FCSTD DOCUMENT  (FreeCAD 1.0R39285 (Git))
Label: pranaV2
License: All rights reserved
LicenseURL: https://en.wikipedia.org/wiki/All_rights_reserved
objects: Sketcher::SketchObject×195, Part::Extrusion×187, Part::Feature×26, Part::MultiFuse×14, Part::Cut×8, Part::Fillet×5, Part::Cylinder×4, Part::Loft×4, Part::MultiCommon×4, App::Part×3, Part::Compound×2, Part::Box×1
note: 645 computed .brp shape members not serialized (recipe doc carries the construction recipe); baked Part::Feature solids carry a one-line shape summary decoded from their .brp

FEATURE [Part::Feature] Part__Feature023  label="COZIR"
  Placement = pos=(5.41029,2.97838,5.56111) rot=(0,0,1;0rad)
  shape: bbox 51.61 x 17 x 50.23 mm, 43 faces (baked)
FEATURE [Part::Feature] Part__Feature024  label="COMPOUND"
  shape: bbox 3.14 x 5 x 10.76 mm, 60 faces, 10 solids (baked)
FEATURE [App::Part] COZIR_Sensor_v2  label="COZIR Sensor v2"
  Group = -> [Part__Feature023,Part__Feature024]
  Origin = -> Origin002
  Placement = pos=(18.5,-15,8.25) rot=(0,-1,0;5.75959rad)
FEATURE [Part::Feature] Part__Feature334  label="CAPC-0805-T0.95-BN v012"
  Placement = pos=(-5.48627,2.66154,1.6) rot=(0,0,-1;1.5708rad)
  shape: bbox 1.35 x 2.1 x 0.95 mm, 42 faces (baked)
FEATURE [Part::Feature] Part__Feature335  label="CAPC-0805-T0.95-BN v013"
  Placement = pos=(-3.43627,2.66154,1.6) rot=(0,0,-1;1.5708rad)
  shape: bbox 1.35 x 2.1 x 0.95 mm, 42 faces (baked)
FEATURE [Part::Feature] Part__Feature336  label="CAPC-0603-T0.9-BN v009"
  Placement = pos=(-1.69987,-3.28475,1.6) rot=(0,0,1;0rad)
  shape: bbox 1.7 x 0.9 x 0.9 mm, 42 faces (baked)
FEATURE [Part::Feature] Part__Feature337  label="BODY_MF06A003"
  Placement = pos=(0,0,0.762) rot=(0.57735,-0.57735,-0.57735;2.0944rad)
  shape: bbox 1.601 x 2.921 x 1.016 mm, 42 faces (baked)
FEATURE [Part::Feature] Part__Feature338  label="LEAD_MF06A018"
  Placement = pos=(-0.9652,-0.9525,0.1016) rot=(0.57735,-0.57735,-0.57735;2.0944rad)
  shape: bbox 0.6223 x 0.3749 x 0.8636 mm, 14 faces (baked)
FEATURE [Part::Feature] Part__Feature339  label="LEAD_MF06A019"
  Placement = pos=(-0.9652,0,0.1016) rot=(0.57735,-0.57735,-0.57735;2.0944rad)
  shape: bbox 0.6223 x 0.3749 x 0.8636 mm, 14 faces (baked)
FEATURE [Part::Feature] Part__Feature340  label="LEAD_MF06A020"
  Placement = pos=(-0.9652,0.9525,0.1016) rot=(0.57735,-0.57735,-0.57735;2.0944rad)
  shape: bbox 0.6223 x 0.3749 x 0.8636 mm, 14 faces (baked)
FEATURE [Part::Feature] Part__Feature341  label="LEAD_MF06A021"
  Placement = pos=(0.9652,-0.9525,0.1016) rot=(0.57735,0.57735,0.57735;2.0944rad)
  shape: bbox 0.6223 x 0.3749 x 0.8636 mm, 14 faces (baked)
FEATURE [Part::Feature] Part__Feature342  label="LEAD_MF06A022"
  Placement = pos=(0.9652,0,0.1016) rot=(0.57735,0.57735,0.57735;2.0944rad)
  shape: bbox 0.6223 x 0.3749 x 0.8636 mm, 14 faces (baked)
FEATURE [Part::Feature] Part__Feature343  label="LEAD_MF06A023"
  Placement = pos=(0.9652,0.9525,0.1016) rot=(0.57735,0.57735,0.57735;2.0944rad)
  shape: bbox 0.6223 x 0.3749 x 0.8636 mm, 14 faces (baked)
FEATURE [Part::Feature] Part__Feature344  label="SOT363 v005"
  Placement = pos=(4.97054,-0.645171,1.675) rot=(0,0,1;3.14159rad)
  shape: bbox 2.1 x 2 x 1.1 mm, 94 faces, 7 solids (baked)
FEATURE [Part::Feature] Part__Feature345  label="LED 0603 single color v005"
  Placement = pos=(-9.18406,3.72778,1.60762) rot=(0,0,1;1.5708rad)
  shape: bbox 1.961 x 0.7932 x 0.7145 mm, 63 faces, 5 solids (baked)
FEATURE [Part::Feature] Part__Feature346  label="RESC-0603 v007"
  Placement = pos=(4.83432,-3.67461,1.6) rot=(0,0,1;0rad)
  shape: bbox 1.7 x 0.9 x 0.55 mm, 52 faces, 3 solids (baked)
FEATURE [Part::Feature] Part__Feature347  label="RESC-0603 v008"
  Placement = pos=(-7.14949,3.61248,1.6) rot=(0,0,-1;1.5708rad)
  shape: bbox 0.9 x 1.7 x 0.55 mm, 52 faces, 3 solids (baked)
FEATURE [Part::Feature] Part__Feature348  label="Printed Circuit Board004"
  shape: bbox 25.4 x 17.78 x 1.6 mm, 42 faces (baked)
FEATURE [Part::Feature] Part__Feature349  label="EAHC2835WD009"
  shape: bbox 3.513 x 2.813 x 0.7485 mm, 108 faces, 4 solids (baked)
FEATURE [Part::Feature] Part__Feature350  label="AS7341 v005"
  Placement = pos=(0,-0.339822,1.6) rot=(0,0,1;0rad)
  shape: bbox 2 x 3.1 x 1.1 mm, 267 faces, 26 solids (baked)
FEATURE [Part::Feature] Part__Feature351  label="CAPC-0805-T0.95-BN v014"
  Placement = pos=(-5.01759,-3.15294,1.6) rot=(0,0,1;0rad)
  shape: bbox 2.1 x 1.35 x 0.95 mm, 42 faces (baked)
FEATURE [Part::Feature] Part__Feature352  label="YC164_RESPACK v007"
  Placement = pos=(2.99591,1.52916,1.6) rot=(0,0,1;0rad)
  shape: bbox 3.2 x 1.6 x 0.61 mm, 172 faces (baked)
FEATURE [Part::Feature] Part__Feature353  label="qwicc v009"
  Placement = pos=(-10.8364,0.0607456,1.65) rot=(0,0,-1;1.5708rad)
  shape: bbox 4.95 x 6 x 2.96 mm, 229 faces, 7 solids (baked)
FEATURE [Part::Feature] Part__Feature354  label="qwicc v010"
  Placement = pos=(10.8256,0.00556102,1.65) rot=(0,0,1;1.5708rad)
  shape: bbox 4.95 x 6 x 2.96 mm, 229 faces, 7 solids (baked)
FEATURE [Part::Feature] Part__Feature356  label="RaspberryPiZeroW002"
  Placement = pos=(0,8,25) rot=(-1,0,0;3.14159rad)
  shape: bbox 65.9 x 4.8 x 31.25 mm, 368 faces, 2 solids (baked)
FEATURE [App::Part] sot_23_6_v005  label="sot-23-6 v005"
  Group = -> [Part__Feature337,Part__Feature338,Part__Feature339,Part__Feature340,Part__Feature341,Part__Feature342,Part__Feature343]
  Origin = -> Origin019
  Placement = pos=(-4.47945,-0.603742,1.69152) rot=(0,0,1;0rad)
FEATURE [App::Part] Adafruit_AS7341_STEMMA_QT_v005  label="bme280"
  Group = -> [Part__Feature348,Part__Feature349,Part__Feature350,Part__Feature351,Part__Feature334,Part__Feature335,Part__Feature336,sot_23_6_v005,Part__Feature344,Part__Feature345,Part__Feature346,Part__Feature347,Part__Feature352,Part__Feature353,Part__Feature354]
  Origin = -> Origin020
  Placement = pos=(-40,-15,75) rot=(0.935113,-0.250563,0.250563;1.62036rad)
FEATURE [Part::Cylinder] Cylinder004  label="heatSetHolderCut001"
  Angle = 360
  AttacherType = Attacher::AttachEngine3D
  FirstAngle = 0
  Height = 4
  Placement = pos=(-8,5,1.1e-15) rot=(0,-1,0;4.71239rad)
  Radius = 1.65
  SecondAngle = 0
FEATURE [Part::Cylinder] Cylinder005  label="m2Cut002"
  Angle = 360
  AttacherType = Attacher::AttachEngine3D
  FirstAngle = 0
  Height = 16
  Placement = pos=(-8,0,1.1e-15) rot=(0,-1,0;4.71239rad)
  Radius = 1.2
  SecondAngle = 0
FEATURE [Part::MultiFuse] Fusion568  label="meshCut001"
  Refine = true
  Shapes = -> [Cylinder005,Cylinder004]
FEATURE [Sketcher::SketchObject] Sketch575
  ArcFitTolerance = 1e-06
  FullyConstrained = true
  MakeInternals = false
  Placement = pos=(0,0,0) rot=(1,0,0;1.5708rad)
  sketch-geometry (49):
    g0: LineSegment StartX=1e-16 StartY=3.5 StartZ=0 EndX=-3.03109 EndY=1.75 EndZ=0
    g1: LineSegment StartX=-3.03109 StartY=1.75 StartZ=0 EndX=-3.03109 EndY=-1.75 EndZ=0
    g2: LineSegment StartX=-3.03109 StartY=-1.75 StartZ=0 EndX=-1e-16 EndY=-3.5 EndZ=0
    g3: LineSegment StartX=-1e-16 StartY=-3.5 StartZ=0 EndX=3.03109 EndY=-1.75 EndZ=0
    g4: LineSegment StartX=3.03109 StartY=-1.75 StartZ=0 EndX=3.03109 EndY=1.75 EndZ=0
    g5: LineSegment StartX=3.03109 StartY=1.75 StartZ=0 EndX=1e-16 EndY=3.5 EndZ=0
    g6: Circle [constr] CenterX=0 CenterY=0 CenterZ=0 NormalX=0 NormalY=0 NormalZ=1 AngleXU=0 Radius=3.5
    g7: LineSegment StartX=4.96892 StartY=-1.75002 StartZ=0 EndX=8.00002 EndY=-3.5 EndZ=0
    g8: LineSegment StartX=8.00002 StartY=-3.5 StartZ=0 EndX=11.0311 EndY=-1.74998 EndZ=0
    g9: LineSegment StartX=11.0311 StartY=-1.74998 StartZ=0 EndX=11.0311 EndY=1.75002 EndZ=0
    g10: LineSegment StartX=11.0311 StartY=1.75002 StartZ=0 EndX=7.99998 EndY=3.5 EndZ=0
    g11: LineSegment StartX=7.99998 StartY=3.5 StartZ=0 EndX=4.9689 EndY=1.74998 EndZ=0
    g12: LineSegment StartX=4.9689 StartY=1.74998 StartZ=0 EndX=4.96892 EndY=-1.75002 EndZ=0
    g13: Circle [constr] CenterX=8 CenterY=0 CenterZ=0 NormalX=0 NormalY=0 NormalZ=1 AngleXU=0 Radius=3.5
    g14: LineSegment StartX=4.03109 StartY=3.5 StartZ=0 EndX=7.06218 EndY=5.25 EndZ=0
    g15: LineSegment StartX=7.06218 StartY=5.25 StartZ=0 EndX=7.06218 EndY=8.75 EndZ=0
    g16: LineSegment StartX=7.06218 StartY=8.75 StartZ=0 EndX=4.03109 EndY=10.5 EndZ=0
    g17: LineSegment StartX=4.03109 StartY=10.5 StartZ=0 EndX=1 EndY=8.75 EndZ=0
    g18: LineSegment StartX=1 StartY=8.75 StartZ=0 EndX=1 EndY=5.25 EndZ=0
    g19: LineSegment StartX=1 StartY=5.25 StartZ=0 EndX=4.03109 EndY=3.5 EndZ=0
    g20: Circle [constr] CenterX=4.03109 CenterY=7 CenterZ=0 NormalX=0 NormalY=0 NormalZ=1 AngleXU=0 Radius=3.5
    g21: LineSegment StartX=-1 StartY=5.25 StartZ=0 EndX=-1 EndY=8.75 EndZ=0
    g22: LineSegment StartX=-1 StartY=8.75 StartZ=0 EndX=-4.03109 EndY=10.5 EndZ=0
    g23: LineSegment StartX=-4.03109 StartY=10.5 StartZ=0 EndX=-7.06218 EndY=8.75 EndZ=0
    g24: LineSegment StartX=-7.06218 StartY=8.75 StartZ=0 EndX=-7.06218 EndY=5.25 EndZ=0
    g25: LineSegment StartX=-7.06218 StartY=5.25 StartZ=0 EndX=-4.03109 EndY=3.5 EndZ=0
    g26: LineSegment StartX=-4.03109 StartY=3.5 StartZ=0 EndX=-1 EndY=5.25 EndZ=0
    g27: Circle [constr] CenterX=-4.03109 CenterY=7 CenterZ=0 NormalX=0 NormalY=0 NormalZ=1 AngleXU=0 Radius=3.5
    g28: LineSegment StartX=-4.96891 StartY=-1.75 StartZ=0 EndX=-4.96891 EndY=1.75 EndZ=0
    g29: LineSegment StartX=-4.96891 StartY=1.75 StartZ=0 EndX=-8 EndY=3.5 EndZ=0
    g30: LineSegment StartX=-8 StartY=3.5 StartZ=0 EndX=-11.0311 EndY=1.75 EndZ=0
    g31: LineSegment StartX=-11.0311 StartY=1.75 StartZ=0 EndX=-11.0311 EndY=-1.75 EndZ=0
    g32: LineSegment StartX=-11.0311 StartY=-1.75 StartZ=0 EndX=-8 EndY=-3.5 EndZ=0
    g33: LineSegment StartX=-8 StartY=-3.5 StartZ=0 EndX=-4.96891 EndY=-1.75 EndZ=0
    g34: Circle [constr] CenterX=-8 CenterY=0 CenterZ=0 NormalX=0 NormalY=0 NormalZ=1 AngleXU=0 Radius=3.5
    g35: LineSegment StartX=-4.03109 StartY=-3.5 StartZ=0 EndX=-7.06218 EndY=-5.25 EndZ=0
    g36: LineSegment StartX=-7.06218 StartY=-5.25 StartZ=0 EndX=-7.06218 EndY=-8.75 EndZ=0
    g37: LineSegment StartX=-7.06218 StartY=-8.75 StartZ=0 EndX=-4.03109 EndY=-10.5 EndZ=0
    g38: LineSegment StartX=-4.03109 StartY=-10.5 StartZ=0 EndX=-1 EndY=-8.75 EndZ=0
    g39: LineSegment StartX=-1 StartY=-8.75 StartZ=0 EndX=-1 EndY=-5.25 EndZ=0
    g40: LineSegment StartX=-1 StartY=-5.25 StartZ=0 EndX=-4.03109 EndY=-3.5 EndZ=0
    g41: Circle [constr] CenterX=-4.03109 CenterY=-7 CenterZ=0 NormalX=0 NormalY=0 NormalZ=1 AngleXU=0 Radius=3.5
    g42: LineSegment StartX=4.03109 StartY=-3.5 StartZ=0 EndX=1 EndY=-5.25 EndZ=0
    g43: LineSegment StartX=1 StartY=-5.25 StartZ=0 EndX=1 EndY=-8.75 EndZ=0
    g44: LineSegment StartX=1 StartY=-8.75 StartZ=0 EndX=4.03109 EndY=-10.5 EndZ=0
    g45: LineSegment StartX=4.03109 StartY=-10.5 StartZ=0 EndX=7.06218 EndY=-8.75 EndZ=0
    g46: LineSegment StartX=7.06218 StartY=-8.75 StartZ=0 EndX=7.06218 EndY=-5.25 EndZ=0
    g47: LineSegment StartX=7.06218 StartY=-5.25 StartZ=0 EndX=4.03109 EndY=-3.5 EndZ=0
    g48: Circle [constr] CenterX=4.03109 CenterY=-7 CenterZ=0 NormalX=0 NormalY=0 NormalZ=1 AngleXU=0 Radius=3.5
  constraints (117):
    c: Coincident(g0,g1)
    c: Coincident(g1,g2)
    c: Coincident(g2,g3)
    c: Coincident(g3,g4)
    c: Coincident(g4,g5)
    c: Coincident(g5,g0)
    c: Equal(g0, g1-g5) x5
    c: PointOnObject(g0,g6)
    c: PointOnObject(g1,g6)
    c: PointOnObject(g2,g6)
    c: PointOnObject(g3,g6)
    c: PointOnObject(g4,g6)
    c: PointOnObject(g5,g6)
    c: Coincident(g6,g-1)
    c: Diameter(g6) = 7
    c: PointOnObject(g0,g-2)
    c: Coincident(g7,g8)
    c: Coincident(g8,g9)
    c: Coincident(g9,g10)
    c: Coincident(g10,g11)
    c: Coincident(g11,g12)
    c: Coincident(g12,g7)
    c: Equal(g7, g8-g12) x5
    c: PointOnObject(g7,g13)
    c: PointOnObject(g8,g13)
    c: PointOnObject(g9,g13)
    c: PointOnObject(g10,g13)
    c: PointOnObject(g11,g13)
    c: PointOnObject(g12,g13)
    c: PointOnObject(g13,g-1)
    c: Diameter(g13) = 7
    c: Distance(g6,g13) = 8
    c: Horizontal(g0,g10)
    c: Coincident(g14,g15)
    c: Coincident(g15,g16)
    c: Coincident(g16,g17)
    c: Coincident(g17,g18)
    c: Coincident(g18,g19)
    c: Coincident(g19,g14)
    c: Equal(g14, g15-g19) x5
    c: PointOnObject(g14,g20)
    c: PointOnObject(g15,g20)
    c: PointOnObject(g16,g20)
    c: PointOnObject(g17,g20)
    c: PointOnObject(g18,g20)
    c: PointOnObject(g19,g20)
    c: Diameter(g20) = 7
    c: DistanceY(g-1,g20) = 7
    c: Vertical(g18)
    c: Distance(g17,g-2) = 1
    c: Coincident(g21,g22)
    c: Coincident(g22,g23)
    c: Coincident(g23,g24)
    c: Coincident(g24,g25)
    c: Coincident(g25,g26)
    c: Coincident(g26,g21)
    c: Equal(g21, g22-g26) x5
    c: PointOnObject(g21,g27)
    c: PointOnObject(g22,g27)
    c: PointOnObject(g23,g27)
    c: PointOnObject(g24,g27)
    c: PointOnObject(g25,g27)
    c: PointOnObject(g26,g27)
    c: Diameter(g27) = 7
    c: DistanceY(g-1,g27) = 7
    c: DistanceX(g21,g-1) = 1
    c: Vertical(g21)
    c: Coincident(g28,g29)
    c: Coincident(g29,g30)
    c: Coincident(g30,g31)
    c: Coincident(g31,g32)
    c: Coincident(g32,g33)
    c: Coincident(g33,g28)
    c: Equal(g28, g29-g33) x5
    c: PointOnObject(g28,g34)
    c: PointOnObject(g29,g34)
    c: PointOnObject(g30,g34)
    c: PointOnObject(g31,g34)
    c: PointOnObject(g32,g34)
    c: PointOnObject(g33,g34)
    c: PointOnObject(g34,g-1)
    c: Diameter(g34) = 7
    c: Vertical(g31)
    c: DistanceX(g34,g-1) = 8
    c: Coincident(g35,g36)
    c: Coincident(g36,g37)
    c: Coincident(g37,g38)
    c: Coincident(g38,g39)
    c: Coincident(g39,g40)
    c: Coincident(g40,g35)
    c: Equal(g35, g36-g40) x5
    c: PointOnObject(g35,g41)
    c: PointOnObject(g36,g41)
    c: PointOnObject(g37,g41)
    c: PointOnObject(g38,g41)
    c: PointOnObject(g39,g41)
    c: PointOnObject(g40,g41)
    c: Coincident(g42,g43)
    c: Coincident(g43,g44)
    c: Coincident(g44,g45)
    c: Coincident(g45,g46)
    c: Coincident(g46,g47)
    c: Coincident(g47,g42)
    c: Equal(g42, g43-g47) x5
    c: PointOnObject(g42,g48)
    c: PointOnObject(g43,g48)
    c: PointOnObject(g44,g48)
    c: PointOnObject(g45,g48)
    c: PointOnObject(g46,g48)
    c: PointOnObject(g47,g48)
    c: Equal(g41,g48)
    c: Diameter(g41) = 7
    c: Vertical(g39)
    c: Vertical(g43)
    c: Distance(g-2,g39) = 1
    c: Symmetric(g38,g43,g-2)
    c: Distance(g41,g-1) = 7
FEATURE [Part::Extrusion] Extrude566  label="hex168"
  Base = -> Sketch575
  Dir = (0,-1,2e-16)
  DirMode = 2
  FaceMakerClass = Part::FaceMakerBullseye
  FaceMakerMode = 3
  LengthFwd = 10
  LengthRev = 0
  Solid = true
  Symmetric = false
FEATURE [Sketcher::SketchObject] Sketch576
  ArcFitTolerance = 1e-06
  FullyConstrained = true
  MakeInternals = false
  Placement = pos=(0,0,0) rot=(1,0,0;1.5708rad)
  sketch-geometry (49):
    g0: LineSegment StartX=1e-16 StartY=3.5 StartZ=0 EndX=-3.03109 EndY=1.75 EndZ=0
    g1: LineSegment StartX=-3.03109 StartY=1.75 StartZ=0 EndX=-3.03109 EndY=-1.75 EndZ=0
    g2: LineSegment StartX=-3.03109 StartY=-1.75 StartZ=0 EndX=-1e-16 EndY=-3.5 EndZ=0
    g3: LineSegment StartX=-1e-16 StartY=-3.5 StartZ=0 EndX=3.03109 EndY=-1.75 EndZ=0
    g4: LineSegment StartX=3.03109 StartY=-1.75 StartZ=0 EndX=3.03109 EndY=1.75 EndZ=0
    g5: LineSegment StartX=3.03109 StartY=1.75 StartZ=0 EndX=1e-16 EndY=3.5 EndZ=0
    g6: Circle [constr] CenterX=0 CenterY=0 CenterZ=0 NormalX=0 NormalY=0 NormalZ=1 AngleXU=0 Radius=3.5
    g7: LineSegment StartX=4.96892 StartY=-1.75002 StartZ=0 EndX=8.00002 EndY=-3.5 EndZ=0
    g8: LineSegment StartX=8.00002 StartY=-3.5 StartZ=0 EndX=11.0311 EndY=-1.74998 EndZ=0
    g9: LineSegment StartX=11.0311 StartY=-1.74998 StartZ=0 EndX=11.0311 EndY=1.75002 EndZ=0
    g10: LineSegment StartX=11.0311 StartY=1.75002 StartZ=0 EndX=7.99998 EndY=3.5 EndZ=0
    g11: LineSegment StartX=7.99998 StartY=3.5 StartZ=0 EndX=4.9689 EndY=1.74998 EndZ=0
    g12: LineSegment StartX=4.9689 StartY=1.74998 StartZ=0 EndX=4.96892 EndY=-1.75002 EndZ=0
    g13: Circle [constr] CenterX=8 CenterY=0 CenterZ=0 NormalX=0 NormalY=0 NormalZ=1 AngleXU=0 Radius=3.5
    g14: LineSegment StartX=4.03109 StartY=3.5 StartZ=0 EndX=7.06218 EndY=5.25 EndZ=0
    g15: LineSegment StartX=7.06218 StartY=5.25 StartZ=0 EndX=7.06218 EndY=8.75 EndZ=0
    g16: LineSegment StartX=7.06218 StartY=8.75 StartZ=0 EndX=4.03109 EndY=10.5 EndZ=0
    g17: LineSegment StartX=4.03109 StartY=10.5 StartZ=0 EndX=1 EndY=8.75 EndZ=0
    g18: LineSegment StartX=1 StartY=8.75 StartZ=0 EndX=1 EndY=5.25 EndZ=0
    g19: LineSegment StartX=1 StartY=5.25 StartZ=0 EndX=4.03109 EndY=3.5 EndZ=0
    g20: Circle [constr] CenterX=4.03109 CenterY=7 CenterZ=0 NormalX=0 NormalY=0 NormalZ=1 AngleXU=0 Radius=3.5
    g21: LineSegment StartX=-1 StartY=5.25 StartZ=0 EndX=-1 EndY=8.75 EndZ=0
    g22: LineSegment StartX=-1 StartY=8.75 StartZ=0 EndX=-4.03109 EndY=10.5 EndZ=0
    g23: LineSegment StartX=-4.03109 StartY=10.5 StartZ=0 EndX=-7.06218 EndY=8.75 EndZ=0
    g24: LineSegment StartX=-7.06218 StartY=8.75 StartZ=0 EndX=-7.06218 EndY=5.25 EndZ=0
    g25: LineSegment StartX=-7.06218 StartY=5.25 StartZ=0 EndX=-4.03109 EndY=3.5 EndZ=0
    g26: LineSegment StartX=-4.03109 StartY=3.5 StartZ=0 EndX=-1 EndY=5.25 EndZ=0
    g27: Circle [constr] CenterX=-4.03109 CenterY=7 CenterZ=0 NormalX=0 NormalY=0 NormalZ=1 AngleXU=0 Radius=3.5
    g28: LineSegment StartX=-4.96891 StartY=-1.75 StartZ=0 EndX=-4.96891 EndY=1.75 EndZ=0
    g29: LineSegment StartX=-4.96891 StartY=1.75 StartZ=0 EndX=-8 EndY=3.5 EndZ=0
    g30: LineSegment StartX=-8 StartY=3.5 StartZ=0 EndX=-11.0311 EndY=1.75 EndZ=0
    g31: LineSegment StartX=-11.0311 StartY=1.75 StartZ=0 EndX=-11.0311 EndY=-1.75 EndZ=0
    g32: LineSegment StartX=-11.0311 StartY=-1.75 StartZ=0 EndX=-8 EndY=-3.5 EndZ=0
    g33: LineSegment StartX=-8 StartY=-3.5 StartZ=0 EndX=-4.96891 EndY=-1.75 EndZ=0
    g34: Circle [constr] CenterX=-8 CenterY=0 CenterZ=0 NormalX=0 NormalY=0 NormalZ=1 AngleXU=0 Radius=3.5
    g35: LineSegment StartX=-4.03109 StartY=-3.5 StartZ=0 EndX=-7.06218 EndY=-5.25 EndZ=0
    g36: LineSegment StartX=-7.06218 StartY=-5.25 StartZ=0 EndX=-7.06218 EndY=-8.75 EndZ=0
    g37: LineSegment StartX=-7.06218 StartY=-8.75 StartZ=0 EndX=-4.03109 EndY=-10.5 EndZ=0
    g38: LineSegment StartX=-4.03109 StartY=-10.5 StartZ=0 EndX=-1 EndY=-8.75 EndZ=0
    g39: LineSegment StartX=-1 StartY=-8.75 StartZ=0 EndX=-1 EndY=-5.25 EndZ=0
    g40: LineSegment StartX=-1 StartY=-5.25 StartZ=0 EndX=-4.03109 EndY=-3.5 EndZ=0
    g41: Circle [constr] CenterX=-4.03109 CenterY=-7 CenterZ=0 NormalX=0 NormalY=0 NormalZ=1 AngleXU=0 Radius=3.5
    g42: LineSegment StartX=4.03109 StartY=-3.5 StartZ=0 EndX=1 EndY=-5.25 EndZ=0
    g43: LineSegment StartX=1 StartY=-5.25 StartZ=0 EndX=1 EndY=-8.75 EndZ=0
    g44: LineSegment StartX=1 StartY=-8.75 StartZ=0 EndX=4.03109 EndY=-10.5 EndZ=0
    g45: LineSegment StartX=4.03109 StartY=-10.5 StartZ=0 EndX=7.06218 EndY=-8.75 EndZ=0
    g46: LineSegment StartX=7.06218 StartY=-8.75 StartZ=0 EndX=7.06218 EndY=-5.25 EndZ=0
    g47: LineSegment StartX=7.06218 StartY=-5.25 StartZ=0 EndX=4.03109 EndY=-3.5 EndZ=0
    g48: Circle [constr] CenterX=4.03109 CenterY=-7 CenterZ=0 NormalX=0 NormalY=0 NormalZ=1 AngleXU=0 Radius=3.5
  constraints (117):
    c: Coincident(g0,g1)
    c: Coincident(g1,g2)
    c: Coincident(g2,g3)
    c: Coincident(g3,g4)
    c: Coincident(g4,g5)
    c: Coincident(g5,g0)
    c: Equal(g0, g1-g5) x5
    c: PointOnObject(g0,g6)
    c: PointOnObject(g1,g6)
    c: PointOnObject(g2,g6)
    c: PointOnObject(g3,g6)
    c: PointOnObject(g4,g6)
    c: PointOnObject(g5,g6)
    c: Coincident(g6,g-1)
    c: Diameter(g6) = 7
    c: PointOnObject(g0,g-2)
    c: Coincident(g7,g8)
    c: Coincident(g8,g9)
    c: Coincident(g9,g10)
    c: Coincident(g10,g11)
    c: Coincident(g11,g12)
    c: Coincident(g12,g7)
    c: Equal(g7, g8-g12) x5
    c: PointOnObject(g7,g13)
    c: PointOnObject(g8,g13)
    c: PointOnObject(g9,g13)
    c: PointOnObject(g10,g13)
    c: PointOnObject(g11,g13)
    c: PointOnObject(g12,g13)
    c: PointOnObject(g13,g-1)
    c: Diameter(g13) = 7
    c: Distance(g6,g13) = 8
    c: Horizontal(g0,g10)
    c: Coincident(g14,g15)
    c: Coincident(g15,g16)
    c: Coincident(g16,g17)
    c: Coincident(g17,g18)
    c: Coincident(g18,g19)
    c: Coincident(g19,g14)
    c: Equal(g14, g15-g19) x5
    c: PointOnObject(g14,g20)
    c: PointOnObject(g15,g20)
    c: PointOnObject(g16,g20)
    c: PointOnObject(g17,g20)
    c: PointOnObject(g18,g20)
    c: PointOnObject(g19,g20)
    c: Diameter(g20) = 7
    c: DistanceY(g-1,g20) = 7
    c: Vertical(g18)
    c: Distance(g17,g-2) = 1
    c: Coincident(g21,g22)
    c: Coincident(g22,g23)
    c: Coincident(g23,g24)
    c: Coincident(g24,g25)
    c: Coincident(g25,g26)
    c: Coincident(g26,g21)
    c: Equal(g21, g22-g26) x5
    c: PointOnObject(g21,g27)
    c: PointOnObject(g22,g27)
    c: PointOnObject(g23,g27)
    c: PointOnObject(g24,g27)
    c: PointOnObject(g25,g27)
    c: PointOnObject(g26,g27)
    c: Diameter(g27) = 7
    c: DistanceY(g-1,g27) = 7
    c: DistanceX(g21,g-1) = 1
    c: Vertical(g21)
    c: Coincident(g28,g29)
    c: Coincident(g29,g30)
    c: Coincident(g30,g31)
    c: Coincident(g31,g32)
    c: Coincident(g32,g33)
    c: Coincident(g33,g28)
    c: Equal(g28, g29-g33) x5
    c: PointOnObject(g28,g34)
    c: PointOnObject(g29,g34)
    c: PointOnObject(g30,g34)
    c: PointOnObject(g31,g34)
    c: PointOnObject(g32,g34)
    c: PointOnObject(g33,g34)
    c: PointOnObject(g34,g-1)
    c: Diameter(g34) = 7
    c: Vertical(g31)
    c: DistanceX(g34,g-1) = 8
    c: Coincident(g35,g36)
    c: Coincident(g36,g37)
    c: Coincident(g37,g38)
    c: Coincident(g38,g39)
    c: Coincident(g39,g40)
    c: Coincident(g40,g35)
    c: Equal(g35, g36-g40) x5
    c: PointOnObject(g35,g41)
    c: PointOnObject(g36,g41)
    c: PointOnObject(g37,g41)
    c: PointOnObject(g38,g41)
    c: PointOnObject(g39,g41)
    c: PointOnObject(g40,g41)
    c: Coincident(g42,g43)
    c: Coincident(g43,g44)
    c: Coincident(g44,g45)
    c: Coincident(g45,g46)
    c: Coincident(g46,g47)
    c: Coincident(g47,g42)
    c: Equal(g42, g43-g47) x5
    c: PointOnObject(g42,g48)
    c: PointOnObject(g43,g48)
    c: PointOnObject(g44,g48)
    c: PointOnObject(g45,g48)
    c: PointOnObject(g46,g48)
    c: PointOnObject(g47,g48)
    c: Equal(g41,g48)
    c: Diameter(g41) = 7
    c: Vertical(g39)
    c: Vertical(g43)
    c: Distance(g-2,g39) = 1
    c: Symmetric(g38,g43,g-2)
    c: Distance(g41,g-1) = 7
FEATURE [Part::Extrusion] Extrude567  label="hex169"
  Base = -> Sketch576
  Dir = (0,-1,2e-16)
  DirMode = 2
  FaceMakerClass = Part::FaceMakerBullseye
  FaceMakerMode = 3
  LengthFwd = 10
  LengthRev = 0
  Placement = pos=(20,0,-7) rot=(0,0,1;0rad)
  Solid = true
  Symmetric = false
FEATURE [Sketcher::SketchObject] Sketch577
  ArcFitTolerance = 1e-06
  FullyConstrained = true
  MakeInternals = false
  Placement = pos=(0,0,0) rot=(1,0,0;1.5708rad)
  sketch-geometry (49):
    g0: LineSegment StartX=1e-16 StartY=3.5 StartZ=0 EndX=-3.03109 EndY=1.75 EndZ=0
    g1: LineSegment StartX=-3.03109 StartY=1.75 StartZ=0 EndX=-3.03109 EndY=-1.75 EndZ=0
    g2: LineSegment StartX=-3.03109 StartY=-1.75 StartZ=0 EndX=-1e-16 EndY=-3.5 EndZ=0
    g3: LineSegment StartX=-1e-16 StartY=-3.5 StartZ=0 EndX=3.03109 EndY=-1.75 EndZ=0
    g4: LineSegment StartX=3.03109 StartY=-1.75 StartZ=0 EndX=3.03109 EndY=1.75 EndZ=0
    g5: LineSegment StartX=3.03109 StartY=1.75 StartZ=0 EndX=1e-16 EndY=3.5 EndZ=0
    g6: Circle [constr] CenterX=0 CenterY=0 CenterZ=0 NormalX=0 NormalY=0 NormalZ=1 AngleXU=0 Radius=3.5
    g7: LineSegment StartX=4.96892 StartY=-1.75002 StartZ=0 EndX=8.00002 EndY=-3.5 EndZ=0
    g8: LineSegment StartX=8.00002 StartY=-3.5 StartZ=0 EndX=11.0311 EndY=-1.74998 EndZ=0
    g9: LineSegment StartX=11.0311 StartY=-1.74998 StartZ=0 EndX=11.0311 EndY=1.75002 EndZ=0
    g10: LineSegment StartX=11.0311 StartY=1.75002 StartZ=0 EndX=7.99998 EndY=3.5 EndZ=0
    g11: LineSegment StartX=7.99998 StartY=3.5 StartZ=0 EndX=4.9689 EndY=1.74998 EndZ=0
    g12: LineSegment StartX=4.9689 StartY=1.74998 StartZ=0 EndX=4.96892 EndY=-1.75002 EndZ=0
    g13: Circle [constr] CenterX=8 CenterY=0 CenterZ=0 NormalX=0 NormalY=0 NormalZ=1 AngleXU=0 Radius=3.5
    g14: LineSegment StartX=4.03109 StartY=3.5 StartZ=0 EndX=7.06218 EndY=5.25 EndZ=0
    g15: LineSegment StartX=7.06218 StartY=5.25 StartZ=0 EndX=7.06218 EndY=8.75 EndZ=0
    g16: LineSegment StartX=7.06218 StartY=8.75 StartZ=0 EndX=4.03109 EndY=10.5 EndZ=0
    g17: LineSegment StartX=4.03109 StartY=10.5 StartZ=0 EndX=1 EndY=8.75 EndZ=0
    g18: LineSegment StartX=1 StartY=8.75 StartZ=0 EndX=1 EndY=5.25 EndZ=0
    g19: LineSegment StartX=1 StartY=5.25 StartZ=0 EndX=4.03109 EndY=3.5 EndZ=0
    g20: Circle [constr] CenterX=4.03109 CenterY=7 CenterZ=0 NormalX=0 NormalY=0 NormalZ=1 AngleXU=0 Radius=3.5
    g21: LineSegment StartX=-1 StartY=5.25 StartZ=0 EndX=-1 EndY=8.75 EndZ=0
    g22: LineSegment StartX=-1 StartY=8.75 StartZ=0 EndX=-4.03109 EndY=10.5 EndZ=0
    g23: LineSegment StartX=-4.03109 StartY=10.5 StartZ=0 EndX=-7.06218 EndY=8.75 EndZ=0
    g24: LineSegment StartX=-7.06218 StartY=8.75 StartZ=0 EndX=-7.06218 EndY=5.25 EndZ=0
    g25: LineSegment StartX=-7.06218 StartY=5.25 StartZ=0 EndX=-4.03109 EndY=3.5 EndZ=0
    g26: LineSegment StartX=-4.03109 StartY=3.5 StartZ=0 EndX=-1 EndY=5.25 EndZ=0
    g27: Circle [constr] CenterX=-4.03109 CenterY=7 CenterZ=0 NormalX=0 NormalY=0 NormalZ=1 AngleXU=0 Radius=3.5
    g28: LineSegment StartX=-4.96891 StartY=-1.75 StartZ=0 EndX=-4.96891 EndY=1.75 EndZ=0
    g29: LineSegment StartX=-4.96891 StartY=1.75 StartZ=0 EndX=-8 EndY=3.5 EndZ=0
    g30: LineSegment StartX=-8 StartY=3.5 StartZ=0 EndX=-11.0311 EndY=1.75 EndZ=0
    g31: LineSegment StartX=-11.0311 StartY=1.75 StartZ=0 EndX=-11.0311 EndY=-1.75 EndZ=0
    g32: LineSegment StartX=-11.0311 StartY=-1.75 StartZ=0 EndX=-8 EndY=-3.5 EndZ=0
    g33: LineSegment StartX=-8 StartY=-3.5 StartZ=0 EndX=-4.96891 EndY=-1.75 EndZ=0
    g34: Circle [constr] CenterX=-8 CenterY=0 CenterZ=0 NormalX=0 NormalY=0 NormalZ=1 AngleXU=0 Radius=3.5
    g35: LineSegment StartX=-4.03109 StartY=-3.5 StartZ=0 EndX=-7.06218 EndY=-5.25 EndZ=0
    g36: LineSegment StartX=-7.06218 StartY=-5.25 StartZ=0 EndX=-7.06218 EndY=-8.75 EndZ=0
    g37: LineSegment StartX=-7.06218 StartY=-8.75 StartZ=0 EndX=-4.03109 EndY=-10.5 EndZ=0
    g38: LineSegment StartX=-4.03109 StartY=-10.5 StartZ=0 EndX=-1 EndY=-8.75 EndZ=0
    g39: LineSegment StartX=-1 StartY=-8.75 StartZ=0 EndX=-1 EndY=-5.25 EndZ=0
    g40: LineSegment StartX=-1 StartY=-5.25 StartZ=0 EndX=-4.03109 EndY=-3.5 EndZ=0
    g41: Circle [constr] CenterX=-4.03109 CenterY=-7 CenterZ=0 NormalX=0 NormalY=0 NormalZ=1 AngleXU=0 Radius=3.5
    g42: LineSegment StartX=4.03109 StartY=-3.5 StartZ=0 EndX=1 EndY=-5.25 EndZ=0
    g43: LineSegment StartX=1 StartY=-5.25 StartZ=0 EndX=1 EndY=-8.75 EndZ=0
    g44: LineSegment StartX=1 StartY=-8.75 StartZ=0 EndX=4.03109 EndY=-10.5 EndZ=0
    g45: LineSegment StartX=4.03109 StartY=-10.5 StartZ=0 EndX=7.06218 EndY=-8.75 EndZ=0
    g46: LineSegment StartX=7.06218 StartY=-8.75 StartZ=0 EndX=7.06218 EndY=-5.25 EndZ=0
    g47: LineSegment StartX=7.06218 StartY=-5.25 StartZ=0 EndX=4.03109 EndY=-3.5 EndZ=0
    g48: Circle [constr] CenterX=4.03109 CenterY=-7 CenterZ=0 NormalX=0 NormalY=0 NormalZ=1 AngleXU=0 Radius=3.5
  constraints (117):
    c: Coincident(g0,g1)
    c: Coincident(g1,g2)
    c: Coincident(g2,g3)
    c: Coincident(g3,g4)
    c: Coincident(g4,g5)
    c: Coincident(g5,g0)
    c: Equal(g0, g1-g5) x5
    c: PointOnObject(g0,g6)
    c: PointOnObject(g1,g6)
    c: PointOnObject(g2,g6)
    c: PointOnObject(g3,g6)
    c: PointOnObject(g4,g6)
    c: PointOnObject(g5,g6)
    c: Coincident(g6,g-1)
    c: Diameter(g6) = 7
    c: PointOnObject(g0,g-2)
    c: Coincident(g7,g8)
    c: Coincident(g8,g9)
    c: Coincident(g9,g10)
    c: Coincident(g10,g11)
    c: Coincident(g11,g12)
    c: Coincident(g12,g7)
    c: Equal(g7, g8-g12) x5
    c: PointOnObject(g7,g13)
    c: PointOnObject(g8,g13)
    c: PointOnObject(g9,g13)
    c: PointOnObject(g10,g13)
    c: PointOnObject(g11,g13)
    c: PointOnObject(g12,g13)
    c: PointOnObject(g13,g-1)
    c: Diameter(g13) = 7
    c: Distance(g6,g13) = 8
    c: Horizontal(g0,g10)
    c: Coincident(g14,g15)
    c: Coincident(g15,g16)
    c: Coincident(g16,g17)
    c: Coincident(g17,g18)
    c: Coincident(g18,g19)
    c: Coincident(g19,g14)
    c: Equal(g14, g15-g19) x5
    c: PointOnObject(g14,g20)
    c: PointOnObject(g15,g20)
    c: PointOnObject(g16,g20)
    c: PointOnObject(g17,g20)
    c: PointOnObject(g18,g20)
    c: PointOnObject(g19,g20)
    c: Diameter(g20) = 7
    c: DistanceY(g-1,g20) = 7
    c: Vertical(g18)
    c: Distance(g17,g-2) = 1
    c: Coincident(g21,g22)
    c: Coincident(g22,g23)
    c: Coincident(g23,g24)
    c: Coincident(g24,g25)
    c: Coincident(g25,g26)
    c: Coincident(g26,g21)
    c: Equal(g21, g22-g26) x5
    c: PointOnObject(g21,g27)
    c: PointOnObject(g22,g27)
    c: PointOnObject(g23,g27)
    c: PointOnObject(g24,g27)
    c: PointOnObject(g25,g27)
    c: PointOnObject(g26,g27)
    c: Diameter(g27) = 7
    c: DistanceY(g-1,g27) = 7
    c: DistanceX(g21,g-1) = 1
    c: Vertical(g21)
    c: Coincident(g28,g29)
    c: Coincident(g29,g30)
    c: Coincident(g30,g31)
    c: Coincident(g31,g32)
    c: Coincident(g32,g33)
    c: Coincident(g33,g28)
    c: Equal(g28, g29-g33) x5
    c: PointOnObject(g28,g34)
    c: PointOnObject(g29,g34)
    c: PointOnObject(g30,g34)
    c: PointOnObject(g31,g34)
    c: PointOnObject(g32,g34)
    c: PointOnObject(g33,g34)
    c: PointOnObject(g34,g-1)
    c: Diameter(g34) = 7
    c: Vertical(g31)
    c: DistanceX(g34,g-1) = 8
    c: Coincident(g35,g36)
    c: Coincident(g36,g37)
    c: Coincident(g37,g38)
    c: Coincident(g38,g39)
    c: Coincident(g39,g40)
    c: Coincident(g40,g35)
    c: Equal(g35, g36-g40) x5
    c: PointOnObject(g35,g41)
    c: PointOnObject(g36,g41)
    c: PointOnObject(g37,g41)
    c: PointOnObject(g38,g41)
    c: PointOnObject(g39,g41)
    c: PointOnObject(g40,g41)
    c: Coincident(g42,g43)
    c: Coincident(g43,g44)
    c: Coincident(g44,g45)
    c: Coincident(g45,g46)
    c: Coincident(g46,g47)
    c: Coincident(g47,g42)
    c: Equal(g42, g43-g47) x5
    c: PointOnObject(g42,g48)
    c: PointOnObject(g43,g48)
    c: PointOnObject(g44,g48)
    c: PointOnObject(g45,g48)
    c: PointOnObject(g46,g48)
    c: PointOnObject(g47,g48)
    c: Equal(g41,g48)
    c: Diameter(g41) = 7
    c: Vertical(g39)
    c: Vertical(g43)
    c: Distance(g-2,g39) = 1
    c: Symmetric(g38,g43,g-2)
    c: Distance(g41,g-1) = 7
FEATURE [Part::Extrusion] Extrude568  label="hex170"
  Base = -> Sketch577
  Dir = (0,-1,2e-16)
  DirMode = 2
  FaceMakerClass = Part::FaceMakerBullseye
  FaceMakerMode = 3
  LengthFwd = 10
  LengthRev = 0
  Placement = pos=(16,0,14) rot=(0,0,1;0rad)
  Solid = true
  Symmetric = false
FEATURE [Sketcher::SketchObject] Sketch578
  ArcFitTolerance = 1e-06
  FullyConstrained = true
  MakeInternals = false
  Placement = pos=(0,0,0) rot=(1,0,0;1.5708rad)
  sketch-geometry (49):
    g0: LineSegment StartX=1e-16 StartY=3.5 StartZ=0 EndX=-3.03109 EndY=1.75 EndZ=0
    g1: LineSegment StartX=-3.03109 StartY=1.75 StartZ=0 EndX=-3.03109 EndY=-1.75 EndZ=0
    g2: LineSegment StartX=-3.03109 StartY=-1.75 StartZ=0 EndX=-1e-16 EndY=-3.5 EndZ=0
    g3: LineSegment StartX=-1e-16 StartY=-3.5 StartZ=0 EndX=3.03109 EndY=-1.75 EndZ=0
    g4: LineSegment StartX=3.03109 StartY=-1.75 StartZ=0 EndX=3.03109 EndY=1.75 EndZ=0
    g5: LineSegment StartX=3.03109 StartY=1.75 StartZ=0 EndX=1e-16 EndY=3.5 EndZ=0
    g6: Circle [constr] CenterX=0 CenterY=0 CenterZ=0 NormalX=0 NormalY=0 NormalZ=1 AngleXU=0 Radius=3.5
    g7: LineSegment StartX=4.96892 StartY=-1.75002 StartZ=0 EndX=8.00002 EndY=-3.5 EndZ=0
    g8: LineSegment StartX=8.00002 StartY=-3.5 StartZ=0 EndX=11.0311 EndY=-1.74998 EndZ=0
    g9: LineSegment StartX=11.0311 StartY=-1.74998 StartZ=0 EndX=11.0311 EndY=1.75002 EndZ=0
    g10: LineSegment StartX=11.0311 StartY=1.75002 StartZ=0 EndX=7.99998 EndY=3.5 EndZ=0
    g11: LineSegment StartX=7.99998 StartY=3.5 StartZ=0 EndX=4.9689 EndY=1.74998 EndZ=0
    g12: LineSegment StartX=4.9689 StartY=1.74998 StartZ=0 EndX=4.96892 EndY=-1.75002 EndZ=0
    g13: Circle [constr] CenterX=8 CenterY=0 CenterZ=0 NormalX=0 NormalY=0 NormalZ=1 AngleXU=0 Radius=3.5
    g14: LineSegment StartX=4.03109 StartY=3.5 StartZ=0 EndX=7.06218 EndY=5.25 EndZ=0
    g15: LineSegment StartX=7.06218 StartY=5.25 StartZ=0 EndX=7.06218 EndY=8.75 EndZ=0
    g16: LineSegment StartX=7.06218 StartY=8.75 StartZ=0 EndX=4.03109 EndY=10.5 EndZ=0
    g17: LineSegment StartX=4.03109 StartY=10.5 StartZ=0 EndX=1 EndY=8.75 EndZ=0
    g18: LineSegment StartX=1 StartY=8.75 StartZ=0 EndX=1 EndY=5.25 EndZ=0
    g19: LineSegment StartX=1 StartY=5.25 StartZ=0 EndX=4.03109 EndY=3.5 EndZ=0
    g20: Circle [constr] CenterX=4.03109 CenterY=7 CenterZ=0 NormalX=0 NormalY=0 NormalZ=1 AngleXU=0 Radius=3.5
    g21: LineSegment StartX=-1 StartY=5.25 StartZ=0 EndX=-1 EndY=8.75 EndZ=0
    g22: LineSegment StartX=-1 StartY=8.75 StartZ=0 EndX=-4.03109 EndY=10.5 EndZ=0
    g23: LineSegment StartX=-4.03109 StartY=10.5 StartZ=0 EndX=-7.06218 EndY=8.75 EndZ=0
    g24: LineSegment StartX=-7.06218 StartY=8.75 StartZ=0 EndX=-7.06218 EndY=5.25 EndZ=0
    g25: LineSegment StartX=-7.06218 StartY=5.25 StartZ=0 EndX=-4.03109 EndY=3.5 EndZ=0
    g26: LineSegment StartX=-4.03109 StartY=3.5 StartZ=0 EndX=-1 EndY=5.25 EndZ=0
    g27: Circle [constr] CenterX=-4.03109 CenterY=7 CenterZ=0 NormalX=0 NormalY=0 NormalZ=1 AngleXU=0 Radius=3.5
    g28: LineSegment StartX=-4.96891 StartY=-1.75 StartZ=0 EndX=-4.96891 EndY=1.75 EndZ=0
    g29: LineSegment StartX=-4.96891 StartY=1.75 StartZ=0 EndX=-8 EndY=3.5 EndZ=0
    g30: LineSegment StartX=-8 StartY=3.5 StartZ=0 EndX=-11.0311 EndY=1.75 EndZ=0
    g31: LineSegment StartX=-11.0311 StartY=1.75 StartZ=0 EndX=-11.0311 EndY=-1.75 EndZ=0
    g32: LineSegment StartX=-11.0311 StartY=-1.75 StartZ=0 EndX=-8 EndY=-3.5 EndZ=0
    g33: LineSegment StartX=-8 StartY=-3.5 StartZ=0 EndX=-4.96891 EndY=-1.75 EndZ=0
    g34: Circle [constr] CenterX=-8 CenterY=0 CenterZ=0 NormalX=0 NormalY=0 NormalZ=1 AngleXU=0 Radius=3.5
    g35: LineSegment StartX=-4.03109 StartY=-3.5 StartZ=0 EndX=-7.06218 EndY=-5.25 EndZ=0
    g36: LineSegment StartX=-7.06218 StartY=-5.25 StartZ=0 EndX=-7.06218 EndY=-8.75 EndZ=0
    g37: LineSegment StartX=-7.06218 StartY=-8.75 StartZ=0 EndX=-4.03109 EndY=-10.5 EndZ=0
    g38: LineSegment StartX=-4.03109 StartY=-10.5 StartZ=0 EndX=-1 EndY=-8.75 EndZ=0
    g39: LineSegment StartX=-1 StartY=-8.75 StartZ=0 EndX=-1 EndY=-5.25 EndZ=0
    g40: LineSegment StartX=-1 StartY=-5.25 StartZ=0 EndX=-4.03109 EndY=-3.5 EndZ=0
    g41: Circle [constr] CenterX=-4.03109 CenterY=-7 CenterZ=0 NormalX=0 NormalY=0 NormalZ=1 AngleXU=0 Radius=3.5
    g42: LineSegment StartX=4.03109 StartY=-3.5 StartZ=0 EndX=1 EndY=-5.25 EndZ=0
    g43: LineSegment StartX=1 StartY=-5.25 StartZ=0 EndX=1 EndY=-8.75 EndZ=0
    g44: LineSegment StartX=1 StartY=-8.75 StartZ=0 EndX=4.03109 EndY=-10.5 EndZ=0
    g45: LineSegment StartX=4.03109 StartY=-10.5 StartZ=0 EndX=7.06218 EndY=-8.75 EndZ=0
    g46: LineSegment StartX=7.06218 StartY=-8.75 StartZ=0 EndX=7.06218 EndY=-5.25 EndZ=0
    g47: LineSegment StartX=7.06218 StartY=-5.25 StartZ=0 EndX=4.03109 EndY=-3.5 EndZ=0
    g48: Circle [constr] CenterX=4.03109 CenterY=-7 CenterZ=0 NormalX=0 NormalY=0 NormalZ=1 AngleXU=0 Radius=3.5
  constraints (117):
    c: Coincident(g0,g1)
    c: Coincident(g1,g2)
    c: Coincident(g2,g3)
    c: Coincident(g3,g4)
    c: Coincident(g4,g5)
    c: Coincident(g5,g0)
    c: Equal(g0, g1-g5) x5
    c: PointOnObject(g0,g6)
    c: PointOnObject(g1,g6)
    c: PointOnObject(g2,g6)
    c: PointOnObject(g3,g6)
    c: PointOnObject(g4,g6)
    c: PointOnObject(g5,g6)
    c: Coincident(g6,g-1)
    c: Diameter(g6) = 7
    c: PointOnObject(g0,g-2)
    c: Coincident(g7,g8)
    c: Coincident(g8,g9)
    c: Coincident(g9,g10)
    c: Coincident(g10,g11)
    c: Coincident(g11,g12)
    c: Coincident(g12,g7)
    c: Equal(g7, g8-g12) x5
    c: PointOnObject(g7,g13)
    c: PointOnObject(g8,g13)
    c: PointOnObject(g9,g13)
    c: PointOnObject(g10,g13)
    c: PointOnObject(g11,g13)
    c: PointOnObject(g12,g13)
    c: PointOnObject(g13,g-1)
    c: Diameter(g13) = 7
    c: Distance(g6,g13) = 8
    c: Horizontal(g0,g10)
    c: Coincident(g14,g15)
    c: Coincident(g15,g16)
    c: Coincident(g16,g17)
    c: Coincident(g17,g18)
    c: Coincident(g18,g19)
    c: Coincident(g19,g14)
    c: Equal(g14, g15-g19) x5
    c: PointOnObject(g14,g20)
    c: PointOnObject(g15,g20)
    c: PointOnObject(g16,g20)
    c: PointOnObject(g17,g20)
    c: PointOnObject(g18,g20)
    c: PointOnObject(g19,g20)
    c: Diameter(g20) = 7
    c: DistanceY(g-1,g20) = 7
    c: Vertical(g18)
    c: Distance(g17,g-2) = 1
    c: Coincident(g21,g22)
    c: Coincident(g22,g23)
    c: Coincident(g23,g24)
    c: Coincident(g24,g25)
    c: Coincident(g25,g26)
    c: Coincident(g26,g21)
    c: Equal(g21, g22-g26) x5
    c: PointOnObject(g21,g27)
    c: PointOnObject(g22,g27)
    c: PointOnObject(g23,g27)
    c: PointOnObject(g24,g27)
    c: PointOnObject(g25,g27)
    c: PointOnObject(g26,g27)
    c: Diameter(g27) = 7
    c: DistanceY(g-1,g27) = 7
    c: DistanceX(g21,g-1) = 1
    c: Vertical(g21)
    c: Coincident(g28,g29)
    c: Coincident(g29,g30)
    c: Coincident(g30,g31)
    c: Coincident(g31,g32)
    c: Coincident(g32,g33)
    c: Coincident(g33,g28)
    c: Equal(g28, g29-g33) x5
    c: PointOnObject(g28,g34)
    c: PointOnObject(g29,g34)
    c: PointOnObject(g30,g34)
    c: PointOnObject(g31,g34)
    c: PointOnObject(g32,g34)
    c: PointOnObject(g33,g34)
    c: PointOnObject(g34,g-1)
    c: Diameter(g34) = 7
    c: Vertical(g31)
    c: DistanceX(g34,g-1) = 8
    c: Coincident(g35,g36)
    c: Coincident(g36,g37)
    c: Coincident(g37,g38)
    c: Coincident(g38,g39)
    c: Coincident(g39,g40)
    c: Coincident(g40,g35)
    c: Equal(g35, g36-g40) x5
    c: PointOnObject(g35,g41)
    c: PointOnObject(g36,g41)
    c: PointOnObject(g37,g41)
    c: PointOnObject(g38,g41)
    c: PointOnObject(g39,g41)
    c: PointOnObject(g40,g41)
    c: Coincident(g42,g43)
    c: Coincident(g43,g44)
    c: Coincident(g44,g45)
    c: Coincident(g45,g46)
    c: Coincident(g46,g47)
    c: Coincident(g47,g42)
    c: Equal(g42, g43-g47) x5
    c: PointOnObject(g42,g48)
    c: PointOnObject(g43,g48)
    c: PointOnObject(g44,g48)
    c: PointOnObject(g45,g48)
    c: PointOnObject(g46,g48)
    c: PointOnObject(g47,g48)
    c: Equal(g41,g48)
    c: Diameter(g41) = 7
    c: Vertical(g39)
    c: Vertical(g43)
    c: Distance(g-2,g39) = 1
    c: Symmetric(g38,g43,g-2)
    c: Distance(g41,g-1) = 7
FEATURE [Part::Extrusion] Extrude569  label="hex171"
  Base = -> Sketch578
  Dir = (0,-1,2e-16)
  DirMode = 2
  FaceMakerClass = Part::FaceMakerBullseye
  FaceMakerMode = 3
  LengthFwd = 10
  LengthRev = 0
  Placement = pos=(-20,0,-7) rot=(0,0,1;0rad)
  Solid = true
  Symmetric = false
FEATURE [Sketcher::SketchObject] Sketch579
  ArcFitTolerance = 1e-06
  FullyConstrained = true
  MakeInternals = false
  Placement = pos=(0,0,0) rot=(1,0,0;1.5708rad)
  sketch-geometry (49):
    g0: LineSegment StartX=1e-16 StartY=3.5 StartZ=0 EndX=-3.03109 EndY=1.75 EndZ=0
    g1: LineSegment StartX=-3.03109 StartY=1.75 StartZ=0 EndX=-3.03109 EndY=-1.75 EndZ=0
    g2: LineSegment StartX=-3.03109 StartY=-1.75 StartZ=0 EndX=-1e-16 EndY=-3.5 EndZ=0
    g3: LineSegment StartX=-1e-16 StartY=-3.5 StartZ=0 EndX=3.03109 EndY=-1.75 EndZ=0
    g4: LineSegment StartX=3.03109 StartY=-1.75 StartZ=0 EndX=3.03109 EndY=1.75 EndZ=0
    g5: LineSegment StartX=3.03109 StartY=1.75 StartZ=0 EndX=1e-16 EndY=3.5 EndZ=0
    g6: Circle [constr] CenterX=0 CenterY=0 CenterZ=0 NormalX=0 NormalY=0 NormalZ=1 AngleXU=0 Radius=3.5
    g7: LineSegment StartX=4.96892 StartY=-1.75002 StartZ=0 EndX=8.00002 EndY=-3.5 EndZ=0
    g8: LineSegment StartX=8.00002 StartY=-3.5 StartZ=0 EndX=11.0311 EndY=-1.74998 EndZ=0
    g9: LineSegment StartX=11.0311 StartY=-1.74998 StartZ=0 EndX=11.0311 EndY=1.75002 EndZ=0
    g10: LineSegment StartX=11.0311 StartY=1.75002 StartZ=0 EndX=7.99998 EndY=3.5 EndZ=0
    g11: LineSegment StartX=7.99998 StartY=3.5 StartZ=0 EndX=4.9689 EndY=1.74998 EndZ=0
    g12: LineSegment StartX=4.9689 StartY=1.74998 StartZ=0 EndX=4.96892 EndY=-1.75002 EndZ=0
    g13: Circle [constr] CenterX=8 CenterY=0 CenterZ=0 NormalX=0 NormalY=0 NormalZ=1 AngleXU=0 Radius=3.5
    g14: LineSegment StartX=4.03109 StartY=3.5 StartZ=0 EndX=7.06218 EndY=5.25 EndZ=0
    g15: LineSegment StartX=7.06218 StartY=5.25 StartZ=0 EndX=7.06218 EndY=8.75 EndZ=0
    g16: LineSegment StartX=7.06218 StartY=8.75 StartZ=0 EndX=4.03109 EndY=10.5 EndZ=0
    g17: LineSegment StartX=4.03109 StartY=10.5 StartZ=0 EndX=1 EndY=8.75 EndZ=0
    g18: LineSegment StartX=1 StartY=8.75 StartZ=0 EndX=1 EndY=5.25 EndZ=0
    g19: LineSegment StartX=1 StartY=5.25 StartZ=0 EndX=4.03109 EndY=3.5 EndZ=0
    g20: Circle [constr] CenterX=4.03109 CenterY=7 CenterZ=0 NormalX=0 NormalY=0 NormalZ=1 AngleXU=0 Radius=3.5
    g21: LineSegment StartX=-1 StartY=5.25 StartZ=0 EndX=-1 EndY=8.75 EndZ=0
    g22: LineSegment StartX=-1 StartY=8.75 StartZ=0 EndX=-4.03109 EndY=10.5 EndZ=0
    g23: LineSegment StartX=-4.03109 StartY=10.5 StartZ=0 EndX=-7.06218 EndY=8.75 EndZ=0
    g24: LineSegment StartX=-7.06218 StartY=8.75 StartZ=0 EndX=-7.06218 EndY=5.25 EndZ=0
    g25: LineSegment StartX=-7.06218 StartY=5.25 StartZ=0 EndX=-4.03109 EndY=3.5 EndZ=0
    g26: LineSegment StartX=-4.03109 StartY=3.5 StartZ=0 EndX=-1 EndY=5.25 EndZ=0
    g27: Circle [constr] CenterX=-4.03109 CenterY=7 CenterZ=0 NormalX=0 NormalY=0 NormalZ=1 AngleXU=0 Radius=3.5
    g28: LineSegment StartX=-4.96891 StartY=-1.75 StartZ=0 EndX=-4.96891 EndY=1.75 EndZ=0
    g29: LineSegment StartX=-4.96891 StartY=1.75 StartZ=0 EndX=-8 EndY=3.5 EndZ=0
    g30: LineSegment StartX=-8 StartY=3.5 StartZ=0 EndX=-11.0311 EndY=1.75 EndZ=0
    g31: LineSegment StartX=-11.0311 StartY=1.75 StartZ=0 EndX=-11.0311 EndY=-1.75 EndZ=0
    g32: LineSegment StartX=-11.0311 StartY=-1.75 StartZ=0 EndX=-8 EndY=-3.5 EndZ=0
    g33: LineSegment StartX=-8 StartY=-3.5 StartZ=0 EndX=-4.96891 EndY=-1.75 EndZ=0
    g34: Circle [constr] CenterX=-8 CenterY=0 CenterZ=0 NormalX=0 NormalY=0 NormalZ=1 AngleXU=0 Radius=3.5
    g35: LineSegment StartX=-4.03109 StartY=-3.5 StartZ=0 EndX=-7.06218 EndY=-5.25 EndZ=0
    g36: LineSegment StartX=-7.06218 StartY=-5.25 StartZ=0 EndX=-7.06218 EndY=-8.75 EndZ=0
    g37: LineSegment StartX=-7.06218 StartY=-8.75 StartZ=0 EndX=-4.03109 EndY=-10.5 EndZ=0
    g38: LineSegment StartX=-4.03109 StartY=-10.5 StartZ=0 EndX=-1 EndY=-8.75 EndZ=0
    g39: LineSegment StartX=-1 StartY=-8.75 StartZ=0 EndX=-1 EndY=-5.25 EndZ=0
    g40: LineSegment StartX=-1 StartY=-5.25 StartZ=0 EndX=-4.03109 EndY=-3.5 EndZ=0
    g41: Circle [constr] CenterX=-4.03109 CenterY=-7 CenterZ=0 NormalX=0 NormalY=0 NormalZ=1 AngleXU=0 Radius=3.5
    g42: LineSegment StartX=4.03109 StartY=-3.5 StartZ=0 EndX=1 EndY=-5.25 EndZ=0
    g43: LineSegment StartX=1 StartY=-5.25 StartZ=0 EndX=1 EndY=-8.75 EndZ=0
    g44: LineSegment StartX=1 StartY=-8.75 StartZ=0 EndX=4.03109 EndY=-10.5 EndZ=0
    g45: LineSegment StartX=4.03109 StartY=-10.5 StartZ=0 EndX=7.06218 EndY=-8.75 EndZ=0
    g46: LineSegment StartX=7.06218 StartY=-8.75 StartZ=0 EndX=7.06218 EndY=-5.25 EndZ=0
    g47: LineSegment StartX=7.06218 StartY=-5.25 StartZ=0 EndX=4.03109 EndY=-3.5 EndZ=0
    g48: Circle [constr] CenterX=4.03109 CenterY=-7 CenterZ=0 NormalX=0 NormalY=0 NormalZ=1 AngleXU=0 Radius=3.5
  constraints (117):
    c: Coincident(g0,g1)
    c: Coincident(g1,g2)
    c: Coincident(g2,g3)
    c: Coincident(g3,g4)
    c: Coincident(g4,g5)
    c: Coincident(g5,g0)
    c: Equal(g0, g1-g5) x5
    c: PointOnObject(g0,g6)
    c: PointOnObject(g1,g6)
    c: PointOnObject(g2,g6)
    c: PointOnObject(g3,g6)
    c: PointOnObject(g4,g6)
    c: PointOnObject(g5,g6)
    c: Coincident(g6,g-1)
    c: Diameter(g6) = 7
    c: PointOnObject(g0,g-2)
    c: Coincident(g7,g8)
    c: Coincident(g8,g9)
    c: Coincident(g9,g10)
    c: Coincident(g10,g11)
    c: Coincident(g11,g12)
    c: Coincident(g12,g7)
    c: Equal(g7, g8-g12) x5
    c: PointOnObject(g7,g13)
    c: PointOnObject(g8,g13)
    c: PointOnObject(g9,g13)
    c: PointOnObject(g10,g13)
    c: PointOnObject(g11,g13)
    c: PointOnObject(g12,g13)
    c: PointOnObject(g13,g-1)
    c: Diameter(g13) = 7
    c: Distance(g6,g13) = 8
    c: Horizontal(g0,g10)
    c: Coincident(g14,g15)
    c: Coincident(g15,g16)
    c: Coincident(g16,g17)
    c: Coincident(g17,g18)
    c: Coincident(g18,g19)
    c: Coincident(g19,g14)
    c: Equal(g14, g15-g19) x5
    c: PointOnObject(g14,g20)
    c: PointOnObject(g15,g20)
    c: PointOnObject(g16,g20)
    c: PointOnObject(g17,g20)
    c: PointOnObject(g18,g20)
    c: PointOnObject(g19,g20)
    c: Diameter(g20) = 7
    c: DistanceY(g-1,g20) = 7
    c: Vertical(g18)
    c: Distance(g17,g-2) = 1
    c: Coincident(g21,g22)
    c: Coincident(g22,g23)
    c: Coincident(g23,g24)
    c: Coincident(g24,g25)
    c: Coincident(g25,g26)
    c: Coincident(g26,g21)
    c: Equal(g21, g22-g26) x5
    c: PointOnObject(g21,g27)
    c: PointOnObject(g22,g27)
    c: PointOnObject(g23,g27)
    c: PointOnObject(g24,g27)
    c: PointOnObject(g25,g27)
    c: PointOnObject(g26,g27)
    c: Diameter(g27) = 7
    c: DistanceY(g-1,g27) = 7
    c: DistanceX(g21,g-1) = 1
    c: Vertical(g21)
    c: Coincident(g28,g29)
    c: Coincident(g29,g30)
    c: Coincident(g30,g31)
    c: Coincident(g31,g32)
    c: Coincident(g32,g33)
    c: Coincident(g33,g28)
    c: Equal(g28, g29-g33) x5
    c: PointOnObject(g28,g34)
    c: PointOnObject(g29,g34)
    c: PointOnObject(g30,g34)
    c: PointOnObject(g31,g34)
    c: PointOnObject(g32,g34)
    c: PointOnObject(g33,g34)
    c: PointOnObject(g34,g-1)
    c: Diameter(g34) = 7
    c: Vertical(g31)
    c: DistanceX(g34,g-1) = 8
    c: Coincident(g35,g36)
    c: Coincident(g36,g37)
    c: Coincident(g37,g38)
    c: Coincident(g38,g39)
    c: Coincident(g39,g40)
    c: Coincident(g40,g35)
    c: Equal(g35, g36-g40) x5
    c: PointOnObject(g35,g41)
    c: PointOnObject(g36,g41)
    c: PointOnObject(g37,g41)
    c: PointOnObject(g38,g41)
    c: PointOnObject(g39,g41)
    c: PointOnObject(g40,g41)
    c: Coincident(g42,g43)
    c: Coincident(g43,g44)
    c: Coincident(g44,g45)
    c: Coincident(g45,g46)
    c: Coincident(g46,g47)
    c: Coincident(g47,g42)
    c: Equal(g42, g43-g47) x5
    c: PointOnObject(g42,g48)
    c: PointOnObject(g43,g48)
    c: PointOnObject(g44,g48)
    c: PointOnObject(g45,g48)
    c: PointOnObject(g46,g48)
    c: PointOnObject(g47,g48)
    c: Equal(g41,g48)
    c: Diameter(g41) = 7
    c: Vertical(g39)
    c: Vertical(g43)
    c: Distance(g-2,g39) = 1
    c: Symmetric(g38,g43,g-2)
    c: Distance(g41,g-1) = 7
FEATURE [Part::Extrusion] Extrude570  label="hex172"
  Base = -> Sketch579
  Dir = (0,-1,2e-16)
  DirMode = 2
  FaceMakerClass = Part::FaceMakerBullseye
  FaceMakerMode = 3
  LengthFwd = 10
  LengthRev = 0
  Placement = pos=(-16,0,14) rot=(0,0,1;0rad)
  Solid = true
  Symmetric = false
FEATURE [Sketcher::SketchObject] Sketch580
  ArcFitTolerance = 1e-06
  FullyConstrained = true
  MakeInternals = false
  Placement = pos=(0,0,0) rot=(1,0,0;1.5708rad)
  sketch-geometry (49):
    g0: LineSegment StartX=1e-16 StartY=3.5 StartZ=0 EndX=-3.03109 EndY=1.75 EndZ=0
    g1: LineSegment StartX=-3.03109 StartY=1.75 StartZ=0 EndX=-3.03109 EndY=-1.75 EndZ=0
    g2: LineSegment StartX=-3.03109 StartY=-1.75 StartZ=0 EndX=-1e-16 EndY=-3.5 EndZ=0
    g3: LineSegment StartX=-1e-16 StartY=-3.5 StartZ=0 EndX=3.03109 EndY=-1.75 EndZ=0
    g4: LineSegment StartX=3.03109 StartY=-1.75 StartZ=0 EndX=3.03109 EndY=1.75 EndZ=0
    g5: LineSegment StartX=3.03109 StartY=1.75 StartZ=0 EndX=1e-16 EndY=3.5 EndZ=0
    g6: Circle [constr] CenterX=0 CenterY=0 CenterZ=0 NormalX=0 NormalY=0 NormalZ=1 AngleXU=0 Radius=3.5
    g7: LineSegment StartX=4.96892 StartY=-1.75002 StartZ=0 EndX=8.00002 EndY=-3.5 EndZ=0
    g8: LineSegment StartX=8.00002 StartY=-3.5 StartZ=0 EndX=11.0311 EndY=-1.74998 EndZ=0
    g9: LineSegment StartX=11.0311 StartY=-1.74998 StartZ=0 EndX=11.0311 EndY=1.75002 EndZ=0
    g10: LineSegment StartX=11.0311 StartY=1.75002 StartZ=0 EndX=7.99998 EndY=3.5 EndZ=0
    g11: LineSegment StartX=7.99998 StartY=3.5 StartZ=0 EndX=4.9689 EndY=1.74998 EndZ=0
    g12: LineSegment StartX=4.9689 StartY=1.74998 StartZ=0 EndX=4.96892 EndY=-1.75002 EndZ=0
    g13: Circle [constr] CenterX=8 CenterY=0 CenterZ=0 NormalX=0 NormalY=0 NormalZ=1 AngleXU=0 Radius=3.5
    g14: LineSegment StartX=4.03109 StartY=3.5 StartZ=0 EndX=7.06218 EndY=5.25 EndZ=0
    g15: LineSegment StartX=7.06218 StartY=5.25 StartZ=0 EndX=7.06218 EndY=8.75 EndZ=0
    g16: LineSegment StartX=7.06218 StartY=8.75 StartZ=0 EndX=4.03109 EndY=10.5 EndZ=0
    g17: LineSegment StartX=4.03109 StartY=10.5 StartZ=0 EndX=1 EndY=8.75 EndZ=0
    g18: LineSegment StartX=1 StartY=8.75 StartZ=0 EndX=1 EndY=5.25 EndZ=0
    g19: LineSegment StartX=1 StartY=5.25 StartZ=0 EndX=4.03109 EndY=3.5 EndZ=0
    g20: Circle [constr] CenterX=4.03109 CenterY=7 CenterZ=0 NormalX=0 NormalY=0 NormalZ=1 AngleXU=0 Radius=3.5
    g21: LineSegment StartX=-1 StartY=5.25 StartZ=0 EndX=-1 EndY=8.75 EndZ=0
    g22: LineSegment StartX=-1 StartY=8.75 StartZ=0 EndX=-4.03109 EndY=10.5 EndZ=0
    g23: LineSegment StartX=-4.03109 StartY=10.5 StartZ=0 EndX=-7.06218 EndY=8.75 EndZ=0
    g24: LineSegment StartX=-7.06218 StartY=8.75 StartZ=0 EndX=-7.06218 EndY=5.25 EndZ=0
    g25: LineSegment StartX=-7.06218 StartY=5.25 StartZ=0 EndX=-4.03109 EndY=3.5 EndZ=0
    g26: LineSegment StartX=-4.03109 StartY=3.5 StartZ=0 EndX=-1 EndY=5.25 EndZ=0
    g27: Circle [constr] CenterX=-4.03109 CenterY=7 CenterZ=0 NormalX=0 NormalY=0 NormalZ=1 AngleXU=0 Radius=3.5
    g28: LineSegment StartX=-4.96891 StartY=-1.75 StartZ=0 EndX=-4.96891 EndY=1.75 EndZ=0
    g29: LineSegment StartX=-4.96891 StartY=1.75 StartZ=0 EndX=-8 EndY=3.5 EndZ=0
    g30: LineSegment StartX=-8 StartY=3.5 StartZ=0 EndX=-11.0311 EndY=1.75 EndZ=0
    g31: LineSegment StartX=-11.0311 StartY=1.75 StartZ=0 EndX=-11.0311 EndY=-1.75 EndZ=0
    g32: LineSegment StartX=-11.0311 StartY=-1.75 StartZ=0 EndX=-8 EndY=-3.5 EndZ=0
    g33: LineSegment StartX=-8 StartY=-3.5 StartZ=0 EndX=-4.96891 EndY=-1.75 EndZ=0
    g34: Circle [constr] CenterX=-8 CenterY=0 CenterZ=0 NormalX=0 NormalY=0 NormalZ=1 AngleXU=0 Radius=3.5
    g35: LineSegment StartX=-4.03109 StartY=-3.5 StartZ=0 EndX=-7.06218 EndY=-5.25 EndZ=0
    g36: LineSegment StartX=-7.06218 StartY=-5.25 StartZ=0 EndX=-7.06218 EndY=-8.75 EndZ=0
    g37: LineSegment StartX=-7.06218 StartY=-8.75 StartZ=0 EndX=-4.03109 EndY=-10.5 EndZ=0
    g38: LineSegment StartX=-4.03109 StartY=-10.5 StartZ=0 EndX=-1 EndY=-8.75 EndZ=0
    g39: LineSegment StartX=-1 StartY=-8.75 StartZ=0 EndX=-1 EndY=-5.25 EndZ=0
    g40: LineSegment StartX=-1 StartY=-5.25 StartZ=0 EndX=-4.03109 EndY=-3.5 EndZ=0
    g41: Circle [constr] CenterX=-4.03109 CenterY=-7 CenterZ=0 NormalX=0 NormalY=0 NormalZ=1 AngleXU=0 Radius=3.5
    g42: LineSegment StartX=4.03109 StartY=-3.5 StartZ=0 EndX=1 EndY=-5.25 EndZ=0
    g43: LineSegment StartX=1 StartY=-5.25 StartZ=0 EndX=1 EndY=-8.75 EndZ=0
    g44: LineSegment StartX=1 StartY=-8.75 StartZ=0 EndX=4.03109 EndY=-10.5 EndZ=0
    g45: LineSegment StartX=4.03109 StartY=-10.5 StartZ=0 EndX=7.06218 EndY=-8.75 EndZ=0
    g46: LineSegment StartX=7.06218 StartY=-8.75 StartZ=0 EndX=7.06218 EndY=-5.25 EndZ=0
    g47: LineSegment StartX=7.06218 StartY=-5.25 StartZ=0 EndX=4.03109 EndY=-3.5 EndZ=0
    g48: Circle [constr] CenterX=4.03109 CenterY=-7 CenterZ=0 NormalX=0 NormalY=0 NormalZ=1 AngleXU=0 Radius=3.5
  constraints (117):
    c: Coincident(g0,g1)
    c: Coincident(g1,g2)
    c: Coincident(g2,g3)
    c: Coincident(g3,g4)
    c: Coincident(g4,g5)
    c: Coincident(g5,g0)
    c: Equal(g0, g1-g5) x5
    c: PointOnObject(g0,g6)
    c: PointOnObject(g1,g6)
    c: PointOnObject(g2,g6)
    c: PointOnObject(g3,g6)
    c: PointOnObject(g4,g6)
    c: PointOnObject(g5,g6)
    c: Coincident(g6,g-1)
    c: Diameter(g6) = 7
    c: PointOnObject(g0,g-2)
    c: Coincident(g7,g8)
    c: Coincident(g8,g9)
    c: Coincident(g9,g10)
    c: Coincident(g10,g11)
    c: Coincident(g11,g12)
    c: Coincident(g12,g7)
    c: Equal(g7, g8-g12) x5
    c: PointOnObject(g7,g13)
    c: PointOnObject(g8,g13)
    c: PointOnObject(g9,g13)
    c: PointOnObject(g10,g13)
    c: PointOnObject(g11,g13)
    c: PointOnObject(g12,g13)
    c: PointOnObject(g13,g-1)
    c: Diameter(g13) = 7
    c: Distance(g6,g13) = 8
    c: Horizontal(g0,g10)
    c: Coincident(g14,g15)
    c: Coincident(g15,g16)
    c: Coincident(g16,g17)
    c: Coincident(g17,g18)
    c: Coincident(g18,g19)
    c: Coincident(g19,g14)
    c: Equal(g14, g15-g19) x5
    c: PointOnObject(g14,g20)
    c: PointOnObject(g15,g20)
    c: PointOnObject(g16,g20)
    c: PointOnObject(g17,g20)
    c: PointOnObject(g18,g20)
    c: PointOnObject(g19,g20)
    c: Diameter(g20) = 7
    c: DistanceY(g-1,g20) = 7
    c: Vertical(g18)
    c: Distance(g17,g-2) = 1
    c: Coincident(g21,g22)
    c: Coincident(g22,g23)
    c: Coincident(g23,g24)
    c: Coincident(g24,g25)
    c: Coincident(g25,g26)
    c: Coincident(g26,g21)
    c: Equal(g21, g22-g26) x5
    c: PointOnObject(g21,g27)
    c: PointOnObject(g22,g27)
    c: PointOnObject(g23,g27)
    c: PointOnObject(g24,g27)
    c: PointOnObject(g25,g27)
    c: PointOnObject(g26,g27)
    c: Diameter(g27) = 7
    c: DistanceY(g-1,g27) = 7
    c: DistanceX(g21,g-1) = 1
    c: Vertical(g21)
    c: Coincident(g28,g29)
    c: Coincident(g29,g30)
    c: Coincident(g30,g31)
    c: Coincident(g31,g32)
    c: Coincident(g32,g33)
    c: Coincident(g33,g28)
    c: Equal(g28, g29-g33) x5
    c: PointOnObject(g28,g34)
    c: PointOnObject(g29,g34)
    c: PointOnObject(g30,g34)
    c: PointOnObject(g31,g34)
    c: PointOnObject(g32,g34)
    c: PointOnObject(g33,g34)
    c: PointOnObject(g34,g-1)
    c: Diameter(g34) = 7
    c: Vertical(g31)
    c: DistanceX(g34,g-1) = 8
    c: Coincident(g35,g36)
    c: Coincident(g36,g37)
    c: Coincident(g37,g38)
    c: Coincident(g38,g39)
    c: Coincident(g39,g40)
    c: Coincident(g40,g35)
    c: Equal(g35, g36-g40) x5
    c: PointOnObject(g35,g41)
    c: PointOnObject(g36,g41)
    c: PointOnObject(g37,g41)
    c: PointOnObject(g38,g41)
    c: PointOnObject(g39,g41)
    c: PointOnObject(g40,g41)
    c: Coincident(g42,g43)
    c: Coincident(g43,g44)
    c: Coincident(g44,g45)
    c: Coincident(g45,g46)
    c: Coincident(g46,g47)
    c: Coincident(g47,g42)
    c: Equal(g42, g43-g47) x5
    c: PointOnObject(g42,g48)
    c: PointOnObject(g43,g48)
    c: PointOnObject(g44,g48)
    c: PointOnObject(g45,g48)
    c: PointOnObject(g46,g48)
    c: PointOnObject(g47,g48)
    c: Equal(g41,g48)
    c: Diameter(g41) = 7
    c: Vertical(g39)
    c: Vertical(g43)
    c: Distance(g-2,g39) = 1
    c: Symmetric(g38,g43,g-2)
    c: Distance(g41,g-1) = 7
FEATURE [Part::Extrusion] Extrude571  label="hex173"
  Base = -> Sketch580
  Dir = (0,-1,2e-16)
  DirMode = 2
  FaceMakerClass = Part::FaceMakerBullseye
  FaceMakerMode = 3
  LengthFwd = 10
  LengthRev = 0
  Placement = pos=(-4,0,-21) rot=(0,0,1;0rad)
  Solid = true
  Symmetric = false
FEATURE [Sketcher::SketchObject] Sketch581
  ArcFitTolerance = 1e-06
  FullyConstrained = true
  MakeInternals = false
  Placement = pos=(0,0,0) rot=(1,0,0;1.5708rad)
  sketch-geometry (49):
    g0: LineSegment StartX=1e-16 StartY=3.5 StartZ=0 EndX=-3.03109 EndY=1.75 EndZ=0
    g1: LineSegment StartX=-3.03109 StartY=1.75 StartZ=0 EndX=-3.03109 EndY=-1.75 EndZ=0
    g2: LineSegment StartX=-3.03109 StartY=-1.75 StartZ=0 EndX=-1e-16 EndY=-3.5 EndZ=0
    g3: LineSegment StartX=-1e-16 StartY=-3.5 StartZ=0 EndX=3.03109 EndY=-1.75 EndZ=0
    g4: LineSegment StartX=3.03109 StartY=-1.75 StartZ=0 EndX=3.03109 EndY=1.75 EndZ=0
    g5: LineSegment StartX=3.03109 StartY=1.75 StartZ=0 EndX=1e-16 EndY=3.5 EndZ=0
    g6: Circle [constr] CenterX=0 CenterY=0 CenterZ=0 NormalX=0 NormalY=0 NormalZ=1 AngleXU=0 Radius=3.5
    g7: LineSegment StartX=4.96892 StartY=-1.75002 StartZ=0 EndX=8.00002 EndY=-3.5 EndZ=0
    g8: LineSegment StartX=8.00002 StartY=-3.5 StartZ=0 EndX=11.0311 EndY=-1.74998 EndZ=0
    g9: LineSegment StartX=11.0311 StartY=-1.74998 StartZ=0 EndX=11.0311 EndY=1.75002 EndZ=0
    g10: LineSegment StartX=11.0311 StartY=1.75002 StartZ=0 EndX=7.99998 EndY=3.5 EndZ=0
    g11: LineSegment StartX=7.99998 StartY=3.5 StartZ=0 EndX=4.9689 EndY=1.74998 EndZ=0
    g12: LineSegment StartX=4.9689 StartY=1.74998 StartZ=0 EndX=4.96892 EndY=-1.75002 EndZ=0
    g13: Circle [constr] CenterX=8 CenterY=0 CenterZ=0 NormalX=0 NormalY=0 NormalZ=1 AngleXU=0 Radius=3.5
    g14: LineSegment StartX=4.03109 StartY=3.5 StartZ=0 EndX=7.06218 EndY=5.25 EndZ=0
    g15: LineSegment StartX=7.06218 StartY=5.25 StartZ=0 EndX=7.06218 EndY=8.75 EndZ=0
    g16: LineSegment StartX=7.06218 StartY=8.75 StartZ=0 EndX=4.03109 EndY=10.5 EndZ=0
    g17: LineSegment StartX=4.03109 StartY=10.5 StartZ=0 EndX=1 EndY=8.75 EndZ=0
    g18: LineSegment StartX=1 StartY=8.75 StartZ=0 EndX=1 EndY=5.25 EndZ=0
    g19: LineSegment StartX=1 StartY=5.25 StartZ=0 EndX=4.03109 EndY=3.5 EndZ=0
    g20: Circle [constr] CenterX=4.03109 CenterY=7 CenterZ=0 NormalX=0 NormalY=0 NormalZ=1 AngleXU=0 Radius=3.5
    g21: LineSegment StartX=-1 StartY=5.25 StartZ=0 EndX=-1 EndY=8.75 EndZ=0
    g22: LineSegment StartX=-1 StartY=8.75 StartZ=0 EndX=-4.03109 EndY=10.5 EndZ=0
    g23: LineSegment StartX=-4.03109 StartY=10.5 StartZ=0 EndX=-7.06218 EndY=8.75 EndZ=0
    g24: LineSegment StartX=-7.06218 StartY=8.75 StartZ=0 EndX=-7.06218 EndY=5.25 EndZ=0
    g25: LineSegment StartX=-7.06218 StartY=5.25 StartZ=0 EndX=-4.03109 EndY=3.5 EndZ=0
    g26: LineSegment StartX=-4.03109 StartY=3.5 StartZ=0 EndX=-1 EndY=5.25 EndZ=0
    g27: Circle [constr] CenterX=-4.03109 CenterY=7 CenterZ=0 NormalX=0 NormalY=0 NormalZ=1 AngleXU=0 Radius=3.5
    g28: LineSegment StartX=-4.96891 StartY=-1.75 StartZ=0 EndX=-4.96891 EndY=1.75 EndZ=0
    g29: LineSegment StartX=-4.96891 StartY=1.75 StartZ=0 EndX=-8 EndY=3.5 EndZ=0
    g30: LineSegment StartX=-8 StartY=3.5 StartZ=0 EndX=-11.0311 EndY=1.75 EndZ=0
    g31: LineSegment StartX=-11.0311 StartY=1.75 StartZ=0 EndX=-11.0311 EndY=-1.75 EndZ=0
    g32: LineSegment StartX=-11.0311 StartY=-1.75 StartZ=0 EndX=-8 EndY=-3.5 EndZ=0
    g33: LineSegment StartX=-8 StartY=-3.5 StartZ=0 EndX=-4.96891 EndY=-1.75 EndZ=0
    g34: Circle [constr] CenterX=-8 CenterY=0 CenterZ=0 NormalX=0 NormalY=0 NormalZ=1 AngleXU=0 Radius=3.5
    g35: LineSegment StartX=-4.03109 StartY=-3.5 StartZ=0 EndX=-7.06218 EndY=-5.25 EndZ=0
    g36: LineSegment StartX=-7.06218 StartY=-5.25 StartZ=0 EndX=-7.06218 EndY=-8.75 EndZ=0
    g37: LineSegment StartX=-7.06218 StartY=-8.75 StartZ=0 EndX=-4.03109 EndY=-10.5 EndZ=0
    g38: LineSegment StartX=-4.03109 StartY=-10.5 StartZ=0 EndX=-1 EndY=-8.75 EndZ=0
    g39: LineSegment StartX=-1 StartY=-8.75 StartZ=0 EndX=-1 EndY=-5.25 EndZ=0
    g40: LineSegment StartX=-1 StartY=-5.25 StartZ=0 EndX=-4.03109 EndY=-3.5 EndZ=0
    g41: Circle [constr] CenterX=-4.03109 CenterY=-7 CenterZ=0 NormalX=0 NormalY=0 NormalZ=1 AngleXU=0 Radius=3.5
    g42: LineSegment StartX=4.03109 StartY=-3.5 StartZ=0 EndX=1 EndY=-5.25 EndZ=0
    g43: LineSegment StartX=1 StartY=-5.25 StartZ=0 EndX=1 EndY=-8.75 EndZ=0
    g44: LineSegment StartX=1 StartY=-8.75 StartZ=0 EndX=4.03109 EndY=-10.5 EndZ=0
    g45: LineSegment StartX=4.03109 StartY=-10.5 StartZ=0 EndX=7.06218 EndY=-8.75 EndZ=0
    g46: LineSegment StartX=7.06218 StartY=-8.75 StartZ=0 EndX=7.06218 EndY=-5.25 EndZ=0
    g47: LineSegment StartX=7.06218 StartY=-5.25 StartZ=0 EndX=4.03109 EndY=-3.5 EndZ=0
    g48: Circle [constr] CenterX=4.03109 CenterY=-7 CenterZ=0 NormalX=0 NormalY=0 NormalZ=1 AngleXU=0 Radius=3.5
  constraints (117):
    c: Coincident(g0,g1)
    c: Coincident(g1,g2)
    c: Coincident(g2,g3)
    c: Coincident(g3,g4)
    c: Coincident(g4,g5)
    c: Coincident(g5,g0)
    c: Equal(g0, g1-g5) x5
    c: PointOnObject(g0,g6)
    c: PointOnObject(g1,g6)
    c: PointOnObject(g2,g6)
    c: PointOnObject(g3,g6)
    c: PointOnObject(g4,g6)
    c: PointOnObject(g5,g6)
    c: Coincident(g6,g-1)
    c: Diameter(g6) = 7
    c: PointOnObject(g0,g-2)
    c: Coincident(g7,g8)
    c: Coincident(g8,g9)
    c: Coincident(g9,g10)
    c: Coincident(g10,g11)
    c: Coincident(g11,g12)
    c: Coincident(g12,g7)
    c: Equal(g7, g8-g12) x5
    c: PointOnObject(g7,g13)
    c: PointOnObject(g8,g13)
    c: PointOnObject(g9,g13)
    c: PointOnObject(g10,g13)
    c: PointOnObject(g11,g13)
    c: PointOnObject(g12,g13)
    c: PointOnObject(g13,g-1)
    c: Diameter(g13) = 7
    c: Distance(g6,g13) = 8
    c: Horizontal(g0,g10)
    c: Coincident(g14,g15)
    c: Coincident(g15,g16)
    c: Coincident(g16,g17)
    c: Coincident(g17,g18)
    c: Coincident(g18,g19)
    c: Coincident(g19,g14)
    c: Equal(g14, g15-g19) x5
    c: PointOnObject(g14,g20)
    c: PointOnObject(g15,g20)
    c: PointOnObject(g16,g20)
    c: PointOnObject(g17,g20)
    c: PointOnObject(g18,g20)
    c: PointOnObject(g19,g20)
    c: Diameter(g20) = 7
    c: DistanceY(g-1,g20) = 7
    c: Vertical(g18)
    c: Distance(g17,g-2) = 1
    c: Coincident(g21,g22)
    c: Coincident(g22,g23)
    c: Coincident(g23,g24)
    c: Coincident(g24,g25)
    c: Coincident(g25,g26)
    c: Coincident(g26,g21)
    c: Equal(g21, g22-g26) x5
    c: PointOnObject(g21,g27)
    c: PointOnObject(g22,g27)
    c: PointOnObject(g23,g27)
    c: PointOnObject(g24,g27)
    c: PointOnObject(g25,g27)
    c: PointOnObject(g26,g27)
    c: Diameter(g27) = 7
    c: DistanceY(g-1,g27) = 7
    c: DistanceX(g21,g-1) = 1
    c: Vertical(g21)
    c: Coincident(g28,g29)
    c: Coincident(g29,g30)
    c: Coincident(g30,g31)
    c: Coincident(g31,g32)
    c: Coincident(g32,g33)
    c: Coincident(g33,g28)
    c: Equal(g28, g29-g33) x5
    c: PointOnObject(g28,g34)
    c: PointOnObject(g29,g34)
    c: PointOnObject(g30,g34)
    c: PointOnObject(g31,g34)
    c: PointOnObject(g32,g34)
    c: PointOnObject(g33,g34)
    c: PointOnObject(g34,g-1)
    c: Diameter(g34) = 7
    c: Vertical(g31)
    c: DistanceX(g34,g-1) = 8
    c: Coincident(g35,g36)
    c: Coincident(g36,g37)
    c: Coincident(g37,g38)
    c: Coincident(g38,g39)
    c: Coincident(g39,g40)
    c: Coincident(g40,g35)
    c: Equal(g35, g36-g40) x5
    c: PointOnObject(g35,g41)
    c: PointOnObject(g36,g41)
    c: PointOnObject(g37,g41)
    c: PointOnObject(g38,g41)
    c: PointOnObject(g39,g41)
    c: PointOnObject(g40,g41)
    c: Coincident(g42,g43)
    c: Coincident(g43,g44)
    c: Coincident(g44,g45)
    c: Coincident(g45,g46)
    c: Coincident(g46,g47)
    c: Coincident(g47,g42)
    c: Equal(g42, g43-g47) x5
    c: PointOnObject(g42,g48)
    c: PointOnObject(g43,g48)
    c: PointOnObject(g44,g48)
    c: PointOnObject(g45,g48)
    c: PointOnObject(g46,g48)
    c: PointOnObject(g47,g48)
    c: Equal(g41,g48)
    c: Diameter(g41) = 7
    c: Vertical(g39)
    c: Vertical(g43)
    c: Distance(g-2,g39) = 1
    c: Symmetric(g38,g43,g-2)
    c: Distance(g41,g-1) = 7
FEATURE [Part::Extrusion] Extrude572  label="hex174"
  Base = -> Sketch581
  Dir = (0,-1,2e-16)
  DirMode = 2
  FaceMakerClass = Part::FaceMakerBullseye
  FaceMakerMode = 3
  LengthFwd = 10
  LengthRev = 0
  Placement = pos=(16,0,-14) rot=(0,0,1;0rad)
  Solid = true
  Symmetric = false
FEATURE [Sketcher::SketchObject] Sketch582
  ArcFitTolerance = 1e-06
  FullyConstrained = true
  MakeInternals = false
  Placement = pos=(0,0,0) rot=(1,0,0;1.5708rad)
  sketch-geometry (49):
    g0: LineSegment StartX=1e-16 StartY=3.5 StartZ=0 EndX=-3.03109 EndY=1.75 EndZ=0
    g1: LineSegment StartX=-3.03109 StartY=1.75 StartZ=0 EndX=-3.03109 EndY=-1.75 EndZ=0
    g2: LineSegment StartX=-3.03109 StartY=-1.75 StartZ=0 EndX=-1e-16 EndY=-3.5 EndZ=0
    g3: LineSegment StartX=-1e-16 StartY=-3.5 StartZ=0 EndX=3.03109 EndY=-1.75 EndZ=0
    g4: LineSegment StartX=3.03109 StartY=-1.75 StartZ=0 EndX=3.03109 EndY=1.75 EndZ=0
    g5: LineSegment StartX=3.03109 StartY=1.75 StartZ=0 EndX=1e-16 EndY=3.5 EndZ=0
    g6: Circle [constr] CenterX=0 CenterY=0 CenterZ=0 NormalX=0 NormalY=0 NormalZ=1 AngleXU=0 Radius=3.5
    g7: LineSegment StartX=4.96892 StartY=-1.75002 StartZ=0 EndX=8.00002 EndY=-3.5 EndZ=0
    g8: LineSegment StartX=8.00002 StartY=-3.5 StartZ=0 EndX=11.0311 EndY=-1.74998 EndZ=0
    g9: LineSegment StartX=11.0311 StartY=-1.74998 StartZ=0 EndX=11.0311 EndY=1.75002 EndZ=0
    g10: LineSegment StartX=11.0311 StartY=1.75002 StartZ=0 EndX=7.99998 EndY=3.5 EndZ=0
    g11: LineSegment StartX=7.99998 StartY=3.5 StartZ=0 EndX=4.9689 EndY=1.74998 EndZ=0
    g12: LineSegment StartX=4.9689 StartY=1.74998 StartZ=0 EndX=4.96892 EndY=-1.75002 EndZ=0
    g13: Circle [constr] CenterX=8 CenterY=0 CenterZ=0 NormalX=0 NormalY=0 NormalZ=1 AngleXU=0 Radius=3.5
    g14: LineSegment StartX=4.03109 StartY=3.5 StartZ=0 EndX=7.06218 EndY=5.25 EndZ=0
    g15: LineSegment StartX=7.06218 StartY=5.25 StartZ=0 EndX=7.06218 EndY=8.75 EndZ=0
    g16: LineSegment StartX=7.06218 StartY=8.75 StartZ=0 EndX=4.03109 EndY=10.5 EndZ=0
    g17: LineSegment StartX=4.03109 StartY=10.5 StartZ=0 EndX=1 EndY=8.75 EndZ=0
    g18: LineSegment StartX=1 StartY=8.75 StartZ=0 EndX=1 EndY=5.25 EndZ=0
    g19: LineSegment StartX=1 StartY=5.25 StartZ=0 EndX=4.03109 EndY=3.5 EndZ=0
    g20: Circle [constr] CenterX=4.03109 CenterY=7 CenterZ=0 NormalX=0 NormalY=0 NormalZ=1 AngleXU=0 Radius=3.5
    g21: LineSegment StartX=-1 StartY=5.25 StartZ=0 EndX=-1 EndY=8.75 EndZ=0
    g22: LineSegment StartX=-1 StartY=8.75 StartZ=0 EndX=-4.03109 EndY=10.5 EndZ=0
    g23: LineSegment StartX=-4.03109 StartY=10.5 StartZ=0 EndX=-7.06218 EndY=8.75 EndZ=0
    g24: LineSegment StartX=-7.06218 StartY=8.75 StartZ=0 EndX=-7.06218 EndY=5.25 EndZ=0
    g25: LineSegment StartX=-7.06218 StartY=5.25 StartZ=0 EndX=-4.03109 EndY=3.5 EndZ=0
    g26: LineSegment StartX=-4.03109 StartY=3.5 StartZ=0 EndX=-1 EndY=5.25 EndZ=0
    g27: Circle [constr] CenterX=-4.03109 CenterY=7 CenterZ=0 NormalX=0 NormalY=0 NormalZ=1 AngleXU=0 Radius=3.5
    g28: LineSegment StartX=-4.96891 StartY=-1.75 StartZ=0 EndX=-4.96891 EndY=1.75 EndZ=0
    g29: LineSegment StartX=-4.96891 StartY=1.75 StartZ=0 EndX=-8 EndY=3.5 EndZ=0
    g30: LineSegment StartX=-8 StartY=3.5 StartZ=0 EndX=-11.0311 EndY=1.75 EndZ=0
    g31: LineSegment StartX=-11.0311 StartY=1.75 StartZ=0 EndX=-11.0311 EndY=-1.75 EndZ=0
    g32: LineSegment StartX=-11.0311 StartY=-1.75 StartZ=0 EndX=-8 EndY=-3.5 EndZ=0
    g33: LineSegment StartX=-8 StartY=-3.5 StartZ=0 EndX=-4.96891 EndY=-1.75 EndZ=0
    g34: Circle [constr] CenterX=-8 CenterY=0 CenterZ=0 NormalX=0 NormalY=0 NormalZ=1 AngleXU=0 Radius=3.5
    g35: LineSegment StartX=-4.03109 StartY=-3.5 StartZ=0 EndX=-7.06218 EndY=-5.25 EndZ=0
    g36: LineSegment StartX=-7.06218 StartY=-5.25 StartZ=0 EndX=-7.06218 EndY=-8.75 EndZ=0
    g37: LineSegment StartX=-7.06218 StartY=-8.75 StartZ=0 EndX=-4.03109 EndY=-10.5 EndZ=0
    g38: LineSegment StartX=-4.03109 StartY=-10.5 StartZ=0 EndX=-1 EndY=-8.75 EndZ=0
    g39: LineSegment StartX=-1 StartY=-8.75 StartZ=0 EndX=-1 EndY=-5.25 EndZ=0
    g40: LineSegment StartX=-1 StartY=-5.25 StartZ=0 EndX=-4.03109 EndY=-3.5 EndZ=0
    g41: Circle [constr] CenterX=-4.03109 CenterY=-7 CenterZ=0 NormalX=0 NormalY=0 NormalZ=1 AngleXU=0 Radius=3.5
    g42: LineSegment StartX=4.03109 StartY=-3.5 StartZ=0 EndX=1 EndY=-5.25 EndZ=0
    g43: LineSegment StartX=1 StartY=-5.25 StartZ=0 EndX=1 EndY=-8.75 EndZ=0
    g44: LineSegment StartX=1 StartY=-8.75 StartZ=0 EndX=4.03109 EndY=-10.5 EndZ=0
    g45: LineSegment StartX=4.03109 StartY=-10.5 StartZ=0 EndX=7.06218 EndY=-8.75 EndZ=0
    g46: LineSegment StartX=7.06218 StartY=-8.75 StartZ=0 EndX=7.06218 EndY=-5.25 EndZ=0
    g47: LineSegment StartX=7.06218 StartY=-5.25 StartZ=0 EndX=4.03109 EndY=-3.5 EndZ=0
    g48: Circle [constr] CenterX=4.03109 CenterY=-7 CenterZ=0 NormalX=0 NormalY=0 NormalZ=1 AngleXU=0 Radius=3.5
  constraints (117):
    c: Coincident(g0,g1)
    c: Coincident(g1,g2)
    c: Coincident(g2,g3)
    c: Coincident(g3,g4)
    c: Coincident(g4,g5)
    c: Coincident(g5,g0)
    c: Equal(g0, g1-g5) x5
    c: PointOnObject(g0,g6)
    c: PointOnObject(g1,g6)
    c: PointOnObject(g2,g6)
    c: PointOnObject(g3,g6)
    c: PointOnObject(g4,g6)
    c: PointOnObject(g5,g6)
    c: Coincident(g6,g-1)
    c: Diameter(g6) = 7
    c: PointOnObject(g0,g-2)
    c: Coincident(g7,g8)
    c: Coincident(g8,g9)
    c: Coincident(g9,g10)
    c: Coincident(g10,g11)
    c: Coincident(g11,g12)
    c: Coincident(g12,g7)
    c: Equal(g7, g8-g12) x5
    c: PointOnObject(g7,g13)
    c: PointOnObject(g8,g13)
    c: PointOnObject(g9,g13)
    c: PointOnObject(g10,g13)
    c: PointOnObject(g11,g13)
    c: PointOnObject(g12,g13)
    c: PointOnObject(g13,g-1)
    c: Diameter(g13) = 7
    c: Distance(g6,g13) = 8
    c: Horizontal(g0,g10)
    c: Coincident(g14,g15)
    c: Coincident(g15,g16)
    c: Coincident(g16,g17)
    c: Coincident(g17,g18)
    c: Coincident(g18,g19)
    c: Coincident(g19,g14)
    c: Equal(g14, g15-g19) x5
    c: PointOnObject(g14,g20)
    c: PointOnObject(g15,g20)
    c: PointOnObject(g16,g20)
    c: PointOnObject(g17,g20)
    c: PointOnObject(g18,g20)
    c: PointOnObject(g19,g20)
    c: Diameter(g20) = 7
    c: DistanceY(g-1,g20) = 7
    c: Vertical(g18)
    c: Distance(g17,g-2) = 1
    c: Coincident(g21,g22)
    c: Coincident(g22,g23)
    c: Coincident(g23,g24)
    c: Coincident(g24,g25)
    c: Coincident(g25,g26)
    c: Coincident(g26,g21)
    c: Equal(g21, g22-g26) x5
    c: PointOnObject(g21,g27)
    c: PointOnObject(g22,g27)
    c: PointOnObject(g23,g27)
    c: PointOnObject(g24,g27)
    c: PointOnObject(g25,g27)
    c: PointOnObject(g26,g27)
    c: Diameter(g27) = 7
    c: DistanceY(g-1,g27) = 7
    c: DistanceX(g21,g-1) = 1
    c: Vertical(g21)
    c: Coincident(g28,g29)
    c: Coincident(g29,g30)
    c: Coincident(g30,g31)
    c: Coincident(g31,g32)
    c: Coincident(g32,g33)
    c: Coincident(g33,g28)
    c: Equal(g28, g29-g33) x5
    c: PointOnObject(g28,g34)
    c: PointOnObject(g29,g34)
    c: PointOnObject(g30,g34)
    c: PointOnObject(g31,g34)
    c: PointOnObject(g32,g34)
    c: PointOnObject(g33,g34)
    c: PointOnObject(g34,g-1)
    c: Diameter(g34) = 7
    c: Vertical(g31)
    c: DistanceX(g34,g-1) = 8
    c: Coincident(g35,g36)
    c: Coincident(g36,g37)
    c: Coincident(g37,g38)
    c: Coincident(g38,g39)
    c: Coincident(g39,g40)
    c: Coincident(g40,g35)
    c: Equal(g35, g36-g40) x5
    c: PointOnObject(g35,g41)
    c: PointOnObject(g36,g41)
    c: PointOnObject(g37,g41)
    c: PointOnObject(g38,g41)
    c: PointOnObject(g39,g41)
    c: PointOnObject(g40,g41)
    c: Coincident(g42,g43)
    c: Coincident(g43,g44)
    c: Coincident(g44,g45)
    c: Coincident(g45,g46)
    c: Coincident(g46,g47)
    c: Coincident(g47,g42)
    c: Equal(g42, g43-g47) x5
    c: PointOnObject(g42,g48)
    c: PointOnObject(g43,g48)
    c: PointOnObject(g44,g48)
    c: PointOnObject(g45,g48)
    c: PointOnObject(g46,g48)
    c: PointOnObject(g47,g48)
    c: Equal(g41,g48)
    c: Diameter(g41) = 7
    c: Vertical(g39)
    c: Vertical(g43)
    c: Distance(g-2,g39) = 1
    c: Symmetric(g38,g43,g-2)
    c: Distance(g41,g-1) = 7
FEATURE [Part::Extrusion] Extrude573  label="hex175"
  Base = -> Sketch582
  Dir = (0,-1,2e-16)
  DirMode = 2
  FaceMakerClass = Part::FaceMakerBullseye
  FaceMakerMode = 3
  LengthFwd = 10
  LengthRev = 0
  Placement = pos=(-4,0,21) rot=(0,0,1;0rad)
  Solid = true
  Symmetric = false
FEATURE [Sketcher::SketchObject] Sketch583
  ArcFitTolerance = 1e-06
  FullyConstrained = true
  MakeInternals = false
  Placement = pos=(0,0,0) rot=(1,0,0;1.5708rad)
  sketch-geometry (49):
    g0: LineSegment StartX=1e-16 StartY=3.5 StartZ=0 EndX=-3.03109 EndY=1.75 EndZ=0
    g1: LineSegment StartX=-3.03109 StartY=1.75 StartZ=0 EndX=-3.03109 EndY=-1.75 EndZ=0
    g2: LineSegment StartX=-3.03109 StartY=-1.75 StartZ=0 EndX=-1e-16 EndY=-3.5 EndZ=0
    g3: LineSegment StartX=-1e-16 StartY=-3.5 StartZ=0 EndX=3.03109 EndY=-1.75 EndZ=0
    g4: LineSegment StartX=3.03109 StartY=-1.75 StartZ=0 EndX=3.03109 EndY=1.75 EndZ=0
    g5: LineSegment StartX=3.03109 StartY=1.75 StartZ=0 EndX=1e-16 EndY=3.5 EndZ=0
    g6: Circle [constr] CenterX=0 CenterY=0 CenterZ=0 NormalX=0 NormalY=0 NormalZ=1 AngleXU=0 Radius=3.5
    g7: LineSegment StartX=4.96892 StartY=-1.75002 StartZ=0 EndX=8.00002 EndY=-3.5 EndZ=0
    g8: LineSegment StartX=8.00002 StartY=-3.5 StartZ=0 EndX=11.0311 EndY=-1.74998 EndZ=0
    g9: LineSegment StartX=11.0311 StartY=-1.74998 StartZ=0 EndX=11.0311 EndY=1.75002 EndZ=0
    g10: LineSegment StartX=11.0311 StartY=1.75002 StartZ=0 EndX=7.99998 EndY=3.5 EndZ=0
    g11: LineSegment StartX=7.99998 StartY=3.5 StartZ=0 EndX=4.9689 EndY=1.74998 EndZ=0
    g12: LineSegment StartX=4.9689 StartY=1.74998 StartZ=0 EndX=4.96892 EndY=-1.75002 EndZ=0
    g13: Circle [constr] CenterX=8 CenterY=0 CenterZ=0 NormalX=0 NormalY=0 NormalZ=1 AngleXU=0 Radius=3.5
    g14: LineSegment StartX=4.03109 StartY=3.5 StartZ=0 EndX=7.06218 EndY=5.25 EndZ=0
    g15: LineSegment StartX=7.06218 StartY=5.25 StartZ=0 EndX=7.06218 EndY=8.75 EndZ=0
    g16: LineSegment StartX=7.06218 StartY=8.75 StartZ=0 EndX=4.03109 EndY=10.5 EndZ=0
    g17: LineSegment StartX=4.03109 StartY=10.5 StartZ=0 EndX=1 EndY=8.75 EndZ=0
    g18: LineSegment StartX=1 StartY=8.75 StartZ=0 EndX=1 EndY=5.25 EndZ=0
    g19: LineSegment StartX=1 StartY=5.25 StartZ=0 EndX=4.03109 EndY=3.5 EndZ=0
    g20: Circle [constr] CenterX=4.03109 CenterY=7 CenterZ=0 NormalX=0 NormalY=0 NormalZ=1 AngleXU=0 Radius=3.5
    g21: LineSegment StartX=-1 StartY=5.25 StartZ=0 EndX=-1 EndY=8.75 EndZ=0
    g22: LineSegment StartX=-1 StartY=8.75 StartZ=0 EndX=-4.03109 EndY=10.5 EndZ=0
    g23: LineSegment StartX=-4.03109 StartY=10.5 StartZ=0 EndX=-7.06218 EndY=8.75 EndZ=0
    g24: LineSegment StartX=-7.06218 StartY=8.75 StartZ=0 EndX=-7.06218 EndY=5.25 EndZ=0
    g25: LineSegment StartX=-7.06218 StartY=5.25 StartZ=0 EndX=-4.03109 EndY=3.5 EndZ=0
    g26: LineSegment StartX=-4.03109 StartY=3.5 StartZ=0 EndX=-1 EndY=5.25 EndZ=0
    g27: Circle [constr] CenterX=-4.03109 CenterY=7 CenterZ=0 NormalX=0 NormalY=0 NormalZ=1 AngleXU=0 Radius=3.5
    g28: LineSegment StartX=-4.96891 StartY=-1.75 StartZ=0 EndX=-4.96891 EndY=1.75 EndZ=0
    g29: LineSegment StartX=-4.96891 StartY=1.75 StartZ=0 EndX=-8 EndY=3.5 EndZ=0
    g30: LineSegment StartX=-8 StartY=3.5 StartZ=0 EndX=-11.0311 EndY=1.75 EndZ=0
    g31: LineSegment StartX=-11.0311 StartY=1.75 StartZ=0 EndX=-11.0311 EndY=-1.75 EndZ=0
    g32: LineSegment StartX=-11.0311 StartY=-1.75 StartZ=0 EndX=-8 EndY=-3.5 EndZ=0
    g33: LineSegment StartX=-8 StartY=-3.5 StartZ=0 EndX=-4.96891 EndY=-1.75 EndZ=0
    g34: Circle [constr] CenterX=-8 CenterY=0 CenterZ=0 NormalX=0 NormalY=0 NormalZ=1 AngleXU=0 Radius=3.5
    g35: LineSegment StartX=-4.03109 StartY=-3.5 StartZ=0 EndX=-7.06218 EndY=-5.25 EndZ=0
    g36: LineSegment StartX=-7.06218 StartY=-5.25 StartZ=0 EndX=-7.06218 EndY=-8.75 EndZ=0
    g37: LineSegment StartX=-7.06218 StartY=-8.75 StartZ=0 EndX=-4.03109 EndY=-10.5 EndZ=0
    g38: LineSegment StartX=-4.03109 StartY=-10.5 StartZ=0 EndX=-1 EndY=-8.75 EndZ=0
    g39: LineSegment StartX=-1 StartY=-8.75 StartZ=0 EndX=-1 EndY=-5.25 EndZ=0
    g40: LineSegment StartX=-1 StartY=-5.25 StartZ=0 EndX=-4.03109 EndY=-3.5 EndZ=0
    g41: Circle [constr] CenterX=-4.03109 CenterY=-7 CenterZ=0 NormalX=0 NormalY=0 NormalZ=1 AngleXU=0 Radius=3.5
    g42: LineSegment StartX=4.03109 StartY=-3.5 StartZ=0 EndX=1 EndY=-5.25 EndZ=0
    g43: LineSegment StartX=1 StartY=-5.25 StartZ=0 EndX=1 EndY=-8.75 EndZ=0
    g44: LineSegment StartX=1 StartY=-8.75 StartZ=0 EndX=4.03109 EndY=-10.5 EndZ=0
    g45: LineSegment StartX=4.03109 StartY=-10.5 StartZ=0 EndX=7.06218 EndY=-8.75 EndZ=0
    g46: LineSegment StartX=7.06218 StartY=-8.75 StartZ=0 EndX=7.06218 EndY=-5.25 EndZ=0
    g47: LineSegment StartX=7.06218 StartY=-5.25 StartZ=0 EndX=4.03109 EndY=-3.5 EndZ=0
    g48: Circle [constr] CenterX=4.03109 CenterY=-7 CenterZ=0 NormalX=0 NormalY=0 NormalZ=1 AngleXU=0 Radius=3.5
  constraints (117):
    c: Coincident(g0,g1)
    c: Coincident(g1,g2)
    c: Coincident(g2,g3)
    c: Coincident(g3,g4)
    c: Coincident(g4,g5)
    c: Coincident(g5,g0)
    c: Equal(g0, g1-g5) x5
    c: PointOnObject(g0,g6)
    c: PointOnObject(g1,g6)
    c: PointOnObject(g2,g6)
    c: PointOnObject(g3,g6)
    c: PointOnObject(g4,g6)
    c: PointOnObject(g5,g6)
    c: Coincident(g6,g-1)
    c: Diameter(g6) = 7
    c: PointOnObject(g0,g-2)
    c: Coincident(g7,g8)
    c: Coincident(g8,g9)
    c: Coincident(g9,g10)
    c: Coincident(g10,g11)
    c: Coincident(g11,g12)
    c: Coincident(g12,g7)
    c: Equal(g7, g8-g12) x5
    c: PointOnObject(g7,g13)
    c: PointOnObject(g8,g13)
    c: PointOnObject(g9,g13)
    c: PointOnObject(g10,g13)
    c: PointOnObject(g11,g13)
    c: PointOnObject(g12,g13)
    c: PointOnObject(g13,g-1)
    c: Diameter(g13) = 7
    c: Distance(g6,g13) = 8
    c: Horizontal(g0,g10)
    c: Coincident(g14,g15)
    c: Coincident(g15,g16)
    c: Coincident(g16,g17)
    c: Coincident(g17,g18)
    c: Coincident(g18,g19)
    c: Coincident(g19,g14)
    c: Equal(g14, g15-g19) x5
    c: PointOnObject(g14,g20)
    c: PointOnObject(g15,g20)
    c: PointOnObject(g16,g20)
    c: PointOnObject(g17,g20)
    c: PointOnObject(g18,g20)
    c: PointOnObject(g19,g20)
    c: Diameter(g20) = 7
    c: DistanceY(g-1,g20) = 7
    c: Vertical(g18)
    c: Distance(g17,g-2) = 1
    c: Coincident(g21,g22)
    c: Coincident(g22,g23)
    c: Coincident(g23,g24)
    c: Coincident(g24,g25)
    c: Coincident(g25,g26)
    c: Coincident(g26,g21)
    c: Equal(g21, g22-g26) x5
    c: PointOnObject(g21,g27)
    c: PointOnObject(g22,g27)
    c: PointOnObject(g23,g27)
    c: PointOnObject(g24,g27)
    c: PointOnObject(g25,g27)
    c: PointOnObject(g26,g27)
    c: Diameter(g27) = 7
    c: DistanceY(g-1,g27) = 7
    c: DistanceX(g21,g-1) = 1
    c: Vertical(g21)
    c: Coincident(g28,g29)
    c: Coincident(g29,g30)
    c: Coincident(g30,g31)
    c: Coincident(g31,g32)
    c: Coincident(g32,g33)
    c: Coincident(g33,g28)
    c: Equal(g28, g29-g33) x5
    c: PointOnObject(g28,g34)
    c: PointOnObject(g29,g34)
    c: PointOnObject(g30,g34)
    c: PointOnObject(g31,g34)
    c: PointOnObject(g32,g34)
    c: PointOnObject(g33,g34)
    c: PointOnObject(g34,g-1)
    c: Diameter(g34) = 7
    c: Vertical(g31)
    c: DistanceX(g34,g-1) = 8
    c: Coincident(g35,g36)
    c: Coincident(g36,g37)
    c: Coincident(g37,g38)
    c: Coincident(g38,g39)
    c: Coincident(g39,g40)
    c: Coincident(g40,g35)
    c: Equal(g35, g36-g40) x5
    c: PointOnObject(g35,g41)
    c: PointOnObject(g36,g41)
    c: PointOnObject(g37,g41)
    c: PointOnObject(g38,g41)
    c: PointOnObject(g39,g41)
    c: PointOnObject(g40,g41)
    c: Coincident(g42,g43)
    c: Coincident(g43,g44)
    c: Coincident(g44,g45)
    c: Coincident(g45,g46)
    c: Coincident(g46,g47)
    c: Coincident(g47,g42)
    c: Equal(g42, g43-g47) x5
    c: PointOnObject(g42,g48)
    c: PointOnObject(g43,g48)
    c: PointOnObject(g44,g48)
    c: PointOnObject(g45,g48)
    c: PointOnObject(g46,g48)
    c: PointOnObject(g47,g48)
    c: Equal(g41,g48)
    c: Diameter(g41) = 7
    c: Vertical(g39)
    c: Vertical(g43)
    c: Distance(g-2,g39) = 1
    c: Symmetric(g38,g43,g-2)
    c: Distance(g41,g-1) = 7
FEATURE [Part::Extrusion] Extrude574  label="hex176"
  Base = -> Sketch583
  Dir = (0,-1,2e-16)
  DirMode = 2
  FaceMakerClass = Part::FaceMakerBullseye
  FaceMakerMode = 3
  LengthFwd = 10
  LengthRev = 0
  Placement = pos=(12,0,-35) rot=(0,0,1;0rad)
  Solid = true
  Symmetric = false
FEATURE [Sketcher::SketchObject] Sketch584
  ArcFitTolerance = 1e-06
  FullyConstrained = true
  MakeInternals = false
  Placement = pos=(0,0,0) rot=(1,0,0;1.5708rad)
  sketch-geometry (49):
    g0: LineSegment StartX=1e-16 StartY=3.5 StartZ=0 EndX=-3.03109 EndY=1.75 EndZ=0
    g1: LineSegment StartX=-3.03109 StartY=1.75 StartZ=0 EndX=-3.03109 EndY=-1.75 EndZ=0
    g2: LineSegment StartX=-3.03109 StartY=-1.75 StartZ=0 EndX=-1e-16 EndY=-3.5 EndZ=0
    g3: LineSegment StartX=-1e-16 StartY=-3.5 StartZ=0 EndX=3.03109 EndY=-1.75 EndZ=0
    g4: LineSegment StartX=3.03109 StartY=-1.75 StartZ=0 EndX=3.03109 EndY=1.75 EndZ=0
    g5: LineSegment StartX=3.03109 StartY=1.75 StartZ=0 EndX=1e-16 EndY=3.5 EndZ=0
    g6: Circle [constr] CenterX=0 CenterY=0 CenterZ=0 NormalX=0 NormalY=0 NormalZ=1 AngleXU=0 Radius=3.5
    g7: LineSegment StartX=4.96892 StartY=-1.75002 StartZ=0 EndX=8.00002 EndY=-3.5 EndZ=0
    g8: LineSegment StartX=8.00002 StartY=-3.5 StartZ=0 EndX=11.0311 EndY=-1.74998 EndZ=0
    g9: LineSegment StartX=11.0311 StartY=-1.74998 StartZ=0 EndX=11.0311 EndY=1.75002 EndZ=0
    g10: LineSegment StartX=11.0311 StartY=1.75002 StartZ=0 EndX=7.99998 EndY=3.5 EndZ=0
    g11: LineSegment StartX=7.99998 StartY=3.5 StartZ=0 EndX=4.9689 EndY=1.74998 EndZ=0
    g12: LineSegment StartX=4.9689 StartY=1.74998 StartZ=0 EndX=4.96892 EndY=-1.75002 EndZ=0
    g13: Circle [constr] CenterX=8 CenterY=0 CenterZ=0 NormalX=0 NormalY=0 NormalZ=1 AngleXU=0 Radius=3.5
    g14: LineSegment StartX=4.03109 StartY=3.5 StartZ=0 EndX=7.06218 EndY=5.25 EndZ=0
    g15: LineSegment StartX=7.06218 StartY=5.25 StartZ=0 EndX=7.06218 EndY=8.75 EndZ=0
    g16: LineSegment StartX=7.06218 StartY=8.75 StartZ=0 EndX=4.03109 EndY=10.5 EndZ=0
    g17: LineSegment StartX=4.03109 StartY=10.5 StartZ=0 EndX=1 EndY=8.75 EndZ=0
    g18: LineSegment StartX=1 StartY=8.75 StartZ=0 EndX=1 EndY=5.25 EndZ=0
    g19: LineSegment StartX=1 StartY=5.25 StartZ=0 EndX=4.03109 EndY=3.5 EndZ=0
    g20: Circle [constr] CenterX=4.03109 CenterY=7 CenterZ=0 NormalX=0 NormalY=0 NormalZ=1 AngleXU=0 Radius=3.5
    g21: LineSegment StartX=-1 StartY=5.25 StartZ=0 EndX=-1 EndY=8.75 EndZ=0
    g22: LineSegment StartX=-1 StartY=8.75 StartZ=0 EndX=-4.03109 EndY=10.5 EndZ=0
    g23: LineSegment StartX=-4.03109 StartY=10.5 StartZ=0 EndX=-7.06218 EndY=8.75 EndZ=0
    g24: LineSegment StartX=-7.06218 StartY=8.75 StartZ=0 EndX=-7.06218 EndY=5.25 EndZ=0
    g25: LineSegment StartX=-7.06218 StartY=5.25 StartZ=0 EndX=-4.03109 EndY=3.5 EndZ=0
    g26: LineSegment StartX=-4.03109 StartY=3.5 StartZ=0 EndX=-1 EndY=5.25 EndZ=0
    g27: Circle [constr] CenterX=-4.03109 CenterY=7 CenterZ=0 NormalX=0 NormalY=0 NormalZ=1 AngleXU=0 Radius=3.5
    g28: LineSegment StartX=-4.96891 StartY=-1.75 StartZ=0 EndX=-4.96891 EndY=1.75 EndZ=0
    g29: LineSegment StartX=-4.96891 StartY=1.75 StartZ=0 EndX=-8 EndY=3.5 EndZ=0
    g30: LineSegment StartX=-8 StartY=3.5 StartZ=0 EndX=-11.0311 EndY=1.75 EndZ=0
    g31: LineSegment StartX=-11.0311 StartY=1.75 StartZ=0 EndX=-11.0311 EndY=-1.75 EndZ=0
    g32: LineSegment StartX=-11.0311 StartY=-1.75 StartZ=0 EndX=-8 EndY=-3.5 EndZ=0
    g33: LineSegment StartX=-8 StartY=-3.5 StartZ=0 EndX=-4.96891 EndY=-1.75 EndZ=0
    g34: Circle [constr] CenterX=-8 CenterY=0 CenterZ=0 NormalX=0 NormalY=0 NormalZ=1 AngleXU=0 Radius=3.5
    g35: LineSegment StartX=-4.03109 StartY=-3.5 StartZ=0 EndX=-7.06218 EndY=-5.25 EndZ=0
    g36: LineSegment StartX=-7.06218 StartY=-5.25 StartZ=0 EndX=-7.06218 EndY=-8.75 EndZ=0
    g37: LineSegment StartX=-7.06218 StartY=-8.75 StartZ=0 EndX=-4.03109 EndY=-10.5 EndZ=0
    g38: LineSegment StartX=-4.03109 StartY=-10.5 StartZ=0 EndX=-1 EndY=-8.75 EndZ=0
    g39: LineSegment StartX=-1 StartY=-8.75 StartZ=0 EndX=-1 EndY=-5.25 EndZ=0
    g40: LineSegment StartX=-1 StartY=-5.25 StartZ=0 EndX=-4.03109 EndY=-3.5 EndZ=0
    g41: Circle [constr] CenterX=-4.03109 CenterY=-7 CenterZ=0 NormalX=0 NormalY=0 NormalZ=1 AngleXU=0 Radius=3.5
    g42: LineSegment StartX=4.03109 StartY=-3.5 StartZ=0 EndX=1 EndY=-5.25 EndZ=0
    g43: LineSegment StartX=1 StartY=-5.25 StartZ=0 EndX=1 EndY=-8.75 EndZ=0
    g44: LineSegment StartX=1 StartY=-8.75 StartZ=0 EndX=4.03109 EndY=-10.5 EndZ=0
    g45: LineSegment StartX=4.03109 StartY=-10.5 StartZ=0 EndX=7.06218 EndY=-8.75 EndZ=0
    g46: LineSegment StartX=7.06218 StartY=-8.75 StartZ=0 EndX=7.06218 EndY=-5.25 EndZ=0
    g47: LineSegment StartX=7.06218 StartY=-5.25 StartZ=0 EndX=4.03109 EndY=-3.5 EndZ=0
    g48: Circle [constr] CenterX=4.03109 CenterY=-7 CenterZ=0 NormalX=0 NormalY=0 NormalZ=1 AngleXU=0 Radius=3.5
  constraints (117):
    c: Coincident(g0,g1)
    c: Coincident(g1,g2)
    c: Coincident(g2,g3)
    c: Coincident(g3,g4)
    c: Coincident(g4,g5)
    c: Coincident(g5,g0)
    c: Equal(g0, g1-g5) x5
    c: PointOnObject(g0,g6)
    c: PointOnObject(g1,g6)
    c: PointOnObject(g2,g6)
    c: PointOnObject(g3,g6)
    c: PointOnObject(g4,g6)
    c: PointOnObject(g5,g6)
    c: Coincident(g6,g-1)
    c: Diameter(g6) = 7
    c: PointOnObject(g0,g-2)
    c: Coincident(g7,g8)
    c: Coincident(g8,g9)
    c: Coincident(g9,g10)
    c: Coincident(g10,g11)
    c: Coincident(g11,g12)
    c: Coincident(g12,g7)
    c: Equal(g7, g8-g12) x5
    c: PointOnObject(g7,g13)
    c: PointOnObject(g8,g13)
    c: PointOnObject(g9,g13)
    c: PointOnObject(g10,g13)
    c: PointOnObject(g11,g13)
    c: PointOnObject(g12,g13)
    c: PointOnObject(g13,g-1)
    c: Diameter(g13) = 7
    c: Distance(g6,g13) = 8
    c: Horizontal(g0,g10)
    c: Coincident(g14,g15)
    c: Coincident(g15,g16)
    c: Coincident(g16,g17)
    c: Coincident(g17,g18)
    c: Coincident(g18,g19)
    c: Coincident(g19,g14)
    c: Equal(g14, g15-g19) x5
    c: PointOnObject(g14,g20)
    c: PointOnObject(g15,g20)
    c: PointOnObject(g16,g20)
    c: PointOnObject(g17,g20)
    c: PointOnObject(g18,g20)
    c: PointOnObject(g19,g20)
    c: Diameter(g20) = 7
    c: DistanceY(g-1,g20) = 7
    c: Vertical(g18)
    c: Distance(g17,g-2) = 1
    c: Coincident(g21,g22)
    c: Coincident(g22,g23)
    c: Coincident(g23,g24)
    c: Coincident(g24,g25)
    c: Coincident(g25,g26)
    c: Coincident(g26,g21)
    c: Equal(g21, g22-g26) x5
    c: PointOnObject(g21,g27)
    c: PointOnObject(g22,g27)
    c: PointOnObject(g23,g27)
    c: PointOnObject(g24,g27)
    c: PointOnObject(g25,g27)
    c: PointOnObject(g26,g27)
    c: Diameter(g27) = 7
    c: DistanceY(g-1,g27) = 7
    c: DistanceX(g21,g-1) = 1
    c: Vertical(g21)
    c: Coincident(g28,g29)
    c: Coincident(g29,g30)
    c: Coincident(g30,g31)
    c: Coincident(g31,g32)
    c: Coincident(g32,g33)
    c: Coincident(g33,g28)
    c: Equal(g28, g29-g33) x5
    c: PointOnObject(g28,g34)
    c: PointOnObject(g29,g34)
    c: PointOnObject(g30,g34)
    c: PointOnObject(g31,g34)
    c: PointOnObject(g32,g34)
    c: PointOnObject(g33,g34)
    c: PointOnObject(g34,g-1)
    c: Diameter(g34) = 7
    c: Vertical(g31)
    c: DistanceX(g34,g-1) = 8
    c: Coincident(g35,g36)
    c: Coincident(g36,g37)
    c: Coincident(g37,g38)
    c: Coincident(g38,g39)
    c: Coincident(g39,g40)
    c: Coincident(g40,g35)
    c: Equal(g35, g36-g40) x5
    c: PointOnObject(g35,g41)
    c: PointOnObject(g36,g41)
    c: PointOnObject(g37,g41)
    c: PointOnObject(g38,g41)
    c: PointOnObject(g39,g41)
    c: PointOnObject(g40,g41)
    c: Coincident(g42,g43)
    c: Coincident(g43,g44)
    c: Coincident(g44,g45)
    c: Coincident(g45,g46)
    c: Coincident(g46,g47)
    c: Coincident(g47,g42)
    c: Equal(g42, g43-g47) x5
    c: PointOnObject(g42,g48)
    c: PointOnObject(g43,g48)
    c: PointOnObject(g44,g48)
    c: PointOnObject(g45,g48)
    c: PointOnObject(g46,g48)
    c: PointOnObject(g47,g48)
    c: Equal(g41,g48)
    c: Diameter(g41) = 7
    c: Vertical(g39)
    c: Vertical(g43)
    c: Distance(g-2,g39) = 1
    c: Symmetric(g38,g43,g-2)
    c: Distance(g41,g-1) = 7
FEATURE [Part::Extrusion] Extrude575  label="hex177"
  Base = -> Sketch584
  Dir = (0,-1,2e-16)
  DirMode = 2
  FaceMakerClass = Part::FaceMakerBullseye
  FaceMakerMode = 3
  LengthFwd = 10
  LengthRev = 0
  Placement = pos=(12,0,35) rot=(0,0,1;0rad)
  Solid = true
  Symmetric = false
FEATURE [Sketcher::SketchObject] Sketch585
  ArcFitTolerance = 1e-06
  FullyConstrained = true
  MakeInternals = false
  Placement = pos=(0,0,0) rot=(1,0,0;1.5708rad)
  sketch-geometry (49):
    g0: LineSegment StartX=1e-16 StartY=3.5 StartZ=0 EndX=-3.03109 EndY=1.75 EndZ=0
    g1: LineSegment StartX=-3.03109 StartY=1.75 StartZ=0 EndX=-3.03109 EndY=-1.75 EndZ=0
    g2: LineSegment StartX=-3.03109 StartY=-1.75 StartZ=0 EndX=-1e-16 EndY=-3.5 EndZ=0
    g3: LineSegment StartX=-1e-16 StartY=-3.5 StartZ=0 EndX=3.03109 EndY=-1.75 EndZ=0
    g4: LineSegment StartX=3.03109 StartY=-1.75 StartZ=0 EndX=3.03109 EndY=1.75 EndZ=0
    g5: LineSegment StartX=3.03109 StartY=1.75 StartZ=0 EndX=1e-16 EndY=3.5 EndZ=0
    g6: Circle [constr] CenterX=0 CenterY=0 CenterZ=0 NormalX=0 NormalY=0 NormalZ=1 AngleXU=0 Radius=3.5
    g7: LineSegment StartX=4.96892 StartY=-1.75002 StartZ=0 EndX=8.00002 EndY=-3.5 EndZ=0
    g8: LineSegment StartX=8.00002 StartY=-3.5 StartZ=0 EndX=11.0311 EndY=-1.74998 EndZ=0
    g9: LineSegment StartX=11.0311 StartY=-1.74998 StartZ=0 EndX=11.0311 EndY=1.75002 EndZ=0
    g10: LineSegment StartX=11.0311 StartY=1.75002 StartZ=0 EndX=7.99998 EndY=3.5 EndZ=0
    g11: LineSegment StartX=7.99998 StartY=3.5 StartZ=0 EndX=4.9689 EndY=1.74998 EndZ=0
    g12: LineSegment StartX=4.9689 StartY=1.74998 StartZ=0 EndX=4.96892 EndY=-1.75002 EndZ=0
    g13: Circle [constr] CenterX=8 CenterY=0 CenterZ=0 NormalX=0 NormalY=0 NormalZ=1 AngleXU=0 Radius=3.5
    g14: LineSegment StartX=4.03109 StartY=3.5 StartZ=0 EndX=7.06218 EndY=5.25 EndZ=0
    g15: LineSegment StartX=7.06218 StartY=5.25 StartZ=0 EndX=7.06218 EndY=8.75 EndZ=0
    g16: LineSegment StartX=7.06218 StartY=8.75 StartZ=0 EndX=4.03109 EndY=10.5 EndZ=0
    g17: LineSegment StartX=4.03109 StartY=10.5 StartZ=0 EndX=1 EndY=8.75 EndZ=0
    g18: LineSegment StartX=1 StartY=8.75 StartZ=0 EndX=1 EndY=5.25 EndZ=0
    g19: LineSegment StartX=1 StartY=5.25 StartZ=0 EndX=4.03109 EndY=3.5 EndZ=0
    g20: Circle [constr] CenterX=4.03109 CenterY=7 CenterZ=0 NormalX=0 NormalY=0 NormalZ=1 AngleXU=0 Radius=3.5
    g21: LineSegment StartX=-1 StartY=5.25 StartZ=0 EndX=-1 EndY=8.75 EndZ=0
    g22: LineSegment StartX=-1 StartY=8.75 StartZ=0 EndX=-4.03109 EndY=10.5 EndZ=0
    g23: LineSegment StartX=-4.03109 StartY=10.5 StartZ=0 EndX=-7.06218 EndY=8.75 EndZ=0
    g24: LineSegment StartX=-7.06218 StartY=8.75 StartZ=0 EndX=-7.06218 EndY=5.25 EndZ=0
    g25: LineSegment StartX=-7.06218 StartY=5.25 StartZ=0 EndX=-4.03109 EndY=3.5 EndZ=0
    g26: LineSegment StartX=-4.03109 StartY=3.5 StartZ=0 EndX=-1 EndY=5.25 EndZ=0
    g27: Circle [constr] CenterX=-4.03109 CenterY=7 CenterZ=0 NormalX=0 NormalY=0 NormalZ=1 AngleXU=0 Radius=3.5
    g28: LineSegment StartX=-4.96891 StartY=-1.75 StartZ=0 EndX=-4.96891 EndY=1.75 EndZ=0
    g29: LineSegment StartX=-4.96891 StartY=1.75 StartZ=0 EndX=-8 EndY=3.5 EndZ=0
    g30: LineSegment StartX=-8 StartY=3.5 StartZ=0 EndX=-11.0311 EndY=1.75 EndZ=0
    g31: LineSegment StartX=-11.0311 StartY=1.75 StartZ=0 EndX=-11.0311 EndY=-1.75 EndZ=0
    g32: LineSegment StartX=-11.0311 StartY=-1.75 StartZ=0 EndX=-8 EndY=-3.5 EndZ=0
    g33: LineSegment StartX=-8 StartY=-3.5 StartZ=0 EndX=-4.96891 EndY=-1.75 EndZ=0
    g34: Circle [constr] CenterX=-8 CenterY=0 CenterZ=0 NormalX=0 NormalY=0 NormalZ=1 AngleXU=0 Radius=3.5
    g35: LineSegment StartX=-4.03109 StartY=-3.5 StartZ=0 EndX=-7.06218 EndY=-5.25 EndZ=0
    g36: LineSegment StartX=-7.06218 StartY=-5.25 StartZ=0 EndX=-7.06218 EndY=-8.75 EndZ=0
    g37: LineSegment StartX=-7.06218 StartY=-8.75 StartZ=0 EndX=-4.03109 EndY=-10.5 EndZ=0
    g38: LineSegment StartX=-4.03109 StartY=-10.5 StartZ=0 EndX=-1 EndY=-8.75 EndZ=0
    g39: LineSegment StartX=-1 StartY=-8.75 StartZ=0 EndX=-1 EndY=-5.25 EndZ=0
    g40: LineSegment StartX=-1 StartY=-5.25 StartZ=0 EndX=-4.03109 EndY=-3.5 EndZ=0
    g41: Circle [constr] CenterX=-4.03109 CenterY=-7 CenterZ=0 NormalX=0 NormalY=0 NormalZ=1 AngleXU=0 Radius=3.5
    g42: LineSegment StartX=4.03109 StartY=-3.5 StartZ=0 EndX=1 EndY=-5.25 EndZ=0
    g43: LineSegment StartX=1 StartY=-5.25 StartZ=0 EndX=1 EndY=-8.75 EndZ=0
    g44: LineSegment StartX=1 StartY=-8.75 StartZ=0 EndX=4.03109 EndY=-10.5 EndZ=0
    g45: LineSegment StartX=4.03109 StartY=-10.5 StartZ=0 EndX=7.06218 EndY=-8.75 EndZ=0
    g46: LineSegment StartX=7.06218 StartY=-8.75 StartZ=0 EndX=7.06218 EndY=-5.25 EndZ=0
    g47: LineSegment StartX=7.06218 StartY=-5.25 StartZ=0 EndX=4.03109 EndY=-3.5 EndZ=0
    g48: Circle [constr] CenterX=4.03109 CenterY=-7 CenterZ=0 NormalX=0 NormalY=0 NormalZ=1 AngleXU=0 Radius=3.5
  constraints (117):
    c: Coincident(g0,g1)
    c: Coincident(g1,g2)
    c: Coincident(g2,g3)
    c: Coincident(g3,g4)
    c: Coincident(g4,g5)
    c: Coincident(g5,g0)
    c: Equal(g0, g1-g5) x5
    c: PointOnObject(g0,g6)
    c: PointOnObject(g1,g6)
    c: PointOnObject(g2,g6)
    c: PointOnObject(g3,g6)
    c: PointOnObject(g4,g6)
    c: PointOnObject(g5,g6)
    c: Coincident(g6,g-1)
    c: Diameter(g6) = 7
    c: PointOnObject(g0,g-2)
    c: Coincident(g7,g8)
    c: Coincident(g8,g9)
    c: Coincident(g9,g10)
    c: Coincident(g10,g11)
    c: Coincident(g11,g12)
    c: Coincident(g12,g7)
    c: Equal(g7, g8-g12) x5
    c: PointOnObject(g7,g13)
    c: PointOnObject(g8,g13)
    c: PointOnObject(g9,g13)
    c: PointOnObject(g10,g13)
    c: PointOnObject(g11,g13)
    c: PointOnObject(g12,g13)
    c: PointOnObject(g13,g-1)
    c: Diameter(g13) = 7
    c: Distance(g6,g13) = 8
    c: Horizontal(g0,g10)
    c: Coincident(g14,g15)
    c: Coincident(g15,g16)
    c: Coincident(g16,g17)
    c: Coincident(g17,g18)
    c: Coincident(g18,g19)
    c: Coincident(g19,g14)
    c: Equal(g14, g15-g19) x5
    c: PointOnObject(g14,g20)
    c: PointOnObject(g15,g20)
    c: PointOnObject(g16,g20)
    c: PointOnObject(g17,g20)
    c: PointOnObject(g18,g20)
    c: PointOnObject(g19,g20)
    c: Diameter(g20) = 7
    c: DistanceY(g-1,g20) = 7
    c: Vertical(g18)
    c: Distance(g17,g-2) = 1
    c: Coincident(g21,g22)
    c: Coincident(g22,g23)
    c: Coincident(g23,g24)
    c: Coincident(g24,g25)
    c: Coincident(g25,g26)
    c: Coincident(g26,g21)
    c: Equal(g21, g22-g26) x5
    c: PointOnObject(g21,g27)
    c: PointOnObject(g22,g27)
    c: PointOnObject(g23,g27)
    c: PointOnObject(g24,g27)
    c: PointOnObject(g25,g27)
    c: PointOnObject(g26,g27)
    c: Diameter(g27) = 7
    c: DistanceY(g-1,g27) = 7
    c: DistanceX(g21,g-1) = 1
    c: Vertical(g21)
    c: Coincident(g28,g29)
    c: Coincident(g29,g30)
    c: Coincident(g30,g31)
    c: Coincident(g31,g32)
    c: Coincident(g32,g33)
    c: Coincident(g33,g28)
    c: Equal(g28, g29-g33) x5
    c: PointOnObject(g28,g34)
    c: PointOnObject(g29,g34)
    c: PointOnObject(g30,g34)
    c: PointOnObject(g31,g34)
    c: PointOnObject(g32,g34)
    c: PointOnObject(g33,g34)
    c: PointOnObject(g34,g-1)
    c: Diameter(g34) = 7
    c: Vertical(g31)
    c: DistanceX(g34,g-1) = 8
    c: Coincident(g35,g36)
    c: Coincident(g36,g37)
    c: Coincident(g37,g38)
    c: Coincident(g38,g39)
    c: Coincident(g39,g40)
    c: Coincident(g40,g35)
    c: Equal(g35, g36-g40) x5
    c: PointOnObject(g35,g41)
    c: PointOnObject(g36,g41)
    c: PointOnObject(g37,g41)
    c: PointOnObject(g38,g41)
    c: PointOnObject(g39,g41)
    c: PointOnObject(g40,g41)
    c: Coincident(g42,g43)
    c: Coincident(g43,g44)
    c: Coincident(g44,g45)
    c: Coincident(g45,g46)
    c: Coincident(g46,g47)
    c: Coincident(g47,g42)
    c: Equal(g42, g43-g47) x5
    c: PointOnObject(g42,g48)
    c: PointOnObject(g43,g48)
    c: PointOnObject(g44,g48)
    c: PointOnObject(g45,g48)
    c: PointOnObject(g46,g48)
    c: PointOnObject(g47,g48)
    c: Equal(g41,g48)
    c: Diameter(g41) = 7
    c: Vertical(g39)
    c: Vertical(g43)
    c: Distance(g-2,g39) = 1
    c: Symmetric(g38,g43,g-2)
    c: Distance(g41,g-1) = 7
FEATURE [Part::Extrusion] Extrude576  label="hex178"
  Base = -> Sketch585
  Dir = (0,-1,2e-16)
  DirMode = 2
  FaceMakerClass = Part::FaceMakerBullseye
  FaceMakerMode = 3
  LengthFwd = 10
  LengthRev = 0
  Placement = pos=(-36,0,7) rot=(0,0,1;0rad)
  Solid = true
  Symmetric = false
FEATURE [Sketcher::SketchObject] Sketch586
  ArcFitTolerance = 1e-06
  FullyConstrained = true
  MakeInternals = false
  Placement = pos=(0,0,0) rot=(1,0,0;1.5708rad)
  sketch-geometry (49):
    g0: LineSegment StartX=1e-16 StartY=3.5 StartZ=0 EndX=-3.03109 EndY=1.75 EndZ=0
    g1: LineSegment StartX=-3.03109 StartY=1.75 StartZ=0 EndX=-3.03109 EndY=-1.75 EndZ=0
    g2: LineSegment StartX=-3.03109 StartY=-1.75 StartZ=0 EndX=-1e-16 EndY=-3.5 EndZ=0
    g3: LineSegment StartX=-1e-16 StartY=-3.5 StartZ=0 EndX=3.03109 EndY=-1.75 EndZ=0
    g4: LineSegment StartX=3.03109 StartY=-1.75 StartZ=0 EndX=3.03109 EndY=1.75 EndZ=0
    g5: LineSegment StartX=3.03109 StartY=1.75 StartZ=0 EndX=1e-16 EndY=3.5 EndZ=0
    g6: Circle [constr] CenterX=0 CenterY=0 CenterZ=0 NormalX=0 NormalY=0 NormalZ=1 AngleXU=0 Radius=3.5
    g7: LineSegment StartX=4.96892 StartY=-1.75002 StartZ=0 EndX=8.00002 EndY=-3.5 EndZ=0
    g8: LineSegment StartX=8.00002 StartY=-3.5 StartZ=0 EndX=11.0311 EndY=-1.74998 EndZ=0
    g9: LineSegment StartX=11.0311 StartY=-1.74998 StartZ=0 EndX=11.0311 EndY=1.75002 EndZ=0
    g10: LineSegment StartX=11.0311 StartY=1.75002 StartZ=0 EndX=7.99998 EndY=3.5 EndZ=0
    g11: LineSegment StartX=7.99998 StartY=3.5 StartZ=0 EndX=4.9689 EndY=1.74998 EndZ=0
    g12: LineSegment StartX=4.9689 StartY=1.74998 StartZ=0 EndX=4.96892 EndY=-1.75002 EndZ=0
    g13: Circle [constr] CenterX=8 CenterY=0 CenterZ=0 NormalX=0 NormalY=0 NormalZ=1 AngleXU=0 Radius=3.5
    g14: LineSegment StartX=4.03109 StartY=3.5 StartZ=0 EndX=7.06218 EndY=5.25 EndZ=0
    g15: LineSegment StartX=7.06218 StartY=5.25 StartZ=0 EndX=7.06218 EndY=8.75 EndZ=0
    g16: LineSegment StartX=7.06218 StartY=8.75 StartZ=0 EndX=4.03109 EndY=10.5 EndZ=0
    g17: LineSegment StartX=4.03109 StartY=10.5 StartZ=0 EndX=1 EndY=8.75 EndZ=0
    g18: LineSegment StartX=1 StartY=8.75 StartZ=0 EndX=1 EndY=5.25 EndZ=0
    g19: LineSegment StartX=1 StartY=5.25 StartZ=0 EndX=4.03109 EndY=3.5 EndZ=0
    g20: Circle [constr] CenterX=4.03109 CenterY=7 CenterZ=0 NormalX=0 NormalY=0 NormalZ=1 AngleXU=0 Radius=3.5
    g21: LineSegment StartX=-1 StartY=5.25 StartZ=0 EndX=-1 EndY=8.75 EndZ=0
    g22: LineSegment StartX=-1 StartY=8.75 StartZ=0 EndX=-4.03109 EndY=10.5 EndZ=0
    g23: LineSegment StartX=-4.03109 StartY=10.5 StartZ=0 EndX=-7.06218 EndY=8.75 EndZ=0
    g24: LineSegment StartX=-7.06218 StartY=8.75 StartZ=0 EndX=-7.06218 EndY=5.25 EndZ=0
    g25: LineSegment StartX=-7.06218 StartY=5.25 StartZ=0 EndX=-4.03109 EndY=3.5 EndZ=0
    g26: LineSegment StartX=-4.03109 StartY=3.5 StartZ=0 EndX=-1 EndY=5.25 EndZ=0
    g27: Circle [constr] CenterX=-4.03109 CenterY=7 CenterZ=0 NormalX=0 NormalY=0 NormalZ=1 AngleXU=0 Radius=3.5
    g28: LineSegment StartX=-4.96891 StartY=-1.75 StartZ=0 EndX=-4.96891 EndY=1.75 EndZ=0
    g29: LineSegment StartX=-4.96891 StartY=1.75 StartZ=0 EndX=-8 EndY=3.5 EndZ=0
    g30: LineSegment StartX=-8 StartY=3.5 StartZ=0 EndX=-11.0311 EndY=1.75 EndZ=0
    g31: LineSegment StartX=-11.0311 StartY=1.75 StartZ=0 EndX=-11.0311 EndY=-1.75 EndZ=0
    g32: LineSegment StartX=-11.0311 StartY=-1.75 StartZ=0 EndX=-8 EndY=-3.5 EndZ=0
    g33: LineSegment StartX=-8 StartY=-3.5 StartZ=0 EndX=-4.96891 EndY=-1.75 EndZ=0
    g34: Circle [constr] CenterX=-8 CenterY=0 CenterZ=0 NormalX=0 NormalY=0 NormalZ=1 AngleXU=0 Radius=3.5
    g35: LineSegment StartX=-4.03109 StartY=-3.5 StartZ=0 EndX=-7.06218 EndY=-5.25 EndZ=0
    g36: LineSegment StartX=-7.06218 StartY=-5.25 StartZ=0 EndX=-7.06218 EndY=-8.75 EndZ=0
    g37: LineSegment StartX=-7.06218 StartY=-8.75 StartZ=0 EndX=-4.03109 EndY=-10.5 EndZ=0
    g38: LineSegment StartX=-4.03109 StartY=-10.5 StartZ=0 EndX=-1 EndY=-8.75 EndZ=0
    g39: LineSegment StartX=-1 StartY=-8.75 StartZ=0 EndX=-1 EndY=-5.25 EndZ=0
    g40: LineSegment StartX=-1 StartY=-5.25 StartZ=0 EndX=-4.03109 EndY=-3.5 EndZ=0
    g41: Circle [constr] CenterX=-4.03109 CenterY=-7 CenterZ=0 NormalX=0 NormalY=0 NormalZ=1 AngleXU=0 Radius=3.5
    g42: LineSegment StartX=4.03109 StartY=-3.5 StartZ=0 EndX=1 EndY=-5.25 EndZ=0
    g43: LineSegment StartX=1 StartY=-5.25 StartZ=0 EndX=1 EndY=-8.75 EndZ=0
    g44: LineSegment StartX=1 StartY=-8.75 StartZ=0 EndX=4.03109 EndY=-10.5 EndZ=0
    g45: LineSegment StartX=4.03109 StartY=-10.5 StartZ=0 EndX=7.06218 EndY=-8.75 EndZ=0
    g46: LineSegment StartX=7.06218 StartY=-8.75 StartZ=0 EndX=7.06218 EndY=-5.25 EndZ=0
    g47: LineSegment StartX=7.06218 StartY=-5.25 StartZ=0 EndX=4.03109 EndY=-3.5 EndZ=0
    g48: Circle [constr] CenterX=4.03109 CenterY=-7 CenterZ=0 NormalX=0 NormalY=0 NormalZ=1 AngleXU=0 Radius=3.5
  constraints (117):
    c: Coincident(g0,g1)
    c: Coincident(g1,g2)
    c: Coincident(g2,g3)
    c: Coincident(g3,g4)
    c: Coincident(g4,g5)
    c: Coincident(g5,g0)
    c: Equal(g0, g1-g5) x5
    c: PointOnObject(g0,g6)
    c: PointOnObject(g1,g6)
    c: PointOnObject(g2,g6)
    c: PointOnObject(g3,g6)
    c: PointOnObject(g4,g6)
    c: PointOnObject(g5,g6)
    c: Coincident(g6,g-1)
    c: Diameter(g6) = 7
    c: PointOnObject(g0,g-2)
    c: Coincident(g7,g8)
    c: Coincident(g8,g9)
    c: Coincident(g9,g10)
    c: Coincident(g10,g11)
    c: Coincident(g11,g12)
    c: Coincident(g12,g7)
    c: Equal(g7, g8-g12) x5
    c: PointOnObject(g7,g13)
    c: PointOnObject(g8,g13)
    c: PointOnObject(g9,g13)
    c: PointOnObject(g10,g13)
    c: PointOnObject(g11,g13)
    c: PointOnObject(g12,g13)
    c: PointOnObject(g13,g-1)
    c: Diameter(g13) = 7
    c: Distance(g6,g13) = 8
    c: Horizontal(g0,g10)
    c: Coincident(g14,g15)
    c: Coincident(g15,g16)
    c: Coincident(g16,g17)
    c: Coincident(g17,g18)
    c: Coincident(g18,g19)
    c: Coincident(g19,g14)
    c: Equal(g14, g15-g19) x5
    c: PointOnObject(g14,g20)
    c: PointOnObject(g15,g20)
    c: PointOnObject(g16,g20)
    c: PointOnObject(g17,g20)
    c: PointOnObject(g18,g20)
    c: PointOnObject(g19,g20)
    c: Diameter(g20) = 7
    c: DistanceY(g-1,g20) = 7
    c: Vertical(g18)
    c: Distance(g17,g-2) = 1
    c: Coincident(g21,g22)
    c: Coincident(g22,g23)
    c: Coincident(g23,g24)
    c: Coincident(g24,g25)
    c: Coincident(g25,g26)
    c: Coincident(g26,g21)
    c: Equal(g21, g22-g26) x5
    c: PointOnObject(g21,g27)
    c: PointOnObject(g22,g27)
    c: PointOnObject(g23,g27)
    c: PointOnObject(g24,g27)
    c: PointOnObject(g25,g27)
    c: PointOnObject(g26,g27)
    c: Diameter(g27) = 7
    c: DistanceY(g-1,g27) = 7
    c: DistanceX(g21,g-1) = 1
    c: Vertical(g21)
    c: Coincident(g28,g29)
    c: Coincident(g29,g30)
    c: Coincident(g30,g31)
    c: Coincident(g31,g32)
    c: Coincident(g32,g33)
    c: Coincident(g33,g28)
    c: Equal(g28, g29-g33) x5
    c: PointOnObject(g28,g34)
    c: PointOnObject(g29,g34)
    c: PointOnObject(g30,g34)
    c: PointOnObject(g31,g34)
    c: PointOnObject(g32,g34)
    c: PointOnObject(g33,g34)
    c: PointOnObject(g34,g-1)
    c: Diameter(g34) = 7
    c: Vertical(g31)
    c: DistanceX(g34,g-1) = 8
    c: Coincident(g35,g36)
    c: Coincident(g36,g37)
    c: Coincident(g37,g38)
    c: Coincident(g38,g39)
    c: Coincident(g39,g40)
    c: Coincident(g40,g35)
    c: Equal(g35, g36-g40) x5
    c: PointOnObject(g35,g41)
    c: PointOnObject(g36,g41)
    c: PointOnObject(g37,g41)
    c: PointOnObject(g38,g41)
    c: PointOnObject(g39,g41)
    c: PointOnObject(g40,g41)
    c: Coincident(g42,g43)
    c: Coincident(g43,g44)
    c: Coincident(g44,g45)
    c: Coincident(g45,g46)
    c: Coincident(g46,g47)
    c: Coincident(g47,g42)
    c: Equal(g42, g43-g47) x5
    c: PointOnObject(g42,g48)
    c: PointOnObject(g43,g48)
    c: PointOnObject(g44,g48)
    c: PointOnObject(g45,g48)
    c: PointOnObject(g46,g48)
    c: PointOnObject(g47,g48)
    c: Equal(g41,g48)
    c: Diameter(g41) = 7
    c: Vertical(g39)
    c: Vertical(g43)
    c: Distance(g-2,g39) = 1
    c: Symmetric(g38,g43,g-2)
    c: Distance(g41,g-1) = 7
FEATURE [Part::Extrusion] Extrude577  label="hex179"
  Base = -> Sketch586
  Dir = (0,-1,2e-16)
  DirMode = 2
  FaceMakerClass = Part::FaceMakerBullseye
  FaceMakerMode = 3
  LengthFwd = 10
  LengthRev = 0
  Placement = pos=(36,0,7) rot=(0,0,1;0rad)
  Solid = true
  Symmetric = false
FEATURE [Sketcher::SketchObject] Sketch587
  ArcFitTolerance = 1e-06
  FullyConstrained = true
  MakeInternals = false
  Placement = pos=(0,0,0) rot=(1,0,0;1.5708rad)
  sketch-geometry (49):
    g0: LineSegment StartX=1e-16 StartY=3.5 StartZ=0 EndX=-3.03109 EndY=1.75 EndZ=0
    g1: LineSegment StartX=-3.03109 StartY=1.75 StartZ=0 EndX=-3.03109 EndY=-1.75 EndZ=0
    g2: LineSegment StartX=-3.03109 StartY=-1.75 StartZ=0 EndX=-1e-16 EndY=-3.5 EndZ=0
    g3: LineSegment StartX=-1e-16 StartY=-3.5 StartZ=0 EndX=3.03109 EndY=-1.75 EndZ=0
    g4: LineSegment StartX=3.03109 StartY=-1.75 StartZ=0 EndX=3.03109 EndY=1.75 EndZ=0
    g5: LineSegment StartX=3.03109 StartY=1.75 StartZ=0 EndX=1e-16 EndY=3.5 EndZ=0
    g6: Circle [constr] CenterX=0 CenterY=0 CenterZ=0 NormalX=0 NormalY=0 NormalZ=1 AngleXU=0 Radius=3.5
    g7: LineSegment StartX=4.96892 StartY=-1.75002 StartZ=0 EndX=8.00002 EndY=-3.5 EndZ=0
    g8: LineSegment StartX=8.00002 StartY=-3.5 StartZ=0 EndX=11.0311 EndY=-1.74998 EndZ=0
    g9: LineSegment StartX=11.0311 StartY=-1.74998 StartZ=0 EndX=11.0311 EndY=1.75002 EndZ=0
    g10: LineSegment StartX=11.0311 StartY=1.75002 StartZ=0 EndX=7.99998 EndY=3.5 EndZ=0
    g11: LineSegment StartX=7.99998 StartY=3.5 StartZ=0 EndX=4.9689 EndY=1.74998 EndZ=0
    g12: LineSegment StartX=4.9689 StartY=1.74998 StartZ=0 EndX=4.96892 EndY=-1.75002 EndZ=0
    g13: Circle [constr] CenterX=8 CenterY=0 CenterZ=0 NormalX=0 NormalY=0 NormalZ=1 AngleXU=0 Radius=3.5
    g14: LineSegment StartX=4.03109 StartY=3.5 StartZ=0 EndX=7.06218 EndY=5.25 EndZ=0
    g15: LineSegment StartX=7.06218 StartY=5.25 StartZ=0 EndX=7.06218 EndY=8.75 EndZ=0
    g16: LineSegment StartX=7.06218 StartY=8.75 StartZ=0 EndX=4.03109 EndY=10.5 EndZ=0
    g17: LineSegment StartX=4.03109 StartY=10.5 StartZ=0 EndX=1 EndY=8.75 EndZ=0
    g18: LineSegment StartX=1 StartY=8.75 StartZ=0 EndX=1 EndY=5.25 EndZ=0
    g19: LineSegment StartX=1 StartY=5.25 StartZ=0 EndX=4.03109 EndY=3.5 EndZ=0
    g20: Circle [constr] CenterX=4.03109 CenterY=7 CenterZ=0 NormalX=0 NormalY=0 NormalZ=1 AngleXU=0 Radius=3.5
    g21: LineSegment StartX=-1 StartY=5.25 StartZ=0 EndX=-1 EndY=8.75 EndZ=0
    g22: LineSegment StartX=-1 StartY=8.75 StartZ=0 EndX=-4.03109 EndY=10.5 EndZ=0
    g23: LineSegment StartX=-4.03109 StartY=10.5 StartZ=0 EndX=-7.06218 EndY=8.75 EndZ=0
    g24: LineSegment StartX=-7.06218 StartY=8.75 StartZ=0 EndX=-7.06218 EndY=5.25 EndZ=0
    g25: LineSegment StartX=-7.06218 StartY=5.25 StartZ=0 EndX=-4.03109 EndY=3.5 EndZ=0
    g26: LineSegment StartX=-4.03109 StartY=3.5 StartZ=0 EndX=-1 EndY=5.25 EndZ=0
    g27: Circle [constr] CenterX=-4.03109 CenterY=7 CenterZ=0 NormalX=0 NormalY=0 NormalZ=1 AngleXU=0 Radius=3.5
    g28: LineSegment StartX=-4.96891 StartY=-1.75 StartZ=0 EndX=-4.96891 EndY=1.75 EndZ=0
    g29: LineSegment StartX=-4.96891 StartY=1.75 StartZ=0 EndX=-8 EndY=3.5 EndZ=0
    g30: LineSegment StartX=-8 StartY=3.5 StartZ=0 EndX=-11.0311 EndY=1.75 EndZ=0
    g31: LineSegment StartX=-11.0311 StartY=1.75 StartZ=0 EndX=-11.0311 EndY=-1.75 EndZ=0
    g32: LineSegment StartX=-11.0311 StartY=-1.75 StartZ=0 EndX=-8 EndY=-3.5 EndZ=0
    g33: LineSegment StartX=-8 StartY=-3.5 StartZ=0 EndX=-4.96891 EndY=-1.75 EndZ=0
    g34: Circle [constr] CenterX=-8 CenterY=0 CenterZ=0 NormalX=0 NormalY=0 NormalZ=1 AngleXU=0 Radius=3.5
    g35: LineSegment StartX=-4.03109 StartY=-3.5 StartZ=0 EndX=-7.06218 EndY=-5.25 EndZ=0
    g36: LineSegment StartX=-7.06218 StartY=-5.25 StartZ=0 EndX=-7.06218 EndY=-8.75 EndZ=0
    g37: LineSegment StartX=-7.06218 StartY=-8.75 StartZ=0 EndX=-4.03109 EndY=-10.5 EndZ=0
    g38: LineSegment StartX=-4.03109 StartY=-10.5 StartZ=0 EndX=-1 EndY=-8.75 EndZ=0
    g39: LineSegment StartX=-1 StartY=-8.75 StartZ=0 EndX=-1 EndY=-5.25 EndZ=0
    g40: LineSegment StartX=-1 StartY=-5.25 StartZ=0 EndX=-4.03109 EndY=-3.5 EndZ=0
    g41: Circle [constr] CenterX=-4.03109 CenterY=-7 CenterZ=0 NormalX=0 NormalY=0 NormalZ=1 AngleXU=0 Radius=3.5
    g42: LineSegment StartX=4.03109 StartY=-3.5 StartZ=0 EndX=1 EndY=-5.25 EndZ=0
    g43: LineSegment StartX=1 StartY=-5.25 StartZ=0 EndX=1 EndY=-8.75 EndZ=0
    g44: LineSegment StartX=1 StartY=-8.75 StartZ=0 EndX=4.03109 EndY=-10.5 EndZ=0
    g45: LineSegment StartX=4.03109 StartY=-10.5 StartZ=0 EndX=7.06218 EndY=-8.75 EndZ=0
    g46: LineSegment StartX=7.06218 StartY=-8.75 StartZ=0 EndX=7.06218 EndY=-5.25 EndZ=0
    g47: LineSegment StartX=7.06218 StartY=-5.25 StartZ=0 EndX=4.03109 EndY=-3.5 EndZ=0
    g48: Circle [constr] CenterX=4.03109 CenterY=-7 CenterZ=0 NormalX=0 NormalY=0 NormalZ=1 AngleXU=0 Radius=3.5
  constraints (117):
    c: Coincident(g0,g1)
    c: Coincident(g1,g2)
    c: Coincident(g2,g3)
    c: Coincident(g3,g4)
    c: Coincident(g4,g5)
    c: Coincident(g5,g0)
    c: Equal(g0, g1-g5) x5
    c: PointOnObject(g0,g6)
    c: PointOnObject(g1,g6)
    c: PointOnObject(g2,g6)
    c: PointOnObject(g3,g6)
    c: PointOnObject(g4,g6)
    c: PointOnObject(g5,g6)
    c: Coincident(g6,g-1)
    c: Diameter(g6) = 7
    c: PointOnObject(g0,g-2)
    c: Coincident(g7,g8)
    c: Coincident(g8,g9)
    c: Coincident(g9,g10)
    c: Coincident(g10,g11)
    c: Coincident(g11,g12)
    c: Coincident(g12,g7)
    c: Equal(g7, g8-g12) x5
    c: PointOnObject(g7,g13)
    c: PointOnObject(g8,g13)
    c: PointOnObject(g9,g13)
    c: PointOnObject(g10,g13)
    c: PointOnObject(g11,g13)
    c: PointOnObject(g12,g13)
    c: PointOnObject(g13,g-1)
    c: Diameter(g13) = 7
    c: Distance(g6,g13) = 8
    c: Horizontal(g0,g10)
    c: Coincident(g14,g15)
    c: Coincident(g15,g16)
    c: Coincident(g16,g17)
    c: Coincident(g17,g18)
    c: Coincident(g18,g19)
    c: Coincident(g19,g14)
    c: Equal(g14, g15-g19) x5
    c: PointOnObject(g14,g20)
    c: PointOnObject(g15,g20)
    c: PointOnObject(g16,g20)
    c: PointOnObject(g17,g20)
    c: PointOnObject(g18,g20)
    c: PointOnObject(g19,g20)
    c: Diameter(g20) = 7
    c: DistanceY(g-1,g20) = 7
    c: Vertical(g18)
    c: Distance(g17,g-2) = 1
    c: Coincident(g21,g22)
    c: Coincident(g22,g23)
    c: Coincident(g23,g24)
    c: Coincident(g24,g25)
    c: Coincident(g25,g26)
    c: Coincident(g26,g21)
    c: Equal(g21, g22-g26) x5
    c: PointOnObject(g21,g27)
    c: PointOnObject(g22,g27)
    c: PointOnObject(g23,g27)
    c: PointOnObject(g24,g27)
    c: PointOnObject(g25,g27)
    c: PointOnObject(g26,g27)
    c: Diameter(g27) = 7
    c: DistanceY(g-1,g27) = 7
    c: DistanceX(g21,g-1) = 1
    c: Vertical(g21)
    c: Coincident(g28,g29)
    c: Coincident(g29,g30)
    c: Coincident(g30,g31)
    c: Coincident(g31,g32)
    c: Coincident(g32,g33)
    c: Coincident(g33,g28)
    c: Equal(g28, g29-g33) x5
    c: PointOnObject(g28,g34)
    c: PointOnObject(g29,g34)
    c: PointOnObject(g30,g34)
    c: PointOnObject(g31,g34)
    c: PointOnObject(g32,g34)
    c: PointOnObject(g33,g34)
    c: PointOnObject(g34,g-1)
    c: Diameter(g34) = 7
    c: Vertical(g31)
    c: DistanceX(g34,g-1) = 8
    c: Coincident(g35,g36)
    c: Coincident(g36,g37)
    c: Coincident(g37,g38)
    c: Coincident(g38,g39)
    c: Coincident(g39,g40)
    c: Coincident(g40,g35)
    c: Equal(g35, g36-g40) x5
    c: PointOnObject(g35,g41)
    c: PointOnObject(g36,g41)
    c: PointOnObject(g37,g41)
    c: PointOnObject(g38,g41)
    c: PointOnObject(g39,g41)
    c: PointOnObject(g40,g41)
    c: Coincident(g42,g43)
    c: Coincident(g43,g44)
    c: Coincident(g44,g45)
    c: Coincident(g45,g46)
    c: Coincident(g46,g47)
    c: Coincident(g47,g42)
    c: Equal(g42, g43-g47) x5
    c: PointOnObject(g42,g48)
    c: PointOnObject(g43,g48)
    c: PointOnObject(g44,g48)
    c: PointOnObject(g45,g48)
    c: PointOnObject(g46,g48)
    c: PointOnObject(g47,g48)
    c: Equal(g41,g48)
    c: Diameter(g41) = 7
    c: Vertical(g39)
    c: Vertical(g43)
    c: Distance(g-2,g39) = 1
    c: Symmetric(g38,g43,g-2)
    c: Distance(g41,g-1) = 7
FEATURE [Part::Extrusion] Extrude578  label="hex180"
  Base = -> Sketch587
  Dir = (0,-1,2e-16)
  DirMode = 2
  FaceMakerClass = Part::FaceMakerBullseye
  FaceMakerMode = 3
  LengthFwd = 10
  LengthRev = 0
  Placement = pos=(32,0,28) rot=(0,0,1;0rad)
  Solid = true
  Symmetric = false
FEATURE [Sketcher::SketchObject] Sketch588
  ArcFitTolerance = 1e-06
  FullyConstrained = true
  MakeInternals = false
  Placement = pos=(0,0,0) rot=(1,0,0;1.5708rad)
  sketch-geometry (49):
    g0: LineSegment StartX=1e-16 StartY=3.5 StartZ=0 EndX=-3.03109 EndY=1.75 EndZ=0
    g1: LineSegment StartX=-3.03109 StartY=1.75 StartZ=0 EndX=-3.03109 EndY=-1.75 EndZ=0
    g2: LineSegment StartX=-3.03109 StartY=-1.75 StartZ=0 EndX=-1e-16 EndY=-3.5 EndZ=0
    g3: LineSegment StartX=-1e-16 StartY=-3.5 StartZ=0 EndX=3.03109 EndY=-1.75 EndZ=0
    g4: LineSegment StartX=3.03109 StartY=-1.75 StartZ=0 EndX=3.03109 EndY=1.75 EndZ=0
    g5: LineSegment StartX=3.03109 StartY=1.75 StartZ=0 EndX=1e-16 EndY=3.5 EndZ=0
    g6: Circle [constr] CenterX=0 CenterY=0 CenterZ=0 NormalX=0 NormalY=0 NormalZ=1 AngleXU=0 Radius=3.5
    g7: LineSegment StartX=4.96892 StartY=-1.75002 StartZ=0 EndX=8.00002 EndY=-3.5 EndZ=0
    g8: LineSegment StartX=8.00002 StartY=-3.5 StartZ=0 EndX=11.0311 EndY=-1.74998 EndZ=0
    g9: LineSegment StartX=11.0311 StartY=-1.74998 StartZ=0 EndX=11.0311 EndY=1.75002 EndZ=0
    g10: LineSegment StartX=11.0311 StartY=1.75002 StartZ=0 EndX=7.99998 EndY=3.5 EndZ=0
    g11: LineSegment StartX=7.99998 StartY=3.5 StartZ=0 EndX=4.9689 EndY=1.74998 EndZ=0
    g12: LineSegment StartX=4.9689 StartY=1.74998 StartZ=0 EndX=4.96892 EndY=-1.75002 EndZ=0
    g13: Circle [constr] CenterX=8 CenterY=0 CenterZ=0 NormalX=0 NormalY=0 NormalZ=1 AngleXU=0 Radius=3.5
    g14: LineSegment StartX=4.03109 StartY=3.5 StartZ=0 EndX=7.06218 EndY=5.25 EndZ=0
    g15: LineSegment StartX=7.06218 StartY=5.25 StartZ=0 EndX=7.06218 EndY=8.75 EndZ=0
    g16: LineSegment StartX=7.06218 StartY=8.75 StartZ=0 EndX=4.03109 EndY=10.5 EndZ=0
    g17: LineSegment StartX=4.03109 StartY=10.5 StartZ=0 EndX=1 EndY=8.75 EndZ=0
    g18: LineSegment StartX=1 StartY=8.75 StartZ=0 EndX=1 EndY=5.25 EndZ=0
    g19: LineSegment StartX=1 StartY=5.25 StartZ=0 EndX=4.03109 EndY=3.5 EndZ=0
    g20: Circle [constr] CenterX=4.03109 CenterY=7 CenterZ=0 NormalX=0 NormalY=0 NormalZ=1 AngleXU=0 Radius=3.5
    g21: LineSegment StartX=-1 StartY=5.25 StartZ=0 EndX=-1 EndY=8.75 EndZ=0
    g22: LineSegment StartX=-1 StartY=8.75 StartZ=0 EndX=-4.03109 EndY=10.5 EndZ=0
    g23: LineSegment StartX=-4.03109 StartY=10.5 StartZ=0 EndX=-7.06218 EndY=8.75 EndZ=0
    g24: LineSegment StartX=-7.06218 StartY=8.75 StartZ=0 EndX=-7.06218 EndY=5.25 EndZ=0
    g25: LineSegment StartX=-7.06218 StartY=5.25 StartZ=0 EndX=-4.03109 EndY=3.5 EndZ=0
    g26: LineSegment StartX=-4.03109 StartY=3.5 StartZ=0 EndX=-1 EndY=5.25 EndZ=0
    g27: Circle [constr] CenterX=-4.03109 CenterY=7 CenterZ=0 NormalX=0 NormalY=0 NormalZ=1 AngleXU=0 Radius=3.5
    g28: LineSegment StartX=-4.96891 StartY=-1.75 StartZ=0 EndX=-4.96891 EndY=1.75 EndZ=0
    g29: LineSegment StartX=-4.96891 StartY=1.75 StartZ=0 EndX=-8 EndY=3.5 EndZ=0
    g30: LineSegment StartX=-8 StartY=3.5 StartZ=0 EndX=-11.0311 EndY=1.75 EndZ=0
    g31: LineSegment StartX=-11.0311 StartY=1.75 StartZ=0 EndX=-11.0311 EndY=-1.75 EndZ=0
    g32: LineSegment StartX=-11.0311 StartY=-1.75 StartZ=0 EndX=-8 EndY=-3.5 EndZ=0
    g33: LineSegment StartX=-8 StartY=-3.5 StartZ=0 EndX=-4.96891 EndY=-1.75 EndZ=0
    g34: Circle [constr] CenterX=-8 CenterY=0 CenterZ=0 NormalX=0 NormalY=0 NormalZ=1 AngleXU=0 Radius=3.5
    g35: LineSegment StartX=-4.03109 StartY=-3.5 StartZ=0 EndX=-7.06218 EndY=-5.25 EndZ=0
    g36: LineSegment StartX=-7.06218 StartY=-5.25 StartZ=0 EndX=-7.06218 EndY=-8.75 EndZ=0
    g37: LineSegment StartX=-7.06218 StartY=-8.75 StartZ=0 EndX=-4.03109 EndY=-10.5 EndZ=0
    g38: LineSegment StartX=-4.03109 StartY=-10.5 StartZ=0 EndX=-1 EndY=-8.75 EndZ=0
    g39: LineSegment StartX=-1 StartY=-8.75 StartZ=0 EndX=-1 EndY=-5.25 EndZ=0
    g40: LineSegment StartX=-1 StartY=-5.25 StartZ=0 EndX=-4.03109 EndY=-3.5 EndZ=0
    g41: Circle [constr] CenterX=-4.03109 CenterY=-7 CenterZ=0 NormalX=0 NormalY=0 NormalZ=1 AngleXU=0 Radius=3.5
    g42: LineSegment StartX=4.03109 StartY=-3.5 StartZ=0 EndX=1 EndY=-5.25 EndZ=0
    g43: LineSegment StartX=1 StartY=-5.25 StartZ=0 EndX=1 EndY=-8.75 EndZ=0
    g44: LineSegment StartX=1 StartY=-8.75 StartZ=0 EndX=4.03109 EndY=-10.5 EndZ=0
    g45: LineSegment StartX=4.03109 StartY=-10.5 StartZ=0 EndX=7.06218 EndY=-8.75 EndZ=0
    g46: LineSegment StartX=7.06218 StartY=-8.75 StartZ=0 EndX=7.06218 EndY=-5.25 EndZ=0
    g47: LineSegment StartX=7.06218 StartY=-5.25 StartZ=0 EndX=4.03109 EndY=-3.5 EndZ=0
    g48: Circle [constr] CenterX=4.03109 CenterY=-7 CenterZ=0 NormalX=0 NormalY=0 NormalZ=1 AngleXU=0 Radius=3.5
  constraints (117):
    c: Coincident(g0,g1)
    c: Coincident(g1,g2)
    c: Coincident(g2,g3)
    c: Coincident(g3,g4)
    c: Coincident(g4,g5)
    c: Coincident(g5,g0)
    c: Equal(g0, g1-g5) x5
    c: PointOnObject(g0,g6)
    c: PointOnObject(g1,g6)
    c: PointOnObject(g2,g6)
    c: PointOnObject(g3,g6)
    c: PointOnObject(g4,g6)
    c: PointOnObject(g5,g6)
    c: Coincident(g6,g-1)
    c: Diameter(g6) = 7
    c: PointOnObject(g0,g-2)
    c: Coincident(g7,g8)
    c: Coincident(g8,g9)
    c: Coincident(g9,g10)
    c: Coincident(g10,g11)
    c: Coincident(g11,g12)
    c: Coincident(g12,g7)
    c: Equal(g7, g8-g12) x5
    c: PointOnObject(g7,g13)
    c: PointOnObject(g8,g13)
    c: PointOnObject(g9,g13)
    c: PointOnObject(g10,g13)
    c: PointOnObject(g11,g13)
    c: PointOnObject(g12,g13)
    c: PointOnObject(g13,g-1)
    c: Diameter(g13) = 7
    c: Distance(g6,g13) = 8
    c: Horizontal(g0,g10)
    c: Coincident(g14,g15)
    c: Coincident(g15,g16)
    c: Coincident(g16,g17)
    c: Coincident(g17,g18)
    c: Coincident(g18,g19)
    c: Coincident(g19,g14)
    c: Equal(g14, g15-g19) x5
    c: PointOnObject(g14,g20)
    c: PointOnObject(g15,g20)
    c: PointOnObject(g16,g20)
    c: PointOnObject(g17,g20)
    c: PointOnObject(g18,g20)
    c: PointOnObject(g19,g20)
    c: Diameter(g20) = 7
    c: DistanceY(g-1,g20) = 7
    c: Vertical(g18)
    c: Distance(g17,g-2) = 1
    c: Coincident(g21,g22)
    c: Coincident(g22,g23)
    c: Coincident(g23,g24)
    c: Coincident(g24,g25)
    c: Coincident(g25,g26)
    c: Coincident(g26,g21)
    c: Equal(g21, g22-g26) x5
    c: PointOnObject(g21,g27)
    c: PointOnObject(g22,g27)
    c: PointOnObject(g23,g27)
    c: PointOnObject(g24,g27)
    c: PointOnObject(g25,g27)
    c: PointOnObject(g26,g27)
    c: Diameter(g27) = 7
    c: DistanceY(g-1,g27) = 7
    c: DistanceX(g21,g-1) = 1
    c: Vertical(g21)
    c: Coincident(g28,g29)
    c: Coincident(g29,g30)
    c: Coincident(g30,g31)
    c: Coincident(g31,g32)
    c: Coincident(g32,g33)
    c: Coincident(g33,g28)
    c: Equal(g28, g29-g33) x5
    c: PointOnObject(g28,g34)
    c: PointOnObject(g29,g34)
    c: PointOnObject(g30,g34)
    c: PointOnObject(g31,g34)
    c: PointOnObject(g32,g34)
    c: PointOnObject(g33,g34)
    c: PointOnObject(g34,g-1)
    c: Diameter(g34) = 7
    c: Vertical(g31)
    c: DistanceX(g34,g-1) = 8
    c: Coincident(g35,g36)
    c: Coincident(g36,g37)
    c: Coincident(g37,g38)
    c: Coincident(g38,g39)
    c: Coincident(g39,g40)
    c: Coincident(g40,g35)
    c: Equal(g35, g36-g40) x5
    c: PointOnObject(g35,g41)
    c: PointOnObject(g36,g41)
    c: PointOnObject(g37,g41)
    c: PointOnObject(g38,g41)
    c: PointOnObject(g39,g41)
    c: PointOnObject(g40,g41)
    c: Coincident(g42,g43)
    c: Coincident(g43,g44)
    c: Coincident(g44,g45)
    c: Coincident(g45,g46)
    c: Coincident(g46,g47)
    c: Coincident(g47,g42)
    c: Equal(g42, g43-g47) x5
    c: PointOnObject(g42,g48)
    c: PointOnObject(g43,g48)
    c: PointOnObject(g44,g48)
    c: PointOnObject(g45,g48)
    c: PointOnObject(g46,g48)
    c: PointOnObject(g47,g48)
    c: Equal(g41,g48)
    c: Diameter(g41) = 7
    c: Vertical(g39)
    c: Vertical(g43)
    c: Distance(g-2,g39) = 1
    c: Symmetric(g38,g43,g-2)
    c: Distance(g41,g-1) = 7
FEATURE [Part::Extrusion] Extrude579  label="hex181"
  Base = -> Sketch588
  Dir = (0,-1,2e-16)
  DirMode = 2
  FaceMakerClass = Part::FaceMakerBullseye
  FaceMakerMode = 3
  LengthFwd = 10
  LengthRev = 0
  Placement = pos=(-40,0,-14) rot=(0,0,1;0rad)
  Solid = true
  Symmetric = false
FEATURE [Sketcher::SketchObject] Sketch589
  ArcFitTolerance = 1e-06
  FullyConstrained = true
  MakeInternals = false
  Placement = pos=(0,0,0) rot=(1,0,0;1.5708rad)
  sketch-geometry (49):
    g0: LineSegment StartX=1e-16 StartY=3.5 StartZ=0 EndX=-3.03109 EndY=1.75 EndZ=0
    g1: LineSegment StartX=-3.03109 StartY=1.75 StartZ=0 EndX=-3.03109 EndY=-1.75 EndZ=0
    g2: LineSegment StartX=-3.03109 StartY=-1.75 StartZ=0 EndX=-1e-16 EndY=-3.5 EndZ=0
    g3: LineSegment StartX=-1e-16 StartY=-3.5 StartZ=0 EndX=3.03109 EndY=-1.75 EndZ=0
    g4: LineSegment StartX=3.03109 StartY=-1.75 StartZ=0 EndX=3.03109 EndY=1.75 EndZ=0
    g5: LineSegment StartX=3.03109 StartY=1.75 StartZ=0 EndX=1e-16 EndY=3.5 EndZ=0
    g6: Circle [constr] CenterX=0 CenterY=0 CenterZ=0 NormalX=0 NormalY=0 NormalZ=1 AngleXU=0 Radius=3.5
    g7: LineSegment StartX=4.96892 StartY=-1.75002 StartZ=0 EndX=8.00002 EndY=-3.5 EndZ=0
    g8: LineSegment StartX=8.00002 StartY=-3.5 StartZ=0 EndX=11.0311 EndY=-1.74998 EndZ=0
    g9: LineSegment StartX=11.0311 StartY=-1.74998 StartZ=0 EndX=11.0311 EndY=1.75002 EndZ=0
    g10: LineSegment StartX=11.0311 StartY=1.75002 StartZ=0 EndX=7.99998 EndY=3.5 EndZ=0
    g11: LineSegment StartX=7.99998 StartY=3.5 StartZ=0 EndX=4.9689 EndY=1.74998 EndZ=0
    g12: LineSegment StartX=4.9689 StartY=1.74998 StartZ=0 EndX=4.96892 EndY=-1.75002 EndZ=0
    g13: Circle [constr] CenterX=8 CenterY=0 CenterZ=0 NormalX=0 NormalY=0 NormalZ=1 AngleXU=0 Radius=3.5
    g14: LineSegment StartX=4.03109 StartY=3.5 StartZ=0 EndX=7.06218 EndY=5.25 EndZ=0
    g15: LineSegment StartX=7.06218 StartY=5.25 StartZ=0 EndX=7.06218 EndY=8.75 EndZ=0
    g16: LineSegment StartX=7.06218 StartY=8.75 StartZ=0 EndX=4.03109 EndY=10.5 EndZ=0
    g17: LineSegment StartX=4.03109 StartY=10.5 StartZ=0 EndX=1 EndY=8.75 EndZ=0
    g18: LineSegment StartX=1 StartY=8.75 StartZ=0 EndX=1 EndY=5.25 EndZ=0
    g19: LineSegment StartX=1 StartY=5.25 StartZ=0 EndX=4.03109 EndY=3.5 EndZ=0
    g20: Circle [constr] CenterX=4.03109 CenterY=7 CenterZ=0 NormalX=0 NormalY=0 NormalZ=1 AngleXU=0 Radius=3.5
    g21: LineSegment StartX=-1 StartY=5.25 StartZ=0 EndX=-1 EndY=8.75 EndZ=0
    g22: LineSegment StartX=-1 StartY=8.75 StartZ=0 EndX=-4.03109 EndY=10.5 EndZ=0
    g23: LineSegment StartX=-4.03109 StartY=10.5 StartZ=0 EndX=-7.06218 EndY=8.75 EndZ=0
    g24: LineSegment StartX=-7.06218 StartY=8.75 StartZ=0 EndX=-7.06218 EndY=5.25 EndZ=0
    g25: LineSegment StartX=-7.06218 StartY=5.25 StartZ=0 EndX=-4.03109 EndY=3.5 EndZ=0
    g26: LineSegment StartX=-4.03109 StartY=3.5 StartZ=0 EndX=-1 EndY=5.25 EndZ=0
    g27: Circle [constr] CenterX=-4.03109 CenterY=7 CenterZ=0 NormalX=0 NormalY=0 NormalZ=1 AngleXU=0 Radius=3.5
    g28: LineSegment StartX=-4.96891 StartY=-1.75 StartZ=0 EndX=-4.96891 EndY=1.75 EndZ=0
    g29: LineSegment StartX=-4.96891 StartY=1.75 StartZ=0 EndX=-8 EndY=3.5 EndZ=0
    g30: LineSegment StartX=-8 StartY=3.5 StartZ=0 EndX=-11.0311 EndY=1.75 EndZ=0
    g31: LineSegment StartX=-11.0311 StartY=1.75 StartZ=0 EndX=-11.0311 EndY=-1.75 EndZ=0
    g32: LineSegment StartX=-11.0311 StartY=-1.75 StartZ=0 EndX=-8 EndY=-3.5 EndZ=0
    g33: LineSegment StartX=-8 StartY=-3.5 StartZ=0 EndX=-4.96891 EndY=-1.75 EndZ=0
    g34: Circle [constr] CenterX=-8 CenterY=0 CenterZ=0 NormalX=0 NormalY=0 NormalZ=1 AngleXU=0 Radius=3.5
    g35: LineSegment StartX=-4.03109 StartY=-3.5 StartZ=0 EndX=-7.06218 EndY=-5.25 EndZ=0
    g36: LineSegment StartX=-7.06218 StartY=-5.25 StartZ=0 EndX=-7.06218 EndY=-8.75 EndZ=0
    g37: LineSegment StartX=-7.06218 StartY=-8.75 StartZ=0 EndX=-4.03109 EndY=-10.5 EndZ=0
    g38: LineSegment StartX=-4.03109 StartY=-10.5 StartZ=0 EndX=-1 EndY=-8.75 EndZ=0
    g39: LineSegment StartX=-1 StartY=-8.75 StartZ=0 EndX=-1 EndY=-5.25 EndZ=0
    g40: LineSegment StartX=-1 StartY=-5.25 StartZ=0 EndX=-4.03109 EndY=-3.5 EndZ=0
    g41: Circle [constr] CenterX=-4.03109 CenterY=-7 CenterZ=0 NormalX=0 NormalY=0 NormalZ=1 AngleXU=0 Radius=3.5
    g42: LineSegment StartX=4.03109 StartY=-3.5 StartZ=0 EndX=1 EndY=-5.25 EndZ=0
    g43: LineSegment StartX=1 StartY=-5.25 StartZ=0 EndX=1 EndY=-8.75 EndZ=0
    g44: LineSegment StartX=1 StartY=-8.75 StartZ=0 EndX=4.03109 EndY=-10.5 EndZ=0
    g45: LineSegment StartX=4.03109 StartY=-10.5 StartZ=0 EndX=7.06218 EndY=-8.75 EndZ=0
    g46: LineSegment StartX=7.06218 StartY=-8.75 StartZ=0 EndX=7.06218 EndY=-5.25 EndZ=0
    g47: LineSegment StartX=7.06218 StartY=-5.25 StartZ=0 EndX=4.03109 EndY=-3.5 EndZ=0
    g48: Circle [constr] CenterX=4.03109 CenterY=-7 CenterZ=0 NormalX=0 NormalY=0 NormalZ=1 AngleXU=0 Radius=3.5
  constraints (117):
    c: Coincident(g0,g1)
    c: Coincident(g1,g2)
    c: Coincident(g2,g3)
    c: Coincident(g3,g4)
    c: Coincident(g4,g5)
    c: Coincident(g5,g0)
    c: Equal(g0, g1-g5) x5
    c: PointOnObject(g0,g6)
    c: PointOnObject(g1,g6)
    c: PointOnObject(g2,g6)
    c: PointOnObject(g3,g6)
    c: PointOnObject(g4,g6)
    c: PointOnObject(g5,g6)
    c: Coincident(g6,g-1)
    c: Diameter(g6) = 7
    c: PointOnObject(g0,g-2)
    c: Coincident(g7,g8)
    c: Coincident(g8,g9)
    c: Coincident(g9,g10)
    c: Coincident(g10,g11)
    c: Coincident(g11,g12)
    c: Coincident(g12,g7)
    c: Equal(g7, g8-g12) x5
    c: PointOnObject(g7,g13)
    c: PointOnObject(g8,g13)
    c: PointOnObject(g9,g13)
    c: PointOnObject(g10,g13)
    c: PointOnObject(g11,g13)
    c: PointOnObject(g12,g13)
    c: PointOnObject(g13,g-1)
    c: Diameter(g13) = 7
    c: Distance(g6,g13) = 8
    c: Horizontal(g0,g10)
    c: Coincident(g14,g15)
    c: Coincident(g15,g16)
    c: Coincident(g16,g17)
    c: Coincident(g17,g18)
    c: Coincident(g18,g19)
    c: Coincident(g19,g14)
    c: Equal(g14, g15-g19) x5
    c: PointOnObject(g14,g20)
    c: PointOnObject(g15,g20)
    c: PointOnObject(g16,g20)
    c: PointOnObject(g17,g20)
    c: PointOnObject(g18,g20)
    c: PointOnObject(g19,g20)
    c: Diameter(g20) = 7
    c: DistanceY(g-1,g20) = 7
    c: Vertical(g18)
    c: Distance(g17,g-2) = 1
    c: Coincident(g21,g22)
    c: Coincident(g22,g23)
    c: Coincident(g23,g24)
    c: Coincident(g24,g25)
    c: Coincident(g25,g26)
    c: Coincident(g26,g21)
    c: Equal(g21, g22-g26) x5
    c: PointOnObject(g21,g27)
    c: PointOnObject(g22,g27)
    c: PointOnObject(g23,g27)
    c: PointOnObject(g24,g27)
    c: PointOnObject(g25,g27)
    c: PointOnObject(g26,g27)
    c: Diameter(g27) = 7
    c: DistanceY(g-1,g27) = 7
    c: DistanceX(g21,g-1) = 1
    c: Vertical(g21)
    c: Coincident(g28,g29)
    c: Coincident(g29,g30)
    c: Coincident(g30,g31)
    c: Coincident(g31,g32)
    c: Coincident(g32,g33)
    c: Coincident(g33,g28)
    c: Equal(g28, g29-g33) x5
    c: PointOnObject(g28,g34)
    c: PointOnObject(g29,g34)
    c: PointOnObject(g30,g34)
    c: PointOnObject(g31,g34)
    c: PointOnObject(g32,g34)
    c: PointOnObject(g33,g34)
    c: PointOnObject(g34,g-1)
    c: Diameter(g34) = 7
    c: Vertical(g31)
    c: DistanceX(g34,g-1) = 8
    c: Coincident(g35,g36)
    c: Coincident(g36,g37)
    c: Coincident(g37,g38)
    c: Coincident(g38,g39)
    c: Coincident(g39,g40)
    c: Coincident(g40,g35)
    c: Equal(g35, g36-g40) x5
    c: PointOnObject(g35,g41)
    c: PointOnObject(g36,g41)
    c: PointOnObject(g37,g41)
    c: PointOnObject(g38,g41)
    c: PointOnObject(g39,g41)
    c: PointOnObject(g40,g41)
    c: Coincident(g42,g43)
    c: Coincident(g43,g44)
    c: Coincident(g44,g45)
    c: Coincident(g45,g46)
    c: Coincident(g46,g47)
    c: Coincident(g47,g42)
    c: Equal(g42, g43-g47) x5
    c: PointOnObject(g42,g48)
    c: PointOnObject(g43,g48)
    c: PointOnObject(g44,g48)
    c: PointOnObject(g45,g48)
    c: PointOnObject(g46,g48)
    c: PointOnObject(g47,g48)
    c: Equal(g41,g48)
    c: Diameter(g41) = 7
    c: Vertical(g39)
    c: Vertical(g43)
    c: Distance(g-2,g39) = 1
    c: Symmetric(g38,g43,g-2)
    c: Distance(g41,g-1) = 7
FEATURE [Part::Extrusion] Extrude580  label="hex182"
  Base = -> Sketch589
  Dir = (0,-1,2e-16)
  DirMode = 2
  FaceMakerClass = Part::FaceMakerBullseye
  FaceMakerMode = 3
  LengthFwd = 10
  LengthRev = 0
  Placement = pos=(-24,0,-28) rot=(0,0,1;0rad)
  Solid = true
  Symmetric = false
FEATURE [Sketcher::SketchObject] Sketch590
  ArcFitTolerance = 1e-06
  FullyConstrained = true
  MakeInternals = false
  Placement = pos=(0,0,0) rot=(1,0,0;1.5708rad)
  sketch-geometry (49):
    g0: LineSegment StartX=1e-16 StartY=3.5 StartZ=0 EndX=-3.03109 EndY=1.75 EndZ=0
    g1: LineSegment StartX=-3.03109 StartY=1.75 StartZ=0 EndX=-3.03109 EndY=-1.75 EndZ=0
    g2: LineSegment StartX=-3.03109 StartY=-1.75 StartZ=0 EndX=-1e-16 EndY=-3.5 EndZ=0
    g3: LineSegment StartX=-1e-16 StartY=-3.5 StartZ=0 EndX=3.03109 EndY=-1.75 EndZ=0
    g4: LineSegment StartX=3.03109 StartY=-1.75 StartZ=0 EndX=3.03109 EndY=1.75 EndZ=0
    g5: LineSegment StartX=3.03109 StartY=1.75 StartZ=0 EndX=1e-16 EndY=3.5 EndZ=0
    g6: Circle [constr] CenterX=0 CenterY=0 CenterZ=0 NormalX=0 NormalY=0 NormalZ=1 AngleXU=0 Radius=3.5
    g7: LineSegment StartX=4.96892 StartY=-1.75002 StartZ=0 EndX=8.00002 EndY=-3.5 EndZ=0
    g8: LineSegment StartX=8.00002 StartY=-3.5 StartZ=0 EndX=11.0311 EndY=-1.74998 EndZ=0
    g9: LineSegment StartX=11.0311 StartY=-1.74998 StartZ=0 EndX=11.0311 EndY=1.75002 EndZ=0
    g10: LineSegment StartX=11.0311 StartY=1.75002 StartZ=0 EndX=7.99998 EndY=3.5 EndZ=0
    g11: LineSegment StartX=7.99998 StartY=3.5 StartZ=0 EndX=4.9689 EndY=1.74998 EndZ=0
    g12: LineSegment StartX=4.9689 StartY=1.74998 StartZ=0 EndX=4.96892 EndY=-1.75002 EndZ=0
    g13: Circle [constr] CenterX=8 CenterY=0 CenterZ=0 NormalX=0 NormalY=0 NormalZ=1 AngleXU=0 Radius=3.5
    g14: LineSegment StartX=4.03109 StartY=3.5 StartZ=0 EndX=7.06218 EndY=5.25 EndZ=0
    g15: LineSegment StartX=7.06218 StartY=5.25 StartZ=0 EndX=7.06218 EndY=8.75 EndZ=0
    g16: LineSegment StartX=7.06218 StartY=8.75 StartZ=0 EndX=4.03109 EndY=10.5 EndZ=0
    g17: LineSegment StartX=4.03109 StartY=10.5 StartZ=0 EndX=1 EndY=8.75 EndZ=0
    g18: LineSegment StartX=1 StartY=8.75 StartZ=0 EndX=1 EndY=5.25 EndZ=0
    g19: LineSegment StartX=1 StartY=5.25 StartZ=0 EndX=4.03109 EndY=3.5 EndZ=0
    g20: Circle [constr] CenterX=4.03109 CenterY=7 CenterZ=0 NormalX=0 NormalY=0 NormalZ=1 AngleXU=0 Radius=3.5
    g21: LineSegment StartX=-1 StartY=5.25 StartZ=0 EndX=-1 EndY=8.75 EndZ=0
    g22: LineSegment StartX=-1 StartY=8.75 StartZ=0 EndX=-4.03109 EndY=10.5 EndZ=0
    g23: LineSegment StartX=-4.03109 StartY=10.5 StartZ=0 EndX=-7.06218 EndY=8.75 EndZ=0
    g24: LineSegment StartX=-7.06218 StartY=8.75 StartZ=0 EndX=-7.06218 EndY=5.25 EndZ=0
    g25: LineSegment StartX=-7.06218 StartY=5.25 StartZ=0 EndX=-4.03109 EndY=3.5 EndZ=0
    g26: LineSegment StartX=-4.03109 StartY=3.5 StartZ=0 EndX=-1 EndY=5.25 EndZ=0
    g27: Circle [constr] CenterX=-4.03109 CenterY=7 CenterZ=0 NormalX=0 NormalY=0 NormalZ=1 AngleXU=0 Radius=3.5
    g28: LineSegment StartX=-4.96891 StartY=-1.75 StartZ=0 EndX=-4.96891 EndY=1.75 EndZ=0
    g29: LineSegment StartX=-4.96891 StartY=1.75 StartZ=0 EndX=-8 EndY=3.5 EndZ=0
    g30: LineSegment StartX=-8 StartY=3.5 StartZ=0 EndX=-11.0311 EndY=1.75 EndZ=0
    g31: LineSegment StartX=-11.0311 StartY=1.75 StartZ=0 EndX=-11.0311 EndY=-1.75 EndZ=0
    g32: LineSegment StartX=-11.0311 StartY=-1.75 StartZ=0 EndX=-8 EndY=-3.5 EndZ=0
    g33: LineSegment StartX=-8 StartY=-3.5 StartZ=0 EndX=-4.96891 EndY=-1.75 EndZ=0
    g34: Circle [constr] CenterX=-8 CenterY=0 CenterZ=0 NormalX=0 NormalY=0 NormalZ=1 AngleXU=0 Radius=3.5
    g35: LineSegment StartX=-4.03109 StartY=-3.5 StartZ=0 EndX=-7.06218 EndY=-5.25 EndZ=0
    g36: LineSegment StartX=-7.06218 StartY=-5.25 StartZ=0 EndX=-7.06218 EndY=-8.75 EndZ=0
    g37: LineSegment StartX=-7.06218 StartY=-8.75 StartZ=0 EndX=-4.03109 EndY=-10.5 EndZ=0
    g38: LineSegment StartX=-4.03109 StartY=-10.5 StartZ=0 EndX=-1 EndY=-8.75 EndZ=0
    g39: LineSegment StartX=-1 StartY=-8.75 StartZ=0 EndX=-1 EndY=-5.25 EndZ=0
    g40: LineSegment StartX=-1 StartY=-5.25 StartZ=0 EndX=-4.03109 EndY=-3.5 EndZ=0
    g41: Circle [constr] CenterX=-4.03109 CenterY=-7 CenterZ=0 NormalX=0 NormalY=0 NormalZ=1 AngleXU=0 Radius=3.5
    g42: LineSegment StartX=4.03109 StartY=-3.5 StartZ=0 EndX=1 EndY=-5.25 EndZ=0
    g43: LineSegment StartX=1 StartY=-5.25 StartZ=0 EndX=1 EndY=-8.75 EndZ=0
    g44: LineSegment StartX=1 StartY=-8.75 StartZ=0 EndX=4.03109 EndY=-10.5 EndZ=0
    g45: LineSegment StartX=4.03109 StartY=-10.5 StartZ=0 EndX=7.06218 EndY=-8.75 EndZ=0
    g46: LineSegment StartX=7.06218 StartY=-8.75 StartZ=0 EndX=7.06218 EndY=-5.25 EndZ=0
    g47: LineSegment StartX=7.06218 StartY=-5.25 StartZ=0 EndX=4.03109 EndY=-3.5 EndZ=0
    g48: Circle [constr] CenterX=4.03109 CenterY=-7 CenterZ=0 NormalX=0 NormalY=0 NormalZ=1 AngleXU=0 Radius=3.5
  constraints (117):
    c: Coincident(g0,g1)
    c: Coincident(g1,g2)
    c: Coincident(g2,g3)
    c: Coincident(g3,g4)
    c: Coincident(g4,g5)
    c: Coincident(g5,g0)
    c: Equal(g0, g1-g5) x5
    c: PointOnObject(g0,g6)
    c: PointOnObject(g1,g6)
    c: PointOnObject(g2,g6)
    c: PointOnObject(g3,g6)
    c: PointOnObject(g4,g6)
    c: PointOnObject(g5,g6)
    c: Coincident(g6,g-1)
    c: Diameter(g6) = 7
    c: PointOnObject(g0,g-2)
    c: Coincident(g7,g8)
    c: Coincident(g8,g9)
    c: Coincident(g9,g10)
    c: Coincident(g10,g11)
    c: Coincident(g11,g12)
    c: Coincident(g12,g7)
    c: Equal(g7, g8-g12) x5
    c: PointOnObject(g7,g13)
    c: PointOnObject(g8,g13)
    c: PointOnObject(g9,g13)
    c: PointOnObject(g10,g13)
    c: PointOnObject(g11,g13)
    c: PointOnObject(g12,g13)
    c: PointOnObject(g13,g-1)
    c: Diameter(g13) = 7
    c: Distance(g6,g13) = 8
    c: Horizontal(g0,g10)
    c: Coincident(g14,g15)
    c: Coincident(g15,g16)
    c: Coincident(g16,g17)
    c: Coincident(g17,g18)
    c: Coincident(g18,g19)
    c: Coincident(g19,g14)
    c: Equal(g14, g15-g19) x5
    c: PointOnObject(g14,g20)
    c: PointOnObject(g15,g20)
    c: PointOnObject(g16,g20)
    c: PointOnObject(g17,g20)
    c: PointOnObject(g18,g20)
    c: PointOnObject(g19,g20)
    c: Diameter(g20) = 7
    c: DistanceY(g-1,g20) = 7
    c: Vertical(g18)
    c: Distance(g17,g-2) = 1
    c: Coincident(g21,g22)
    c: Coincident(g22,g23)
    c: Coincident(g23,g24)
    c: Coincident(g24,g25)
    c: Coincident(g25,g26)
    c: Coincident(g26,g21)
    c: Equal(g21, g22-g26) x5
    c: PointOnObject(g21,g27)
    c: PointOnObject(g22,g27)
    c: PointOnObject(g23,g27)
    c: PointOnObject(g24,g27)
    c: PointOnObject(g25,g27)
    c: PointOnObject(g26,g27)
    c: Diameter(g27) = 7
    c: DistanceY(g-1,g27) = 7
    c: DistanceX(g21,g-1) = 1
    c: Vertical(g21)
    c: Coincident(g28,g29)
    c: Coincident(g29,g30)
    c: Coincident(g30,g31)
    c: Coincident(g31,g32)
    c: Coincident(g32,g33)
    c: Coincident(g33,g28)
    c: Equal(g28, g29-g33) x5
    c: PointOnObject(g28,g34)
    c: PointOnObject(g29,g34)
    c: PointOnObject(g30,g34)
    c: PointOnObject(g31,g34)
    c: PointOnObject(g32,g34)
    c: PointOnObject(g33,g34)
    c: PointOnObject(g34,g-1)
    c: Diameter(g34) = 7
    c: Vertical(g31)
    c: DistanceX(g34,g-1) = 8
    c: Coincident(g35,g36)
    c: Coincident(g36,g37)
    c: Coincident(g37,g38)
    c: Coincident(g38,g39)
    c: Coincident(g39,g40)
    c: Coincident(g40,g35)
    c: Equal(g35, g36-g40) x5
    c: PointOnObject(g35,g41)
    c: PointOnObject(g36,g41)
    c: PointOnObject(g37,g41)
    c: PointOnObject(g38,g41)
    c: PointOnObject(g39,g41)
    c: PointOnObject(g40,g41)
    c: Coincident(g42,g43)
    c: Coincident(g43,g44)
    c: Coincident(g44,g45)
    c: Coincident(g45,g46)
    c: Coincident(g46,g47)
    c: Coincident(g47,g42)
    c: Equal(g42, g43-g47) x5
    c: PointOnObject(g42,g48)
    c: PointOnObject(g43,g48)
    c: PointOnObject(g44,g48)
    c: PointOnObject(g45,g48)
    c: PointOnObject(g46,g48)
    c: PointOnObject(g47,g48)
    c: Equal(g41,g48)
    c: Diameter(g41) = 7
    c: Vertical(g39)
    c: Vertical(g43)
    c: Distance(g-2,g39) = 1
    c: Symmetric(g38,g43,g-2)
    c: Distance(g41,g-1) = 7
FEATURE [Part::Extrusion] Extrude581  label="hex183"
  Base = -> Sketch590
  Dir = (0,-1,2e-16)
  DirMode = 2
  FaceMakerClass = Part::FaceMakerBullseye
  FaceMakerMode = 3
  LengthFwd = 10
  LengthRev = 0
  Placement = pos=(-8,0,-42) rot=(0,0,1;0rad)
  Solid = true
  Symmetric = false
FEATURE [Sketcher::SketchObject] Sketch591
  ArcFitTolerance = 1e-06
  FullyConstrained = true
  MakeInternals = false
  Placement = pos=(0,0,0) rot=(1,0,0;1.5708rad)
  sketch-geometry (49):
    g0: LineSegment StartX=1e-16 StartY=3.5 StartZ=0 EndX=-3.03109 EndY=1.75 EndZ=0
    g1: LineSegment StartX=-3.03109 StartY=1.75 StartZ=0 EndX=-3.03109 EndY=-1.75 EndZ=0
    g2: LineSegment StartX=-3.03109 StartY=-1.75 StartZ=0 EndX=-1e-16 EndY=-3.5 EndZ=0
    g3: LineSegment StartX=-1e-16 StartY=-3.5 StartZ=0 EndX=3.03109 EndY=-1.75 EndZ=0
    g4: LineSegment StartX=3.03109 StartY=-1.75 StartZ=0 EndX=3.03109 EndY=1.75 EndZ=0
    g5: LineSegment StartX=3.03109 StartY=1.75 StartZ=0 EndX=1e-16 EndY=3.5 EndZ=0
    g6: Circle [constr] CenterX=0 CenterY=0 CenterZ=0 NormalX=0 NormalY=0 NormalZ=1 AngleXU=0 Radius=3.5
    g7: LineSegment StartX=4.96892 StartY=-1.75002 StartZ=0 EndX=8.00002 EndY=-3.5 EndZ=0
    g8: LineSegment StartX=8.00002 StartY=-3.5 StartZ=0 EndX=11.0311 EndY=-1.74998 EndZ=0
    g9: LineSegment StartX=11.0311 StartY=-1.74998 StartZ=0 EndX=11.0311 EndY=1.75002 EndZ=0
    g10: LineSegment StartX=11.0311 StartY=1.75002 StartZ=0 EndX=7.99998 EndY=3.5 EndZ=0
    g11: LineSegment StartX=7.99998 StartY=3.5 StartZ=0 EndX=4.9689 EndY=1.74998 EndZ=0
    g12: LineSegment StartX=4.9689 StartY=1.74998 StartZ=0 EndX=4.96892 EndY=-1.75002 EndZ=0
    g13: Circle [constr] CenterX=8 CenterY=0 CenterZ=0 NormalX=0 NormalY=0 NormalZ=1 AngleXU=0 Radius=3.5
    g14: LineSegment StartX=4.03109 StartY=3.5 StartZ=0 EndX=7.06218 EndY=5.25 EndZ=0
    g15: LineSegment StartX=7.06218 StartY=5.25 StartZ=0 EndX=7.06218 EndY=8.75 EndZ=0
    g16: LineSegment StartX=7.06218 StartY=8.75 StartZ=0 EndX=4.03109 EndY=10.5 EndZ=0
    g17: LineSegment StartX=4.03109 StartY=10.5 StartZ=0 EndX=1 EndY=8.75 EndZ=0
    g18: LineSegment StartX=1 StartY=8.75 StartZ=0 EndX=1 EndY=5.25 EndZ=0
    g19: LineSegment StartX=1 StartY=5.25 StartZ=0 EndX=4.03109 EndY=3.5 EndZ=0
    g20: Circle [constr] CenterX=4.03109 CenterY=7 CenterZ=0 NormalX=0 NormalY=0 NormalZ=1 AngleXU=0 Radius=3.5
    g21: LineSegment StartX=-1 StartY=5.25 StartZ=0 EndX=-1 EndY=8.75 EndZ=0
    g22: LineSegment StartX=-1 StartY=8.75 StartZ=0 EndX=-4.03109 EndY=10.5 EndZ=0
    g23: LineSegment StartX=-4.03109 StartY=10.5 StartZ=0 EndX=-7.06218 EndY=8.75 EndZ=0
    g24: LineSegment StartX=-7.06218 StartY=8.75 StartZ=0 EndX=-7.06218 EndY=5.25 EndZ=0
    g25: LineSegment StartX=-7.06218 StartY=5.25 StartZ=0 EndX=-4.03109 EndY=3.5 EndZ=0
    g26: LineSegment StartX=-4.03109 StartY=3.5 StartZ=0 EndX=-1 EndY=5.25 EndZ=0
    g27: Circle [constr] CenterX=-4.03109 CenterY=7 CenterZ=0 NormalX=0 NormalY=0 NormalZ=1 AngleXU=0 Radius=3.5
    g28: LineSegment StartX=-4.96891 StartY=-1.75 StartZ=0 EndX=-4.96891 EndY=1.75 EndZ=0
    g29: LineSegment StartX=-4.96891 StartY=1.75 StartZ=0 EndX=-8 EndY=3.5 EndZ=0
    g30: LineSegment StartX=-8 StartY=3.5 StartZ=0 EndX=-11.0311 EndY=1.75 EndZ=0
    g31: LineSegment StartX=-11.0311 StartY=1.75 StartZ=0 EndX=-11.0311 EndY=-1.75 EndZ=0
    g32: LineSegment StartX=-11.0311 StartY=-1.75 StartZ=0 EndX=-8 EndY=-3.5 EndZ=0
    g33: LineSegment StartX=-8 StartY=-3.5 StartZ=0 EndX=-4.96891 EndY=-1.75 EndZ=0
    g34: Circle [constr] CenterX=-8 CenterY=0 CenterZ=0 NormalX=0 NormalY=0 NormalZ=1 AngleXU=0 Radius=3.5
    g35: LineSegment StartX=-4.03109 StartY=-3.5 StartZ=0 EndX=-7.06218 EndY=-5.25 EndZ=0
    g36: LineSegment StartX=-7.06218 StartY=-5.25 StartZ=0 EndX=-7.06218 EndY=-8.75 EndZ=0
    g37: LineSegment StartX=-7.06218 StartY=-8.75 StartZ=0 EndX=-4.03109 EndY=-10.5 EndZ=0
    g38: LineSegment StartX=-4.03109 StartY=-10.5 StartZ=0 EndX=-1 EndY=-8.75 EndZ=0
    g39: LineSegment StartX=-1 StartY=-8.75 StartZ=0 EndX=-1 EndY=-5.25 EndZ=0
    g40: LineSegment StartX=-1 StartY=-5.25 StartZ=0 EndX=-4.03109 EndY=-3.5 EndZ=0
    g41: Circle [constr] CenterX=-4.03109 CenterY=-7 CenterZ=0 NormalX=0 NormalY=0 NormalZ=1 AngleXU=0 Radius=3.5
    g42: LineSegment StartX=4.03109 StartY=-3.5 StartZ=0 EndX=1 EndY=-5.25 EndZ=0
    g43: LineSegment StartX=1 StartY=-5.25 StartZ=0 EndX=1 EndY=-8.75 EndZ=0
    g44: LineSegment StartX=1 StartY=-8.75 StartZ=0 EndX=4.03109 EndY=-10.5 EndZ=0
    g45: LineSegment StartX=4.03109 StartY=-10.5 StartZ=0 EndX=7.06218 EndY=-8.75 EndZ=0
    g46: LineSegment StartX=7.06218 StartY=-8.75 StartZ=0 EndX=7.06218 EndY=-5.25 EndZ=0
    g47: LineSegment StartX=7.06218 StartY=-5.25 StartZ=0 EndX=4.03109 EndY=-3.5 EndZ=0
    g48: Circle [constr] CenterX=4.03109 CenterY=-7 CenterZ=0 NormalX=0 NormalY=0 NormalZ=1 AngleXU=0 Radius=3.5
  constraints (117):
    c: Coincident(g0,g1)
    c: Coincident(g1,g2)
    c: Coincident(g2,g3)
    c: Coincident(g3,g4)
    c: Coincident(g4,g5)
    c: Coincident(g5,g0)
    c: Equal(g0, g1-g5) x5
    c: PointOnObject(g0,g6)
    c: PointOnObject(g1,g6)
    c: PointOnObject(g2,g6)
    c: PointOnObject(g3,g6)
    c: PointOnObject(g4,g6)
    c: PointOnObject(g5,g6)
    c: Coincident(g6,g-1)
    c: Diameter(g6) = 7
    c: PointOnObject(g0,g-2)
    c: Coincident(g7,g8)
    c: Coincident(g8,g9)
    c: Coincident(g9,g10)
    c: Coincident(g10,g11)
    c: Coincident(g11,g12)
    c: Coincident(g12,g7)
    c: Equal(g7, g8-g12) x5
    c: PointOnObject(g7,g13)
    c: PointOnObject(g8,g13)
    c: PointOnObject(g9,g13)
    c: PointOnObject(g10,g13)
    c: PointOnObject(g11,g13)
    c: PointOnObject(g12,g13)
    c: PointOnObject(g13,g-1)
    c: Diameter(g13) = 7
    c: Distance(g6,g13) = 8
    c: Horizontal(g0,g10)
    c: Coincident(g14,g15)
    c: Coincident(g15,g16)
    c: Coincident(g16,g17)
    c: Coincident(g17,g18)
    c: Coincident(g18,g19)
    c: Coincident(g19,g14)
    c: Equal(g14, g15-g19) x5
    c: PointOnObject(g14,g20)
    c: PointOnObject(g15,g20)
    c: PointOnObject(g16,g20)
    c: PointOnObject(g17,g20)
    c: PointOnObject(g18,g20)
    c: PointOnObject(g19,g20)
    c: Diameter(g20) = 7
    c: DistanceY(g-1,g20) = 7
    c: Vertical(g18)
    c: Distance(g17,g-2) = 1
    c: Coincident(g21,g22)
    c: Coincident(g22,g23)
    c: Coincident(g23,g24)
    c: Coincident(g24,g25)
    c: Coincident(g25,g26)
    c: Coincident(g26,g21)
    c: Equal(g21, g22-g26) x5
    c: PointOnObject(g21,g27)
    c: PointOnObject(g22,g27)
    c: PointOnObject(g23,g27)
    c: PointOnObject(g24,g27)
    c: PointOnObject(g25,g27)
    c: PointOnObject(g26,g27)
    c: Diameter(g27) = 7
    c: DistanceY(g-1,g27) = 7
    c: DistanceX(g21,g-1) = 1
    c: Vertical(g21)
    c: Coincident(g28,g29)
    c: Coincident(g29,g30)
    c: Coincident(g30,g31)
    c: Coincident(g31,g32)
    c: Coincident(g32,g33)
    c: Coincident(g33,g28)
    c: Equal(g28, g29-g33) x5
    c: PointOnObject(g28,g34)
    c: PointOnObject(g29,g34)
    c: PointOnObject(g30,g34)
    c: PointOnObject(g31,g34)
    c: PointOnObject(g32,g34)
    c: PointOnObject(g33,g34)
    c: PointOnObject(g34,g-1)
    c: Diameter(g34) = 7
    c: Vertical(g31)
    c: DistanceX(g34,g-1) = 8
    c: Coincident(g35,g36)
    c: Coincident(g36,g37)
    c: Coincident(g37,g38)
    c: Coincident(g38,g39)
    c: Coincident(g39,g40)
    c: Coincident(g40,g35)
    c: Equal(g35, g36-g40) x5
    c: PointOnObject(g35,g41)
    c: PointOnObject(g36,g41)
    c: PointOnObject(g37,g41)
    c: PointOnObject(g38,g41)
    c: PointOnObject(g39,g41)
    c: PointOnObject(g40,g41)
    c: Coincident(g42,g43)
    c: Coincident(g43,g44)
    c: Coincident(g44,g45)
    c: Coincident(g45,g46)
    c: Coincident(g46,g47)
    c: Coincident(g47,g42)
    c: Equal(g42, g43-g47) x5
    c: PointOnObject(g42,g48)
    c: PointOnObject(g43,g48)
    c: PointOnObject(g44,g48)
    c: PointOnObject(g45,g48)
    c: PointOnObject(g46,g48)
    c: PointOnObject(g47,g48)
    c: Equal(g41,g48)
    c: Diameter(g41) = 7
    c: Vertical(g39)
    c: Vertical(g43)
    c: Distance(g-2,g39) = 1
    c: Symmetric(g38,g43,g-2)
    c: Distance(g41,g-1) = 7
FEATURE [Part::Extrusion] Extrude582  label="hex184"
  Base = -> Sketch591
  Dir = (0,-1,2e-16)
  DirMode = 2
  FaceMakerClass = Part::FaceMakerBullseye
  FaceMakerMode = 3
  LengthFwd = 10
  LengthRev = 0
  Placement = pos=(32,0,-28) rot=(0,0,1;0rad)
  Solid = true
  Symmetric = false
FEATURE [Sketcher::SketchObject] Sketch592
  ArcFitTolerance = 1e-06
  FullyConstrained = true
  MakeInternals = false
  Placement = pos=(0,0,0) rot=(1,0,0;1.5708rad)
  sketch-geometry (49):
    g0: LineSegment StartX=1e-16 StartY=3.5 StartZ=0 EndX=-3.03109 EndY=1.75 EndZ=0
    g1: LineSegment StartX=-3.03109 StartY=1.75 StartZ=0 EndX=-3.03109 EndY=-1.75 EndZ=0
    g2: LineSegment StartX=-3.03109 StartY=-1.75 StartZ=0 EndX=-1e-16 EndY=-3.5 EndZ=0
    g3: LineSegment StartX=-1e-16 StartY=-3.5 StartZ=0 EndX=3.03109 EndY=-1.75 EndZ=0
    g4: LineSegment StartX=3.03109 StartY=-1.75 StartZ=0 EndX=3.03109 EndY=1.75 EndZ=0
    g5: LineSegment StartX=3.03109 StartY=1.75 StartZ=0 EndX=1e-16 EndY=3.5 EndZ=0
    g6: Circle [constr] CenterX=0 CenterY=0 CenterZ=0 NormalX=0 NormalY=0 NormalZ=1 AngleXU=0 Radius=3.5
    g7: LineSegment StartX=4.96892 StartY=-1.75002 StartZ=0 EndX=8.00002 EndY=-3.5 EndZ=0
    g8: LineSegment StartX=8.00002 StartY=-3.5 StartZ=0 EndX=11.0311 EndY=-1.74998 EndZ=0
    g9: LineSegment StartX=11.0311 StartY=-1.74998 StartZ=0 EndX=11.0311 EndY=1.75002 EndZ=0
    g10: LineSegment StartX=11.0311 StartY=1.75002 StartZ=0 EndX=7.99998 EndY=3.5 EndZ=0
    g11: LineSegment StartX=7.99998 StartY=3.5 StartZ=0 EndX=4.9689 EndY=1.74998 EndZ=0
    g12: LineSegment StartX=4.9689 StartY=1.74998 StartZ=0 EndX=4.96892 EndY=-1.75002 EndZ=0
    g13: Circle [constr] CenterX=8 CenterY=0 CenterZ=0 NormalX=0 NormalY=0 NormalZ=1 AngleXU=0 Radius=3.5
    g14: LineSegment StartX=4.03109 StartY=3.5 StartZ=0 EndX=7.06218 EndY=5.25 EndZ=0
    g15: LineSegment StartX=7.06218 StartY=5.25 StartZ=0 EndX=7.06218 EndY=8.75 EndZ=0
    g16: LineSegment StartX=7.06218 StartY=8.75 StartZ=0 EndX=4.03109 EndY=10.5 EndZ=0
    g17: LineSegment StartX=4.03109 StartY=10.5 StartZ=0 EndX=1 EndY=8.75 EndZ=0
    g18: LineSegment StartX=1 StartY=8.75 StartZ=0 EndX=1 EndY=5.25 EndZ=0
    g19: LineSegment StartX=1 StartY=5.25 StartZ=0 EndX=4.03109 EndY=3.5 EndZ=0
    g20: Circle [constr] CenterX=4.03109 CenterY=7 CenterZ=0 NormalX=0 NormalY=0 NormalZ=1 AngleXU=0 Radius=3.5
    g21: LineSegment StartX=-1 StartY=5.25 StartZ=0 EndX=-1 EndY=8.75 EndZ=0
    g22: LineSegment StartX=-1 StartY=8.75 StartZ=0 EndX=-4.03109 EndY=10.5 EndZ=0
    g23: LineSegment StartX=-4.03109 StartY=10.5 StartZ=0 EndX=-7.06218 EndY=8.75 EndZ=0
    g24: LineSegment StartX=-7.06218 StartY=8.75 StartZ=0 EndX=-7.06218 EndY=5.25 EndZ=0
    g25: LineSegment StartX=-7.06218 StartY=5.25 StartZ=0 EndX=-4.03109 EndY=3.5 EndZ=0
    g26: LineSegment StartX=-4.03109 StartY=3.5 StartZ=0 EndX=-1 EndY=5.25 EndZ=0
    g27: Circle [constr] CenterX=-4.03109 CenterY=7 CenterZ=0 NormalX=0 NormalY=0 NormalZ=1 AngleXU=0 Radius=3.5
    g28: LineSegment StartX=-4.96891 StartY=-1.75 StartZ=0 EndX=-4.96891 EndY=1.75 EndZ=0
    g29: LineSegment StartX=-4.96891 StartY=1.75 StartZ=0 EndX=-8 EndY=3.5 EndZ=0
    g30: LineSegment StartX=-8 StartY=3.5 StartZ=0 EndX=-11.0311 EndY=1.75 EndZ=0
    g31: LineSegment StartX=-11.0311 StartY=1.75 StartZ=0 EndX=-11.0311 EndY=-1.75 EndZ=0
    g32: LineSegment StartX=-11.0311 StartY=-1.75 StartZ=0 EndX=-8 EndY=-3.5 EndZ=0
    g33: LineSegment StartX=-8 StartY=-3.5 StartZ=0 EndX=-4.96891 EndY=-1.75 EndZ=0
    g34: Circle [constr] CenterX=-8 CenterY=0 CenterZ=0 NormalX=0 NormalY=0 NormalZ=1 AngleXU=0 Radius=3.5
    g35: LineSegment StartX=-4.03109 StartY=-3.5 StartZ=0 EndX=-7.06218 EndY=-5.25 EndZ=0
    g36: LineSegment StartX=-7.06218 StartY=-5.25 StartZ=0 EndX=-7.06218 EndY=-8.75 EndZ=0
    g37: LineSegment StartX=-7.06218 StartY=-8.75 StartZ=0 EndX=-4.03109 EndY=-10.5 EndZ=0
    g38: LineSegment StartX=-4.03109 StartY=-10.5 StartZ=0 EndX=-1 EndY=-8.75 EndZ=0
    g39: LineSegment StartX=-1 StartY=-8.75 StartZ=0 EndX=-1 EndY=-5.25 EndZ=0
    g40: LineSegment StartX=-1 StartY=-5.25 StartZ=0 EndX=-4.03109 EndY=-3.5 EndZ=0
    g41: Circle [constr] CenterX=-4.03109 CenterY=-7 CenterZ=0 NormalX=0 NormalY=0 NormalZ=1 AngleXU=0 Radius=3.5
    g42: LineSegment StartX=4.03109 StartY=-3.5 StartZ=0 EndX=1 EndY=-5.25 EndZ=0
    g43: LineSegment StartX=1 StartY=-5.25 StartZ=0 EndX=1 EndY=-8.75 EndZ=0
    g44: LineSegment StartX=1 StartY=-8.75 StartZ=0 EndX=4.03109 EndY=-10.5 EndZ=0
    g45: LineSegment StartX=4.03109 StartY=-10.5 StartZ=0 EndX=7.06218 EndY=-8.75 EndZ=0
    g46: LineSegment StartX=7.06218 StartY=-8.75 StartZ=0 EndX=7.06218 EndY=-5.25 EndZ=0
    g47: LineSegment StartX=7.06218 StartY=-5.25 StartZ=0 EndX=4.03109 EndY=-3.5 EndZ=0
    g48: Circle [constr] CenterX=4.03109 CenterY=-7 CenterZ=0 NormalX=0 NormalY=0 NormalZ=1 AngleXU=0 Radius=3.5
  constraints (117):
    c: Coincident(g0,g1)
    c: Coincident(g1,g2)
    c: Coincident(g2,g3)
    c: Coincident(g3,g4)
    c: Coincident(g4,g5)
    c: Coincident(g5,g0)
    c: Equal(g0, g1-g5) x5
    c: PointOnObject(g0,g6)
    c: PointOnObject(g1,g6)
    c: PointOnObject(g2,g6)
    c: PointOnObject(g3,g6)
    c: PointOnObject(g4,g6)
    c: PointOnObject(g5,g6)
    c: Coincident(g6,g-1)
    c: Diameter(g6) = 7
    c: PointOnObject(g0,g-2)
    c: Coincident(g7,g8)
    c: Coincident(g8,g9)
    c: Coincident(g9,g10)
    c: Coincident(g10,g11)
    c: Coincident(g11,g12)
    c: Coincident(g12,g7)
    c: Equal(g7, g8-g12) x5
    c: PointOnObject(g7,g13)
    c: PointOnObject(g8,g13)
    c: PointOnObject(g9,g13)
    c: PointOnObject(g10,g13)
    c: PointOnObject(g11,g13)
    c: PointOnObject(g12,g13)
    c: PointOnObject(g13,g-1)
    c: Diameter(g13) = 7
    c: Distance(g6,g13) = 8
    c: Horizontal(g0,g10)
    c: Coincident(g14,g15)
    c: Coincident(g15,g16)
    c: Coincident(g16,g17)
    c: Coincident(g17,g18)
    c: Coincident(g18,g19)
    c: Coincident(g19,g14)
    c: Equal(g14, g15-g19) x5
    c: PointOnObject(g14,g20)
    c: PointOnObject(g15,g20)
    c: PointOnObject(g16,g20)
    c: PointOnObject(g17,g20)
    c: PointOnObject(g18,g20)
    c: PointOnObject(g19,g20)
    c: Diameter(g20) = 7
    c: DistanceY(g-1,g20) = 7
    c: Vertical(g18)
    c: Distance(g17,g-2) = 1
    c: Coincident(g21,g22)
    c: Coincident(g22,g23)
    c: Coincident(g23,g24)
    c: Coincident(g24,g25)
    c: Coincident(g25,g26)
    c: Coincident(g26,g21)
    c: Equal(g21, g22-g26) x5
    c: PointOnObject(g21,g27)
    c: PointOnObject(g22,g27)
    c: PointOnObject(g23,g27)
    c: PointOnObject(g24,g27)
    c: PointOnObject(g25,g27)
    c: PointOnObject(g26,g27)
    c: Diameter(g27) = 7
    c: DistanceY(g-1,g27) = 7
    c: DistanceX(g21,g-1) = 1
    c: Vertical(g21)
    c: Coincident(g28,g29)
    c: Coincident(g29,g30)
    c: Coincident(g30,g31)
    c: Coincident(g31,g32)
    c: Coincident(g32,g33)
    c: Coincident(g33,g28)
    c: Equal(g28, g29-g33) x5
    c: PointOnObject(g28,g34)
    c: PointOnObject(g29,g34)
    c: PointOnObject(g30,g34)
    c: PointOnObject(g31,g34)
    c: PointOnObject(g32,g34)
    c: PointOnObject(g33,g34)
    c: PointOnObject(g34,g-1)
    c: Diameter(g34) = 7
    c: Vertical(g31)
    c: DistanceX(g34,g-1) = 8
    c: Coincident(g35,g36)
    c: Coincident(g36,g37)
    c: Coincident(g37,g38)
    c: Coincident(g38,g39)
    c: Coincident(g39,g40)
    c: Coincident(g40,g35)
    c: Equal(g35, g36-g40) x5
    c: PointOnObject(g35,g41)
    c: PointOnObject(g36,g41)
    c: PointOnObject(g37,g41)
    c: PointOnObject(g38,g41)
    c: PointOnObject(g39,g41)
    c: PointOnObject(g40,g41)
    c: Coincident(g42,g43)
    c: Coincident(g43,g44)
    c: Coincident(g44,g45)
    c: Coincident(g45,g46)
    c: Coincident(g46,g47)
    c: Coincident(g47,g42)
    c: Equal(g42, g43-g47) x5
    c: PointOnObject(g42,g48)
    c: PointOnObject(g43,g48)
    c: PointOnObject(g44,g48)
    c: PointOnObject(g45,g48)
    c: PointOnObject(g46,g48)
    c: PointOnObject(g47,g48)
    c: Equal(g41,g48)
    c: Diameter(g41) = 7
    c: Vertical(g39)
    c: Vertical(g43)
    c: Distance(g-2,g39) = 1
    c: Symmetric(g38,g43,g-2)
    c: Distance(g41,g-1) = 7
FEATURE [Part::Extrusion] Extrude583  label="hex185"
  Base = -> Sketch592
  Dir = (0,-1,2e-16)
  DirMode = 2
  FaceMakerClass = Part::FaceMakerBullseye
  FaceMakerMode = 3
  LengthFwd = 10
  LengthRev = 0
  Placement = pos=(36,0,-7) rot=(0,0,1;0rad)
  Solid = true
  Symmetric = false
FEATURE [Sketcher::SketchObject] Sketch593
  ArcFitTolerance = 1e-06
  FullyConstrained = true
  MakeInternals = false
  Placement = pos=(0,0,0) rot=(1,0,0;1.5708rad)
  sketch-geometry (49):
    g0: LineSegment StartX=1e-16 StartY=3.5 StartZ=0 EndX=-3.03109 EndY=1.75 EndZ=0
    g1: LineSegment StartX=-3.03109 StartY=1.75 StartZ=0 EndX=-3.03109 EndY=-1.75 EndZ=0
    g2: LineSegment StartX=-3.03109 StartY=-1.75 StartZ=0 EndX=-1e-16 EndY=-3.5 EndZ=0
    g3: LineSegment StartX=-1e-16 StartY=-3.5 StartZ=0 EndX=3.03109 EndY=-1.75 EndZ=0
    g4: LineSegment StartX=3.03109 StartY=-1.75 StartZ=0 EndX=3.03109 EndY=1.75 EndZ=0
    g5: LineSegment StartX=3.03109 StartY=1.75 StartZ=0 EndX=1e-16 EndY=3.5 EndZ=0
    g6: Circle [constr] CenterX=0 CenterY=0 CenterZ=0 NormalX=0 NormalY=0 NormalZ=1 AngleXU=0 Radius=3.5
    g7: LineSegment StartX=4.96892 StartY=-1.75002 StartZ=0 EndX=8.00002 EndY=-3.5 EndZ=0
    g8: LineSegment StartX=8.00002 StartY=-3.5 StartZ=0 EndX=11.0311 EndY=-1.74998 EndZ=0
    g9: LineSegment StartX=11.0311 StartY=-1.74998 StartZ=0 EndX=11.0311 EndY=1.75002 EndZ=0
    g10: LineSegment StartX=11.0311 StartY=1.75002 StartZ=0 EndX=7.99998 EndY=3.5 EndZ=0
    g11: LineSegment StartX=7.99998 StartY=3.5 StartZ=0 EndX=4.9689 EndY=1.74998 EndZ=0
    g12: LineSegment StartX=4.9689 StartY=1.74998 StartZ=0 EndX=4.96892 EndY=-1.75002 EndZ=0
    g13: Circle [constr] CenterX=8 CenterY=0 CenterZ=0 NormalX=0 NormalY=0 NormalZ=1 AngleXU=0 Radius=3.5
    g14: LineSegment StartX=4.03109 StartY=3.5 StartZ=0 EndX=7.06218 EndY=5.25 EndZ=0
    g15: LineSegment StartX=7.06218 StartY=5.25 StartZ=0 EndX=7.06218 EndY=8.75 EndZ=0
    g16: LineSegment StartX=7.06218 StartY=8.75 StartZ=0 EndX=4.03109 EndY=10.5 EndZ=0
    g17: LineSegment StartX=4.03109 StartY=10.5 StartZ=0 EndX=1 EndY=8.75 EndZ=0
    g18: LineSegment StartX=1 StartY=8.75 StartZ=0 EndX=1 EndY=5.25 EndZ=0
    g19: LineSegment StartX=1 StartY=5.25 StartZ=0 EndX=4.03109 EndY=3.5 EndZ=0
    g20: Circle [constr] CenterX=4.03109 CenterY=7 CenterZ=0 NormalX=0 NormalY=0 NormalZ=1 AngleXU=0 Radius=3.5
    g21: LineSegment StartX=-1 StartY=5.25 StartZ=0 EndX=-1 EndY=8.75 EndZ=0
    g22: LineSegment StartX=-1 StartY=8.75 StartZ=0 EndX=-4.03109 EndY=10.5 EndZ=0
    g23: LineSegment StartX=-4.03109 StartY=10.5 StartZ=0 EndX=-7.06218 EndY=8.75 EndZ=0
    g24: LineSegment StartX=-7.06218 StartY=8.75 StartZ=0 EndX=-7.06218 EndY=5.25 EndZ=0
    g25: LineSegment StartX=-7.06218 StartY=5.25 StartZ=0 EndX=-4.03109 EndY=3.5 EndZ=0
    g26: LineSegment StartX=-4.03109 StartY=3.5 StartZ=0 EndX=-1 EndY=5.25 EndZ=0
    g27: Circle [constr] CenterX=-4.03109 CenterY=7 CenterZ=0 NormalX=0 NormalY=0 NormalZ=1 AngleXU=0 Radius=3.5
    g28: LineSegment StartX=-4.96891 StartY=-1.75 StartZ=0 EndX=-4.96891 EndY=1.75 EndZ=0
    g29: LineSegment StartX=-4.96891 StartY=1.75 StartZ=0 EndX=-8 EndY=3.5 EndZ=0
    g30: LineSegment StartX=-8 StartY=3.5 StartZ=0 EndX=-11.0311 EndY=1.75 EndZ=0
    g31: LineSegment StartX=-11.0311 StartY=1.75 StartZ=0 EndX=-11.0311 EndY=-1.75 EndZ=0
    g32: LineSegment StartX=-11.0311 StartY=-1.75 StartZ=0 EndX=-8 EndY=-3.5 EndZ=0
    g33: LineSegment StartX=-8 StartY=-3.5 StartZ=0 EndX=-4.96891 EndY=-1.75 EndZ=0
    g34: Circle [constr] CenterX=-8 CenterY=0 CenterZ=0 NormalX=0 NormalY=0 NormalZ=1 AngleXU=0 Radius=3.5
    g35: LineSegment StartX=-4.03109 StartY=-3.5 StartZ=0 EndX=-7.06218 EndY=-5.25 EndZ=0
    g36: LineSegment StartX=-7.06218 StartY=-5.25 StartZ=0 EndX=-7.06218 EndY=-8.75 EndZ=0
    g37: LineSegment StartX=-7.06218 StartY=-8.75 StartZ=0 EndX=-4.03109 EndY=-10.5 EndZ=0
    g38: LineSegment StartX=-4.03109 StartY=-10.5 StartZ=0 EndX=-1 EndY=-8.75 EndZ=0
    g39: LineSegment StartX=-1 StartY=-8.75 StartZ=0 EndX=-1 EndY=-5.25 EndZ=0
    g40: LineSegment StartX=-1 StartY=-5.25 StartZ=0 EndX=-4.03109 EndY=-3.5 EndZ=0
    g41: Circle [constr] CenterX=-4.03109 CenterY=-7 CenterZ=0 NormalX=0 NormalY=0 NormalZ=1 AngleXU=0 Radius=3.5
    g42: LineSegment StartX=4.03109 StartY=-3.5 StartZ=0 EndX=1 EndY=-5.25 EndZ=0
    g43: LineSegment StartX=1 StartY=-5.25 StartZ=0 EndX=1 EndY=-8.75 EndZ=0
    g44: LineSegment StartX=1 StartY=-8.75 StartZ=0 EndX=4.03109 EndY=-10.5 EndZ=0
    g45: LineSegment StartX=4.03109 StartY=-10.5 StartZ=0 EndX=7.06218 EndY=-8.75 EndZ=0
    g46: LineSegment StartX=7.06218 StartY=-8.75 StartZ=0 EndX=7.06218 EndY=-5.25 EndZ=0
    g47: LineSegment StartX=7.06218 StartY=-5.25 StartZ=0 EndX=4.03109 EndY=-3.5 EndZ=0
    g48: Circle [constr] CenterX=4.03109 CenterY=-7 CenterZ=0 NormalX=0 NormalY=0 NormalZ=1 AngleXU=0 Radius=3.5
  constraints (117):
    c: Coincident(g0,g1)
    c: Coincident(g1,g2)
    c: Coincident(g2,g3)
    c: Coincident(g3,g4)
    c: Coincident(g4,g5)
    c: Coincident(g5,g0)
    c: Equal(g0, g1-g5) x5
    c: PointOnObject(g0,g6)
    c: PointOnObject(g1,g6)
    c: PointOnObject(g2,g6)
    c: PointOnObject(g3,g6)
    c: PointOnObject(g4,g6)
    c: PointOnObject(g5,g6)
    c: Coincident(g6,g-1)
    c: Diameter(g6) = 7
    c: PointOnObject(g0,g-2)
    c: Coincident(g7,g8)
    c: Coincident(g8,g9)
    c: Coincident(g9,g10)
    c: Coincident(g10,g11)
    c: Coincident(g11,g12)
    c: Coincident(g12,g7)
    c: Equal(g7, g8-g12) x5
    c: PointOnObject(g7,g13)
    c: PointOnObject(g8,g13)
    c: PointOnObject(g9,g13)
    c: PointOnObject(g10,g13)
    c: PointOnObject(g11,g13)
    c: PointOnObject(g12,g13)
    c: PointOnObject(g13,g-1)
    c: Diameter(g13) = 7
    c: Distance(g6,g13) = 8
    c: Horizontal(g0,g10)
    c: Coincident(g14,g15)
    c: Coincident(g15,g16)
    c: Coincident(g16,g17)
    c: Coincident(g17,g18)
    c: Coincident(g18,g19)
    c: Coincident(g19,g14)
    c: Equal(g14, g15-g19) x5
    c: PointOnObject(g14,g20)
    c: PointOnObject(g15,g20)
    c: PointOnObject(g16,g20)
    c: PointOnObject(g17,g20)
    c: PointOnObject(g18,g20)
    c: PointOnObject(g19,g20)
    c: Diameter(g20) = 7
    c: DistanceY(g-1,g20) = 7
    c: Vertical(g18)
    c: Distance(g17,g-2) = 1
    c: Coincident(g21,g22)
    c: Coincident(g22,g23)
    c: Coincident(g23,g24)
    c: Coincident(g24,g25)
    c: Coincident(g25,g26)
    c: Coincident(g26,g21)
    c: Equal(g21, g22-g26) x5
    c: PointOnObject(g21,g27)
    c: PointOnObject(g22,g27)
    c: PointOnObject(g23,g27)
    c: PointOnObject(g24,g27)
    c: PointOnObject(g25,g27)
    c: PointOnObject(g26,g27)
    c: Diameter(g27) = 7
    c: DistanceY(g-1,g27) = 7
    c: DistanceX(g21,g-1) = 1
    c: Vertical(g21)
    c: Coincident(g28,g29)
    c: Coincident(g29,g30)
    c: Coincident(g30,g31)
    c: Coincident(g31,g32)
    c: Coincident(g32,g33)
    c: Coincident(g33,g28)
    c: Equal(g28, g29-g33) x5
    c: PointOnObject(g28,g34)
    c: PointOnObject(g29,g34)
    c: PointOnObject(g30,g34)
    c: PointOnObject(g31,g34)
    c: PointOnObject(g32,g34)
    c: PointOnObject(g33,g34)
    c: PointOnObject(g34,g-1)
    c: Diameter(g34) = 7
    c: Vertical(g31)
    c: DistanceX(g34,g-1) = 8
    c: Coincident(g35,g36)
    c: Coincident(g36,g37)
    c: Coincident(g37,g38)
    c: Coincident(g38,g39)
    c: Coincident(g39,g40)
    c: Coincident(g40,g35)
    c: Equal(g35, g36-g40) x5
    c: PointOnObject(g35,g41)
    c: PointOnObject(g36,g41)
    c: PointOnObject(g37,g41)
    c: PointOnObject(g38,g41)
    c: PointOnObject(g39,g41)
    c: PointOnObject(g40,g41)
    c: Coincident(g42,g43)
    c: Coincident(g43,g44)
    c: Coincident(g44,g45)
    c: Coincident(g45,g46)
    c: Coincident(g46,g47)
    c: Coincident(g47,g42)
    c: Equal(g42, g43-g47) x5
    c: PointOnObject(g42,g48)
    c: PointOnObject(g43,g48)
    c: PointOnObject(g44,g48)
    c: PointOnObject(g45,g48)
    c: PointOnObject(g46,g48)
    c: PointOnObject(g47,g48)
    c: Equal(g41,g48)
    c: Diameter(g41) = 7
    c: Vertical(g39)
    c: Vertical(g43)
    c: Distance(g-2,g39) = 1
    c: Symmetric(g38,g43,g-2)
    c: Distance(g41,g-1) = 7
FEATURE [Part::Extrusion] Extrude584  label="hex186"
  Base = -> Sketch593
  Dir = (0,-1,2e-16)
  DirMode = 2
  FaceMakerClass = Part::FaceMakerBullseye
  FaceMakerMode = 3
  LengthFwd = 10
  LengthRev = 0
  Placement = pos=(56,0,0) rot=(0,0,1;0rad)
  Solid = true
  Symmetric = false
FEATURE [Sketcher::SketchObject] Sketch594
  ArcFitTolerance = 1e-06
  FullyConstrained = true
  MakeInternals = false
  Placement = pos=(0,0,0) rot=(1,0,0;1.5708rad)
  sketch-geometry (49):
    g0: LineSegment StartX=1e-16 StartY=3.5 StartZ=0 EndX=-3.03109 EndY=1.75 EndZ=0
    g1: LineSegment StartX=-3.03109 StartY=1.75 StartZ=0 EndX=-3.03109 EndY=-1.75 EndZ=0
    g2: LineSegment StartX=-3.03109 StartY=-1.75 StartZ=0 EndX=-1e-16 EndY=-3.5 EndZ=0
    g3: LineSegment StartX=-1e-16 StartY=-3.5 StartZ=0 EndX=3.03109 EndY=-1.75 EndZ=0
    g4: LineSegment StartX=3.03109 StartY=-1.75 StartZ=0 EndX=3.03109 EndY=1.75 EndZ=0
    g5: LineSegment StartX=3.03109 StartY=1.75 StartZ=0 EndX=1e-16 EndY=3.5 EndZ=0
    g6: Circle [constr] CenterX=0 CenterY=0 CenterZ=0 NormalX=0 NormalY=0 NormalZ=1 AngleXU=0 Radius=3.5
    g7: LineSegment StartX=4.96892 StartY=-1.75002 StartZ=0 EndX=8.00002 EndY=-3.5 EndZ=0
    g8: LineSegment StartX=8.00002 StartY=-3.5 StartZ=0 EndX=11.0311 EndY=-1.74998 EndZ=0
    g9: LineSegment StartX=11.0311 StartY=-1.74998 StartZ=0 EndX=11.0311 EndY=1.75002 EndZ=0
    g10: LineSegment StartX=11.0311 StartY=1.75002 StartZ=0 EndX=7.99998 EndY=3.5 EndZ=0
    g11: LineSegment StartX=7.99998 StartY=3.5 StartZ=0 EndX=4.9689 EndY=1.74998 EndZ=0
    g12: LineSegment StartX=4.9689 StartY=1.74998 StartZ=0 EndX=4.96892 EndY=-1.75002 EndZ=0
    g13: Circle [constr] CenterX=8 CenterY=0 CenterZ=0 NormalX=0 NormalY=0 NormalZ=1 AngleXU=0 Radius=3.5
    g14: LineSegment StartX=4.03109 StartY=3.5 StartZ=0 EndX=7.06218 EndY=5.25 EndZ=0
    g15: LineSegment StartX=7.06218 StartY=5.25 StartZ=0 EndX=7.06218 EndY=8.75 EndZ=0
    g16: LineSegment StartX=7.06218 StartY=8.75 StartZ=0 EndX=4.03109 EndY=10.5 EndZ=0
    g17: LineSegment StartX=4.03109 StartY=10.5 StartZ=0 EndX=1 EndY=8.75 EndZ=0
    g18: LineSegment StartX=1 StartY=8.75 StartZ=0 EndX=1 EndY=5.25 EndZ=0
    g19: LineSegment StartX=1 StartY=5.25 StartZ=0 EndX=4.03109 EndY=3.5 EndZ=0
    g20: Circle [constr] CenterX=4.03109 CenterY=7 CenterZ=0 NormalX=0 NormalY=0 NormalZ=1 AngleXU=0 Radius=3.5
    g21: LineSegment StartX=-1 StartY=5.25 StartZ=0 EndX=-1 EndY=8.75 EndZ=0
    g22: LineSegment StartX=-1 StartY=8.75 StartZ=0 EndX=-4.03109 EndY=10.5 EndZ=0
    g23: LineSegment StartX=-4.03109 StartY=10.5 StartZ=0 EndX=-7.06218 EndY=8.75 EndZ=0
    g24: LineSegment StartX=-7.06218 StartY=8.75 StartZ=0 EndX=-7.06218 EndY=5.25 EndZ=0
    g25: LineSegment StartX=-7.06218 StartY=5.25 StartZ=0 EndX=-4.03109 EndY=3.5 EndZ=0
    g26: LineSegment StartX=-4.03109 StartY=3.5 StartZ=0 EndX=-1 EndY=5.25 EndZ=0
    g27: Circle [constr] CenterX=-4.03109 CenterY=7 CenterZ=0 NormalX=0 NormalY=0 NormalZ=1 AngleXU=0 Radius=3.5
    g28: LineSegment StartX=-4.96891 StartY=-1.75 StartZ=0 EndX=-4.96891 EndY=1.75 EndZ=0
    g29: LineSegment StartX=-4.96891 StartY=1.75 StartZ=0 EndX=-8 EndY=3.5 EndZ=0
    g30: LineSegment StartX=-8 StartY=3.5 StartZ=0 EndX=-11.0311 EndY=1.75 EndZ=0
    g31: LineSegment StartX=-11.0311 StartY=1.75 StartZ=0 EndX=-11.0311 EndY=-1.75 EndZ=0
    g32: LineSegment StartX=-11.0311 StartY=-1.75 StartZ=0 EndX=-8 EndY=-3.5 EndZ=0
    g33: LineSegment StartX=-8 StartY=-3.5 StartZ=0 EndX=-4.96891 EndY=-1.75 EndZ=0
    g34: Circle [constr] CenterX=-8 CenterY=0 CenterZ=0 NormalX=0 NormalY=0 NormalZ=1 AngleXU=0 Radius=3.5
    g35: LineSegment StartX=-4.03109 StartY=-3.5 StartZ=0 EndX=-7.06218 EndY=-5.25 EndZ=0
    g36: LineSegment StartX=-7.06218 StartY=-5.25 StartZ=0 EndX=-7.06218 EndY=-8.75 EndZ=0
    g37: LineSegment StartX=-7.06218 StartY=-8.75 StartZ=0 EndX=-4.03109 EndY=-10.5 EndZ=0
    g38: LineSegment StartX=-4.03109 StartY=-10.5 StartZ=0 EndX=-1 EndY=-8.75 EndZ=0
    g39: LineSegment StartX=-1 StartY=-8.75 StartZ=0 EndX=-1 EndY=-5.25 EndZ=0
    g40: LineSegment StartX=-1 StartY=-5.25 StartZ=0 EndX=-4.03109 EndY=-3.5 EndZ=0
    g41: Circle [constr] CenterX=-4.03109 CenterY=-7 CenterZ=0 NormalX=0 NormalY=0 NormalZ=1 AngleXU=0 Radius=3.5
    g42: LineSegment StartX=4.03109 StartY=-3.5 StartZ=0 EndX=1 EndY=-5.25 EndZ=0
    g43: LineSegment StartX=1 StartY=-5.25 StartZ=0 EndX=1 EndY=-8.75 EndZ=0
    g44: LineSegment StartX=1 StartY=-8.75 StartZ=0 EndX=4.03109 EndY=-10.5 EndZ=0
    g45: LineSegment StartX=4.03109 StartY=-10.5 StartZ=0 EndX=7.06218 EndY=-8.75 EndZ=0
    g46: LineSegment StartX=7.06218 StartY=-8.75 StartZ=0 EndX=7.06218 EndY=-5.25 EndZ=0
    g47: LineSegment StartX=7.06218 StartY=-5.25 StartZ=0 EndX=4.03109 EndY=-3.5 EndZ=0
    g48: Circle [constr] CenterX=4.03109 CenterY=-7 CenterZ=0 NormalX=0 NormalY=0 NormalZ=1 AngleXU=0 Radius=3.5
  constraints (117):
    c: Coincident(g0,g1)
    c: Coincident(g1,g2)
    c: Coincident(g2,g3)
    c: Coincident(g3,g4)
    c: Coincident(g4,g5)
    c: Coincident(g5,g0)
    c: Equal(g0, g1-g5) x5
    c: PointOnObject(g0,g6)
    c: PointOnObject(g1,g6)
    c: PointOnObject(g2,g6)
    c: PointOnObject(g3,g6)
    c: PointOnObject(g4,g6)
    c: PointOnObject(g5,g6)
    c: Coincident(g6,g-1)
    c: Diameter(g6) = 7
    c: PointOnObject(g0,g-2)
    c: Coincident(g7,g8)
    c: Coincident(g8,g9)
    c: Coincident(g9,g10)
    c: Coincident(g10,g11)
    c: Coincident(g11,g12)
    c: Coincident(g12,g7)
    c: Equal(g7, g8-g12) x5
    c: PointOnObject(g7,g13)
    c: PointOnObject(g8,g13)
    c: PointOnObject(g9,g13)
    c: PointOnObject(g10,g13)
    c: PointOnObject(g11,g13)
    c: PointOnObject(g12,g13)
    c: PointOnObject(g13,g-1)
    c: Diameter(g13) = 7
    c: Distance(g6,g13) = 8
    c: Horizontal(g0,g10)
    c: Coincident(g14,g15)
    c: Coincident(g15,g16)
    c: Coincident(g16,g17)
    c: Coincident(g17,g18)
    c: Coincident(g18,g19)
    c: Coincident(g19,g14)
    c: Equal(g14, g15-g19) x5
    c: PointOnObject(g14,g20)
    c: PointOnObject(g15,g20)
    c: PointOnObject(g16,g20)
    c: PointOnObject(g17,g20)
    c: PointOnObject(g18,g20)
    c: PointOnObject(g19,g20)
    c: Diameter(g20) = 7
    c: DistanceY(g-1,g20) = 7
    c: Vertical(g18)
    c: Distance(g17,g-2) = 1
    c: Coincident(g21,g22)
    c: Coincident(g22,g23)
    c: Coincident(g23,g24)
    c: Coincident(g24,g25)
    c: Coincident(g25,g26)
    c: Coincident(g26,g21)
    c: Equal(g21, g22-g26) x5
    c: PointOnObject(g21,g27)
    c: PointOnObject(g22,g27)
    c: PointOnObject(g23,g27)
    c: PointOnObject(g24,g27)
    c: PointOnObject(g25,g27)
    c: PointOnObject(g26,g27)
    c: Diameter(g27) = 7
    c: DistanceY(g-1,g27) = 7
    c: DistanceX(g21,g-1) = 1
    c: Vertical(g21)
    c: Coincident(g28,g29)
    c: Coincident(g29,g30)
    c: Coincident(g30,g31)
    c: Coincident(g31,g32)
    c: Coincident(g32,g33)
    c: Coincident(g33,g28)
    c: Equal(g28, g29-g33) x5
    c: PointOnObject(g28,g34)
    c: PointOnObject(g29,g34)
    c: PointOnObject(g30,g34)
    c: PointOnObject(g31,g34)
    c: PointOnObject(g32,g34)
    c: PointOnObject(g33,g34)
    c: PointOnObject(g34,g-1)
    c: Diameter(g34) = 7
    c: Vertical(g31)
    c: DistanceX(g34,g-1) = 8
    c: Coincident(g35,g36)
    c: Coincident(g36,g37)
    c: Coincident(g37,g38)
    c: Coincident(g38,g39)
    c: Coincident(g39,g40)
    c: Coincident(g40,g35)
    c: Equal(g35, g36-g40) x5
    c: PointOnObject(g35,g41)
    c: PointOnObject(g36,g41)
    c: PointOnObject(g37,g41)
    c: PointOnObject(g38,g41)
    c: PointOnObject(g39,g41)
    c: PointOnObject(g40,g41)
    c: Coincident(g42,g43)
    c: Coincident(g43,g44)
    c: Coincident(g44,g45)
    c: Coincident(g45,g46)
    c: Coincident(g46,g47)
    c: Coincident(g47,g42)
    c: Equal(g42, g43-g47) x5
    c: PointOnObject(g42,g48)
    c: PointOnObject(g43,g48)
    c: PointOnObject(g44,g48)
    c: PointOnObject(g45,g48)
    c: PointOnObject(g46,g48)
    c: PointOnObject(g47,g48)
    c: Equal(g41,g48)
    c: Diameter(g41) = 7
    c: Vertical(g39)
    c: Vertical(g43)
    c: Distance(g-2,g39) = 1
    c: Symmetric(g38,g43,g-2)
    c: Distance(g41,g-1) = 7
FEATURE [Part::Extrusion] Extrude585  label="hex187"
  Base = -> Sketch594
  Dir = (0,-1,2e-16)
  DirMode = 2
  FaceMakerClass = Part::FaceMakerBullseye
  FaceMakerMode = 3
  LengthFwd = 10
  LengthRev = 0
  Placement = pos=(52,0,-21) rot=(0,0,1;0rad)
  Solid = true
  Symmetric = false
FEATURE [Sketcher::SketchObject] Sketch595
  ArcFitTolerance = 1e-06
  FullyConstrained = true
  MakeInternals = false
  Placement = pos=(0,0,0) rot=(1,0,0;1.5708rad)
  sketch-geometry (49):
    g0: LineSegment StartX=1e-16 StartY=3.5 StartZ=0 EndX=-3.03109 EndY=1.75 EndZ=0
    g1: LineSegment StartX=-3.03109 StartY=1.75 StartZ=0 EndX=-3.03109 EndY=-1.75 EndZ=0
    g2: LineSegment StartX=-3.03109 StartY=-1.75 StartZ=0 EndX=-1e-16 EndY=-3.5 EndZ=0
    g3: LineSegment StartX=-1e-16 StartY=-3.5 StartZ=0 EndX=3.03109 EndY=-1.75 EndZ=0
    g4: LineSegment StartX=3.03109 StartY=-1.75 StartZ=0 EndX=3.03109 EndY=1.75 EndZ=0
    g5: LineSegment StartX=3.03109 StartY=1.75 StartZ=0 EndX=1e-16 EndY=3.5 EndZ=0
    g6: Circle [constr] CenterX=0 CenterY=0 CenterZ=0 NormalX=0 NormalY=0 NormalZ=1 AngleXU=0 Radius=3.5
    g7: LineSegment StartX=4.96892 StartY=-1.75002 StartZ=0 EndX=8.00002 EndY=-3.5 EndZ=0
    g8: LineSegment StartX=8.00002 StartY=-3.5 StartZ=0 EndX=11.0311 EndY=-1.74998 EndZ=0
    g9: LineSegment StartX=11.0311 StartY=-1.74998 StartZ=0 EndX=11.0311 EndY=1.75002 EndZ=0
    g10: LineSegment StartX=11.0311 StartY=1.75002 StartZ=0 EndX=7.99998 EndY=3.5 EndZ=0
    g11: LineSegment StartX=7.99998 StartY=3.5 StartZ=0 EndX=4.9689 EndY=1.74998 EndZ=0
    g12: LineSegment StartX=4.9689 StartY=1.74998 StartZ=0 EndX=4.96892 EndY=-1.75002 EndZ=0
    g13: Circle [constr] CenterX=8 CenterY=0 CenterZ=0 NormalX=0 NormalY=0 NormalZ=1 AngleXU=0 Radius=3.5
    g14: LineSegment StartX=4.03109 StartY=3.5 StartZ=0 EndX=7.06218 EndY=5.25 EndZ=0
    g15: LineSegment StartX=7.06218 StartY=5.25 StartZ=0 EndX=7.06218 EndY=8.75 EndZ=0
    g16: LineSegment StartX=7.06218 StartY=8.75 StartZ=0 EndX=4.03109 EndY=10.5 EndZ=0
    g17: LineSegment StartX=4.03109 StartY=10.5 StartZ=0 EndX=1 EndY=8.75 EndZ=0
    g18: LineSegment StartX=1 StartY=8.75 StartZ=0 EndX=1 EndY=5.25 EndZ=0
    g19: LineSegment StartX=1 StartY=5.25 StartZ=0 EndX=4.03109 EndY=3.5 EndZ=0
    g20: Circle [constr] CenterX=4.03109 CenterY=7 CenterZ=0 NormalX=0 NormalY=0 NormalZ=1 AngleXU=0 Radius=3.5
    g21: LineSegment StartX=-1 StartY=5.25 StartZ=0 EndX=-1 EndY=8.75 EndZ=0
    g22: LineSegment StartX=-1 StartY=8.75 StartZ=0 EndX=-4.03109 EndY=10.5 EndZ=0
    g23: LineSegment StartX=-4.03109 StartY=10.5 StartZ=0 EndX=-7.06218 EndY=8.75 EndZ=0
    g24: LineSegment StartX=-7.06218 StartY=8.75 StartZ=0 EndX=-7.06218 EndY=5.25 EndZ=0
    g25: LineSegment StartX=-7.06218 StartY=5.25 StartZ=0 EndX=-4.03109 EndY=3.5 EndZ=0
    g26: LineSegment StartX=-4.03109 StartY=3.5 StartZ=0 EndX=-1 EndY=5.25 EndZ=0
    g27: Circle [constr] CenterX=-4.03109 CenterY=7 CenterZ=0 NormalX=0 NormalY=0 NormalZ=1 AngleXU=0 Radius=3.5
    g28: LineSegment StartX=-4.96891 StartY=-1.75 StartZ=0 EndX=-4.96891 EndY=1.75 EndZ=0
    g29: LineSegment StartX=-4.96891 StartY=1.75 StartZ=0 EndX=-8 EndY=3.5 EndZ=0
    g30: LineSegment StartX=-8 StartY=3.5 StartZ=0 EndX=-11.0311 EndY=1.75 EndZ=0
    g31: LineSegment StartX=-11.0311 StartY=1.75 StartZ=0 EndX=-11.0311 EndY=-1.75 EndZ=0
    g32: LineSegment StartX=-11.0311 StartY=-1.75 StartZ=0 EndX=-8 EndY=-3.5 EndZ=0
    g33: LineSegment StartX=-8 StartY=-3.5 StartZ=0 EndX=-4.96891 EndY=-1.75 EndZ=0
    g34: Circle [constr] CenterX=-8 CenterY=0 CenterZ=0 NormalX=0 NormalY=0 NormalZ=1 AngleXU=0 Radius=3.5
    g35: LineSegment StartX=-4.03109 StartY=-3.5 StartZ=0 EndX=-7.06218 EndY=-5.25 EndZ=0
    g36: LineSegment StartX=-7.06218 StartY=-5.25 StartZ=0 EndX=-7.06218 EndY=-8.75 EndZ=0
    g37: LineSegment StartX=-7.06218 StartY=-8.75 StartZ=0 EndX=-4.03109 EndY=-10.5 EndZ=0
    g38: LineSegment StartX=-4.03109 StartY=-10.5 StartZ=0 EndX=-1 EndY=-8.75 EndZ=0
    g39: LineSegment StartX=-1 StartY=-8.75 StartZ=0 EndX=-1 EndY=-5.25 EndZ=0
    g40: LineSegment StartX=-1 StartY=-5.25 StartZ=0 EndX=-4.03109 EndY=-3.5 EndZ=0
    g41: Circle [constr] CenterX=-4.03109 CenterY=-7 CenterZ=0 NormalX=0 NormalY=0 NormalZ=1 AngleXU=0 Radius=3.5
    g42: LineSegment StartX=4.03109 StartY=-3.5 StartZ=0 EndX=1 EndY=-5.25 EndZ=0
    g43: LineSegment StartX=1 StartY=-5.25 StartZ=0 EndX=1 EndY=-8.75 EndZ=0
    g44: LineSegment StartX=1 StartY=-8.75 StartZ=0 EndX=4.03109 EndY=-10.5 EndZ=0
    g45: LineSegment StartX=4.03109 StartY=-10.5 StartZ=0 EndX=7.06218 EndY=-8.75 EndZ=0
    g46: LineSegment StartX=7.06218 StartY=-8.75 StartZ=0 EndX=7.06218 EndY=-5.25 EndZ=0
    g47: LineSegment StartX=7.06218 StartY=-5.25 StartZ=0 EndX=4.03109 EndY=-3.5 EndZ=0
    g48: Circle [constr] CenterX=4.03109 CenterY=-7 CenterZ=0 NormalX=0 NormalY=0 NormalZ=1 AngleXU=0 Radius=3.5
  constraints (117):
    c: Coincident(g0,g1)
    c: Coincident(g1,g2)
    c: Coincident(g2,g3)
    c: Coincident(g3,g4)
    c: Coincident(g4,g5)
    c: Coincident(g5,g0)
    c: Equal(g0, g1-g5) x5
    c: PointOnObject(g0,g6)
    c: PointOnObject(g1,g6)
    c: PointOnObject(g2,g6)
    c: PointOnObject(g3,g6)
    c: PointOnObject(g4,g6)
    c: PointOnObject(g5,g6)
    c: Coincident(g6,g-1)
    c: Diameter(g6) = 7
    c: PointOnObject(g0,g-2)
    c: Coincident(g7,g8)
    c: Coincident(g8,g9)
    c: Coincident(g9,g10)
    c: Coincident(g10,g11)
    c: Coincident(g11,g12)
    c: Coincident(g12,g7)
    c: Equal(g7, g8-g12) x5
    c: PointOnObject(g7,g13)
    c: PointOnObject(g8,g13)
    c: PointOnObject(g9,g13)
    c: PointOnObject(g10,g13)
    c: PointOnObject(g11,g13)
    c: PointOnObject(g12,g13)
    c: PointOnObject(g13,g-1)
    c: Diameter(g13) = 7
    c: Distance(g6,g13) = 8
    c: Horizontal(g0,g10)
    c: Coincident(g14,g15)
    c: Coincident(g15,g16)
    c: Coincident(g16,g17)
    c: Coincident(g17,g18)
    c: Coincident(g18,g19)
    c: Coincident(g19,g14)
    c: Equal(g14, g15-g19) x5
    c: PointOnObject(g14,g20)
    c: PointOnObject(g15,g20)
    c: PointOnObject(g16,g20)
    c: PointOnObject(g17,g20)
    c: PointOnObject(g18,g20)
    c: PointOnObject(g19,g20)
    c: Diameter(g20) = 7
    c: DistanceY(g-1,g20) = 7
    c: Vertical(g18)
    c: Distance(g17,g-2) = 1
    c: Coincident(g21,g22)
    c: Coincident(g22,g23)
    c: Coincident(g23,g24)
    c: Coincident(g24,g25)
    c: Coincident(g25,g26)
    c: Coincident(g26,g21)
    c: Equal(g21, g22-g26) x5
    c: PointOnObject(g21,g27)
    c: PointOnObject(g22,g27)
    c: PointOnObject(g23,g27)
    c: PointOnObject(g24,g27)
    c: PointOnObject(g25,g27)
    c: PointOnObject(g26,g27)
    c: Diameter(g27) = 7
    c: DistanceY(g-1,g27) = 7
    c: DistanceX(g21,g-1) = 1
    c: Vertical(g21)
    c: Coincident(g28,g29)
    c: Coincident(g29,g30)
    c: Coincident(g30,g31)
    c: Coincident(g31,g32)
    c: Coincident(g32,g33)
    c: Coincident(g33,g28)
    c: Equal(g28, g29-g33) x5
    c: PointOnObject(g28,g34)
    c: PointOnObject(g29,g34)
    c: PointOnObject(g30,g34)
    c: PointOnObject(g31,g34)
    c: PointOnObject(g32,g34)
    c: PointOnObject(g33,g34)
    c: PointOnObject(g34,g-1)
    c: Diameter(g34) = 7
    c: Vertical(g31)
    c: DistanceX(g34,g-1) = 8
    c: Coincident(g35,g36)
    c: Coincident(g36,g37)
    c: Coincident(g37,g38)
    c: Coincident(g38,g39)
    c: Coincident(g39,g40)
    c: Coincident(g40,g35)
    c: Equal(g35, g36-g40) x5
    c: PointOnObject(g35,g41)
    c: PointOnObject(g36,g41)
    c: PointOnObject(g37,g41)
    c: PointOnObject(g38,g41)
    c: PointOnObject(g39,g41)
    c: PointOnObject(g40,g41)
    c: Coincident(g42,g43)
    c: Coincident(g43,g44)
    c: Coincident(g44,g45)
    c: Coincident(g45,g46)
    c: Coincident(g46,g47)
    c: Coincident(g47,g42)
    c: Equal(g42, g43-g47) x5
    c: PointOnObject(g42,g48)
    c: PointOnObject(g43,g48)
    c: PointOnObject(g44,g48)
    c: PointOnObject(g45,g48)
    c: PointOnObject(g46,g48)
    c: PointOnObject(g47,g48)
    c: Equal(g41,g48)
    c: Diameter(g41) = 7
    c: Vertical(g39)
    c: Vertical(g43)
    c: Distance(g-2,g39) = 1
    c: Symmetric(g38,g43,g-2)
    c: Distance(g41,g-1) = 7
FEATURE [Part::Extrusion] Extrude586  label="hex188"
  Base = -> Sketch595
  Dir = (0,-1,2e-16)
  DirMode = 2
  FaceMakerClass = Part::FaceMakerBullseye
  FaceMakerMode = 3
  LengthFwd = 10
  LengthRev = 0
  Placement = pos=(-56,0,0) rot=(0,0,1;0rad)
  Solid = true
  Symmetric = false
FEATURE [Sketcher::SketchObject] Sketch596
  ArcFitTolerance = 1e-06
  FullyConstrained = true
  MakeInternals = false
  Placement = pos=(0,0,0) rot=(1,0,0;1.5708rad)
  sketch-geometry (49):
    g0: LineSegment StartX=1e-16 StartY=3.5 StartZ=0 EndX=-3.03109 EndY=1.75 EndZ=0
    g1: LineSegment StartX=-3.03109 StartY=1.75 StartZ=0 EndX=-3.03109 EndY=-1.75 EndZ=0
    g2: LineSegment StartX=-3.03109 StartY=-1.75 StartZ=0 EndX=-1e-16 EndY=-3.5 EndZ=0
    g3: LineSegment StartX=-1e-16 StartY=-3.5 StartZ=0 EndX=3.03109 EndY=-1.75 EndZ=0
    g4: LineSegment StartX=3.03109 StartY=-1.75 StartZ=0 EndX=3.03109 EndY=1.75 EndZ=0
    g5: LineSegment StartX=3.03109 StartY=1.75 StartZ=0 EndX=1e-16 EndY=3.5 EndZ=0
    g6: Circle [constr] CenterX=0 CenterY=0 CenterZ=0 NormalX=0 NormalY=0 NormalZ=1 AngleXU=0 Radius=3.5
    g7: LineSegment StartX=4.96892 StartY=-1.75002 StartZ=0 EndX=8.00002 EndY=-3.5 EndZ=0
    g8: LineSegment StartX=8.00002 StartY=-3.5 StartZ=0 EndX=11.0311 EndY=-1.74998 EndZ=0
    g9: LineSegment StartX=11.0311 StartY=-1.74998 StartZ=0 EndX=11.0311 EndY=1.75002 EndZ=0
    g10: LineSegment StartX=11.0311 StartY=1.75002 StartZ=0 EndX=7.99998 EndY=3.5 EndZ=0
    g11: LineSegment StartX=7.99998 StartY=3.5 StartZ=0 EndX=4.9689 EndY=1.74998 EndZ=0
    g12: LineSegment StartX=4.9689 StartY=1.74998 StartZ=0 EndX=4.96892 EndY=-1.75002 EndZ=0
    g13: Circle [constr] CenterX=8 CenterY=0 CenterZ=0 NormalX=0 NormalY=0 NormalZ=1 AngleXU=0 Radius=3.5
    g14: LineSegment StartX=4.03109 StartY=3.5 StartZ=0 EndX=7.06218 EndY=5.25 EndZ=0
    g15: LineSegment StartX=7.06218 StartY=5.25 StartZ=0 EndX=7.06218 EndY=8.75 EndZ=0
    g16: LineSegment StartX=7.06218 StartY=8.75 StartZ=0 EndX=4.03109 EndY=10.5 EndZ=0
    g17: LineSegment StartX=4.03109 StartY=10.5 StartZ=0 EndX=1 EndY=8.75 EndZ=0
    g18: LineSegment StartX=1 StartY=8.75 StartZ=0 EndX=1 EndY=5.25 EndZ=0
    g19: LineSegment StartX=1 StartY=5.25 StartZ=0 EndX=4.03109 EndY=3.5 EndZ=0
    g20: Circle [constr] CenterX=4.03109 CenterY=7 CenterZ=0 NormalX=0 NormalY=0 NormalZ=1 AngleXU=0 Radius=3.5
    g21: LineSegment StartX=-1 StartY=5.25 StartZ=0 EndX=-1 EndY=8.75 EndZ=0
    g22: LineSegment StartX=-1 StartY=8.75 StartZ=0 EndX=-4.03109 EndY=10.5 EndZ=0
    g23: LineSegment StartX=-4.03109 StartY=10.5 StartZ=0 EndX=-7.06218 EndY=8.75 EndZ=0
    g24: LineSegment StartX=-7.06218 StartY=8.75 StartZ=0 EndX=-7.06218 EndY=5.25 EndZ=0
    g25: LineSegment StartX=-7.06218 StartY=5.25 StartZ=0 EndX=-4.03109 EndY=3.5 EndZ=0
    g26: LineSegment StartX=-4.03109 StartY=3.5 StartZ=0 EndX=-1 EndY=5.25 EndZ=0
    g27: Circle [constr] CenterX=-4.03109 CenterY=7 CenterZ=0 NormalX=0 NormalY=0 NormalZ=1 AngleXU=0 Radius=3.5
    g28: LineSegment StartX=-4.96891 StartY=-1.75 StartZ=0 EndX=-4.96891 EndY=1.75 EndZ=0
    g29: LineSegment StartX=-4.96891 StartY=1.75 StartZ=0 EndX=-8 EndY=3.5 EndZ=0
    g30: LineSegment StartX=-8 StartY=3.5 StartZ=0 EndX=-11.0311 EndY=1.75 EndZ=0
    g31: LineSegment StartX=-11.0311 StartY=1.75 StartZ=0 EndX=-11.0311 EndY=-1.75 EndZ=0
    g32: LineSegment StartX=-11.0311 StartY=-1.75 StartZ=0 EndX=-8 EndY=-3.5 EndZ=0
    g33: LineSegment StartX=-8 StartY=-3.5 StartZ=0 EndX=-4.96891 EndY=-1.75 EndZ=0
    g34: Circle [constr] CenterX=-8 CenterY=0 CenterZ=0 NormalX=0 NormalY=0 NormalZ=1 AngleXU=0 Radius=3.5
    g35: LineSegment StartX=-4.03109 StartY=-3.5 StartZ=0 EndX=-7.06218 EndY=-5.25 EndZ=0
    g36: LineSegment StartX=-7.06218 StartY=-5.25 StartZ=0 EndX=-7.06218 EndY=-8.75 EndZ=0
    g37: LineSegment StartX=-7.06218 StartY=-8.75 StartZ=0 EndX=-4.03109 EndY=-10.5 EndZ=0
    g38: LineSegment StartX=-4.03109 StartY=-10.5 StartZ=0 EndX=-1 EndY=-8.75 EndZ=0
    g39: LineSegment StartX=-1 StartY=-8.75 StartZ=0 EndX=-1 EndY=-5.25 EndZ=0
    g40: LineSegment StartX=-1 StartY=-5.25 StartZ=0 EndX=-4.03109 EndY=-3.5 EndZ=0
    g41: Circle [constr] CenterX=-4.03109 CenterY=-7 CenterZ=0 NormalX=0 NormalY=0 NormalZ=1 AngleXU=0 Radius=3.5
    g42: LineSegment StartX=4.03109 StartY=-3.5 StartZ=0 EndX=1 EndY=-5.25 EndZ=0
    g43: LineSegment StartX=1 StartY=-5.25 StartZ=0 EndX=1 EndY=-8.75 EndZ=0
    g44: LineSegment StartX=1 StartY=-8.75 StartZ=0 EndX=4.03109 EndY=-10.5 EndZ=0
    g45: LineSegment StartX=4.03109 StartY=-10.5 StartZ=0 EndX=7.06218 EndY=-8.75 EndZ=0
    g46: LineSegment StartX=7.06218 StartY=-8.75 StartZ=0 EndX=7.06218 EndY=-5.25 EndZ=0
    g47: LineSegment StartX=7.06218 StartY=-5.25 StartZ=0 EndX=4.03109 EndY=-3.5 EndZ=0
    g48: Circle [constr] CenterX=4.03109 CenterY=-7 CenterZ=0 NormalX=0 NormalY=0 NormalZ=1 AngleXU=0 Radius=3.5
  constraints (117):
    c: Coincident(g0,g1)
    c: Coincident(g1,g2)
    c: Coincident(g2,g3)
    c: Coincident(g3,g4)
    c: Coincident(g4,g5)
    c: Coincident(g5,g0)
    c: Equal(g0, g1-g5) x5
    c: PointOnObject(g0,g6)
    c: PointOnObject(g1,g6)
    c: PointOnObject(g2,g6)
    c: PointOnObject(g3,g6)
    c: PointOnObject(g4,g6)
    c: PointOnObject(g5,g6)
    c: Coincident(g6,g-1)
    c: Diameter(g6) = 7
    c: PointOnObject(g0,g-2)
    c: Coincident(g7,g8)
    c: Coincident(g8,g9)
    c: Coincident(g9,g10)
    c: Coincident(g10,g11)
    c: Coincident(g11,g12)
    c: Coincident(g12,g7)
    c: Equal(g7, g8-g12) x5
    c: PointOnObject(g7,g13)
    c: PointOnObject(g8,g13)
    c: PointOnObject(g9,g13)
    c: PointOnObject(g10,g13)
    c: PointOnObject(g11,g13)
    c: PointOnObject(g12,g13)
    c: PointOnObject(g13,g-1)
    c: Diameter(g13) = 7
    c: Distance(g6,g13) = 8
    c: Horizontal(g0,g10)
    c: Coincident(g14,g15)
    c: Coincident(g15,g16)
    c: Coincident(g16,g17)
    c: Coincident(g17,g18)
    c: Coincident(g18,g19)
    c: Coincident(g19,g14)
    c: Equal(g14, g15-g19) x5
    c: PointOnObject(g14,g20)
    c: PointOnObject(g15,g20)
    c: PointOnObject(g16,g20)
    c: PointOnObject(g17,g20)
    c: PointOnObject(g18,g20)
    c: PointOnObject(g19,g20)
    c: Diameter(g20) = 7
    c: DistanceY(g-1,g20) = 7
    c: Vertical(g18)
    c: Distance(g17,g-2) = 1
    c: Coincident(g21,g22)
    c: Coincident(g22,g23)
    c: Coincident(g23,g24)
    c: Coincident(g24,g25)
    c: Coincident(g25,g26)
    c: Coincident(g26,g21)
    c: Equal(g21, g22-g26) x5
    c: PointOnObject(g21,g27)
    c: PointOnObject(g22,g27)
    c: PointOnObject(g23,g27)
    c: PointOnObject(g24,g27)
    c: PointOnObject(g25,g27)
    c: PointOnObject(g26,g27)
    c: Diameter(g27) = 7
    c: DistanceY(g-1,g27) = 7
    c: DistanceX(g21,g-1) = 1
    c: Vertical(g21)
    c: Coincident(g28,g29)
    c: Coincident(g29,g30)
    c: Coincident(g30,g31)
    c: Coincident(g31,g32)
    c: Coincident(g32,g33)
    c: Coincident(g33,g28)
    c: Equal(g28, g29-g33) x5
    c: PointOnObject(g28,g34)
    c: PointOnObject(g29,g34)
    c: PointOnObject(g30,g34)
    c: PointOnObject(g31,g34)
    c: PointOnObject(g32,g34)
    c: PointOnObject(g33,g34)
    c: PointOnObject(g34,g-1)
    c: Diameter(g34) = 7
    c: Vertical(g31)
    c: DistanceX(g34,g-1) = 8
    c: Coincident(g35,g36)
    c: Coincident(g36,g37)
    c: Coincident(g37,g38)
    c: Coincident(g38,g39)
    c: Coincident(g39,g40)
    c: Coincident(g40,g35)
    c: Equal(g35, g36-g40) x5
    c: PointOnObject(g35,g41)
    c: PointOnObject(g36,g41)
    c: PointOnObject(g37,g41)
    c: PointOnObject(g38,g41)
    c: PointOnObject(g39,g41)
    c: PointOnObject(g40,g41)
    c: Coincident(g42,g43)
    c: Coincident(g43,g44)
    c: Coincident(g44,g45)
    c: Coincident(g45,g46)
    c: Coincident(g46,g47)
    c: Coincident(g47,g42)
    c: Equal(g42, g43-g47) x5
    c: PointOnObject(g42,g48)
    c: PointOnObject(g43,g48)
    c: PointOnObject(g44,g48)
    c: PointOnObject(g45,g48)
    c: PointOnObject(g46,g48)
    c: PointOnObject(g47,g48)
    c: Equal(g41,g48)
    c: Diameter(g41) = 7
    c: Vertical(g39)
    c: Vertical(g43)
    c: Distance(g-2,g39) = 1
    c: Symmetric(g38,g43,g-2)
    c: Distance(g41,g-1) = 7
FEATURE [Part::Extrusion] Extrude587  label="hex189"
  Base = -> Sketch596
  Dir = (0,-1,2e-16)
  DirMode = 2
  FaceMakerClass = Part::FaceMakerBullseye
  FaceMakerMode = 3
  LengthFwd = 10
  LengthRev = 0
  Placement = pos=(-52,0,21) rot=(0,0,1;0rad)
  Solid = true
  Symmetric = false
FEATURE [Sketcher::SketchObject] Sketch597
  ArcFitTolerance = 1e-06
  FullyConstrained = true
  MakeInternals = false
  Placement = pos=(0,0,0) rot=(1,0,0;1.5708rad)
  sketch-geometry (49):
    g0: LineSegment StartX=1e-16 StartY=3.5 StartZ=0 EndX=-3.03109 EndY=1.75 EndZ=0
    g1: LineSegment StartX=-3.03109 StartY=1.75 StartZ=0 EndX=-3.03109 EndY=-1.75 EndZ=0
    g2: LineSegment StartX=-3.03109 StartY=-1.75 StartZ=0 EndX=-1e-16 EndY=-3.5 EndZ=0
    g3: LineSegment StartX=-1e-16 StartY=-3.5 StartZ=0 EndX=3.03109 EndY=-1.75 EndZ=0
    g4: LineSegment StartX=3.03109 StartY=-1.75 StartZ=0 EndX=3.03109 EndY=1.75 EndZ=0
    g5: LineSegment StartX=3.03109 StartY=1.75 StartZ=0 EndX=1e-16 EndY=3.5 EndZ=0
    g6: Circle [constr] CenterX=0 CenterY=0 CenterZ=0 NormalX=0 NormalY=0 NormalZ=1 AngleXU=0 Radius=3.5
    g7: LineSegment StartX=4.96892 StartY=-1.75002 StartZ=0 EndX=8.00002 EndY=-3.5 EndZ=0
    g8: LineSegment StartX=8.00002 StartY=-3.5 StartZ=0 EndX=11.0311 EndY=-1.74998 EndZ=0
    g9: LineSegment StartX=11.0311 StartY=-1.74998 StartZ=0 EndX=11.0311 EndY=1.75002 EndZ=0
    g10: LineSegment StartX=11.0311 StartY=1.75002 StartZ=0 EndX=7.99998 EndY=3.5 EndZ=0
    g11: LineSegment StartX=7.99998 StartY=3.5 StartZ=0 EndX=4.9689 EndY=1.74998 EndZ=0
    g12: LineSegment StartX=4.9689 StartY=1.74998 StartZ=0 EndX=4.96892 EndY=-1.75002 EndZ=0
    g13: Circle [constr] CenterX=8 CenterY=0 CenterZ=0 NormalX=0 NormalY=0 NormalZ=1 AngleXU=0 Radius=3.5
    g14: LineSegment StartX=4.03109 StartY=3.5 StartZ=0 EndX=7.06218 EndY=5.25 EndZ=0
    g15: LineSegment StartX=7.06218 StartY=5.25 StartZ=0 EndX=7.06218 EndY=8.75 EndZ=0
    g16: LineSegment StartX=7.06218 StartY=8.75 StartZ=0 EndX=4.03109 EndY=10.5 EndZ=0
    g17: LineSegment StartX=4.03109 StartY=10.5 StartZ=0 EndX=1 EndY=8.75 EndZ=0
    g18: LineSegment StartX=1 StartY=8.75 StartZ=0 EndX=1 EndY=5.25 EndZ=0
    g19: LineSegment StartX=1 StartY=5.25 StartZ=0 EndX=4.03109 EndY=3.5 EndZ=0
    g20: Circle [constr] CenterX=4.03109 CenterY=7 CenterZ=0 NormalX=0 NormalY=0 NormalZ=1 AngleXU=0 Radius=3.5
    g21: LineSegment StartX=-1 StartY=5.25 StartZ=0 EndX=-1 EndY=8.75 EndZ=0
    g22: LineSegment StartX=-1 StartY=8.75 StartZ=0 EndX=-4.03109 EndY=10.5 EndZ=0
    g23: LineSegment StartX=-4.03109 StartY=10.5 StartZ=0 EndX=-7.06218 EndY=8.75 EndZ=0
    g24: LineSegment StartX=-7.06218 StartY=8.75 StartZ=0 EndX=-7.06218 EndY=5.25 EndZ=0
    g25: LineSegment StartX=-7.06218 StartY=5.25 StartZ=0 EndX=-4.03109 EndY=3.5 EndZ=0
    g26: LineSegment StartX=-4.03109 StartY=3.5 StartZ=0 EndX=-1 EndY=5.25 EndZ=0
    g27: Circle [constr] CenterX=-4.03109 CenterY=7 CenterZ=0 NormalX=0 NormalY=0 NormalZ=1 AngleXU=0 Radius=3.5
    g28: LineSegment StartX=-4.96891 StartY=-1.75 StartZ=0 EndX=-4.96891 EndY=1.75 EndZ=0
    g29: LineSegment StartX=-4.96891 StartY=1.75 StartZ=0 EndX=-8 EndY=3.5 EndZ=0
    g30: LineSegment StartX=-8 StartY=3.5 StartZ=0 EndX=-11.0311 EndY=1.75 EndZ=0
    g31: LineSegment StartX=-11.0311 StartY=1.75 StartZ=0 EndX=-11.0311 EndY=-1.75 EndZ=0
    g32: LineSegment StartX=-11.0311 StartY=-1.75 StartZ=0 EndX=-8 EndY=-3.5 EndZ=0
    g33: LineSegment StartX=-8 StartY=-3.5 StartZ=0 EndX=-4.96891 EndY=-1.75 EndZ=0
    g34: Circle [constr] CenterX=-8 CenterY=0 CenterZ=0 NormalX=0 NormalY=0 NormalZ=1 AngleXU=0 Radius=3.5
    g35: LineSegment StartX=-4.03109 StartY=-3.5 StartZ=0 EndX=-7.06218 EndY=-5.25 EndZ=0
    g36: LineSegment StartX=-7.06218 StartY=-5.25 StartZ=0 EndX=-7.06218 EndY=-8.75 EndZ=0
    g37: LineSegment StartX=-7.06218 StartY=-8.75 StartZ=0 EndX=-4.03109 EndY=-10.5 EndZ=0
    g38: LineSegment StartX=-4.03109 StartY=-10.5 StartZ=0 EndX=-1 EndY=-8.75 EndZ=0
    g39: LineSegment StartX=-1 StartY=-8.75 StartZ=0 EndX=-1 EndY=-5.25 EndZ=0
    g40: LineSegment StartX=-1 StartY=-5.25 StartZ=0 EndX=-4.03109 EndY=-3.5 EndZ=0
    g41: Circle [constr] CenterX=-4.03109 CenterY=-7 CenterZ=0 NormalX=0 NormalY=0 NormalZ=1 AngleXU=0 Radius=3.5
    g42: LineSegment StartX=4.03109 StartY=-3.5 StartZ=0 EndX=1 EndY=-5.25 EndZ=0
    g43: LineSegment StartX=1 StartY=-5.25 StartZ=0 EndX=1 EndY=-8.75 EndZ=0
    g44: LineSegment StartX=1 StartY=-8.75 StartZ=0 EndX=4.03109 EndY=-10.5 EndZ=0
    g45: LineSegment StartX=4.03109 StartY=-10.5 StartZ=0 EndX=7.06218 EndY=-8.75 EndZ=0
    g46: LineSegment StartX=7.06218 StartY=-8.75 StartZ=0 EndX=7.06218 EndY=-5.25 EndZ=0
    g47: LineSegment StartX=7.06218 StartY=-5.25 StartZ=0 EndX=4.03109 EndY=-3.5 EndZ=0
    g48: Circle [constr] CenterX=4.03109 CenterY=-7 CenterZ=0 NormalX=0 NormalY=0 NormalZ=1 AngleXU=0 Radius=3.5
  constraints (117):
    c: Coincident(g0,g1)
    c: Coincident(g1,g2)
    c: Coincident(g2,g3)
    c: Coincident(g3,g4)
    c: Coincident(g4,g5)
    c: Coincident(g5,g0)
    c: Equal(g0, g1-g5) x5
    c: PointOnObject(g0,g6)
    c: PointOnObject(g1,g6)
    c: PointOnObject(g2,g6)
    c: PointOnObject(g3,g6)
    c: PointOnObject(g4,g6)
    c: PointOnObject(g5,g6)
    c: Coincident(g6,g-1)
    c: Diameter(g6) = 7
    c: PointOnObject(g0,g-2)
    c: Coincident(g7,g8)
    c: Coincident(g8,g9)
    c: Coincident(g9,g10)
    c: Coincident(g10,g11)
    c: Coincident(g11,g12)
    c: Coincident(g12,g7)
    c: Equal(g7, g8-g12) x5
    c: PointOnObject(g7,g13)
    c: PointOnObject(g8,g13)
    c: PointOnObject(g9,g13)
    c: PointOnObject(g10,g13)
    c: PointOnObject(g11,g13)
    c: PointOnObject(g12,g13)
    c: PointOnObject(g13,g-1)
    c: Diameter(g13) = 7
    c: Distance(g6,g13) = 8
    c: Horizontal(g0,g10)
    c: Coincident(g14,g15)
    c: Coincident(g15,g16)
    c: Coincident(g16,g17)
    c: Coincident(g17,g18)
    c: Coincident(g18,g19)
    c: Coincident(g19,g14)
    c: Equal(g14, g15-g19) x5
    c: PointOnObject(g14,g20)
    c: PointOnObject(g15,g20)
    c: PointOnObject(g16,g20)
    c: PointOnObject(g17,g20)
    c: PointOnObject(g18,g20)
    c: PointOnObject(g19,g20)
    c: Diameter(g20) = 7
    c: DistanceY(g-1,g20) = 7
    c: Vertical(g18)
    c: Distance(g17,g-2) = 1
    c: Coincident(g21,g22)
    c: Coincident(g22,g23)
    c: Coincident(g23,g24)
    c: Coincident(g24,g25)
    c: Coincident(g25,g26)
    c: Coincident(g26,g21)
    c: Equal(g21, g22-g26) x5
    c: PointOnObject(g21,g27)
    c: PointOnObject(g22,g27)
    c: PointOnObject(g23,g27)
    c: PointOnObject(g24,g27)
    c: PointOnObject(g25,g27)
    c: PointOnObject(g26,g27)
    c: Diameter(g27) = 7
    c: DistanceY(g-1,g27) = 7
    c: DistanceX(g21,g-1) = 1
    c: Vertical(g21)
    c: Coincident(g28,g29)
    c: Coincident(g29,g30)
    c: Coincident(g30,g31)
    c: Coincident(g31,g32)
    c: Coincident(g32,g33)
    c: Coincident(g33,g28)
    c: Equal(g28, g29-g33) x5
    c: PointOnObject(g28,g34)
    c: PointOnObject(g29,g34)
    c: PointOnObject(g30,g34)
    c: PointOnObject(g31,g34)
    c: PointOnObject(g32,g34)
    c: PointOnObject(g33,g34)
    c: PointOnObject(g34,g-1)
    c: Diameter(g34) = 7
    c: Vertical(g31)
    c: DistanceX(g34,g-1) = 8
    c: Coincident(g35,g36)
    c: Coincident(g36,g37)
    c: Coincident(g37,g38)
    c: Coincident(g38,g39)
    c: Coincident(g39,g40)
    c: Coincident(g40,g35)
    c: Equal(g35, g36-g40) x5
    c: PointOnObject(g35,g41)
    c: PointOnObject(g36,g41)
    c: PointOnObject(g37,g41)
    c: PointOnObject(g38,g41)
    c: PointOnObject(g39,g41)
    c: PointOnObject(g40,g41)
    c: Coincident(g42,g43)
    c: Coincident(g43,g44)
    c: Coincident(g44,g45)
    c: Coincident(g45,g46)
    c: Coincident(g46,g47)
    c: Coincident(g47,g42)
    c: Equal(g42, g43-g47) x5
    c: PointOnObject(g42,g48)
    c: PointOnObject(g43,g48)
    c: PointOnObject(g44,g48)
    c: PointOnObject(g45,g48)
    c: PointOnObject(g46,g48)
    c: PointOnObject(g47,g48)
    c: Equal(g41,g48)
    c: Diameter(g41) = 7
    c: Vertical(g39)
    c: Vertical(g43)
    c: Distance(g-2,g39) = 1
    c: Symmetric(g38,g43,g-2)
    c: Distance(g41,g-1) = 7
FEATURE [Part::Extrusion] Extrude588  label="hex190"
  Base = -> Sketch597
  Dir = (0,-1,2e-16)
  DirMode = 2
  FaceMakerClass = Part::FaceMakerBullseye
  FaceMakerMode = 3
  LengthFwd = 10
  LengthRev = 0
  Placement = pos=(52,0,21) rot=(0,0,1;0rad)
  Solid = true
  Symmetric = false
FEATURE [Sketcher::SketchObject] Sketch598
  ArcFitTolerance = 1e-06
  FullyConstrained = true
  MakeInternals = false
  Placement = pos=(0,0,0) rot=(1,0,0;1.5708rad)
  sketch-geometry (49):
    g0: LineSegment StartX=1e-16 StartY=3.5 StartZ=0 EndX=-3.03109 EndY=1.75 EndZ=0
    g1: LineSegment StartX=-3.03109 StartY=1.75 StartZ=0 EndX=-3.03109 EndY=-1.75 EndZ=0
    g2: LineSegment StartX=-3.03109 StartY=-1.75 StartZ=0 EndX=-1e-16 EndY=-3.5 EndZ=0
    g3: LineSegment StartX=-1e-16 StartY=-3.5 StartZ=0 EndX=3.03109 EndY=-1.75 EndZ=0
    g4: LineSegment StartX=3.03109 StartY=-1.75 StartZ=0 EndX=3.03109 EndY=1.75 EndZ=0
    g5: LineSegment StartX=3.03109 StartY=1.75 StartZ=0 EndX=1e-16 EndY=3.5 EndZ=0
    g6: Circle [constr] CenterX=0 CenterY=0 CenterZ=0 NormalX=0 NormalY=0 NormalZ=1 AngleXU=0 Radius=3.5
    g7: LineSegment StartX=4.96892 StartY=-1.75002 StartZ=0 EndX=8.00002 EndY=-3.5 EndZ=0
    g8: LineSegment StartX=8.00002 StartY=-3.5 StartZ=0 EndX=11.0311 EndY=-1.74998 EndZ=0
    g9: LineSegment StartX=11.0311 StartY=-1.74998 StartZ=0 EndX=11.0311 EndY=1.75002 EndZ=0
    g10: LineSegment StartX=11.0311 StartY=1.75002 StartZ=0 EndX=7.99998 EndY=3.5 EndZ=0
    g11: LineSegment StartX=7.99998 StartY=3.5 StartZ=0 EndX=4.9689 EndY=1.74998 EndZ=0
    g12: LineSegment StartX=4.9689 StartY=1.74998 StartZ=0 EndX=4.96892 EndY=-1.75002 EndZ=0
    g13: Circle [constr] CenterX=8 CenterY=0 CenterZ=0 NormalX=0 NormalY=0 NormalZ=1 AngleXU=0 Radius=3.5
    g14: LineSegment StartX=4.03109 StartY=3.5 StartZ=0 EndX=7.06218 EndY=5.25 EndZ=0
    g15: LineSegment StartX=7.06218 StartY=5.25 StartZ=0 EndX=7.06218 EndY=8.75 EndZ=0
    g16: LineSegment StartX=7.06218 StartY=8.75 StartZ=0 EndX=4.03109 EndY=10.5 EndZ=0
    g17: LineSegment StartX=4.03109 StartY=10.5 StartZ=0 EndX=1 EndY=8.75 EndZ=0
    g18: LineSegment StartX=1 StartY=8.75 StartZ=0 EndX=1 EndY=5.25 EndZ=0
    g19: LineSegment StartX=1 StartY=5.25 StartZ=0 EndX=4.03109 EndY=3.5 EndZ=0
    g20: Circle [constr] CenterX=4.03109 CenterY=7 CenterZ=0 NormalX=0 NormalY=0 NormalZ=1 AngleXU=0 Radius=3.5
    g21: LineSegment StartX=-1 StartY=5.25 StartZ=0 EndX=-1 EndY=8.75 EndZ=0
    g22: LineSegment StartX=-1 StartY=8.75 StartZ=0 EndX=-4.03109 EndY=10.5 EndZ=0
    g23: LineSegment StartX=-4.03109 StartY=10.5 StartZ=0 EndX=-7.06218 EndY=8.75 EndZ=0
    g24: LineSegment StartX=-7.06218 StartY=8.75 StartZ=0 EndX=-7.06218 EndY=5.25 EndZ=0
    g25: LineSegment StartX=-7.06218 StartY=5.25 StartZ=0 EndX=-4.03109 EndY=3.5 EndZ=0
    g26: LineSegment StartX=-4.03109 StartY=3.5 StartZ=0 EndX=-1 EndY=5.25 EndZ=0
    g27: Circle [constr] CenterX=-4.03109 CenterY=7 CenterZ=0 NormalX=0 NormalY=0 NormalZ=1 AngleXU=0 Radius=3.5
    g28: LineSegment StartX=-4.96891 StartY=-1.75 StartZ=0 EndX=-4.96891 EndY=1.75 EndZ=0
    g29: LineSegment StartX=-4.96891 StartY=1.75 StartZ=0 EndX=-8 EndY=3.5 EndZ=0
    g30: LineSegment StartX=-8 StartY=3.5 StartZ=0 EndX=-11.0311 EndY=1.75 EndZ=0
    g31: LineSegment StartX=-11.0311 StartY=1.75 StartZ=0 EndX=-11.0311 EndY=-1.75 EndZ=0
    g32: LineSegment StartX=-11.0311 StartY=-1.75 StartZ=0 EndX=-8 EndY=-3.5 EndZ=0
    g33: LineSegment StartX=-8 StartY=-3.5 StartZ=0 EndX=-4.96891 EndY=-1.75 EndZ=0
    g34: Circle [constr] CenterX=-8 CenterY=0 CenterZ=0 NormalX=0 NormalY=0 NormalZ=1 AngleXU=0 Radius=3.5
    g35: LineSegment StartX=-4.03109 StartY=-3.5 StartZ=0 EndX=-7.06218 EndY=-5.25 EndZ=0
    g36: LineSegment StartX=-7.06218 StartY=-5.25 StartZ=0 EndX=-7.06218 EndY=-8.75 EndZ=0
    g37: LineSegment StartX=-7.06218 StartY=-8.75 StartZ=0 EndX=-4.03109 EndY=-10.5 EndZ=0
    g38: LineSegment StartX=-4.03109 StartY=-10.5 StartZ=0 EndX=-1 EndY=-8.75 EndZ=0
    g39: LineSegment StartX=-1 StartY=-8.75 StartZ=0 EndX=-1 EndY=-5.25 EndZ=0
    g40: LineSegment StartX=-1 StartY=-5.25 StartZ=0 EndX=-4.03109 EndY=-3.5 EndZ=0
    g41: Circle [constr] CenterX=-4.03109 CenterY=-7 CenterZ=0 NormalX=0 NormalY=0 NormalZ=1 AngleXU=0 Radius=3.5
    g42: LineSegment StartX=4.03109 StartY=-3.5 StartZ=0 EndX=1 EndY=-5.25 EndZ=0
    g43: LineSegment StartX=1 StartY=-5.25 StartZ=0 EndX=1 EndY=-8.75 EndZ=0
    g44: LineSegment StartX=1 StartY=-8.75 StartZ=0 EndX=4.03109 EndY=-10.5 EndZ=0
    g45: LineSegment StartX=4.03109 StartY=-10.5 StartZ=0 EndX=7.06218 EndY=-8.75 EndZ=0
    g46: LineSegment StartX=7.06218 StartY=-8.75 StartZ=0 EndX=7.06218 EndY=-5.25 EndZ=0
    g47: LineSegment StartX=7.06218 StartY=-5.25 StartZ=0 EndX=4.03109 EndY=-3.5 EndZ=0
    g48: Circle [constr] CenterX=4.03109 CenterY=-7 CenterZ=0 NormalX=0 NormalY=0 NormalZ=1 AngleXU=0 Radius=3.5
  constraints (117):
    c: Coincident(g0,g1)
    c: Coincident(g1,g2)
    c: Coincident(g2,g3)
    c: Coincident(g3,g4)
    c: Coincident(g4,g5)
    c: Coincident(g5,g0)
    c: Equal(g0, g1-g5) x5
    c: PointOnObject(g0,g6)
    c: PointOnObject(g1,g6)
    c: PointOnObject(g2,g6)
    c: PointOnObject(g3,g6)
    c: PointOnObject(g4,g6)
    c: PointOnObject(g5,g6)
    c: Coincident(g6,g-1)
    c: Diameter(g6) = 7
    c: PointOnObject(g0,g-2)
    c: Coincident(g7,g8)
    c: Coincident(g8,g9)
    c: Coincident(g9,g10)
    c: Coincident(g10,g11)
    c: Coincident(g11,g12)
    c: Coincident(g12,g7)
    c: Equal(g7, g8-g12) x5
    c: PointOnObject(g7,g13)
    c: PointOnObject(g8,g13)
    c: PointOnObject(g9,g13)
    c: PointOnObject(g10,g13)
    c: PointOnObject(g11,g13)
    c: PointOnObject(g12,g13)
    c: PointOnObject(g13,g-1)
    c: Diameter(g13) = 7
    c: Distance(g6,g13) = 8
    c: Horizontal(g0,g10)
    c: Coincident(g14,g15)
    c: Coincident(g15,g16)
    c: Coincident(g16,g17)
    c: Coincident(g17,g18)
    c: Coincident(g18,g19)
    c: Coincident(g19,g14)
    c: Equal(g14, g15-g19) x5
    c: PointOnObject(g14,g20)
    c: PointOnObject(g15,g20)
    c: PointOnObject(g16,g20)
    c: PointOnObject(g17,g20)
    c: PointOnObject(g18,g20)
    c: PointOnObject(g19,g20)
    c: Diameter(g20) = 7
    c: DistanceY(g-1,g20) = 7
    c: Vertical(g18)
    c: Distance(g17,g-2) = 1
    c: Coincident(g21,g22)
    c: Coincident(g22,g23)
    c: Coincident(g23,g24)
    c: Coincident(g24,g25)
    c: Coincident(g25,g26)
    c: Coincident(g26,g21)
    c: Equal(g21, g22-g26) x5
    c: PointOnObject(g21,g27)
    c: PointOnObject(g22,g27)
    c: PointOnObject(g23,g27)
    c: PointOnObject(g24,g27)
    c: PointOnObject(g25,g27)
    c: PointOnObject(g26,g27)
    c: Diameter(g27) = 7
    c: DistanceY(g-1,g27) = 7
    c: DistanceX(g21,g-1) = 1
    c: Vertical(g21)
    c: Coincident(g28,g29)
    c: Coincident(g29,g30)
    c: Coincident(g30,g31)
    c: Coincident(g31,g32)
    c: Coincident(g32,g33)
    c: Coincident(g33,g28)
    c: Equal(g28, g29-g33) x5
    c: PointOnObject(g28,g34)
    c: PointOnObject(g29,g34)
    c: PointOnObject(g30,g34)
    c: PointOnObject(g31,g34)
    c: PointOnObject(g32,g34)
    c: PointOnObject(g33,g34)
    c: PointOnObject(g34,g-1)
    c: Diameter(g34) = 7
    c: Vertical(g31)
    c: DistanceX(g34,g-1) = 8
    c: Coincident(g35,g36)
    c: Coincident(g36,g37)
    c: Coincident(g37,g38)
    c: Coincident(g38,g39)
    c: Coincident(g39,g40)
    c: Coincident(g40,g35)
    c: Equal(g35, g36-g40) x5
    c: PointOnObject(g35,g41)
    c: PointOnObject(g36,g41)
    c: PointOnObject(g37,g41)
    c: PointOnObject(g38,g41)
    c: PointOnObject(g39,g41)
    c: PointOnObject(g40,g41)
    c: Coincident(g42,g43)
    c: Coincident(g43,g44)
    c: Coincident(g44,g45)
    c: Coincident(g45,g46)
    c: Coincident(g46,g47)
    c: Coincident(g47,g42)
    c: Equal(g42, g43-g47) x5
    c: PointOnObject(g42,g48)
    c: PointOnObject(g43,g48)
    c: PointOnObject(g44,g48)
    c: PointOnObject(g45,g48)
    c: PointOnObject(g46,g48)
    c: PointOnObject(g47,g48)
    c: Equal(g41,g48)
    c: Diameter(g41) = 7
    c: Vertical(g39)
    c: Vertical(g43)
    c: Distance(g-2,g39) = 1
    c: Symmetric(g38,g43,g-2)
    c: Distance(g41,g-1) = 7
FEATURE [Part::Extrusion] Extrude589  label="hex191"
  Base = -> Sketch598
  Dir = (0,-1,2e-16)
  DirMode = 2
  FaceMakerClass = Part::FaceMakerBullseye
  FaceMakerMode = 3
  LengthFwd = 10
  LengthRev = 0
  Placement = pos=(-32,0,28) rot=(0,0,1;0rad)
  Solid = true
  Symmetric = false
FEATURE [Sketcher::SketchObject] Sketch599
  ArcFitTolerance = 1e-06
  FullyConstrained = true
  MakeInternals = false
  Placement = pos=(0,0,0) rot=(1,0,0;1.5708rad)
  sketch-geometry (49):
    g0: LineSegment StartX=1e-16 StartY=3.5 StartZ=0 EndX=-3.03109 EndY=1.75 EndZ=0
    g1: LineSegment StartX=-3.03109 StartY=1.75 StartZ=0 EndX=-3.03109 EndY=-1.75 EndZ=0
    g2: LineSegment StartX=-3.03109 StartY=-1.75 StartZ=0 EndX=-1e-16 EndY=-3.5 EndZ=0
    g3: LineSegment StartX=-1e-16 StartY=-3.5 StartZ=0 EndX=3.03109 EndY=-1.75 EndZ=0
    g4: LineSegment StartX=3.03109 StartY=-1.75 StartZ=0 EndX=3.03109 EndY=1.75 EndZ=0
    g5: LineSegment StartX=3.03109 StartY=1.75 StartZ=0 EndX=1e-16 EndY=3.5 EndZ=0
    g6: Circle [constr] CenterX=0 CenterY=0 CenterZ=0 NormalX=0 NormalY=0 NormalZ=1 AngleXU=0 Radius=3.5
    g7: LineSegment StartX=4.96892 StartY=-1.75002 StartZ=0 EndX=8.00002 EndY=-3.5 EndZ=0
    g8: LineSegment StartX=8.00002 StartY=-3.5 StartZ=0 EndX=11.0311 EndY=-1.74998 EndZ=0
    g9: LineSegment StartX=11.0311 StartY=-1.74998 StartZ=0 EndX=11.0311 EndY=1.75002 EndZ=0
    g10: LineSegment StartX=11.0311 StartY=1.75002 StartZ=0 EndX=7.99998 EndY=3.5 EndZ=0
    g11: LineSegment StartX=7.99998 StartY=3.5 StartZ=0 EndX=4.9689 EndY=1.74998 EndZ=0
    g12: LineSegment StartX=4.9689 StartY=1.74998 StartZ=0 EndX=4.96892 EndY=-1.75002 EndZ=0
    g13: Circle [constr] CenterX=8 CenterY=0 CenterZ=0 NormalX=0 NormalY=0 NormalZ=1 AngleXU=0 Radius=3.5
    g14: LineSegment StartX=4.03109 StartY=3.5 StartZ=0 EndX=7.06218 EndY=5.25 EndZ=0
    g15: LineSegment StartX=7.06218 StartY=5.25 StartZ=0 EndX=7.06218 EndY=8.75 EndZ=0
    g16: LineSegment StartX=7.06218 StartY=8.75 StartZ=0 EndX=4.03109 EndY=10.5 EndZ=0
    g17: LineSegment StartX=4.03109 StartY=10.5 StartZ=0 EndX=1 EndY=8.75 EndZ=0
    g18: LineSegment StartX=1 StartY=8.75 StartZ=0 EndX=1 EndY=5.25 EndZ=0
    g19: LineSegment StartX=1 StartY=5.25 StartZ=0 EndX=4.03109 EndY=3.5 EndZ=0
    g20: Circle [constr] CenterX=4.03109 CenterY=7 CenterZ=0 NormalX=0 NormalY=0 NormalZ=1 AngleXU=0 Radius=3.5
    g21: LineSegment StartX=-1 StartY=5.25 StartZ=0 EndX=-1 EndY=8.75 EndZ=0
    g22: LineSegment StartX=-1 StartY=8.75 StartZ=0 EndX=-4.03109 EndY=10.5 EndZ=0
    g23: LineSegment StartX=-4.03109 StartY=10.5 StartZ=0 EndX=-7.06218 EndY=8.75 EndZ=0
    g24: LineSegment StartX=-7.06218 StartY=8.75 StartZ=0 EndX=-7.06218 EndY=5.25 EndZ=0
    g25: LineSegment StartX=-7.06218 StartY=5.25 StartZ=0 EndX=-4.03109 EndY=3.5 EndZ=0
    g26: LineSegment StartX=-4.03109 StartY=3.5 StartZ=0 EndX=-1 EndY=5.25 EndZ=0
    g27: Circle [constr] CenterX=-4.03109 CenterY=7 CenterZ=0 NormalX=0 NormalY=0 NormalZ=1 AngleXU=0 Radius=3.5
    g28: LineSegment StartX=-4.96891 StartY=-1.75 StartZ=0 EndX=-4.96891 EndY=1.75 EndZ=0
    g29: LineSegment StartX=-4.96891 StartY=1.75 StartZ=0 EndX=-8 EndY=3.5 EndZ=0
    g30: LineSegment StartX=-8 StartY=3.5 StartZ=0 EndX=-11.0311 EndY=1.75 EndZ=0
    g31: LineSegment StartX=-11.0311 StartY=1.75 StartZ=0 EndX=-11.0311 EndY=-1.75 EndZ=0
    g32: LineSegment StartX=-11.0311 StartY=-1.75 StartZ=0 EndX=-8 EndY=-3.5 EndZ=0
    g33: LineSegment StartX=-8 StartY=-3.5 StartZ=0 EndX=-4.96891 EndY=-1.75 EndZ=0
    g34: Circle [constr] CenterX=-8 CenterY=0 CenterZ=0 NormalX=0 NormalY=0 NormalZ=1 AngleXU=0 Radius=3.5
    g35: LineSegment StartX=-4.03109 StartY=-3.5 StartZ=0 EndX=-7.06218 EndY=-5.25 EndZ=0
    g36: LineSegment StartX=-7.06218 StartY=-5.25 StartZ=0 EndX=-7.06218 EndY=-8.75 EndZ=0
    g37: LineSegment StartX=-7.06218 StartY=-8.75 StartZ=0 EndX=-4.03109 EndY=-10.5 EndZ=0
    g38: LineSegment StartX=-4.03109 StartY=-10.5 StartZ=0 EndX=-1 EndY=-8.75 EndZ=0
    g39: LineSegment StartX=-1 StartY=-8.75 StartZ=0 EndX=-1 EndY=-5.25 EndZ=0
    g40: LineSegment StartX=-1 StartY=-5.25 StartZ=0 EndX=-4.03109 EndY=-3.5 EndZ=0
    g41: Circle [constr] CenterX=-4.03109 CenterY=-7 CenterZ=0 NormalX=0 NormalY=0 NormalZ=1 AngleXU=0 Radius=3.5
    g42: LineSegment StartX=4.03109 StartY=-3.5 StartZ=0 EndX=1 EndY=-5.25 EndZ=0
    g43: LineSegment StartX=1 StartY=-5.25 StartZ=0 EndX=1 EndY=-8.75 EndZ=0
    g44: LineSegment StartX=1 StartY=-8.75 StartZ=0 EndX=4.03109 EndY=-10.5 EndZ=0
    g45: LineSegment StartX=4.03109 StartY=-10.5 StartZ=0 EndX=7.06218 EndY=-8.75 EndZ=0
    g46: LineSegment StartX=7.06218 StartY=-8.75 StartZ=0 EndX=7.06218 EndY=-5.25 EndZ=0
    g47: LineSegment StartX=7.06218 StartY=-5.25 StartZ=0 EndX=4.03109 EndY=-3.5 EndZ=0
    g48: Circle [constr] CenterX=4.03109 CenterY=-7 CenterZ=0 NormalX=0 NormalY=0 NormalZ=1 AngleXU=0 Radius=3.5
  constraints (117):
    c: Coincident(g0,g1)
    c: Coincident(g1,g2)
    c: Coincident(g2,g3)
    c: Coincident(g3,g4)
    c: Coincident(g4,g5)
    c: Coincident(g5,g0)
    c: Equal(g0, g1-g5) x5
    c: PointOnObject(g0,g6)
    c: PointOnObject(g1,g6)
    c: PointOnObject(g2,g6)
    c: PointOnObject(g3,g6)
    c: PointOnObject(g4,g6)
    c: PointOnObject(g5,g6)
    c: Coincident(g6,g-1)
    c: Diameter(g6) = 7
    c: PointOnObject(g0,g-2)
    c: Coincident(g7,g8)
    c: Coincident(g8,g9)
    c: Coincident(g9,g10)
    c: Coincident(g10,g11)
    c: Coincident(g11,g12)
    c: Coincident(g12,g7)
    c: Equal(g7, g8-g12) x5
    c: PointOnObject(g7,g13)
    c: PointOnObject(g8,g13)
    c: PointOnObject(g9,g13)
    c: PointOnObject(g10,g13)
    c: PointOnObject(g11,g13)
    c: PointOnObject(g12,g13)
    c: PointOnObject(g13,g-1)
    c: Diameter(g13) = 7
    c: Distance(g6,g13) = 8
    c: Horizontal(g0,g10)
    c: Coincident(g14,g15)
    c: Coincident(g15,g16)
    c: Coincident(g16,g17)
    c: Coincident(g17,g18)
    c: Coincident(g18,g19)
    c: Coincident(g19,g14)
    c: Equal(g14, g15-g19) x5
    c: PointOnObject(g14,g20)
    c: PointOnObject(g15,g20)
    c: PointOnObject(g16,g20)
    c: PointOnObject(g17,g20)
    c: PointOnObject(g18,g20)
    c: PointOnObject(g19,g20)
    c: Diameter(g20) = 7
    c: DistanceY(g-1,g20) = 7
    c: Vertical(g18)
    c: Distance(g17,g-2) = 1
    c: Coincident(g21,g22)
    c: Coincident(g22,g23)
    c: Coincident(g23,g24)
    c: Coincident(g24,g25)
    c: Coincident(g25,g26)
    c: Coincident(g26,g21)
    c: Equal(g21, g22-g26) x5
    c: PointOnObject(g21,g27)
    c: PointOnObject(g22,g27)
    c: PointOnObject(g23,g27)
    c: PointOnObject(g24,g27)
    c: PointOnObject(g25,g27)
    c: PointOnObject(g26,g27)
    c: Diameter(g27) = 7
    c: DistanceY(g-1,g27) = 7
    c: DistanceX(g21,g-1) = 1
    c: Vertical(g21)
    c: Coincident(g28,g29)
    c: Coincident(g29,g30)
    c: Coincident(g30,g31)
    c: Coincident(g31,g32)
    c: Coincident(g32,g33)
    c: Coincident(g33,g28)
    c: Equal(g28, g29-g33) x5
    c: PointOnObject(g28,g34)
    c: PointOnObject(g29,g34)
    c: PointOnObject(g30,g34)
    c: PointOnObject(g31,g34)
    c: PointOnObject(g32,g34)
    c: PointOnObject(g33,g34)
    c: PointOnObject(g34,g-1)
    c: Diameter(g34) = 7
    c: Vertical(g31)
    c: DistanceX(g34,g-1) = 8
    c: Coincident(g35,g36)
    c: Coincident(g36,g37)
    c: Coincident(g37,g38)
    c: Coincident(g38,g39)
    c: Coincident(g39,g40)
    c: Coincident(g40,g35)
    c: Equal(g35, g36-g40) x5
    c: PointOnObject(g35,g41)
    c: PointOnObject(g36,g41)
    c: PointOnObject(g37,g41)
    c: PointOnObject(g38,g41)
    c: PointOnObject(g39,g41)
    c: PointOnObject(g40,g41)
    c: Coincident(g42,g43)
    c: Coincident(g43,g44)
    c: Coincident(g44,g45)
    c: Coincident(g45,g46)
    c: Coincident(g46,g47)
    c: Coincident(g47,g42)
    c: Equal(g42, g43-g47) x5
    c: PointOnObject(g42,g48)
    c: PointOnObject(g43,g48)
    c: PointOnObject(g44,g48)
    c: PointOnObject(g45,g48)
    c: PointOnObject(g46,g48)
    c: PointOnObject(g47,g48)
    c: Equal(g41,g48)
    c: Diameter(g41) = 7
    c: Vertical(g39)
    c: Vertical(g43)
    c: Distance(g-2,g39) = 1
    c: Symmetric(g38,g43,g-2)
    c: Distance(g41,g-1) = 7
FEATURE [Part::Extrusion] Extrude590  label="hex192"
  Base = -> Sketch599
  Dir = (0,-1,2e-16)
  DirMode = 2
  FaceMakerClass = Part::FaceMakerBullseye
  FaceMakerMode = 3
  LengthFwd = 10
  LengthRev = 0
  Placement = pos=(-12,0,35) rot=(0,0,1;0rad)
  Solid = true
  Symmetric = false
FEATURE [Sketcher::SketchObject] Sketch600
  ArcFitTolerance = 1e-06
  FullyConstrained = true
  MakeInternals = false
  Placement = pos=(0,0,0) rot=(1,0,0;1.5708rad)
  sketch-geometry (49):
    g0: LineSegment StartX=1e-16 StartY=3.5 StartZ=0 EndX=-3.03109 EndY=1.75 EndZ=0
    g1: LineSegment StartX=-3.03109 StartY=1.75 StartZ=0 EndX=-3.03109 EndY=-1.75 EndZ=0
    g2: LineSegment StartX=-3.03109 StartY=-1.75 StartZ=0 EndX=-1e-16 EndY=-3.5 EndZ=0
    g3: LineSegment StartX=-1e-16 StartY=-3.5 StartZ=0 EndX=3.03109 EndY=-1.75 EndZ=0
    g4: LineSegment StartX=3.03109 StartY=-1.75 StartZ=0 EndX=3.03109 EndY=1.75 EndZ=0
    g5: LineSegment StartX=3.03109 StartY=1.75 StartZ=0 EndX=1e-16 EndY=3.5 EndZ=0
    g6: Circle [constr] CenterX=0 CenterY=0 CenterZ=0 NormalX=0 NormalY=0 NormalZ=1 AngleXU=0 Radius=3.5
    g7: LineSegment StartX=4.96892 StartY=-1.75002 StartZ=0 EndX=8.00002 EndY=-3.5 EndZ=0
    g8: LineSegment StartX=8.00002 StartY=-3.5 StartZ=0 EndX=11.0311 EndY=-1.74998 EndZ=0
    g9: LineSegment StartX=11.0311 StartY=-1.74998 StartZ=0 EndX=11.0311 EndY=1.75002 EndZ=0
    g10: LineSegment StartX=11.0311 StartY=1.75002 StartZ=0 EndX=7.99998 EndY=3.5 EndZ=0
    g11: LineSegment StartX=7.99998 StartY=3.5 StartZ=0 EndX=4.9689 EndY=1.74998 EndZ=0
    g12: LineSegment StartX=4.9689 StartY=1.74998 StartZ=0 EndX=4.96892 EndY=-1.75002 EndZ=0
    g13: Circle [constr] CenterX=8 CenterY=0 CenterZ=0 NormalX=0 NormalY=0 NormalZ=1 AngleXU=0 Radius=3.5
    g14: LineSegment StartX=4.03109 StartY=3.5 StartZ=0 EndX=7.06218 EndY=5.25 EndZ=0
    g15: LineSegment StartX=7.06218 StartY=5.25 StartZ=0 EndX=7.06218 EndY=8.75 EndZ=0
    g16: LineSegment StartX=7.06218 StartY=8.75 StartZ=0 EndX=4.03109 EndY=10.5 EndZ=0
    g17: LineSegment StartX=4.03109 StartY=10.5 StartZ=0 EndX=1 EndY=8.75 EndZ=0
    g18: LineSegment StartX=1 StartY=8.75 StartZ=0 EndX=1 EndY=5.25 EndZ=0
    g19: LineSegment StartX=1 StartY=5.25 StartZ=0 EndX=4.03109 EndY=3.5 EndZ=0
    g20: Circle [constr] CenterX=4.03109 CenterY=7 CenterZ=0 NormalX=0 NormalY=0 NormalZ=1 AngleXU=0 Radius=3.5
    g21: LineSegment StartX=-1 StartY=5.25 StartZ=0 EndX=-1 EndY=8.75 EndZ=0
    g22: LineSegment StartX=-1 StartY=8.75 StartZ=0 EndX=-4.03109 EndY=10.5 EndZ=0
    g23: LineSegment StartX=-4.03109 StartY=10.5 StartZ=0 EndX=-7.06218 EndY=8.75 EndZ=0
    g24: LineSegment StartX=-7.06218 StartY=8.75 StartZ=0 EndX=-7.06218 EndY=5.25 EndZ=0
    g25: LineSegment StartX=-7.06218 StartY=5.25 StartZ=0 EndX=-4.03109 EndY=3.5 EndZ=0
    g26: LineSegment StartX=-4.03109 StartY=3.5 StartZ=0 EndX=-1 EndY=5.25 EndZ=0
    g27: Circle [constr] CenterX=-4.03109 CenterY=7 CenterZ=0 NormalX=0 NormalY=0 NormalZ=1 AngleXU=0 Radius=3.5
    g28: LineSegment StartX=-4.96891 StartY=-1.75 StartZ=0 EndX=-4.96891 EndY=1.75 EndZ=0
    g29: LineSegment StartX=-4.96891 StartY=1.75 StartZ=0 EndX=-8 EndY=3.5 EndZ=0
    g30: LineSegment StartX=-8 StartY=3.5 StartZ=0 EndX=-11.0311 EndY=1.75 EndZ=0
    g31: LineSegment StartX=-11.0311 StartY=1.75 StartZ=0 EndX=-11.0311 EndY=-1.75 EndZ=0
    g32: LineSegment StartX=-11.0311 StartY=-1.75 StartZ=0 EndX=-8 EndY=-3.5 EndZ=0
    g33: LineSegment StartX=-8 StartY=-3.5 StartZ=0 EndX=-4.96891 EndY=-1.75 EndZ=0
    g34: Circle [constr] CenterX=-8 CenterY=0 CenterZ=0 NormalX=0 NormalY=0 NormalZ=1 AngleXU=0 Radius=3.5
    g35: LineSegment StartX=-4.03109 StartY=-3.5 StartZ=0 EndX=-7.06218 EndY=-5.25 EndZ=0
    g36: LineSegment StartX=-7.06218 StartY=-5.25 StartZ=0 EndX=-7.06218 EndY=-8.75 EndZ=0
    g37: LineSegment StartX=-7.06218 StartY=-8.75 StartZ=0 EndX=-4.03109 EndY=-10.5 EndZ=0
    g38: LineSegment StartX=-4.03109 StartY=-10.5 StartZ=0 EndX=-1 EndY=-8.75 EndZ=0
    g39: LineSegment StartX=-1 StartY=-8.75 StartZ=0 EndX=-1 EndY=-5.25 EndZ=0
    g40: LineSegment StartX=-1 StartY=-5.25 StartZ=0 EndX=-4.03109 EndY=-3.5 EndZ=0
    g41: Circle [constr] CenterX=-4.03109 CenterY=-7 CenterZ=0 NormalX=0 NormalY=0 NormalZ=1 AngleXU=0 Radius=3.5
    g42: LineSegment StartX=4.03109 StartY=-3.5 StartZ=0 EndX=1 EndY=-5.25 EndZ=0
    g43: LineSegment StartX=1 StartY=-5.25 StartZ=0 EndX=1 EndY=-8.75 EndZ=0
    g44: LineSegment StartX=1 StartY=-8.75 StartZ=0 EndX=4.03109 EndY=-10.5 EndZ=0
    g45: LineSegment StartX=4.03109 StartY=-10.5 StartZ=0 EndX=7.06218 EndY=-8.75 EndZ=0
    g46: LineSegment StartX=7.06218 StartY=-8.75 StartZ=0 EndX=7.06218 EndY=-5.25 EndZ=0
    g47: LineSegment StartX=7.06218 StartY=-5.25 StartZ=0 EndX=4.03109 EndY=-3.5 EndZ=0
    g48: Circle [constr] CenterX=4.03109 CenterY=-7 CenterZ=0 NormalX=0 NormalY=0 NormalZ=1 AngleXU=0 Radius=3.5
  constraints (117):
    c: Coincident(g0,g1)
    c: Coincident(g1,g2)
    c: Coincident(g2,g3)
    c: Coincident(g3,g4)
    c: Coincident(g4,g5)
    c: Coincident(g5,g0)
    c: Equal(g0, g1-g5) x5
    c: PointOnObject(g0,g6)
    c: PointOnObject(g1,g6)
    c: PointOnObject(g2,g6)
    c: PointOnObject(g3,g6)
    c: PointOnObject(g4,g6)
    c: PointOnObject(g5,g6)
    c: Coincident(g6,g-1)
    c: Diameter(g6) = 7
    c: PointOnObject(g0,g-2)
    c: Coincident(g7,g8)
    c: Coincident(g8,g9)
    c: Coincident(g9,g10)
    c: Coincident(g10,g11)
    c: Coincident(g11,g12)
    c: Coincident(g12,g7)
    c: Equal(g7, g8-g12) x5
    c: PointOnObject(g7,g13)
    c: PointOnObject(g8,g13)
    c: PointOnObject(g9,g13)
    c: PointOnObject(g10,g13)
    c: PointOnObject(g11,g13)
    c: PointOnObject(g12,g13)
    c: PointOnObject(g13,g-1)
    c: Diameter(g13) = 7
    c: Distance(g6,g13) = 8
    c: Horizontal(g0,g10)
    c: Coincident(g14,g15)
    c: Coincident(g15,g16)
    c: Coincident(g16,g17)
    c: Coincident(g17,g18)
    c: Coincident(g18,g19)
    c: Coincident(g19,g14)
    c: Equal(g14, g15-g19) x5
    c: PointOnObject(g14,g20)
    c: PointOnObject(g15,g20)
    c: PointOnObject(g16,g20)
    c: PointOnObject(g17,g20)
    c: PointOnObject(g18,g20)
    c: PointOnObject(g19,g20)
    c: Diameter(g20) = 7
    c: DistanceY(g-1,g20) = 7
    c: Vertical(g18)
    c: Distance(g17,g-2) = 1
    c: Coincident(g21,g22)
    c: Coincident(g22,g23)
    c: Coincident(g23,g24)
    c: Coincident(g24,g25)
    c: Coincident(g25,g26)
    c: Coincident(g26,g21)
    c: Equal(g21, g22-g26) x5
    c: PointOnObject(g21,g27)
    c: PointOnObject(g22,g27)
    c: PointOnObject(g23,g27)
    c: PointOnObject(g24,g27)
    c: PointOnObject(g25,g27)
    c: PointOnObject(g26,g27)
    c: Diameter(g27) = 7
    c: DistanceY(g-1,g27) = 7
    c: DistanceX(g21,g-1) = 1
    c: Vertical(g21)
    c: Coincident(g28,g29)
    c: Coincident(g29,g30)
    c: Coincident(g30,g31)
    c: Coincident(g31,g32)
    c: Coincident(g32,g33)
    c: Coincident(g33,g28)
    c: Equal(g28, g29-g33) x5
    c: PointOnObject(g28,g34)
    c: PointOnObject(g29,g34)
    c: PointOnObject(g30,g34)
    c: PointOnObject(g31,g34)
    c: PointOnObject(g32,g34)
    c: PointOnObject(g33,g34)
    c: PointOnObject(g34,g-1)
    c: Diameter(g34) = 7
    c: Vertical(g31)
    c: DistanceX(g34,g-1) = 8
    c: Coincident(g35,g36)
    c: Coincident(g36,g37)
    c: Coincident(g37,g38)
    c: Coincident(g38,g39)
    c: Coincident(g39,g40)
    c: Coincident(g40,g35)
    c: Equal(g35, g36-g40) x5
    c: PointOnObject(g35,g41)
    c: PointOnObject(g36,g41)
    c: PointOnObject(g37,g41)
    c: PointOnObject(g38,g41)
    c: PointOnObject(g39,g41)
    c: PointOnObject(g40,g41)
    c: Coincident(g42,g43)
    c: Coincident(g43,g44)
    c: Coincident(g44,g45)
    c: Coincident(g45,g46)
    c: Coincident(g46,g47)
    c: Coincident(g47,g42)
    c: Equal(g42, g43-g47) x5
    c: PointOnObject(g42,g48)
    c: PointOnObject(g43,g48)
    c: PointOnObject(g44,g48)
    c: PointOnObject(g45,g48)
    c: PointOnObject(g46,g48)
    c: PointOnObject(g47,g48)
    c: Equal(g41,g48)
    c: Diameter(g41) = 7
    c: Vertical(g39)
    c: Vertical(g43)
    c: Distance(g-2,g39) = 1
    c: Symmetric(g38,g43,g-2)
    c: Distance(g41,g-1) = 7
FEATURE [Part::Extrusion] Extrude591  label="hex193"
  Base = -> Sketch600
  Dir = (0,-1,2e-16)
  DirMode = 2
  FaceMakerClass = Part::FaceMakerBullseye
  FaceMakerMode = 3
  LengthFwd = 10
  LengthRev = 0
  Placement = pos=(-80,0,0) rot=(0,0,1;0rad)
  Solid = true
  Symmetric = false
FEATURE [Sketcher::SketchObject] Sketch601
  ArcFitTolerance = 1e-06
  FullyConstrained = true
  MakeInternals = false
  Placement = pos=(0,0,0) rot=(1,0,0;1.5708rad)
  sketch-geometry (49):
    g0: LineSegment StartX=1e-16 StartY=3.5 StartZ=0 EndX=-3.03109 EndY=1.75 EndZ=0
    g1: LineSegment StartX=-3.03109 StartY=1.75 StartZ=0 EndX=-3.03109 EndY=-1.75 EndZ=0
    g2: LineSegment StartX=-3.03109 StartY=-1.75 StartZ=0 EndX=-1e-16 EndY=-3.5 EndZ=0
    g3: LineSegment StartX=-1e-16 StartY=-3.5 StartZ=0 EndX=3.03109 EndY=-1.75 EndZ=0
    g4: LineSegment StartX=3.03109 StartY=-1.75 StartZ=0 EndX=3.03109 EndY=1.75 EndZ=0
    g5: LineSegment StartX=3.03109 StartY=1.75 StartZ=0 EndX=1e-16 EndY=3.5 EndZ=0
    g6: Circle [constr] CenterX=0 CenterY=0 CenterZ=0 NormalX=0 NormalY=0 NormalZ=1 AngleXU=0 Radius=3.5
    g7: LineSegment StartX=4.96892 StartY=-1.75002 StartZ=0 EndX=8.00002 EndY=-3.5 EndZ=0
    g8: LineSegment StartX=8.00002 StartY=-3.5 StartZ=0 EndX=11.0311 EndY=-1.74998 EndZ=0
    g9: LineSegment StartX=11.0311 StartY=-1.74998 StartZ=0 EndX=11.0311 EndY=1.75002 EndZ=0
    g10: LineSegment StartX=11.0311 StartY=1.75002 StartZ=0 EndX=7.99998 EndY=3.5 EndZ=0
    g11: LineSegment StartX=7.99998 StartY=3.5 StartZ=0 EndX=4.9689 EndY=1.74998 EndZ=0
    g12: LineSegment StartX=4.9689 StartY=1.74998 StartZ=0 EndX=4.96892 EndY=-1.75002 EndZ=0
    g13: Circle [constr] CenterX=8 CenterY=0 CenterZ=0 NormalX=0 NormalY=0 NormalZ=1 AngleXU=0 Radius=3.5
    g14: LineSegment StartX=4.03109 StartY=3.5 StartZ=0 EndX=7.06218 EndY=5.25 EndZ=0
    g15: LineSegment StartX=7.06218 StartY=5.25 StartZ=0 EndX=7.06218 EndY=8.75 EndZ=0
    g16: LineSegment StartX=7.06218 StartY=8.75 StartZ=0 EndX=4.03109 EndY=10.5 EndZ=0
    g17: LineSegment StartX=4.03109 StartY=10.5 StartZ=0 EndX=1 EndY=8.75 EndZ=0
    g18: LineSegment StartX=1 StartY=8.75 StartZ=0 EndX=1 EndY=5.25 EndZ=0
    g19: LineSegment StartX=1 StartY=5.25 StartZ=0 EndX=4.03109 EndY=3.5 EndZ=0
    g20: Circle [constr] CenterX=4.03109 CenterY=7 CenterZ=0 NormalX=0 NormalY=0 NormalZ=1 AngleXU=0 Radius=3.5
    g21: LineSegment StartX=-1 StartY=5.25 StartZ=0 EndX=-1 EndY=8.75 EndZ=0
    g22: LineSegment StartX=-1 StartY=8.75 StartZ=0 EndX=-4.03109 EndY=10.5 EndZ=0
    g23: LineSegment StartX=-4.03109 StartY=10.5 StartZ=0 EndX=-7.06218 EndY=8.75 EndZ=0
    g24: LineSegment StartX=-7.06218 StartY=8.75 StartZ=0 EndX=-7.06218 EndY=5.25 EndZ=0
    g25: LineSegment StartX=-7.06218 StartY=5.25 StartZ=0 EndX=-4.03109 EndY=3.5 EndZ=0
    g26: LineSegment StartX=-4.03109 StartY=3.5 StartZ=0 EndX=-1 EndY=5.25 EndZ=0
    g27: Circle [constr] CenterX=-4.03109 CenterY=7 CenterZ=0 NormalX=0 NormalY=0 NormalZ=1 AngleXU=0 Radius=3.5
    g28: LineSegment StartX=-4.96891 StartY=-1.75 StartZ=0 EndX=-4.96891 EndY=1.75 EndZ=0
    g29: LineSegment StartX=-4.96891 StartY=1.75 StartZ=0 EndX=-8 EndY=3.5 EndZ=0
    g30: LineSegment StartX=-8 StartY=3.5 StartZ=0 EndX=-11.0311 EndY=1.75 EndZ=0
    g31: LineSegment StartX=-11.0311 StartY=1.75 StartZ=0 EndX=-11.0311 EndY=-1.75 EndZ=0
    g32: LineSegment StartX=-11.0311 StartY=-1.75 StartZ=0 EndX=-8 EndY=-3.5 EndZ=0
    g33: LineSegment StartX=-8 StartY=-3.5 StartZ=0 EndX=-4.96891 EndY=-1.75 EndZ=0
    g34: Circle [constr] CenterX=-8 CenterY=0 CenterZ=0 NormalX=0 NormalY=0 NormalZ=1 AngleXU=0 Radius=3.5
    g35: LineSegment StartX=-4.03109 StartY=-3.5 StartZ=0 EndX=-7.06218 EndY=-5.25 EndZ=0
    g36: LineSegment StartX=-7.06218 StartY=-5.25 StartZ=0 EndX=-7.06218 EndY=-8.75 EndZ=0
    g37: LineSegment StartX=-7.06218 StartY=-8.75 StartZ=0 EndX=-4.03109 EndY=-10.5 EndZ=0
    g38: LineSegment StartX=-4.03109 StartY=-10.5 StartZ=0 EndX=-1 EndY=-8.75 EndZ=0
    g39: LineSegment StartX=-1 StartY=-8.75 StartZ=0 EndX=-1 EndY=-5.25 EndZ=0
    g40: LineSegment StartX=-1 StartY=-5.25 StartZ=0 EndX=-4.03109 EndY=-3.5 EndZ=0
    g41: Circle [constr] CenterX=-4.03109 CenterY=-7 CenterZ=0 NormalX=0 NormalY=0 NormalZ=1 AngleXU=0 Radius=3.5
    g42: LineSegment StartX=4.03109 StartY=-3.5 StartZ=0 EndX=1 EndY=-5.25 EndZ=0
    g43: LineSegment StartX=1 StartY=-5.25 StartZ=0 EndX=1 EndY=-8.75 EndZ=0
    g44: LineSegment StartX=1 StartY=-8.75 StartZ=0 EndX=4.03109 EndY=-10.5 EndZ=0
    g45: LineSegment StartX=4.03109 StartY=-10.5 StartZ=0 EndX=7.06218 EndY=-8.75 EndZ=0
    g46: LineSegment StartX=7.06218 StartY=-8.75 StartZ=0 EndX=7.06218 EndY=-5.25 EndZ=0
    g47: LineSegment StartX=7.06218 StartY=-5.25 StartZ=0 EndX=4.03109 EndY=-3.5 EndZ=0
    g48: Circle [constr] CenterX=4.03109 CenterY=-7 CenterZ=0 NormalX=0 NormalY=0 NormalZ=1 AngleXU=0 Radius=3.5
  constraints (117):
    c: Coincident(g0,g1)
    c: Coincident(g1,g2)
    c: Coincident(g2,g3)
    c: Coincident(g3,g4)
    c: Coincident(g4,g5)
    c: Coincident(g5,g0)
    c: Equal(g0, g1-g5) x5
    c: PointOnObject(g0,g6)
    c: PointOnObject(g1,g6)
    c: PointOnObject(g2,g6)
    c: PointOnObject(g3,g6)
    c: PointOnObject(g4,g6)
    c: PointOnObject(g5,g6)
    c: Coincident(g6,g-1)
    c: Diameter(g6) = 7
    c: PointOnObject(g0,g-2)
    c: Coincident(g7,g8)
    c: Coincident(g8,g9)
    c: Coincident(g9,g10)
    c: Coincident(g10,g11)
    c: Coincident(g11,g12)
    c: Coincident(g12,g7)
    c: Equal(g7, g8-g12) x5
    c: PointOnObject(g7,g13)
    c: PointOnObject(g8,g13)
    c: PointOnObject(g9,g13)
    c: PointOnObject(g10,g13)
    c: PointOnObject(g11,g13)
    c: PointOnObject(g12,g13)
    c: PointOnObject(g13,g-1)
    c: Diameter(g13) = 7
    c: Distance(g6,g13) = 8
    c: Horizontal(g0,g10)
    c: Coincident(g14,g15)
    c: Coincident(g15,g16)
    c: Coincident(g16,g17)
    c: Coincident(g17,g18)
    c: Coincident(g18,g19)
    c: Coincident(g19,g14)
    c: Equal(g14, g15-g19) x5
    c: PointOnObject(g14,g20)
    c: PointOnObject(g15,g20)
    c: PointOnObject(g16,g20)
    c: PointOnObject(g17,g20)
    c: PointOnObject(g18,g20)
    c: PointOnObject(g19,g20)
    c: Diameter(g20) = 7
    c: DistanceY(g-1,g20) = 7
    c: Vertical(g18)
    c: Distance(g17,g-2) = 1
    c: Coincident(g21,g22)
    c: Coincident(g22,g23)
    c: Coincident(g23,g24)
    c: Coincident(g24,g25)
    c: Coincident(g25,g26)
    c: Coincident(g26,g21)
    c: Equal(g21, g22-g26) x5
    c: PointOnObject(g21,g27)
    c: PointOnObject(g22,g27)
    c: PointOnObject(g23,g27)
    c: PointOnObject(g24,g27)
    c: PointOnObject(g25,g27)
    c: PointOnObject(g26,g27)
    c: Diameter(g27) = 7
    c: DistanceY(g-1,g27) = 7
    c: DistanceX(g21,g-1) = 1
    c: Vertical(g21)
    c: Coincident(g28,g29)
    c: Coincident(g29,g30)
    c: Coincident(g30,g31)
    c: Coincident(g31,g32)
    c: Coincident(g32,g33)
    c: Coincident(g33,g28)
    c: Equal(g28, g29-g33) x5
    c: PointOnObject(g28,g34)
    c: PointOnObject(g29,g34)
    c: PointOnObject(g30,g34)
    c: PointOnObject(g31,g34)
    c: PointOnObject(g32,g34)
    c: PointOnObject(g33,g34)
    c: PointOnObject(g34,g-1)
    c: Diameter(g34) = 7
    c: Vertical(g31)
    c: DistanceX(g34,g-1) = 8
    c: Coincident(g35,g36)
    c: Coincident(g36,g37)
    c: Coincident(g37,g38)
    c: Coincident(g38,g39)
    c: Coincident(g39,g40)
    c: Coincident(g40,g35)
    c: Equal(g35, g36-g40) x5
    c: PointOnObject(g35,g41)
    c: PointOnObject(g36,g41)
    c: PointOnObject(g37,g41)
    c: PointOnObject(g38,g41)
    c: PointOnObject(g39,g41)
    c: PointOnObject(g40,g41)
    c: Coincident(g42,g43)
    c: Coincident(g43,g44)
    c: Coincident(g44,g45)
    c: Coincident(g45,g46)
    c: Coincident(g46,g47)
    c: Coincident(g47,g42)
    c: Equal(g42, g43-g47) x5
    c: PointOnObject(g42,g48)
    c: PointOnObject(g43,g48)
    c: PointOnObject(g44,g48)
    c: PointOnObject(g45,g48)
    c: PointOnObject(g46,g48)
    c: PointOnObject(g47,g48)
    c: Equal(g41,g48)
    c: Diameter(g41) = 7
    c: Vertical(g39)
    c: Vertical(g43)
    c: Distance(g-2,g39) = 1
    c: Symmetric(g38,g43,g-2)
    c: Distance(g41,g-1) = 7
FEATURE [Part::Extrusion] Extrude592  label="hex194"
  Base = -> Sketch601
  Dir = (0,-1,2e-16)
  DirMode = 2
  FaceMakerClass = Part::FaceMakerBullseye
  FaceMakerMode = 3
  LengthFwd = 10
  LengthRev = 0
  Placement = pos=(-104,0,0) rot=(0,0,1;0rad)
  Solid = true
  Symmetric = false
FEATURE [Sketcher::SketchObject] Sketch602
  ArcFitTolerance = 1e-06
  FullyConstrained = true
  MakeInternals = false
  Placement = pos=(0,0,0) rot=(1,0,0;1.5708rad)
  sketch-geometry (49):
    g0: LineSegment StartX=1e-16 StartY=3.5 StartZ=0 EndX=-3.03109 EndY=1.75 EndZ=0
    g1: LineSegment StartX=-3.03109 StartY=1.75 StartZ=0 EndX=-3.03109 EndY=-1.75 EndZ=0
    g2: LineSegment StartX=-3.03109 StartY=-1.75 StartZ=0 EndX=-1e-16 EndY=-3.5 EndZ=0
    g3: LineSegment StartX=-1e-16 StartY=-3.5 StartZ=0 EndX=3.03109 EndY=-1.75 EndZ=0
    g4: LineSegment StartX=3.03109 StartY=-1.75 StartZ=0 EndX=3.03109 EndY=1.75 EndZ=0
    g5: LineSegment StartX=3.03109 StartY=1.75 StartZ=0 EndX=1e-16 EndY=3.5 EndZ=0
    g6: Circle [constr] CenterX=0 CenterY=0 CenterZ=0 NormalX=0 NormalY=0 NormalZ=1 AngleXU=0 Radius=3.5
    g7: LineSegment StartX=4.96892 StartY=-1.75002 StartZ=0 EndX=8.00002 EndY=-3.5 EndZ=0
    g8: LineSegment StartX=8.00002 StartY=-3.5 StartZ=0 EndX=11.0311 EndY=-1.74998 EndZ=0
    g9: LineSegment StartX=11.0311 StartY=-1.74998 StartZ=0 EndX=11.0311 EndY=1.75002 EndZ=0
    g10: LineSegment StartX=11.0311 StartY=1.75002 StartZ=0 EndX=7.99998 EndY=3.5 EndZ=0
    g11: LineSegment StartX=7.99998 StartY=3.5 StartZ=0 EndX=4.9689 EndY=1.74998 EndZ=0
    g12: LineSegment StartX=4.9689 StartY=1.74998 StartZ=0 EndX=4.96892 EndY=-1.75002 EndZ=0
    g13: Circle [constr] CenterX=8 CenterY=0 CenterZ=0 NormalX=0 NormalY=0 NormalZ=1 AngleXU=0 Radius=3.5
    g14: LineSegment StartX=4.03109 StartY=3.5 StartZ=0 EndX=7.06218 EndY=5.25 EndZ=0
    g15: LineSegment StartX=7.06218 StartY=5.25 StartZ=0 EndX=7.06218 EndY=8.75 EndZ=0
    g16: LineSegment StartX=7.06218 StartY=8.75 StartZ=0 EndX=4.03109 EndY=10.5 EndZ=0
    g17: LineSegment StartX=4.03109 StartY=10.5 StartZ=0 EndX=1 EndY=8.75 EndZ=0
    g18: LineSegment StartX=1 StartY=8.75 StartZ=0 EndX=1 EndY=5.25 EndZ=0
    g19: LineSegment StartX=1 StartY=5.25 StartZ=0 EndX=4.03109 EndY=3.5 EndZ=0
    g20: Circle [constr] CenterX=4.03109 CenterY=7 CenterZ=0 NormalX=0 NormalY=0 NormalZ=1 AngleXU=0 Radius=3.5
    g21: LineSegment StartX=-1 StartY=5.25 StartZ=0 EndX=-1 EndY=8.75 EndZ=0
    g22: LineSegment StartX=-1 StartY=8.75 StartZ=0 EndX=-4.03109 EndY=10.5 EndZ=0
    g23: LineSegment StartX=-4.03109 StartY=10.5 StartZ=0 EndX=-7.06218 EndY=8.75 EndZ=0
    g24: LineSegment StartX=-7.06218 StartY=8.75 StartZ=0 EndX=-7.06218 EndY=5.25 EndZ=0
    g25: LineSegment StartX=-7.06218 StartY=5.25 StartZ=0 EndX=-4.03109 EndY=3.5 EndZ=0
    g26: LineSegment StartX=-4.03109 StartY=3.5 StartZ=0 EndX=-1 EndY=5.25 EndZ=0
    g27: Circle [constr] CenterX=-4.03109 CenterY=7 CenterZ=0 NormalX=0 NormalY=0 NormalZ=1 AngleXU=0 Radius=3.5
    g28: LineSegment StartX=-4.96891 StartY=-1.75 StartZ=0 EndX=-4.96891 EndY=1.75 EndZ=0
    g29: LineSegment StartX=-4.96891 StartY=1.75 StartZ=0 EndX=-8 EndY=3.5 EndZ=0
    g30: LineSegment StartX=-8 StartY=3.5 StartZ=0 EndX=-11.0311 EndY=1.75 EndZ=0
    g31: LineSegment StartX=-11.0311 StartY=1.75 StartZ=0 EndX=-11.0311 EndY=-1.75 EndZ=0
    g32: LineSegment StartX=-11.0311 StartY=-1.75 StartZ=0 EndX=-8 EndY=-3.5 EndZ=0
    g33: LineSegment StartX=-8 StartY=-3.5 StartZ=0 EndX=-4.96891 EndY=-1.75 EndZ=0
    g34: Circle [constr] CenterX=-8 CenterY=0 CenterZ=0 NormalX=0 NormalY=0 NormalZ=1 AngleXU=0 Radius=3.5
    g35: LineSegment StartX=-4.03109 StartY=-3.5 StartZ=0 EndX=-7.06218 EndY=-5.25 EndZ=0
    g36: LineSegment StartX=-7.06218 StartY=-5.25 StartZ=0 EndX=-7.06218 EndY=-8.75 EndZ=0
    g37: LineSegment StartX=-7.06218 StartY=-8.75 StartZ=0 EndX=-4.03109 EndY=-10.5 EndZ=0
    g38: LineSegment StartX=-4.03109 StartY=-10.5 StartZ=0 EndX=-1 EndY=-8.75 EndZ=0
    g39: LineSegment StartX=-1 StartY=-8.75 StartZ=0 EndX=-1 EndY=-5.25 EndZ=0
    g40: LineSegment StartX=-1 StartY=-5.25 StartZ=0 EndX=-4.03109 EndY=-3.5 EndZ=0
    g41: Circle [constr] CenterX=-4.03109 CenterY=-7 CenterZ=0 NormalX=0 NormalY=0 NormalZ=1 AngleXU=0 Radius=3.5
    g42: LineSegment StartX=4.03109 StartY=-3.5 StartZ=0 EndX=1 EndY=-5.25 EndZ=0
    g43: LineSegment StartX=1 StartY=-5.25 StartZ=0 EndX=1 EndY=-8.75 EndZ=0
    g44: LineSegment StartX=1 StartY=-8.75 StartZ=0 EndX=4.03109 EndY=-10.5 EndZ=0
    g45: LineSegment StartX=4.03109 StartY=-10.5 StartZ=0 EndX=7.06218 EndY=-8.75 EndZ=0
    g46: LineSegment StartX=7.06218 StartY=-8.75 StartZ=0 EndX=7.06218 EndY=-5.25 EndZ=0
    g47: LineSegment StartX=7.06218 StartY=-5.25 StartZ=0 EndX=4.03109 EndY=-3.5 EndZ=0
    g48: Circle [constr] CenterX=4.03109 CenterY=-7 CenterZ=0 NormalX=0 NormalY=0 NormalZ=1 AngleXU=0 Radius=3.5
  constraints (117):
    c: Coincident(g0,g1)
    c: Coincident(g1,g2)
    c: Coincident(g2,g3)
    c: Coincident(g3,g4)
    c: Coincident(g4,g5)
    c: Coincident(g5,g0)
    c: Equal(g0, g1-g5) x5
    c: PointOnObject(g0,g6)
    c: PointOnObject(g1,g6)
    c: PointOnObject(g2,g6)
    c: PointOnObject(g3,g6)
    c: PointOnObject(g4,g6)
    c: PointOnObject(g5,g6)
    c: Coincident(g6,g-1)
    c: Diameter(g6) = 7
    c: PointOnObject(g0,g-2)
    c: Coincident(g7,g8)
    c: Coincident(g8,g9)
    c: Coincident(g9,g10)
    c: Coincident(g10,g11)
    c: Coincident(g11,g12)
    c: Coincident(g12,g7)
    c: Equal(g7, g8-g12) x5
    c: PointOnObject(g7,g13)
    c: PointOnObject(g8,g13)
    c: PointOnObject(g9,g13)
    c: PointOnObject(g10,g13)
    c: PointOnObject(g11,g13)
    c: PointOnObject(g12,g13)
    c: PointOnObject(g13,g-1)
    c: Diameter(g13) = 7
    c: Distance(g6,g13) = 8
    c: Horizontal(g0,g10)
    c: Coincident(g14,g15)
    c: Coincident(g15,g16)
    c: Coincident(g16,g17)
    c: Coincident(g17,g18)
    c: Coincident(g18,g19)
    c: Coincident(g19,g14)
    c: Equal(g14, g15-g19) x5
    c: PointOnObject(g14,g20)
    c: PointOnObject(g15,g20)
    c: PointOnObject(g16,g20)
    c: PointOnObject(g17,g20)
    c: PointOnObject(g18,g20)
    c: PointOnObject(g19,g20)
    c: Diameter(g20) = 7
    c: DistanceY(g-1,g20) = 7
    c: Vertical(g18)
    c: Distance(g17,g-2) = 1
    c: Coincident(g21,g22)
    c: Coincident(g22,g23)
    c: Coincident(g23,g24)
    c: Coincident(g24,g25)
    c: Coincident(g25,g26)
    c: Coincident(g26,g21)
    c: Equal(g21, g22-g26) x5
    c: PointOnObject(g21,g27)
    c: PointOnObject(g22,g27)
    c: PointOnObject(g23,g27)
    c: PointOnObject(g24,g27)
    c: PointOnObject(g25,g27)
    c: PointOnObject(g26,g27)
    c: Diameter(g27) = 7
    c: DistanceY(g-1,g27) = 7
    c: DistanceX(g21,g-1) = 1
    c: Vertical(g21)
    c: Coincident(g28,g29)
    c: Coincident(g29,g30)
    c: Coincident(g30,g31)
    c: Coincident(g31,g32)
    c: Coincident(g32,g33)
    c: Coincident(g33,g28)
    c: Equal(g28, g29-g33) x5
    c: PointOnObject(g28,g34)
    c: PointOnObject(g29,g34)
    c: PointOnObject(g30,g34)
    c: PointOnObject(g31,g34)
    c: PointOnObject(g32,g34)
    c: PointOnObject(g33,g34)
    c: PointOnObject(g34,g-1)
    c: Diameter(g34) = 7
    c: Vertical(g31)
    c: DistanceX(g34,g-1) = 8
    c: Coincident(g35,g36)
    c: Coincident(g36,g37)
    c: Coincident(g37,g38)
    c: Coincident(g38,g39)
    c: Coincident(g39,g40)
    c: Coincident(g40,g35)
    c: Equal(g35, g36-g40) x5
    c: PointOnObject(g35,g41)
    c: PointOnObject(g36,g41)
    c: PointOnObject(g37,g41)
    c: PointOnObject(g38,g41)
    c: PointOnObject(g39,g41)
    c: PointOnObject(g40,g41)
    c: Coincident(g42,g43)
    c: Coincident(g43,g44)
    c: Coincident(g44,g45)
    c: Coincident(g45,g46)
    c: Coincident(g46,g47)
    c: Coincident(g47,g42)
    c: Equal(g42, g43-g47) x5
    c: PointOnObject(g42,g48)
    c: PointOnObject(g43,g48)
    c: PointOnObject(g44,g48)
    c: PointOnObject(g45,g48)
    c: PointOnObject(g46,g48)
    c: PointOnObject(g47,g48)
    c: Equal(g41,g48)
    c: Diameter(g41) = 7
    c: Vertical(g39)
    c: Vertical(g43)
    c: Distance(g-2,g39) = 1
    c: Symmetric(g38,g43,g-2)
    c: Distance(g41,g-1) = 7
FEATURE [Part::Extrusion] Extrude593  label="hex195"
  Base = -> Sketch602
  Dir = (0,-1,2e-16)
  DirMode = 2
  FaceMakerClass = Part::FaceMakerBullseye
  FaceMakerMode = 3
  LengthFwd = 10
  LengthRev = 0
  Placement = pos=(-64,0,14) rot=(0,0,1;0rad)
  Solid = true
  Symmetric = false
FEATURE [Sketcher::SketchObject] Sketch603
  ArcFitTolerance = 1e-06
  FullyConstrained = true
  MakeInternals = false
  Placement = pos=(0,0,0) rot=(1,0,0;1.5708rad)
  sketch-geometry (49):
    g0: LineSegment StartX=1e-16 StartY=3.5 StartZ=0 EndX=-3.03109 EndY=1.75 EndZ=0
    g1: LineSegment StartX=-3.03109 StartY=1.75 StartZ=0 EndX=-3.03109 EndY=-1.75 EndZ=0
    g2: LineSegment StartX=-3.03109 StartY=-1.75 StartZ=0 EndX=-1e-16 EndY=-3.5 EndZ=0
    g3: LineSegment StartX=-1e-16 StartY=-3.5 StartZ=0 EndX=3.03109 EndY=-1.75 EndZ=0
    g4: LineSegment StartX=3.03109 StartY=-1.75 StartZ=0 EndX=3.03109 EndY=1.75 EndZ=0
    g5: LineSegment StartX=3.03109 StartY=1.75 StartZ=0 EndX=1e-16 EndY=3.5 EndZ=0
    g6: Circle [constr] CenterX=0 CenterY=0 CenterZ=0 NormalX=0 NormalY=0 NormalZ=1 AngleXU=0 Radius=3.5
    g7: LineSegment StartX=4.96892 StartY=-1.75002 StartZ=0 EndX=8.00002 EndY=-3.5 EndZ=0
    g8: LineSegment StartX=8.00002 StartY=-3.5 StartZ=0 EndX=11.0311 EndY=-1.74998 EndZ=0
    g9: LineSegment StartX=11.0311 StartY=-1.74998 StartZ=0 EndX=11.0311 EndY=1.75002 EndZ=0
    g10: LineSegment StartX=11.0311 StartY=1.75002 StartZ=0 EndX=7.99998 EndY=3.5 EndZ=0
    g11: LineSegment StartX=7.99998 StartY=3.5 StartZ=0 EndX=4.9689 EndY=1.74998 EndZ=0
    g12: LineSegment StartX=4.9689 StartY=1.74998 StartZ=0 EndX=4.96892 EndY=-1.75002 EndZ=0
    g13: Circle [constr] CenterX=8 CenterY=0 CenterZ=0 NormalX=0 NormalY=0 NormalZ=1 AngleXU=0 Radius=3.5
    g14: LineSegment StartX=4.03109 StartY=3.5 StartZ=0 EndX=7.06218 EndY=5.25 EndZ=0
    g15: LineSegment StartX=7.06218 StartY=5.25 StartZ=0 EndX=7.06218 EndY=8.75 EndZ=0
    g16: LineSegment StartX=7.06218 StartY=8.75 StartZ=0 EndX=4.03109 EndY=10.5 EndZ=0
    g17: LineSegment StartX=4.03109 StartY=10.5 StartZ=0 EndX=1 EndY=8.75 EndZ=0
    g18: LineSegment StartX=1 StartY=8.75 StartZ=0 EndX=1 EndY=5.25 EndZ=0
    g19: LineSegment StartX=1 StartY=5.25 StartZ=0 EndX=4.03109 EndY=3.5 EndZ=0
    g20: Circle [constr] CenterX=4.03109 CenterY=7 CenterZ=0 NormalX=0 NormalY=0 NormalZ=1 AngleXU=0 Radius=3.5
    g21: LineSegment StartX=-1 StartY=5.25 StartZ=0 EndX=-1 EndY=8.75 EndZ=0
    g22: LineSegment StartX=-1 StartY=8.75 StartZ=0 EndX=-4.03109 EndY=10.5 EndZ=0
    g23: LineSegment StartX=-4.03109 StartY=10.5 StartZ=0 EndX=-7.06218 EndY=8.75 EndZ=0
    g24: LineSegment StartX=-7.06218 StartY=8.75 StartZ=0 EndX=-7.06218 EndY=5.25 EndZ=0
    g25: LineSegment StartX=-7.06218 StartY=5.25 StartZ=0 EndX=-4.03109 EndY=3.5 EndZ=0
    g26: LineSegment StartX=-4.03109 StartY=3.5 StartZ=0 EndX=-1 EndY=5.25 EndZ=0
    g27: Circle [constr] CenterX=-4.03109 CenterY=7 CenterZ=0 NormalX=0 NormalY=0 NormalZ=1 AngleXU=0 Radius=3.5
    g28: LineSegment StartX=-4.96891 StartY=-1.75 StartZ=0 EndX=-4.96891 EndY=1.75 EndZ=0
    g29: LineSegment StartX=-4.96891 StartY=1.75 StartZ=0 EndX=-8 EndY=3.5 EndZ=0
    g30: LineSegment StartX=-8 StartY=3.5 StartZ=0 EndX=-11.0311 EndY=1.75 EndZ=0
    g31: LineSegment StartX=-11.0311 StartY=1.75 StartZ=0 EndX=-11.0311 EndY=-1.75 EndZ=0
    g32: LineSegment StartX=-11.0311 StartY=-1.75 StartZ=0 EndX=-8 EndY=-3.5 EndZ=0
    g33: LineSegment StartX=-8 StartY=-3.5 StartZ=0 EndX=-4.96891 EndY=-1.75 EndZ=0
    g34: Circle [constr] CenterX=-8 CenterY=0 CenterZ=0 NormalX=0 NormalY=0 NormalZ=1 AngleXU=0 Radius=3.5
    g35: LineSegment StartX=-4.03109 StartY=-3.5 StartZ=0 EndX=-7.06218 EndY=-5.25 EndZ=0
    g36: LineSegment StartX=-7.06218 StartY=-5.25 StartZ=0 EndX=-7.06218 EndY=-8.75 EndZ=0
    g37: LineSegment StartX=-7.06218 StartY=-8.75 StartZ=0 EndX=-4.03109 EndY=-10.5 EndZ=0
    g38: LineSegment StartX=-4.03109 StartY=-10.5 StartZ=0 EndX=-1 EndY=-8.75 EndZ=0
    g39: LineSegment StartX=-1 StartY=-8.75 StartZ=0 EndX=-1 EndY=-5.25 EndZ=0
    g40: LineSegment StartX=-1 StartY=-5.25 StartZ=0 EndX=-4.03109 EndY=-3.5 EndZ=0
    g41: Circle [constr] CenterX=-4.03109 CenterY=-7 CenterZ=0 NormalX=0 NormalY=0 NormalZ=1 AngleXU=0 Radius=3.5
    g42: LineSegment StartX=4.03109 StartY=-3.5 StartZ=0 EndX=1 EndY=-5.25 EndZ=0
    g43: LineSegment StartX=1 StartY=-5.25 StartZ=0 EndX=1 EndY=-8.75 EndZ=0
    g44: LineSegment StartX=1 StartY=-8.75 StartZ=0 EndX=4.03109 EndY=-10.5 EndZ=0
    g45: LineSegment StartX=4.03109 StartY=-10.5 StartZ=0 EndX=7.06218 EndY=-8.75 EndZ=0
    g46: LineSegment StartX=7.06218 StartY=-8.75 StartZ=0 EndX=7.06218 EndY=-5.25 EndZ=0
    g47: LineSegment StartX=7.06218 StartY=-5.25 StartZ=0 EndX=4.03109 EndY=-3.5 EndZ=0
    g48: Circle [constr] CenterX=4.03109 CenterY=-7 CenterZ=0 NormalX=0 NormalY=0 NormalZ=1 AngleXU=0 Radius=3.5
  constraints (117):
    c: Coincident(g0,g1)
    c: Coincident(g1,g2)
    c: Coincident(g2,g3)
    c: Coincident(g3,g4)
    c: Coincident(g4,g5)
    c: Coincident(g5,g0)
    c: Equal(g0, g1-g5) x5
    c: PointOnObject(g0,g6)
    c: PointOnObject(g1,g6)
    c: PointOnObject(g2,g6)
    c: PointOnObject(g3,g6)
    c: PointOnObject(g4,g6)
    c: PointOnObject(g5,g6)
    c: Coincident(g6,g-1)
    c: Diameter(g6) = 7
    c: PointOnObject(g0,g-2)
    c: Coincident(g7,g8)
    c: Coincident(g8,g9)
    c: Coincident(g9,g10)
    c: Coincident(g10,g11)
    c: Coincident(g11,g12)
    c: Coincident(g12,g7)
    c: Equal(g7, g8-g12) x5
    c: PointOnObject(g7,g13)
    c: PointOnObject(g8,g13)
    c: PointOnObject(g9,g13)
    c: PointOnObject(g10,g13)
    c: PointOnObject(g11,g13)
    c: PointOnObject(g12,g13)
    c: PointOnObject(g13,g-1)
    c: Diameter(g13) = 7
    c: Distance(g6,g13) = 8
    c: Horizontal(g0,g10)
    c: Coincident(g14,g15)
    c: Coincident(g15,g16)
    c: Coincident(g16,g17)
    c: Coincident(g17,g18)
    c: Coincident(g18,g19)
    c: Coincident(g19,g14)
    c: Equal(g14, g15-g19) x5
    c: PointOnObject(g14,g20)
    c: PointOnObject(g15,g20)
    c: PointOnObject(g16,g20)
    c: PointOnObject(g17,g20)
    c: PointOnObject(g18,g20)
    c: PointOnObject(g19,g20)
    c: Diameter(g20) = 7
    c: DistanceY(g-1,g20) = 7
    c: Vertical(g18)
    c: Distance(g17,g-2) = 1
    c: Coincident(g21,g22)
    c: Coincident(g22,g23)
    c: Coincident(g23,g24)
    c: Coincident(g24,g25)
    c: Coincident(g25,g26)
    c: Coincident(g26,g21)
    c: Equal(g21, g22-g26) x5
    c: PointOnObject(g21,g27)
    c: PointOnObject(g22,g27)
    c: PointOnObject(g23,g27)
    c: PointOnObject(g24,g27)
    c: PointOnObject(g25,g27)
    c: PointOnObject(g26,g27)
    c: Diameter(g27) = 7
    c: DistanceY(g-1,g27) = 7
    c: DistanceX(g21,g-1) = 1
    c: Vertical(g21)
    c: Coincident(g28,g29)
    c: Coincident(g29,g30)
    c: Coincident(g30,g31)
    c: Coincident(g31,g32)
    c: Coincident(g32,g33)
    c: Coincident(g33,g28)
    c: Equal(g28, g29-g33) x5
    c: PointOnObject(g28,g34)
    c: PointOnObject(g29,g34)
    c: PointOnObject(g30,g34)
    c: PointOnObject(g31,g34)
    c: PointOnObject(g32,g34)
    c: PointOnObject(g33,g34)
    c: PointOnObject(g34,g-1)
    c: Diameter(g34) = 7
    c: Vertical(g31)
    c: DistanceX(g34,g-1) = 8
    c: Coincident(g35,g36)
    c: Coincident(g36,g37)
    c: Coincident(g37,g38)
    c: Coincident(g38,g39)
    c: Coincident(g39,g40)
    c: Coincident(g40,g35)
    c: Equal(g35, g36-g40) x5
    c: PointOnObject(g35,g41)
    c: PointOnObject(g36,g41)
    c: PointOnObject(g37,g41)
    c: PointOnObject(g38,g41)
    c: PointOnObject(g39,g41)
    c: PointOnObject(g40,g41)
    c: Coincident(g42,g43)
    c: Coincident(g43,g44)
    c: Coincident(g44,g45)
    c: Coincident(g45,g46)
    c: Coincident(g46,g47)
    c: Coincident(g47,g42)
    c: Equal(g42, g43-g47) x5
    c: PointOnObject(g42,g48)
    c: PointOnObject(g43,g48)
    c: PointOnObject(g44,g48)
    c: PointOnObject(g45,g48)
    c: PointOnObject(g46,g48)
    c: PointOnObject(g47,g48)
    c: Equal(g41,g48)
    c: Diameter(g41) = 7
    c: Vertical(g39)
    c: Vertical(g43)
    c: Distance(g-2,g39) = 1
    c: Symmetric(g38,g43,g-2)
    c: Distance(g41,g-1) = 7
FEATURE [Part::Extrusion] Extrude594  label="hex196"
  Base = -> Sketch603
  Dir = (0,-1,2e-16)
  DirMode = 2
  FaceMakerClass = Part::FaceMakerBullseye
  FaceMakerMode = 3
  LengthFwd = 10
  LengthRev = 0
  Placement = pos=(-64,0,-14) rot=(0,0,1;0rad)
  Solid = true
  Symmetric = false
FEATURE [Sketcher::SketchObject] Sketch604
  ArcFitTolerance = 1e-06
  FullyConstrained = true
  MakeInternals = false
  Placement = pos=(0,0,0) rot=(1,0,0;1.5708rad)
  sketch-geometry (49):
    g0: LineSegment StartX=1e-16 StartY=3.5 StartZ=0 EndX=-3.03109 EndY=1.75 EndZ=0
    g1: LineSegment StartX=-3.03109 StartY=1.75 StartZ=0 EndX=-3.03109 EndY=-1.75 EndZ=0
    g2: LineSegment StartX=-3.03109 StartY=-1.75 StartZ=0 EndX=-1e-16 EndY=-3.5 EndZ=0
    g3: LineSegment StartX=-1e-16 StartY=-3.5 StartZ=0 EndX=3.03109 EndY=-1.75 EndZ=0
    g4: LineSegment StartX=3.03109 StartY=-1.75 StartZ=0 EndX=3.03109 EndY=1.75 EndZ=0
    g5: LineSegment StartX=3.03109 StartY=1.75 StartZ=0 EndX=1e-16 EndY=3.5 EndZ=0
    g6: Circle [constr] CenterX=0 CenterY=0 CenterZ=0 NormalX=0 NormalY=0 NormalZ=1 AngleXU=0 Radius=3.5
    g7: LineSegment StartX=4.96892 StartY=-1.75002 StartZ=0 EndX=8.00002 EndY=-3.5 EndZ=0
    g8: LineSegment StartX=8.00002 StartY=-3.5 StartZ=0 EndX=11.0311 EndY=-1.74998 EndZ=0
    g9: LineSegment StartX=11.0311 StartY=-1.74998 StartZ=0 EndX=11.0311 EndY=1.75002 EndZ=0
    g10: LineSegment StartX=11.0311 StartY=1.75002 StartZ=0 EndX=7.99998 EndY=3.5 EndZ=0
    g11: LineSegment StartX=7.99998 StartY=3.5 StartZ=0 EndX=4.9689 EndY=1.74998 EndZ=0
    g12: LineSegment StartX=4.9689 StartY=1.74998 StartZ=0 EndX=4.96892 EndY=-1.75002 EndZ=0
    g13: Circle [constr] CenterX=8 CenterY=0 CenterZ=0 NormalX=0 NormalY=0 NormalZ=1 AngleXU=0 Radius=3.5
    g14: LineSegment StartX=4.03109 StartY=3.5 StartZ=0 EndX=7.06218 EndY=5.25 EndZ=0
    g15: LineSegment StartX=7.06218 StartY=5.25 StartZ=0 EndX=7.06218 EndY=8.75 EndZ=0
    g16: LineSegment StartX=7.06218 StartY=8.75 StartZ=0 EndX=4.03109 EndY=10.5 EndZ=0
    g17: LineSegment StartX=4.03109 StartY=10.5 StartZ=0 EndX=1 EndY=8.75 EndZ=0
    g18: LineSegment StartX=1 StartY=8.75 StartZ=0 EndX=1 EndY=5.25 EndZ=0
    g19: LineSegment StartX=1 StartY=5.25 StartZ=0 EndX=4.03109 EndY=3.5 EndZ=0
    g20: Circle [constr] CenterX=4.03109 CenterY=7 CenterZ=0 NormalX=0 NormalY=0 NormalZ=1 AngleXU=0 Radius=3.5
    g21: LineSegment StartX=-1 StartY=5.25 StartZ=0 EndX=-1 EndY=8.75 EndZ=0
    g22: LineSegment StartX=-1 StartY=8.75 StartZ=0 EndX=-4.03109 EndY=10.5 EndZ=0
    g23: LineSegment StartX=-4.03109 StartY=10.5 StartZ=0 EndX=-7.06218 EndY=8.75 EndZ=0
    g24: LineSegment StartX=-7.06218 StartY=8.75 StartZ=0 EndX=-7.06218 EndY=5.25 EndZ=0
    g25: LineSegment StartX=-7.06218 StartY=5.25 StartZ=0 EndX=-4.03109 EndY=3.5 EndZ=0
    g26: LineSegment StartX=-4.03109 StartY=3.5 StartZ=0 EndX=-1 EndY=5.25 EndZ=0
    g27: Circle [constr] CenterX=-4.03109 CenterY=7 CenterZ=0 NormalX=0 NormalY=0 NormalZ=1 AngleXU=0 Radius=3.5
    g28: LineSegment StartX=-4.96891 StartY=-1.75 StartZ=0 EndX=-4.96891 EndY=1.75 EndZ=0
    g29: LineSegment StartX=-4.96891 StartY=1.75 StartZ=0 EndX=-8 EndY=3.5 EndZ=0
    g30: LineSegment StartX=-8 StartY=3.5 StartZ=0 EndX=-11.0311 EndY=1.75 EndZ=0
    g31: LineSegment StartX=-11.0311 StartY=1.75 StartZ=0 EndX=-11.0311 EndY=-1.75 EndZ=0
    g32: LineSegment StartX=-11.0311 StartY=-1.75 StartZ=0 EndX=-8 EndY=-3.5 EndZ=0
    g33: LineSegment StartX=-8 StartY=-3.5 StartZ=0 EndX=-4.96891 EndY=-1.75 EndZ=0
    g34: Circle [constr] CenterX=-8 CenterY=0 CenterZ=0 NormalX=0 NormalY=0 NormalZ=1 AngleXU=0 Radius=3.5
    g35: LineSegment StartX=-4.03109 StartY=-3.5 StartZ=0 EndX=-7.06218 EndY=-5.25 EndZ=0
    g36: LineSegment StartX=-7.06218 StartY=-5.25 StartZ=0 EndX=-7.06218 EndY=-8.75 EndZ=0
    g37: LineSegment StartX=-7.06218 StartY=-8.75 StartZ=0 EndX=-4.03109 EndY=-10.5 EndZ=0
    g38: LineSegment StartX=-4.03109 StartY=-10.5 StartZ=0 EndX=-1 EndY=-8.75 EndZ=0
    g39: LineSegment StartX=-1 StartY=-8.75 StartZ=0 EndX=-1 EndY=-5.25 EndZ=0
    g40: LineSegment StartX=-1 StartY=-5.25 StartZ=0 EndX=-4.03109 EndY=-3.5 EndZ=0
    g41: Circle [constr] CenterX=-4.03109 CenterY=-7 CenterZ=0 NormalX=0 NormalY=0 NormalZ=1 AngleXU=0 Radius=3.5
    g42: LineSegment StartX=4.03109 StartY=-3.5 StartZ=0 EndX=1 EndY=-5.25 EndZ=0
    g43: LineSegment StartX=1 StartY=-5.25 StartZ=0 EndX=1 EndY=-8.75 EndZ=0
    g44: LineSegment StartX=1 StartY=-8.75 StartZ=0 EndX=4.03109 EndY=-10.5 EndZ=0
    g45: LineSegment StartX=4.03109 StartY=-10.5 StartZ=0 EndX=7.06218 EndY=-8.75 EndZ=0
    g46: LineSegment StartX=7.06218 StartY=-8.75 StartZ=0 EndX=7.06218 EndY=-5.25 EndZ=0
    g47: LineSegment StartX=7.06218 StartY=-5.25 StartZ=0 EndX=4.03109 EndY=-3.5 EndZ=0
    g48: Circle [constr] CenterX=4.03109 CenterY=-7 CenterZ=0 NormalX=0 NormalY=0 NormalZ=1 AngleXU=0 Radius=3.5
  constraints (117):
    c: Coincident(g0,g1)
    c: Coincident(g1,g2)
    c: Coincident(g2,g3)
    c: Coincident(g3,g4)
    c: Coincident(g4,g5)
    c: Coincident(g5,g0)
    c: Equal(g0, g1-g5) x5
    c: PointOnObject(g0,g6)
    c: PointOnObject(g1,g6)
    c: PointOnObject(g2,g6)
    c: PointOnObject(g3,g6)
    c: PointOnObject(g4,g6)
    c: PointOnObject(g5,g6)
    c: Coincident(g6,g-1)
    c: Diameter(g6) = 7
    c: PointOnObject(g0,g-2)
    c: Coincident(g7,g8)
    c: Coincident(g8,g9)
    c: Coincident(g9,g10)
    c: Coincident(g10,g11)
    c: Coincident(g11,g12)
    c: Coincident(g12,g7)
    c: Equal(g7, g8-g12) x5
    c: PointOnObject(g7,g13)
    c: PointOnObject(g8,g13)
    c: PointOnObject(g9,g13)
    c: PointOnObject(g10,g13)
    c: PointOnObject(g11,g13)
    c: PointOnObject(g12,g13)
    c: PointOnObject(g13,g-1)
    c: Diameter(g13) = 7
    c: Distance(g6,g13) = 8
    c: Horizontal(g0,g10)
    c: Coincident(g14,g15)
    c: Coincident(g15,g16)
    c: Coincident(g16,g17)
    c: Coincident(g17,g18)
    c: Coincident(g18,g19)
    c: Coincident(g19,g14)
    c: Equal(g14, g15-g19) x5
    c: PointOnObject(g14,g20)
    c: PointOnObject(g15,g20)
    c: PointOnObject(g16,g20)
    c: PointOnObject(g17,g20)
    c: PointOnObject(g18,g20)
    c: PointOnObject(g19,g20)
    c: Diameter(g20) = 7
    c: DistanceY(g-1,g20) = 7
    c: Vertical(g18)
    c: Distance(g17,g-2) = 1
    c: Coincident(g21,g22)
    c: Coincident(g22,g23)
    c: Coincident(g23,g24)
    c: Coincident(g24,g25)
    c: Coincident(g25,g26)
    c: Coincident(g26,g21)
    c: Equal(g21, g22-g26) x5
    c: PointOnObject(g21,g27)
    c: PointOnObject(g22,g27)
    c: PointOnObject(g23,g27)
    c: PointOnObject(g24,g27)
    c: PointOnObject(g25,g27)
    c: PointOnObject(g26,g27)
    c: Diameter(g27) = 7
    c: DistanceY(g-1,g27) = 7
    c: DistanceX(g21,g-1) = 1
    c: Vertical(g21)
    c: Coincident(g28,g29)
    c: Coincident(g29,g30)
    c: Coincident(g30,g31)
    c: Coincident(g31,g32)
    c: Coincident(g32,g33)
    c: Coincident(g33,g28)
    c: Equal(g28, g29-g33) x5
    c: PointOnObject(g28,g34)
    c: PointOnObject(g29,g34)
    c: PointOnObject(g30,g34)
    c: PointOnObject(g31,g34)
    c: PointOnObject(g32,g34)
    c: PointOnObject(g33,g34)
    c: PointOnObject(g34,g-1)
    c: Diameter(g34) = 7
    c: Vertical(g31)
    c: DistanceX(g34,g-1) = 8
    c: Coincident(g35,g36)
    c: Coincident(g36,g37)
    c: Coincident(g37,g38)
    c: Coincident(g38,g39)
    c: Coincident(g39,g40)
    c: Coincident(g40,g35)
    c: Equal(g35, g36-g40) x5
    c: PointOnObject(g35,g41)
    c: PointOnObject(g36,g41)
    c: PointOnObject(g37,g41)
    c: PointOnObject(g38,g41)
    c: PointOnObject(g39,g41)
    c: PointOnObject(g40,g41)
    c: Coincident(g42,g43)
    c: Coincident(g43,g44)
    c: Coincident(g44,g45)
    c: Coincident(g45,g46)
    c: Coincident(g46,g47)
    c: Coincident(g47,g42)
    c: Equal(g42, g43-g47) x5
    c: PointOnObject(g42,g48)
    c: PointOnObject(g43,g48)
    c: PointOnObject(g44,g48)
    c: PointOnObject(g45,g48)
    c: PointOnObject(g46,g48)
    c: PointOnObject(g47,g48)
    c: Equal(g41,g48)
    c: Diameter(g41) = 7
    c: Vertical(g39)
    c: Vertical(g43)
    c: Distance(g-2,g39) = 1
    c: Symmetric(g38,g43,g-2)
    c: Distance(g41,g-1) = 7
FEATURE [Part::Extrusion] Extrude595  label="hex197"
  Base = -> Sketch604
  Dir = (0,-1,2e-16)
  DirMode = 2
  FaceMakerClass = Part::FaceMakerBullseye
  FaceMakerMode = 3
  LengthFwd = 10
  LengthRev = 0
  Placement = pos=(-48,0,-28) rot=(0,0,1;0rad)
  Solid = true
  Symmetric = false
FEATURE [Sketcher::SketchObject] Sketch605
  ArcFitTolerance = 1e-06
  FullyConstrained = true
  MakeInternals = false
  Placement = pos=(0,0,0) rot=(1,0,0;1.5708rad)
  sketch-geometry (49):
    g0: LineSegment StartX=1e-16 StartY=3.5 StartZ=0 EndX=-3.03109 EndY=1.75 EndZ=0
    g1: LineSegment StartX=-3.03109 StartY=1.75 StartZ=0 EndX=-3.03109 EndY=-1.75 EndZ=0
    g2: LineSegment StartX=-3.03109 StartY=-1.75 StartZ=0 EndX=-1e-16 EndY=-3.5 EndZ=0
    g3: LineSegment StartX=-1e-16 StartY=-3.5 StartZ=0 EndX=3.03109 EndY=-1.75 EndZ=0
    g4: LineSegment StartX=3.03109 StartY=-1.75 StartZ=0 EndX=3.03109 EndY=1.75 EndZ=0
    g5: LineSegment StartX=3.03109 StartY=1.75 StartZ=0 EndX=1e-16 EndY=3.5 EndZ=0
    g6: Circle [constr] CenterX=0 CenterY=0 CenterZ=0 NormalX=0 NormalY=0 NormalZ=1 AngleXU=0 Radius=3.5
    g7: LineSegment StartX=4.96892 StartY=-1.75002 StartZ=0 EndX=8.00002 EndY=-3.5 EndZ=0
    g8: LineSegment StartX=8.00002 StartY=-3.5 StartZ=0 EndX=11.0311 EndY=-1.74998 EndZ=0
    g9: LineSegment StartX=11.0311 StartY=-1.74998 StartZ=0 EndX=11.0311 EndY=1.75002 EndZ=0
    g10: LineSegment StartX=11.0311 StartY=1.75002 StartZ=0 EndX=7.99998 EndY=3.5 EndZ=0
    g11: LineSegment StartX=7.99998 StartY=3.5 StartZ=0 EndX=4.9689 EndY=1.74998 EndZ=0
    g12: LineSegment StartX=4.9689 StartY=1.74998 StartZ=0 EndX=4.96892 EndY=-1.75002 EndZ=0
    g13: Circle [constr] CenterX=8 CenterY=0 CenterZ=0 NormalX=0 NormalY=0 NormalZ=1 AngleXU=0 Radius=3.5
    g14: LineSegment StartX=4.03109 StartY=3.5 StartZ=0 EndX=7.06218 EndY=5.25 EndZ=0
    g15: LineSegment StartX=7.06218 StartY=5.25 StartZ=0 EndX=7.06218 EndY=8.75 EndZ=0
    g16: LineSegment StartX=7.06218 StartY=8.75 StartZ=0 EndX=4.03109 EndY=10.5 EndZ=0
    g17: LineSegment StartX=4.03109 StartY=10.5 StartZ=0 EndX=1 EndY=8.75 EndZ=0
    g18: LineSegment StartX=1 StartY=8.75 StartZ=0 EndX=1 EndY=5.25 EndZ=0
    g19: LineSegment StartX=1 StartY=5.25 StartZ=0 EndX=4.03109 EndY=3.5 EndZ=0
    g20: Circle [constr] CenterX=4.03109 CenterY=7 CenterZ=0 NormalX=0 NormalY=0 NormalZ=1 AngleXU=0 Radius=3.5
    g21: LineSegment StartX=-1 StartY=5.25 StartZ=0 EndX=-1 EndY=8.75 EndZ=0
    g22: LineSegment StartX=-1 StartY=8.75 StartZ=0 EndX=-4.03109 EndY=10.5 EndZ=0
    g23: LineSegment StartX=-4.03109 StartY=10.5 StartZ=0 EndX=-7.06218 EndY=8.75 EndZ=0
    g24: LineSegment StartX=-7.06218 StartY=8.75 StartZ=0 EndX=-7.06218 EndY=5.25 EndZ=0
    g25: LineSegment StartX=-7.06218 StartY=5.25 StartZ=0 EndX=-4.03109 EndY=3.5 EndZ=0
    g26: LineSegment StartX=-4.03109 StartY=3.5 StartZ=0 EndX=-1 EndY=5.25 EndZ=0
    g27: Circle [constr] CenterX=-4.03109 CenterY=7 CenterZ=0 NormalX=0 NormalY=0 NormalZ=1 AngleXU=0 Radius=3.5
    g28: LineSegment StartX=-4.96891 StartY=-1.75 StartZ=0 EndX=-4.96891 EndY=1.75 EndZ=0
    g29: LineSegment StartX=-4.96891 StartY=1.75 StartZ=0 EndX=-8 EndY=3.5 EndZ=0
    g30: LineSegment StartX=-8 StartY=3.5 StartZ=0 EndX=-11.0311 EndY=1.75 EndZ=0
    g31: LineSegment StartX=-11.0311 StartY=1.75 StartZ=0 EndX=-11.0311 EndY=-1.75 EndZ=0
    g32: LineSegment StartX=-11.0311 StartY=-1.75 StartZ=0 EndX=-8 EndY=-3.5 EndZ=0
    g33: LineSegment StartX=-8 StartY=-3.5 StartZ=0 EndX=-4.96891 EndY=-1.75 EndZ=0
    g34: Circle [constr] CenterX=-8 CenterY=0 CenterZ=0 NormalX=0 NormalY=0 NormalZ=1 AngleXU=0 Radius=3.5
    g35: LineSegment StartX=-4.03109 StartY=-3.5 StartZ=0 EndX=-7.06218 EndY=-5.25 EndZ=0
    g36: LineSegment StartX=-7.06218 StartY=-5.25 StartZ=0 EndX=-7.06218 EndY=-8.75 EndZ=0
    g37: LineSegment StartX=-7.06218 StartY=-8.75 StartZ=0 EndX=-4.03109 EndY=-10.5 EndZ=0
    g38: LineSegment StartX=-4.03109 StartY=-10.5 StartZ=0 EndX=-1 EndY=-8.75 EndZ=0
    g39: LineSegment StartX=-1 StartY=-8.75 StartZ=0 EndX=-1 EndY=-5.25 EndZ=0
    g40: LineSegment StartX=-1 StartY=-5.25 StartZ=0 EndX=-4.03109 EndY=-3.5 EndZ=0
    g41: Circle [constr] CenterX=-4.03109 CenterY=-7 CenterZ=0 NormalX=0 NormalY=0 NormalZ=1 AngleXU=0 Radius=3.5
    g42: LineSegment StartX=4.03109 StartY=-3.5 StartZ=0 EndX=1 EndY=-5.25 EndZ=0
    g43: LineSegment StartX=1 StartY=-5.25 StartZ=0 EndX=1 EndY=-8.75 EndZ=0
    g44: LineSegment StartX=1 StartY=-8.75 StartZ=0 EndX=4.03109 EndY=-10.5 EndZ=0
    g45: LineSegment StartX=4.03109 StartY=-10.5 StartZ=0 EndX=7.06218 EndY=-8.75 EndZ=0
    g46: LineSegment StartX=7.06218 StartY=-8.75 StartZ=0 EndX=7.06218 EndY=-5.25 EndZ=0
    g47: LineSegment StartX=7.06218 StartY=-5.25 StartZ=0 EndX=4.03109 EndY=-3.5 EndZ=0
    g48: Circle [constr] CenterX=4.03109 CenterY=-7 CenterZ=0 NormalX=0 NormalY=0 NormalZ=1 AngleXU=0 Radius=3.5
  constraints (117):
    c: Coincident(g0,g1)
    c: Coincident(g1,g2)
    c: Coincident(g2,g3)
    c: Coincident(g3,g4)
    c: Coincident(g4,g5)
    c: Coincident(g5,g0)
    c: Equal(g0, g1-g5) x5
    c: PointOnObject(g0,g6)
    c: PointOnObject(g1,g6)
    c: PointOnObject(g2,g6)
    c: PointOnObject(g3,g6)
    c: PointOnObject(g4,g6)
    c: PointOnObject(g5,g6)
    c: Coincident(g6,g-1)
    c: Diameter(g6) = 7
    c: PointOnObject(g0,g-2)
    c: Coincident(g7,g8)
    c: Coincident(g8,g9)
    c: Coincident(g9,g10)
    c: Coincident(g10,g11)
    c: Coincident(g11,g12)
    c: Coincident(g12,g7)
    c: Equal(g7, g8-g12) x5
    c: PointOnObject(g7,g13)
    c: PointOnObject(g8,g13)
    c: PointOnObject(g9,g13)
    c: PointOnObject(g10,g13)
    c: PointOnObject(g11,g13)
    c: PointOnObject(g12,g13)
    c: PointOnObject(g13,g-1)
    c: Diameter(g13) = 7
    c: Distance(g6,g13) = 8
    c: Horizontal(g0,g10)
    c: Coincident(g14,g15)
    c: Coincident(g15,g16)
    c: Coincident(g16,g17)
    c: Coincident(g17,g18)
    c: Coincident(g18,g19)
    c: Coincident(g19,g14)
    c: Equal(g14, g15-g19) x5
    c: PointOnObject(g14,g20)
    c: PointOnObject(g15,g20)
    c: PointOnObject(g16,g20)
    c: PointOnObject(g17,g20)
    c: PointOnObject(g18,g20)
    c: PointOnObject(g19,g20)
    c: Diameter(g20) = 7
    c: DistanceY(g-1,g20) = 7
    c: Vertical(g18)
    c: Distance(g17,g-2) = 1
    c: Coincident(g21,g22)
    c: Coincident(g22,g23)
    c: Coincident(g23,g24)
    c: Coincident(g24,g25)
    c: Coincident(g25,g26)
    c: Coincident(g26,g21)
    c: Equal(g21, g22-g26) x5
    c: PointOnObject(g21,g27)
    c: PointOnObject(g22,g27)
    c: PointOnObject(g23,g27)
    c: PointOnObject(g24,g27)
    c: PointOnObject(g25,g27)
    c: PointOnObject(g26,g27)
    c: Diameter(g27) = 7
    c: DistanceY(g-1,g27) = 7
    c: DistanceX(g21,g-1) = 1
    c: Vertical(g21)
    c: Coincident(g28,g29)
    c: Coincident(g29,g30)
    c: Coincident(g30,g31)
    c: Coincident(g31,g32)
    c: Coincident(g32,g33)
    c: Coincident(g33,g28)
    c: Equal(g28, g29-g33) x5
    c: PointOnObject(g28,g34)
    c: PointOnObject(g29,g34)
    c: PointOnObject(g30,g34)
    c: PointOnObject(g31,g34)
    c: PointOnObject(g32,g34)
    c: PointOnObject(g33,g34)
    c: PointOnObject(g34,g-1)
    c: Diameter(g34) = 7
    c: Vertical(g31)
    c: DistanceX(g34,g-1) = 8
    c: Coincident(g35,g36)
    c: Coincident(g36,g37)
    c: Coincident(g37,g38)
    c: Coincident(g38,g39)
    c: Coincident(g39,g40)
    c: Coincident(g40,g35)
    c: Equal(g35, g36-g40) x5
    c: PointOnObject(g35,g41)
    c: PointOnObject(g36,g41)
    c: PointOnObject(g37,g41)
    c: PointOnObject(g38,g41)
    c: PointOnObject(g39,g41)
    c: PointOnObject(g40,g41)
    c: Coincident(g42,g43)
    c: Coincident(g43,g44)
    c: Coincident(g44,g45)
    c: Coincident(g45,g46)
    c: Coincident(g46,g47)
    c: Coincident(g47,g42)
    c: Equal(g42, g43-g47) x5
    c: PointOnObject(g42,g48)
    c: PointOnObject(g43,g48)
    c: PointOnObject(g44,g48)
    c: PointOnObject(g45,g48)
    c: PointOnObject(g46,g48)
    c: PointOnObject(g47,g48)
    c: Equal(g41,g48)
    c: Diameter(g41) = 7
    c: Vertical(g39)
    c: Vertical(g43)
    c: Distance(g-2,g39) = 1
    c: Symmetric(g38,g43,g-2)
    c: Distance(g41,g-1) = 7
FEATURE [Part::Extrusion] Extrude596  label="hex198"
  Base = -> Sketch605
  Dir = (0,-1,2e-16)
  DirMode = 2
  FaceMakerClass = Part::FaceMakerBullseye
  FaceMakerMode = 3
  LengthFwd = 10
  LengthRev = 0
  Placement = pos=(-32,0,-42) rot=(0,0,1;0rad)
  Solid = true
  Symmetric = false
FEATURE [Sketcher::SketchObject] Sketch606
  ArcFitTolerance = 1e-06
  FullyConstrained = true
  MakeInternals = false
  Placement = pos=(0,0,0) rot=(1,0,0;1.5708rad)
  sketch-geometry (49):
    g0: LineSegment StartX=1e-16 StartY=3.5 StartZ=0 EndX=-3.03109 EndY=1.75 EndZ=0
    g1: LineSegment StartX=-3.03109 StartY=1.75 StartZ=0 EndX=-3.03109 EndY=-1.75 EndZ=0
    g2: LineSegment StartX=-3.03109 StartY=-1.75 StartZ=0 EndX=-1e-16 EndY=-3.5 EndZ=0
    g3: LineSegment StartX=-1e-16 StartY=-3.5 StartZ=0 EndX=3.03109 EndY=-1.75 EndZ=0
    g4: LineSegment StartX=3.03109 StartY=-1.75 StartZ=0 EndX=3.03109 EndY=1.75 EndZ=0
    g5: LineSegment StartX=3.03109 StartY=1.75 StartZ=0 EndX=1e-16 EndY=3.5 EndZ=0
    g6: Circle [constr] CenterX=0 CenterY=0 CenterZ=0 NormalX=0 NormalY=0 NormalZ=1 AngleXU=0 Radius=3.5
    g7: LineSegment StartX=4.96892 StartY=-1.75002 StartZ=0 EndX=8.00002 EndY=-3.5 EndZ=0
    g8: LineSegment StartX=8.00002 StartY=-3.5 StartZ=0 EndX=11.0311 EndY=-1.74998 EndZ=0
    g9: LineSegment StartX=11.0311 StartY=-1.74998 StartZ=0 EndX=11.0311 EndY=1.75002 EndZ=0
    g10: LineSegment StartX=11.0311 StartY=1.75002 StartZ=0 EndX=7.99998 EndY=3.5 EndZ=0
    g11: LineSegment StartX=7.99998 StartY=3.5 StartZ=0 EndX=4.9689 EndY=1.74998 EndZ=0
    g12: LineSegment StartX=4.9689 StartY=1.74998 StartZ=0 EndX=4.96892 EndY=-1.75002 EndZ=0
    g13: Circle [constr] CenterX=8 CenterY=0 CenterZ=0 NormalX=0 NormalY=0 NormalZ=1 AngleXU=0 Radius=3.5
    g14: LineSegment StartX=4.03109 StartY=3.5 StartZ=0 EndX=7.06218 EndY=5.25 EndZ=0
    g15: LineSegment StartX=7.06218 StartY=5.25 StartZ=0 EndX=7.06218 EndY=8.75 EndZ=0
    g16: LineSegment StartX=7.06218 StartY=8.75 StartZ=0 EndX=4.03109 EndY=10.5 EndZ=0
    g17: LineSegment StartX=4.03109 StartY=10.5 StartZ=0 EndX=1 EndY=8.75 EndZ=0
    g18: LineSegment StartX=1 StartY=8.75 StartZ=0 EndX=1 EndY=5.25 EndZ=0
    g19: LineSegment StartX=1 StartY=5.25 StartZ=0 EndX=4.03109 EndY=3.5 EndZ=0
    g20: Circle [constr] CenterX=4.03109 CenterY=7 CenterZ=0 NormalX=0 NormalY=0 NormalZ=1 AngleXU=0 Radius=3.5
    g21: LineSegment StartX=-1 StartY=5.25 StartZ=0 EndX=-1 EndY=8.75 EndZ=0
    g22: LineSegment StartX=-1 StartY=8.75 StartZ=0 EndX=-4.03109 EndY=10.5 EndZ=0
    g23: LineSegment StartX=-4.03109 StartY=10.5 StartZ=0 EndX=-7.06218 EndY=8.75 EndZ=0
    g24: LineSegment StartX=-7.06218 StartY=8.75 StartZ=0 EndX=-7.06218 EndY=5.25 EndZ=0
    g25: LineSegment StartX=-7.06218 StartY=5.25 StartZ=0 EndX=-4.03109 EndY=3.5 EndZ=0
    g26: LineSegment StartX=-4.03109 StartY=3.5 StartZ=0 EndX=-1 EndY=5.25 EndZ=0
    g27: Circle [constr] CenterX=-4.03109 CenterY=7 CenterZ=0 NormalX=0 NormalY=0 NormalZ=1 AngleXU=0 Radius=3.5
    g28: LineSegment StartX=-4.96891 StartY=-1.75 StartZ=0 EndX=-4.96891 EndY=1.75 EndZ=0
    g29: LineSegment StartX=-4.96891 StartY=1.75 StartZ=0 EndX=-8 EndY=3.5 EndZ=0
    g30: LineSegment StartX=-8 StartY=3.5 StartZ=0 EndX=-11.0311 EndY=1.75 EndZ=0
    g31: LineSegment StartX=-11.0311 StartY=1.75 StartZ=0 EndX=-11.0311 EndY=-1.75 EndZ=0
    g32: LineSegment StartX=-11.0311 StartY=-1.75 StartZ=0 EndX=-8 EndY=-3.5 EndZ=0
    g33: LineSegment StartX=-8 StartY=-3.5 StartZ=0 EndX=-4.96891 EndY=-1.75 EndZ=0
    g34: Circle [constr] CenterX=-8 CenterY=0 CenterZ=0 NormalX=0 NormalY=0 NormalZ=1 AngleXU=0 Radius=3.5
    g35: LineSegment StartX=-4.03109 StartY=-3.5 StartZ=0 EndX=-7.06218 EndY=-5.25 EndZ=0
    g36: LineSegment StartX=-7.06218 StartY=-5.25 StartZ=0 EndX=-7.06218 EndY=-8.75 EndZ=0
    g37: LineSegment StartX=-7.06218 StartY=-8.75 StartZ=0 EndX=-4.03109 EndY=-10.5 EndZ=0
    g38: LineSegment StartX=-4.03109 StartY=-10.5 StartZ=0 EndX=-1 EndY=-8.75 EndZ=0
    g39: LineSegment StartX=-1 StartY=-8.75 StartZ=0 EndX=-1 EndY=-5.25 EndZ=0
    g40: LineSegment StartX=-1 StartY=-5.25 StartZ=0 EndX=-4.03109 EndY=-3.5 EndZ=0
    g41: Circle [constr] CenterX=-4.03109 CenterY=-7 CenterZ=0 NormalX=0 NormalY=0 NormalZ=1 AngleXU=0 Radius=3.5
    g42: LineSegment StartX=4.03109 StartY=-3.5 StartZ=0 EndX=1 EndY=-5.25 EndZ=0
    g43: LineSegment StartX=1 StartY=-5.25 StartZ=0 EndX=1 EndY=-8.75 EndZ=0
    g44: LineSegment StartX=1 StartY=-8.75 StartZ=0 EndX=4.03109 EndY=-10.5 EndZ=0
    g45: LineSegment StartX=4.03109 StartY=-10.5 StartZ=0 EndX=7.06218 EndY=-8.75 EndZ=0
    g46: LineSegment StartX=7.06218 StartY=-8.75 StartZ=0 EndX=7.06218 EndY=-5.25 EndZ=0
    g47: LineSegment StartX=7.06218 StartY=-5.25 StartZ=0 EndX=4.03109 EndY=-3.5 EndZ=0
    g48: Circle [constr] CenterX=4.03109 CenterY=-7 CenterZ=0 NormalX=0 NormalY=0 NormalZ=1 AngleXU=0 Radius=3.5
  constraints (117):
    c: Coincident(g0,g1)
    c: Coincident(g1,g2)
    c: Coincident(g2,g3)
    c: Coincident(g3,g4)
    c: Coincident(g4,g5)
    c: Coincident(g5,g0)
    c: Equal(g0, g1-g5) x5
    c: PointOnObject(g0,g6)
    c: PointOnObject(g1,g6)
    c: PointOnObject(g2,g6)
    c: PointOnObject(g3,g6)
    c: PointOnObject(g4,g6)
    c: PointOnObject(g5,g6)
    c: Coincident(g6,g-1)
    c: Diameter(g6) = 7
    c: PointOnObject(g0,g-2)
    c: Coincident(g7,g8)
    c: Coincident(g8,g9)
    c: Coincident(g9,g10)
    c: Coincident(g10,g11)
    c: Coincident(g11,g12)
    c: Coincident(g12,g7)
    c: Equal(g7, g8-g12) x5
    c: PointOnObject(g7,g13)
    c: PointOnObject(g8,g13)
    c: PointOnObject(g9,g13)
    c: PointOnObject(g10,g13)
    c: PointOnObject(g11,g13)
    c: PointOnObject(g12,g13)
    c: PointOnObject(g13,g-1)
    c: Diameter(g13) = 7
    c: Distance(g6,g13) = 8
    c: Horizontal(g0,g10)
    c: Coincident(g14,g15)
    c: Coincident(g15,g16)
    c: Coincident(g16,g17)
    c: Coincident(g17,g18)
    c: Coincident(g18,g19)
    c: Coincident(g19,g14)
    c: Equal(g14, g15-g19) x5
    c: PointOnObject(g14,g20)
    c: PointOnObject(g15,g20)
    c: PointOnObject(g16,g20)
    c: PointOnObject(g17,g20)
    c: PointOnObject(g18,g20)
    c: PointOnObject(g19,g20)
    c: Diameter(g20) = 7
    c: DistanceY(g-1,g20) = 7
    c: Vertical(g18)
    c: Distance(g17,g-2) = 1
    c: Coincident(g21,g22)
    c: Coincident(g22,g23)
    c: Coincident(g23,g24)
    c: Coincident(g24,g25)
    c: Coincident(g25,g26)
    c: Coincident(g26,g21)
    c: Equal(g21, g22-g26) x5
    c: PointOnObject(g21,g27)
    c: PointOnObject(g22,g27)
    c: PointOnObject(g23,g27)
    c: PointOnObject(g24,g27)
    c: PointOnObject(g25,g27)
    c: PointOnObject(g26,g27)
    c: Diameter(g27) = 7
    c: DistanceY(g-1,g27) = 7
    c: DistanceX(g21,g-1) = 1
    c: Vertical(g21)
    c: Coincident(g28,g29)
    c: Coincident(g29,g30)
    c: Coincident(g30,g31)
    c: Coincident(g31,g32)
    c: Coincident(g32,g33)
    c: Coincident(g33,g28)
    c: Equal(g28, g29-g33) x5
    c: PointOnObject(g28,g34)
    c: PointOnObject(g29,g34)
    c: PointOnObject(g30,g34)
    c: PointOnObject(g31,g34)
    c: PointOnObject(g32,g34)
    c: PointOnObject(g33,g34)
    c: PointOnObject(g34,g-1)
    c: Diameter(g34) = 7
    c: Vertical(g31)
    c: DistanceX(g34,g-1) = 8
    c: Coincident(g35,g36)
    c: Coincident(g36,g37)
    c: Coincident(g37,g38)
    c: Coincident(g38,g39)
    c: Coincident(g39,g40)
    c: Coincident(g40,g35)
    c: Equal(g35, g36-g40) x5
    c: PointOnObject(g35,g41)
    c: PointOnObject(g36,g41)
    c: PointOnObject(g37,g41)
    c: PointOnObject(g38,g41)
    c: PointOnObject(g39,g41)
    c: PointOnObject(g40,g41)
    c: Coincident(g42,g43)
    c: Coincident(g43,g44)
    c: Coincident(g44,g45)
    c: Coincident(g45,g46)
    c: Coincident(g46,g47)
    c: Coincident(g47,g42)
    c: Equal(g42, g43-g47) x5
    c: PointOnObject(g42,g48)
    c: PointOnObject(g43,g48)
    c: PointOnObject(g44,g48)
    c: PointOnObject(g45,g48)
    c: PointOnObject(g46,g48)
    c: PointOnObject(g47,g48)
    c: Equal(g41,g48)
    c: Diameter(g41) = 7
    c: Vertical(g39)
    c: Vertical(g43)
    c: Distance(g-2,g39) = 1
    c: Symmetric(g38,g43,g-2)
    c: Distance(g41,g-1) = 7
FEATURE [Part::Extrusion] Extrude597  label="hex199"
  Base = -> Sketch606
  Dir = (0,-1,2e-16)
  DirMode = 2
  FaceMakerClass = Part::FaceMakerBullseye
  FaceMakerMode = 3
  LengthFwd = 10
  LengthRev = 0
  Placement = pos=(-56,0,-42) rot=(0,0,1;0rad)
  Solid = true
  Symmetric = false
FEATURE [Sketcher::SketchObject] Sketch607
  ArcFitTolerance = 1e-06
  FullyConstrained = true
  MakeInternals = false
  Placement = pos=(0,0,0) rot=(1,0,0;1.5708rad)
  sketch-geometry (49):
    g0: LineSegment StartX=1e-16 StartY=3.5 StartZ=0 EndX=-3.03109 EndY=1.75 EndZ=0
    g1: LineSegment StartX=-3.03109 StartY=1.75 StartZ=0 EndX=-3.03109 EndY=-1.75 EndZ=0
    g2: LineSegment StartX=-3.03109 StartY=-1.75 StartZ=0 EndX=-1e-16 EndY=-3.5 EndZ=0
    g3: LineSegment StartX=-1e-16 StartY=-3.5 StartZ=0 EndX=3.03109 EndY=-1.75 EndZ=0
    g4: LineSegment StartX=3.03109 StartY=-1.75 StartZ=0 EndX=3.03109 EndY=1.75 EndZ=0
    g5: LineSegment StartX=3.03109 StartY=1.75 StartZ=0 EndX=1e-16 EndY=3.5 EndZ=0
    g6: Circle [constr] CenterX=0 CenterY=0 CenterZ=0 NormalX=0 NormalY=0 NormalZ=1 AngleXU=0 Radius=3.5
    g7: LineSegment StartX=4.96892 StartY=-1.75002 StartZ=0 EndX=8.00002 EndY=-3.5 EndZ=0
    g8: LineSegment StartX=8.00002 StartY=-3.5 StartZ=0 EndX=11.0311 EndY=-1.74998 EndZ=0
    g9: LineSegment StartX=11.0311 StartY=-1.74998 StartZ=0 EndX=11.0311 EndY=1.75002 EndZ=0
    g10: LineSegment StartX=11.0311 StartY=1.75002 StartZ=0 EndX=7.99998 EndY=3.5 EndZ=0
    g11: LineSegment StartX=7.99998 StartY=3.5 StartZ=0 EndX=4.9689 EndY=1.74998 EndZ=0
    g12: LineSegment StartX=4.9689 StartY=1.74998 StartZ=0 EndX=4.96892 EndY=-1.75002 EndZ=0
    g13: Circle [constr] CenterX=8 CenterY=0 CenterZ=0 NormalX=0 NormalY=0 NormalZ=1 AngleXU=0 Radius=3.5
    g14: LineSegment StartX=4.03109 StartY=3.5 StartZ=0 EndX=7.06218 EndY=5.25 EndZ=0
    g15: LineSegment StartX=7.06218 StartY=5.25 StartZ=0 EndX=7.06218 EndY=8.75 EndZ=0
    g16: LineSegment StartX=7.06218 StartY=8.75 StartZ=0 EndX=4.03109 EndY=10.5 EndZ=0
    g17: LineSegment StartX=4.03109 StartY=10.5 StartZ=0 EndX=1 EndY=8.75 EndZ=0
    g18: LineSegment StartX=1 StartY=8.75 StartZ=0 EndX=1 EndY=5.25 EndZ=0
    g19: LineSegment StartX=1 StartY=5.25 StartZ=0 EndX=4.03109 EndY=3.5 EndZ=0
    g20: Circle [constr] CenterX=4.03109 CenterY=7 CenterZ=0 NormalX=0 NormalY=0 NormalZ=1 AngleXU=0 Radius=3.5
    g21: LineSegment StartX=-1 StartY=5.25 StartZ=0 EndX=-1 EndY=8.75 EndZ=0
    g22: LineSegment StartX=-1 StartY=8.75 StartZ=0 EndX=-4.03109 EndY=10.5 EndZ=0
    g23: LineSegment StartX=-4.03109 StartY=10.5 StartZ=0 EndX=-7.06218 EndY=8.75 EndZ=0
    g24: LineSegment StartX=-7.06218 StartY=8.75 StartZ=0 EndX=-7.06218 EndY=5.25 EndZ=0
    g25: LineSegment StartX=-7.06218 StartY=5.25 StartZ=0 EndX=-4.03109 EndY=3.5 EndZ=0
    g26: LineSegment StartX=-4.03109 StartY=3.5 StartZ=0 EndX=-1 EndY=5.25 EndZ=0
    g27: Circle [constr] CenterX=-4.03109 CenterY=7 CenterZ=0 NormalX=0 NormalY=0 NormalZ=1 AngleXU=0 Radius=3.5
    g28: LineSegment StartX=-4.96891 StartY=-1.75 StartZ=0 EndX=-4.96891 EndY=1.75 EndZ=0
    g29: LineSegment StartX=-4.96891 StartY=1.75 StartZ=0 EndX=-8 EndY=3.5 EndZ=0
    g30: LineSegment StartX=-8 StartY=3.5 StartZ=0 EndX=-11.0311 EndY=1.75 EndZ=0
    g31: LineSegment StartX=-11.0311 StartY=1.75 StartZ=0 EndX=-11.0311 EndY=-1.75 EndZ=0
    g32: LineSegment StartX=-11.0311 StartY=-1.75 StartZ=0 EndX=-8 EndY=-3.5 EndZ=0
    g33: LineSegment StartX=-8 StartY=-3.5 StartZ=0 EndX=-4.96891 EndY=-1.75 EndZ=0
    g34: Circle [constr] CenterX=-8 CenterY=0 CenterZ=0 NormalX=0 NormalY=0 NormalZ=1 AngleXU=0 Radius=3.5
    g35: LineSegment StartX=-4.03109 StartY=-3.5 StartZ=0 EndX=-7.06218 EndY=-5.25 EndZ=0
    g36: LineSegment StartX=-7.06218 StartY=-5.25 StartZ=0 EndX=-7.06218 EndY=-8.75 EndZ=0
    g37: LineSegment StartX=-7.06218 StartY=-8.75 StartZ=0 EndX=-4.03109 EndY=-10.5 EndZ=0
    g38: LineSegment StartX=-4.03109 StartY=-10.5 StartZ=0 EndX=-1 EndY=-8.75 EndZ=0
    g39: LineSegment StartX=-1 StartY=-8.75 StartZ=0 EndX=-1 EndY=-5.25 EndZ=0
    g40: LineSegment StartX=-1 StartY=-5.25 StartZ=0 EndX=-4.03109 EndY=-3.5 EndZ=0
    g41: Circle [constr] CenterX=-4.03109 CenterY=-7 CenterZ=0 NormalX=0 NormalY=0 NormalZ=1 AngleXU=0 Radius=3.5
    g42: LineSegment StartX=4.03109 StartY=-3.5 StartZ=0 EndX=1 EndY=-5.25 EndZ=0
    g43: LineSegment StartX=1 StartY=-5.25 StartZ=0 EndX=1 EndY=-8.75 EndZ=0
    g44: LineSegment StartX=1 StartY=-8.75 StartZ=0 EndX=4.03109 EndY=-10.5 EndZ=0
    g45: LineSegment StartX=4.03109 StartY=-10.5 StartZ=0 EndX=7.06218 EndY=-8.75 EndZ=0
    g46: LineSegment StartX=7.06218 StartY=-8.75 StartZ=0 EndX=7.06218 EndY=-5.25 EndZ=0
    g47: LineSegment StartX=7.06218 StartY=-5.25 StartZ=0 EndX=4.03109 EndY=-3.5 EndZ=0
    g48: Circle [constr] CenterX=4.03109 CenterY=-7 CenterZ=0 NormalX=0 NormalY=0 NormalZ=1 AngleXU=0 Radius=3.5
  constraints (117):
    c: Coincident(g0,g1)
    c: Coincident(g1,g2)
    c: Coincident(g2,g3)
    c: Coincident(g3,g4)
    c: Coincident(g4,g5)
    c: Coincident(g5,g0)
    c: Equal(g0, g1-g5) x5
    c: PointOnObject(g0,g6)
    c: PointOnObject(g1,g6)
    c: PointOnObject(g2,g6)
    c: PointOnObject(g3,g6)
    c: PointOnObject(g4,g6)
    c: PointOnObject(g5,g6)
    c: Coincident(g6,g-1)
    c: Diameter(g6) = 7
    c: PointOnObject(g0,g-2)
    c: Coincident(g7,g8)
    c: Coincident(g8,g9)
    c: Coincident(g9,g10)
    c: Coincident(g10,g11)
    c: Coincident(g11,g12)
    c: Coincident(g12,g7)
    c: Equal(g7, g8-g12) x5
    c: PointOnObject(g7,g13)
    c: PointOnObject(g8,g13)
    c: PointOnObject(g9,g13)
    c: PointOnObject(g10,g13)
    c: PointOnObject(g11,g13)
    c: PointOnObject(g12,g13)
    c: PointOnObject(g13,g-1)
    c: Diameter(g13) = 7
    c: Distance(g6,g13) = 8
    c: Horizontal(g0,g10)
    c: Coincident(g14,g15)
    c: Coincident(g15,g16)
    c: Coincident(g16,g17)
    c: Coincident(g17,g18)
    c: Coincident(g18,g19)
    c: Coincident(g19,g14)
    c: Equal(g14, g15-g19) x5
    c: PointOnObject(g14,g20)
    c: PointOnObject(g15,g20)
    c: PointOnObject(g16,g20)
    c: PointOnObject(g17,g20)
    c: PointOnObject(g18,g20)
    c: PointOnObject(g19,g20)
    c: Diameter(g20) = 7
    c: DistanceY(g-1,g20) = 7
    c: Vertical(g18)
    c: Distance(g17,g-2) = 1
    c: Coincident(g21,g22)
    c: Coincident(g22,g23)
    c: Coincident(g23,g24)
    c: Coincident(g24,g25)
    c: Coincident(g25,g26)
    c: Coincident(g26,g21)
    c: Equal(g21, g22-g26) x5
    c: PointOnObject(g21,g27)
    c: PointOnObject(g22,g27)
    c: PointOnObject(g23,g27)
    c: PointOnObject(g24,g27)
    c: PointOnObject(g25,g27)
    c: PointOnObject(g26,g27)
    c: Diameter(g27) = 7
    c: DistanceY(g-1,g27) = 7
    c: DistanceX(g21,g-1) = 1
    c: Vertical(g21)
    c: Coincident(g28,g29)
    c: Coincident(g29,g30)
    c: Coincident(g30,g31)
    c: Coincident(g31,g32)
    c: Coincident(g32,g33)
    c: Coincident(g33,g28)
    c: Equal(g28, g29-g33) x5
    c: PointOnObject(g28,g34)
    c: PointOnObject(g29,g34)
    c: PointOnObject(g30,g34)
    c: PointOnObject(g31,g34)
    c: PointOnObject(g32,g34)
    c: PointOnObject(g33,g34)
    c: PointOnObject(g34,g-1)
    c: Diameter(g34) = 7
    c: Vertical(g31)
    c: DistanceX(g34,g-1) = 8
    c: Coincident(g35,g36)
    c: Coincident(g36,g37)
    c: Coincident(g37,g38)
    c: Coincident(g38,g39)
    c: Coincident(g39,g40)
    c: Coincident(g40,g35)
    c: Equal(g35, g36-g40) x5
    c: PointOnObject(g35,g41)
    c: PointOnObject(g36,g41)
    c: PointOnObject(g37,g41)
    c: PointOnObject(g38,g41)
    c: PointOnObject(g39,g41)
    c: PointOnObject(g40,g41)
    c: Coincident(g42,g43)
    c: Coincident(g43,g44)
    c: Coincident(g44,g45)
    c: Coincident(g45,g46)
    c: Coincident(g46,g47)
    c: Coincident(g47,g42)
    c: Equal(g42, g43-g47) x5
    c: PointOnObject(g42,g48)
    c: PointOnObject(g43,g48)
    c: PointOnObject(g44,g48)
    c: PointOnObject(g45,g48)
    c: PointOnObject(g46,g48)
    c: PointOnObject(g47,g48)
    c: Equal(g41,g48)
    c: Diameter(g41) = 7
    c: Vertical(g39)
    c: Vertical(g43)
    c: Distance(g-2,g39) = 1
    c: Symmetric(g38,g43,g-2)
    c: Distance(g41,g-1) = 7
FEATURE [Part::Extrusion] Extrude598  label="hex200"
  Base = -> Sketch607
  Dir = (0,-1,2e-16)
  DirMode = 2
  FaceMakerClass = Part::FaceMakerBullseye
  FaceMakerMode = 3
  LengthFwd = 10
  LengthRev = 0
  Placement = pos=(-40,0,-56) rot=(0,0,1;0rad)
  Solid = true
  Symmetric = false
FEATURE [Sketcher::SketchObject] Sketch608
  ArcFitTolerance = 1e-06
  FullyConstrained = true
  MakeInternals = false
  Placement = pos=(0,0,0) rot=(1,0,0;1.5708rad)
  sketch-geometry (49):
    g0: LineSegment StartX=1e-16 StartY=3.5 StartZ=0 EndX=-3.03109 EndY=1.75 EndZ=0
    g1: LineSegment StartX=-3.03109 StartY=1.75 StartZ=0 EndX=-3.03109 EndY=-1.75 EndZ=0
    g2: LineSegment StartX=-3.03109 StartY=-1.75 StartZ=0 EndX=-1e-16 EndY=-3.5 EndZ=0
    g3: LineSegment StartX=-1e-16 StartY=-3.5 StartZ=0 EndX=3.03109 EndY=-1.75 EndZ=0
    g4: LineSegment StartX=3.03109 StartY=-1.75 StartZ=0 EndX=3.03109 EndY=1.75 EndZ=0
    g5: LineSegment StartX=3.03109 StartY=1.75 StartZ=0 EndX=1e-16 EndY=3.5 EndZ=0
    g6: Circle [constr] CenterX=0 CenterY=0 CenterZ=0 NormalX=0 NormalY=0 NormalZ=1 AngleXU=0 Radius=3.5
    g7: LineSegment StartX=4.96892 StartY=-1.75002 StartZ=0 EndX=8.00002 EndY=-3.5 EndZ=0
    g8: LineSegment StartX=8.00002 StartY=-3.5 StartZ=0 EndX=11.0311 EndY=-1.74998 EndZ=0
    g9: LineSegment StartX=11.0311 StartY=-1.74998 StartZ=0 EndX=11.0311 EndY=1.75002 EndZ=0
    g10: LineSegment StartX=11.0311 StartY=1.75002 StartZ=0 EndX=7.99998 EndY=3.5 EndZ=0
    g11: LineSegment StartX=7.99998 StartY=3.5 StartZ=0 EndX=4.9689 EndY=1.74998 EndZ=0
    g12: LineSegment StartX=4.9689 StartY=1.74998 StartZ=0 EndX=4.96892 EndY=-1.75002 EndZ=0
    g13: Circle [constr] CenterX=8 CenterY=0 CenterZ=0 NormalX=0 NormalY=0 NormalZ=1 AngleXU=0 Radius=3.5
    g14: LineSegment StartX=4.03109 StartY=3.5 StartZ=0 EndX=7.06218 EndY=5.25 EndZ=0
    g15: LineSegment StartX=7.06218 StartY=5.25 StartZ=0 EndX=7.06218 EndY=8.75 EndZ=0
    g16: LineSegment StartX=7.06218 StartY=8.75 StartZ=0 EndX=4.03109 EndY=10.5 EndZ=0
    g17: LineSegment StartX=4.03109 StartY=10.5 StartZ=0 EndX=1 EndY=8.75 EndZ=0
    g18: LineSegment StartX=1 StartY=8.75 StartZ=0 EndX=1 EndY=5.25 EndZ=0
    g19: LineSegment StartX=1 StartY=5.25 StartZ=0 EndX=4.03109 EndY=3.5 EndZ=0
    g20: Circle [constr] CenterX=4.03109 CenterY=7 CenterZ=0 NormalX=0 NormalY=0 NormalZ=1 AngleXU=0 Radius=3.5
    g21: LineSegment StartX=-1 StartY=5.25 StartZ=0 EndX=-1 EndY=8.75 EndZ=0
    g22: LineSegment StartX=-1 StartY=8.75 StartZ=0 EndX=-4.03109 EndY=10.5 EndZ=0
    g23: LineSegment StartX=-4.03109 StartY=10.5 StartZ=0 EndX=-7.06218 EndY=8.75 EndZ=0
    g24: LineSegment StartX=-7.06218 StartY=8.75 StartZ=0 EndX=-7.06218 EndY=5.25 EndZ=0
    g25: LineSegment StartX=-7.06218 StartY=5.25 StartZ=0 EndX=-4.03109 EndY=3.5 EndZ=0
    g26: LineSegment StartX=-4.03109 StartY=3.5 StartZ=0 EndX=-1 EndY=5.25 EndZ=0
    g27: Circle [constr] CenterX=-4.03109 CenterY=7 CenterZ=0 NormalX=0 NormalY=0 NormalZ=1 AngleXU=0 Radius=3.5
    g28: LineSegment StartX=-4.96891 StartY=-1.75 StartZ=0 EndX=-4.96891 EndY=1.75 EndZ=0
    g29: LineSegment StartX=-4.96891 StartY=1.75 StartZ=0 EndX=-8 EndY=3.5 EndZ=0
    g30: LineSegment StartX=-8 StartY=3.5 StartZ=0 EndX=-11.0311 EndY=1.75 EndZ=0
    g31: LineSegment StartX=-11.0311 StartY=1.75 StartZ=0 EndX=-11.0311 EndY=-1.75 EndZ=0
    g32: LineSegment StartX=-11.0311 StartY=-1.75 StartZ=0 EndX=-8 EndY=-3.5 EndZ=0
    g33: LineSegment StartX=-8 StartY=-3.5 StartZ=0 EndX=-4.96891 EndY=-1.75 EndZ=0
    g34: Circle [constr] CenterX=-8 CenterY=0 CenterZ=0 NormalX=0 NormalY=0 NormalZ=1 AngleXU=0 Radius=3.5
    g35: LineSegment StartX=-4.03109 StartY=-3.5 StartZ=0 EndX=-7.06218 EndY=-5.25 EndZ=0
    g36: LineSegment StartX=-7.06218 StartY=-5.25 StartZ=0 EndX=-7.06218 EndY=-8.75 EndZ=0
    g37: LineSegment StartX=-7.06218 StartY=-8.75 StartZ=0 EndX=-4.03109 EndY=-10.5 EndZ=0
    g38: LineSegment StartX=-4.03109 StartY=-10.5 StartZ=0 EndX=-1 EndY=-8.75 EndZ=0
    g39: LineSegment StartX=-1 StartY=-8.75 StartZ=0 EndX=-1 EndY=-5.25 EndZ=0
    g40: LineSegment StartX=-1 StartY=-5.25 StartZ=0 EndX=-4.03109 EndY=-3.5 EndZ=0
    g41: Circle [constr] CenterX=-4.03109 CenterY=-7 CenterZ=0 NormalX=0 NormalY=0 NormalZ=1 AngleXU=0 Radius=3.5
    g42: LineSegment StartX=4.03109 StartY=-3.5 StartZ=0 EndX=1 EndY=-5.25 EndZ=0
    g43: LineSegment StartX=1 StartY=-5.25 StartZ=0 EndX=1 EndY=-8.75 EndZ=0
    g44: LineSegment StartX=1 StartY=-8.75 StartZ=0 EndX=4.03109 EndY=-10.5 EndZ=0
    g45: LineSegment StartX=4.03109 StartY=-10.5 StartZ=0 EndX=7.06218 EndY=-8.75 EndZ=0
    g46: LineSegment StartX=7.06218 StartY=-8.75 StartZ=0 EndX=7.06218 EndY=-5.25 EndZ=0
    g47: LineSegment StartX=7.06218 StartY=-5.25 StartZ=0 EndX=4.03109 EndY=-3.5 EndZ=0
    g48: Circle [constr] CenterX=4.03109 CenterY=-7 CenterZ=0 NormalX=0 NormalY=0 NormalZ=1 AngleXU=0 Radius=3.5
  constraints (117):
    c: Coincident(g0,g1)
    c: Coincident(g1,g2)
    c: Coincident(g2,g3)
    c: Coincident(g3,g4)
    c: Coincident(g4,g5)
    c: Coincident(g5,g0)
    c: Equal(g0, g1-g5) x5
    c: PointOnObject(g0,g6)
    c: PointOnObject(g1,g6)
    c: PointOnObject(g2,g6)
    c: PointOnObject(g3,g6)
    c: PointOnObject(g4,g6)
    c: PointOnObject(g5,g6)
    c: Coincident(g6,g-1)
    c: Diameter(g6) = 7
    c: PointOnObject(g0,g-2)
    c: Coincident(g7,g8)
    c: Coincident(g8,g9)
    c: Coincident(g9,g10)
    c: Coincident(g10,g11)
    c: Coincident(g11,g12)
    c: Coincident(g12,g7)
    c: Equal(g7, g8-g12) x5
    c: PointOnObject(g7,g13)
    c: PointOnObject(g8,g13)
    c: PointOnObject(g9,g13)
    c: PointOnObject(g10,g13)
    c: PointOnObject(g11,g13)
    c: PointOnObject(g12,g13)
    c: PointOnObject(g13,g-1)
    c: Diameter(g13) = 7
    c: Distance(g6,g13) = 8
    c: Horizontal(g0,g10)
    c: Coincident(g14,g15)
    c: Coincident(g15,g16)
    c: Coincident(g16,g17)
    c: Coincident(g17,g18)
    c: Coincident(g18,g19)
    c: Coincident(g19,g14)
    c: Equal(g14, g15-g19) x5
    c: PointOnObject(g14,g20)
    c: PointOnObject(g15,g20)
    c: PointOnObject(g16,g20)
    c: PointOnObject(g17,g20)
    c: PointOnObject(g18,g20)
    c: PointOnObject(g19,g20)
    c: Diameter(g20) = 7
    c: DistanceY(g-1,g20) = 7
    c: Vertical(g18)
    c: Distance(g17,g-2) = 1
    c: Coincident(g21,g22)
    c: Coincident(g22,g23)
    c: Coincident(g23,g24)
    c: Coincident(g24,g25)
    c: Coincident(g25,g26)
    c: Coincident(g26,g21)
    c: Equal(g21, g22-g26) x5
    c: PointOnObject(g21,g27)
    c: PointOnObject(g22,g27)
    c: PointOnObject(g23,g27)
    c: PointOnObject(g24,g27)
    c: PointOnObject(g25,g27)
    c: PointOnObject(g26,g27)
    c: Diameter(g27) = 7
    c: DistanceY(g-1,g27) = 7
    c: DistanceX(g21,g-1) = 1
    c: Vertical(g21)
    c: Coincident(g28,g29)
    c: Coincident(g29,g30)
    c: Coincident(g30,g31)
    c: Coincident(g31,g32)
    c: Coincident(g32,g33)
    c: Coincident(g33,g28)
    c: Equal(g28, g29-g33) x5
    c: PointOnObject(g28,g34)
    c: PointOnObject(g29,g34)
    c: PointOnObject(g30,g34)
    c: PointOnObject(g31,g34)
    c: PointOnObject(g32,g34)
    c: PointOnObject(g33,g34)
    c: PointOnObject(g34,g-1)
    c: Diameter(g34) = 7
    c: Vertical(g31)
    c: DistanceX(g34,g-1) = 8
    c: Coincident(g35,g36)
    c: Coincident(g36,g37)
    c: Coincident(g37,g38)
    c: Coincident(g38,g39)
    c: Coincident(g39,g40)
    c: Coincident(g40,g35)
    c: Equal(g35, g36-g40) x5
    c: PointOnObject(g35,g41)
    c: PointOnObject(g36,g41)
    c: PointOnObject(g37,g41)
    c: PointOnObject(g38,g41)
    c: PointOnObject(g39,g41)
    c: PointOnObject(g40,g41)
    c: Coincident(g42,g43)
    c: Coincident(g43,g44)
    c: Coincident(g44,g45)
    c: Coincident(g45,g46)
    c: Coincident(g46,g47)
    c: Coincident(g47,g42)
    c: Equal(g42, g43-g47) x5
    c: PointOnObject(g42,g48)
    c: PointOnObject(g43,g48)
    c: PointOnObject(g44,g48)
    c: PointOnObject(g45,g48)
    c: PointOnObject(g46,g48)
    c: PointOnObject(g47,g48)
    c: Equal(g41,g48)
    c: Diameter(g41) = 7
    c: Vertical(g39)
    c: Vertical(g43)
    c: Distance(g-2,g39) = 1
    c: Symmetric(g38,g43,g-2)
    c: Distance(g41,g-1) = 7
FEATURE [Part::Extrusion] Extrude599  label="hex201"
  Base = -> Sketch608
  Dir = (0,-1,2e-16)
  DirMode = 2
  FaceMakerClass = Part::FaceMakerBullseye
  FaceMakerMode = 3
  LengthFwd = 10
  LengthRev = 0
  Placement = pos=(-16,0,-56) rot=(0,0,1;0rad)
  Solid = true
  Symmetric = false
FEATURE [Sketcher::SketchObject] Sketch609
  ArcFitTolerance = 1e-06
  FullyConstrained = true
  MakeInternals = false
  Placement = pos=(0,0,0) rot=(1,0,0;1.5708rad)
  sketch-geometry (49):
    g0: LineSegment StartX=1e-16 StartY=3.5 StartZ=0 EndX=-3.03109 EndY=1.75 EndZ=0
    g1: LineSegment StartX=-3.03109 StartY=1.75 StartZ=0 EndX=-3.03109 EndY=-1.75 EndZ=0
    g2: LineSegment StartX=-3.03109 StartY=-1.75 StartZ=0 EndX=-1e-16 EndY=-3.5 EndZ=0
    g3: LineSegment StartX=-1e-16 StartY=-3.5 StartZ=0 EndX=3.03109 EndY=-1.75 EndZ=0
    g4: LineSegment StartX=3.03109 StartY=-1.75 StartZ=0 EndX=3.03109 EndY=1.75 EndZ=0
    g5: LineSegment StartX=3.03109 StartY=1.75 StartZ=0 EndX=1e-16 EndY=3.5 EndZ=0
    g6: Circle [constr] CenterX=0 CenterY=0 CenterZ=0 NormalX=0 NormalY=0 NormalZ=1 AngleXU=0 Radius=3.5
    g7: LineSegment StartX=4.96892 StartY=-1.75002 StartZ=0 EndX=8.00002 EndY=-3.5 EndZ=0
    g8: LineSegment StartX=8.00002 StartY=-3.5 StartZ=0 EndX=11.0311 EndY=-1.74998 EndZ=0
    g9: LineSegment StartX=11.0311 StartY=-1.74998 StartZ=0 EndX=11.0311 EndY=1.75002 EndZ=0
    g10: LineSegment StartX=11.0311 StartY=1.75002 StartZ=0 EndX=7.99998 EndY=3.5 EndZ=0
    g11: LineSegment StartX=7.99998 StartY=3.5 StartZ=0 EndX=4.9689 EndY=1.74998 EndZ=0
    g12: LineSegment StartX=4.9689 StartY=1.74998 StartZ=0 EndX=4.96892 EndY=-1.75002 EndZ=0
    g13: Circle [constr] CenterX=8 CenterY=0 CenterZ=0 NormalX=0 NormalY=0 NormalZ=1 AngleXU=0 Radius=3.5
    g14: LineSegment StartX=4.03109 StartY=3.5 StartZ=0 EndX=7.06218 EndY=5.25 EndZ=0
    g15: LineSegment StartX=7.06218 StartY=5.25 StartZ=0 EndX=7.06218 EndY=8.75 EndZ=0
    g16: LineSegment StartX=7.06218 StartY=8.75 StartZ=0 EndX=4.03109 EndY=10.5 EndZ=0
    g17: LineSegment StartX=4.03109 StartY=10.5 StartZ=0 EndX=1 EndY=8.75 EndZ=0
    g18: LineSegment StartX=1 StartY=8.75 StartZ=0 EndX=1 EndY=5.25 EndZ=0
    g19: LineSegment StartX=1 StartY=5.25 StartZ=0 EndX=4.03109 EndY=3.5 EndZ=0
    g20: Circle [constr] CenterX=4.03109 CenterY=7 CenterZ=0 NormalX=0 NormalY=0 NormalZ=1 AngleXU=0 Radius=3.5
    g21: LineSegment StartX=-1 StartY=5.25 StartZ=0 EndX=-1 EndY=8.75 EndZ=0
    g22: LineSegment StartX=-1 StartY=8.75 StartZ=0 EndX=-4.03109 EndY=10.5 EndZ=0
    g23: LineSegment StartX=-4.03109 StartY=10.5 StartZ=0 EndX=-7.06218 EndY=8.75 EndZ=0
    g24: LineSegment StartX=-7.06218 StartY=8.75 StartZ=0 EndX=-7.06218 EndY=5.25 EndZ=0
    g25: LineSegment StartX=-7.06218 StartY=5.25 StartZ=0 EndX=-4.03109 EndY=3.5 EndZ=0
    g26: LineSegment StartX=-4.03109 StartY=3.5 StartZ=0 EndX=-1 EndY=5.25 EndZ=0
    g27: Circle [constr] CenterX=-4.03109 CenterY=7 CenterZ=0 NormalX=0 NormalY=0 NormalZ=1 AngleXU=0 Radius=3.5
    g28: LineSegment StartX=-4.96891 StartY=-1.75 StartZ=0 EndX=-4.96891 EndY=1.75 EndZ=0
    g29: LineSegment StartX=-4.96891 StartY=1.75 StartZ=0 EndX=-8 EndY=3.5 EndZ=0
    g30: LineSegment StartX=-8 StartY=3.5 StartZ=0 EndX=-11.0311 EndY=1.75 EndZ=0
    g31: LineSegment StartX=-11.0311 StartY=1.75 StartZ=0 EndX=-11.0311 EndY=-1.75 EndZ=0
    g32: LineSegment StartX=-11.0311 StartY=-1.75 StartZ=0 EndX=-8 EndY=-3.5 EndZ=0
    g33: LineSegment StartX=-8 StartY=-3.5 StartZ=0 EndX=-4.96891 EndY=-1.75 EndZ=0
    g34: Circle [constr] CenterX=-8 CenterY=0 CenterZ=0 NormalX=0 NormalY=0 NormalZ=1 AngleXU=0 Radius=3.5
    g35: LineSegment StartX=-4.03109 StartY=-3.5 StartZ=0 EndX=-7.06218 EndY=-5.25 EndZ=0
    g36: LineSegment StartX=-7.06218 StartY=-5.25 StartZ=0 EndX=-7.06218 EndY=-8.75 EndZ=0
    g37: LineSegment StartX=-7.06218 StartY=-8.75 StartZ=0 EndX=-4.03109 EndY=-10.5 EndZ=0
    g38: LineSegment StartX=-4.03109 StartY=-10.5 StartZ=0 EndX=-1 EndY=-8.75 EndZ=0
    g39: LineSegment StartX=-1 StartY=-8.75 StartZ=0 EndX=-1 EndY=-5.25 EndZ=0
    g40: LineSegment StartX=-1 StartY=-5.25 StartZ=0 EndX=-4.03109 EndY=-3.5 EndZ=0
    g41: Circle [constr] CenterX=-4.03109 CenterY=-7 CenterZ=0 NormalX=0 NormalY=0 NormalZ=1 AngleXU=0 Radius=3.5
    g42: LineSegment StartX=4.03109 StartY=-3.5 StartZ=0 EndX=1 EndY=-5.25 EndZ=0
    g43: LineSegment StartX=1 StartY=-5.25 StartZ=0 EndX=1 EndY=-8.75 EndZ=0
    g44: LineSegment StartX=1 StartY=-8.75 StartZ=0 EndX=4.03109 EndY=-10.5 EndZ=0
    g45: LineSegment StartX=4.03109 StartY=-10.5 StartZ=0 EndX=7.06218 EndY=-8.75 EndZ=0
    g46: LineSegment StartX=7.06218 StartY=-8.75 StartZ=0 EndX=7.06218 EndY=-5.25 EndZ=0
    g47: LineSegment StartX=7.06218 StartY=-5.25 StartZ=0 EndX=4.03109 EndY=-3.5 EndZ=0
    g48: Circle [constr] CenterX=4.03109 CenterY=-7 CenterZ=0 NormalX=0 NormalY=0 NormalZ=1 AngleXU=0 Radius=3.5
  constraints (117):
    c: Coincident(g0,g1)
    c: Coincident(g1,g2)
    c: Coincident(g2,g3)
    c: Coincident(g3,g4)
    c: Coincident(g4,g5)
    c: Coincident(g5,g0)
    c: Equal(g0, g1-g5) x5
    c: PointOnObject(g0,g6)
    c: PointOnObject(g1,g6)
    c: PointOnObject(g2,g6)
    c: PointOnObject(g3,g6)
    c: PointOnObject(g4,g6)
    c: PointOnObject(g5,g6)
    c: Coincident(g6,g-1)
    c: Diameter(g6) = 7
    c: PointOnObject(g0,g-2)
    c: Coincident(g7,g8)
    c: Coincident(g8,g9)
    c: Coincident(g9,g10)
    c: Coincident(g10,g11)
    c: Coincident(g11,g12)
    c: Coincident(g12,g7)
    c: Equal(g7, g8-g12) x5
    c: PointOnObject(g7,g13)
    c: PointOnObject(g8,g13)
    c: PointOnObject(g9,g13)
    c: PointOnObject(g10,g13)
    c: PointOnObject(g11,g13)
    c: PointOnObject(g12,g13)
    c: PointOnObject(g13,g-1)
    c: Diameter(g13) = 7
    c: Distance(g6,g13) = 8
    c: Horizontal(g0,g10)
    c: Coincident(g14,g15)
    c: Coincident(g15,g16)
    c: Coincident(g16,g17)
    c: Coincident(g17,g18)
    c: Coincident(g18,g19)
    c: Coincident(g19,g14)
    c: Equal(g14, g15-g19) x5
    c: PointOnObject(g14,g20)
    c: PointOnObject(g15,g20)
    c: PointOnObject(g16,g20)
    c: PointOnObject(g17,g20)
    c: PointOnObject(g18,g20)
    c: PointOnObject(g19,g20)
    c: Diameter(g20) = 7
    c: DistanceY(g-1,g20) = 7
    c: Vertical(g18)
    c: Distance(g17,g-2) = 1
    c: Coincident(g21,g22)
    c: Coincident(g22,g23)
    c: Coincident(g23,g24)
    c: Coincident(g24,g25)
    c: Coincident(g25,g26)
    c: Coincident(g26,g21)
    c: Equal(g21, g22-g26) x5
    c: PointOnObject(g21,g27)
    c: PointOnObject(g22,g27)
    c: PointOnObject(g23,g27)
    c: PointOnObject(g24,g27)
    c: PointOnObject(g25,g27)
    c: PointOnObject(g26,g27)
    c: Diameter(g27) = 7
    c: DistanceY(g-1,g27) = 7
    c: DistanceX(g21,g-1) = 1
    c: Vertical(g21)
    c: Coincident(g28,g29)
    c: Coincident(g29,g30)
    c: Coincident(g30,g31)
    c: Coincident(g31,g32)
    c: Coincident(g32,g33)
    c: Coincident(g33,g28)
    c: Equal(g28, g29-g33) x5
    c: PointOnObject(g28,g34)
    c: PointOnObject(g29,g34)
    c: PointOnObject(g30,g34)
    c: PointOnObject(g31,g34)
    c: PointOnObject(g32,g34)
    c: PointOnObject(g33,g34)
    c: PointOnObject(g34,g-1)
    c: Diameter(g34) = 7
    c: Vertical(g31)
    c: DistanceX(g34,g-1) = 8
    c: Coincident(g35,g36)
    c: Coincident(g36,g37)
    c: Coincident(g37,g38)
    c: Coincident(g38,g39)
    c: Coincident(g39,g40)
    c: Coincident(g40,g35)
    c: Equal(g35, g36-g40) x5
    c: PointOnObject(g35,g41)
    c: PointOnObject(g36,g41)
    c: PointOnObject(g37,g41)
    c: PointOnObject(g38,g41)
    c: PointOnObject(g39,g41)
    c: PointOnObject(g40,g41)
    c: Coincident(g42,g43)
    c: Coincident(g43,g44)
    c: Coincident(g44,g45)
    c: Coincident(g45,g46)
    c: Coincident(g46,g47)
    c: Coincident(g47,g42)
    c: Equal(g42, g43-g47) x5
    c: PointOnObject(g42,g48)
    c: PointOnObject(g43,g48)
    c: PointOnObject(g44,g48)
    c: PointOnObject(g45,g48)
    c: PointOnObject(g46,g48)
    c: PointOnObject(g47,g48)
    c: Equal(g41,g48)
    c: Diameter(g41) = 7
    c: Vertical(g39)
    c: Vertical(g43)
    c: Distance(g-2,g39) = 1
    c: Symmetric(g38,g43,g-2)
    c: Distance(g41,g-1) = 7
FEATURE [Part::Extrusion] Extrude600  label="hex202"
  Base = -> Sketch609
  Dir = (0,-1,2e-16)
  DirMode = 2
  FaceMakerClass = Part::FaceMakerBullseye
  FaceMakerMode = 3
  LengthFwd = 10
  LengthRev = 0
  Placement = pos=(8,0,-56) rot=(0,0,1;0rad)
  Solid = true
  Symmetric = false
FEATURE [Sketcher::SketchObject] Sketch610
  ArcFitTolerance = 1e-06
  FullyConstrained = true
  MakeInternals = false
  Placement = pos=(0,0,0) rot=(1,0,0;1.5708rad)
  sketch-geometry (49):
    g0: LineSegment StartX=1e-16 StartY=3.5 StartZ=0 EndX=-3.03109 EndY=1.75 EndZ=0
    g1: LineSegment StartX=-3.03109 StartY=1.75 StartZ=0 EndX=-3.03109 EndY=-1.75 EndZ=0
    g2: LineSegment StartX=-3.03109 StartY=-1.75 StartZ=0 EndX=-1e-16 EndY=-3.5 EndZ=0
    g3: LineSegment StartX=-1e-16 StartY=-3.5 StartZ=0 EndX=3.03109 EndY=-1.75 EndZ=0
    g4: LineSegment StartX=3.03109 StartY=-1.75 StartZ=0 EndX=3.03109 EndY=1.75 EndZ=0
    g5: LineSegment StartX=3.03109 StartY=1.75 StartZ=0 EndX=1e-16 EndY=3.5 EndZ=0
    g6: Circle [constr] CenterX=0 CenterY=0 CenterZ=0 NormalX=0 NormalY=0 NormalZ=1 AngleXU=0 Radius=3.5
    g7: LineSegment StartX=4.96892 StartY=-1.75002 StartZ=0 EndX=8.00002 EndY=-3.5 EndZ=0
    g8: LineSegment StartX=8.00002 StartY=-3.5 StartZ=0 EndX=11.0311 EndY=-1.74998 EndZ=0
    g9: LineSegment StartX=11.0311 StartY=-1.74998 StartZ=0 EndX=11.0311 EndY=1.75002 EndZ=0
    g10: LineSegment StartX=11.0311 StartY=1.75002 StartZ=0 EndX=7.99998 EndY=3.5 EndZ=0
    g11: LineSegment StartX=7.99998 StartY=3.5 StartZ=0 EndX=4.9689 EndY=1.74998 EndZ=0
    g12: LineSegment StartX=4.9689 StartY=1.74998 StartZ=0 EndX=4.96892 EndY=-1.75002 EndZ=0
    g13: Circle [constr] CenterX=8 CenterY=0 CenterZ=0 NormalX=0 NormalY=0 NormalZ=1 AngleXU=0 Radius=3.5
    g14: LineSegment StartX=4.03109 StartY=3.5 StartZ=0 EndX=7.06218 EndY=5.25 EndZ=0
    g15: LineSegment StartX=7.06218 StartY=5.25 StartZ=0 EndX=7.06218 EndY=8.75 EndZ=0
    g16: LineSegment StartX=7.06218 StartY=8.75 StartZ=0 EndX=4.03109 EndY=10.5 EndZ=0
    g17: LineSegment StartX=4.03109 StartY=10.5 StartZ=0 EndX=1 EndY=8.75 EndZ=0
    g18: LineSegment StartX=1 StartY=8.75 StartZ=0 EndX=1 EndY=5.25 EndZ=0
    g19: LineSegment StartX=1 StartY=5.25 StartZ=0 EndX=4.03109 EndY=3.5 EndZ=0
    g20: Circle [constr] CenterX=4.03109 CenterY=7 CenterZ=0 NormalX=0 NormalY=0 NormalZ=1 AngleXU=0 Radius=3.5
    g21: LineSegment StartX=-1 StartY=5.25 StartZ=0 EndX=-1 EndY=8.75 EndZ=0
    g22: LineSegment StartX=-1 StartY=8.75 StartZ=0 EndX=-4.03109 EndY=10.5 EndZ=0
    g23: LineSegment StartX=-4.03109 StartY=10.5 StartZ=0 EndX=-7.06218 EndY=8.75 EndZ=0
    g24: LineSegment StartX=-7.06218 StartY=8.75 StartZ=0 EndX=-7.06218 EndY=5.25 EndZ=0
    g25: LineSegment StartX=-7.06218 StartY=5.25 StartZ=0 EndX=-4.03109 EndY=3.5 EndZ=0
    g26: LineSegment StartX=-4.03109 StartY=3.5 StartZ=0 EndX=-1 EndY=5.25 EndZ=0
    g27: Circle [constr] CenterX=-4.03109 CenterY=7 CenterZ=0 NormalX=0 NormalY=0 NormalZ=1 AngleXU=0 Radius=3.5
    g28: LineSegment StartX=-4.96891 StartY=-1.75 StartZ=0 EndX=-4.96891 EndY=1.75 EndZ=0
    g29: LineSegment StartX=-4.96891 StartY=1.75 StartZ=0 EndX=-8 EndY=3.5 EndZ=0
    g30: LineSegment StartX=-8 StartY=3.5 StartZ=0 EndX=-11.0311 EndY=1.75 EndZ=0
    g31: LineSegment StartX=-11.0311 StartY=1.75 StartZ=0 EndX=-11.0311 EndY=-1.75 EndZ=0
    g32: LineSegment StartX=-11.0311 StartY=-1.75 StartZ=0 EndX=-8 EndY=-3.5 EndZ=0
    g33: LineSegment StartX=-8 StartY=-3.5 StartZ=0 EndX=-4.96891 EndY=-1.75 EndZ=0
    g34: Circle [constr] CenterX=-8 CenterY=0 CenterZ=0 NormalX=0 NormalY=0 NormalZ=1 AngleXU=0 Radius=3.5
    g35: LineSegment StartX=-4.03109 StartY=-3.5 StartZ=0 EndX=-7.06218 EndY=-5.25 EndZ=0
    g36: LineSegment StartX=-7.06218 StartY=-5.25 StartZ=0 EndX=-7.06218 EndY=-8.75 EndZ=0
    g37: LineSegment StartX=-7.06218 StartY=-8.75 StartZ=0 EndX=-4.03109 EndY=-10.5 EndZ=0
    g38: LineSegment StartX=-4.03109 StartY=-10.5 StartZ=0 EndX=-1 EndY=-8.75 EndZ=0
    g39: LineSegment StartX=-1 StartY=-8.75 StartZ=0 EndX=-1 EndY=-5.25 EndZ=0
    g40: LineSegment StartX=-1 StartY=-5.25 StartZ=0 EndX=-4.03109 EndY=-3.5 EndZ=0
    g41: Circle [constr] CenterX=-4.03109 CenterY=-7 CenterZ=0 NormalX=0 NormalY=0 NormalZ=1 AngleXU=0 Radius=3.5
    g42: LineSegment StartX=4.03109 StartY=-3.5 StartZ=0 EndX=1 EndY=-5.25 EndZ=0
    g43: LineSegment StartX=1 StartY=-5.25 StartZ=0 EndX=1 EndY=-8.75 EndZ=0
    g44: LineSegment StartX=1 StartY=-8.75 StartZ=0 EndX=4.03109 EndY=-10.5 EndZ=0
    g45: LineSegment StartX=4.03109 StartY=-10.5 StartZ=0 EndX=7.06218 EndY=-8.75 EndZ=0
    g46: LineSegment StartX=7.06218 StartY=-8.75 StartZ=0 EndX=7.06218 EndY=-5.25 EndZ=0
    g47: LineSegment StartX=7.06218 StartY=-5.25 StartZ=0 EndX=4.03109 EndY=-3.5 EndZ=0
    g48: Circle [constr] CenterX=4.03109 CenterY=-7 CenterZ=0 NormalX=0 NormalY=0 NormalZ=1 AngleXU=0 Radius=3.5
  constraints (117):
    c: Coincident(g0,g1)
    c: Coincident(g1,g2)
    c: Coincident(g2,g3)
    c: Coincident(g3,g4)
    c: Coincident(g4,g5)
    c: Coincident(g5,g0)
    c: Equal(g0, g1-g5) x5
    c: PointOnObject(g0,g6)
    c: PointOnObject(g1,g6)
    c: PointOnObject(g2,g6)
    c: PointOnObject(g3,g6)
    c: PointOnObject(g4,g6)
    c: PointOnObject(g5,g6)
    c: Coincident(g6,g-1)
    c: Diameter(g6) = 7
    c: PointOnObject(g0,g-2)
    c: Coincident(g7,g8)
    c: Coincident(g8,g9)
    c: Coincident(g9,g10)
    c: Coincident(g10,g11)
    c: Coincident(g11,g12)
    c: Coincident(g12,g7)
    c: Equal(g7, g8-g12) x5
    c: PointOnObject(g7,g13)
    c: PointOnObject(g8,g13)
    c: PointOnObject(g9,g13)
    c: PointOnObject(g10,g13)
    c: PointOnObject(g11,g13)
    c: PointOnObject(g12,g13)
    c: PointOnObject(g13,g-1)
    c: Diameter(g13) = 7
    c: Distance(g6,g13) = 8
    c: Horizontal(g0,g10)
    c: Coincident(g14,g15)
    c: Coincident(g15,g16)
    c: Coincident(g16,g17)
    c: Coincident(g17,g18)
    c: Coincident(g18,g19)
    c: Coincident(g19,g14)
    c: Equal(g14, g15-g19) x5
    c: PointOnObject(g14,g20)
    c: PointOnObject(g15,g20)
    c: PointOnObject(g16,g20)
    c: PointOnObject(g17,g20)
    c: PointOnObject(g18,g20)
    c: PointOnObject(g19,g20)
    c: Diameter(g20) = 7
    c: DistanceY(g-1,g20) = 7
    c: Vertical(g18)
    c: Distance(g17,g-2) = 1
    c: Coincident(g21,g22)
    c: Coincident(g22,g23)
    c: Coincident(g23,g24)
    c: Coincident(g24,g25)
    c: Coincident(g25,g26)
    c: Coincident(g26,g21)
    c: Equal(g21, g22-g26) x5
    c: PointOnObject(g21,g27)
    c: PointOnObject(g22,g27)
    c: PointOnObject(g23,g27)
    c: PointOnObject(g24,g27)
    c: PointOnObject(g25,g27)
    c: PointOnObject(g26,g27)
    c: Diameter(g27) = 7
    c: DistanceY(g-1,g27) = 7
    c: DistanceX(g21,g-1) = 1
    c: Vertical(g21)
    c: Coincident(g28,g29)
    c: Coincident(g29,g30)
    c: Coincident(g30,g31)
    c: Coincident(g31,g32)
    c: Coincident(g32,g33)
    c: Coincident(g33,g28)
    c: Equal(g28, g29-g33) x5
    c: PointOnObject(g28,g34)
    c: PointOnObject(g29,g34)
    c: PointOnObject(g30,g34)
    c: PointOnObject(g31,g34)
    c: PointOnObject(g32,g34)
    c: PointOnObject(g33,g34)
    c: PointOnObject(g34,g-1)
    c: Diameter(g34) = 7
    c: Vertical(g31)
    c: DistanceX(g34,g-1) = 8
    c: Coincident(g35,g36)
    c: Coincident(g36,g37)
    c: Coincident(g37,g38)
    c: Coincident(g38,g39)
    c: Coincident(g39,g40)
    c: Coincident(g40,g35)
    c: Equal(g35, g36-g40) x5
    c: PointOnObject(g35,g41)
    c: PointOnObject(g36,g41)
    c: PointOnObject(g37,g41)
    c: PointOnObject(g38,g41)
    c: PointOnObject(g39,g41)
    c: PointOnObject(g40,g41)
    c: Coincident(g42,g43)
    c: Coincident(g43,g44)
    c: Coincident(g44,g45)
    c: Coincident(g45,g46)
    c: Coincident(g46,g47)
    c: Coincident(g47,g42)
    c: Equal(g42, g43-g47) x5
    c: PointOnObject(g42,g48)
    c: PointOnObject(g43,g48)
    c: PointOnObject(g44,g48)
    c: PointOnObject(g45,g48)
    c: PointOnObject(g46,g48)
    c: PointOnObject(g47,g48)
    c: Equal(g41,g48)
    c: Diameter(g41) = 7
    c: Vertical(g39)
    c: Vertical(g43)
    c: Distance(g-2,g39) = 1
    c: Symmetric(g38,g43,g-2)
    c: Distance(g41,g-1) = 7
FEATURE [Part::Extrusion] Extrude601  label="hex203"
  Base = -> Sketch610
  Dir = (0,-1,2e-16)
  DirMode = 2
  FaceMakerClass = Part::FaceMakerBullseye
  FaceMakerMode = 3
  LengthFwd = 10
  LengthRev = 0
  Placement = pos=(28,0,-49) rot=(0,0,1;0rad)
  Solid = true
  Symmetric = false
FEATURE [Sketcher::SketchObject] Sketch611
  ArcFitTolerance = 1e-06
  FullyConstrained = true
  MakeInternals = false
  Placement = pos=(0,0,0) rot=(1,0,0;1.5708rad)
  sketch-geometry (49):
    g0: LineSegment StartX=1e-16 StartY=3.5 StartZ=0 EndX=-3.03109 EndY=1.75 EndZ=0
    g1: LineSegment StartX=-3.03109 StartY=1.75 StartZ=0 EndX=-3.03109 EndY=-1.75 EndZ=0
    g2: LineSegment StartX=-3.03109 StartY=-1.75 StartZ=0 EndX=-1e-16 EndY=-3.5 EndZ=0
    g3: LineSegment StartX=-1e-16 StartY=-3.5 StartZ=0 EndX=3.03109 EndY=-1.75 EndZ=0
    g4: LineSegment StartX=3.03109 StartY=-1.75 StartZ=0 EndX=3.03109 EndY=1.75 EndZ=0
    g5: LineSegment StartX=3.03109 StartY=1.75 StartZ=0 EndX=1e-16 EndY=3.5 EndZ=0
    g6: Circle [constr] CenterX=0 CenterY=0 CenterZ=0 NormalX=0 NormalY=0 NormalZ=1 AngleXU=0 Radius=3.5
    g7: LineSegment StartX=4.96892 StartY=-1.75002 StartZ=0 EndX=8.00002 EndY=-3.5 EndZ=0
    g8: LineSegment StartX=8.00002 StartY=-3.5 StartZ=0 EndX=11.0311 EndY=-1.74998 EndZ=0
    g9: LineSegment StartX=11.0311 StartY=-1.74998 StartZ=0 EndX=11.0311 EndY=1.75002 EndZ=0
    g10: LineSegment StartX=11.0311 StartY=1.75002 StartZ=0 EndX=7.99998 EndY=3.5 EndZ=0
    g11: LineSegment StartX=7.99998 StartY=3.5 StartZ=0 EndX=4.9689 EndY=1.74998 EndZ=0
    g12: LineSegment StartX=4.9689 StartY=1.74998 StartZ=0 EndX=4.96892 EndY=-1.75002 EndZ=0
    g13: Circle [constr] CenterX=8 CenterY=0 CenterZ=0 NormalX=0 NormalY=0 NormalZ=1 AngleXU=0 Radius=3.5
    g14: LineSegment StartX=4.03109 StartY=3.5 StartZ=0 EndX=7.06218 EndY=5.25 EndZ=0
    g15: LineSegment StartX=7.06218 StartY=5.25 StartZ=0 EndX=7.06218 EndY=8.75 EndZ=0
    g16: LineSegment StartX=7.06218 StartY=8.75 StartZ=0 EndX=4.03109 EndY=10.5 EndZ=0
    g17: LineSegment StartX=4.03109 StartY=10.5 StartZ=0 EndX=1 EndY=8.75 EndZ=0
    g18: LineSegment StartX=1 StartY=8.75 StartZ=0 EndX=1 EndY=5.25 EndZ=0
    g19: LineSegment StartX=1 StartY=5.25 StartZ=0 EndX=4.03109 EndY=3.5 EndZ=0
    g20: Circle [constr] CenterX=4.03109 CenterY=7 CenterZ=0 NormalX=0 NormalY=0 NormalZ=1 AngleXU=0 Radius=3.5
    g21: LineSegment StartX=-1 StartY=5.25 StartZ=0 EndX=-1 EndY=8.75 EndZ=0
    g22: LineSegment StartX=-1 StartY=8.75 StartZ=0 EndX=-4.03109 EndY=10.5 EndZ=0
    g23: LineSegment StartX=-4.03109 StartY=10.5 StartZ=0 EndX=-7.06218 EndY=8.75 EndZ=0
    g24: LineSegment StartX=-7.06218 StartY=8.75 StartZ=0 EndX=-7.06218 EndY=5.25 EndZ=0
    g25: LineSegment StartX=-7.06218 StartY=5.25 StartZ=0 EndX=-4.03109 EndY=3.5 EndZ=0
    g26: LineSegment StartX=-4.03109 StartY=3.5 StartZ=0 EndX=-1 EndY=5.25 EndZ=0
    g27: Circle [constr] CenterX=-4.03109 CenterY=7 CenterZ=0 NormalX=0 NormalY=0 NormalZ=1 AngleXU=0 Radius=3.5
    g28: LineSegment StartX=-4.96891 StartY=-1.75 StartZ=0 EndX=-4.96891 EndY=1.75 EndZ=0
    g29: LineSegment StartX=-4.96891 StartY=1.75 StartZ=0 EndX=-8 EndY=3.5 EndZ=0
    g30: LineSegment StartX=-8 StartY=3.5 StartZ=0 EndX=-11.0311 EndY=1.75 EndZ=0
    g31: LineSegment StartX=-11.0311 StartY=1.75 StartZ=0 EndX=-11.0311 EndY=-1.75 EndZ=0
    g32: LineSegment StartX=-11.0311 StartY=-1.75 StartZ=0 EndX=-8 EndY=-3.5 EndZ=0
    g33: LineSegment StartX=-8 StartY=-3.5 StartZ=0 EndX=-4.96891 EndY=-1.75 EndZ=0
    g34: Circle [constr] CenterX=-8 CenterY=0 CenterZ=0 NormalX=0 NormalY=0 NormalZ=1 AngleXU=0 Radius=3.5
    g35: LineSegment StartX=-4.03109 StartY=-3.5 StartZ=0 EndX=-7.06218 EndY=-5.25 EndZ=0
    g36: LineSegment StartX=-7.06218 StartY=-5.25 StartZ=0 EndX=-7.06218 EndY=-8.75 EndZ=0
    g37: LineSegment StartX=-7.06218 StartY=-8.75 StartZ=0 EndX=-4.03109 EndY=-10.5 EndZ=0
    g38: LineSegment StartX=-4.03109 StartY=-10.5 StartZ=0 EndX=-1 EndY=-8.75 EndZ=0
    g39: LineSegment StartX=-1 StartY=-8.75 StartZ=0 EndX=-1 EndY=-5.25 EndZ=0
    g40: LineSegment StartX=-1 StartY=-5.25 StartZ=0 EndX=-4.03109 EndY=-3.5 EndZ=0
    g41: Circle [constr] CenterX=-4.03109 CenterY=-7 CenterZ=0 NormalX=0 NormalY=0 NormalZ=1 AngleXU=0 Radius=3.5
    g42: LineSegment StartX=4.03109 StartY=-3.5 StartZ=0 EndX=1 EndY=-5.25 EndZ=0
    g43: LineSegment StartX=1 StartY=-5.25 StartZ=0 EndX=1 EndY=-8.75 EndZ=0
    g44: LineSegment StartX=1 StartY=-8.75 StartZ=0 EndX=4.03109 EndY=-10.5 EndZ=0
    g45: LineSegment StartX=4.03109 StartY=-10.5 StartZ=0 EndX=7.06218 EndY=-8.75 EndZ=0
    g46: LineSegment StartX=7.06218 StartY=-8.75 StartZ=0 EndX=7.06218 EndY=-5.25 EndZ=0
    g47: LineSegment StartX=7.06218 StartY=-5.25 StartZ=0 EndX=4.03109 EndY=-3.5 EndZ=0
    g48: Circle [constr] CenterX=4.03109 CenterY=-7 CenterZ=0 NormalX=0 NormalY=0 NormalZ=1 AngleXU=0 Radius=3.5
  constraints (117):
    c: Coincident(g0,g1)
    c: Coincident(g1,g2)
    c: Coincident(g2,g3)
    c: Coincident(g3,g4)
    c: Coincident(g4,g5)
    c: Coincident(g5,g0)
    c: Equal(g0, g1-g5) x5
    c: PointOnObject(g0,g6)
    c: PointOnObject(g1,g6)
    c: PointOnObject(g2,g6)
    c: PointOnObject(g3,g6)
    c: PointOnObject(g4,g6)
    c: PointOnObject(g5,g6)
    c: Coincident(g6,g-1)
    c: Diameter(g6) = 7
    c: PointOnObject(g0,g-2)
    c: Coincident(g7,g8)
    c: Coincident(g8,g9)
    c: Coincident(g9,g10)
    c: Coincident(g10,g11)
    c: Coincident(g11,g12)
    c: Coincident(g12,g7)
    c: Equal(g7, g8-g12) x5
    c: PointOnObject(g7,g13)
    c: PointOnObject(g8,g13)
    c: PointOnObject(g9,g13)
    c: PointOnObject(g10,g13)
    c: PointOnObject(g11,g13)
    c: PointOnObject(g12,g13)
    c: PointOnObject(g13,g-1)
    c: Diameter(g13) = 7
    c: Distance(g6,g13) = 8
    c: Horizontal(g0,g10)
    c: Coincident(g14,g15)
    c: Coincident(g15,g16)
    c: Coincident(g16,g17)
    c: Coincident(g17,g18)
    c: Coincident(g18,g19)
    c: Coincident(g19,g14)
    c: Equal(g14, g15-g19) x5
    c: PointOnObject(g14,g20)
    c: PointOnObject(g15,g20)
    c: PointOnObject(g16,g20)
    c: PointOnObject(g17,g20)
    c: PointOnObject(g18,g20)
    c: PointOnObject(g19,g20)
    c: Diameter(g20) = 7
    c: DistanceY(g-1,g20) = 7
    c: Vertical(g18)
    c: Distance(g17,g-2) = 1
    c: Coincident(g21,g22)
    c: Coincident(g22,g23)
    c: Coincident(g23,g24)
    c: Coincident(g24,g25)
    c: Coincident(g25,g26)
    c: Coincident(g26,g21)
    c: Equal(g21, g22-g26) x5
    c: PointOnObject(g21,g27)
    c: PointOnObject(g22,g27)
    c: PointOnObject(g23,g27)
    c: PointOnObject(g24,g27)
    c: PointOnObject(g25,g27)
    c: PointOnObject(g26,g27)
    c: Diameter(g27) = 7
    c: DistanceY(g-1,g27) = 7
    c: DistanceX(g21,g-1) = 1
    c: Vertical(g21)
    c: Coincident(g28,g29)
    c: Coincident(g29,g30)
    c: Coincident(g30,g31)
    c: Coincident(g31,g32)
    c: Coincident(g32,g33)
    c: Coincident(g33,g28)
    c: Equal(g28, g29-g33) x5
    c: PointOnObject(g28,g34)
    c: PointOnObject(g29,g34)
    c: PointOnObject(g30,g34)
    c: PointOnObject(g31,g34)
    c: PointOnObject(g32,g34)
    c: PointOnObject(g33,g34)
    c: PointOnObject(g34,g-1)
    c: Diameter(g34) = 7
    c: Vertical(g31)
    c: DistanceX(g34,g-1) = 8
    c: Coincident(g35,g36)
    c: Coincident(g36,g37)
    c: Coincident(g37,g38)
    c: Coincident(g38,g39)
    c: Coincident(g39,g40)
    c: Coincident(g40,g35)
    c: Equal(g35, g36-g40) x5
    c: PointOnObject(g35,g41)
    c: PointOnObject(g36,g41)
    c: PointOnObject(g37,g41)
    c: PointOnObject(g38,g41)
    c: PointOnObject(g39,g41)
    c: PointOnObject(g40,g41)
    c: Coincident(g42,g43)
    c: Coincident(g43,g44)
    c: Coincident(g44,g45)
    c: Coincident(g45,g46)
    c: Coincident(g46,g47)
    c: Coincident(g47,g42)
    c: Equal(g42, g43-g47) x5
    c: PointOnObject(g42,g48)
    c: PointOnObject(g43,g48)
    c: PointOnObject(g44,g48)
    c: PointOnObject(g45,g48)
    c: PointOnObject(g46,g48)
    c: PointOnObject(g47,g48)
    c: Equal(g41,g48)
    c: Diameter(g41) = 7
    c: Vertical(g39)
    c: Vertical(g43)
    c: Distance(g-2,g39) = 1
    c: Symmetric(g38,g43,g-2)
    c: Distance(g41,g-1) = 7
FEATURE [Part::Extrusion] Extrude602  label="hex204"
  Base = -> Sketch611
  Dir = (0,-1,2e-16)
  DirMode = 2
  FaceMakerClass = Part::FaceMakerBullseye
  FaceMakerMode = 3
  LengthFwd = 10
  LengthRev = 0
  Placement = pos=(48,0,-42) rot=(0,0,1;0rad)
  Solid = true
  Symmetric = false
FEATURE [Sketcher::SketchObject] Sketch612
  ArcFitTolerance = 1e-06
  FullyConstrained = true
  MakeInternals = false
  Placement = pos=(0,0,0) rot=(1,0,0;1.5708rad)
  sketch-geometry (49):
    g0: LineSegment StartX=1e-16 StartY=3.5 StartZ=0 EndX=-3.03109 EndY=1.75 EndZ=0
    g1: LineSegment StartX=-3.03109 StartY=1.75 StartZ=0 EndX=-3.03109 EndY=-1.75 EndZ=0
    g2: LineSegment StartX=-3.03109 StartY=-1.75 StartZ=0 EndX=-1e-16 EndY=-3.5 EndZ=0
    g3: LineSegment StartX=-1e-16 StartY=-3.5 StartZ=0 EndX=3.03109 EndY=-1.75 EndZ=0
    g4: LineSegment StartX=3.03109 StartY=-1.75 StartZ=0 EndX=3.03109 EndY=1.75 EndZ=0
    g5: LineSegment StartX=3.03109 StartY=1.75 StartZ=0 EndX=1e-16 EndY=3.5 EndZ=0
    g6: Circle [constr] CenterX=0 CenterY=0 CenterZ=0 NormalX=0 NormalY=0 NormalZ=1 AngleXU=0 Radius=3.5
    g7: LineSegment StartX=4.96892 StartY=-1.75002 StartZ=0 EndX=8.00002 EndY=-3.5 EndZ=0
    g8: LineSegment StartX=8.00002 StartY=-3.5 StartZ=0 EndX=11.0311 EndY=-1.74998 EndZ=0
    g9: LineSegment StartX=11.0311 StartY=-1.74998 StartZ=0 EndX=11.0311 EndY=1.75002 EndZ=0
    g10: LineSegment StartX=11.0311 StartY=1.75002 StartZ=0 EndX=7.99998 EndY=3.5 EndZ=0
    g11: LineSegment StartX=7.99998 StartY=3.5 StartZ=0 EndX=4.9689 EndY=1.74998 EndZ=0
    g12: LineSegment StartX=4.9689 StartY=1.74998 StartZ=0 EndX=4.96892 EndY=-1.75002 EndZ=0
    g13: Circle [constr] CenterX=8 CenterY=0 CenterZ=0 NormalX=0 NormalY=0 NormalZ=1 AngleXU=0 Radius=3.5
    g14: LineSegment StartX=4.03109 StartY=3.5 StartZ=0 EndX=7.06218 EndY=5.25 EndZ=0
    g15: LineSegment StartX=7.06218 StartY=5.25 StartZ=0 EndX=7.06218 EndY=8.75 EndZ=0
    g16: LineSegment StartX=7.06218 StartY=8.75 StartZ=0 EndX=4.03109 EndY=10.5 EndZ=0
    g17: LineSegment StartX=4.03109 StartY=10.5 StartZ=0 EndX=1 EndY=8.75 EndZ=0
    g18: LineSegment StartX=1 StartY=8.75 StartZ=0 EndX=1 EndY=5.25 EndZ=0
    g19: LineSegment StartX=1 StartY=5.25 StartZ=0 EndX=4.03109 EndY=3.5 EndZ=0
    g20: Circle [constr] CenterX=4.03109 CenterY=7 CenterZ=0 NormalX=0 NormalY=0 NormalZ=1 AngleXU=0 Radius=3.5
    g21: LineSegment StartX=-1 StartY=5.25 StartZ=0 EndX=-1 EndY=8.75 EndZ=0
    g22: LineSegment StartX=-1 StartY=8.75 StartZ=0 EndX=-4.03109 EndY=10.5 EndZ=0
    g23: LineSegment StartX=-4.03109 StartY=10.5 StartZ=0 EndX=-7.06218 EndY=8.75 EndZ=0
    g24: LineSegment StartX=-7.06218 StartY=8.75 StartZ=0 EndX=-7.06218 EndY=5.25 EndZ=0
    g25: LineSegment StartX=-7.06218 StartY=5.25 StartZ=0 EndX=-4.03109 EndY=3.5 EndZ=0
    g26: LineSegment StartX=-4.03109 StartY=3.5 StartZ=0 EndX=-1 EndY=5.25 EndZ=0
    g27: Circle [constr] CenterX=-4.03109 CenterY=7 CenterZ=0 NormalX=0 NormalY=0 NormalZ=1 AngleXU=0 Radius=3.5
    g28: LineSegment StartX=-4.96891 StartY=-1.75 StartZ=0 EndX=-4.96891 EndY=1.75 EndZ=0
    g29: LineSegment StartX=-4.96891 StartY=1.75 StartZ=0 EndX=-8 EndY=3.5 EndZ=0
    g30: LineSegment StartX=-8 StartY=3.5 StartZ=0 EndX=-11.0311 EndY=1.75 EndZ=0
    g31: LineSegment StartX=-11.0311 StartY=1.75 StartZ=0 EndX=-11.0311 EndY=-1.75 EndZ=0
    g32: LineSegment StartX=-11.0311 StartY=-1.75 StartZ=0 EndX=-8 EndY=-3.5 EndZ=0
    g33: LineSegment StartX=-8 StartY=-3.5 StartZ=0 EndX=-4.96891 EndY=-1.75 EndZ=0
    g34: Circle [constr] CenterX=-8 CenterY=0 CenterZ=0 NormalX=0 NormalY=0 NormalZ=1 AngleXU=0 Radius=3.5
    g35: LineSegment StartX=-4.03109 StartY=-3.5 StartZ=0 EndX=-7.06218 EndY=-5.25 EndZ=0
    g36: LineSegment StartX=-7.06218 StartY=-5.25 StartZ=0 EndX=-7.06218 EndY=-8.75 EndZ=0
    g37: LineSegment StartX=-7.06218 StartY=-8.75 StartZ=0 EndX=-4.03109 EndY=-10.5 EndZ=0
    g38: LineSegment StartX=-4.03109 StartY=-10.5 StartZ=0 EndX=-1 EndY=-8.75 EndZ=0
    g39: LineSegment StartX=-1 StartY=-8.75 StartZ=0 EndX=-1 EndY=-5.25 EndZ=0
    g40: LineSegment StartX=-1 StartY=-5.25 StartZ=0 EndX=-4.03109 EndY=-3.5 EndZ=0
    g41: Circle [constr] CenterX=-4.03109 CenterY=-7 CenterZ=0 NormalX=0 NormalY=0 NormalZ=1 AngleXU=0 Radius=3.5
    g42: LineSegment StartX=4.03109 StartY=-3.5 StartZ=0 EndX=1 EndY=-5.25 EndZ=0
    g43: LineSegment StartX=1 StartY=-5.25 StartZ=0 EndX=1 EndY=-8.75 EndZ=0
    g44: LineSegment StartX=1 StartY=-8.75 StartZ=0 EndX=4.03109 EndY=-10.5 EndZ=0
    g45: LineSegment StartX=4.03109 StartY=-10.5 StartZ=0 EndX=7.06218 EndY=-8.75 EndZ=0
    g46: LineSegment StartX=7.06218 StartY=-8.75 StartZ=0 EndX=7.06218 EndY=-5.25 EndZ=0
    g47: LineSegment StartX=7.06218 StartY=-5.25 StartZ=0 EndX=4.03109 EndY=-3.5 EndZ=0
    g48: Circle [constr] CenterX=4.03109 CenterY=-7 CenterZ=0 NormalX=0 NormalY=0 NormalZ=1 AngleXU=0 Radius=3.5
  constraints (117):
    c: Coincident(g0,g1)
    c: Coincident(g1,g2)
    c: Coincident(g2,g3)
    c: Coincident(g3,g4)
    c: Coincident(g4,g5)
    c: Coincident(g5,g0)
    c: Equal(g0, g1-g5) x5
    c: PointOnObject(g0,g6)
    c: PointOnObject(g1,g6)
    c: PointOnObject(g2,g6)
    c: PointOnObject(g3,g6)
    c: PointOnObject(g4,g6)
    c: PointOnObject(g5,g6)
    c: Coincident(g6,g-1)
    c: Diameter(g6) = 7
    c: PointOnObject(g0,g-2)
    c: Coincident(g7,g8)
    c: Coincident(g8,g9)
    c: Coincident(g9,g10)
    c: Coincident(g10,g11)
    c: Coincident(g11,g12)
    c: Coincident(g12,g7)
    c: Equal(g7, g8-g12) x5
    c: PointOnObject(g7,g13)
    c: PointOnObject(g8,g13)
    c: PointOnObject(g9,g13)
    c: PointOnObject(g10,g13)
    c: PointOnObject(g11,g13)
    c: PointOnObject(g12,g13)
    c: PointOnObject(g13,g-1)
    c: Diameter(g13) = 7
    c: Distance(g6,g13) = 8
    c: Horizontal(g0,g10)
    c: Coincident(g14,g15)
    c: Coincident(g15,g16)
    c: Coincident(g16,g17)
    c: Coincident(g17,g18)
    c: Coincident(g18,g19)
    c: Coincident(g19,g14)
    c: Equal(g14, g15-g19) x5
    c: PointOnObject(g14,g20)
    c: PointOnObject(g15,g20)
    c: PointOnObject(g16,g20)
    c: PointOnObject(g17,g20)
    c: PointOnObject(g18,g20)
    c: PointOnObject(g19,g20)
    c: Diameter(g20) = 7
    c: DistanceY(g-1,g20) = 7
    c: Vertical(g18)
    c: Distance(g17,g-2) = 1
    c: Coincident(g21,g22)
    c: Coincident(g22,g23)
    c: Coincident(g23,g24)
    c: Coincident(g24,g25)
    c: Coincident(g25,g26)
    c: Coincident(g26,g21)
    c: Equal(g21, g22-g26) x5
    c: PointOnObject(g21,g27)
    c: PointOnObject(g22,g27)
    c: PointOnObject(g23,g27)
    c: PointOnObject(g24,g27)
    c: PointOnObject(g25,g27)
    c: PointOnObject(g26,g27)
    c: Diameter(g27) = 7
    c: DistanceY(g-1,g27) = 7
    c: DistanceX(g21,g-1) = 1
    c: Vertical(g21)
    c: Coincident(g28,g29)
    c: Coincident(g29,g30)
    c: Coincident(g30,g31)
    c: Coincident(g31,g32)
    c: Coincident(g32,g33)
    c: Coincident(g33,g28)
    c: Equal(g28, g29-g33) x5
    c: PointOnObject(g28,g34)
    c: PointOnObject(g29,g34)
    c: PointOnObject(g30,g34)
    c: PointOnObject(g31,g34)
    c: PointOnObject(g32,g34)
    c: PointOnObject(g33,g34)
    c: PointOnObject(g34,g-1)
    c: Diameter(g34) = 7
    c: Vertical(g31)
    c: DistanceX(g34,g-1) = 8
    c: Coincident(g35,g36)
    c: Coincident(g36,g37)
    c: Coincident(g37,g38)
    c: Coincident(g38,g39)
    c: Coincident(g39,g40)
    c: Coincident(g40,g35)
    c: Equal(g35, g36-g40) x5
    c: PointOnObject(g35,g41)
    c: PointOnObject(g36,g41)
    c: PointOnObject(g37,g41)
    c: PointOnObject(g38,g41)
    c: PointOnObject(g39,g41)
    c: PointOnObject(g40,g41)
    c: Coincident(g42,g43)
    c: Coincident(g43,g44)
    c: Coincident(g44,g45)
    c: Coincident(g45,g46)
    c: Coincident(g46,g47)
    c: Coincident(g47,g42)
    c: Equal(g42, g43-g47) x5
    c: PointOnObject(g42,g48)
    c: PointOnObject(g43,g48)
    c: PointOnObject(g44,g48)
    c: PointOnObject(g45,g48)
    c: PointOnObject(g46,g48)
    c: PointOnObject(g47,g48)
    c: Equal(g41,g48)
    c: Diameter(g41) = 7
    c: Vertical(g39)
    c: Vertical(g43)
    c: Distance(g-2,g39) = 1
    c: Symmetric(g38,g43,g-2)
    c: Distance(g41,g-1) = 7
FEATURE [Part::Extrusion] Extrude603  label="hex205"
  Base = -> Sketch612
  Dir = (0,-1,2e-16)
  DirMode = 2
  FaceMakerClass = Part::FaceMakerBullseye
  FaceMakerMode = 3
  LengthFwd = 10
  LengthRev = 0
  Placement = pos=(68,0,-35) rot=(0,0,1;0rad)
  Solid = true
  Symmetric = false
FEATURE [Sketcher::SketchObject] Sketch613
  ArcFitTolerance = 1e-06
  FullyConstrained = true
  MakeInternals = false
  Placement = pos=(0,0,0) rot=(1,0,0;1.5708rad)
  sketch-geometry (49):
    g0: LineSegment StartX=1e-16 StartY=3.5 StartZ=0 EndX=-3.03109 EndY=1.75 EndZ=0
    g1: LineSegment StartX=-3.03109 StartY=1.75 StartZ=0 EndX=-3.03109 EndY=-1.75 EndZ=0
    g2: LineSegment StartX=-3.03109 StartY=-1.75 StartZ=0 EndX=-1e-16 EndY=-3.5 EndZ=0
    g3: LineSegment StartX=-1e-16 StartY=-3.5 StartZ=0 EndX=3.03109 EndY=-1.75 EndZ=0
    g4: LineSegment StartX=3.03109 StartY=-1.75 StartZ=0 EndX=3.03109 EndY=1.75 EndZ=0
    g5: LineSegment StartX=3.03109 StartY=1.75 StartZ=0 EndX=1e-16 EndY=3.5 EndZ=0
    g6: Circle [constr] CenterX=0 CenterY=0 CenterZ=0 NormalX=0 NormalY=0 NormalZ=1 AngleXU=0 Radius=3.5
    g7: LineSegment StartX=4.96892 StartY=-1.75002 StartZ=0 EndX=8.00002 EndY=-3.5 EndZ=0
    g8: LineSegment StartX=8.00002 StartY=-3.5 StartZ=0 EndX=11.0311 EndY=-1.74998 EndZ=0
    g9: LineSegment StartX=11.0311 StartY=-1.74998 StartZ=0 EndX=11.0311 EndY=1.75002 EndZ=0
    g10: LineSegment StartX=11.0311 StartY=1.75002 StartZ=0 EndX=7.99998 EndY=3.5 EndZ=0
    g11: LineSegment StartX=7.99998 StartY=3.5 StartZ=0 EndX=4.9689 EndY=1.74998 EndZ=0
    g12: LineSegment StartX=4.9689 StartY=1.74998 StartZ=0 EndX=4.96892 EndY=-1.75002 EndZ=0
    g13: Circle [constr] CenterX=8 CenterY=0 CenterZ=0 NormalX=0 NormalY=0 NormalZ=1 AngleXU=0 Radius=3.5
    g14: LineSegment StartX=4.03109 StartY=3.5 StartZ=0 EndX=7.06218 EndY=5.25 EndZ=0
    g15: LineSegment StartX=7.06218 StartY=5.25 StartZ=0 EndX=7.06218 EndY=8.75 EndZ=0
    g16: LineSegment StartX=7.06218 StartY=8.75 StartZ=0 EndX=4.03109 EndY=10.5 EndZ=0
    g17: LineSegment StartX=4.03109 StartY=10.5 StartZ=0 EndX=1 EndY=8.75 EndZ=0
    g18: LineSegment StartX=1 StartY=8.75 StartZ=0 EndX=1 EndY=5.25 EndZ=0
    g19: LineSegment StartX=1 StartY=5.25 StartZ=0 EndX=4.03109 EndY=3.5 EndZ=0
    g20: Circle [constr] CenterX=4.03109 CenterY=7 CenterZ=0 NormalX=0 NormalY=0 NormalZ=1 AngleXU=0 Radius=3.5
    g21: LineSegment StartX=-1 StartY=5.25 StartZ=0 EndX=-1 EndY=8.75 EndZ=0
    g22: LineSegment StartX=-1 StartY=8.75 StartZ=0 EndX=-4.03109 EndY=10.5 EndZ=0
    g23: LineSegment StartX=-4.03109 StartY=10.5 StartZ=0 EndX=-7.06218 EndY=8.75 EndZ=0
    g24: LineSegment StartX=-7.06218 StartY=8.75 StartZ=0 EndX=-7.06218 EndY=5.25 EndZ=0
    g25: LineSegment StartX=-7.06218 StartY=5.25 StartZ=0 EndX=-4.03109 EndY=3.5 EndZ=0
    g26: LineSegment StartX=-4.03109 StartY=3.5 StartZ=0 EndX=-1 EndY=5.25 EndZ=0
    g27: Circle [constr] CenterX=-4.03109 CenterY=7 CenterZ=0 NormalX=0 NormalY=0 NormalZ=1 AngleXU=0 Radius=3.5
    g28: LineSegment StartX=-4.96891 StartY=-1.75 StartZ=0 EndX=-4.96891 EndY=1.75 EndZ=0
    g29: LineSegment StartX=-4.96891 StartY=1.75 StartZ=0 EndX=-8 EndY=3.5 EndZ=0
    g30: LineSegment StartX=-8 StartY=3.5 StartZ=0 EndX=-11.0311 EndY=1.75 EndZ=0
    g31: LineSegment StartX=-11.0311 StartY=1.75 StartZ=0 EndX=-11.0311 EndY=-1.75 EndZ=0
    g32: LineSegment StartX=-11.0311 StartY=-1.75 StartZ=0 EndX=-8 EndY=-3.5 EndZ=0
    g33: LineSegment StartX=-8 StartY=-3.5 StartZ=0 EndX=-4.96891 EndY=-1.75 EndZ=0
    g34: Circle [constr] CenterX=-8 CenterY=0 CenterZ=0 NormalX=0 NormalY=0 NormalZ=1 AngleXU=0 Radius=3.5
    g35: LineSegment StartX=-4.03109 StartY=-3.5 StartZ=0 EndX=-7.06218 EndY=-5.25 EndZ=0
    g36: LineSegment StartX=-7.06218 StartY=-5.25 StartZ=0 EndX=-7.06218 EndY=-8.75 EndZ=0
    g37: LineSegment StartX=-7.06218 StartY=-8.75 StartZ=0 EndX=-4.03109 EndY=-10.5 EndZ=0
    g38: LineSegment StartX=-4.03109 StartY=-10.5 StartZ=0 EndX=-1 EndY=-8.75 EndZ=0
    g39: LineSegment StartX=-1 StartY=-8.75 StartZ=0 EndX=-1 EndY=-5.25 EndZ=0
    g40: LineSegment StartX=-1 StartY=-5.25 StartZ=0 EndX=-4.03109 EndY=-3.5 EndZ=0
    g41: Circle [constr] CenterX=-4.03109 CenterY=-7 CenterZ=0 NormalX=0 NormalY=0 NormalZ=1 AngleXU=0 Radius=3.5
    g42: LineSegment StartX=4.03109 StartY=-3.5 StartZ=0 EndX=1 EndY=-5.25 EndZ=0
    g43: LineSegment StartX=1 StartY=-5.25 StartZ=0 EndX=1 EndY=-8.75 EndZ=0
    g44: LineSegment StartX=1 StartY=-8.75 StartZ=0 EndX=4.03109 EndY=-10.5 EndZ=0
    g45: LineSegment StartX=4.03109 StartY=-10.5 StartZ=0 EndX=7.06218 EndY=-8.75 EndZ=0
    g46: LineSegment StartX=7.06218 StartY=-8.75 StartZ=0 EndX=7.06218 EndY=-5.25 EndZ=0
    g47: LineSegment StartX=7.06218 StartY=-5.25 StartZ=0 EndX=4.03109 EndY=-3.5 EndZ=0
    g48: Circle [constr] CenterX=4.03109 CenterY=-7 CenterZ=0 NormalX=0 NormalY=0 NormalZ=1 AngleXU=0 Radius=3.5
  constraints (117):
    c: Coincident(g0,g1)
    c: Coincident(g1,g2)
    c: Coincident(g2,g3)
    c: Coincident(g3,g4)
    c: Coincident(g4,g5)
    c: Coincident(g5,g0)
    c: Equal(g0, g1-g5) x5
    c: PointOnObject(g0,g6)
    c: PointOnObject(g1,g6)
    c: PointOnObject(g2,g6)
    c: PointOnObject(g3,g6)
    c: PointOnObject(g4,g6)
    c: PointOnObject(g5,g6)
    c: Coincident(g6,g-1)
    c: Diameter(g6) = 7
    c: PointOnObject(g0,g-2)
    c: Coincident(g7,g8)
    c: Coincident(g8,g9)
    c: Coincident(g9,g10)
    c: Coincident(g10,g11)
    c: Coincident(g11,g12)
    c: Coincident(g12,g7)
    c: Equal(g7, g8-g12) x5
    c: PointOnObject(g7,g13)
    c: PointOnObject(g8,g13)
    c: PointOnObject(g9,g13)
    c: PointOnObject(g10,g13)
    c: PointOnObject(g11,g13)
    c: PointOnObject(g12,g13)
    c: PointOnObject(g13,g-1)
    c: Diameter(g13) = 7
    c: Distance(g6,g13) = 8
    c: Horizontal(g0,g10)
    c: Coincident(g14,g15)
    c: Coincident(g15,g16)
    c: Coincident(g16,g17)
    c: Coincident(g17,g18)
    c: Coincident(g18,g19)
    c: Coincident(g19,g14)
    c: Equal(g14, g15-g19) x5
    c: PointOnObject(g14,g20)
    c: PointOnObject(g15,g20)
    c: PointOnObject(g16,g20)
    c: PointOnObject(g17,g20)
    c: PointOnObject(g18,g20)
    c: PointOnObject(g19,g20)
    c: Diameter(g20) = 7
    c: DistanceY(g-1,g20) = 7
    c: Vertical(g18)
    c: Distance(g17,g-2) = 1
    c: Coincident(g21,g22)
    c: Coincident(g22,g23)
    c: Coincident(g23,g24)
    c: Coincident(g24,g25)
    c: Coincident(g25,g26)
    c: Coincident(g26,g21)
    c: Equal(g21, g22-g26) x5
    c: PointOnObject(g21,g27)
    c: PointOnObject(g22,g27)
    c: PointOnObject(g23,g27)
    c: PointOnObject(g24,g27)
    c: PointOnObject(g25,g27)
    c: PointOnObject(g26,g27)
    c: Diameter(g27) = 7
    c: DistanceY(g-1,g27) = 7
    c: DistanceX(g21,g-1) = 1
    c: Vertical(g21)
    c: Coincident(g28,g29)
    c: Coincident(g29,g30)
    c: Coincident(g30,g31)
    c: Coincident(g31,g32)
    c: Coincident(g32,g33)
    c: Coincident(g33,g28)
    c: Equal(g28, g29-g33) x5
    c: PointOnObject(g28,g34)
    c: PointOnObject(g29,g34)
    c: PointOnObject(g30,g34)
    c: PointOnObject(g31,g34)
    c: PointOnObject(g32,g34)
    c: PointOnObject(g33,g34)
    c: PointOnObject(g34,g-1)
    c: Diameter(g34) = 7
    c: Vertical(g31)
    c: DistanceX(g34,g-1) = 8
    c: Coincident(g35,g36)
    c: Coincident(g36,g37)
    c: Coincident(g37,g38)
    c: Coincident(g38,g39)
    c: Coincident(g39,g40)
    c: Coincident(g40,g35)
    c: Equal(g35, g36-g40) x5
    c: PointOnObject(g35,g41)
    c: PointOnObject(g36,g41)
    c: PointOnObject(g37,g41)
    c: PointOnObject(g38,g41)
    c: PointOnObject(g39,g41)
    c: PointOnObject(g40,g41)
    c: Coincident(g42,g43)
    c: Coincident(g43,g44)
    c: Coincident(g44,g45)
    c: Coincident(g45,g46)
    c: Coincident(g46,g47)
    c: Coincident(g47,g42)
    c: Equal(g42, g43-g47) x5
    c: PointOnObject(g42,g48)
    c: PointOnObject(g43,g48)
    c: PointOnObject(g44,g48)
    c: PointOnObject(g45,g48)
    c: PointOnObject(g46,g48)
    c: PointOnObject(g47,g48)
    c: Equal(g41,g48)
    c: Diameter(g41) = 7
    c: Vertical(g39)
    c: Vertical(g43)
    c: Distance(g-2,g39) = 1
    c: Symmetric(g38,g43,g-2)
    c: Distance(g41,g-1) = 7
FEATURE [Part::Extrusion] Extrude604  label="hex206"
  Base = -> Sketch613
  Dir = (0,-1,2e-16)
  DirMode = 2
  FaceMakerClass = Part::FaceMakerBullseye
  FaceMakerMode = 3
  LengthFwd = 10
  LengthRev = 0
  Placement = pos=(72,0,-14) rot=(0,0,1;0rad)
  Solid = true
  Symmetric = false
FEATURE [Sketcher::SketchObject] Sketch614
  ArcFitTolerance = 1e-06
  FullyConstrained = true
  MakeInternals = false
  Placement = pos=(0,0,0) rot=(1,0,0;1.5708rad)
  sketch-geometry (49):
    g0: LineSegment StartX=1e-16 StartY=3.5 StartZ=0 EndX=-3.03109 EndY=1.75 EndZ=0
    g1: LineSegment StartX=-3.03109 StartY=1.75 StartZ=0 EndX=-3.03109 EndY=-1.75 EndZ=0
    g2: LineSegment StartX=-3.03109 StartY=-1.75 StartZ=0 EndX=-1e-16 EndY=-3.5 EndZ=0
    g3: LineSegment StartX=-1e-16 StartY=-3.5 StartZ=0 EndX=3.03109 EndY=-1.75 EndZ=0
    g4: LineSegment StartX=3.03109 StartY=-1.75 StartZ=0 EndX=3.03109 EndY=1.75 EndZ=0
    g5: LineSegment StartX=3.03109 StartY=1.75 StartZ=0 EndX=1e-16 EndY=3.5 EndZ=0
    g6: Circle [constr] CenterX=0 CenterY=0 CenterZ=0 NormalX=0 NormalY=0 NormalZ=1 AngleXU=0 Radius=3.5
    g7: LineSegment StartX=4.96892 StartY=-1.75002 StartZ=0 EndX=8.00002 EndY=-3.5 EndZ=0
    g8: LineSegment StartX=8.00002 StartY=-3.5 StartZ=0 EndX=11.0311 EndY=-1.74998 EndZ=0
    g9: LineSegment StartX=11.0311 StartY=-1.74998 StartZ=0 EndX=11.0311 EndY=1.75002 EndZ=0
    g10: LineSegment StartX=11.0311 StartY=1.75002 StartZ=0 EndX=7.99998 EndY=3.5 EndZ=0
    g11: LineSegment StartX=7.99998 StartY=3.5 StartZ=0 EndX=4.9689 EndY=1.74998 EndZ=0
    g12: LineSegment StartX=4.9689 StartY=1.74998 StartZ=0 EndX=4.96892 EndY=-1.75002 EndZ=0
    g13: Circle [constr] CenterX=8 CenterY=0 CenterZ=0 NormalX=0 NormalY=0 NormalZ=1 AngleXU=0 Radius=3.5
    g14: LineSegment StartX=4.03109 StartY=3.5 StartZ=0 EndX=7.06218 EndY=5.25 EndZ=0
    g15: LineSegment StartX=7.06218 StartY=5.25 StartZ=0 EndX=7.06218 EndY=8.75 EndZ=0
    g16: LineSegment StartX=7.06218 StartY=8.75 StartZ=0 EndX=4.03109 EndY=10.5 EndZ=0
    g17: LineSegment StartX=4.03109 StartY=10.5 StartZ=0 EndX=1 EndY=8.75 EndZ=0
    g18: LineSegment StartX=1 StartY=8.75 StartZ=0 EndX=1 EndY=5.25 EndZ=0
    g19: LineSegment StartX=1 StartY=5.25 StartZ=0 EndX=4.03109 EndY=3.5 EndZ=0
    g20: Circle [constr] CenterX=4.03109 CenterY=7 CenterZ=0 NormalX=0 NormalY=0 NormalZ=1 AngleXU=0 Radius=3.5
    g21: LineSegment StartX=-1 StartY=5.25 StartZ=0 EndX=-1 EndY=8.75 EndZ=0
    g22: LineSegment StartX=-1 StartY=8.75 StartZ=0 EndX=-4.03109 EndY=10.5 EndZ=0
    g23: LineSegment StartX=-4.03109 StartY=10.5 StartZ=0 EndX=-7.06218 EndY=8.75 EndZ=0
    g24: LineSegment StartX=-7.06218 StartY=8.75 StartZ=0 EndX=-7.06218 EndY=5.25 EndZ=0
    g25: LineSegment StartX=-7.06218 StartY=5.25 StartZ=0 EndX=-4.03109 EndY=3.5 EndZ=0
    g26: LineSegment StartX=-4.03109 StartY=3.5 StartZ=0 EndX=-1 EndY=5.25 EndZ=0
    g27: Circle [constr] CenterX=-4.03109 CenterY=7 CenterZ=0 NormalX=0 NormalY=0 NormalZ=1 AngleXU=0 Radius=3.5
    g28: LineSegment StartX=-4.96891 StartY=-1.75 StartZ=0 EndX=-4.96891 EndY=1.75 EndZ=0
    g29: LineSegment StartX=-4.96891 StartY=1.75 StartZ=0 EndX=-8 EndY=3.5 EndZ=0
    g30: LineSegment StartX=-8 StartY=3.5 StartZ=0 EndX=-11.0311 EndY=1.75 EndZ=0
    g31: LineSegment StartX=-11.0311 StartY=1.75 StartZ=0 EndX=-11.0311 EndY=-1.75 EndZ=0
    g32: LineSegment StartX=-11.0311 StartY=-1.75 StartZ=0 EndX=-8 EndY=-3.5 EndZ=0
    g33: LineSegment StartX=-8 StartY=-3.5 StartZ=0 EndX=-4.96891 EndY=-1.75 EndZ=0
    g34: Circle [constr] CenterX=-8 CenterY=0 CenterZ=0 NormalX=0 NormalY=0 NormalZ=1 AngleXU=0 Radius=3.5
    g35: LineSegment StartX=-4.03109 StartY=-3.5 StartZ=0 EndX=-7.06218 EndY=-5.25 EndZ=0
    g36: LineSegment StartX=-7.06218 StartY=-5.25 StartZ=0 EndX=-7.06218 EndY=-8.75 EndZ=0
    g37: LineSegment StartX=-7.06218 StartY=-8.75 StartZ=0 EndX=-4.03109 EndY=-10.5 EndZ=0
    g38: LineSegment StartX=-4.03109 StartY=-10.5 StartZ=0 EndX=-1 EndY=-8.75 EndZ=0
    g39: LineSegment StartX=-1 StartY=-8.75 StartZ=0 EndX=-1 EndY=-5.25 EndZ=0
    g40: LineSegment StartX=-1 StartY=-5.25 StartZ=0 EndX=-4.03109 EndY=-3.5 EndZ=0
    g41: Circle [constr] CenterX=-4.03109 CenterY=-7 CenterZ=0 NormalX=0 NormalY=0 NormalZ=1 AngleXU=0 Radius=3.5
    g42: LineSegment StartX=4.03109 StartY=-3.5 StartZ=0 EndX=1 EndY=-5.25 EndZ=0
    g43: LineSegment StartX=1 StartY=-5.25 StartZ=0 EndX=1 EndY=-8.75 EndZ=0
    g44: LineSegment StartX=1 StartY=-8.75 StartZ=0 EndX=4.03109 EndY=-10.5 EndZ=0
    g45: LineSegment StartX=4.03109 StartY=-10.5 StartZ=0 EndX=7.06218 EndY=-8.75 EndZ=0
    g46: LineSegment StartX=7.06218 StartY=-8.75 StartZ=0 EndX=7.06218 EndY=-5.25 EndZ=0
    g47: LineSegment StartX=7.06218 StartY=-5.25 StartZ=0 EndX=4.03109 EndY=-3.5 EndZ=0
    g48: Circle [constr] CenterX=4.03109 CenterY=-7 CenterZ=0 NormalX=0 NormalY=0 NormalZ=1 AngleXU=0 Radius=3.5
  constraints (117):
    c: Coincident(g0,g1)
    c: Coincident(g1,g2)
    c: Coincident(g2,g3)
    c: Coincident(g3,g4)
    c: Coincident(g4,g5)
    c: Coincident(g5,g0)
    c: Equal(g0, g1-g5) x5
    c: PointOnObject(g0,g6)
    c: PointOnObject(g1,g6)
    c: PointOnObject(g2,g6)
    c: PointOnObject(g3,g6)
    c: PointOnObject(g4,g6)
    c: PointOnObject(g5,g6)
    c: Coincident(g6,g-1)
    c: Diameter(g6) = 7
    c: PointOnObject(g0,g-2)
    c: Coincident(g7,g8)
    c: Coincident(g8,g9)
    c: Coincident(g9,g10)
    c: Coincident(g10,g11)
    c: Coincident(g11,g12)
    c: Coincident(g12,g7)
    c: Equal(g7, g8-g12) x5
    c: PointOnObject(g7,g13)
    c: PointOnObject(g8,g13)
    c: PointOnObject(g9,g13)
    c: PointOnObject(g10,g13)
    c: PointOnObject(g11,g13)
    c: PointOnObject(g12,g13)
    c: PointOnObject(g13,g-1)
    c: Diameter(g13) = 7
    c: Distance(g6,g13) = 8
    c: Horizontal(g0,g10)
    c: Coincident(g14,g15)
    c: Coincident(g15,g16)
    c: Coincident(g16,g17)
    c: Coincident(g17,g18)
    c: Coincident(g18,g19)
    c: Coincident(g19,g14)
    c: Equal(g14, g15-g19) x5
    c: PointOnObject(g14,g20)
    c: PointOnObject(g15,g20)
    c: PointOnObject(g16,g20)
    c: PointOnObject(g17,g20)
    c: PointOnObject(g18,g20)
    c: PointOnObject(g19,g20)
    c: Diameter(g20) = 7
    c: DistanceY(g-1,g20) = 7
    c: Vertical(g18)
    c: Distance(g17,g-2) = 1
    c: Coincident(g21,g22)
    c: Coincident(g22,g23)
    c: Coincident(g23,g24)
    c: Coincident(g24,g25)
    c: Coincident(g25,g26)
    c: Coincident(g26,g21)
    c: Equal(g21, g22-g26) x5
    c: PointOnObject(g21,g27)
    c: PointOnObject(g22,g27)
    c: PointOnObject(g23,g27)
    c: PointOnObject(g24,g27)
    c: PointOnObject(g25,g27)
    c: PointOnObject(g26,g27)
    c: Diameter(g27) = 7
    c: DistanceY(g-1,g27) = 7
    c: DistanceX(g21,g-1) = 1
    c: Vertical(g21)
    c: Coincident(g28,g29)
    c: Coincident(g29,g30)
    c: Coincident(g30,g31)
    c: Coincident(g31,g32)
    c: Coincident(g32,g33)
    c: Coincident(g33,g28)
    c: Equal(g28, g29-g33) x5
    c: PointOnObject(g28,g34)
    c: PointOnObject(g29,g34)
    c: PointOnObject(g30,g34)
    c: PointOnObject(g31,g34)
    c: PointOnObject(g32,g34)
    c: PointOnObject(g33,g34)
    c: PointOnObject(g34,g-1)
    c: Diameter(g34) = 7
    c: Vertical(g31)
    c: DistanceX(g34,g-1) = 8
    c: Coincident(g35,g36)
    c: Coincident(g36,g37)
    c: Coincident(g37,g38)
    c: Coincident(g38,g39)
    c: Coincident(g39,g40)
    c: Coincident(g40,g35)
    c: Equal(g35, g36-g40) x5
    c: PointOnObject(g35,g41)
    c: PointOnObject(g36,g41)
    c: PointOnObject(g37,g41)
    c: PointOnObject(g38,g41)
    c: PointOnObject(g39,g41)
    c: PointOnObject(g40,g41)
    c: Coincident(g42,g43)
    c: Coincident(g43,g44)
    c: Coincident(g44,g45)
    c: Coincident(g45,g46)
    c: Coincident(g46,g47)
    c: Coincident(g47,g42)
    c: Equal(g42, g43-g47) x5
    c: PointOnObject(g42,g48)
    c: PointOnObject(g43,g48)
    c: PointOnObject(g44,g48)
    c: PointOnObject(g45,g48)
    c: PointOnObject(g46,g48)
    c: PointOnObject(g47,g48)
    c: Equal(g41,g48)
    c: Diameter(g41) = 7
    c: Vertical(g39)
    c: Vertical(g43)
    c: Distance(g-2,g39) = 1
    c: Symmetric(g38,g43,g-2)
    c: Distance(g41,g-1) = 7
FEATURE [Part::Extrusion] Extrude605  label="hex207"
  Base = -> Sketch614
  Dir = (0,-1,2e-16)
  DirMode = 2
  FaceMakerClass = Part::FaceMakerBullseye
  FaceMakerMode = 3
  LengthFwd = 10
  LengthRev = 0
  Placement = pos=(72,0,14) rot=(0,0,1;0rad)
  Solid = true
  Symmetric = false
FEATURE [Sketcher::SketchObject] Sketch615
  ArcFitTolerance = 1e-06
  FullyConstrained = true
  MakeInternals = false
  Placement = pos=(0,0,0) rot=(1,0,0;1.5708rad)
  sketch-geometry (49):
    g0: LineSegment StartX=1e-16 StartY=3.5 StartZ=0 EndX=-3.03109 EndY=1.75 EndZ=0
    g1: LineSegment StartX=-3.03109 StartY=1.75 StartZ=0 EndX=-3.03109 EndY=-1.75 EndZ=0
    g2: LineSegment StartX=-3.03109 StartY=-1.75 StartZ=0 EndX=-1e-16 EndY=-3.5 EndZ=0
    g3: LineSegment StartX=-1e-16 StartY=-3.5 StartZ=0 EndX=3.03109 EndY=-1.75 EndZ=0
    g4: LineSegment StartX=3.03109 StartY=-1.75 StartZ=0 EndX=3.03109 EndY=1.75 EndZ=0
    g5: LineSegment StartX=3.03109 StartY=1.75 StartZ=0 EndX=1e-16 EndY=3.5 EndZ=0
    g6: Circle [constr] CenterX=0 CenterY=0 CenterZ=0 NormalX=0 NormalY=0 NormalZ=1 AngleXU=0 Radius=3.5
    g7: LineSegment StartX=4.96892 StartY=-1.75002 StartZ=0 EndX=8.00002 EndY=-3.5 EndZ=0
    g8: LineSegment StartX=8.00002 StartY=-3.5 StartZ=0 EndX=11.0311 EndY=-1.74998 EndZ=0
    g9: LineSegment StartX=11.0311 StartY=-1.74998 StartZ=0 EndX=11.0311 EndY=1.75002 EndZ=0
    g10: LineSegment StartX=11.0311 StartY=1.75002 StartZ=0 EndX=7.99998 EndY=3.5 EndZ=0
    g11: LineSegment StartX=7.99998 StartY=3.5 StartZ=0 EndX=4.9689 EndY=1.74998 EndZ=0
    g12: LineSegment StartX=4.9689 StartY=1.74998 StartZ=0 EndX=4.96892 EndY=-1.75002 EndZ=0
    g13: Circle [constr] CenterX=8 CenterY=0 CenterZ=0 NormalX=0 NormalY=0 NormalZ=1 AngleXU=0 Radius=3.5
    g14: LineSegment StartX=4.03109 StartY=3.5 StartZ=0 EndX=7.06218 EndY=5.25 EndZ=0
    g15: LineSegment StartX=7.06218 StartY=5.25 StartZ=0 EndX=7.06218 EndY=8.75 EndZ=0
    g16: LineSegment StartX=7.06218 StartY=8.75 StartZ=0 EndX=4.03109 EndY=10.5 EndZ=0
    g17: LineSegment StartX=4.03109 StartY=10.5 StartZ=0 EndX=1 EndY=8.75 EndZ=0
    g18: LineSegment StartX=1 StartY=8.75 StartZ=0 EndX=1 EndY=5.25 EndZ=0
    g19: LineSegment StartX=1 StartY=5.25 StartZ=0 EndX=4.03109 EndY=3.5 EndZ=0
    g20: Circle [constr] CenterX=4.03109 CenterY=7 CenterZ=0 NormalX=0 NormalY=0 NormalZ=1 AngleXU=0 Radius=3.5
    g21: LineSegment StartX=-1 StartY=5.25 StartZ=0 EndX=-1 EndY=8.75 EndZ=0
    g22: LineSegment StartX=-1 StartY=8.75 StartZ=0 EndX=-4.03109 EndY=10.5 EndZ=0
    g23: LineSegment StartX=-4.03109 StartY=10.5 StartZ=0 EndX=-7.06218 EndY=8.75 EndZ=0
    g24: LineSegment StartX=-7.06218 StartY=8.75 StartZ=0 EndX=-7.06218 EndY=5.25 EndZ=0
    g25: LineSegment StartX=-7.06218 StartY=5.25 StartZ=0 EndX=-4.03109 EndY=3.5 EndZ=0
    g26: LineSegment StartX=-4.03109 StartY=3.5 StartZ=0 EndX=-1 EndY=5.25 EndZ=0
    g27: Circle [constr] CenterX=-4.03109 CenterY=7 CenterZ=0 NormalX=0 NormalY=0 NormalZ=1 AngleXU=0 Radius=3.5
    g28: LineSegment StartX=-4.96891 StartY=-1.75 StartZ=0 EndX=-4.96891 EndY=1.75 EndZ=0
    g29: LineSegment StartX=-4.96891 StartY=1.75 StartZ=0 EndX=-8 EndY=3.5 EndZ=0
    g30: LineSegment StartX=-8 StartY=3.5 StartZ=0 EndX=-11.0311 EndY=1.75 EndZ=0
    g31: LineSegment StartX=-11.0311 StartY=1.75 StartZ=0 EndX=-11.0311 EndY=-1.75 EndZ=0
    g32: LineSegment StartX=-11.0311 StartY=-1.75 StartZ=0 EndX=-8 EndY=-3.5 EndZ=0
    g33: LineSegment StartX=-8 StartY=-3.5 StartZ=0 EndX=-4.96891 EndY=-1.75 EndZ=0
    g34: Circle [constr] CenterX=-8 CenterY=0 CenterZ=0 NormalX=0 NormalY=0 NormalZ=1 AngleXU=0 Radius=3.5
    g35: LineSegment StartX=-4.03109 StartY=-3.5 StartZ=0 EndX=-7.06218 EndY=-5.25 EndZ=0
    g36: LineSegment StartX=-7.06218 StartY=-5.25 StartZ=0 EndX=-7.06218 EndY=-8.75 EndZ=0
    g37: LineSegment StartX=-7.06218 StartY=-8.75 StartZ=0 EndX=-4.03109 EndY=-10.5 EndZ=0
    g38: LineSegment StartX=-4.03109 StartY=-10.5 StartZ=0 EndX=-1 EndY=-8.75 EndZ=0
    g39: LineSegment StartX=-1 StartY=-8.75 StartZ=0 EndX=-1 EndY=-5.25 EndZ=0
    g40: LineSegment StartX=-1 StartY=-5.25 StartZ=0 EndX=-4.03109 EndY=-3.5 EndZ=0
    g41: Circle [constr] CenterX=-4.03109 CenterY=-7 CenterZ=0 NormalX=0 NormalY=0 NormalZ=1 AngleXU=0 Radius=3.5
    g42: LineSegment StartX=4.03109 StartY=-3.5 StartZ=0 EndX=1 EndY=-5.25 EndZ=0
    g43: LineSegment StartX=1 StartY=-5.25 StartZ=0 EndX=1 EndY=-8.75 EndZ=0
    g44: LineSegment StartX=1 StartY=-8.75 StartZ=0 EndX=4.03109 EndY=-10.5 EndZ=0
    g45: LineSegment StartX=4.03109 StartY=-10.5 StartZ=0 EndX=7.06218 EndY=-8.75 EndZ=0
    g46: LineSegment StartX=7.06218 StartY=-8.75 StartZ=0 EndX=7.06218 EndY=-5.25 EndZ=0
    g47: LineSegment StartX=7.06218 StartY=-5.25 StartZ=0 EndX=4.03109 EndY=-3.5 EndZ=0
    g48: Circle [constr] CenterX=4.03109 CenterY=-7 CenterZ=0 NormalX=0 NormalY=0 NormalZ=1 AngleXU=0 Radius=3.5
  constraints (117):
    c: Coincident(g0,g1)
    c: Coincident(g1,g2)
    c: Coincident(g2,g3)
    c: Coincident(g3,g4)
    c: Coincident(g4,g5)
    c: Coincident(g5,g0)
    c: Equal(g0, g1-g5) x5
    c: PointOnObject(g0,g6)
    c: PointOnObject(g1,g6)
    c: PointOnObject(g2,g6)
    c: PointOnObject(g3,g6)
    c: PointOnObject(g4,g6)
    c: PointOnObject(g5,g6)
    c: Coincident(g6,g-1)
    c: Diameter(g6) = 7
    c: PointOnObject(g0,g-2)
    c: Coincident(g7,g8)
    c: Coincident(g8,g9)
    c: Coincident(g9,g10)
    c: Coincident(g10,g11)
    c: Coincident(g11,g12)
    c: Coincident(g12,g7)
    c: Equal(g7, g8-g12) x5
    c: PointOnObject(g7,g13)
    c: PointOnObject(g8,g13)
    c: PointOnObject(g9,g13)
    c: PointOnObject(g10,g13)
    c: PointOnObject(g11,g13)
    c: PointOnObject(g12,g13)
    c: PointOnObject(g13,g-1)
    c: Diameter(g13) = 7
    c: Distance(g6,g13) = 8
    c: Horizontal(g0,g10)
    c: Coincident(g14,g15)
    c: Coincident(g15,g16)
    c: Coincident(g16,g17)
    c: Coincident(g17,g18)
    c: Coincident(g18,g19)
    c: Coincident(g19,g14)
    c: Equal(g14, g15-g19) x5
    c: PointOnObject(g14,g20)
    c: PointOnObject(g15,g20)
    c: PointOnObject(g16,g20)
    c: PointOnObject(g17,g20)
    c: PointOnObject(g18,g20)
    c: PointOnObject(g19,g20)
    c: Diameter(g20) = 7
    c: DistanceY(g-1,g20) = 7
    c: Vertical(g18)
    c: Distance(g17,g-2) = 1
    c: Coincident(g21,g22)
    c: Coincident(g22,g23)
    c: Coincident(g23,g24)
    c: Coincident(g24,g25)
    c: Coincident(g25,g26)
    c: Coincident(g26,g21)
    c: Equal(g21, g22-g26) x5
    c: PointOnObject(g21,g27)
    c: PointOnObject(g22,g27)
    c: PointOnObject(g23,g27)
    c: PointOnObject(g24,g27)
    c: PointOnObject(g25,g27)
    c: PointOnObject(g26,g27)
    c: Diameter(g27) = 7
    c: DistanceY(g-1,g27) = 7
    c: DistanceX(g21,g-1) = 1
    c: Vertical(g21)
    c: Coincident(g28,g29)
    c: Coincident(g29,g30)
    c: Coincident(g30,g31)
    c: Coincident(g31,g32)
    c: Coincident(g32,g33)
    c: Coincident(g33,g28)
    c: Equal(g28, g29-g33) x5
    c: PointOnObject(g28,g34)
    c: PointOnObject(g29,g34)
    c: PointOnObject(g30,g34)
    c: PointOnObject(g31,g34)
    c: PointOnObject(g32,g34)
    c: PointOnObject(g33,g34)
    c: PointOnObject(g34,g-1)
    c: Diameter(g34) = 7
    c: Vertical(g31)
    c: DistanceX(g34,g-1) = 8
    c: Coincident(g35,g36)
    c: Coincident(g36,g37)
    c: Coincident(g37,g38)
    c: Coincident(g38,g39)
    c: Coincident(g39,g40)
    c: Coincident(g40,g35)
    c: Equal(g35, g36-g40) x5
    c: PointOnObject(g35,g41)
    c: PointOnObject(g36,g41)
    c: PointOnObject(g37,g41)
    c: PointOnObject(g38,g41)
    c: PointOnObject(g39,g41)
    c: PointOnObject(g40,g41)
    c: Coincident(g42,g43)
    c: Coincident(g43,g44)
    c: Coincident(g44,g45)
    c: Coincident(g45,g46)
    c: Coincident(g46,g47)
    c: Coincident(g47,g42)
    c: Equal(g42, g43-g47) x5
    c: PointOnObject(g42,g48)
    c: PointOnObject(g43,g48)
    c: PointOnObject(g44,g48)
    c: PointOnObject(g45,g48)
    c: PointOnObject(g46,g48)
    c: PointOnObject(g47,g48)
    c: Equal(g41,g48)
    c: Diameter(g41) = 7
    c: Vertical(g39)
    c: Vertical(g43)
    c: Distance(g-2,g39) = 1
    c: Symmetric(g38,g43,g-2)
    c: Distance(g41,g-1) = 7
FEATURE [Part::Extrusion] Extrude606  label="hex208"
  Base = -> Sketch615
  Dir = (0,-1,2e-16)
  DirMode = 2
  FaceMakerClass = Part::FaceMakerBullseye
  FaceMakerMode = 3
  LengthFwd = 10
  LengthRev = 0
  Placement = pos=(80,0,0) rot=(0,0,1;0rad)
  Solid = true
  Symmetric = false
FEATURE [Sketcher::SketchObject] Sketch616
  ArcFitTolerance = 1e-06
  FullyConstrained = true
  MakeInternals = false
  Placement = pos=(0,0,0) rot=(1,0,0;1.5708rad)
  sketch-geometry (49):
    g0: LineSegment StartX=1e-16 StartY=3.5 StartZ=0 EndX=-3.03109 EndY=1.75 EndZ=0
    g1: LineSegment StartX=-3.03109 StartY=1.75 StartZ=0 EndX=-3.03109 EndY=-1.75 EndZ=0
    g2: LineSegment StartX=-3.03109 StartY=-1.75 StartZ=0 EndX=-1e-16 EndY=-3.5 EndZ=0
    g3: LineSegment StartX=-1e-16 StartY=-3.5 StartZ=0 EndX=3.03109 EndY=-1.75 EndZ=0
    g4: LineSegment StartX=3.03109 StartY=-1.75 StartZ=0 EndX=3.03109 EndY=1.75 EndZ=0
    g5: LineSegment StartX=3.03109 StartY=1.75 StartZ=0 EndX=1e-16 EndY=3.5 EndZ=0
    g6: Circle [constr] CenterX=0 CenterY=0 CenterZ=0 NormalX=0 NormalY=0 NormalZ=1 AngleXU=0 Radius=3.5
    g7: LineSegment StartX=4.96892 StartY=-1.75002 StartZ=0 EndX=8.00002 EndY=-3.5 EndZ=0
    g8: LineSegment StartX=8.00002 StartY=-3.5 StartZ=0 EndX=11.0311 EndY=-1.74998 EndZ=0
    g9: LineSegment StartX=11.0311 StartY=-1.74998 StartZ=0 EndX=11.0311 EndY=1.75002 EndZ=0
    g10: LineSegment StartX=11.0311 StartY=1.75002 StartZ=0 EndX=7.99998 EndY=3.5 EndZ=0
    g11: LineSegment StartX=7.99998 StartY=3.5 StartZ=0 EndX=4.9689 EndY=1.74998 EndZ=0
    g12: LineSegment StartX=4.9689 StartY=1.74998 StartZ=0 EndX=4.96892 EndY=-1.75002 EndZ=0
    g13: Circle [constr] CenterX=8 CenterY=0 CenterZ=0 NormalX=0 NormalY=0 NormalZ=1 AngleXU=0 Radius=3.5
    g14: LineSegment StartX=4.03109 StartY=3.5 StartZ=0 EndX=7.06218 EndY=5.25 EndZ=0
    g15: LineSegment StartX=7.06218 StartY=5.25 StartZ=0 EndX=7.06218 EndY=8.75 EndZ=0
    g16: LineSegment StartX=7.06218 StartY=8.75 StartZ=0 EndX=4.03109 EndY=10.5 EndZ=0
    g17: LineSegment StartX=4.03109 StartY=10.5 StartZ=0 EndX=1 EndY=8.75 EndZ=0
    g18: LineSegment StartX=1 StartY=8.75 StartZ=0 EndX=1 EndY=5.25 EndZ=0
    g19: LineSegment StartX=1 StartY=5.25 StartZ=0 EndX=4.03109 EndY=3.5 EndZ=0
    g20: Circle [constr] CenterX=4.03109 CenterY=7 CenterZ=0 NormalX=0 NormalY=0 NormalZ=1 AngleXU=0 Radius=3.5
    g21: LineSegment StartX=-1 StartY=5.25 StartZ=0 EndX=-1 EndY=8.75 EndZ=0
    g22: LineSegment StartX=-1 StartY=8.75 StartZ=0 EndX=-4.03109 EndY=10.5 EndZ=0
    g23: LineSegment StartX=-4.03109 StartY=10.5 StartZ=0 EndX=-7.06218 EndY=8.75 EndZ=0
    g24: LineSegment StartX=-7.06218 StartY=8.75 StartZ=0 EndX=-7.06218 EndY=5.25 EndZ=0
    g25: LineSegment StartX=-7.06218 StartY=5.25 StartZ=0 EndX=-4.03109 EndY=3.5 EndZ=0
    g26: LineSegment StartX=-4.03109 StartY=3.5 StartZ=0 EndX=-1 EndY=5.25 EndZ=0
    g27: Circle [constr] CenterX=-4.03109 CenterY=7 CenterZ=0 NormalX=0 NormalY=0 NormalZ=1 AngleXU=0 Radius=3.5
    g28: LineSegment StartX=-4.96891 StartY=-1.75 StartZ=0 EndX=-4.96891 EndY=1.75 EndZ=0
    g29: LineSegment StartX=-4.96891 StartY=1.75 StartZ=0 EndX=-8 EndY=3.5 EndZ=0
    g30: LineSegment StartX=-8 StartY=3.5 StartZ=0 EndX=-11.0311 EndY=1.75 EndZ=0
    g31: LineSegment StartX=-11.0311 StartY=1.75 StartZ=0 EndX=-11.0311 EndY=-1.75 EndZ=0
    g32: LineSegment StartX=-11.0311 StartY=-1.75 StartZ=0 EndX=-8 EndY=-3.5 EndZ=0
    g33: LineSegment StartX=-8 StartY=-3.5 StartZ=0 EndX=-4.96891 EndY=-1.75 EndZ=0
    g34: Circle [constr] CenterX=-8 CenterY=0 CenterZ=0 NormalX=0 NormalY=0 NormalZ=1 AngleXU=0 Radius=3.5
    g35: LineSegment StartX=-4.03109 StartY=-3.5 StartZ=0 EndX=-7.06218 EndY=-5.25 EndZ=0
    g36: LineSegment StartX=-7.06218 StartY=-5.25 StartZ=0 EndX=-7.06218 EndY=-8.75 EndZ=0
    g37: LineSegment StartX=-7.06218 StartY=-8.75 StartZ=0 EndX=-4.03109 EndY=-10.5 EndZ=0
    g38: LineSegment StartX=-4.03109 StartY=-10.5 StartZ=0 EndX=-1 EndY=-8.75 EndZ=0
    g39: LineSegment StartX=-1 StartY=-8.75 StartZ=0 EndX=-1 EndY=-5.25 EndZ=0
    g40: LineSegment StartX=-1 StartY=-5.25 StartZ=0 EndX=-4.03109 EndY=-3.5 EndZ=0
    g41: Circle [constr] CenterX=-4.03109 CenterY=-7 CenterZ=0 NormalX=0 NormalY=0 NormalZ=1 AngleXU=0 Radius=3.5
    g42: LineSegment StartX=4.03109 StartY=-3.5 StartZ=0 EndX=1 EndY=-5.25 EndZ=0
    g43: LineSegment StartX=1 StartY=-5.25 StartZ=0 EndX=1 EndY=-8.75 EndZ=0
    g44: LineSegment StartX=1 StartY=-8.75 StartZ=0 EndX=4.03109 EndY=-10.5 EndZ=0
    g45: LineSegment StartX=4.03109 StartY=-10.5 StartZ=0 EndX=7.06218 EndY=-8.75 EndZ=0
    g46: LineSegment StartX=7.06218 StartY=-8.75 StartZ=0 EndX=7.06218 EndY=-5.25 EndZ=0
    g47: LineSegment StartX=7.06218 StartY=-5.25 StartZ=0 EndX=4.03109 EndY=-3.5 EndZ=0
    g48: Circle [constr] CenterX=4.03109 CenterY=-7 CenterZ=0 NormalX=0 NormalY=0 NormalZ=1 AngleXU=0 Radius=3.5
  constraints (117):
    c: Coincident(g0,g1)
    c: Coincident(g1,g2)
    c: Coincident(g2,g3)
    c: Coincident(g3,g4)
    c: Coincident(g4,g5)
    c: Coincident(g5,g0)
    c: Equal(g0, g1-g5) x5
    c: PointOnObject(g0,g6)
    c: PointOnObject(g1,g6)
    c: PointOnObject(g2,g6)
    c: PointOnObject(g3,g6)
    c: PointOnObject(g4,g6)
    c: PointOnObject(g5,g6)
    c: Coincident(g6,g-1)
    c: Diameter(g6) = 7
    c: PointOnObject(g0,g-2)
    c: Coincident(g7,g8)
    c: Coincident(g8,g9)
    c: Coincident(g9,g10)
    c: Coincident(g10,g11)
    c: Coincident(g11,g12)
    c: Coincident(g12,g7)
    c: Equal(g7, g8-g12) x5
    c: PointOnObject(g7,g13)
    c: PointOnObject(g8,g13)
    c: PointOnObject(g9,g13)
    c: PointOnObject(g10,g13)
    c: PointOnObject(g11,g13)
    c: PointOnObject(g12,g13)
    c: PointOnObject(g13,g-1)
    c: Diameter(g13) = 7
    c: Distance(g6,g13) = 8
    c: Horizontal(g0,g10)
    c: Coincident(g14,g15)
    c: Coincident(g15,g16)
    c: Coincident(g16,g17)
    c: Coincident(g17,g18)
    c: Coincident(g18,g19)
    c: Coincident(g19,g14)
    c: Equal(g14, g15-g19) x5
    c: PointOnObject(g14,g20)
    c: PointOnObject(g15,g20)
    c: PointOnObject(g16,g20)
    c: PointOnObject(g17,g20)
    c: PointOnObject(g18,g20)
    c: PointOnObject(g19,g20)
    c: Diameter(g20) = 7
    c: DistanceY(g-1,g20) = 7
    c: Vertical(g18)
    c: Distance(g17,g-2) = 1
    c: Coincident(g21,g22)
    c: Coincident(g22,g23)
    c: Coincident(g23,g24)
    c: Coincident(g24,g25)
    c: Coincident(g25,g26)
    c: Coincident(g26,g21)
    c: Equal(g21, g22-g26) x5
    c: PointOnObject(g21,g27)
    c: PointOnObject(g22,g27)
    c: PointOnObject(g23,g27)
    c: PointOnObject(g24,g27)
    c: PointOnObject(g25,g27)
    c: PointOnObject(g26,g27)
    c: Diameter(g27) = 7
    c: DistanceY(g-1,g27) = 7
    c: DistanceX(g21,g-1) = 1
    c: Vertical(g21)
    c: Coincident(g28,g29)
    c: Coincident(g29,g30)
    c: Coincident(g30,g31)
    c: Coincident(g31,g32)
    c: Coincident(g32,g33)
    c: Coincident(g33,g28)
    c: Equal(g28, g29-g33) x5
    c: PointOnObject(g28,g34)
    c: PointOnObject(g29,g34)
    c: PointOnObject(g30,g34)
    c: PointOnObject(g31,g34)
    c: PointOnObject(g32,g34)
    c: PointOnObject(g33,g34)
    c: PointOnObject(g34,g-1)
    c: Diameter(g34) = 7
    c: Vertical(g31)
    c: DistanceX(g34,g-1) = 8
    c: Coincident(g35,g36)
    c: Coincident(g36,g37)
    c: Coincident(g37,g38)
    c: Coincident(g38,g39)
    c: Coincident(g39,g40)
    c: Coincident(g40,g35)
    c: Equal(g35, g36-g40) x5
    c: PointOnObject(g35,g41)
    c: PointOnObject(g36,g41)
    c: PointOnObject(g37,g41)
    c: PointOnObject(g38,g41)
    c: PointOnObject(g39,g41)
    c: PointOnObject(g40,g41)
    c: Coincident(g42,g43)
    c: Coincident(g43,g44)
    c: Coincident(g44,g45)
    c: Coincident(g45,g46)
    c: Coincident(g46,g47)
    c: Coincident(g47,g42)
    c: Equal(g42, g43-g47) x5
    c: PointOnObject(g42,g48)
    c: PointOnObject(g43,g48)
    c: PointOnObject(g44,g48)
    c: PointOnObject(g45,g48)
    c: PointOnObject(g46,g48)
    c: PointOnObject(g47,g48)
    c: Equal(g41,g48)
    c: Diameter(g41) = 7
    c: Vertical(g39)
    c: Vertical(g43)
    c: Distance(g-2,g39) = 1
    c: Symmetric(g38,g43,g-2)
    c: Distance(g41,g-1) = 7
FEATURE [Part::Extrusion] Extrude607  label="hex209"
  Base = -> Sketch616
  Dir = (0,-1,2e-16)
  DirMode = 2
  FaceMakerClass = Part::FaceMakerBullseye
  FaceMakerMode = 3
  LengthFwd = 10
  LengthRev = 0
  Placement = pos=(104,0,0) rot=(0,0,1;0rad)
  Solid = true
  Symmetric = false
FEATURE [Sketcher::SketchObject] Sketch617
  ArcFitTolerance = 1e-06
  FullyConstrained = true
  MakeInternals = false
  Placement = pos=(0,0,0) rot=(1,0,0;1.5708rad)
  sketch-geometry (49):
    g0: LineSegment StartX=1e-16 StartY=3.5 StartZ=0 EndX=-3.03109 EndY=1.75 EndZ=0
    g1: LineSegment StartX=-3.03109 StartY=1.75 StartZ=0 EndX=-3.03109 EndY=-1.75 EndZ=0
    g2: LineSegment StartX=-3.03109 StartY=-1.75 StartZ=0 EndX=-1e-16 EndY=-3.5 EndZ=0
    g3: LineSegment StartX=-1e-16 StartY=-3.5 StartZ=0 EndX=3.03109 EndY=-1.75 EndZ=0
    g4: LineSegment StartX=3.03109 StartY=-1.75 StartZ=0 EndX=3.03109 EndY=1.75 EndZ=0
    g5: LineSegment StartX=3.03109 StartY=1.75 StartZ=0 EndX=1e-16 EndY=3.5 EndZ=0
    g6: Circle [constr] CenterX=0 CenterY=0 CenterZ=0 NormalX=0 NormalY=0 NormalZ=1 AngleXU=0 Radius=3.5
    g7: LineSegment StartX=4.96892 StartY=-1.75002 StartZ=0 EndX=8.00002 EndY=-3.5 EndZ=0
    g8: LineSegment StartX=8.00002 StartY=-3.5 StartZ=0 EndX=11.0311 EndY=-1.74998 EndZ=0
    g9: LineSegment StartX=11.0311 StartY=-1.74998 StartZ=0 EndX=11.0311 EndY=1.75002 EndZ=0
    g10: LineSegment StartX=11.0311 StartY=1.75002 StartZ=0 EndX=7.99998 EndY=3.5 EndZ=0
    g11: LineSegment StartX=7.99998 StartY=3.5 StartZ=0 EndX=4.9689 EndY=1.74998 EndZ=0
    g12: LineSegment StartX=4.9689 StartY=1.74998 StartZ=0 EndX=4.96892 EndY=-1.75002 EndZ=0
    g13: Circle [constr] CenterX=8 CenterY=0 CenterZ=0 NormalX=0 NormalY=0 NormalZ=1 AngleXU=0 Radius=3.5
    g14: LineSegment StartX=4.03109 StartY=3.5 StartZ=0 EndX=7.06218 EndY=5.25 EndZ=0
    g15: LineSegment StartX=7.06218 StartY=5.25 StartZ=0 EndX=7.06218 EndY=8.75 EndZ=0
    g16: LineSegment StartX=7.06218 StartY=8.75 StartZ=0 EndX=4.03109 EndY=10.5 EndZ=0
    g17: LineSegment StartX=4.03109 StartY=10.5 StartZ=0 EndX=1 EndY=8.75 EndZ=0
    g18: LineSegment StartX=1 StartY=8.75 StartZ=0 EndX=1 EndY=5.25 EndZ=0
    g19: LineSegment StartX=1 StartY=5.25 StartZ=0 EndX=4.03109 EndY=3.5 EndZ=0
    g20: Circle [constr] CenterX=4.03109 CenterY=7 CenterZ=0 NormalX=0 NormalY=0 NormalZ=1 AngleXU=0 Radius=3.5
    g21: LineSegment StartX=-1 StartY=5.25 StartZ=0 EndX=-1 EndY=8.75 EndZ=0
    g22: LineSegment StartX=-1 StartY=8.75 StartZ=0 EndX=-4.03109 EndY=10.5 EndZ=0
    g23: LineSegment StartX=-4.03109 StartY=10.5 StartZ=0 EndX=-7.06218 EndY=8.75 EndZ=0
    g24: LineSegment StartX=-7.06218 StartY=8.75 StartZ=0 EndX=-7.06218 EndY=5.25 EndZ=0
    g25: LineSegment StartX=-7.06218 StartY=5.25 StartZ=0 EndX=-4.03109 EndY=3.5 EndZ=0
    g26: LineSegment StartX=-4.03109 StartY=3.5 StartZ=0 EndX=-1 EndY=5.25 EndZ=0
    g27: Circle [constr] CenterX=-4.03109 CenterY=7 CenterZ=0 NormalX=0 NormalY=0 NormalZ=1 AngleXU=0 Radius=3.5
    g28: LineSegment StartX=-4.96891 StartY=-1.75 StartZ=0 EndX=-4.96891 EndY=1.75 EndZ=0
    g29: LineSegment StartX=-4.96891 StartY=1.75 StartZ=0 EndX=-8 EndY=3.5 EndZ=0
    g30: LineSegment StartX=-8 StartY=3.5 StartZ=0 EndX=-11.0311 EndY=1.75 EndZ=0
    g31: LineSegment StartX=-11.0311 StartY=1.75 StartZ=0 EndX=-11.0311 EndY=-1.75 EndZ=0
    g32: LineSegment StartX=-11.0311 StartY=-1.75 StartZ=0 EndX=-8 EndY=-3.5 EndZ=0
    g33: LineSegment StartX=-8 StartY=-3.5 StartZ=0 EndX=-4.96891 EndY=-1.75 EndZ=0
    g34: Circle [constr] CenterX=-8 CenterY=0 CenterZ=0 NormalX=0 NormalY=0 NormalZ=1 AngleXU=0 Radius=3.5
    g35: LineSegment StartX=-4.03109 StartY=-3.5 StartZ=0 EndX=-7.06218 EndY=-5.25 EndZ=0
    g36: LineSegment StartX=-7.06218 StartY=-5.25 StartZ=0 EndX=-7.06218 EndY=-8.75 EndZ=0
    g37: LineSegment StartX=-7.06218 StartY=-8.75 StartZ=0 EndX=-4.03109 EndY=-10.5 EndZ=0
    g38: LineSegment StartX=-4.03109 StartY=-10.5 StartZ=0 EndX=-1 EndY=-8.75 EndZ=0
    g39: LineSegment StartX=-1 StartY=-8.75 StartZ=0 EndX=-1 EndY=-5.25 EndZ=0
    g40: LineSegment StartX=-1 StartY=-5.25 StartZ=0 EndX=-4.03109 EndY=-3.5 EndZ=0
    g41: Circle [constr] CenterX=-4.03109 CenterY=-7 CenterZ=0 NormalX=0 NormalY=0 NormalZ=1 AngleXU=0 Radius=3.5
    g42: LineSegment StartX=4.03109 StartY=-3.5 StartZ=0 EndX=1 EndY=-5.25 EndZ=0
    g43: LineSegment StartX=1 StartY=-5.25 StartZ=0 EndX=1 EndY=-8.75 EndZ=0
    g44: LineSegment StartX=1 StartY=-8.75 StartZ=0 EndX=4.03109 EndY=-10.5 EndZ=0
    g45: LineSegment StartX=4.03109 StartY=-10.5 StartZ=0 EndX=7.06218 EndY=-8.75 EndZ=0
    g46: LineSegment StartX=7.06218 StartY=-8.75 StartZ=0 EndX=7.06218 EndY=-5.25 EndZ=0
    g47: LineSegment StartX=7.06218 StartY=-5.25 StartZ=0 EndX=4.03109 EndY=-3.5 EndZ=0
    g48: Circle [constr] CenterX=4.03109 CenterY=-7 CenterZ=0 NormalX=0 NormalY=0 NormalZ=1 AngleXU=0 Radius=3.5
  constraints (117):
    c: Coincident(g0,g1)
    c: Coincident(g1,g2)
    c: Coincident(g2,g3)
    c: Coincident(g3,g4)
    c: Coincident(g4,g5)
    c: Coincident(g5,g0)
    c: Equal(g0, g1-g5) x5
    c: PointOnObject(g0,g6)
    c: PointOnObject(g1,g6)
    c: PointOnObject(g2,g6)
    c: PointOnObject(g3,g6)
    c: PointOnObject(g4,g6)
    c: PointOnObject(g5,g6)
    c: Coincident(g6,g-1)
    c: Diameter(g6) = 7
    c: PointOnObject(g0,g-2)
    c: Coincident(g7,g8)
    c: Coincident(g8,g9)
    c: Coincident(g9,g10)
    c: Coincident(g10,g11)
    c: Coincident(g11,g12)
    c: Coincident(g12,g7)
    c: Equal(g7, g8-g12) x5
    c: PointOnObject(g7,g13)
    c: PointOnObject(g8,g13)
    c: PointOnObject(g9,g13)
    c: PointOnObject(g10,g13)
    c: PointOnObject(g11,g13)
    c: PointOnObject(g12,g13)
    c: PointOnObject(g13,g-1)
    c: Diameter(g13) = 7
    c: Distance(g6,g13) = 8
    c: Horizontal(g0,g10)
    c: Coincident(g14,g15)
    c: Coincident(g15,g16)
    c: Coincident(g16,g17)
    c: Coincident(g17,g18)
    c: Coincident(g18,g19)
    c: Coincident(g19,g14)
    c: Equal(g14, g15-g19) x5
    c: PointOnObject(g14,g20)
    c: PointOnObject(g15,g20)
    c: PointOnObject(g16,g20)
    c: PointOnObject(g17,g20)
    c: PointOnObject(g18,g20)
    c: PointOnObject(g19,g20)
    c: Diameter(g20) = 7
    c: DistanceY(g-1,g20) = 7
    c: Vertical(g18)
    c: Distance(g17,g-2) = 1
    c: Coincident(g21,g22)
    c: Coincident(g22,g23)
    c: Coincident(g23,g24)
    c: Coincident(g24,g25)
    c: Coincident(g25,g26)
    c: Coincident(g26,g21)
    c: Equal(g21, g22-g26) x5
    c: PointOnObject(g21,g27)
    c: PointOnObject(g22,g27)
    c: PointOnObject(g23,g27)
    c: PointOnObject(g24,g27)
    c: PointOnObject(g25,g27)
    c: PointOnObject(g26,g27)
    c: Diameter(g27) = 7
    c: DistanceY(g-1,g27) = 7
    c: DistanceX(g21,g-1) = 1
    c: Vertical(g21)
    c: Coincident(g28,g29)
    c: Coincident(g29,g30)
    c: Coincident(g30,g31)
    c: Coincident(g31,g32)
    c: Coincident(g32,g33)
    c: Coincident(g33,g28)
    c: Equal(g28, g29-g33) x5
    c: PointOnObject(g28,g34)
    c: PointOnObject(g29,g34)
    c: PointOnObject(g30,g34)
    c: PointOnObject(g31,g34)
    c: PointOnObject(g32,g34)
    c: PointOnObject(g33,g34)
    c: PointOnObject(g34,g-1)
    c: Diameter(g34) = 7
    c: Vertical(g31)
    c: DistanceX(g34,g-1) = 8
    c: Coincident(g35,g36)
    c: Coincident(g36,g37)
    c: Coincident(g37,g38)
    c: Coincident(g38,g39)
    c: Coincident(g39,g40)
    c: Coincident(g40,g35)
    c: Equal(g35, g36-g40) x5
    c: PointOnObject(g35,g41)
    c: PointOnObject(g36,g41)
    c: PointOnObject(g37,g41)
    c: PointOnObject(g38,g41)
    c: PointOnObject(g39,g41)
    c: PointOnObject(g40,g41)
    c: Coincident(g42,g43)
    c: Coincident(g43,g44)
    c: Coincident(g44,g45)
    c: Coincident(g45,g46)
    c: Coincident(g46,g47)
    c: Coincident(g47,g42)
    c: Equal(g42, g43-g47) x5
    c: PointOnObject(g42,g48)
    c: PointOnObject(g43,g48)
    c: PointOnObject(g44,g48)
    c: PointOnObject(g45,g48)
    c: PointOnObject(g46,g48)
    c: PointOnObject(g47,g48)
    c: Equal(g41,g48)
    c: Diameter(g41) = 7
    c: Vertical(g39)
    c: Vertical(g43)
    c: Distance(g-2,g39) = 1
    c: Symmetric(g38,g43,g-2)
    c: Distance(g41,g-1) = 7
FEATURE [Part::Extrusion] Extrude608  label="hex210"
  Base = -> Sketch617
  Dir = (0,-1,2e-16)
  DirMode = 2
  FaceMakerClass = Part::FaceMakerBullseye
  FaceMakerMode = 3
  LengthFwd = 10
  LengthRev = 0
  Placement = pos=(96,0,-14) rot=(0,0,1;0rad)
  Solid = true
  Symmetric = false
FEATURE [Sketcher::SketchObject] Sketch618
  ArcFitTolerance = 1e-06
  FullyConstrained = true
  MakeInternals = false
  Placement = pos=(0,0,0) rot=(1,0,0;1.5708rad)
  sketch-geometry (49):
    g0: LineSegment StartX=1e-16 StartY=3.5 StartZ=0 EndX=-3.03109 EndY=1.75 EndZ=0
    g1: LineSegment StartX=-3.03109 StartY=1.75 StartZ=0 EndX=-3.03109 EndY=-1.75 EndZ=0
    g2: LineSegment StartX=-3.03109 StartY=-1.75 StartZ=0 EndX=-1e-16 EndY=-3.5 EndZ=0
    g3: LineSegment StartX=-1e-16 StartY=-3.5 StartZ=0 EndX=3.03109 EndY=-1.75 EndZ=0
    g4: LineSegment StartX=3.03109 StartY=-1.75 StartZ=0 EndX=3.03109 EndY=1.75 EndZ=0
    g5: LineSegment StartX=3.03109 StartY=1.75 StartZ=0 EndX=1e-16 EndY=3.5 EndZ=0
    g6: Circle [constr] CenterX=0 CenterY=0 CenterZ=0 NormalX=0 NormalY=0 NormalZ=1 AngleXU=0 Radius=3.5
    g7: LineSegment StartX=4.96892 StartY=-1.75002 StartZ=0 EndX=8.00002 EndY=-3.5 EndZ=0
    g8: LineSegment StartX=8.00002 StartY=-3.5 StartZ=0 EndX=11.0311 EndY=-1.74998 EndZ=0
    g9: LineSegment StartX=11.0311 StartY=-1.74998 StartZ=0 EndX=11.0311 EndY=1.75002 EndZ=0
    g10: LineSegment StartX=11.0311 StartY=1.75002 StartZ=0 EndX=7.99998 EndY=3.5 EndZ=0
    g11: LineSegment StartX=7.99998 StartY=3.5 StartZ=0 EndX=4.9689 EndY=1.74998 EndZ=0
    g12: LineSegment StartX=4.9689 StartY=1.74998 StartZ=0 EndX=4.96892 EndY=-1.75002 EndZ=0
    g13: Circle [constr] CenterX=8 CenterY=0 CenterZ=0 NormalX=0 NormalY=0 NormalZ=1 AngleXU=0 Radius=3.5
    g14: LineSegment StartX=4.03109 StartY=3.5 StartZ=0 EndX=7.06218 EndY=5.25 EndZ=0
    g15: LineSegment StartX=7.06218 StartY=5.25 StartZ=0 EndX=7.06218 EndY=8.75 EndZ=0
    g16: LineSegment StartX=7.06218 StartY=8.75 StartZ=0 EndX=4.03109 EndY=10.5 EndZ=0
    g17: LineSegment StartX=4.03109 StartY=10.5 StartZ=0 EndX=1 EndY=8.75 EndZ=0
    g18: LineSegment StartX=1 StartY=8.75 StartZ=0 EndX=1 EndY=5.25 EndZ=0
    g19: LineSegment StartX=1 StartY=5.25 StartZ=0 EndX=4.03109 EndY=3.5 EndZ=0
    g20: Circle [constr] CenterX=4.03109 CenterY=7 CenterZ=0 NormalX=0 NormalY=0 NormalZ=1 AngleXU=0 Radius=3.5
    g21: LineSegment StartX=-1 StartY=5.25 StartZ=0 EndX=-1 EndY=8.75 EndZ=0
    g22: LineSegment StartX=-1 StartY=8.75 StartZ=0 EndX=-4.03109 EndY=10.5 EndZ=0
    g23: LineSegment StartX=-4.03109 StartY=10.5 StartZ=0 EndX=-7.06218 EndY=8.75 EndZ=0
    g24: LineSegment StartX=-7.06218 StartY=8.75 StartZ=0 EndX=-7.06218 EndY=5.25 EndZ=0
    g25: LineSegment StartX=-7.06218 StartY=5.25 StartZ=0 EndX=-4.03109 EndY=3.5 EndZ=0
    g26: LineSegment StartX=-4.03109 StartY=3.5 StartZ=0 EndX=-1 EndY=5.25 EndZ=0
    g27: Circle [constr] CenterX=-4.03109 CenterY=7 CenterZ=0 NormalX=0 NormalY=0 NormalZ=1 AngleXU=0 Radius=3.5
    g28: LineSegment StartX=-4.96891 StartY=-1.75 StartZ=0 EndX=-4.96891 EndY=1.75 EndZ=0
    g29: LineSegment StartX=-4.96891 StartY=1.75 StartZ=0 EndX=-8 EndY=3.5 EndZ=0
    g30: LineSegment StartX=-8 StartY=3.5 StartZ=0 EndX=-11.0311 EndY=1.75 EndZ=0
    g31: LineSegment StartX=-11.0311 StartY=1.75 StartZ=0 EndX=-11.0311 EndY=-1.75 EndZ=0
    g32: LineSegment StartX=-11.0311 StartY=-1.75 StartZ=0 EndX=-8 EndY=-3.5 EndZ=0
    g33: LineSegment StartX=-8 StartY=-3.5 StartZ=0 EndX=-4.96891 EndY=-1.75 EndZ=0
    g34: Circle [constr] CenterX=-8 CenterY=0 CenterZ=0 NormalX=0 NormalY=0 NormalZ=1 AngleXU=0 Radius=3.5
    g35: LineSegment StartX=-4.03109 StartY=-3.5 StartZ=0 EndX=-7.06218 EndY=-5.25 EndZ=0
    g36: LineSegment StartX=-7.06218 StartY=-5.25 StartZ=0 EndX=-7.06218 EndY=-8.75 EndZ=0
    g37: LineSegment StartX=-7.06218 StartY=-8.75 StartZ=0 EndX=-4.03109 EndY=-10.5 EndZ=0
    g38: LineSegment StartX=-4.03109 StartY=-10.5 StartZ=0 EndX=-1 EndY=-8.75 EndZ=0
    g39: LineSegment StartX=-1 StartY=-8.75 StartZ=0 EndX=-1 EndY=-5.25 EndZ=0
    g40: LineSegment StartX=-1 StartY=-5.25 StartZ=0 EndX=-4.03109 EndY=-3.5 EndZ=0
    g41: Circle [constr] CenterX=-4.03109 CenterY=-7 CenterZ=0 NormalX=0 NormalY=0 NormalZ=1 AngleXU=0 Radius=3.5
    g42: LineSegment StartX=4.03109 StartY=-3.5 StartZ=0 EndX=1 EndY=-5.25 EndZ=0
    g43: LineSegment StartX=1 StartY=-5.25 StartZ=0 EndX=1 EndY=-8.75 EndZ=0
    g44: LineSegment StartX=1 StartY=-8.75 StartZ=0 EndX=4.03109 EndY=-10.5 EndZ=0
    g45: LineSegment StartX=4.03109 StartY=-10.5 StartZ=0 EndX=7.06218 EndY=-8.75 EndZ=0
    g46: LineSegment StartX=7.06218 StartY=-8.75 StartZ=0 EndX=7.06218 EndY=-5.25 EndZ=0
    g47: LineSegment StartX=7.06218 StartY=-5.25 StartZ=0 EndX=4.03109 EndY=-3.5 EndZ=0
    g48: Circle [constr] CenterX=4.03109 CenterY=-7 CenterZ=0 NormalX=0 NormalY=0 NormalZ=1 AngleXU=0 Radius=3.5
  constraints (117):
    c: Coincident(g0,g1)
    c: Coincident(g1,g2)
    c: Coincident(g2,g3)
    c: Coincident(g3,g4)
    c: Coincident(g4,g5)
    c: Coincident(g5,g0)
    c: Equal(g0, g1-g5) x5
    c: PointOnObject(g0,g6)
    c: PointOnObject(g1,g6)
    c: PointOnObject(g2,g6)
    c: PointOnObject(g3,g6)
    c: PointOnObject(g4,g6)
    c: PointOnObject(g5,g6)
    c: Coincident(g6,g-1)
    c: Diameter(g6) = 7
    c: PointOnObject(g0,g-2)
    c: Coincident(g7,g8)
    c: Coincident(g8,g9)
    c: Coincident(g9,g10)
    c: Coincident(g10,g11)
    c: Coincident(g11,g12)
    c: Coincident(g12,g7)
    c: Equal(g7, g8-g12) x5
    c: PointOnObject(g7,g13)
    c: PointOnObject(g8,g13)
    c: PointOnObject(g9,g13)
    c: PointOnObject(g10,g13)
    c: PointOnObject(g11,g13)
    c: PointOnObject(g12,g13)
    c: PointOnObject(g13,g-1)
    c: Diameter(g13) = 7
    c: Distance(g6,g13) = 8
    c: Horizontal(g0,g10)
    c: Coincident(g14,g15)
    c: Coincident(g15,g16)
    c: Coincident(g16,g17)
    c: Coincident(g17,g18)
    c: Coincident(g18,g19)
    c: Coincident(g19,g14)
    c: Equal(g14, g15-g19) x5
    c: PointOnObject(g14,g20)
    c: PointOnObject(g15,g20)
    c: PointOnObject(g16,g20)
    c: PointOnObject(g17,g20)
    c: PointOnObject(g18,g20)
    c: PointOnObject(g19,g20)
    c: Diameter(g20) = 7
    c: DistanceY(g-1,g20) = 7
    c: Vertical(g18)
    c: Distance(g17,g-2) = 1
    c: Coincident(g21,g22)
    c: Coincident(g22,g23)
    c: Coincident(g23,g24)
    c: Coincident(g24,g25)
    c: Coincident(g25,g26)
    c: Coincident(g26,g21)
    c: Equal(g21, g22-g26) x5
    c: PointOnObject(g21,g27)
    c: PointOnObject(g22,g27)
    c: PointOnObject(g23,g27)
    c: PointOnObject(g24,g27)
    c: PointOnObject(g25,g27)
    c: PointOnObject(g26,g27)
    c: Diameter(g27) = 7
    c: DistanceY(g-1,g27) = 7
    c: DistanceX(g21,g-1) = 1
    c: Vertical(g21)
    c: Coincident(g28,g29)
    c: Coincident(g29,g30)
    c: Coincident(g30,g31)
    c: Coincident(g31,g32)
    c: Coincident(g32,g33)
    c: Coincident(g33,g28)
    c: Equal(g28, g29-g33) x5
    c: PointOnObject(g28,g34)
    c: PointOnObject(g29,g34)
    c: PointOnObject(g30,g34)
    c: PointOnObject(g31,g34)
    c: PointOnObject(g32,g34)
    c: PointOnObject(g33,g34)
    c: PointOnObject(g34,g-1)
    c: Diameter(g34) = 7
    c: Vertical(g31)
    c: DistanceX(g34,g-1) = 8
    c: Coincident(g35,g36)
    c: Coincident(g36,g37)
    c: Coincident(g37,g38)
    c: Coincident(g38,g39)
    c: Coincident(g39,g40)
    c: Coincident(g40,g35)
    c: Equal(g35, g36-g40) x5
    c: PointOnObject(g35,g41)
    c: PointOnObject(g36,g41)
    c: PointOnObject(g37,g41)
    c: PointOnObject(g38,g41)
    c: PointOnObject(g39,g41)
    c: PointOnObject(g40,g41)
    c: Coincident(g42,g43)
    c: Coincident(g43,g44)
    c: Coincident(g44,g45)
    c: Coincident(g45,g46)
    c: Coincident(g46,g47)
    c: Coincident(g47,g42)
    c: Equal(g42, g43-g47) x5
    c: PointOnObject(g42,g48)
    c: PointOnObject(g43,g48)
    c: PointOnObject(g44,g48)
    c: PointOnObject(g45,g48)
    c: PointOnObject(g46,g48)
    c: PointOnObject(g47,g48)
    c: Equal(g41,g48)
    c: Diameter(g41) = 7
    c: Vertical(g39)
    c: Vertical(g43)
    c: Distance(g-2,g39) = 1
    c: Symmetric(g38,g43,g-2)
    c: Distance(g41,g-1) = 7
FEATURE [Part::Extrusion] Extrude609  label="hex211"
  Base = -> Sketch618
  Dir = (0,-1,2e-16)
  DirMode = 2
  FaceMakerClass = Part::FaceMakerBullseye
  FaceMakerMode = 3
  LengthFwd = 10
  LengthRev = 0
  Placement = pos=(88,0,-28) rot=(0,0,1;0rad)
  Solid = true
  Symmetric = false
FEATURE [Sketcher::SketchObject] Sketch619
  ArcFitTolerance = 1e-06
  FullyConstrained = true
  MakeInternals = false
  Placement = pos=(0,0,0) rot=(1,0,0;1.5708rad)
  sketch-geometry (49):
    g0: LineSegment StartX=1e-16 StartY=3.5 StartZ=0 EndX=-3.03109 EndY=1.75 EndZ=0
    g1: LineSegment StartX=-3.03109 StartY=1.75 StartZ=0 EndX=-3.03109 EndY=-1.75 EndZ=0
    g2: LineSegment StartX=-3.03109 StartY=-1.75 StartZ=0 EndX=-1e-16 EndY=-3.5 EndZ=0
    g3: LineSegment StartX=-1e-16 StartY=-3.5 StartZ=0 EndX=3.03109 EndY=-1.75 EndZ=0
    g4: LineSegment StartX=3.03109 StartY=-1.75 StartZ=0 EndX=3.03109 EndY=1.75 EndZ=0
    g5: LineSegment StartX=3.03109 StartY=1.75 StartZ=0 EndX=1e-16 EndY=3.5 EndZ=0
    g6: Circle [constr] CenterX=0 CenterY=0 CenterZ=0 NormalX=0 NormalY=0 NormalZ=1 AngleXU=0 Radius=3.5
    g7: LineSegment StartX=4.96892 StartY=-1.75002 StartZ=0 EndX=8.00002 EndY=-3.5 EndZ=0
    g8: LineSegment StartX=8.00002 StartY=-3.5 StartZ=0 EndX=11.0311 EndY=-1.74998 EndZ=0
    g9: LineSegment StartX=11.0311 StartY=-1.74998 StartZ=0 EndX=11.0311 EndY=1.75002 EndZ=0
    g10: LineSegment StartX=11.0311 StartY=1.75002 StartZ=0 EndX=7.99998 EndY=3.5 EndZ=0
    g11: LineSegment StartX=7.99998 StartY=3.5 StartZ=0 EndX=4.9689 EndY=1.74998 EndZ=0
    g12: LineSegment StartX=4.9689 StartY=1.74998 StartZ=0 EndX=4.96892 EndY=-1.75002 EndZ=0
    g13: Circle [constr] CenterX=8 CenterY=0 CenterZ=0 NormalX=0 NormalY=0 NormalZ=1 AngleXU=0 Radius=3.5
    g14: LineSegment StartX=4.03109 StartY=3.5 StartZ=0 EndX=7.06218 EndY=5.25 EndZ=0
    g15: LineSegment StartX=7.06218 StartY=5.25 StartZ=0 EndX=7.06218 EndY=8.75 EndZ=0
    g16: LineSegment StartX=7.06218 StartY=8.75 StartZ=0 EndX=4.03109 EndY=10.5 EndZ=0
    g17: LineSegment StartX=4.03109 StartY=10.5 StartZ=0 EndX=1 EndY=8.75 EndZ=0
    g18: LineSegment StartX=1 StartY=8.75 StartZ=0 EndX=1 EndY=5.25 EndZ=0
    g19: LineSegment StartX=1 StartY=5.25 StartZ=0 EndX=4.03109 EndY=3.5 EndZ=0
    g20: Circle [constr] CenterX=4.03109 CenterY=7 CenterZ=0 NormalX=0 NormalY=0 NormalZ=1 AngleXU=0 Radius=3.5
    g21: LineSegment StartX=-1 StartY=5.25 StartZ=0 EndX=-1 EndY=8.75 EndZ=0
    g22: LineSegment StartX=-1 StartY=8.75 StartZ=0 EndX=-4.03109 EndY=10.5 EndZ=0
    g23: LineSegment StartX=-4.03109 StartY=10.5 StartZ=0 EndX=-7.06218 EndY=8.75 EndZ=0
    g24: LineSegment StartX=-7.06218 StartY=8.75 StartZ=0 EndX=-7.06218 EndY=5.25 EndZ=0
    g25: LineSegment StartX=-7.06218 StartY=5.25 StartZ=0 EndX=-4.03109 EndY=3.5 EndZ=0
    g26: LineSegment StartX=-4.03109 StartY=3.5 StartZ=0 EndX=-1 EndY=5.25 EndZ=0
    g27: Circle [constr] CenterX=-4.03109 CenterY=7 CenterZ=0 NormalX=0 NormalY=0 NormalZ=1 AngleXU=0 Radius=3.5
    g28: LineSegment StartX=-4.96891 StartY=-1.75 StartZ=0 EndX=-4.96891 EndY=1.75 EndZ=0
    g29: LineSegment StartX=-4.96891 StartY=1.75 StartZ=0 EndX=-8 EndY=3.5 EndZ=0
    g30: LineSegment StartX=-8 StartY=3.5 StartZ=0 EndX=-11.0311 EndY=1.75 EndZ=0
    g31: LineSegment StartX=-11.0311 StartY=1.75 StartZ=0 EndX=-11.0311 EndY=-1.75 EndZ=0
    g32: LineSegment StartX=-11.0311 StartY=-1.75 StartZ=0 EndX=-8 EndY=-3.5 EndZ=0
    g33: LineSegment StartX=-8 StartY=-3.5 StartZ=0 EndX=-4.96891 EndY=-1.75 EndZ=0
    g34: Circle [constr] CenterX=-8 CenterY=0 CenterZ=0 NormalX=0 NormalY=0 NormalZ=1 AngleXU=0 Radius=3.5
    g35: LineSegment StartX=-4.03109 StartY=-3.5 StartZ=0 EndX=-7.06218 EndY=-5.25 EndZ=0
    g36: LineSegment StartX=-7.06218 StartY=-5.25 StartZ=0 EndX=-7.06218 EndY=-8.75 EndZ=0
    g37: LineSegment StartX=-7.06218 StartY=-8.75 StartZ=0 EndX=-4.03109 EndY=-10.5 EndZ=0
    g38: LineSegment StartX=-4.03109 StartY=-10.5 StartZ=0 EndX=-1 EndY=-8.75 EndZ=0
    g39: LineSegment StartX=-1 StartY=-8.75 StartZ=0 EndX=-1 EndY=-5.25 EndZ=0
    g40: LineSegment StartX=-1 StartY=-5.25 StartZ=0 EndX=-4.03109 EndY=-3.5 EndZ=0
    g41: Circle [constr] CenterX=-4.03109 CenterY=-7 CenterZ=0 NormalX=0 NormalY=0 NormalZ=1 AngleXU=0 Radius=3.5
    g42: LineSegment StartX=4.03109 StartY=-3.5 StartZ=0 EndX=1 EndY=-5.25 EndZ=0
    g43: LineSegment StartX=1 StartY=-5.25 StartZ=0 EndX=1 EndY=-8.75 EndZ=0
    g44: LineSegment StartX=1 StartY=-8.75 StartZ=0 EndX=4.03109 EndY=-10.5 EndZ=0
    g45: LineSegment StartX=4.03109 StartY=-10.5 StartZ=0 EndX=7.06218 EndY=-8.75 EndZ=0
    g46: LineSegment StartX=7.06218 StartY=-8.75 StartZ=0 EndX=7.06218 EndY=-5.25 EndZ=0
    g47: LineSegment StartX=7.06218 StartY=-5.25 StartZ=0 EndX=4.03109 EndY=-3.5 EndZ=0
    g48: Circle [constr] CenterX=4.03109 CenterY=-7 CenterZ=0 NormalX=0 NormalY=0 NormalZ=1 AngleXU=0 Radius=3.5
  constraints (117):
    c: Coincident(g0,g1)
    c: Coincident(g1,g2)
    c: Coincident(g2,g3)
    c: Coincident(g3,g4)
    c: Coincident(g4,g5)
    c: Coincident(g5,g0)
    c: Equal(g0, g1-g5) x5
    c: PointOnObject(g0,g6)
    c: PointOnObject(g1,g6)
    c: PointOnObject(g2,g6)
    c: PointOnObject(g3,g6)
    c: PointOnObject(g4,g6)
    c: PointOnObject(g5,g6)
    c: Coincident(g6,g-1)
    c: Diameter(g6) = 7
    c: PointOnObject(g0,g-2)
    c: Coincident(g7,g8)
    c: Coincident(g8,g9)
    c: Coincident(g9,g10)
    c: Coincident(g10,g11)
    c: Coincident(g11,g12)
    c: Coincident(g12,g7)
    c: Equal(g7, g8-g12) x5
    c: PointOnObject(g7,g13)
    c: PointOnObject(g8,g13)
    c: PointOnObject(g9,g13)
    c: PointOnObject(g10,g13)
    c: PointOnObject(g11,g13)
    c: PointOnObject(g12,g13)
    c: PointOnObject(g13,g-1)
    c: Diameter(g13) = 7
    c: Distance(g6,g13) = 8
    c: Horizontal(g0,g10)
    c: Coincident(g14,g15)
    c: Coincident(g15,g16)
    c: Coincident(g16,g17)
    c: Coincident(g17,g18)
    c: Coincident(g18,g19)
    c: Coincident(g19,g14)
    c: Equal(g14, g15-g19) x5
    c: PointOnObject(g14,g20)
    c: PointOnObject(g15,g20)
    c: PointOnObject(g16,g20)
    c: PointOnObject(g17,g20)
    c: PointOnObject(g18,g20)
    c: PointOnObject(g19,g20)
    c: Diameter(g20) = 7
    c: DistanceY(g-1,g20) = 7
    c: Vertical(g18)
    c: Distance(g17,g-2) = 1
    c: Coincident(g21,g22)
    c: Coincident(g22,g23)
    c: Coincident(g23,g24)
    c: Coincident(g24,g25)
    c: Coincident(g25,g26)
    c: Coincident(g26,g21)
    c: Equal(g21, g22-g26) x5
    c: PointOnObject(g21,g27)
    c: PointOnObject(g22,g27)
    c: PointOnObject(g23,g27)
    c: PointOnObject(g24,g27)
    c: PointOnObject(g25,g27)
    c: PointOnObject(g26,g27)
    c: Diameter(g27) = 7
    c: DistanceY(g-1,g27) = 7
    c: DistanceX(g21,g-1) = 1
    c: Vertical(g21)
    c: Coincident(g28,g29)
    c: Coincident(g29,g30)
    c: Coincident(g30,g31)
    c: Coincident(g31,g32)
    c: Coincident(g32,g33)
    c: Coincident(g33,g28)
    c: Equal(g28, g29-g33) x5
    c: PointOnObject(g28,g34)
    c: PointOnObject(g29,g34)
    c: PointOnObject(g30,g34)
    c: PointOnObject(g31,g34)
    c: PointOnObject(g32,g34)
    c: PointOnObject(g33,g34)
    c: PointOnObject(g34,g-1)
    c: Diameter(g34) = 7
    c: Vertical(g31)
    c: DistanceX(g34,g-1) = 8
    c: Coincident(g35,g36)
    c: Coincident(g36,g37)
    c: Coincident(g37,g38)
    c: Coincident(g38,g39)
    c: Coincident(g39,g40)
    c: Coincident(g40,g35)
    c: Equal(g35, g36-g40) x5
    c: PointOnObject(g35,g41)
    c: PointOnObject(g36,g41)
    c: PointOnObject(g37,g41)
    c: PointOnObject(g38,g41)
    c: PointOnObject(g39,g41)
    c: PointOnObject(g40,g41)
    c: Coincident(g42,g43)
    c: Coincident(g43,g44)
    c: Coincident(g44,g45)
    c: Coincident(g45,g46)
    c: Coincident(g46,g47)
    c: Coincident(g47,g42)
    c: Equal(g42, g43-g47) x5
    c: PointOnObject(g42,g48)
    c: PointOnObject(g43,g48)
    c: PointOnObject(g44,g48)
    c: PointOnObject(g45,g48)
    c: PointOnObject(g46,g48)
    c: PointOnObject(g47,g48)
    c: Equal(g41,g48)
    c: Diameter(g41) = 7
    c: Vertical(g39)
    c: Vertical(g43)
    c: Distance(g-2,g39) = 1
    c: Symmetric(g38,g43,g-2)
    c: Distance(g41,g-1) = 7
FEATURE [Part::Extrusion] Extrude610  label="hex212"
  Base = -> Sketch619
  Dir = (0,-1,2e-16)
  DirMode = 2
  FaceMakerClass = Part::FaceMakerBullseye
  FaceMakerMode = 3
  LengthFwd = 10
  LengthRev = 0
  Placement = pos=(104,0,-28) rot=(0,0,1;0rad)
  Solid = true
  Symmetric = false
FEATURE [Sketcher::SketchObject] Sketch620
  ArcFitTolerance = 1e-06
  FullyConstrained = true
  MakeInternals = false
  Placement = pos=(0,0,0) rot=(1,0,0;1.5708rad)
  sketch-geometry (49):
    g0: LineSegment StartX=1e-16 StartY=3.5 StartZ=0 EndX=-3.03109 EndY=1.75 EndZ=0
    g1: LineSegment StartX=-3.03109 StartY=1.75 StartZ=0 EndX=-3.03109 EndY=-1.75 EndZ=0
    g2: LineSegment StartX=-3.03109 StartY=-1.75 StartZ=0 EndX=-1e-16 EndY=-3.5 EndZ=0
    g3: LineSegment StartX=-1e-16 StartY=-3.5 StartZ=0 EndX=3.03109 EndY=-1.75 EndZ=0
    g4: LineSegment StartX=3.03109 StartY=-1.75 StartZ=0 EndX=3.03109 EndY=1.75 EndZ=0
    g5: LineSegment StartX=3.03109 StartY=1.75 StartZ=0 EndX=1e-16 EndY=3.5 EndZ=0
    g6: Circle [constr] CenterX=0 CenterY=0 CenterZ=0 NormalX=0 NormalY=0 NormalZ=1 AngleXU=0 Radius=3.5
    g7: LineSegment StartX=4.96892 StartY=-1.75002 StartZ=0 EndX=8.00002 EndY=-3.5 EndZ=0
    g8: LineSegment StartX=8.00002 StartY=-3.5 StartZ=0 EndX=11.0311 EndY=-1.74998 EndZ=0
    g9: LineSegment StartX=11.0311 StartY=-1.74998 StartZ=0 EndX=11.0311 EndY=1.75002 EndZ=0
    g10: LineSegment StartX=11.0311 StartY=1.75002 StartZ=0 EndX=7.99998 EndY=3.5 EndZ=0
    g11: LineSegment StartX=7.99998 StartY=3.5 StartZ=0 EndX=4.9689 EndY=1.74998 EndZ=0
    g12: LineSegment StartX=4.9689 StartY=1.74998 StartZ=0 EndX=4.96892 EndY=-1.75002 EndZ=0
    g13: Circle [constr] CenterX=8 CenterY=0 CenterZ=0 NormalX=0 NormalY=0 NormalZ=1 AngleXU=0 Radius=3.5
    g14: LineSegment StartX=4.03109 StartY=3.5 StartZ=0 EndX=7.06218 EndY=5.25 EndZ=0
    g15: LineSegment StartX=7.06218 StartY=5.25 StartZ=0 EndX=7.06218 EndY=8.75 EndZ=0
    g16: LineSegment StartX=7.06218 StartY=8.75 StartZ=0 EndX=4.03109 EndY=10.5 EndZ=0
    g17: LineSegment StartX=4.03109 StartY=10.5 StartZ=0 EndX=1 EndY=8.75 EndZ=0
    g18: LineSegment StartX=1 StartY=8.75 StartZ=0 EndX=1 EndY=5.25 EndZ=0
    g19: LineSegment StartX=1 StartY=5.25 StartZ=0 EndX=4.03109 EndY=3.5 EndZ=0
    g20: Circle [constr] CenterX=4.03109 CenterY=7 CenterZ=0 NormalX=0 NormalY=0 NormalZ=1 AngleXU=0 Radius=3.5
    g21: LineSegment StartX=-1 StartY=5.25 StartZ=0 EndX=-1 EndY=8.75 EndZ=0
    g22: LineSegment StartX=-1 StartY=8.75 StartZ=0 EndX=-4.03109 EndY=10.5 EndZ=0
    g23: LineSegment StartX=-4.03109 StartY=10.5 StartZ=0 EndX=-7.06218 EndY=8.75 EndZ=0
    g24: LineSegment StartX=-7.06218 StartY=8.75 StartZ=0 EndX=-7.06218 EndY=5.25 EndZ=0
    g25: LineSegment StartX=-7.06218 StartY=5.25 StartZ=0 EndX=-4.03109 EndY=3.5 EndZ=0
    g26: LineSegment StartX=-4.03109 StartY=3.5 StartZ=0 EndX=-1 EndY=5.25 EndZ=0
    g27: Circle [constr] CenterX=-4.03109 CenterY=7 CenterZ=0 NormalX=0 NormalY=0 NormalZ=1 AngleXU=0 Radius=3.5
    g28: LineSegment StartX=-4.96891 StartY=-1.75 StartZ=0 EndX=-4.96891 EndY=1.75 EndZ=0
    g29: LineSegment StartX=-4.96891 StartY=1.75 StartZ=0 EndX=-8 EndY=3.5 EndZ=0
    g30: LineSegment StartX=-8 StartY=3.5 StartZ=0 EndX=-11.0311 EndY=1.75 EndZ=0
    g31: LineSegment StartX=-11.0311 StartY=1.75 StartZ=0 EndX=-11.0311 EndY=-1.75 EndZ=0
    g32: LineSegment StartX=-11.0311 StartY=-1.75 StartZ=0 EndX=-8 EndY=-3.5 EndZ=0
    g33: LineSegment StartX=-8 StartY=-3.5 StartZ=0 EndX=-4.96891 EndY=-1.75 EndZ=0
    g34: Circle [constr] CenterX=-8 CenterY=0 CenterZ=0 NormalX=0 NormalY=0 NormalZ=1 AngleXU=0 Radius=3.5
    g35: LineSegment StartX=-4.03109 StartY=-3.5 StartZ=0 EndX=-7.06218 EndY=-5.25 EndZ=0
    g36: LineSegment StartX=-7.06218 StartY=-5.25 StartZ=0 EndX=-7.06218 EndY=-8.75 EndZ=0
    g37: LineSegment StartX=-7.06218 StartY=-8.75 StartZ=0 EndX=-4.03109 EndY=-10.5 EndZ=0
    g38: LineSegment StartX=-4.03109 StartY=-10.5 StartZ=0 EndX=-1 EndY=-8.75 EndZ=0
    g39: LineSegment StartX=-1 StartY=-8.75 StartZ=0 EndX=-1 EndY=-5.25 EndZ=0
    g40: LineSegment StartX=-1 StartY=-5.25 StartZ=0 EndX=-4.03109 EndY=-3.5 EndZ=0
    g41: Circle [constr] CenterX=-4.03109 CenterY=-7 CenterZ=0 NormalX=0 NormalY=0 NormalZ=1 AngleXU=0 Radius=3.5
    g42: LineSegment StartX=4.03109 StartY=-3.5 StartZ=0 EndX=1 EndY=-5.25 EndZ=0
    g43: LineSegment StartX=1 StartY=-5.25 StartZ=0 EndX=1 EndY=-8.75 EndZ=0
    g44: LineSegment StartX=1 StartY=-8.75 StartZ=0 EndX=4.03109 EndY=-10.5 EndZ=0
    g45: LineSegment StartX=4.03109 StartY=-10.5 StartZ=0 EndX=7.06218 EndY=-8.75 EndZ=0
    g46: LineSegment StartX=7.06218 StartY=-8.75 StartZ=0 EndX=7.06218 EndY=-5.25 EndZ=0
    g47: LineSegment StartX=7.06218 StartY=-5.25 StartZ=0 EndX=4.03109 EndY=-3.5 EndZ=0
    g48: Circle [constr] CenterX=4.03109 CenterY=-7 CenterZ=0 NormalX=0 NormalY=0 NormalZ=1 AngleXU=0 Radius=3.5
  constraints (117):
    c: Coincident(g0,g1)
    c: Coincident(g1,g2)
    c: Coincident(g2,g3)
    c: Coincident(g3,g4)
    c: Coincident(g4,g5)
    c: Coincident(g5,g0)
    c: Equal(g0, g1-g5) x5
    c: PointOnObject(g0,g6)
    c: PointOnObject(g1,g6)
    c: PointOnObject(g2,g6)
    c: PointOnObject(g3,g6)
    c: PointOnObject(g4,g6)
    c: PointOnObject(g5,g6)
    c: Coincident(g6,g-1)
    c: Diameter(g6) = 7
    c: PointOnObject(g0,g-2)
    c: Coincident(g7,g8)
    c: Coincident(g8,g9)
    c: Coincident(g9,g10)
    c: Coincident(g10,g11)
    c: Coincident(g11,g12)
    c: Coincident(g12,g7)
    c: Equal(g7, g8-g12) x5
    c: PointOnObject(g7,g13)
    c: PointOnObject(g8,g13)
    c: PointOnObject(g9,g13)
    c: PointOnObject(g10,g13)
    c: PointOnObject(g11,g13)
    c: PointOnObject(g12,g13)
    c: PointOnObject(g13,g-1)
    c: Diameter(g13) = 7
    c: Distance(g6,g13) = 8
    c: Horizontal(g0,g10)
    c: Coincident(g14,g15)
    c: Coincident(g15,g16)
    c: Coincident(g16,g17)
    c: Coincident(g17,g18)
    c: Coincident(g18,g19)
    c: Coincident(g19,g14)
    c: Equal(g14, g15-g19) x5
    c: PointOnObject(g14,g20)
    c: PointOnObject(g15,g20)
    c: PointOnObject(g16,g20)
    c: PointOnObject(g17,g20)
    c: PointOnObject(g18,g20)
    c: PointOnObject(g19,g20)
    c: Diameter(g20) = 7
    c: DistanceY(g-1,g20) = 7
    c: Vertical(g18)
    c: Distance(g17,g-2) = 1
    c: Coincident(g21,g22)
    c: Coincident(g22,g23)
    c: Coincident(g23,g24)
    c: Coincident(g24,g25)
    c: Coincident(g25,g26)
    c: Coincident(g26,g21)
    c: Equal(g21, g22-g26) x5
    c: PointOnObject(g21,g27)
    c: PointOnObject(g22,g27)
    c: PointOnObject(g23,g27)
    c: PointOnObject(g24,g27)
    c: PointOnObject(g25,g27)
    c: PointOnObject(g26,g27)
    c: Diameter(g27) = 7
    c: DistanceY(g-1,g27) = 7
    c: DistanceX(g21,g-1) = 1
    c: Vertical(g21)
    c: Coincident(g28,g29)
    c: Coincident(g29,g30)
    c: Coincident(g30,g31)
    c: Coincident(g31,g32)
    c: Coincident(g32,g33)
    c: Coincident(g33,g28)
    c: Equal(g28, g29-g33) x5
    c: PointOnObject(g28,g34)
    c: PointOnObject(g29,g34)
    c: PointOnObject(g30,g34)
    c: PointOnObject(g31,g34)
    c: PointOnObject(g32,g34)
    c: PointOnObject(g33,g34)
    c: PointOnObject(g34,g-1)
    c: Diameter(g34) = 7
    c: Vertical(g31)
    c: DistanceX(g34,g-1) = 8
    c: Coincident(g35,g36)
    c: Coincident(g36,g37)
    c: Coincident(g37,g38)
    c: Coincident(g38,g39)
    c: Coincident(g39,g40)
    c: Coincident(g40,g35)
    c: Equal(g35, g36-g40) x5
    c: PointOnObject(g35,g41)
    c: PointOnObject(g36,g41)
    c: PointOnObject(g37,g41)
    c: PointOnObject(g38,g41)
    c: PointOnObject(g39,g41)
    c: PointOnObject(g40,g41)
    c: Coincident(g42,g43)
    c: Coincident(g43,g44)
    c: Coincident(g44,g45)
    c: Coincident(g45,g46)
    c: Coincident(g46,g47)
    c: Coincident(g47,g42)
    c: Equal(g42, g43-g47) x5
    c: PointOnObject(g42,g48)
    c: PointOnObject(g43,g48)
    c: PointOnObject(g44,g48)
    c: PointOnObject(g45,g48)
    c: PointOnObject(g46,g48)
    c: PointOnObject(g47,g48)
    c: Equal(g41,g48)
    c: Diameter(g41) = 7
    c: Vertical(g39)
    c: Vertical(g43)
    c: Distance(g-2,g39) = 1
    c: Symmetric(g38,g43,g-2)
    c: Distance(g41,g-1) = 7
FEATURE [Part::Extrusion] Extrude611  label="hex213"
  Base = -> Sketch620
  Dir = (0,-1,2e-16)
  DirMode = 2
  FaceMakerClass = Part::FaceMakerBullseye
  FaceMakerMode = 3
  LengthFwd = 10
  LengthRev = 0
  Placement = pos=(-96,0,-14) rot=(0,0,1;0rad)
  Solid = true
  Symmetric = false
FEATURE [Sketcher::SketchObject] Sketch621
  ArcFitTolerance = 1e-06
  FullyConstrained = true
  MakeInternals = false
  Placement = pos=(0,0,0) rot=(1,0,0;1.5708rad)
  sketch-geometry (49):
    g0: LineSegment StartX=1e-16 StartY=3.5 StartZ=0 EndX=-3.03109 EndY=1.75 EndZ=0
    g1: LineSegment StartX=-3.03109 StartY=1.75 StartZ=0 EndX=-3.03109 EndY=-1.75 EndZ=0
    g2: LineSegment StartX=-3.03109 StartY=-1.75 StartZ=0 EndX=-1e-16 EndY=-3.5 EndZ=0
    g3: LineSegment StartX=-1e-16 StartY=-3.5 StartZ=0 EndX=3.03109 EndY=-1.75 EndZ=0
    g4: LineSegment StartX=3.03109 StartY=-1.75 StartZ=0 EndX=3.03109 EndY=1.75 EndZ=0
    g5: LineSegment StartX=3.03109 StartY=1.75 StartZ=0 EndX=1e-16 EndY=3.5 EndZ=0
    g6: Circle [constr] CenterX=0 CenterY=0 CenterZ=0 NormalX=0 NormalY=0 NormalZ=1 AngleXU=0 Radius=3.5
    g7: LineSegment StartX=4.96892 StartY=-1.75002 StartZ=0 EndX=8.00002 EndY=-3.5 EndZ=0
    g8: LineSegment StartX=8.00002 StartY=-3.5 StartZ=0 EndX=11.0311 EndY=-1.74998 EndZ=0
    g9: LineSegment StartX=11.0311 StartY=-1.74998 StartZ=0 EndX=11.0311 EndY=1.75002 EndZ=0
    g10: LineSegment StartX=11.0311 StartY=1.75002 StartZ=0 EndX=7.99998 EndY=3.5 EndZ=0
    g11: LineSegment StartX=7.99998 StartY=3.5 StartZ=0 EndX=4.9689 EndY=1.74998 EndZ=0
    g12: LineSegment StartX=4.9689 StartY=1.74998 StartZ=0 EndX=4.96892 EndY=-1.75002 EndZ=0
    g13: Circle [constr] CenterX=8 CenterY=0 CenterZ=0 NormalX=0 NormalY=0 NormalZ=1 AngleXU=0 Radius=3.5
    g14: LineSegment StartX=4.03109 StartY=3.5 StartZ=0 EndX=7.06218 EndY=5.25 EndZ=0
    g15: LineSegment StartX=7.06218 StartY=5.25 StartZ=0 EndX=7.06218 EndY=8.75 EndZ=0
    g16: LineSegment StartX=7.06218 StartY=8.75 StartZ=0 EndX=4.03109 EndY=10.5 EndZ=0
    g17: LineSegment StartX=4.03109 StartY=10.5 StartZ=0 EndX=1 EndY=8.75 EndZ=0
    g18: LineSegment StartX=1 StartY=8.75 StartZ=0 EndX=1 EndY=5.25 EndZ=0
    g19: LineSegment StartX=1 StartY=5.25 StartZ=0 EndX=4.03109 EndY=3.5 EndZ=0
    g20: Circle [constr] CenterX=4.03109 CenterY=7 CenterZ=0 NormalX=0 NormalY=0 NormalZ=1 AngleXU=0 Radius=3.5
    g21: LineSegment StartX=-1 StartY=5.25 StartZ=0 EndX=-1 EndY=8.75 EndZ=0
    g22: LineSegment StartX=-1 StartY=8.75 StartZ=0 EndX=-4.03109 EndY=10.5 EndZ=0
    g23: LineSegment StartX=-4.03109 StartY=10.5 StartZ=0 EndX=-7.06218 EndY=8.75 EndZ=0
    g24: LineSegment StartX=-7.06218 StartY=8.75 StartZ=0 EndX=-7.06218 EndY=5.25 EndZ=0
    g25: LineSegment StartX=-7.06218 StartY=5.25 StartZ=0 EndX=-4.03109 EndY=3.5 EndZ=0
    g26: LineSegment StartX=-4.03109 StartY=3.5 StartZ=0 EndX=-1 EndY=5.25 EndZ=0
    g27: Circle [constr] CenterX=-4.03109 CenterY=7 CenterZ=0 NormalX=0 NormalY=0 NormalZ=1 AngleXU=0 Radius=3.5
    g28: LineSegment StartX=-4.96891 StartY=-1.75 StartZ=0 EndX=-4.96891 EndY=1.75 EndZ=0
    g29: LineSegment StartX=-4.96891 StartY=1.75 StartZ=0 EndX=-8 EndY=3.5 EndZ=0
    g30: LineSegment StartX=-8 StartY=3.5 StartZ=0 EndX=-11.0311 EndY=1.75 EndZ=0
    g31: LineSegment StartX=-11.0311 StartY=1.75 StartZ=0 EndX=-11.0311 EndY=-1.75 EndZ=0
    g32: LineSegment StartX=-11.0311 StartY=-1.75 StartZ=0 EndX=-8 EndY=-3.5 EndZ=0
    g33: LineSegment StartX=-8 StartY=-3.5 StartZ=0 EndX=-4.96891 EndY=-1.75 EndZ=0
    g34: Circle [constr] CenterX=-8 CenterY=0 CenterZ=0 NormalX=0 NormalY=0 NormalZ=1 AngleXU=0 Radius=3.5
    g35: LineSegment StartX=-4.03109 StartY=-3.5 StartZ=0 EndX=-7.06218 EndY=-5.25 EndZ=0
    g36: LineSegment StartX=-7.06218 StartY=-5.25 StartZ=0 EndX=-7.06218 EndY=-8.75 EndZ=0
    g37: LineSegment StartX=-7.06218 StartY=-8.75 StartZ=0 EndX=-4.03109 EndY=-10.5 EndZ=0
    g38: LineSegment StartX=-4.03109 StartY=-10.5 StartZ=0 EndX=-1 EndY=-8.75 EndZ=0
    g39: LineSegment StartX=-1 StartY=-8.75 StartZ=0 EndX=-1 EndY=-5.25 EndZ=0
    g40: LineSegment StartX=-1 StartY=-5.25 StartZ=0 EndX=-4.03109 EndY=-3.5 EndZ=0
    g41: Circle [constr] CenterX=-4.03109 CenterY=-7 CenterZ=0 NormalX=0 NormalY=0 NormalZ=1 AngleXU=0 Radius=3.5
    g42: LineSegment StartX=4.03109 StartY=-3.5 StartZ=0 EndX=1 EndY=-5.25 EndZ=0
    g43: LineSegment StartX=1 StartY=-5.25 StartZ=0 EndX=1 EndY=-8.75 EndZ=0
    g44: LineSegment StartX=1 StartY=-8.75 StartZ=0 EndX=4.03109 EndY=-10.5 EndZ=0
    g45: LineSegment StartX=4.03109 StartY=-10.5 StartZ=0 EndX=7.06218 EndY=-8.75 EndZ=0
    g46: LineSegment StartX=7.06218 StartY=-8.75 StartZ=0 EndX=7.06218 EndY=-5.25 EndZ=0
    g47: LineSegment StartX=7.06218 StartY=-5.25 StartZ=0 EndX=4.03109 EndY=-3.5 EndZ=0
    g48: Circle [constr] CenterX=4.03109 CenterY=-7 CenterZ=0 NormalX=0 NormalY=0 NormalZ=1 AngleXU=0 Radius=3.5
  constraints (117):
    c: Coincident(g0,g1)
    c: Coincident(g1,g2)
    c: Coincident(g2,g3)
    c: Coincident(g3,g4)
    c: Coincident(g4,g5)
    c: Coincident(g5,g0)
    c: Equal(g0, g1-g5) x5
    c: PointOnObject(g0,g6)
    c: PointOnObject(g1,g6)
    c: PointOnObject(g2,g6)
    c: PointOnObject(g3,g6)
    c: PointOnObject(g4,g6)
    c: PointOnObject(g5,g6)
    c: Coincident(g6,g-1)
    c: Diameter(g6) = 7
    c: PointOnObject(g0,g-2)
    c: Coincident(g7,g8)
    c: Coincident(g8,g9)
    c: Coincident(g9,g10)
    c: Coincident(g10,g11)
    c: Coincident(g11,g12)
    c: Coincident(g12,g7)
    c: Equal(g7, g8-g12) x5
    c: PointOnObject(g7,g13)
    c: PointOnObject(g8,g13)
    c: PointOnObject(g9,g13)
    c: PointOnObject(g10,g13)
    c: PointOnObject(g11,g13)
    c: PointOnObject(g12,g13)
    c: PointOnObject(g13,g-1)
    c: Diameter(g13) = 7
    c: Distance(g6,g13) = 8
    c: Horizontal(g0,g10)
    c: Coincident(g14,g15)
    c: Coincident(g15,g16)
    c: Coincident(g16,g17)
    c: Coincident(g17,g18)
    c: Coincident(g18,g19)
    c: Coincident(g19,g14)
    c: Equal(g14, g15-g19) x5
    c: PointOnObject(g14,g20)
    c: PointOnObject(g15,g20)
    c: PointOnObject(g16,g20)
    c: PointOnObject(g17,g20)
    c: PointOnObject(g18,g20)
    c: PointOnObject(g19,g20)
    c: Diameter(g20) = 7
    c: DistanceY(g-1,g20) = 7
    c: Vertical(g18)
    c: Distance(g17,g-2) = 1
    c: Coincident(g21,g22)
    c: Coincident(g22,g23)
    c: Coincident(g23,g24)
    c: Coincident(g24,g25)
    c: Coincident(g25,g26)
    c: Coincident(g26,g21)
    c: Equal(g21, g22-g26) x5
    c: PointOnObject(g21,g27)
    c: PointOnObject(g22,g27)
    c: PointOnObject(g23,g27)
    c: PointOnObject(g24,g27)
    c: PointOnObject(g25,g27)
    c: PointOnObject(g26,g27)
    c: Diameter(g27) = 7
    c: DistanceY(g-1,g27) = 7
    c: DistanceX(g21,g-1) = 1
    c: Vertical(g21)
    c: Coincident(g28,g29)
    c: Coincident(g29,g30)
    c: Coincident(g30,g31)
    c: Coincident(g31,g32)
    c: Coincident(g32,g33)
    c: Coincident(g33,g28)
    c: Equal(g28, g29-g33) x5
    c: PointOnObject(g28,g34)
    c: PointOnObject(g29,g34)
    c: PointOnObject(g30,g34)
    c: PointOnObject(g31,g34)
    c: PointOnObject(g32,g34)
    c: PointOnObject(g33,g34)
    c: PointOnObject(g34,g-1)
    c: Diameter(g34) = 7
    c: Vertical(g31)
    c: DistanceX(g34,g-1) = 8
    c: Coincident(g35,g36)
    c: Coincident(g36,g37)
    c: Coincident(g37,g38)
    c: Coincident(g38,g39)
    c: Coincident(g39,g40)
    c: Coincident(g40,g35)
    c: Equal(g35, g36-g40) x5
    c: PointOnObject(g35,g41)
    c: PointOnObject(g36,g41)
    c: PointOnObject(g37,g41)
    c: PointOnObject(g38,g41)
    c: PointOnObject(g39,g41)
    c: PointOnObject(g40,g41)
    c: Coincident(g42,g43)
    c: Coincident(g43,g44)
    c: Coincident(g44,g45)
    c: Coincident(g45,g46)
    c: Coincident(g46,g47)
    c: Coincident(g47,g42)
    c: Equal(g42, g43-g47) x5
    c: PointOnObject(g42,g48)
    c: PointOnObject(g43,g48)
    c: PointOnObject(g44,g48)
    c: PointOnObject(g45,g48)
    c: PointOnObject(g46,g48)
    c: PointOnObject(g47,g48)
    c: Equal(g41,g48)
    c: Diameter(g41) = 7
    c: Vertical(g39)
    c: Vertical(g43)
    c: Distance(g-2,g39) = 1
    c: Symmetric(g38,g43,g-2)
    c: Distance(g41,g-1) = 7
FEATURE [Part::Extrusion] Extrude612  label="hex214"
  Base = -> Sketch621
  Dir = (0,-1,2e-16)
  DirMode = 2
  FaceMakerClass = Part::FaceMakerBullseye
  FaceMakerMode = 3
  LengthFwd = 10
  LengthRev = 0
  Placement = pos=(-68,0,-35) rot=(0,0,1;0rad)
  Solid = true
  Symmetric = false
FEATURE [Sketcher::SketchObject] Sketch622
  ArcFitTolerance = 1e-06
  FullyConstrained = true
  MakeInternals = false
  Placement = pos=(0,0,0) rot=(1,0,0;1.5708rad)
  sketch-geometry (49):
    g0: LineSegment StartX=1e-16 StartY=3.5 StartZ=0 EndX=-3.03109 EndY=1.75 EndZ=0
    g1: LineSegment StartX=-3.03109 StartY=1.75 StartZ=0 EndX=-3.03109 EndY=-1.75 EndZ=0
    g2: LineSegment StartX=-3.03109 StartY=-1.75 StartZ=0 EndX=-1e-16 EndY=-3.5 EndZ=0
    g3: LineSegment StartX=-1e-16 StartY=-3.5 StartZ=0 EndX=3.03109 EndY=-1.75 EndZ=0
    g4: LineSegment StartX=3.03109 StartY=-1.75 StartZ=0 EndX=3.03109 EndY=1.75 EndZ=0
    g5: LineSegment StartX=3.03109 StartY=1.75 StartZ=0 EndX=1e-16 EndY=3.5 EndZ=0
    g6: Circle [constr] CenterX=0 CenterY=0 CenterZ=0 NormalX=0 NormalY=0 NormalZ=1 AngleXU=0 Radius=3.5
    g7: LineSegment StartX=4.96892 StartY=-1.75002 StartZ=0 EndX=8.00002 EndY=-3.5 EndZ=0
    g8: LineSegment StartX=8.00002 StartY=-3.5 StartZ=0 EndX=11.0311 EndY=-1.74998 EndZ=0
    g9: LineSegment StartX=11.0311 StartY=-1.74998 StartZ=0 EndX=11.0311 EndY=1.75002 EndZ=0
    g10: LineSegment StartX=11.0311 StartY=1.75002 StartZ=0 EndX=7.99998 EndY=3.5 EndZ=0
    g11: LineSegment StartX=7.99998 StartY=3.5 StartZ=0 EndX=4.9689 EndY=1.74998 EndZ=0
    g12: LineSegment StartX=4.9689 StartY=1.74998 StartZ=0 EndX=4.96892 EndY=-1.75002 EndZ=0
    g13: Circle [constr] CenterX=8 CenterY=0 CenterZ=0 NormalX=0 NormalY=0 NormalZ=1 AngleXU=0 Radius=3.5
    g14: LineSegment StartX=4.03109 StartY=3.5 StartZ=0 EndX=7.06218 EndY=5.25 EndZ=0
    g15: LineSegment StartX=7.06218 StartY=5.25 StartZ=0 EndX=7.06218 EndY=8.75 EndZ=0
    g16: LineSegment StartX=7.06218 StartY=8.75 StartZ=0 EndX=4.03109 EndY=10.5 EndZ=0
    g17: LineSegment StartX=4.03109 StartY=10.5 StartZ=0 EndX=1 EndY=8.75 EndZ=0
    g18: LineSegment StartX=1 StartY=8.75 StartZ=0 EndX=1 EndY=5.25 EndZ=0
    g19: LineSegment StartX=1 StartY=5.25 StartZ=0 EndX=4.03109 EndY=3.5 EndZ=0
    g20: Circle [constr] CenterX=4.03109 CenterY=7 CenterZ=0 NormalX=0 NormalY=0 NormalZ=1 AngleXU=0 Radius=3.5
    g21: LineSegment StartX=-1 StartY=5.25 StartZ=0 EndX=-1 EndY=8.75 EndZ=0
    g22: LineSegment StartX=-1 StartY=8.75 StartZ=0 EndX=-4.03109 EndY=10.5 EndZ=0
    g23: LineSegment StartX=-4.03109 StartY=10.5 StartZ=0 EndX=-7.06218 EndY=8.75 EndZ=0
    g24: LineSegment StartX=-7.06218 StartY=8.75 StartZ=0 EndX=-7.06218 EndY=5.25 EndZ=0
    g25: LineSegment StartX=-7.06218 StartY=5.25 StartZ=0 EndX=-4.03109 EndY=3.5 EndZ=0
    g26: LineSegment StartX=-4.03109 StartY=3.5 StartZ=0 EndX=-1 EndY=5.25 EndZ=0
    g27: Circle [constr] CenterX=-4.03109 CenterY=7 CenterZ=0 NormalX=0 NormalY=0 NormalZ=1 AngleXU=0 Radius=3.5
    g28: LineSegment StartX=-4.96891 StartY=-1.75 StartZ=0 EndX=-4.96891 EndY=1.75 EndZ=0
    g29: LineSegment StartX=-4.96891 StartY=1.75 StartZ=0 EndX=-8 EndY=3.5 EndZ=0
    g30: LineSegment StartX=-8 StartY=3.5 StartZ=0 EndX=-11.0311 EndY=1.75 EndZ=0
    g31: LineSegment StartX=-11.0311 StartY=1.75 StartZ=0 EndX=-11.0311 EndY=-1.75 EndZ=0
    g32: LineSegment StartX=-11.0311 StartY=-1.75 StartZ=0 EndX=-8 EndY=-3.5 EndZ=0
    g33: LineSegment StartX=-8 StartY=-3.5 StartZ=0 EndX=-4.96891 EndY=-1.75 EndZ=0
    g34: Circle [constr] CenterX=-8 CenterY=0 CenterZ=0 NormalX=0 NormalY=0 NormalZ=1 AngleXU=0 Radius=3.5
    g35: LineSegment StartX=-4.03109 StartY=-3.5 StartZ=0 EndX=-7.06218 EndY=-5.25 EndZ=0
    g36: LineSegment StartX=-7.06218 StartY=-5.25 StartZ=0 EndX=-7.06218 EndY=-8.75 EndZ=0
    g37: LineSegment StartX=-7.06218 StartY=-8.75 StartZ=0 EndX=-4.03109 EndY=-10.5 EndZ=0
    g38: LineSegment StartX=-4.03109 StartY=-10.5 StartZ=0 EndX=-1 EndY=-8.75 EndZ=0
    g39: LineSegment StartX=-1 StartY=-8.75 StartZ=0 EndX=-1 EndY=-5.25 EndZ=0
    g40: LineSegment StartX=-1 StartY=-5.25 StartZ=0 EndX=-4.03109 EndY=-3.5 EndZ=0
    g41: Circle [constr] CenterX=-4.03109 CenterY=-7 CenterZ=0 NormalX=0 NormalY=0 NormalZ=1 AngleXU=0 Radius=3.5
    g42: LineSegment StartX=4.03109 StartY=-3.5 StartZ=0 EndX=1 EndY=-5.25 EndZ=0
    g43: LineSegment StartX=1 StartY=-5.25 StartZ=0 EndX=1 EndY=-8.75 EndZ=0
    g44: LineSegment StartX=1 StartY=-8.75 StartZ=0 EndX=4.03109 EndY=-10.5 EndZ=0
    g45: LineSegment StartX=4.03109 StartY=-10.5 StartZ=0 EndX=7.06218 EndY=-8.75 EndZ=0
    g46: LineSegment StartX=7.06218 StartY=-8.75 StartZ=0 EndX=7.06218 EndY=-5.25 EndZ=0
    g47: LineSegment StartX=7.06218 StartY=-5.25 StartZ=0 EndX=4.03109 EndY=-3.5 EndZ=0
    g48: Circle [constr] CenterX=4.03109 CenterY=-7 CenterZ=0 NormalX=0 NormalY=0 NormalZ=1 AngleXU=0 Radius=3.5
  constraints (117):
    c: Coincident(g0,g1)
    c: Coincident(g1,g2)
    c: Coincident(g2,g3)
    c: Coincident(g3,g4)
    c: Coincident(g4,g5)
    c: Coincident(g5,g0)
    c: Equal(g0, g1-g5) x5
    c: PointOnObject(g0,g6)
    c: PointOnObject(g1,g6)
    c: PointOnObject(g2,g6)
    c: PointOnObject(g3,g6)
    c: PointOnObject(g4,g6)
    c: PointOnObject(g5,g6)
    c: Coincident(g6,g-1)
    c: Diameter(g6) = 7
    c: PointOnObject(g0,g-2)
    c: Coincident(g7,g8)
    c: Coincident(g8,g9)
    c: Coincident(g9,g10)
    c: Coincident(g10,g11)
    c: Coincident(g11,g12)
    c: Coincident(g12,g7)
    c: Equal(g7, g8-g12) x5
    c: PointOnObject(g7,g13)
    c: PointOnObject(g8,g13)
    c: PointOnObject(g9,g13)
    c: PointOnObject(g10,g13)
    c: PointOnObject(g11,g13)
    c: PointOnObject(g12,g13)
    c: PointOnObject(g13,g-1)
    c: Diameter(g13) = 7
    c: Distance(g6,g13) = 8
    c: Horizontal(g0,g10)
    c: Coincident(g14,g15)
    c: Coincident(g15,g16)
    c: Coincident(g16,g17)
    c: Coincident(g17,g18)
    c: Coincident(g18,g19)
    c: Coincident(g19,g14)
    c: Equal(g14, g15-g19) x5
    c: PointOnObject(g14,g20)
    c: PointOnObject(g15,g20)
    c: PointOnObject(g16,g20)
    c: PointOnObject(g17,g20)
    c: PointOnObject(g18,g20)
    c: PointOnObject(g19,g20)
    c: Diameter(g20) = 7
    c: DistanceY(g-1,g20) = 7
    c: Vertical(g18)
    c: Distance(g17,g-2) = 1
    c: Coincident(g21,g22)
    c: Coincident(g22,g23)
    c: Coincident(g23,g24)
    c: Coincident(g24,g25)
    c: Coincident(g25,g26)
    c: Coincident(g26,g21)
    c: Equal(g21, g22-g26) x5
    c: PointOnObject(g21,g27)
    c: PointOnObject(g22,g27)
    c: PointOnObject(g23,g27)
    c: PointOnObject(g24,g27)
    c: PointOnObject(g25,g27)
    c: PointOnObject(g26,g27)
    c: Diameter(g27) = 7
    c: DistanceY(g-1,g27) = 7
    c: DistanceX(g21,g-1) = 1
    c: Vertical(g21)
    c: Coincident(g28,g29)
    c: Coincident(g29,g30)
    c: Coincident(g30,g31)
    c: Coincident(g31,g32)
    c: Coincident(g32,g33)
    c: Coincident(g33,g28)
    c: Equal(g28, g29-g33) x5
    c: PointOnObject(g28,g34)
    c: PointOnObject(g29,g34)
    c: PointOnObject(g30,g34)
    c: PointOnObject(g31,g34)
    c: PointOnObject(g32,g34)
    c: PointOnObject(g33,g34)
    c: PointOnObject(g34,g-1)
    c: Diameter(g34) = 7
    c: Vertical(g31)
    c: DistanceX(g34,g-1) = 8
    c: Coincident(g35,g36)
    c: Coincident(g36,g37)
    c: Coincident(g37,g38)
    c: Coincident(g38,g39)
    c: Coincident(g39,g40)
    c: Coincident(g40,g35)
    c: Equal(g35, g36-g40) x5
    c: PointOnObject(g35,g41)
    c: PointOnObject(g36,g41)
    c: PointOnObject(g37,g41)
    c: PointOnObject(g38,g41)
    c: PointOnObject(g39,g41)
    c: PointOnObject(g40,g41)
    c: Coincident(g42,g43)
    c: Coincident(g43,g44)
    c: Coincident(g44,g45)
    c: Coincident(g45,g46)
    c: Coincident(g46,g47)
    c: Coincident(g47,g42)
    c: Equal(g42, g43-g47) x5
    c: PointOnObject(g42,g48)
    c: PointOnObject(g43,g48)
    c: PointOnObject(g44,g48)
    c: PointOnObject(g45,g48)
    c: PointOnObject(g46,g48)
    c: PointOnObject(g47,g48)
    c: Equal(g41,g48)
    c: Diameter(g41) = 7
    c: Vertical(g39)
    c: Vertical(g43)
    c: Distance(g-2,g39) = 1
    c: Symmetric(g38,g43,g-2)
    c: Distance(g41,g-1) = 7
FEATURE [Part::Extrusion] Extrude613  label="hex215"
  Base = -> Sketch622
  Dir = (0,-1,2e-16)
  DirMode = 2
  FaceMakerClass = Part::FaceMakerBullseye
  FaceMakerMode = 3
  LengthFwd = 10
  LengthRev = 0
  Placement = pos=(-84,0,-21) rot=(0,0,1;0rad)
  Solid = true
  Symmetric = false
FEATURE [Sketcher::SketchObject] Sketch623
  ArcFitTolerance = 1e-06
  FullyConstrained = true
  MakeInternals = false
  Placement = pos=(0,0,0) rot=(1,0,0;1.5708rad)
  sketch-geometry (49):
    g0: LineSegment StartX=1e-16 StartY=3.5 StartZ=0 EndX=-3.03109 EndY=1.75 EndZ=0
    g1: LineSegment StartX=-3.03109 StartY=1.75 StartZ=0 EndX=-3.03109 EndY=-1.75 EndZ=0
    g2: LineSegment StartX=-3.03109 StartY=-1.75 StartZ=0 EndX=-1e-16 EndY=-3.5 EndZ=0
    g3: LineSegment StartX=-1e-16 StartY=-3.5 StartZ=0 EndX=3.03109 EndY=-1.75 EndZ=0
    g4: LineSegment StartX=3.03109 StartY=-1.75 StartZ=0 EndX=3.03109 EndY=1.75 EndZ=0
    g5: LineSegment StartX=3.03109 StartY=1.75 StartZ=0 EndX=1e-16 EndY=3.5 EndZ=0
    g6: Circle [constr] CenterX=0 CenterY=0 CenterZ=0 NormalX=0 NormalY=0 NormalZ=1 AngleXU=0 Radius=3.5
    g7: LineSegment StartX=4.96892 StartY=-1.75002 StartZ=0 EndX=8.00002 EndY=-3.5 EndZ=0
    g8: LineSegment StartX=8.00002 StartY=-3.5 StartZ=0 EndX=11.0311 EndY=-1.74998 EndZ=0
    g9: LineSegment StartX=11.0311 StartY=-1.74998 StartZ=0 EndX=11.0311 EndY=1.75002 EndZ=0
    g10: LineSegment StartX=11.0311 StartY=1.75002 StartZ=0 EndX=7.99998 EndY=3.5 EndZ=0
    g11: LineSegment StartX=7.99998 StartY=3.5 StartZ=0 EndX=4.9689 EndY=1.74998 EndZ=0
    g12: LineSegment StartX=4.9689 StartY=1.74998 StartZ=0 EndX=4.96892 EndY=-1.75002 EndZ=0
    g13: Circle [constr] CenterX=8 CenterY=0 CenterZ=0 NormalX=0 NormalY=0 NormalZ=1 AngleXU=0 Radius=3.5
    g14: LineSegment StartX=4.03109 StartY=3.5 StartZ=0 EndX=7.06218 EndY=5.25 EndZ=0
    g15: LineSegment StartX=7.06218 StartY=5.25 StartZ=0 EndX=7.06218 EndY=8.75 EndZ=0
    g16: LineSegment StartX=7.06218 StartY=8.75 StartZ=0 EndX=4.03109 EndY=10.5 EndZ=0
    g17: LineSegment StartX=4.03109 StartY=10.5 StartZ=0 EndX=1 EndY=8.75 EndZ=0
    g18: LineSegment StartX=1 StartY=8.75 StartZ=0 EndX=1 EndY=5.25 EndZ=0
    g19: LineSegment StartX=1 StartY=5.25 StartZ=0 EndX=4.03109 EndY=3.5 EndZ=0
    g20: Circle [constr] CenterX=4.03109 CenterY=7 CenterZ=0 NormalX=0 NormalY=0 NormalZ=1 AngleXU=0 Radius=3.5
    g21: LineSegment StartX=-1 StartY=5.25 StartZ=0 EndX=-1 EndY=8.75 EndZ=0
    g22: LineSegment StartX=-1 StartY=8.75 StartZ=0 EndX=-4.03109 EndY=10.5 EndZ=0
    g23: LineSegment StartX=-4.03109 StartY=10.5 StartZ=0 EndX=-7.06218 EndY=8.75 EndZ=0
    g24: LineSegment StartX=-7.06218 StartY=8.75 StartZ=0 EndX=-7.06218 EndY=5.25 EndZ=0
    g25: LineSegment StartX=-7.06218 StartY=5.25 StartZ=0 EndX=-4.03109 EndY=3.5 EndZ=0
    g26: LineSegment StartX=-4.03109 StartY=3.5 StartZ=0 EndX=-1 EndY=5.25 EndZ=0
    g27: Circle [constr] CenterX=-4.03109 CenterY=7 CenterZ=0 NormalX=0 NormalY=0 NormalZ=1 AngleXU=0 Radius=3.5
    g28: LineSegment StartX=-4.96891 StartY=-1.75 StartZ=0 EndX=-4.96891 EndY=1.75 EndZ=0
    g29: LineSegment StartX=-4.96891 StartY=1.75 StartZ=0 EndX=-8 EndY=3.5 EndZ=0
    g30: LineSegment StartX=-8 StartY=3.5 StartZ=0 EndX=-11.0311 EndY=1.75 EndZ=0
    g31: LineSegment StartX=-11.0311 StartY=1.75 StartZ=0 EndX=-11.0311 EndY=-1.75 EndZ=0
    g32: LineSegment StartX=-11.0311 StartY=-1.75 StartZ=0 EndX=-8 EndY=-3.5 EndZ=0
    g33: LineSegment StartX=-8 StartY=-3.5 StartZ=0 EndX=-4.96891 EndY=-1.75 EndZ=0
    g34: Circle [constr] CenterX=-8 CenterY=0 CenterZ=0 NormalX=0 NormalY=0 NormalZ=1 AngleXU=0 Radius=3.5
    g35: LineSegment StartX=-4.03109 StartY=-3.5 StartZ=0 EndX=-7.06218 EndY=-5.25 EndZ=0
    g36: LineSegment StartX=-7.06218 StartY=-5.25 StartZ=0 EndX=-7.06218 EndY=-8.75 EndZ=0
    g37: LineSegment StartX=-7.06218 StartY=-8.75 StartZ=0 EndX=-4.03109 EndY=-10.5 EndZ=0
    g38: LineSegment StartX=-4.03109 StartY=-10.5 StartZ=0 EndX=-1 EndY=-8.75 EndZ=0
    g39: LineSegment StartX=-1 StartY=-8.75 StartZ=0 EndX=-1 EndY=-5.25 EndZ=0
    g40: LineSegment StartX=-1 StartY=-5.25 StartZ=0 EndX=-4.03109 EndY=-3.5 EndZ=0
    g41: Circle [constr] CenterX=-4.03109 CenterY=-7 CenterZ=0 NormalX=0 NormalY=0 NormalZ=1 AngleXU=0 Radius=3.5
    g42: LineSegment StartX=4.03109 StartY=-3.5 StartZ=0 EndX=1 EndY=-5.25 EndZ=0
    g43: LineSegment StartX=1 StartY=-5.25 StartZ=0 EndX=1 EndY=-8.75 EndZ=0
    g44: LineSegment StartX=1 StartY=-8.75 StartZ=0 EndX=4.03109 EndY=-10.5 EndZ=0
    g45: LineSegment StartX=4.03109 StartY=-10.5 StartZ=0 EndX=7.06218 EndY=-8.75 EndZ=0
    g46: LineSegment StartX=7.06218 StartY=-8.75 StartZ=0 EndX=7.06218 EndY=-5.25 EndZ=0
    g47: LineSegment StartX=7.06218 StartY=-5.25 StartZ=0 EndX=4.03109 EndY=-3.5 EndZ=0
    g48: Circle [constr] CenterX=4.03109 CenterY=-7 CenterZ=0 NormalX=0 NormalY=0 NormalZ=1 AngleXU=0 Radius=3.5
  constraints (117):
    c: Coincident(g0,g1)
    c: Coincident(g1,g2)
    c: Coincident(g2,g3)
    c: Coincident(g3,g4)
    c: Coincident(g4,g5)
    c: Coincident(g5,g0)
    c: Equal(g0, g1-g5) x5
    c: PointOnObject(g0,g6)
    c: PointOnObject(g1,g6)
    c: PointOnObject(g2,g6)
    c: PointOnObject(g3,g6)
    c: PointOnObject(g4,g6)
    c: PointOnObject(g5,g6)
    c: Coincident(g6,g-1)
    c: Diameter(g6) = 7
    c: PointOnObject(g0,g-2)
    c: Coincident(g7,g8)
    c: Coincident(g8,g9)
    c: Coincident(g9,g10)
    c: Coincident(g10,g11)
    c: Coincident(g11,g12)
    c: Coincident(g12,g7)
    c: Equal(g7, g8-g12) x5
    c: PointOnObject(g7,g13)
    c: PointOnObject(g8,g13)
    c: PointOnObject(g9,g13)
    c: PointOnObject(g10,g13)
    c: PointOnObject(g11,g13)
    c: PointOnObject(g12,g13)
    c: PointOnObject(g13,g-1)
    c: Diameter(g13) = 7
    c: Distance(g6,g13) = 8
    c: Horizontal(g0,g10)
    c: Coincident(g14,g15)
    c: Coincident(g15,g16)
    c: Coincident(g16,g17)
    c: Coincident(g17,g18)
    c: Coincident(g18,g19)
    c: Coincident(g19,g14)
    c: Equal(g14, g15-g19) x5
    c: PointOnObject(g14,g20)
    c: PointOnObject(g15,g20)
    c: PointOnObject(g16,g20)
    c: PointOnObject(g17,g20)
    c: PointOnObject(g18,g20)
    c: PointOnObject(g19,g20)
    c: Diameter(g20) = 7
    c: DistanceY(g-1,g20) = 7
    c: Vertical(g18)
    c: Distance(g17,g-2) = 1
    c: Coincident(g21,g22)
    c: Coincident(g22,g23)
    c: Coincident(g23,g24)
    c: Coincident(g24,g25)
    c: Coincident(g25,g26)
    c: Coincident(g26,g21)
    c: Equal(g21, g22-g26) x5
    c: PointOnObject(g21,g27)
    c: PointOnObject(g22,g27)
    c: PointOnObject(g23,g27)
    c: PointOnObject(g24,g27)
    c: PointOnObject(g25,g27)
    c: PointOnObject(g26,g27)
    c: Diameter(g27) = 7
    c: DistanceY(g-1,g27) = 7
    c: DistanceX(g21,g-1) = 1
    c: Vertical(g21)
    c: Coincident(g28,g29)
    c: Coincident(g29,g30)
    c: Coincident(g30,g31)
    c: Coincident(g31,g32)
    c: Coincident(g32,g33)
    c: Coincident(g33,g28)
    c: Equal(g28, g29-g33) x5
    c: PointOnObject(g28,g34)
    c: PointOnObject(g29,g34)
    c: PointOnObject(g30,g34)
    c: PointOnObject(g31,g34)
    c: PointOnObject(g32,g34)
    c: PointOnObject(g33,g34)
    c: PointOnObject(g34,g-1)
    c: Diameter(g34) = 7
    c: Vertical(g31)
    c: DistanceX(g34,g-1) = 8
    c: Coincident(g35,g36)
    c: Coincident(g36,g37)
    c: Coincident(g37,g38)
    c: Coincident(g38,g39)
    c: Coincident(g39,g40)
    c: Coincident(g40,g35)
    c: Equal(g35, g36-g40) x5
    c: PointOnObject(g35,g41)
    c: PointOnObject(g36,g41)
    c: PointOnObject(g37,g41)
    c: PointOnObject(g38,g41)
    c: PointOnObject(g39,g41)
    c: PointOnObject(g40,g41)
    c: Coincident(g42,g43)
    c: Coincident(g43,g44)
    c: Coincident(g44,g45)
    c: Coincident(g45,g46)
    c: Coincident(g46,g47)
    c: Coincident(g47,g42)
    c: Equal(g42, g43-g47) x5
    c: PointOnObject(g42,g48)
    c: PointOnObject(g43,g48)
    c: PointOnObject(g44,g48)
    c: PointOnObject(g45,g48)
    c: PointOnObject(g46,g48)
    c: PointOnObject(g47,g48)
    c: Equal(g41,g48)
    c: Diameter(g41) = 7
    c: Vertical(g39)
    c: Vertical(g43)
    c: Distance(g-2,g39) = 1
    c: Symmetric(g38,g43,g-2)
    c: Distance(g41,g-1) = 7
FEATURE [Part::Extrusion] Extrude614  label="hex216"
  Base = -> Sketch623
  Dir = (0,-1,2e-16)
  DirMode = 2
  FaceMakerClass = Part::FaceMakerBullseye
  FaceMakerMode = 3
  LengthFwd = 10
  LengthRev = 0
  Placement = pos=(-88,0,14) rot=(0,0,1;0rad)
  Solid = true
  Symmetric = false
FEATURE [Sketcher::SketchObject] Sketch624
  ArcFitTolerance = 1e-06
  FullyConstrained = true
  MakeInternals = false
  Placement = pos=(0,0,0) rot=(1,0,0;1.5708rad)
  sketch-geometry (49):
    g0: LineSegment StartX=1e-16 StartY=3.5 StartZ=0 EndX=-3.03109 EndY=1.75 EndZ=0
    g1: LineSegment StartX=-3.03109 StartY=1.75 StartZ=0 EndX=-3.03109 EndY=-1.75 EndZ=0
    g2: LineSegment StartX=-3.03109 StartY=-1.75 StartZ=0 EndX=-1e-16 EndY=-3.5 EndZ=0
    g3: LineSegment StartX=-1e-16 StartY=-3.5 StartZ=0 EndX=3.03109 EndY=-1.75 EndZ=0
    g4: LineSegment StartX=3.03109 StartY=-1.75 StartZ=0 EndX=3.03109 EndY=1.75 EndZ=0
    g5: LineSegment StartX=3.03109 StartY=1.75 StartZ=0 EndX=1e-16 EndY=3.5 EndZ=0
    g6: Circle [constr] CenterX=0 CenterY=0 CenterZ=0 NormalX=0 NormalY=0 NormalZ=1 AngleXU=0 Radius=3.5
    g7: LineSegment StartX=4.96892 StartY=-1.75002 StartZ=0 EndX=8.00002 EndY=-3.5 EndZ=0
    g8: LineSegment StartX=8.00002 StartY=-3.5 StartZ=0 EndX=11.0311 EndY=-1.74998 EndZ=0
    g9: LineSegment StartX=11.0311 StartY=-1.74998 StartZ=0 EndX=11.0311 EndY=1.75002 EndZ=0
    g10: LineSegment StartX=11.0311 StartY=1.75002 StartZ=0 EndX=7.99998 EndY=3.5 EndZ=0
    g11: LineSegment StartX=7.99998 StartY=3.5 StartZ=0 EndX=4.9689 EndY=1.74998 EndZ=0
    g12: LineSegment StartX=4.9689 StartY=1.74998 StartZ=0 EndX=4.96892 EndY=-1.75002 EndZ=0
    g13: Circle [constr] CenterX=8 CenterY=0 CenterZ=0 NormalX=0 NormalY=0 NormalZ=1 AngleXU=0 Radius=3.5
    g14: LineSegment StartX=4.03109 StartY=3.5 StartZ=0 EndX=7.06218 EndY=5.25 EndZ=0
    g15: LineSegment StartX=7.06218 StartY=5.25 StartZ=0 EndX=7.06218 EndY=8.75 EndZ=0
    g16: LineSegment StartX=7.06218 StartY=8.75 StartZ=0 EndX=4.03109 EndY=10.5 EndZ=0
    g17: LineSegment StartX=4.03109 StartY=10.5 StartZ=0 EndX=1 EndY=8.75 EndZ=0
    g18: LineSegment StartX=1 StartY=8.75 StartZ=0 EndX=1 EndY=5.25 EndZ=0
    g19: LineSegment StartX=1 StartY=5.25 StartZ=0 EndX=4.03109 EndY=3.5 EndZ=0
    g20: Circle [constr] CenterX=4.03109 CenterY=7 CenterZ=0 NormalX=0 NormalY=0 NormalZ=1 AngleXU=0 Radius=3.5
    g21: LineSegment StartX=-1 StartY=5.25 StartZ=0 EndX=-1 EndY=8.75 EndZ=0
    g22: LineSegment StartX=-1 StartY=8.75 StartZ=0 EndX=-4.03109 EndY=10.5 EndZ=0
    g23: LineSegment StartX=-4.03109 StartY=10.5 StartZ=0 EndX=-7.06218 EndY=8.75 EndZ=0
    g24: LineSegment StartX=-7.06218 StartY=8.75 StartZ=0 EndX=-7.06218 EndY=5.25 EndZ=0
    g25: LineSegment StartX=-7.06218 StartY=5.25 StartZ=0 EndX=-4.03109 EndY=3.5 EndZ=0
    g26: LineSegment StartX=-4.03109 StartY=3.5 StartZ=0 EndX=-1 EndY=5.25 EndZ=0
    g27: Circle [constr] CenterX=-4.03109 CenterY=7 CenterZ=0 NormalX=0 NormalY=0 NormalZ=1 AngleXU=0 Radius=3.5
    g28: LineSegment StartX=-4.96891 StartY=-1.75 StartZ=0 EndX=-4.96891 EndY=1.75 EndZ=0
    g29: LineSegment StartX=-4.96891 StartY=1.75 StartZ=0 EndX=-8 EndY=3.5 EndZ=0
    g30: LineSegment StartX=-8 StartY=3.5 StartZ=0 EndX=-11.0311 EndY=1.75 EndZ=0
    g31: LineSegment StartX=-11.0311 StartY=1.75 StartZ=0 EndX=-11.0311 EndY=-1.75 EndZ=0
    g32: LineSegment StartX=-11.0311 StartY=-1.75 StartZ=0 EndX=-8 EndY=-3.5 EndZ=0
    g33: LineSegment StartX=-8 StartY=-3.5 StartZ=0 EndX=-4.96891 EndY=-1.75 EndZ=0
    g34: Circle [constr] CenterX=-8 CenterY=0 CenterZ=0 NormalX=0 NormalY=0 NormalZ=1 AngleXU=0 Radius=3.5
    g35: LineSegment StartX=-4.03109 StartY=-3.5 StartZ=0 EndX=-7.06218 EndY=-5.25 EndZ=0
    g36: LineSegment StartX=-7.06218 StartY=-5.25 StartZ=0 EndX=-7.06218 EndY=-8.75 EndZ=0
    g37: LineSegment StartX=-7.06218 StartY=-8.75 StartZ=0 EndX=-4.03109 EndY=-10.5 EndZ=0
    g38: LineSegment StartX=-4.03109 StartY=-10.5 StartZ=0 EndX=-1 EndY=-8.75 EndZ=0
    g39: LineSegment StartX=-1 StartY=-8.75 StartZ=0 EndX=-1 EndY=-5.25 EndZ=0
    g40: LineSegment StartX=-1 StartY=-5.25 StartZ=0 EndX=-4.03109 EndY=-3.5 EndZ=0
    g41: Circle [constr] CenterX=-4.03109 CenterY=-7 CenterZ=0 NormalX=0 NormalY=0 NormalZ=1 AngleXU=0 Radius=3.5
    g42: LineSegment StartX=4.03109 StartY=-3.5 StartZ=0 EndX=1 EndY=-5.25 EndZ=0
    g43: LineSegment StartX=1 StartY=-5.25 StartZ=0 EndX=1 EndY=-8.75 EndZ=0
    g44: LineSegment StartX=1 StartY=-8.75 StartZ=0 EndX=4.03109 EndY=-10.5 EndZ=0
    g45: LineSegment StartX=4.03109 StartY=-10.5 StartZ=0 EndX=7.06218 EndY=-8.75 EndZ=0
    g46: LineSegment StartX=7.06218 StartY=-8.75 StartZ=0 EndX=7.06218 EndY=-5.25 EndZ=0
    g47: LineSegment StartX=7.06218 StartY=-5.25 StartZ=0 EndX=4.03109 EndY=-3.5 EndZ=0
    g48: Circle [constr] CenterX=4.03109 CenterY=-7 CenterZ=0 NormalX=0 NormalY=0 NormalZ=1 AngleXU=0 Radius=3.5
  constraints (117):
    c: Coincident(g0,g1)
    c: Coincident(g1,g2)
    c: Coincident(g2,g3)
    c: Coincident(g3,g4)
    c: Coincident(g4,g5)
    c: Coincident(g5,g0)
    c: Equal(g0, g1-g5) x5
    c: PointOnObject(g0,g6)
    c: PointOnObject(g1,g6)
    c: PointOnObject(g2,g6)
    c: PointOnObject(g3,g6)
    c: PointOnObject(g4,g6)
    c: PointOnObject(g5,g6)
    c: Coincident(g6,g-1)
    c: Diameter(g6) = 7
    c: PointOnObject(g0,g-2)
    c: Coincident(g7,g8)
    c: Coincident(g8,g9)
    c: Coincident(g9,g10)
    c: Coincident(g10,g11)
    c: Coincident(g11,g12)
    c: Coincident(g12,g7)
    c: Equal(g7, g8-g12) x5
    c: PointOnObject(g7,g13)
    c: PointOnObject(g8,g13)
    c: PointOnObject(g9,g13)
    c: PointOnObject(g10,g13)
    c: PointOnObject(g11,g13)
    c: PointOnObject(g12,g13)
    c: PointOnObject(g13,g-1)
    c: Diameter(g13) = 7
    c: Distance(g6,g13) = 8
    c: Horizontal(g0,g10)
    c: Coincident(g14,g15)
    c: Coincident(g15,g16)
    c: Coincident(g16,g17)
    c: Coincident(g17,g18)
    c: Coincident(g18,g19)
    c: Coincident(g19,g14)
    c: Equal(g14, g15-g19) x5
    c: PointOnObject(g14,g20)
    c: PointOnObject(g15,g20)
    c: PointOnObject(g16,g20)
    c: PointOnObject(g17,g20)
    c: PointOnObject(g18,g20)
    c: PointOnObject(g19,g20)
    c: Diameter(g20) = 7
    c: DistanceY(g-1,g20) = 7
    c: Vertical(g18)
    c: Distance(g17,g-2) = 1
    c: Coincident(g21,g22)
    c: Coincident(g22,g23)
    c: Coincident(g23,g24)
    c: Coincident(g24,g25)
    c: Coincident(g25,g26)
    c: Coincident(g26,g21)
    c: Equal(g21, g22-g26) x5
    c: PointOnObject(g21,g27)
    c: PointOnObject(g22,g27)
    c: PointOnObject(g23,g27)
    c: PointOnObject(g24,g27)
    c: PointOnObject(g25,g27)
    c: PointOnObject(g26,g27)
    c: Diameter(g27) = 7
    c: DistanceY(g-1,g27) = 7
    c: DistanceX(g21,g-1) = 1
    c: Vertical(g21)
    c: Coincident(g28,g29)
    c: Coincident(g29,g30)
    c: Coincident(g30,g31)
    c: Coincident(g31,g32)
    c: Coincident(g32,g33)
    c: Coincident(g33,g28)
    c: Equal(g28, g29-g33) x5
    c: PointOnObject(g28,g34)
    c: PointOnObject(g29,g34)
    c: PointOnObject(g30,g34)
    c: PointOnObject(g31,g34)
    c: PointOnObject(g32,g34)
    c: PointOnObject(g33,g34)
    c: PointOnObject(g34,g-1)
    c: Diameter(g34) = 7
    c: Vertical(g31)
    c: DistanceX(g34,g-1) = 8
    c: Coincident(g35,g36)
    c: Coincident(g36,g37)
    c: Coincident(g37,g38)
    c: Coincident(g38,g39)
    c: Coincident(g39,g40)
    c: Coincident(g40,g35)
    c: Equal(g35, g36-g40) x5
    c: PointOnObject(g35,g41)
    c: PointOnObject(g36,g41)
    c: PointOnObject(g37,g41)
    c: PointOnObject(g38,g41)
    c: PointOnObject(g39,g41)
    c: PointOnObject(g40,g41)
    c: Coincident(g42,g43)
    c: Coincident(g43,g44)
    c: Coincident(g44,g45)
    c: Coincident(g45,g46)
    c: Coincident(g46,g47)
    c: Coincident(g47,g42)
    c: Equal(g42, g43-g47) x5
    c: PointOnObject(g42,g48)
    c: PointOnObject(g43,g48)
    c: PointOnObject(g44,g48)
    c: PointOnObject(g45,g48)
    c: PointOnObject(g46,g48)
    c: PointOnObject(g47,g48)
    c: Equal(g41,g48)
    c: Diameter(g41) = 7
    c: Vertical(g39)
    c: Vertical(g43)
    c: Distance(g-2,g39) = 1
    c: Symmetric(g38,g43,g-2)
    c: Distance(g41,g-1) = 7
FEATURE [Part::Extrusion] Extrude615  label="hex217"
  Base = -> Sketch624
  Dir = (0,-1,2e-16)
  DirMode = 2
  FaceMakerClass = Part::FaceMakerBullseye
  FaceMakerMode = 3
  LengthFwd = 10
  LengthRev = 0
  Placement = pos=(96,0,14) rot=(0,0,1;0rad)
  Solid = true
  Symmetric = false
FEATURE [Part::MultiFuse] Fusion563
  Refine = true
  Shapes = -> [Extrude566,Extrude567,Extrude568,Extrude569,Extrude570,Extrude571,Extrude572,Extrude573,Extrude574,Extrude575,Extrude576,Extrude577,Extrude578,Extrude579,Extrude580,Extrude581,Extrude582,Extrude583,Extrude584,Extrude585,Extrude586,Extrude587,Extrude588,Extrude589,Extrude590,Extrude591,Extrude592,Extrude593,Extrude594,Extrude595,Extrude596,Extrude597,Extrude598,Extrude599,Extrude600,Extrude601,+14 more]
FEATURE [Sketcher::SketchObject] Sketch625
  ArcFitTolerance = 1e-06
  FullyConstrained = true
  MakeInternals = false
  Placement = pos=(0,0,0) rot=(1,0,0;1.5708rad)
  sketch-geometry (49):
    g0: LineSegment StartX=1e-16 StartY=3.5 StartZ=0 EndX=-3.03109 EndY=1.75 EndZ=0
    g1: LineSegment StartX=-3.03109 StartY=1.75 StartZ=0 EndX=-3.03109 EndY=-1.75 EndZ=0
    g2: LineSegment StartX=-3.03109 StartY=-1.75 StartZ=0 EndX=-1e-16 EndY=-3.5 EndZ=0
    g3: LineSegment StartX=-1e-16 StartY=-3.5 StartZ=0 EndX=3.03109 EndY=-1.75 EndZ=0
    g4: LineSegment StartX=3.03109 StartY=-1.75 StartZ=0 EndX=3.03109 EndY=1.75 EndZ=0
    g5: LineSegment StartX=3.03109 StartY=1.75 StartZ=0 EndX=1e-16 EndY=3.5 EndZ=0
    g6: Circle [constr] CenterX=0 CenterY=0 CenterZ=0 NormalX=0 NormalY=0 NormalZ=1 AngleXU=0 Radius=3.5
    g7: LineSegment StartX=4.96892 StartY=-1.75002 StartZ=0 EndX=8.00002 EndY=-3.5 EndZ=0
    g8: LineSegment StartX=8.00002 StartY=-3.5 StartZ=0 EndX=11.0311 EndY=-1.74998 EndZ=0
    g9: LineSegment StartX=11.0311 StartY=-1.74998 StartZ=0 EndX=11.0311 EndY=1.75002 EndZ=0
    g10: LineSegment StartX=11.0311 StartY=1.75002 StartZ=0 EndX=7.99998 EndY=3.5 EndZ=0
    g11: LineSegment StartX=7.99998 StartY=3.5 StartZ=0 EndX=4.9689 EndY=1.74998 EndZ=0
    g12: LineSegment StartX=4.9689 StartY=1.74998 StartZ=0 EndX=4.96892 EndY=-1.75002 EndZ=0
    g13: Circle [constr] CenterX=8 CenterY=0 CenterZ=0 NormalX=0 NormalY=0 NormalZ=1 AngleXU=0 Radius=3.5
    g14: LineSegment StartX=4.03109 StartY=3.5 StartZ=0 EndX=7.06218 EndY=5.25 EndZ=0
    g15: LineSegment StartX=7.06218 StartY=5.25 StartZ=0 EndX=7.06218 EndY=8.75 EndZ=0
    g16: LineSegment StartX=7.06218 StartY=8.75 StartZ=0 EndX=4.03109 EndY=10.5 EndZ=0
    g17: LineSegment StartX=4.03109 StartY=10.5 StartZ=0 EndX=1 EndY=8.75 EndZ=0
    g18: LineSegment StartX=1 StartY=8.75 StartZ=0 EndX=1 EndY=5.25 EndZ=0
    g19: LineSegment StartX=1 StartY=5.25 StartZ=0 EndX=4.03109 EndY=3.5 EndZ=0
    g20: Circle [constr] CenterX=4.03109 CenterY=7 CenterZ=0 NormalX=0 NormalY=0 NormalZ=1 AngleXU=0 Radius=3.5
    g21: LineSegment StartX=-1 StartY=5.25 StartZ=0 EndX=-1 EndY=8.75 EndZ=0
    g22: LineSegment StartX=-1 StartY=8.75 StartZ=0 EndX=-4.03109 EndY=10.5 EndZ=0
    g23: LineSegment StartX=-4.03109 StartY=10.5 StartZ=0 EndX=-7.06218 EndY=8.75 EndZ=0
    g24: LineSegment StartX=-7.06218 StartY=8.75 StartZ=0 EndX=-7.06218 EndY=5.25 EndZ=0
    g25: LineSegment StartX=-7.06218 StartY=5.25 StartZ=0 EndX=-4.03109 EndY=3.5 EndZ=0
    g26: LineSegment StartX=-4.03109 StartY=3.5 StartZ=0 EndX=-1 EndY=5.25 EndZ=0
    g27: Circle [constr] CenterX=-4.03109 CenterY=7 CenterZ=0 NormalX=0 NormalY=0 NormalZ=1 AngleXU=0 Radius=3.5
    g28: LineSegment StartX=-4.96891 StartY=-1.75 StartZ=0 EndX=-4.96891 EndY=1.75 EndZ=0
    g29: LineSegment StartX=-4.96891 StartY=1.75 StartZ=0 EndX=-8 EndY=3.5 EndZ=0
    g30: LineSegment StartX=-8 StartY=3.5 StartZ=0 EndX=-11.0311 EndY=1.75 EndZ=0
    g31: LineSegment StartX=-11.0311 StartY=1.75 StartZ=0 EndX=-11.0311 EndY=-1.75 EndZ=0
    g32: LineSegment StartX=-11.0311 StartY=-1.75 StartZ=0 EndX=-8 EndY=-3.5 EndZ=0
    g33: LineSegment StartX=-8 StartY=-3.5 StartZ=0 EndX=-4.96891 EndY=-1.75 EndZ=0
    g34: Circle [constr] CenterX=-8 CenterY=0 CenterZ=0 NormalX=0 NormalY=0 NormalZ=1 AngleXU=0 Radius=3.5
    g35: LineSegment StartX=-4.03109 StartY=-3.5 StartZ=0 EndX=-7.06218 EndY=-5.25 EndZ=0
    g36: LineSegment StartX=-7.06218 StartY=-5.25 StartZ=0 EndX=-7.06218 EndY=-8.75 EndZ=0
    g37: LineSegment StartX=-7.06218 StartY=-8.75 StartZ=0 EndX=-4.03109 EndY=-10.5 EndZ=0
    g38: LineSegment StartX=-4.03109 StartY=-10.5 StartZ=0 EndX=-1 EndY=-8.75 EndZ=0
    g39: LineSegment StartX=-1 StartY=-8.75 StartZ=0 EndX=-1 EndY=-5.25 EndZ=0
    g40: LineSegment StartX=-1 StartY=-5.25 StartZ=0 EndX=-4.03109 EndY=-3.5 EndZ=0
    g41: Circle [constr] CenterX=-4.03109 CenterY=-7 CenterZ=0 NormalX=0 NormalY=0 NormalZ=1 AngleXU=0 Radius=3.5
    g42: LineSegment StartX=4.03109 StartY=-3.5 StartZ=0 EndX=1 EndY=-5.25 EndZ=0
    g43: LineSegment StartX=1 StartY=-5.25 StartZ=0 EndX=1 EndY=-8.75 EndZ=0
    g44: LineSegment StartX=1 StartY=-8.75 StartZ=0 EndX=4.03109 EndY=-10.5 EndZ=0
    g45: LineSegment StartX=4.03109 StartY=-10.5 StartZ=0 EndX=7.06218 EndY=-8.75 EndZ=0
    g46: LineSegment StartX=7.06218 StartY=-8.75 StartZ=0 EndX=7.06218 EndY=-5.25 EndZ=0
    g47: LineSegment StartX=7.06218 StartY=-5.25 StartZ=0 EndX=4.03109 EndY=-3.5 EndZ=0
    g48: Circle [constr] CenterX=4.03109 CenterY=-7 CenterZ=0 NormalX=0 NormalY=0 NormalZ=1 AngleXU=0 Radius=3.5
  constraints (117):
    c: Coincident(g0,g1)
    c: Coincident(g1,g2)
    c: Coincident(g2,g3)
    c: Coincident(g3,g4)
    c: Coincident(g4,g5)
    c: Coincident(g5,g0)
    c: Equal(g0, g1-g5) x5
    c: PointOnObject(g0,g6)
    c: PointOnObject(g1,g6)
    c: PointOnObject(g2,g6)
    c: PointOnObject(g3,g6)
    c: PointOnObject(g4,g6)
    c: PointOnObject(g5,g6)
    c: Coincident(g6,g-1)
    c: Diameter(g6) = 7
    c: PointOnObject(g0,g-2)
    c: Coincident(g7,g8)
    c: Coincident(g8,g9)
    c: Coincident(g9,g10)
    c: Coincident(g10,g11)
    c: Coincident(g11,g12)
    c: Coincident(g12,g7)
    c: Equal(g7, g8-g12) x5
    c: PointOnObject(g7,g13)
    c: PointOnObject(g8,g13)
    c: PointOnObject(g9,g13)
    c: PointOnObject(g10,g13)
    c: PointOnObject(g11,g13)
    c: PointOnObject(g12,g13)
    c: PointOnObject(g13,g-1)
    c: Diameter(g13) = 7
    c: Distance(g6,g13) = 8
    c: Horizontal(g0,g10)
    c: Coincident(g14,g15)
    c: Coincident(g15,g16)
    c: Coincident(g16,g17)
    c: Coincident(g17,g18)
    c: Coincident(g18,g19)
    c: Coincident(g19,g14)
    c: Equal(g14, g15-g19) x5
    c: PointOnObject(g14,g20)
    c: PointOnObject(g15,g20)
    c: PointOnObject(g16,g20)
    c: PointOnObject(g17,g20)
    c: PointOnObject(g18,g20)
    c: PointOnObject(g19,g20)
    c: Diameter(g20) = 7
    c: DistanceY(g-1,g20) = 7
    c: Vertical(g18)
    c: Distance(g17,g-2) = 1
    c: Coincident(g21,g22)
    c: Coincident(g22,g23)
    c: Coincident(g23,g24)
    c: Coincident(g24,g25)
    c: Coincident(g25,g26)
    c: Coincident(g26,g21)
    c: Equal(g21, g22-g26) x5
    c: PointOnObject(g21,g27)
    c: PointOnObject(g22,g27)
    c: PointOnObject(g23,g27)
    c: PointOnObject(g24,g27)
    c: PointOnObject(g25,g27)
    c: PointOnObject(g26,g27)
    c: Diameter(g27) = 7
    c: DistanceY(g-1,g27) = 7
    c: DistanceX(g21,g-1) = 1
    c: Vertical(g21)
    c: Coincident(g28,g29)
    c: Coincident(g29,g30)
    c: Coincident(g30,g31)
    c: Coincident(g31,g32)
    c: Coincident(g32,g33)
    c: Coincident(g33,g28)
    c: Equal(g28, g29-g33) x5
    c: PointOnObject(g28,g34)
    c: PointOnObject(g29,g34)
    c: PointOnObject(g30,g34)
    c: PointOnObject(g31,g34)
    c: PointOnObject(g32,g34)
    c: PointOnObject(g33,g34)
    c: PointOnObject(g34,g-1)
    c: Diameter(g34) = 7
    c: Vertical(g31)
    c: DistanceX(g34,g-1) = 8
    c: Coincident(g35,g36)
    c: Coincident(g36,g37)
    c: Coincident(g37,g38)
    c: Coincident(g38,g39)
    c: Coincident(g39,g40)
    c: Coincident(g40,g35)
    c: Equal(g35, g36-g40) x5
    c: PointOnObject(g35,g41)
    c: PointOnObject(g36,g41)
    c: PointOnObject(g37,g41)
    c: PointOnObject(g38,g41)
    c: PointOnObject(g39,g41)
    c: PointOnObject(g40,g41)
    c: Coincident(g42,g43)
    c: Coincident(g43,g44)
    c: Coincident(g44,g45)
    c: Coincident(g45,g46)
    c: Coincident(g46,g47)
    c: Coincident(g47,g42)
    c: Equal(g42, g43-g47) x5
    c: PointOnObject(g42,g48)
    c: PointOnObject(g43,g48)
    c: PointOnObject(g44,g48)
    c: PointOnObject(g45,g48)
    c: PointOnObject(g46,g48)
    c: PointOnObject(g47,g48)
    c: Equal(g41,g48)
    c: Diameter(g41) = 7
    c: Vertical(g39)
    c: Vertical(g43)
    c: Distance(g-2,g39) = 1
    c: Symmetric(g38,g43,g-2)
    c: Distance(g41,g-1) = 7
FEATURE [Part::Extrusion] Extrude616  label="hex218"
  Base = -> Sketch625
  Dir = (0,-1,2e-16)
  DirMode = 2
  FaceMakerClass = Part::FaceMakerBullseye
  FaceMakerMode = 3
  LengthFwd = 10
  LengthRev = 0
  Solid = true
  Symmetric = false
FEATURE [Sketcher::SketchObject] Sketch626
  ArcFitTolerance = 1e-06
  FullyConstrained = true
  MakeInternals = false
  Placement = pos=(0,0,0) rot=(1,0,0;1.5708rad)
  sketch-geometry (49):
    g0: LineSegment StartX=1e-16 StartY=3.5 StartZ=0 EndX=-3.03109 EndY=1.75 EndZ=0
    g1: LineSegment StartX=-3.03109 StartY=1.75 StartZ=0 EndX=-3.03109 EndY=-1.75 EndZ=0
    g2: LineSegment StartX=-3.03109 StartY=-1.75 StartZ=0 EndX=-1e-16 EndY=-3.5 EndZ=0
    g3: LineSegment StartX=-1e-16 StartY=-3.5 StartZ=0 EndX=3.03109 EndY=-1.75 EndZ=0
    g4: LineSegment StartX=3.03109 StartY=-1.75 StartZ=0 EndX=3.03109 EndY=1.75 EndZ=0
    g5: LineSegment StartX=3.03109 StartY=1.75 StartZ=0 EndX=1e-16 EndY=3.5 EndZ=0
    g6: Circle [constr] CenterX=0 CenterY=0 CenterZ=0 NormalX=0 NormalY=0 NormalZ=1 AngleXU=0 Radius=3.5
    g7: LineSegment StartX=4.96892 StartY=-1.75002 StartZ=0 EndX=8.00002 EndY=-3.5 EndZ=0
    g8: LineSegment StartX=8.00002 StartY=-3.5 StartZ=0 EndX=11.0311 EndY=-1.74998 EndZ=0
    g9: LineSegment StartX=11.0311 StartY=-1.74998 StartZ=0 EndX=11.0311 EndY=1.75002 EndZ=0
    g10: LineSegment StartX=11.0311 StartY=1.75002 StartZ=0 EndX=7.99998 EndY=3.5 EndZ=0
    g11: LineSegment StartX=7.99998 StartY=3.5 StartZ=0 EndX=4.9689 EndY=1.74998 EndZ=0
    g12: LineSegment StartX=4.9689 StartY=1.74998 StartZ=0 EndX=4.96892 EndY=-1.75002 EndZ=0
    g13: Circle [constr] CenterX=8 CenterY=0 CenterZ=0 NormalX=0 NormalY=0 NormalZ=1 AngleXU=0 Radius=3.5
    g14: LineSegment StartX=4.03109 StartY=3.5 StartZ=0 EndX=7.06218 EndY=5.25 EndZ=0
    g15: LineSegment StartX=7.06218 StartY=5.25 StartZ=0 EndX=7.06218 EndY=8.75 EndZ=0
    g16: LineSegment StartX=7.06218 StartY=8.75 StartZ=0 EndX=4.03109 EndY=10.5 EndZ=0
    g17: LineSegment StartX=4.03109 StartY=10.5 StartZ=0 EndX=1 EndY=8.75 EndZ=0
    g18: LineSegment StartX=1 StartY=8.75 StartZ=0 EndX=1 EndY=5.25 EndZ=0
    g19: LineSegment StartX=1 StartY=5.25 StartZ=0 EndX=4.03109 EndY=3.5 EndZ=0
    g20: Circle [constr] CenterX=4.03109 CenterY=7 CenterZ=0 NormalX=0 NormalY=0 NormalZ=1 AngleXU=0 Radius=3.5
    g21: LineSegment StartX=-1 StartY=5.25 StartZ=0 EndX=-1 EndY=8.75 EndZ=0
    g22: LineSegment StartX=-1 StartY=8.75 StartZ=0 EndX=-4.03109 EndY=10.5 EndZ=0
    g23: LineSegment StartX=-4.03109 StartY=10.5 StartZ=0 EndX=-7.06218 EndY=8.75 EndZ=0
    g24: LineSegment StartX=-7.06218 StartY=8.75 StartZ=0 EndX=-7.06218 EndY=5.25 EndZ=0
    g25: LineSegment StartX=-7.06218 StartY=5.25 StartZ=0 EndX=-4.03109 EndY=3.5 EndZ=0
    g26: LineSegment StartX=-4.03109 StartY=3.5 StartZ=0 EndX=-1 EndY=5.25 EndZ=0
    g27: Circle [constr] CenterX=-4.03109 CenterY=7 CenterZ=0 NormalX=0 NormalY=0 NormalZ=1 AngleXU=0 Radius=3.5
    g28: LineSegment StartX=-4.96891 StartY=-1.75 StartZ=0 EndX=-4.96891 EndY=1.75 EndZ=0
    g29: LineSegment StartX=-4.96891 StartY=1.75 StartZ=0 EndX=-8 EndY=3.5 EndZ=0
    g30: LineSegment StartX=-8 StartY=3.5 StartZ=0 EndX=-11.0311 EndY=1.75 EndZ=0
    g31: LineSegment StartX=-11.0311 StartY=1.75 StartZ=0 EndX=-11.0311 EndY=-1.75 EndZ=0
    g32: LineSegment StartX=-11.0311 StartY=-1.75 StartZ=0 EndX=-8 EndY=-3.5 EndZ=0
    g33: LineSegment StartX=-8 StartY=-3.5 StartZ=0 EndX=-4.96891 EndY=-1.75 EndZ=0
    g34: Circle [constr] CenterX=-8 CenterY=0 CenterZ=0 NormalX=0 NormalY=0 NormalZ=1 AngleXU=0 Radius=3.5
    g35: LineSegment StartX=-4.03109 StartY=-3.5 StartZ=0 EndX=-7.06218 EndY=-5.25 EndZ=0
    g36: LineSegment StartX=-7.06218 StartY=-5.25 StartZ=0 EndX=-7.06218 EndY=-8.75 EndZ=0
    g37: LineSegment StartX=-7.06218 StartY=-8.75 StartZ=0 EndX=-4.03109 EndY=-10.5 EndZ=0
    g38: LineSegment StartX=-4.03109 StartY=-10.5 StartZ=0 EndX=-1 EndY=-8.75 EndZ=0
    g39: LineSegment StartX=-1 StartY=-8.75 StartZ=0 EndX=-1 EndY=-5.25 EndZ=0
    g40: LineSegment StartX=-1 StartY=-5.25 StartZ=0 EndX=-4.03109 EndY=-3.5 EndZ=0
    g41: Circle [constr] CenterX=-4.03109 CenterY=-7 CenterZ=0 NormalX=0 NormalY=0 NormalZ=1 AngleXU=0 Radius=3.5
    g42: LineSegment StartX=4.03109 StartY=-3.5 StartZ=0 EndX=1 EndY=-5.25 EndZ=0
    g43: LineSegment StartX=1 StartY=-5.25 StartZ=0 EndX=1 EndY=-8.75 EndZ=0
    g44: LineSegment StartX=1 StartY=-8.75 StartZ=0 EndX=4.03109 EndY=-10.5 EndZ=0
    g45: LineSegment StartX=4.03109 StartY=-10.5 StartZ=0 EndX=7.06218 EndY=-8.75 EndZ=0
    g46: LineSegment StartX=7.06218 StartY=-8.75 StartZ=0 EndX=7.06218 EndY=-5.25 EndZ=0
    g47: LineSegment StartX=7.06218 StartY=-5.25 StartZ=0 EndX=4.03109 EndY=-3.5 EndZ=0
    g48: Circle [constr] CenterX=4.03109 CenterY=-7 CenterZ=0 NormalX=0 NormalY=0 NormalZ=1 AngleXU=0 Radius=3.5
  constraints (117):
    c: Coincident(g0,g1)
    c: Coincident(g1,g2)
    c: Coincident(g2,g3)
    c: Coincident(g3,g4)
    c: Coincident(g4,g5)
    c: Coincident(g5,g0)
    c: Equal(g0, g1-g5) x5
    c: PointOnObject(g0,g6)
    c: PointOnObject(g1,g6)
    c: PointOnObject(g2,g6)
    c: PointOnObject(g3,g6)
    c: PointOnObject(g4,g6)
    c: PointOnObject(g5,g6)
    c: Coincident(g6,g-1)
    c: Diameter(g6) = 7
    c: PointOnObject(g0,g-2)
    c: Coincident(g7,g8)
    c: Coincident(g8,g9)
    c: Coincident(g9,g10)
    c: Coincident(g10,g11)
    c: Coincident(g11,g12)
    c: Coincident(g12,g7)
    c: Equal(g7, g8-g12) x5
    c: PointOnObject(g7,g13)
    c: PointOnObject(g8,g13)
    c: PointOnObject(g9,g13)
    c: PointOnObject(g10,g13)
    c: PointOnObject(g11,g13)
    c: PointOnObject(g12,g13)
    c: PointOnObject(g13,g-1)
    c: Diameter(g13) = 7
    c: Distance(g6,g13) = 8
    c: Horizontal(g0,g10)
    c: Coincident(g14,g15)
    c: Coincident(g15,g16)
    c: Coincident(g16,g17)
    c: Coincident(g17,g18)
    c: Coincident(g18,g19)
    c: Coincident(g19,g14)
    c: Equal(g14, g15-g19) x5
    c: PointOnObject(g14,g20)
    c: PointOnObject(g15,g20)
    c: PointOnObject(g16,g20)
    c: PointOnObject(g17,g20)
    c: PointOnObject(g18,g20)
    c: PointOnObject(g19,g20)
    c: Diameter(g20) = 7
    c: DistanceY(g-1,g20) = 7
    c: Vertical(g18)
    c: Distance(g17,g-2) = 1
    c: Coincident(g21,g22)
    c: Coincident(g22,g23)
    c: Coincident(g23,g24)
    c: Coincident(g24,g25)
    c: Coincident(g25,g26)
    c: Coincident(g26,g21)
    c: Equal(g21, g22-g26) x5
    c: PointOnObject(g21,g27)
    c: PointOnObject(g22,g27)
    c: PointOnObject(g23,g27)
    c: PointOnObject(g24,g27)
    c: PointOnObject(g25,g27)
    c: PointOnObject(g26,g27)
    c: Diameter(g27) = 7
    c: DistanceY(g-1,g27) = 7
    c: DistanceX(g21,g-1) = 1
    c: Vertical(g21)
    c: Coincident(g28,g29)
    c: Coincident(g29,g30)
    c: Coincident(g30,g31)
    c: Coincident(g31,g32)
    c: Coincident(g32,g33)
    c: Coincident(g33,g28)
    c: Equal(g28, g29-g33) x5
    c: PointOnObject(g28,g34)
    c: PointOnObject(g29,g34)
    c: PointOnObject(g30,g34)
    c: PointOnObject(g31,g34)
    c: PointOnObject(g32,g34)
    c: PointOnObject(g33,g34)
    c: PointOnObject(g34,g-1)
    c: Diameter(g34) = 7
    c: Vertical(g31)
    c: DistanceX(g34,g-1) = 8
    c: Coincident(g35,g36)
    c: Coincident(g36,g37)
    c: Coincident(g37,g38)
    c: Coincident(g38,g39)
    c: Coincident(g39,g40)
    c: Coincident(g40,g35)
    c: Equal(g35, g36-g40) x5
    c: PointOnObject(g35,g41)
    c: PointOnObject(g36,g41)
    c: PointOnObject(g37,g41)
    c: PointOnObject(g38,g41)
    c: PointOnObject(g39,g41)
    c: PointOnObject(g40,g41)
    c: Coincident(g42,g43)
    c: Coincident(g43,g44)
    c: Coincident(g44,g45)
    c: Coincident(g45,g46)
    c: Coincident(g46,g47)
    c: Coincident(g47,g42)
    c: Equal(g42, g43-g47) x5
    c: PointOnObject(g42,g48)
    c: PointOnObject(g43,g48)
    c: PointOnObject(g44,g48)
    c: PointOnObject(g45,g48)
    c: PointOnObject(g46,g48)
    c: PointOnObject(g47,g48)
    c: Equal(g41,g48)
    c: Diameter(g41) = 7
    c: Vertical(g39)
    c: Vertical(g43)
    c: Distance(g-2,g39) = 1
    c: Symmetric(g38,g43,g-2)
    c: Distance(g41,g-1) = 7
FEATURE [Part::Extrusion] Extrude617  label="hex219"
  Base = -> Sketch626
  Dir = (0,-1,2e-16)
  DirMode = 2
  FaceMakerClass = Part::FaceMakerBullseye
  FaceMakerMode = 3
  LengthFwd = 10
  LengthRev = 0
  Placement = pos=(20,0,-7) rot=(0,0,1;0rad)
  Solid = true
  Symmetric = false
FEATURE [Sketcher::SketchObject] Sketch627
  ArcFitTolerance = 1e-06
  FullyConstrained = true
  MakeInternals = false
  Placement = pos=(0,0,0) rot=(1,0,0;1.5708rad)
  sketch-geometry (49):
    g0: LineSegment StartX=1e-16 StartY=3.5 StartZ=0 EndX=-3.03109 EndY=1.75 EndZ=0
    g1: LineSegment StartX=-3.03109 StartY=1.75 StartZ=0 EndX=-3.03109 EndY=-1.75 EndZ=0
    g2: LineSegment StartX=-3.03109 StartY=-1.75 StartZ=0 EndX=-1e-16 EndY=-3.5 EndZ=0
    g3: LineSegment StartX=-1e-16 StartY=-3.5 StartZ=0 EndX=3.03109 EndY=-1.75 EndZ=0
    g4: LineSegment StartX=3.03109 StartY=-1.75 StartZ=0 EndX=3.03109 EndY=1.75 EndZ=0
    g5: LineSegment StartX=3.03109 StartY=1.75 StartZ=0 EndX=1e-16 EndY=3.5 EndZ=0
    g6: Circle [constr] CenterX=0 CenterY=0 CenterZ=0 NormalX=0 NormalY=0 NormalZ=1 AngleXU=0 Radius=3.5
    g7: LineSegment StartX=4.96892 StartY=-1.75002 StartZ=0 EndX=8.00002 EndY=-3.5 EndZ=0
    g8: LineSegment StartX=8.00002 StartY=-3.5 StartZ=0 EndX=11.0311 EndY=-1.74998 EndZ=0
    g9: LineSegment StartX=11.0311 StartY=-1.74998 StartZ=0 EndX=11.0311 EndY=1.75002 EndZ=0
    g10: LineSegment StartX=11.0311 StartY=1.75002 StartZ=0 EndX=7.99998 EndY=3.5 EndZ=0
    g11: LineSegment StartX=7.99998 StartY=3.5 StartZ=0 EndX=4.9689 EndY=1.74998 EndZ=0
    g12: LineSegment StartX=4.9689 StartY=1.74998 StartZ=0 EndX=4.96892 EndY=-1.75002 EndZ=0
    g13: Circle [constr] CenterX=8 CenterY=0 CenterZ=0 NormalX=0 NormalY=0 NormalZ=1 AngleXU=0 Radius=3.5
    g14: LineSegment StartX=4.03109 StartY=3.5 StartZ=0 EndX=7.06218 EndY=5.25 EndZ=0
    g15: LineSegment StartX=7.06218 StartY=5.25 StartZ=0 EndX=7.06218 EndY=8.75 EndZ=0
    g16: LineSegment StartX=7.06218 StartY=8.75 StartZ=0 EndX=4.03109 EndY=10.5 EndZ=0
    g17: LineSegment StartX=4.03109 StartY=10.5 StartZ=0 EndX=1 EndY=8.75 EndZ=0
    g18: LineSegment StartX=1 StartY=8.75 StartZ=0 EndX=1 EndY=5.25 EndZ=0
    g19: LineSegment StartX=1 StartY=5.25 StartZ=0 EndX=4.03109 EndY=3.5 EndZ=0
    g20: Circle [constr] CenterX=4.03109 CenterY=7 CenterZ=0 NormalX=0 NormalY=0 NormalZ=1 AngleXU=0 Radius=3.5
    g21: LineSegment StartX=-1 StartY=5.25 StartZ=0 EndX=-1 EndY=8.75 EndZ=0
    g22: LineSegment StartX=-1 StartY=8.75 StartZ=0 EndX=-4.03109 EndY=10.5 EndZ=0
    g23: LineSegment StartX=-4.03109 StartY=10.5 StartZ=0 EndX=-7.06218 EndY=8.75 EndZ=0
    g24: LineSegment StartX=-7.06218 StartY=8.75 StartZ=0 EndX=-7.06218 EndY=5.25 EndZ=0
    g25: LineSegment StartX=-7.06218 StartY=5.25 StartZ=0 EndX=-4.03109 EndY=3.5 EndZ=0
    g26: LineSegment StartX=-4.03109 StartY=3.5 StartZ=0 EndX=-1 EndY=5.25 EndZ=0
    g27: Circle [constr] CenterX=-4.03109 CenterY=7 CenterZ=0 NormalX=0 NormalY=0 NormalZ=1 AngleXU=0 Radius=3.5
    g28: LineSegment StartX=-4.96891 StartY=-1.75 StartZ=0 EndX=-4.96891 EndY=1.75 EndZ=0
    g29: LineSegment StartX=-4.96891 StartY=1.75 StartZ=0 EndX=-8 EndY=3.5 EndZ=0
    g30: LineSegment StartX=-8 StartY=3.5 StartZ=0 EndX=-11.0311 EndY=1.75 EndZ=0
    g31: LineSegment StartX=-11.0311 StartY=1.75 StartZ=0 EndX=-11.0311 EndY=-1.75 EndZ=0
    g32: LineSegment StartX=-11.0311 StartY=-1.75 StartZ=0 EndX=-8 EndY=-3.5 EndZ=0
    g33: LineSegment StartX=-8 StartY=-3.5 StartZ=0 EndX=-4.96891 EndY=-1.75 EndZ=0
    g34: Circle [constr] CenterX=-8 CenterY=0 CenterZ=0 NormalX=0 NormalY=0 NormalZ=1 AngleXU=0 Radius=3.5
    g35: LineSegment StartX=-4.03109 StartY=-3.5 StartZ=0 EndX=-7.06218 EndY=-5.25 EndZ=0
    g36: LineSegment StartX=-7.06218 StartY=-5.25 StartZ=0 EndX=-7.06218 EndY=-8.75 EndZ=0
    g37: LineSegment StartX=-7.06218 StartY=-8.75 StartZ=0 EndX=-4.03109 EndY=-10.5 EndZ=0
    g38: LineSegment StartX=-4.03109 StartY=-10.5 StartZ=0 EndX=-1 EndY=-8.75 EndZ=0
    g39: LineSegment StartX=-1 StartY=-8.75 StartZ=0 EndX=-1 EndY=-5.25 EndZ=0
    g40: LineSegment StartX=-1 StartY=-5.25 StartZ=0 EndX=-4.03109 EndY=-3.5 EndZ=0
    g41: Circle [constr] CenterX=-4.03109 CenterY=-7 CenterZ=0 NormalX=0 NormalY=0 NormalZ=1 AngleXU=0 Radius=3.5
    g42: LineSegment StartX=4.03109 StartY=-3.5 StartZ=0 EndX=1 EndY=-5.25 EndZ=0
    g43: LineSegment StartX=1 StartY=-5.25 StartZ=0 EndX=1 EndY=-8.75 EndZ=0
    g44: LineSegment StartX=1 StartY=-8.75 StartZ=0 EndX=4.03109 EndY=-10.5 EndZ=0
    g45: LineSegment StartX=4.03109 StartY=-10.5 StartZ=0 EndX=7.06218 EndY=-8.75 EndZ=0
    g46: LineSegment StartX=7.06218 StartY=-8.75 StartZ=0 EndX=7.06218 EndY=-5.25 EndZ=0
    g47: LineSegment StartX=7.06218 StartY=-5.25 StartZ=0 EndX=4.03109 EndY=-3.5 EndZ=0
    g48: Circle [constr] CenterX=4.03109 CenterY=-7 CenterZ=0 NormalX=0 NormalY=0 NormalZ=1 AngleXU=0 Radius=3.5
  constraints (117):
    c: Coincident(g0,g1)
    c: Coincident(g1,g2)
    c: Coincident(g2,g3)
    c: Coincident(g3,g4)
    c: Coincident(g4,g5)
    c: Coincident(g5,g0)
    c: Equal(g0, g1-g5) x5
    c: PointOnObject(g0,g6)
    c: PointOnObject(g1,g6)
    c: PointOnObject(g2,g6)
    c: PointOnObject(g3,g6)
    c: PointOnObject(g4,g6)
    c: PointOnObject(g5,g6)
    c: Coincident(g6,g-1)
    c: Diameter(g6) = 7
    c: PointOnObject(g0,g-2)
    c: Coincident(g7,g8)
    c: Coincident(g8,g9)
    c: Coincident(g9,g10)
    c: Coincident(g10,g11)
    c: Coincident(g11,g12)
    c: Coincident(g12,g7)
    c: Equal(g7, g8-g12) x5
    c: PointOnObject(g7,g13)
    c: PointOnObject(g8,g13)
    c: PointOnObject(g9,g13)
    c: PointOnObject(g10,g13)
    c: PointOnObject(g11,g13)
    c: PointOnObject(g12,g13)
    c: PointOnObject(g13,g-1)
    c: Diameter(g13) = 7
    c: Distance(g6,g13) = 8
    c: Horizontal(g0,g10)
    c: Coincident(g14,g15)
    c: Coincident(g15,g16)
    c: Coincident(g16,g17)
    c: Coincident(g17,g18)
    c: Coincident(g18,g19)
    c: Coincident(g19,g14)
    c: Equal(g14, g15-g19) x5
    c: PointOnObject(g14,g20)
    c: PointOnObject(g15,g20)
    c: PointOnObject(g16,g20)
    c: PointOnObject(g17,g20)
    c: PointOnObject(g18,g20)
    c: PointOnObject(g19,g20)
    c: Diameter(g20) = 7
    c: DistanceY(g-1,g20) = 7
    c: Vertical(g18)
    c: Distance(g17,g-2) = 1
    c: Coincident(g21,g22)
    c: Coincident(g22,g23)
    c: Coincident(g23,g24)
    c: Coincident(g24,g25)
    c: Coincident(g25,g26)
    c: Coincident(g26,g21)
    c: Equal(g21, g22-g26) x5
    c: PointOnObject(g21,g27)
    c: PointOnObject(g22,g27)
    c: PointOnObject(g23,g27)
    c: PointOnObject(g24,g27)
    c: PointOnObject(g25,g27)
    c: PointOnObject(g26,g27)
    c: Diameter(g27) = 7
    c: DistanceY(g-1,g27) = 7
    c: DistanceX(g21,g-1) = 1
    c: Vertical(g21)
    c: Coincident(g28,g29)
    c: Coincident(g29,g30)
    c: Coincident(g30,g31)
    c: Coincident(g31,g32)
    c: Coincident(g32,g33)
    c: Coincident(g33,g28)
    c: Equal(g28, g29-g33) x5
    c: PointOnObject(g28,g34)
    c: PointOnObject(g29,g34)
    c: PointOnObject(g30,g34)
    c: PointOnObject(g31,g34)
    c: PointOnObject(g32,g34)
    c: PointOnObject(g33,g34)
    c: PointOnObject(g34,g-1)
    c: Diameter(g34) = 7
    c: Vertical(g31)
    c: DistanceX(g34,g-1) = 8
    c: Coincident(g35,g36)
    c: Coincident(g36,g37)
    c: Coincident(g37,g38)
    c: Coincident(g38,g39)
    c: Coincident(g39,g40)
    c: Coincident(g40,g35)
    c: Equal(g35, g36-g40) x5
    c: PointOnObject(g35,g41)
    c: PointOnObject(g36,g41)
    c: PointOnObject(g37,g41)
    c: PointOnObject(g38,g41)
    c: PointOnObject(g39,g41)
    c: PointOnObject(g40,g41)
    c: Coincident(g42,g43)
    c: Coincident(g43,g44)
    c: Coincident(g44,g45)
    c: Coincident(g45,g46)
    c: Coincident(g46,g47)
    c: Coincident(g47,g42)
    c: Equal(g42, g43-g47) x5
    c: PointOnObject(g42,g48)
    c: PointOnObject(g43,g48)
    c: PointOnObject(g44,g48)
    c: PointOnObject(g45,g48)
    c: PointOnObject(g46,g48)
    c: PointOnObject(g47,g48)
    c: Equal(g41,g48)
    c: Diameter(g41) = 7
    c: Vertical(g39)
    c: Vertical(g43)
    c: Distance(g-2,g39) = 1
    c: Symmetric(g38,g43,g-2)
    c: Distance(g41,g-1) = 7
FEATURE [Part::Extrusion] Extrude618  label="hex220"
  Base = -> Sketch627
  Dir = (0,-1,2e-16)
  DirMode = 2
  FaceMakerClass = Part::FaceMakerBullseye
  FaceMakerMode = 3
  LengthFwd = 10
  LengthRev = 0
  Placement = pos=(16,0,14) rot=(0,0,1;0rad)
  Solid = true
  Symmetric = false
FEATURE [Sketcher::SketchObject] Sketch628
  ArcFitTolerance = 1e-06
  FullyConstrained = true
  MakeInternals = false
  Placement = pos=(0,0,0) rot=(1,0,0;1.5708rad)
  sketch-geometry (49):
    g0: LineSegment StartX=1e-16 StartY=3.5 StartZ=0 EndX=-3.03109 EndY=1.75 EndZ=0
    g1: LineSegment StartX=-3.03109 StartY=1.75 StartZ=0 EndX=-3.03109 EndY=-1.75 EndZ=0
    g2: LineSegment StartX=-3.03109 StartY=-1.75 StartZ=0 EndX=-1e-16 EndY=-3.5 EndZ=0
    g3: LineSegment StartX=-1e-16 StartY=-3.5 StartZ=0 EndX=3.03109 EndY=-1.75 EndZ=0
    g4: LineSegment StartX=3.03109 StartY=-1.75 StartZ=0 EndX=3.03109 EndY=1.75 EndZ=0
    g5: LineSegment StartX=3.03109 StartY=1.75 StartZ=0 EndX=1e-16 EndY=3.5 EndZ=0
    g6: Circle [constr] CenterX=0 CenterY=0 CenterZ=0 NormalX=0 NormalY=0 NormalZ=1 AngleXU=0 Radius=3.5
    g7: LineSegment StartX=4.96892 StartY=-1.75002 StartZ=0 EndX=8.00002 EndY=-3.5 EndZ=0
    g8: LineSegment StartX=8.00002 StartY=-3.5 StartZ=0 EndX=11.0311 EndY=-1.74998 EndZ=0
    g9: LineSegment StartX=11.0311 StartY=-1.74998 StartZ=0 EndX=11.0311 EndY=1.75002 EndZ=0
    g10: LineSegment StartX=11.0311 StartY=1.75002 StartZ=0 EndX=7.99998 EndY=3.5 EndZ=0
    g11: LineSegment StartX=7.99998 StartY=3.5 StartZ=0 EndX=4.9689 EndY=1.74998 EndZ=0
    g12: LineSegment StartX=4.9689 StartY=1.74998 StartZ=0 EndX=4.96892 EndY=-1.75002 EndZ=0
    g13: Circle [constr] CenterX=8 CenterY=0 CenterZ=0 NormalX=0 NormalY=0 NormalZ=1 AngleXU=0 Radius=3.5
    g14: LineSegment StartX=4.03109 StartY=3.5 StartZ=0 EndX=7.06218 EndY=5.25 EndZ=0
    g15: LineSegment StartX=7.06218 StartY=5.25 StartZ=0 EndX=7.06218 EndY=8.75 EndZ=0
    g16: LineSegment StartX=7.06218 StartY=8.75 StartZ=0 EndX=4.03109 EndY=10.5 EndZ=0
    g17: LineSegment StartX=4.03109 StartY=10.5 StartZ=0 EndX=1 EndY=8.75 EndZ=0
    g18: LineSegment StartX=1 StartY=8.75 StartZ=0 EndX=1 EndY=5.25 EndZ=0
    g19: LineSegment StartX=1 StartY=5.25 StartZ=0 EndX=4.03109 EndY=3.5 EndZ=0
    g20: Circle [constr] CenterX=4.03109 CenterY=7 CenterZ=0 NormalX=0 NormalY=0 NormalZ=1 AngleXU=0 Radius=3.5
    g21: LineSegment StartX=-1 StartY=5.25 StartZ=0 EndX=-1 EndY=8.75 EndZ=0
    g22: LineSegment StartX=-1 StartY=8.75 StartZ=0 EndX=-4.03109 EndY=10.5 EndZ=0
    g23: LineSegment StartX=-4.03109 StartY=10.5 StartZ=0 EndX=-7.06218 EndY=8.75 EndZ=0
    g24: LineSegment StartX=-7.06218 StartY=8.75 StartZ=0 EndX=-7.06218 EndY=5.25 EndZ=0
    g25: LineSegment StartX=-7.06218 StartY=5.25 StartZ=0 EndX=-4.03109 EndY=3.5 EndZ=0
    g26: LineSegment StartX=-4.03109 StartY=3.5 StartZ=0 EndX=-1 EndY=5.25 EndZ=0
    g27: Circle [constr] CenterX=-4.03109 CenterY=7 CenterZ=0 NormalX=0 NormalY=0 NormalZ=1 AngleXU=0 Radius=3.5
    g28: LineSegment StartX=-4.96891 StartY=-1.75 StartZ=0 EndX=-4.96891 EndY=1.75 EndZ=0
    g29: LineSegment StartX=-4.96891 StartY=1.75 StartZ=0 EndX=-8 EndY=3.5 EndZ=0
    g30: LineSegment StartX=-8 StartY=3.5 StartZ=0 EndX=-11.0311 EndY=1.75 EndZ=0
    g31: LineSegment StartX=-11.0311 StartY=1.75 StartZ=0 EndX=-11.0311 EndY=-1.75 EndZ=0
    g32: LineSegment StartX=-11.0311 StartY=-1.75 StartZ=0 EndX=-8 EndY=-3.5 EndZ=0
    g33: LineSegment StartX=-8 StartY=-3.5 StartZ=0 EndX=-4.96891 EndY=-1.75 EndZ=0
    g34: Circle [constr] CenterX=-8 CenterY=0 CenterZ=0 NormalX=0 NormalY=0 NormalZ=1 AngleXU=0 Radius=3.5
    g35: LineSegment StartX=-4.03109 StartY=-3.5 StartZ=0 EndX=-7.06218 EndY=-5.25 EndZ=0
    g36: LineSegment StartX=-7.06218 StartY=-5.25 StartZ=0 EndX=-7.06218 EndY=-8.75 EndZ=0
    g37: LineSegment StartX=-7.06218 StartY=-8.75 StartZ=0 EndX=-4.03109 EndY=-10.5 EndZ=0
    g38: LineSegment StartX=-4.03109 StartY=-10.5 StartZ=0 EndX=-1 EndY=-8.75 EndZ=0
    g39: LineSegment StartX=-1 StartY=-8.75 StartZ=0 EndX=-1 EndY=-5.25 EndZ=0
    g40: LineSegment StartX=-1 StartY=-5.25 StartZ=0 EndX=-4.03109 EndY=-3.5 EndZ=0
    g41: Circle [constr] CenterX=-4.03109 CenterY=-7 CenterZ=0 NormalX=0 NormalY=0 NormalZ=1 AngleXU=0 Radius=3.5
    g42: LineSegment StartX=4.03109 StartY=-3.5 StartZ=0 EndX=1 EndY=-5.25 EndZ=0
    g43: LineSegment StartX=1 StartY=-5.25 StartZ=0 EndX=1 EndY=-8.75 EndZ=0
    g44: LineSegment StartX=1 StartY=-8.75 StartZ=0 EndX=4.03109 EndY=-10.5 EndZ=0
    g45: LineSegment StartX=4.03109 StartY=-10.5 StartZ=0 EndX=7.06218 EndY=-8.75 EndZ=0
    g46: LineSegment StartX=7.06218 StartY=-8.75 StartZ=0 EndX=7.06218 EndY=-5.25 EndZ=0
    g47: LineSegment StartX=7.06218 StartY=-5.25 StartZ=0 EndX=4.03109 EndY=-3.5 EndZ=0
    g48: Circle [constr] CenterX=4.03109 CenterY=-7 CenterZ=0 NormalX=0 NormalY=0 NormalZ=1 AngleXU=0 Radius=3.5
  constraints (117):
    c: Coincident(g0,g1)
    c: Coincident(g1,g2)
    c: Coincident(g2,g3)
    c: Coincident(g3,g4)
    c: Coincident(g4,g5)
    c: Coincident(g5,g0)
    c: Equal(g0, g1-g5) x5
    c: PointOnObject(g0,g6)
    c: PointOnObject(g1,g6)
    c: PointOnObject(g2,g6)
    c: PointOnObject(g3,g6)
    c: PointOnObject(g4,g6)
    c: PointOnObject(g5,g6)
    c: Coincident(g6,g-1)
    c: Diameter(g6) = 7
    c: PointOnObject(g0,g-2)
    c: Coincident(g7,g8)
    c: Coincident(g8,g9)
    c: Coincident(g9,g10)
    c: Coincident(g10,g11)
    c: Coincident(g11,g12)
    c: Coincident(g12,g7)
    c: Equal(g7, g8-g12) x5
    c: PointOnObject(g7,g13)
    c: PointOnObject(g8,g13)
    c: PointOnObject(g9,g13)
    c: PointOnObject(g10,g13)
    c: PointOnObject(g11,g13)
    c: PointOnObject(g12,g13)
    c: PointOnObject(g13,g-1)
    c: Diameter(g13) = 7
    c: Distance(g6,g13) = 8
    c: Horizontal(g0,g10)
    c: Coincident(g14,g15)
    c: Coincident(g15,g16)
    c: Coincident(g16,g17)
    c: Coincident(g17,g18)
    c: Coincident(g18,g19)
    c: Coincident(g19,g14)
    c: Equal(g14, g15-g19) x5
    c: PointOnObject(g14,g20)
    c: PointOnObject(g15,g20)
    c: PointOnObject(g16,g20)
    c: PointOnObject(g17,g20)
    c: PointOnObject(g18,g20)
    c: PointOnObject(g19,g20)
    c: Diameter(g20) = 7
    c: DistanceY(g-1,g20) = 7
    c: Vertical(g18)
    c: Distance(g17,g-2) = 1
    c: Coincident(g21,g22)
    c: Coincident(g22,g23)
    c: Coincident(g23,g24)
    c: Coincident(g24,g25)
    c: Coincident(g25,g26)
    c: Coincident(g26,g21)
    c: Equal(g21, g22-g26) x5
    c: PointOnObject(g21,g27)
    c: PointOnObject(g22,g27)
    c: PointOnObject(g23,g27)
    c: PointOnObject(g24,g27)
    c: PointOnObject(g25,g27)
    c: PointOnObject(g26,g27)
    c: Diameter(g27) = 7
    c: DistanceY(g-1,g27) = 7
    c: DistanceX(g21,g-1) = 1
    c: Vertical(g21)
    c: Coincident(g28,g29)
    c: Coincident(g29,g30)
    c: Coincident(g30,g31)
    c: Coincident(g31,g32)
    c: Coincident(g32,g33)
    c: Coincident(g33,g28)
    c: Equal(g28, g29-g33) x5
    c: PointOnObject(g28,g34)
    c: PointOnObject(g29,g34)
    c: PointOnObject(g30,g34)
    c: PointOnObject(g31,g34)
    c: PointOnObject(g32,g34)
    c: PointOnObject(g33,g34)
    c: PointOnObject(g34,g-1)
    c: Diameter(g34) = 7
    c: Vertical(g31)
    c: DistanceX(g34,g-1) = 8
    c: Coincident(g35,g36)
    c: Coincident(g36,g37)
    c: Coincident(g37,g38)
    c: Coincident(g38,g39)
    c: Coincident(g39,g40)
    c: Coincident(g40,g35)
    c: Equal(g35, g36-g40) x5
    c: PointOnObject(g35,g41)
    c: PointOnObject(g36,g41)
    c: PointOnObject(g37,g41)
    c: PointOnObject(g38,g41)
    c: PointOnObject(g39,g41)
    c: PointOnObject(g40,g41)
    c: Coincident(g42,g43)
    c: Coincident(g43,g44)
    c: Coincident(g44,g45)
    c: Coincident(g45,g46)
    c: Coincident(g46,g47)
    c: Coincident(g47,g42)
    c: Equal(g42, g43-g47) x5
    c: PointOnObject(g42,g48)
    c: PointOnObject(g43,g48)
    c: PointOnObject(g44,g48)
    c: PointOnObject(g45,g48)
    c: PointOnObject(g46,g48)
    c: PointOnObject(g47,g48)
    c: Equal(g41,g48)
    c: Diameter(g41) = 7
    c: Vertical(g39)
    c: Vertical(g43)
    c: Distance(g-2,g39) = 1
    c: Symmetric(g38,g43,g-2)
    c: Distance(g41,g-1) = 7
FEATURE [Part::Extrusion] Extrude619  label="hex221"
  Base = -> Sketch628
  Dir = (0,-1,2e-16)
  DirMode = 2
  FaceMakerClass = Part::FaceMakerBullseye
  FaceMakerMode = 3
  LengthFwd = 10
  LengthRev = 0
  Placement = pos=(-20,0,-7) rot=(0,0,1;0rad)
  Solid = true
  Symmetric = false
FEATURE [Sketcher::SketchObject] Sketch629
  ArcFitTolerance = 1e-06
  FullyConstrained = true
  MakeInternals = false
  Placement = pos=(0,0,0) rot=(1,0,0;1.5708rad)
  sketch-geometry (49):
    g0: LineSegment StartX=1e-16 StartY=3.5 StartZ=0 EndX=-3.03109 EndY=1.75 EndZ=0
    g1: LineSegment StartX=-3.03109 StartY=1.75 StartZ=0 EndX=-3.03109 EndY=-1.75 EndZ=0
    g2: LineSegment StartX=-3.03109 StartY=-1.75 StartZ=0 EndX=-1e-16 EndY=-3.5 EndZ=0
    g3: LineSegment StartX=-1e-16 StartY=-3.5 StartZ=0 EndX=3.03109 EndY=-1.75 EndZ=0
    g4: LineSegment StartX=3.03109 StartY=-1.75 StartZ=0 EndX=3.03109 EndY=1.75 EndZ=0
    g5: LineSegment StartX=3.03109 StartY=1.75 StartZ=0 EndX=1e-16 EndY=3.5 EndZ=0
    g6: Circle [constr] CenterX=0 CenterY=0 CenterZ=0 NormalX=0 NormalY=0 NormalZ=1 AngleXU=0 Radius=3.5
    g7: LineSegment StartX=4.96892 StartY=-1.75002 StartZ=0 EndX=8.00002 EndY=-3.5 EndZ=0
    g8: LineSegment StartX=8.00002 StartY=-3.5 StartZ=0 EndX=11.0311 EndY=-1.74998 EndZ=0
    g9: LineSegment StartX=11.0311 StartY=-1.74998 StartZ=0 EndX=11.0311 EndY=1.75002 EndZ=0
    g10: LineSegment StartX=11.0311 StartY=1.75002 StartZ=0 EndX=7.99998 EndY=3.5 EndZ=0
    g11: LineSegment StartX=7.99998 StartY=3.5 StartZ=0 EndX=4.9689 EndY=1.74998 EndZ=0
    g12: LineSegment StartX=4.9689 StartY=1.74998 StartZ=0 EndX=4.96892 EndY=-1.75002 EndZ=0
    g13: Circle [constr] CenterX=8 CenterY=0 CenterZ=0 NormalX=0 NormalY=0 NormalZ=1 AngleXU=0 Radius=3.5
    g14: LineSegment StartX=4.03109 StartY=3.5 StartZ=0 EndX=7.06218 EndY=5.25 EndZ=0
    g15: LineSegment StartX=7.06218 StartY=5.25 StartZ=0 EndX=7.06218 EndY=8.75 EndZ=0
    g16: LineSegment StartX=7.06218 StartY=8.75 StartZ=0 EndX=4.03109 EndY=10.5 EndZ=0
    g17: LineSegment StartX=4.03109 StartY=10.5 StartZ=0 EndX=1 EndY=8.75 EndZ=0
    g18: LineSegment StartX=1 StartY=8.75 StartZ=0 EndX=1 EndY=5.25 EndZ=0
    g19: LineSegment StartX=1 StartY=5.25 StartZ=0 EndX=4.03109 EndY=3.5 EndZ=0
    g20: Circle [constr] CenterX=4.03109 CenterY=7 CenterZ=0 NormalX=0 NormalY=0 NormalZ=1 AngleXU=0 Radius=3.5
    g21: LineSegment StartX=-1 StartY=5.25 StartZ=0 EndX=-1 EndY=8.75 EndZ=0
    g22: LineSegment StartX=-1 StartY=8.75 StartZ=0 EndX=-4.03109 EndY=10.5 EndZ=0
    g23: LineSegment StartX=-4.03109 StartY=10.5 StartZ=0 EndX=-7.06218 EndY=8.75 EndZ=0
    g24: LineSegment StartX=-7.06218 StartY=8.75 StartZ=0 EndX=-7.06218 EndY=5.25 EndZ=0
    g25: LineSegment StartX=-7.06218 StartY=5.25 StartZ=0 EndX=-4.03109 EndY=3.5 EndZ=0
    g26: LineSegment StartX=-4.03109 StartY=3.5 StartZ=0 EndX=-1 EndY=5.25 EndZ=0
    g27: Circle [constr] CenterX=-4.03109 CenterY=7 CenterZ=0 NormalX=0 NormalY=0 NormalZ=1 AngleXU=0 Radius=3.5
    g28: LineSegment StartX=-4.96891 StartY=-1.75 StartZ=0 EndX=-4.96891 EndY=1.75 EndZ=0
    g29: LineSegment StartX=-4.96891 StartY=1.75 StartZ=0 EndX=-8 EndY=3.5 EndZ=0
    g30: LineSegment StartX=-8 StartY=3.5 StartZ=0 EndX=-11.0311 EndY=1.75 EndZ=0
    g31: LineSegment StartX=-11.0311 StartY=1.75 StartZ=0 EndX=-11.0311 EndY=-1.75 EndZ=0
    g32: LineSegment StartX=-11.0311 StartY=-1.75 StartZ=0 EndX=-8 EndY=-3.5 EndZ=0
    g33: LineSegment StartX=-8 StartY=-3.5 StartZ=0 EndX=-4.96891 EndY=-1.75 EndZ=0
    g34: Circle [constr] CenterX=-8 CenterY=0 CenterZ=0 NormalX=0 NormalY=0 NormalZ=1 AngleXU=0 Radius=3.5
    g35: LineSegment StartX=-4.03109 StartY=-3.5 StartZ=0 EndX=-7.06218 EndY=-5.25 EndZ=0
    g36: LineSegment StartX=-7.06218 StartY=-5.25 StartZ=0 EndX=-7.06218 EndY=-8.75 EndZ=0
    g37: LineSegment StartX=-7.06218 StartY=-8.75 StartZ=0 EndX=-4.03109 EndY=-10.5 EndZ=0
    g38: LineSegment StartX=-4.03109 StartY=-10.5 StartZ=0 EndX=-1 EndY=-8.75 EndZ=0
    g39: LineSegment StartX=-1 StartY=-8.75 StartZ=0 EndX=-1 EndY=-5.25 EndZ=0
    g40: LineSegment StartX=-1 StartY=-5.25 StartZ=0 EndX=-4.03109 EndY=-3.5 EndZ=0
    g41: Circle [constr] CenterX=-4.03109 CenterY=-7 CenterZ=0 NormalX=0 NormalY=0 NormalZ=1 AngleXU=0 Radius=3.5
    g42: LineSegment StartX=4.03109 StartY=-3.5 StartZ=0 EndX=1 EndY=-5.25 EndZ=0
    g43: LineSegment StartX=1 StartY=-5.25 StartZ=0 EndX=1 EndY=-8.75 EndZ=0
    g44: LineSegment StartX=1 StartY=-8.75 StartZ=0 EndX=4.03109 EndY=-10.5 EndZ=0
    g45: LineSegment StartX=4.03109 StartY=-10.5 StartZ=0 EndX=7.06218 EndY=-8.75 EndZ=0
    g46: LineSegment StartX=7.06218 StartY=-8.75 StartZ=0 EndX=7.06218 EndY=-5.25 EndZ=0
    g47: LineSegment StartX=7.06218 StartY=-5.25 StartZ=0 EndX=4.03109 EndY=-3.5 EndZ=0
    g48: Circle [constr] CenterX=4.03109 CenterY=-7 CenterZ=0 NormalX=0 NormalY=0 NormalZ=1 AngleXU=0 Radius=3.5
  constraints (117):
    c: Coincident(g0,g1)
    c: Coincident(g1,g2)
    c: Coincident(g2,g3)
    c: Coincident(g3,g4)
    c: Coincident(g4,g5)
    c: Coincident(g5,g0)
    c: Equal(g0, g1-g5) x5
    c: PointOnObject(g0,g6)
    c: PointOnObject(g1,g6)
    c: PointOnObject(g2,g6)
    c: PointOnObject(g3,g6)
    c: PointOnObject(g4,g6)
    c: PointOnObject(g5,g6)
    c: Coincident(g6,g-1)
    c: Diameter(g6) = 7
    c: PointOnObject(g0,g-2)
    c: Coincident(g7,g8)
    c: Coincident(g8,g9)
    c: Coincident(g9,g10)
    c: Coincident(g10,g11)
    c: Coincident(g11,g12)
    c: Coincident(g12,g7)
    c: Equal(g7, g8-g12) x5
    c: PointOnObject(g7,g13)
    c: PointOnObject(g8,g13)
    c: PointOnObject(g9,g13)
    c: PointOnObject(g10,g13)
    c: PointOnObject(g11,g13)
    c: PointOnObject(g12,g13)
    c: PointOnObject(g13,g-1)
    c: Diameter(g13) = 7
    c: Distance(g6,g13) = 8
    c: Horizontal(g0,g10)
    c: Coincident(g14,g15)
    c: Coincident(g15,g16)
    c: Coincident(g16,g17)
    c: Coincident(g17,g18)
    c: Coincident(g18,g19)
    c: Coincident(g19,g14)
    c: Equal(g14, g15-g19) x5
    c: PointOnObject(g14,g20)
    c: PointOnObject(g15,g20)
    c: PointOnObject(g16,g20)
    c: PointOnObject(g17,g20)
    c: PointOnObject(g18,g20)
    c: PointOnObject(g19,g20)
    c: Diameter(g20) = 7
    c: DistanceY(g-1,g20) = 7
    c: Vertical(g18)
    c: Distance(g17,g-2) = 1
    c: Coincident(g21,g22)
    c: Coincident(g22,g23)
    c: Coincident(g23,g24)
    c: Coincident(g24,g25)
    c: Coincident(g25,g26)
    c: Coincident(g26,g21)
    c: Equal(g21, g22-g26) x5
    c: PointOnObject(g21,g27)
    c: PointOnObject(g22,g27)
    c: PointOnObject(g23,g27)
    c: PointOnObject(g24,g27)
    c: PointOnObject(g25,g27)
    c: PointOnObject(g26,g27)
    c: Diameter(g27) = 7
    c: DistanceY(g-1,g27) = 7
    c: DistanceX(g21,g-1) = 1
    c: Vertical(g21)
    c: Coincident(g28,g29)
    c: Coincident(g29,g30)
    c: Coincident(g30,g31)
    c: Coincident(g31,g32)
    c: Coincident(g32,g33)
    c: Coincident(g33,g28)
    c: Equal(g28, g29-g33) x5
    c: PointOnObject(g28,g34)
    c: PointOnObject(g29,g34)
    c: PointOnObject(g30,g34)
    c: PointOnObject(g31,g34)
    c: PointOnObject(g32,g34)
    c: PointOnObject(g33,g34)
    c: PointOnObject(g34,g-1)
    c: Diameter(g34) = 7
    c: Vertical(g31)
    c: DistanceX(g34,g-1) = 8
    c: Coincident(g35,g36)
    c: Coincident(g36,g37)
    c: Coincident(g37,g38)
    c: Coincident(g38,g39)
    c: Coincident(g39,g40)
    c: Coincident(g40,g35)
    c: Equal(g35, g36-g40) x5
    c: PointOnObject(g35,g41)
    c: PointOnObject(g36,g41)
    c: PointOnObject(g37,g41)
    c: PointOnObject(g38,g41)
    c: PointOnObject(g39,g41)
    c: PointOnObject(g40,g41)
    c: Coincident(g42,g43)
    c: Coincident(g43,g44)
    c: Coincident(g44,g45)
    c: Coincident(g45,g46)
    c: Coincident(g46,g47)
    c: Coincident(g47,g42)
    c: Equal(g42, g43-g47) x5
    c: PointOnObject(g42,g48)
    c: PointOnObject(g43,g48)
    c: PointOnObject(g44,g48)
    c: PointOnObject(g45,g48)
    c: PointOnObject(g46,g48)
    c: PointOnObject(g47,g48)
    c: Equal(g41,g48)
    c: Diameter(g41) = 7
    c: Vertical(g39)
    c: Vertical(g43)
    c: Distance(g-2,g39) = 1
    c: Symmetric(g38,g43,g-2)
    c: Distance(g41,g-1) = 7
FEATURE [Part::Extrusion] Extrude620  label="hex222"
  Base = -> Sketch629
  Dir = (0,-1,2e-16)
  DirMode = 2
  FaceMakerClass = Part::FaceMakerBullseye
  FaceMakerMode = 3
  LengthFwd = 10
  LengthRev = 0
  Placement = pos=(-16,0,14) rot=(0,0,1;0rad)
  Solid = true
  Symmetric = false
FEATURE [Sketcher::SketchObject] Sketch630
  ArcFitTolerance = 1e-06
  FullyConstrained = true
  MakeInternals = false
  Placement = pos=(0,0,0) rot=(1,0,0;1.5708rad)
  sketch-geometry (49):
    g0: LineSegment StartX=1e-16 StartY=3.5 StartZ=0 EndX=-3.03109 EndY=1.75 EndZ=0
    g1: LineSegment StartX=-3.03109 StartY=1.75 StartZ=0 EndX=-3.03109 EndY=-1.75 EndZ=0
    g2: LineSegment StartX=-3.03109 StartY=-1.75 StartZ=0 EndX=-1e-16 EndY=-3.5 EndZ=0
    g3: LineSegment StartX=-1e-16 StartY=-3.5 StartZ=0 EndX=3.03109 EndY=-1.75 EndZ=0
    g4: LineSegment StartX=3.03109 StartY=-1.75 StartZ=0 EndX=3.03109 EndY=1.75 EndZ=0
    g5: LineSegment StartX=3.03109 StartY=1.75 StartZ=0 EndX=1e-16 EndY=3.5 EndZ=0
    g6: Circle [constr] CenterX=0 CenterY=0 CenterZ=0 NormalX=0 NormalY=0 NormalZ=1 AngleXU=0 Radius=3.5
    g7: LineSegment StartX=4.96892 StartY=-1.75002 StartZ=0 EndX=8.00002 EndY=-3.5 EndZ=0
    g8: LineSegment StartX=8.00002 StartY=-3.5 StartZ=0 EndX=11.0311 EndY=-1.74998 EndZ=0
    g9: LineSegment StartX=11.0311 StartY=-1.74998 StartZ=0 EndX=11.0311 EndY=1.75002 EndZ=0
    g10: LineSegment StartX=11.0311 StartY=1.75002 StartZ=0 EndX=7.99998 EndY=3.5 EndZ=0
    g11: LineSegment StartX=7.99998 StartY=3.5 StartZ=0 EndX=4.9689 EndY=1.74998 EndZ=0
    g12: LineSegment StartX=4.9689 StartY=1.74998 StartZ=0 EndX=4.96892 EndY=-1.75002 EndZ=0
    g13: Circle [constr] CenterX=8 CenterY=0 CenterZ=0 NormalX=0 NormalY=0 NormalZ=1 AngleXU=0 Radius=3.5
    g14: LineSegment StartX=4.03109 StartY=3.5 StartZ=0 EndX=7.06218 EndY=5.25 EndZ=0
    g15: LineSegment StartX=7.06218 StartY=5.25 StartZ=0 EndX=7.06218 EndY=8.75 EndZ=0
    g16: LineSegment StartX=7.06218 StartY=8.75 StartZ=0 EndX=4.03109 EndY=10.5 EndZ=0
    g17: LineSegment StartX=4.03109 StartY=10.5 StartZ=0 EndX=1 EndY=8.75 EndZ=0
    g18: LineSegment StartX=1 StartY=8.75 StartZ=0 EndX=1 EndY=5.25 EndZ=0
    g19: LineSegment StartX=1 StartY=5.25 StartZ=0 EndX=4.03109 EndY=3.5 EndZ=0
    g20: Circle [constr] CenterX=4.03109 CenterY=7 CenterZ=0 NormalX=0 NormalY=0 NormalZ=1 AngleXU=0 Radius=3.5
    g21: LineSegment StartX=-1 StartY=5.25 StartZ=0 EndX=-1 EndY=8.75 EndZ=0
    g22: LineSegment StartX=-1 StartY=8.75 StartZ=0 EndX=-4.03109 EndY=10.5 EndZ=0
    g23: LineSegment StartX=-4.03109 StartY=10.5 StartZ=0 EndX=-7.06218 EndY=8.75 EndZ=0
    g24: LineSegment StartX=-7.06218 StartY=8.75 StartZ=0 EndX=-7.06218 EndY=5.25 EndZ=0
    g25: LineSegment StartX=-7.06218 StartY=5.25 StartZ=0 EndX=-4.03109 EndY=3.5 EndZ=0
    g26: LineSegment StartX=-4.03109 StartY=3.5 StartZ=0 EndX=-1 EndY=5.25 EndZ=0
    g27: Circle [constr] CenterX=-4.03109 CenterY=7 CenterZ=0 NormalX=0 NormalY=0 NormalZ=1 AngleXU=0 Radius=3.5
    g28: LineSegment StartX=-4.96891 StartY=-1.75 StartZ=0 EndX=-4.96891 EndY=1.75 EndZ=0
    g29: LineSegment StartX=-4.96891 StartY=1.75 StartZ=0 EndX=-8 EndY=3.5 EndZ=0
    g30: LineSegment StartX=-8 StartY=3.5 StartZ=0 EndX=-11.0311 EndY=1.75 EndZ=0
    g31: LineSegment StartX=-11.0311 StartY=1.75 StartZ=0 EndX=-11.0311 EndY=-1.75 EndZ=0
    g32: LineSegment StartX=-11.0311 StartY=-1.75 StartZ=0 EndX=-8 EndY=-3.5 EndZ=0
    g33: LineSegment StartX=-8 StartY=-3.5 StartZ=0 EndX=-4.96891 EndY=-1.75 EndZ=0
    g34: Circle [constr] CenterX=-8 CenterY=0 CenterZ=0 NormalX=0 NormalY=0 NormalZ=1 AngleXU=0 Radius=3.5
    g35: LineSegment StartX=-4.03109 StartY=-3.5 StartZ=0 EndX=-7.06218 EndY=-5.25 EndZ=0
    g36: LineSegment StartX=-7.06218 StartY=-5.25 StartZ=0 EndX=-7.06218 EndY=-8.75 EndZ=0
    g37: LineSegment StartX=-7.06218 StartY=-8.75 StartZ=0 EndX=-4.03109 EndY=-10.5 EndZ=0
    g38: LineSegment StartX=-4.03109 StartY=-10.5 StartZ=0 EndX=-1 EndY=-8.75 EndZ=0
    g39: LineSegment StartX=-1 StartY=-8.75 StartZ=0 EndX=-1 EndY=-5.25 EndZ=0
    g40: LineSegment StartX=-1 StartY=-5.25 StartZ=0 EndX=-4.03109 EndY=-3.5 EndZ=0
    g41: Circle [constr] CenterX=-4.03109 CenterY=-7 CenterZ=0 NormalX=0 NormalY=0 NormalZ=1 AngleXU=0 Radius=3.5
    g42: LineSegment StartX=4.03109 StartY=-3.5 StartZ=0 EndX=1 EndY=-5.25 EndZ=0
    g43: LineSegment StartX=1 StartY=-5.25 StartZ=0 EndX=1 EndY=-8.75 EndZ=0
    g44: LineSegment StartX=1 StartY=-8.75 StartZ=0 EndX=4.03109 EndY=-10.5 EndZ=0
    g45: LineSegment StartX=4.03109 StartY=-10.5 StartZ=0 EndX=7.06218 EndY=-8.75 EndZ=0
    g46: LineSegment StartX=7.06218 StartY=-8.75 StartZ=0 EndX=7.06218 EndY=-5.25 EndZ=0
    g47: LineSegment StartX=7.06218 StartY=-5.25 StartZ=0 EndX=4.03109 EndY=-3.5 EndZ=0
    g48: Circle [constr] CenterX=4.03109 CenterY=-7 CenterZ=0 NormalX=0 NormalY=0 NormalZ=1 AngleXU=0 Radius=3.5
  constraints (117):
    c: Coincident(g0,g1)
    c: Coincident(g1,g2)
    c: Coincident(g2,g3)
    c: Coincident(g3,g4)
    c: Coincident(g4,g5)
    c: Coincident(g5,g0)
    c: Equal(g0, g1-g5) x5
    c: PointOnObject(g0,g6)
    c: PointOnObject(g1,g6)
    c: PointOnObject(g2,g6)
    c: PointOnObject(g3,g6)
    c: PointOnObject(g4,g6)
    c: PointOnObject(g5,g6)
    c: Coincident(g6,g-1)
    c: Diameter(g6) = 7
    c: PointOnObject(g0,g-2)
    c: Coincident(g7,g8)
    c: Coincident(g8,g9)
    c: Coincident(g9,g10)
    c: Coincident(g10,g11)
    c: Coincident(g11,g12)
    c: Coincident(g12,g7)
    c: Equal(g7, g8-g12) x5
    c: PointOnObject(g7,g13)
    c: PointOnObject(g8,g13)
    c: PointOnObject(g9,g13)
    c: PointOnObject(g10,g13)
    c: PointOnObject(g11,g13)
    c: PointOnObject(g12,g13)
    c: PointOnObject(g13,g-1)
    c: Diameter(g13) = 7
    c: Distance(g6,g13) = 8
    c: Horizontal(g0,g10)
    c: Coincident(g14,g15)
    c: Coincident(g15,g16)
    c: Coincident(g16,g17)
    c: Coincident(g17,g18)
    c: Coincident(g18,g19)
    c: Coincident(g19,g14)
    c: Equal(g14, g15-g19) x5
    c: PointOnObject(g14,g20)
    c: PointOnObject(g15,g20)
    c: PointOnObject(g16,g20)
    c: PointOnObject(g17,g20)
    c: PointOnObject(g18,g20)
    c: PointOnObject(g19,g20)
    c: Diameter(g20) = 7
    c: DistanceY(g-1,g20) = 7
    c: Vertical(g18)
    c: Distance(g17,g-2) = 1
    c: Coincident(g21,g22)
    c: Coincident(g22,g23)
    c: Coincident(g23,g24)
    c: Coincident(g24,g25)
    c: Coincident(g25,g26)
    c: Coincident(g26,g21)
    c: Equal(g21, g22-g26) x5
    c: PointOnObject(g21,g27)
    c: PointOnObject(g22,g27)
    c: PointOnObject(g23,g27)
    c: PointOnObject(g24,g27)
    c: PointOnObject(g25,g27)
    c: PointOnObject(g26,g27)
    c: Diameter(g27) = 7
    c: DistanceY(g-1,g27) = 7
    c: DistanceX(g21,g-1) = 1
    c: Vertical(g21)
    c: Coincident(g28,g29)
    c: Coincident(g29,g30)
    c: Coincident(g30,g31)
    c: Coincident(g31,g32)
    c: Coincident(g32,g33)
    c: Coincident(g33,g28)
    c: Equal(g28, g29-g33) x5
    c: PointOnObject(g28,g34)
    c: PointOnObject(g29,g34)
    c: PointOnObject(g30,g34)
    c: PointOnObject(g31,g34)
    c: PointOnObject(g32,g34)
    c: PointOnObject(g33,g34)
    c: PointOnObject(g34,g-1)
    c: Diameter(g34) = 7
    c: Vertical(g31)
    c: DistanceX(g34,g-1) = 8
    c: Coincident(g35,g36)
    c: Coincident(g36,g37)
    c: Coincident(g37,g38)
    c: Coincident(g38,g39)
    c: Coincident(g39,g40)
    c: Coincident(g40,g35)
    c: Equal(g35, g36-g40) x5
    c: PointOnObject(g35,g41)
    c: PointOnObject(g36,g41)
    c: PointOnObject(g37,g41)
    c: PointOnObject(g38,g41)
    c: PointOnObject(g39,g41)
    c: PointOnObject(g40,g41)
    c: Coincident(g42,g43)
    c: Coincident(g43,g44)
    c: Coincident(g44,g45)
    c: Coincident(g45,g46)
    c: Coincident(g46,g47)
    c: Coincident(g47,g42)
    c: Equal(g42, g43-g47) x5
    c: PointOnObject(g42,g48)
    c: PointOnObject(g43,g48)
    c: PointOnObject(g44,g48)
    c: PointOnObject(g45,g48)
    c: PointOnObject(g46,g48)
    c: PointOnObject(g47,g48)
    c: Equal(g41,g48)
    c: Diameter(g41) = 7
    c: Vertical(g39)
    c: Vertical(g43)
    c: Distance(g-2,g39) = 1
    c: Symmetric(g38,g43,g-2)
    c: Distance(g41,g-1) = 7
FEATURE [Part::Extrusion] Extrude621  label="hex223"
  Base = -> Sketch630
  Dir = (0,-1,2e-16)
  DirMode = 2
  FaceMakerClass = Part::FaceMakerBullseye
  FaceMakerMode = 3
  LengthFwd = 10
  LengthRev = 0
  Placement = pos=(-4,0,-21) rot=(0,0,1;0rad)
  Solid = true
  Symmetric = false
FEATURE [Sketcher::SketchObject] Sketch631
  ArcFitTolerance = 1e-06
  FullyConstrained = true
  MakeInternals = false
  Placement = pos=(0,0,0) rot=(1,0,0;1.5708rad)
  sketch-geometry (49):
    g0: LineSegment StartX=1e-16 StartY=3.5 StartZ=0 EndX=-3.03109 EndY=1.75 EndZ=0
    g1: LineSegment StartX=-3.03109 StartY=1.75 StartZ=0 EndX=-3.03109 EndY=-1.75 EndZ=0
    g2: LineSegment StartX=-3.03109 StartY=-1.75 StartZ=0 EndX=-1e-16 EndY=-3.5 EndZ=0
    g3: LineSegment StartX=-1e-16 StartY=-3.5 StartZ=0 EndX=3.03109 EndY=-1.75 EndZ=0
    g4: LineSegment StartX=3.03109 StartY=-1.75 StartZ=0 EndX=3.03109 EndY=1.75 EndZ=0
    g5: LineSegment StartX=3.03109 StartY=1.75 StartZ=0 EndX=1e-16 EndY=3.5 EndZ=0
    g6: Circle [constr] CenterX=0 CenterY=0 CenterZ=0 NormalX=0 NormalY=0 NormalZ=1 AngleXU=0 Radius=3.5
    g7: LineSegment StartX=4.96892 StartY=-1.75002 StartZ=0 EndX=8.00002 EndY=-3.5 EndZ=0
    g8: LineSegment StartX=8.00002 StartY=-3.5 StartZ=0 EndX=11.0311 EndY=-1.74998 EndZ=0
    g9: LineSegment StartX=11.0311 StartY=-1.74998 StartZ=0 EndX=11.0311 EndY=1.75002 EndZ=0
    g10: LineSegment StartX=11.0311 StartY=1.75002 StartZ=0 EndX=7.99998 EndY=3.5 EndZ=0
    g11: LineSegment StartX=7.99998 StartY=3.5 StartZ=0 EndX=4.9689 EndY=1.74998 EndZ=0
    g12: LineSegment StartX=4.9689 StartY=1.74998 StartZ=0 EndX=4.96892 EndY=-1.75002 EndZ=0
    g13: Circle [constr] CenterX=8 CenterY=0 CenterZ=0 NormalX=0 NormalY=0 NormalZ=1 AngleXU=0 Radius=3.5
    g14: LineSegment StartX=4.03109 StartY=3.5 StartZ=0 EndX=7.06218 EndY=5.25 EndZ=0
    g15: LineSegment StartX=7.06218 StartY=5.25 StartZ=0 EndX=7.06218 EndY=8.75 EndZ=0
    g16: LineSegment StartX=7.06218 StartY=8.75 StartZ=0 EndX=4.03109 EndY=10.5 EndZ=0
    g17: LineSegment StartX=4.03109 StartY=10.5 StartZ=0 EndX=1 EndY=8.75 EndZ=0
    g18: LineSegment StartX=1 StartY=8.75 StartZ=0 EndX=1 EndY=5.25 EndZ=0
    g19: LineSegment StartX=1 StartY=5.25 StartZ=0 EndX=4.03109 EndY=3.5 EndZ=0
    g20: Circle [constr] CenterX=4.03109 CenterY=7 CenterZ=0 NormalX=0 NormalY=0 NormalZ=1 AngleXU=0 Radius=3.5
    g21: LineSegment StartX=-1 StartY=5.25 StartZ=0 EndX=-1 EndY=8.75 EndZ=0
    g22: LineSegment StartX=-1 StartY=8.75 StartZ=0 EndX=-4.03109 EndY=10.5 EndZ=0
    g23: LineSegment StartX=-4.03109 StartY=10.5 StartZ=0 EndX=-7.06218 EndY=8.75 EndZ=0
    g24: LineSegment StartX=-7.06218 StartY=8.75 StartZ=0 EndX=-7.06218 EndY=5.25 EndZ=0
    g25: LineSegment StartX=-7.06218 StartY=5.25 StartZ=0 EndX=-4.03109 EndY=3.5 EndZ=0
    g26: LineSegment StartX=-4.03109 StartY=3.5 StartZ=0 EndX=-1 EndY=5.25 EndZ=0
    g27: Circle [constr] CenterX=-4.03109 CenterY=7 CenterZ=0 NormalX=0 NormalY=0 NormalZ=1 AngleXU=0 Radius=3.5
    g28: LineSegment StartX=-4.96891 StartY=-1.75 StartZ=0 EndX=-4.96891 EndY=1.75 EndZ=0
    g29: LineSegment StartX=-4.96891 StartY=1.75 StartZ=0 EndX=-8 EndY=3.5 EndZ=0
    g30: LineSegment StartX=-8 StartY=3.5 StartZ=0 EndX=-11.0311 EndY=1.75 EndZ=0
    g31: LineSegment StartX=-11.0311 StartY=1.75 StartZ=0 EndX=-11.0311 EndY=-1.75 EndZ=0
    g32: LineSegment StartX=-11.0311 StartY=-1.75 StartZ=0 EndX=-8 EndY=-3.5 EndZ=0
    g33: LineSegment StartX=-8 StartY=-3.5 StartZ=0 EndX=-4.96891 EndY=-1.75 EndZ=0
    g34: Circle [constr] CenterX=-8 CenterY=0 CenterZ=0 NormalX=0 NormalY=0 NormalZ=1 AngleXU=0 Radius=3.5
    g35: LineSegment StartX=-4.03109 StartY=-3.5 StartZ=0 EndX=-7.06218 EndY=-5.25 EndZ=0
    g36: LineSegment StartX=-7.06218 StartY=-5.25 StartZ=0 EndX=-7.06218 EndY=-8.75 EndZ=0
    g37: LineSegment StartX=-7.06218 StartY=-8.75 StartZ=0 EndX=-4.03109 EndY=-10.5 EndZ=0
    g38: LineSegment StartX=-4.03109 StartY=-10.5 StartZ=0 EndX=-1 EndY=-8.75 EndZ=0
    g39: LineSegment StartX=-1 StartY=-8.75 StartZ=0 EndX=-1 EndY=-5.25 EndZ=0
    g40: LineSegment StartX=-1 StartY=-5.25 StartZ=0 EndX=-4.03109 EndY=-3.5 EndZ=0
    g41: Circle [constr] CenterX=-4.03109 CenterY=-7 CenterZ=0 NormalX=0 NormalY=0 NormalZ=1 AngleXU=0 Radius=3.5
    g42: LineSegment StartX=4.03109 StartY=-3.5 StartZ=0 EndX=1 EndY=-5.25 EndZ=0
    g43: LineSegment StartX=1 StartY=-5.25 StartZ=0 EndX=1 EndY=-8.75 EndZ=0
    g44: LineSegment StartX=1 StartY=-8.75 StartZ=0 EndX=4.03109 EndY=-10.5 EndZ=0
    g45: LineSegment StartX=4.03109 StartY=-10.5 StartZ=0 EndX=7.06218 EndY=-8.75 EndZ=0
    g46: LineSegment StartX=7.06218 StartY=-8.75 StartZ=0 EndX=7.06218 EndY=-5.25 EndZ=0
    g47: LineSegment StartX=7.06218 StartY=-5.25 StartZ=0 EndX=4.03109 EndY=-3.5 EndZ=0
    g48: Circle [constr] CenterX=4.03109 CenterY=-7 CenterZ=0 NormalX=0 NormalY=0 NormalZ=1 AngleXU=0 Radius=3.5
  constraints (117):
    c: Coincident(g0,g1)
    c: Coincident(g1,g2)
    c: Coincident(g2,g3)
    c: Coincident(g3,g4)
    c: Coincident(g4,g5)
    c: Coincident(g5,g0)
    c: Equal(g0, g1-g5) x5
    c: PointOnObject(g0,g6)
    c: PointOnObject(g1,g6)
    c: PointOnObject(g2,g6)
    c: PointOnObject(g3,g6)
    c: PointOnObject(g4,g6)
    c: PointOnObject(g5,g6)
    c: Coincident(g6,g-1)
    c: Diameter(g6) = 7
    c: PointOnObject(g0,g-2)
    c: Coincident(g7,g8)
    c: Coincident(g8,g9)
    c: Coincident(g9,g10)
    c: Coincident(g10,g11)
    c: Coincident(g11,g12)
    c: Coincident(g12,g7)
    c: Equal(g7, g8-g12) x5
    c: PointOnObject(g7,g13)
    c: PointOnObject(g8,g13)
    c: PointOnObject(g9,g13)
    c: PointOnObject(g10,g13)
    c: PointOnObject(g11,g13)
    c: PointOnObject(g12,g13)
    c: PointOnObject(g13,g-1)
    c: Diameter(g13) = 7
    c: Distance(g6,g13) = 8
    c: Horizontal(g0,g10)
    c: Coincident(g14,g15)
    c: Coincident(g15,g16)
    c: Coincident(g16,g17)
    c: Coincident(g17,g18)
    c: Coincident(g18,g19)
    c: Coincident(g19,g14)
    c: Equal(g14, g15-g19) x5
    c: PointOnObject(g14,g20)
    c: PointOnObject(g15,g20)
    c: PointOnObject(g16,g20)
    c: PointOnObject(g17,g20)
    c: PointOnObject(g18,g20)
    c: PointOnObject(g19,g20)
    c: Diameter(g20) = 7
    c: DistanceY(g-1,g20) = 7
    c: Vertical(g18)
    c: Distance(g17,g-2) = 1
    c: Coincident(g21,g22)
    c: Coincident(g22,g23)
    c: Coincident(g23,g24)
    c: Coincident(g24,g25)
    c: Coincident(g25,g26)
    c: Coincident(g26,g21)
    c: Equal(g21, g22-g26) x5
    c: PointOnObject(g21,g27)
    c: PointOnObject(g22,g27)
    c: PointOnObject(g23,g27)
    c: PointOnObject(g24,g27)
    c: PointOnObject(g25,g27)
    c: PointOnObject(g26,g27)
    c: Diameter(g27) = 7
    c: DistanceY(g-1,g27) = 7
    c: DistanceX(g21,g-1) = 1
    c: Vertical(g21)
    c: Coincident(g28,g29)
    c: Coincident(g29,g30)
    c: Coincident(g30,g31)
    c: Coincident(g31,g32)
    c: Coincident(g32,g33)
    c: Coincident(g33,g28)
    c: Equal(g28, g29-g33) x5
    c: PointOnObject(g28,g34)
    c: PointOnObject(g29,g34)
    c: PointOnObject(g30,g34)
    c: PointOnObject(g31,g34)
    c: PointOnObject(g32,g34)
    c: PointOnObject(g33,g34)
    c: PointOnObject(g34,g-1)
    c: Diameter(g34) = 7
    c: Vertical(g31)
    c: DistanceX(g34,g-1) = 8
    c: Coincident(g35,g36)
    c: Coincident(g36,g37)
    c: Coincident(g37,g38)
    c: Coincident(g38,g39)
    c: Coincident(g39,g40)
    c: Coincident(g40,g35)
    c: Equal(g35, g36-g40) x5
    c: PointOnObject(g35,g41)
    c: PointOnObject(g36,g41)
    c: PointOnObject(g37,g41)
    c: PointOnObject(g38,g41)
    c: PointOnObject(g39,g41)
    c: PointOnObject(g40,g41)
    c: Coincident(g42,g43)
    c: Coincident(g43,g44)
    c: Coincident(g44,g45)
    c: Coincident(g45,g46)
    c: Coincident(g46,g47)
    c: Coincident(g47,g42)
    c: Equal(g42, g43-g47) x5
    c: PointOnObject(g42,g48)
    c: PointOnObject(g43,g48)
    c: PointOnObject(g44,g48)
    c: PointOnObject(g45,g48)
    c: PointOnObject(g46,g48)
    c: PointOnObject(g47,g48)
    c: Equal(g41,g48)
    c: Diameter(g41) = 7
    c: Vertical(g39)
    c: Vertical(g43)
    c: Distance(g-2,g39) = 1
    c: Symmetric(g38,g43,g-2)
    c: Distance(g41,g-1) = 7
FEATURE [Part::Extrusion] Extrude622  label="hex224"
  Base = -> Sketch631
  Dir = (0,-1,2e-16)
  DirMode = 2
  FaceMakerClass = Part::FaceMakerBullseye
  FaceMakerMode = 3
  LengthFwd = 10
  LengthRev = 0
  Placement = pos=(16,0,-14) rot=(0,0,1;0rad)
  Solid = true
  Symmetric = false
FEATURE [Sketcher::SketchObject] Sketch632
  ArcFitTolerance = 1e-06
  FullyConstrained = true
  MakeInternals = false
  Placement = pos=(0,0,0) rot=(1,0,0;1.5708rad)
  sketch-geometry (49):
    g0: LineSegment StartX=1e-16 StartY=3.5 StartZ=0 EndX=-3.03109 EndY=1.75 EndZ=0
    g1: LineSegment StartX=-3.03109 StartY=1.75 StartZ=0 EndX=-3.03109 EndY=-1.75 EndZ=0
    g2: LineSegment StartX=-3.03109 StartY=-1.75 StartZ=0 EndX=-1e-16 EndY=-3.5 EndZ=0
    g3: LineSegment StartX=-1e-16 StartY=-3.5 StartZ=0 EndX=3.03109 EndY=-1.75 EndZ=0
    g4: LineSegment StartX=3.03109 StartY=-1.75 StartZ=0 EndX=3.03109 EndY=1.75 EndZ=0
    g5: LineSegment StartX=3.03109 StartY=1.75 StartZ=0 EndX=1e-16 EndY=3.5 EndZ=0
    g6: Circle [constr] CenterX=0 CenterY=0 CenterZ=0 NormalX=0 NormalY=0 NormalZ=1 AngleXU=0 Radius=3.5
    g7: LineSegment StartX=4.96892 StartY=-1.75002 StartZ=0 EndX=8.00002 EndY=-3.5 EndZ=0
    g8: LineSegment StartX=8.00002 StartY=-3.5 StartZ=0 EndX=11.0311 EndY=-1.74998 EndZ=0
    g9: LineSegment StartX=11.0311 StartY=-1.74998 StartZ=0 EndX=11.0311 EndY=1.75002 EndZ=0
    g10: LineSegment StartX=11.0311 StartY=1.75002 StartZ=0 EndX=7.99998 EndY=3.5 EndZ=0
    g11: LineSegment StartX=7.99998 StartY=3.5 StartZ=0 EndX=4.9689 EndY=1.74998 EndZ=0
    g12: LineSegment StartX=4.9689 StartY=1.74998 StartZ=0 EndX=4.96892 EndY=-1.75002 EndZ=0
    g13: Circle [constr] CenterX=8 CenterY=0 CenterZ=0 NormalX=0 NormalY=0 NormalZ=1 AngleXU=0 Radius=3.5
    g14: LineSegment StartX=4.03109 StartY=3.5 StartZ=0 EndX=7.06218 EndY=5.25 EndZ=0
    g15: LineSegment StartX=7.06218 StartY=5.25 StartZ=0 EndX=7.06218 EndY=8.75 EndZ=0
    g16: LineSegment StartX=7.06218 StartY=8.75 StartZ=0 EndX=4.03109 EndY=10.5 EndZ=0
    g17: LineSegment StartX=4.03109 StartY=10.5 StartZ=0 EndX=1 EndY=8.75 EndZ=0
    g18: LineSegment StartX=1 StartY=8.75 StartZ=0 EndX=1 EndY=5.25 EndZ=0
    g19: LineSegment StartX=1 StartY=5.25 StartZ=0 EndX=4.03109 EndY=3.5 EndZ=0
    g20: Circle [constr] CenterX=4.03109 CenterY=7 CenterZ=0 NormalX=0 NormalY=0 NormalZ=1 AngleXU=0 Radius=3.5
    g21: LineSegment StartX=-1 StartY=5.25 StartZ=0 EndX=-1 EndY=8.75 EndZ=0
    g22: LineSegment StartX=-1 StartY=8.75 StartZ=0 EndX=-4.03109 EndY=10.5 EndZ=0
    g23: LineSegment StartX=-4.03109 StartY=10.5 StartZ=0 EndX=-7.06218 EndY=8.75 EndZ=0
    g24: LineSegment StartX=-7.06218 StartY=8.75 StartZ=0 EndX=-7.06218 EndY=5.25 EndZ=0
    g25: LineSegment StartX=-7.06218 StartY=5.25 StartZ=0 EndX=-4.03109 EndY=3.5 EndZ=0
    g26: LineSegment StartX=-4.03109 StartY=3.5 StartZ=0 EndX=-1 EndY=5.25 EndZ=0
    g27: Circle [constr] CenterX=-4.03109 CenterY=7 CenterZ=0 NormalX=0 NormalY=0 NormalZ=1 AngleXU=0 Radius=3.5
    g28: LineSegment StartX=-4.96891 StartY=-1.75 StartZ=0 EndX=-4.96891 EndY=1.75 EndZ=0
    g29: LineSegment StartX=-4.96891 StartY=1.75 StartZ=0 EndX=-8 EndY=3.5 EndZ=0
    g30: LineSegment StartX=-8 StartY=3.5 StartZ=0 EndX=-11.0311 EndY=1.75 EndZ=0
    g31: LineSegment StartX=-11.0311 StartY=1.75 StartZ=0 EndX=-11.0311 EndY=-1.75 EndZ=0
    g32: LineSegment StartX=-11.0311 StartY=-1.75 StartZ=0 EndX=-8 EndY=-3.5 EndZ=0
    g33: LineSegment StartX=-8 StartY=-3.5 StartZ=0 EndX=-4.96891 EndY=-1.75 EndZ=0
    g34: Circle [constr] CenterX=-8 CenterY=0 CenterZ=0 NormalX=0 NormalY=0 NormalZ=1 AngleXU=0 Radius=3.5
    g35: LineSegment StartX=-4.03109 StartY=-3.5 StartZ=0 EndX=-7.06218 EndY=-5.25 EndZ=0
    g36: LineSegment StartX=-7.06218 StartY=-5.25 StartZ=0 EndX=-7.06218 EndY=-8.75 EndZ=0
    g37: LineSegment StartX=-7.06218 StartY=-8.75 StartZ=0 EndX=-4.03109 EndY=-10.5 EndZ=0
    g38: LineSegment StartX=-4.03109 StartY=-10.5 StartZ=0 EndX=-1 EndY=-8.75 EndZ=0
    g39: LineSegment StartX=-1 StartY=-8.75 StartZ=0 EndX=-1 EndY=-5.25 EndZ=0
    g40: LineSegment StartX=-1 StartY=-5.25 StartZ=0 EndX=-4.03109 EndY=-3.5 EndZ=0
    g41: Circle [constr] CenterX=-4.03109 CenterY=-7 CenterZ=0 NormalX=0 NormalY=0 NormalZ=1 AngleXU=0 Radius=3.5
    g42: LineSegment StartX=4.03109 StartY=-3.5 StartZ=0 EndX=1 EndY=-5.25 EndZ=0
    g43: LineSegment StartX=1 StartY=-5.25 StartZ=0 EndX=1 EndY=-8.75 EndZ=0
    g44: LineSegment StartX=1 StartY=-8.75 StartZ=0 EndX=4.03109 EndY=-10.5 EndZ=0
    g45: LineSegment StartX=4.03109 StartY=-10.5 StartZ=0 EndX=7.06218 EndY=-8.75 EndZ=0
    g46: LineSegment StartX=7.06218 StartY=-8.75 StartZ=0 EndX=7.06218 EndY=-5.25 EndZ=0
    g47: LineSegment StartX=7.06218 StartY=-5.25 StartZ=0 EndX=4.03109 EndY=-3.5 EndZ=0
    g48: Circle [constr] CenterX=4.03109 CenterY=-7 CenterZ=0 NormalX=0 NormalY=0 NormalZ=1 AngleXU=0 Radius=3.5
  constraints (117):
    c: Coincident(g0,g1)
    c: Coincident(g1,g2)
    c: Coincident(g2,g3)
    c: Coincident(g3,g4)
    c: Coincident(g4,g5)
    c: Coincident(g5,g0)
    c: Equal(g0, g1-g5) x5
    c: PointOnObject(g0,g6)
    c: PointOnObject(g1,g6)
    c: PointOnObject(g2,g6)
    c: PointOnObject(g3,g6)
    c: PointOnObject(g4,g6)
    c: PointOnObject(g5,g6)
    c: Coincident(g6,g-1)
    c: Diameter(g6) = 7
    c: PointOnObject(g0,g-2)
    c: Coincident(g7,g8)
    c: Coincident(g8,g9)
    c: Coincident(g9,g10)
    c: Coincident(g10,g11)
    c: Coincident(g11,g12)
    c: Coincident(g12,g7)
    c: Equal(g7, g8-g12) x5
    c: PointOnObject(g7,g13)
    c: PointOnObject(g8,g13)
    c: PointOnObject(g9,g13)
    c: PointOnObject(g10,g13)
    c: PointOnObject(g11,g13)
    c: PointOnObject(g12,g13)
    c: PointOnObject(g13,g-1)
    c: Diameter(g13) = 7
    c: Distance(g6,g13) = 8
    c: Horizontal(g0,g10)
    c: Coincident(g14,g15)
    c: Coincident(g15,g16)
    c: Coincident(g16,g17)
    c: Coincident(g17,g18)
    c: Coincident(g18,g19)
    c: Coincident(g19,g14)
    c: Equal(g14, g15-g19) x5
    c: PointOnObject(g14,g20)
    c: PointOnObject(g15,g20)
    c: PointOnObject(g16,g20)
    c: PointOnObject(g17,g20)
    c: PointOnObject(g18,g20)
    c: PointOnObject(g19,g20)
    c: Diameter(g20) = 7
    c: DistanceY(g-1,g20) = 7
    c: Vertical(g18)
    c: Distance(g17,g-2) = 1
    c: Coincident(g21,g22)
    c: Coincident(g22,g23)
    c: Coincident(g23,g24)
    c: Coincident(g24,g25)
    c: Coincident(g25,g26)
    c: Coincident(g26,g21)
    c: Equal(g21, g22-g26) x5
    c: PointOnObject(g21,g27)
    c: PointOnObject(g22,g27)
    c: PointOnObject(g23,g27)
    c: PointOnObject(g24,g27)
    c: PointOnObject(g25,g27)
    c: PointOnObject(g26,g27)
    c: Diameter(g27) = 7
    c: DistanceY(g-1,g27) = 7
    c: DistanceX(g21,g-1) = 1
    c: Vertical(g21)
    c: Coincident(g28,g29)
    c: Coincident(g29,g30)
    c: Coincident(g30,g31)
    c: Coincident(g31,g32)
    c: Coincident(g32,g33)
    c: Coincident(g33,g28)
    c: Equal(g28, g29-g33) x5
    c: PointOnObject(g28,g34)
    c: PointOnObject(g29,g34)
    c: PointOnObject(g30,g34)
    c: PointOnObject(g31,g34)
    c: PointOnObject(g32,g34)
    c: PointOnObject(g33,g34)
    c: PointOnObject(g34,g-1)
    c: Diameter(g34) = 7
    c: Vertical(g31)
    c: DistanceX(g34,g-1) = 8
    c: Coincident(g35,g36)
    c: Coincident(g36,g37)
    c: Coincident(g37,g38)
    c: Coincident(g38,g39)
    c: Coincident(g39,g40)
    c: Coincident(g40,g35)
    c: Equal(g35, g36-g40) x5
    c: PointOnObject(g35,g41)
    c: PointOnObject(g36,g41)
    c: PointOnObject(g37,g41)
    c: PointOnObject(g38,g41)
    c: PointOnObject(g39,g41)
    c: PointOnObject(g40,g41)
    c: Coincident(g42,g43)
    c: Coincident(g43,g44)
    c: Coincident(g44,g45)
    c: Coincident(g45,g46)
    c: Coincident(g46,g47)
    c: Coincident(g47,g42)
    c: Equal(g42, g43-g47) x5
    c: PointOnObject(g42,g48)
    c: PointOnObject(g43,g48)
    c: PointOnObject(g44,g48)
    c: PointOnObject(g45,g48)
    c: PointOnObject(g46,g48)
    c: PointOnObject(g47,g48)
    c: Equal(g41,g48)
    c: Diameter(g41) = 7
    c: Vertical(g39)
    c: Vertical(g43)
    c: Distance(g-2,g39) = 1
    c: Symmetric(g38,g43,g-2)
    c: Distance(g41,g-1) = 7
FEATURE [Part::Extrusion] Extrude623  label="hex225"
  Base = -> Sketch632
  Dir = (0,-1,2e-16)
  DirMode = 2
  FaceMakerClass = Part::FaceMakerBullseye
  FaceMakerMode = 3
  LengthFwd = 10
  LengthRev = 0
  Placement = pos=(-4,0,21) rot=(0,0,1;0rad)
  Solid = true
  Symmetric = false
FEATURE [Sketcher::SketchObject] Sketch633
  ArcFitTolerance = 1e-06
  FullyConstrained = true
  MakeInternals = false
  Placement = pos=(0,0,0) rot=(1,0,0;1.5708rad)
  sketch-geometry (49):
    g0: LineSegment StartX=1e-16 StartY=3.5 StartZ=0 EndX=-3.03109 EndY=1.75 EndZ=0
    g1: LineSegment StartX=-3.03109 StartY=1.75 StartZ=0 EndX=-3.03109 EndY=-1.75 EndZ=0
    g2: LineSegment StartX=-3.03109 StartY=-1.75 StartZ=0 EndX=-1e-16 EndY=-3.5 EndZ=0
    g3: LineSegment StartX=-1e-16 StartY=-3.5 StartZ=0 EndX=3.03109 EndY=-1.75 EndZ=0
    g4: LineSegment StartX=3.03109 StartY=-1.75 StartZ=0 EndX=3.03109 EndY=1.75 EndZ=0
    g5: LineSegment StartX=3.03109 StartY=1.75 StartZ=0 EndX=1e-16 EndY=3.5 EndZ=0
    g6: Circle [constr] CenterX=0 CenterY=0 CenterZ=0 NormalX=0 NormalY=0 NormalZ=1 AngleXU=0 Radius=3.5
    g7: LineSegment StartX=4.96892 StartY=-1.75002 StartZ=0 EndX=8.00002 EndY=-3.5 EndZ=0
    g8: LineSegment StartX=8.00002 StartY=-3.5 StartZ=0 EndX=11.0311 EndY=-1.74998 EndZ=0
    g9: LineSegment StartX=11.0311 StartY=-1.74998 StartZ=0 EndX=11.0311 EndY=1.75002 EndZ=0
    g10: LineSegment StartX=11.0311 StartY=1.75002 StartZ=0 EndX=7.99998 EndY=3.5 EndZ=0
    g11: LineSegment StartX=7.99998 StartY=3.5 StartZ=0 EndX=4.9689 EndY=1.74998 EndZ=0
    g12: LineSegment StartX=4.9689 StartY=1.74998 StartZ=0 EndX=4.96892 EndY=-1.75002 EndZ=0
    g13: Circle [constr] CenterX=8 CenterY=0 CenterZ=0 NormalX=0 NormalY=0 NormalZ=1 AngleXU=0 Radius=3.5
    g14: LineSegment StartX=4.03109 StartY=3.5 StartZ=0 EndX=7.06218 EndY=5.25 EndZ=0
    g15: LineSegment StartX=7.06218 StartY=5.25 StartZ=0 EndX=7.06218 EndY=8.75 EndZ=0
    g16: LineSegment StartX=7.06218 StartY=8.75 StartZ=0 EndX=4.03109 EndY=10.5 EndZ=0
    g17: LineSegment StartX=4.03109 StartY=10.5 StartZ=0 EndX=1 EndY=8.75 EndZ=0
    g18: LineSegment StartX=1 StartY=8.75 StartZ=0 EndX=1 EndY=5.25 EndZ=0
    g19: LineSegment StartX=1 StartY=5.25 StartZ=0 EndX=4.03109 EndY=3.5 EndZ=0
    g20: Circle [constr] CenterX=4.03109 CenterY=7 CenterZ=0 NormalX=0 NormalY=0 NormalZ=1 AngleXU=0 Radius=3.5
    g21: LineSegment StartX=-1 StartY=5.25 StartZ=0 EndX=-1 EndY=8.75 EndZ=0
    g22: LineSegment StartX=-1 StartY=8.75 StartZ=0 EndX=-4.03109 EndY=10.5 EndZ=0
    g23: LineSegment StartX=-4.03109 StartY=10.5 StartZ=0 EndX=-7.06218 EndY=8.75 EndZ=0
    g24: LineSegment StartX=-7.06218 StartY=8.75 StartZ=0 EndX=-7.06218 EndY=5.25 EndZ=0
    g25: LineSegment StartX=-7.06218 StartY=5.25 StartZ=0 EndX=-4.03109 EndY=3.5 EndZ=0
    g26: LineSegment StartX=-4.03109 StartY=3.5 StartZ=0 EndX=-1 EndY=5.25 EndZ=0
    g27: Circle [constr] CenterX=-4.03109 CenterY=7 CenterZ=0 NormalX=0 NormalY=0 NormalZ=1 AngleXU=0 Radius=3.5
    g28: LineSegment StartX=-4.96891 StartY=-1.75 StartZ=0 EndX=-4.96891 EndY=1.75 EndZ=0
    g29: LineSegment StartX=-4.96891 StartY=1.75 StartZ=0 EndX=-8 EndY=3.5 EndZ=0
    g30: LineSegment StartX=-8 StartY=3.5 StartZ=0 EndX=-11.0311 EndY=1.75 EndZ=0
    g31: LineSegment StartX=-11.0311 StartY=1.75 StartZ=0 EndX=-11.0311 EndY=-1.75 EndZ=0
    g32: LineSegment StartX=-11.0311 StartY=-1.75 StartZ=0 EndX=-8 EndY=-3.5 EndZ=0
    g33: LineSegment StartX=-8 StartY=-3.5 StartZ=0 EndX=-4.96891 EndY=-1.75 EndZ=0
    g34: Circle [constr] CenterX=-8 CenterY=0 CenterZ=0 NormalX=0 NormalY=0 NormalZ=1 AngleXU=0 Radius=3.5
    g35: LineSegment StartX=-4.03109 StartY=-3.5 StartZ=0 EndX=-7.06218 EndY=-5.25 EndZ=0
    g36: LineSegment StartX=-7.06218 StartY=-5.25 StartZ=0 EndX=-7.06218 EndY=-8.75 EndZ=0
    g37: LineSegment StartX=-7.06218 StartY=-8.75 StartZ=0 EndX=-4.03109 EndY=-10.5 EndZ=0
    g38: LineSegment StartX=-4.03109 StartY=-10.5 StartZ=0 EndX=-1 EndY=-8.75 EndZ=0
    g39: LineSegment StartX=-1 StartY=-8.75 StartZ=0 EndX=-1 EndY=-5.25 EndZ=0
    g40: LineSegment StartX=-1 StartY=-5.25 StartZ=0 EndX=-4.03109 EndY=-3.5 EndZ=0
    g41: Circle [constr] CenterX=-4.03109 CenterY=-7 CenterZ=0 NormalX=0 NormalY=0 NormalZ=1 AngleXU=0 Radius=3.5
    g42: LineSegment StartX=4.03109 StartY=-3.5 StartZ=0 EndX=1 EndY=-5.25 EndZ=0
    g43: LineSegment StartX=1 StartY=-5.25 StartZ=0 EndX=1 EndY=-8.75 EndZ=0
    g44: LineSegment StartX=1 StartY=-8.75 StartZ=0 EndX=4.03109 EndY=-10.5 EndZ=0
    g45: LineSegment StartX=4.03109 StartY=-10.5 StartZ=0 EndX=7.06218 EndY=-8.75 EndZ=0
    g46: LineSegment StartX=7.06218 StartY=-8.75 StartZ=0 EndX=7.06218 EndY=-5.25 EndZ=0
    g47: LineSegment StartX=7.06218 StartY=-5.25 StartZ=0 EndX=4.03109 EndY=-3.5 EndZ=0
    g48: Circle [constr] CenterX=4.03109 CenterY=-7 CenterZ=0 NormalX=0 NormalY=0 NormalZ=1 AngleXU=0 Radius=3.5
  constraints (117):
    c: Coincident(g0,g1)
    c: Coincident(g1,g2)
    c: Coincident(g2,g3)
    c: Coincident(g3,g4)
    c: Coincident(g4,g5)
    c: Coincident(g5,g0)
    c: Equal(g0, g1-g5) x5
    c: PointOnObject(g0,g6)
    c: PointOnObject(g1,g6)
    c: PointOnObject(g2,g6)
    c: PointOnObject(g3,g6)
    c: PointOnObject(g4,g6)
    c: PointOnObject(g5,g6)
    c: Coincident(g6,g-1)
    c: Diameter(g6) = 7
    c: PointOnObject(g0,g-2)
    c: Coincident(g7,g8)
    c: Coincident(g8,g9)
    c: Coincident(g9,g10)
    c: Coincident(g10,g11)
    c: Coincident(g11,g12)
    c: Coincident(g12,g7)
    c: Equal(g7, g8-g12) x5
    c: PointOnObject(g7,g13)
    c: PointOnObject(g8,g13)
    c: PointOnObject(g9,g13)
    c: PointOnObject(g10,g13)
    c: PointOnObject(g11,g13)
    c: PointOnObject(g12,g13)
    c: PointOnObject(g13,g-1)
    c: Diameter(g13) = 7
    c: Distance(g6,g13) = 8
    c: Horizontal(g0,g10)
    c: Coincident(g14,g15)
    c: Coincident(g15,g16)
    c: Coincident(g16,g17)
    c: Coincident(g17,g18)
    c: Coincident(g18,g19)
    c: Coincident(g19,g14)
    c: Equal(g14, g15-g19) x5
    c: PointOnObject(g14,g20)
    c: PointOnObject(g15,g20)
    c: PointOnObject(g16,g20)
    c: PointOnObject(g17,g20)
    c: PointOnObject(g18,g20)
    c: PointOnObject(g19,g20)
    c: Diameter(g20) = 7
    c: DistanceY(g-1,g20) = 7
    c: Vertical(g18)
    c: Distance(g17,g-2) = 1
    c: Coincident(g21,g22)
    c: Coincident(g22,g23)
    c: Coincident(g23,g24)
    c: Coincident(g24,g25)
    c: Coincident(g25,g26)
    c: Coincident(g26,g21)
    c: Equal(g21, g22-g26) x5
    c: PointOnObject(g21,g27)
    c: PointOnObject(g22,g27)
    c: PointOnObject(g23,g27)
    c: PointOnObject(g24,g27)
    c: PointOnObject(g25,g27)
    c: PointOnObject(g26,g27)
    c: Diameter(g27) = 7
    c: DistanceY(g-1,g27) = 7
    c: DistanceX(g21,g-1) = 1
    c: Vertical(g21)
    c: Coincident(g28,g29)
    c: Coincident(g29,g30)
    c: Coincident(g30,g31)
    c: Coincident(g31,g32)
    c: Coincident(g32,g33)
    c: Coincident(g33,g28)
    c: Equal(g28, g29-g33) x5
    c: PointOnObject(g28,g34)
    c: PointOnObject(g29,g34)
    c: PointOnObject(g30,g34)
    c: PointOnObject(g31,g34)
    c: PointOnObject(g32,g34)
    c: PointOnObject(g33,g34)
    c: PointOnObject(g34,g-1)
    c: Diameter(g34) = 7
    c: Vertical(g31)
    c: DistanceX(g34,g-1) = 8
    c: Coincident(g35,g36)
    c: Coincident(g36,g37)
    c: Coincident(g37,g38)
    c: Coincident(g38,g39)
    c: Coincident(g39,g40)
    c: Coincident(g40,g35)
    c: Equal(g35, g36-g40) x5
    c: PointOnObject(g35,g41)
    c: PointOnObject(g36,g41)
    c: PointOnObject(g37,g41)
    c: PointOnObject(g38,g41)
    c: PointOnObject(g39,g41)
    c: PointOnObject(g40,g41)
    c: Coincident(g42,g43)
    c: Coincident(g43,g44)
    c: Coincident(g44,g45)
    c: Coincident(g45,g46)
    c: Coincident(g46,g47)
    c: Coincident(g47,g42)
    c: Equal(g42, g43-g47) x5
    c: PointOnObject(g42,g48)
    c: PointOnObject(g43,g48)
    c: PointOnObject(g44,g48)
    c: PointOnObject(g45,g48)
    c: PointOnObject(g46,g48)
    c: PointOnObject(g47,g48)
    c: Equal(g41,g48)
    c: Diameter(g41) = 7
    c: Vertical(g39)
    c: Vertical(g43)
    c: Distance(g-2,g39) = 1
    c: Symmetric(g38,g43,g-2)
    c: Distance(g41,g-1) = 7
FEATURE [Part::Extrusion] Extrude624  label="hex226"
  Base = -> Sketch633
  Dir = (0,-1,2e-16)
  DirMode = 2
  FaceMakerClass = Part::FaceMakerBullseye
  FaceMakerMode = 3
  LengthFwd = 10
  LengthRev = 0
  Placement = pos=(12,0,-35) rot=(0,0,1;0rad)
  Solid = true
  Symmetric = false
FEATURE [Sketcher::SketchObject] Sketch634
  ArcFitTolerance = 1e-06
  FullyConstrained = true
  MakeInternals = false
  Placement = pos=(0,0,0) rot=(1,0,0;1.5708rad)
  sketch-geometry (49):
    g0: LineSegment StartX=1e-16 StartY=3.5 StartZ=0 EndX=-3.03109 EndY=1.75 EndZ=0
    g1: LineSegment StartX=-3.03109 StartY=1.75 StartZ=0 EndX=-3.03109 EndY=-1.75 EndZ=0
    g2: LineSegment StartX=-3.03109 StartY=-1.75 StartZ=0 EndX=-1e-16 EndY=-3.5 EndZ=0
    g3: LineSegment StartX=-1e-16 StartY=-3.5 StartZ=0 EndX=3.03109 EndY=-1.75 EndZ=0
    g4: LineSegment StartX=3.03109 StartY=-1.75 StartZ=0 EndX=3.03109 EndY=1.75 EndZ=0
    g5: LineSegment StartX=3.03109 StartY=1.75 StartZ=0 EndX=1e-16 EndY=3.5 EndZ=0
    g6: Circle [constr] CenterX=0 CenterY=0 CenterZ=0 NormalX=0 NormalY=0 NormalZ=1 AngleXU=0 Radius=3.5
    g7: LineSegment StartX=4.96892 StartY=-1.75002 StartZ=0 EndX=8.00002 EndY=-3.5 EndZ=0
    g8: LineSegment StartX=8.00002 StartY=-3.5 StartZ=0 EndX=11.0311 EndY=-1.74998 EndZ=0
    g9: LineSegment StartX=11.0311 StartY=-1.74998 StartZ=0 EndX=11.0311 EndY=1.75002 EndZ=0
    g10: LineSegment StartX=11.0311 StartY=1.75002 StartZ=0 EndX=7.99998 EndY=3.5 EndZ=0
    g11: LineSegment StartX=7.99998 StartY=3.5 StartZ=0 EndX=4.9689 EndY=1.74998 EndZ=0
    g12: LineSegment StartX=4.9689 StartY=1.74998 StartZ=0 EndX=4.96892 EndY=-1.75002 EndZ=0
    g13: Circle [constr] CenterX=8 CenterY=0 CenterZ=0 NormalX=0 NormalY=0 NormalZ=1 AngleXU=0 Radius=3.5
    g14: LineSegment StartX=4.03109 StartY=3.5 StartZ=0 EndX=7.06218 EndY=5.25 EndZ=0
    g15: LineSegment StartX=7.06218 StartY=5.25 StartZ=0 EndX=7.06218 EndY=8.75 EndZ=0
    g16: LineSegment StartX=7.06218 StartY=8.75 StartZ=0 EndX=4.03109 EndY=10.5 EndZ=0
    g17: LineSegment StartX=4.03109 StartY=10.5 StartZ=0 EndX=1 EndY=8.75 EndZ=0
    g18: LineSegment StartX=1 StartY=8.75 StartZ=0 EndX=1 EndY=5.25 EndZ=0
    g19: LineSegment StartX=1 StartY=5.25 StartZ=0 EndX=4.03109 EndY=3.5 EndZ=0
    g20: Circle [constr] CenterX=4.03109 CenterY=7 CenterZ=0 NormalX=0 NormalY=0 NormalZ=1 AngleXU=0 Radius=3.5
    g21: LineSegment StartX=-1 StartY=5.25 StartZ=0 EndX=-1 EndY=8.75 EndZ=0
    g22: LineSegment StartX=-1 StartY=8.75 StartZ=0 EndX=-4.03109 EndY=10.5 EndZ=0
    g23: LineSegment StartX=-4.03109 StartY=10.5 StartZ=0 EndX=-7.06218 EndY=8.75 EndZ=0
    g24: LineSegment StartX=-7.06218 StartY=8.75 StartZ=0 EndX=-7.06218 EndY=5.25 EndZ=0
    g25: LineSegment StartX=-7.06218 StartY=5.25 StartZ=0 EndX=-4.03109 EndY=3.5 EndZ=0
    g26: LineSegment StartX=-4.03109 StartY=3.5 StartZ=0 EndX=-1 EndY=5.25 EndZ=0
    g27: Circle [constr] CenterX=-4.03109 CenterY=7 CenterZ=0 NormalX=0 NormalY=0 NormalZ=1 AngleXU=0 Radius=3.5
    g28: LineSegment StartX=-4.96891 StartY=-1.75 StartZ=0 EndX=-4.96891 EndY=1.75 EndZ=0
    g29: LineSegment StartX=-4.96891 StartY=1.75 StartZ=0 EndX=-8 EndY=3.5 EndZ=0
    g30: LineSegment StartX=-8 StartY=3.5 StartZ=0 EndX=-11.0311 EndY=1.75 EndZ=0
    g31: LineSegment StartX=-11.0311 StartY=1.75 StartZ=0 EndX=-11.0311 EndY=-1.75 EndZ=0
    g32: LineSegment StartX=-11.0311 StartY=-1.75 StartZ=0 EndX=-8 EndY=-3.5 EndZ=0
    g33: LineSegment StartX=-8 StartY=-3.5 StartZ=0 EndX=-4.96891 EndY=-1.75 EndZ=0
    g34: Circle [constr] CenterX=-8 CenterY=0 CenterZ=0 NormalX=0 NormalY=0 NormalZ=1 AngleXU=0 Radius=3.5
    g35: LineSegment StartX=-4.03109 StartY=-3.5 StartZ=0 EndX=-7.06218 EndY=-5.25 EndZ=0
    g36: LineSegment StartX=-7.06218 StartY=-5.25 StartZ=0 EndX=-7.06218 EndY=-8.75 EndZ=0
    g37: LineSegment StartX=-7.06218 StartY=-8.75 StartZ=0 EndX=-4.03109 EndY=-10.5 EndZ=0
    g38: LineSegment StartX=-4.03109 StartY=-10.5 StartZ=0 EndX=-1 EndY=-8.75 EndZ=0
    g39: LineSegment StartX=-1 StartY=-8.75 StartZ=0 EndX=-1 EndY=-5.25 EndZ=0
    g40: LineSegment StartX=-1 StartY=-5.25 StartZ=0 EndX=-4.03109 EndY=-3.5 EndZ=0
    g41: Circle [constr] CenterX=-4.03109 CenterY=-7 CenterZ=0 NormalX=0 NormalY=0 NormalZ=1 AngleXU=0 Radius=3.5
    g42: LineSegment StartX=4.03109 StartY=-3.5 StartZ=0 EndX=1 EndY=-5.25 EndZ=0
    g43: LineSegment StartX=1 StartY=-5.25 StartZ=0 EndX=1 EndY=-8.75 EndZ=0
    g44: LineSegment StartX=1 StartY=-8.75 StartZ=0 EndX=4.03109 EndY=-10.5 EndZ=0
    g45: LineSegment StartX=4.03109 StartY=-10.5 StartZ=0 EndX=7.06218 EndY=-8.75 EndZ=0
    g46: LineSegment StartX=7.06218 StartY=-8.75 StartZ=0 EndX=7.06218 EndY=-5.25 EndZ=0
    g47: LineSegment StartX=7.06218 StartY=-5.25 StartZ=0 EndX=4.03109 EndY=-3.5 EndZ=0
    g48: Circle [constr] CenterX=4.03109 CenterY=-7 CenterZ=0 NormalX=0 NormalY=0 NormalZ=1 AngleXU=0 Radius=3.5
  constraints (117):
    c: Coincident(g0,g1)
    c: Coincident(g1,g2)
    c: Coincident(g2,g3)
    c: Coincident(g3,g4)
    c: Coincident(g4,g5)
    c: Coincident(g5,g0)
    c: Equal(g0, g1-g5) x5
    c: PointOnObject(g0,g6)
    c: PointOnObject(g1,g6)
    c: PointOnObject(g2,g6)
    c: PointOnObject(g3,g6)
    c: PointOnObject(g4,g6)
    c: PointOnObject(g5,g6)
    c: Coincident(g6,g-1)
    c: Diameter(g6) = 7
    c: PointOnObject(g0,g-2)
    c: Coincident(g7,g8)
    c: Coincident(g8,g9)
    c: Coincident(g9,g10)
    c: Coincident(g10,g11)
    c: Coincident(g11,g12)
    c: Coincident(g12,g7)
    c: Equal(g7, g8-g12) x5
    c: PointOnObject(g7,g13)
    c: PointOnObject(g8,g13)
    c: PointOnObject(g9,g13)
    c: PointOnObject(g10,g13)
    c: PointOnObject(g11,g13)
    c: PointOnObject(g12,g13)
    c: PointOnObject(g13,g-1)
    c: Diameter(g13) = 7
    c: Distance(g6,g13) = 8
    c: Horizontal(g0,g10)
    c: Coincident(g14,g15)
    c: Coincident(g15,g16)
    c: Coincident(g16,g17)
    c: Coincident(g17,g18)
    c: Coincident(g18,g19)
    c: Coincident(g19,g14)
    c: Equal(g14, g15-g19) x5
    c: PointOnObject(g14,g20)
    c: PointOnObject(g15,g20)
    c: PointOnObject(g16,g20)
    c: PointOnObject(g17,g20)
    c: PointOnObject(g18,g20)
    c: PointOnObject(g19,g20)
    c: Diameter(g20) = 7
    c: DistanceY(g-1,g20) = 7
    c: Vertical(g18)
    c: Distance(g17,g-2) = 1
    c: Coincident(g21,g22)
    c: Coincident(g22,g23)
    c: Coincident(g23,g24)
    c: Coincident(g24,g25)
    c: Coincident(g25,g26)
    c: Coincident(g26,g21)
    c: Equal(g21, g22-g26) x5
    c: PointOnObject(g21,g27)
    c: PointOnObject(g22,g27)
    c: PointOnObject(g23,g27)
    c: PointOnObject(g24,g27)
    c: PointOnObject(g25,g27)
    c: PointOnObject(g26,g27)
    c: Diameter(g27) = 7
    c: DistanceY(g-1,g27) = 7
    c: DistanceX(g21,g-1) = 1
    c: Vertical(g21)
    c: Coincident(g28,g29)
    c: Coincident(g29,g30)
    c: Coincident(g30,g31)
    c: Coincident(g31,g32)
    c: Coincident(g32,g33)
    c: Coincident(g33,g28)
    c: Equal(g28, g29-g33) x5
    c: PointOnObject(g28,g34)
    c: PointOnObject(g29,g34)
    c: PointOnObject(g30,g34)
    c: PointOnObject(g31,g34)
    c: PointOnObject(g32,g34)
    c: PointOnObject(g33,g34)
    c: PointOnObject(g34,g-1)
    c: Diameter(g34) = 7
    c: Vertical(g31)
    c: DistanceX(g34,g-1) = 8
    c: Coincident(g35,g36)
    c: Coincident(g36,g37)
    c: Coincident(g37,g38)
    c: Coincident(g38,g39)
    c: Coincident(g39,g40)
    c: Coincident(g40,g35)
    c: Equal(g35, g36-g40) x5
    c: PointOnObject(g35,g41)
    c: PointOnObject(g36,g41)
    c: PointOnObject(g37,g41)
    c: PointOnObject(g38,g41)
    c: PointOnObject(g39,g41)
    c: PointOnObject(g40,g41)
    c: Coincident(g42,g43)
    c: Coincident(g43,g44)
    c: Coincident(g44,g45)
    c: Coincident(g45,g46)
    c: Coincident(g46,g47)
    c: Coincident(g47,g42)
    c: Equal(g42, g43-g47) x5
    c: PointOnObject(g42,g48)
    c: PointOnObject(g43,g48)
    c: PointOnObject(g44,g48)
    c: PointOnObject(g45,g48)
    c: PointOnObject(g46,g48)
    c: PointOnObject(g47,g48)
    c: Equal(g41,g48)
    c: Diameter(g41) = 7
    c: Vertical(g39)
    c: Vertical(g43)
    c: Distance(g-2,g39) = 1
    c: Symmetric(g38,g43,g-2)
    c: Distance(g41,g-1) = 7
FEATURE [Part::Extrusion] Extrude625  label="hex227"
  Base = -> Sketch634
  Dir = (0,-1,2e-16)
  DirMode = 2
  FaceMakerClass = Part::FaceMakerBullseye
  FaceMakerMode = 3
  LengthFwd = 10
  LengthRev = 0
  Placement = pos=(12,0,35) rot=(0,0,1;0rad)
  Solid = true
  Symmetric = false
FEATURE [Sketcher::SketchObject] Sketch635
  ArcFitTolerance = 1e-06
  FullyConstrained = true
  MakeInternals = false
  Placement = pos=(0,0,0) rot=(1,0,0;1.5708rad)
  sketch-geometry (49):
    g0: LineSegment StartX=1e-16 StartY=3.5 StartZ=0 EndX=-3.03109 EndY=1.75 EndZ=0
    g1: LineSegment StartX=-3.03109 StartY=1.75 StartZ=0 EndX=-3.03109 EndY=-1.75 EndZ=0
    g2: LineSegment StartX=-3.03109 StartY=-1.75 StartZ=0 EndX=-1e-16 EndY=-3.5 EndZ=0
    g3: LineSegment StartX=-1e-16 StartY=-3.5 StartZ=0 EndX=3.03109 EndY=-1.75 EndZ=0
    g4: LineSegment StartX=3.03109 StartY=-1.75 StartZ=0 EndX=3.03109 EndY=1.75 EndZ=0
    g5: LineSegment StartX=3.03109 StartY=1.75 StartZ=0 EndX=1e-16 EndY=3.5 EndZ=0
    g6: Circle [constr] CenterX=0 CenterY=0 CenterZ=0 NormalX=0 NormalY=0 NormalZ=1 AngleXU=0 Radius=3.5
    g7: LineSegment StartX=4.96892 StartY=-1.75002 StartZ=0 EndX=8.00002 EndY=-3.5 EndZ=0
    g8: LineSegment StartX=8.00002 StartY=-3.5 StartZ=0 EndX=11.0311 EndY=-1.74998 EndZ=0
    g9: LineSegment StartX=11.0311 StartY=-1.74998 StartZ=0 EndX=11.0311 EndY=1.75002 EndZ=0
    g10: LineSegment StartX=11.0311 StartY=1.75002 StartZ=0 EndX=7.99998 EndY=3.5 EndZ=0
    g11: LineSegment StartX=7.99998 StartY=3.5 StartZ=0 EndX=4.9689 EndY=1.74998 EndZ=0
    g12: LineSegment StartX=4.9689 StartY=1.74998 StartZ=0 EndX=4.96892 EndY=-1.75002 EndZ=0
    g13: Circle [constr] CenterX=8 CenterY=0 CenterZ=0 NormalX=0 NormalY=0 NormalZ=1 AngleXU=0 Radius=3.5
    g14: LineSegment StartX=4.03109 StartY=3.5 StartZ=0 EndX=7.06218 EndY=5.25 EndZ=0
    g15: LineSegment StartX=7.06218 StartY=5.25 StartZ=0 EndX=7.06218 EndY=8.75 EndZ=0
    g16: LineSegment StartX=7.06218 StartY=8.75 StartZ=0 EndX=4.03109 EndY=10.5 EndZ=0
    g17: LineSegment StartX=4.03109 StartY=10.5 StartZ=0 EndX=1 EndY=8.75 EndZ=0
    g18: LineSegment StartX=1 StartY=8.75 StartZ=0 EndX=1 EndY=5.25 EndZ=0
    g19: LineSegment StartX=1 StartY=5.25 StartZ=0 EndX=4.03109 EndY=3.5 EndZ=0
    g20: Circle [constr] CenterX=4.03109 CenterY=7 CenterZ=0 NormalX=0 NormalY=0 NormalZ=1 AngleXU=0 Radius=3.5
    g21: LineSegment StartX=-1 StartY=5.25 StartZ=0 EndX=-1 EndY=8.75 EndZ=0
    g22: LineSegment StartX=-1 StartY=8.75 StartZ=0 EndX=-4.03109 EndY=10.5 EndZ=0
    g23: LineSegment StartX=-4.03109 StartY=10.5 StartZ=0 EndX=-7.06218 EndY=8.75 EndZ=0
    g24: LineSegment StartX=-7.06218 StartY=8.75 StartZ=0 EndX=-7.06218 EndY=5.25 EndZ=0
    g25: LineSegment StartX=-7.06218 StartY=5.25 StartZ=0 EndX=-4.03109 EndY=3.5 EndZ=0
    g26: LineSegment StartX=-4.03109 StartY=3.5 StartZ=0 EndX=-1 EndY=5.25 EndZ=0
    g27: Circle [constr] CenterX=-4.03109 CenterY=7 CenterZ=0 NormalX=0 NormalY=0 NormalZ=1 AngleXU=0 Radius=3.5
    g28: LineSegment StartX=-4.96891 StartY=-1.75 StartZ=0 EndX=-4.96891 EndY=1.75 EndZ=0
    g29: LineSegment StartX=-4.96891 StartY=1.75 StartZ=0 EndX=-8 EndY=3.5 EndZ=0
    g30: LineSegment StartX=-8 StartY=3.5 StartZ=0 EndX=-11.0311 EndY=1.75 EndZ=0
    g31: LineSegment StartX=-11.0311 StartY=1.75 StartZ=0 EndX=-11.0311 EndY=-1.75 EndZ=0
    g32: LineSegment StartX=-11.0311 StartY=-1.75 StartZ=0 EndX=-8 EndY=-3.5 EndZ=0
    g33: LineSegment StartX=-8 StartY=-3.5 StartZ=0 EndX=-4.96891 EndY=-1.75 EndZ=0
    g34: Circle [constr] CenterX=-8 CenterY=0 CenterZ=0 NormalX=0 NormalY=0 NormalZ=1 AngleXU=0 Radius=3.5
    g35: LineSegment StartX=-4.03109 StartY=-3.5 StartZ=0 EndX=-7.06218 EndY=-5.25 EndZ=0
    g36: LineSegment StartX=-7.06218 StartY=-5.25 StartZ=0 EndX=-7.06218 EndY=-8.75 EndZ=0
    g37: LineSegment StartX=-7.06218 StartY=-8.75 StartZ=0 EndX=-4.03109 EndY=-10.5 EndZ=0
    g38: LineSegment StartX=-4.03109 StartY=-10.5 StartZ=0 EndX=-1 EndY=-8.75 EndZ=0
    g39: LineSegment StartX=-1 StartY=-8.75 StartZ=0 EndX=-1 EndY=-5.25 EndZ=0
    g40: LineSegment StartX=-1 StartY=-5.25 StartZ=0 EndX=-4.03109 EndY=-3.5 EndZ=0
    g41: Circle [constr] CenterX=-4.03109 CenterY=-7 CenterZ=0 NormalX=0 NormalY=0 NormalZ=1 AngleXU=0 Radius=3.5
    g42: LineSegment StartX=4.03109 StartY=-3.5 StartZ=0 EndX=1 EndY=-5.25 EndZ=0
    g43: LineSegment StartX=1 StartY=-5.25 StartZ=0 EndX=1 EndY=-8.75 EndZ=0
    g44: LineSegment StartX=1 StartY=-8.75 StartZ=0 EndX=4.03109 EndY=-10.5 EndZ=0
    g45: LineSegment StartX=4.03109 StartY=-10.5 StartZ=0 EndX=7.06218 EndY=-8.75 EndZ=0
    g46: LineSegment StartX=7.06218 StartY=-8.75 StartZ=0 EndX=7.06218 EndY=-5.25 EndZ=0
    g47: LineSegment StartX=7.06218 StartY=-5.25 StartZ=0 EndX=4.03109 EndY=-3.5 EndZ=0
    g48: Circle [constr] CenterX=4.03109 CenterY=-7 CenterZ=0 NormalX=0 NormalY=0 NormalZ=1 AngleXU=0 Radius=3.5
  constraints (117):
    c: Coincident(g0,g1)
    c: Coincident(g1,g2)
    c: Coincident(g2,g3)
    c: Coincident(g3,g4)
    c: Coincident(g4,g5)
    c: Coincident(g5,g0)
    c: Equal(g0, g1-g5) x5
    c: PointOnObject(g0,g6)
    c: PointOnObject(g1,g6)
    c: PointOnObject(g2,g6)
    c: PointOnObject(g3,g6)
    c: PointOnObject(g4,g6)
    c: PointOnObject(g5,g6)
    c: Coincident(g6,g-1)
    c: Diameter(g6) = 7
    c: PointOnObject(g0,g-2)
    c: Coincident(g7,g8)
    c: Coincident(g8,g9)
    c: Coincident(g9,g10)
    c: Coincident(g10,g11)
    c: Coincident(g11,g12)
    c: Coincident(g12,g7)
    c: Equal(g7, g8-g12) x5
    c: PointOnObject(g7,g13)
    c: PointOnObject(g8,g13)
    c: PointOnObject(g9,g13)
    c: PointOnObject(g10,g13)
    c: PointOnObject(g11,g13)
    c: PointOnObject(g12,g13)
    c: PointOnObject(g13,g-1)
    c: Diameter(g13) = 7
    c: Distance(g6,g13) = 8
    c: Horizontal(g0,g10)
    c: Coincident(g14,g15)
    c: Coincident(g15,g16)
    c: Coincident(g16,g17)
    c: Coincident(g17,g18)
    c: Coincident(g18,g19)
    c: Coincident(g19,g14)
    c: Equal(g14, g15-g19) x5
    c: PointOnObject(g14,g20)
    c: PointOnObject(g15,g20)
    c: PointOnObject(g16,g20)
    c: PointOnObject(g17,g20)
    c: PointOnObject(g18,g20)
    c: PointOnObject(g19,g20)
    c: Diameter(g20) = 7
    c: DistanceY(g-1,g20) = 7
    c: Vertical(g18)
    c: Distance(g17,g-2) = 1
    c: Coincident(g21,g22)
    c: Coincident(g22,g23)
    c: Coincident(g23,g24)
    c: Coincident(g24,g25)
    c: Coincident(g25,g26)
    c: Coincident(g26,g21)
    c: Equal(g21, g22-g26) x5
    c: PointOnObject(g21,g27)
    c: PointOnObject(g22,g27)
    c: PointOnObject(g23,g27)
    c: PointOnObject(g24,g27)
    c: PointOnObject(g25,g27)
    c: PointOnObject(g26,g27)
    c: Diameter(g27) = 7
    c: DistanceY(g-1,g27) = 7
    c: DistanceX(g21,g-1) = 1
    c: Vertical(g21)
    c: Coincident(g28,g29)
    c: Coincident(g29,g30)
    c: Coincident(g30,g31)
    c: Coincident(g31,g32)
    c: Coincident(g32,g33)
    c: Coincident(g33,g28)
    c: Equal(g28, g29-g33) x5
    c: PointOnObject(g28,g34)
    c: PointOnObject(g29,g34)
    c: PointOnObject(g30,g34)
    c: PointOnObject(g31,g34)
    c: PointOnObject(g32,g34)
    c: PointOnObject(g33,g34)
    c: PointOnObject(g34,g-1)
    c: Diameter(g34) = 7
    c: Vertical(g31)
    c: DistanceX(g34,g-1) = 8
    c: Coincident(g35,g36)
    c: Coincident(g36,g37)
    c: Coincident(g37,g38)
    c: Coincident(g38,g39)
    c: Coincident(g39,g40)
    c: Coincident(g40,g35)
    c: Equal(g35, g36-g40) x5
    c: PointOnObject(g35,g41)
    c: PointOnObject(g36,g41)
    c: PointOnObject(g37,g41)
    c: PointOnObject(g38,g41)
    c: PointOnObject(g39,g41)
    c: PointOnObject(g40,g41)
    c: Coincident(g42,g43)
    c: Coincident(g43,g44)
    c: Coincident(g44,g45)
    c: Coincident(g45,g46)
    c: Coincident(g46,g47)
    c: Coincident(g47,g42)
    c: Equal(g42, g43-g47) x5
    c: PointOnObject(g42,g48)
    c: PointOnObject(g43,g48)
    c: PointOnObject(g44,g48)
    c: PointOnObject(g45,g48)
    c: PointOnObject(g46,g48)
    c: PointOnObject(g47,g48)
    c: Equal(g41,g48)
    c: Diameter(g41) = 7
    c: Vertical(g39)
    c: Vertical(g43)
    c: Distance(g-2,g39) = 1
    c: Symmetric(g38,g43,g-2)
    c: Distance(g41,g-1) = 7
FEATURE [Part::Extrusion] Extrude626  label="hex228"
  Base = -> Sketch635
  Dir = (0,-1,2e-16)
  DirMode = 2
  FaceMakerClass = Part::FaceMakerBullseye
  FaceMakerMode = 3
  LengthFwd = 10
  LengthRev = 0
  Placement = pos=(-36,0,7) rot=(0,0,1;0rad)
  Solid = true
  Symmetric = false
FEATURE [Sketcher::SketchObject] Sketch636
  ArcFitTolerance = 1e-06
  FullyConstrained = true
  MakeInternals = false
  Placement = pos=(0,0,0) rot=(1,0,0;1.5708rad)
  sketch-geometry (49):
    g0: LineSegment StartX=1e-16 StartY=3.5 StartZ=0 EndX=-3.03109 EndY=1.75 EndZ=0
    g1: LineSegment StartX=-3.03109 StartY=1.75 StartZ=0 EndX=-3.03109 EndY=-1.75 EndZ=0
    g2: LineSegment StartX=-3.03109 StartY=-1.75 StartZ=0 EndX=-1e-16 EndY=-3.5 EndZ=0
    g3: LineSegment StartX=-1e-16 StartY=-3.5 StartZ=0 EndX=3.03109 EndY=-1.75 EndZ=0
    g4: LineSegment StartX=3.03109 StartY=-1.75 StartZ=0 EndX=3.03109 EndY=1.75 EndZ=0
    g5: LineSegment StartX=3.03109 StartY=1.75 StartZ=0 EndX=1e-16 EndY=3.5 EndZ=0
    g6: Circle [constr] CenterX=0 CenterY=0 CenterZ=0 NormalX=0 NormalY=0 NormalZ=1 AngleXU=0 Radius=3.5
    g7: LineSegment StartX=4.96892 StartY=-1.75002 StartZ=0 EndX=8.00002 EndY=-3.5 EndZ=0
    g8: LineSegment StartX=8.00002 StartY=-3.5 StartZ=0 EndX=11.0311 EndY=-1.74998 EndZ=0
    g9: LineSegment StartX=11.0311 StartY=-1.74998 StartZ=0 EndX=11.0311 EndY=1.75002 EndZ=0
    g10: LineSegment StartX=11.0311 StartY=1.75002 StartZ=0 EndX=7.99998 EndY=3.5 EndZ=0
    g11: LineSegment StartX=7.99998 StartY=3.5 StartZ=0 EndX=4.9689 EndY=1.74998 EndZ=0
    g12: LineSegment StartX=4.9689 StartY=1.74998 StartZ=0 EndX=4.96892 EndY=-1.75002 EndZ=0
    g13: Circle [constr] CenterX=8 CenterY=0 CenterZ=0 NormalX=0 NormalY=0 NormalZ=1 AngleXU=0 Radius=3.5
    g14: LineSegment StartX=4.03109 StartY=3.5 StartZ=0 EndX=7.06218 EndY=5.25 EndZ=0
    g15: LineSegment StartX=7.06218 StartY=5.25 StartZ=0 EndX=7.06218 EndY=8.75 EndZ=0
    g16: LineSegment StartX=7.06218 StartY=8.75 StartZ=0 EndX=4.03109 EndY=10.5 EndZ=0
    g17: LineSegment StartX=4.03109 StartY=10.5 StartZ=0 EndX=1 EndY=8.75 EndZ=0
    g18: LineSegment StartX=1 StartY=8.75 StartZ=0 EndX=1 EndY=5.25 EndZ=0
    g19: LineSegment StartX=1 StartY=5.25 StartZ=0 EndX=4.03109 EndY=3.5 EndZ=0
    g20: Circle [constr] CenterX=4.03109 CenterY=7 CenterZ=0 NormalX=0 NormalY=0 NormalZ=1 AngleXU=0 Radius=3.5
    g21: LineSegment StartX=-1 StartY=5.25 StartZ=0 EndX=-1 EndY=8.75 EndZ=0
    g22: LineSegment StartX=-1 StartY=8.75 StartZ=0 EndX=-4.03109 EndY=10.5 EndZ=0
    g23: LineSegment StartX=-4.03109 StartY=10.5 StartZ=0 EndX=-7.06218 EndY=8.75 EndZ=0
    g24: LineSegment StartX=-7.06218 StartY=8.75 StartZ=0 EndX=-7.06218 EndY=5.25 EndZ=0
    g25: LineSegment StartX=-7.06218 StartY=5.25 StartZ=0 EndX=-4.03109 EndY=3.5 EndZ=0
    g26: LineSegment StartX=-4.03109 StartY=3.5 StartZ=0 EndX=-1 EndY=5.25 EndZ=0
    g27: Circle [constr] CenterX=-4.03109 CenterY=7 CenterZ=0 NormalX=0 NormalY=0 NormalZ=1 AngleXU=0 Radius=3.5
    g28: LineSegment StartX=-4.96891 StartY=-1.75 StartZ=0 EndX=-4.96891 EndY=1.75 EndZ=0
    g29: LineSegment StartX=-4.96891 StartY=1.75 StartZ=0 EndX=-8 EndY=3.5 EndZ=0
    g30: LineSegment StartX=-8 StartY=3.5 StartZ=0 EndX=-11.0311 EndY=1.75 EndZ=0
    g31: LineSegment StartX=-11.0311 StartY=1.75 StartZ=0 EndX=-11.0311 EndY=-1.75 EndZ=0
    g32: LineSegment StartX=-11.0311 StartY=-1.75 StartZ=0 EndX=-8 EndY=-3.5 EndZ=0
    g33: LineSegment StartX=-8 StartY=-3.5 StartZ=0 EndX=-4.96891 EndY=-1.75 EndZ=0
    g34: Circle [constr] CenterX=-8 CenterY=0 CenterZ=0 NormalX=0 NormalY=0 NormalZ=1 AngleXU=0 Radius=3.5
    g35: LineSegment StartX=-4.03109 StartY=-3.5 StartZ=0 EndX=-7.06218 EndY=-5.25 EndZ=0
    g36: LineSegment StartX=-7.06218 StartY=-5.25 StartZ=0 EndX=-7.06218 EndY=-8.75 EndZ=0
    g37: LineSegment StartX=-7.06218 StartY=-8.75 StartZ=0 EndX=-4.03109 EndY=-10.5 EndZ=0
    g38: LineSegment StartX=-4.03109 StartY=-10.5 StartZ=0 EndX=-1 EndY=-8.75 EndZ=0
    g39: LineSegment StartX=-1 StartY=-8.75 StartZ=0 EndX=-1 EndY=-5.25 EndZ=0
    g40: LineSegment StartX=-1 StartY=-5.25 StartZ=0 EndX=-4.03109 EndY=-3.5 EndZ=0
    g41: Circle [constr] CenterX=-4.03109 CenterY=-7 CenterZ=0 NormalX=0 NormalY=0 NormalZ=1 AngleXU=0 Radius=3.5
    g42: LineSegment StartX=4.03109 StartY=-3.5 StartZ=0 EndX=1 EndY=-5.25 EndZ=0
    g43: LineSegment StartX=1 StartY=-5.25 StartZ=0 EndX=1 EndY=-8.75 EndZ=0
    g44: LineSegment StartX=1 StartY=-8.75 StartZ=0 EndX=4.03109 EndY=-10.5 EndZ=0
    g45: LineSegment StartX=4.03109 StartY=-10.5 StartZ=0 EndX=7.06218 EndY=-8.75 EndZ=0
    g46: LineSegment StartX=7.06218 StartY=-8.75 StartZ=0 EndX=7.06218 EndY=-5.25 EndZ=0
    g47: LineSegment StartX=7.06218 StartY=-5.25 StartZ=0 EndX=4.03109 EndY=-3.5 EndZ=0
    g48: Circle [constr] CenterX=4.03109 CenterY=-7 CenterZ=0 NormalX=0 NormalY=0 NormalZ=1 AngleXU=0 Radius=3.5
  constraints (117):
    c: Coincident(g0,g1)
    c: Coincident(g1,g2)
    c: Coincident(g2,g3)
    c: Coincident(g3,g4)
    c: Coincident(g4,g5)
    c: Coincident(g5,g0)
    c: Equal(g0, g1-g5) x5
    c: PointOnObject(g0,g6)
    c: PointOnObject(g1,g6)
    c: PointOnObject(g2,g6)
    c: PointOnObject(g3,g6)
    c: PointOnObject(g4,g6)
    c: PointOnObject(g5,g6)
    c: Coincident(g6,g-1)
    c: Diameter(g6) = 7
    c: PointOnObject(g0,g-2)
    c: Coincident(g7,g8)
    c: Coincident(g8,g9)
    c: Coincident(g9,g10)
    c: Coincident(g10,g11)
    c: Coincident(g11,g12)
    c: Coincident(g12,g7)
    c: Equal(g7, g8-g12) x5
    c: PointOnObject(g7,g13)
    c: PointOnObject(g8,g13)
    c: PointOnObject(g9,g13)
    c: PointOnObject(g10,g13)
    c: PointOnObject(g11,g13)
    c: PointOnObject(g12,g13)
    c: PointOnObject(g13,g-1)
    c: Diameter(g13) = 7
    c: Distance(g6,g13) = 8
    c: Horizontal(g0,g10)
    c: Coincident(g14,g15)
    c: Coincident(g15,g16)
    c: Coincident(g16,g17)
    c: Coincident(g17,g18)
    c: Coincident(g18,g19)
    c: Coincident(g19,g14)
    c: Equal(g14, g15-g19) x5
    c: PointOnObject(g14,g20)
    c: PointOnObject(g15,g20)
    c: PointOnObject(g16,g20)
    c: PointOnObject(g17,g20)
    c: PointOnObject(g18,g20)
    c: PointOnObject(g19,g20)
    c: Diameter(g20) = 7
    c: DistanceY(g-1,g20) = 7
    c: Vertical(g18)
    c: Distance(g17,g-2) = 1
    c: Coincident(g21,g22)
    c: Coincident(g22,g23)
    c: Coincident(g23,g24)
    c: Coincident(g24,g25)
    c: Coincident(g25,g26)
    c: Coincident(g26,g21)
    c: Equal(g21, g22-g26) x5
    c: PointOnObject(g21,g27)
    c: PointOnObject(g22,g27)
    c: PointOnObject(g23,g27)
    c: PointOnObject(g24,g27)
    c: PointOnObject(g25,g27)
    c: PointOnObject(g26,g27)
    c: Diameter(g27) = 7
    c: DistanceY(g-1,g27) = 7
    c: DistanceX(g21,g-1) = 1
    c: Vertical(g21)
    c: Coincident(g28,g29)
    c: Coincident(g29,g30)
    c: Coincident(g30,g31)
    c: Coincident(g31,g32)
    c: Coincident(g32,g33)
    c: Coincident(g33,g28)
    c: Equal(g28, g29-g33) x5
    c: PointOnObject(g28,g34)
    c: PointOnObject(g29,g34)
    c: PointOnObject(g30,g34)
    c: PointOnObject(g31,g34)
    c: PointOnObject(g32,g34)
    c: PointOnObject(g33,g34)
    c: PointOnObject(g34,g-1)
    c: Diameter(g34) = 7
    c: Vertical(g31)
    c: DistanceX(g34,g-1) = 8
    c: Coincident(g35,g36)
    c: Coincident(g36,g37)
    c: Coincident(g37,g38)
    c: Coincident(g38,g39)
    c: Coincident(g39,g40)
    c: Coincident(g40,g35)
    c: Equal(g35, g36-g40) x5
    c: PointOnObject(g35,g41)
    c: PointOnObject(g36,g41)
    c: PointOnObject(g37,g41)
    c: PointOnObject(g38,g41)
    c: PointOnObject(g39,g41)
    c: PointOnObject(g40,g41)
    c: Coincident(g42,g43)
    c: Coincident(g43,g44)
    c: Coincident(g44,g45)
    c: Coincident(g45,g46)
    c: Coincident(g46,g47)
    c: Coincident(g47,g42)
    c: Equal(g42, g43-g47) x5
    c: PointOnObject(g42,g48)
    c: PointOnObject(g43,g48)
    c: PointOnObject(g44,g48)
    c: PointOnObject(g45,g48)
    c: PointOnObject(g46,g48)
    c: PointOnObject(g47,g48)
    c: Equal(g41,g48)
    c: Diameter(g41) = 7
    c: Vertical(g39)
    c: Vertical(g43)
    c: Distance(g-2,g39) = 1
    c: Symmetric(g38,g43,g-2)
    c: Distance(g41,g-1) = 7
FEATURE [Part::Extrusion] Extrude627  label="hex229"
  Base = -> Sketch636
  Dir = (0,-1,2e-16)
  DirMode = 2
  FaceMakerClass = Part::FaceMakerBullseye
  FaceMakerMode = 3
  LengthFwd = 10
  LengthRev = 0
  Placement = pos=(36,0,7) rot=(0,0,1;0rad)
  Solid = true
  Symmetric = false
FEATURE [Sketcher::SketchObject] Sketch637
  ArcFitTolerance = 1e-06
  FullyConstrained = true
  MakeInternals = false
  Placement = pos=(0,0,0) rot=(1,0,0;1.5708rad)
  sketch-geometry (49):
    g0: LineSegment StartX=1e-16 StartY=3.5 StartZ=0 EndX=-3.03109 EndY=1.75 EndZ=0
    g1: LineSegment StartX=-3.03109 StartY=1.75 StartZ=0 EndX=-3.03109 EndY=-1.75 EndZ=0
    g2: LineSegment StartX=-3.03109 StartY=-1.75 StartZ=0 EndX=-1e-16 EndY=-3.5 EndZ=0
    g3: LineSegment StartX=-1e-16 StartY=-3.5 StartZ=0 EndX=3.03109 EndY=-1.75 EndZ=0
    g4: LineSegment StartX=3.03109 StartY=-1.75 StartZ=0 EndX=3.03109 EndY=1.75 EndZ=0
    g5: LineSegment StartX=3.03109 StartY=1.75 StartZ=0 EndX=1e-16 EndY=3.5 EndZ=0
    g6: Circle [constr] CenterX=0 CenterY=0 CenterZ=0 NormalX=0 NormalY=0 NormalZ=1 AngleXU=0 Radius=3.5
    g7: LineSegment StartX=4.96892 StartY=-1.75002 StartZ=0 EndX=8.00002 EndY=-3.5 EndZ=0
    g8: LineSegment StartX=8.00002 StartY=-3.5 StartZ=0 EndX=11.0311 EndY=-1.74998 EndZ=0
    g9: LineSegment StartX=11.0311 StartY=-1.74998 StartZ=0 EndX=11.0311 EndY=1.75002 EndZ=0
    g10: LineSegment StartX=11.0311 StartY=1.75002 StartZ=0 EndX=7.99998 EndY=3.5 EndZ=0
    g11: LineSegment StartX=7.99998 StartY=3.5 StartZ=0 EndX=4.9689 EndY=1.74998 EndZ=0
    g12: LineSegment StartX=4.9689 StartY=1.74998 StartZ=0 EndX=4.96892 EndY=-1.75002 EndZ=0
    g13: Circle [constr] CenterX=8 CenterY=0 CenterZ=0 NormalX=0 NormalY=0 NormalZ=1 AngleXU=0 Radius=3.5
    g14: LineSegment StartX=4.03109 StartY=3.5 StartZ=0 EndX=7.06218 EndY=5.25 EndZ=0
    g15: LineSegment StartX=7.06218 StartY=5.25 StartZ=0 EndX=7.06218 EndY=8.75 EndZ=0
    g16: LineSegment StartX=7.06218 StartY=8.75 StartZ=0 EndX=4.03109 EndY=10.5 EndZ=0
    g17: LineSegment StartX=4.03109 StartY=10.5 StartZ=0 EndX=1 EndY=8.75 EndZ=0
    g18: LineSegment StartX=1 StartY=8.75 StartZ=0 EndX=1 EndY=5.25 EndZ=0
    g19: LineSegment StartX=1 StartY=5.25 StartZ=0 EndX=4.03109 EndY=3.5 EndZ=0
    g20: Circle [constr] CenterX=4.03109 CenterY=7 CenterZ=0 NormalX=0 NormalY=0 NormalZ=1 AngleXU=0 Radius=3.5
    g21: LineSegment StartX=-1 StartY=5.25 StartZ=0 EndX=-1 EndY=8.75 EndZ=0
    g22: LineSegment StartX=-1 StartY=8.75 StartZ=0 EndX=-4.03109 EndY=10.5 EndZ=0
    g23: LineSegment StartX=-4.03109 StartY=10.5 StartZ=0 EndX=-7.06218 EndY=8.75 EndZ=0
    g24: LineSegment StartX=-7.06218 StartY=8.75 StartZ=0 EndX=-7.06218 EndY=5.25 EndZ=0
    g25: LineSegment StartX=-7.06218 StartY=5.25 StartZ=0 EndX=-4.03109 EndY=3.5 EndZ=0
    g26: LineSegment StartX=-4.03109 StartY=3.5 StartZ=0 EndX=-1 EndY=5.25 EndZ=0
    g27: Circle [constr] CenterX=-4.03109 CenterY=7 CenterZ=0 NormalX=0 NormalY=0 NormalZ=1 AngleXU=0 Radius=3.5
    g28: LineSegment StartX=-4.96891 StartY=-1.75 StartZ=0 EndX=-4.96891 EndY=1.75 EndZ=0
    g29: LineSegment StartX=-4.96891 StartY=1.75 StartZ=0 EndX=-8 EndY=3.5 EndZ=0
    g30: LineSegment StartX=-8 StartY=3.5 StartZ=0 EndX=-11.0311 EndY=1.75 EndZ=0
    g31: LineSegment StartX=-11.0311 StartY=1.75 StartZ=0 EndX=-11.0311 EndY=-1.75 EndZ=0
    g32: LineSegment StartX=-11.0311 StartY=-1.75 StartZ=0 EndX=-8 EndY=-3.5 EndZ=0
    g33: LineSegment StartX=-8 StartY=-3.5 StartZ=0 EndX=-4.96891 EndY=-1.75 EndZ=0
    g34: Circle [constr] CenterX=-8 CenterY=0 CenterZ=0 NormalX=0 NormalY=0 NormalZ=1 AngleXU=0 Radius=3.5
    g35: LineSegment StartX=-4.03109 StartY=-3.5 StartZ=0 EndX=-7.06218 EndY=-5.25 EndZ=0
    g36: LineSegment StartX=-7.06218 StartY=-5.25 StartZ=0 EndX=-7.06218 EndY=-8.75 EndZ=0
    g37: LineSegment StartX=-7.06218 StartY=-8.75 StartZ=0 EndX=-4.03109 EndY=-10.5 EndZ=0
    g38: LineSegment StartX=-4.03109 StartY=-10.5 StartZ=0 EndX=-1 EndY=-8.75 EndZ=0
    g39: LineSegment StartX=-1 StartY=-8.75 StartZ=0 EndX=-1 EndY=-5.25 EndZ=0
    g40: LineSegment StartX=-1 StartY=-5.25 StartZ=0 EndX=-4.03109 EndY=-3.5 EndZ=0
    g41: Circle [constr] CenterX=-4.03109 CenterY=-7 CenterZ=0 NormalX=0 NormalY=0 NormalZ=1 AngleXU=0 Radius=3.5
    g42: LineSegment StartX=4.03109 StartY=-3.5 StartZ=0 EndX=1 EndY=-5.25 EndZ=0
    g43: LineSegment StartX=1 StartY=-5.25 StartZ=0 EndX=1 EndY=-8.75 EndZ=0
    g44: LineSegment StartX=1 StartY=-8.75 StartZ=0 EndX=4.03109 EndY=-10.5 EndZ=0
    g45: LineSegment StartX=4.03109 StartY=-10.5 StartZ=0 EndX=7.06218 EndY=-8.75 EndZ=0
    g46: LineSegment StartX=7.06218 StartY=-8.75 StartZ=0 EndX=7.06218 EndY=-5.25 EndZ=0
    g47: LineSegment StartX=7.06218 StartY=-5.25 StartZ=0 EndX=4.03109 EndY=-3.5 EndZ=0
    g48: Circle [constr] CenterX=4.03109 CenterY=-7 CenterZ=0 NormalX=0 NormalY=0 NormalZ=1 AngleXU=0 Radius=3.5
  constraints (117):
    c: Coincident(g0,g1)
    c: Coincident(g1,g2)
    c: Coincident(g2,g3)
    c: Coincident(g3,g4)
    c: Coincident(g4,g5)
    c: Coincident(g5,g0)
    c: Equal(g0, g1-g5) x5
    c: PointOnObject(g0,g6)
    c: PointOnObject(g1,g6)
    c: PointOnObject(g2,g6)
    c: PointOnObject(g3,g6)
    c: PointOnObject(g4,g6)
    c: PointOnObject(g5,g6)
    c: Coincident(g6,g-1)
    c: Diameter(g6) = 7
    c: PointOnObject(g0,g-2)
    c: Coincident(g7,g8)
    c: Coincident(g8,g9)
    c: Coincident(g9,g10)
    c: Coincident(g10,g11)
    c: Coincident(g11,g12)
    c: Coincident(g12,g7)
    c: Equal(g7, g8-g12) x5
    c: PointOnObject(g7,g13)
    c: PointOnObject(g8,g13)
    c: PointOnObject(g9,g13)
    c: PointOnObject(g10,g13)
    c: PointOnObject(g11,g13)
    c: PointOnObject(g12,g13)
    c: PointOnObject(g13,g-1)
    c: Diameter(g13) = 7
    c: Distance(g6,g13) = 8
    c: Horizontal(g0,g10)
    c: Coincident(g14,g15)
    c: Coincident(g15,g16)
    c: Coincident(g16,g17)
    c: Coincident(g17,g18)
    c: Coincident(g18,g19)
    c: Coincident(g19,g14)
    c: Equal(g14, g15-g19) x5
    c: PointOnObject(g14,g20)
    c: PointOnObject(g15,g20)
    c: PointOnObject(g16,g20)
    c: PointOnObject(g17,g20)
    c: PointOnObject(g18,g20)
    c: PointOnObject(g19,g20)
    c: Diameter(g20) = 7
    c: DistanceY(g-1,g20) = 7
    c: Vertical(g18)
    c: Distance(g17,g-2) = 1
    c: Coincident(g21,g22)
    c: Coincident(g22,g23)
    c: Coincident(g23,g24)
    c: Coincident(g24,g25)
    c: Coincident(g25,g26)
    c: Coincident(g26,g21)
    c: Equal(g21, g22-g26) x5
    c: PointOnObject(g21,g27)
    c: PointOnObject(g22,g27)
    c: PointOnObject(g23,g27)
    c: PointOnObject(g24,g27)
    c: PointOnObject(g25,g27)
    c: PointOnObject(g26,g27)
    c: Diameter(g27) = 7
    c: DistanceY(g-1,g27) = 7
    c: DistanceX(g21,g-1) = 1
    c: Vertical(g21)
    c: Coincident(g28,g29)
    c: Coincident(g29,g30)
    c: Coincident(g30,g31)
    c: Coincident(g31,g32)
    c: Coincident(g32,g33)
    c: Coincident(g33,g28)
    c: Equal(g28, g29-g33) x5
    c: PointOnObject(g28,g34)
    c: PointOnObject(g29,g34)
    c: PointOnObject(g30,g34)
    c: PointOnObject(g31,g34)
    c: PointOnObject(g32,g34)
    c: PointOnObject(g33,g34)
    c: PointOnObject(g34,g-1)
    c: Diameter(g34) = 7
    c: Vertical(g31)
    c: DistanceX(g34,g-1) = 8
    c: Coincident(g35,g36)
    c: Coincident(g36,g37)
    c: Coincident(g37,g38)
    c: Coincident(g38,g39)
    c: Coincident(g39,g40)
    c: Coincident(g40,g35)
    c: Equal(g35, g36-g40) x5
    c: PointOnObject(g35,g41)
    c: PointOnObject(g36,g41)
    c: PointOnObject(g37,g41)
    c: PointOnObject(g38,g41)
    c: PointOnObject(g39,g41)
    c: PointOnObject(g40,g41)
    c: Coincident(g42,g43)
    c: Coincident(g43,g44)
    c: Coincident(g44,g45)
    c: Coincident(g45,g46)
    c: Coincident(g46,g47)
    c: Coincident(g47,g42)
    c: Equal(g42, g43-g47) x5
    c: PointOnObject(g42,g48)
    c: PointOnObject(g43,g48)
    c: PointOnObject(g44,g48)
    c: PointOnObject(g45,g48)
    c: PointOnObject(g46,g48)
    c: PointOnObject(g47,g48)
    c: Equal(g41,g48)
    c: Diameter(g41) = 7
    c: Vertical(g39)
    c: Vertical(g43)
    c: Distance(g-2,g39) = 1
    c: Symmetric(g38,g43,g-2)
    c: Distance(g41,g-1) = 7
FEATURE [Part::Extrusion] Extrude628  label="hex230"
  Base = -> Sketch637
  Dir = (0,-1,2e-16)
  DirMode = 2
  FaceMakerClass = Part::FaceMakerBullseye
  FaceMakerMode = 3
  LengthFwd = 10
  LengthRev = 0
  Placement = pos=(32,0,28) rot=(0,0,1;0rad)
  Solid = true
  Symmetric = false
FEATURE [Sketcher::SketchObject] Sketch638
  ArcFitTolerance = 1e-06
  FullyConstrained = true
  MakeInternals = false
  Placement = pos=(0,0,0) rot=(1,0,0;1.5708rad)
  sketch-geometry (49):
    g0: LineSegment StartX=1e-16 StartY=3.5 StartZ=0 EndX=-3.03109 EndY=1.75 EndZ=0
    g1: LineSegment StartX=-3.03109 StartY=1.75 StartZ=0 EndX=-3.03109 EndY=-1.75 EndZ=0
    g2: LineSegment StartX=-3.03109 StartY=-1.75 StartZ=0 EndX=-1e-16 EndY=-3.5 EndZ=0
    g3: LineSegment StartX=-1e-16 StartY=-3.5 StartZ=0 EndX=3.03109 EndY=-1.75 EndZ=0
    g4: LineSegment StartX=3.03109 StartY=-1.75 StartZ=0 EndX=3.03109 EndY=1.75 EndZ=0
    g5: LineSegment StartX=3.03109 StartY=1.75 StartZ=0 EndX=1e-16 EndY=3.5 EndZ=0
    g6: Circle [constr] CenterX=0 CenterY=0 CenterZ=0 NormalX=0 NormalY=0 NormalZ=1 AngleXU=0 Radius=3.5
    g7: LineSegment StartX=4.96892 StartY=-1.75002 StartZ=0 EndX=8.00002 EndY=-3.5 EndZ=0
    g8: LineSegment StartX=8.00002 StartY=-3.5 StartZ=0 EndX=11.0311 EndY=-1.74998 EndZ=0
    g9: LineSegment StartX=11.0311 StartY=-1.74998 StartZ=0 EndX=11.0311 EndY=1.75002 EndZ=0
    g10: LineSegment StartX=11.0311 StartY=1.75002 StartZ=0 EndX=7.99998 EndY=3.5 EndZ=0
    g11: LineSegment StartX=7.99998 StartY=3.5 StartZ=0 EndX=4.9689 EndY=1.74998 EndZ=0
    g12: LineSegment StartX=4.9689 StartY=1.74998 StartZ=0 EndX=4.96892 EndY=-1.75002 EndZ=0
    g13: Circle [constr] CenterX=8 CenterY=0 CenterZ=0 NormalX=0 NormalY=0 NormalZ=1 AngleXU=0 Radius=3.5
    g14: LineSegment StartX=4.03109 StartY=3.5 StartZ=0 EndX=7.06218 EndY=5.25 EndZ=0
    g15: LineSegment StartX=7.06218 StartY=5.25 StartZ=0 EndX=7.06218 EndY=8.75 EndZ=0
    g16: LineSegment StartX=7.06218 StartY=8.75 StartZ=0 EndX=4.03109 EndY=10.5 EndZ=0
    g17: LineSegment StartX=4.03109 StartY=10.5 StartZ=0 EndX=1 EndY=8.75 EndZ=0
    g18: LineSegment StartX=1 StartY=8.75 StartZ=0 EndX=1 EndY=5.25 EndZ=0
    g19: LineSegment StartX=1 StartY=5.25 StartZ=0 EndX=4.03109 EndY=3.5 EndZ=0
    g20: Circle [constr] CenterX=4.03109 CenterY=7 CenterZ=0 NormalX=0 NormalY=0 NormalZ=1 AngleXU=0 Radius=3.5
    g21: LineSegment StartX=-1 StartY=5.25 StartZ=0 EndX=-1 EndY=8.75 EndZ=0
    g22: LineSegment StartX=-1 StartY=8.75 StartZ=0 EndX=-4.03109 EndY=10.5 EndZ=0
    g23: LineSegment StartX=-4.03109 StartY=10.5 StartZ=0 EndX=-7.06218 EndY=8.75 EndZ=0
    g24: LineSegment StartX=-7.06218 StartY=8.75 StartZ=0 EndX=-7.06218 EndY=5.25 EndZ=0
    g25: LineSegment StartX=-7.06218 StartY=5.25 StartZ=0 EndX=-4.03109 EndY=3.5 EndZ=0
    g26: LineSegment StartX=-4.03109 StartY=3.5 StartZ=0 EndX=-1 EndY=5.25 EndZ=0
    g27: Circle [constr] CenterX=-4.03109 CenterY=7 CenterZ=0 NormalX=0 NormalY=0 NormalZ=1 AngleXU=0 Radius=3.5
    g28: LineSegment StartX=-4.96891 StartY=-1.75 StartZ=0 EndX=-4.96891 EndY=1.75 EndZ=0
    g29: LineSegment StartX=-4.96891 StartY=1.75 StartZ=0 EndX=-8 EndY=3.5 EndZ=0
    g30: LineSegment StartX=-8 StartY=3.5 StartZ=0 EndX=-11.0311 EndY=1.75 EndZ=0
    g31: LineSegment StartX=-11.0311 StartY=1.75 StartZ=0 EndX=-11.0311 EndY=-1.75 EndZ=0
    g32: LineSegment StartX=-11.0311 StartY=-1.75 StartZ=0 EndX=-8 EndY=-3.5 EndZ=0
    g33: LineSegment StartX=-8 StartY=-3.5 StartZ=0 EndX=-4.96891 EndY=-1.75 EndZ=0
    g34: Circle [constr] CenterX=-8 CenterY=0 CenterZ=0 NormalX=0 NormalY=0 NormalZ=1 AngleXU=0 Radius=3.5
    g35: LineSegment StartX=-4.03109 StartY=-3.5 StartZ=0 EndX=-7.06218 EndY=-5.25 EndZ=0
    g36: LineSegment StartX=-7.06218 StartY=-5.25 StartZ=0 EndX=-7.06218 EndY=-8.75 EndZ=0
    g37: LineSegment StartX=-7.06218 StartY=-8.75 StartZ=0 EndX=-4.03109 EndY=-10.5 EndZ=0
    g38: LineSegment StartX=-4.03109 StartY=-10.5 StartZ=0 EndX=-1 EndY=-8.75 EndZ=0
    g39: LineSegment StartX=-1 StartY=-8.75 StartZ=0 EndX=-1 EndY=-5.25 EndZ=0
    g40: LineSegment StartX=-1 StartY=-5.25 StartZ=0 EndX=-4.03109 EndY=-3.5 EndZ=0
    g41: Circle [constr] CenterX=-4.03109 CenterY=-7 CenterZ=0 NormalX=0 NormalY=0 NormalZ=1 AngleXU=0 Radius=3.5
    g42: LineSegment StartX=4.03109 StartY=-3.5 StartZ=0 EndX=1 EndY=-5.25 EndZ=0
    g43: LineSegment StartX=1 StartY=-5.25 StartZ=0 EndX=1 EndY=-8.75 EndZ=0
    g44: LineSegment StartX=1 StartY=-8.75 StartZ=0 EndX=4.03109 EndY=-10.5 EndZ=0
    g45: LineSegment StartX=4.03109 StartY=-10.5 StartZ=0 EndX=7.06218 EndY=-8.75 EndZ=0
    g46: LineSegment StartX=7.06218 StartY=-8.75 StartZ=0 EndX=7.06218 EndY=-5.25 EndZ=0
    g47: LineSegment StartX=7.06218 StartY=-5.25 StartZ=0 EndX=4.03109 EndY=-3.5 EndZ=0
    g48: Circle [constr] CenterX=4.03109 CenterY=-7 CenterZ=0 NormalX=0 NormalY=0 NormalZ=1 AngleXU=0 Radius=3.5
  constraints (117):
    c: Coincident(g0,g1)
    c: Coincident(g1,g2)
    c: Coincident(g2,g3)
    c: Coincident(g3,g4)
    c: Coincident(g4,g5)
    c: Coincident(g5,g0)
    c: Equal(g0, g1-g5) x5
    c: PointOnObject(g0,g6)
    c: PointOnObject(g1,g6)
    c: PointOnObject(g2,g6)
    c: PointOnObject(g3,g6)
    c: PointOnObject(g4,g6)
    c: PointOnObject(g5,g6)
    c: Coincident(g6,g-1)
    c: Diameter(g6) = 7
    c: PointOnObject(g0,g-2)
    c: Coincident(g7,g8)
    c: Coincident(g8,g9)
    c: Coincident(g9,g10)
    c: Coincident(g10,g11)
    c: Coincident(g11,g12)
    c: Coincident(g12,g7)
    c: Equal(g7, g8-g12) x5
    c: PointOnObject(g7,g13)
    c: PointOnObject(g8,g13)
    c: PointOnObject(g9,g13)
    c: PointOnObject(g10,g13)
    c: PointOnObject(g11,g13)
    c: PointOnObject(g12,g13)
    c: PointOnObject(g13,g-1)
    c: Diameter(g13) = 7
    c: Distance(g6,g13) = 8
    c: Horizontal(g0,g10)
    c: Coincident(g14,g15)
    c: Coincident(g15,g16)
    c: Coincident(g16,g17)
    c: Coincident(g17,g18)
    c: Coincident(g18,g19)
    c: Coincident(g19,g14)
    c: Equal(g14, g15-g19) x5
    c: PointOnObject(g14,g20)
    c: PointOnObject(g15,g20)
    c: PointOnObject(g16,g20)
    c: PointOnObject(g17,g20)
    c: PointOnObject(g18,g20)
    c: PointOnObject(g19,g20)
    c: Diameter(g20) = 7
    c: DistanceY(g-1,g20) = 7
    c: Vertical(g18)
    c: Distance(g17,g-2) = 1
    c: Coincident(g21,g22)
    c: Coincident(g22,g23)
    c: Coincident(g23,g24)
    c: Coincident(g24,g25)
    c: Coincident(g25,g26)
    c: Coincident(g26,g21)
    c: Equal(g21, g22-g26) x5
    c: PointOnObject(g21,g27)
    c: PointOnObject(g22,g27)
    c: PointOnObject(g23,g27)
    c: PointOnObject(g24,g27)
    c: PointOnObject(g25,g27)
    c: PointOnObject(g26,g27)
    c: Diameter(g27) = 7
    c: DistanceY(g-1,g27) = 7
    c: DistanceX(g21,g-1) = 1
    c: Vertical(g21)
    c: Coincident(g28,g29)
    c: Coincident(g29,g30)
    c: Coincident(g30,g31)
    c: Coincident(g31,g32)
    c: Coincident(g32,g33)
    c: Coincident(g33,g28)
    c: Equal(g28, g29-g33) x5
    c: PointOnObject(g28,g34)
    c: PointOnObject(g29,g34)
    c: PointOnObject(g30,g34)
    c: PointOnObject(g31,g34)
    c: PointOnObject(g32,g34)
    c: PointOnObject(g33,g34)
    c: PointOnObject(g34,g-1)
    c: Diameter(g34) = 7
    c: Vertical(g31)
    c: DistanceX(g34,g-1) = 8
    c: Coincident(g35,g36)
    c: Coincident(g36,g37)
    c: Coincident(g37,g38)
    c: Coincident(g38,g39)
    c: Coincident(g39,g40)
    c: Coincident(g40,g35)
    c: Equal(g35, g36-g40) x5
    c: PointOnObject(g35,g41)
    c: PointOnObject(g36,g41)
    c: PointOnObject(g37,g41)
    c: PointOnObject(g38,g41)
    c: PointOnObject(g39,g41)
    c: PointOnObject(g40,g41)
    c: Coincident(g42,g43)
    c: Coincident(g43,g44)
    c: Coincident(g44,g45)
    c: Coincident(g45,g46)
    c: Coincident(g46,g47)
    c: Coincident(g47,g42)
    c: Equal(g42, g43-g47) x5
    c: PointOnObject(g42,g48)
    c: PointOnObject(g43,g48)
    c: PointOnObject(g44,g48)
    c: PointOnObject(g45,g48)
    c: PointOnObject(g46,g48)
    c: PointOnObject(g47,g48)
    c: Equal(g41,g48)
    c: Diameter(g41) = 7
    c: Vertical(g39)
    c: Vertical(g43)
    c: Distance(g-2,g39) = 1
    c: Symmetric(g38,g43,g-2)
    c: Distance(g41,g-1) = 7
FEATURE [Part::Extrusion] Extrude629  label="hex231"
  Base = -> Sketch638
  Dir = (0,-1,2e-16)
  DirMode = 2
  FaceMakerClass = Part::FaceMakerBullseye
  FaceMakerMode = 3
  LengthFwd = 10
  LengthRev = 0
  Placement = pos=(-40,0,-14) rot=(0,0,1;0rad)
  Solid = true
  Symmetric = false
FEATURE [Sketcher::SketchObject] Sketch639
  ArcFitTolerance = 1e-06
  FullyConstrained = true
  MakeInternals = false
  Placement = pos=(0,0,0) rot=(1,0,0;1.5708rad)
  sketch-geometry (49):
    g0: LineSegment StartX=1e-16 StartY=3.5 StartZ=0 EndX=-3.03109 EndY=1.75 EndZ=0
    g1: LineSegment StartX=-3.03109 StartY=1.75 StartZ=0 EndX=-3.03109 EndY=-1.75 EndZ=0
    g2: LineSegment StartX=-3.03109 StartY=-1.75 StartZ=0 EndX=-1e-16 EndY=-3.5 EndZ=0
    g3: LineSegment StartX=-1e-16 StartY=-3.5 StartZ=0 EndX=3.03109 EndY=-1.75 EndZ=0
    g4: LineSegment StartX=3.03109 StartY=-1.75 StartZ=0 EndX=3.03109 EndY=1.75 EndZ=0
    g5: LineSegment StartX=3.03109 StartY=1.75 StartZ=0 EndX=1e-16 EndY=3.5 EndZ=0
    g6: Circle [constr] CenterX=0 CenterY=0 CenterZ=0 NormalX=0 NormalY=0 NormalZ=1 AngleXU=0 Radius=3.5
    g7: LineSegment StartX=4.96892 StartY=-1.75002 StartZ=0 EndX=8.00002 EndY=-3.5 EndZ=0
    g8: LineSegment StartX=8.00002 StartY=-3.5 StartZ=0 EndX=11.0311 EndY=-1.74998 EndZ=0
    g9: LineSegment StartX=11.0311 StartY=-1.74998 StartZ=0 EndX=11.0311 EndY=1.75002 EndZ=0
    g10: LineSegment StartX=11.0311 StartY=1.75002 StartZ=0 EndX=7.99998 EndY=3.5 EndZ=0
    g11: LineSegment StartX=7.99998 StartY=3.5 StartZ=0 EndX=4.9689 EndY=1.74998 EndZ=0
    g12: LineSegment StartX=4.9689 StartY=1.74998 StartZ=0 EndX=4.96892 EndY=-1.75002 EndZ=0
    g13: Circle [constr] CenterX=8 CenterY=0 CenterZ=0 NormalX=0 NormalY=0 NormalZ=1 AngleXU=0 Radius=3.5
    g14: LineSegment StartX=4.03109 StartY=3.5 StartZ=0 EndX=7.06218 EndY=5.25 EndZ=0
    g15: LineSegment StartX=7.06218 StartY=5.25 StartZ=0 EndX=7.06218 EndY=8.75 EndZ=0
    g16: LineSegment StartX=7.06218 StartY=8.75 StartZ=0 EndX=4.03109 EndY=10.5 EndZ=0
    g17: LineSegment StartX=4.03109 StartY=10.5 StartZ=0 EndX=1 EndY=8.75 EndZ=0
    g18: LineSegment StartX=1 StartY=8.75 StartZ=0 EndX=1 EndY=5.25 EndZ=0
    g19: LineSegment StartX=1 StartY=5.25 StartZ=0 EndX=4.03109 EndY=3.5 EndZ=0
    g20: Circle [constr] CenterX=4.03109 CenterY=7 CenterZ=0 NormalX=0 NormalY=0 NormalZ=1 AngleXU=0 Radius=3.5
    g21: LineSegment StartX=-1 StartY=5.25 StartZ=0 EndX=-1 EndY=8.75 EndZ=0
    g22: LineSegment StartX=-1 StartY=8.75 StartZ=0 EndX=-4.03109 EndY=10.5 EndZ=0
    g23: LineSegment StartX=-4.03109 StartY=10.5 StartZ=0 EndX=-7.06218 EndY=8.75 EndZ=0
    g24: LineSegment StartX=-7.06218 StartY=8.75 StartZ=0 EndX=-7.06218 EndY=5.25 EndZ=0
    g25: LineSegment StartX=-7.06218 StartY=5.25 StartZ=0 EndX=-4.03109 EndY=3.5 EndZ=0
    g26: LineSegment StartX=-4.03109 StartY=3.5 StartZ=0 EndX=-1 EndY=5.25 EndZ=0
    g27: Circle [constr] CenterX=-4.03109 CenterY=7 CenterZ=0 NormalX=0 NormalY=0 NormalZ=1 AngleXU=0 Radius=3.5
    g28: LineSegment StartX=-4.96891 StartY=-1.75 StartZ=0 EndX=-4.96891 EndY=1.75 EndZ=0
    g29: LineSegment StartX=-4.96891 StartY=1.75 StartZ=0 EndX=-8 EndY=3.5 EndZ=0
    g30: LineSegment StartX=-8 StartY=3.5 StartZ=0 EndX=-11.0311 EndY=1.75 EndZ=0
    g31: LineSegment StartX=-11.0311 StartY=1.75 StartZ=0 EndX=-11.0311 EndY=-1.75 EndZ=0
    g32: LineSegment StartX=-11.0311 StartY=-1.75 StartZ=0 EndX=-8 EndY=-3.5 EndZ=0
    g33: LineSegment StartX=-8 StartY=-3.5 StartZ=0 EndX=-4.96891 EndY=-1.75 EndZ=0
    g34: Circle [constr] CenterX=-8 CenterY=0 CenterZ=0 NormalX=0 NormalY=0 NormalZ=1 AngleXU=0 Radius=3.5
    g35: LineSegment StartX=-4.03109 StartY=-3.5 StartZ=0 EndX=-7.06218 EndY=-5.25 EndZ=0
    g36: LineSegment StartX=-7.06218 StartY=-5.25 StartZ=0 EndX=-7.06218 EndY=-8.75 EndZ=0
    g37: LineSegment StartX=-7.06218 StartY=-8.75 StartZ=0 EndX=-4.03109 EndY=-10.5 EndZ=0
    g38: LineSegment StartX=-4.03109 StartY=-10.5 StartZ=0 EndX=-1 EndY=-8.75 EndZ=0
    g39: LineSegment StartX=-1 StartY=-8.75 StartZ=0 EndX=-1 EndY=-5.25 EndZ=0
    g40: LineSegment StartX=-1 StartY=-5.25 StartZ=0 EndX=-4.03109 EndY=-3.5 EndZ=0
    g41: Circle [constr] CenterX=-4.03109 CenterY=-7 CenterZ=0 NormalX=0 NormalY=0 NormalZ=1 AngleXU=0 Radius=3.5
    g42: LineSegment StartX=4.03109 StartY=-3.5 StartZ=0 EndX=1 EndY=-5.25 EndZ=0
    g43: LineSegment StartX=1 StartY=-5.25 StartZ=0 EndX=1 EndY=-8.75 EndZ=0
    g44: LineSegment StartX=1 StartY=-8.75 StartZ=0 EndX=4.03109 EndY=-10.5 EndZ=0
    g45: LineSegment StartX=4.03109 StartY=-10.5 StartZ=0 EndX=7.06218 EndY=-8.75 EndZ=0
    g46: LineSegment StartX=7.06218 StartY=-8.75 StartZ=0 EndX=7.06218 EndY=-5.25 EndZ=0
    g47: LineSegment StartX=7.06218 StartY=-5.25 StartZ=0 EndX=4.03109 EndY=-3.5 EndZ=0
    g48: Circle [constr] CenterX=4.03109 CenterY=-7 CenterZ=0 NormalX=0 NormalY=0 NormalZ=1 AngleXU=0 Radius=3.5
  constraints (117):
    c: Coincident(g0,g1)
    c: Coincident(g1,g2)
    c: Coincident(g2,g3)
    c: Coincident(g3,g4)
    c: Coincident(g4,g5)
    c: Coincident(g5,g0)
    c: Equal(g0, g1-g5) x5
    c: PointOnObject(g0,g6)
    c: PointOnObject(g1,g6)
    c: PointOnObject(g2,g6)
    c: PointOnObject(g3,g6)
    c: PointOnObject(g4,g6)
    c: PointOnObject(g5,g6)
    c: Coincident(g6,g-1)
    c: Diameter(g6) = 7
    c: PointOnObject(g0,g-2)
    c: Coincident(g7,g8)
    c: Coincident(g8,g9)
    c: Coincident(g9,g10)
    c: Coincident(g10,g11)
    c: Coincident(g11,g12)
    c: Coincident(g12,g7)
    c: Equal(g7, g8-g12) x5
    c: PointOnObject(g7,g13)
    c: PointOnObject(g8,g13)
    c: PointOnObject(g9,g13)
    c: PointOnObject(g10,g13)
    c: PointOnObject(g11,g13)
    c: PointOnObject(g12,g13)
    c: PointOnObject(g13,g-1)
    c: Diameter(g13) = 7
    c: Distance(g6,g13) = 8
    c: Horizontal(g0,g10)
    c: Coincident(g14,g15)
    c: Coincident(g15,g16)
    c: Coincident(g16,g17)
    c: Coincident(g17,g18)
    c: Coincident(g18,g19)
    c: Coincident(g19,g14)
    c: Equal(g14, g15-g19) x5
    c: PointOnObject(g14,g20)
    c: PointOnObject(g15,g20)
    c: PointOnObject(g16,g20)
    c: PointOnObject(g17,g20)
    c: PointOnObject(g18,g20)
    c: PointOnObject(g19,g20)
    c: Diameter(g20) = 7
    c: DistanceY(g-1,g20) = 7
    c: Vertical(g18)
    c: Distance(g17,g-2) = 1
    c: Coincident(g21,g22)
    c: Coincident(g22,g23)
    c: Coincident(g23,g24)
    c: Coincident(g24,g25)
    c: Coincident(g25,g26)
    c: Coincident(g26,g21)
    c: Equal(g21, g22-g26) x5
    c: PointOnObject(g21,g27)
    c: PointOnObject(g22,g27)
    c: PointOnObject(g23,g27)
    c: PointOnObject(g24,g27)
    c: PointOnObject(g25,g27)
    c: PointOnObject(g26,g27)
    c: Diameter(g27) = 7
    c: DistanceY(g-1,g27) = 7
    c: DistanceX(g21,g-1) = 1
    c: Vertical(g21)
    c: Coincident(g28,g29)
    c: Coincident(g29,g30)
    c: Coincident(g30,g31)
    c: Coincident(g31,g32)
    c: Coincident(g32,g33)
    c: Coincident(g33,g28)
    c: Equal(g28, g29-g33) x5
    c: PointOnObject(g28,g34)
    c: PointOnObject(g29,g34)
    c: PointOnObject(g30,g34)
    c: PointOnObject(g31,g34)
    c: PointOnObject(g32,g34)
    c: PointOnObject(g33,g34)
    c: PointOnObject(g34,g-1)
    c: Diameter(g34) = 7
    c: Vertical(g31)
    c: DistanceX(g34,g-1) = 8
    c: Coincident(g35,g36)
    c: Coincident(g36,g37)
    c: Coincident(g37,g38)
    c: Coincident(g38,g39)
    c: Coincident(g39,g40)
    c: Coincident(g40,g35)
    c: Equal(g35, g36-g40) x5
    c: PointOnObject(g35,g41)
    c: PointOnObject(g36,g41)
    c: PointOnObject(g37,g41)
    c: PointOnObject(g38,g41)
    c: PointOnObject(g39,g41)
    c: PointOnObject(g40,g41)
    c: Coincident(g42,g43)
    c: Coincident(g43,g44)
    c: Coincident(g44,g45)
    c: Coincident(g45,g46)
    c: Coincident(g46,g47)
    c: Coincident(g47,g42)
    c: Equal(g42, g43-g47) x5
    c: PointOnObject(g42,g48)
    c: PointOnObject(g43,g48)
    c: PointOnObject(g44,g48)
    c: PointOnObject(g45,g48)
    c: PointOnObject(g46,g48)
    c: PointOnObject(g47,g48)
    c: Equal(g41,g48)
    c: Diameter(g41) = 7
    c: Vertical(g39)
    c: Vertical(g43)
    c: Distance(g-2,g39) = 1
    c: Symmetric(g38,g43,g-2)
    c: Distance(g41,g-1) = 7
FEATURE [Part::Extrusion] Extrude630  label="hex232"
  Base = -> Sketch639
  Dir = (0,-1,2e-16)
  DirMode = 2
  FaceMakerClass = Part::FaceMakerBullseye
  FaceMakerMode = 3
  LengthFwd = 10
  LengthRev = 0
  Placement = pos=(-24,0,-28) rot=(0,0,1;0rad)
  Solid = true
  Symmetric = false
FEATURE [Sketcher::SketchObject] Sketch640
  ArcFitTolerance = 1e-06
  FullyConstrained = true
  MakeInternals = false
  Placement = pos=(0,0,0) rot=(1,0,0;1.5708rad)
  sketch-geometry (49):
    g0: LineSegment StartX=1e-16 StartY=3.5 StartZ=0 EndX=-3.03109 EndY=1.75 EndZ=0
    g1: LineSegment StartX=-3.03109 StartY=1.75 StartZ=0 EndX=-3.03109 EndY=-1.75 EndZ=0
    g2: LineSegment StartX=-3.03109 StartY=-1.75 StartZ=0 EndX=-1e-16 EndY=-3.5 EndZ=0
    g3: LineSegment StartX=-1e-16 StartY=-3.5 StartZ=0 EndX=3.03109 EndY=-1.75 EndZ=0
    g4: LineSegment StartX=3.03109 StartY=-1.75 StartZ=0 EndX=3.03109 EndY=1.75 EndZ=0
    g5: LineSegment StartX=3.03109 StartY=1.75 StartZ=0 EndX=1e-16 EndY=3.5 EndZ=0
    g6: Circle [constr] CenterX=0 CenterY=0 CenterZ=0 NormalX=0 NormalY=0 NormalZ=1 AngleXU=0 Radius=3.5
    g7: LineSegment StartX=4.96892 StartY=-1.75002 StartZ=0 EndX=8.00002 EndY=-3.5 EndZ=0
    g8: LineSegment StartX=8.00002 StartY=-3.5 StartZ=0 EndX=11.0311 EndY=-1.74998 EndZ=0
    g9: LineSegment StartX=11.0311 StartY=-1.74998 StartZ=0 EndX=11.0311 EndY=1.75002 EndZ=0
    g10: LineSegment StartX=11.0311 StartY=1.75002 StartZ=0 EndX=7.99998 EndY=3.5 EndZ=0
    g11: LineSegment StartX=7.99998 StartY=3.5 StartZ=0 EndX=4.9689 EndY=1.74998 EndZ=0
    g12: LineSegment StartX=4.9689 StartY=1.74998 StartZ=0 EndX=4.96892 EndY=-1.75002 EndZ=0
    g13: Circle [constr] CenterX=8 CenterY=0 CenterZ=0 NormalX=0 NormalY=0 NormalZ=1 AngleXU=0 Radius=3.5
    g14: LineSegment StartX=4.03109 StartY=3.5 StartZ=0 EndX=7.06218 EndY=5.25 EndZ=0
    g15: LineSegment StartX=7.06218 StartY=5.25 StartZ=0 EndX=7.06218 EndY=8.75 EndZ=0
    g16: LineSegment StartX=7.06218 StartY=8.75 StartZ=0 EndX=4.03109 EndY=10.5 EndZ=0
    g17: LineSegment StartX=4.03109 StartY=10.5 StartZ=0 EndX=1 EndY=8.75 EndZ=0
    g18: LineSegment StartX=1 StartY=8.75 StartZ=0 EndX=1 EndY=5.25 EndZ=0
    g19: LineSegment StartX=1 StartY=5.25 StartZ=0 EndX=4.03109 EndY=3.5 EndZ=0
    g20: Circle [constr] CenterX=4.03109 CenterY=7 CenterZ=0 NormalX=0 NormalY=0 NormalZ=1 AngleXU=0 Radius=3.5
    g21: LineSegment StartX=-1 StartY=5.25 StartZ=0 EndX=-1 EndY=8.75 EndZ=0
    g22: LineSegment StartX=-1 StartY=8.75 StartZ=0 EndX=-4.03109 EndY=10.5 EndZ=0
    g23: LineSegment StartX=-4.03109 StartY=10.5 StartZ=0 EndX=-7.06218 EndY=8.75 EndZ=0
    g24: LineSegment StartX=-7.06218 StartY=8.75 StartZ=0 EndX=-7.06218 EndY=5.25 EndZ=0
    g25: LineSegment StartX=-7.06218 StartY=5.25 StartZ=0 EndX=-4.03109 EndY=3.5 EndZ=0
    g26: LineSegment StartX=-4.03109 StartY=3.5 StartZ=0 EndX=-1 EndY=5.25 EndZ=0
    g27: Circle [constr] CenterX=-4.03109 CenterY=7 CenterZ=0 NormalX=0 NormalY=0 NormalZ=1 AngleXU=0 Radius=3.5
    g28: LineSegment StartX=-4.96891 StartY=-1.75 StartZ=0 EndX=-4.96891 EndY=1.75 EndZ=0
    g29: LineSegment StartX=-4.96891 StartY=1.75 StartZ=0 EndX=-8 EndY=3.5 EndZ=0
    g30: LineSegment StartX=-8 StartY=3.5 StartZ=0 EndX=-11.0311 EndY=1.75 EndZ=0
    g31: LineSegment StartX=-11.0311 StartY=1.75 StartZ=0 EndX=-11.0311 EndY=-1.75 EndZ=0
    g32: LineSegment StartX=-11.0311 StartY=-1.75 StartZ=0 EndX=-8 EndY=-3.5 EndZ=0
    g33: LineSegment StartX=-8 StartY=-3.5 StartZ=0 EndX=-4.96891 EndY=-1.75 EndZ=0
    g34: Circle [constr] CenterX=-8 CenterY=0 CenterZ=0 NormalX=0 NormalY=0 NormalZ=1 AngleXU=0 Radius=3.5
    g35: LineSegment StartX=-4.03109 StartY=-3.5 StartZ=0 EndX=-7.06218 EndY=-5.25 EndZ=0
    g36: LineSegment StartX=-7.06218 StartY=-5.25 StartZ=0 EndX=-7.06218 EndY=-8.75 EndZ=0
    g37: LineSegment StartX=-7.06218 StartY=-8.75 StartZ=0 EndX=-4.03109 EndY=-10.5 EndZ=0
    g38: LineSegment StartX=-4.03109 StartY=-10.5 StartZ=0 EndX=-1 EndY=-8.75 EndZ=0
    g39: LineSegment StartX=-1 StartY=-8.75 StartZ=0 EndX=-1 EndY=-5.25 EndZ=0
    g40: LineSegment StartX=-1 StartY=-5.25 StartZ=0 EndX=-4.03109 EndY=-3.5 EndZ=0
    g41: Circle [constr] CenterX=-4.03109 CenterY=-7 CenterZ=0 NormalX=0 NormalY=0 NormalZ=1 AngleXU=0 Radius=3.5
    g42: LineSegment StartX=4.03109 StartY=-3.5 StartZ=0 EndX=1 EndY=-5.25 EndZ=0
    g43: LineSegment StartX=1 StartY=-5.25 StartZ=0 EndX=1 EndY=-8.75 EndZ=0
    g44: LineSegment StartX=1 StartY=-8.75 StartZ=0 EndX=4.03109 EndY=-10.5 EndZ=0
    g45: LineSegment StartX=4.03109 StartY=-10.5 StartZ=0 EndX=7.06218 EndY=-8.75 EndZ=0
    g46: LineSegment StartX=7.06218 StartY=-8.75 StartZ=0 EndX=7.06218 EndY=-5.25 EndZ=0
    g47: LineSegment StartX=7.06218 StartY=-5.25 StartZ=0 EndX=4.03109 EndY=-3.5 EndZ=0
    g48: Circle [constr] CenterX=4.03109 CenterY=-7 CenterZ=0 NormalX=0 NormalY=0 NormalZ=1 AngleXU=0 Radius=3.5
  constraints (117):
    c: Coincident(g0,g1)
    c: Coincident(g1,g2)
    c: Coincident(g2,g3)
    c: Coincident(g3,g4)
    c: Coincident(g4,g5)
    c: Coincident(g5,g0)
    c: Equal(g0, g1-g5) x5
    c: PointOnObject(g0,g6)
    c: PointOnObject(g1,g6)
    c: PointOnObject(g2,g6)
    c: PointOnObject(g3,g6)
    c: PointOnObject(g4,g6)
    c: PointOnObject(g5,g6)
    c: Coincident(g6,g-1)
    c: Diameter(g6) = 7
    c: PointOnObject(g0,g-2)
    c: Coincident(g7,g8)
    c: Coincident(g8,g9)
    c: Coincident(g9,g10)
    c: Coincident(g10,g11)
    c: Coincident(g11,g12)
    c: Coincident(g12,g7)
    c: Equal(g7, g8-g12) x5
    c: PointOnObject(g7,g13)
    c: PointOnObject(g8,g13)
    c: PointOnObject(g9,g13)
    c: PointOnObject(g10,g13)
    c: PointOnObject(g11,g13)
    c: PointOnObject(g12,g13)
    c: PointOnObject(g13,g-1)
    c: Diameter(g13) = 7
    c: Distance(g6,g13) = 8
    c: Horizontal(g0,g10)
    c: Coincident(g14,g15)
    c: Coincident(g15,g16)
    c: Coincident(g16,g17)
    c: Coincident(g17,g18)
    c: Coincident(g18,g19)
    c: Coincident(g19,g14)
    c: Equal(g14, g15-g19) x5
    c: PointOnObject(g14,g20)
    c: PointOnObject(g15,g20)
    c: PointOnObject(g16,g20)
    c: PointOnObject(g17,g20)
    c: PointOnObject(g18,g20)
    c: PointOnObject(g19,g20)
    c: Diameter(g20) = 7
    c: DistanceY(g-1,g20) = 7
    c: Vertical(g18)
    c: Distance(g17,g-2) = 1
    c: Coincident(g21,g22)
    c: Coincident(g22,g23)
    c: Coincident(g23,g24)
    c: Coincident(g24,g25)
    c: Coincident(g25,g26)
    c: Coincident(g26,g21)
    c: Equal(g21, g22-g26) x5
    c: PointOnObject(g21,g27)
    c: PointOnObject(g22,g27)
    c: PointOnObject(g23,g27)
    c: PointOnObject(g24,g27)
    c: PointOnObject(g25,g27)
    c: PointOnObject(g26,g27)
    c: Diameter(g27) = 7
    c: DistanceY(g-1,g27) = 7
    c: DistanceX(g21,g-1) = 1
    c: Vertical(g21)
    c: Coincident(g28,g29)
    c: Coincident(g29,g30)
    c: Coincident(g30,g31)
    c: Coincident(g31,g32)
    c: Coincident(g32,g33)
    c: Coincident(g33,g28)
    c: Equal(g28, g29-g33) x5
    c: PointOnObject(g28,g34)
    c: PointOnObject(g29,g34)
    c: PointOnObject(g30,g34)
    c: PointOnObject(g31,g34)
    c: PointOnObject(g32,g34)
    c: PointOnObject(g33,g34)
    c: PointOnObject(g34,g-1)
    c: Diameter(g34) = 7
    c: Vertical(g31)
    c: DistanceX(g34,g-1) = 8
    c: Coincident(g35,g36)
    c: Coincident(g36,g37)
    c: Coincident(g37,g38)
    c: Coincident(g38,g39)
    c: Coincident(g39,g40)
    c: Coincident(g40,g35)
    c: Equal(g35, g36-g40) x5
    c: PointOnObject(g35,g41)
    c: PointOnObject(g36,g41)
    c: PointOnObject(g37,g41)
    c: PointOnObject(g38,g41)
    c: PointOnObject(g39,g41)
    c: PointOnObject(g40,g41)
    c: Coincident(g42,g43)
    c: Coincident(g43,g44)
    c: Coincident(g44,g45)
    c: Coincident(g45,g46)
    c: Coincident(g46,g47)
    c: Coincident(g47,g42)
    c: Equal(g42, g43-g47) x5
    c: PointOnObject(g42,g48)
    c: PointOnObject(g43,g48)
    c: PointOnObject(g44,g48)
    c: PointOnObject(g45,g48)
    c: PointOnObject(g46,g48)
    c: PointOnObject(g47,g48)
    c: Equal(g41,g48)
    c: Diameter(g41) = 7
    c: Vertical(g39)
    c: Vertical(g43)
    c: Distance(g-2,g39) = 1
    c: Symmetric(g38,g43,g-2)
    c: Distance(g41,g-1) = 7
FEATURE [Part::Extrusion] Extrude631  label="hex233"
  Base = -> Sketch640
  Dir = (0,-1,2e-16)
  DirMode = 2
  FaceMakerClass = Part::FaceMakerBullseye
  FaceMakerMode = 3
  LengthFwd = 10
  LengthRev = 0
  Placement = pos=(-8,0,-42) rot=(0,0,1;0rad)
  Solid = true
  Symmetric = false
FEATURE [Sketcher::SketchObject] Sketch641
  ArcFitTolerance = 1e-06
  FullyConstrained = true
  MakeInternals = false
  Placement = pos=(0,0,0) rot=(1,0,0;1.5708rad)
  sketch-geometry (49):
    g0: LineSegment StartX=1e-16 StartY=3.5 StartZ=0 EndX=-3.03109 EndY=1.75 EndZ=0
    g1: LineSegment StartX=-3.03109 StartY=1.75 StartZ=0 EndX=-3.03109 EndY=-1.75 EndZ=0
    g2: LineSegment StartX=-3.03109 StartY=-1.75 StartZ=0 EndX=-1e-16 EndY=-3.5 EndZ=0
    g3: LineSegment StartX=-1e-16 StartY=-3.5 StartZ=0 EndX=3.03109 EndY=-1.75 EndZ=0
    g4: LineSegment StartX=3.03109 StartY=-1.75 StartZ=0 EndX=3.03109 EndY=1.75 EndZ=0
    g5: LineSegment StartX=3.03109 StartY=1.75 StartZ=0 EndX=1e-16 EndY=3.5 EndZ=0
    g6: Circle [constr] CenterX=0 CenterY=0 CenterZ=0 NormalX=0 NormalY=0 NormalZ=1 AngleXU=0 Radius=3.5
    g7: LineSegment StartX=4.96892 StartY=-1.75002 StartZ=0 EndX=8.00002 EndY=-3.5 EndZ=0
    g8: LineSegment StartX=8.00002 StartY=-3.5 StartZ=0 EndX=11.0311 EndY=-1.74998 EndZ=0
    g9: LineSegment StartX=11.0311 StartY=-1.74998 StartZ=0 EndX=11.0311 EndY=1.75002 EndZ=0
    g10: LineSegment StartX=11.0311 StartY=1.75002 StartZ=0 EndX=7.99998 EndY=3.5 EndZ=0
    g11: LineSegment StartX=7.99998 StartY=3.5 StartZ=0 EndX=4.9689 EndY=1.74998 EndZ=0
    g12: LineSegment StartX=4.9689 StartY=1.74998 StartZ=0 EndX=4.96892 EndY=-1.75002 EndZ=0
    g13: Circle [constr] CenterX=8 CenterY=0 CenterZ=0 NormalX=0 NormalY=0 NormalZ=1 AngleXU=0 Radius=3.5
    g14: LineSegment StartX=4.03109 StartY=3.5 StartZ=0 EndX=7.06218 EndY=5.25 EndZ=0
    g15: LineSegment StartX=7.06218 StartY=5.25 StartZ=0 EndX=7.06218 EndY=8.75 EndZ=0
    g16: LineSegment StartX=7.06218 StartY=8.75 StartZ=0 EndX=4.03109 EndY=10.5 EndZ=0
    g17: LineSegment StartX=4.03109 StartY=10.5 StartZ=0 EndX=1 EndY=8.75 EndZ=0
    g18: LineSegment StartX=1 StartY=8.75 StartZ=0 EndX=1 EndY=5.25 EndZ=0
    g19: LineSegment StartX=1 StartY=5.25 StartZ=0 EndX=4.03109 EndY=3.5 EndZ=0
    g20: Circle [constr] CenterX=4.03109 CenterY=7 CenterZ=0 NormalX=0 NormalY=0 NormalZ=1 AngleXU=0 Radius=3.5
    g21: LineSegment StartX=-1 StartY=5.25 StartZ=0 EndX=-1 EndY=8.75 EndZ=0
    g22: LineSegment StartX=-1 StartY=8.75 StartZ=0 EndX=-4.03109 EndY=10.5 EndZ=0
    g23: LineSegment StartX=-4.03109 StartY=10.5 StartZ=0 EndX=-7.06218 EndY=8.75 EndZ=0
    g24: LineSegment StartX=-7.06218 StartY=8.75 StartZ=0 EndX=-7.06218 EndY=5.25 EndZ=0
    g25: LineSegment StartX=-7.06218 StartY=5.25 StartZ=0 EndX=-4.03109 EndY=3.5 EndZ=0
    g26: LineSegment StartX=-4.03109 StartY=3.5 StartZ=0 EndX=-1 EndY=5.25 EndZ=0
    g27: Circle [constr] CenterX=-4.03109 CenterY=7 CenterZ=0 NormalX=0 NormalY=0 NormalZ=1 AngleXU=0 Radius=3.5
    g28: LineSegment StartX=-4.96891 StartY=-1.75 StartZ=0 EndX=-4.96891 EndY=1.75 EndZ=0
    g29: LineSegment StartX=-4.96891 StartY=1.75 StartZ=0 EndX=-8 EndY=3.5 EndZ=0
    g30: LineSegment StartX=-8 StartY=3.5 StartZ=0 EndX=-11.0311 EndY=1.75 EndZ=0
    g31: LineSegment StartX=-11.0311 StartY=1.75 StartZ=0 EndX=-11.0311 EndY=-1.75 EndZ=0
    g32: LineSegment StartX=-11.0311 StartY=-1.75 StartZ=0 EndX=-8 EndY=-3.5 EndZ=0
    g33: LineSegment StartX=-8 StartY=-3.5 StartZ=0 EndX=-4.96891 EndY=-1.75 EndZ=0
    g34: Circle [constr] CenterX=-8 CenterY=0 CenterZ=0 NormalX=0 NormalY=0 NormalZ=1 AngleXU=0 Radius=3.5
    g35: LineSegment StartX=-4.03109 StartY=-3.5 StartZ=0 EndX=-7.06218 EndY=-5.25 EndZ=0
    g36: LineSegment StartX=-7.06218 StartY=-5.25 StartZ=0 EndX=-7.06218 EndY=-8.75 EndZ=0
    g37: LineSegment StartX=-7.06218 StartY=-8.75 StartZ=0 EndX=-4.03109 EndY=-10.5 EndZ=0
    g38: LineSegment StartX=-4.03109 StartY=-10.5 StartZ=0 EndX=-1 EndY=-8.75 EndZ=0
    g39: LineSegment StartX=-1 StartY=-8.75 StartZ=0 EndX=-1 EndY=-5.25 EndZ=0
    g40: LineSegment StartX=-1 StartY=-5.25 StartZ=0 EndX=-4.03109 EndY=-3.5 EndZ=0
    g41: Circle [constr] CenterX=-4.03109 CenterY=-7 CenterZ=0 NormalX=0 NormalY=0 NormalZ=1 AngleXU=0 Radius=3.5
    g42: LineSegment StartX=4.03109 StartY=-3.5 StartZ=0 EndX=1 EndY=-5.25 EndZ=0
    g43: LineSegment StartX=1 StartY=-5.25 StartZ=0 EndX=1 EndY=-8.75 EndZ=0
    g44: LineSegment StartX=1 StartY=-8.75 StartZ=0 EndX=4.03109 EndY=-10.5 EndZ=0
    g45: LineSegment StartX=4.03109 StartY=-10.5 StartZ=0 EndX=7.06218 EndY=-8.75 EndZ=0
    g46: LineSegment StartX=7.06218 StartY=-8.75 StartZ=0 EndX=7.06218 EndY=-5.25 EndZ=0
    g47: LineSegment StartX=7.06218 StartY=-5.25 StartZ=0 EndX=4.03109 EndY=-3.5 EndZ=0
    g48: Circle [constr] CenterX=4.03109 CenterY=-7 CenterZ=0 NormalX=0 NormalY=0 NormalZ=1 AngleXU=0 Radius=3.5
  constraints (117):
    c: Coincident(g0,g1)
    c: Coincident(g1,g2)
    c: Coincident(g2,g3)
    c: Coincident(g3,g4)
    c: Coincident(g4,g5)
    c: Coincident(g5,g0)
    c: Equal(g0, g1-g5) x5
    c: PointOnObject(g0,g6)
    c: PointOnObject(g1,g6)
    c: PointOnObject(g2,g6)
    c: PointOnObject(g3,g6)
    c: PointOnObject(g4,g6)
    c: PointOnObject(g5,g6)
    c: Coincident(g6,g-1)
    c: Diameter(g6) = 7
    c: PointOnObject(g0,g-2)
    c: Coincident(g7,g8)
    c: Coincident(g8,g9)
    c: Coincident(g9,g10)
    c: Coincident(g10,g11)
    c: Coincident(g11,g12)
    c: Coincident(g12,g7)
    c: Equal(g7, g8-g12) x5
    c: PointOnObject(g7,g13)
    c: PointOnObject(g8,g13)
    c: PointOnObject(g9,g13)
    c: PointOnObject(g10,g13)
    c: PointOnObject(g11,g13)
    c: PointOnObject(g12,g13)
    c: PointOnObject(g13,g-1)
    c: Diameter(g13) = 7
    c: Distance(g6,g13) = 8
    c: Horizontal(g0,g10)
    c: Coincident(g14,g15)
    c: Coincident(g15,g16)
    c: Coincident(g16,g17)
    c: Coincident(g17,g18)
    c: Coincident(g18,g19)
    c: Coincident(g19,g14)
    c: Equal(g14, g15-g19) x5
    c: PointOnObject(g14,g20)
    c: PointOnObject(g15,g20)
    c: PointOnObject(g16,g20)
    c: PointOnObject(g17,g20)
    c: PointOnObject(g18,g20)
    c: PointOnObject(g19,g20)
    c: Diameter(g20) = 7
    c: DistanceY(g-1,g20) = 7
    c: Vertical(g18)
    c: Distance(g17,g-2) = 1
    c: Coincident(g21,g22)
    c: Coincident(g22,g23)
    c: Coincident(g23,g24)
    c: Coincident(g24,g25)
    c: Coincident(g25,g26)
    c: Coincident(g26,g21)
    c: Equal(g21, g22-g26) x5
    c: PointOnObject(g21,g27)
    c: PointOnObject(g22,g27)
    c: PointOnObject(g23,g27)
    c: PointOnObject(g24,g27)
    c: PointOnObject(g25,g27)
    c: PointOnObject(g26,g27)
    c: Diameter(g27) = 7
    c: DistanceY(g-1,g27) = 7
    c: DistanceX(g21,g-1) = 1
    c: Vertical(g21)
    c: Coincident(g28,g29)
    c: Coincident(g29,g30)
    c: Coincident(g30,g31)
    c: Coincident(g31,g32)
    c: Coincident(g32,g33)
    c: Coincident(g33,g28)
    c: Equal(g28, g29-g33) x5
    c: PointOnObject(g28,g34)
    c: PointOnObject(g29,g34)
    c: PointOnObject(g30,g34)
    c: PointOnObject(g31,g34)
    c: PointOnObject(g32,g34)
    c: PointOnObject(g33,g34)
    c: PointOnObject(g34,g-1)
    c: Diameter(g34) = 7
    c: Vertical(g31)
    c: DistanceX(g34,g-1) = 8
    c: Coincident(g35,g36)
    c: Coincident(g36,g37)
    c: Coincident(g37,g38)
    c: Coincident(g38,g39)
    c: Coincident(g39,g40)
    c: Coincident(g40,g35)
    c: Equal(g35, g36-g40) x5
    c: PointOnObject(g35,g41)
    c: PointOnObject(g36,g41)
    c: PointOnObject(g37,g41)
    c: PointOnObject(g38,g41)
    c: PointOnObject(g39,g41)
    c: PointOnObject(g40,g41)
    c: Coincident(g42,g43)
    c: Coincident(g43,g44)
    c: Coincident(g44,g45)
    c: Coincident(g45,g46)
    c: Coincident(g46,g47)
    c: Coincident(g47,g42)
    c: Equal(g42, g43-g47) x5
    c: PointOnObject(g42,g48)
    c: PointOnObject(g43,g48)
    c: PointOnObject(g44,g48)
    c: PointOnObject(g45,g48)
    c: PointOnObject(g46,g48)
    c: PointOnObject(g47,g48)
    c: Equal(g41,g48)
    c: Diameter(g41) = 7
    c: Vertical(g39)
    c: Vertical(g43)
    c: Distance(g-2,g39) = 1
    c: Symmetric(g38,g43,g-2)
    c: Distance(g41,g-1) = 7
FEATURE [Part::Extrusion] Extrude632  label="hex234"
  Base = -> Sketch641
  Dir = (0,-1,2e-16)
  DirMode = 2
  FaceMakerClass = Part::FaceMakerBullseye
  FaceMakerMode = 3
  LengthFwd = 10
  LengthRev = 0
  Placement = pos=(32,0,-28) rot=(0,0,1;0rad)
  Solid = true
  Symmetric = false
FEATURE [Sketcher::SketchObject] Sketch642
  ArcFitTolerance = 1e-06
  FullyConstrained = true
  MakeInternals = false
  Placement = pos=(0,0,0) rot=(1,0,0;1.5708rad)
  sketch-geometry (49):
    g0: LineSegment StartX=1e-16 StartY=3.5 StartZ=0 EndX=-3.03109 EndY=1.75 EndZ=0
    g1: LineSegment StartX=-3.03109 StartY=1.75 StartZ=0 EndX=-3.03109 EndY=-1.75 EndZ=0
    g2: LineSegment StartX=-3.03109 StartY=-1.75 StartZ=0 EndX=-1e-16 EndY=-3.5 EndZ=0
    g3: LineSegment StartX=-1e-16 StartY=-3.5 StartZ=0 EndX=3.03109 EndY=-1.75 EndZ=0
    g4: LineSegment StartX=3.03109 StartY=-1.75 StartZ=0 EndX=3.03109 EndY=1.75 EndZ=0
    g5: LineSegment StartX=3.03109 StartY=1.75 StartZ=0 EndX=1e-16 EndY=3.5 EndZ=0
    g6: Circle [constr] CenterX=0 CenterY=0 CenterZ=0 NormalX=0 NormalY=0 NormalZ=1 AngleXU=0 Radius=3.5
    g7: LineSegment StartX=4.96892 StartY=-1.75002 StartZ=0 EndX=8.00002 EndY=-3.5 EndZ=0
    g8: LineSegment StartX=8.00002 StartY=-3.5 StartZ=0 EndX=11.0311 EndY=-1.74998 EndZ=0
    g9: LineSegment StartX=11.0311 StartY=-1.74998 StartZ=0 EndX=11.0311 EndY=1.75002 EndZ=0
    g10: LineSegment StartX=11.0311 StartY=1.75002 StartZ=0 EndX=7.99998 EndY=3.5 EndZ=0
    g11: LineSegment StartX=7.99998 StartY=3.5 StartZ=0 EndX=4.9689 EndY=1.74998 EndZ=0
    g12: LineSegment StartX=4.9689 StartY=1.74998 StartZ=0 EndX=4.96892 EndY=-1.75002 EndZ=0
    g13: Circle [constr] CenterX=8 CenterY=0 CenterZ=0 NormalX=0 NormalY=0 NormalZ=1 AngleXU=0 Radius=3.5
    g14: LineSegment StartX=4.03109 StartY=3.5 StartZ=0 EndX=7.06218 EndY=5.25 EndZ=0
    g15: LineSegment StartX=7.06218 StartY=5.25 StartZ=0 EndX=7.06218 EndY=8.75 EndZ=0
    g16: LineSegment StartX=7.06218 StartY=8.75 StartZ=0 EndX=4.03109 EndY=10.5 EndZ=0
    g17: LineSegment StartX=4.03109 StartY=10.5 StartZ=0 EndX=1 EndY=8.75 EndZ=0
    g18: LineSegment StartX=1 StartY=8.75 StartZ=0 EndX=1 EndY=5.25 EndZ=0
    g19: LineSegment StartX=1 StartY=5.25 StartZ=0 EndX=4.03109 EndY=3.5 EndZ=0
    g20: Circle [constr] CenterX=4.03109 CenterY=7 CenterZ=0 NormalX=0 NormalY=0 NormalZ=1 AngleXU=0 Radius=3.5
    g21: LineSegment StartX=-1 StartY=5.25 StartZ=0 EndX=-1 EndY=8.75 EndZ=0
    g22: LineSegment StartX=-1 StartY=8.75 StartZ=0 EndX=-4.03109 EndY=10.5 EndZ=0
    g23: LineSegment StartX=-4.03109 StartY=10.5 StartZ=0 EndX=-7.06218 EndY=8.75 EndZ=0
    g24: LineSegment StartX=-7.06218 StartY=8.75 StartZ=0 EndX=-7.06218 EndY=5.25 EndZ=0
    g25: LineSegment StartX=-7.06218 StartY=5.25 StartZ=0 EndX=-4.03109 EndY=3.5 EndZ=0
    g26: LineSegment StartX=-4.03109 StartY=3.5 StartZ=0 EndX=-1 EndY=5.25 EndZ=0
    g27: Circle [constr] CenterX=-4.03109 CenterY=7 CenterZ=0 NormalX=0 NormalY=0 NormalZ=1 AngleXU=0 Radius=3.5
    g28: LineSegment StartX=-4.96891 StartY=-1.75 StartZ=0 EndX=-4.96891 EndY=1.75 EndZ=0
    g29: LineSegment StartX=-4.96891 StartY=1.75 StartZ=0 EndX=-8 EndY=3.5 EndZ=0
    g30: LineSegment StartX=-8 StartY=3.5 StartZ=0 EndX=-11.0311 EndY=1.75 EndZ=0
    g31: LineSegment StartX=-11.0311 StartY=1.75 StartZ=0 EndX=-11.0311 EndY=-1.75 EndZ=0
    g32: LineSegment StartX=-11.0311 StartY=-1.75 StartZ=0 EndX=-8 EndY=-3.5 EndZ=0
    g33: LineSegment StartX=-8 StartY=-3.5 StartZ=0 EndX=-4.96891 EndY=-1.75 EndZ=0
    g34: Circle [constr] CenterX=-8 CenterY=0 CenterZ=0 NormalX=0 NormalY=0 NormalZ=1 AngleXU=0 Radius=3.5
    g35: LineSegment StartX=-4.03109 StartY=-3.5 StartZ=0 EndX=-7.06218 EndY=-5.25 EndZ=0
    g36: LineSegment StartX=-7.06218 StartY=-5.25 StartZ=0 EndX=-7.06218 EndY=-8.75 EndZ=0
    g37: LineSegment StartX=-7.06218 StartY=-8.75 StartZ=0 EndX=-4.03109 EndY=-10.5 EndZ=0
    g38: LineSegment StartX=-4.03109 StartY=-10.5 StartZ=0 EndX=-1 EndY=-8.75 EndZ=0
    g39: LineSegment StartX=-1 StartY=-8.75 StartZ=0 EndX=-1 EndY=-5.25 EndZ=0
    g40: LineSegment StartX=-1 StartY=-5.25 StartZ=0 EndX=-4.03109 EndY=-3.5 EndZ=0
    g41: Circle [constr] CenterX=-4.03109 CenterY=-7 CenterZ=0 NormalX=0 NormalY=0 NormalZ=1 AngleXU=0 Radius=3.5
    g42: LineSegment StartX=4.03109 StartY=-3.5 StartZ=0 EndX=1 EndY=-5.25 EndZ=0
    g43: LineSegment StartX=1 StartY=-5.25 StartZ=0 EndX=1 EndY=-8.75 EndZ=0
    g44: LineSegment StartX=1 StartY=-8.75 StartZ=0 EndX=4.03109 EndY=-10.5 EndZ=0
    g45: LineSegment StartX=4.03109 StartY=-10.5 StartZ=0 EndX=7.06218 EndY=-8.75 EndZ=0
    g46: LineSegment StartX=7.06218 StartY=-8.75 StartZ=0 EndX=7.06218 EndY=-5.25 EndZ=0
    g47: LineSegment StartX=7.06218 StartY=-5.25 StartZ=0 EndX=4.03109 EndY=-3.5 EndZ=0
    g48: Circle [constr] CenterX=4.03109 CenterY=-7 CenterZ=0 NormalX=0 NormalY=0 NormalZ=1 AngleXU=0 Radius=3.5
  constraints (117):
    c: Coincident(g0,g1)
    c: Coincident(g1,g2)
    c: Coincident(g2,g3)
    c: Coincident(g3,g4)
    c: Coincident(g4,g5)
    c: Coincident(g5,g0)
    c: Equal(g0, g1-g5) x5
    c: PointOnObject(g0,g6)
    c: PointOnObject(g1,g6)
    c: PointOnObject(g2,g6)
    c: PointOnObject(g3,g6)
    c: PointOnObject(g4,g6)
    c: PointOnObject(g5,g6)
    c: Coincident(g6,g-1)
    c: Diameter(g6) = 7
    c: PointOnObject(g0,g-2)
    c: Coincident(g7,g8)
    c: Coincident(g8,g9)
    c: Coincident(g9,g10)
    c: Coincident(g10,g11)
    c: Coincident(g11,g12)
    c: Coincident(g12,g7)
    c: Equal(g7, g8-g12) x5
    c: PointOnObject(g7,g13)
    c: PointOnObject(g8,g13)
    c: PointOnObject(g9,g13)
    c: PointOnObject(g10,g13)
    c: PointOnObject(g11,g13)
    c: PointOnObject(g12,g13)
    c: PointOnObject(g13,g-1)
    c: Diameter(g13) = 7
    c: Distance(g6,g13) = 8
    c: Horizontal(g0,g10)
    c: Coincident(g14,g15)
    c: Coincident(g15,g16)
    c: Coincident(g16,g17)
    c: Coincident(g17,g18)
    c: Coincident(g18,g19)
    c: Coincident(g19,g14)
    c: Equal(g14, g15-g19) x5
    c: PointOnObject(g14,g20)
    c: PointOnObject(g15,g20)
    c: PointOnObject(g16,g20)
    c: PointOnObject(g17,g20)
    c: PointOnObject(g18,g20)
    c: PointOnObject(g19,g20)
    c: Diameter(g20) = 7
    c: DistanceY(g-1,g20) = 7
    c: Vertical(g18)
    c: Distance(g17,g-2) = 1
    c: Coincident(g21,g22)
    c: Coincident(g22,g23)
    c: Coincident(g23,g24)
    c: Coincident(g24,g25)
    c: Coincident(g25,g26)
    c: Coincident(g26,g21)
    c: Equal(g21, g22-g26) x5
    c: PointOnObject(g21,g27)
    c: PointOnObject(g22,g27)
    c: PointOnObject(g23,g27)
    c: PointOnObject(g24,g27)
    c: PointOnObject(g25,g27)
    c: PointOnObject(g26,g27)
    c: Diameter(g27) = 7
    c: DistanceY(g-1,g27) = 7
    c: DistanceX(g21,g-1) = 1
    c: Vertical(g21)
    c: Coincident(g28,g29)
    c: Coincident(g29,g30)
    c: Coincident(g30,g31)
    c: Coincident(g31,g32)
    c: Coincident(g32,g33)
    c: Coincident(g33,g28)
    c: Equal(g28, g29-g33) x5
    c: PointOnObject(g28,g34)
    c: PointOnObject(g29,g34)
    c: PointOnObject(g30,g34)
    c: PointOnObject(g31,g34)
    c: PointOnObject(g32,g34)
    c: PointOnObject(g33,g34)
    c: PointOnObject(g34,g-1)
    c: Diameter(g34) = 7
    c: Vertical(g31)
    c: DistanceX(g34,g-1) = 8
    c: Coincident(g35,g36)
    c: Coincident(g36,g37)
    c: Coincident(g37,g38)
    c: Coincident(g38,g39)
    c: Coincident(g39,g40)
    c: Coincident(g40,g35)
    c: Equal(g35, g36-g40) x5
    c: PointOnObject(g35,g41)
    c: PointOnObject(g36,g41)
    c: PointOnObject(g37,g41)
    c: PointOnObject(g38,g41)
    c: PointOnObject(g39,g41)
    c: PointOnObject(g40,g41)
    c: Coincident(g42,g43)
    c: Coincident(g43,g44)
    c: Coincident(g44,g45)
    c: Coincident(g45,g46)
    c: Coincident(g46,g47)
    c: Coincident(g47,g42)
    c: Equal(g42, g43-g47) x5
    c: PointOnObject(g42,g48)
    c: PointOnObject(g43,g48)
    c: PointOnObject(g44,g48)
    c: PointOnObject(g45,g48)
    c: PointOnObject(g46,g48)
    c: PointOnObject(g47,g48)
    c: Equal(g41,g48)
    c: Diameter(g41) = 7
    c: Vertical(g39)
    c: Vertical(g43)
    c: Distance(g-2,g39) = 1
    c: Symmetric(g38,g43,g-2)
    c: Distance(g41,g-1) = 7
FEATURE [Part::Extrusion] Extrude633  label="hex235"
  Base = -> Sketch642
  Dir = (0,-1,2e-16)
  DirMode = 2
  FaceMakerClass = Part::FaceMakerBullseye
  FaceMakerMode = 3
  LengthFwd = 10
  LengthRev = 0
  Placement = pos=(36,0,-7) rot=(0,0,1;0rad)
  Solid = true
  Symmetric = false
FEATURE [Sketcher::SketchObject] Sketch643
  ArcFitTolerance = 1e-06
  FullyConstrained = true
  MakeInternals = false
  Placement = pos=(0,0,0) rot=(1,0,0;1.5708rad)
  sketch-geometry (49):
    g0: LineSegment StartX=1e-16 StartY=3.5 StartZ=0 EndX=-3.03109 EndY=1.75 EndZ=0
    g1: LineSegment StartX=-3.03109 StartY=1.75 StartZ=0 EndX=-3.03109 EndY=-1.75 EndZ=0
    g2: LineSegment StartX=-3.03109 StartY=-1.75 StartZ=0 EndX=-1e-16 EndY=-3.5 EndZ=0
    g3: LineSegment StartX=-1e-16 StartY=-3.5 StartZ=0 EndX=3.03109 EndY=-1.75 EndZ=0
    g4: LineSegment StartX=3.03109 StartY=-1.75 StartZ=0 EndX=3.03109 EndY=1.75 EndZ=0
    g5: LineSegment StartX=3.03109 StartY=1.75 StartZ=0 EndX=1e-16 EndY=3.5 EndZ=0
    g6: Circle [constr] CenterX=0 CenterY=0 CenterZ=0 NormalX=0 NormalY=0 NormalZ=1 AngleXU=0 Radius=3.5
    g7: LineSegment StartX=4.96892 StartY=-1.75002 StartZ=0 EndX=8.00002 EndY=-3.5 EndZ=0
    g8: LineSegment StartX=8.00002 StartY=-3.5 StartZ=0 EndX=11.0311 EndY=-1.74998 EndZ=0
    g9: LineSegment StartX=11.0311 StartY=-1.74998 StartZ=0 EndX=11.0311 EndY=1.75002 EndZ=0
    g10: LineSegment StartX=11.0311 StartY=1.75002 StartZ=0 EndX=7.99998 EndY=3.5 EndZ=0
    g11: LineSegment StartX=7.99998 StartY=3.5 StartZ=0 EndX=4.9689 EndY=1.74998 EndZ=0
    g12: LineSegment StartX=4.9689 StartY=1.74998 StartZ=0 EndX=4.96892 EndY=-1.75002 EndZ=0
    g13: Circle [constr] CenterX=8 CenterY=0 CenterZ=0 NormalX=0 NormalY=0 NormalZ=1 AngleXU=0 Radius=3.5
    g14: LineSegment StartX=4.03109 StartY=3.5 StartZ=0 EndX=7.06218 EndY=5.25 EndZ=0
    g15: LineSegment StartX=7.06218 StartY=5.25 StartZ=0 EndX=7.06218 EndY=8.75 EndZ=0
    g16: LineSegment StartX=7.06218 StartY=8.75 StartZ=0 EndX=4.03109 EndY=10.5 EndZ=0
    g17: LineSegment StartX=4.03109 StartY=10.5 StartZ=0 EndX=1 EndY=8.75 EndZ=0
    g18: LineSegment StartX=1 StartY=8.75 StartZ=0 EndX=1 EndY=5.25 EndZ=0
    g19: LineSegment StartX=1 StartY=5.25 StartZ=0 EndX=4.03109 EndY=3.5 EndZ=0
    g20: Circle [constr] CenterX=4.03109 CenterY=7 CenterZ=0 NormalX=0 NormalY=0 NormalZ=1 AngleXU=0 Radius=3.5
    g21: LineSegment StartX=-1 StartY=5.25 StartZ=0 EndX=-1 EndY=8.75 EndZ=0
    g22: LineSegment StartX=-1 StartY=8.75 StartZ=0 EndX=-4.03109 EndY=10.5 EndZ=0
    g23: LineSegment StartX=-4.03109 StartY=10.5 StartZ=0 EndX=-7.06218 EndY=8.75 EndZ=0
    g24: LineSegment StartX=-7.06218 StartY=8.75 StartZ=0 EndX=-7.06218 EndY=5.25 EndZ=0
    g25: LineSegment StartX=-7.06218 StartY=5.25 StartZ=0 EndX=-4.03109 EndY=3.5 EndZ=0
    g26: LineSegment StartX=-4.03109 StartY=3.5 StartZ=0 EndX=-1 EndY=5.25 EndZ=0
    g27: Circle [constr] CenterX=-4.03109 CenterY=7 CenterZ=0 NormalX=0 NormalY=0 NormalZ=1 AngleXU=0 Radius=3.5
    g28: LineSegment StartX=-4.96891 StartY=-1.75 StartZ=0 EndX=-4.96891 EndY=1.75 EndZ=0
    g29: LineSegment StartX=-4.96891 StartY=1.75 StartZ=0 EndX=-8 EndY=3.5 EndZ=0
    g30: LineSegment StartX=-8 StartY=3.5 StartZ=0 EndX=-11.0311 EndY=1.75 EndZ=0
    g31: LineSegment StartX=-11.0311 StartY=1.75 StartZ=0 EndX=-11.0311 EndY=-1.75 EndZ=0
    g32: LineSegment StartX=-11.0311 StartY=-1.75 StartZ=0 EndX=-8 EndY=-3.5 EndZ=0
    g33: LineSegment StartX=-8 StartY=-3.5 StartZ=0 EndX=-4.96891 EndY=-1.75 EndZ=0
    g34: Circle [constr] CenterX=-8 CenterY=0 CenterZ=0 NormalX=0 NormalY=0 NormalZ=1 AngleXU=0 Radius=3.5
    g35: LineSegment StartX=-4.03109 StartY=-3.5 StartZ=0 EndX=-7.06218 EndY=-5.25 EndZ=0
    g36: LineSegment StartX=-7.06218 StartY=-5.25 StartZ=0 EndX=-7.06218 EndY=-8.75 EndZ=0
    g37: LineSegment StartX=-7.06218 StartY=-8.75 StartZ=0 EndX=-4.03109 EndY=-10.5 EndZ=0
    g38: LineSegment StartX=-4.03109 StartY=-10.5 StartZ=0 EndX=-1 EndY=-8.75 EndZ=0
    g39: LineSegment StartX=-1 StartY=-8.75 StartZ=0 EndX=-1 EndY=-5.25 EndZ=0
    g40: LineSegment StartX=-1 StartY=-5.25 StartZ=0 EndX=-4.03109 EndY=-3.5 EndZ=0
    g41: Circle [constr] CenterX=-4.03109 CenterY=-7 CenterZ=0 NormalX=0 NormalY=0 NormalZ=1 AngleXU=0 Radius=3.5
    g42: LineSegment StartX=4.03109 StartY=-3.5 StartZ=0 EndX=1 EndY=-5.25 EndZ=0
    g43: LineSegment StartX=1 StartY=-5.25 StartZ=0 EndX=1 EndY=-8.75 EndZ=0
    g44: LineSegment StartX=1 StartY=-8.75 StartZ=0 EndX=4.03109 EndY=-10.5 EndZ=0
    g45: LineSegment StartX=4.03109 StartY=-10.5 StartZ=0 EndX=7.06218 EndY=-8.75 EndZ=0
    g46: LineSegment StartX=7.06218 StartY=-8.75 StartZ=0 EndX=7.06218 EndY=-5.25 EndZ=0
    g47: LineSegment StartX=7.06218 StartY=-5.25 StartZ=0 EndX=4.03109 EndY=-3.5 EndZ=0
    g48: Circle [constr] CenterX=4.03109 CenterY=-7 CenterZ=0 NormalX=0 NormalY=0 NormalZ=1 AngleXU=0 Radius=3.5
  constraints (117):
    c: Coincident(g0,g1)
    c: Coincident(g1,g2)
    c: Coincident(g2,g3)
    c: Coincident(g3,g4)
    c: Coincident(g4,g5)
    c: Coincident(g5,g0)
    c: Equal(g0, g1-g5) x5
    c: PointOnObject(g0,g6)
    c: PointOnObject(g1,g6)
    c: PointOnObject(g2,g6)
    c: PointOnObject(g3,g6)
    c: PointOnObject(g4,g6)
    c: PointOnObject(g5,g6)
    c: Coincident(g6,g-1)
    c: Diameter(g6) = 7
    c: PointOnObject(g0,g-2)
    c: Coincident(g7,g8)
    c: Coincident(g8,g9)
    c: Coincident(g9,g10)
    c: Coincident(g10,g11)
    c: Coincident(g11,g12)
    c: Coincident(g12,g7)
    c: Equal(g7, g8-g12) x5
    c: PointOnObject(g7,g13)
    c: PointOnObject(g8,g13)
    c: PointOnObject(g9,g13)
    c: PointOnObject(g10,g13)
    c: PointOnObject(g11,g13)
    c: PointOnObject(g12,g13)
    c: PointOnObject(g13,g-1)
    c: Diameter(g13) = 7
    c: Distance(g6,g13) = 8
    c: Horizontal(g0,g10)
    c: Coincident(g14,g15)
    c: Coincident(g15,g16)
    c: Coincident(g16,g17)
    c: Coincident(g17,g18)
    c: Coincident(g18,g19)
    c: Coincident(g19,g14)
    c: Equal(g14, g15-g19) x5
    c: PointOnObject(g14,g20)
    c: PointOnObject(g15,g20)
    c: PointOnObject(g16,g20)
    c: PointOnObject(g17,g20)
    c: PointOnObject(g18,g20)
    c: PointOnObject(g19,g20)
    c: Diameter(g20) = 7
    c: DistanceY(g-1,g20) = 7
    c: Vertical(g18)
    c: Distance(g17,g-2) = 1
    c: Coincident(g21,g22)
    c: Coincident(g22,g23)
    c: Coincident(g23,g24)
    c: Coincident(g24,g25)
    c: Coincident(g25,g26)
    c: Coincident(g26,g21)
    c: Equal(g21, g22-g26) x5
    c: PointOnObject(g21,g27)
    c: PointOnObject(g22,g27)
    c: PointOnObject(g23,g27)
    c: PointOnObject(g24,g27)
    c: PointOnObject(g25,g27)
    c: PointOnObject(g26,g27)
    c: Diameter(g27) = 7
    c: DistanceY(g-1,g27) = 7
    c: DistanceX(g21,g-1) = 1
    c: Vertical(g21)
    c: Coincident(g28,g29)
    c: Coincident(g29,g30)
    c: Coincident(g30,g31)
    c: Coincident(g31,g32)
    c: Coincident(g32,g33)
    c: Coincident(g33,g28)
    c: Equal(g28, g29-g33) x5
    c: PointOnObject(g28,g34)
    c: PointOnObject(g29,g34)
    c: PointOnObject(g30,g34)
    c: PointOnObject(g31,g34)
    c: PointOnObject(g32,g34)
    c: PointOnObject(g33,g34)
    c: PointOnObject(g34,g-1)
    c: Diameter(g34) = 7
    c: Vertical(g31)
    c: DistanceX(g34,g-1) = 8
    c: Coincident(g35,g36)
    c: Coincident(g36,g37)
    c: Coincident(g37,g38)
    c: Coincident(g38,g39)
    c: Coincident(g39,g40)
    c: Coincident(g40,g35)
    c: Equal(g35, g36-g40) x5
    c: PointOnObject(g35,g41)
    c: PointOnObject(g36,g41)
    c: PointOnObject(g37,g41)
    c: PointOnObject(g38,g41)
    c: PointOnObject(g39,g41)
    c: PointOnObject(g40,g41)
    c: Coincident(g42,g43)
    c: Coincident(g43,g44)
    c: Coincident(g44,g45)
    c: Coincident(g45,g46)
    c: Coincident(g46,g47)
    c: Coincident(g47,g42)
    c: Equal(g42, g43-g47) x5
    c: PointOnObject(g42,g48)
    c: PointOnObject(g43,g48)
    c: PointOnObject(g44,g48)
    c: PointOnObject(g45,g48)
    c: PointOnObject(g46,g48)
    c: PointOnObject(g47,g48)
    c: Equal(g41,g48)
    c: Diameter(g41) = 7
    c: Vertical(g39)
    c: Vertical(g43)
    c: Distance(g-2,g39) = 1
    c: Symmetric(g38,g43,g-2)
    c: Distance(g41,g-1) = 7
FEATURE [Part::Extrusion] Extrude634  label="hex236"
  Base = -> Sketch643
  Dir = (0,-1,2e-16)
  DirMode = 2
  FaceMakerClass = Part::FaceMakerBullseye
  FaceMakerMode = 3
  LengthFwd = 10
  LengthRev = 0
  Placement = pos=(56,0,0) rot=(0,0,1;0rad)
  Solid = true
  Symmetric = false
FEATURE [Sketcher::SketchObject] Sketch644
  ArcFitTolerance = 1e-06
  FullyConstrained = true
  MakeInternals = false
  Placement = pos=(0,0,0) rot=(1,0,0;1.5708rad)
  sketch-geometry (49):
    g0: LineSegment StartX=1e-16 StartY=3.5 StartZ=0 EndX=-3.03109 EndY=1.75 EndZ=0
    g1: LineSegment StartX=-3.03109 StartY=1.75 StartZ=0 EndX=-3.03109 EndY=-1.75 EndZ=0
    g2: LineSegment StartX=-3.03109 StartY=-1.75 StartZ=0 EndX=-1e-16 EndY=-3.5 EndZ=0
    g3: LineSegment StartX=-1e-16 StartY=-3.5 StartZ=0 EndX=3.03109 EndY=-1.75 EndZ=0
    g4: LineSegment StartX=3.03109 StartY=-1.75 StartZ=0 EndX=3.03109 EndY=1.75 EndZ=0
    g5: LineSegment StartX=3.03109 StartY=1.75 StartZ=0 EndX=1e-16 EndY=3.5 EndZ=0
    g6: Circle [constr] CenterX=0 CenterY=0 CenterZ=0 NormalX=0 NormalY=0 NormalZ=1 AngleXU=0 Radius=3.5
    g7: LineSegment StartX=4.96892 StartY=-1.75002 StartZ=0 EndX=8.00002 EndY=-3.5 EndZ=0
    g8: LineSegment StartX=8.00002 StartY=-3.5 StartZ=0 EndX=11.0311 EndY=-1.74998 EndZ=0
    g9: LineSegment StartX=11.0311 StartY=-1.74998 StartZ=0 EndX=11.0311 EndY=1.75002 EndZ=0
    g10: LineSegment StartX=11.0311 StartY=1.75002 StartZ=0 EndX=7.99998 EndY=3.5 EndZ=0
    g11: LineSegment StartX=7.99998 StartY=3.5 StartZ=0 EndX=4.9689 EndY=1.74998 EndZ=0
    g12: LineSegment StartX=4.9689 StartY=1.74998 StartZ=0 EndX=4.96892 EndY=-1.75002 EndZ=0
    g13: Circle [constr] CenterX=8 CenterY=0 CenterZ=0 NormalX=0 NormalY=0 NormalZ=1 AngleXU=0 Radius=3.5
    g14: LineSegment StartX=4.03109 StartY=3.5 StartZ=0 EndX=7.06218 EndY=5.25 EndZ=0
    g15: LineSegment StartX=7.06218 StartY=5.25 StartZ=0 EndX=7.06218 EndY=8.75 EndZ=0
    g16: LineSegment StartX=7.06218 StartY=8.75 StartZ=0 EndX=4.03109 EndY=10.5 EndZ=0
    g17: LineSegment StartX=4.03109 StartY=10.5 StartZ=0 EndX=1 EndY=8.75 EndZ=0
    g18: LineSegment StartX=1 StartY=8.75 StartZ=0 EndX=1 EndY=5.25 EndZ=0
    g19: LineSegment StartX=1 StartY=5.25 StartZ=0 EndX=4.03109 EndY=3.5 EndZ=0
    g20: Circle [constr] CenterX=4.03109 CenterY=7 CenterZ=0 NormalX=0 NormalY=0 NormalZ=1 AngleXU=0 Radius=3.5
    g21: LineSegment StartX=-1 StartY=5.25 StartZ=0 EndX=-1 EndY=8.75 EndZ=0
    g22: LineSegment StartX=-1 StartY=8.75 StartZ=0 EndX=-4.03109 EndY=10.5 EndZ=0
    g23: LineSegment StartX=-4.03109 StartY=10.5 StartZ=0 EndX=-7.06218 EndY=8.75 EndZ=0
    g24: LineSegment StartX=-7.06218 StartY=8.75 StartZ=0 EndX=-7.06218 EndY=5.25 EndZ=0
    g25: LineSegment StartX=-7.06218 StartY=5.25 StartZ=0 EndX=-4.03109 EndY=3.5 EndZ=0
    g26: LineSegment StartX=-4.03109 StartY=3.5 StartZ=0 EndX=-1 EndY=5.25 EndZ=0
    g27: Circle [constr] CenterX=-4.03109 CenterY=7 CenterZ=0 NormalX=0 NormalY=0 NormalZ=1 AngleXU=0 Radius=3.5
    g28: LineSegment StartX=-4.96891 StartY=-1.75 StartZ=0 EndX=-4.96891 EndY=1.75 EndZ=0
    g29: LineSegment StartX=-4.96891 StartY=1.75 StartZ=0 EndX=-8 EndY=3.5 EndZ=0
    g30: LineSegment StartX=-8 StartY=3.5 StartZ=0 EndX=-11.0311 EndY=1.75 EndZ=0
    g31: LineSegment StartX=-11.0311 StartY=1.75 StartZ=0 EndX=-11.0311 EndY=-1.75 EndZ=0
    g32: LineSegment StartX=-11.0311 StartY=-1.75 StartZ=0 EndX=-8 EndY=-3.5 EndZ=0
    g33: LineSegment StartX=-8 StartY=-3.5 StartZ=0 EndX=-4.96891 EndY=-1.75 EndZ=0
    g34: Circle [constr] CenterX=-8 CenterY=0 CenterZ=0 NormalX=0 NormalY=0 NormalZ=1 AngleXU=0 Radius=3.5
    g35: LineSegment StartX=-4.03109 StartY=-3.5 StartZ=0 EndX=-7.06218 EndY=-5.25 EndZ=0
    g36: LineSegment StartX=-7.06218 StartY=-5.25 StartZ=0 EndX=-7.06218 EndY=-8.75 EndZ=0
    g37: LineSegment StartX=-7.06218 StartY=-8.75 StartZ=0 EndX=-4.03109 EndY=-10.5 EndZ=0
    g38: LineSegment StartX=-4.03109 StartY=-10.5 StartZ=0 EndX=-1 EndY=-8.75 EndZ=0
    g39: LineSegment StartX=-1 StartY=-8.75 StartZ=0 EndX=-1 EndY=-5.25 EndZ=0
    g40: LineSegment StartX=-1 StartY=-5.25 StartZ=0 EndX=-4.03109 EndY=-3.5 EndZ=0
    g41: Circle [constr] CenterX=-4.03109 CenterY=-7 CenterZ=0 NormalX=0 NormalY=0 NormalZ=1 AngleXU=0 Radius=3.5
    g42: LineSegment StartX=4.03109 StartY=-3.5 StartZ=0 EndX=1 EndY=-5.25 EndZ=0
    g43: LineSegment StartX=1 StartY=-5.25 StartZ=0 EndX=1 EndY=-8.75 EndZ=0
    g44: LineSegment StartX=1 StartY=-8.75 StartZ=0 EndX=4.03109 EndY=-10.5 EndZ=0
    g45: LineSegment StartX=4.03109 StartY=-10.5 StartZ=0 EndX=7.06218 EndY=-8.75 EndZ=0
    g46: LineSegment StartX=7.06218 StartY=-8.75 StartZ=0 EndX=7.06218 EndY=-5.25 EndZ=0
    g47: LineSegment StartX=7.06218 StartY=-5.25 StartZ=0 EndX=4.03109 EndY=-3.5 EndZ=0
    g48: Circle [constr] CenterX=4.03109 CenterY=-7 CenterZ=0 NormalX=0 NormalY=0 NormalZ=1 AngleXU=0 Radius=3.5
  constraints (117):
    c: Coincident(g0,g1)
    c: Coincident(g1,g2)
    c: Coincident(g2,g3)
    c: Coincident(g3,g4)
    c: Coincident(g4,g5)
    c: Coincident(g5,g0)
    c: Equal(g0, g1-g5) x5
    c: PointOnObject(g0,g6)
    c: PointOnObject(g1,g6)
    c: PointOnObject(g2,g6)
    c: PointOnObject(g3,g6)
    c: PointOnObject(g4,g6)
    c: PointOnObject(g5,g6)
    c: Coincident(g6,g-1)
    c: Diameter(g6) = 7
    c: PointOnObject(g0,g-2)
    c: Coincident(g7,g8)
    c: Coincident(g8,g9)
    c: Coincident(g9,g10)
    c: Coincident(g10,g11)
    c: Coincident(g11,g12)
    c: Coincident(g12,g7)
    c: Equal(g7, g8-g12) x5
    c: PointOnObject(g7,g13)
    c: PointOnObject(g8,g13)
    c: PointOnObject(g9,g13)
    c: PointOnObject(g10,g13)
    c: PointOnObject(g11,g13)
    c: PointOnObject(g12,g13)
    c: PointOnObject(g13,g-1)
    c: Diameter(g13) = 7
    c: Distance(g6,g13) = 8
    c: Horizontal(g0,g10)
    c: Coincident(g14,g15)
    c: Coincident(g15,g16)
    c: Coincident(g16,g17)
    c: Coincident(g17,g18)
    c: Coincident(g18,g19)
    c: Coincident(g19,g14)
    c: Equal(g14, g15-g19) x5
    c: PointOnObject(g14,g20)
    c: PointOnObject(g15,g20)
    c: PointOnObject(g16,g20)
    c: PointOnObject(g17,g20)
    c: PointOnObject(g18,g20)
    c: PointOnObject(g19,g20)
    c: Diameter(g20) = 7
    c: DistanceY(g-1,g20) = 7
    c: Vertical(g18)
    c: Distance(g17,g-2) = 1
    c: Coincident(g21,g22)
    c: Coincident(g22,g23)
    c: Coincident(g23,g24)
    c: Coincident(g24,g25)
    c: Coincident(g25,g26)
    c: Coincident(g26,g21)
    c: Equal(g21, g22-g26) x5
    c: PointOnObject(g21,g27)
    c: PointOnObject(g22,g27)
    c: PointOnObject(g23,g27)
    c: PointOnObject(g24,g27)
    c: PointOnObject(g25,g27)
    c: PointOnObject(g26,g27)
    c: Diameter(g27) = 7
    c: DistanceY(g-1,g27) = 7
    c: DistanceX(g21,g-1) = 1
    c: Vertical(g21)
    c: Coincident(g28,g29)
    c: Coincident(g29,g30)
    c: Coincident(g30,g31)
    c: Coincident(g31,g32)
    c: Coincident(g32,g33)
    c: Coincident(g33,g28)
    c: Equal(g28, g29-g33) x5
    c: PointOnObject(g28,g34)
    c: PointOnObject(g29,g34)
    c: PointOnObject(g30,g34)
    c: PointOnObject(g31,g34)
    c: PointOnObject(g32,g34)
    c: PointOnObject(g33,g34)
    c: PointOnObject(g34,g-1)
    c: Diameter(g34) = 7
    c: Vertical(g31)
    c: DistanceX(g34,g-1) = 8
    c: Coincident(g35,g36)
    c: Coincident(g36,g37)
    c: Coincident(g37,g38)
    c: Coincident(g38,g39)
    c: Coincident(g39,g40)
    c: Coincident(g40,g35)
    c: Equal(g35, g36-g40) x5
    c: PointOnObject(g35,g41)
    c: PointOnObject(g36,g41)
    c: PointOnObject(g37,g41)
    c: PointOnObject(g38,g41)
    c: PointOnObject(g39,g41)
    c: PointOnObject(g40,g41)
    c: Coincident(g42,g43)
    c: Coincident(g43,g44)
    c: Coincident(g44,g45)
    c: Coincident(g45,g46)
    c: Coincident(g46,g47)
    c: Coincident(g47,g42)
    c: Equal(g42, g43-g47) x5
    c: PointOnObject(g42,g48)
    c: PointOnObject(g43,g48)
    c: PointOnObject(g44,g48)
    c: PointOnObject(g45,g48)
    c: PointOnObject(g46,g48)
    c: PointOnObject(g47,g48)
    c: Equal(g41,g48)
    c: Diameter(g41) = 7
    c: Vertical(g39)
    c: Vertical(g43)
    c: Distance(g-2,g39) = 1
    c: Symmetric(g38,g43,g-2)
    c: Distance(g41,g-1) = 7
FEATURE [Part::Extrusion] Extrude635  label="hex237"
  Base = -> Sketch644
  Dir = (0,-1,2e-16)
  DirMode = 2
  FaceMakerClass = Part::FaceMakerBullseye
  FaceMakerMode = 3
  LengthFwd = 10
  LengthRev = 0
  Placement = pos=(52,0,-21) rot=(0,0,1;0rad)
  Solid = true
  Symmetric = false
FEATURE [Sketcher::SketchObject] Sketch645
  ArcFitTolerance = 1e-06
  FullyConstrained = true
  MakeInternals = false
  Placement = pos=(0,0,0) rot=(1,0,0;1.5708rad)
  sketch-geometry (49):
    g0: LineSegment StartX=1e-16 StartY=3.5 StartZ=0 EndX=-3.03109 EndY=1.75 EndZ=0
    g1: LineSegment StartX=-3.03109 StartY=1.75 StartZ=0 EndX=-3.03109 EndY=-1.75 EndZ=0
    g2: LineSegment StartX=-3.03109 StartY=-1.75 StartZ=0 EndX=-1e-16 EndY=-3.5 EndZ=0
    g3: LineSegment StartX=-1e-16 StartY=-3.5 StartZ=0 EndX=3.03109 EndY=-1.75 EndZ=0
    g4: LineSegment StartX=3.03109 StartY=-1.75 StartZ=0 EndX=3.03109 EndY=1.75 EndZ=0
    g5: LineSegment StartX=3.03109 StartY=1.75 StartZ=0 EndX=1e-16 EndY=3.5 EndZ=0
    g6: Circle [constr] CenterX=0 CenterY=0 CenterZ=0 NormalX=0 NormalY=0 NormalZ=1 AngleXU=0 Radius=3.5
    g7: LineSegment StartX=4.96892 StartY=-1.75002 StartZ=0 EndX=8.00002 EndY=-3.5 EndZ=0
    g8: LineSegment StartX=8.00002 StartY=-3.5 StartZ=0 EndX=11.0311 EndY=-1.74998 EndZ=0
    g9: LineSegment StartX=11.0311 StartY=-1.74998 StartZ=0 EndX=11.0311 EndY=1.75002 EndZ=0
    g10: LineSegment StartX=11.0311 StartY=1.75002 StartZ=0 EndX=7.99998 EndY=3.5 EndZ=0
    g11: LineSegment StartX=7.99998 StartY=3.5 StartZ=0 EndX=4.9689 EndY=1.74998 EndZ=0
    g12: LineSegment StartX=4.9689 StartY=1.74998 StartZ=0 EndX=4.96892 EndY=-1.75002 EndZ=0
    g13: Circle [constr] CenterX=8 CenterY=0 CenterZ=0 NormalX=0 NormalY=0 NormalZ=1 AngleXU=0 Radius=3.5
    g14: LineSegment StartX=4.03109 StartY=3.5 StartZ=0 EndX=7.06218 EndY=5.25 EndZ=0
    g15: LineSegment StartX=7.06218 StartY=5.25 StartZ=0 EndX=7.06218 EndY=8.75 EndZ=0
    g16: LineSegment StartX=7.06218 StartY=8.75 StartZ=0 EndX=4.03109 EndY=10.5 EndZ=0
    g17: LineSegment StartX=4.03109 StartY=10.5 StartZ=0 EndX=1 EndY=8.75 EndZ=0
    g18: LineSegment StartX=1 StartY=8.75 StartZ=0 EndX=1 EndY=5.25 EndZ=0
    g19: LineSegment StartX=1 StartY=5.25 StartZ=0 EndX=4.03109 EndY=3.5 EndZ=0
    g20: Circle [constr] CenterX=4.03109 CenterY=7 CenterZ=0 NormalX=0 NormalY=0 NormalZ=1 AngleXU=0 Radius=3.5
    g21: LineSegment StartX=-1 StartY=5.25 StartZ=0 EndX=-1 EndY=8.75 EndZ=0
    g22: LineSegment StartX=-1 StartY=8.75 StartZ=0 EndX=-4.03109 EndY=10.5 EndZ=0
    g23: LineSegment StartX=-4.03109 StartY=10.5 StartZ=0 EndX=-7.06218 EndY=8.75 EndZ=0
    g24: LineSegment StartX=-7.06218 StartY=8.75 StartZ=0 EndX=-7.06218 EndY=5.25 EndZ=0
    g25: LineSegment StartX=-7.06218 StartY=5.25 StartZ=0 EndX=-4.03109 EndY=3.5 EndZ=0
    g26: LineSegment StartX=-4.03109 StartY=3.5 StartZ=0 EndX=-1 EndY=5.25 EndZ=0
    g27: Circle [constr] CenterX=-4.03109 CenterY=7 CenterZ=0 NormalX=0 NormalY=0 NormalZ=1 AngleXU=0 Radius=3.5
    g28: LineSegment StartX=-4.96891 StartY=-1.75 StartZ=0 EndX=-4.96891 EndY=1.75 EndZ=0
    g29: LineSegment StartX=-4.96891 StartY=1.75 StartZ=0 EndX=-8 EndY=3.5 EndZ=0
    g30: LineSegment StartX=-8 StartY=3.5 StartZ=0 EndX=-11.0311 EndY=1.75 EndZ=0
    g31: LineSegment StartX=-11.0311 StartY=1.75 StartZ=0 EndX=-11.0311 EndY=-1.75 EndZ=0
    g32: LineSegment StartX=-11.0311 StartY=-1.75 StartZ=0 EndX=-8 EndY=-3.5 EndZ=0
    g33: LineSegment StartX=-8 StartY=-3.5 StartZ=0 EndX=-4.96891 EndY=-1.75 EndZ=0
    g34: Circle [constr] CenterX=-8 CenterY=0 CenterZ=0 NormalX=0 NormalY=0 NormalZ=1 AngleXU=0 Radius=3.5
    g35: LineSegment StartX=-4.03109 StartY=-3.5 StartZ=0 EndX=-7.06218 EndY=-5.25 EndZ=0
    g36: LineSegment StartX=-7.06218 StartY=-5.25 StartZ=0 EndX=-7.06218 EndY=-8.75 EndZ=0
    g37: LineSegment StartX=-7.06218 StartY=-8.75 StartZ=0 EndX=-4.03109 EndY=-10.5 EndZ=0
    g38: LineSegment StartX=-4.03109 StartY=-10.5 StartZ=0 EndX=-1 EndY=-8.75 EndZ=0
    g39: LineSegment StartX=-1 StartY=-8.75 StartZ=0 EndX=-1 EndY=-5.25 EndZ=0
    g40: LineSegment StartX=-1 StartY=-5.25 StartZ=0 EndX=-4.03109 EndY=-3.5 EndZ=0
    g41: Circle [constr] CenterX=-4.03109 CenterY=-7 CenterZ=0 NormalX=0 NormalY=0 NormalZ=1 AngleXU=0 Radius=3.5
    g42: LineSegment StartX=4.03109 StartY=-3.5 StartZ=0 EndX=1 EndY=-5.25 EndZ=0
    g43: LineSegment StartX=1 StartY=-5.25 StartZ=0 EndX=1 EndY=-8.75 EndZ=0
    g44: LineSegment StartX=1 StartY=-8.75 StartZ=0 EndX=4.03109 EndY=-10.5 EndZ=0
    g45: LineSegment StartX=4.03109 StartY=-10.5 StartZ=0 EndX=7.06218 EndY=-8.75 EndZ=0
    g46: LineSegment StartX=7.06218 StartY=-8.75 StartZ=0 EndX=7.06218 EndY=-5.25 EndZ=0
    g47: LineSegment StartX=7.06218 StartY=-5.25 StartZ=0 EndX=4.03109 EndY=-3.5 EndZ=0
    g48: Circle [constr] CenterX=4.03109 CenterY=-7 CenterZ=0 NormalX=0 NormalY=0 NormalZ=1 AngleXU=0 Radius=3.5
  constraints (117):
    c: Coincident(g0,g1)
    c: Coincident(g1,g2)
    c: Coincident(g2,g3)
    c: Coincident(g3,g4)
    c: Coincident(g4,g5)
    c: Coincident(g5,g0)
    c: Equal(g0, g1-g5) x5
    c: PointOnObject(g0,g6)
    c: PointOnObject(g1,g6)
    c: PointOnObject(g2,g6)
    c: PointOnObject(g3,g6)
    c: PointOnObject(g4,g6)
    c: PointOnObject(g5,g6)
    c: Coincident(g6,g-1)
    c: Diameter(g6) = 7
    c: PointOnObject(g0,g-2)
    c: Coincident(g7,g8)
    c: Coincident(g8,g9)
    c: Coincident(g9,g10)
    c: Coincident(g10,g11)
    c: Coincident(g11,g12)
    c: Coincident(g12,g7)
    c: Equal(g7, g8-g12) x5
    c: PointOnObject(g7,g13)
    c: PointOnObject(g8,g13)
    c: PointOnObject(g9,g13)
    c: PointOnObject(g10,g13)
    c: PointOnObject(g11,g13)
    c: PointOnObject(g12,g13)
    c: PointOnObject(g13,g-1)
    c: Diameter(g13) = 7
    c: Distance(g6,g13) = 8
    c: Horizontal(g0,g10)
    c: Coincident(g14,g15)
    c: Coincident(g15,g16)
    c: Coincident(g16,g17)
    c: Coincident(g17,g18)
    c: Coincident(g18,g19)
    c: Coincident(g19,g14)
    c: Equal(g14, g15-g19) x5
    c: PointOnObject(g14,g20)
    c: PointOnObject(g15,g20)
    c: PointOnObject(g16,g20)
    c: PointOnObject(g17,g20)
    c: PointOnObject(g18,g20)
    c: PointOnObject(g19,g20)
    c: Diameter(g20) = 7
    c: DistanceY(g-1,g20) = 7
    c: Vertical(g18)
    c: Distance(g17,g-2) = 1
    c: Coincident(g21,g22)
    c: Coincident(g22,g23)
    c: Coincident(g23,g24)
    c: Coincident(g24,g25)
    c: Coincident(g25,g26)
    c: Coincident(g26,g21)
    c: Equal(g21, g22-g26) x5
    c: PointOnObject(g21,g27)
    c: PointOnObject(g22,g27)
    c: PointOnObject(g23,g27)
    c: PointOnObject(g24,g27)
    c: PointOnObject(g25,g27)
    c: PointOnObject(g26,g27)
    c: Diameter(g27) = 7
    c: DistanceY(g-1,g27) = 7
    c: DistanceX(g21,g-1) = 1
    c: Vertical(g21)
    c: Coincident(g28,g29)
    c: Coincident(g29,g30)
    c: Coincident(g30,g31)
    c: Coincident(g31,g32)
    c: Coincident(g32,g33)
    c: Coincident(g33,g28)
    c: Equal(g28, g29-g33) x5
    c: PointOnObject(g28,g34)
    c: PointOnObject(g29,g34)
    c: PointOnObject(g30,g34)
    c: PointOnObject(g31,g34)
    c: PointOnObject(g32,g34)
    c: PointOnObject(g33,g34)
    c: PointOnObject(g34,g-1)
    c: Diameter(g34) = 7
    c: Vertical(g31)
    c: DistanceX(g34,g-1) = 8
    c: Coincident(g35,g36)
    c: Coincident(g36,g37)
    c: Coincident(g37,g38)
    c: Coincident(g38,g39)
    c: Coincident(g39,g40)
    c: Coincident(g40,g35)
    c: Equal(g35, g36-g40) x5
    c: PointOnObject(g35,g41)
    c: PointOnObject(g36,g41)
    c: PointOnObject(g37,g41)
    c: PointOnObject(g38,g41)
    c: PointOnObject(g39,g41)
    c: PointOnObject(g40,g41)
    c: Coincident(g42,g43)
    c: Coincident(g43,g44)
    c: Coincident(g44,g45)
    c: Coincident(g45,g46)
    c: Coincident(g46,g47)
    c: Coincident(g47,g42)
    c: Equal(g42, g43-g47) x5
    c: PointOnObject(g42,g48)
    c: PointOnObject(g43,g48)
    c: PointOnObject(g44,g48)
    c: PointOnObject(g45,g48)
    c: PointOnObject(g46,g48)
    c: PointOnObject(g47,g48)
    c: Equal(g41,g48)
    c: Diameter(g41) = 7
    c: Vertical(g39)
    c: Vertical(g43)
    c: Distance(g-2,g39) = 1
    c: Symmetric(g38,g43,g-2)
    c: Distance(g41,g-1) = 7
FEATURE [Part::Extrusion] Extrude636  label="hex238"
  Base = -> Sketch645
  Dir = (0,-1,2e-16)
  DirMode = 2
  FaceMakerClass = Part::FaceMakerBullseye
  FaceMakerMode = 3
  LengthFwd = 10
  LengthRev = 0
  Placement = pos=(-56,0,0) rot=(0,0,1;0rad)
  Solid = true
  Symmetric = false
FEATURE [Sketcher::SketchObject] Sketch646
  ArcFitTolerance = 1e-06
  FullyConstrained = true
  MakeInternals = false
  Placement = pos=(0,0,0) rot=(1,0,0;1.5708rad)
  sketch-geometry (49):
    g0: LineSegment StartX=1e-16 StartY=3.5 StartZ=0 EndX=-3.03109 EndY=1.75 EndZ=0
    g1: LineSegment StartX=-3.03109 StartY=1.75 StartZ=0 EndX=-3.03109 EndY=-1.75 EndZ=0
    g2: LineSegment StartX=-3.03109 StartY=-1.75 StartZ=0 EndX=-1e-16 EndY=-3.5 EndZ=0
    g3: LineSegment StartX=-1e-16 StartY=-3.5 StartZ=0 EndX=3.03109 EndY=-1.75 EndZ=0
    g4: LineSegment StartX=3.03109 StartY=-1.75 StartZ=0 EndX=3.03109 EndY=1.75 EndZ=0
    g5: LineSegment StartX=3.03109 StartY=1.75 StartZ=0 EndX=1e-16 EndY=3.5 EndZ=0
    g6: Circle [constr] CenterX=0 CenterY=0 CenterZ=0 NormalX=0 NormalY=0 NormalZ=1 AngleXU=0 Radius=3.5
    g7: LineSegment StartX=4.96892 StartY=-1.75002 StartZ=0 EndX=8.00002 EndY=-3.5 EndZ=0
    g8: LineSegment StartX=8.00002 StartY=-3.5 StartZ=0 EndX=11.0311 EndY=-1.74998 EndZ=0
    g9: LineSegment StartX=11.0311 StartY=-1.74998 StartZ=0 EndX=11.0311 EndY=1.75002 EndZ=0
    g10: LineSegment StartX=11.0311 StartY=1.75002 StartZ=0 EndX=7.99998 EndY=3.5 EndZ=0
    g11: LineSegment StartX=7.99998 StartY=3.5 StartZ=0 EndX=4.9689 EndY=1.74998 EndZ=0
    g12: LineSegment StartX=4.9689 StartY=1.74998 StartZ=0 EndX=4.96892 EndY=-1.75002 EndZ=0
    g13: Circle [constr] CenterX=8 CenterY=0 CenterZ=0 NormalX=0 NormalY=0 NormalZ=1 AngleXU=0 Radius=3.5
    g14: LineSegment StartX=4.03109 StartY=3.5 StartZ=0 EndX=7.06218 EndY=5.25 EndZ=0
    g15: LineSegment StartX=7.06218 StartY=5.25 StartZ=0 EndX=7.06218 EndY=8.75 EndZ=0
    g16: LineSegment StartX=7.06218 StartY=8.75 StartZ=0 EndX=4.03109 EndY=10.5 EndZ=0
    g17: LineSegment StartX=4.03109 StartY=10.5 StartZ=0 EndX=1 EndY=8.75 EndZ=0
    g18: LineSegment StartX=1 StartY=8.75 StartZ=0 EndX=1 EndY=5.25 EndZ=0
    g19: LineSegment StartX=1 StartY=5.25 StartZ=0 EndX=4.03109 EndY=3.5 EndZ=0
    g20: Circle [constr] CenterX=4.03109 CenterY=7 CenterZ=0 NormalX=0 NormalY=0 NormalZ=1 AngleXU=0 Radius=3.5
    g21: LineSegment StartX=-1 StartY=5.25 StartZ=0 EndX=-1 EndY=8.75 EndZ=0
    g22: LineSegment StartX=-1 StartY=8.75 StartZ=0 EndX=-4.03109 EndY=10.5 EndZ=0
    g23: LineSegment StartX=-4.03109 StartY=10.5 StartZ=0 EndX=-7.06218 EndY=8.75 EndZ=0
    g24: LineSegment StartX=-7.06218 StartY=8.75 StartZ=0 EndX=-7.06218 EndY=5.25 EndZ=0
    g25: LineSegment StartX=-7.06218 StartY=5.25 StartZ=0 EndX=-4.03109 EndY=3.5 EndZ=0
    g26: LineSegment StartX=-4.03109 StartY=3.5 StartZ=0 EndX=-1 EndY=5.25 EndZ=0
    g27: Circle [constr] CenterX=-4.03109 CenterY=7 CenterZ=0 NormalX=0 NormalY=0 NormalZ=1 AngleXU=0 Radius=3.5
    g28: LineSegment StartX=-4.96891 StartY=-1.75 StartZ=0 EndX=-4.96891 EndY=1.75 EndZ=0
    g29: LineSegment StartX=-4.96891 StartY=1.75 StartZ=0 EndX=-8 EndY=3.5 EndZ=0
    g30: LineSegment StartX=-8 StartY=3.5 StartZ=0 EndX=-11.0311 EndY=1.75 EndZ=0
    g31: LineSegment StartX=-11.0311 StartY=1.75 StartZ=0 EndX=-11.0311 EndY=-1.75 EndZ=0
    g32: LineSegment StartX=-11.0311 StartY=-1.75 StartZ=0 EndX=-8 EndY=-3.5 EndZ=0
    g33: LineSegment StartX=-8 StartY=-3.5 StartZ=0 EndX=-4.96891 EndY=-1.75 EndZ=0
    g34: Circle [constr] CenterX=-8 CenterY=0 CenterZ=0 NormalX=0 NormalY=0 NormalZ=1 AngleXU=0 Radius=3.5
    g35: LineSegment StartX=-4.03109 StartY=-3.5 StartZ=0 EndX=-7.06218 EndY=-5.25 EndZ=0
    g36: LineSegment StartX=-7.06218 StartY=-5.25 StartZ=0 EndX=-7.06218 EndY=-8.75 EndZ=0
    g37: LineSegment StartX=-7.06218 StartY=-8.75 StartZ=0 EndX=-4.03109 EndY=-10.5 EndZ=0
    g38: LineSegment StartX=-4.03109 StartY=-10.5 StartZ=0 EndX=-1 EndY=-8.75 EndZ=0
    g39: LineSegment StartX=-1 StartY=-8.75 StartZ=0 EndX=-1 EndY=-5.25 EndZ=0
    g40: LineSegment StartX=-1 StartY=-5.25 StartZ=0 EndX=-4.03109 EndY=-3.5 EndZ=0
    g41: Circle [constr] CenterX=-4.03109 CenterY=-7 CenterZ=0 NormalX=0 NormalY=0 NormalZ=1 AngleXU=0 Radius=3.5
    g42: LineSegment StartX=4.03109 StartY=-3.5 StartZ=0 EndX=1 EndY=-5.25 EndZ=0
    g43: LineSegment StartX=1 StartY=-5.25 StartZ=0 EndX=1 EndY=-8.75 EndZ=0
    g44: LineSegment StartX=1 StartY=-8.75 StartZ=0 EndX=4.03109 EndY=-10.5 EndZ=0
    g45: LineSegment StartX=4.03109 StartY=-10.5 StartZ=0 EndX=7.06218 EndY=-8.75 EndZ=0
    g46: LineSegment StartX=7.06218 StartY=-8.75 StartZ=0 EndX=7.06218 EndY=-5.25 EndZ=0
    g47: LineSegment StartX=7.06218 StartY=-5.25 StartZ=0 EndX=4.03109 EndY=-3.5 EndZ=0
    g48: Circle [constr] CenterX=4.03109 CenterY=-7 CenterZ=0 NormalX=0 NormalY=0 NormalZ=1 AngleXU=0 Radius=3.5
  constraints (117):
    c: Coincident(g0,g1)
    c: Coincident(g1,g2)
    c: Coincident(g2,g3)
    c: Coincident(g3,g4)
    c: Coincident(g4,g5)
    c: Coincident(g5,g0)
    c: Equal(g0, g1-g5) x5
    c: PointOnObject(g0,g6)
    c: PointOnObject(g1,g6)
    c: PointOnObject(g2,g6)
    c: PointOnObject(g3,g6)
    c: PointOnObject(g4,g6)
    c: PointOnObject(g5,g6)
    c: Coincident(g6,g-1)
    c: Diameter(g6) = 7
    c: PointOnObject(g0,g-2)
    c: Coincident(g7,g8)
    c: Coincident(g8,g9)
    c: Coincident(g9,g10)
    c: Coincident(g10,g11)
    c: Coincident(g11,g12)
    c: Coincident(g12,g7)
    c: Equal(g7, g8-g12) x5
    c: PointOnObject(g7,g13)
    c: PointOnObject(g8,g13)
    c: PointOnObject(g9,g13)
    c: PointOnObject(g10,g13)
    c: PointOnObject(g11,g13)
    c: PointOnObject(g12,g13)
    c: PointOnObject(g13,g-1)
    c: Diameter(g13) = 7
    c: Distance(g6,g13) = 8
    c: Horizontal(g0,g10)
    c: Coincident(g14,g15)
    c: Coincident(g15,g16)
    c: Coincident(g16,g17)
    c: Coincident(g17,g18)
    c: Coincident(g18,g19)
    c: Coincident(g19,g14)
    c: Equal(g14, g15-g19) x5
    c: PointOnObject(g14,g20)
    c: PointOnObject(g15,g20)
    c: PointOnObject(g16,g20)
    c: PointOnObject(g17,g20)
    c: PointOnObject(g18,g20)
    c: PointOnObject(g19,g20)
    c: Diameter(g20) = 7
    c: DistanceY(g-1,g20) = 7
    c: Vertical(g18)
    c: Distance(g17,g-2) = 1
    c: Coincident(g21,g22)
    c: Coincident(g22,g23)
    c: Coincident(g23,g24)
    c: Coincident(g24,g25)
    c: Coincident(g25,g26)
    c: Coincident(g26,g21)
    c: Equal(g21, g22-g26) x5
    c: PointOnObject(g21,g27)
    c: PointOnObject(g22,g27)
    c: PointOnObject(g23,g27)
    c: PointOnObject(g24,g27)
    c: PointOnObject(g25,g27)
    c: PointOnObject(g26,g27)
    c: Diameter(g27) = 7
    c: DistanceY(g-1,g27) = 7
    c: DistanceX(g21,g-1) = 1
    c: Vertical(g21)
    c: Coincident(g28,g29)
    c: Coincident(g29,g30)
    c: Coincident(g30,g31)
    c: Coincident(g31,g32)
    c: Coincident(g32,g33)
    c: Coincident(g33,g28)
    c: Equal(g28, g29-g33) x5
    c: PointOnObject(g28,g34)
    c: PointOnObject(g29,g34)
    c: PointOnObject(g30,g34)
    c: PointOnObject(g31,g34)
    c: PointOnObject(g32,g34)
    c: PointOnObject(g33,g34)
    c: PointOnObject(g34,g-1)
    c: Diameter(g34) = 7
    c: Vertical(g31)
    c: DistanceX(g34,g-1) = 8
    c: Coincident(g35,g36)
    c: Coincident(g36,g37)
    c: Coincident(g37,g38)
    c: Coincident(g38,g39)
    c: Coincident(g39,g40)
    c: Coincident(g40,g35)
    c: Equal(g35, g36-g40) x5
    c: PointOnObject(g35,g41)
    c: PointOnObject(g36,g41)
    c: PointOnObject(g37,g41)
    c: PointOnObject(g38,g41)
    c: PointOnObject(g39,g41)
    c: PointOnObject(g40,g41)
    c: Coincident(g42,g43)
    c: Coincident(g43,g44)
    c: Coincident(g44,g45)
    c: Coincident(g45,g46)
    c: Coincident(g46,g47)
    c: Coincident(g47,g42)
    c: Equal(g42, g43-g47) x5
    c: PointOnObject(g42,g48)
    c: PointOnObject(g43,g48)
    c: PointOnObject(g44,g48)
    c: PointOnObject(g45,g48)
    c: PointOnObject(g46,g48)
    c: PointOnObject(g47,g48)
    c: Equal(g41,g48)
    c: Diameter(g41) = 7
    c: Vertical(g39)
    c: Vertical(g43)
    c: Distance(g-2,g39) = 1
    c: Symmetric(g38,g43,g-2)
    c: Distance(g41,g-1) = 7
FEATURE [Part::Extrusion] Extrude637  label="hex239"
  Base = -> Sketch646
  Dir = (0,-1,2e-16)
  DirMode = 2
  FaceMakerClass = Part::FaceMakerBullseye
  FaceMakerMode = 3
  LengthFwd = 10
  LengthRev = 0
  Placement = pos=(-52,0,21) rot=(0,0,1;0rad)
  Solid = true
  Symmetric = false
FEATURE [Sketcher::SketchObject] Sketch647
  ArcFitTolerance = 1e-06
  FullyConstrained = true
  MakeInternals = false
  Placement = pos=(0,0,0) rot=(1,0,0;1.5708rad)
  sketch-geometry (49):
    g0: LineSegment StartX=1e-16 StartY=3.5 StartZ=0 EndX=-3.03109 EndY=1.75 EndZ=0
    g1: LineSegment StartX=-3.03109 StartY=1.75 StartZ=0 EndX=-3.03109 EndY=-1.75 EndZ=0
    g2: LineSegment StartX=-3.03109 StartY=-1.75 StartZ=0 EndX=-1e-16 EndY=-3.5 EndZ=0
    g3: LineSegment StartX=-1e-16 StartY=-3.5 StartZ=0 EndX=3.03109 EndY=-1.75 EndZ=0
    g4: LineSegment StartX=3.03109 StartY=-1.75 StartZ=0 EndX=3.03109 EndY=1.75 EndZ=0
    g5: LineSegment StartX=3.03109 StartY=1.75 StartZ=0 EndX=1e-16 EndY=3.5 EndZ=0
    g6: Circle [constr] CenterX=0 CenterY=0 CenterZ=0 NormalX=0 NormalY=0 NormalZ=1 AngleXU=0 Radius=3.5
    g7: LineSegment StartX=4.96892 StartY=-1.75002 StartZ=0 EndX=8.00002 EndY=-3.5 EndZ=0
    g8: LineSegment StartX=8.00002 StartY=-3.5 StartZ=0 EndX=11.0311 EndY=-1.74998 EndZ=0
    g9: LineSegment StartX=11.0311 StartY=-1.74998 StartZ=0 EndX=11.0311 EndY=1.75002 EndZ=0
    g10: LineSegment StartX=11.0311 StartY=1.75002 StartZ=0 EndX=7.99998 EndY=3.5 EndZ=0
    g11: LineSegment StartX=7.99998 StartY=3.5 StartZ=0 EndX=4.9689 EndY=1.74998 EndZ=0
    g12: LineSegment StartX=4.9689 StartY=1.74998 StartZ=0 EndX=4.96892 EndY=-1.75002 EndZ=0
    g13: Circle [constr] CenterX=8 CenterY=0 CenterZ=0 NormalX=0 NormalY=0 NormalZ=1 AngleXU=0 Radius=3.5
    g14: LineSegment StartX=4.03109 StartY=3.5 StartZ=0 EndX=7.06218 EndY=5.25 EndZ=0
    g15: LineSegment StartX=7.06218 StartY=5.25 StartZ=0 EndX=7.06218 EndY=8.75 EndZ=0
    g16: LineSegment StartX=7.06218 StartY=8.75 StartZ=0 EndX=4.03109 EndY=10.5 EndZ=0
    g17: LineSegment StartX=4.03109 StartY=10.5 StartZ=0 EndX=1 EndY=8.75 EndZ=0
    g18: LineSegment StartX=1 StartY=8.75 StartZ=0 EndX=1 EndY=5.25 EndZ=0
    g19: LineSegment StartX=1 StartY=5.25 StartZ=0 EndX=4.03109 EndY=3.5 EndZ=0
    g20: Circle [constr] CenterX=4.03109 CenterY=7 CenterZ=0 NormalX=0 NormalY=0 NormalZ=1 AngleXU=0 Radius=3.5
    g21: LineSegment StartX=-1 StartY=5.25 StartZ=0 EndX=-1 EndY=8.75 EndZ=0
    g22: LineSegment StartX=-1 StartY=8.75 StartZ=0 EndX=-4.03109 EndY=10.5 EndZ=0
    g23: LineSegment StartX=-4.03109 StartY=10.5 StartZ=0 EndX=-7.06218 EndY=8.75 EndZ=0
    g24: LineSegment StartX=-7.06218 StartY=8.75 StartZ=0 EndX=-7.06218 EndY=5.25 EndZ=0
    g25: LineSegment StartX=-7.06218 StartY=5.25 StartZ=0 EndX=-4.03109 EndY=3.5 EndZ=0
    g26: LineSegment StartX=-4.03109 StartY=3.5 StartZ=0 EndX=-1 EndY=5.25 EndZ=0
    g27: Circle [constr] CenterX=-4.03109 CenterY=7 CenterZ=0 NormalX=0 NormalY=0 NormalZ=1 AngleXU=0 Radius=3.5
    g28: LineSegment StartX=-4.96891 StartY=-1.75 StartZ=0 EndX=-4.96891 EndY=1.75 EndZ=0
    g29: LineSegment StartX=-4.96891 StartY=1.75 StartZ=0 EndX=-8 EndY=3.5 EndZ=0
    g30: LineSegment StartX=-8 StartY=3.5 StartZ=0 EndX=-11.0311 EndY=1.75 EndZ=0
    g31: LineSegment StartX=-11.0311 StartY=1.75 StartZ=0 EndX=-11.0311 EndY=-1.75 EndZ=0
    g32: LineSegment StartX=-11.0311 StartY=-1.75 StartZ=0 EndX=-8 EndY=-3.5 EndZ=0
    g33: LineSegment StartX=-8 StartY=-3.5 StartZ=0 EndX=-4.96891 EndY=-1.75 EndZ=0
    g34: Circle [constr] CenterX=-8 CenterY=0 CenterZ=0 NormalX=0 NormalY=0 NormalZ=1 AngleXU=0 Radius=3.5
    g35: LineSegment StartX=-4.03109 StartY=-3.5 StartZ=0 EndX=-7.06218 EndY=-5.25 EndZ=0
    g36: LineSegment StartX=-7.06218 StartY=-5.25 StartZ=0 EndX=-7.06218 EndY=-8.75 EndZ=0
    g37: LineSegment StartX=-7.06218 StartY=-8.75 StartZ=0 EndX=-4.03109 EndY=-10.5 EndZ=0
    g38: LineSegment StartX=-4.03109 StartY=-10.5 StartZ=0 EndX=-1 EndY=-8.75 EndZ=0
    g39: LineSegment StartX=-1 StartY=-8.75 StartZ=0 EndX=-1 EndY=-5.25 EndZ=0
    g40: LineSegment StartX=-1 StartY=-5.25 StartZ=0 EndX=-4.03109 EndY=-3.5 EndZ=0
    g41: Circle [constr] CenterX=-4.03109 CenterY=-7 CenterZ=0 NormalX=0 NormalY=0 NormalZ=1 AngleXU=0 Radius=3.5
    g42: LineSegment StartX=4.03109 StartY=-3.5 StartZ=0 EndX=1 EndY=-5.25 EndZ=0
    g43: LineSegment StartX=1 StartY=-5.25 StartZ=0 EndX=1 EndY=-8.75 EndZ=0
    g44: LineSegment StartX=1 StartY=-8.75 StartZ=0 EndX=4.03109 EndY=-10.5 EndZ=0
    g45: LineSegment StartX=4.03109 StartY=-10.5 StartZ=0 EndX=7.06218 EndY=-8.75 EndZ=0
    g46: LineSegment StartX=7.06218 StartY=-8.75 StartZ=0 EndX=7.06218 EndY=-5.25 EndZ=0
    g47: LineSegment StartX=7.06218 StartY=-5.25 StartZ=0 EndX=4.03109 EndY=-3.5 EndZ=0
    g48: Circle [constr] CenterX=4.03109 CenterY=-7 CenterZ=0 NormalX=0 NormalY=0 NormalZ=1 AngleXU=0 Radius=3.5
  constraints (117):
    c: Coincident(g0,g1)
    c: Coincident(g1,g2)
    c: Coincident(g2,g3)
    c: Coincident(g3,g4)
    c: Coincident(g4,g5)
    c: Coincident(g5,g0)
    c: Equal(g0, g1-g5) x5
    c: PointOnObject(g0,g6)
    c: PointOnObject(g1,g6)
    c: PointOnObject(g2,g6)
    c: PointOnObject(g3,g6)
    c: PointOnObject(g4,g6)
    c: PointOnObject(g5,g6)
    c: Coincident(g6,g-1)
    c: Diameter(g6) = 7
    c: PointOnObject(g0,g-2)
    c: Coincident(g7,g8)
    c: Coincident(g8,g9)
    c: Coincident(g9,g10)
    c: Coincident(g10,g11)
    c: Coincident(g11,g12)
    c: Coincident(g12,g7)
    c: Equal(g7, g8-g12) x5
    c: PointOnObject(g7,g13)
    c: PointOnObject(g8,g13)
    c: PointOnObject(g9,g13)
    c: PointOnObject(g10,g13)
    c: PointOnObject(g11,g13)
    c: PointOnObject(g12,g13)
    c: PointOnObject(g13,g-1)
    c: Diameter(g13) = 7
    c: Distance(g6,g13) = 8
    c: Horizontal(g0,g10)
    c: Coincident(g14,g15)
    c: Coincident(g15,g16)
    c: Coincident(g16,g17)
    c: Coincident(g17,g18)
    c: Coincident(g18,g19)
    c: Coincident(g19,g14)
    c: Equal(g14, g15-g19) x5
    c: PointOnObject(g14,g20)
    c: PointOnObject(g15,g20)
    c: PointOnObject(g16,g20)
    c: PointOnObject(g17,g20)
    c: PointOnObject(g18,g20)
    c: PointOnObject(g19,g20)
    c: Diameter(g20) = 7
    c: DistanceY(g-1,g20) = 7
    c: Vertical(g18)
    c: Distance(g17,g-2) = 1
    c: Coincident(g21,g22)
    c: Coincident(g22,g23)
    c: Coincident(g23,g24)
    c: Coincident(g24,g25)
    c: Coincident(g25,g26)
    c: Coincident(g26,g21)
    c: Equal(g21, g22-g26) x5
    c: PointOnObject(g21,g27)
    c: PointOnObject(g22,g27)
    c: PointOnObject(g23,g27)
    c: PointOnObject(g24,g27)
    c: PointOnObject(g25,g27)
    c: PointOnObject(g26,g27)
    c: Diameter(g27) = 7
    c: DistanceY(g-1,g27) = 7
    c: DistanceX(g21,g-1) = 1
    c: Vertical(g21)
    c: Coincident(g28,g29)
    c: Coincident(g29,g30)
    c: Coincident(g30,g31)
    c: Coincident(g31,g32)
    c: Coincident(g32,g33)
    c: Coincident(g33,g28)
    c: Equal(g28, g29-g33) x5
    c: PointOnObject(g28,g34)
    c: PointOnObject(g29,g34)
    c: PointOnObject(g30,g34)
    c: PointOnObject(g31,g34)
    c: PointOnObject(g32,g34)
    c: PointOnObject(g33,g34)
    c: PointOnObject(g34,g-1)
    c: Diameter(g34) = 7
    c: Vertical(g31)
    c: DistanceX(g34,g-1) = 8
    c: Coincident(g35,g36)
    c: Coincident(g36,g37)
    c: Coincident(g37,g38)
    c: Coincident(g38,g39)
    c: Coincident(g39,g40)
    c: Coincident(g40,g35)
    c: Equal(g35, g36-g40) x5
    c: PointOnObject(g35,g41)
    c: PointOnObject(g36,g41)
    c: PointOnObject(g37,g41)
    c: PointOnObject(g38,g41)
    c: PointOnObject(g39,g41)
    c: PointOnObject(g40,g41)
    c: Coincident(g42,g43)
    c: Coincident(g43,g44)
    c: Coincident(g44,g45)
    c: Coincident(g45,g46)
    c: Coincident(g46,g47)
    c: Coincident(g47,g42)
    c: Equal(g42, g43-g47) x5
    c: PointOnObject(g42,g48)
    c: PointOnObject(g43,g48)
    c: PointOnObject(g44,g48)
    c: PointOnObject(g45,g48)
    c: PointOnObject(g46,g48)
    c: PointOnObject(g47,g48)
    c: Equal(g41,g48)
    c: Diameter(g41) = 7
    c: Vertical(g39)
    c: Vertical(g43)
    c: Distance(g-2,g39) = 1
    c: Symmetric(g38,g43,g-2)
    c: Distance(g41,g-1) = 7
FEATURE [Part::Extrusion] Extrude638  label="hex240"
  Base = -> Sketch647
  Dir = (0,-1,2e-16)
  DirMode = 2
  FaceMakerClass = Part::FaceMakerBullseye
  FaceMakerMode = 3
  LengthFwd = 10
  LengthRev = 0
  Placement = pos=(52,0,21) rot=(0,0,1;0rad)
  Solid = true
  Symmetric = false
FEATURE [Sketcher::SketchObject] Sketch648
  ArcFitTolerance = 1e-06
  FullyConstrained = true
  MakeInternals = false
  Placement = pos=(0,0,0) rot=(1,0,0;1.5708rad)
  sketch-geometry (49):
    g0: LineSegment StartX=1e-16 StartY=3.5 StartZ=0 EndX=-3.03109 EndY=1.75 EndZ=0
    g1: LineSegment StartX=-3.03109 StartY=1.75 StartZ=0 EndX=-3.03109 EndY=-1.75 EndZ=0
    g2: LineSegment StartX=-3.03109 StartY=-1.75 StartZ=0 EndX=-1e-16 EndY=-3.5 EndZ=0
    g3: LineSegment StartX=-1e-16 StartY=-3.5 StartZ=0 EndX=3.03109 EndY=-1.75 EndZ=0
    g4: LineSegment StartX=3.03109 StartY=-1.75 StartZ=0 EndX=3.03109 EndY=1.75 EndZ=0
    g5: LineSegment StartX=3.03109 StartY=1.75 StartZ=0 EndX=1e-16 EndY=3.5 EndZ=0
    g6: Circle [constr] CenterX=0 CenterY=0 CenterZ=0 NormalX=0 NormalY=0 NormalZ=1 AngleXU=0 Radius=3.5
    g7: LineSegment StartX=4.96892 StartY=-1.75002 StartZ=0 EndX=8.00002 EndY=-3.5 EndZ=0
    g8: LineSegment StartX=8.00002 StartY=-3.5 StartZ=0 EndX=11.0311 EndY=-1.74998 EndZ=0
    g9: LineSegment StartX=11.0311 StartY=-1.74998 StartZ=0 EndX=11.0311 EndY=1.75002 EndZ=0
    g10: LineSegment StartX=11.0311 StartY=1.75002 StartZ=0 EndX=7.99998 EndY=3.5 EndZ=0
    g11: LineSegment StartX=7.99998 StartY=3.5 StartZ=0 EndX=4.9689 EndY=1.74998 EndZ=0
    g12: LineSegment StartX=4.9689 StartY=1.74998 StartZ=0 EndX=4.96892 EndY=-1.75002 EndZ=0
    g13: Circle [constr] CenterX=8 CenterY=0 CenterZ=0 NormalX=0 NormalY=0 NormalZ=1 AngleXU=0 Radius=3.5
    g14: LineSegment StartX=4.03109 StartY=3.5 StartZ=0 EndX=7.06218 EndY=5.25 EndZ=0
    g15: LineSegment StartX=7.06218 StartY=5.25 StartZ=0 EndX=7.06218 EndY=8.75 EndZ=0
    g16: LineSegment StartX=7.06218 StartY=8.75 StartZ=0 EndX=4.03109 EndY=10.5 EndZ=0
    g17: LineSegment StartX=4.03109 StartY=10.5 StartZ=0 EndX=1 EndY=8.75 EndZ=0
    g18: LineSegment StartX=1 StartY=8.75 StartZ=0 EndX=1 EndY=5.25 EndZ=0
    g19: LineSegment StartX=1 StartY=5.25 StartZ=0 EndX=4.03109 EndY=3.5 EndZ=0
    g20: Circle [constr] CenterX=4.03109 CenterY=7 CenterZ=0 NormalX=0 NormalY=0 NormalZ=1 AngleXU=0 Radius=3.5
    g21: LineSegment StartX=-1 StartY=5.25 StartZ=0 EndX=-1 EndY=8.75 EndZ=0
    g22: LineSegment StartX=-1 StartY=8.75 StartZ=0 EndX=-4.03109 EndY=10.5 EndZ=0
    g23: LineSegment StartX=-4.03109 StartY=10.5 StartZ=0 EndX=-7.06218 EndY=8.75 EndZ=0
    g24: LineSegment StartX=-7.06218 StartY=8.75 StartZ=0 EndX=-7.06218 EndY=5.25 EndZ=0
    g25: LineSegment StartX=-7.06218 StartY=5.25 StartZ=0 EndX=-4.03109 EndY=3.5 EndZ=0
    g26: LineSegment StartX=-4.03109 StartY=3.5 StartZ=0 EndX=-1 EndY=5.25 EndZ=0
    g27: Circle [constr] CenterX=-4.03109 CenterY=7 CenterZ=0 NormalX=0 NormalY=0 NormalZ=1 AngleXU=0 Radius=3.5
    g28: LineSegment StartX=-4.96891 StartY=-1.75 StartZ=0 EndX=-4.96891 EndY=1.75 EndZ=0
    g29: LineSegment StartX=-4.96891 StartY=1.75 StartZ=0 EndX=-8 EndY=3.5 EndZ=0
    g30: LineSegment StartX=-8 StartY=3.5 StartZ=0 EndX=-11.0311 EndY=1.75 EndZ=0
    g31: LineSegment StartX=-11.0311 StartY=1.75 StartZ=0 EndX=-11.0311 EndY=-1.75 EndZ=0
    g32: LineSegment StartX=-11.0311 StartY=-1.75 StartZ=0 EndX=-8 EndY=-3.5 EndZ=0
    g33: LineSegment StartX=-8 StartY=-3.5 StartZ=0 EndX=-4.96891 EndY=-1.75 EndZ=0
    g34: Circle [constr] CenterX=-8 CenterY=0 CenterZ=0 NormalX=0 NormalY=0 NormalZ=1 AngleXU=0 Radius=3.5
    g35: LineSegment StartX=-4.03109 StartY=-3.5 StartZ=0 EndX=-7.06218 EndY=-5.25 EndZ=0
    g36: LineSegment StartX=-7.06218 StartY=-5.25 StartZ=0 EndX=-7.06218 EndY=-8.75 EndZ=0
    g37: LineSegment StartX=-7.06218 StartY=-8.75 StartZ=0 EndX=-4.03109 EndY=-10.5 EndZ=0
    g38: LineSegment StartX=-4.03109 StartY=-10.5 StartZ=0 EndX=-1 EndY=-8.75 EndZ=0
    g39: LineSegment StartX=-1 StartY=-8.75 StartZ=0 EndX=-1 EndY=-5.25 EndZ=0
    g40: LineSegment StartX=-1 StartY=-5.25 StartZ=0 EndX=-4.03109 EndY=-3.5 EndZ=0
    g41: Circle [constr] CenterX=-4.03109 CenterY=-7 CenterZ=0 NormalX=0 NormalY=0 NormalZ=1 AngleXU=0 Radius=3.5
    g42: LineSegment StartX=4.03109 StartY=-3.5 StartZ=0 EndX=1 EndY=-5.25 EndZ=0
    g43: LineSegment StartX=1 StartY=-5.25 StartZ=0 EndX=1 EndY=-8.75 EndZ=0
    g44: LineSegment StartX=1 StartY=-8.75 StartZ=0 EndX=4.03109 EndY=-10.5 EndZ=0
    g45: LineSegment StartX=4.03109 StartY=-10.5 StartZ=0 EndX=7.06218 EndY=-8.75 EndZ=0
    g46: LineSegment StartX=7.06218 StartY=-8.75 StartZ=0 EndX=7.06218 EndY=-5.25 EndZ=0
    g47: LineSegment StartX=7.06218 StartY=-5.25 StartZ=0 EndX=4.03109 EndY=-3.5 EndZ=0
    g48: Circle [constr] CenterX=4.03109 CenterY=-7 CenterZ=0 NormalX=0 NormalY=0 NormalZ=1 AngleXU=0 Radius=3.5
  constraints (117):
    c: Coincident(g0,g1)
    c: Coincident(g1,g2)
    c: Coincident(g2,g3)
    c: Coincident(g3,g4)
    c: Coincident(g4,g5)
    c: Coincident(g5,g0)
    c: Equal(g0, g1-g5) x5
    c: PointOnObject(g0,g6)
    c: PointOnObject(g1,g6)
    c: PointOnObject(g2,g6)
    c: PointOnObject(g3,g6)
    c: PointOnObject(g4,g6)
    c: PointOnObject(g5,g6)
    c: Coincident(g6,g-1)
    c: Diameter(g6) = 7
    c: PointOnObject(g0,g-2)
    c: Coincident(g7,g8)
    c: Coincident(g8,g9)
    c: Coincident(g9,g10)
    c: Coincident(g10,g11)
    c: Coincident(g11,g12)
    c: Coincident(g12,g7)
    c: Equal(g7, g8-g12) x5
    c: PointOnObject(g7,g13)
    c: PointOnObject(g8,g13)
    c: PointOnObject(g9,g13)
    c: PointOnObject(g10,g13)
    c: PointOnObject(g11,g13)
    c: PointOnObject(g12,g13)
    c: PointOnObject(g13,g-1)
    c: Diameter(g13) = 7
    c: Distance(g6,g13) = 8
    c: Horizontal(g0,g10)
    c: Coincident(g14,g15)
    c: Coincident(g15,g16)
    c: Coincident(g16,g17)
    c: Coincident(g17,g18)
    c: Coincident(g18,g19)
    c: Coincident(g19,g14)
    c: Equal(g14, g15-g19) x5
    c: PointOnObject(g14,g20)
    c: PointOnObject(g15,g20)
    c: PointOnObject(g16,g20)
    c: PointOnObject(g17,g20)
    c: PointOnObject(g18,g20)
    c: PointOnObject(g19,g20)
    c: Diameter(g20) = 7
    c: DistanceY(g-1,g20) = 7
    c: Vertical(g18)
    c: Distance(g17,g-2) = 1
    c: Coincident(g21,g22)
    c: Coincident(g22,g23)
    c: Coincident(g23,g24)
    c: Coincident(g24,g25)
    c: Coincident(g25,g26)
    c: Coincident(g26,g21)
    c: Equal(g21, g22-g26) x5
    c: PointOnObject(g21,g27)
    c: PointOnObject(g22,g27)
    c: PointOnObject(g23,g27)
    c: PointOnObject(g24,g27)
    c: PointOnObject(g25,g27)
    c: PointOnObject(g26,g27)
    c: Diameter(g27) = 7
    c: DistanceY(g-1,g27) = 7
    c: DistanceX(g21,g-1) = 1
    c: Vertical(g21)
    c: Coincident(g28,g29)
    c: Coincident(g29,g30)
    c: Coincident(g30,g31)
    c: Coincident(g31,g32)
    c: Coincident(g32,g33)
    c: Coincident(g33,g28)
    c: Equal(g28, g29-g33) x5
    c: PointOnObject(g28,g34)
    c: PointOnObject(g29,g34)
    c: PointOnObject(g30,g34)
    c: PointOnObject(g31,g34)
    c: PointOnObject(g32,g34)
    c: PointOnObject(g33,g34)
    c: PointOnObject(g34,g-1)
    c: Diameter(g34) = 7
    c: Vertical(g31)
    c: DistanceX(g34,g-1) = 8
    c: Coincident(g35,g36)
    c: Coincident(g36,g37)
    c: Coincident(g37,g38)
    c: Coincident(g38,g39)
    c: Coincident(g39,g40)
    c: Coincident(g40,g35)
    c: Equal(g35, g36-g40) x5
    c: PointOnObject(g35,g41)
    c: PointOnObject(g36,g41)
    c: PointOnObject(g37,g41)
    c: PointOnObject(g38,g41)
    c: PointOnObject(g39,g41)
    c: PointOnObject(g40,g41)
    c: Coincident(g42,g43)
    c: Coincident(g43,g44)
    c: Coincident(g44,g45)
    c: Coincident(g45,g46)
    c: Coincident(g46,g47)
    c: Coincident(g47,g42)
    c: Equal(g42, g43-g47) x5
    c: PointOnObject(g42,g48)
    c: PointOnObject(g43,g48)
    c: PointOnObject(g44,g48)
    c: PointOnObject(g45,g48)
    c: PointOnObject(g46,g48)
    c: PointOnObject(g47,g48)
    c: Equal(g41,g48)
    c: Diameter(g41) = 7
    c: Vertical(g39)
    c: Vertical(g43)
    c: Distance(g-2,g39) = 1
    c: Symmetric(g38,g43,g-2)
    c: Distance(g41,g-1) = 7
FEATURE [Part::Extrusion] Extrude639  label="hex241"
  Base = -> Sketch648
  Dir = (0,-1,2e-16)
  DirMode = 2
  FaceMakerClass = Part::FaceMakerBullseye
  FaceMakerMode = 3
  LengthFwd = 10
  LengthRev = 0
  Placement = pos=(-32,0,28) rot=(0,0,1;0rad)
  Solid = true
  Symmetric = false
FEATURE [Sketcher::SketchObject] Sketch649
  ArcFitTolerance = 1e-06
  FullyConstrained = true
  MakeInternals = false
  Placement = pos=(0,0,0) rot=(1,0,0;1.5708rad)
  sketch-geometry (49):
    g0: LineSegment StartX=1e-16 StartY=3.5 StartZ=0 EndX=-3.03109 EndY=1.75 EndZ=0
    g1: LineSegment StartX=-3.03109 StartY=1.75 StartZ=0 EndX=-3.03109 EndY=-1.75 EndZ=0
    g2: LineSegment StartX=-3.03109 StartY=-1.75 StartZ=0 EndX=-1e-16 EndY=-3.5 EndZ=0
    g3: LineSegment StartX=-1e-16 StartY=-3.5 StartZ=0 EndX=3.03109 EndY=-1.75 EndZ=0
    g4: LineSegment StartX=3.03109 StartY=-1.75 StartZ=0 EndX=3.03109 EndY=1.75 EndZ=0
    g5: LineSegment StartX=3.03109 StartY=1.75 StartZ=0 EndX=1e-16 EndY=3.5 EndZ=0
    g6: Circle [constr] CenterX=0 CenterY=0 CenterZ=0 NormalX=0 NormalY=0 NormalZ=1 AngleXU=0 Radius=3.5
    g7: LineSegment StartX=4.96892 StartY=-1.75002 StartZ=0 EndX=8.00002 EndY=-3.5 EndZ=0
    g8: LineSegment StartX=8.00002 StartY=-3.5 StartZ=0 EndX=11.0311 EndY=-1.74998 EndZ=0
    g9: LineSegment StartX=11.0311 StartY=-1.74998 StartZ=0 EndX=11.0311 EndY=1.75002 EndZ=0
    g10: LineSegment StartX=11.0311 StartY=1.75002 StartZ=0 EndX=7.99998 EndY=3.5 EndZ=0
    g11: LineSegment StartX=7.99998 StartY=3.5 StartZ=0 EndX=4.9689 EndY=1.74998 EndZ=0
    g12: LineSegment StartX=4.9689 StartY=1.74998 StartZ=0 EndX=4.96892 EndY=-1.75002 EndZ=0
    g13: Circle [constr] CenterX=8 CenterY=0 CenterZ=0 NormalX=0 NormalY=0 NormalZ=1 AngleXU=0 Radius=3.5
    g14: LineSegment StartX=4.03109 StartY=3.5 StartZ=0 EndX=7.06218 EndY=5.25 EndZ=0
    g15: LineSegment StartX=7.06218 StartY=5.25 StartZ=0 EndX=7.06218 EndY=8.75 EndZ=0
    g16: LineSegment StartX=7.06218 StartY=8.75 StartZ=0 EndX=4.03109 EndY=10.5 EndZ=0
    g17: LineSegment StartX=4.03109 StartY=10.5 StartZ=0 EndX=1 EndY=8.75 EndZ=0
    g18: LineSegment StartX=1 StartY=8.75 StartZ=0 EndX=1 EndY=5.25 EndZ=0
    g19: LineSegment StartX=1 StartY=5.25 StartZ=0 EndX=4.03109 EndY=3.5 EndZ=0
    g20: Circle [constr] CenterX=4.03109 CenterY=7 CenterZ=0 NormalX=0 NormalY=0 NormalZ=1 AngleXU=0 Radius=3.5
    g21: LineSegment StartX=-1 StartY=5.25 StartZ=0 EndX=-1 EndY=8.75 EndZ=0
    g22: LineSegment StartX=-1 StartY=8.75 StartZ=0 EndX=-4.03109 EndY=10.5 EndZ=0
    g23: LineSegment StartX=-4.03109 StartY=10.5 StartZ=0 EndX=-7.06218 EndY=8.75 EndZ=0
    g24: LineSegment StartX=-7.06218 StartY=8.75 StartZ=0 EndX=-7.06218 EndY=5.25 EndZ=0
    g25: LineSegment StartX=-7.06218 StartY=5.25 StartZ=0 EndX=-4.03109 EndY=3.5 EndZ=0
    g26: LineSegment StartX=-4.03109 StartY=3.5 StartZ=0 EndX=-1 EndY=5.25 EndZ=0
    g27: Circle [constr] CenterX=-4.03109 CenterY=7 CenterZ=0 NormalX=0 NormalY=0 NormalZ=1 AngleXU=0 Radius=3.5
    g28: LineSegment StartX=-4.96891 StartY=-1.75 StartZ=0 EndX=-4.96891 EndY=1.75 EndZ=0
    g29: LineSegment StartX=-4.96891 StartY=1.75 StartZ=0 EndX=-8 EndY=3.5 EndZ=0
    g30: LineSegment StartX=-8 StartY=3.5 StartZ=0 EndX=-11.0311 EndY=1.75 EndZ=0
    g31: LineSegment StartX=-11.0311 StartY=1.75 StartZ=0 EndX=-11.0311 EndY=-1.75 EndZ=0
    g32: LineSegment StartX=-11.0311 StartY=-1.75 StartZ=0 EndX=-8 EndY=-3.5 EndZ=0
    g33: LineSegment StartX=-8 StartY=-3.5 StartZ=0 EndX=-4.96891 EndY=-1.75 EndZ=0
    g34: Circle [constr] CenterX=-8 CenterY=0 CenterZ=0 NormalX=0 NormalY=0 NormalZ=1 AngleXU=0 Radius=3.5
    g35: LineSegment StartX=-4.03109 StartY=-3.5 StartZ=0 EndX=-7.06218 EndY=-5.25 EndZ=0
    g36: LineSegment StartX=-7.06218 StartY=-5.25 StartZ=0 EndX=-7.06218 EndY=-8.75 EndZ=0
    g37: LineSegment StartX=-7.06218 StartY=-8.75 StartZ=0 EndX=-4.03109 EndY=-10.5 EndZ=0
    g38: LineSegment StartX=-4.03109 StartY=-10.5 StartZ=0 EndX=-1 EndY=-8.75 EndZ=0
    g39: LineSegment StartX=-1 StartY=-8.75 StartZ=0 EndX=-1 EndY=-5.25 EndZ=0
    g40: LineSegment StartX=-1 StartY=-5.25 StartZ=0 EndX=-4.03109 EndY=-3.5 EndZ=0
    g41: Circle [constr] CenterX=-4.03109 CenterY=-7 CenterZ=0 NormalX=0 NormalY=0 NormalZ=1 AngleXU=0 Radius=3.5
    g42: LineSegment StartX=4.03109 StartY=-3.5 StartZ=0 EndX=1 EndY=-5.25 EndZ=0
    g43: LineSegment StartX=1 StartY=-5.25 StartZ=0 EndX=1 EndY=-8.75 EndZ=0
    g44: LineSegment StartX=1 StartY=-8.75 StartZ=0 EndX=4.03109 EndY=-10.5 EndZ=0
    g45: LineSegment StartX=4.03109 StartY=-10.5 StartZ=0 EndX=7.06218 EndY=-8.75 EndZ=0
    g46: LineSegment StartX=7.06218 StartY=-8.75 StartZ=0 EndX=7.06218 EndY=-5.25 EndZ=0
    g47: LineSegment StartX=7.06218 StartY=-5.25 StartZ=0 EndX=4.03109 EndY=-3.5 EndZ=0
    g48: Circle [constr] CenterX=4.03109 CenterY=-7 CenterZ=0 NormalX=0 NormalY=0 NormalZ=1 AngleXU=0 Radius=3.5
  constraints (117):
    c: Coincident(g0,g1)
    c: Coincident(g1,g2)
    c: Coincident(g2,g3)
    c: Coincident(g3,g4)
    c: Coincident(g4,g5)
    c: Coincident(g5,g0)
    c: Equal(g0, g1-g5) x5
    c: PointOnObject(g0,g6)
    c: PointOnObject(g1,g6)
    c: PointOnObject(g2,g6)
    c: PointOnObject(g3,g6)
    c: PointOnObject(g4,g6)
    c: PointOnObject(g5,g6)
    c: Coincident(g6,g-1)
    c: Diameter(g6) = 7
    c: PointOnObject(g0,g-2)
    c: Coincident(g7,g8)
    c: Coincident(g8,g9)
    c: Coincident(g9,g10)
    c: Coincident(g10,g11)
    c: Coincident(g11,g12)
    c: Coincident(g12,g7)
    c: Equal(g7, g8-g12) x5
    c: PointOnObject(g7,g13)
    c: PointOnObject(g8,g13)
    c: PointOnObject(g9,g13)
    c: PointOnObject(g10,g13)
    c: PointOnObject(g11,g13)
    c: PointOnObject(g12,g13)
    c: PointOnObject(g13,g-1)
    c: Diameter(g13) = 7
    c: Distance(g6,g13) = 8
    c: Horizontal(g0,g10)
    c: Coincident(g14,g15)
    c: Coincident(g15,g16)
    c: Coincident(g16,g17)
    c: Coincident(g17,g18)
    c: Coincident(g18,g19)
    c: Coincident(g19,g14)
    c: Equal(g14, g15-g19) x5
    c: PointOnObject(g14,g20)
    c: PointOnObject(g15,g20)
    c: PointOnObject(g16,g20)
    c: PointOnObject(g17,g20)
    c: PointOnObject(g18,g20)
    c: PointOnObject(g19,g20)
    c: Diameter(g20) = 7
    c: DistanceY(g-1,g20) = 7
    c: Vertical(g18)
    c: Distance(g17,g-2) = 1
    c: Coincident(g21,g22)
    c: Coincident(g22,g23)
    c: Coincident(g23,g24)
    c: Coincident(g24,g25)
    c: Coincident(g25,g26)
    c: Coincident(g26,g21)
    c: Equal(g21, g22-g26) x5
    c: PointOnObject(g21,g27)
    c: PointOnObject(g22,g27)
    c: PointOnObject(g23,g27)
    c: PointOnObject(g24,g27)
    c: PointOnObject(g25,g27)
    c: PointOnObject(g26,g27)
    c: Diameter(g27) = 7
    c: DistanceY(g-1,g27) = 7
    c: DistanceX(g21,g-1) = 1
    c: Vertical(g21)
    c: Coincident(g28,g29)
    c: Coincident(g29,g30)
    c: Coincident(g30,g31)
    c: Coincident(g31,g32)
    c: Coincident(g32,g33)
    c: Coincident(g33,g28)
    c: Equal(g28, g29-g33) x5
    c: PointOnObject(g28,g34)
    c: PointOnObject(g29,g34)
    c: PointOnObject(g30,g34)
    c: PointOnObject(g31,g34)
    c: PointOnObject(g32,g34)
    c: PointOnObject(g33,g34)
    c: PointOnObject(g34,g-1)
    c: Diameter(g34) = 7
    c: Vertical(g31)
    c: DistanceX(g34,g-1) = 8
    c: Coincident(g35,g36)
    c: Coincident(g36,g37)
    c: Coincident(g37,g38)
    c: Coincident(g38,g39)
    c: Coincident(g39,g40)
    c: Coincident(g40,g35)
    c: Equal(g35, g36-g40) x5
    c: PointOnObject(g35,g41)
    c: PointOnObject(g36,g41)
    c: PointOnObject(g37,g41)
    c: PointOnObject(g38,g41)
    c: PointOnObject(g39,g41)
    c: PointOnObject(g40,g41)
    c: Coincident(g42,g43)
    c: Coincident(g43,g44)
    c: Coincident(g44,g45)
    c: Coincident(g45,g46)
    c: Coincident(g46,g47)
    c: Coincident(g47,g42)
    c: Equal(g42, g43-g47) x5
    c: PointOnObject(g42,g48)
    c: PointOnObject(g43,g48)
    c: PointOnObject(g44,g48)
    c: PointOnObject(g45,g48)
    c: PointOnObject(g46,g48)
    c: PointOnObject(g47,g48)
    c: Equal(g41,g48)
    c: Diameter(g41) = 7
    c: Vertical(g39)
    c: Vertical(g43)
    c: Distance(g-2,g39) = 1
    c: Symmetric(g38,g43,g-2)
    c: Distance(g41,g-1) = 7
FEATURE [Part::Extrusion] Extrude640  label="hex242"
  Base = -> Sketch649
  Dir = (0,-1,2e-16)
  DirMode = 2
  FaceMakerClass = Part::FaceMakerBullseye
  FaceMakerMode = 3
  LengthFwd = 10
  LengthRev = 0
  Placement = pos=(-12,0,35) rot=(0,0,1;0rad)
  Solid = true
  Symmetric = false
FEATURE [Sketcher::SketchObject] Sketch650
  ArcFitTolerance = 1e-06
  FullyConstrained = true
  MakeInternals = false
  Placement = pos=(0,0,0) rot=(1,0,0;1.5708rad)
  sketch-geometry (49):
    g0: LineSegment StartX=1e-16 StartY=3.5 StartZ=0 EndX=-3.03109 EndY=1.75 EndZ=0
    g1: LineSegment StartX=-3.03109 StartY=1.75 StartZ=0 EndX=-3.03109 EndY=-1.75 EndZ=0
    g2: LineSegment StartX=-3.03109 StartY=-1.75 StartZ=0 EndX=-1e-16 EndY=-3.5 EndZ=0
    g3: LineSegment StartX=-1e-16 StartY=-3.5 StartZ=0 EndX=3.03109 EndY=-1.75 EndZ=0
    g4: LineSegment StartX=3.03109 StartY=-1.75 StartZ=0 EndX=3.03109 EndY=1.75 EndZ=0
    g5: LineSegment StartX=3.03109 StartY=1.75 StartZ=0 EndX=1e-16 EndY=3.5 EndZ=0
    g6: Circle [constr] CenterX=0 CenterY=0 CenterZ=0 NormalX=0 NormalY=0 NormalZ=1 AngleXU=0 Radius=3.5
    g7: LineSegment StartX=4.96892 StartY=-1.75002 StartZ=0 EndX=8.00002 EndY=-3.5 EndZ=0
    g8: LineSegment StartX=8.00002 StartY=-3.5 StartZ=0 EndX=11.0311 EndY=-1.74998 EndZ=0
    g9: LineSegment StartX=11.0311 StartY=-1.74998 StartZ=0 EndX=11.0311 EndY=1.75002 EndZ=0
    g10: LineSegment StartX=11.0311 StartY=1.75002 StartZ=0 EndX=7.99998 EndY=3.5 EndZ=0
    g11: LineSegment StartX=7.99998 StartY=3.5 StartZ=0 EndX=4.9689 EndY=1.74998 EndZ=0
    g12: LineSegment StartX=4.9689 StartY=1.74998 StartZ=0 EndX=4.96892 EndY=-1.75002 EndZ=0
    g13: Circle [constr] CenterX=8 CenterY=0 CenterZ=0 NormalX=0 NormalY=0 NormalZ=1 AngleXU=0 Radius=3.5
    g14: LineSegment StartX=4.03109 StartY=3.5 StartZ=0 EndX=7.06218 EndY=5.25 EndZ=0
    g15: LineSegment StartX=7.06218 StartY=5.25 StartZ=0 EndX=7.06218 EndY=8.75 EndZ=0
    g16: LineSegment StartX=7.06218 StartY=8.75 StartZ=0 EndX=4.03109 EndY=10.5 EndZ=0
    g17: LineSegment StartX=4.03109 StartY=10.5 StartZ=0 EndX=1 EndY=8.75 EndZ=0
    g18: LineSegment StartX=1 StartY=8.75 StartZ=0 EndX=1 EndY=5.25 EndZ=0
    g19: LineSegment StartX=1 StartY=5.25 StartZ=0 EndX=4.03109 EndY=3.5 EndZ=0
    g20: Circle [constr] CenterX=4.03109 CenterY=7 CenterZ=0 NormalX=0 NormalY=0 NormalZ=1 AngleXU=0 Radius=3.5
    g21: LineSegment StartX=-1 StartY=5.25 StartZ=0 EndX=-1 EndY=8.75 EndZ=0
    g22: LineSegment StartX=-1 StartY=8.75 StartZ=0 EndX=-4.03109 EndY=10.5 EndZ=0
    g23: LineSegment StartX=-4.03109 StartY=10.5 StartZ=0 EndX=-7.06218 EndY=8.75 EndZ=0
    g24: LineSegment StartX=-7.06218 StartY=8.75 StartZ=0 EndX=-7.06218 EndY=5.25 EndZ=0
    g25: LineSegment StartX=-7.06218 StartY=5.25 StartZ=0 EndX=-4.03109 EndY=3.5 EndZ=0
    g26: LineSegment StartX=-4.03109 StartY=3.5 StartZ=0 EndX=-1 EndY=5.25 EndZ=0
    g27: Circle [constr] CenterX=-4.03109 CenterY=7 CenterZ=0 NormalX=0 NormalY=0 NormalZ=1 AngleXU=0 Radius=3.5
    g28: LineSegment StartX=-4.96891 StartY=-1.75 StartZ=0 EndX=-4.96891 EndY=1.75 EndZ=0
    g29: LineSegment StartX=-4.96891 StartY=1.75 StartZ=0 EndX=-8 EndY=3.5 EndZ=0
    g30: LineSegment StartX=-8 StartY=3.5 StartZ=0 EndX=-11.0311 EndY=1.75 EndZ=0
    g31: LineSegment StartX=-11.0311 StartY=1.75 StartZ=0 EndX=-11.0311 EndY=-1.75 EndZ=0
    g32: LineSegment StartX=-11.0311 StartY=-1.75 StartZ=0 EndX=-8 EndY=-3.5 EndZ=0
    g33: LineSegment StartX=-8 StartY=-3.5 StartZ=0 EndX=-4.96891 EndY=-1.75 EndZ=0
    g34: Circle [constr] CenterX=-8 CenterY=0 CenterZ=0 NormalX=0 NormalY=0 NormalZ=1 AngleXU=0 Radius=3.5
    g35: LineSegment StartX=-4.03109 StartY=-3.5 StartZ=0 EndX=-7.06218 EndY=-5.25 EndZ=0
    g36: LineSegment StartX=-7.06218 StartY=-5.25 StartZ=0 EndX=-7.06218 EndY=-8.75 EndZ=0
    g37: LineSegment StartX=-7.06218 StartY=-8.75 StartZ=0 EndX=-4.03109 EndY=-10.5 EndZ=0
    g38: LineSegment StartX=-4.03109 StartY=-10.5 StartZ=0 EndX=-1 EndY=-8.75 EndZ=0
    g39: LineSegment StartX=-1 StartY=-8.75 StartZ=0 EndX=-1 EndY=-5.25 EndZ=0
    g40: LineSegment StartX=-1 StartY=-5.25 StartZ=0 EndX=-4.03109 EndY=-3.5 EndZ=0
    g41: Circle [constr] CenterX=-4.03109 CenterY=-7 CenterZ=0 NormalX=0 NormalY=0 NormalZ=1 AngleXU=0 Radius=3.5
    g42: LineSegment StartX=4.03109 StartY=-3.5 StartZ=0 EndX=1 EndY=-5.25 EndZ=0
    g43: LineSegment StartX=1 StartY=-5.25 StartZ=0 EndX=1 EndY=-8.75 EndZ=0
    g44: LineSegment StartX=1 StartY=-8.75 StartZ=0 EndX=4.03109 EndY=-10.5 EndZ=0
    g45: LineSegment StartX=4.03109 StartY=-10.5 StartZ=0 EndX=7.06218 EndY=-8.75 EndZ=0
    g46: LineSegment StartX=7.06218 StartY=-8.75 StartZ=0 EndX=7.06218 EndY=-5.25 EndZ=0
    g47: LineSegment StartX=7.06218 StartY=-5.25 StartZ=0 EndX=4.03109 EndY=-3.5 EndZ=0
    g48: Circle [constr] CenterX=4.03109 CenterY=-7 CenterZ=0 NormalX=0 NormalY=0 NormalZ=1 AngleXU=0 Radius=3.5
  constraints (117):
    c: Coincident(g0,g1)
    c: Coincident(g1,g2)
    c: Coincident(g2,g3)
    c: Coincident(g3,g4)
    c: Coincident(g4,g5)
    c: Coincident(g5,g0)
    c: Equal(g0, g1-g5) x5
    c: PointOnObject(g0,g6)
    c: PointOnObject(g1,g6)
    c: PointOnObject(g2,g6)
    c: PointOnObject(g3,g6)
    c: PointOnObject(g4,g6)
    c: PointOnObject(g5,g6)
    c: Coincident(g6,g-1)
    c: Diameter(g6) = 7
    c: PointOnObject(g0,g-2)
    c: Coincident(g7,g8)
    c: Coincident(g8,g9)
    c: Coincident(g9,g10)
    c: Coincident(g10,g11)
    c: Coincident(g11,g12)
    c: Coincident(g12,g7)
    c: Equal(g7, g8-g12) x5
    c: PointOnObject(g7,g13)
    c: PointOnObject(g8,g13)
    c: PointOnObject(g9,g13)
    c: PointOnObject(g10,g13)
    c: PointOnObject(g11,g13)
    c: PointOnObject(g12,g13)
    c: PointOnObject(g13,g-1)
    c: Diameter(g13) = 7
    c: Distance(g6,g13) = 8
    c: Horizontal(g0,g10)
    c: Coincident(g14,g15)
    c: Coincident(g15,g16)
    c: Coincident(g16,g17)
    c: Coincident(g17,g18)
    c: Coincident(g18,g19)
    c: Coincident(g19,g14)
    c: Equal(g14, g15-g19) x5
    c: PointOnObject(g14,g20)
    c: PointOnObject(g15,g20)
    c: PointOnObject(g16,g20)
    c: PointOnObject(g17,g20)
    c: PointOnObject(g18,g20)
    c: PointOnObject(g19,g20)
    c: Diameter(g20) = 7
    c: DistanceY(g-1,g20) = 7
    c: Vertical(g18)
    c: Distance(g17,g-2) = 1
    c: Coincident(g21,g22)
    c: Coincident(g22,g23)
    c: Coincident(g23,g24)
    c: Coincident(g24,g25)
    c: Coincident(g25,g26)
    c: Coincident(g26,g21)
    c: Equal(g21, g22-g26) x5
    c: PointOnObject(g21,g27)
    c: PointOnObject(g22,g27)
    c: PointOnObject(g23,g27)
    c: PointOnObject(g24,g27)
    c: PointOnObject(g25,g27)
    c: PointOnObject(g26,g27)
    c: Diameter(g27) = 7
    c: DistanceY(g-1,g27) = 7
    c: DistanceX(g21,g-1) = 1
    c: Vertical(g21)
    c: Coincident(g28,g29)
    c: Coincident(g29,g30)
    c: Coincident(g30,g31)
    c: Coincident(g31,g32)
    c: Coincident(g32,g33)
    c: Coincident(g33,g28)
    c: Equal(g28, g29-g33) x5
    c: PointOnObject(g28,g34)
    c: PointOnObject(g29,g34)
    c: PointOnObject(g30,g34)
    c: PointOnObject(g31,g34)
    c: PointOnObject(g32,g34)
    c: PointOnObject(g33,g34)
    c: PointOnObject(g34,g-1)
    c: Diameter(g34) = 7
    c: Vertical(g31)
    c: DistanceX(g34,g-1) = 8
    c: Coincident(g35,g36)
    c: Coincident(g36,g37)
    c: Coincident(g37,g38)
    c: Coincident(g38,g39)
    c: Coincident(g39,g40)
    c: Coincident(g40,g35)
    c: Equal(g35, g36-g40) x5
    c: PointOnObject(g35,g41)
    c: PointOnObject(g36,g41)
    c: PointOnObject(g37,g41)
    c: PointOnObject(g38,g41)
    c: PointOnObject(g39,g41)
    c: PointOnObject(g40,g41)
    c: Coincident(g42,g43)
    c: Coincident(g43,g44)
    c: Coincident(g44,g45)
    c: Coincident(g45,g46)
    c: Coincident(g46,g47)
    c: Coincident(g47,g42)
    c: Equal(g42, g43-g47) x5
    c: PointOnObject(g42,g48)
    c: PointOnObject(g43,g48)
    c: PointOnObject(g44,g48)
    c: PointOnObject(g45,g48)
    c: PointOnObject(g46,g48)
    c: PointOnObject(g47,g48)
    c: Equal(g41,g48)
    c: Diameter(g41) = 7
    c: Vertical(g39)
    c: Vertical(g43)
    c: Distance(g-2,g39) = 1
    c: Symmetric(g38,g43,g-2)
    c: Distance(g41,g-1) = 7
FEATURE [Part::Extrusion] Extrude641  label="hex243"
  Base = -> Sketch650
  Dir = (0,-1,2e-16)
  DirMode = 2
  FaceMakerClass = Part::FaceMakerBullseye
  FaceMakerMode = 3
  LengthFwd = 10
  LengthRev = 0
  Placement = pos=(-80,0,0) rot=(0,0,1;0rad)
  Solid = true
  Symmetric = false
FEATURE [Sketcher::SketchObject] Sketch651
  ArcFitTolerance = 1e-06
  FullyConstrained = true
  MakeInternals = false
  Placement = pos=(0,0,0) rot=(1,0,0;1.5708rad)
  sketch-geometry (49):
    g0: LineSegment StartX=1e-16 StartY=3.5 StartZ=0 EndX=-3.03109 EndY=1.75 EndZ=0
    g1: LineSegment StartX=-3.03109 StartY=1.75 StartZ=0 EndX=-3.03109 EndY=-1.75 EndZ=0
    g2: LineSegment StartX=-3.03109 StartY=-1.75 StartZ=0 EndX=-1e-16 EndY=-3.5 EndZ=0
    g3: LineSegment StartX=-1e-16 StartY=-3.5 StartZ=0 EndX=3.03109 EndY=-1.75 EndZ=0
    g4: LineSegment StartX=3.03109 StartY=-1.75 StartZ=0 EndX=3.03109 EndY=1.75 EndZ=0
    g5: LineSegment StartX=3.03109 StartY=1.75 StartZ=0 EndX=1e-16 EndY=3.5 EndZ=0
    g6: Circle [constr] CenterX=0 CenterY=0 CenterZ=0 NormalX=0 NormalY=0 NormalZ=1 AngleXU=0 Radius=3.5
    g7: LineSegment StartX=4.96892 StartY=-1.75002 StartZ=0 EndX=8.00002 EndY=-3.5 EndZ=0
    g8: LineSegment StartX=8.00002 StartY=-3.5 StartZ=0 EndX=11.0311 EndY=-1.74998 EndZ=0
    g9: LineSegment StartX=11.0311 StartY=-1.74998 StartZ=0 EndX=11.0311 EndY=1.75002 EndZ=0
    g10: LineSegment StartX=11.0311 StartY=1.75002 StartZ=0 EndX=7.99998 EndY=3.5 EndZ=0
    g11: LineSegment StartX=7.99998 StartY=3.5 StartZ=0 EndX=4.9689 EndY=1.74998 EndZ=0
    g12: LineSegment StartX=4.9689 StartY=1.74998 StartZ=0 EndX=4.96892 EndY=-1.75002 EndZ=0
    g13: Circle [constr] CenterX=8 CenterY=0 CenterZ=0 NormalX=0 NormalY=0 NormalZ=1 AngleXU=0 Radius=3.5
    g14: LineSegment StartX=4.03109 StartY=3.5 StartZ=0 EndX=7.06218 EndY=5.25 EndZ=0
    g15: LineSegment StartX=7.06218 StartY=5.25 StartZ=0 EndX=7.06218 EndY=8.75 EndZ=0
    g16: LineSegment StartX=7.06218 StartY=8.75 StartZ=0 EndX=4.03109 EndY=10.5 EndZ=0
    g17: LineSegment StartX=4.03109 StartY=10.5 StartZ=0 EndX=1 EndY=8.75 EndZ=0
    g18: LineSegment StartX=1 StartY=8.75 StartZ=0 EndX=1 EndY=5.25 EndZ=0
    g19: LineSegment StartX=1 StartY=5.25 StartZ=0 EndX=4.03109 EndY=3.5 EndZ=0
    g20: Circle [constr] CenterX=4.03109 CenterY=7 CenterZ=0 NormalX=0 NormalY=0 NormalZ=1 AngleXU=0 Radius=3.5
    g21: LineSegment StartX=-1 StartY=5.25 StartZ=0 EndX=-1 EndY=8.75 EndZ=0
    g22: LineSegment StartX=-1 StartY=8.75 StartZ=0 EndX=-4.03109 EndY=10.5 EndZ=0
    g23: LineSegment StartX=-4.03109 StartY=10.5 StartZ=0 EndX=-7.06218 EndY=8.75 EndZ=0
    g24: LineSegment StartX=-7.06218 StartY=8.75 StartZ=0 EndX=-7.06218 EndY=5.25 EndZ=0
    g25: LineSegment StartX=-7.06218 StartY=5.25 StartZ=0 EndX=-4.03109 EndY=3.5 EndZ=0
    g26: LineSegment StartX=-4.03109 StartY=3.5 StartZ=0 EndX=-1 EndY=5.25 EndZ=0
    g27: Circle [constr] CenterX=-4.03109 CenterY=7 CenterZ=0 NormalX=0 NormalY=0 NormalZ=1 AngleXU=0 Radius=3.5
    g28: LineSegment StartX=-4.96891 StartY=-1.75 StartZ=0 EndX=-4.96891 EndY=1.75 EndZ=0
    g29: LineSegment StartX=-4.96891 StartY=1.75 StartZ=0 EndX=-8 EndY=3.5 EndZ=0
    g30: LineSegment StartX=-8 StartY=3.5 StartZ=0 EndX=-11.0311 EndY=1.75 EndZ=0
    g31: LineSegment StartX=-11.0311 StartY=1.75 StartZ=0 EndX=-11.0311 EndY=-1.75 EndZ=0
    g32: LineSegment StartX=-11.0311 StartY=-1.75 StartZ=0 EndX=-8 EndY=-3.5 EndZ=0
    g33: LineSegment StartX=-8 StartY=-3.5 StartZ=0 EndX=-4.96891 EndY=-1.75 EndZ=0
    g34: Circle [constr] CenterX=-8 CenterY=0 CenterZ=0 NormalX=0 NormalY=0 NormalZ=1 AngleXU=0 Radius=3.5
    g35: LineSegment StartX=-4.03109 StartY=-3.5 StartZ=0 EndX=-7.06218 EndY=-5.25 EndZ=0
    g36: LineSegment StartX=-7.06218 StartY=-5.25 StartZ=0 EndX=-7.06218 EndY=-8.75 EndZ=0
    g37: LineSegment StartX=-7.06218 StartY=-8.75 StartZ=0 EndX=-4.03109 EndY=-10.5 EndZ=0
    g38: LineSegment StartX=-4.03109 StartY=-10.5 StartZ=0 EndX=-1 EndY=-8.75 EndZ=0
    g39: LineSegment StartX=-1 StartY=-8.75 StartZ=0 EndX=-1 EndY=-5.25 EndZ=0
    g40: LineSegment StartX=-1 StartY=-5.25 StartZ=0 EndX=-4.03109 EndY=-3.5 EndZ=0
    g41: Circle [constr] CenterX=-4.03109 CenterY=-7 CenterZ=0 NormalX=0 NormalY=0 NormalZ=1 AngleXU=0 Radius=3.5
    g42: LineSegment StartX=4.03109 StartY=-3.5 StartZ=0 EndX=1 EndY=-5.25 EndZ=0
    g43: LineSegment StartX=1 StartY=-5.25 StartZ=0 EndX=1 EndY=-8.75 EndZ=0
    g44: LineSegment StartX=1 StartY=-8.75 StartZ=0 EndX=4.03109 EndY=-10.5 EndZ=0
    g45: LineSegment StartX=4.03109 StartY=-10.5 StartZ=0 EndX=7.06218 EndY=-8.75 EndZ=0
    g46: LineSegment StartX=7.06218 StartY=-8.75 StartZ=0 EndX=7.06218 EndY=-5.25 EndZ=0
    g47: LineSegment StartX=7.06218 StartY=-5.25 StartZ=0 EndX=4.03109 EndY=-3.5 EndZ=0
    g48: Circle [constr] CenterX=4.03109 CenterY=-7 CenterZ=0 NormalX=0 NormalY=0 NormalZ=1 AngleXU=0 Radius=3.5
  constraints (117):
    c: Coincident(g0,g1)
    c: Coincident(g1,g2)
    c: Coincident(g2,g3)
    c: Coincident(g3,g4)
    c: Coincident(g4,g5)
    c: Coincident(g5,g0)
    c: Equal(g0, g1-g5) x5
    c: PointOnObject(g0,g6)
    c: PointOnObject(g1,g6)
    c: PointOnObject(g2,g6)
    c: PointOnObject(g3,g6)
    c: PointOnObject(g4,g6)
    c: PointOnObject(g5,g6)
    c: Coincident(g6,g-1)
    c: Diameter(g6) = 7
    c: PointOnObject(g0,g-2)
    c: Coincident(g7,g8)
    c: Coincident(g8,g9)
    c: Coincident(g9,g10)
    c: Coincident(g10,g11)
    c: Coincident(g11,g12)
    c: Coincident(g12,g7)
    c: Equal(g7, g8-g12) x5
    c: PointOnObject(g7,g13)
    c: PointOnObject(g8,g13)
    c: PointOnObject(g9,g13)
    c: PointOnObject(g10,g13)
    c: PointOnObject(g11,g13)
    c: PointOnObject(g12,g13)
    c: PointOnObject(g13,g-1)
    c: Diameter(g13) = 7
    c: Distance(g6,g13) = 8
    c: Horizontal(g0,g10)
    c: Coincident(g14,g15)
    c: Coincident(g15,g16)
    c: Coincident(g16,g17)
    c: Coincident(g17,g18)
    c: Coincident(g18,g19)
    c: Coincident(g19,g14)
    c: Equal(g14, g15-g19) x5
    c: PointOnObject(g14,g20)
    c: PointOnObject(g15,g20)
    c: PointOnObject(g16,g20)
    c: PointOnObject(g17,g20)
    c: PointOnObject(g18,g20)
    c: PointOnObject(g19,g20)
    c: Diameter(g20) = 7
    c: DistanceY(g-1,g20) = 7
    c: Vertical(g18)
    c: Distance(g17,g-2) = 1
    c: Coincident(g21,g22)
    c: Coincident(g22,g23)
    c: Coincident(g23,g24)
    c: Coincident(g24,g25)
    c: Coincident(g25,g26)
    c: Coincident(g26,g21)
    c: Equal(g21, g22-g26) x5
    c: PointOnObject(g21,g27)
    c: PointOnObject(g22,g27)
    c: PointOnObject(g23,g27)
    c: PointOnObject(g24,g27)
    c: PointOnObject(g25,g27)
    c: PointOnObject(g26,g27)
    c: Diameter(g27) = 7
    c: DistanceY(g-1,g27) = 7
    c: DistanceX(g21,g-1) = 1
    c: Vertical(g21)
    c: Coincident(g28,g29)
    c: Coincident(g29,g30)
    c: Coincident(g30,g31)
    c: Coincident(g31,g32)
    c: Coincident(g32,g33)
    c: Coincident(g33,g28)
    c: Equal(g28, g29-g33) x5
    c: PointOnObject(g28,g34)
    c: PointOnObject(g29,g34)
    c: PointOnObject(g30,g34)
    c: PointOnObject(g31,g34)
    c: PointOnObject(g32,g34)
    c: PointOnObject(g33,g34)
    c: PointOnObject(g34,g-1)
    c: Diameter(g34) = 7
    c: Vertical(g31)
    c: DistanceX(g34,g-1) = 8
    c: Coincident(g35,g36)
    c: Coincident(g36,g37)
    c: Coincident(g37,g38)
    c: Coincident(g38,g39)
    c: Coincident(g39,g40)
    c: Coincident(g40,g35)
    c: Equal(g35, g36-g40) x5
    c: PointOnObject(g35,g41)
    c: PointOnObject(g36,g41)
    c: PointOnObject(g37,g41)
    c: PointOnObject(g38,g41)
    c: PointOnObject(g39,g41)
    c: PointOnObject(g40,g41)
    c: Coincident(g42,g43)
    c: Coincident(g43,g44)
    c: Coincident(g44,g45)
    c: Coincident(g45,g46)
    c: Coincident(g46,g47)
    c: Coincident(g47,g42)
    c: Equal(g42, g43-g47) x5
    c: PointOnObject(g42,g48)
    c: PointOnObject(g43,g48)
    c: PointOnObject(g44,g48)
    c: PointOnObject(g45,g48)
    c: PointOnObject(g46,g48)
    c: PointOnObject(g47,g48)
    c: Equal(g41,g48)
    c: Diameter(g41) = 7
    c: Vertical(g39)
    c: Vertical(g43)
    c: Distance(g-2,g39) = 1
    c: Symmetric(g38,g43,g-2)
    c: Distance(g41,g-1) = 7
FEATURE [Part::Extrusion] Extrude642  label="hex244"
  Base = -> Sketch651
  Dir = (0,-1,2e-16)
  DirMode = 2
  FaceMakerClass = Part::FaceMakerBullseye
  FaceMakerMode = 3
  LengthFwd = 10
  LengthRev = 0
  Placement = pos=(-104,0,0) rot=(0,0,1;0rad)
  Solid = true
  Symmetric = false
FEATURE [Sketcher::SketchObject] Sketch652
  ArcFitTolerance = 1e-06
  FullyConstrained = true
  MakeInternals = false
  Placement = pos=(0,0,0) rot=(1,0,0;1.5708rad)
  sketch-geometry (49):
    g0: LineSegment StartX=1e-16 StartY=3.5 StartZ=0 EndX=-3.03109 EndY=1.75 EndZ=0
    g1: LineSegment StartX=-3.03109 StartY=1.75 StartZ=0 EndX=-3.03109 EndY=-1.75 EndZ=0
    g2: LineSegment StartX=-3.03109 StartY=-1.75 StartZ=0 EndX=-1e-16 EndY=-3.5 EndZ=0
    g3: LineSegment StartX=-1e-16 StartY=-3.5 StartZ=0 EndX=3.03109 EndY=-1.75 EndZ=0
    g4: LineSegment StartX=3.03109 StartY=-1.75 StartZ=0 EndX=3.03109 EndY=1.75 EndZ=0
    g5: LineSegment StartX=3.03109 StartY=1.75 StartZ=0 EndX=1e-16 EndY=3.5 EndZ=0
    g6: Circle [constr] CenterX=0 CenterY=0 CenterZ=0 NormalX=0 NormalY=0 NormalZ=1 AngleXU=0 Radius=3.5
    g7: LineSegment StartX=4.96892 StartY=-1.75002 StartZ=0 EndX=8.00002 EndY=-3.5 EndZ=0
    g8: LineSegment StartX=8.00002 StartY=-3.5 StartZ=0 EndX=11.0311 EndY=-1.74998 EndZ=0
    g9: LineSegment StartX=11.0311 StartY=-1.74998 StartZ=0 EndX=11.0311 EndY=1.75002 EndZ=0
    g10: LineSegment StartX=11.0311 StartY=1.75002 StartZ=0 EndX=7.99998 EndY=3.5 EndZ=0
    g11: LineSegment StartX=7.99998 StartY=3.5 StartZ=0 EndX=4.9689 EndY=1.74998 EndZ=0
    g12: LineSegment StartX=4.9689 StartY=1.74998 StartZ=0 EndX=4.96892 EndY=-1.75002 EndZ=0
    g13: Circle [constr] CenterX=8 CenterY=0 CenterZ=0 NormalX=0 NormalY=0 NormalZ=1 AngleXU=0 Radius=3.5
    g14: LineSegment StartX=4.03109 StartY=3.5 StartZ=0 EndX=7.06218 EndY=5.25 EndZ=0
    g15: LineSegment StartX=7.06218 StartY=5.25 StartZ=0 EndX=7.06218 EndY=8.75 EndZ=0
    g16: LineSegment StartX=7.06218 StartY=8.75 StartZ=0 EndX=4.03109 EndY=10.5 EndZ=0
    g17: LineSegment StartX=4.03109 StartY=10.5 StartZ=0 EndX=1 EndY=8.75 EndZ=0
    g18: LineSegment StartX=1 StartY=8.75 StartZ=0 EndX=1 EndY=5.25 EndZ=0
    g19: LineSegment StartX=1 StartY=5.25 StartZ=0 EndX=4.03109 EndY=3.5 EndZ=0
    g20: Circle [constr] CenterX=4.03109 CenterY=7 CenterZ=0 NormalX=0 NormalY=0 NormalZ=1 AngleXU=0 Radius=3.5
    g21: LineSegment StartX=-1 StartY=5.25 StartZ=0 EndX=-1 EndY=8.75 EndZ=0
    g22: LineSegment StartX=-1 StartY=8.75 StartZ=0 EndX=-4.03109 EndY=10.5 EndZ=0
    g23: LineSegment StartX=-4.03109 StartY=10.5 StartZ=0 EndX=-7.06218 EndY=8.75 EndZ=0
    g24: LineSegment StartX=-7.06218 StartY=8.75 StartZ=0 EndX=-7.06218 EndY=5.25 EndZ=0
    g25: LineSegment StartX=-7.06218 StartY=5.25 StartZ=0 EndX=-4.03109 EndY=3.5 EndZ=0
    g26: LineSegment StartX=-4.03109 StartY=3.5 StartZ=0 EndX=-1 EndY=5.25 EndZ=0
    g27: Circle [constr] CenterX=-4.03109 CenterY=7 CenterZ=0 NormalX=0 NormalY=0 NormalZ=1 AngleXU=0 Radius=3.5
    g28: LineSegment StartX=-4.96891 StartY=-1.75 StartZ=0 EndX=-4.96891 EndY=1.75 EndZ=0
    g29: LineSegment StartX=-4.96891 StartY=1.75 StartZ=0 EndX=-8 EndY=3.5 EndZ=0
    g30: LineSegment StartX=-8 StartY=3.5 StartZ=0 EndX=-11.0311 EndY=1.75 EndZ=0
    g31: LineSegment StartX=-11.0311 StartY=1.75 StartZ=0 EndX=-11.0311 EndY=-1.75 EndZ=0
    g32: LineSegment StartX=-11.0311 StartY=-1.75 StartZ=0 EndX=-8 EndY=-3.5 EndZ=0
    g33: LineSegment StartX=-8 StartY=-3.5 StartZ=0 EndX=-4.96891 EndY=-1.75 EndZ=0
    g34: Circle [constr] CenterX=-8 CenterY=0 CenterZ=0 NormalX=0 NormalY=0 NormalZ=1 AngleXU=0 Radius=3.5
    g35: LineSegment StartX=-4.03109 StartY=-3.5 StartZ=0 EndX=-7.06218 EndY=-5.25 EndZ=0
    g36: LineSegment StartX=-7.06218 StartY=-5.25 StartZ=0 EndX=-7.06218 EndY=-8.75 EndZ=0
    g37: LineSegment StartX=-7.06218 StartY=-8.75 StartZ=0 EndX=-4.03109 EndY=-10.5 EndZ=0
    g38: LineSegment StartX=-4.03109 StartY=-10.5 StartZ=0 EndX=-1 EndY=-8.75 EndZ=0
    g39: LineSegment StartX=-1 StartY=-8.75 StartZ=0 EndX=-1 EndY=-5.25 EndZ=0
    g40: LineSegment StartX=-1 StartY=-5.25 StartZ=0 EndX=-4.03109 EndY=-3.5 EndZ=0
    g41: Circle [constr] CenterX=-4.03109 CenterY=-7 CenterZ=0 NormalX=0 NormalY=0 NormalZ=1 AngleXU=0 Radius=3.5
    g42: LineSegment StartX=4.03109 StartY=-3.5 StartZ=0 EndX=1 EndY=-5.25 EndZ=0
    g43: LineSegment StartX=1 StartY=-5.25 StartZ=0 EndX=1 EndY=-8.75 EndZ=0
    g44: LineSegment StartX=1 StartY=-8.75 StartZ=0 EndX=4.03109 EndY=-10.5 EndZ=0
    g45: LineSegment StartX=4.03109 StartY=-10.5 StartZ=0 EndX=7.06218 EndY=-8.75 EndZ=0
    g46: LineSegment StartX=7.06218 StartY=-8.75 StartZ=0 EndX=7.06218 EndY=-5.25 EndZ=0
    g47: LineSegment StartX=7.06218 StartY=-5.25 StartZ=0 EndX=4.03109 EndY=-3.5 EndZ=0
    g48: Circle [constr] CenterX=4.03109 CenterY=-7 CenterZ=0 NormalX=0 NormalY=0 NormalZ=1 AngleXU=0 Radius=3.5
  constraints (117):
    c: Coincident(g0,g1)
    c: Coincident(g1,g2)
    c: Coincident(g2,g3)
    c: Coincident(g3,g4)
    c: Coincident(g4,g5)
    c: Coincident(g5,g0)
    c: Equal(g0, g1-g5) x5
    c: PointOnObject(g0,g6)
    c: PointOnObject(g1,g6)
    c: PointOnObject(g2,g6)
    c: PointOnObject(g3,g6)
    c: PointOnObject(g4,g6)
    c: PointOnObject(g5,g6)
    c: Coincident(g6,g-1)
    c: Diameter(g6) = 7
    c: PointOnObject(g0,g-2)
    c: Coincident(g7,g8)
    c: Coincident(g8,g9)
    c: Coincident(g9,g10)
    c: Coincident(g10,g11)
    c: Coincident(g11,g12)
    c: Coincident(g12,g7)
    c: Equal(g7, g8-g12) x5
    c: PointOnObject(g7,g13)
    c: PointOnObject(g8,g13)
    c: PointOnObject(g9,g13)
    c: PointOnObject(g10,g13)
    c: PointOnObject(g11,g13)
    c: PointOnObject(g12,g13)
    c: PointOnObject(g13,g-1)
    c: Diameter(g13) = 7
    c: Distance(g6,g13) = 8
    c: Horizontal(g0,g10)
    c: Coincident(g14,g15)
    c: Coincident(g15,g16)
    c: Coincident(g16,g17)
    c: Coincident(g17,g18)
    c: Coincident(g18,g19)
    c: Coincident(g19,g14)
    c: Equal(g14, g15-g19) x5
    c: PointOnObject(g14,g20)
    c: PointOnObject(g15,g20)
    c: PointOnObject(g16,g20)
    c: PointOnObject(g17,g20)
    c: PointOnObject(g18,g20)
    c: PointOnObject(g19,g20)
    c: Diameter(g20) = 7
    c: DistanceY(g-1,g20) = 7
    c: Vertical(g18)
    c: Distance(g17,g-2) = 1
    c: Coincident(g21,g22)
    c: Coincident(g22,g23)
    c: Coincident(g23,g24)
    c: Coincident(g24,g25)
    c: Coincident(g25,g26)
    c: Coincident(g26,g21)
    c: Equal(g21, g22-g26) x5
    c: PointOnObject(g21,g27)
    c: PointOnObject(g22,g27)
    c: PointOnObject(g23,g27)
    c: PointOnObject(g24,g27)
    c: PointOnObject(g25,g27)
    c: PointOnObject(g26,g27)
    c: Diameter(g27) = 7
    c: DistanceY(g-1,g27) = 7
    c: DistanceX(g21,g-1) = 1
    c: Vertical(g21)
    c: Coincident(g28,g29)
    c: Coincident(g29,g30)
    c: Coincident(g30,g31)
    c: Coincident(g31,g32)
    c: Coincident(g32,g33)
    c: Coincident(g33,g28)
    c: Equal(g28, g29-g33) x5
    c: PointOnObject(g28,g34)
    c: PointOnObject(g29,g34)
    c: PointOnObject(g30,g34)
    c: PointOnObject(g31,g34)
    c: PointOnObject(g32,g34)
    c: PointOnObject(g33,g34)
    c: PointOnObject(g34,g-1)
    c: Diameter(g34) = 7
    c: Vertical(g31)
    c: DistanceX(g34,g-1) = 8
    c: Coincident(g35,g36)
    c: Coincident(g36,g37)
    c: Coincident(g37,g38)
    c: Coincident(g38,g39)
    c: Coincident(g39,g40)
    c: Coincident(g40,g35)
    c: Equal(g35, g36-g40) x5
    c: PointOnObject(g35,g41)
    c: PointOnObject(g36,g41)
    c: PointOnObject(g37,g41)
    c: PointOnObject(g38,g41)
    c: PointOnObject(g39,g41)
    c: PointOnObject(g40,g41)
    c: Coincident(g42,g43)
    c: Coincident(g43,g44)
    c: Coincident(g44,g45)
    c: Coincident(g45,g46)
    c: Coincident(g46,g47)
    c: Coincident(g47,g42)
    c: Equal(g42, g43-g47) x5
    c: PointOnObject(g42,g48)
    c: PointOnObject(g43,g48)
    c: PointOnObject(g44,g48)
    c: PointOnObject(g45,g48)
    c: PointOnObject(g46,g48)
    c: PointOnObject(g47,g48)
    c: Equal(g41,g48)
    c: Diameter(g41) = 7
    c: Vertical(g39)
    c: Vertical(g43)
    c: Distance(g-2,g39) = 1
    c: Symmetric(g38,g43,g-2)
    c: Distance(g41,g-1) = 7
FEATURE [Part::Extrusion] Extrude643  label="hex245"
  Base = -> Sketch652
  Dir = (0,-1,2e-16)
  DirMode = 2
  FaceMakerClass = Part::FaceMakerBullseye
  FaceMakerMode = 3
  LengthFwd = 10
  LengthRev = 0
  Placement = pos=(-64,0,14) rot=(0,0,1;0rad)
  Solid = true
  Symmetric = false
FEATURE [Sketcher::SketchObject] Sketch653
  ArcFitTolerance = 1e-06
  FullyConstrained = true
  MakeInternals = false
  Placement = pos=(0,0,0) rot=(1,0,0;1.5708rad)
  sketch-geometry (49):
    g0: LineSegment StartX=1e-16 StartY=3.5 StartZ=0 EndX=-3.03109 EndY=1.75 EndZ=0
    g1: LineSegment StartX=-3.03109 StartY=1.75 StartZ=0 EndX=-3.03109 EndY=-1.75 EndZ=0
    g2: LineSegment StartX=-3.03109 StartY=-1.75 StartZ=0 EndX=-1e-16 EndY=-3.5 EndZ=0
    g3: LineSegment StartX=-1e-16 StartY=-3.5 StartZ=0 EndX=3.03109 EndY=-1.75 EndZ=0
    g4: LineSegment StartX=3.03109 StartY=-1.75 StartZ=0 EndX=3.03109 EndY=1.75 EndZ=0
    g5: LineSegment StartX=3.03109 StartY=1.75 StartZ=0 EndX=1e-16 EndY=3.5 EndZ=0
    g6: Circle [constr] CenterX=0 CenterY=0 CenterZ=0 NormalX=0 NormalY=0 NormalZ=1 AngleXU=0 Radius=3.5
    g7: LineSegment StartX=4.96892 StartY=-1.75002 StartZ=0 EndX=8.00002 EndY=-3.5 EndZ=0
    g8: LineSegment StartX=8.00002 StartY=-3.5 StartZ=0 EndX=11.0311 EndY=-1.74998 EndZ=0
    g9: LineSegment StartX=11.0311 StartY=-1.74998 StartZ=0 EndX=11.0311 EndY=1.75002 EndZ=0
    g10: LineSegment StartX=11.0311 StartY=1.75002 StartZ=0 EndX=7.99998 EndY=3.5 EndZ=0
    g11: LineSegment StartX=7.99998 StartY=3.5 StartZ=0 EndX=4.9689 EndY=1.74998 EndZ=0
    g12: LineSegment StartX=4.9689 StartY=1.74998 StartZ=0 EndX=4.96892 EndY=-1.75002 EndZ=0
    g13: Circle [constr] CenterX=8 CenterY=0 CenterZ=0 NormalX=0 NormalY=0 NormalZ=1 AngleXU=0 Radius=3.5
    g14: LineSegment StartX=4.03109 StartY=3.5 StartZ=0 EndX=7.06218 EndY=5.25 EndZ=0
    g15: LineSegment StartX=7.06218 StartY=5.25 StartZ=0 EndX=7.06218 EndY=8.75 EndZ=0
    g16: LineSegment StartX=7.06218 StartY=8.75 StartZ=0 EndX=4.03109 EndY=10.5 EndZ=0
    g17: LineSegment StartX=4.03109 StartY=10.5 StartZ=0 EndX=1 EndY=8.75 EndZ=0
    g18: LineSegment StartX=1 StartY=8.75 StartZ=0 EndX=1 EndY=5.25 EndZ=0
    g19: LineSegment StartX=1 StartY=5.25 StartZ=0 EndX=4.03109 EndY=3.5 EndZ=0
    g20: Circle [constr] CenterX=4.03109 CenterY=7 CenterZ=0 NormalX=0 NormalY=0 NormalZ=1 AngleXU=0 Radius=3.5
    g21: LineSegment StartX=-1 StartY=5.25 StartZ=0 EndX=-1 EndY=8.75 EndZ=0
    g22: LineSegment StartX=-1 StartY=8.75 StartZ=0 EndX=-4.03109 EndY=10.5 EndZ=0
    g23: LineSegment StartX=-4.03109 StartY=10.5 StartZ=0 EndX=-7.06218 EndY=8.75 EndZ=0
    g24: LineSegment StartX=-7.06218 StartY=8.75 StartZ=0 EndX=-7.06218 EndY=5.25 EndZ=0
    g25: LineSegment StartX=-7.06218 StartY=5.25 StartZ=0 EndX=-4.03109 EndY=3.5 EndZ=0
    g26: LineSegment StartX=-4.03109 StartY=3.5 StartZ=0 EndX=-1 EndY=5.25 EndZ=0
    g27: Circle [constr] CenterX=-4.03109 CenterY=7 CenterZ=0 NormalX=0 NormalY=0 NormalZ=1 AngleXU=0 Radius=3.5
    g28: LineSegment StartX=-4.96891 StartY=-1.75 StartZ=0 EndX=-4.96891 EndY=1.75 EndZ=0
    g29: LineSegment StartX=-4.96891 StartY=1.75 StartZ=0 EndX=-8 EndY=3.5 EndZ=0
    g30: LineSegment StartX=-8 StartY=3.5 StartZ=0 EndX=-11.0311 EndY=1.75 EndZ=0
    g31: LineSegment StartX=-11.0311 StartY=1.75 StartZ=0 EndX=-11.0311 EndY=-1.75 EndZ=0
    g32: LineSegment StartX=-11.0311 StartY=-1.75 StartZ=0 EndX=-8 EndY=-3.5 EndZ=0
    g33: LineSegment StartX=-8 StartY=-3.5 StartZ=0 EndX=-4.96891 EndY=-1.75 EndZ=0
    g34: Circle [constr] CenterX=-8 CenterY=0 CenterZ=0 NormalX=0 NormalY=0 NormalZ=1 AngleXU=0 Radius=3.5
    g35: LineSegment StartX=-4.03109 StartY=-3.5 StartZ=0 EndX=-7.06218 EndY=-5.25 EndZ=0
    g36: LineSegment StartX=-7.06218 StartY=-5.25 StartZ=0 EndX=-7.06218 EndY=-8.75 EndZ=0
    g37: LineSegment StartX=-7.06218 StartY=-8.75 StartZ=0 EndX=-4.03109 EndY=-10.5 EndZ=0
    g38: LineSegment StartX=-4.03109 StartY=-10.5 StartZ=0 EndX=-1 EndY=-8.75 EndZ=0
    g39: LineSegment StartX=-1 StartY=-8.75 StartZ=0 EndX=-1 EndY=-5.25 EndZ=0
    g40: LineSegment StartX=-1 StartY=-5.25 StartZ=0 EndX=-4.03109 EndY=-3.5 EndZ=0
    g41: Circle [constr] CenterX=-4.03109 CenterY=-7 CenterZ=0 NormalX=0 NormalY=0 NormalZ=1 AngleXU=0 Radius=3.5
    g42: LineSegment StartX=4.03109 StartY=-3.5 StartZ=0 EndX=1 EndY=-5.25 EndZ=0
    g43: LineSegment StartX=1 StartY=-5.25 StartZ=0 EndX=1 EndY=-8.75 EndZ=0
    g44: LineSegment StartX=1 StartY=-8.75 StartZ=0 EndX=4.03109 EndY=-10.5 EndZ=0
    g45: LineSegment StartX=4.03109 StartY=-10.5 StartZ=0 EndX=7.06218 EndY=-8.75 EndZ=0
    g46: LineSegment StartX=7.06218 StartY=-8.75 StartZ=0 EndX=7.06218 EndY=-5.25 EndZ=0
    g47: LineSegment StartX=7.06218 StartY=-5.25 StartZ=0 EndX=4.03109 EndY=-3.5 EndZ=0
    g48: Circle [constr] CenterX=4.03109 CenterY=-7 CenterZ=0 NormalX=0 NormalY=0 NormalZ=1 AngleXU=0 Radius=3.5
  constraints (117):
    c: Coincident(g0,g1)
    c: Coincident(g1,g2)
    c: Coincident(g2,g3)
    c: Coincident(g3,g4)
    c: Coincident(g4,g5)
    c: Coincident(g5,g0)
    c: Equal(g0, g1-g5) x5
    c: PointOnObject(g0,g6)
    c: PointOnObject(g1,g6)
    c: PointOnObject(g2,g6)
    c: PointOnObject(g3,g6)
    c: PointOnObject(g4,g6)
    c: PointOnObject(g5,g6)
    c: Coincident(g6,g-1)
    c: Diameter(g6) = 7
    c: PointOnObject(g0,g-2)
    c: Coincident(g7,g8)
    c: Coincident(g8,g9)
    c: Coincident(g9,g10)
    c: Coincident(g10,g11)
    c: Coincident(g11,g12)
    c: Coincident(g12,g7)
    c: Equal(g7, g8-g12) x5
    c: PointOnObject(g7,g13)
    c: PointOnObject(g8,g13)
    c: PointOnObject(g9,g13)
    c: PointOnObject(g10,g13)
    c: PointOnObject(g11,g13)
    c: PointOnObject(g12,g13)
    c: PointOnObject(g13,g-1)
    c: Diameter(g13) = 7
    c: Distance(g6,g13) = 8
    c: Horizontal(g0,g10)
    c: Coincident(g14,g15)
    c: Coincident(g15,g16)
    c: Coincident(g16,g17)
    c: Coincident(g17,g18)
    c: Coincident(g18,g19)
    c: Coincident(g19,g14)
    c: Equal(g14, g15-g19) x5
    c: PointOnObject(g14,g20)
    c: PointOnObject(g15,g20)
    c: PointOnObject(g16,g20)
    c: PointOnObject(g17,g20)
    c: PointOnObject(g18,g20)
    c: PointOnObject(g19,g20)
    c: Diameter(g20) = 7
    c: DistanceY(g-1,g20) = 7
    c: Vertical(g18)
    c: Distance(g17,g-2) = 1
    c: Coincident(g21,g22)
    c: Coincident(g22,g23)
    c: Coincident(g23,g24)
    c: Coincident(g24,g25)
    c: Coincident(g25,g26)
    c: Coincident(g26,g21)
    c: Equal(g21, g22-g26) x5
    c: PointOnObject(g21,g27)
    c: PointOnObject(g22,g27)
    c: PointOnObject(g23,g27)
    c: PointOnObject(g24,g27)
    c: PointOnObject(g25,g27)
    c: PointOnObject(g26,g27)
    c: Diameter(g27) = 7
    c: DistanceY(g-1,g27) = 7
    c: DistanceX(g21,g-1) = 1
    c: Vertical(g21)
    c: Coincident(g28,g29)
    c: Coincident(g29,g30)
    c: Coincident(g30,g31)
    c: Coincident(g31,g32)
    c: Coincident(g32,g33)
    c: Coincident(g33,g28)
    c: Equal(g28, g29-g33) x5
    c: PointOnObject(g28,g34)
    c: PointOnObject(g29,g34)
    c: PointOnObject(g30,g34)
    c: PointOnObject(g31,g34)
    c: PointOnObject(g32,g34)
    c: PointOnObject(g33,g34)
    c: PointOnObject(g34,g-1)
    c: Diameter(g34) = 7
    c: Vertical(g31)
    c: DistanceX(g34,g-1) = 8
    c: Coincident(g35,g36)
    c: Coincident(g36,g37)
    c: Coincident(g37,g38)
    c: Coincident(g38,g39)
    c: Coincident(g39,g40)
    c: Coincident(g40,g35)
    c: Equal(g35, g36-g40) x5
    c: PointOnObject(g35,g41)
    c: PointOnObject(g36,g41)
    c: PointOnObject(g37,g41)
    c: PointOnObject(g38,g41)
    c: PointOnObject(g39,g41)
    c: PointOnObject(g40,g41)
    c: Coincident(g42,g43)
    c: Coincident(g43,g44)
    c: Coincident(g44,g45)
    c: Coincident(g45,g46)
    c: Coincident(g46,g47)
    c: Coincident(g47,g42)
    c: Equal(g42, g43-g47) x5
    c: PointOnObject(g42,g48)
    c: PointOnObject(g43,g48)
    c: PointOnObject(g44,g48)
    c: PointOnObject(g45,g48)
    c: PointOnObject(g46,g48)
    c: PointOnObject(g47,g48)
    c: Equal(g41,g48)
    c: Diameter(g41) = 7
    c: Vertical(g39)
    c: Vertical(g43)
    c: Distance(g-2,g39) = 1
    c: Symmetric(g38,g43,g-2)
    c: Distance(g41,g-1) = 7
FEATURE [Part::Extrusion] Extrude644  label="hex246"
  Base = -> Sketch653
  Dir = (0,-1,2e-16)
  DirMode = 2
  FaceMakerClass = Part::FaceMakerBullseye
  FaceMakerMode = 3
  LengthFwd = 10
  LengthRev = 0
  Placement = pos=(-64,0,-14) rot=(0,0,1;0rad)
  Solid = true
  Symmetric = false
FEATURE [Sketcher::SketchObject] Sketch654
  ArcFitTolerance = 1e-06
  FullyConstrained = true
  MakeInternals = false
  Placement = pos=(0,0,0) rot=(1,0,0;1.5708rad)
  sketch-geometry (49):
    g0: LineSegment StartX=1e-16 StartY=3.5 StartZ=0 EndX=-3.03109 EndY=1.75 EndZ=0
    g1: LineSegment StartX=-3.03109 StartY=1.75 StartZ=0 EndX=-3.03109 EndY=-1.75 EndZ=0
    g2: LineSegment StartX=-3.03109 StartY=-1.75 StartZ=0 EndX=-1e-16 EndY=-3.5 EndZ=0
    g3: LineSegment StartX=-1e-16 StartY=-3.5 StartZ=0 EndX=3.03109 EndY=-1.75 EndZ=0
    g4: LineSegment StartX=3.03109 StartY=-1.75 StartZ=0 EndX=3.03109 EndY=1.75 EndZ=0
    g5: LineSegment StartX=3.03109 StartY=1.75 StartZ=0 EndX=1e-16 EndY=3.5 EndZ=0
    g6: Circle [constr] CenterX=0 CenterY=0 CenterZ=0 NormalX=0 NormalY=0 NormalZ=1 AngleXU=0 Radius=3.5
    g7: LineSegment StartX=4.96892 StartY=-1.75002 StartZ=0 EndX=8.00002 EndY=-3.5 EndZ=0
    g8: LineSegment StartX=8.00002 StartY=-3.5 StartZ=0 EndX=11.0311 EndY=-1.74998 EndZ=0
    g9: LineSegment StartX=11.0311 StartY=-1.74998 StartZ=0 EndX=11.0311 EndY=1.75002 EndZ=0
    g10: LineSegment StartX=11.0311 StartY=1.75002 StartZ=0 EndX=7.99998 EndY=3.5 EndZ=0
    g11: LineSegment StartX=7.99998 StartY=3.5 StartZ=0 EndX=4.9689 EndY=1.74998 EndZ=0
    g12: LineSegment StartX=4.9689 StartY=1.74998 StartZ=0 EndX=4.96892 EndY=-1.75002 EndZ=0
    g13: Circle [constr] CenterX=8 CenterY=0 CenterZ=0 NormalX=0 NormalY=0 NormalZ=1 AngleXU=0 Radius=3.5
    g14: LineSegment StartX=4.03109 StartY=3.5 StartZ=0 EndX=7.06218 EndY=5.25 EndZ=0
    g15: LineSegment StartX=7.06218 StartY=5.25 StartZ=0 EndX=7.06218 EndY=8.75 EndZ=0
    g16: LineSegment StartX=7.06218 StartY=8.75 StartZ=0 EndX=4.03109 EndY=10.5 EndZ=0
    g17: LineSegment StartX=4.03109 StartY=10.5 StartZ=0 EndX=1 EndY=8.75 EndZ=0
    g18: LineSegment StartX=1 StartY=8.75 StartZ=0 EndX=1 EndY=5.25 EndZ=0
    g19: LineSegment StartX=1 StartY=5.25 StartZ=0 EndX=4.03109 EndY=3.5 EndZ=0
    g20: Circle [constr] CenterX=4.03109 CenterY=7 CenterZ=0 NormalX=0 NormalY=0 NormalZ=1 AngleXU=0 Radius=3.5
    g21: LineSegment StartX=-1 StartY=5.25 StartZ=0 EndX=-1 EndY=8.75 EndZ=0
    g22: LineSegment StartX=-1 StartY=8.75 StartZ=0 EndX=-4.03109 EndY=10.5 EndZ=0
    g23: LineSegment StartX=-4.03109 StartY=10.5 StartZ=0 EndX=-7.06218 EndY=8.75 EndZ=0
    g24: LineSegment StartX=-7.06218 StartY=8.75 StartZ=0 EndX=-7.06218 EndY=5.25 EndZ=0
    g25: LineSegment StartX=-7.06218 StartY=5.25 StartZ=0 EndX=-4.03109 EndY=3.5 EndZ=0
    g26: LineSegment StartX=-4.03109 StartY=3.5 StartZ=0 EndX=-1 EndY=5.25 EndZ=0
    g27: Circle [constr] CenterX=-4.03109 CenterY=7 CenterZ=0 NormalX=0 NormalY=0 NormalZ=1 AngleXU=0 Radius=3.5
    g28: LineSegment StartX=-4.96891 StartY=-1.75 StartZ=0 EndX=-4.96891 EndY=1.75 EndZ=0
    g29: LineSegment StartX=-4.96891 StartY=1.75 StartZ=0 EndX=-8 EndY=3.5 EndZ=0
    g30: LineSegment StartX=-8 StartY=3.5 StartZ=0 EndX=-11.0311 EndY=1.75 EndZ=0
    g31: LineSegment StartX=-11.0311 StartY=1.75 StartZ=0 EndX=-11.0311 EndY=-1.75 EndZ=0
    g32: LineSegment StartX=-11.0311 StartY=-1.75 StartZ=0 EndX=-8 EndY=-3.5 EndZ=0
    g33: LineSegment StartX=-8 StartY=-3.5 StartZ=0 EndX=-4.96891 EndY=-1.75 EndZ=0
    g34: Circle [constr] CenterX=-8 CenterY=0 CenterZ=0 NormalX=0 NormalY=0 NormalZ=1 AngleXU=0 Radius=3.5
    g35: LineSegment StartX=-4.03109 StartY=-3.5 StartZ=0 EndX=-7.06218 EndY=-5.25 EndZ=0
    g36: LineSegment StartX=-7.06218 StartY=-5.25 StartZ=0 EndX=-7.06218 EndY=-8.75 EndZ=0
    g37: LineSegment StartX=-7.06218 StartY=-8.75 StartZ=0 EndX=-4.03109 EndY=-10.5 EndZ=0
    g38: LineSegment StartX=-4.03109 StartY=-10.5 StartZ=0 EndX=-1 EndY=-8.75 EndZ=0
    g39: LineSegment StartX=-1 StartY=-8.75 StartZ=0 EndX=-1 EndY=-5.25 EndZ=0
    g40: LineSegment StartX=-1 StartY=-5.25 StartZ=0 EndX=-4.03109 EndY=-3.5 EndZ=0
    g41: Circle [constr] CenterX=-4.03109 CenterY=-7 CenterZ=0 NormalX=0 NormalY=0 NormalZ=1 AngleXU=0 Radius=3.5
    g42: LineSegment StartX=4.03109 StartY=-3.5 StartZ=0 EndX=1 EndY=-5.25 EndZ=0
    g43: LineSegment StartX=1 StartY=-5.25 StartZ=0 EndX=1 EndY=-8.75 EndZ=0
    g44: LineSegment StartX=1 StartY=-8.75 StartZ=0 EndX=4.03109 EndY=-10.5 EndZ=0
    g45: LineSegment StartX=4.03109 StartY=-10.5 StartZ=0 EndX=7.06218 EndY=-8.75 EndZ=0
    g46: LineSegment StartX=7.06218 StartY=-8.75 StartZ=0 EndX=7.06218 EndY=-5.25 EndZ=0
    g47: LineSegment StartX=7.06218 StartY=-5.25 StartZ=0 EndX=4.03109 EndY=-3.5 EndZ=0
    g48: Circle [constr] CenterX=4.03109 CenterY=-7 CenterZ=0 NormalX=0 NormalY=0 NormalZ=1 AngleXU=0 Radius=3.5
  constraints (117):
    c: Coincident(g0,g1)
    c: Coincident(g1,g2)
    c: Coincident(g2,g3)
    c: Coincident(g3,g4)
    c: Coincident(g4,g5)
    c: Coincident(g5,g0)
    c: Equal(g0, g1-g5) x5
    c: PointOnObject(g0,g6)
    c: PointOnObject(g1,g6)
    c: PointOnObject(g2,g6)
    c: PointOnObject(g3,g6)
    c: PointOnObject(g4,g6)
    c: PointOnObject(g5,g6)
    c: Coincident(g6,g-1)
    c: Diameter(g6) = 7
    c: PointOnObject(g0,g-2)
    c: Coincident(g7,g8)
    c: Coincident(g8,g9)
    c: Coincident(g9,g10)
    c: Coincident(g10,g11)
    c: Coincident(g11,g12)
    c: Coincident(g12,g7)
    c: Equal(g7, g8-g12) x5
    c: PointOnObject(g7,g13)
    c: PointOnObject(g8,g13)
    c: PointOnObject(g9,g13)
    c: PointOnObject(g10,g13)
    c: PointOnObject(g11,g13)
    c: PointOnObject(g12,g13)
    c: PointOnObject(g13,g-1)
    c: Diameter(g13) = 7
    c: Distance(g6,g13) = 8
    c: Horizontal(g0,g10)
    c: Coincident(g14,g15)
    c: Coincident(g15,g16)
    c: Coincident(g16,g17)
    c: Coincident(g17,g18)
    c: Coincident(g18,g19)
    c: Coincident(g19,g14)
    c: Equal(g14, g15-g19) x5
    c: PointOnObject(g14,g20)
    c: PointOnObject(g15,g20)
    c: PointOnObject(g16,g20)
    c: PointOnObject(g17,g20)
    c: PointOnObject(g18,g20)
    c: PointOnObject(g19,g20)
    c: Diameter(g20) = 7
    c: DistanceY(g-1,g20) = 7
    c: Vertical(g18)
    c: Distance(g17,g-2) = 1
    c: Coincident(g21,g22)
    c: Coincident(g22,g23)
    c: Coincident(g23,g24)
    c: Coincident(g24,g25)
    c: Coincident(g25,g26)
    c: Coincident(g26,g21)
    c: Equal(g21, g22-g26) x5
    c: PointOnObject(g21,g27)
    c: PointOnObject(g22,g27)
    c: PointOnObject(g23,g27)
    c: PointOnObject(g24,g27)
    c: PointOnObject(g25,g27)
    c: PointOnObject(g26,g27)
    c: Diameter(g27) = 7
    c: DistanceY(g-1,g27) = 7
    c: DistanceX(g21,g-1) = 1
    c: Vertical(g21)
    c: Coincident(g28,g29)
    c: Coincident(g29,g30)
    c: Coincident(g30,g31)
    c: Coincident(g31,g32)
    c: Coincident(g32,g33)
    c: Coincident(g33,g28)
    c: Equal(g28, g29-g33) x5
    c: PointOnObject(g28,g34)
    c: PointOnObject(g29,g34)
    c: PointOnObject(g30,g34)
    c: PointOnObject(g31,g34)
    c: PointOnObject(g32,g34)
    c: PointOnObject(g33,g34)
    c: PointOnObject(g34,g-1)
    c: Diameter(g34) = 7
    c: Vertical(g31)
    c: DistanceX(g34,g-1) = 8
    c: Coincident(g35,g36)
    c: Coincident(g36,g37)
    c: Coincident(g37,g38)
    c: Coincident(g38,g39)
    c: Coincident(g39,g40)
    c: Coincident(g40,g35)
    c: Equal(g35, g36-g40) x5
    c: PointOnObject(g35,g41)
    c: PointOnObject(g36,g41)
    c: PointOnObject(g37,g41)
    c: PointOnObject(g38,g41)
    c: PointOnObject(g39,g41)
    c: PointOnObject(g40,g41)
    c: Coincident(g42,g43)
    c: Coincident(g43,g44)
    c: Coincident(g44,g45)
    c: Coincident(g45,g46)
    c: Coincident(g46,g47)
    c: Coincident(g47,g42)
    c: Equal(g42, g43-g47) x5
    c: PointOnObject(g42,g48)
    c: PointOnObject(g43,g48)
    c: PointOnObject(g44,g48)
    c: PointOnObject(g45,g48)
    c: PointOnObject(g46,g48)
    c: PointOnObject(g47,g48)
    c: Equal(g41,g48)
    c: Diameter(g41) = 7
    c: Vertical(g39)
    c: Vertical(g43)
    c: Distance(g-2,g39) = 1
    c: Symmetric(g38,g43,g-2)
    c: Distance(g41,g-1) = 7
FEATURE [Part::Extrusion] Extrude645  label="hex247"
  Base = -> Sketch654
  Dir = (0,-1,2e-16)
  DirMode = 2
  FaceMakerClass = Part::FaceMakerBullseye
  FaceMakerMode = 3
  LengthFwd = 10
  LengthRev = 0
  Placement = pos=(-48,0,-28) rot=(0,0,1;0rad)
  Solid = true
  Symmetric = false
FEATURE [Sketcher::SketchObject] Sketch655
  ArcFitTolerance = 1e-06
  FullyConstrained = true
  MakeInternals = false
  Placement = pos=(0,0,0) rot=(1,0,0;1.5708rad)
  sketch-geometry (49):
    g0: LineSegment StartX=1e-16 StartY=3.5 StartZ=0 EndX=-3.03109 EndY=1.75 EndZ=0
    g1: LineSegment StartX=-3.03109 StartY=1.75 StartZ=0 EndX=-3.03109 EndY=-1.75 EndZ=0
    g2: LineSegment StartX=-3.03109 StartY=-1.75 StartZ=0 EndX=-1e-16 EndY=-3.5 EndZ=0
    g3: LineSegment StartX=-1e-16 StartY=-3.5 StartZ=0 EndX=3.03109 EndY=-1.75 EndZ=0
    g4: LineSegment StartX=3.03109 StartY=-1.75 StartZ=0 EndX=3.03109 EndY=1.75 EndZ=0
    g5: LineSegment StartX=3.03109 StartY=1.75 StartZ=0 EndX=1e-16 EndY=3.5 EndZ=0
    g6: Circle [constr] CenterX=0 CenterY=0 CenterZ=0 NormalX=0 NormalY=0 NormalZ=1 AngleXU=0 Radius=3.5
    g7: LineSegment StartX=4.96892 StartY=-1.75002 StartZ=0 EndX=8.00002 EndY=-3.5 EndZ=0
    g8: LineSegment StartX=8.00002 StartY=-3.5 StartZ=0 EndX=11.0311 EndY=-1.74998 EndZ=0
    g9: LineSegment StartX=11.0311 StartY=-1.74998 StartZ=0 EndX=11.0311 EndY=1.75002 EndZ=0
    g10: LineSegment StartX=11.0311 StartY=1.75002 StartZ=0 EndX=7.99998 EndY=3.5 EndZ=0
    g11: LineSegment StartX=7.99998 StartY=3.5 StartZ=0 EndX=4.9689 EndY=1.74998 EndZ=0
    g12: LineSegment StartX=4.9689 StartY=1.74998 StartZ=0 EndX=4.96892 EndY=-1.75002 EndZ=0
    g13: Circle [constr] CenterX=8 CenterY=0 CenterZ=0 NormalX=0 NormalY=0 NormalZ=1 AngleXU=0 Radius=3.5
    g14: LineSegment StartX=4.03109 StartY=3.5 StartZ=0 EndX=7.06218 EndY=5.25 EndZ=0
    g15: LineSegment StartX=7.06218 StartY=5.25 StartZ=0 EndX=7.06218 EndY=8.75 EndZ=0
    g16: LineSegment StartX=7.06218 StartY=8.75 StartZ=0 EndX=4.03109 EndY=10.5 EndZ=0
    g17: LineSegment StartX=4.03109 StartY=10.5 StartZ=0 EndX=1 EndY=8.75 EndZ=0
    g18: LineSegment StartX=1 StartY=8.75 StartZ=0 EndX=1 EndY=5.25 EndZ=0
    g19: LineSegment StartX=1 StartY=5.25 StartZ=0 EndX=4.03109 EndY=3.5 EndZ=0
    g20: Circle [constr] CenterX=4.03109 CenterY=7 CenterZ=0 NormalX=0 NormalY=0 NormalZ=1 AngleXU=0 Radius=3.5
    g21: LineSegment StartX=-1 StartY=5.25 StartZ=0 EndX=-1 EndY=8.75 EndZ=0
    g22: LineSegment StartX=-1 StartY=8.75 StartZ=0 EndX=-4.03109 EndY=10.5 EndZ=0
    g23: LineSegment StartX=-4.03109 StartY=10.5 StartZ=0 EndX=-7.06218 EndY=8.75 EndZ=0
    g24: LineSegment StartX=-7.06218 StartY=8.75 StartZ=0 EndX=-7.06218 EndY=5.25 EndZ=0
    g25: LineSegment StartX=-7.06218 StartY=5.25 StartZ=0 EndX=-4.03109 EndY=3.5 EndZ=0
    g26: LineSegment StartX=-4.03109 StartY=3.5 StartZ=0 EndX=-1 EndY=5.25 EndZ=0
    g27: Circle [constr] CenterX=-4.03109 CenterY=7 CenterZ=0 NormalX=0 NormalY=0 NormalZ=1 AngleXU=0 Radius=3.5
    g28: LineSegment StartX=-4.96891 StartY=-1.75 StartZ=0 EndX=-4.96891 EndY=1.75 EndZ=0
    g29: LineSegment StartX=-4.96891 StartY=1.75 StartZ=0 EndX=-8 EndY=3.5 EndZ=0
    g30: LineSegment StartX=-8 StartY=3.5 StartZ=0 EndX=-11.0311 EndY=1.75 EndZ=0
    g31: LineSegment StartX=-11.0311 StartY=1.75 StartZ=0 EndX=-11.0311 EndY=-1.75 EndZ=0
    g32: LineSegment StartX=-11.0311 StartY=-1.75 StartZ=0 EndX=-8 EndY=-3.5 EndZ=0
    g33: LineSegment StartX=-8 StartY=-3.5 StartZ=0 EndX=-4.96891 EndY=-1.75 EndZ=0
    g34: Circle [constr] CenterX=-8 CenterY=0 CenterZ=0 NormalX=0 NormalY=0 NormalZ=1 AngleXU=0 Radius=3.5
    g35: LineSegment StartX=-4.03109 StartY=-3.5 StartZ=0 EndX=-7.06218 EndY=-5.25 EndZ=0
    g36: LineSegment StartX=-7.06218 StartY=-5.25 StartZ=0 EndX=-7.06218 EndY=-8.75 EndZ=0
    g37: LineSegment StartX=-7.06218 StartY=-8.75 StartZ=0 EndX=-4.03109 EndY=-10.5 EndZ=0
    g38: LineSegment StartX=-4.03109 StartY=-10.5 StartZ=0 EndX=-1 EndY=-8.75 EndZ=0
    g39: LineSegment StartX=-1 StartY=-8.75 StartZ=0 EndX=-1 EndY=-5.25 EndZ=0
    g40: LineSegment StartX=-1 StartY=-5.25 StartZ=0 EndX=-4.03109 EndY=-3.5 EndZ=0
    g41: Circle [constr] CenterX=-4.03109 CenterY=-7 CenterZ=0 NormalX=0 NormalY=0 NormalZ=1 AngleXU=0 Radius=3.5
    g42: LineSegment StartX=4.03109 StartY=-3.5 StartZ=0 EndX=1 EndY=-5.25 EndZ=0
    g43: LineSegment StartX=1 StartY=-5.25 StartZ=0 EndX=1 EndY=-8.75 EndZ=0
    g44: LineSegment StartX=1 StartY=-8.75 StartZ=0 EndX=4.03109 EndY=-10.5 EndZ=0
    g45: LineSegment StartX=4.03109 StartY=-10.5 StartZ=0 EndX=7.06218 EndY=-8.75 EndZ=0
    g46: LineSegment StartX=7.06218 StartY=-8.75 StartZ=0 EndX=7.06218 EndY=-5.25 EndZ=0
    g47: LineSegment StartX=7.06218 StartY=-5.25 StartZ=0 EndX=4.03109 EndY=-3.5 EndZ=0
    g48: Circle [constr] CenterX=4.03109 CenterY=-7 CenterZ=0 NormalX=0 NormalY=0 NormalZ=1 AngleXU=0 Radius=3.5
  constraints (117):
    c: Coincident(g0,g1)
    c: Coincident(g1,g2)
    c: Coincident(g2,g3)
    c: Coincident(g3,g4)
    c: Coincident(g4,g5)
    c: Coincident(g5,g0)
    c: Equal(g0, g1-g5) x5
    c: PointOnObject(g0,g6)
    c: PointOnObject(g1,g6)
    c: PointOnObject(g2,g6)
    c: PointOnObject(g3,g6)
    c: PointOnObject(g4,g6)
    c: PointOnObject(g5,g6)
    c: Coincident(g6,g-1)
    c: Diameter(g6) = 7
    c: PointOnObject(g0,g-2)
    c: Coincident(g7,g8)
    c: Coincident(g8,g9)
    c: Coincident(g9,g10)
    c: Coincident(g10,g11)
    c: Coincident(g11,g12)
    c: Coincident(g12,g7)
    c: Equal(g7, g8-g12) x5
    c: PointOnObject(g7,g13)
    c: PointOnObject(g8,g13)
    c: PointOnObject(g9,g13)
    c: PointOnObject(g10,g13)
    c: PointOnObject(g11,g13)
    c: PointOnObject(g12,g13)
    c: PointOnObject(g13,g-1)
    c: Diameter(g13) = 7
    c: Distance(g6,g13) = 8
    c: Horizontal(g0,g10)
    c: Coincident(g14,g15)
    c: Coincident(g15,g16)
    c: Coincident(g16,g17)
    c: Coincident(g17,g18)
    c: Coincident(g18,g19)
    c: Coincident(g19,g14)
    c: Equal(g14, g15-g19) x5
    c: PointOnObject(g14,g20)
    c: PointOnObject(g15,g20)
    c: PointOnObject(g16,g20)
    c: PointOnObject(g17,g20)
    c: PointOnObject(g18,g20)
    c: PointOnObject(g19,g20)
    c: Diameter(g20) = 7
    c: DistanceY(g-1,g20) = 7
    c: Vertical(g18)
    c: Distance(g17,g-2) = 1
    c: Coincident(g21,g22)
    c: Coincident(g22,g23)
    c: Coincident(g23,g24)
    c: Coincident(g24,g25)
    c: Coincident(g25,g26)
    c: Coincident(g26,g21)
    c: Equal(g21, g22-g26) x5
    c: PointOnObject(g21,g27)
    c: PointOnObject(g22,g27)
    c: PointOnObject(g23,g27)
    c: PointOnObject(g24,g27)
    c: PointOnObject(g25,g27)
    c: PointOnObject(g26,g27)
    c: Diameter(g27) = 7
    c: DistanceY(g-1,g27) = 7
    c: DistanceX(g21,g-1) = 1
    c: Vertical(g21)
    c: Coincident(g28,g29)
    c: Coincident(g29,g30)
    c: Coincident(g30,g31)
    c: Coincident(g31,g32)
    c: Coincident(g32,g33)
    c: Coincident(g33,g28)
    c: Equal(g28, g29-g33) x5
    c: PointOnObject(g28,g34)
    c: PointOnObject(g29,g34)
    c: PointOnObject(g30,g34)
    c: PointOnObject(g31,g34)
    c: PointOnObject(g32,g34)
    c: PointOnObject(g33,g34)
    c: PointOnObject(g34,g-1)
    c: Diameter(g34) = 7
    c: Vertical(g31)
    c: DistanceX(g34,g-1) = 8
    c: Coincident(g35,g36)
    c: Coincident(g36,g37)
    c: Coincident(g37,g38)
    c: Coincident(g38,g39)
    c: Coincident(g39,g40)
    c: Coincident(g40,g35)
    c: Equal(g35, g36-g40) x5
    c: PointOnObject(g35,g41)
    c: PointOnObject(g36,g41)
    c: PointOnObject(g37,g41)
    c: PointOnObject(g38,g41)
    c: PointOnObject(g39,g41)
    c: PointOnObject(g40,g41)
    c: Coincident(g42,g43)
    c: Coincident(g43,g44)
    c: Coincident(g44,g45)
    c: Coincident(g45,g46)
    c: Coincident(g46,g47)
    c: Coincident(g47,g42)
    c: Equal(g42, g43-g47) x5
    c: PointOnObject(g42,g48)
    c: PointOnObject(g43,g48)
    c: PointOnObject(g44,g48)
    c: PointOnObject(g45,g48)
    c: PointOnObject(g46,g48)
    c: PointOnObject(g47,g48)
    c: Equal(g41,g48)
    c: Diameter(g41) = 7
    c: Vertical(g39)
    c: Vertical(g43)
    c: Distance(g-2,g39) = 1
    c: Symmetric(g38,g43,g-2)
    c: Distance(g41,g-1) = 7
FEATURE [Part::Extrusion] Extrude646  label="hex248"
  Base = -> Sketch655
  Dir = (0,-1,2e-16)
  DirMode = 2
  FaceMakerClass = Part::FaceMakerBullseye
  FaceMakerMode = 3
  LengthFwd = 10
  LengthRev = 0
  Placement = pos=(-32,0,-42) rot=(0,0,1;0rad)
  Solid = true
  Symmetric = false
FEATURE [Sketcher::SketchObject] Sketch656
  ArcFitTolerance = 1e-06
  FullyConstrained = true
  MakeInternals = false
  Placement = pos=(0,0,0) rot=(1,0,0;1.5708rad)
  sketch-geometry (49):
    g0: LineSegment StartX=1e-16 StartY=3.5 StartZ=0 EndX=-3.03109 EndY=1.75 EndZ=0
    g1: LineSegment StartX=-3.03109 StartY=1.75 StartZ=0 EndX=-3.03109 EndY=-1.75 EndZ=0
    g2: LineSegment StartX=-3.03109 StartY=-1.75 StartZ=0 EndX=-1e-16 EndY=-3.5 EndZ=0
    g3: LineSegment StartX=-1e-16 StartY=-3.5 StartZ=0 EndX=3.03109 EndY=-1.75 EndZ=0
    g4: LineSegment StartX=3.03109 StartY=-1.75 StartZ=0 EndX=3.03109 EndY=1.75 EndZ=0
    g5: LineSegment StartX=3.03109 StartY=1.75 StartZ=0 EndX=1e-16 EndY=3.5 EndZ=0
    g6: Circle [constr] CenterX=0 CenterY=0 CenterZ=0 NormalX=0 NormalY=0 NormalZ=1 AngleXU=0 Radius=3.5
    g7: LineSegment StartX=4.96892 StartY=-1.75002 StartZ=0 EndX=8.00002 EndY=-3.5 EndZ=0
    g8: LineSegment StartX=8.00002 StartY=-3.5 StartZ=0 EndX=11.0311 EndY=-1.74998 EndZ=0
    g9: LineSegment StartX=11.0311 StartY=-1.74998 StartZ=0 EndX=11.0311 EndY=1.75002 EndZ=0
    g10: LineSegment StartX=11.0311 StartY=1.75002 StartZ=0 EndX=7.99998 EndY=3.5 EndZ=0
    g11: LineSegment StartX=7.99998 StartY=3.5 StartZ=0 EndX=4.9689 EndY=1.74998 EndZ=0
    g12: LineSegment StartX=4.9689 StartY=1.74998 StartZ=0 EndX=4.96892 EndY=-1.75002 EndZ=0
    g13: Circle [constr] CenterX=8 CenterY=0 CenterZ=0 NormalX=0 NormalY=0 NormalZ=1 AngleXU=0 Radius=3.5
    g14: LineSegment StartX=4.03109 StartY=3.5 StartZ=0 EndX=7.06218 EndY=5.25 EndZ=0
    g15: LineSegment StartX=7.06218 StartY=5.25 StartZ=0 EndX=7.06218 EndY=8.75 EndZ=0
    g16: LineSegment StartX=7.06218 StartY=8.75 StartZ=0 EndX=4.03109 EndY=10.5 EndZ=0
    g17: LineSegment StartX=4.03109 StartY=10.5 StartZ=0 EndX=1 EndY=8.75 EndZ=0
    g18: LineSegment StartX=1 StartY=8.75 StartZ=0 EndX=1 EndY=5.25 EndZ=0
    g19: LineSegment StartX=1 StartY=5.25 StartZ=0 EndX=4.03109 EndY=3.5 EndZ=0
    g20: Circle [constr] CenterX=4.03109 CenterY=7 CenterZ=0 NormalX=0 NormalY=0 NormalZ=1 AngleXU=0 Radius=3.5
    g21: LineSegment StartX=-1 StartY=5.25 StartZ=0 EndX=-1 EndY=8.75 EndZ=0
    g22: LineSegment StartX=-1 StartY=8.75 StartZ=0 EndX=-4.03109 EndY=10.5 EndZ=0
    g23: LineSegment StartX=-4.03109 StartY=10.5 StartZ=0 EndX=-7.06218 EndY=8.75 EndZ=0
    g24: LineSegment StartX=-7.06218 StartY=8.75 StartZ=0 EndX=-7.06218 EndY=5.25 EndZ=0
    g25: LineSegment StartX=-7.06218 StartY=5.25 StartZ=0 EndX=-4.03109 EndY=3.5 EndZ=0
    g26: LineSegment StartX=-4.03109 StartY=3.5 StartZ=0 EndX=-1 EndY=5.25 EndZ=0
    g27: Circle [constr] CenterX=-4.03109 CenterY=7 CenterZ=0 NormalX=0 NormalY=0 NormalZ=1 AngleXU=0 Radius=3.5
    g28: LineSegment StartX=-4.96891 StartY=-1.75 StartZ=0 EndX=-4.96891 EndY=1.75 EndZ=0
    g29: LineSegment StartX=-4.96891 StartY=1.75 StartZ=0 EndX=-8 EndY=3.5 EndZ=0
    g30: LineSegment StartX=-8 StartY=3.5 StartZ=0 EndX=-11.0311 EndY=1.75 EndZ=0
    g31: LineSegment StartX=-11.0311 StartY=1.75 StartZ=0 EndX=-11.0311 EndY=-1.75 EndZ=0
    g32: LineSegment StartX=-11.0311 StartY=-1.75 StartZ=0 EndX=-8 EndY=-3.5 EndZ=0
    g33: LineSegment StartX=-8 StartY=-3.5 StartZ=0 EndX=-4.96891 EndY=-1.75 EndZ=0
    g34: Circle [constr] CenterX=-8 CenterY=0 CenterZ=0 NormalX=0 NormalY=0 NormalZ=1 AngleXU=0 Radius=3.5
    g35: LineSegment StartX=-4.03109 StartY=-3.5 StartZ=0 EndX=-7.06218 EndY=-5.25 EndZ=0
    g36: LineSegment StartX=-7.06218 StartY=-5.25 StartZ=0 EndX=-7.06218 EndY=-8.75 EndZ=0
    g37: LineSegment StartX=-7.06218 StartY=-8.75 StartZ=0 EndX=-4.03109 EndY=-10.5 EndZ=0
    g38: LineSegment StartX=-4.03109 StartY=-10.5 StartZ=0 EndX=-1 EndY=-8.75 EndZ=0
    g39: LineSegment StartX=-1 StartY=-8.75 StartZ=0 EndX=-1 EndY=-5.25 EndZ=0
    g40: LineSegment StartX=-1 StartY=-5.25 StartZ=0 EndX=-4.03109 EndY=-3.5 EndZ=0
    g41: Circle [constr] CenterX=-4.03109 CenterY=-7 CenterZ=0 NormalX=0 NormalY=0 NormalZ=1 AngleXU=0 Radius=3.5
    g42: LineSegment StartX=4.03109 StartY=-3.5 StartZ=0 EndX=1 EndY=-5.25 EndZ=0
    g43: LineSegment StartX=1 StartY=-5.25 StartZ=0 EndX=1 EndY=-8.75 EndZ=0
    g44: LineSegment StartX=1 StartY=-8.75 StartZ=0 EndX=4.03109 EndY=-10.5 EndZ=0
    g45: LineSegment StartX=4.03109 StartY=-10.5 StartZ=0 EndX=7.06218 EndY=-8.75 EndZ=0
    g46: LineSegment StartX=7.06218 StartY=-8.75 StartZ=0 EndX=7.06218 EndY=-5.25 EndZ=0
    g47: LineSegment StartX=7.06218 StartY=-5.25 StartZ=0 EndX=4.03109 EndY=-3.5 EndZ=0
    g48: Circle [constr] CenterX=4.03109 CenterY=-7 CenterZ=0 NormalX=0 NormalY=0 NormalZ=1 AngleXU=0 Radius=3.5
  constraints (117):
    c: Coincident(g0,g1)
    c: Coincident(g1,g2)
    c: Coincident(g2,g3)
    c: Coincident(g3,g4)
    c: Coincident(g4,g5)
    c: Coincident(g5,g0)
    c: Equal(g0, g1-g5) x5
    c: PointOnObject(g0,g6)
    c: PointOnObject(g1,g6)
    c: PointOnObject(g2,g6)
    c: PointOnObject(g3,g6)
    c: PointOnObject(g4,g6)
    c: PointOnObject(g5,g6)
    c: Coincident(g6,g-1)
    c: Diameter(g6) = 7
    c: PointOnObject(g0,g-2)
    c: Coincident(g7,g8)
    c: Coincident(g8,g9)
    c: Coincident(g9,g10)
    c: Coincident(g10,g11)
    c: Coincident(g11,g12)
    c: Coincident(g12,g7)
    c: Equal(g7, g8-g12) x5
    c: PointOnObject(g7,g13)
    c: PointOnObject(g8,g13)
    c: PointOnObject(g9,g13)
    c: PointOnObject(g10,g13)
    c: PointOnObject(g11,g13)
    c: PointOnObject(g12,g13)
    c: PointOnObject(g13,g-1)
    c: Diameter(g13) = 7
    c: Distance(g6,g13) = 8
    c: Horizontal(g0,g10)
    c: Coincident(g14,g15)
    c: Coincident(g15,g16)
    c: Coincident(g16,g17)
    c: Coincident(g17,g18)
    c: Coincident(g18,g19)
    c: Coincident(g19,g14)
    c: Equal(g14, g15-g19) x5
    c: PointOnObject(g14,g20)
    c: PointOnObject(g15,g20)
    c: PointOnObject(g16,g20)
    c: PointOnObject(g17,g20)
    c: PointOnObject(g18,g20)
    c: PointOnObject(g19,g20)
    c: Diameter(g20) = 7
    c: DistanceY(g-1,g20) = 7
    c: Vertical(g18)
    c: Distance(g17,g-2) = 1
    c: Coincident(g21,g22)
    c: Coincident(g22,g23)
    c: Coincident(g23,g24)
    c: Coincident(g24,g25)
    c: Coincident(g25,g26)
    c: Coincident(g26,g21)
    c: Equal(g21, g22-g26) x5
    c: PointOnObject(g21,g27)
    c: PointOnObject(g22,g27)
    c: PointOnObject(g23,g27)
    c: PointOnObject(g24,g27)
    c: PointOnObject(g25,g27)
    c: PointOnObject(g26,g27)
    c: Diameter(g27) = 7
    c: DistanceY(g-1,g27) = 7
    c: DistanceX(g21,g-1) = 1
    c: Vertical(g21)
    c: Coincident(g28,g29)
    c: Coincident(g29,g30)
    c: Coincident(g30,g31)
    c: Coincident(g31,g32)
    c: Coincident(g32,g33)
    c: Coincident(g33,g28)
    c: Equal(g28, g29-g33) x5
    c: PointOnObject(g28,g34)
    c: PointOnObject(g29,g34)
    c: PointOnObject(g30,g34)
    c: PointOnObject(g31,g34)
    c: PointOnObject(g32,g34)
    c: PointOnObject(g33,g34)
    c: PointOnObject(g34,g-1)
    c: Diameter(g34) = 7
    c: Vertical(g31)
    c: DistanceX(g34,g-1) = 8
    c: Coincident(g35,g36)
    c: Coincident(g36,g37)
    c: Coincident(g37,g38)
    c: Coincident(g38,g39)
    c: Coincident(g39,g40)
    c: Coincident(g40,g35)
    c: Equal(g35, g36-g40) x5
    c: PointOnObject(g35,g41)
    c: PointOnObject(g36,g41)
    c: PointOnObject(g37,g41)
    c: PointOnObject(g38,g41)
    c: PointOnObject(g39,g41)
    c: PointOnObject(g40,g41)
    c: Coincident(g42,g43)
    c: Coincident(g43,g44)
    c: Coincident(g44,g45)
    c: Coincident(g45,g46)
    c: Coincident(g46,g47)
    c: Coincident(g47,g42)
    c: Equal(g42, g43-g47) x5
    c: PointOnObject(g42,g48)
    c: PointOnObject(g43,g48)
    c: PointOnObject(g44,g48)
    c: PointOnObject(g45,g48)
    c: PointOnObject(g46,g48)
    c: PointOnObject(g47,g48)
    c: Equal(g41,g48)
    c: Diameter(g41) = 7
    c: Vertical(g39)
    c: Vertical(g43)
    c: Distance(g-2,g39) = 1
    c: Symmetric(g38,g43,g-2)
    c: Distance(g41,g-1) = 7
FEATURE [Part::Extrusion] Extrude647  label="hex249"
  Base = -> Sketch656
  Dir = (0,-1,2e-16)
  DirMode = 2
  FaceMakerClass = Part::FaceMakerBullseye
  FaceMakerMode = 3
  LengthFwd = 10
  LengthRev = 0
  Placement = pos=(-56,0,-42) rot=(0,0,1;0rad)
  Solid = true
  Symmetric = false
FEATURE [Sketcher::SketchObject] Sketch657
  ArcFitTolerance = 1e-06
  FullyConstrained = true
  MakeInternals = false
  Placement = pos=(0,0,0) rot=(1,0,0;1.5708rad)
  sketch-geometry (49):
    g0: LineSegment StartX=1e-16 StartY=3.5 StartZ=0 EndX=-3.03109 EndY=1.75 EndZ=0
    g1: LineSegment StartX=-3.03109 StartY=1.75 StartZ=0 EndX=-3.03109 EndY=-1.75 EndZ=0
    g2: LineSegment StartX=-3.03109 StartY=-1.75 StartZ=0 EndX=-1e-16 EndY=-3.5 EndZ=0
    g3: LineSegment StartX=-1e-16 StartY=-3.5 StartZ=0 EndX=3.03109 EndY=-1.75 EndZ=0
    g4: LineSegment StartX=3.03109 StartY=-1.75 StartZ=0 EndX=3.03109 EndY=1.75 EndZ=0
    g5: LineSegment StartX=3.03109 StartY=1.75 StartZ=0 EndX=1e-16 EndY=3.5 EndZ=0
    g6: Circle [constr] CenterX=0 CenterY=0 CenterZ=0 NormalX=0 NormalY=0 NormalZ=1 AngleXU=0 Radius=3.5
    g7: LineSegment StartX=4.96892 StartY=-1.75002 StartZ=0 EndX=8.00002 EndY=-3.5 EndZ=0
    g8: LineSegment StartX=8.00002 StartY=-3.5 StartZ=0 EndX=11.0311 EndY=-1.74998 EndZ=0
    g9: LineSegment StartX=11.0311 StartY=-1.74998 StartZ=0 EndX=11.0311 EndY=1.75002 EndZ=0
    g10: LineSegment StartX=11.0311 StartY=1.75002 StartZ=0 EndX=7.99998 EndY=3.5 EndZ=0
    g11: LineSegment StartX=7.99998 StartY=3.5 StartZ=0 EndX=4.9689 EndY=1.74998 EndZ=0
    g12: LineSegment StartX=4.9689 StartY=1.74998 StartZ=0 EndX=4.96892 EndY=-1.75002 EndZ=0
    g13: Circle [constr] CenterX=8 CenterY=0 CenterZ=0 NormalX=0 NormalY=0 NormalZ=1 AngleXU=0 Radius=3.5
    g14: LineSegment StartX=4.03109 StartY=3.5 StartZ=0 EndX=7.06218 EndY=5.25 EndZ=0
    g15: LineSegment StartX=7.06218 StartY=5.25 StartZ=0 EndX=7.06218 EndY=8.75 EndZ=0
    g16: LineSegment StartX=7.06218 StartY=8.75 StartZ=0 EndX=4.03109 EndY=10.5 EndZ=0
    g17: LineSegment StartX=4.03109 StartY=10.5 StartZ=0 EndX=1 EndY=8.75 EndZ=0
    g18: LineSegment StartX=1 StartY=8.75 StartZ=0 EndX=1 EndY=5.25 EndZ=0
    g19: LineSegment StartX=1 StartY=5.25 StartZ=0 EndX=4.03109 EndY=3.5 EndZ=0
    g20: Circle [constr] CenterX=4.03109 CenterY=7 CenterZ=0 NormalX=0 NormalY=0 NormalZ=1 AngleXU=0 Radius=3.5
    g21: LineSegment StartX=-1 StartY=5.25 StartZ=0 EndX=-1 EndY=8.75 EndZ=0
    g22: LineSegment StartX=-1 StartY=8.75 StartZ=0 EndX=-4.03109 EndY=10.5 EndZ=0
    g23: LineSegment StartX=-4.03109 StartY=10.5 StartZ=0 EndX=-7.06218 EndY=8.75 EndZ=0
    g24: LineSegment StartX=-7.06218 StartY=8.75 StartZ=0 EndX=-7.06218 EndY=5.25 EndZ=0
    g25: LineSegment StartX=-7.06218 StartY=5.25 StartZ=0 EndX=-4.03109 EndY=3.5 EndZ=0
    g26: LineSegment StartX=-4.03109 StartY=3.5 StartZ=0 EndX=-1 EndY=5.25 EndZ=0
    g27: Circle [constr] CenterX=-4.03109 CenterY=7 CenterZ=0 NormalX=0 NormalY=0 NormalZ=1 AngleXU=0 Radius=3.5
    g28: LineSegment StartX=-4.96891 StartY=-1.75 StartZ=0 EndX=-4.96891 EndY=1.75 EndZ=0
    g29: LineSegment StartX=-4.96891 StartY=1.75 StartZ=0 EndX=-8 EndY=3.5 EndZ=0
    g30: LineSegment StartX=-8 StartY=3.5 StartZ=0 EndX=-11.0311 EndY=1.75 EndZ=0
    g31: LineSegment StartX=-11.0311 StartY=1.75 StartZ=0 EndX=-11.0311 EndY=-1.75 EndZ=0
    g32: LineSegment StartX=-11.0311 StartY=-1.75 StartZ=0 EndX=-8 EndY=-3.5 EndZ=0
    g33: LineSegment StartX=-8 StartY=-3.5 StartZ=0 EndX=-4.96891 EndY=-1.75 EndZ=0
    g34: Circle [constr] CenterX=-8 CenterY=0 CenterZ=0 NormalX=0 NormalY=0 NormalZ=1 AngleXU=0 Radius=3.5
    g35: LineSegment StartX=-4.03109 StartY=-3.5 StartZ=0 EndX=-7.06218 EndY=-5.25 EndZ=0
    g36: LineSegment StartX=-7.06218 StartY=-5.25 StartZ=0 EndX=-7.06218 EndY=-8.75 EndZ=0
    g37: LineSegment StartX=-7.06218 StartY=-8.75 StartZ=0 EndX=-4.03109 EndY=-10.5 EndZ=0
    g38: LineSegment StartX=-4.03109 StartY=-10.5 StartZ=0 EndX=-1 EndY=-8.75 EndZ=0
    g39: LineSegment StartX=-1 StartY=-8.75 StartZ=0 EndX=-1 EndY=-5.25 EndZ=0
    g40: LineSegment StartX=-1 StartY=-5.25 StartZ=0 EndX=-4.03109 EndY=-3.5 EndZ=0
    g41: Circle [constr] CenterX=-4.03109 CenterY=-7 CenterZ=0 NormalX=0 NormalY=0 NormalZ=1 AngleXU=0 Radius=3.5
    g42: LineSegment StartX=4.03109 StartY=-3.5 StartZ=0 EndX=1 EndY=-5.25 EndZ=0
    g43: LineSegment StartX=1 StartY=-5.25 StartZ=0 EndX=1 EndY=-8.75 EndZ=0
    g44: LineSegment StartX=1 StartY=-8.75 StartZ=0 EndX=4.03109 EndY=-10.5 EndZ=0
    g45: LineSegment StartX=4.03109 StartY=-10.5 StartZ=0 EndX=7.06218 EndY=-8.75 EndZ=0
    g46: LineSegment StartX=7.06218 StartY=-8.75 StartZ=0 EndX=7.06218 EndY=-5.25 EndZ=0
    g47: LineSegment StartX=7.06218 StartY=-5.25 StartZ=0 EndX=4.03109 EndY=-3.5 EndZ=0
    g48: Circle [constr] CenterX=4.03109 CenterY=-7 CenterZ=0 NormalX=0 NormalY=0 NormalZ=1 AngleXU=0 Radius=3.5
  constraints (117):
    c: Coincident(g0,g1)
    c: Coincident(g1,g2)
    c: Coincident(g2,g3)
    c: Coincident(g3,g4)
    c: Coincident(g4,g5)
    c: Coincident(g5,g0)
    c: Equal(g0, g1-g5) x5
    c: PointOnObject(g0,g6)
    c: PointOnObject(g1,g6)
    c: PointOnObject(g2,g6)
    c: PointOnObject(g3,g6)
    c: PointOnObject(g4,g6)
    c: PointOnObject(g5,g6)
    c: Coincident(g6,g-1)
    c: Diameter(g6) = 7
    c: PointOnObject(g0,g-2)
    c: Coincident(g7,g8)
    c: Coincident(g8,g9)
    c: Coincident(g9,g10)
    c: Coincident(g10,g11)
    c: Coincident(g11,g12)
    c: Coincident(g12,g7)
    c: Equal(g7, g8-g12) x5
    c: PointOnObject(g7,g13)
    c: PointOnObject(g8,g13)
    c: PointOnObject(g9,g13)
    c: PointOnObject(g10,g13)
    c: PointOnObject(g11,g13)
    c: PointOnObject(g12,g13)
    c: PointOnObject(g13,g-1)
    c: Diameter(g13) = 7
    c: Distance(g6,g13) = 8
    c: Horizontal(g0,g10)
    c: Coincident(g14,g15)
    c: Coincident(g15,g16)
    c: Coincident(g16,g17)
    c: Coincident(g17,g18)
    c: Coincident(g18,g19)
    c: Coincident(g19,g14)
    c: Equal(g14, g15-g19) x5
    c: PointOnObject(g14,g20)
    c: PointOnObject(g15,g20)
    c: PointOnObject(g16,g20)
    c: PointOnObject(g17,g20)
    c: PointOnObject(g18,g20)
    c: PointOnObject(g19,g20)
    c: Diameter(g20) = 7
    c: DistanceY(g-1,g20) = 7
    c: Vertical(g18)
    c: Distance(g17,g-2) = 1
    c: Coincident(g21,g22)
    c: Coincident(g22,g23)
    c: Coincident(g23,g24)
    c: Coincident(g24,g25)
    c: Coincident(g25,g26)
    c: Coincident(g26,g21)
    c: Equal(g21, g22-g26) x5
    c: PointOnObject(g21,g27)
    c: PointOnObject(g22,g27)
    c: PointOnObject(g23,g27)
    c: PointOnObject(g24,g27)
    c: PointOnObject(g25,g27)
    c: PointOnObject(g26,g27)
    c: Diameter(g27) = 7
    c: DistanceY(g-1,g27) = 7
    c: DistanceX(g21,g-1) = 1
    c: Vertical(g21)
    c: Coincident(g28,g29)
    c: Coincident(g29,g30)
    c: Coincident(g30,g31)
    c: Coincident(g31,g32)
    c: Coincident(g32,g33)
    c: Coincident(g33,g28)
    c: Equal(g28, g29-g33) x5
    c: PointOnObject(g28,g34)
    c: PointOnObject(g29,g34)
    c: PointOnObject(g30,g34)
    c: PointOnObject(g31,g34)
    c: PointOnObject(g32,g34)
    c: PointOnObject(g33,g34)
    c: PointOnObject(g34,g-1)
    c: Diameter(g34) = 7
    c: Vertical(g31)
    c: DistanceX(g34,g-1) = 8
    c: Coincident(g35,g36)
    c: Coincident(g36,g37)
    c: Coincident(g37,g38)
    c: Coincident(g38,g39)
    c: Coincident(g39,g40)
    c: Coincident(g40,g35)
    c: Equal(g35, g36-g40) x5
    c: PointOnObject(g35,g41)
    c: PointOnObject(g36,g41)
    c: PointOnObject(g37,g41)
    c: PointOnObject(g38,g41)
    c: PointOnObject(g39,g41)
    c: PointOnObject(g40,g41)
    c: Coincident(g42,g43)
    c: Coincident(g43,g44)
    c: Coincident(g44,g45)
    c: Coincident(g45,g46)
    c: Coincident(g46,g47)
    c: Coincident(g47,g42)
    c: Equal(g42, g43-g47) x5
    c: PointOnObject(g42,g48)
    c: PointOnObject(g43,g48)
    c: PointOnObject(g44,g48)
    c: PointOnObject(g45,g48)
    c: PointOnObject(g46,g48)
    c: PointOnObject(g47,g48)
    c: Equal(g41,g48)
    c: Diameter(g41) = 7
    c: Vertical(g39)
    c: Vertical(g43)
    c: Distance(g-2,g39) = 1
    c: Symmetric(g38,g43,g-2)
    c: Distance(g41,g-1) = 7
FEATURE [Part::Extrusion] Extrude648  label="hex250"
  Base = -> Sketch657
  Dir = (0,-1,2e-16)
  DirMode = 2
  FaceMakerClass = Part::FaceMakerBullseye
  FaceMakerMode = 3
  LengthFwd = 10
  LengthRev = 0
  Placement = pos=(-40,0,-56) rot=(0,0,1;0rad)
  Solid = true
  Symmetric = false
FEATURE [Sketcher::SketchObject] Sketch658
  ArcFitTolerance = 1e-06
  FullyConstrained = true
  MakeInternals = false
  Placement = pos=(0,0,0) rot=(1,0,0;1.5708rad)
  sketch-geometry (49):
    g0: LineSegment StartX=1e-16 StartY=3.5 StartZ=0 EndX=-3.03109 EndY=1.75 EndZ=0
    g1: LineSegment StartX=-3.03109 StartY=1.75 StartZ=0 EndX=-3.03109 EndY=-1.75 EndZ=0
    g2: LineSegment StartX=-3.03109 StartY=-1.75 StartZ=0 EndX=-1e-16 EndY=-3.5 EndZ=0
    g3: LineSegment StartX=-1e-16 StartY=-3.5 StartZ=0 EndX=3.03109 EndY=-1.75 EndZ=0
    g4: LineSegment StartX=3.03109 StartY=-1.75 StartZ=0 EndX=3.03109 EndY=1.75 EndZ=0
    g5: LineSegment StartX=3.03109 StartY=1.75 StartZ=0 EndX=1e-16 EndY=3.5 EndZ=0
    g6: Circle [constr] CenterX=0 CenterY=0 CenterZ=0 NormalX=0 NormalY=0 NormalZ=1 AngleXU=0 Radius=3.5
    g7: LineSegment StartX=4.96892 StartY=-1.75002 StartZ=0 EndX=8.00002 EndY=-3.5 EndZ=0
    g8: LineSegment StartX=8.00002 StartY=-3.5 StartZ=0 EndX=11.0311 EndY=-1.74998 EndZ=0
    g9: LineSegment StartX=11.0311 StartY=-1.74998 StartZ=0 EndX=11.0311 EndY=1.75002 EndZ=0
    g10: LineSegment StartX=11.0311 StartY=1.75002 StartZ=0 EndX=7.99998 EndY=3.5 EndZ=0
    g11: LineSegment StartX=7.99998 StartY=3.5 StartZ=0 EndX=4.9689 EndY=1.74998 EndZ=0
    g12: LineSegment StartX=4.9689 StartY=1.74998 StartZ=0 EndX=4.96892 EndY=-1.75002 EndZ=0
    g13: Circle [constr] CenterX=8 CenterY=0 CenterZ=0 NormalX=0 NormalY=0 NormalZ=1 AngleXU=0 Radius=3.5
    g14: LineSegment StartX=4.03109 StartY=3.5 StartZ=0 EndX=7.06218 EndY=5.25 EndZ=0
    g15: LineSegment StartX=7.06218 StartY=5.25 StartZ=0 EndX=7.06218 EndY=8.75 EndZ=0
    g16: LineSegment StartX=7.06218 StartY=8.75 StartZ=0 EndX=4.03109 EndY=10.5 EndZ=0
    g17: LineSegment StartX=4.03109 StartY=10.5 StartZ=0 EndX=1 EndY=8.75 EndZ=0
    g18: LineSegment StartX=1 StartY=8.75 StartZ=0 EndX=1 EndY=5.25 EndZ=0
    g19: LineSegment StartX=1 StartY=5.25 StartZ=0 EndX=4.03109 EndY=3.5 EndZ=0
    g20: Circle [constr] CenterX=4.03109 CenterY=7 CenterZ=0 NormalX=0 NormalY=0 NormalZ=1 AngleXU=0 Radius=3.5
    g21: LineSegment StartX=-1 StartY=5.25 StartZ=0 EndX=-1 EndY=8.75 EndZ=0
    g22: LineSegment StartX=-1 StartY=8.75 StartZ=0 EndX=-4.03109 EndY=10.5 EndZ=0
    g23: LineSegment StartX=-4.03109 StartY=10.5 StartZ=0 EndX=-7.06218 EndY=8.75 EndZ=0
    g24: LineSegment StartX=-7.06218 StartY=8.75 StartZ=0 EndX=-7.06218 EndY=5.25 EndZ=0
    g25: LineSegment StartX=-7.06218 StartY=5.25 StartZ=0 EndX=-4.03109 EndY=3.5 EndZ=0
    g26: LineSegment StartX=-4.03109 StartY=3.5 StartZ=0 EndX=-1 EndY=5.25 EndZ=0
    g27: Circle [constr] CenterX=-4.03109 CenterY=7 CenterZ=0 NormalX=0 NormalY=0 NormalZ=1 AngleXU=0 Radius=3.5
    g28: LineSegment StartX=-4.96891 StartY=-1.75 StartZ=0 EndX=-4.96891 EndY=1.75 EndZ=0
    g29: LineSegment StartX=-4.96891 StartY=1.75 StartZ=0 EndX=-8 EndY=3.5 EndZ=0
    g30: LineSegment StartX=-8 StartY=3.5 StartZ=0 EndX=-11.0311 EndY=1.75 EndZ=0
    g31: LineSegment StartX=-11.0311 StartY=1.75 StartZ=0 EndX=-11.0311 EndY=-1.75 EndZ=0
    g32: LineSegment StartX=-11.0311 StartY=-1.75 StartZ=0 EndX=-8 EndY=-3.5 EndZ=0
    g33: LineSegment StartX=-8 StartY=-3.5 StartZ=0 EndX=-4.96891 EndY=-1.75 EndZ=0
    g34: Circle [constr] CenterX=-8 CenterY=0 CenterZ=0 NormalX=0 NormalY=0 NormalZ=1 AngleXU=0 Radius=3.5
    g35: LineSegment StartX=-4.03109 StartY=-3.5 StartZ=0 EndX=-7.06218 EndY=-5.25 EndZ=0
    g36: LineSegment StartX=-7.06218 StartY=-5.25 StartZ=0 EndX=-7.06218 EndY=-8.75 EndZ=0
    g37: LineSegment StartX=-7.06218 StartY=-8.75 StartZ=0 EndX=-4.03109 EndY=-10.5 EndZ=0
    g38: LineSegment StartX=-4.03109 StartY=-10.5 StartZ=0 EndX=-1 EndY=-8.75 EndZ=0
    g39: LineSegment StartX=-1 StartY=-8.75 StartZ=0 EndX=-1 EndY=-5.25 EndZ=0
    g40: LineSegment StartX=-1 StartY=-5.25 StartZ=0 EndX=-4.03109 EndY=-3.5 EndZ=0
    g41: Circle [constr] CenterX=-4.03109 CenterY=-7 CenterZ=0 NormalX=0 NormalY=0 NormalZ=1 AngleXU=0 Radius=3.5
    g42: LineSegment StartX=4.03109 StartY=-3.5 StartZ=0 EndX=1 EndY=-5.25 EndZ=0
    g43: LineSegment StartX=1 StartY=-5.25 StartZ=0 EndX=1 EndY=-8.75 EndZ=0
    g44: LineSegment StartX=1 StartY=-8.75 StartZ=0 EndX=4.03109 EndY=-10.5 EndZ=0
    g45: LineSegment StartX=4.03109 StartY=-10.5 StartZ=0 EndX=7.06218 EndY=-8.75 EndZ=0
    g46: LineSegment StartX=7.06218 StartY=-8.75 StartZ=0 EndX=7.06218 EndY=-5.25 EndZ=0
    g47: LineSegment StartX=7.06218 StartY=-5.25 StartZ=0 EndX=4.03109 EndY=-3.5 EndZ=0
    g48: Circle [constr] CenterX=4.03109 CenterY=-7 CenterZ=0 NormalX=0 NormalY=0 NormalZ=1 AngleXU=0 Radius=3.5
  constraints (117):
    c: Coincident(g0,g1)
    c: Coincident(g1,g2)
    c: Coincident(g2,g3)
    c: Coincident(g3,g4)
    c: Coincident(g4,g5)
    c: Coincident(g5,g0)
    c: Equal(g0, g1-g5) x5
    c: PointOnObject(g0,g6)
    c: PointOnObject(g1,g6)
    c: PointOnObject(g2,g6)
    c: PointOnObject(g3,g6)
    c: PointOnObject(g4,g6)
    c: PointOnObject(g5,g6)
    c: Coincident(g6,g-1)
    c: Diameter(g6) = 7
    c: PointOnObject(g0,g-2)
    c: Coincident(g7,g8)
    c: Coincident(g8,g9)
    c: Coincident(g9,g10)
    c: Coincident(g10,g11)
    c: Coincident(g11,g12)
    c: Coincident(g12,g7)
    c: Equal(g7, g8-g12) x5
    c: PointOnObject(g7,g13)
    c: PointOnObject(g8,g13)
    c: PointOnObject(g9,g13)
    c: PointOnObject(g10,g13)
    c: PointOnObject(g11,g13)
    c: PointOnObject(g12,g13)
    c: PointOnObject(g13,g-1)
    c: Diameter(g13) = 7
    c: Distance(g6,g13) = 8
    c: Horizontal(g0,g10)
    c: Coincident(g14,g15)
    c: Coincident(g15,g16)
    c: Coincident(g16,g17)
    c: Coincident(g17,g18)
    c: Coincident(g18,g19)
    c: Coincident(g19,g14)
    c: Equal(g14, g15-g19) x5
    c: PointOnObject(g14,g20)
    c: PointOnObject(g15,g20)
    c: PointOnObject(g16,g20)
    c: PointOnObject(g17,g20)
    c: PointOnObject(g18,g20)
    c: PointOnObject(g19,g20)
    c: Diameter(g20) = 7
    c: DistanceY(g-1,g20) = 7
    c: Vertical(g18)
    c: Distance(g17,g-2) = 1
    c: Coincident(g21,g22)
    c: Coincident(g22,g23)
    c: Coincident(g23,g24)
    c: Coincident(g24,g25)
    c: Coincident(g25,g26)
    c: Coincident(g26,g21)
    c: Equal(g21, g22-g26) x5
    c: PointOnObject(g21,g27)
    c: PointOnObject(g22,g27)
    c: PointOnObject(g23,g27)
    c: PointOnObject(g24,g27)
    c: PointOnObject(g25,g27)
    c: PointOnObject(g26,g27)
    c: Diameter(g27) = 7
    c: DistanceY(g-1,g27) = 7
    c: DistanceX(g21,g-1) = 1
    c: Vertical(g21)
    c: Coincident(g28,g29)
    c: Coincident(g29,g30)
    c: Coincident(g30,g31)
    c: Coincident(g31,g32)
    c: Coincident(g32,g33)
    c: Coincident(g33,g28)
    c: Equal(g28, g29-g33) x5
    c: PointOnObject(g28,g34)
    c: PointOnObject(g29,g34)
    c: PointOnObject(g30,g34)
    c: PointOnObject(g31,g34)
    c: PointOnObject(g32,g34)
    c: PointOnObject(g33,g34)
    c: PointOnObject(g34,g-1)
    c: Diameter(g34) = 7
    c: Vertical(g31)
    c: DistanceX(g34,g-1) = 8
    c: Coincident(g35,g36)
    c: Coincident(g36,g37)
    c: Coincident(g37,g38)
    c: Coincident(g38,g39)
    c: Coincident(g39,g40)
    c: Coincident(g40,g35)
    c: Equal(g35, g36-g40) x5
    c: PointOnObject(g35,g41)
    c: PointOnObject(g36,g41)
    c: PointOnObject(g37,g41)
    c: PointOnObject(g38,g41)
    c: PointOnObject(g39,g41)
    c: PointOnObject(g40,g41)
    c: Coincident(g42,g43)
    c: Coincident(g43,g44)
    c: Coincident(g44,g45)
    c: Coincident(g45,g46)
    c: Coincident(g46,g47)
    c: Coincident(g47,g42)
    c: Equal(g42, g43-g47) x5
    c: PointOnObject(g42,g48)
    c: PointOnObject(g43,g48)
    c: PointOnObject(g44,g48)
    c: PointOnObject(g45,g48)
    c: PointOnObject(g46,g48)
    c: PointOnObject(g47,g48)
    c: Equal(g41,g48)
    c: Diameter(g41) = 7
    c: Vertical(g39)
    c: Vertical(g43)
    c: Distance(g-2,g39) = 1
    c: Symmetric(g38,g43,g-2)
    c: Distance(g41,g-1) = 7
FEATURE [Part::Extrusion] Extrude649  label="hex251"
  Base = -> Sketch658
  Dir = (0,-1,2e-16)
  DirMode = 2
  FaceMakerClass = Part::FaceMakerBullseye
  FaceMakerMode = 3
  LengthFwd = 10
  LengthRev = 0
  Placement = pos=(-16,0,-56) rot=(0,0,1;0rad)
  Solid = true
  Symmetric = false
FEATURE [Sketcher::SketchObject] Sketch659
  ArcFitTolerance = 1e-06
  FullyConstrained = true
  MakeInternals = false
  Placement = pos=(0,0,0) rot=(1,0,0;1.5708rad)
  sketch-geometry (49):
    g0: LineSegment StartX=1e-16 StartY=3.5 StartZ=0 EndX=-3.03109 EndY=1.75 EndZ=0
    g1: LineSegment StartX=-3.03109 StartY=1.75 StartZ=0 EndX=-3.03109 EndY=-1.75 EndZ=0
    g2: LineSegment StartX=-3.03109 StartY=-1.75 StartZ=0 EndX=-1e-16 EndY=-3.5 EndZ=0
    g3: LineSegment StartX=-1e-16 StartY=-3.5 StartZ=0 EndX=3.03109 EndY=-1.75 EndZ=0
    g4: LineSegment StartX=3.03109 StartY=-1.75 StartZ=0 EndX=3.03109 EndY=1.75 EndZ=0
    g5: LineSegment StartX=3.03109 StartY=1.75 StartZ=0 EndX=1e-16 EndY=3.5 EndZ=0
    g6: Circle [constr] CenterX=0 CenterY=0 CenterZ=0 NormalX=0 NormalY=0 NormalZ=1 AngleXU=0 Radius=3.5
    g7: LineSegment StartX=4.96892 StartY=-1.75002 StartZ=0 EndX=8.00002 EndY=-3.5 EndZ=0
    g8: LineSegment StartX=8.00002 StartY=-3.5 StartZ=0 EndX=11.0311 EndY=-1.74998 EndZ=0
    g9: LineSegment StartX=11.0311 StartY=-1.74998 StartZ=0 EndX=11.0311 EndY=1.75002 EndZ=0
    g10: LineSegment StartX=11.0311 StartY=1.75002 StartZ=0 EndX=7.99998 EndY=3.5 EndZ=0
    g11: LineSegment StartX=7.99998 StartY=3.5 StartZ=0 EndX=4.9689 EndY=1.74998 EndZ=0
    g12: LineSegment StartX=4.9689 StartY=1.74998 StartZ=0 EndX=4.96892 EndY=-1.75002 EndZ=0
    g13: Circle [constr] CenterX=8 CenterY=0 CenterZ=0 NormalX=0 NormalY=0 NormalZ=1 AngleXU=0 Radius=3.5
    g14: LineSegment StartX=4.03109 StartY=3.5 StartZ=0 EndX=7.06218 EndY=5.25 EndZ=0
    g15: LineSegment StartX=7.06218 StartY=5.25 StartZ=0 EndX=7.06218 EndY=8.75 EndZ=0
    g16: LineSegment StartX=7.06218 StartY=8.75 StartZ=0 EndX=4.03109 EndY=10.5 EndZ=0
    g17: LineSegment StartX=4.03109 StartY=10.5 StartZ=0 EndX=1 EndY=8.75 EndZ=0
    g18: LineSegment StartX=1 StartY=8.75 StartZ=0 EndX=1 EndY=5.25 EndZ=0
    g19: LineSegment StartX=1 StartY=5.25 StartZ=0 EndX=4.03109 EndY=3.5 EndZ=0
    g20: Circle [constr] CenterX=4.03109 CenterY=7 CenterZ=0 NormalX=0 NormalY=0 NormalZ=1 AngleXU=0 Radius=3.5
    g21: LineSegment StartX=-1 StartY=5.25 StartZ=0 EndX=-1 EndY=8.75 EndZ=0
    g22: LineSegment StartX=-1 StartY=8.75 StartZ=0 EndX=-4.03109 EndY=10.5 EndZ=0
    g23: LineSegment StartX=-4.03109 StartY=10.5 StartZ=0 EndX=-7.06218 EndY=8.75 EndZ=0
    g24: LineSegment StartX=-7.06218 StartY=8.75 StartZ=0 EndX=-7.06218 EndY=5.25 EndZ=0
    g25: LineSegment StartX=-7.06218 StartY=5.25 StartZ=0 EndX=-4.03109 EndY=3.5 EndZ=0
    g26: LineSegment StartX=-4.03109 StartY=3.5 StartZ=0 EndX=-1 EndY=5.25 EndZ=0
    g27: Circle [constr] CenterX=-4.03109 CenterY=7 CenterZ=0 NormalX=0 NormalY=0 NormalZ=1 AngleXU=0 Radius=3.5
    g28: LineSegment StartX=-4.96891 StartY=-1.75 StartZ=0 EndX=-4.96891 EndY=1.75 EndZ=0
    g29: LineSegment StartX=-4.96891 StartY=1.75 StartZ=0 EndX=-8 EndY=3.5 EndZ=0
    g30: LineSegment StartX=-8 StartY=3.5 StartZ=0 EndX=-11.0311 EndY=1.75 EndZ=0
    g31: LineSegment StartX=-11.0311 StartY=1.75 StartZ=0 EndX=-11.0311 EndY=-1.75 EndZ=0
    g32: LineSegment StartX=-11.0311 StartY=-1.75 StartZ=0 EndX=-8 EndY=-3.5 EndZ=0
    g33: LineSegment StartX=-8 StartY=-3.5 StartZ=0 EndX=-4.96891 EndY=-1.75 EndZ=0
    g34: Circle [constr] CenterX=-8 CenterY=0 CenterZ=0 NormalX=0 NormalY=0 NormalZ=1 AngleXU=0 Radius=3.5
    g35: LineSegment StartX=-4.03109 StartY=-3.5 StartZ=0 EndX=-7.06218 EndY=-5.25 EndZ=0
    g36: LineSegment StartX=-7.06218 StartY=-5.25 StartZ=0 EndX=-7.06218 EndY=-8.75 EndZ=0
    g37: LineSegment StartX=-7.06218 StartY=-8.75 StartZ=0 EndX=-4.03109 EndY=-10.5 EndZ=0
    g38: LineSegment StartX=-4.03109 StartY=-10.5 StartZ=0 EndX=-1 EndY=-8.75 EndZ=0
    g39: LineSegment StartX=-1 StartY=-8.75 StartZ=0 EndX=-1 EndY=-5.25 EndZ=0
    g40: LineSegment StartX=-1 StartY=-5.25 StartZ=0 EndX=-4.03109 EndY=-3.5 EndZ=0
    g41: Circle [constr] CenterX=-4.03109 CenterY=-7 CenterZ=0 NormalX=0 NormalY=0 NormalZ=1 AngleXU=0 Radius=3.5
    g42: LineSegment StartX=4.03109 StartY=-3.5 StartZ=0 EndX=1 EndY=-5.25 EndZ=0
    g43: LineSegment StartX=1 StartY=-5.25 StartZ=0 EndX=1 EndY=-8.75 EndZ=0
    g44: LineSegment StartX=1 StartY=-8.75 StartZ=0 EndX=4.03109 EndY=-10.5 EndZ=0
    g45: LineSegment StartX=4.03109 StartY=-10.5 StartZ=0 EndX=7.06218 EndY=-8.75 EndZ=0
    g46: LineSegment StartX=7.06218 StartY=-8.75 StartZ=0 EndX=7.06218 EndY=-5.25 EndZ=0
    g47: LineSegment StartX=7.06218 StartY=-5.25 StartZ=0 EndX=4.03109 EndY=-3.5 EndZ=0
    g48: Circle [constr] CenterX=4.03109 CenterY=-7 CenterZ=0 NormalX=0 NormalY=0 NormalZ=1 AngleXU=0 Radius=3.5
  constraints (117):
    c: Coincident(g0,g1)
    c: Coincident(g1,g2)
    c: Coincident(g2,g3)
    c: Coincident(g3,g4)
    c: Coincident(g4,g5)
    c: Coincident(g5,g0)
    c: Equal(g0, g1-g5) x5
    c: PointOnObject(g0,g6)
    c: PointOnObject(g1,g6)
    c: PointOnObject(g2,g6)
    c: PointOnObject(g3,g6)
    c: PointOnObject(g4,g6)
    c: PointOnObject(g5,g6)
    c: Coincident(g6,g-1)
    c: Diameter(g6) = 7
    c: PointOnObject(g0,g-2)
    c: Coincident(g7,g8)
    c: Coincident(g8,g9)
    c: Coincident(g9,g10)
    c: Coincident(g10,g11)
    c: Coincident(g11,g12)
    c: Coincident(g12,g7)
    c: Equal(g7, g8-g12) x5
    c: PointOnObject(g7,g13)
    c: PointOnObject(g8,g13)
    c: PointOnObject(g9,g13)
    c: PointOnObject(g10,g13)
    c: PointOnObject(g11,g13)
    c: PointOnObject(g12,g13)
    c: PointOnObject(g13,g-1)
    c: Diameter(g13) = 7
    c: Distance(g6,g13) = 8
    c: Horizontal(g0,g10)
    c: Coincident(g14,g15)
    c: Coincident(g15,g16)
    c: Coincident(g16,g17)
    c: Coincident(g17,g18)
    c: Coincident(g18,g19)
    c: Coincident(g19,g14)
    c: Equal(g14, g15-g19) x5
    c: PointOnObject(g14,g20)
    c: PointOnObject(g15,g20)
    c: PointOnObject(g16,g20)
    c: PointOnObject(g17,g20)
    c: PointOnObject(g18,g20)
    c: PointOnObject(g19,g20)
    c: Diameter(g20) = 7
    c: DistanceY(g-1,g20) = 7
    c: Vertical(g18)
    c: Distance(g17,g-2) = 1
    c: Coincident(g21,g22)
    c: Coincident(g22,g23)
    c: Coincident(g23,g24)
    c: Coincident(g24,g25)
    c: Coincident(g25,g26)
    c: Coincident(g26,g21)
    c: Equal(g21, g22-g26) x5
    c: PointOnObject(g21,g27)
    c: PointOnObject(g22,g27)
    c: PointOnObject(g23,g27)
    c: PointOnObject(g24,g27)
    c: PointOnObject(g25,g27)
    c: PointOnObject(g26,g27)
    c: Diameter(g27) = 7
    c: DistanceY(g-1,g27) = 7
    c: DistanceX(g21,g-1) = 1
    c: Vertical(g21)
    c: Coincident(g28,g29)
    c: Coincident(g29,g30)
    c: Coincident(g30,g31)
    c: Coincident(g31,g32)
    c: Coincident(g32,g33)
    c: Coincident(g33,g28)
    c: Equal(g28, g29-g33) x5
    c: PointOnObject(g28,g34)
    c: PointOnObject(g29,g34)
    c: PointOnObject(g30,g34)
    c: PointOnObject(g31,g34)
    c: PointOnObject(g32,g34)
    c: PointOnObject(g33,g34)
    c: PointOnObject(g34,g-1)
    c: Diameter(g34) = 7
    c: Vertical(g31)
    c: DistanceX(g34,g-1) = 8
    c: Coincident(g35,g36)
    c: Coincident(g36,g37)
    c: Coincident(g37,g38)
    c: Coincident(g38,g39)
    c: Coincident(g39,g40)
    c: Coincident(g40,g35)
    c: Equal(g35, g36-g40) x5
    c: PointOnObject(g35,g41)
    c: PointOnObject(g36,g41)
    c: PointOnObject(g37,g41)
    c: PointOnObject(g38,g41)
    c: PointOnObject(g39,g41)
    c: PointOnObject(g40,g41)
    c: Coincident(g42,g43)
    c: Coincident(g43,g44)
    c: Coincident(g44,g45)
    c: Coincident(g45,g46)
    c: Coincident(g46,g47)
    c: Coincident(g47,g42)
    c: Equal(g42, g43-g47) x5
    c: PointOnObject(g42,g48)
    c: PointOnObject(g43,g48)
    c: PointOnObject(g44,g48)
    c: PointOnObject(g45,g48)
    c: PointOnObject(g46,g48)
    c: PointOnObject(g47,g48)
    c: Equal(g41,g48)
    c: Diameter(g41) = 7
    c: Vertical(g39)
    c: Vertical(g43)
    c: Distance(g-2,g39) = 1
    c: Symmetric(g38,g43,g-2)
    c: Distance(g41,g-1) = 7
FEATURE [Part::Extrusion] Extrude650  label="hex252"
  Base = -> Sketch659
  Dir = (0,-1,2e-16)
  DirMode = 2
  FaceMakerClass = Part::FaceMakerBullseye
  FaceMakerMode = 3
  LengthFwd = 10
  LengthRev = 0
  Placement = pos=(8,0,-56) rot=(0,0,1;0rad)
  Solid = true
  Symmetric = false
FEATURE [Sketcher::SketchObject] Sketch660
  ArcFitTolerance = 1e-06
  FullyConstrained = true
  MakeInternals = false
  Placement = pos=(0,0,0) rot=(1,0,0;1.5708rad)
  sketch-geometry (49):
    g0: LineSegment StartX=1e-16 StartY=3.5 StartZ=0 EndX=-3.03109 EndY=1.75 EndZ=0
    g1: LineSegment StartX=-3.03109 StartY=1.75 StartZ=0 EndX=-3.03109 EndY=-1.75 EndZ=0
    g2: LineSegment StartX=-3.03109 StartY=-1.75 StartZ=0 EndX=-1e-16 EndY=-3.5 EndZ=0
    g3: LineSegment StartX=-1e-16 StartY=-3.5 StartZ=0 EndX=3.03109 EndY=-1.75 EndZ=0
    g4: LineSegment StartX=3.03109 StartY=-1.75 StartZ=0 EndX=3.03109 EndY=1.75 EndZ=0
    g5: LineSegment StartX=3.03109 StartY=1.75 StartZ=0 EndX=1e-16 EndY=3.5 EndZ=0
    g6: Circle [constr] CenterX=0 CenterY=0 CenterZ=0 NormalX=0 NormalY=0 NormalZ=1 AngleXU=0 Radius=3.5
    g7: LineSegment StartX=4.96892 StartY=-1.75002 StartZ=0 EndX=8.00002 EndY=-3.5 EndZ=0
    g8: LineSegment StartX=8.00002 StartY=-3.5 StartZ=0 EndX=11.0311 EndY=-1.74998 EndZ=0
    g9: LineSegment StartX=11.0311 StartY=-1.74998 StartZ=0 EndX=11.0311 EndY=1.75002 EndZ=0
    g10: LineSegment StartX=11.0311 StartY=1.75002 StartZ=0 EndX=7.99998 EndY=3.5 EndZ=0
    g11: LineSegment StartX=7.99998 StartY=3.5 StartZ=0 EndX=4.9689 EndY=1.74998 EndZ=0
    g12: LineSegment StartX=4.9689 StartY=1.74998 StartZ=0 EndX=4.96892 EndY=-1.75002 EndZ=0
    g13: Circle [constr] CenterX=8 CenterY=0 CenterZ=0 NormalX=0 NormalY=0 NormalZ=1 AngleXU=0 Radius=3.5
    g14: LineSegment StartX=4.03109 StartY=3.5 StartZ=0 EndX=7.06218 EndY=5.25 EndZ=0
    g15: LineSegment StartX=7.06218 StartY=5.25 StartZ=0 EndX=7.06218 EndY=8.75 EndZ=0
    g16: LineSegment StartX=7.06218 StartY=8.75 StartZ=0 EndX=4.03109 EndY=10.5 EndZ=0
    g17: LineSegment StartX=4.03109 StartY=10.5 StartZ=0 EndX=1 EndY=8.75 EndZ=0
    g18: LineSegment StartX=1 StartY=8.75 StartZ=0 EndX=1 EndY=5.25 EndZ=0
    g19: LineSegment StartX=1 StartY=5.25 StartZ=0 EndX=4.03109 EndY=3.5 EndZ=0
    g20: Circle [constr] CenterX=4.03109 CenterY=7 CenterZ=0 NormalX=0 NormalY=0 NormalZ=1 AngleXU=0 Radius=3.5
    g21: LineSegment StartX=-1 StartY=5.25 StartZ=0 EndX=-1 EndY=8.75 EndZ=0
    g22: LineSegment StartX=-1 StartY=8.75 StartZ=0 EndX=-4.03109 EndY=10.5 EndZ=0
    g23: LineSegment StartX=-4.03109 StartY=10.5 StartZ=0 EndX=-7.06218 EndY=8.75 EndZ=0
    g24: LineSegment StartX=-7.06218 StartY=8.75 StartZ=0 EndX=-7.06218 EndY=5.25 EndZ=0
    g25: LineSegment StartX=-7.06218 StartY=5.25 StartZ=0 EndX=-4.03109 EndY=3.5 EndZ=0
    g26: LineSegment StartX=-4.03109 StartY=3.5 StartZ=0 EndX=-1 EndY=5.25 EndZ=0
    g27: Circle [constr] CenterX=-4.03109 CenterY=7 CenterZ=0 NormalX=0 NormalY=0 NormalZ=1 AngleXU=0 Radius=3.5
    g28: LineSegment StartX=-4.96891 StartY=-1.75 StartZ=0 EndX=-4.96891 EndY=1.75 EndZ=0
    g29: LineSegment StartX=-4.96891 StartY=1.75 StartZ=0 EndX=-8 EndY=3.5 EndZ=0
    g30: LineSegment StartX=-8 StartY=3.5 StartZ=0 EndX=-11.0311 EndY=1.75 EndZ=0
    g31: LineSegment StartX=-11.0311 StartY=1.75 StartZ=0 EndX=-11.0311 EndY=-1.75 EndZ=0
    g32: LineSegment StartX=-11.0311 StartY=-1.75 StartZ=0 EndX=-8 EndY=-3.5 EndZ=0
    g33: LineSegment StartX=-8 StartY=-3.5 StartZ=0 EndX=-4.96891 EndY=-1.75 EndZ=0
    g34: Circle [constr] CenterX=-8 CenterY=0 CenterZ=0 NormalX=0 NormalY=0 NormalZ=1 AngleXU=0 Radius=3.5
    g35: LineSegment StartX=-4.03109 StartY=-3.5 StartZ=0 EndX=-7.06218 EndY=-5.25 EndZ=0
    g36: LineSegment StartX=-7.06218 StartY=-5.25 StartZ=0 EndX=-7.06218 EndY=-8.75 EndZ=0
    g37: LineSegment StartX=-7.06218 StartY=-8.75 StartZ=0 EndX=-4.03109 EndY=-10.5 EndZ=0
    g38: LineSegment StartX=-4.03109 StartY=-10.5 StartZ=0 EndX=-1 EndY=-8.75 EndZ=0
    g39: LineSegment StartX=-1 StartY=-8.75 StartZ=0 EndX=-1 EndY=-5.25 EndZ=0
    g40: LineSegment StartX=-1 StartY=-5.25 StartZ=0 EndX=-4.03109 EndY=-3.5 EndZ=0
    g41: Circle [constr] CenterX=-4.03109 CenterY=-7 CenterZ=0 NormalX=0 NormalY=0 NormalZ=1 AngleXU=0 Radius=3.5
    g42: LineSegment StartX=4.03109 StartY=-3.5 StartZ=0 EndX=1 EndY=-5.25 EndZ=0
    g43: LineSegment StartX=1 StartY=-5.25 StartZ=0 EndX=1 EndY=-8.75 EndZ=0
    g44: LineSegment StartX=1 StartY=-8.75 StartZ=0 EndX=4.03109 EndY=-10.5 EndZ=0
    g45: LineSegment StartX=4.03109 StartY=-10.5 StartZ=0 EndX=7.06218 EndY=-8.75 EndZ=0
    g46: LineSegment StartX=7.06218 StartY=-8.75 StartZ=0 EndX=7.06218 EndY=-5.25 EndZ=0
    g47: LineSegment StartX=7.06218 StartY=-5.25 StartZ=0 EndX=4.03109 EndY=-3.5 EndZ=0
    g48: Circle [constr] CenterX=4.03109 CenterY=-7 CenterZ=0 NormalX=0 NormalY=0 NormalZ=1 AngleXU=0 Radius=3.5
  constraints (117):
    c: Coincident(g0,g1)
    c: Coincident(g1,g2)
    c: Coincident(g2,g3)
    c: Coincident(g3,g4)
    c: Coincident(g4,g5)
    c: Coincident(g5,g0)
    c: Equal(g0, g1-g5) x5
    c: PointOnObject(g0,g6)
    c: PointOnObject(g1,g6)
    c: PointOnObject(g2,g6)
    c: PointOnObject(g3,g6)
    c: PointOnObject(g4,g6)
    c: PointOnObject(g5,g6)
    c: Coincident(g6,g-1)
    c: Diameter(g6) = 7
    c: PointOnObject(g0,g-2)
    c: Coincident(g7,g8)
    c: Coincident(g8,g9)
    c: Coincident(g9,g10)
    c: Coincident(g10,g11)
    c: Coincident(g11,g12)
    c: Coincident(g12,g7)
    c: Equal(g7, g8-g12) x5
    c: PointOnObject(g7,g13)
    c: PointOnObject(g8,g13)
    c: PointOnObject(g9,g13)
    c: PointOnObject(g10,g13)
    c: PointOnObject(g11,g13)
    c: PointOnObject(g12,g13)
    c: PointOnObject(g13,g-1)
    c: Diameter(g13) = 7
    c: Distance(g6,g13) = 8
    c: Horizontal(g0,g10)
    c: Coincident(g14,g15)
    c: Coincident(g15,g16)
    c: Coincident(g16,g17)
    c: Coincident(g17,g18)
    c: Coincident(g18,g19)
    c: Coincident(g19,g14)
    c: Equal(g14, g15-g19) x5
    c: PointOnObject(g14,g20)
    c: PointOnObject(g15,g20)
    c: PointOnObject(g16,g20)
    c: PointOnObject(g17,g20)
    c: PointOnObject(g18,g20)
    c: PointOnObject(g19,g20)
    c: Diameter(g20) = 7
    c: DistanceY(g-1,g20) = 7
    c: Vertical(g18)
    c: Distance(g17,g-2) = 1
    c: Coincident(g21,g22)
    c: Coincident(g22,g23)
    c: Coincident(g23,g24)
    c: Coincident(g24,g25)
    c: Coincident(g25,g26)
    c: Coincident(g26,g21)
    c: Equal(g21, g22-g26) x5
    c: PointOnObject(g21,g27)
    c: PointOnObject(g22,g27)
    c: PointOnObject(g23,g27)
    c: PointOnObject(g24,g27)
    c: PointOnObject(g25,g27)
    c: PointOnObject(g26,g27)
    c: Diameter(g27) = 7
    c: DistanceY(g-1,g27) = 7
    c: DistanceX(g21,g-1) = 1
    c: Vertical(g21)
    c: Coincident(g28,g29)
    c: Coincident(g29,g30)
    c: Coincident(g30,g31)
    c: Coincident(g31,g32)
    c: Coincident(g32,g33)
    c: Coincident(g33,g28)
    c: Equal(g28, g29-g33) x5
    c: PointOnObject(g28,g34)
    c: PointOnObject(g29,g34)
    c: PointOnObject(g30,g34)
    c: PointOnObject(g31,g34)
    c: PointOnObject(g32,g34)
    c: PointOnObject(g33,g34)
    c: PointOnObject(g34,g-1)
    c: Diameter(g34) = 7
    c: Vertical(g31)
    c: DistanceX(g34,g-1) = 8
    c: Coincident(g35,g36)
    c: Coincident(g36,g37)
    c: Coincident(g37,g38)
    c: Coincident(g38,g39)
    c: Coincident(g39,g40)
    c: Coincident(g40,g35)
    c: Equal(g35, g36-g40) x5
    c: PointOnObject(g35,g41)
    c: PointOnObject(g36,g41)
    c: PointOnObject(g37,g41)
    c: PointOnObject(g38,g41)
    c: PointOnObject(g39,g41)
    c: PointOnObject(g40,g41)
    c: Coincident(g42,g43)
    c: Coincident(g43,g44)
    c: Coincident(g44,g45)
    c: Coincident(g45,g46)
    c: Coincident(g46,g47)
    c: Coincident(g47,g42)
    c: Equal(g42, g43-g47) x5
    c: PointOnObject(g42,g48)
    c: PointOnObject(g43,g48)
    c: PointOnObject(g44,g48)
    c: PointOnObject(g45,g48)
    c: PointOnObject(g46,g48)
    c: PointOnObject(g47,g48)
    c: Equal(g41,g48)
    c: Diameter(g41) = 7
    c: Vertical(g39)
    c: Vertical(g43)
    c: Distance(g-2,g39) = 1
    c: Symmetric(g38,g43,g-2)
    c: Distance(g41,g-1) = 7
FEATURE [Part::Extrusion] Extrude651  label="hex253"
  Base = -> Sketch660
  Dir = (0,-1,2e-16)
  DirMode = 2
  FaceMakerClass = Part::FaceMakerBullseye
  FaceMakerMode = 3
  LengthFwd = 10
  LengthRev = 0
  Placement = pos=(28,0,-49) rot=(0,0,1;0rad)
  Solid = true
  Symmetric = false
FEATURE [Sketcher::SketchObject] Sketch661
  ArcFitTolerance = 1e-06
  FullyConstrained = true
  MakeInternals = false
  Placement = pos=(0,0,0) rot=(1,0,0;1.5708rad)
  sketch-geometry (49):
    g0: LineSegment StartX=1e-16 StartY=3.5 StartZ=0 EndX=-3.03109 EndY=1.75 EndZ=0
    g1: LineSegment StartX=-3.03109 StartY=1.75 StartZ=0 EndX=-3.03109 EndY=-1.75 EndZ=0
    g2: LineSegment StartX=-3.03109 StartY=-1.75 StartZ=0 EndX=-1e-16 EndY=-3.5 EndZ=0
    g3: LineSegment StartX=-1e-16 StartY=-3.5 StartZ=0 EndX=3.03109 EndY=-1.75 EndZ=0
    g4: LineSegment StartX=3.03109 StartY=-1.75 StartZ=0 EndX=3.03109 EndY=1.75 EndZ=0
    g5: LineSegment StartX=3.03109 StartY=1.75 StartZ=0 EndX=1e-16 EndY=3.5 EndZ=0
    g6: Circle [constr] CenterX=0 CenterY=0 CenterZ=0 NormalX=0 NormalY=0 NormalZ=1 AngleXU=0 Radius=3.5
    g7: LineSegment StartX=4.96892 StartY=-1.75002 StartZ=0 EndX=8.00002 EndY=-3.5 EndZ=0
    g8: LineSegment StartX=8.00002 StartY=-3.5 StartZ=0 EndX=11.0311 EndY=-1.74998 EndZ=0
    g9: LineSegment StartX=11.0311 StartY=-1.74998 StartZ=0 EndX=11.0311 EndY=1.75002 EndZ=0
    g10: LineSegment StartX=11.0311 StartY=1.75002 StartZ=0 EndX=7.99998 EndY=3.5 EndZ=0
    g11: LineSegment StartX=7.99998 StartY=3.5 StartZ=0 EndX=4.9689 EndY=1.74998 EndZ=0
    g12: LineSegment StartX=4.9689 StartY=1.74998 StartZ=0 EndX=4.96892 EndY=-1.75002 EndZ=0
    g13: Circle [constr] CenterX=8 CenterY=0 CenterZ=0 NormalX=0 NormalY=0 NormalZ=1 AngleXU=0 Radius=3.5
    g14: LineSegment StartX=4.03109 StartY=3.5 StartZ=0 EndX=7.06218 EndY=5.25 EndZ=0
    g15: LineSegment StartX=7.06218 StartY=5.25 StartZ=0 EndX=7.06218 EndY=8.75 EndZ=0
    g16: LineSegment StartX=7.06218 StartY=8.75 StartZ=0 EndX=4.03109 EndY=10.5 EndZ=0
    g17: LineSegment StartX=4.03109 StartY=10.5 StartZ=0 EndX=1 EndY=8.75 EndZ=0
    g18: LineSegment StartX=1 StartY=8.75 StartZ=0 EndX=1 EndY=5.25 EndZ=0
    g19: LineSegment StartX=1 StartY=5.25 StartZ=0 EndX=4.03109 EndY=3.5 EndZ=0
    g20: Circle [constr] CenterX=4.03109 CenterY=7 CenterZ=0 NormalX=0 NormalY=0 NormalZ=1 AngleXU=0 Radius=3.5
    g21: LineSegment StartX=-1 StartY=5.25 StartZ=0 EndX=-1 EndY=8.75 EndZ=0
    g22: LineSegment StartX=-1 StartY=8.75 StartZ=0 EndX=-4.03109 EndY=10.5 EndZ=0
    g23: LineSegment StartX=-4.03109 StartY=10.5 StartZ=0 EndX=-7.06218 EndY=8.75 EndZ=0
    g24: LineSegment StartX=-7.06218 StartY=8.75 StartZ=0 EndX=-7.06218 EndY=5.25 EndZ=0
    g25: LineSegment StartX=-7.06218 StartY=5.25 StartZ=0 EndX=-4.03109 EndY=3.5 EndZ=0
    g26: LineSegment StartX=-4.03109 StartY=3.5 StartZ=0 EndX=-1 EndY=5.25 EndZ=0
    g27: Circle [constr] CenterX=-4.03109 CenterY=7 CenterZ=0 NormalX=0 NormalY=0 NormalZ=1 AngleXU=0 Radius=3.5
    g28: LineSegment StartX=-4.96891 StartY=-1.75 StartZ=0 EndX=-4.96891 EndY=1.75 EndZ=0
    g29: LineSegment StartX=-4.96891 StartY=1.75 StartZ=0 EndX=-8 EndY=3.5 EndZ=0
    g30: LineSegment StartX=-8 StartY=3.5 StartZ=0 EndX=-11.0311 EndY=1.75 EndZ=0
    g31: LineSegment StartX=-11.0311 StartY=1.75 StartZ=0 EndX=-11.0311 EndY=-1.75 EndZ=0
    g32: LineSegment StartX=-11.0311 StartY=-1.75 StartZ=0 EndX=-8 EndY=-3.5 EndZ=0
    g33: LineSegment StartX=-8 StartY=-3.5 StartZ=0 EndX=-4.96891 EndY=-1.75 EndZ=0
    g34: Circle [constr] CenterX=-8 CenterY=0 CenterZ=0 NormalX=0 NormalY=0 NormalZ=1 AngleXU=0 Radius=3.5
    g35: LineSegment StartX=-4.03109 StartY=-3.5 StartZ=0 EndX=-7.06218 EndY=-5.25 EndZ=0
    g36: LineSegment StartX=-7.06218 StartY=-5.25 StartZ=0 EndX=-7.06218 EndY=-8.75 EndZ=0
    g37: LineSegment StartX=-7.06218 StartY=-8.75 StartZ=0 EndX=-4.03109 EndY=-10.5 EndZ=0
    g38: LineSegment StartX=-4.03109 StartY=-10.5 StartZ=0 EndX=-1 EndY=-8.75 EndZ=0
    g39: LineSegment StartX=-1 StartY=-8.75 StartZ=0 EndX=-1 EndY=-5.25 EndZ=0
    g40: LineSegment StartX=-1 StartY=-5.25 StartZ=0 EndX=-4.03109 EndY=-3.5 EndZ=0
    g41: Circle [constr] CenterX=-4.03109 CenterY=-7 CenterZ=0 NormalX=0 NormalY=0 NormalZ=1 AngleXU=0 Radius=3.5
    g42: LineSegment StartX=4.03109 StartY=-3.5 StartZ=0 EndX=1 EndY=-5.25 EndZ=0
    g43: LineSegment StartX=1 StartY=-5.25 StartZ=0 EndX=1 EndY=-8.75 EndZ=0
    g44: LineSegment StartX=1 StartY=-8.75 StartZ=0 EndX=4.03109 EndY=-10.5 EndZ=0
    g45: LineSegment StartX=4.03109 StartY=-10.5 StartZ=0 EndX=7.06218 EndY=-8.75 EndZ=0
    g46: LineSegment StartX=7.06218 StartY=-8.75 StartZ=0 EndX=7.06218 EndY=-5.25 EndZ=0
    g47: LineSegment StartX=7.06218 StartY=-5.25 StartZ=0 EndX=4.03109 EndY=-3.5 EndZ=0
    g48: Circle [constr] CenterX=4.03109 CenterY=-7 CenterZ=0 NormalX=0 NormalY=0 NormalZ=1 AngleXU=0 Radius=3.5
  constraints (117):
    c: Coincident(g0,g1)
    c: Coincident(g1,g2)
    c: Coincident(g2,g3)
    c: Coincident(g3,g4)
    c: Coincident(g4,g5)
    c: Coincident(g5,g0)
    c: Equal(g0, g1-g5) x5
    c: PointOnObject(g0,g6)
    c: PointOnObject(g1,g6)
    c: PointOnObject(g2,g6)
    c: PointOnObject(g3,g6)
    c: PointOnObject(g4,g6)
    c: PointOnObject(g5,g6)
    c: Coincident(g6,g-1)
    c: Diameter(g6) = 7
    c: PointOnObject(g0,g-2)
    c: Coincident(g7,g8)
    c: Coincident(g8,g9)
    c: Coincident(g9,g10)
    c: Coincident(g10,g11)
    c: Coincident(g11,g12)
    c: Coincident(g12,g7)
    c: Equal(g7, g8-g12) x5
    c: PointOnObject(g7,g13)
    c: PointOnObject(g8,g13)
    c: PointOnObject(g9,g13)
    c: PointOnObject(g10,g13)
    c: PointOnObject(g11,g13)
    c: PointOnObject(g12,g13)
    c: PointOnObject(g13,g-1)
    c: Diameter(g13) = 7
    c: Distance(g6,g13) = 8
    c: Horizontal(g0,g10)
    c: Coincident(g14,g15)
    c: Coincident(g15,g16)
    c: Coincident(g16,g17)
    c: Coincident(g17,g18)
    c: Coincident(g18,g19)
    c: Coincident(g19,g14)
    c: Equal(g14, g15-g19) x5
    c: PointOnObject(g14,g20)
    c: PointOnObject(g15,g20)
    c: PointOnObject(g16,g20)
    c: PointOnObject(g17,g20)
    c: PointOnObject(g18,g20)
    c: PointOnObject(g19,g20)
    c: Diameter(g20) = 7
    c: DistanceY(g-1,g20) = 7
    c: Vertical(g18)
    c: Distance(g17,g-2) = 1
    c: Coincident(g21,g22)
    c: Coincident(g22,g23)
    c: Coincident(g23,g24)
    c: Coincident(g24,g25)
    c: Coincident(g25,g26)
    c: Coincident(g26,g21)
    c: Equal(g21, g22-g26) x5
    c: PointOnObject(g21,g27)
    c: PointOnObject(g22,g27)
    c: PointOnObject(g23,g27)
    c: PointOnObject(g24,g27)
    c: PointOnObject(g25,g27)
    c: PointOnObject(g26,g27)
    c: Diameter(g27) = 7
    c: DistanceY(g-1,g27) = 7
    c: DistanceX(g21,g-1) = 1
    c: Vertical(g21)
    c: Coincident(g28,g29)
    c: Coincident(g29,g30)
    c: Coincident(g30,g31)
    c: Coincident(g31,g32)
    c: Coincident(g32,g33)
    c: Coincident(g33,g28)
    c: Equal(g28, g29-g33) x5
    c: PointOnObject(g28,g34)
    c: PointOnObject(g29,g34)
    c: PointOnObject(g30,g34)
    c: PointOnObject(g31,g34)
    c: PointOnObject(g32,g34)
    c: PointOnObject(g33,g34)
    c: PointOnObject(g34,g-1)
    c: Diameter(g34) = 7
    c: Vertical(g31)
    c: DistanceX(g34,g-1) = 8
    c: Coincident(g35,g36)
    c: Coincident(g36,g37)
    c: Coincident(g37,g38)
    c: Coincident(g38,g39)
    c: Coincident(g39,g40)
    c: Coincident(g40,g35)
    c: Equal(g35, g36-g40) x5
    c: PointOnObject(g35,g41)
    c: PointOnObject(g36,g41)
    c: PointOnObject(g37,g41)
    c: PointOnObject(g38,g41)
    c: PointOnObject(g39,g41)
    c: PointOnObject(g40,g41)
    c: Coincident(g42,g43)
    c: Coincident(g43,g44)
    c: Coincident(g44,g45)
    c: Coincident(g45,g46)
    c: Coincident(g46,g47)
    c: Coincident(g47,g42)
    c: Equal(g42, g43-g47) x5
    c: PointOnObject(g42,g48)
    c: PointOnObject(g43,g48)
    c: PointOnObject(g44,g48)
    c: PointOnObject(g45,g48)
    c: PointOnObject(g46,g48)
    c: PointOnObject(g47,g48)
    c: Equal(g41,g48)
    c: Diameter(g41) = 7
    c: Vertical(g39)
    c: Vertical(g43)
    c: Distance(g-2,g39) = 1
    c: Symmetric(g38,g43,g-2)
    c: Distance(g41,g-1) = 7
FEATURE [Part::Extrusion] Extrude652  label="hex254"
  Base = -> Sketch661
  Dir = (0,-1,2e-16)
  DirMode = 2
  FaceMakerClass = Part::FaceMakerBullseye
  FaceMakerMode = 3
  LengthFwd = 10
  LengthRev = 0
  Placement = pos=(48,0,-42) rot=(0,0,1;0rad)
  Solid = true
  Symmetric = false
FEATURE [Sketcher::SketchObject] Sketch662
  ArcFitTolerance = 1e-06
  FullyConstrained = true
  MakeInternals = false
  Placement = pos=(0,0,0) rot=(1,0,0;1.5708rad)
  sketch-geometry (49):
    g0: LineSegment StartX=1e-16 StartY=3.5 StartZ=0 EndX=-3.03109 EndY=1.75 EndZ=0
    g1: LineSegment StartX=-3.03109 StartY=1.75 StartZ=0 EndX=-3.03109 EndY=-1.75 EndZ=0
    g2: LineSegment StartX=-3.03109 StartY=-1.75 StartZ=0 EndX=-1e-16 EndY=-3.5 EndZ=0
    g3: LineSegment StartX=-1e-16 StartY=-3.5 StartZ=0 EndX=3.03109 EndY=-1.75 EndZ=0
    g4: LineSegment StartX=3.03109 StartY=-1.75 StartZ=0 EndX=3.03109 EndY=1.75 EndZ=0
    g5: LineSegment StartX=3.03109 StartY=1.75 StartZ=0 EndX=1e-16 EndY=3.5 EndZ=0
    g6: Circle [constr] CenterX=0 CenterY=0 CenterZ=0 NormalX=0 NormalY=0 NormalZ=1 AngleXU=0 Radius=3.5
    g7: LineSegment StartX=4.96892 StartY=-1.75002 StartZ=0 EndX=8.00002 EndY=-3.5 EndZ=0
    g8: LineSegment StartX=8.00002 StartY=-3.5 StartZ=0 EndX=11.0311 EndY=-1.74998 EndZ=0
    g9: LineSegment StartX=11.0311 StartY=-1.74998 StartZ=0 EndX=11.0311 EndY=1.75002 EndZ=0
    g10: LineSegment StartX=11.0311 StartY=1.75002 StartZ=0 EndX=7.99998 EndY=3.5 EndZ=0
    g11: LineSegment StartX=7.99998 StartY=3.5 StartZ=0 EndX=4.9689 EndY=1.74998 EndZ=0
    g12: LineSegment StartX=4.9689 StartY=1.74998 StartZ=0 EndX=4.96892 EndY=-1.75002 EndZ=0
    g13: Circle [constr] CenterX=8 CenterY=0 CenterZ=0 NormalX=0 NormalY=0 NormalZ=1 AngleXU=0 Radius=3.5
    g14: LineSegment StartX=4.03109 StartY=3.5 StartZ=0 EndX=7.06218 EndY=5.25 EndZ=0
    g15: LineSegment StartX=7.06218 StartY=5.25 StartZ=0 EndX=7.06218 EndY=8.75 EndZ=0
    g16: LineSegment StartX=7.06218 StartY=8.75 StartZ=0 EndX=4.03109 EndY=10.5 EndZ=0
    g17: LineSegment StartX=4.03109 StartY=10.5 StartZ=0 EndX=1 EndY=8.75 EndZ=0
    g18: LineSegment StartX=1 StartY=8.75 StartZ=0 EndX=1 EndY=5.25 EndZ=0
    g19: LineSegment StartX=1 StartY=5.25 StartZ=0 EndX=4.03109 EndY=3.5 EndZ=0
    g20: Circle [constr] CenterX=4.03109 CenterY=7 CenterZ=0 NormalX=0 NormalY=0 NormalZ=1 AngleXU=0 Radius=3.5
    g21: LineSegment StartX=-1 StartY=5.25 StartZ=0 EndX=-1 EndY=8.75 EndZ=0
    g22: LineSegment StartX=-1 StartY=8.75 StartZ=0 EndX=-4.03109 EndY=10.5 EndZ=0
    g23: LineSegment StartX=-4.03109 StartY=10.5 StartZ=0 EndX=-7.06218 EndY=8.75 EndZ=0
    g24: LineSegment StartX=-7.06218 StartY=8.75 StartZ=0 EndX=-7.06218 EndY=5.25 EndZ=0
    g25: LineSegment StartX=-7.06218 StartY=5.25 StartZ=0 EndX=-4.03109 EndY=3.5 EndZ=0
    g26: LineSegment StartX=-4.03109 StartY=3.5 StartZ=0 EndX=-1 EndY=5.25 EndZ=0
    g27: Circle [constr] CenterX=-4.03109 CenterY=7 CenterZ=0 NormalX=0 NormalY=0 NormalZ=1 AngleXU=0 Radius=3.5
    g28: LineSegment StartX=-4.96891 StartY=-1.75 StartZ=0 EndX=-4.96891 EndY=1.75 EndZ=0
    g29: LineSegment StartX=-4.96891 StartY=1.75 StartZ=0 EndX=-8 EndY=3.5 EndZ=0
    g30: LineSegment StartX=-8 StartY=3.5 StartZ=0 EndX=-11.0311 EndY=1.75 EndZ=0
    g31: LineSegment StartX=-11.0311 StartY=1.75 StartZ=0 EndX=-11.0311 EndY=-1.75 EndZ=0
    g32: LineSegment StartX=-11.0311 StartY=-1.75 StartZ=0 EndX=-8 EndY=-3.5 EndZ=0
    g33: LineSegment StartX=-8 StartY=-3.5 StartZ=0 EndX=-4.96891 EndY=-1.75 EndZ=0
    g34: Circle [constr] CenterX=-8 CenterY=0 CenterZ=0 NormalX=0 NormalY=0 NormalZ=1 AngleXU=0 Radius=3.5
    g35: LineSegment StartX=-4.03109 StartY=-3.5 StartZ=0 EndX=-7.06218 EndY=-5.25 EndZ=0
    g36: LineSegment StartX=-7.06218 StartY=-5.25 StartZ=0 EndX=-7.06218 EndY=-8.75 EndZ=0
    g37: LineSegment StartX=-7.06218 StartY=-8.75 StartZ=0 EndX=-4.03109 EndY=-10.5 EndZ=0
    g38: LineSegment StartX=-4.03109 StartY=-10.5 StartZ=0 EndX=-1 EndY=-8.75 EndZ=0
    g39: LineSegment StartX=-1 StartY=-8.75 StartZ=0 EndX=-1 EndY=-5.25 EndZ=0
    g40: LineSegment StartX=-1 StartY=-5.25 StartZ=0 EndX=-4.03109 EndY=-3.5 EndZ=0
    g41: Circle [constr] CenterX=-4.03109 CenterY=-7 CenterZ=0 NormalX=0 NormalY=0 NormalZ=1 AngleXU=0 Radius=3.5
    g42: LineSegment StartX=4.03109 StartY=-3.5 StartZ=0 EndX=1 EndY=-5.25 EndZ=0
    g43: LineSegment StartX=1 StartY=-5.25 StartZ=0 EndX=1 EndY=-8.75 EndZ=0
    g44: LineSegment StartX=1 StartY=-8.75 StartZ=0 EndX=4.03109 EndY=-10.5 EndZ=0
    g45: LineSegment StartX=4.03109 StartY=-10.5 StartZ=0 EndX=7.06218 EndY=-8.75 EndZ=0
    g46: LineSegment StartX=7.06218 StartY=-8.75 StartZ=0 EndX=7.06218 EndY=-5.25 EndZ=0
    g47: LineSegment StartX=7.06218 StartY=-5.25 StartZ=0 EndX=4.03109 EndY=-3.5 EndZ=0
    g48: Circle [constr] CenterX=4.03109 CenterY=-7 CenterZ=0 NormalX=0 NormalY=0 NormalZ=1 AngleXU=0 Radius=3.5
  constraints (117):
    c: Coincident(g0,g1)
    c: Coincident(g1,g2)
    c: Coincident(g2,g3)
    c: Coincident(g3,g4)
    c: Coincident(g4,g5)
    c: Coincident(g5,g0)
    c: Equal(g0, g1-g5) x5
    c: PointOnObject(g0,g6)
    c: PointOnObject(g1,g6)
    c: PointOnObject(g2,g6)
    c: PointOnObject(g3,g6)
    c: PointOnObject(g4,g6)
    c: PointOnObject(g5,g6)
    c: Coincident(g6,g-1)
    c: Diameter(g6) = 7
    c: PointOnObject(g0,g-2)
    c: Coincident(g7,g8)
    c: Coincident(g8,g9)
    c: Coincident(g9,g10)
    c: Coincident(g10,g11)
    c: Coincident(g11,g12)
    c: Coincident(g12,g7)
    c: Equal(g7, g8-g12) x5
    c: PointOnObject(g7,g13)
    c: PointOnObject(g8,g13)
    c: PointOnObject(g9,g13)
    c: PointOnObject(g10,g13)
    c: PointOnObject(g11,g13)
    c: PointOnObject(g12,g13)
    c: PointOnObject(g13,g-1)
    c: Diameter(g13) = 7
    c: Distance(g6,g13) = 8
    c: Horizontal(g0,g10)
    c: Coincident(g14,g15)
    c: Coincident(g15,g16)
    c: Coincident(g16,g17)
    c: Coincident(g17,g18)
    c: Coincident(g18,g19)
    c: Coincident(g19,g14)
    c: Equal(g14, g15-g19) x5
    c: PointOnObject(g14,g20)
    c: PointOnObject(g15,g20)
    c: PointOnObject(g16,g20)
    c: PointOnObject(g17,g20)
    c: PointOnObject(g18,g20)
    c: PointOnObject(g19,g20)
    c: Diameter(g20) = 7
    c: DistanceY(g-1,g20) = 7
    c: Vertical(g18)
    c: Distance(g17,g-2) = 1
    c: Coincident(g21,g22)
    c: Coincident(g22,g23)
    c: Coincident(g23,g24)
    c: Coincident(g24,g25)
    c: Coincident(g25,g26)
    c: Coincident(g26,g21)
    c: Equal(g21, g22-g26) x5
    c: PointOnObject(g21,g27)
    c: PointOnObject(g22,g27)
    c: PointOnObject(g23,g27)
    c: PointOnObject(g24,g27)
    c: PointOnObject(g25,g27)
    c: PointOnObject(g26,g27)
    c: Diameter(g27) = 7
    c: DistanceY(g-1,g27) = 7
    c: DistanceX(g21,g-1) = 1
    c: Vertical(g21)
    c: Coincident(g28,g29)
    c: Coincident(g29,g30)
    c: Coincident(g30,g31)
    c: Coincident(g31,g32)
    c: Coincident(g32,g33)
    c: Coincident(g33,g28)
    c: Equal(g28, g29-g33) x5
    c: PointOnObject(g28,g34)
    c: PointOnObject(g29,g34)
    c: PointOnObject(g30,g34)
    c: PointOnObject(g31,g34)
    c: PointOnObject(g32,g34)
    c: PointOnObject(g33,g34)
    c: PointOnObject(g34,g-1)
    c: Diameter(g34) = 7
    c: Vertical(g31)
    c: DistanceX(g34,g-1) = 8
    c: Coincident(g35,g36)
    c: Coincident(g36,g37)
    c: Coincident(g37,g38)
    c: Coincident(g38,g39)
    c: Coincident(g39,g40)
    c: Coincident(g40,g35)
    c: Equal(g35, g36-g40) x5
    c: PointOnObject(g35,g41)
    c: PointOnObject(g36,g41)
    c: PointOnObject(g37,g41)
    c: PointOnObject(g38,g41)
    c: PointOnObject(g39,g41)
    c: PointOnObject(g40,g41)
    c: Coincident(g42,g43)
    c: Coincident(g43,g44)
    c: Coincident(g44,g45)
    c: Coincident(g45,g46)
    c: Coincident(g46,g47)
    c: Coincident(g47,g42)
    c: Equal(g42, g43-g47) x5
    c: PointOnObject(g42,g48)
    c: PointOnObject(g43,g48)
    c: PointOnObject(g44,g48)
    c: PointOnObject(g45,g48)
    c: PointOnObject(g46,g48)
    c: PointOnObject(g47,g48)
    c: Equal(g41,g48)
    c: Diameter(g41) = 7
    c: Vertical(g39)
    c: Vertical(g43)
    c: Distance(g-2,g39) = 1
    c: Symmetric(g38,g43,g-2)
    c: Distance(g41,g-1) = 7
FEATURE [Part::Extrusion] Extrude653  label="hex255"
  Base = -> Sketch662
  Dir = (0,-1,2e-16)
  DirMode = 2
  FaceMakerClass = Part::FaceMakerBullseye
  FaceMakerMode = 3
  LengthFwd = 10
  LengthRev = 0
  Placement = pos=(68,0,-35) rot=(0,0,1;0rad)
  Solid = true
  Symmetric = false
FEATURE [Sketcher::SketchObject] Sketch663
  ArcFitTolerance = 1e-06
  FullyConstrained = true
  MakeInternals = false
  Placement = pos=(0,0,0) rot=(1,0,0;1.5708rad)
  sketch-geometry (49):
    g0: LineSegment StartX=1e-16 StartY=3.5 StartZ=0 EndX=-3.03109 EndY=1.75 EndZ=0
    g1: LineSegment StartX=-3.03109 StartY=1.75 StartZ=0 EndX=-3.03109 EndY=-1.75 EndZ=0
    g2: LineSegment StartX=-3.03109 StartY=-1.75 StartZ=0 EndX=-1e-16 EndY=-3.5 EndZ=0
    g3: LineSegment StartX=-1e-16 StartY=-3.5 StartZ=0 EndX=3.03109 EndY=-1.75 EndZ=0
    g4: LineSegment StartX=3.03109 StartY=-1.75 StartZ=0 EndX=3.03109 EndY=1.75 EndZ=0
    g5: LineSegment StartX=3.03109 StartY=1.75 StartZ=0 EndX=1e-16 EndY=3.5 EndZ=0
    g6: Circle [constr] CenterX=0 CenterY=0 CenterZ=0 NormalX=0 NormalY=0 NormalZ=1 AngleXU=0 Radius=3.5
    g7: LineSegment StartX=4.96892 StartY=-1.75002 StartZ=0 EndX=8.00002 EndY=-3.5 EndZ=0
    g8: LineSegment StartX=8.00002 StartY=-3.5 StartZ=0 EndX=11.0311 EndY=-1.74998 EndZ=0
    g9: LineSegment StartX=11.0311 StartY=-1.74998 StartZ=0 EndX=11.0311 EndY=1.75002 EndZ=0
    g10: LineSegment StartX=11.0311 StartY=1.75002 StartZ=0 EndX=7.99998 EndY=3.5 EndZ=0
    g11: LineSegment StartX=7.99998 StartY=3.5 StartZ=0 EndX=4.9689 EndY=1.74998 EndZ=0
    g12: LineSegment StartX=4.9689 StartY=1.74998 StartZ=0 EndX=4.96892 EndY=-1.75002 EndZ=0
    g13: Circle [constr] CenterX=8 CenterY=0 CenterZ=0 NormalX=0 NormalY=0 NormalZ=1 AngleXU=0 Radius=3.5
    g14: LineSegment StartX=4.03109 StartY=3.5 StartZ=0 EndX=7.06218 EndY=5.25 EndZ=0
    g15: LineSegment StartX=7.06218 StartY=5.25 StartZ=0 EndX=7.06218 EndY=8.75 EndZ=0
    g16: LineSegment StartX=7.06218 StartY=8.75 StartZ=0 EndX=4.03109 EndY=10.5 EndZ=0
    g17: LineSegment StartX=4.03109 StartY=10.5 StartZ=0 EndX=1 EndY=8.75 EndZ=0
    g18: LineSegment StartX=1 StartY=8.75 StartZ=0 EndX=1 EndY=5.25 EndZ=0
    g19: LineSegment StartX=1 StartY=5.25 StartZ=0 EndX=4.03109 EndY=3.5 EndZ=0
    g20: Circle [constr] CenterX=4.03109 CenterY=7 CenterZ=0 NormalX=0 NormalY=0 NormalZ=1 AngleXU=0 Radius=3.5
    g21: LineSegment StartX=-1 StartY=5.25 StartZ=0 EndX=-1 EndY=8.75 EndZ=0
    g22: LineSegment StartX=-1 StartY=8.75 StartZ=0 EndX=-4.03109 EndY=10.5 EndZ=0
    g23: LineSegment StartX=-4.03109 StartY=10.5 StartZ=0 EndX=-7.06218 EndY=8.75 EndZ=0
    g24: LineSegment StartX=-7.06218 StartY=8.75 StartZ=0 EndX=-7.06218 EndY=5.25 EndZ=0
    g25: LineSegment StartX=-7.06218 StartY=5.25 StartZ=0 EndX=-4.03109 EndY=3.5 EndZ=0
    g26: LineSegment StartX=-4.03109 StartY=3.5 StartZ=0 EndX=-1 EndY=5.25 EndZ=0
    g27: Circle [constr] CenterX=-4.03109 CenterY=7 CenterZ=0 NormalX=0 NormalY=0 NormalZ=1 AngleXU=0 Radius=3.5
    g28: LineSegment StartX=-4.96891 StartY=-1.75 StartZ=0 EndX=-4.96891 EndY=1.75 EndZ=0
    g29: LineSegment StartX=-4.96891 StartY=1.75 StartZ=0 EndX=-8 EndY=3.5 EndZ=0
    g30: LineSegment StartX=-8 StartY=3.5 StartZ=0 EndX=-11.0311 EndY=1.75 EndZ=0
    g31: LineSegment StartX=-11.0311 StartY=1.75 StartZ=0 EndX=-11.0311 EndY=-1.75 EndZ=0
    g32: LineSegment StartX=-11.0311 StartY=-1.75 StartZ=0 EndX=-8 EndY=-3.5 EndZ=0
    g33: LineSegment StartX=-8 StartY=-3.5 StartZ=0 EndX=-4.96891 EndY=-1.75 EndZ=0
    g34: Circle [constr] CenterX=-8 CenterY=0 CenterZ=0 NormalX=0 NormalY=0 NormalZ=1 AngleXU=0 Radius=3.5
    g35: LineSegment StartX=-4.03109 StartY=-3.5 StartZ=0 EndX=-7.06218 EndY=-5.25 EndZ=0
    g36: LineSegment StartX=-7.06218 StartY=-5.25 StartZ=0 EndX=-7.06218 EndY=-8.75 EndZ=0
    g37: LineSegment StartX=-7.06218 StartY=-8.75 StartZ=0 EndX=-4.03109 EndY=-10.5 EndZ=0
    g38: LineSegment StartX=-4.03109 StartY=-10.5 StartZ=0 EndX=-1 EndY=-8.75 EndZ=0
    g39: LineSegment StartX=-1 StartY=-8.75 StartZ=0 EndX=-1 EndY=-5.25 EndZ=0
    g40: LineSegment StartX=-1 StartY=-5.25 StartZ=0 EndX=-4.03109 EndY=-3.5 EndZ=0
    g41: Circle [constr] CenterX=-4.03109 CenterY=-7 CenterZ=0 NormalX=0 NormalY=0 NormalZ=1 AngleXU=0 Radius=3.5
    g42: LineSegment StartX=4.03109 StartY=-3.5 StartZ=0 EndX=1 EndY=-5.25 EndZ=0
    g43: LineSegment StartX=1 StartY=-5.25 StartZ=0 EndX=1 EndY=-8.75 EndZ=0
    g44: LineSegment StartX=1 StartY=-8.75 StartZ=0 EndX=4.03109 EndY=-10.5 EndZ=0
    g45: LineSegment StartX=4.03109 StartY=-10.5 StartZ=0 EndX=7.06218 EndY=-8.75 EndZ=0
    g46: LineSegment StartX=7.06218 StartY=-8.75 StartZ=0 EndX=7.06218 EndY=-5.25 EndZ=0
    g47: LineSegment StartX=7.06218 StartY=-5.25 StartZ=0 EndX=4.03109 EndY=-3.5 EndZ=0
    g48: Circle [constr] CenterX=4.03109 CenterY=-7 CenterZ=0 NormalX=0 NormalY=0 NormalZ=1 AngleXU=0 Radius=3.5
  constraints (117):
    c: Coincident(g0,g1)
    c: Coincident(g1,g2)
    c: Coincident(g2,g3)
    c: Coincident(g3,g4)
    c: Coincident(g4,g5)
    c: Coincident(g5,g0)
    c: Equal(g0, g1-g5) x5
    c: PointOnObject(g0,g6)
    c: PointOnObject(g1,g6)
    c: PointOnObject(g2,g6)
    c: PointOnObject(g3,g6)
    c: PointOnObject(g4,g6)
    c: PointOnObject(g5,g6)
    c: Coincident(g6,g-1)
    c: Diameter(g6) = 7
    c: PointOnObject(g0,g-2)
    c: Coincident(g7,g8)
    c: Coincident(g8,g9)
    c: Coincident(g9,g10)
    c: Coincident(g10,g11)
    c: Coincident(g11,g12)
    c: Coincident(g12,g7)
    c: Equal(g7, g8-g12) x5
    c: PointOnObject(g7,g13)
    c: PointOnObject(g8,g13)
    c: PointOnObject(g9,g13)
    c: PointOnObject(g10,g13)
    c: PointOnObject(g11,g13)
    c: PointOnObject(g12,g13)
    c: PointOnObject(g13,g-1)
    c: Diameter(g13) = 7
    c: Distance(g6,g13) = 8
    c: Horizontal(g0,g10)
    c: Coincident(g14,g15)
    c: Coincident(g15,g16)
    c: Coincident(g16,g17)
    c: Coincident(g17,g18)
    c: Coincident(g18,g19)
    c: Coincident(g19,g14)
    c: Equal(g14, g15-g19) x5
    c: PointOnObject(g14,g20)
    c: PointOnObject(g15,g20)
    c: PointOnObject(g16,g20)
    c: PointOnObject(g17,g20)
    c: PointOnObject(g18,g20)
    c: PointOnObject(g19,g20)
    c: Diameter(g20) = 7
    c: DistanceY(g-1,g20) = 7
    c: Vertical(g18)
    c: Distance(g17,g-2) = 1
    c: Coincident(g21,g22)
    c: Coincident(g22,g23)
    c: Coincident(g23,g24)
    c: Coincident(g24,g25)
    c: Coincident(g25,g26)
    c: Coincident(g26,g21)
    c: Equal(g21, g22-g26) x5
    c: PointOnObject(g21,g27)
    c: PointOnObject(g22,g27)
    c: PointOnObject(g23,g27)
    c: PointOnObject(g24,g27)
    c: PointOnObject(g25,g27)
    c: PointOnObject(g26,g27)
    c: Diameter(g27) = 7
    c: DistanceY(g-1,g27) = 7
    c: DistanceX(g21,g-1) = 1
    c: Vertical(g21)
    c: Coincident(g28,g29)
    c: Coincident(g29,g30)
    c: Coincident(g30,g31)
    c: Coincident(g31,g32)
    c: Coincident(g32,g33)
    c: Coincident(g33,g28)
    c: Equal(g28, g29-g33) x5
    c: PointOnObject(g28,g34)
    c: PointOnObject(g29,g34)
    c: PointOnObject(g30,g34)
    c: PointOnObject(g31,g34)
    c: PointOnObject(g32,g34)
    c: PointOnObject(g33,g34)
    c: PointOnObject(g34,g-1)
    c: Diameter(g34) = 7
    c: Vertical(g31)
    c: DistanceX(g34,g-1) = 8
    c: Coincident(g35,g36)
    c: Coincident(g36,g37)
    c: Coincident(g37,g38)
    c: Coincident(g38,g39)
    c: Coincident(g39,g40)
    c: Coincident(g40,g35)
    c: Equal(g35, g36-g40) x5
    c: PointOnObject(g35,g41)
    c: PointOnObject(g36,g41)
    c: PointOnObject(g37,g41)
    c: PointOnObject(g38,g41)
    c: PointOnObject(g39,g41)
    c: PointOnObject(g40,g41)
    c: Coincident(g42,g43)
    c: Coincident(g43,g44)
    c: Coincident(g44,g45)
    c: Coincident(g45,g46)
    c: Coincident(g46,g47)
    c: Coincident(g47,g42)
    c: Equal(g42, g43-g47) x5
    c: PointOnObject(g42,g48)
    c: PointOnObject(g43,g48)
    c: PointOnObject(g44,g48)
    c: PointOnObject(g45,g48)
    c: PointOnObject(g46,g48)
    c: PointOnObject(g47,g48)
    c: Equal(g41,g48)
    c: Diameter(g41) = 7
    c: Vertical(g39)
    c: Vertical(g43)
    c: Distance(g-2,g39) = 1
    c: Symmetric(g38,g43,g-2)
    c: Distance(g41,g-1) = 7
FEATURE [Part::Extrusion] Extrude654  label="hex256"
  Base = -> Sketch663
  Dir = (0,-1,2e-16)
  DirMode = 2
  FaceMakerClass = Part::FaceMakerBullseye
  FaceMakerMode = 3
  LengthFwd = 10
  LengthRev = 0
  Placement = pos=(72,0,-14) rot=(0,0,1;0rad)
  Solid = true
  Symmetric = false
FEATURE [Sketcher::SketchObject] Sketch664
  ArcFitTolerance = 1e-06
  FullyConstrained = true
  MakeInternals = false
  Placement = pos=(0,0,0) rot=(1,0,0;1.5708rad)
  sketch-geometry (49):
    g0: LineSegment StartX=1e-16 StartY=3.5 StartZ=0 EndX=-3.03109 EndY=1.75 EndZ=0
    g1: LineSegment StartX=-3.03109 StartY=1.75 StartZ=0 EndX=-3.03109 EndY=-1.75 EndZ=0
    g2: LineSegment StartX=-3.03109 StartY=-1.75 StartZ=0 EndX=-1e-16 EndY=-3.5 EndZ=0
    g3: LineSegment StartX=-1e-16 StartY=-3.5 StartZ=0 EndX=3.03109 EndY=-1.75 EndZ=0
    g4: LineSegment StartX=3.03109 StartY=-1.75 StartZ=0 EndX=3.03109 EndY=1.75 EndZ=0
    g5: LineSegment StartX=3.03109 StartY=1.75 StartZ=0 EndX=1e-16 EndY=3.5 EndZ=0
    g6: Circle [constr] CenterX=0 CenterY=0 CenterZ=0 NormalX=0 NormalY=0 NormalZ=1 AngleXU=0 Radius=3.5
    g7: LineSegment StartX=4.96892 StartY=-1.75002 StartZ=0 EndX=8.00002 EndY=-3.5 EndZ=0
    g8: LineSegment StartX=8.00002 StartY=-3.5 StartZ=0 EndX=11.0311 EndY=-1.74998 EndZ=0
    g9: LineSegment StartX=11.0311 StartY=-1.74998 StartZ=0 EndX=11.0311 EndY=1.75002 EndZ=0
    g10: LineSegment StartX=11.0311 StartY=1.75002 StartZ=0 EndX=7.99998 EndY=3.5 EndZ=0
    g11: LineSegment StartX=7.99998 StartY=3.5 StartZ=0 EndX=4.9689 EndY=1.74998 EndZ=0
    g12: LineSegment StartX=4.9689 StartY=1.74998 StartZ=0 EndX=4.96892 EndY=-1.75002 EndZ=0
    g13: Circle [constr] CenterX=8 CenterY=0 CenterZ=0 NormalX=0 NormalY=0 NormalZ=1 AngleXU=0 Radius=3.5
    g14: LineSegment StartX=4.03109 StartY=3.5 StartZ=0 EndX=7.06218 EndY=5.25 EndZ=0
    g15: LineSegment StartX=7.06218 StartY=5.25 StartZ=0 EndX=7.06218 EndY=8.75 EndZ=0
    g16: LineSegment StartX=7.06218 StartY=8.75 StartZ=0 EndX=4.03109 EndY=10.5 EndZ=0
    g17: LineSegment StartX=4.03109 StartY=10.5 StartZ=0 EndX=1 EndY=8.75 EndZ=0
    g18: LineSegment StartX=1 StartY=8.75 StartZ=0 EndX=1 EndY=5.25 EndZ=0
    g19: LineSegment StartX=1 StartY=5.25 StartZ=0 EndX=4.03109 EndY=3.5 EndZ=0
    g20: Circle [constr] CenterX=4.03109 CenterY=7 CenterZ=0 NormalX=0 NormalY=0 NormalZ=1 AngleXU=0 Radius=3.5
    g21: LineSegment StartX=-1 StartY=5.25 StartZ=0 EndX=-1 EndY=8.75 EndZ=0
    g22: LineSegment StartX=-1 StartY=8.75 StartZ=0 EndX=-4.03109 EndY=10.5 EndZ=0
    g23: LineSegment StartX=-4.03109 StartY=10.5 StartZ=0 EndX=-7.06218 EndY=8.75 EndZ=0
    g24: LineSegment StartX=-7.06218 StartY=8.75 StartZ=0 EndX=-7.06218 EndY=5.25 EndZ=0
    g25: LineSegment StartX=-7.06218 StartY=5.25 StartZ=0 EndX=-4.03109 EndY=3.5 EndZ=0
    g26: LineSegment StartX=-4.03109 StartY=3.5 StartZ=0 EndX=-1 EndY=5.25 EndZ=0
    g27: Circle [constr] CenterX=-4.03109 CenterY=7 CenterZ=0 NormalX=0 NormalY=0 NormalZ=1 AngleXU=0 Radius=3.5
    g28: LineSegment StartX=-4.96891 StartY=-1.75 StartZ=0 EndX=-4.96891 EndY=1.75 EndZ=0
    g29: LineSegment StartX=-4.96891 StartY=1.75 StartZ=0 EndX=-8 EndY=3.5 EndZ=0
    g30: LineSegment StartX=-8 StartY=3.5 StartZ=0 EndX=-11.0311 EndY=1.75 EndZ=0
    g31: LineSegment StartX=-11.0311 StartY=1.75 StartZ=0 EndX=-11.0311 EndY=-1.75 EndZ=0
    g32: LineSegment StartX=-11.0311 StartY=-1.75 StartZ=0 EndX=-8 EndY=-3.5 EndZ=0
    g33: LineSegment StartX=-8 StartY=-3.5 StartZ=0 EndX=-4.96891 EndY=-1.75 EndZ=0
    g34: Circle [constr] CenterX=-8 CenterY=0 CenterZ=0 NormalX=0 NormalY=0 NormalZ=1 AngleXU=0 Radius=3.5
    g35: LineSegment StartX=-4.03109 StartY=-3.5 StartZ=0 EndX=-7.06218 EndY=-5.25 EndZ=0
    g36: LineSegment StartX=-7.06218 StartY=-5.25 StartZ=0 EndX=-7.06218 EndY=-8.75 EndZ=0
    g37: LineSegment StartX=-7.06218 StartY=-8.75 StartZ=0 EndX=-4.03109 EndY=-10.5 EndZ=0
    g38: LineSegment StartX=-4.03109 StartY=-10.5 StartZ=0 EndX=-1 EndY=-8.75 EndZ=0
    g39: LineSegment StartX=-1 StartY=-8.75 StartZ=0 EndX=-1 EndY=-5.25 EndZ=0
    g40: LineSegment StartX=-1 StartY=-5.25 StartZ=0 EndX=-4.03109 EndY=-3.5 EndZ=0
    g41: Circle [constr] CenterX=-4.03109 CenterY=-7 CenterZ=0 NormalX=0 NormalY=0 NormalZ=1 AngleXU=0 Radius=3.5
    g42: LineSegment StartX=4.03109 StartY=-3.5 StartZ=0 EndX=1 EndY=-5.25 EndZ=0
    g43: LineSegment StartX=1 StartY=-5.25 StartZ=0 EndX=1 EndY=-8.75 EndZ=0
    g44: LineSegment StartX=1 StartY=-8.75 StartZ=0 EndX=4.03109 EndY=-10.5 EndZ=0
    g45: LineSegment StartX=4.03109 StartY=-10.5 StartZ=0 EndX=7.06218 EndY=-8.75 EndZ=0
    g46: LineSegment StartX=7.06218 StartY=-8.75 StartZ=0 EndX=7.06218 EndY=-5.25 EndZ=0
    g47: LineSegment StartX=7.06218 StartY=-5.25 StartZ=0 EndX=4.03109 EndY=-3.5 EndZ=0
    g48: Circle [constr] CenterX=4.03109 CenterY=-7 CenterZ=0 NormalX=0 NormalY=0 NormalZ=1 AngleXU=0 Radius=3.5
  constraints (117):
    c: Coincident(g0,g1)
    c: Coincident(g1,g2)
    c: Coincident(g2,g3)
    c: Coincident(g3,g4)
    c: Coincident(g4,g5)
    c: Coincident(g5,g0)
    c: Equal(g0, g1-g5) x5
    c: PointOnObject(g0,g6)
    c: PointOnObject(g1,g6)
    c: PointOnObject(g2,g6)
    c: PointOnObject(g3,g6)
    c: PointOnObject(g4,g6)
    c: PointOnObject(g5,g6)
    c: Coincident(g6,g-1)
    c: Diameter(g6) = 7
    c: PointOnObject(g0,g-2)
    c: Coincident(g7,g8)
    c: Coincident(g8,g9)
    c: Coincident(g9,g10)
    c: Coincident(g10,g11)
    c: Coincident(g11,g12)
    c: Coincident(g12,g7)
    c: Equal(g7, g8-g12) x5
    c: PointOnObject(g7,g13)
    c: PointOnObject(g8,g13)
    c: PointOnObject(g9,g13)
    c: PointOnObject(g10,g13)
    c: PointOnObject(g11,g13)
    c: PointOnObject(g12,g13)
    c: PointOnObject(g13,g-1)
    c: Diameter(g13) = 7
    c: Distance(g6,g13) = 8
    c: Horizontal(g0,g10)
    c: Coincident(g14,g15)
    c: Coincident(g15,g16)
    c: Coincident(g16,g17)
    c: Coincident(g17,g18)
    c: Coincident(g18,g19)
    c: Coincident(g19,g14)
    c: Equal(g14, g15-g19) x5
    c: PointOnObject(g14,g20)
    c: PointOnObject(g15,g20)
    c: PointOnObject(g16,g20)
    c: PointOnObject(g17,g20)
    c: PointOnObject(g18,g20)
    c: PointOnObject(g19,g20)
    c: Diameter(g20) = 7
    c: DistanceY(g-1,g20) = 7
    c: Vertical(g18)
    c: Distance(g17,g-2) = 1
    c: Coincident(g21,g22)
    c: Coincident(g22,g23)
    c: Coincident(g23,g24)
    c: Coincident(g24,g25)
    c: Coincident(g25,g26)
    c: Coincident(g26,g21)
    c: Equal(g21, g22-g26) x5
    c: PointOnObject(g21,g27)
    c: PointOnObject(g22,g27)
    c: PointOnObject(g23,g27)
    c: PointOnObject(g24,g27)
    c: PointOnObject(g25,g27)
    c: PointOnObject(g26,g27)
    c: Diameter(g27) = 7
    c: DistanceY(g-1,g27) = 7
    c: DistanceX(g21,g-1) = 1
    c: Vertical(g21)
    c: Coincident(g28,g29)
    c: Coincident(g29,g30)
    c: Coincident(g30,g31)
    c: Coincident(g31,g32)
    c: Coincident(g32,g33)
    c: Coincident(g33,g28)
    c: Equal(g28, g29-g33) x5
    c: PointOnObject(g28,g34)
    c: PointOnObject(g29,g34)
    c: PointOnObject(g30,g34)
    c: PointOnObject(g31,g34)
    c: PointOnObject(g32,g34)
    c: PointOnObject(g33,g34)
    c: PointOnObject(g34,g-1)
    c: Diameter(g34) = 7
    c: Vertical(g31)
    c: DistanceX(g34,g-1) = 8
    c: Coincident(g35,g36)
    c: Coincident(g36,g37)
    c: Coincident(g37,g38)
    c: Coincident(g38,g39)
    c: Coincident(g39,g40)
    c: Coincident(g40,g35)
    c: Equal(g35, g36-g40) x5
    c: PointOnObject(g35,g41)
    c: PointOnObject(g36,g41)
    c: PointOnObject(g37,g41)
    c: PointOnObject(g38,g41)
    c: PointOnObject(g39,g41)
    c: PointOnObject(g40,g41)
    c: Coincident(g42,g43)
    c: Coincident(g43,g44)
    c: Coincident(g44,g45)
    c: Coincident(g45,g46)
    c: Coincident(g46,g47)
    c: Coincident(g47,g42)
    c: Equal(g42, g43-g47) x5
    c: PointOnObject(g42,g48)
    c: PointOnObject(g43,g48)
    c: PointOnObject(g44,g48)
    c: PointOnObject(g45,g48)
    c: PointOnObject(g46,g48)
    c: PointOnObject(g47,g48)
    c: Equal(g41,g48)
    c: Diameter(g41) = 7
    c: Vertical(g39)
    c: Vertical(g43)
    c: Distance(g-2,g39) = 1
    c: Symmetric(g38,g43,g-2)
    c: Distance(g41,g-1) = 7
FEATURE [Part::Extrusion] Extrude655  label="hex257"
  Base = -> Sketch664
  Dir = (0,-1,2e-16)
  DirMode = 2
  FaceMakerClass = Part::FaceMakerBullseye
  FaceMakerMode = 3
  LengthFwd = 10
  LengthRev = 0
  Placement = pos=(72,0,14) rot=(0,0,1;0rad)
  Solid = true
  Symmetric = false
FEATURE [Sketcher::SketchObject] Sketch665
  ArcFitTolerance = 1e-06
  FullyConstrained = true
  MakeInternals = false
  Placement = pos=(0,0,0) rot=(1,0,0;1.5708rad)
  sketch-geometry (49):
    g0: LineSegment StartX=1e-16 StartY=3.5 StartZ=0 EndX=-3.03109 EndY=1.75 EndZ=0
    g1: LineSegment StartX=-3.03109 StartY=1.75 StartZ=0 EndX=-3.03109 EndY=-1.75 EndZ=0
    g2: LineSegment StartX=-3.03109 StartY=-1.75 StartZ=0 EndX=-1e-16 EndY=-3.5 EndZ=0
    g3: LineSegment StartX=-1e-16 StartY=-3.5 StartZ=0 EndX=3.03109 EndY=-1.75 EndZ=0
    g4: LineSegment StartX=3.03109 StartY=-1.75 StartZ=0 EndX=3.03109 EndY=1.75 EndZ=0
    g5: LineSegment StartX=3.03109 StartY=1.75 StartZ=0 EndX=1e-16 EndY=3.5 EndZ=0
    g6: Circle [constr] CenterX=0 CenterY=0 CenterZ=0 NormalX=0 NormalY=0 NormalZ=1 AngleXU=0 Radius=3.5
    g7: LineSegment StartX=4.96892 StartY=-1.75002 StartZ=0 EndX=8.00002 EndY=-3.5 EndZ=0
    g8: LineSegment StartX=8.00002 StartY=-3.5 StartZ=0 EndX=11.0311 EndY=-1.74998 EndZ=0
    g9: LineSegment StartX=11.0311 StartY=-1.74998 StartZ=0 EndX=11.0311 EndY=1.75002 EndZ=0
    g10: LineSegment StartX=11.0311 StartY=1.75002 StartZ=0 EndX=7.99998 EndY=3.5 EndZ=0
    g11: LineSegment StartX=7.99998 StartY=3.5 StartZ=0 EndX=4.9689 EndY=1.74998 EndZ=0
    g12: LineSegment StartX=4.9689 StartY=1.74998 StartZ=0 EndX=4.96892 EndY=-1.75002 EndZ=0
    g13: Circle [constr] CenterX=8 CenterY=0 CenterZ=0 NormalX=0 NormalY=0 NormalZ=1 AngleXU=0 Radius=3.5
    g14: LineSegment StartX=4.03109 StartY=3.5 StartZ=0 EndX=7.06218 EndY=5.25 EndZ=0
    g15: LineSegment StartX=7.06218 StartY=5.25 StartZ=0 EndX=7.06218 EndY=8.75 EndZ=0
    g16: LineSegment StartX=7.06218 StartY=8.75 StartZ=0 EndX=4.03109 EndY=10.5 EndZ=0
    g17: LineSegment StartX=4.03109 StartY=10.5 StartZ=0 EndX=1 EndY=8.75 EndZ=0
    g18: LineSegment StartX=1 StartY=8.75 StartZ=0 EndX=1 EndY=5.25 EndZ=0
    g19: LineSegment StartX=1 StartY=5.25 StartZ=0 EndX=4.03109 EndY=3.5 EndZ=0
    g20: Circle [constr] CenterX=4.03109 CenterY=7 CenterZ=0 NormalX=0 NormalY=0 NormalZ=1 AngleXU=0 Radius=3.5
    g21: LineSegment StartX=-1 StartY=5.25 StartZ=0 EndX=-1 EndY=8.75 EndZ=0
    g22: LineSegment StartX=-1 StartY=8.75 StartZ=0 EndX=-4.03109 EndY=10.5 EndZ=0
    g23: LineSegment StartX=-4.03109 StartY=10.5 StartZ=0 EndX=-7.06218 EndY=8.75 EndZ=0
    g24: LineSegment StartX=-7.06218 StartY=8.75 StartZ=0 EndX=-7.06218 EndY=5.25 EndZ=0
    g25: LineSegment StartX=-7.06218 StartY=5.25 StartZ=0 EndX=-4.03109 EndY=3.5 EndZ=0
    g26: LineSegment StartX=-4.03109 StartY=3.5 StartZ=0 EndX=-1 EndY=5.25 EndZ=0
    g27: Circle [constr] CenterX=-4.03109 CenterY=7 CenterZ=0 NormalX=0 NormalY=0 NormalZ=1 AngleXU=0 Radius=3.5
    g28: LineSegment StartX=-4.96891 StartY=-1.75 StartZ=0 EndX=-4.96891 EndY=1.75 EndZ=0
    g29: LineSegment StartX=-4.96891 StartY=1.75 StartZ=0 EndX=-8 EndY=3.5 EndZ=0
    g30: LineSegment StartX=-8 StartY=3.5 StartZ=0 EndX=-11.0311 EndY=1.75 EndZ=0
    g31: LineSegment StartX=-11.0311 StartY=1.75 StartZ=0 EndX=-11.0311 EndY=-1.75 EndZ=0
    g32: LineSegment StartX=-11.0311 StartY=-1.75 StartZ=0 EndX=-8 EndY=-3.5 EndZ=0
    g33: LineSegment StartX=-8 StartY=-3.5 StartZ=0 EndX=-4.96891 EndY=-1.75 EndZ=0
    g34: Circle [constr] CenterX=-8 CenterY=0 CenterZ=0 NormalX=0 NormalY=0 NormalZ=1 AngleXU=0 Radius=3.5
    g35: LineSegment StartX=-4.03109 StartY=-3.5 StartZ=0 EndX=-7.06218 EndY=-5.25 EndZ=0
    g36: LineSegment StartX=-7.06218 StartY=-5.25 StartZ=0 EndX=-7.06218 EndY=-8.75 EndZ=0
    g37: LineSegment StartX=-7.06218 StartY=-8.75 StartZ=0 EndX=-4.03109 EndY=-10.5 EndZ=0
    g38: LineSegment StartX=-4.03109 StartY=-10.5 StartZ=0 EndX=-1 EndY=-8.75 EndZ=0
    g39: LineSegment StartX=-1 StartY=-8.75 StartZ=0 EndX=-1 EndY=-5.25 EndZ=0
    g40: LineSegment StartX=-1 StartY=-5.25 StartZ=0 EndX=-4.03109 EndY=-3.5 EndZ=0
    g41: Circle [constr] CenterX=-4.03109 CenterY=-7 CenterZ=0 NormalX=0 NormalY=0 NormalZ=1 AngleXU=0 Radius=3.5
    g42: LineSegment StartX=4.03109 StartY=-3.5 StartZ=0 EndX=1 EndY=-5.25 EndZ=0
    g43: LineSegment StartX=1 StartY=-5.25 StartZ=0 EndX=1 EndY=-8.75 EndZ=0
    g44: LineSegment StartX=1 StartY=-8.75 StartZ=0 EndX=4.03109 EndY=-10.5 EndZ=0
    g45: LineSegment StartX=4.03109 StartY=-10.5 StartZ=0 EndX=7.06218 EndY=-8.75 EndZ=0
    g46: LineSegment StartX=7.06218 StartY=-8.75 StartZ=0 EndX=7.06218 EndY=-5.25 EndZ=0
    g47: LineSegment StartX=7.06218 StartY=-5.25 StartZ=0 EndX=4.03109 EndY=-3.5 EndZ=0
    g48: Circle [constr] CenterX=4.03109 CenterY=-7 CenterZ=0 NormalX=0 NormalY=0 NormalZ=1 AngleXU=0 Radius=3.5
  constraints (117):
    c: Coincident(g0,g1)
    c: Coincident(g1,g2)
    c: Coincident(g2,g3)
    c: Coincident(g3,g4)
    c: Coincident(g4,g5)
    c: Coincident(g5,g0)
    c: Equal(g0, g1-g5) x5
    c: PointOnObject(g0,g6)
    c: PointOnObject(g1,g6)
    c: PointOnObject(g2,g6)
    c: PointOnObject(g3,g6)
    c: PointOnObject(g4,g6)
    c: PointOnObject(g5,g6)
    c: Coincident(g6,g-1)
    c: Diameter(g6) = 7
    c: PointOnObject(g0,g-2)
    c: Coincident(g7,g8)
    c: Coincident(g8,g9)
    c: Coincident(g9,g10)
    c: Coincident(g10,g11)
    c: Coincident(g11,g12)
    c: Coincident(g12,g7)
    c: Equal(g7, g8-g12) x5
    c: PointOnObject(g7,g13)
    c: PointOnObject(g8,g13)
    c: PointOnObject(g9,g13)
    c: PointOnObject(g10,g13)
    c: PointOnObject(g11,g13)
    c: PointOnObject(g12,g13)
    c: PointOnObject(g13,g-1)
    c: Diameter(g13) = 7
    c: Distance(g6,g13) = 8
    c: Horizontal(g0,g10)
    c: Coincident(g14,g15)
    c: Coincident(g15,g16)
    c: Coincident(g16,g17)
    c: Coincident(g17,g18)
    c: Coincident(g18,g19)
    c: Coincident(g19,g14)
    c: Equal(g14, g15-g19) x5
    c: PointOnObject(g14,g20)
    c: PointOnObject(g15,g20)
    c: PointOnObject(g16,g20)
    c: PointOnObject(g17,g20)
    c: PointOnObject(g18,g20)
    c: PointOnObject(g19,g20)
    c: Diameter(g20) = 7
    c: DistanceY(g-1,g20) = 7
    c: Vertical(g18)
    c: Distance(g17,g-2) = 1
    c: Coincident(g21,g22)
    c: Coincident(g22,g23)
    c: Coincident(g23,g24)
    c: Coincident(g24,g25)
    c: Coincident(g25,g26)
    c: Coincident(g26,g21)
    c: Equal(g21, g22-g26) x5
    c: PointOnObject(g21,g27)
    c: PointOnObject(g22,g27)
    c: PointOnObject(g23,g27)
    c: PointOnObject(g24,g27)
    c: PointOnObject(g25,g27)
    c: PointOnObject(g26,g27)
    c: Diameter(g27) = 7
    c: DistanceY(g-1,g27) = 7
    c: DistanceX(g21,g-1) = 1
    c: Vertical(g21)
    c: Coincident(g28,g29)
    c: Coincident(g29,g30)
    c: Coincident(g30,g31)
    c: Coincident(g31,g32)
    c: Coincident(g32,g33)
    c: Coincident(g33,g28)
    c: Equal(g28, g29-g33) x5
    c: PointOnObject(g28,g34)
    c: PointOnObject(g29,g34)
    c: PointOnObject(g30,g34)
    c: PointOnObject(g31,g34)
    c: PointOnObject(g32,g34)
    c: PointOnObject(g33,g34)
    c: PointOnObject(g34,g-1)
    c: Diameter(g34) = 7
    c: Vertical(g31)
    c: DistanceX(g34,g-1) = 8
    c: Coincident(g35,g36)
    c: Coincident(g36,g37)
    c: Coincident(g37,g38)
    c: Coincident(g38,g39)
    c: Coincident(g39,g40)
    c: Coincident(g40,g35)
    c: Equal(g35, g36-g40) x5
    c: PointOnObject(g35,g41)
    c: PointOnObject(g36,g41)
    c: PointOnObject(g37,g41)
    c: PointOnObject(g38,g41)
    c: PointOnObject(g39,g41)
    c: PointOnObject(g40,g41)
    c: Coincident(g42,g43)
    c: Coincident(g43,g44)
    c: Coincident(g44,g45)
    c: Coincident(g45,g46)
    c: Coincident(g46,g47)
    c: Coincident(g47,g42)
    c: Equal(g42, g43-g47) x5
    c: PointOnObject(g42,g48)
    c: PointOnObject(g43,g48)
    c: PointOnObject(g44,g48)
    c: PointOnObject(g45,g48)
    c: PointOnObject(g46,g48)
    c: PointOnObject(g47,g48)
    c: Equal(g41,g48)
    c: Diameter(g41) = 7
    c: Vertical(g39)
    c: Vertical(g43)
    c: Distance(g-2,g39) = 1
    c: Symmetric(g38,g43,g-2)
    c: Distance(g41,g-1) = 7
FEATURE [Part::Extrusion] Extrude656  label="hex258"
  Base = -> Sketch665
  Dir = (0,-1,2e-16)
  DirMode = 2
  FaceMakerClass = Part::FaceMakerBullseye
  FaceMakerMode = 3
  LengthFwd = 10
  LengthRev = 0
  Placement = pos=(80,0,0) rot=(0,0,1;0rad)
  Solid = true
  Symmetric = false
FEATURE [Sketcher::SketchObject] Sketch666
  ArcFitTolerance = 1e-06
  FullyConstrained = true
  MakeInternals = false
  Placement = pos=(0,0,0) rot=(1,0,0;1.5708rad)
  sketch-geometry (49):
    g0: LineSegment StartX=1e-16 StartY=3.5 StartZ=0 EndX=-3.03109 EndY=1.75 EndZ=0
    g1: LineSegment StartX=-3.03109 StartY=1.75 StartZ=0 EndX=-3.03109 EndY=-1.75 EndZ=0
    g2: LineSegment StartX=-3.03109 StartY=-1.75 StartZ=0 EndX=-1e-16 EndY=-3.5 EndZ=0
    g3: LineSegment StartX=-1e-16 StartY=-3.5 StartZ=0 EndX=3.03109 EndY=-1.75 EndZ=0
    g4: LineSegment StartX=3.03109 StartY=-1.75 StartZ=0 EndX=3.03109 EndY=1.75 EndZ=0
    g5: LineSegment StartX=3.03109 StartY=1.75 StartZ=0 EndX=1e-16 EndY=3.5 EndZ=0
    g6: Circle [constr] CenterX=0 CenterY=0 CenterZ=0 NormalX=0 NormalY=0 NormalZ=1 AngleXU=0 Radius=3.5
    g7: LineSegment StartX=4.96892 StartY=-1.75002 StartZ=0 EndX=8.00002 EndY=-3.5 EndZ=0
    g8: LineSegment StartX=8.00002 StartY=-3.5 StartZ=0 EndX=11.0311 EndY=-1.74998 EndZ=0
    g9: LineSegment StartX=11.0311 StartY=-1.74998 StartZ=0 EndX=11.0311 EndY=1.75002 EndZ=0
    g10: LineSegment StartX=11.0311 StartY=1.75002 StartZ=0 EndX=7.99998 EndY=3.5 EndZ=0
    g11: LineSegment StartX=7.99998 StartY=3.5 StartZ=0 EndX=4.9689 EndY=1.74998 EndZ=0
    g12: LineSegment StartX=4.9689 StartY=1.74998 StartZ=0 EndX=4.96892 EndY=-1.75002 EndZ=0
    g13: Circle [constr] CenterX=8 CenterY=0 CenterZ=0 NormalX=0 NormalY=0 NormalZ=1 AngleXU=0 Radius=3.5
    g14: LineSegment StartX=4.03109 StartY=3.5 StartZ=0 EndX=7.06218 EndY=5.25 EndZ=0
    g15: LineSegment StartX=7.06218 StartY=5.25 StartZ=0 EndX=7.06218 EndY=8.75 EndZ=0
    g16: LineSegment StartX=7.06218 StartY=8.75 StartZ=0 EndX=4.03109 EndY=10.5 EndZ=0
    g17: LineSegment StartX=4.03109 StartY=10.5 StartZ=0 EndX=1 EndY=8.75 EndZ=0
    g18: LineSegment StartX=1 StartY=8.75 StartZ=0 EndX=1 EndY=5.25 EndZ=0
    g19: LineSegment StartX=1 StartY=5.25 StartZ=0 EndX=4.03109 EndY=3.5 EndZ=0
    g20: Circle [constr] CenterX=4.03109 CenterY=7 CenterZ=0 NormalX=0 NormalY=0 NormalZ=1 AngleXU=0 Radius=3.5
    g21: LineSegment StartX=-1 StartY=5.25 StartZ=0 EndX=-1 EndY=8.75 EndZ=0
    g22: LineSegment StartX=-1 StartY=8.75 StartZ=0 EndX=-4.03109 EndY=10.5 EndZ=0
    g23: LineSegment StartX=-4.03109 StartY=10.5 StartZ=0 EndX=-7.06218 EndY=8.75 EndZ=0
    g24: LineSegment StartX=-7.06218 StartY=8.75 StartZ=0 EndX=-7.06218 EndY=5.25 EndZ=0
    g25: LineSegment StartX=-7.06218 StartY=5.25 StartZ=0 EndX=-4.03109 EndY=3.5 EndZ=0
    g26: LineSegment StartX=-4.03109 StartY=3.5 StartZ=0 EndX=-1 EndY=5.25 EndZ=0
    g27: Circle [constr] CenterX=-4.03109 CenterY=7 CenterZ=0 NormalX=0 NormalY=0 NormalZ=1 AngleXU=0 Radius=3.5
    g28: LineSegment StartX=-4.96891 StartY=-1.75 StartZ=0 EndX=-4.96891 EndY=1.75 EndZ=0
    g29: LineSegment StartX=-4.96891 StartY=1.75 StartZ=0 EndX=-8 EndY=3.5 EndZ=0
    g30: LineSegment StartX=-8 StartY=3.5 StartZ=0 EndX=-11.0311 EndY=1.75 EndZ=0
    g31: LineSegment StartX=-11.0311 StartY=1.75 StartZ=0 EndX=-11.0311 EndY=-1.75 EndZ=0
    g32: LineSegment StartX=-11.0311 StartY=-1.75 StartZ=0 EndX=-8 EndY=-3.5 EndZ=0
    g33: LineSegment StartX=-8 StartY=-3.5 StartZ=0 EndX=-4.96891 EndY=-1.75 EndZ=0
    g34: Circle [constr] CenterX=-8 CenterY=0 CenterZ=0 NormalX=0 NormalY=0 NormalZ=1 AngleXU=0 Radius=3.5
    g35: LineSegment StartX=-4.03109 StartY=-3.5 StartZ=0 EndX=-7.06218 EndY=-5.25 EndZ=0
    g36: LineSegment StartX=-7.06218 StartY=-5.25 StartZ=0 EndX=-7.06218 EndY=-8.75 EndZ=0
    g37: LineSegment StartX=-7.06218 StartY=-8.75 StartZ=0 EndX=-4.03109 EndY=-10.5 EndZ=0
    g38: LineSegment StartX=-4.03109 StartY=-10.5 StartZ=0 EndX=-1 EndY=-8.75 EndZ=0
    g39: LineSegment StartX=-1 StartY=-8.75 StartZ=0 EndX=-1 EndY=-5.25 EndZ=0
    g40: LineSegment StartX=-1 StartY=-5.25 StartZ=0 EndX=-4.03109 EndY=-3.5 EndZ=0
    g41: Circle [constr] CenterX=-4.03109 CenterY=-7 CenterZ=0 NormalX=0 NormalY=0 NormalZ=1 AngleXU=0 Radius=3.5
    g42: LineSegment StartX=4.03109 StartY=-3.5 StartZ=0 EndX=1 EndY=-5.25 EndZ=0
    g43: LineSegment StartX=1 StartY=-5.25 StartZ=0 EndX=1 EndY=-8.75 EndZ=0
    g44: LineSegment StartX=1 StartY=-8.75 StartZ=0 EndX=4.03109 EndY=-10.5 EndZ=0
    g45: LineSegment StartX=4.03109 StartY=-10.5 StartZ=0 EndX=7.06218 EndY=-8.75 EndZ=0
    g46: LineSegment StartX=7.06218 StartY=-8.75 StartZ=0 EndX=7.06218 EndY=-5.25 EndZ=0
    g47: LineSegment StartX=7.06218 StartY=-5.25 StartZ=0 EndX=4.03109 EndY=-3.5 EndZ=0
    g48: Circle [constr] CenterX=4.03109 CenterY=-7 CenterZ=0 NormalX=0 NormalY=0 NormalZ=1 AngleXU=0 Radius=3.5
  constraints (117):
    c: Coincident(g0,g1)
    c: Coincident(g1,g2)
    c: Coincident(g2,g3)
    c: Coincident(g3,g4)
    c: Coincident(g4,g5)
    c: Coincident(g5,g0)
    c: Equal(g0, g1-g5) x5
    c: PointOnObject(g0,g6)
    c: PointOnObject(g1,g6)
    c: PointOnObject(g2,g6)
    c: PointOnObject(g3,g6)
    c: PointOnObject(g4,g6)
    c: PointOnObject(g5,g6)
    c: Coincident(g6,g-1)
    c: Diameter(g6) = 7
    c: PointOnObject(g0,g-2)
    c: Coincident(g7,g8)
    c: Coincident(g8,g9)
    c: Coincident(g9,g10)
    c: Coincident(g10,g11)
    c: Coincident(g11,g12)
    c: Coincident(g12,g7)
    c: Equal(g7, g8-g12) x5
    c: PointOnObject(g7,g13)
    c: PointOnObject(g8,g13)
    c: PointOnObject(g9,g13)
    c: PointOnObject(g10,g13)
    c: PointOnObject(g11,g13)
    c: PointOnObject(g12,g13)
    c: PointOnObject(g13,g-1)
    c: Diameter(g13) = 7
    c: Distance(g6,g13) = 8
    c: Horizontal(g0,g10)
    c: Coincident(g14,g15)
    c: Coincident(g15,g16)
    c: Coincident(g16,g17)
    c: Coincident(g17,g18)
    c: Coincident(g18,g19)
    c: Coincident(g19,g14)
    c: Equal(g14, g15-g19) x5
    c: PointOnObject(g14,g20)
    c: PointOnObject(g15,g20)
    c: PointOnObject(g16,g20)
    c: PointOnObject(g17,g20)
    c: PointOnObject(g18,g20)
    c: PointOnObject(g19,g20)
    c: Diameter(g20) = 7
    c: DistanceY(g-1,g20) = 7
    c: Vertical(g18)
    c: Distance(g17,g-2) = 1
    c: Coincident(g21,g22)
    c: Coincident(g22,g23)
    c: Coincident(g23,g24)
    c: Coincident(g24,g25)
    c: Coincident(g25,g26)
    c: Coincident(g26,g21)
    c: Equal(g21, g22-g26) x5
    c: PointOnObject(g21,g27)
    c: PointOnObject(g22,g27)
    c: PointOnObject(g23,g27)
    c: PointOnObject(g24,g27)
    c: PointOnObject(g25,g27)
    c: PointOnObject(g26,g27)
    c: Diameter(g27) = 7
    c: DistanceY(g-1,g27) = 7
    c: DistanceX(g21,g-1) = 1
    c: Vertical(g21)
    c: Coincident(g28,g29)
    c: Coincident(g29,g30)
    c: Coincident(g30,g31)
    c: Coincident(g31,g32)
    c: Coincident(g32,g33)
    c: Coincident(g33,g28)
    c: Equal(g28, g29-g33) x5
    c: PointOnObject(g28,g34)
    c: PointOnObject(g29,g34)
    c: PointOnObject(g30,g34)
    c: PointOnObject(g31,g34)
    c: PointOnObject(g32,g34)
    c: PointOnObject(g33,g34)
    c: PointOnObject(g34,g-1)
    c: Diameter(g34) = 7
    c: Vertical(g31)
    c: DistanceX(g34,g-1) = 8
    c: Coincident(g35,g36)
    c: Coincident(g36,g37)
    c: Coincident(g37,g38)
    c: Coincident(g38,g39)
    c: Coincident(g39,g40)
    c: Coincident(g40,g35)
    c: Equal(g35, g36-g40) x5
    c: PointOnObject(g35,g41)
    c: PointOnObject(g36,g41)
    c: PointOnObject(g37,g41)
    c: PointOnObject(g38,g41)
    c: PointOnObject(g39,g41)
    c: PointOnObject(g40,g41)
    c: Coincident(g42,g43)
    c: Coincident(g43,g44)
    c: Coincident(g44,g45)
    c: Coincident(g45,g46)
    c: Coincident(g46,g47)
    c: Coincident(g47,g42)
    c: Equal(g42, g43-g47) x5
    c: PointOnObject(g42,g48)
    c: PointOnObject(g43,g48)
    c: PointOnObject(g44,g48)
    c: PointOnObject(g45,g48)
    c: PointOnObject(g46,g48)
    c: PointOnObject(g47,g48)
    c: Equal(g41,g48)
    c: Diameter(g41) = 7
    c: Vertical(g39)
    c: Vertical(g43)
    c: Distance(g-2,g39) = 1
    c: Symmetric(g38,g43,g-2)
    c: Distance(g41,g-1) = 7
FEATURE [Part::Extrusion] Extrude657  label="hex259"
  Base = -> Sketch666
  Dir = (0,-1,2e-16)
  DirMode = 2
  FaceMakerClass = Part::FaceMakerBullseye
  FaceMakerMode = 3
  LengthFwd = 10
  LengthRev = 0
  Placement = pos=(104,0,0) rot=(0,0,1;0rad)
  Solid = true
  Symmetric = false
FEATURE [Sketcher::SketchObject] Sketch667
  ArcFitTolerance = 1e-06
  FullyConstrained = true
  MakeInternals = false
  Placement = pos=(0,0,0) rot=(1,0,0;1.5708rad)
  sketch-geometry (49):
    g0: LineSegment StartX=1e-16 StartY=3.5 StartZ=0 EndX=-3.03109 EndY=1.75 EndZ=0
    g1: LineSegment StartX=-3.03109 StartY=1.75 StartZ=0 EndX=-3.03109 EndY=-1.75 EndZ=0
    g2: LineSegment StartX=-3.03109 StartY=-1.75 StartZ=0 EndX=-1e-16 EndY=-3.5 EndZ=0
    g3: LineSegment StartX=-1e-16 StartY=-3.5 StartZ=0 EndX=3.03109 EndY=-1.75 EndZ=0
    g4: LineSegment StartX=3.03109 StartY=-1.75 StartZ=0 EndX=3.03109 EndY=1.75 EndZ=0
    g5: LineSegment StartX=3.03109 StartY=1.75 StartZ=0 EndX=1e-16 EndY=3.5 EndZ=0
    g6: Circle [constr] CenterX=0 CenterY=0 CenterZ=0 NormalX=0 NormalY=0 NormalZ=1 AngleXU=0 Radius=3.5
    g7: LineSegment StartX=4.96892 StartY=-1.75002 StartZ=0 EndX=8.00002 EndY=-3.5 EndZ=0
    g8: LineSegment StartX=8.00002 StartY=-3.5 StartZ=0 EndX=11.0311 EndY=-1.74998 EndZ=0
    g9: LineSegment StartX=11.0311 StartY=-1.74998 StartZ=0 EndX=11.0311 EndY=1.75002 EndZ=0
    g10: LineSegment StartX=11.0311 StartY=1.75002 StartZ=0 EndX=7.99998 EndY=3.5 EndZ=0
    g11: LineSegment StartX=7.99998 StartY=3.5 StartZ=0 EndX=4.9689 EndY=1.74998 EndZ=0
    g12: LineSegment StartX=4.9689 StartY=1.74998 StartZ=0 EndX=4.96892 EndY=-1.75002 EndZ=0
    g13: Circle [constr] CenterX=8 CenterY=0 CenterZ=0 NormalX=0 NormalY=0 NormalZ=1 AngleXU=0 Radius=3.5
    g14: LineSegment StartX=4.03109 StartY=3.5 StartZ=0 EndX=7.06218 EndY=5.25 EndZ=0
    g15: LineSegment StartX=7.06218 StartY=5.25 StartZ=0 EndX=7.06218 EndY=8.75 EndZ=0
    g16: LineSegment StartX=7.06218 StartY=8.75 StartZ=0 EndX=4.03109 EndY=10.5 EndZ=0
    g17: LineSegment StartX=4.03109 StartY=10.5 StartZ=0 EndX=1 EndY=8.75 EndZ=0
    g18: LineSegment StartX=1 StartY=8.75 StartZ=0 EndX=1 EndY=5.25 EndZ=0
    g19: LineSegment StartX=1 StartY=5.25 StartZ=0 EndX=4.03109 EndY=3.5 EndZ=0
    g20: Circle [constr] CenterX=4.03109 CenterY=7 CenterZ=0 NormalX=0 NormalY=0 NormalZ=1 AngleXU=0 Radius=3.5
    g21: LineSegment StartX=-1 StartY=5.25 StartZ=0 EndX=-1 EndY=8.75 EndZ=0
    g22: LineSegment StartX=-1 StartY=8.75 StartZ=0 EndX=-4.03109 EndY=10.5 EndZ=0
    g23: LineSegment StartX=-4.03109 StartY=10.5 StartZ=0 EndX=-7.06218 EndY=8.75 EndZ=0
    g24: LineSegment StartX=-7.06218 StartY=8.75 StartZ=0 EndX=-7.06218 EndY=5.25 EndZ=0
    g25: LineSegment StartX=-7.06218 StartY=5.25 StartZ=0 EndX=-4.03109 EndY=3.5 EndZ=0
    g26: LineSegment StartX=-4.03109 StartY=3.5 StartZ=0 EndX=-1 EndY=5.25 EndZ=0
    g27: Circle [constr] CenterX=-4.03109 CenterY=7 CenterZ=0 NormalX=0 NormalY=0 NormalZ=1 AngleXU=0 Radius=3.5
    g28: LineSegment StartX=-4.96891 StartY=-1.75 StartZ=0 EndX=-4.96891 EndY=1.75 EndZ=0
    g29: LineSegment StartX=-4.96891 StartY=1.75 StartZ=0 EndX=-8 EndY=3.5 EndZ=0
    g30: LineSegment StartX=-8 StartY=3.5 StartZ=0 EndX=-11.0311 EndY=1.75 EndZ=0
    g31: LineSegment StartX=-11.0311 StartY=1.75 StartZ=0 EndX=-11.0311 EndY=-1.75 EndZ=0
    g32: LineSegment StartX=-11.0311 StartY=-1.75 StartZ=0 EndX=-8 EndY=-3.5 EndZ=0
    g33: LineSegment StartX=-8 StartY=-3.5 StartZ=0 EndX=-4.96891 EndY=-1.75 EndZ=0
    g34: Circle [constr] CenterX=-8 CenterY=0 CenterZ=0 NormalX=0 NormalY=0 NormalZ=1 AngleXU=0 Radius=3.5
    g35: LineSegment StartX=-4.03109 StartY=-3.5 StartZ=0 EndX=-7.06218 EndY=-5.25 EndZ=0
    g36: LineSegment StartX=-7.06218 StartY=-5.25 StartZ=0 EndX=-7.06218 EndY=-8.75 EndZ=0
    g37: LineSegment StartX=-7.06218 StartY=-8.75 StartZ=0 EndX=-4.03109 EndY=-10.5 EndZ=0
    g38: LineSegment StartX=-4.03109 StartY=-10.5 StartZ=0 EndX=-1 EndY=-8.75 EndZ=0
    g39: LineSegment StartX=-1 StartY=-8.75 StartZ=0 EndX=-1 EndY=-5.25 EndZ=0
    g40: LineSegment StartX=-1 StartY=-5.25 StartZ=0 EndX=-4.03109 EndY=-3.5 EndZ=0
    g41: Circle [constr] CenterX=-4.03109 CenterY=-7 CenterZ=0 NormalX=0 NormalY=0 NormalZ=1 AngleXU=0 Radius=3.5
    g42: LineSegment StartX=4.03109 StartY=-3.5 StartZ=0 EndX=1 EndY=-5.25 EndZ=0
    g43: LineSegment StartX=1 StartY=-5.25 StartZ=0 EndX=1 EndY=-8.75 EndZ=0
    g44: LineSegment StartX=1 StartY=-8.75 StartZ=0 EndX=4.03109 EndY=-10.5 EndZ=0
    g45: LineSegment StartX=4.03109 StartY=-10.5 StartZ=0 EndX=7.06218 EndY=-8.75 EndZ=0
    g46: LineSegment StartX=7.06218 StartY=-8.75 StartZ=0 EndX=7.06218 EndY=-5.25 EndZ=0
    g47: LineSegment StartX=7.06218 StartY=-5.25 StartZ=0 EndX=4.03109 EndY=-3.5 EndZ=0
    g48: Circle [constr] CenterX=4.03109 CenterY=-7 CenterZ=0 NormalX=0 NormalY=0 NormalZ=1 AngleXU=0 Radius=3.5
  constraints (117):
    c: Coincident(g0,g1)
    c: Coincident(g1,g2)
    c: Coincident(g2,g3)
    c: Coincident(g3,g4)
    c: Coincident(g4,g5)
    c: Coincident(g5,g0)
    c: Equal(g0, g1-g5) x5
    c: PointOnObject(g0,g6)
    c: PointOnObject(g1,g6)
    c: PointOnObject(g2,g6)
    c: PointOnObject(g3,g6)
    c: PointOnObject(g4,g6)
    c: PointOnObject(g5,g6)
    c: Coincident(g6,g-1)
    c: Diameter(g6) = 7
    c: PointOnObject(g0,g-2)
    c: Coincident(g7,g8)
    c: Coincident(g8,g9)
    c: Coincident(g9,g10)
    c: Coincident(g10,g11)
    c: Coincident(g11,g12)
    c: Coincident(g12,g7)
    c: Equal(g7, g8-g12) x5
    c: PointOnObject(g7,g13)
    c: PointOnObject(g8,g13)
    c: PointOnObject(g9,g13)
    c: PointOnObject(g10,g13)
    c: PointOnObject(g11,g13)
    c: PointOnObject(g12,g13)
    c: PointOnObject(g13,g-1)
    c: Diameter(g13) = 7
    c: Distance(g6,g13) = 8
    c: Horizontal(g0,g10)
    c: Coincident(g14,g15)
    c: Coincident(g15,g16)
    c: Coincident(g16,g17)
    c: Coincident(g17,g18)
    c: Coincident(g18,g19)
    c: Coincident(g19,g14)
    c: Equal(g14, g15-g19) x5
    c: PointOnObject(g14,g20)
    c: PointOnObject(g15,g20)
    c: PointOnObject(g16,g20)
    c: PointOnObject(g17,g20)
    c: PointOnObject(g18,g20)
    c: PointOnObject(g19,g20)
    c: Diameter(g20) = 7
    c: DistanceY(g-1,g20) = 7
    c: Vertical(g18)
    c: Distance(g17,g-2) = 1
    c: Coincident(g21,g22)
    c: Coincident(g22,g23)
    c: Coincident(g23,g24)
    c: Coincident(g24,g25)
    c: Coincident(g25,g26)
    c: Coincident(g26,g21)
    c: Equal(g21, g22-g26) x5
    c: PointOnObject(g21,g27)
    c: PointOnObject(g22,g27)
    c: PointOnObject(g23,g27)
    c: PointOnObject(g24,g27)
    c: PointOnObject(g25,g27)
    c: PointOnObject(g26,g27)
    c: Diameter(g27) = 7
    c: DistanceY(g-1,g27) = 7
    c: DistanceX(g21,g-1) = 1
    c: Vertical(g21)
    c: Coincident(g28,g29)
    c: Coincident(g29,g30)
    c: Coincident(g30,g31)
    c: Coincident(g31,g32)
    c: Coincident(g32,g33)
    c: Coincident(g33,g28)
    c: Equal(g28, g29-g33) x5
    c: PointOnObject(g28,g34)
    c: PointOnObject(g29,g34)
    c: PointOnObject(g30,g34)
    c: PointOnObject(g31,g34)
    c: PointOnObject(g32,g34)
    c: PointOnObject(g33,g34)
    c: PointOnObject(g34,g-1)
    c: Diameter(g34) = 7
    c: Vertical(g31)
    c: DistanceX(g34,g-1) = 8
    c: Coincident(g35,g36)
    c: Coincident(g36,g37)
    c: Coincident(g37,g38)
    c: Coincident(g38,g39)
    c: Coincident(g39,g40)
    c: Coincident(g40,g35)
    c: Equal(g35, g36-g40) x5
    c: PointOnObject(g35,g41)
    c: PointOnObject(g36,g41)
    c: PointOnObject(g37,g41)
    c: PointOnObject(g38,g41)
    c: PointOnObject(g39,g41)
    c: PointOnObject(g40,g41)
    c: Coincident(g42,g43)
    c: Coincident(g43,g44)
    c: Coincident(g44,g45)
    c: Coincident(g45,g46)
    c: Coincident(g46,g47)
    c: Coincident(g47,g42)
    c: Equal(g42, g43-g47) x5
    c: PointOnObject(g42,g48)
    c: PointOnObject(g43,g48)
    c: PointOnObject(g44,g48)
    c: PointOnObject(g45,g48)
    c: PointOnObject(g46,g48)
    c: PointOnObject(g47,g48)
    c: Equal(g41,g48)
    c: Diameter(g41) = 7
    c: Vertical(g39)
    c: Vertical(g43)
    c: Distance(g-2,g39) = 1
    c: Symmetric(g38,g43,g-2)
    c: Distance(g41,g-1) = 7
FEATURE [Part::Extrusion] Extrude658  label="hex260"
  Base = -> Sketch667
  Dir = (0,-1,2e-16)
  DirMode = 2
  FaceMakerClass = Part::FaceMakerBullseye
  FaceMakerMode = 3
  LengthFwd = 10
  LengthRev = 0
  Placement = pos=(96,0,-14) rot=(0,0,1;0rad)
  Solid = true
  Symmetric = false
FEATURE [Sketcher::SketchObject] Sketch668
  ArcFitTolerance = 1e-06
  FullyConstrained = true
  MakeInternals = false
  Placement = pos=(0,0,0) rot=(1,0,0;1.5708rad)
  sketch-geometry (49):
    g0: LineSegment StartX=1e-16 StartY=3.5 StartZ=0 EndX=-3.03109 EndY=1.75 EndZ=0
    g1: LineSegment StartX=-3.03109 StartY=1.75 StartZ=0 EndX=-3.03109 EndY=-1.75 EndZ=0
    g2: LineSegment StartX=-3.03109 StartY=-1.75 StartZ=0 EndX=-1e-16 EndY=-3.5 EndZ=0
    g3: LineSegment StartX=-1e-16 StartY=-3.5 StartZ=0 EndX=3.03109 EndY=-1.75 EndZ=0
    g4: LineSegment StartX=3.03109 StartY=-1.75 StartZ=0 EndX=3.03109 EndY=1.75 EndZ=0
    g5: LineSegment StartX=3.03109 StartY=1.75 StartZ=0 EndX=1e-16 EndY=3.5 EndZ=0
    g6: Circle [constr] CenterX=0 CenterY=0 CenterZ=0 NormalX=0 NormalY=0 NormalZ=1 AngleXU=0 Radius=3.5
    g7: LineSegment StartX=4.96892 StartY=-1.75002 StartZ=0 EndX=8.00002 EndY=-3.5 EndZ=0
    g8: LineSegment StartX=8.00002 StartY=-3.5 StartZ=0 EndX=11.0311 EndY=-1.74998 EndZ=0
    g9: LineSegment StartX=11.0311 StartY=-1.74998 StartZ=0 EndX=11.0311 EndY=1.75002 EndZ=0
    g10: LineSegment StartX=11.0311 StartY=1.75002 StartZ=0 EndX=7.99998 EndY=3.5 EndZ=0
    g11: LineSegment StartX=7.99998 StartY=3.5 StartZ=0 EndX=4.9689 EndY=1.74998 EndZ=0
    g12: LineSegment StartX=4.9689 StartY=1.74998 StartZ=0 EndX=4.96892 EndY=-1.75002 EndZ=0
    g13: Circle [constr] CenterX=8 CenterY=0 CenterZ=0 NormalX=0 NormalY=0 NormalZ=1 AngleXU=0 Radius=3.5
    g14: LineSegment StartX=4.03109 StartY=3.5 StartZ=0 EndX=7.06218 EndY=5.25 EndZ=0
    g15: LineSegment StartX=7.06218 StartY=5.25 StartZ=0 EndX=7.06218 EndY=8.75 EndZ=0
    g16: LineSegment StartX=7.06218 StartY=8.75 StartZ=0 EndX=4.03109 EndY=10.5 EndZ=0
    g17: LineSegment StartX=4.03109 StartY=10.5 StartZ=0 EndX=1 EndY=8.75 EndZ=0
    g18: LineSegment StartX=1 StartY=8.75 StartZ=0 EndX=1 EndY=5.25 EndZ=0
    g19: LineSegment StartX=1 StartY=5.25 StartZ=0 EndX=4.03109 EndY=3.5 EndZ=0
    g20: Circle [constr] CenterX=4.03109 CenterY=7 CenterZ=0 NormalX=0 NormalY=0 NormalZ=1 AngleXU=0 Radius=3.5
    g21: LineSegment StartX=-1 StartY=5.25 StartZ=0 EndX=-1 EndY=8.75 EndZ=0
    g22: LineSegment StartX=-1 StartY=8.75 StartZ=0 EndX=-4.03109 EndY=10.5 EndZ=0
    g23: LineSegment StartX=-4.03109 StartY=10.5 StartZ=0 EndX=-7.06218 EndY=8.75 EndZ=0
    g24: LineSegment StartX=-7.06218 StartY=8.75 StartZ=0 EndX=-7.06218 EndY=5.25 EndZ=0
    g25: LineSegment StartX=-7.06218 StartY=5.25 StartZ=0 EndX=-4.03109 EndY=3.5 EndZ=0
    g26: LineSegment StartX=-4.03109 StartY=3.5 StartZ=0 EndX=-1 EndY=5.25 EndZ=0
    g27: Circle [constr] CenterX=-4.03109 CenterY=7 CenterZ=0 NormalX=0 NormalY=0 NormalZ=1 AngleXU=0 Radius=3.5
    g28: LineSegment StartX=-4.96891 StartY=-1.75 StartZ=0 EndX=-4.96891 EndY=1.75 EndZ=0
    g29: LineSegment StartX=-4.96891 StartY=1.75 StartZ=0 EndX=-8 EndY=3.5 EndZ=0
    g30: LineSegment StartX=-8 StartY=3.5 StartZ=0 EndX=-11.0311 EndY=1.75 EndZ=0
    g31: LineSegment StartX=-11.0311 StartY=1.75 StartZ=0 EndX=-11.0311 EndY=-1.75 EndZ=0
    g32: LineSegment StartX=-11.0311 StartY=-1.75 StartZ=0 EndX=-8 EndY=-3.5 EndZ=0
    g33: LineSegment StartX=-8 StartY=-3.5 StartZ=0 EndX=-4.96891 EndY=-1.75 EndZ=0
    g34: Circle [constr] CenterX=-8 CenterY=0 CenterZ=0 NormalX=0 NormalY=0 NormalZ=1 AngleXU=0 Radius=3.5
    g35: LineSegment StartX=-4.03109 StartY=-3.5 StartZ=0 EndX=-7.06218 EndY=-5.25 EndZ=0
    g36: LineSegment StartX=-7.06218 StartY=-5.25 StartZ=0 EndX=-7.06218 EndY=-8.75 EndZ=0
    g37: LineSegment StartX=-7.06218 StartY=-8.75 StartZ=0 EndX=-4.03109 EndY=-10.5 EndZ=0
    g38: LineSegment StartX=-4.03109 StartY=-10.5 StartZ=0 EndX=-1 EndY=-8.75 EndZ=0
    g39: LineSegment StartX=-1 StartY=-8.75 StartZ=0 EndX=-1 EndY=-5.25 EndZ=0
    g40: LineSegment StartX=-1 StartY=-5.25 StartZ=0 EndX=-4.03109 EndY=-3.5 EndZ=0
    g41: Circle [constr] CenterX=-4.03109 CenterY=-7 CenterZ=0 NormalX=0 NormalY=0 NormalZ=1 AngleXU=0 Radius=3.5
    g42: LineSegment StartX=4.03109 StartY=-3.5 StartZ=0 EndX=1 EndY=-5.25 EndZ=0
    g43: LineSegment StartX=1 StartY=-5.25 StartZ=0 EndX=1 EndY=-8.75 EndZ=0
    g44: LineSegment StartX=1 StartY=-8.75 StartZ=0 EndX=4.03109 EndY=-10.5 EndZ=0
    g45: LineSegment StartX=4.03109 StartY=-10.5 StartZ=0 EndX=7.06218 EndY=-8.75 EndZ=0
    g46: LineSegment StartX=7.06218 StartY=-8.75 StartZ=0 EndX=7.06218 EndY=-5.25 EndZ=0
    g47: LineSegment StartX=7.06218 StartY=-5.25 StartZ=0 EndX=4.03109 EndY=-3.5 EndZ=0
    g48: Circle [constr] CenterX=4.03109 CenterY=-7 CenterZ=0 NormalX=0 NormalY=0 NormalZ=1 AngleXU=0 Radius=3.5
  constraints (117):
    c: Coincident(g0,g1)
    c: Coincident(g1,g2)
    c: Coincident(g2,g3)
    c: Coincident(g3,g4)
    c: Coincident(g4,g5)
    c: Coincident(g5,g0)
    c: Equal(g0, g1-g5) x5
    c: PointOnObject(g0,g6)
    c: PointOnObject(g1,g6)
    c: PointOnObject(g2,g6)
    c: PointOnObject(g3,g6)
    c: PointOnObject(g4,g6)
    c: PointOnObject(g5,g6)
    c: Coincident(g6,g-1)
    c: Diameter(g6) = 7
    c: PointOnObject(g0,g-2)
    c: Coincident(g7,g8)
    c: Coincident(g8,g9)
    c: Coincident(g9,g10)
    c: Coincident(g10,g11)
    c: Coincident(g11,g12)
    c: Coincident(g12,g7)
    c: Equal(g7, g8-g12) x5
    c: PointOnObject(g7,g13)
    c: PointOnObject(g8,g13)
    c: PointOnObject(g9,g13)
    c: PointOnObject(g10,g13)
    c: PointOnObject(g11,g13)
    c: PointOnObject(g12,g13)
    c: PointOnObject(g13,g-1)
    c: Diameter(g13) = 7
    c: Distance(g6,g13) = 8
    c: Horizontal(g0,g10)
    c: Coincident(g14,g15)
    c: Coincident(g15,g16)
    c: Coincident(g16,g17)
    c: Coincident(g17,g18)
    c: Coincident(g18,g19)
    c: Coincident(g19,g14)
    c: Equal(g14, g15-g19) x5
    c: PointOnObject(g14,g20)
    c: PointOnObject(g15,g20)
    c: PointOnObject(g16,g20)
    c: PointOnObject(g17,g20)
    c: PointOnObject(g18,g20)
    c: PointOnObject(g19,g20)
    c: Diameter(g20) = 7
    c: DistanceY(g-1,g20) = 7
    c: Vertical(g18)
    c: Distance(g17,g-2) = 1
    c: Coincident(g21,g22)
    c: Coincident(g22,g23)
    c: Coincident(g23,g24)
    c: Coincident(g24,g25)
    c: Coincident(g25,g26)
    c: Coincident(g26,g21)
    c: Equal(g21, g22-g26) x5
    c: PointOnObject(g21,g27)
    c: PointOnObject(g22,g27)
    c: PointOnObject(g23,g27)
    c: PointOnObject(g24,g27)
    c: PointOnObject(g25,g27)
    c: PointOnObject(g26,g27)
    c: Diameter(g27) = 7
    c: DistanceY(g-1,g27) = 7
    c: DistanceX(g21,g-1) = 1
    c: Vertical(g21)
    c: Coincident(g28,g29)
    c: Coincident(g29,g30)
    c: Coincident(g30,g31)
    c: Coincident(g31,g32)
    c: Coincident(g32,g33)
    c: Coincident(g33,g28)
    c: Equal(g28, g29-g33) x5
    c: PointOnObject(g28,g34)
    c: PointOnObject(g29,g34)
    c: PointOnObject(g30,g34)
    c: PointOnObject(g31,g34)
    c: PointOnObject(g32,g34)
    c: PointOnObject(g33,g34)
    c: PointOnObject(g34,g-1)
    c: Diameter(g34) = 7
    c: Vertical(g31)
    c: DistanceX(g34,g-1) = 8
    c: Coincident(g35,g36)
    c: Coincident(g36,g37)
    c: Coincident(g37,g38)
    c: Coincident(g38,g39)
    c: Coincident(g39,g40)
    c: Coincident(g40,g35)
    c: Equal(g35, g36-g40) x5
    c: PointOnObject(g35,g41)
    c: PointOnObject(g36,g41)
    c: PointOnObject(g37,g41)
    c: PointOnObject(g38,g41)
    c: PointOnObject(g39,g41)
    c: PointOnObject(g40,g41)
    c: Coincident(g42,g43)
    c: Coincident(g43,g44)
    c: Coincident(g44,g45)
    c: Coincident(g45,g46)
    c: Coincident(g46,g47)
    c: Coincident(g47,g42)
    c: Equal(g42, g43-g47) x5
    c: PointOnObject(g42,g48)
    c: PointOnObject(g43,g48)
    c: PointOnObject(g44,g48)
    c: PointOnObject(g45,g48)
    c: PointOnObject(g46,g48)
    c: PointOnObject(g47,g48)
    c: Equal(g41,g48)
    c: Diameter(g41) = 7
    c: Vertical(g39)
    c: Vertical(g43)
    c: Distance(g-2,g39) = 1
    c: Symmetric(g38,g43,g-2)
    c: Distance(g41,g-1) = 7
FEATURE [Part::Extrusion] Extrude659  label="hex261"
  Base = -> Sketch668
  Dir = (0,-1,2e-16)
  DirMode = 2
  FaceMakerClass = Part::FaceMakerBullseye
  FaceMakerMode = 3
  LengthFwd = 10
  LengthRev = 0
  Placement = pos=(88,0,-28) rot=(0,0,1;0rad)
  Solid = true
  Symmetric = false
FEATURE [Sketcher::SketchObject] Sketch669
  ArcFitTolerance = 1e-06
  FullyConstrained = true
  MakeInternals = false
  Placement = pos=(0,0,0) rot=(1,0,0;1.5708rad)
  sketch-geometry (49):
    g0: LineSegment StartX=1e-16 StartY=3.5 StartZ=0 EndX=-3.03109 EndY=1.75 EndZ=0
    g1: LineSegment StartX=-3.03109 StartY=1.75 StartZ=0 EndX=-3.03109 EndY=-1.75 EndZ=0
    g2: LineSegment StartX=-3.03109 StartY=-1.75 StartZ=0 EndX=-1e-16 EndY=-3.5 EndZ=0
    g3: LineSegment StartX=-1e-16 StartY=-3.5 StartZ=0 EndX=3.03109 EndY=-1.75 EndZ=0
    g4: LineSegment StartX=3.03109 StartY=-1.75 StartZ=0 EndX=3.03109 EndY=1.75 EndZ=0
    g5: LineSegment StartX=3.03109 StartY=1.75 StartZ=0 EndX=1e-16 EndY=3.5 EndZ=0
    g6: Circle [constr] CenterX=0 CenterY=0 CenterZ=0 NormalX=0 NormalY=0 NormalZ=1 AngleXU=0 Radius=3.5
    g7: LineSegment StartX=4.96892 StartY=-1.75002 StartZ=0 EndX=8.00002 EndY=-3.5 EndZ=0
    g8: LineSegment StartX=8.00002 StartY=-3.5 StartZ=0 EndX=11.0311 EndY=-1.74998 EndZ=0
    g9: LineSegment StartX=11.0311 StartY=-1.74998 StartZ=0 EndX=11.0311 EndY=1.75002 EndZ=0
    g10: LineSegment StartX=11.0311 StartY=1.75002 StartZ=0 EndX=7.99998 EndY=3.5 EndZ=0
    g11: LineSegment StartX=7.99998 StartY=3.5 StartZ=0 EndX=4.9689 EndY=1.74998 EndZ=0
    g12: LineSegment StartX=4.9689 StartY=1.74998 StartZ=0 EndX=4.96892 EndY=-1.75002 EndZ=0
    g13: Circle [constr] CenterX=8 CenterY=0 CenterZ=0 NormalX=0 NormalY=0 NormalZ=1 AngleXU=0 Radius=3.5
    g14: LineSegment StartX=4.03109 StartY=3.5 StartZ=0 EndX=7.06218 EndY=5.25 EndZ=0
    g15: LineSegment StartX=7.06218 StartY=5.25 StartZ=0 EndX=7.06218 EndY=8.75 EndZ=0
    g16: LineSegment StartX=7.06218 StartY=8.75 StartZ=0 EndX=4.03109 EndY=10.5 EndZ=0
    g17: LineSegment StartX=4.03109 StartY=10.5 StartZ=0 EndX=1 EndY=8.75 EndZ=0
    g18: LineSegment StartX=1 StartY=8.75 StartZ=0 EndX=1 EndY=5.25 EndZ=0
    g19: LineSegment StartX=1 StartY=5.25 StartZ=0 EndX=4.03109 EndY=3.5 EndZ=0
    g20: Circle [constr] CenterX=4.03109 CenterY=7 CenterZ=0 NormalX=0 NormalY=0 NormalZ=1 AngleXU=0 Radius=3.5
    g21: LineSegment StartX=-1 StartY=5.25 StartZ=0 EndX=-1 EndY=8.75 EndZ=0
    g22: LineSegment StartX=-1 StartY=8.75 StartZ=0 EndX=-4.03109 EndY=10.5 EndZ=0
    g23: LineSegment StartX=-4.03109 StartY=10.5 StartZ=0 EndX=-7.06218 EndY=8.75 EndZ=0
    g24: LineSegment StartX=-7.06218 StartY=8.75 StartZ=0 EndX=-7.06218 EndY=5.25 EndZ=0
    g25: LineSegment StartX=-7.06218 StartY=5.25 StartZ=0 EndX=-4.03109 EndY=3.5 EndZ=0
    g26: LineSegment StartX=-4.03109 StartY=3.5 StartZ=0 EndX=-1 EndY=5.25 EndZ=0
    g27: Circle [constr] CenterX=-4.03109 CenterY=7 CenterZ=0 NormalX=0 NormalY=0 NormalZ=1 AngleXU=0 Radius=3.5
    g28: LineSegment StartX=-4.96891 StartY=-1.75 StartZ=0 EndX=-4.96891 EndY=1.75 EndZ=0
    g29: LineSegment StartX=-4.96891 StartY=1.75 StartZ=0 EndX=-8 EndY=3.5 EndZ=0
    g30: LineSegment StartX=-8 StartY=3.5 StartZ=0 EndX=-11.0311 EndY=1.75 EndZ=0
    g31: LineSegment StartX=-11.0311 StartY=1.75 StartZ=0 EndX=-11.0311 EndY=-1.75 EndZ=0
    g32: LineSegment StartX=-11.0311 StartY=-1.75 StartZ=0 EndX=-8 EndY=-3.5 EndZ=0
    g33: LineSegment StartX=-8 StartY=-3.5 StartZ=0 EndX=-4.96891 EndY=-1.75 EndZ=0
    g34: Circle [constr] CenterX=-8 CenterY=0 CenterZ=0 NormalX=0 NormalY=0 NormalZ=1 AngleXU=0 Radius=3.5
    g35: LineSegment StartX=-4.03109 StartY=-3.5 StartZ=0 EndX=-7.06218 EndY=-5.25 EndZ=0
    g36: LineSegment StartX=-7.06218 StartY=-5.25 StartZ=0 EndX=-7.06218 EndY=-8.75 EndZ=0
    g37: LineSegment StartX=-7.06218 StartY=-8.75 StartZ=0 EndX=-4.03109 EndY=-10.5 EndZ=0
    g38: LineSegment StartX=-4.03109 StartY=-10.5 StartZ=0 EndX=-1 EndY=-8.75 EndZ=0
    g39: LineSegment StartX=-1 StartY=-8.75 StartZ=0 EndX=-1 EndY=-5.25 EndZ=0
    g40: LineSegment StartX=-1 StartY=-5.25 StartZ=0 EndX=-4.03109 EndY=-3.5 EndZ=0
    g41: Circle [constr] CenterX=-4.03109 CenterY=-7 CenterZ=0 NormalX=0 NormalY=0 NormalZ=1 AngleXU=0 Radius=3.5
    g42: LineSegment StartX=4.03109 StartY=-3.5 StartZ=0 EndX=1 EndY=-5.25 EndZ=0
    g43: LineSegment StartX=1 StartY=-5.25 StartZ=0 EndX=1 EndY=-8.75 EndZ=0
    g44: LineSegment StartX=1 StartY=-8.75 StartZ=0 EndX=4.03109 EndY=-10.5 EndZ=0
    g45: LineSegment StartX=4.03109 StartY=-10.5 StartZ=0 EndX=7.06218 EndY=-8.75 EndZ=0
    g46: LineSegment StartX=7.06218 StartY=-8.75 StartZ=0 EndX=7.06218 EndY=-5.25 EndZ=0
    g47: LineSegment StartX=7.06218 StartY=-5.25 StartZ=0 EndX=4.03109 EndY=-3.5 EndZ=0
    g48: Circle [constr] CenterX=4.03109 CenterY=-7 CenterZ=0 NormalX=0 NormalY=0 NormalZ=1 AngleXU=0 Radius=3.5
  constraints (117):
    c: Coincident(g0,g1)
    c: Coincident(g1,g2)
    c: Coincident(g2,g3)
    c: Coincident(g3,g4)
    c: Coincident(g4,g5)
    c: Coincident(g5,g0)
    c: Equal(g0, g1-g5) x5
    c: PointOnObject(g0,g6)
    c: PointOnObject(g1,g6)
    c: PointOnObject(g2,g6)
    c: PointOnObject(g3,g6)
    c: PointOnObject(g4,g6)
    c: PointOnObject(g5,g6)
    c: Coincident(g6,g-1)
    c: Diameter(g6) = 7
    c: PointOnObject(g0,g-2)
    c: Coincident(g7,g8)
    c: Coincident(g8,g9)
    c: Coincident(g9,g10)
    c: Coincident(g10,g11)
    c: Coincident(g11,g12)
    c: Coincident(g12,g7)
    c: Equal(g7, g8-g12) x5
    c: PointOnObject(g7,g13)
    c: PointOnObject(g8,g13)
    c: PointOnObject(g9,g13)
    c: PointOnObject(g10,g13)
    c: PointOnObject(g11,g13)
    c: PointOnObject(g12,g13)
    c: PointOnObject(g13,g-1)
    c: Diameter(g13) = 7
    c: Distance(g6,g13) = 8
    c: Horizontal(g0,g10)
    c: Coincident(g14,g15)
    c: Coincident(g15,g16)
    c: Coincident(g16,g17)
    c: Coincident(g17,g18)
    c: Coincident(g18,g19)
    c: Coincident(g19,g14)
    c: Equal(g14, g15-g19) x5
    c: PointOnObject(g14,g20)
    c: PointOnObject(g15,g20)
    c: PointOnObject(g16,g20)
    c: PointOnObject(g17,g20)
    c: PointOnObject(g18,g20)
    c: PointOnObject(g19,g20)
    c: Diameter(g20) = 7
    c: DistanceY(g-1,g20) = 7
    c: Vertical(g18)
    c: Distance(g17,g-2) = 1
    c: Coincident(g21,g22)
    c: Coincident(g22,g23)
    c: Coincident(g23,g24)
    c: Coincident(g24,g25)
    c: Coincident(g25,g26)
    c: Coincident(g26,g21)
    c: Equal(g21, g22-g26) x5
    c: PointOnObject(g21,g27)
    c: PointOnObject(g22,g27)
    c: PointOnObject(g23,g27)
    c: PointOnObject(g24,g27)
    c: PointOnObject(g25,g27)
    c: PointOnObject(g26,g27)
    c: Diameter(g27) = 7
    c: DistanceY(g-1,g27) = 7
    c: DistanceX(g21,g-1) = 1
    c: Vertical(g21)
    c: Coincident(g28,g29)
    c: Coincident(g29,g30)
    c: Coincident(g30,g31)
    c: Coincident(g31,g32)
    c: Coincident(g32,g33)
    c: Coincident(g33,g28)
    c: Equal(g28, g29-g33) x5
    c: PointOnObject(g28,g34)
    c: PointOnObject(g29,g34)
    c: PointOnObject(g30,g34)
    c: PointOnObject(g31,g34)
    c: PointOnObject(g32,g34)
    c: PointOnObject(g33,g34)
    c: PointOnObject(g34,g-1)
    c: Diameter(g34) = 7
    c: Vertical(g31)
    c: DistanceX(g34,g-1) = 8
    c: Coincident(g35,g36)
    c: Coincident(g36,g37)
    c: Coincident(g37,g38)
    c: Coincident(g38,g39)
    c: Coincident(g39,g40)
    c: Coincident(g40,g35)
    c: Equal(g35, g36-g40) x5
    c: PointOnObject(g35,g41)
    c: PointOnObject(g36,g41)
    c: PointOnObject(g37,g41)
    c: PointOnObject(g38,g41)
    c: PointOnObject(g39,g41)
    c: PointOnObject(g40,g41)
    c: Coincident(g42,g43)
    c: Coincident(g43,g44)
    c: Coincident(g44,g45)
    c: Coincident(g45,g46)
    c: Coincident(g46,g47)
    c: Coincident(g47,g42)
    c: Equal(g42, g43-g47) x5
    c: PointOnObject(g42,g48)
    c: PointOnObject(g43,g48)
    c: PointOnObject(g44,g48)
    c: PointOnObject(g45,g48)
    c: PointOnObject(g46,g48)
    c: PointOnObject(g47,g48)
    c: Equal(g41,g48)
    c: Diameter(g41) = 7
    c: Vertical(g39)
    c: Vertical(g43)
    c: Distance(g-2,g39) = 1
    c: Symmetric(g38,g43,g-2)
    c: Distance(g41,g-1) = 7
FEATURE [Part::Extrusion] Extrude660  label="hex262"
  Base = -> Sketch669
  Dir = (0,-1,2e-16)
  DirMode = 2
  FaceMakerClass = Part::FaceMakerBullseye
  FaceMakerMode = 3
  LengthFwd = 10
  LengthRev = 0
  Placement = pos=(104,0,-28) rot=(0,0,1;0rad)
  Solid = true
  Symmetric = false
FEATURE [Sketcher::SketchObject] Sketch670
  ArcFitTolerance = 1e-06
  FullyConstrained = true
  MakeInternals = false
  Placement = pos=(0,0,0) rot=(1,0,0;1.5708rad)
  sketch-geometry (49):
    g0: LineSegment StartX=1e-16 StartY=3.5 StartZ=0 EndX=-3.03109 EndY=1.75 EndZ=0
    g1: LineSegment StartX=-3.03109 StartY=1.75 StartZ=0 EndX=-3.03109 EndY=-1.75 EndZ=0
    g2: LineSegment StartX=-3.03109 StartY=-1.75 StartZ=0 EndX=-1e-16 EndY=-3.5 EndZ=0
    g3: LineSegment StartX=-1e-16 StartY=-3.5 StartZ=0 EndX=3.03109 EndY=-1.75 EndZ=0
    g4: LineSegment StartX=3.03109 StartY=-1.75 StartZ=0 EndX=3.03109 EndY=1.75 EndZ=0
    g5: LineSegment StartX=3.03109 StartY=1.75 StartZ=0 EndX=1e-16 EndY=3.5 EndZ=0
    g6: Circle [constr] CenterX=0 CenterY=0 CenterZ=0 NormalX=0 NormalY=0 NormalZ=1 AngleXU=0 Radius=3.5
    g7: LineSegment StartX=4.96892 StartY=-1.75002 StartZ=0 EndX=8.00002 EndY=-3.5 EndZ=0
    g8: LineSegment StartX=8.00002 StartY=-3.5 StartZ=0 EndX=11.0311 EndY=-1.74998 EndZ=0
    g9: LineSegment StartX=11.0311 StartY=-1.74998 StartZ=0 EndX=11.0311 EndY=1.75002 EndZ=0
    g10: LineSegment StartX=11.0311 StartY=1.75002 StartZ=0 EndX=7.99998 EndY=3.5 EndZ=0
    g11: LineSegment StartX=7.99998 StartY=3.5 StartZ=0 EndX=4.9689 EndY=1.74998 EndZ=0
    g12: LineSegment StartX=4.9689 StartY=1.74998 StartZ=0 EndX=4.96892 EndY=-1.75002 EndZ=0
    g13: Circle [constr] CenterX=8 CenterY=0 CenterZ=0 NormalX=0 NormalY=0 NormalZ=1 AngleXU=0 Radius=3.5
    g14: LineSegment StartX=4.03109 StartY=3.5 StartZ=0 EndX=7.06218 EndY=5.25 EndZ=0
    g15: LineSegment StartX=7.06218 StartY=5.25 StartZ=0 EndX=7.06218 EndY=8.75 EndZ=0
    g16: LineSegment StartX=7.06218 StartY=8.75 StartZ=0 EndX=4.03109 EndY=10.5 EndZ=0
    g17: LineSegment StartX=4.03109 StartY=10.5 StartZ=0 EndX=1 EndY=8.75 EndZ=0
    g18: LineSegment StartX=1 StartY=8.75 StartZ=0 EndX=1 EndY=5.25 EndZ=0
    g19: LineSegment StartX=1 StartY=5.25 StartZ=0 EndX=4.03109 EndY=3.5 EndZ=0
    g20: Circle [constr] CenterX=4.03109 CenterY=7 CenterZ=0 NormalX=0 NormalY=0 NormalZ=1 AngleXU=0 Radius=3.5
    g21: LineSegment StartX=-1 StartY=5.25 StartZ=0 EndX=-1 EndY=8.75 EndZ=0
    g22: LineSegment StartX=-1 StartY=8.75 StartZ=0 EndX=-4.03109 EndY=10.5 EndZ=0
    g23: LineSegment StartX=-4.03109 StartY=10.5 StartZ=0 EndX=-7.06218 EndY=8.75 EndZ=0
    g24: LineSegment StartX=-7.06218 StartY=8.75 StartZ=0 EndX=-7.06218 EndY=5.25 EndZ=0
    g25: LineSegment StartX=-7.06218 StartY=5.25 StartZ=0 EndX=-4.03109 EndY=3.5 EndZ=0
    g26: LineSegment StartX=-4.03109 StartY=3.5 StartZ=0 EndX=-1 EndY=5.25 EndZ=0
    g27: Circle [constr] CenterX=-4.03109 CenterY=7 CenterZ=0 NormalX=0 NormalY=0 NormalZ=1 AngleXU=0 Radius=3.5
    g28: LineSegment StartX=-4.96891 StartY=-1.75 StartZ=0 EndX=-4.96891 EndY=1.75 EndZ=0
    g29: LineSegment StartX=-4.96891 StartY=1.75 StartZ=0 EndX=-8 EndY=3.5 EndZ=0
    g30: LineSegment StartX=-8 StartY=3.5 StartZ=0 EndX=-11.0311 EndY=1.75 EndZ=0
    g31: LineSegment StartX=-11.0311 StartY=1.75 StartZ=0 EndX=-11.0311 EndY=-1.75 EndZ=0
    g32: LineSegment StartX=-11.0311 StartY=-1.75 StartZ=0 EndX=-8 EndY=-3.5 EndZ=0
    g33: LineSegment StartX=-8 StartY=-3.5 StartZ=0 EndX=-4.96891 EndY=-1.75 EndZ=0
    g34: Circle [constr] CenterX=-8 CenterY=0 CenterZ=0 NormalX=0 NormalY=0 NormalZ=1 AngleXU=0 Radius=3.5
    g35: LineSegment StartX=-4.03109 StartY=-3.5 StartZ=0 EndX=-7.06218 EndY=-5.25 EndZ=0
    g36: LineSegment StartX=-7.06218 StartY=-5.25 StartZ=0 EndX=-7.06218 EndY=-8.75 EndZ=0
    g37: LineSegment StartX=-7.06218 StartY=-8.75 StartZ=0 EndX=-4.03109 EndY=-10.5 EndZ=0
    g38: LineSegment StartX=-4.03109 StartY=-10.5 StartZ=0 EndX=-1 EndY=-8.75 EndZ=0
    g39: LineSegment StartX=-1 StartY=-8.75 StartZ=0 EndX=-1 EndY=-5.25 EndZ=0
    g40: LineSegment StartX=-1 StartY=-5.25 StartZ=0 EndX=-4.03109 EndY=-3.5 EndZ=0
    g41: Circle [constr] CenterX=-4.03109 CenterY=-7 CenterZ=0 NormalX=0 NormalY=0 NormalZ=1 AngleXU=0 Radius=3.5
    g42: LineSegment StartX=4.03109 StartY=-3.5 StartZ=0 EndX=1 EndY=-5.25 EndZ=0
    g43: LineSegment StartX=1 StartY=-5.25 StartZ=0 EndX=1 EndY=-8.75 EndZ=0
    g44: LineSegment StartX=1 StartY=-8.75 StartZ=0 EndX=4.03109 EndY=-10.5 EndZ=0
    g45: LineSegment StartX=4.03109 StartY=-10.5 StartZ=0 EndX=7.06218 EndY=-8.75 EndZ=0
    g46: LineSegment StartX=7.06218 StartY=-8.75 StartZ=0 EndX=7.06218 EndY=-5.25 EndZ=0
    g47: LineSegment StartX=7.06218 StartY=-5.25 StartZ=0 EndX=4.03109 EndY=-3.5 EndZ=0
    g48: Circle [constr] CenterX=4.03109 CenterY=-7 CenterZ=0 NormalX=0 NormalY=0 NormalZ=1 AngleXU=0 Radius=3.5
  constraints (117):
    c: Coincident(g0,g1)
    c: Coincident(g1,g2)
    c: Coincident(g2,g3)
    c: Coincident(g3,g4)
    c: Coincident(g4,g5)
    c: Coincident(g5,g0)
    c: Equal(g0, g1-g5) x5
    c: PointOnObject(g0,g6)
    c: PointOnObject(g1,g6)
    c: PointOnObject(g2,g6)
    c: PointOnObject(g3,g6)
    c: PointOnObject(g4,g6)
    c: PointOnObject(g5,g6)
    c: Coincident(g6,g-1)
    c: Diameter(g6) = 7
    c: PointOnObject(g0,g-2)
    c: Coincident(g7,g8)
    c: Coincident(g8,g9)
    c: Coincident(g9,g10)
    c: Coincident(g10,g11)
    c: Coincident(g11,g12)
    c: Coincident(g12,g7)
    c: Equal(g7, g8-g12) x5
    c: PointOnObject(g7,g13)
    c: PointOnObject(g8,g13)
    c: PointOnObject(g9,g13)
    c: PointOnObject(g10,g13)
    c: PointOnObject(g11,g13)
    c: PointOnObject(g12,g13)
    c: PointOnObject(g13,g-1)
    c: Diameter(g13) = 7
    c: Distance(g6,g13) = 8
    c: Horizontal(g0,g10)
    c: Coincident(g14,g15)
    c: Coincident(g15,g16)
    c: Coincident(g16,g17)
    c: Coincident(g17,g18)
    c: Coincident(g18,g19)
    c: Coincident(g19,g14)
    c: Equal(g14, g15-g19) x5
    c: PointOnObject(g14,g20)
    c: PointOnObject(g15,g20)
    c: PointOnObject(g16,g20)
    c: PointOnObject(g17,g20)
    c: PointOnObject(g18,g20)
    c: PointOnObject(g19,g20)
    c: Diameter(g20) = 7
    c: DistanceY(g-1,g20) = 7
    c: Vertical(g18)
    c: Distance(g17,g-2) = 1
    c: Coincident(g21,g22)
    c: Coincident(g22,g23)
    c: Coincident(g23,g24)
    c: Coincident(g24,g25)
    c: Coincident(g25,g26)
    c: Coincident(g26,g21)
    c: Equal(g21, g22-g26) x5
    c: PointOnObject(g21,g27)
    c: PointOnObject(g22,g27)
    c: PointOnObject(g23,g27)
    c: PointOnObject(g24,g27)
    c: PointOnObject(g25,g27)
    c: PointOnObject(g26,g27)
    c: Diameter(g27) = 7
    c: DistanceY(g-1,g27) = 7
    c: DistanceX(g21,g-1) = 1
    c: Vertical(g21)
    c: Coincident(g28,g29)
    c: Coincident(g29,g30)
    c: Coincident(g30,g31)
    c: Coincident(g31,g32)
    c: Coincident(g32,g33)
    c: Coincident(g33,g28)
    c: Equal(g28, g29-g33) x5
    c: PointOnObject(g28,g34)
    c: PointOnObject(g29,g34)
    c: PointOnObject(g30,g34)
    c: PointOnObject(g31,g34)
    c: PointOnObject(g32,g34)
    c: PointOnObject(g33,g34)
    c: PointOnObject(g34,g-1)
    c: Diameter(g34) = 7
    c: Vertical(g31)
    c: DistanceX(g34,g-1) = 8
    c: Coincident(g35,g36)
    c: Coincident(g36,g37)
    c: Coincident(g37,g38)
    c: Coincident(g38,g39)
    c: Coincident(g39,g40)
    c: Coincident(g40,g35)
    c: Equal(g35, g36-g40) x5
    c: PointOnObject(g35,g41)
    c: PointOnObject(g36,g41)
    c: PointOnObject(g37,g41)
    c: PointOnObject(g38,g41)
    c: PointOnObject(g39,g41)
    c: PointOnObject(g40,g41)
    c: Coincident(g42,g43)
    c: Coincident(g43,g44)
    c: Coincident(g44,g45)
    c: Coincident(g45,g46)
    c: Coincident(g46,g47)
    c: Coincident(g47,g42)
    c: Equal(g42, g43-g47) x5
    c: PointOnObject(g42,g48)
    c: PointOnObject(g43,g48)
    c: PointOnObject(g44,g48)
    c: PointOnObject(g45,g48)
    c: PointOnObject(g46,g48)
    c: PointOnObject(g47,g48)
    c: Equal(g41,g48)
    c: Diameter(g41) = 7
    c: Vertical(g39)
    c: Vertical(g43)
    c: Distance(g-2,g39) = 1
    c: Symmetric(g38,g43,g-2)
    c: Distance(g41,g-1) = 7
FEATURE [Part::Extrusion] Extrude661  label="hex263"
  Base = -> Sketch670
  Dir = (0,-1,2e-16)
  DirMode = 2
  FaceMakerClass = Part::FaceMakerBullseye
  FaceMakerMode = 3
  LengthFwd = 10
  LengthRev = 0
  Placement = pos=(-96,0,-14) rot=(0,0,1;0rad)
  Solid = true
  Symmetric = false
FEATURE [Sketcher::SketchObject] Sketch671
  ArcFitTolerance = 1e-06
  FullyConstrained = true
  MakeInternals = false
  Placement = pos=(0,0,0) rot=(1,0,0;1.5708rad)
  sketch-geometry (49):
    g0: LineSegment StartX=1e-16 StartY=3.5 StartZ=0 EndX=-3.03109 EndY=1.75 EndZ=0
    g1: LineSegment StartX=-3.03109 StartY=1.75 StartZ=0 EndX=-3.03109 EndY=-1.75 EndZ=0
    g2: LineSegment StartX=-3.03109 StartY=-1.75 StartZ=0 EndX=-1e-16 EndY=-3.5 EndZ=0
    g3: LineSegment StartX=-1e-16 StartY=-3.5 StartZ=0 EndX=3.03109 EndY=-1.75 EndZ=0
    g4: LineSegment StartX=3.03109 StartY=-1.75 StartZ=0 EndX=3.03109 EndY=1.75 EndZ=0
    g5: LineSegment StartX=3.03109 StartY=1.75 StartZ=0 EndX=1e-16 EndY=3.5 EndZ=0
    g6: Circle [constr] CenterX=0 CenterY=0 CenterZ=0 NormalX=0 NormalY=0 NormalZ=1 AngleXU=0 Radius=3.5
    g7: LineSegment StartX=4.96892 StartY=-1.75002 StartZ=0 EndX=8.00002 EndY=-3.5 EndZ=0
    g8: LineSegment StartX=8.00002 StartY=-3.5 StartZ=0 EndX=11.0311 EndY=-1.74998 EndZ=0
    g9: LineSegment StartX=11.0311 StartY=-1.74998 StartZ=0 EndX=11.0311 EndY=1.75002 EndZ=0
    g10: LineSegment StartX=11.0311 StartY=1.75002 StartZ=0 EndX=7.99998 EndY=3.5 EndZ=0
    g11: LineSegment StartX=7.99998 StartY=3.5 StartZ=0 EndX=4.9689 EndY=1.74998 EndZ=0
    g12: LineSegment StartX=4.9689 StartY=1.74998 StartZ=0 EndX=4.96892 EndY=-1.75002 EndZ=0
    g13: Circle [constr] CenterX=8 CenterY=0 CenterZ=0 NormalX=0 NormalY=0 NormalZ=1 AngleXU=0 Radius=3.5
    g14: LineSegment StartX=4.03109 StartY=3.5 StartZ=0 EndX=7.06218 EndY=5.25 EndZ=0
    g15: LineSegment StartX=7.06218 StartY=5.25 StartZ=0 EndX=7.06218 EndY=8.75 EndZ=0
    g16: LineSegment StartX=7.06218 StartY=8.75 StartZ=0 EndX=4.03109 EndY=10.5 EndZ=0
    g17: LineSegment StartX=4.03109 StartY=10.5 StartZ=0 EndX=1 EndY=8.75 EndZ=0
    g18: LineSegment StartX=1 StartY=8.75 StartZ=0 EndX=1 EndY=5.25 EndZ=0
    g19: LineSegment StartX=1 StartY=5.25 StartZ=0 EndX=4.03109 EndY=3.5 EndZ=0
    g20: Circle [constr] CenterX=4.03109 CenterY=7 CenterZ=0 NormalX=0 NormalY=0 NormalZ=1 AngleXU=0 Radius=3.5
    g21: LineSegment StartX=-1 StartY=5.25 StartZ=0 EndX=-1 EndY=8.75 EndZ=0
    g22: LineSegment StartX=-1 StartY=8.75 StartZ=0 EndX=-4.03109 EndY=10.5 EndZ=0
    g23: LineSegment StartX=-4.03109 StartY=10.5 StartZ=0 EndX=-7.06218 EndY=8.75 EndZ=0
    g24: LineSegment StartX=-7.06218 StartY=8.75 StartZ=0 EndX=-7.06218 EndY=5.25 EndZ=0
    g25: LineSegment StartX=-7.06218 StartY=5.25 StartZ=0 EndX=-4.03109 EndY=3.5 EndZ=0
    g26: LineSegment StartX=-4.03109 StartY=3.5 StartZ=0 EndX=-1 EndY=5.25 EndZ=0
    g27: Circle [constr] CenterX=-4.03109 CenterY=7 CenterZ=0 NormalX=0 NormalY=0 NormalZ=1 AngleXU=0 Radius=3.5
    g28: LineSegment StartX=-4.96891 StartY=-1.75 StartZ=0 EndX=-4.96891 EndY=1.75 EndZ=0
    g29: LineSegment StartX=-4.96891 StartY=1.75 StartZ=0 EndX=-8 EndY=3.5 EndZ=0
    g30: LineSegment StartX=-8 StartY=3.5 StartZ=0 EndX=-11.0311 EndY=1.75 EndZ=0
    g31: LineSegment StartX=-11.0311 StartY=1.75 StartZ=0 EndX=-11.0311 EndY=-1.75 EndZ=0
    g32: LineSegment StartX=-11.0311 StartY=-1.75 StartZ=0 EndX=-8 EndY=-3.5 EndZ=0
    g33: LineSegment StartX=-8 StartY=-3.5 StartZ=0 EndX=-4.96891 EndY=-1.75 EndZ=0
    g34: Circle [constr] CenterX=-8 CenterY=0 CenterZ=0 NormalX=0 NormalY=0 NormalZ=1 AngleXU=0 Radius=3.5
    g35: LineSegment StartX=-4.03109 StartY=-3.5 StartZ=0 EndX=-7.06218 EndY=-5.25 EndZ=0
    g36: LineSegment StartX=-7.06218 StartY=-5.25 StartZ=0 EndX=-7.06218 EndY=-8.75 EndZ=0
    g37: LineSegment StartX=-7.06218 StartY=-8.75 StartZ=0 EndX=-4.03109 EndY=-10.5 EndZ=0
    g38: LineSegment StartX=-4.03109 StartY=-10.5 StartZ=0 EndX=-1 EndY=-8.75 EndZ=0
    g39: LineSegment StartX=-1 StartY=-8.75 StartZ=0 EndX=-1 EndY=-5.25 EndZ=0
    g40: LineSegment StartX=-1 StartY=-5.25 StartZ=0 EndX=-4.03109 EndY=-3.5 EndZ=0
    g41: Circle [constr] CenterX=-4.03109 CenterY=-7 CenterZ=0 NormalX=0 NormalY=0 NormalZ=1 AngleXU=0 Radius=3.5
    g42: LineSegment StartX=4.03109 StartY=-3.5 StartZ=0 EndX=1 EndY=-5.25 EndZ=0
    g43: LineSegment StartX=1 StartY=-5.25 StartZ=0 EndX=1 EndY=-8.75 EndZ=0
    g44: LineSegment StartX=1 StartY=-8.75 StartZ=0 EndX=4.03109 EndY=-10.5 EndZ=0
    g45: LineSegment StartX=4.03109 StartY=-10.5 StartZ=0 EndX=7.06218 EndY=-8.75 EndZ=0
    g46: LineSegment StartX=7.06218 StartY=-8.75 StartZ=0 EndX=7.06218 EndY=-5.25 EndZ=0
    g47: LineSegment StartX=7.06218 StartY=-5.25 StartZ=0 EndX=4.03109 EndY=-3.5 EndZ=0
    g48: Circle [constr] CenterX=4.03109 CenterY=-7 CenterZ=0 NormalX=0 NormalY=0 NormalZ=1 AngleXU=0 Radius=3.5
  constraints (117):
    c: Coincident(g0,g1)
    c: Coincident(g1,g2)
    c: Coincident(g2,g3)
    c: Coincident(g3,g4)
    c: Coincident(g4,g5)
    c: Coincident(g5,g0)
    c: Equal(g0, g1-g5) x5
    c: PointOnObject(g0,g6)
    c: PointOnObject(g1,g6)
    c: PointOnObject(g2,g6)
    c: PointOnObject(g3,g6)
    c: PointOnObject(g4,g6)
    c: PointOnObject(g5,g6)
    c: Coincident(g6,g-1)
    c: Diameter(g6) = 7
    c: PointOnObject(g0,g-2)
    c: Coincident(g7,g8)
    c: Coincident(g8,g9)
    c: Coincident(g9,g10)
    c: Coincident(g10,g11)
    c: Coincident(g11,g12)
    c: Coincident(g12,g7)
    c: Equal(g7, g8-g12) x5
    c: PointOnObject(g7,g13)
    c: PointOnObject(g8,g13)
    c: PointOnObject(g9,g13)
    c: PointOnObject(g10,g13)
    c: PointOnObject(g11,g13)
    c: PointOnObject(g12,g13)
    c: PointOnObject(g13,g-1)
    c: Diameter(g13) = 7
    c: Distance(g6,g13) = 8
    c: Horizontal(g0,g10)
    c: Coincident(g14,g15)
    c: Coincident(g15,g16)
    c: Coincident(g16,g17)
    c: Coincident(g17,g18)
    c: Coincident(g18,g19)
    c: Coincident(g19,g14)
    c: Equal(g14, g15-g19) x5
    c: PointOnObject(g14,g20)
    c: PointOnObject(g15,g20)
    c: PointOnObject(g16,g20)
    c: PointOnObject(g17,g20)
    c: PointOnObject(g18,g20)
    c: PointOnObject(g19,g20)
    c: Diameter(g20) = 7
    c: DistanceY(g-1,g20) = 7
    c: Vertical(g18)
    c: Distance(g17,g-2) = 1
    c: Coincident(g21,g22)
    c: Coincident(g22,g23)
    c: Coincident(g23,g24)
    c: Coincident(g24,g25)
    c: Coincident(g25,g26)
    c: Coincident(g26,g21)
    c: Equal(g21, g22-g26) x5
    c: PointOnObject(g21,g27)
    c: PointOnObject(g22,g27)
    c: PointOnObject(g23,g27)
    c: PointOnObject(g24,g27)
    c: PointOnObject(g25,g27)
    c: PointOnObject(g26,g27)
    c: Diameter(g27) = 7
    c: DistanceY(g-1,g27) = 7
    c: DistanceX(g21,g-1) = 1
    c: Vertical(g21)
    c: Coincident(g28,g29)
    c: Coincident(g29,g30)
    c: Coincident(g30,g31)
    c: Coincident(g31,g32)
    c: Coincident(g32,g33)
    c: Coincident(g33,g28)
    c: Equal(g28, g29-g33) x5
    c: PointOnObject(g28,g34)
    c: PointOnObject(g29,g34)
    c: PointOnObject(g30,g34)
    c: PointOnObject(g31,g34)
    c: PointOnObject(g32,g34)
    c: PointOnObject(g33,g34)
    c: PointOnObject(g34,g-1)
    c: Diameter(g34) = 7
    c: Vertical(g31)
    c: DistanceX(g34,g-1) = 8
    c: Coincident(g35,g36)
    c: Coincident(g36,g37)
    c: Coincident(g37,g38)
    c: Coincident(g38,g39)
    c: Coincident(g39,g40)
    c: Coincident(g40,g35)
    c: Equal(g35, g36-g40) x5
    c: PointOnObject(g35,g41)
    c: PointOnObject(g36,g41)
    c: PointOnObject(g37,g41)
    c: PointOnObject(g38,g41)
    c: PointOnObject(g39,g41)
    c: PointOnObject(g40,g41)
    c: Coincident(g42,g43)
    c: Coincident(g43,g44)
    c: Coincident(g44,g45)
    c: Coincident(g45,g46)
    c: Coincident(g46,g47)
    c: Coincident(g47,g42)
    c: Equal(g42, g43-g47) x5
    c: PointOnObject(g42,g48)
    c: PointOnObject(g43,g48)
    c: PointOnObject(g44,g48)
    c: PointOnObject(g45,g48)
    c: PointOnObject(g46,g48)
    c: PointOnObject(g47,g48)
    c: Equal(g41,g48)
    c: Diameter(g41) = 7
    c: Vertical(g39)
    c: Vertical(g43)
    c: Distance(g-2,g39) = 1
    c: Symmetric(g38,g43,g-2)
    c: Distance(g41,g-1) = 7
FEATURE [Part::Extrusion] Extrude662  label="hex264"
  Base = -> Sketch671
  Dir = (0,-1,2e-16)
  DirMode = 2
  FaceMakerClass = Part::FaceMakerBullseye
  FaceMakerMode = 3
  LengthFwd = 10
  LengthRev = 0
  Placement = pos=(-68,0,-35) rot=(0,0,1;0rad)
  Solid = true
  Symmetric = false
FEATURE [Sketcher::SketchObject] Sketch672
  ArcFitTolerance = 1e-06
  FullyConstrained = true
  MakeInternals = false
  Placement = pos=(0,0,0) rot=(1,0,0;1.5708rad)
  sketch-geometry (49):
    g0: LineSegment StartX=1e-16 StartY=3.5 StartZ=0 EndX=-3.03109 EndY=1.75 EndZ=0
    g1: LineSegment StartX=-3.03109 StartY=1.75 StartZ=0 EndX=-3.03109 EndY=-1.75 EndZ=0
    g2: LineSegment StartX=-3.03109 StartY=-1.75 StartZ=0 EndX=-1e-16 EndY=-3.5 EndZ=0
    g3: LineSegment StartX=-1e-16 StartY=-3.5 StartZ=0 EndX=3.03109 EndY=-1.75 EndZ=0
    g4: LineSegment StartX=3.03109 StartY=-1.75 StartZ=0 EndX=3.03109 EndY=1.75 EndZ=0
    g5: LineSegment StartX=3.03109 StartY=1.75 StartZ=0 EndX=1e-16 EndY=3.5 EndZ=0
    g6: Circle [constr] CenterX=0 CenterY=0 CenterZ=0 NormalX=0 NormalY=0 NormalZ=1 AngleXU=0 Radius=3.5
    g7: LineSegment StartX=4.96892 StartY=-1.75002 StartZ=0 EndX=8.00002 EndY=-3.5 EndZ=0
    g8: LineSegment StartX=8.00002 StartY=-3.5 StartZ=0 EndX=11.0311 EndY=-1.74998 EndZ=0
    g9: LineSegment StartX=11.0311 StartY=-1.74998 StartZ=0 EndX=11.0311 EndY=1.75002 EndZ=0
    g10: LineSegment StartX=11.0311 StartY=1.75002 StartZ=0 EndX=7.99998 EndY=3.5 EndZ=0
    g11: LineSegment StartX=7.99998 StartY=3.5 StartZ=0 EndX=4.9689 EndY=1.74998 EndZ=0
    g12: LineSegment StartX=4.9689 StartY=1.74998 StartZ=0 EndX=4.96892 EndY=-1.75002 EndZ=0
    g13: Circle [constr] CenterX=8 CenterY=0 CenterZ=0 NormalX=0 NormalY=0 NormalZ=1 AngleXU=0 Radius=3.5
    g14: LineSegment StartX=4.03109 StartY=3.5 StartZ=0 EndX=7.06218 EndY=5.25 EndZ=0
    g15: LineSegment StartX=7.06218 StartY=5.25 StartZ=0 EndX=7.06218 EndY=8.75 EndZ=0
    g16: LineSegment StartX=7.06218 StartY=8.75 StartZ=0 EndX=4.03109 EndY=10.5 EndZ=0
    g17: LineSegment StartX=4.03109 StartY=10.5 StartZ=0 EndX=1 EndY=8.75 EndZ=0
    g18: LineSegment StartX=1 StartY=8.75 StartZ=0 EndX=1 EndY=5.25 EndZ=0
    g19: LineSegment StartX=1 StartY=5.25 StartZ=0 EndX=4.03109 EndY=3.5 EndZ=0
    g20: Circle [constr] CenterX=4.03109 CenterY=7 CenterZ=0 NormalX=0 NormalY=0 NormalZ=1 AngleXU=0 Radius=3.5
    g21: LineSegment StartX=-1 StartY=5.25 StartZ=0 EndX=-1 EndY=8.75 EndZ=0
    g22: LineSegment StartX=-1 StartY=8.75 StartZ=0 EndX=-4.03109 EndY=10.5 EndZ=0
    g23: LineSegment StartX=-4.03109 StartY=10.5 StartZ=0 EndX=-7.06218 EndY=8.75 EndZ=0
    g24: LineSegment StartX=-7.06218 StartY=8.75 StartZ=0 EndX=-7.06218 EndY=5.25 EndZ=0
    g25: LineSegment StartX=-7.06218 StartY=5.25 StartZ=0 EndX=-4.03109 EndY=3.5 EndZ=0
    g26: LineSegment StartX=-4.03109 StartY=3.5 StartZ=0 EndX=-1 EndY=5.25 EndZ=0
    g27: Circle [constr] CenterX=-4.03109 CenterY=7 CenterZ=0 NormalX=0 NormalY=0 NormalZ=1 AngleXU=0 Radius=3.5
    g28: LineSegment StartX=-4.96891 StartY=-1.75 StartZ=0 EndX=-4.96891 EndY=1.75 EndZ=0
    g29: LineSegment StartX=-4.96891 StartY=1.75 StartZ=0 EndX=-8 EndY=3.5 EndZ=0
    g30: LineSegment StartX=-8 StartY=3.5 StartZ=0 EndX=-11.0311 EndY=1.75 EndZ=0
    g31: LineSegment StartX=-11.0311 StartY=1.75 StartZ=0 EndX=-11.0311 EndY=-1.75 EndZ=0
    g32: LineSegment StartX=-11.0311 StartY=-1.75 StartZ=0 EndX=-8 EndY=-3.5 EndZ=0
    g33: LineSegment StartX=-8 StartY=-3.5 StartZ=0 EndX=-4.96891 EndY=-1.75 EndZ=0
    g34: Circle [constr] CenterX=-8 CenterY=0 CenterZ=0 NormalX=0 NormalY=0 NormalZ=1 AngleXU=0 Radius=3.5
    g35: LineSegment StartX=-4.03109 StartY=-3.5 StartZ=0 EndX=-7.06218 EndY=-5.25 EndZ=0
    g36: LineSegment StartX=-7.06218 StartY=-5.25 StartZ=0 EndX=-7.06218 EndY=-8.75 EndZ=0
    g37: LineSegment StartX=-7.06218 StartY=-8.75 StartZ=0 EndX=-4.03109 EndY=-10.5 EndZ=0
    g38: LineSegment StartX=-4.03109 StartY=-10.5 StartZ=0 EndX=-1 EndY=-8.75 EndZ=0
    g39: LineSegment StartX=-1 StartY=-8.75 StartZ=0 EndX=-1 EndY=-5.25 EndZ=0
    g40: LineSegment StartX=-1 StartY=-5.25 StartZ=0 EndX=-4.03109 EndY=-3.5 EndZ=0
    g41: Circle [constr] CenterX=-4.03109 CenterY=-7 CenterZ=0 NormalX=0 NormalY=0 NormalZ=1 AngleXU=0 Radius=3.5
    g42: LineSegment StartX=4.03109 StartY=-3.5 StartZ=0 EndX=1 EndY=-5.25 EndZ=0
    g43: LineSegment StartX=1 StartY=-5.25 StartZ=0 EndX=1 EndY=-8.75 EndZ=0
    g44: LineSegment StartX=1 StartY=-8.75 StartZ=0 EndX=4.03109 EndY=-10.5 EndZ=0
    g45: LineSegment StartX=4.03109 StartY=-10.5 StartZ=0 EndX=7.06218 EndY=-8.75 EndZ=0
    g46: LineSegment StartX=7.06218 StartY=-8.75 StartZ=0 EndX=7.06218 EndY=-5.25 EndZ=0
    g47: LineSegment StartX=7.06218 StartY=-5.25 StartZ=0 EndX=4.03109 EndY=-3.5 EndZ=0
    g48: Circle [constr] CenterX=4.03109 CenterY=-7 CenterZ=0 NormalX=0 NormalY=0 NormalZ=1 AngleXU=0 Radius=3.5
  constraints (117):
    c: Coincident(g0,g1)
    c: Coincident(g1,g2)
    c: Coincident(g2,g3)
    c: Coincident(g3,g4)
    c: Coincident(g4,g5)
    c: Coincident(g5,g0)
    c: Equal(g0, g1-g5) x5
    c: PointOnObject(g0,g6)
    c: PointOnObject(g1,g6)
    c: PointOnObject(g2,g6)
    c: PointOnObject(g3,g6)
    c: PointOnObject(g4,g6)
    c: PointOnObject(g5,g6)
    c: Coincident(g6,g-1)
    c: Diameter(g6) = 7
    c: PointOnObject(g0,g-2)
    c: Coincident(g7,g8)
    c: Coincident(g8,g9)
    c: Coincident(g9,g10)
    c: Coincident(g10,g11)
    c: Coincident(g11,g12)
    c: Coincident(g12,g7)
    c: Equal(g7, g8-g12) x5
    c: PointOnObject(g7,g13)
    c: PointOnObject(g8,g13)
    c: PointOnObject(g9,g13)
    c: PointOnObject(g10,g13)
    c: PointOnObject(g11,g13)
    c: PointOnObject(g12,g13)
    c: PointOnObject(g13,g-1)
    c: Diameter(g13) = 7
    c: Distance(g6,g13) = 8
    c: Horizontal(g0,g10)
    c: Coincident(g14,g15)
    c: Coincident(g15,g16)
    c: Coincident(g16,g17)
    c: Coincident(g17,g18)
    c: Coincident(g18,g19)
    c: Coincident(g19,g14)
    c: Equal(g14, g15-g19) x5
    c: PointOnObject(g14,g20)
    c: PointOnObject(g15,g20)
    c: PointOnObject(g16,g20)
    c: PointOnObject(g17,g20)
    c: PointOnObject(g18,g20)
    c: PointOnObject(g19,g20)
    c: Diameter(g20) = 7
    c: DistanceY(g-1,g20) = 7
    c: Vertical(g18)
    c: Distance(g17,g-2) = 1
    c: Coincident(g21,g22)
    c: Coincident(g22,g23)
    c: Coincident(g23,g24)
    c: Coincident(g24,g25)
    c: Coincident(g25,g26)
    c: Coincident(g26,g21)
    c: Equal(g21, g22-g26) x5
    c: PointOnObject(g21,g27)
    c: PointOnObject(g22,g27)
    c: PointOnObject(g23,g27)
    c: PointOnObject(g24,g27)
    c: PointOnObject(g25,g27)
    c: PointOnObject(g26,g27)
    c: Diameter(g27) = 7
    c: DistanceY(g-1,g27) = 7
    c: DistanceX(g21,g-1) = 1
    c: Vertical(g21)
    c: Coincident(g28,g29)
    c: Coincident(g29,g30)
    c: Coincident(g30,g31)
    c: Coincident(g31,g32)
    c: Coincident(g32,g33)
    c: Coincident(g33,g28)
    c: Equal(g28, g29-g33) x5
    c: PointOnObject(g28,g34)
    c: PointOnObject(g29,g34)
    c: PointOnObject(g30,g34)
    c: PointOnObject(g31,g34)
    c: PointOnObject(g32,g34)
    c: PointOnObject(g33,g34)
    c: PointOnObject(g34,g-1)
    c: Diameter(g34) = 7
    c: Vertical(g31)
    c: DistanceX(g34,g-1) = 8
    c: Coincident(g35,g36)
    c: Coincident(g36,g37)
    c: Coincident(g37,g38)
    c: Coincident(g38,g39)
    c: Coincident(g39,g40)
    c: Coincident(g40,g35)
    c: Equal(g35, g36-g40) x5
    c: PointOnObject(g35,g41)
    c: PointOnObject(g36,g41)
    c: PointOnObject(g37,g41)
    c: PointOnObject(g38,g41)
    c: PointOnObject(g39,g41)
    c: PointOnObject(g40,g41)
    c: Coincident(g42,g43)
    c: Coincident(g43,g44)
    c: Coincident(g44,g45)
    c: Coincident(g45,g46)
    c: Coincident(g46,g47)
    c: Coincident(g47,g42)
    c: Equal(g42, g43-g47) x5
    c: PointOnObject(g42,g48)
    c: PointOnObject(g43,g48)
    c: PointOnObject(g44,g48)
    c: PointOnObject(g45,g48)
    c: PointOnObject(g46,g48)
    c: PointOnObject(g47,g48)
    c: Equal(g41,g48)
    c: Diameter(g41) = 7
    c: Vertical(g39)
    c: Vertical(g43)
    c: Distance(g-2,g39) = 1
    c: Symmetric(g38,g43,g-2)
    c: Distance(g41,g-1) = 7
FEATURE [Part::Extrusion] Extrude663  label="hex265"
  Base = -> Sketch672
  Dir = (0,-1,2e-16)
  DirMode = 2
  FaceMakerClass = Part::FaceMakerBullseye
  FaceMakerMode = 3
  LengthFwd = 10
  LengthRev = 0
  Placement = pos=(-84,0,-21) rot=(0,0,1;0rad)
  Solid = true
  Symmetric = false
FEATURE [Sketcher::SketchObject] Sketch673
  ArcFitTolerance = 1e-06
  FullyConstrained = true
  MakeInternals = false
  Placement = pos=(0,0,0) rot=(1,0,0;1.5708rad)
  sketch-geometry (49):
    g0: LineSegment StartX=1e-16 StartY=3.5 StartZ=0 EndX=-3.03109 EndY=1.75 EndZ=0
    g1: LineSegment StartX=-3.03109 StartY=1.75 StartZ=0 EndX=-3.03109 EndY=-1.75 EndZ=0
    g2: LineSegment StartX=-3.03109 StartY=-1.75 StartZ=0 EndX=-1e-16 EndY=-3.5 EndZ=0
    g3: LineSegment StartX=-1e-16 StartY=-3.5 StartZ=0 EndX=3.03109 EndY=-1.75 EndZ=0
    g4: LineSegment StartX=3.03109 StartY=-1.75 StartZ=0 EndX=3.03109 EndY=1.75 EndZ=0
    g5: LineSegment StartX=3.03109 StartY=1.75 StartZ=0 EndX=1e-16 EndY=3.5 EndZ=0
    g6: Circle [constr] CenterX=0 CenterY=0 CenterZ=0 NormalX=0 NormalY=0 NormalZ=1 AngleXU=0 Radius=3.5
    g7: LineSegment StartX=4.96892 StartY=-1.75002 StartZ=0 EndX=8.00002 EndY=-3.5 EndZ=0
    g8: LineSegment StartX=8.00002 StartY=-3.5 StartZ=0 EndX=11.0311 EndY=-1.74998 EndZ=0
    g9: LineSegment StartX=11.0311 StartY=-1.74998 StartZ=0 EndX=11.0311 EndY=1.75002 EndZ=0
    g10: LineSegment StartX=11.0311 StartY=1.75002 StartZ=0 EndX=7.99998 EndY=3.5 EndZ=0
    g11: LineSegment StartX=7.99998 StartY=3.5 StartZ=0 EndX=4.9689 EndY=1.74998 EndZ=0
    g12: LineSegment StartX=4.9689 StartY=1.74998 StartZ=0 EndX=4.96892 EndY=-1.75002 EndZ=0
    g13: Circle [constr] CenterX=8 CenterY=0 CenterZ=0 NormalX=0 NormalY=0 NormalZ=1 AngleXU=0 Radius=3.5
    g14: LineSegment StartX=4.03109 StartY=3.5 StartZ=0 EndX=7.06218 EndY=5.25 EndZ=0
    g15: LineSegment StartX=7.06218 StartY=5.25 StartZ=0 EndX=7.06218 EndY=8.75 EndZ=0
    g16: LineSegment StartX=7.06218 StartY=8.75 StartZ=0 EndX=4.03109 EndY=10.5 EndZ=0
    g17: LineSegment StartX=4.03109 StartY=10.5 StartZ=0 EndX=1 EndY=8.75 EndZ=0
    g18: LineSegment StartX=1 StartY=8.75 StartZ=0 EndX=1 EndY=5.25 EndZ=0
    g19: LineSegment StartX=1 StartY=5.25 StartZ=0 EndX=4.03109 EndY=3.5 EndZ=0
    g20: Circle [constr] CenterX=4.03109 CenterY=7 CenterZ=0 NormalX=0 NormalY=0 NormalZ=1 AngleXU=0 Radius=3.5
    g21: LineSegment StartX=-1 StartY=5.25 StartZ=0 EndX=-1 EndY=8.75 EndZ=0
    g22: LineSegment StartX=-1 StartY=8.75 StartZ=0 EndX=-4.03109 EndY=10.5 EndZ=0
    g23: LineSegment StartX=-4.03109 StartY=10.5 StartZ=0 EndX=-7.06218 EndY=8.75 EndZ=0
    g24: LineSegment StartX=-7.06218 StartY=8.75 StartZ=0 EndX=-7.06218 EndY=5.25 EndZ=0
    g25: LineSegment StartX=-7.06218 StartY=5.25 StartZ=0 EndX=-4.03109 EndY=3.5 EndZ=0
    g26: LineSegment StartX=-4.03109 StartY=3.5 StartZ=0 EndX=-1 EndY=5.25 EndZ=0
    g27: Circle [constr] CenterX=-4.03109 CenterY=7 CenterZ=0 NormalX=0 NormalY=0 NormalZ=1 AngleXU=0 Radius=3.5
    g28: LineSegment StartX=-4.96891 StartY=-1.75 StartZ=0 EndX=-4.96891 EndY=1.75 EndZ=0
    g29: LineSegment StartX=-4.96891 StartY=1.75 StartZ=0 EndX=-8 EndY=3.5 EndZ=0
    g30: LineSegment StartX=-8 StartY=3.5 StartZ=0 EndX=-11.0311 EndY=1.75 EndZ=0
    g31: LineSegment StartX=-11.0311 StartY=1.75 StartZ=0 EndX=-11.0311 EndY=-1.75 EndZ=0
    g32: LineSegment StartX=-11.0311 StartY=-1.75 StartZ=0 EndX=-8 EndY=-3.5 EndZ=0
    g33: LineSegment StartX=-8 StartY=-3.5 StartZ=0 EndX=-4.96891 EndY=-1.75 EndZ=0
    g34: Circle [constr] CenterX=-8 CenterY=0 CenterZ=0 NormalX=0 NormalY=0 NormalZ=1 AngleXU=0 Radius=3.5
    g35: LineSegment StartX=-4.03109 StartY=-3.5 StartZ=0 EndX=-7.06218 EndY=-5.25 EndZ=0
    g36: LineSegment StartX=-7.06218 StartY=-5.25 StartZ=0 EndX=-7.06218 EndY=-8.75 EndZ=0
    g37: LineSegment StartX=-7.06218 StartY=-8.75 StartZ=0 EndX=-4.03109 EndY=-10.5 EndZ=0
    g38: LineSegment StartX=-4.03109 StartY=-10.5 StartZ=0 EndX=-1 EndY=-8.75 EndZ=0
    g39: LineSegment StartX=-1 StartY=-8.75 StartZ=0 EndX=-1 EndY=-5.25 EndZ=0
    g40: LineSegment StartX=-1 StartY=-5.25 StartZ=0 EndX=-4.03109 EndY=-3.5 EndZ=0
    g41: Circle [constr] CenterX=-4.03109 CenterY=-7 CenterZ=0 NormalX=0 NormalY=0 NormalZ=1 AngleXU=0 Radius=3.5
    g42: LineSegment StartX=4.03109 StartY=-3.5 StartZ=0 EndX=1 EndY=-5.25 EndZ=0
    g43: LineSegment StartX=1 StartY=-5.25 StartZ=0 EndX=1 EndY=-8.75 EndZ=0
    g44: LineSegment StartX=1 StartY=-8.75 StartZ=0 EndX=4.03109 EndY=-10.5 EndZ=0
    g45: LineSegment StartX=4.03109 StartY=-10.5 StartZ=0 EndX=7.06218 EndY=-8.75 EndZ=0
    g46: LineSegment StartX=7.06218 StartY=-8.75 StartZ=0 EndX=7.06218 EndY=-5.25 EndZ=0
    g47: LineSegment StartX=7.06218 StartY=-5.25 StartZ=0 EndX=4.03109 EndY=-3.5 EndZ=0
    g48: Circle [constr] CenterX=4.03109 CenterY=-7 CenterZ=0 NormalX=0 NormalY=0 NormalZ=1 AngleXU=0 Radius=3.5
  constraints (117):
    c: Coincident(g0,g1)
    c: Coincident(g1,g2)
    c: Coincident(g2,g3)
    c: Coincident(g3,g4)
    c: Coincident(g4,g5)
    c: Coincident(g5,g0)
    c: Equal(g0, g1-g5) x5
    c: PointOnObject(g0,g6)
    c: PointOnObject(g1,g6)
    c: PointOnObject(g2,g6)
    c: PointOnObject(g3,g6)
    c: PointOnObject(g4,g6)
    c: PointOnObject(g5,g6)
    c: Coincident(g6,g-1)
    c: Diameter(g6) = 7
    c: PointOnObject(g0,g-2)
    c: Coincident(g7,g8)
    c: Coincident(g8,g9)
    c: Coincident(g9,g10)
    c: Coincident(g10,g11)
    c: Coincident(g11,g12)
    c: Coincident(g12,g7)
    c: Equal(g7, g8-g12) x5
    c: PointOnObject(g7,g13)
    c: PointOnObject(g8,g13)
    c: PointOnObject(g9,g13)
    c: PointOnObject(g10,g13)
    c: PointOnObject(g11,g13)
    c: PointOnObject(g12,g13)
    c: PointOnObject(g13,g-1)
    c: Diameter(g13) = 7
    c: Distance(g6,g13) = 8
    c: Horizontal(g0,g10)
    c: Coincident(g14,g15)
    c: Coincident(g15,g16)
    c: Coincident(g16,g17)
    c: Coincident(g17,g18)
    c: Coincident(g18,g19)
    c: Coincident(g19,g14)
    c: Equal(g14, g15-g19) x5
    c: PointOnObject(g14,g20)
    c: PointOnObject(g15,g20)
    c: PointOnObject(g16,g20)
    c: PointOnObject(g17,g20)
    c: PointOnObject(g18,g20)
    c: PointOnObject(g19,g20)
    c: Diameter(g20) = 7
    c: DistanceY(g-1,g20) = 7
    c: Vertical(g18)
    c: Distance(g17,g-2) = 1
    c: Coincident(g21,g22)
    c: Coincident(g22,g23)
    c: Coincident(g23,g24)
    c: Coincident(g24,g25)
    c: Coincident(g25,g26)
    c: Coincident(g26,g21)
    c: Equal(g21, g22-g26) x5
    c: PointOnObject(g21,g27)
    c: PointOnObject(g22,g27)
    c: PointOnObject(g23,g27)
    c: PointOnObject(g24,g27)
    c: PointOnObject(g25,g27)
    c: PointOnObject(g26,g27)
    c: Diameter(g27) = 7
    c: DistanceY(g-1,g27) = 7
    c: DistanceX(g21,g-1) = 1
    c: Vertical(g21)
    c: Coincident(g28,g29)
    c: Coincident(g29,g30)
    c: Coincident(g30,g31)
    c: Coincident(g31,g32)
    c: Coincident(g32,g33)
    c: Coincident(g33,g28)
    c: Equal(g28, g29-g33) x5
    c: PointOnObject(g28,g34)
    c: PointOnObject(g29,g34)
    c: PointOnObject(g30,g34)
    c: PointOnObject(g31,g34)
    c: PointOnObject(g32,g34)
    c: PointOnObject(g33,g34)
    c: PointOnObject(g34,g-1)
    c: Diameter(g34) = 7
    c: Vertical(g31)
    c: DistanceX(g34,g-1) = 8
    c: Coincident(g35,g36)
    c: Coincident(g36,g37)
    c: Coincident(g37,g38)
    c: Coincident(g38,g39)
    c: Coincident(g39,g40)
    c: Coincident(g40,g35)
    c: Equal(g35, g36-g40) x5
    c: PointOnObject(g35,g41)
    c: PointOnObject(g36,g41)
    c: PointOnObject(g37,g41)
    c: PointOnObject(g38,g41)
    c: PointOnObject(g39,g41)
    c: PointOnObject(g40,g41)
    c: Coincident(g42,g43)
    c: Coincident(g43,g44)
    c: Coincident(g44,g45)
    c: Coincident(g45,g46)
    c: Coincident(g46,g47)
    c: Coincident(g47,g42)
    c: Equal(g42, g43-g47) x5
    c: PointOnObject(g42,g48)
    c: PointOnObject(g43,g48)
    c: PointOnObject(g44,g48)
    c: PointOnObject(g45,g48)
    c: PointOnObject(g46,g48)
    c: PointOnObject(g47,g48)
    c: Equal(g41,g48)
    c: Diameter(g41) = 7
    c: Vertical(g39)
    c: Vertical(g43)
    c: Distance(g-2,g39) = 1
    c: Symmetric(g38,g43,g-2)
    c: Distance(g41,g-1) = 7
FEATURE [Part::Extrusion] Extrude664  label="hex266"
  Base = -> Sketch673
  Dir = (0,-1,2e-16)
  DirMode = 2
  FaceMakerClass = Part::FaceMakerBullseye
  FaceMakerMode = 3
  LengthFwd = 10
  LengthRev = 0
  Placement = pos=(-88,0,14) rot=(0,0,1;0rad)
  Solid = true
  Symmetric = false
FEATURE [Sketcher::SketchObject] Sketch674
  ArcFitTolerance = 1e-06
  FullyConstrained = true
  MakeInternals = false
  Placement = pos=(0,0,0) rot=(1,0,0;1.5708rad)
  sketch-geometry (49):
    g0: LineSegment StartX=1e-16 StartY=3.5 StartZ=0 EndX=-3.03109 EndY=1.75 EndZ=0
    g1: LineSegment StartX=-3.03109 StartY=1.75 StartZ=0 EndX=-3.03109 EndY=-1.75 EndZ=0
    g2: LineSegment StartX=-3.03109 StartY=-1.75 StartZ=0 EndX=-1e-16 EndY=-3.5 EndZ=0
    g3: LineSegment StartX=-1e-16 StartY=-3.5 StartZ=0 EndX=3.03109 EndY=-1.75 EndZ=0
    g4: LineSegment StartX=3.03109 StartY=-1.75 StartZ=0 EndX=3.03109 EndY=1.75 EndZ=0
    g5: LineSegment StartX=3.03109 StartY=1.75 StartZ=0 EndX=1e-16 EndY=3.5 EndZ=0
    g6: Circle [constr] CenterX=0 CenterY=0 CenterZ=0 NormalX=0 NormalY=0 NormalZ=1 AngleXU=0 Radius=3.5
    g7: LineSegment StartX=4.96892 StartY=-1.75002 StartZ=0 EndX=8.00002 EndY=-3.5 EndZ=0
    g8: LineSegment StartX=8.00002 StartY=-3.5 StartZ=0 EndX=11.0311 EndY=-1.74998 EndZ=0
    g9: LineSegment StartX=11.0311 StartY=-1.74998 StartZ=0 EndX=11.0311 EndY=1.75002 EndZ=0
    g10: LineSegment StartX=11.0311 StartY=1.75002 StartZ=0 EndX=7.99998 EndY=3.5 EndZ=0
    g11: LineSegment StartX=7.99998 StartY=3.5 StartZ=0 EndX=4.9689 EndY=1.74998 EndZ=0
    g12: LineSegment StartX=4.9689 StartY=1.74998 StartZ=0 EndX=4.96892 EndY=-1.75002 EndZ=0
    g13: Circle [constr] CenterX=8 CenterY=0 CenterZ=0 NormalX=0 NormalY=0 NormalZ=1 AngleXU=0 Radius=3.5
    g14: LineSegment StartX=4.03109 StartY=3.5 StartZ=0 EndX=7.06218 EndY=5.25 EndZ=0
    g15: LineSegment StartX=7.06218 StartY=5.25 StartZ=0 EndX=7.06218 EndY=8.75 EndZ=0
    g16: LineSegment StartX=7.06218 StartY=8.75 StartZ=0 EndX=4.03109 EndY=10.5 EndZ=0
    g17: LineSegment StartX=4.03109 StartY=10.5 StartZ=0 EndX=1 EndY=8.75 EndZ=0
    g18: LineSegment StartX=1 StartY=8.75 StartZ=0 EndX=1 EndY=5.25 EndZ=0
    g19: LineSegment StartX=1 StartY=5.25 StartZ=0 EndX=4.03109 EndY=3.5 EndZ=0
    g20: Circle [constr] CenterX=4.03109 CenterY=7 CenterZ=0 NormalX=0 NormalY=0 NormalZ=1 AngleXU=0 Radius=3.5
    g21: LineSegment StartX=-1 StartY=5.25 StartZ=0 EndX=-1 EndY=8.75 EndZ=0
    g22: LineSegment StartX=-1 StartY=8.75 StartZ=0 EndX=-4.03109 EndY=10.5 EndZ=0
    g23: LineSegment StartX=-4.03109 StartY=10.5 StartZ=0 EndX=-7.06218 EndY=8.75 EndZ=0
    g24: LineSegment StartX=-7.06218 StartY=8.75 StartZ=0 EndX=-7.06218 EndY=5.25 EndZ=0
    g25: LineSegment StartX=-7.06218 StartY=5.25 StartZ=0 EndX=-4.03109 EndY=3.5 EndZ=0
    g26: LineSegment StartX=-4.03109 StartY=3.5 StartZ=0 EndX=-1 EndY=5.25 EndZ=0
    g27: Circle [constr] CenterX=-4.03109 CenterY=7 CenterZ=0 NormalX=0 NormalY=0 NormalZ=1 AngleXU=0 Radius=3.5
    g28: LineSegment StartX=-4.96891 StartY=-1.75 StartZ=0 EndX=-4.96891 EndY=1.75 EndZ=0
    g29: LineSegment StartX=-4.96891 StartY=1.75 StartZ=0 EndX=-8 EndY=3.5 EndZ=0
    g30: LineSegment StartX=-8 StartY=3.5 StartZ=0 EndX=-11.0311 EndY=1.75 EndZ=0
    g31: LineSegment StartX=-11.0311 StartY=1.75 StartZ=0 EndX=-11.0311 EndY=-1.75 EndZ=0
    g32: LineSegment StartX=-11.0311 StartY=-1.75 StartZ=0 EndX=-8 EndY=-3.5 EndZ=0
    g33: LineSegment StartX=-8 StartY=-3.5 StartZ=0 EndX=-4.96891 EndY=-1.75 EndZ=0
    g34: Circle [constr] CenterX=-8 CenterY=0 CenterZ=0 NormalX=0 NormalY=0 NormalZ=1 AngleXU=0 Radius=3.5
    g35: LineSegment StartX=-4.03109 StartY=-3.5 StartZ=0 EndX=-7.06218 EndY=-5.25 EndZ=0
    g36: LineSegment StartX=-7.06218 StartY=-5.25 StartZ=0 EndX=-7.06218 EndY=-8.75 EndZ=0
    g37: LineSegment StartX=-7.06218 StartY=-8.75 StartZ=0 EndX=-4.03109 EndY=-10.5 EndZ=0
    g38: LineSegment StartX=-4.03109 StartY=-10.5 StartZ=0 EndX=-1 EndY=-8.75 EndZ=0
    g39: LineSegment StartX=-1 StartY=-8.75 StartZ=0 EndX=-1 EndY=-5.25 EndZ=0
    g40: LineSegment StartX=-1 StartY=-5.25 StartZ=0 EndX=-4.03109 EndY=-3.5 EndZ=0
    g41: Circle [constr] CenterX=-4.03109 CenterY=-7 CenterZ=0 NormalX=0 NormalY=0 NormalZ=1 AngleXU=0 Radius=3.5
    g42: LineSegment StartX=4.03109 StartY=-3.5 StartZ=0 EndX=1 EndY=-5.25 EndZ=0
    g43: LineSegment StartX=1 StartY=-5.25 StartZ=0 EndX=1 EndY=-8.75 EndZ=0
    g44: LineSegment StartX=1 StartY=-8.75 StartZ=0 EndX=4.03109 EndY=-10.5 EndZ=0
    g45: LineSegment StartX=4.03109 StartY=-10.5 StartZ=0 EndX=7.06218 EndY=-8.75 EndZ=0
    g46: LineSegment StartX=7.06218 StartY=-8.75 StartZ=0 EndX=7.06218 EndY=-5.25 EndZ=0
    g47: LineSegment StartX=7.06218 StartY=-5.25 StartZ=0 EndX=4.03109 EndY=-3.5 EndZ=0
    g48: Circle [constr] CenterX=4.03109 CenterY=-7 CenterZ=0 NormalX=0 NormalY=0 NormalZ=1 AngleXU=0 Radius=3.5
  constraints (117):
    c: Coincident(g0,g1)
    c: Coincident(g1,g2)
    c: Coincident(g2,g3)
    c: Coincident(g3,g4)
    c: Coincident(g4,g5)
    c: Coincident(g5,g0)
    c: Equal(g0, g1-g5) x5
    c: PointOnObject(g0,g6)
    c: PointOnObject(g1,g6)
    c: PointOnObject(g2,g6)
    c: PointOnObject(g3,g6)
    c: PointOnObject(g4,g6)
    c: PointOnObject(g5,g6)
    c: Coincident(g6,g-1)
    c: Diameter(g6) = 7
    c: PointOnObject(g0,g-2)
    c: Coincident(g7,g8)
    c: Coincident(g8,g9)
    c: Coincident(g9,g10)
    c: Coincident(g10,g11)
    c: Coincident(g11,g12)
    c: Coincident(g12,g7)
    c: Equal(g7, g8-g12) x5
    c: PointOnObject(g7,g13)
    c: PointOnObject(g8,g13)
    c: PointOnObject(g9,g13)
    c: PointOnObject(g10,g13)
    c: PointOnObject(g11,g13)
    c: PointOnObject(g12,g13)
    c: PointOnObject(g13,g-1)
    c: Diameter(g13) = 7
    c: Distance(g6,g13) = 8
    c: Horizontal(g0,g10)
    c: Coincident(g14,g15)
    c: Coincident(g15,g16)
    c: Coincident(g16,g17)
    c: Coincident(g17,g18)
    c: Coincident(g18,g19)
    c: Coincident(g19,g14)
    c: Equal(g14, g15-g19) x5
    c: PointOnObject(g14,g20)
    c: PointOnObject(g15,g20)
    c: PointOnObject(g16,g20)
    c: PointOnObject(g17,g20)
    c: PointOnObject(g18,g20)
    c: PointOnObject(g19,g20)
    c: Diameter(g20) = 7
    c: DistanceY(g-1,g20) = 7
    c: Vertical(g18)
    c: Distance(g17,g-2) = 1
    c: Coincident(g21,g22)
    c: Coincident(g22,g23)
    c: Coincident(g23,g24)
    c: Coincident(g24,g25)
    c: Coincident(g25,g26)
    c: Coincident(g26,g21)
    c: Equal(g21, g22-g26) x5
    c: PointOnObject(g21,g27)
    c: PointOnObject(g22,g27)
    c: PointOnObject(g23,g27)
    c: PointOnObject(g24,g27)
    c: PointOnObject(g25,g27)
    c: PointOnObject(g26,g27)
    c: Diameter(g27) = 7
    c: DistanceY(g-1,g27) = 7
    c: DistanceX(g21,g-1) = 1
    c: Vertical(g21)
    c: Coincident(g28,g29)
    c: Coincident(g29,g30)
    c: Coincident(g30,g31)
    c: Coincident(g31,g32)
    c: Coincident(g32,g33)
    c: Coincident(g33,g28)
    c: Equal(g28, g29-g33) x5
    c: PointOnObject(g28,g34)
    c: PointOnObject(g29,g34)
    c: PointOnObject(g30,g34)
    c: PointOnObject(g31,g34)
    c: PointOnObject(g32,g34)
    c: PointOnObject(g33,g34)
    c: PointOnObject(g34,g-1)
    c: Diameter(g34) = 7
    c: Vertical(g31)
    c: DistanceX(g34,g-1) = 8
    c: Coincident(g35,g36)
    c: Coincident(g36,g37)
    c: Coincident(g37,g38)
    c: Coincident(g38,g39)
    c: Coincident(g39,g40)
    c: Coincident(g40,g35)
    c: Equal(g35, g36-g40) x5
    c: PointOnObject(g35,g41)
    c: PointOnObject(g36,g41)
    c: PointOnObject(g37,g41)
    c: PointOnObject(g38,g41)
    c: PointOnObject(g39,g41)
    c: PointOnObject(g40,g41)
    c: Coincident(g42,g43)
    c: Coincident(g43,g44)
    c: Coincident(g44,g45)
    c: Coincident(g45,g46)
    c: Coincident(g46,g47)
    c: Coincident(g47,g42)
    c: Equal(g42, g43-g47) x5
    c: PointOnObject(g42,g48)
    c: PointOnObject(g43,g48)
    c: PointOnObject(g44,g48)
    c: PointOnObject(g45,g48)
    c: PointOnObject(g46,g48)
    c: PointOnObject(g47,g48)
    c: Equal(g41,g48)
    c: Diameter(g41) = 7
    c: Vertical(g39)
    c: Vertical(g43)
    c: Distance(g-2,g39) = 1
    c: Symmetric(g38,g43,g-2)
    c: Distance(g41,g-1) = 7
FEATURE [Part::Extrusion] Extrude665  label="hex267"
  Base = -> Sketch674
  Dir = (0,-1,2e-16)
  DirMode = 2
  FaceMakerClass = Part::FaceMakerBullseye
  FaceMakerMode = 3
  LengthFwd = 10
  LengthRev = 0
  Placement = pos=(96,0,14) rot=(0,0,1;0rad)
  Solid = true
  Symmetric = false
FEATURE [Part::MultiFuse] Fusion564
  Placement = pos=(0,0,56) rot=(0,0,1;0rad)
  Refine = true
  Shapes = -> [Extrude616,Extrude617,Extrude618,Extrude619,Extrude620,Extrude621,Extrude622,Extrude623,Extrude624,Extrude625,Extrude626,Extrude627,Extrude628,Extrude629,Extrude630,Extrude631,Extrude632,Extrude633,Extrude634,Extrude635,Extrude636,Extrude637,Extrude638,Extrude639,Extrude640,Extrude641,Extrude642,Extrude643,Extrude644,Extrude645,Extrude646,Extrude647,Extrude648,Extrude649,Extrude650,Extrude651,+14 more]
FEATURE [Sketcher::SketchObject] Sketch675
  ArcFitTolerance = 1e-06
  FullyConstrained = true
  MakeInternals = false
  Placement = pos=(0,0,0) rot=(1,0,0;1.5708rad)
  sketch-geometry (49):
    g0: LineSegment StartX=1e-16 StartY=3.5 StartZ=0 EndX=-3.03109 EndY=1.75 EndZ=0
    g1: LineSegment StartX=-3.03109 StartY=1.75 StartZ=0 EndX=-3.03109 EndY=-1.75 EndZ=0
    g2: LineSegment StartX=-3.03109 StartY=-1.75 StartZ=0 EndX=-1e-16 EndY=-3.5 EndZ=0
    g3: LineSegment StartX=-1e-16 StartY=-3.5 StartZ=0 EndX=3.03109 EndY=-1.75 EndZ=0
    g4: LineSegment StartX=3.03109 StartY=-1.75 StartZ=0 EndX=3.03109 EndY=1.75 EndZ=0
    g5: LineSegment StartX=3.03109 StartY=1.75 StartZ=0 EndX=1e-16 EndY=3.5 EndZ=0
    g6: Circle [constr] CenterX=0 CenterY=0 CenterZ=0 NormalX=0 NormalY=0 NormalZ=1 AngleXU=0 Radius=3.5
    g7: LineSegment StartX=4.96892 StartY=-1.75002 StartZ=0 EndX=8.00002 EndY=-3.5 EndZ=0
    g8: LineSegment StartX=8.00002 StartY=-3.5 StartZ=0 EndX=11.0311 EndY=-1.74998 EndZ=0
    g9: LineSegment StartX=11.0311 StartY=-1.74998 StartZ=0 EndX=11.0311 EndY=1.75002 EndZ=0
    g10: LineSegment StartX=11.0311 StartY=1.75002 StartZ=0 EndX=7.99998 EndY=3.5 EndZ=0
    g11: LineSegment StartX=7.99998 StartY=3.5 StartZ=0 EndX=4.9689 EndY=1.74998 EndZ=0
    g12: LineSegment StartX=4.9689 StartY=1.74998 StartZ=0 EndX=4.96892 EndY=-1.75002 EndZ=0
    g13: Circle [constr] CenterX=8 CenterY=0 CenterZ=0 NormalX=0 NormalY=0 NormalZ=1 AngleXU=0 Radius=3.5
    g14: LineSegment StartX=4.03109 StartY=3.5 StartZ=0 EndX=7.06218 EndY=5.25 EndZ=0
    g15: LineSegment StartX=7.06218 StartY=5.25 StartZ=0 EndX=7.06218 EndY=8.75 EndZ=0
    g16: LineSegment StartX=7.06218 StartY=8.75 StartZ=0 EndX=4.03109 EndY=10.5 EndZ=0
    g17: LineSegment StartX=4.03109 StartY=10.5 StartZ=0 EndX=1 EndY=8.75 EndZ=0
    g18: LineSegment StartX=1 StartY=8.75 StartZ=0 EndX=1 EndY=5.25 EndZ=0
    g19: LineSegment StartX=1 StartY=5.25 StartZ=0 EndX=4.03109 EndY=3.5 EndZ=0
    g20: Circle [constr] CenterX=4.03109 CenterY=7 CenterZ=0 NormalX=0 NormalY=0 NormalZ=1 AngleXU=0 Radius=3.5
    g21: LineSegment StartX=-1 StartY=5.25 StartZ=0 EndX=-1 EndY=8.75 EndZ=0
    g22: LineSegment StartX=-1 StartY=8.75 StartZ=0 EndX=-4.03109 EndY=10.5 EndZ=0
    g23: LineSegment StartX=-4.03109 StartY=10.5 StartZ=0 EndX=-7.06218 EndY=8.75 EndZ=0
    g24: LineSegment StartX=-7.06218 StartY=8.75 StartZ=0 EndX=-7.06218 EndY=5.25 EndZ=0
    g25: LineSegment StartX=-7.06218 StartY=5.25 StartZ=0 EndX=-4.03109 EndY=3.5 EndZ=0
    g26: LineSegment StartX=-4.03109 StartY=3.5 StartZ=0 EndX=-1 EndY=5.25 EndZ=0
    g27: Circle [constr] CenterX=-4.03109 CenterY=7 CenterZ=0 NormalX=0 NormalY=0 NormalZ=1 AngleXU=0 Radius=3.5
    g28: LineSegment StartX=-4.96891 StartY=-1.75 StartZ=0 EndX=-4.96891 EndY=1.75 EndZ=0
    g29: LineSegment StartX=-4.96891 StartY=1.75 StartZ=0 EndX=-8 EndY=3.5 EndZ=0
    g30: LineSegment StartX=-8 StartY=3.5 StartZ=0 EndX=-11.0311 EndY=1.75 EndZ=0
    g31: LineSegment StartX=-11.0311 StartY=1.75 StartZ=0 EndX=-11.0311 EndY=-1.75 EndZ=0
    g32: LineSegment StartX=-11.0311 StartY=-1.75 StartZ=0 EndX=-8 EndY=-3.5 EndZ=0
    g33: LineSegment StartX=-8 StartY=-3.5 StartZ=0 EndX=-4.96891 EndY=-1.75 EndZ=0
    g34: Circle [constr] CenterX=-8 CenterY=0 CenterZ=0 NormalX=0 NormalY=0 NormalZ=1 AngleXU=0 Radius=3.5
    g35: LineSegment StartX=-4.03109 StartY=-3.5 StartZ=0 EndX=-7.06218 EndY=-5.25 EndZ=0
    g36: LineSegment StartX=-7.06218 StartY=-5.25 StartZ=0 EndX=-7.06218 EndY=-8.75 EndZ=0
    g37: LineSegment StartX=-7.06218 StartY=-8.75 StartZ=0 EndX=-4.03109 EndY=-10.5 EndZ=0
    g38: LineSegment StartX=-4.03109 StartY=-10.5 StartZ=0 EndX=-1 EndY=-8.75 EndZ=0
    g39: LineSegment StartX=-1 StartY=-8.75 StartZ=0 EndX=-1 EndY=-5.25 EndZ=0
    g40: LineSegment StartX=-1 StartY=-5.25 StartZ=0 EndX=-4.03109 EndY=-3.5 EndZ=0
    g41: Circle [constr] CenterX=-4.03109 CenterY=-7 CenterZ=0 NormalX=0 NormalY=0 NormalZ=1 AngleXU=0 Radius=3.5
    g42: LineSegment StartX=4.03109 StartY=-3.5 StartZ=0 EndX=1 EndY=-5.25 EndZ=0
    g43: LineSegment StartX=1 StartY=-5.25 StartZ=0 EndX=1 EndY=-8.75 EndZ=0
    g44: LineSegment StartX=1 StartY=-8.75 StartZ=0 EndX=4.03109 EndY=-10.5 EndZ=0
    g45: LineSegment StartX=4.03109 StartY=-10.5 StartZ=0 EndX=7.06218 EndY=-8.75 EndZ=0
    g46: LineSegment StartX=7.06218 StartY=-8.75 StartZ=0 EndX=7.06218 EndY=-5.25 EndZ=0
    g47: LineSegment StartX=7.06218 StartY=-5.25 StartZ=0 EndX=4.03109 EndY=-3.5 EndZ=0
    g48: Circle [constr] CenterX=4.03109 CenterY=-7 CenterZ=0 NormalX=0 NormalY=0 NormalZ=1 AngleXU=0 Radius=3.5
  constraints (117):
    c: Coincident(g0,g1)
    c: Coincident(g1,g2)
    c: Coincident(g2,g3)
    c: Coincident(g3,g4)
    c: Coincident(g4,g5)
    c: Coincident(g5,g0)
    c: Equal(g0, g1-g5) x5
    c: PointOnObject(g0,g6)
    c: PointOnObject(g1,g6)
    c: PointOnObject(g2,g6)
    c: PointOnObject(g3,g6)
    c: PointOnObject(g4,g6)
    c: PointOnObject(g5,g6)
    c: Coincident(g6,g-1)
    c: Diameter(g6) = 7
    c: PointOnObject(g0,g-2)
    c: Coincident(g7,g8)
    c: Coincident(g8,g9)
    c: Coincident(g9,g10)
    c: Coincident(g10,g11)
    c: Coincident(g11,g12)
    c: Coincident(g12,g7)
    c: Equal(g7, g8-g12) x5
    c: PointOnObject(g7,g13)
    c: PointOnObject(g8,g13)
    c: PointOnObject(g9,g13)
    c: PointOnObject(g10,g13)
    c: PointOnObject(g11,g13)
    c: PointOnObject(g12,g13)
    c: PointOnObject(g13,g-1)
    c: Diameter(g13) = 7
    c: Distance(g6,g13) = 8
    c: Horizontal(g0,g10)
    c: Coincident(g14,g15)
    c: Coincident(g15,g16)
    c: Coincident(g16,g17)
    c: Coincident(g17,g18)
    c: Coincident(g18,g19)
    c: Coincident(g19,g14)
    c: Equal(g14, g15-g19) x5
    c: PointOnObject(g14,g20)
    c: PointOnObject(g15,g20)
    c: PointOnObject(g16,g20)
    c: PointOnObject(g17,g20)
    c: PointOnObject(g18,g20)
    c: PointOnObject(g19,g20)
    c: Diameter(g20) = 7
    c: DistanceY(g-1,g20) = 7
    c: Vertical(g18)
    c: Distance(g17,g-2) = 1
    c: Coincident(g21,g22)
    c: Coincident(g22,g23)
    c: Coincident(g23,g24)
    c: Coincident(g24,g25)
    c: Coincident(g25,g26)
    c: Coincident(g26,g21)
    c: Equal(g21, g22-g26) x5
    c: PointOnObject(g21,g27)
    c: PointOnObject(g22,g27)
    c: PointOnObject(g23,g27)
    c: PointOnObject(g24,g27)
    c: PointOnObject(g25,g27)
    c: PointOnObject(g26,g27)
    c: Diameter(g27) = 7
    c: DistanceY(g-1,g27) = 7
    c: DistanceX(g21,g-1) = 1
    c: Vertical(g21)
    c: Coincident(g28,g29)
    c: Coincident(g29,g30)
    c: Coincident(g30,g31)
    c: Coincident(g31,g32)
    c: Coincident(g32,g33)
    c: Coincident(g33,g28)
    c: Equal(g28, g29-g33) x5
    c: PointOnObject(g28,g34)
    c: PointOnObject(g29,g34)
    c: PointOnObject(g30,g34)
    c: PointOnObject(g31,g34)
    c: PointOnObject(g32,g34)
    c: PointOnObject(g33,g34)
    c: PointOnObject(g34,g-1)
    c: Diameter(g34) = 7
    c: Vertical(g31)
    c: DistanceX(g34,g-1) = 8
    c: Coincident(g35,g36)
    c: Coincident(g36,g37)
    c: Coincident(g37,g38)
    c: Coincident(g38,g39)
    c: Coincident(g39,g40)
    c: Coincident(g40,g35)
    c: Equal(g35, g36-g40) x5
    c: PointOnObject(g35,g41)
    c: PointOnObject(g36,g41)
    c: PointOnObject(g37,g41)
    c: PointOnObject(g38,g41)
    c: PointOnObject(g39,g41)
    c: PointOnObject(g40,g41)
    c: Coincident(g42,g43)
    c: Coincident(g43,g44)
    c: Coincident(g44,g45)
    c: Coincident(g45,g46)
    c: Coincident(g46,g47)
    c: Coincident(g47,g42)
    c: Equal(g42, g43-g47) x5
    c: PointOnObject(g42,g48)
    c: PointOnObject(g43,g48)
    c: PointOnObject(g44,g48)
    c: PointOnObject(g45,g48)
    c: PointOnObject(g46,g48)
    c: PointOnObject(g47,g48)
    c: Equal(g41,g48)
    c: Diameter(g41) = 7
    c: Vertical(g39)
    c: Vertical(g43)
    c: Distance(g-2,g39) = 1
    c: Symmetric(g38,g43,g-2)
    c: Distance(g41,g-1) = 7
FEATURE [Part::Extrusion] Extrude666  label="hex268"
  Base = -> Sketch675
  Dir = (0,-1,2e-16)
  DirMode = 2
  FaceMakerClass = Part::FaceMakerBullseye
  FaceMakerMode = 3
  LengthFwd = 10
  LengthRev = 0
  Solid = true
  Symmetric = false
FEATURE [Sketcher::SketchObject] Sketch676
  ArcFitTolerance = 1e-06
  FullyConstrained = true
  MakeInternals = false
  Placement = pos=(0,0,0) rot=(1,0,0;1.5708rad)
  sketch-geometry (49):
    g0: LineSegment StartX=1e-16 StartY=3.5 StartZ=0 EndX=-3.03109 EndY=1.75 EndZ=0
    g1: LineSegment StartX=-3.03109 StartY=1.75 StartZ=0 EndX=-3.03109 EndY=-1.75 EndZ=0
    g2: LineSegment StartX=-3.03109 StartY=-1.75 StartZ=0 EndX=-1e-16 EndY=-3.5 EndZ=0
    g3: LineSegment StartX=-1e-16 StartY=-3.5 StartZ=0 EndX=3.03109 EndY=-1.75 EndZ=0
    g4: LineSegment StartX=3.03109 StartY=-1.75 StartZ=0 EndX=3.03109 EndY=1.75 EndZ=0
    g5: LineSegment StartX=3.03109 StartY=1.75 StartZ=0 EndX=1e-16 EndY=3.5 EndZ=0
    g6: Circle [constr] CenterX=0 CenterY=0 CenterZ=0 NormalX=0 NormalY=0 NormalZ=1 AngleXU=0 Radius=3.5
    g7: LineSegment StartX=4.96892 StartY=-1.75002 StartZ=0 EndX=8.00002 EndY=-3.5 EndZ=0
    g8: LineSegment StartX=8.00002 StartY=-3.5 StartZ=0 EndX=11.0311 EndY=-1.74998 EndZ=0
    g9: LineSegment StartX=11.0311 StartY=-1.74998 StartZ=0 EndX=11.0311 EndY=1.75002 EndZ=0
    g10: LineSegment StartX=11.0311 StartY=1.75002 StartZ=0 EndX=7.99998 EndY=3.5 EndZ=0
    g11: LineSegment StartX=7.99998 StartY=3.5 StartZ=0 EndX=4.9689 EndY=1.74998 EndZ=0
    g12: LineSegment StartX=4.9689 StartY=1.74998 StartZ=0 EndX=4.96892 EndY=-1.75002 EndZ=0
    g13: Circle [constr] CenterX=8 CenterY=0 CenterZ=0 NormalX=0 NormalY=0 NormalZ=1 AngleXU=0 Radius=3.5
    g14: LineSegment StartX=4.03109 StartY=3.5 StartZ=0 EndX=7.06218 EndY=5.25 EndZ=0
    g15: LineSegment StartX=7.06218 StartY=5.25 StartZ=0 EndX=7.06218 EndY=8.75 EndZ=0
    g16: LineSegment StartX=7.06218 StartY=8.75 StartZ=0 EndX=4.03109 EndY=10.5 EndZ=0
    g17: LineSegment StartX=4.03109 StartY=10.5 StartZ=0 EndX=1 EndY=8.75 EndZ=0
    g18: LineSegment StartX=1 StartY=8.75 StartZ=0 EndX=1 EndY=5.25 EndZ=0
    g19: LineSegment StartX=1 StartY=5.25 StartZ=0 EndX=4.03109 EndY=3.5 EndZ=0
    g20: Circle [constr] CenterX=4.03109 CenterY=7 CenterZ=0 NormalX=0 NormalY=0 NormalZ=1 AngleXU=0 Radius=3.5
    g21: LineSegment StartX=-1 StartY=5.25 StartZ=0 EndX=-1 EndY=8.75 EndZ=0
    g22: LineSegment StartX=-1 StartY=8.75 StartZ=0 EndX=-4.03109 EndY=10.5 EndZ=0
    g23: LineSegment StartX=-4.03109 StartY=10.5 StartZ=0 EndX=-7.06218 EndY=8.75 EndZ=0
    g24: LineSegment StartX=-7.06218 StartY=8.75 StartZ=0 EndX=-7.06218 EndY=5.25 EndZ=0
    g25: LineSegment StartX=-7.06218 StartY=5.25 StartZ=0 EndX=-4.03109 EndY=3.5 EndZ=0
    g26: LineSegment StartX=-4.03109 StartY=3.5 StartZ=0 EndX=-1 EndY=5.25 EndZ=0
    g27: Circle [constr] CenterX=-4.03109 CenterY=7 CenterZ=0 NormalX=0 NormalY=0 NormalZ=1 AngleXU=0 Radius=3.5
    g28: LineSegment StartX=-4.96891 StartY=-1.75 StartZ=0 EndX=-4.96891 EndY=1.75 EndZ=0
    g29: LineSegment StartX=-4.96891 StartY=1.75 StartZ=0 EndX=-8 EndY=3.5 EndZ=0
    g30: LineSegment StartX=-8 StartY=3.5 StartZ=0 EndX=-11.0311 EndY=1.75 EndZ=0
    g31: LineSegment StartX=-11.0311 StartY=1.75 StartZ=0 EndX=-11.0311 EndY=-1.75 EndZ=0
    g32: LineSegment StartX=-11.0311 StartY=-1.75 StartZ=0 EndX=-8 EndY=-3.5 EndZ=0
    g33: LineSegment StartX=-8 StartY=-3.5 StartZ=0 EndX=-4.96891 EndY=-1.75 EndZ=0
    g34: Circle [constr] CenterX=-8 CenterY=0 CenterZ=0 NormalX=0 NormalY=0 NormalZ=1 AngleXU=0 Radius=3.5
    g35: LineSegment StartX=-4.03109 StartY=-3.5 StartZ=0 EndX=-7.06218 EndY=-5.25 EndZ=0
    g36: LineSegment StartX=-7.06218 StartY=-5.25 StartZ=0 EndX=-7.06218 EndY=-8.75 EndZ=0
    g37: LineSegment StartX=-7.06218 StartY=-8.75 StartZ=0 EndX=-4.03109 EndY=-10.5 EndZ=0
    g38: LineSegment StartX=-4.03109 StartY=-10.5 StartZ=0 EndX=-1 EndY=-8.75 EndZ=0
    g39: LineSegment StartX=-1 StartY=-8.75 StartZ=0 EndX=-1 EndY=-5.25 EndZ=0
    g40: LineSegment StartX=-1 StartY=-5.25 StartZ=0 EndX=-4.03109 EndY=-3.5 EndZ=0
    g41: Circle [constr] CenterX=-4.03109 CenterY=-7 CenterZ=0 NormalX=0 NormalY=0 NormalZ=1 AngleXU=0 Radius=3.5
    g42: LineSegment StartX=4.03109 StartY=-3.5 StartZ=0 EndX=1 EndY=-5.25 EndZ=0
    g43: LineSegment StartX=1 StartY=-5.25 StartZ=0 EndX=1 EndY=-8.75 EndZ=0
    g44: LineSegment StartX=1 StartY=-8.75 StartZ=0 EndX=4.03109 EndY=-10.5 EndZ=0
    g45: LineSegment StartX=4.03109 StartY=-10.5 StartZ=0 EndX=7.06218 EndY=-8.75 EndZ=0
    g46: LineSegment StartX=7.06218 StartY=-8.75 StartZ=0 EndX=7.06218 EndY=-5.25 EndZ=0
    g47: LineSegment StartX=7.06218 StartY=-5.25 StartZ=0 EndX=4.03109 EndY=-3.5 EndZ=0
    g48: Circle [constr] CenterX=4.03109 CenterY=-7 CenterZ=0 NormalX=0 NormalY=0 NormalZ=1 AngleXU=0 Radius=3.5
  constraints (117):
    c: Coincident(g0,g1)
    c: Coincident(g1,g2)
    c: Coincident(g2,g3)
    c: Coincident(g3,g4)
    c: Coincident(g4,g5)
    c: Coincident(g5,g0)
    c: Equal(g0, g1-g5) x5
    c: PointOnObject(g0,g6)
    c: PointOnObject(g1,g6)
    c: PointOnObject(g2,g6)
    c: PointOnObject(g3,g6)
    c: PointOnObject(g4,g6)
    c: PointOnObject(g5,g6)
    c: Coincident(g6,g-1)
    c: Diameter(g6) = 7
    c: PointOnObject(g0,g-2)
    c: Coincident(g7,g8)
    c: Coincident(g8,g9)
    c: Coincident(g9,g10)
    c: Coincident(g10,g11)
    c: Coincident(g11,g12)
    c: Coincident(g12,g7)
    c: Equal(g7, g8-g12) x5
    c: PointOnObject(g7,g13)
    c: PointOnObject(g8,g13)
    c: PointOnObject(g9,g13)
    c: PointOnObject(g10,g13)
    c: PointOnObject(g11,g13)
    c: PointOnObject(g12,g13)
    c: PointOnObject(g13,g-1)
    c: Diameter(g13) = 7
    c: Distance(g6,g13) = 8
    c: Horizontal(g0,g10)
    c: Coincident(g14,g15)
    c: Coincident(g15,g16)
    c: Coincident(g16,g17)
    c: Coincident(g17,g18)
    c: Coincident(g18,g19)
    c: Coincident(g19,g14)
    c: Equal(g14, g15-g19) x5
    c: PointOnObject(g14,g20)
    c: PointOnObject(g15,g20)
    c: PointOnObject(g16,g20)
    c: PointOnObject(g17,g20)
    c: PointOnObject(g18,g20)
    c: PointOnObject(g19,g20)
    c: Diameter(g20) = 7
    c: DistanceY(g-1,g20) = 7
    c: Vertical(g18)
    c: Distance(g17,g-2) = 1
    c: Coincident(g21,g22)
    c: Coincident(g22,g23)
    c: Coincident(g23,g24)
    c: Coincident(g24,g25)
    c: Coincident(g25,g26)
    c: Coincident(g26,g21)
    c: Equal(g21, g22-g26) x5
    c: PointOnObject(g21,g27)
    c: PointOnObject(g22,g27)
    c: PointOnObject(g23,g27)
    c: PointOnObject(g24,g27)
    c: PointOnObject(g25,g27)
    c: PointOnObject(g26,g27)
    c: Diameter(g27) = 7
    c: DistanceY(g-1,g27) = 7
    c: DistanceX(g21,g-1) = 1
    c: Vertical(g21)
    c: Coincident(g28,g29)
    c: Coincident(g29,g30)
    c: Coincident(g30,g31)
    c: Coincident(g31,g32)
    c: Coincident(g32,g33)
    c: Coincident(g33,g28)
    c: Equal(g28, g29-g33) x5
    c: PointOnObject(g28,g34)
    c: PointOnObject(g29,g34)
    c: PointOnObject(g30,g34)
    c: PointOnObject(g31,g34)
    c: PointOnObject(g32,g34)
    c: PointOnObject(g33,g34)
    c: PointOnObject(g34,g-1)
    c: Diameter(g34) = 7
    c: Vertical(g31)
    c: DistanceX(g34,g-1) = 8
    c: Coincident(g35,g36)
    c: Coincident(g36,g37)
    c: Coincident(g37,g38)
    c: Coincident(g38,g39)
    c: Coincident(g39,g40)
    c: Coincident(g40,g35)
    c: Equal(g35, g36-g40) x5
    c: PointOnObject(g35,g41)
    c: PointOnObject(g36,g41)
    c: PointOnObject(g37,g41)
    c: PointOnObject(g38,g41)
    c: PointOnObject(g39,g41)
    c: PointOnObject(g40,g41)
    c: Coincident(g42,g43)
    c: Coincident(g43,g44)
    c: Coincident(g44,g45)
    c: Coincident(g45,g46)
    c: Coincident(g46,g47)
    c: Coincident(g47,g42)
    c: Equal(g42, g43-g47) x5
    c: PointOnObject(g42,g48)
    c: PointOnObject(g43,g48)
    c: PointOnObject(g44,g48)
    c: PointOnObject(g45,g48)
    c: PointOnObject(g46,g48)
    c: PointOnObject(g47,g48)
    c: Equal(g41,g48)
    c: Diameter(g41) = 7
    c: Vertical(g39)
    c: Vertical(g43)
    c: Distance(g-2,g39) = 1
    c: Symmetric(g38,g43,g-2)
    c: Distance(g41,g-1) = 7
FEATURE [Part::Extrusion] Extrude667  label="hex269"
  Base = -> Sketch676
  Dir = (0,-1,2e-16)
  DirMode = 2
  FaceMakerClass = Part::FaceMakerBullseye
  FaceMakerMode = 3
  LengthFwd = 10
  LengthRev = 0
  Placement = pos=(20,0,-7) rot=(0,0,1;0rad)
  Solid = true
  Symmetric = false
FEATURE [Sketcher::SketchObject] Sketch677
  ArcFitTolerance = 1e-06
  FullyConstrained = true
  MakeInternals = false
  Placement = pos=(0,0,0) rot=(1,0,0;1.5708rad)
  sketch-geometry (49):
    g0: LineSegment StartX=1e-16 StartY=3.5 StartZ=0 EndX=-3.03109 EndY=1.75 EndZ=0
    g1: LineSegment StartX=-3.03109 StartY=1.75 StartZ=0 EndX=-3.03109 EndY=-1.75 EndZ=0
    g2: LineSegment StartX=-3.03109 StartY=-1.75 StartZ=0 EndX=-1e-16 EndY=-3.5 EndZ=0
    g3: LineSegment StartX=-1e-16 StartY=-3.5 StartZ=0 EndX=3.03109 EndY=-1.75 EndZ=0
    g4: LineSegment StartX=3.03109 StartY=-1.75 StartZ=0 EndX=3.03109 EndY=1.75 EndZ=0
    g5: LineSegment StartX=3.03109 StartY=1.75 StartZ=0 EndX=1e-16 EndY=3.5 EndZ=0
    g6: Circle [constr] CenterX=0 CenterY=0 CenterZ=0 NormalX=0 NormalY=0 NormalZ=1 AngleXU=0 Radius=3.5
    g7: LineSegment StartX=4.96892 StartY=-1.75002 StartZ=0 EndX=8.00002 EndY=-3.5 EndZ=0
    g8: LineSegment StartX=8.00002 StartY=-3.5 StartZ=0 EndX=11.0311 EndY=-1.74998 EndZ=0
    g9: LineSegment StartX=11.0311 StartY=-1.74998 StartZ=0 EndX=11.0311 EndY=1.75002 EndZ=0
    g10: LineSegment StartX=11.0311 StartY=1.75002 StartZ=0 EndX=7.99998 EndY=3.5 EndZ=0
    g11: LineSegment StartX=7.99998 StartY=3.5 StartZ=0 EndX=4.9689 EndY=1.74998 EndZ=0
    g12: LineSegment StartX=4.9689 StartY=1.74998 StartZ=0 EndX=4.96892 EndY=-1.75002 EndZ=0
    g13: Circle [constr] CenterX=8 CenterY=0 CenterZ=0 NormalX=0 NormalY=0 NormalZ=1 AngleXU=0 Radius=3.5
    g14: LineSegment StartX=4.03109 StartY=3.5 StartZ=0 EndX=7.06218 EndY=5.25 EndZ=0
    g15: LineSegment StartX=7.06218 StartY=5.25 StartZ=0 EndX=7.06218 EndY=8.75 EndZ=0
    g16: LineSegment StartX=7.06218 StartY=8.75 StartZ=0 EndX=4.03109 EndY=10.5 EndZ=0
    g17: LineSegment StartX=4.03109 StartY=10.5 StartZ=0 EndX=1 EndY=8.75 EndZ=0
    g18: LineSegment StartX=1 StartY=8.75 StartZ=0 EndX=1 EndY=5.25 EndZ=0
    g19: LineSegment StartX=1 StartY=5.25 StartZ=0 EndX=4.03109 EndY=3.5 EndZ=0
    g20: Circle [constr] CenterX=4.03109 CenterY=7 CenterZ=0 NormalX=0 NormalY=0 NormalZ=1 AngleXU=0 Radius=3.5
    g21: LineSegment StartX=-1 StartY=5.25 StartZ=0 EndX=-1 EndY=8.75 EndZ=0
    g22: LineSegment StartX=-1 StartY=8.75 StartZ=0 EndX=-4.03109 EndY=10.5 EndZ=0
    g23: LineSegment StartX=-4.03109 StartY=10.5 StartZ=0 EndX=-7.06218 EndY=8.75 EndZ=0
    g24: LineSegment StartX=-7.06218 StartY=8.75 StartZ=0 EndX=-7.06218 EndY=5.25 EndZ=0
    g25: LineSegment StartX=-7.06218 StartY=5.25 StartZ=0 EndX=-4.03109 EndY=3.5 EndZ=0
    g26: LineSegment StartX=-4.03109 StartY=3.5 StartZ=0 EndX=-1 EndY=5.25 EndZ=0
    g27: Circle [constr] CenterX=-4.03109 CenterY=7 CenterZ=0 NormalX=0 NormalY=0 NormalZ=1 AngleXU=0 Radius=3.5
    g28: LineSegment StartX=-4.96891 StartY=-1.75 StartZ=0 EndX=-4.96891 EndY=1.75 EndZ=0
    g29: LineSegment StartX=-4.96891 StartY=1.75 StartZ=0 EndX=-8 EndY=3.5 EndZ=0
    g30: LineSegment StartX=-8 StartY=3.5 StartZ=0 EndX=-11.0311 EndY=1.75 EndZ=0
    g31: LineSegment StartX=-11.0311 StartY=1.75 StartZ=0 EndX=-11.0311 EndY=-1.75 EndZ=0
    g32: LineSegment StartX=-11.0311 StartY=-1.75 StartZ=0 EndX=-8 EndY=-3.5 EndZ=0
    g33: LineSegment StartX=-8 StartY=-3.5 StartZ=0 EndX=-4.96891 EndY=-1.75 EndZ=0
    g34: Circle [constr] CenterX=-8 CenterY=0 CenterZ=0 NormalX=0 NormalY=0 NormalZ=1 AngleXU=0 Radius=3.5
    g35: LineSegment StartX=-4.03109 StartY=-3.5 StartZ=0 EndX=-7.06218 EndY=-5.25 EndZ=0
    g36: LineSegment StartX=-7.06218 StartY=-5.25 StartZ=0 EndX=-7.06218 EndY=-8.75 EndZ=0
    g37: LineSegment StartX=-7.06218 StartY=-8.75 StartZ=0 EndX=-4.03109 EndY=-10.5 EndZ=0
    g38: LineSegment StartX=-4.03109 StartY=-10.5 StartZ=0 EndX=-1 EndY=-8.75 EndZ=0
    g39: LineSegment StartX=-1 StartY=-8.75 StartZ=0 EndX=-1 EndY=-5.25 EndZ=0
    g40: LineSegment StartX=-1 StartY=-5.25 StartZ=0 EndX=-4.03109 EndY=-3.5 EndZ=0
    g41: Circle [constr] CenterX=-4.03109 CenterY=-7 CenterZ=0 NormalX=0 NormalY=0 NormalZ=1 AngleXU=0 Radius=3.5
    g42: LineSegment StartX=4.03109 StartY=-3.5 StartZ=0 EndX=1 EndY=-5.25 EndZ=0
    g43: LineSegment StartX=1 StartY=-5.25 StartZ=0 EndX=1 EndY=-8.75 EndZ=0
    g44: LineSegment StartX=1 StartY=-8.75 StartZ=0 EndX=4.03109 EndY=-10.5 EndZ=0
    g45: LineSegment StartX=4.03109 StartY=-10.5 StartZ=0 EndX=7.06218 EndY=-8.75 EndZ=0
    g46: LineSegment StartX=7.06218 StartY=-8.75 StartZ=0 EndX=7.06218 EndY=-5.25 EndZ=0
    g47: LineSegment StartX=7.06218 StartY=-5.25 StartZ=0 EndX=4.03109 EndY=-3.5 EndZ=0
    g48: Circle [constr] CenterX=4.03109 CenterY=-7 CenterZ=0 NormalX=0 NormalY=0 NormalZ=1 AngleXU=0 Radius=3.5
  constraints (117):
    c: Coincident(g0,g1)
    c: Coincident(g1,g2)
    c: Coincident(g2,g3)
    c: Coincident(g3,g4)
    c: Coincident(g4,g5)
    c: Coincident(g5,g0)
    c: Equal(g0, g1-g5) x5
    c: PointOnObject(g0,g6)
    c: PointOnObject(g1,g6)
    c: PointOnObject(g2,g6)
    c: PointOnObject(g3,g6)
    c: PointOnObject(g4,g6)
    c: PointOnObject(g5,g6)
    c: Coincident(g6,g-1)
    c: Diameter(g6) = 7
    c: PointOnObject(g0,g-2)
    c: Coincident(g7,g8)
    c: Coincident(g8,g9)
    c: Coincident(g9,g10)
    c: Coincident(g10,g11)
    c: Coincident(g11,g12)
    c: Coincident(g12,g7)
    c: Equal(g7, g8-g12) x5
    c: PointOnObject(g7,g13)
    c: PointOnObject(g8,g13)
    c: PointOnObject(g9,g13)
    c: PointOnObject(g10,g13)
    c: PointOnObject(g11,g13)
    c: PointOnObject(g12,g13)
    c: PointOnObject(g13,g-1)
    c: Diameter(g13) = 7
    c: Distance(g6,g13) = 8
    c: Horizontal(g0,g10)
    c: Coincident(g14,g15)
    c: Coincident(g15,g16)
    c: Coincident(g16,g17)
    c: Coincident(g17,g18)
    c: Coincident(g18,g19)
    c: Coincident(g19,g14)
    c: Equal(g14, g15-g19) x5
    c: PointOnObject(g14,g20)
    c: PointOnObject(g15,g20)
    c: PointOnObject(g16,g20)
    c: PointOnObject(g17,g20)
    c: PointOnObject(g18,g20)
    c: PointOnObject(g19,g20)
    c: Diameter(g20) = 7
    c: DistanceY(g-1,g20) = 7
    c: Vertical(g18)
    c: Distance(g17,g-2) = 1
    c: Coincident(g21,g22)
    c: Coincident(g22,g23)
    c: Coincident(g23,g24)
    c: Coincident(g24,g25)
    c: Coincident(g25,g26)
    c: Coincident(g26,g21)
    c: Equal(g21, g22-g26) x5
    c: PointOnObject(g21,g27)
    c: PointOnObject(g22,g27)
    c: PointOnObject(g23,g27)
    c: PointOnObject(g24,g27)
    c: PointOnObject(g25,g27)
    c: PointOnObject(g26,g27)
    c: Diameter(g27) = 7
    c: DistanceY(g-1,g27) = 7
    c: DistanceX(g21,g-1) = 1
    c: Vertical(g21)
    c: Coincident(g28,g29)
    c: Coincident(g29,g30)
    c: Coincident(g30,g31)
    c: Coincident(g31,g32)
    c: Coincident(g32,g33)
    c: Coincident(g33,g28)
    c: Equal(g28, g29-g33) x5
    c: PointOnObject(g28,g34)
    c: PointOnObject(g29,g34)
    c: PointOnObject(g30,g34)
    c: PointOnObject(g31,g34)
    c: PointOnObject(g32,g34)
    c: PointOnObject(g33,g34)
    c: PointOnObject(g34,g-1)
    c: Diameter(g34) = 7
    c: Vertical(g31)
    c: DistanceX(g34,g-1) = 8
    c: Coincident(g35,g36)
    c: Coincident(g36,g37)
    c: Coincident(g37,g38)
    c: Coincident(g38,g39)
    c: Coincident(g39,g40)
    c: Coincident(g40,g35)
    c: Equal(g35, g36-g40) x5
    c: PointOnObject(g35,g41)
    c: PointOnObject(g36,g41)
    c: PointOnObject(g37,g41)
    c: PointOnObject(g38,g41)
    c: PointOnObject(g39,g41)
    c: PointOnObject(g40,g41)
    c: Coincident(g42,g43)
    c: Coincident(g43,g44)
    c: Coincident(g44,g45)
    c: Coincident(g45,g46)
    c: Coincident(g46,g47)
    c: Coincident(g47,g42)
    c: Equal(g42, g43-g47) x5
    c: PointOnObject(g42,g48)
    c: PointOnObject(g43,g48)
    c: PointOnObject(g44,g48)
    c: PointOnObject(g45,g48)
    c: PointOnObject(g46,g48)
    c: PointOnObject(g47,g48)
    c: Equal(g41,g48)
    c: Diameter(g41) = 7
    c: Vertical(g39)
    c: Vertical(g43)
    c: Distance(g-2,g39) = 1
    c: Symmetric(g38,g43,g-2)
    c: Distance(g41,g-1) = 7
FEATURE [Part::Extrusion] Extrude668  label="hex270"
  Base = -> Sketch677
  Dir = (0,-1,2e-16)
  DirMode = 2
  FaceMakerClass = Part::FaceMakerBullseye
  FaceMakerMode = 3
  LengthFwd = 10
  LengthRev = 0
  Placement = pos=(16,0,14) rot=(0,0,1;0rad)
  Solid = true
  Symmetric = false
FEATURE [Sketcher::SketchObject] Sketch678
  ArcFitTolerance = 1e-06
  FullyConstrained = true
  MakeInternals = false
  Placement = pos=(0,0,0) rot=(1,0,0;1.5708rad)
  sketch-geometry (49):
    g0: LineSegment StartX=1e-16 StartY=3.5 StartZ=0 EndX=-3.03109 EndY=1.75 EndZ=0
    g1: LineSegment StartX=-3.03109 StartY=1.75 StartZ=0 EndX=-3.03109 EndY=-1.75 EndZ=0
    g2: LineSegment StartX=-3.03109 StartY=-1.75 StartZ=0 EndX=-1e-16 EndY=-3.5 EndZ=0
    g3: LineSegment StartX=-1e-16 StartY=-3.5 StartZ=0 EndX=3.03109 EndY=-1.75 EndZ=0
    g4: LineSegment StartX=3.03109 StartY=-1.75 StartZ=0 EndX=3.03109 EndY=1.75 EndZ=0
    g5: LineSegment StartX=3.03109 StartY=1.75 StartZ=0 EndX=1e-16 EndY=3.5 EndZ=0
    g6: Circle [constr] CenterX=0 CenterY=0 CenterZ=0 NormalX=0 NormalY=0 NormalZ=1 AngleXU=0 Radius=3.5
    g7: LineSegment StartX=4.96892 StartY=-1.75002 StartZ=0 EndX=8.00002 EndY=-3.5 EndZ=0
    g8: LineSegment StartX=8.00002 StartY=-3.5 StartZ=0 EndX=11.0311 EndY=-1.74998 EndZ=0
    g9: LineSegment StartX=11.0311 StartY=-1.74998 StartZ=0 EndX=11.0311 EndY=1.75002 EndZ=0
    g10: LineSegment StartX=11.0311 StartY=1.75002 StartZ=0 EndX=7.99998 EndY=3.5 EndZ=0
    g11: LineSegment StartX=7.99998 StartY=3.5 StartZ=0 EndX=4.9689 EndY=1.74998 EndZ=0
    g12: LineSegment StartX=4.9689 StartY=1.74998 StartZ=0 EndX=4.96892 EndY=-1.75002 EndZ=0
    g13: Circle [constr] CenterX=8 CenterY=0 CenterZ=0 NormalX=0 NormalY=0 NormalZ=1 AngleXU=0 Radius=3.5
    g14: LineSegment StartX=4.03109 StartY=3.5 StartZ=0 EndX=7.06218 EndY=5.25 EndZ=0
    g15: LineSegment StartX=7.06218 StartY=5.25 StartZ=0 EndX=7.06218 EndY=8.75 EndZ=0
    g16: LineSegment StartX=7.06218 StartY=8.75 StartZ=0 EndX=4.03109 EndY=10.5 EndZ=0
    g17: LineSegment StartX=4.03109 StartY=10.5 StartZ=0 EndX=1 EndY=8.75 EndZ=0
    g18: LineSegment StartX=1 StartY=8.75 StartZ=0 EndX=1 EndY=5.25 EndZ=0
    g19: LineSegment StartX=1 StartY=5.25 StartZ=0 EndX=4.03109 EndY=3.5 EndZ=0
    g20: Circle [constr] CenterX=4.03109 CenterY=7 CenterZ=0 NormalX=0 NormalY=0 NormalZ=1 AngleXU=0 Radius=3.5
    g21: LineSegment StartX=-1 StartY=5.25 StartZ=0 EndX=-1 EndY=8.75 EndZ=0
    g22: LineSegment StartX=-1 StartY=8.75 StartZ=0 EndX=-4.03109 EndY=10.5 EndZ=0
    g23: LineSegment StartX=-4.03109 StartY=10.5 StartZ=0 EndX=-7.06218 EndY=8.75 EndZ=0
    g24: LineSegment StartX=-7.06218 StartY=8.75 StartZ=0 EndX=-7.06218 EndY=5.25 EndZ=0
    g25: LineSegment StartX=-7.06218 StartY=5.25 StartZ=0 EndX=-4.03109 EndY=3.5 EndZ=0
    g26: LineSegment StartX=-4.03109 StartY=3.5 StartZ=0 EndX=-1 EndY=5.25 EndZ=0
    g27: Circle [constr] CenterX=-4.03109 CenterY=7 CenterZ=0 NormalX=0 NormalY=0 NormalZ=1 AngleXU=0 Radius=3.5
    g28: LineSegment StartX=-4.96891 StartY=-1.75 StartZ=0 EndX=-4.96891 EndY=1.75 EndZ=0
    g29: LineSegment StartX=-4.96891 StartY=1.75 StartZ=0 EndX=-8 EndY=3.5 EndZ=0
    g30: LineSegment StartX=-8 StartY=3.5 StartZ=0 EndX=-11.0311 EndY=1.75 EndZ=0
    g31: LineSegment StartX=-11.0311 StartY=1.75 StartZ=0 EndX=-11.0311 EndY=-1.75 EndZ=0
    g32: LineSegment StartX=-11.0311 StartY=-1.75 StartZ=0 EndX=-8 EndY=-3.5 EndZ=0
    g33: LineSegment StartX=-8 StartY=-3.5 StartZ=0 EndX=-4.96891 EndY=-1.75 EndZ=0
    g34: Circle [constr] CenterX=-8 CenterY=0 CenterZ=0 NormalX=0 NormalY=0 NormalZ=1 AngleXU=0 Radius=3.5
    g35: LineSegment StartX=-4.03109 StartY=-3.5 StartZ=0 EndX=-7.06218 EndY=-5.25 EndZ=0
    g36: LineSegment StartX=-7.06218 StartY=-5.25 StartZ=0 EndX=-7.06218 EndY=-8.75 EndZ=0
    g37: LineSegment StartX=-7.06218 StartY=-8.75 StartZ=0 EndX=-4.03109 EndY=-10.5 EndZ=0
    g38: LineSegment StartX=-4.03109 StartY=-10.5 StartZ=0 EndX=-1 EndY=-8.75 EndZ=0
    g39: LineSegment StartX=-1 StartY=-8.75 StartZ=0 EndX=-1 EndY=-5.25 EndZ=0
    g40: LineSegment StartX=-1 StartY=-5.25 StartZ=0 EndX=-4.03109 EndY=-3.5 EndZ=0
    g41: Circle [constr] CenterX=-4.03109 CenterY=-7 CenterZ=0 NormalX=0 NormalY=0 NormalZ=1 AngleXU=0 Radius=3.5
    g42: LineSegment StartX=4.03109 StartY=-3.5 StartZ=0 EndX=1 EndY=-5.25 EndZ=0
    g43: LineSegment StartX=1 StartY=-5.25 StartZ=0 EndX=1 EndY=-8.75 EndZ=0
    g44: LineSegment StartX=1 StartY=-8.75 StartZ=0 EndX=4.03109 EndY=-10.5 EndZ=0
    g45: LineSegment StartX=4.03109 StartY=-10.5 StartZ=0 EndX=7.06218 EndY=-8.75 EndZ=0
    g46: LineSegment StartX=7.06218 StartY=-8.75 StartZ=0 EndX=7.06218 EndY=-5.25 EndZ=0
    g47: LineSegment StartX=7.06218 StartY=-5.25 StartZ=0 EndX=4.03109 EndY=-3.5 EndZ=0
    g48: Circle [constr] CenterX=4.03109 CenterY=-7 CenterZ=0 NormalX=0 NormalY=0 NormalZ=1 AngleXU=0 Radius=3.5
  constraints (117):
    c: Coincident(g0,g1)
    c: Coincident(g1,g2)
    c: Coincident(g2,g3)
    c: Coincident(g3,g4)
    c: Coincident(g4,g5)
    c: Coincident(g5,g0)
    c: Equal(g0, g1-g5) x5
    c: PointOnObject(g0,g6)
    c: PointOnObject(g1,g6)
    c: PointOnObject(g2,g6)
    c: PointOnObject(g3,g6)
    c: PointOnObject(g4,g6)
    c: PointOnObject(g5,g6)
    c: Coincident(g6,g-1)
    c: Diameter(g6) = 7
    c: PointOnObject(g0,g-2)
    c: Coincident(g7,g8)
    c: Coincident(g8,g9)
    c: Coincident(g9,g10)
    c: Coincident(g10,g11)
    c: Coincident(g11,g12)
    c: Coincident(g12,g7)
    c: Equal(g7, g8-g12) x5
    c: PointOnObject(g7,g13)
    c: PointOnObject(g8,g13)
    c: PointOnObject(g9,g13)
    c: PointOnObject(g10,g13)
    c: PointOnObject(g11,g13)
    c: PointOnObject(g12,g13)
    c: PointOnObject(g13,g-1)
    c: Diameter(g13) = 7
    c: Distance(g6,g13) = 8
    c: Horizontal(g0,g10)
    c: Coincident(g14,g15)
    c: Coincident(g15,g16)
    c: Coincident(g16,g17)
    c: Coincident(g17,g18)
    c: Coincident(g18,g19)
    c: Coincident(g19,g14)
    c: Equal(g14, g15-g19) x5
    c: PointOnObject(g14,g20)
    c: PointOnObject(g15,g20)
    c: PointOnObject(g16,g20)
    c: PointOnObject(g17,g20)
    c: PointOnObject(g18,g20)
    c: PointOnObject(g19,g20)
    c: Diameter(g20) = 7
    c: DistanceY(g-1,g20) = 7
    c: Vertical(g18)
    c: Distance(g17,g-2) = 1
    c: Coincident(g21,g22)
    c: Coincident(g22,g23)
    c: Coincident(g23,g24)
    c: Coincident(g24,g25)
    c: Coincident(g25,g26)
    c: Coincident(g26,g21)
    c: Equal(g21, g22-g26) x5
    c: PointOnObject(g21,g27)
    c: PointOnObject(g22,g27)
    c: PointOnObject(g23,g27)
    c: PointOnObject(g24,g27)
    c: PointOnObject(g25,g27)
    c: PointOnObject(g26,g27)
    c: Diameter(g27) = 7
    c: DistanceY(g-1,g27) = 7
    c: DistanceX(g21,g-1) = 1
    c: Vertical(g21)
    c: Coincident(g28,g29)
    c: Coincident(g29,g30)
    c: Coincident(g30,g31)
    c: Coincident(g31,g32)
    c: Coincident(g32,g33)
    c: Coincident(g33,g28)
    c: Equal(g28, g29-g33) x5
    c: PointOnObject(g28,g34)
    c: PointOnObject(g29,g34)
    c: PointOnObject(g30,g34)
    c: PointOnObject(g31,g34)
    c: PointOnObject(g32,g34)
    c: PointOnObject(g33,g34)
    c: PointOnObject(g34,g-1)
    c: Diameter(g34) = 7
    c: Vertical(g31)
    c: DistanceX(g34,g-1) = 8
    c: Coincident(g35,g36)
    c: Coincident(g36,g37)
    c: Coincident(g37,g38)
    c: Coincident(g38,g39)
    c: Coincident(g39,g40)
    c: Coincident(g40,g35)
    c: Equal(g35, g36-g40) x5
    c: PointOnObject(g35,g41)
    c: PointOnObject(g36,g41)
    c: PointOnObject(g37,g41)
    c: PointOnObject(g38,g41)
    c: PointOnObject(g39,g41)
    c: PointOnObject(g40,g41)
    c: Coincident(g42,g43)
    c: Coincident(g43,g44)
    c: Coincident(g44,g45)
    c: Coincident(g45,g46)
    c: Coincident(g46,g47)
    c: Coincident(g47,g42)
    c: Equal(g42, g43-g47) x5
    c: PointOnObject(g42,g48)
    c: PointOnObject(g43,g48)
    c: PointOnObject(g44,g48)
    c: PointOnObject(g45,g48)
    c: PointOnObject(g46,g48)
    c: PointOnObject(g47,g48)
    c: Equal(g41,g48)
    c: Diameter(g41) = 7
    c: Vertical(g39)
    c: Vertical(g43)
    c: Distance(g-2,g39) = 1
    c: Symmetric(g38,g43,g-2)
    c: Distance(g41,g-1) = 7
FEATURE [Part::Extrusion] Extrude669  label="hex271"
  Base = -> Sketch678
  Dir = (0,-1,2e-16)
  DirMode = 2
  FaceMakerClass = Part::FaceMakerBullseye
  FaceMakerMode = 3
  LengthFwd = 10
  LengthRev = 0
  Placement = pos=(-20,0,-7) rot=(0,0,1;0rad)
  Solid = true
  Symmetric = false
FEATURE [Sketcher::SketchObject] Sketch679
  ArcFitTolerance = 1e-06
  FullyConstrained = true
  MakeInternals = false
  Placement = pos=(0,0,0) rot=(1,0,0;1.5708rad)
  sketch-geometry (49):
    g0: LineSegment StartX=1e-16 StartY=3.5 StartZ=0 EndX=-3.03109 EndY=1.75 EndZ=0
    g1: LineSegment StartX=-3.03109 StartY=1.75 StartZ=0 EndX=-3.03109 EndY=-1.75 EndZ=0
    g2: LineSegment StartX=-3.03109 StartY=-1.75 StartZ=0 EndX=-1e-16 EndY=-3.5 EndZ=0
    g3: LineSegment StartX=-1e-16 StartY=-3.5 StartZ=0 EndX=3.03109 EndY=-1.75 EndZ=0
    g4: LineSegment StartX=3.03109 StartY=-1.75 StartZ=0 EndX=3.03109 EndY=1.75 EndZ=0
    g5: LineSegment StartX=3.03109 StartY=1.75 StartZ=0 EndX=1e-16 EndY=3.5 EndZ=0
    g6: Circle [constr] CenterX=0 CenterY=0 CenterZ=0 NormalX=0 NormalY=0 NormalZ=1 AngleXU=0 Radius=3.5
    g7: LineSegment StartX=4.96892 StartY=-1.75002 StartZ=0 EndX=8.00002 EndY=-3.5 EndZ=0
    g8: LineSegment StartX=8.00002 StartY=-3.5 StartZ=0 EndX=11.0311 EndY=-1.74998 EndZ=0
    g9: LineSegment StartX=11.0311 StartY=-1.74998 StartZ=0 EndX=11.0311 EndY=1.75002 EndZ=0
    g10: LineSegment StartX=11.0311 StartY=1.75002 StartZ=0 EndX=7.99998 EndY=3.5 EndZ=0
    g11: LineSegment StartX=7.99998 StartY=3.5 StartZ=0 EndX=4.9689 EndY=1.74998 EndZ=0
    g12: LineSegment StartX=4.9689 StartY=1.74998 StartZ=0 EndX=4.96892 EndY=-1.75002 EndZ=0
    g13: Circle [constr] CenterX=8 CenterY=0 CenterZ=0 NormalX=0 NormalY=0 NormalZ=1 AngleXU=0 Radius=3.5
    g14: LineSegment StartX=4.03109 StartY=3.5 StartZ=0 EndX=7.06218 EndY=5.25 EndZ=0
    g15: LineSegment StartX=7.06218 StartY=5.25 StartZ=0 EndX=7.06218 EndY=8.75 EndZ=0
    g16: LineSegment StartX=7.06218 StartY=8.75 StartZ=0 EndX=4.03109 EndY=10.5 EndZ=0
    g17: LineSegment StartX=4.03109 StartY=10.5 StartZ=0 EndX=1 EndY=8.75 EndZ=0
    g18: LineSegment StartX=1 StartY=8.75 StartZ=0 EndX=1 EndY=5.25 EndZ=0
    g19: LineSegment StartX=1 StartY=5.25 StartZ=0 EndX=4.03109 EndY=3.5 EndZ=0
    g20: Circle [constr] CenterX=4.03109 CenterY=7 CenterZ=0 NormalX=0 NormalY=0 NormalZ=1 AngleXU=0 Radius=3.5
    g21: LineSegment StartX=-1 StartY=5.25 StartZ=0 EndX=-1 EndY=8.75 EndZ=0
    g22: LineSegment StartX=-1 StartY=8.75 StartZ=0 EndX=-4.03109 EndY=10.5 EndZ=0
    g23: LineSegment StartX=-4.03109 StartY=10.5 StartZ=0 EndX=-7.06218 EndY=8.75 EndZ=0
    g24: LineSegment StartX=-7.06218 StartY=8.75 StartZ=0 EndX=-7.06218 EndY=5.25 EndZ=0
    g25: LineSegment StartX=-7.06218 StartY=5.25 StartZ=0 EndX=-4.03109 EndY=3.5 EndZ=0
    g26: LineSegment StartX=-4.03109 StartY=3.5 StartZ=0 EndX=-1 EndY=5.25 EndZ=0
    g27: Circle [constr] CenterX=-4.03109 CenterY=7 CenterZ=0 NormalX=0 NormalY=0 NormalZ=1 AngleXU=0 Radius=3.5
    g28: LineSegment StartX=-4.96891 StartY=-1.75 StartZ=0 EndX=-4.96891 EndY=1.75 EndZ=0
    g29: LineSegment StartX=-4.96891 StartY=1.75 StartZ=0 EndX=-8 EndY=3.5 EndZ=0
    g30: LineSegment StartX=-8 StartY=3.5 StartZ=0 EndX=-11.0311 EndY=1.75 EndZ=0
    g31: LineSegment StartX=-11.0311 StartY=1.75 StartZ=0 EndX=-11.0311 EndY=-1.75 EndZ=0
    g32: LineSegment StartX=-11.0311 StartY=-1.75 StartZ=0 EndX=-8 EndY=-3.5 EndZ=0
    g33: LineSegment StartX=-8 StartY=-3.5 StartZ=0 EndX=-4.96891 EndY=-1.75 EndZ=0
    g34: Circle [constr] CenterX=-8 CenterY=0 CenterZ=0 NormalX=0 NormalY=0 NormalZ=1 AngleXU=0 Radius=3.5
    g35: LineSegment StartX=-4.03109 StartY=-3.5 StartZ=0 EndX=-7.06218 EndY=-5.25 EndZ=0
    g36: LineSegment StartX=-7.06218 StartY=-5.25 StartZ=0 EndX=-7.06218 EndY=-8.75 EndZ=0
    g37: LineSegment StartX=-7.06218 StartY=-8.75 StartZ=0 EndX=-4.03109 EndY=-10.5 EndZ=0
    g38: LineSegment StartX=-4.03109 StartY=-10.5 StartZ=0 EndX=-1 EndY=-8.75 EndZ=0
    g39: LineSegment StartX=-1 StartY=-8.75 StartZ=0 EndX=-1 EndY=-5.25 EndZ=0
    g40: LineSegment StartX=-1 StartY=-5.25 StartZ=0 EndX=-4.03109 EndY=-3.5 EndZ=0
    g41: Circle [constr] CenterX=-4.03109 CenterY=-7 CenterZ=0 NormalX=0 NormalY=0 NormalZ=1 AngleXU=0 Radius=3.5
    g42: LineSegment StartX=4.03109 StartY=-3.5 StartZ=0 EndX=1 EndY=-5.25 EndZ=0
    g43: LineSegment StartX=1 StartY=-5.25 StartZ=0 EndX=1 EndY=-8.75 EndZ=0
    g44: LineSegment StartX=1 StartY=-8.75 StartZ=0 EndX=4.03109 EndY=-10.5 EndZ=0
    g45: LineSegment StartX=4.03109 StartY=-10.5 StartZ=0 EndX=7.06218 EndY=-8.75 EndZ=0
    g46: LineSegment StartX=7.06218 StartY=-8.75 StartZ=0 EndX=7.06218 EndY=-5.25 EndZ=0
    g47: LineSegment StartX=7.06218 StartY=-5.25 StartZ=0 EndX=4.03109 EndY=-3.5 EndZ=0
    g48: Circle [constr] CenterX=4.03109 CenterY=-7 CenterZ=0 NormalX=0 NormalY=0 NormalZ=1 AngleXU=0 Radius=3.5
  constraints (117):
    c: Coincident(g0,g1)
    c: Coincident(g1,g2)
    c: Coincident(g2,g3)
    c: Coincident(g3,g4)
    c: Coincident(g4,g5)
    c: Coincident(g5,g0)
    c: Equal(g0, g1-g5) x5
    c: PointOnObject(g0,g6)
    c: PointOnObject(g1,g6)
    c: PointOnObject(g2,g6)
    c: PointOnObject(g3,g6)
    c: PointOnObject(g4,g6)
    c: PointOnObject(g5,g6)
    c: Coincident(g6,g-1)
    c: Diameter(g6) = 7
    c: PointOnObject(g0,g-2)
    c: Coincident(g7,g8)
    c: Coincident(g8,g9)
    c: Coincident(g9,g10)
    c: Coincident(g10,g11)
    c: Coincident(g11,g12)
    c: Coincident(g12,g7)
    c: Equal(g7, g8-g12) x5
    c: PointOnObject(g7,g13)
    c: PointOnObject(g8,g13)
    c: PointOnObject(g9,g13)
    c: PointOnObject(g10,g13)
    c: PointOnObject(g11,g13)
    c: PointOnObject(g12,g13)
    c: PointOnObject(g13,g-1)
    c: Diameter(g13) = 7
    c: Distance(g6,g13) = 8
    c: Horizontal(g0,g10)
    c: Coincident(g14,g15)
    c: Coincident(g15,g16)
    c: Coincident(g16,g17)
    c: Coincident(g17,g18)
    c: Coincident(g18,g19)
    c: Coincident(g19,g14)
    c: Equal(g14, g15-g19) x5
    c: PointOnObject(g14,g20)
    c: PointOnObject(g15,g20)
    c: PointOnObject(g16,g20)
    c: PointOnObject(g17,g20)
    c: PointOnObject(g18,g20)
    c: PointOnObject(g19,g20)
    c: Diameter(g20) = 7
    c: DistanceY(g-1,g20) = 7
    c: Vertical(g18)
    c: Distance(g17,g-2) = 1
    c: Coincident(g21,g22)
    c: Coincident(g22,g23)
    c: Coincident(g23,g24)
    c: Coincident(g24,g25)
    c: Coincident(g25,g26)
    c: Coincident(g26,g21)
    c: Equal(g21, g22-g26) x5
    c: PointOnObject(g21,g27)
    c: PointOnObject(g22,g27)
    c: PointOnObject(g23,g27)
    c: PointOnObject(g24,g27)
    c: PointOnObject(g25,g27)
    c: PointOnObject(g26,g27)
    c: Diameter(g27) = 7
    c: DistanceY(g-1,g27) = 7
    c: DistanceX(g21,g-1) = 1
    c: Vertical(g21)
    c: Coincident(g28,g29)
    c: Coincident(g29,g30)
    c: Coincident(g30,g31)
    c: Coincident(g31,g32)
    c: Coincident(g32,g33)
    c: Coincident(g33,g28)
    c: Equal(g28, g29-g33) x5
    c: PointOnObject(g28,g34)
    c: PointOnObject(g29,g34)
    c: PointOnObject(g30,g34)
    c: PointOnObject(g31,g34)
    c: PointOnObject(g32,g34)
    c: PointOnObject(g33,g34)
    c: PointOnObject(g34,g-1)
    c: Diameter(g34) = 7
    c: Vertical(g31)
    c: DistanceX(g34,g-1) = 8
    c: Coincident(g35,g36)
    c: Coincident(g36,g37)
    c: Coincident(g37,g38)
    c: Coincident(g38,g39)
    c: Coincident(g39,g40)
    c: Coincident(g40,g35)
    c: Equal(g35, g36-g40) x5
    c: PointOnObject(g35,g41)
    c: PointOnObject(g36,g41)
    c: PointOnObject(g37,g41)
    c: PointOnObject(g38,g41)
    c: PointOnObject(g39,g41)
    c: PointOnObject(g40,g41)
    c: Coincident(g42,g43)
    c: Coincident(g43,g44)
    c: Coincident(g44,g45)
    c: Coincident(g45,g46)
    c: Coincident(g46,g47)
    c: Coincident(g47,g42)
    c: Equal(g42, g43-g47) x5
    c: PointOnObject(g42,g48)
    c: PointOnObject(g43,g48)
    c: PointOnObject(g44,g48)
    c: PointOnObject(g45,g48)
    c: PointOnObject(g46,g48)
    c: PointOnObject(g47,g48)
    c: Equal(g41,g48)
    c: Diameter(g41) = 7
    c: Vertical(g39)
    c: Vertical(g43)
    c: Distance(g-2,g39) = 1
    c: Symmetric(g38,g43,g-2)
    c: Distance(g41,g-1) = 7
FEATURE [Part::Extrusion] Extrude670  label="hex272"
  Base = -> Sketch679
  Dir = (0,-1,2e-16)
  DirMode = 2
  FaceMakerClass = Part::FaceMakerBullseye
  FaceMakerMode = 3
  LengthFwd = 10
  LengthRev = 0
  Placement = pos=(-16,0,14) rot=(0,0,1;0rad)
  Solid = true
  Symmetric = false
FEATURE [Sketcher::SketchObject] Sketch680
  ArcFitTolerance = 1e-06
  FullyConstrained = true
  MakeInternals = false
  Placement = pos=(0,0,0) rot=(1,0,0;1.5708rad)
  sketch-geometry (49):
    g0: LineSegment StartX=1e-16 StartY=3.5 StartZ=0 EndX=-3.03109 EndY=1.75 EndZ=0
    g1: LineSegment StartX=-3.03109 StartY=1.75 StartZ=0 EndX=-3.03109 EndY=-1.75 EndZ=0
    g2: LineSegment StartX=-3.03109 StartY=-1.75 StartZ=0 EndX=-1e-16 EndY=-3.5 EndZ=0
    g3: LineSegment StartX=-1e-16 StartY=-3.5 StartZ=0 EndX=3.03109 EndY=-1.75 EndZ=0
    g4: LineSegment StartX=3.03109 StartY=-1.75 StartZ=0 EndX=3.03109 EndY=1.75 EndZ=0
    g5: LineSegment StartX=3.03109 StartY=1.75 StartZ=0 EndX=1e-16 EndY=3.5 EndZ=0
    g6: Circle [constr] CenterX=0 CenterY=0 CenterZ=0 NormalX=0 NormalY=0 NormalZ=1 AngleXU=0 Radius=3.5
    g7: LineSegment StartX=4.96892 StartY=-1.75002 StartZ=0 EndX=8.00002 EndY=-3.5 EndZ=0
    g8: LineSegment StartX=8.00002 StartY=-3.5 StartZ=0 EndX=11.0311 EndY=-1.74998 EndZ=0
    g9: LineSegment StartX=11.0311 StartY=-1.74998 StartZ=0 EndX=11.0311 EndY=1.75002 EndZ=0
    g10: LineSegment StartX=11.0311 StartY=1.75002 StartZ=0 EndX=7.99998 EndY=3.5 EndZ=0
    g11: LineSegment StartX=7.99998 StartY=3.5 StartZ=0 EndX=4.9689 EndY=1.74998 EndZ=0
    g12: LineSegment StartX=4.9689 StartY=1.74998 StartZ=0 EndX=4.96892 EndY=-1.75002 EndZ=0
    g13: Circle [constr] CenterX=8 CenterY=0 CenterZ=0 NormalX=0 NormalY=0 NormalZ=1 AngleXU=0 Radius=3.5
    g14: LineSegment StartX=4.03109 StartY=3.5 StartZ=0 EndX=7.06218 EndY=5.25 EndZ=0
    g15: LineSegment StartX=7.06218 StartY=5.25 StartZ=0 EndX=7.06218 EndY=8.75 EndZ=0
    g16: LineSegment StartX=7.06218 StartY=8.75 StartZ=0 EndX=4.03109 EndY=10.5 EndZ=0
    g17: LineSegment StartX=4.03109 StartY=10.5 StartZ=0 EndX=1 EndY=8.75 EndZ=0
    g18: LineSegment StartX=1 StartY=8.75 StartZ=0 EndX=1 EndY=5.25 EndZ=0
    g19: LineSegment StartX=1 StartY=5.25 StartZ=0 EndX=4.03109 EndY=3.5 EndZ=0
    g20: Circle [constr] CenterX=4.03109 CenterY=7 CenterZ=0 NormalX=0 NormalY=0 NormalZ=1 AngleXU=0 Radius=3.5
    g21: LineSegment StartX=-1 StartY=5.25 StartZ=0 EndX=-1 EndY=8.75 EndZ=0
    g22: LineSegment StartX=-1 StartY=8.75 StartZ=0 EndX=-4.03109 EndY=10.5 EndZ=0
    g23: LineSegment StartX=-4.03109 StartY=10.5 StartZ=0 EndX=-7.06218 EndY=8.75 EndZ=0
    g24: LineSegment StartX=-7.06218 StartY=8.75 StartZ=0 EndX=-7.06218 EndY=5.25 EndZ=0
    g25: LineSegment StartX=-7.06218 StartY=5.25 StartZ=0 EndX=-4.03109 EndY=3.5 EndZ=0
    g26: LineSegment StartX=-4.03109 StartY=3.5 StartZ=0 EndX=-1 EndY=5.25 EndZ=0
    g27: Circle [constr] CenterX=-4.03109 CenterY=7 CenterZ=0 NormalX=0 NormalY=0 NormalZ=1 AngleXU=0 Radius=3.5
    g28: LineSegment StartX=-4.96891 StartY=-1.75 StartZ=0 EndX=-4.96891 EndY=1.75 EndZ=0
    g29: LineSegment StartX=-4.96891 StartY=1.75 StartZ=0 EndX=-8 EndY=3.5 EndZ=0
    g30: LineSegment StartX=-8 StartY=3.5 StartZ=0 EndX=-11.0311 EndY=1.75 EndZ=0
    g31: LineSegment StartX=-11.0311 StartY=1.75 StartZ=0 EndX=-11.0311 EndY=-1.75 EndZ=0
    g32: LineSegment StartX=-11.0311 StartY=-1.75 StartZ=0 EndX=-8 EndY=-3.5 EndZ=0
    g33: LineSegment StartX=-8 StartY=-3.5 StartZ=0 EndX=-4.96891 EndY=-1.75 EndZ=0
    g34: Circle [constr] CenterX=-8 CenterY=0 CenterZ=0 NormalX=0 NormalY=0 NormalZ=1 AngleXU=0 Radius=3.5
    g35: LineSegment StartX=-4.03109 StartY=-3.5 StartZ=0 EndX=-7.06218 EndY=-5.25 EndZ=0
    g36: LineSegment StartX=-7.06218 StartY=-5.25 StartZ=0 EndX=-7.06218 EndY=-8.75 EndZ=0
    g37: LineSegment StartX=-7.06218 StartY=-8.75 StartZ=0 EndX=-4.03109 EndY=-10.5 EndZ=0
    g38: LineSegment StartX=-4.03109 StartY=-10.5 StartZ=0 EndX=-1 EndY=-8.75 EndZ=0
    g39: LineSegment StartX=-1 StartY=-8.75 StartZ=0 EndX=-1 EndY=-5.25 EndZ=0
    g40: LineSegment StartX=-1 StartY=-5.25 StartZ=0 EndX=-4.03109 EndY=-3.5 EndZ=0
    g41: Circle [constr] CenterX=-4.03109 CenterY=-7 CenterZ=0 NormalX=0 NormalY=0 NormalZ=1 AngleXU=0 Radius=3.5
    g42: LineSegment StartX=4.03109 StartY=-3.5 StartZ=0 EndX=1 EndY=-5.25 EndZ=0
    g43: LineSegment StartX=1 StartY=-5.25 StartZ=0 EndX=1 EndY=-8.75 EndZ=0
    g44: LineSegment StartX=1 StartY=-8.75 StartZ=0 EndX=4.03109 EndY=-10.5 EndZ=0
    g45: LineSegment StartX=4.03109 StartY=-10.5 StartZ=0 EndX=7.06218 EndY=-8.75 EndZ=0
    g46: LineSegment StartX=7.06218 StartY=-8.75 StartZ=0 EndX=7.06218 EndY=-5.25 EndZ=0
    g47: LineSegment StartX=7.06218 StartY=-5.25 StartZ=0 EndX=4.03109 EndY=-3.5 EndZ=0
    g48: Circle [constr] CenterX=4.03109 CenterY=-7 CenterZ=0 NormalX=0 NormalY=0 NormalZ=1 AngleXU=0 Radius=3.5
  constraints (117):
    c: Coincident(g0,g1)
    c: Coincident(g1,g2)
    c: Coincident(g2,g3)
    c: Coincident(g3,g4)
    c: Coincident(g4,g5)
    c: Coincident(g5,g0)
    c: Equal(g0, g1-g5) x5
    c: PointOnObject(g0,g6)
    c: PointOnObject(g1,g6)
    c: PointOnObject(g2,g6)
    c: PointOnObject(g3,g6)
    c: PointOnObject(g4,g6)
    c: PointOnObject(g5,g6)
    c: Coincident(g6,g-1)
    c: Diameter(g6) = 7
    c: PointOnObject(g0,g-2)
    c: Coincident(g7,g8)
    c: Coincident(g8,g9)
    c: Coincident(g9,g10)
    c: Coincident(g10,g11)
    c: Coincident(g11,g12)
    c: Coincident(g12,g7)
    c: Equal(g7, g8-g12) x5
    c: PointOnObject(g7,g13)
    c: PointOnObject(g8,g13)
    c: PointOnObject(g9,g13)
    c: PointOnObject(g10,g13)
    c: PointOnObject(g11,g13)
    c: PointOnObject(g12,g13)
    c: PointOnObject(g13,g-1)
    c: Diameter(g13) = 7
    c: Distance(g6,g13) = 8
    c: Horizontal(g0,g10)
    c: Coincident(g14,g15)
    c: Coincident(g15,g16)
    c: Coincident(g16,g17)
    c: Coincident(g17,g18)
    c: Coincident(g18,g19)
    c: Coincident(g19,g14)
    c: Equal(g14, g15-g19) x5
    c: PointOnObject(g14,g20)
    c: PointOnObject(g15,g20)
    c: PointOnObject(g16,g20)
    c: PointOnObject(g17,g20)
    c: PointOnObject(g18,g20)
    c: PointOnObject(g19,g20)
    c: Diameter(g20) = 7
    c: DistanceY(g-1,g20) = 7
    c: Vertical(g18)
    c: Distance(g17,g-2) = 1
    c: Coincident(g21,g22)
    c: Coincident(g22,g23)
    c: Coincident(g23,g24)
    c: Coincident(g24,g25)
    c: Coincident(g25,g26)
    c: Coincident(g26,g21)
    c: Equal(g21, g22-g26) x5
    c: PointOnObject(g21,g27)
    c: PointOnObject(g22,g27)
    c: PointOnObject(g23,g27)
    c: PointOnObject(g24,g27)
    c: PointOnObject(g25,g27)
    c: PointOnObject(g26,g27)
    c: Diameter(g27) = 7
    c: DistanceY(g-1,g27) = 7
    c: DistanceX(g21,g-1) = 1
    c: Vertical(g21)
    c: Coincident(g28,g29)
    c: Coincident(g29,g30)
    c: Coincident(g30,g31)
    c: Coincident(g31,g32)
    c: Coincident(g32,g33)
    c: Coincident(g33,g28)
    c: Equal(g28, g29-g33) x5
    c: PointOnObject(g28,g34)
    c: PointOnObject(g29,g34)
    c: PointOnObject(g30,g34)
    c: PointOnObject(g31,g34)
    c: PointOnObject(g32,g34)
    c: PointOnObject(g33,g34)
    c: PointOnObject(g34,g-1)
    c: Diameter(g34) = 7
    c: Vertical(g31)
    c: DistanceX(g34,g-1) = 8
    c: Coincident(g35,g36)
    c: Coincident(g36,g37)
    c: Coincident(g37,g38)
    c: Coincident(g38,g39)
    c: Coincident(g39,g40)
    c: Coincident(g40,g35)
    c: Equal(g35, g36-g40) x5
    c: PointOnObject(g35,g41)
    c: PointOnObject(g36,g41)
    c: PointOnObject(g37,g41)
    c: PointOnObject(g38,g41)
    c: PointOnObject(g39,g41)
    c: PointOnObject(g40,g41)
    c: Coincident(g42,g43)
    c: Coincident(g43,g44)
    c: Coincident(g44,g45)
    c: Coincident(g45,g46)
    c: Coincident(g46,g47)
    c: Coincident(g47,g42)
    c: Equal(g42, g43-g47) x5
    c: PointOnObject(g42,g48)
    c: PointOnObject(g43,g48)
    c: PointOnObject(g44,g48)
    c: PointOnObject(g45,g48)
    c: PointOnObject(g46,g48)
    c: PointOnObject(g47,g48)
    c: Equal(g41,g48)
    c: Diameter(g41) = 7
    c: Vertical(g39)
    c: Vertical(g43)
    c: Distance(g-2,g39) = 1
    c: Symmetric(g38,g43,g-2)
    c: Distance(g41,g-1) = 7
FEATURE [Part::Extrusion] Extrude671  label="hex273"
  Base = -> Sketch680
  Dir = (0,-1,2e-16)
  DirMode = 2
  FaceMakerClass = Part::FaceMakerBullseye
  FaceMakerMode = 3
  LengthFwd = 10
  LengthRev = 0
  Placement = pos=(-4,0,-21) rot=(0,0,1;0rad)
  Solid = true
  Symmetric = false
FEATURE [Sketcher::SketchObject] Sketch681
  ArcFitTolerance = 1e-06
  FullyConstrained = true
  MakeInternals = false
  Placement = pos=(0,0,0) rot=(1,0,0;1.5708rad)
  sketch-geometry (49):
    g0: LineSegment StartX=1e-16 StartY=3.5 StartZ=0 EndX=-3.03109 EndY=1.75 EndZ=0
    g1: LineSegment StartX=-3.03109 StartY=1.75 StartZ=0 EndX=-3.03109 EndY=-1.75 EndZ=0
    g2: LineSegment StartX=-3.03109 StartY=-1.75 StartZ=0 EndX=-1e-16 EndY=-3.5 EndZ=0
    g3: LineSegment StartX=-1e-16 StartY=-3.5 StartZ=0 EndX=3.03109 EndY=-1.75 EndZ=0
    g4: LineSegment StartX=3.03109 StartY=-1.75 StartZ=0 EndX=3.03109 EndY=1.75 EndZ=0
    g5: LineSegment StartX=3.03109 StartY=1.75 StartZ=0 EndX=1e-16 EndY=3.5 EndZ=0
    g6: Circle [constr] CenterX=0 CenterY=0 CenterZ=0 NormalX=0 NormalY=0 NormalZ=1 AngleXU=0 Radius=3.5
    g7: LineSegment StartX=4.96892 StartY=-1.75002 StartZ=0 EndX=8.00002 EndY=-3.5 EndZ=0
    g8: LineSegment StartX=8.00002 StartY=-3.5 StartZ=0 EndX=11.0311 EndY=-1.74998 EndZ=0
    g9: LineSegment StartX=11.0311 StartY=-1.74998 StartZ=0 EndX=11.0311 EndY=1.75002 EndZ=0
    g10: LineSegment StartX=11.0311 StartY=1.75002 StartZ=0 EndX=7.99998 EndY=3.5 EndZ=0
    g11: LineSegment StartX=7.99998 StartY=3.5 StartZ=0 EndX=4.9689 EndY=1.74998 EndZ=0
    g12: LineSegment StartX=4.9689 StartY=1.74998 StartZ=0 EndX=4.96892 EndY=-1.75002 EndZ=0
    g13: Circle [constr] CenterX=8 CenterY=0 CenterZ=0 NormalX=0 NormalY=0 NormalZ=1 AngleXU=0 Radius=3.5
    g14: LineSegment StartX=4.03109 StartY=3.5 StartZ=0 EndX=7.06218 EndY=5.25 EndZ=0
    g15: LineSegment StartX=7.06218 StartY=5.25 StartZ=0 EndX=7.06218 EndY=8.75 EndZ=0
    g16: LineSegment StartX=7.06218 StartY=8.75 StartZ=0 EndX=4.03109 EndY=10.5 EndZ=0
    g17: LineSegment StartX=4.03109 StartY=10.5 StartZ=0 EndX=1 EndY=8.75 EndZ=0
    g18: LineSegment StartX=1 StartY=8.75 StartZ=0 EndX=1 EndY=5.25 EndZ=0
    g19: LineSegment StartX=1 StartY=5.25 StartZ=0 EndX=4.03109 EndY=3.5 EndZ=0
    g20: Circle [constr] CenterX=4.03109 CenterY=7 CenterZ=0 NormalX=0 NormalY=0 NormalZ=1 AngleXU=0 Radius=3.5
    g21: LineSegment StartX=-1 StartY=5.25 StartZ=0 EndX=-1 EndY=8.75 EndZ=0
    g22: LineSegment StartX=-1 StartY=8.75 StartZ=0 EndX=-4.03109 EndY=10.5 EndZ=0
    g23: LineSegment StartX=-4.03109 StartY=10.5 StartZ=0 EndX=-7.06218 EndY=8.75 EndZ=0
    g24: LineSegment StartX=-7.06218 StartY=8.75 StartZ=0 EndX=-7.06218 EndY=5.25 EndZ=0
    g25: LineSegment StartX=-7.06218 StartY=5.25 StartZ=0 EndX=-4.03109 EndY=3.5 EndZ=0
    g26: LineSegment StartX=-4.03109 StartY=3.5 StartZ=0 EndX=-1 EndY=5.25 EndZ=0
    g27: Circle [constr] CenterX=-4.03109 CenterY=7 CenterZ=0 NormalX=0 NormalY=0 NormalZ=1 AngleXU=0 Radius=3.5
    g28: LineSegment StartX=-4.96891 StartY=-1.75 StartZ=0 EndX=-4.96891 EndY=1.75 EndZ=0
    g29: LineSegment StartX=-4.96891 StartY=1.75 StartZ=0 EndX=-8 EndY=3.5 EndZ=0
    g30: LineSegment StartX=-8 StartY=3.5 StartZ=0 EndX=-11.0311 EndY=1.75 EndZ=0
    g31: LineSegment StartX=-11.0311 StartY=1.75 StartZ=0 EndX=-11.0311 EndY=-1.75 EndZ=0
    g32: LineSegment StartX=-11.0311 StartY=-1.75 StartZ=0 EndX=-8 EndY=-3.5 EndZ=0
    g33: LineSegment StartX=-8 StartY=-3.5 StartZ=0 EndX=-4.96891 EndY=-1.75 EndZ=0
    g34: Circle [constr] CenterX=-8 CenterY=0 CenterZ=0 NormalX=0 NormalY=0 NormalZ=1 AngleXU=0 Radius=3.5
    g35: LineSegment StartX=-4.03109 StartY=-3.5 StartZ=0 EndX=-7.06218 EndY=-5.25 EndZ=0
    g36: LineSegment StartX=-7.06218 StartY=-5.25 StartZ=0 EndX=-7.06218 EndY=-8.75 EndZ=0
    g37: LineSegment StartX=-7.06218 StartY=-8.75 StartZ=0 EndX=-4.03109 EndY=-10.5 EndZ=0
    g38: LineSegment StartX=-4.03109 StartY=-10.5 StartZ=0 EndX=-1 EndY=-8.75 EndZ=0
    g39: LineSegment StartX=-1 StartY=-8.75 StartZ=0 EndX=-1 EndY=-5.25 EndZ=0
    g40: LineSegment StartX=-1 StartY=-5.25 StartZ=0 EndX=-4.03109 EndY=-3.5 EndZ=0
    g41: Circle [constr] CenterX=-4.03109 CenterY=-7 CenterZ=0 NormalX=0 NormalY=0 NormalZ=1 AngleXU=0 Radius=3.5
    g42: LineSegment StartX=4.03109 StartY=-3.5 StartZ=0 EndX=1 EndY=-5.25 EndZ=0
    g43: LineSegment StartX=1 StartY=-5.25 StartZ=0 EndX=1 EndY=-8.75 EndZ=0
    g44: LineSegment StartX=1 StartY=-8.75 StartZ=0 EndX=4.03109 EndY=-10.5 EndZ=0
    g45: LineSegment StartX=4.03109 StartY=-10.5 StartZ=0 EndX=7.06218 EndY=-8.75 EndZ=0
    g46: LineSegment StartX=7.06218 StartY=-8.75 StartZ=0 EndX=7.06218 EndY=-5.25 EndZ=0
    g47: LineSegment StartX=7.06218 StartY=-5.25 StartZ=0 EndX=4.03109 EndY=-3.5 EndZ=0
    g48: Circle [constr] CenterX=4.03109 CenterY=-7 CenterZ=0 NormalX=0 NormalY=0 NormalZ=1 AngleXU=0 Radius=3.5
  constraints (117):
    c: Coincident(g0,g1)
    c: Coincident(g1,g2)
    c: Coincident(g2,g3)
    c: Coincident(g3,g4)
    c: Coincident(g4,g5)
    c: Coincident(g5,g0)
    c: Equal(g0, g1-g5) x5
    c: PointOnObject(g0,g6)
    c: PointOnObject(g1,g6)
    c: PointOnObject(g2,g6)
    c: PointOnObject(g3,g6)
    c: PointOnObject(g4,g6)
    c: PointOnObject(g5,g6)
    c: Coincident(g6,g-1)
    c: Diameter(g6) = 7
    c: PointOnObject(g0,g-2)
    c: Coincident(g7,g8)
    c: Coincident(g8,g9)
    c: Coincident(g9,g10)
    c: Coincident(g10,g11)
    c: Coincident(g11,g12)
    c: Coincident(g12,g7)
    c: Equal(g7, g8-g12) x5
    c: PointOnObject(g7,g13)
    c: PointOnObject(g8,g13)
    c: PointOnObject(g9,g13)
    c: PointOnObject(g10,g13)
    c: PointOnObject(g11,g13)
    c: PointOnObject(g12,g13)
    c: PointOnObject(g13,g-1)
    c: Diameter(g13) = 7
    c: Distance(g6,g13) = 8
    c: Horizontal(g0,g10)
    c: Coincident(g14,g15)
    c: Coincident(g15,g16)
    c: Coincident(g16,g17)
    c: Coincident(g17,g18)
    c: Coincident(g18,g19)
    c: Coincident(g19,g14)
    c: Equal(g14, g15-g19) x5
    c: PointOnObject(g14,g20)
    c: PointOnObject(g15,g20)
    c: PointOnObject(g16,g20)
    c: PointOnObject(g17,g20)
    c: PointOnObject(g18,g20)
    c: PointOnObject(g19,g20)
    c: Diameter(g20) = 7
    c: DistanceY(g-1,g20) = 7
    c: Vertical(g18)
    c: Distance(g17,g-2) = 1
    c: Coincident(g21,g22)
    c: Coincident(g22,g23)
    c: Coincident(g23,g24)
    c: Coincident(g24,g25)
    c: Coincident(g25,g26)
    c: Coincident(g26,g21)
    c: Equal(g21, g22-g26) x5
    c: PointOnObject(g21,g27)
    c: PointOnObject(g22,g27)
    c: PointOnObject(g23,g27)
    c: PointOnObject(g24,g27)
    c: PointOnObject(g25,g27)
    c: PointOnObject(g26,g27)
    c: Diameter(g27) = 7
    c: DistanceY(g-1,g27) = 7
    c: DistanceX(g21,g-1) = 1
    c: Vertical(g21)
    c: Coincident(g28,g29)
    c: Coincident(g29,g30)
    c: Coincident(g30,g31)
    c: Coincident(g31,g32)
    c: Coincident(g32,g33)
    c: Coincident(g33,g28)
    c: Equal(g28, g29-g33) x5
    c: PointOnObject(g28,g34)
    c: PointOnObject(g29,g34)
    c: PointOnObject(g30,g34)
    c: PointOnObject(g31,g34)
    c: PointOnObject(g32,g34)
    c: PointOnObject(g33,g34)
    c: PointOnObject(g34,g-1)
    c: Diameter(g34) = 7
    c: Vertical(g31)
    c: DistanceX(g34,g-1) = 8
    c: Coincident(g35,g36)
    c: Coincident(g36,g37)
    c: Coincident(g37,g38)
    c: Coincident(g38,g39)
    c: Coincident(g39,g40)
    c: Coincident(g40,g35)
    c: Equal(g35, g36-g40) x5
    c: PointOnObject(g35,g41)
    c: PointOnObject(g36,g41)
    c: PointOnObject(g37,g41)
    c: PointOnObject(g38,g41)
    c: PointOnObject(g39,g41)
    c: PointOnObject(g40,g41)
    c: Coincident(g42,g43)
    c: Coincident(g43,g44)
    c: Coincident(g44,g45)
    c: Coincident(g45,g46)
    c: Coincident(g46,g47)
    c: Coincident(g47,g42)
    c: Equal(g42, g43-g47) x5
    c: PointOnObject(g42,g48)
    c: PointOnObject(g43,g48)
    c: PointOnObject(g44,g48)
    c: PointOnObject(g45,g48)
    c: PointOnObject(g46,g48)
    c: PointOnObject(g47,g48)
    c: Equal(g41,g48)
    c: Diameter(g41) = 7
    c: Vertical(g39)
    c: Vertical(g43)
    c: Distance(g-2,g39) = 1
    c: Symmetric(g38,g43,g-2)
    c: Distance(g41,g-1) = 7
FEATURE [Part::Extrusion] Extrude672  label="hex274"
  Base = -> Sketch681
  Dir = (0,-1,2e-16)
  DirMode = 2
  FaceMakerClass = Part::FaceMakerBullseye
  FaceMakerMode = 3
  LengthFwd = 10
  LengthRev = 0
  Placement = pos=(16,0,-14) rot=(0,0,1;0rad)
  Solid = true
  Symmetric = false
FEATURE [Sketcher::SketchObject] Sketch682
  ArcFitTolerance = 1e-06
  FullyConstrained = true
  MakeInternals = false
  Placement = pos=(0,0,0) rot=(1,0,0;1.5708rad)
  sketch-geometry (49):
    g0: LineSegment StartX=1e-16 StartY=3.5 StartZ=0 EndX=-3.03109 EndY=1.75 EndZ=0
    g1: LineSegment StartX=-3.03109 StartY=1.75 StartZ=0 EndX=-3.03109 EndY=-1.75 EndZ=0
    g2: LineSegment StartX=-3.03109 StartY=-1.75 StartZ=0 EndX=-1e-16 EndY=-3.5 EndZ=0
    g3: LineSegment StartX=-1e-16 StartY=-3.5 StartZ=0 EndX=3.03109 EndY=-1.75 EndZ=0
    g4: LineSegment StartX=3.03109 StartY=-1.75 StartZ=0 EndX=3.03109 EndY=1.75 EndZ=0
    g5: LineSegment StartX=3.03109 StartY=1.75 StartZ=0 EndX=1e-16 EndY=3.5 EndZ=0
    g6: Circle [constr] CenterX=0 CenterY=0 CenterZ=0 NormalX=0 NormalY=0 NormalZ=1 AngleXU=0 Radius=3.5
    g7: LineSegment StartX=4.96892 StartY=-1.75002 StartZ=0 EndX=8.00002 EndY=-3.5 EndZ=0
    g8: LineSegment StartX=8.00002 StartY=-3.5 StartZ=0 EndX=11.0311 EndY=-1.74998 EndZ=0
    g9: LineSegment StartX=11.0311 StartY=-1.74998 StartZ=0 EndX=11.0311 EndY=1.75002 EndZ=0
    g10: LineSegment StartX=11.0311 StartY=1.75002 StartZ=0 EndX=7.99998 EndY=3.5 EndZ=0
    g11: LineSegment StartX=7.99998 StartY=3.5 StartZ=0 EndX=4.9689 EndY=1.74998 EndZ=0
    g12: LineSegment StartX=4.9689 StartY=1.74998 StartZ=0 EndX=4.96892 EndY=-1.75002 EndZ=0
    g13: Circle [constr] CenterX=8 CenterY=0 CenterZ=0 NormalX=0 NormalY=0 NormalZ=1 AngleXU=0 Radius=3.5
    g14: LineSegment StartX=4.03109 StartY=3.5 StartZ=0 EndX=7.06218 EndY=5.25 EndZ=0
    g15: LineSegment StartX=7.06218 StartY=5.25 StartZ=0 EndX=7.06218 EndY=8.75 EndZ=0
    g16: LineSegment StartX=7.06218 StartY=8.75 StartZ=0 EndX=4.03109 EndY=10.5 EndZ=0
    g17: LineSegment StartX=4.03109 StartY=10.5 StartZ=0 EndX=1 EndY=8.75 EndZ=0
    g18: LineSegment StartX=1 StartY=8.75 StartZ=0 EndX=1 EndY=5.25 EndZ=0
    g19: LineSegment StartX=1 StartY=5.25 StartZ=0 EndX=4.03109 EndY=3.5 EndZ=0
    g20: Circle [constr] CenterX=4.03109 CenterY=7 CenterZ=0 NormalX=0 NormalY=0 NormalZ=1 AngleXU=0 Radius=3.5
    g21: LineSegment StartX=-1 StartY=5.25 StartZ=0 EndX=-1 EndY=8.75 EndZ=0
    g22: LineSegment StartX=-1 StartY=8.75 StartZ=0 EndX=-4.03109 EndY=10.5 EndZ=0
    g23: LineSegment StartX=-4.03109 StartY=10.5 StartZ=0 EndX=-7.06218 EndY=8.75 EndZ=0
    g24: LineSegment StartX=-7.06218 StartY=8.75 StartZ=0 EndX=-7.06218 EndY=5.25 EndZ=0
    g25: LineSegment StartX=-7.06218 StartY=5.25 StartZ=0 EndX=-4.03109 EndY=3.5 EndZ=0
    g26: LineSegment StartX=-4.03109 StartY=3.5 StartZ=0 EndX=-1 EndY=5.25 EndZ=0
    g27: Circle [constr] CenterX=-4.03109 CenterY=7 CenterZ=0 NormalX=0 NormalY=0 NormalZ=1 AngleXU=0 Radius=3.5
    g28: LineSegment StartX=-4.96891 StartY=-1.75 StartZ=0 EndX=-4.96891 EndY=1.75 EndZ=0
    g29: LineSegment StartX=-4.96891 StartY=1.75 StartZ=0 EndX=-8 EndY=3.5 EndZ=0
    g30: LineSegment StartX=-8 StartY=3.5 StartZ=0 EndX=-11.0311 EndY=1.75 EndZ=0
    g31: LineSegment StartX=-11.0311 StartY=1.75 StartZ=0 EndX=-11.0311 EndY=-1.75 EndZ=0
    g32: LineSegment StartX=-11.0311 StartY=-1.75 StartZ=0 EndX=-8 EndY=-3.5 EndZ=0
    g33: LineSegment StartX=-8 StartY=-3.5 StartZ=0 EndX=-4.96891 EndY=-1.75 EndZ=0
    g34: Circle [constr] CenterX=-8 CenterY=0 CenterZ=0 NormalX=0 NormalY=0 NormalZ=1 AngleXU=0 Radius=3.5
    g35: LineSegment StartX=-4.03109 StartY=-3.5 StartZ=0 EndX=-7.06218 EndY=-5.25 EndZ=0
    g36: LineSegment StartX=-7.06218 StartY=-5.25 StartZ=0 EndX=-7.06218 EndY=-8.75 EndZ=0
    g37: LineSegment StartX=-7.06218 StartY=-8.75 StartZ=0 EndX=-4.03109 EndY=-10.5 EndZ=0
    g38: LineSegment StartX=-4.03109 StartY=-10.5 StartZ=0 EndX=-1 EndY=-8.75 EndZ=0
    g39: LineSegment StartX=-1 StartY=-8.75 StartZ=0 EndX=-1 EndY=-5.25 EndZ=0
    g40: LineSegment StartX=-1 StartY=-5.25 StartZ=0 EndX=-4.03109 EndY=-3.5 EndZ=0
    g41: Circle [constr] CenterX=-4.03109 CenterY=-7 CenterZ=0 NormalX=0 NormalY=0 NormalZ=1 AngleXU=0 Radius=3.5
    g42: LineSegment StartX=4.03109 StartY=-3.5 StartZ=0 EndX=1 EndY=-5.25 EndZ=0
    g43: LineSegment StartX=1 StartY=-5.25 StartZ=0 EndX=1 EndY=-8.75 EndZ=0
    g44: LineSegment StartX=1 StartY=-8.75 StartZ=0 EndX=4.03109 EndY=-10.5 EndZ=0
    g45: LineSegment StartX=4.03109 StartY=-10.5 StartZ=0 EndX=7.06218 EndY=-8.75 EndZ=0
    g46: LineSegment StartX=7.06218 StartY=-8.75 StartZ=0 EndX=7.06218 EndY=-5.25 EndZ=0
    g47: LineSegment StartX=7.06218 StartY=-5.25 StartZ=0 EndX=4.03109 EndY=-3.5 EndZ=0
    g48: Circle [constr] CenterX=4.03109 CenterY=-7 CenterZ=0 NormalX=0 NormalY=0 NormalZ=1 AngleXU=0 Radius=3.5
  constraints (117):
    c: Coincident(g0,g1)
    c: Coincident(g1,g2)
    c: Coincident(g2,g3)
    c: Coincident(g3,g4)
    c: Coincident(g4,g5)
    c: Coincident(g5,g0)
    c: Equal(g0, g1-g5) x5
    c: PointOnObject(g0,g6)
    c: PointOnObject(g1,g6)
    c: PointOnObject(g2,g6)
    c: PointOnObject(g3,g6)
    c: PointOnObject(g4,g6)
    c: PointOnObject(g5,g6)
    c: Coincident(g6,g-1)
    c: Diameter(g6) = 7
    c: PointOnObject(g0,g-2)
    c: Coincident(g7,g8)
    c: Coincident(g8,g9)
    c: Coincident(g9,g10)
    c: Coincident(g10,g11)
    c: Coincident(g11,g12)
    c: Coincident(g12,g7)
    c: Equal(g7, g8-g12) x5
    c: PointOnObject(g7,g13)
    c: PointOnObject(g8,g13)
    c: PointOnObject(g9,g13)
    c: PointOnObject(g10,g13)
    c: PointOnObject(g11,g13)
    c: PointOnObject(g12,g13)
    c: PointOnObject(g13,g-1)
    c: Diameter(g13) = 7
    c: Distance(g6,g13) = 8
    c: Horizontal(g0,g10)
    c: Coincident(g14,g15)
    c: Coincident(g15,g16)
    c: Coincident(g16,g17)
    c: Coincident(g17,g18)
    c: Coincident(g18,g19)
    c: Coincident(g19,g14)
    c: Equal(g14, g15-g19) x5
    c: PointOnObject(g14,g20)
    c: PointOnObject(g15,g20)
    c: PointOnObject(g16,g20)
    c: PointOnObject(g17,g20)
    c: PointOnObject(g18,g20)
    c: PointOnObject(g19,g20)
    c: Diameter(g20) = 7
    c: DistanceY(g-1,g20) = 7
    c: Vertical(g18)
    c: Distance(g17,g-2) = 1
    c: Coincident(g21,g22)
    c: Coincident(g22,g23)
    c: Coincident(g23,g24)
    c: Coincident(g24,g25)
    c: Coincident(g25,g26)
    c: Coincident(g26,g21)
    c: Equal(g21, g22-g26) x5
    c: PointOnObject(g21,g27)
    c: PointOnObject(g22,g27)
    c: PointOnObject(g23,g27)
    c: PointOnObject(g24,g27)
    c: PointOnObject(g25,g27)
    c: PointOnObject(g26,g27)
    c: Diameter(g27) = 7
    c: DistanceY(g-1,g27) = 7
    c: DistanceX(g21,g-1) = 1
    c: Vertical(g21)
    c: Coincident(g28,g29)
    c: Coincident(g29,g30)
    c: Coincident(g30,g31)
    c: Coincident(g31,g32)
    c: Coincident(g32,g33)
    c: Coincident(g33,g28)
    c: Equal(g28, g29-g33) x5
    c: PointOnObject(g28,g34)
    c: PointOnObject(g29,g34)
    c: PointOnObject(g30,g34)
    c: PointOnObject(g31,g34)
    c: PointOnObject(g32,g34)
    c: PointOnObject(g33,g34)
    c: PointOnObject(g34,g-1)
    c: Diameter(g34) = 7
    c: Vertical(g31)
    c: DistanceX(g34,g-1) = 8
    c: Coincident(g35,g36)
    c: Coincident(g36,g37)
    c: Coincident(g37,g38)
    c: Coincident(g38,g39)
    c: Coincident(g39,g40)
    c: Coincident(g40,g35)
    c: Equal(g35, g36-g40) x5
    c: PointOnObject(g35,g41)
    c: PointOnObject(g36,g41)
    c: PointOnObject(g37,g41)
    c: PointOnObject(g38,g41)
    c: PointOnObject(g39,g41)
    c: PointOnObject(g40,g41)
    c: Coincident(g42,g43)
    c: Coincident(g43,g44)
    c: Coincident(g44,g45)
    c: Coincident(g45,g46)
    c: Coincident(g46,g47)
    c: Coincident(g47,g42)
    c: Equal(g42, g43-g47) x5
    c: PointOnObject(g42,g48)
    c: PointOnObject(g43,g48)
    c: PointOnObject(g44,g48)
    c: PointOnObject(g45,g48)
    c: PointOnObject(g46,g48)
    c: PointOnObject(g47,g48)
    c: Equal(g41,g48)
    c: Diameter(g41) = 7
    c: Vertical(g39)
    c: Vertical(g43)
    c: Distance(g-2,g39) = 1
    c: Symmetric(g38,g43,g-2)
    c: Distance(g41,g-1) = 7
FEATURE [Part::Extrusion] Extrude673  label="hex275"
  Base = -> Sketch682
  Dir = (0,-1,2e-16)
  DirMode = 2
  FaceMakerClass = Part::FaceMakerBullseye
  FaceMakerMode = 3
  LengthFwd = 10
  LengthRev = 0
  Placement = pos=(-4,0,21) rot=(0,0,1;0rad)
  Solid = true
  Symmetric = false
FEATURE [Sketcher::SketchObject] Sketch683
  ArcFitTolerance = 1e-06
  FullyConstrained = true
  MakeInternals = false
  Placement = pos=(0,0,0) rot=(1,0,0;1.5708rad)
  sketch-geometry (49):
    g0: LineSegment StartX=1e-16 StartY=3.5 StartZ=0 EndX=-3.03109 EndY=1.75 EndZ=0
    g1: LineSegment StartX=-3.03109 StartY=1.75 StartZ=0 EndX=-3.03109 EndY=-1.75 EndZ=0
    g2: LineSegment StartX=-3.03109 StartY=-1.75 StartZ=0 EndX=-1e-16 EndY=-3.5 EndZ=0
    g3: LineSegment StartX=-1e-16 StartY=-3.5 StartZ=0 EndX=3.03109 EndY=-1.75 EndZ=0
    g4: LineSegment StartX=3.03109 StartY=-1.75 StartZ=0 EndX=3.03109 EndY=1.75 EndZ=0
    g5: LineSegment StartX=3.03109 StartY=1.75 StartZ=0 EndX=1e-16 EndY=3.5 EndZ=0
    g6: Circle [constr] CenterX=0 CenterY=0 CenterZ=0 NormalX=0 NormalY=0 NormalZ=1 AngleXU=0 Radius=3.5
    g7: LineSegment StartX=4.96892 StartY=-1.75002 StartZ=0 EndX=8.00002 EndY=-3.5 EndZ=0
    g8: LineSegment StartX=8.00002 StartY=-3.5 StartZ=0 EndX=11.0311 EndY=-1.74998 EndZ=0
    g9: LineSegment StartX=11.0311 StartY=-1.74998 StartZ=0 EndX=11.0311 EndY=1.75002 EndZ=0
    g10: LineSegment StartX=11.0311 StartY=1.75002 StartZ=0 EndX=7.99998 EndY=3.5 EndZ=0
    g11: LineSegment StartX=7.99998 StartY=3.5 StartZ=0 EndX=4.9689 EndY=1.74998 EndZ=0
    g12: LineSegment StartX=4.9689 StartY=1.74998 StartZ=0 EndX=4.96892 EndY=-1.75002 EndZ=0
    g13: Circle [constr] CenterX=8 CenterY=0 CenterZ=0 NormalX=0 NormalY=0 NormalZ=1 AngleXU=0 Radius=3.5
    g14: LineSegment StartX=4.03109 StartY=3.5 StartZ=0 EndX=7.06218 EndY=5.25 EndZ=0
    g15: LineSegment StartX=7.06218 StartY=5.25 StartZ=0 EndX=7.06218 EndY=8.75 EndZ=0
    g16: LineSegment StartX=7.06218 StartY=8.75 StartZ=0 EndX=4.03109 EndY=10.5 EndZ=0
    g17: LineSegment StartX=4.03109 StartY=10.5 StartZ=0 EndX=1 EndY=8.75 EndZ=0
    g18: LineSegment StartX=1 StartY=8.75 StartZ=0 EndX=1 EndY=5.25 EndZ=0
    g19: LineSegment StartX=1 StartY=5.25 StartZ=0 EndX=4.03109 EndY=3.5 EndZ=0
    g20: Circle [constr] CenterX=4.03109 CenterY=7 CenterZ=0 NormalX=0 NormalY=0 NormalZ=1 AngleXU=0 Radius=3.5
    g21: LineSegment StartX=-1 StartY=5.25 StartZ=0 EndX=-1 EndY=8.75 EndZ=0
    g22: LineSegment StartX=-1 StartY=8.75 StartZ=0 EndX=-4.03109 EndY=10.5 EndZ=0
    g23: LineSegment StartX=-4.03109 StartY=10.5 StartZ=0 EndX=-7.06218 EndY=8.75 EndZ=0
    g24: LineSegment StartX=-7.06218 StartY=8.75 StartZ=0 EndX=-7.06218 EndY=5.25 EndZ=0
    g25: LineSegment StartX=-7.06218 StartY=5.25 StartZ=0 EndX=-4.03109 EndY=3.5 EndZ=0
    g26: LineSegment StartX=-4.03109 StartY=3.5 StartZ=0 EndX=-1 EndY=5.25 EndZ=0
    g27: Circle [constr] CenterX=-4.03109 CenterY=7 CenterZ=0 NormalX=0 NormalY=0 NormalZ=1 AngleXU=0 Radius=3.5
    g28: LineSegment StartX=-4.96891 StartY=-1.75 StartZ=0 EndX=-4.96891 EndY=1.75 EndZ=0
    g29: LineSegment StartX=-4.96891 StartY=1.75 StartZ=0 EndX=-8 EndY=3.5 EndZ=0
    g30: LineSegment StartX=-8 StartY=3.5 StartZ=0 EndX=-11.0311 EndY=1.75 EndZ=0
    g31: LineSegment StartX=-11.0311 StartY=1.75 StartZ=0 EndX=-11.0311 EndY=-1.75 EndZ=0
    g32: LineSegment StartX=-11.0311 StartY=-1.75 StartZ=0 EndX=-8 EndY=-3.5 EndZ=0
    g33: LineSegment StartX=-8 StartY=-3.5 StartZ=0 EndX=-4.96891 EndY=-1.75 EndZ=0
    g34: Circle [constr] CenterX=-8 CenterY=0 CenterZ=0 NormalX=0 NormalY=0 NormalZ=1 AngleXU=0 Radius=3.5
    g35: LineSegment StartX=-4.03109 StartY=-3.5 StartZ=0 EndX=-7.06218 EndY=-5.25 EndZ=0
    g36: LineSegment StartX=-7.06218 StartY=-5.25 StartZ=0 EndX=-7.06218 EndY=-8.75 EndZ=0
    g37: LineSegment StartX=-7.06218 StartY=-8.75 StartZ=0 EndX=-4.03109 EndY=-10.5 EndZ=0
    g38: LineSegment StartX=-4.03109 StartY=-10.5 StartZ=0 EndX=-1 EndY=-8.75 EndZ=0
    g39: LineSegment StartX=-1 StartY=-8.75 StartZ=0 EndX=-1 EndY=-5.25 EndZ=0
    g40: LineSegment StartX=-1 StartY=-5.25 StartZ=0 EndX=-4.03109 EndY=-3.5 EndZ=0
    g41: Circle [constr] CenterX=-4.03109 CenterY=-7 CenterZ=0 NormalX=0 NormalY=0 NormalZ=1 AngleXU=0 Radius=3.5
    g42: LineSegment StartX=4.03109 StartY=-3.5 StartZ=0 EndX=1 EndY=-5.25 EndZ=0
    g43: LineSegment StartX=1 StartY=-5.25 StartZ=0 EndX=1 EndY=-8.75 EndZ=0
    g44: LineSegment StartX=1 StartY=-8.75 StartZ=0 EndX=4.03109 EndY=-10.5 EndZ=0
    g45: LineSegment StartX=4.03109 StartY=-10.5 StartZ=0 EndX=7.06218 EndY=-8.75 EndZ=0
    g46: LineSegment StartX=7.06218 StartY=-8.75 StartZ=0 EndX=7.06218 EndY=-5.25 EndZ=0
    g47: LineSegment StartX=7.06218 StartY=-5.25 StartZ=0 EndX=4.03109 EndY=-3.5 EndZ=0
    g48: Circle [constr] CenterX=4.03109 CenterY=-7 CenterZ=0 NormalX=0 NormalY=0 NormalZ=1 AngleXU=0 Radius=3.5
  constraints (117):
    c: Coincident(g0,g1)
    c: Coincident(g1,g2)
    c: Coincident(g2,g3)
    c: Coincident(g3,g4)
    c: Coincident(g4,g5)
    c: Coincident(g5,g0)
    c: Equal(g0, g1-g5) x5
    c: PointOnObject(g0,g6)
    c: PointOnObject(g1,g6)
    c: PointOnObject(g2,g6)
    c: PointOnObject(g3,g6)
    c: PointOnObject(g4,g6)
    c: PointOnObject(g5,g6)
    c: Coincident(g6,g-1)
    c: Diameter(g6) = 7
    c: PointOnObject(g0,g-2)
    c: Coincident(g7,g8)
    c: Coincident(g8,g9)
    c: Coincident(g9,g10)
    c: Coincident(g10,g11)
    c: Coincident(g11,g12)
    c: Coincident(g12,g7)
    c: Equal(g7, g8-g12) x5
    c: PointOnObject(g7,g13)
    c: PointOnObject(g8,g13)
    c: PointOnObject(g9,g13)
    c: PointOnObject(g10,g13)
    c: PointOnObject(g11,g13)
    c: PointOnObject(g12,g13)
    c: PointOnObject(g13,g-1)
    c: Diameter(g13) = 7
    c: Distance(g6,g13) = 8
    c: Horizontal(g0,g10)
    c: Coincident(g14,g15)
    c: Coincident(g15,g16)
    c: Coincident(g16,g17)
    c: Coincident(g17,g18)
    c: Coincident(g18,g19)
    c: Coincident(g19,g14)
    c: Equal(g14, g15-g19) x5
    c: PointOnObject(g14,g20)
    c: PointOnObject(g15,g20)
    c: PointOnObject(g16,g20)
    c: PointOnObject(g17,g20)
    c: PointOnObject(g18,g20)
    c: PointOnObject(g19,g20)
    c: Diameter(g20) = 7
    c: DistanceY(g-1,g20) = 7
    c: Vertical(g18)
    c: Distance(g17,g-2) = 1
    c: Coincident(g21,g22)
    c: Coincident(g22,g23)
    c: Coincident(g23,g24)
    c: Coincident(g24,g25)
    c: Coincident(g25,g26)
    c: Coincident(g26,g21)
    c: Equal(g21, g22-g26) x5
    c: PointOnObject(g21,g27)
    c: PointOnObject(g22,g27)
    c: PointOnObject(g23,g27)
    c: PointOnObject(g24,g27)
    c: PointOnObject(g25,g27)
    c: PointOnObject(g26,g27)
    c: Diameter(g27) = 7
    c: DistanceY(g-1,g27) = 7
    c: DistanceX(g21,g-1) = 1
    c: Vertical(g21)
    c: Coincident(g28,g29)
    c: Coincident(g29,g30)
    c: Coincident(g30,g31)
    c: Coincident(g31,g32)
    c: Coincident(g32,g33)
    c: Coincident(g33,g28)
    c: Equal(g28, g29-g33) x5
    c: PointOnObject(g28,g34)
    c: PointOnObject(g29,g34)
    c: PointOnObject(g30,g34)
    c: PointOnObject(g31,g34)
    c: PointOnObject(g32,g34)
    c: PointOnObject(g33,g34)
    c: PointOnObject(g34,g-1)
    c: Diameter(g34) = 7
    c: Vertical(g31)
    c: DistanceX(g34,g-1) = 8
    c: Coincident(g35,g36)
    c: Coincident(g36,g37)
    c: Coincident(g37,g38)
    c: Coincident(g38,g39)
    c: Coincident(g39,g40)
    c: Coincident(g40,g35)
    c: Equal(g35, g36-g40) x5
    c: PointOnObject(g35,g41)
    c: PointOnObject(g36,g41)
    c: PointOnObject(g37,g41)
    c: PointOnObject(g38,g41)
    c: PointOnObject(g39,g41)
    c: PointOnObject(g40,g41)
    c: Coincident(g42,g43)
    c: Coincident(g43,g44)
    c: Coincident(g44,g45)
    c: Coincident(g45,g46)
    c: Coincident(g46,g47)
    c: Coincident(g47,g42)
    c: Equal(g42, g43-g47) x5
    c: PointOnObject(g42,g48)
    c: PointOnObject(g43,g48)
    c: PointOnObject(g44,g48)
    c: PointOnObject(g45,g48)
    c: PointOnObject(g46,g48)
    c: PointOnObject(g47,g48)
    c: Equal(g41,g48)
    c: Diameter(g41) = 7
    c: Vertical(g39)
    c: Vertical(g43)
    c: Distance(g-2,g39) = 1
    c: Symmetric(g38,g43,g-2)
    c: Distance(g41,g-1) = 7
FEATURE [Part::Extrusion] Extrude674  label="hex276"
  Base = -> Sketch683
  Dir = (0,-1,2e-16)
  DirMode = 2
  FaceMakerClass = Part::FaceMakerBullseye
  FaceMakerMode = 3
  LengthFwd = 10
  LengthRev = 0
  Placement = pos=(12,0,-35) rot=(0,0,1;0rad)
  Solid = true
  Symmetric = false
FEATURE [Sketcher::SketchObject] Sketch684
  ArcFitTolerance = 1e-06
  FullyConstrained = true
  MakeInternals = false
  Placement = pos=(0,0,0) rot=(1,0,0;1.5708rad)
  sketch-geometry (49):
    g0: LineSegment StartX=1e-16 StartY=3.5 StartZ=0 EndX=-3.03109 EndY=1.75 EndZ=0
    g1: LineSegment StartX=-3.03109 StartY=1.75 StartZ=0 EndX=-3.03109 EndY=-1.75 EndZ=0
    g2: LineSegment StartX=-3.03109 StartY=-1.75 StartZ=0 EndX=-1e-16 EndY=-3.5 EndZ=0
    g3: LineSegment StartX=-1e-16 StartY=-3.5 StartZ=0 EndX=3.03109 EndY=-1.75 EndZ=0
    g4: LineSegment StartX=3.03109 StartY=-1.75 StartZ=0 EndX=3.03109 EndY=1.75 EndZ=0
    g5: LineSegment StartX=3.03109 StartY=1.75 StartZ=0 EndX=1e-16 EndY=3.5 EndZ=0
    g6: Circle [constr] CenterX=0 CenterY=0 CenterZ=0 NormalX=0 NormalY=0 NormalZ=1 AngleXU=0 Radius=3.5
    g7: LineSegment StartX=4.96892 StartY=-1.75002 StartZ=0 EndX=8.00002 EndY=-3.5 EndZ=0
    g8: LineSegment StartX=8.00002 StartY=-3.5 StartZ=0 EndX=11.0311 EndY=-1.74998 EndZ=0
    g9: LineSegment StartX=11.0311 StartY=-1.74998 StartZ=0 EndX=11.0311 EndY=1.75002 EndZ=0
    g10: LineSegment StartX=11.0311 StartY=1.75002 StartZ=0 EndX=7.99998 EndY=3.5 EndZ=0
    g11: LineSegment StartX=7.99998 StartY=3.5 StartZ=0 EndX=4.9689 EndY=1.74998 EndZ=0
    g12: LineSegment StartX=4.9689 StartY=1.74998 StartZ=0 EndX=4.96892 EndY=-1.75002 EndZ=0
    g13: Circle [constr] CenterX=8 CenterY=0 CenterZ=0 NormalX=0 NormalY=0 NormalZ=1 AngleXU=0 Radius=3.5
    g14: LineSegment StartX=4.03109 StartY=3.5 StartZ=0 EndX=7.06218 EndY=5.25 EndZ=0
    g15: LineSegment StartX=7.06218 StartY=5.25 StartZ=0 EndX=7.06218 EndY=8.75 EndZ=0
    g16: LineSegment StartX=7.06218 StartY=8.75 StartZ=0 EndX=4.03109 EndY=10.5 EndZ=0
    g17: LineSegment StartX=4.03109 StartY=10.5 StartZ=0 EndX=1 EndY=8.75 EndZ=0
    g18: LineSegment StartX=1 StartY=8.75 StartZ=0 EndX=1 EndY=5.25 EndZ=0
    g19: LineSegment StartX=1 StartY=5.25 StartZ=0 EndX=4.03109 EndY=3.5 EndZ=0
    g20: Circle [constr] CenterX=4.03109 CenterY=7 CenterZ=0 NormalX=0 NormalY=0 NormalZ=1 AngleXU=0 Radius=3.5
    g21: LineSegment StartX=-1 StartY=5.25 StartZ=0 EndX=-1 EndY=8.75 EndZ=0
    g22: LineSegment StartX=-1 StartY=8.75 StartZ=0 EndX=-4.03109 EndY=10.5 EndZ=0
    g23: LineSegment StartX=-4.03109 StartY=10.5 StartZ=0 EndX=-7.06218 EndY=8.75 EndZ=0
    g24: LineSegment StartX=-7.06218 StartY=8.75 StartZ=0 EndX=-7.06218 EndY=5.25 EndZ=0
    g25: LineSegment StartX=-7.06218 StartY=5.25 StartZ=0 EndX=-4.03109 EndY=3.5 EndZ=0
    g26: LineSegment StartX=-4.03109 StartY=3.5 StartZ=0 EndX=-1 EndY=5.25 EndZ=0
    g27: Circle [constr] CenterX=-4.03109 CenterY=7 CenterZ=0 NormalX=0 NormalY=0 NormalZ=1 AngleXU=0 Radius=3.5
    g28: LineSegment StartX=-4.96891 StartY=-1.75 StartZ=0 EndX=-4.96891 EndY=1.75 EndZ=0
    g29: LineSegment StartX=-4.96891 StartY=1.75 StartZ=0 EndX=-8 EndY=3.5 EndZ=0
    g30: LineSegment StartX=-8 StartY=3.5 StartZ=0 EndX=-11.0311 EndY=1.75 EndZ=0
    g31: LineSegment StartX=-11.0311 StartY=1.75 StartZ=0 EndX=-11.0311 EndY=-1.75 EndZ=0
    g32: LineSegment StartX=-11.0311 StartY=-1.75 StartZ=0 EndX=-8 EndY=-3.5 EndZ=0
    g33: LineSegment StartX=-8 StartY=-3.5 StartZ=0 EndX=-4.96891 EndY=-1.75 EndZ=0
    g34: Circle [constr] CenterX=-8 CenterY=0 CenterZ=0 NormalX=0 NormalY=0 NormalZ=1 AngleXU=0 Radius=3.5
    g35: LineSegment StartX=-4.03109 StartY=-3.5 StartZ=0 EndX=-7.06218 EndY=-5.25 EndZ=0
    g36: LineSegment StartX=-7.06218 StartY=-5.25 StartZ=0 EndX=-7.06218 EndY=-8.75 EndZ=0
    g37: LineSegment StartX=-7.06218 StartY=-8.75 StartZ=0 EndX=-4.03109 EndY=-10.5 EndZ=0
    g38: LineSegment StartX=-4.03109 StartY=-10.5 StartZ=0 EndX=-1 EndY=-8.75 EndZ=0
    g39: LineSegment StartX=-1 StartY=-8.75 StartZ=0 EndX=-1 EndY=-5.25 EndZ=0
    g40: LineSegment StartX=-1 StartY=-5.25 StartZ=0 EndX=-4.03109 EndY=-3.5 EndZ=0
    g41: Circle [constr] CenterX=-4.03109 CenterY=-7 CenterZ=0 NormalX=0 NormalY=0 NormalZ=1 AngleXU=0 Radius=3.5
    g42: LineSegment StartX=4.03109 StartY=-3.5 StartZ=0 EndX=1 EndY=-5.25 EndZ=0
    g43: LineSegment StartX=1 StartY=-5.25 StartZ=0 EndX=1 EndY=-8.75 EndZ=0
    g44: LineSegment StartX=1 StartY=-8.75 StartZ=0 EndX=4.03109 EndY=-10.5 EndZ=0
    g45: LineSegment StartX=4.03109 StartY=-10.5 StartZ=0 EndX=7.06218 EndY=-8.75 EndZ=0
    g46: LineSegment StartX=7.06218 StartY=-8.75 StartZ=0 EndX=7.06218 EndY=-5.25 EndZ=0
    g47: LineSegment StartX=7.06218 StartY=-5.25 StartZ=0 EndX=4.03109 EndY=-3.5 EndZ=0
    g48: Circle [constr] CenterX=4.03109 CenterY=-7 CenterZ=0 NormalX=0 NormalY=0 NormalZ=1 AngleXU=0 Radius=3.5
  constraints (117):
    c: Coincident(g0,g1)
    c: Coincident(g1,g2)
    c: Coincident(g2,g3)
    c: Coincident(g3,g4)
    c: Coincident(g4,g5)
    c: Coincident(g5,g0)
    c: Equal(g0, g1-g5) x5
    c: PointOnObject(g0,g6)
    c: PointOnObject(g1,g6)
    c: PointOnObject(g2,g6)
    c: PointOnObject(g3,g6)
    c: PointOnObject(g4,g6)
    c: PointOnObject(g5,g6)
    c: Coincident(g6,g-1)
    c: Diameter(g6) = 7
    c: PointOnObject(g0,g-2)
    c: Coincident(g7,g8)
    c: Coincident(g8,g9)
    c: Coincident(g9,g10)
    c: Coincident(g10,g11)
    c: Coincident(g11,g12)
    c: Coincident(g12,g7)
    c: Equal(g7, g8-g12) x5
    c: PointOnObject(g7,g13)
    c: PointOnObject(g8,g13)
    c: PointOnObject(g9,g13)
    c: PointOnObject(g10,g13)
    c: PointOnObject(g11,g13)
    c: PointOnObject(g12,g13)
    c: PointOnObject(g13,g-1)
    c: Diameter(g13) = 7
    c: Distance(g6,g13) = 8
    c: Horizontal(g0,g10)
    c: Coincident(g14,g15)
    c: Coincident(g15,g16)
    c: Coincident(g16,g17)
    c: Coincident(g17,g18)
    c: Coincident(g18,g19)
    c: Coincident(g19,g14)
    c: Equal(g14, g15-g19) x5
    c: PointOnObject(g14,g20)
    c: PointOnObject(g15,g20)
    c: PointOnObject(g16,g20)
    c: PointOnObject(g17,g20)
    c: PointOnObject(g18,g20)
    c: PointOnObject(g19,g20)
    c: Diameter(g20) = 7
    c: DistanceY(g-1,g20) = 7
    c: Vertical(g18)
    c: Distance(g17,g-2) = 1
    c: Coincident(g21,g22)
    c: Coincident(g22,g23)
    c: Coincident(g23,g24)
    c: Coincident(g24,g25)
    c: Coincident(g25,g26)
    c: Coincident(g26,g21)
    c: Equal(g21, g22-g26) x5
    c: PointOnObject(g21,g27)
    c: PointOnObject(g22,g27)
    c: PointOnObject(g23,g27)
    c: PointOnObject(g24,g27)
    c: PointOnObject(g25,g27)
    c: PointOnObject(g26,g27)
    c: Diameter(g27) = 7
    c: DistanceY(g-1,g27) = 7
    c: DistanceX(g21,g-1) = 1
    c: Vertical(g21)
    c: Coincident(g28,g29)
    c: Coincident(g29,g30)
    c: Coincident(g30,g31)
    c: Coincident(g31,g32)
    c: Coincident(g32,g33)
    c: Coincident(g33,g28)
    c: Equal(g28, g29-g33) x5
    c: PointOnObject(g28,g34)
    c: PointOnObject(g29,g34)
    c: PointOnObject(g30,g34)
    c: PointOnObject(g31,g34)
    c: PointOnObject(g32,g34)
    c: PointOnObject(g33,g34)
    c: PointOnObject(g34,g-1)
    c: Diameter(g34) = 7
    c: Vertical(g31)
    c: DistanceX(g34,g-1) = 8
    c: Coincident(g35,g36)
    c: Coincident(g36,g37)
    c: Coincident(g37,g38)
    c: Coincident(g38,g39)
    c: Coincident(g39,g40)
    c: Coincident(g40,g35)
    c: Equal(g35, g36-g40) x5
    c: PointOnObject(g35,g41)
    c: PointOnObject(g36,g41)
    c: PointOnObject(g37,g41)
    c: PointOnObject(g38,g41)
    c: PointOnObject(g39,g41)
    c: PointOnObject(g40,g41)
    c: Coincident(g42,g43)
    c: Coincident(g43,g44)
    c: Coincident(g44,g45)
    c: Coincident(g45,g46)
    c: Coincident(g46,g47)
    c: Coincident(g47,g42)
    c: Equal(g42, g43-g47) x5
    c: PointOnObject(g42,g48)
    c: PointOnObject(g43,g48)
    c: PointOnObject(g44,g48)
    c: PointOnObject(g45,g48)
    c: PointOnObject(g46,g48)
    c: PointOnObject(g47,g48)
    c: Equal(g41,g48)
    c: Diameter(g41) = 7
    c: Vertical(g39)
    c: Vertical(g43)
    c: Distance(g-2,g39) = 1
    c: Symmetric(g38,g43,g-2)
    c: Distance(g41,g-1) = 7
FEATURE [Part::Extrusion] Extrude675  label="hex277"
  Base = -> Sketch684
  Dir = (0,-1,2e-16)
  DirMode = 2
  FaceMakerClass = Part::FaceMakerBullseye
  FaceMakerMode = 3
  LengthFwd = 10
  LengthRev = 0
  Placement = pos=(12,0,35) rot=(0,0,1;0rad)
  Solid = true
  Symmetric = false
FEATURE [Sketcher::SketchObject] Sketch685
  ArcFitTolerance = 1e-06
  FullyConstrained = true
  MakeInternals = false
  Placement = pos=(0,0,0) rot=(1,0,0;1.5708rad)
  sketch-geometry (49):
    g0: LineSegment StartX=1e-16 StartY=3.5 StartZ=0 EndX=-3.03109 EndY=1.75 EndZ=0
    g1: LineSegment StartX=-3.03109 StartY=1.75 StartZ=0 EndX=-3.03109 EndY=-1.75 EndZ=0
    g2: LineSegment StartX=-3.03109 StartY=-1.75 StartZ=0 EndX=-1e-16 EndY=-3.5 EndZ=0
    g3: LineSegment StartX=-1e-16 StartY=-3.5 StartZ=0 EndX=3.03109 EndY=-1.75 EndZ=0
    g4: LineSegment StartX=3.03109 StartY=-1.75 StartZ=0 EndX=3.03109 EndY=1.75 EndZ=0
    g5: LineSegment StartX=3.03109 StartY=1.75 StartZ=0 EndX=1e-16 EndY=3.5 EndZ=0
    g6: Circle [constr] CenterX=0 CenterY=0 CenterZ=0 NormalX=0 NormalY=0 NormalZ=1 AngleXU=0 Radius=3.5
    g7: LineSegment StartX=4.96892 StartY=-1.75002 StartZ=0 EndX=8.00002 EndY=-3.5 EndZ=0
    g8: LineSegment StartX=8.00002 StartY=-3.5 StartZ=0 EndX=11.0311 EndY=-1.74998 EndZ=0
    g9: LineSegment StartX=11.0311 StartY=-1.74998 StartZ=0 EndX=11.0311 EndY=1.75002 EndZ=0
    g10: LineSegment StartX=11.0311 StartY=1.75002 StartZ=0 EndX=7.99998 EndY=3.5 EndZ=0
    g11: LineSegment StartX=7.99998 StartY=3.5 StartZ=0 EndX=4.9689 EndY=1.74998 EndZ=0
    g12: LineSegment StartX=4.9689 StartY=1.74998 StartZ=0 EndX=4.96892 EndY=-1.75002 EndZ=0
    g13: Circle [constr] CenterX=8 CenterY=0 CenterZ=0 NormalX=0 NormalY=0 NormalZ=1 AngleXU=0 Radius=3.5
    g14: LineSegment StartX=4.03109 StartY=3.5 StartZ=0 EndX=7.06218 EndY=5.25 EndZ=0
    g15: LineSegment StartX=7.06218 StartY=5.25 StartZ=0 EndX=7.06218 EndY=8.75 EndZ=0
    g16: LineSegment StartX=7.06218 StartY=8.75 StartZ=0 EndX=4.03109 EndY=10.5 EndZ=0
    g17: LineSegment StartX=4.03109 StartY=10.5 StartZ=0 EndX=1 EndY=8.75 EndZ=0
    g18: LineSegment StartX=1 StartY=8.75 StartZ=0 EndX=1 EndY=5.25 EndZ=0
    g19: LineSegment StartX=1 StartY=5.25 StartZ=0 EndX=4.03109 EndY=3.5 EndZ=0
    g20: Circle [constr] CenterX=4.03109 CenterY=7 CenterZ=0 NormalX=0 NormalY=0 NormalZ=1 AngleXU=0 Radius=3.5
    g21: LineSegment StartX=-1 StartY=5.25 StartZ=0 EndX=-1 EndY=8.75 EndZ=0
    g22: LineSegment StartX=-1 StartY=8.75 StartZ=0 EndX=-4.03109 EndY=10.5 EndZ=0
    g23: LineSegment StartX=-4.03109 StartY=10.5 StartZ=0 EndX=-7.06218 EndY=8.75 EndZ=0
    g24: LineSegment StartX=-7.06218 StartY=8.75 StartZ=0 EndX=-7.06218 EndY=5.25 EndZ=0
    g25: LineSegment StartX=-7.06218 StartY=5.25 StartZ=0 EndX=-4.03109 EndY=3.5 EndZ=0
    g26: LineSegment StartX=-4.03109 StartY=3.5 StartZ=0 EndX=-1 EndY=5.25 EndZ=0
    g27: Circle [constr] CenterX=-4.03109 CenterY=7 CenterZ=0 NormalX=0 NormalY=0 NormalZ=1 AngleXU=0 Radius=3.5
    g28: LineSegment StartX=-4.96891 StartY=-1.75 StartZ=0 EndX=-4.96891 EndY=1.75 EndZ=0
    g29: LineSegment StartX=-4.96891 StartY=1.75 StartZ=0 EndX=-8 EndY=3.5 EndZ=0
    g30: LineSegment StartX=-8 StartY=3.5 StartZ=0 EndX=-11.0311 EndY=1.75 EndZ=0
    g31: LineSegment StartX=-11.0311 StartY=1.75 StartZ=0 EndX=-11.0311 EndY=-1.75 EndZ=0
    g32: LineSegment StartX=-11.0311 StartY=-1.75 StartZ=0 EndX=-8 EndY=-3.5 EndZ=0
    g33: LineSegment StartX=-8 StartY=-3.5 StartZ=0 EndX=-4.96891 EndY=-1.75 EndZ=0
    g34: Circle [constr] CenterX=-8 CenterY=0 CenterZ=0 NormalX=0 NormalY=0 NormalZ=1 AngleXU=0 Radius=3.5
    g35: LineSegment StartX=-4.03109 StartY=-3.5 StartZ=0 EndX=-7.06218 EndY=-5.25 EndZ=0
    g36: LineSegment StartX=-7.06218 StartY=-5.25 StartZ=0 EndX=-7.06218 EndY=-8.75 EndZ=0
    g37: LineSegment StartX=-7.06218 StartY=-8.75 StartZ=0 EndX=-4.03109 EndY=-10.5 EndZ=0
    g38: LineSegment StartX=-4.03109 StartY=-10.5 StartZ=0 EndX=-1 EndY=-8.75 EndZ=0
    g39: LineSegment StartX=-1 StartY=-8.75 StartZ=0 EndX=-1 EndY=-5.25 EndZ=0
    g40: LineSegment StartX=-1 StartY=-5.25 StartZ=0 EndX=-4.03109 EndY=-3.5 EndZ=0
    g41: Circle [constr] CenterX=-4.03109 CenterY=-7 CenterZ=0 NormalX=0 NormalY=0 NormalZ=1 AngleXU=0 Radius=3.5
    g42: LineSegment StartX=4.03109 StartY=-3.5 StartZ=0 EndX=1 EndY=-5.25 EndZ=0
    g43: LineSegment StartX=1 StartY=-5.25 StartZ=0 EndX=1 EndY=-8.75 EndZ=0
    g44: LineSegment StartX=1 StartY=-8.75 StartZ=0 EndX=4.03109 EndY=-10.5 EndZ=0
    g45: LineSegment StartX=4.03109 StartY=-10.5 StartZ=0 EndX=7.06218 EndY=-8.75 EndZ=0
    g46: LineSegment StartX=7.06218 StartY=-8.75 StartZ=0 EndX=7.06218 EndY=-5.25 EndZ=0
    g47: LineSegment StartX=7.06218 StartY=-5.25 StartZ=0 EndX=4.03109 EndY=-3.5 EndZ=0
    g48: Circle [constr] CenterX=4.03109 CenterY=-7 CenterZ=0 NormalX=0 NormalY=0 NormalZ=1 AngleXU=0 Radius=3.5
  constraints (117):
    c: Coincident(g0,g1)
    c: Coincident(g1,g2)
    c: Coincident(g2,g3)
    c: Coincident(g3,g4)
    c: Coincident(g4,g5)
    c: Coincident(g5,g0)
    c: Equal(g0, g1-g5) x5
    c: PointOnObject(g0,g6)
    c: PointOnObject(g1,g6)
    c: PointOnObject(g2,g6)
    c: PointOnObject(g3,g6)
    c: PointOnObject(g4,g6)
    c: PointOnObject(g5,g6)
    c: Coincident(g6,g-1)
    c: Diameter(g6) = 7
    c: PointOnObject(g0,g-2)
    c: Coincident(g7,g8)
    c: Coincident(g8,g9)
    c: Coincident(g9,g10)
    c: Coincident(g10,g11)
    c: Coincident(g11,g12)
    c: Coincident(g12,g7)
    c: Equal(g7, g8-g12) x5
    c: PointOnObject(g7,g13)
    c: PointOnObject(g8,g13)
    c: PointOnObject(g9,g13)
    c: PointOnObject(g10,g13)
    c: PointOnObject(g11,g13)
    c: PointOnObject(g12,g13)
    c: PointOnObject(g13,g-1)
    c: Diameter(g13) = 7
    c: Distance(g6,g13) = 8
    c: Horizontal(g0,g10)
    c: Coincident(g14,g15)
    c: Coincident(g15,g16)
    c: Coincident(g16,g17)
    c: Coincident(g17,g18)
    c: Coincident(g18,g19)
    c: Coincident(g19,g14)
    c: Equal(g14, g15-g19) x5
    c: PointOnObject(g14,g20)
    c: PointOnObject(g15,g20)
    c: PointOnObject(g16,g20)
    c: PointOnObject(g17,g20)
    c: PointOnObject(g18,g20)
    c: PointOnObject(g19,g20)
    c: Diameter(g20) = 7
    c: DistanceY(g-1,g20) = 7
    c: Vertical(g18)
    c: Distance(g17,g-2) = 1
    c: Coincident(g21,g22)
    c: Coincident(g22,g23)
    c: Coincident(g23,g24)
    c: Coincident(g24,g25)
    c: Coincident(g25,g26)
    c: Coincident(g26,g21)
    c: Equal(g21, g22-g26) x5
    c: PointOnObject(g21,g27)
    c: PointOnObject(g22,g27)
    c: PointOnObject(g23,g27)
    c: PointOnObject(g24,g27)
    c: PointOnObject(g25,g27)
    c: PointOnObject(g26,g27)
    c: Diameter(g27) = 7
    c: DistanceY(g-1,g27) = 7
    c: DistanceX(g21,g-1) = 1
    c: Vertical(g21)
    c: Coincident(g28,g29)
    c: Coincident(g29,g30)
    c: Coincident(g30,g31)
    c: Coincident(g31,g32)
    c: Coincident(g32,g33)
    c: Coincident(g33,g28)
    c: Equal(g28, g29-g33) x5
    c: PointOnObject(g28,g34)
    c: PointOnObject(g29,g34)
    c: PointOnObject(g30,g34)
    c: PointOnObject(g31,g34)
    c: PointOnObject(g32,g34)
    c: PointOnObject(g33,g34)
    c: PointOnObject(g34,g-1)
    c: Diameter(g34) = 7
    c: Vertical(g31)
    c: DistanceX(g34,g-1) = 8
    c: Coincident(g35,g36)
    c: Coincident(g36,g37)
    c: Coincident(g37,g38)
    c: Coincident(g38,g39)
    c: Coincident(g39,g40)
    c: Coincident(g40,g35)
    c: Equal(g35, g36-g40) x5
    c: PointOnObject(g35,g41)
    c: PointOnObject(g36,g41)
    c: PointOnObject(g37,g41)
    c: PointOnObject(g38,g41)
    c: PointOnObject(g39,g41)
    c: PointOnObject(g40,g41)
    c: Coincident(g42,g43)
    c: Coincident(g43,g44)
    c: Coincident(g44,g45)
    c: Coincident(g45,g46)
    c: Coincident(g46,g47)
    c: Coincident(g47,g42)
    c: Equal(g42, g43-g47) x5
    c: PointOnObject(g42,g48)
    c: PointOnObject(g43,g48)
    c: PointOnObject(g44,g48)
    c: PointOnObject(g45,g48)
    c: PointOnObject(g46,g48)
    c: PointOnObject(g47,g48)
    c: Equal(g41,g48)
    c: Diameter(g41) = 7
    c: Vertical(g39)
    c: Vertical(g43)
    c: Distance(g-2,g39) = 1
    c: Symmetric(g38,g43,g-2)
    c: Distance(g41,g-1) = 7
FEATURE [Part::Extrusion] Extrude676  label="hex278"
  Base = -> Sketch685
  Dir = (0,-1,2e-16)
  DirMode = 2
  FaceMakerClass = Part::FaceMakerBullseye
  FaceMakerMode = 3
  LengthFwd = 10
  LengthRev = 0
  Placement = pos=(-36,0,7) rot=(0,0,1;0rad)
  Solid = true
  Symmetric = false
FEATURE [Sketcher::SketchObject] Sketch686
  ArcFitTolerance = 1e-06
  FullyConstrained = true
  MakeInternals = false
  Placement = pos=(0,0,0) rot=(1,0,0;1.5708rad)
  sketch-geometry (49):
    g0: LineSegment StartX=1e-16 StartY=3.5 StartZ=0 EndX=-3.03109 EndY=1.75 EndZ=0
    g1: LineSegment StartX=-3.03109 StartY=1.75 StartZ=0 EndX=-3.03109 EndY=-1.75 EndZ=0
    g2: LineSegment StartX=-3.03109 StartY=-1.75 StartZ=0 EndX=-1e-16 EndY=-3.5 EndZ=0
    g3: LineSegment StartX=-1e-16 StartY=-3.5 StartZ=0 EndX=3.03109 EndY=-1.75 EndZ=0
    g4: LineSegment StartX=3.03109 StartY=-1.75 StartZ=0 EndX=3.03109 EndY=1.75 EndZ=0
    g5: LineSegment StartX=3.03109 StartY=1.75 StartZ=0 EndX=1e-16 EndY=3.5 EndZ=0
    g6: Circle [constr] CenterX=0 CenterY=0 CenterZ=0 NormalX=0 NormalY=0 NormalZ=1 AngleXU=0 Radius=3.5
    g7: LineSegment StartX=4.96892 StartY=-1.75002 StartZ=0 EndX=8.00002 EndY=-3.5 EndZ=0
    g8: LineSegment StartX=8.00002 StartY=-3.5 StartZ=0 EndX=11.0311 EndY=-1.74998 EndZ=0
    g9: LineSegment StartX=11.0311 StartY=-1.74998 StartZ=0 EndX=11.0311 EndY=1.75002 EndZ=0
    g10: LineSegment StartX=11.0311 StartY=1.75002 StartZ=0 EndX=7.99998 EndY=3.5 EndZ=0
    g11: LineSegment StartX=7.99998 StartY=3.5 StartZ=0 EndX=4.9689 EndY=1.74998 EndZ=0
    g12: LineSegment StartX=4.9689 StartY=1.74998 StartZ=0 EndX=4.96892 EndY=-1.75002 EndZ=0
    g13: Circle [constr] CenterX=8 CenterY=0 CenterZ=0 NormalX=0 NormalY=0 NormalZ=1 AngleXU=0 Radius=3.5
    g14: LineSegment StartX=4.03109 StartY=3.5 StartZ=0 EndX=7.06218 EndY=5.25 EndZ=0
    g15: LineSegment StartX=7.06218 StartY=5.25 StartZ=0 EndX=7.06218 EndY=8.75 EndZ=0
    g16: LineSegment StartX=7.06218 StartY=8.75 StartZ=0 EndX=4.03109 EndY=10.5 EndZ=0
    g17: LineSegment StartX=4.03109 StartY=10.5 StartZ=0 EndX=1 EndY=8.75 EndZ=0
    g18: LineSegment StartX=1 StartY=8.75 StartZ=0 EndX=1 EndY=5.25 EndZ=0
    g19: LineSegment StartX=1 StartY=5.25 StartZ=0 EndX=4.03109 EndY=3.5 EndZ=0
    g20: Circle [constr] CenterX=4.03109 CenterY=7 CenterZ=0 NormalX=0 NormalY=0 NormalZ=1 AngleXU=0 Radius=3.5
    g21: LineSegment StartX=-1 StartY=5.25 StartZ=0 EndX=-1 EndY=8.75 EndZ=0
    g22: LineSegment StartX=-1 StartY=8.75 StartZ=0 EndX=-4.03109 EndY=10.5 EndZ=0
    g23: LineSegment StartX=-4.03109 StartY=10.5 StartZ=0 EndX=-7.06218 EndY=8.75 EndZ=0
    g24: LineSegment StartX=-7.06218 StartY=8.75 StartZ=0 EndX=-7.06218 EndY=5.25 EndZ=0
    g25: LineSegment StartX=-7.06218 StartY=5.25 StartZ=0 EndX=-4.03109 EndY=3.5 EndZ=0
    g26: LineSegment StartX=-4.03109 StartY=3.5 StartZ=0 EndX=-1 EndY=5.25 EndZ=0
    g27: Circle [constr] CenterX=-4.03109 CenterY=7 CenterZ=0 NormalX=0 NormalY=0 NormalZ=1 AngleXU=0 Radius=3.5
    g28: LineSegment StartX=-4.96891 StartY=-1.75 StartZ=0 EndX=-4.96891 EndY=1.75 EndZ=0
    g29: LineSegment StartX=-4.96891 StartY=1.75 StartZ=0 EndX=-8 EndY=3.5 EndZ=0
    g30: LineSegment StartX=-8 StartY=3.5 StartZ=0 EndX=-11.0311 EndY=1.75 EndZ=0
    g31: LineSegment StartX=-11.0311 StartY=1.75 StartZ=0 EndX=-11.0311 EndY=-1.75 EndZ=0
    g32: LineSegment StartX=-11.0311 StartY=-1.75 StartZ=0 EndX=-8 EndY=-3.5 EndZ=0
    g33: LineSegment StartX=-8 StartY=-3.5 StartZ=0 EndX=-4.96891 EndY=-1.75 EndZ=0
    g34: Circle [constr] CenterX=-8 CenterY=0 CenterZ=0 NormalX=0 NormalY=0 NormalZ=1 AngleXU=0 Radius=3.5
    g35: LineSegment StartX=-4.03109 StartY=-3.5 StartZ=0 EndX=-7.06218 EndY=-5.25 EndZ=0
    g36: LineSegment StartX=-7.06218 StartY=-5.25 StartZ=0 EndX=-7.06218 EndY=-8.75 EndZ=0
    g37: LineSegment StartX=-7.06218 StartY=-8.75 StartZ=0 EndX=-4.03109 EndY=-10.5 EndZ=0
    g38: LineSegment StartX=-4.03109 StartY=-10.5 StartZ=0 EndX=-1 EndY=-8.75 EndZ=0
    g39: LineSegment StartX=-1 StartY=-8.75 StartZ=0 EndX=-1 EndY=-5.25 EndZ=0
    g40: LineSegment StartX=-1 StartY=-5.25 StartZ=0 EndX=-4.03109 EndY=-3.5 EndZ=0
    g41: Circle [constr] CenterX=-4.03109 CenterY=-7 CenterZ=0 NormalX=0 NormalY=0 NormalZ=1 AngleXU=0 Radius=3.5
    g42: LineSegment StartX=4.03109 StartY=-3.5 StartZ=0 EndX=1 EndY=-5.25 EndZ=0
    g43: LineSegment StartX=1 StartY=-5.25 StartZ=0 EndX=1 EndY=-8.75 EndZ=0
    g44: LineSegment StartX=1 StartY=-8.75 StartZ=0 EndX=4.03109 EndY=-10.5 EndZ=0
    g45: LineSegment StartX=4.03109 StartY=-10.5 StartZ=0 EndX=7.06218 EndY=-8.75 EndZ=0
    g46: LineSegment StartX=7.06218 StartY=-8.75 StartZ=0 EndX=7.06218 EndY=-5.25 EndZ=0
    g47: LineSegment StartX=7.06218 StartY=-5.25 StartZ=0 EndX=4.03109 EndY=-3.5 EndZ=0
    g48: Circle [constr] CenterX=4.03109 CenterY=-7 CenterZ=0 NormalX=0 NormalY=0 NormalZ=1 AngleXU=0 Radius=3.5
  constraints (117):
    c: Coincident(g0,g1)
    c: Coincident(g1,g2)
    c: Coincident(g2,g3)
    c: Coincident(g3,g4)
    c: Coincident(g4,g5)
    c: Coincident(g5,g0)
    c: Equal(g0, g1-g5) x5
    c: PointOnObject(g0,g6)
    c: PointOnObject(g1,g6)
    c: PointOnObject(g2,g6)
    c: PointOnObject(g3,g6)
    c: PointOnObject(g4,g6)
    c: PointOnObject(g5,g6)
    c: Coincident(g6,g-1)
    c: Diameter(g6) = 7
    c: PointOnObject(g0,g-2)
    c: Coincident(g7,g8)
    c: Coincident(g8,g9)
    c: Coincident(g9,g10)
    c: Coincident(g10,g11)
    c: Coincident(g11,g12)
    c: Coincident(g12,g7)
    c: Equal(g7, g8-g12) x5
    c: PointOnObject(g7,g13)
    c: PointOnObject(g8,g13)
    c: PointOnObject(g9,g13)
    c: PointOnObject(g10,g13)
    c: PointOnObject(g11,g13)
    c: PointOnObject(g12,g13)
    c: PointOnObject(g13,g-1)
    c: Diameter(g13) = 7
    c: Distance(g6,g13) = 8
    c: Horizontal(g0,g10)
    c: Coincident(g14,g15)
    c: Coincident(g15,g16)
    c: Coincident(g16,g17)
    c: Coincident(g17,g18)
    c: Coincident(g18,g19)
    c: Coincident(g19,g14)
    c: Equal(g14, g15-g19) x5
    c: PointOnObject(g14,g20)
    c: PointOnObject(g15,g20)
    c: PointOnObject(g16,g20)
    c: PointOnObject(g17,g20)
    c: PointOnObject(g18,g20)
    c: PointOnObject(g19,g20)
    c: Diameter(g20) = 7
    c: DistanceY(g-1,g20) = 7
    c: Vertical(g18)
    c: Distance(g17,g-2) = 1
    c: Coincident(g21,g22)
    c: Coincident(g22,g23)
    c: Coincident(g23,g24)
    c: Coincident(g24,g25)
    c: Coincident(g25,g26)
    c: Coincident(g26,g21)
    c: Equal(g21, g22-g26) x5
    c: PointOnObject(g21,g27)
    c: PointOnObject(g22,g27)
    c: PointOnObject(g23,g27)
    c: PointOnObject(g24,g27)
    c: PointOnObject(g25,g27)
    c: PointOnObject(g26,g27)
    c: Diameter(g27) = 7
    c: DistanceY(g-1,g27) = 7
    c: DistanceX(g21,g-1) = 1
    c: Vertical(g21)
    c: Coincident(g28,g29)
    c: Coincident(g29,g30)
    c: Coincident(g30,g31)
    c: Coincident(g31,g32)
    c: Coincident(g32,g33)
    c: Coincident(g33,g28)
    c: Equal(g28, g29-g33) x5
    c: PointOnObject(g28,g34)
    c: PointOnObject(g29,g34)
    c: PointOnObject(g30,g34)
    c: PointOnObject(g31,g34)
    c: PointOnObject(g32,g34)
    c: PointOnObject(g33,g34)
    c: PointOnObject(g34,g-1)
    c: Diameter(g34) = 7
    c: Vertical(g31)
    c: DistanceX(g34,g-1) = 8
    c: Coincident(g35,g36)
    c: Coincident(g36,g37)
    c: Coincident(g37,g38)
    c: Coincident(g38,g39)
    c: Coincident(g39,g40)
    c: Coincident(g40,g35)
    c: Equal(g35, g36-g40) x5
    c: PointOnObject(g35,g41)
    c: PointOnObject(g36,g41)
    c: PointOnObject(g37,g41)
    c: PointOnObject(g38,g41)
    c: PointOnObject(g39,g41)
    c: PointOnObject(g40,g41)
    c: Coincident(g42,g43)
    c: Coincident(g43,g44)
    c: Coincident(g44,g45)
    c: Coincident(g45,g46)
    c: Coincident(g46,g47)
    c: Coincident(g47,g42)
    c: Equal(g42, g43-g47) x5
    c: PointOnObject(g42,g48)
    c: PointOnObject(g43,g48)
    c: PointOnObject(g44,g48)
    c: PointOnObject(g45,g48)
    c: PointOnObject(g46,g48)
    c: PointOnObject(g47,g48)
    c: Equal(g41,g48)
    c: Diameter(g41) = 7
    c: Vertical(g39)
    c: Vertical(g43)
    c: Distance(g-2,g39) = 1
    c: Symmetric(g38,g43,g-2)
    c: Distance(g41,g-1) = 7
FEATURE [Part::Extrusion] Extrude677  label="hex279"
  Base = -> Sketch686
  Dir = (0,-1,2e-16)
  DirMode = 2
  FaceMakerClass = Part::FaceMakerBullseye
  FaceMakerMode = 3
  LengthFwd = 10
  LengthRev = 0
  Placement = pos=(36,0,7) rot=(0,0,1;0rad)
  Solid = true
  Symmetric = false
FEATURE [Sketcher::SketchObject] Sketch687
  ArcFitTolerance = 1e-06
  FullyConstrained = true
  MakeInternals = false
  Placement = pos=(0,0,0) rot=(1,0,0;1.5708rad)
  sketch-geometry (49):
    g0: LineSegment StartX=1e-16 StartY=3.5 StartZ=0 EndX=-3.03109 EndY=1.75 EndZ=0
    g1: LineSegment StartX=-3.03109 StartY=1.75 StartZ=0 EndX=-3.03109 EndY=-1.75 EndZ=0
    g2: LineSegment StartX=-3.03109 StartY=-1.75 StartZ=0 EndX=-1e-16 EndY=-3.5 EndZ=0
    g3: LineSegment StartX=-1e-16 StartY=-3.5 StartZ=0 EndX=3.03109 EndY=-1.75 EndZ=0
    g4: LineSegment StartX=3.03109 StartY=-1.75 StartZ=0 EndX=3.03109 EndY=1.75 EndZ=0
    g5: LineSegment StartX=3.03109 StartY=1.75 StartZ=0 EndX=1e-16 EndY=3.5 EndZ=0
    g6: Circle [constr] CenterX=0 CenterY=0 CenterZ=0 NormalX=0 NormalY=0 NormalZ=1 AngleXU=0 Radius=3.5
    g7: LineSegment StartX=4.96892 StartY=-1.75002 StartZ=0 EndX=8.00002 EndY=-3.5 EndZ=0
    g8: LineSegment StartX=8.00002 StartY=-3.5 StartZ=0 EndX=11.0311 EndY=-1.74998 EndZ=0
    g9: LineSegment StartX=11.0311 StartY=-1.74998 StartZ=0 EndX=11.0311 EndY=1.75002 EndZ=0
    g10: LineSegment StartX=11.0311 StartY=1.75002 StartZ=0 EndX=7.99998 EndY=3.5 EndZ=0
    g11: LineSegment StartX=7.99998 StartY=3.5 StartZ=0 EndX=4.9689 EndY=1.74998 EndZ=0
    g12: LineSegment StartX=4.9689 StartY=1.74998 StartZ=0 EndX=4.96892 EndY=-1.75002 EndZ=0
    g13: Circle [constr] CenterX=8 CenterY=0 CenterZ=0 NormalX=0 NormalY=0 NormalZ=1 AngleXU=0 Radius=3.5
    g14: LineSegment StartX=4.03109 StartY=3.5 StartZ=0 EndX=7.06218 EndY=5.25 EndZ=0
    g15: LineSegment StartX=7.06218 StartY=5.25 StartZ=0 EndX=7.06218 EndY=8.75 EndZ=0
    g16: LineSegment StartX=7.06218 StartY=8.75 StartZ=0 EndX=4.03109 EndY=10.5 EndZ=0
    g17: LineSegment StartX=4.03109 StartY=10.5 StartZ=0 EndX=1 EndY=8.75 EndZ=0
    g18: LineSegment StartX=1 StartY=8.75 StartZ=0 EndX=1 EndY=5.25 EndZ=0
    g19: LineSegment StartX=1 StartY=5.25 StartZ=0 EndX=4.03109 EndY=3.5 EndZ=0
    g20: Circle [constr] CenterX=4.03109 CenterY=7 CenterZ=0 NormalX=0 NormalY=0 NormalZ=1 AngleXU=0 Radius=3.5
    g21: LineSegment StartX=-1 StartY=5.25 StartZ=0 EndX=-1 EndY=8.75 EndZ=0
    g22: LineSegment StartX=-1 StartY=8.75 StartZ=0 EndX=-4.03109 EndY=10.5 EndZ=0
    g23: LineSegment StartX=-4.03109 StartY=10.5 StartZ=0 EndX=-7.06218 EndY=8.75 EndZ=0
    g24: LineSegment StartX=-7.06218 StartY=8.75 StartZ=0 EndX=-7.06218 EndY=5.25 EndZ=0
    g25: LineSegment StartX=-7.06218 StartY=5.25 StartZ=0 EndX=-4.03109 EndY=3.5 EndZ=0
    g26: LineSegment StartX=-4.03109 StartY=3.5 StartZ=0 EndX=-1 EndY=5.25 EndZ=0
    g27: Circle [constr] CenterX=-4.03109 CenterY=7 CenterZ=0 NormalX=0 NormalY=0 NormalZ=1 AngleXU=0 Radius=3.5
    g28: LineSegment StartX=-4.96891 StartY=-1.75 StartZ=0 EndX=-4.96891 EndY=1.75 EndZ=0
    g29: LineSegment StartX=-4.96891 StartY=1.75 StartZ=0 EndX=-8 EndY=3.5 EndZ=0
    g30: LineSegment StartX=-8 StartY=3.5 StartZ=0 EndX=-11.0311 EndY=1.75 EndZ=0
    g31: LineSegment StartX=-11.0311 StartY=1.75 StartZ=0 EndX=-11.0311 EndY=-1.75 EndZ=0
    g32: LineSegment StartX=-11.0311 StartY=-1.75 StartZ=0 EndX=-8 EndY=-3.5 EndZ=0
    g33: LineSegment StartX=-8 StartY=-3.5 StartZ=0 EndX=-4.96891 EndY=-1.75 EndZ=0
    g34: Circle [constr] CenterX=-8 CenterY=0 CenterZ=0 NormalX=0 NormalY=0 NormalZ=1 AngleXU=0 Radius=3.5
    g35: LineSegment StartX=-4.03109 StartY=-3.5 StartZ=0 EndX=-7.06218 EndY=-5.25 EndZ=0
    g36: LineSegment StartX=-7.06218 StartY=-5.25 StartZ=0 EndX=-7.06218 EndY=-8.75 EndZ=0
    g37: LineSegment StartX=-7.06218 StartY=-8.75 StartZ=0 EndX=-4.03109 EndY=-10.5 EndZ=0
    g38: LineSegment StartX=-4.03109 StartY=-10.5 StartZ=0 EndX=-1 EndY=-8.75 EndZ=0
    g39: LineSegment StartX=-1 StartY=-8.75 StartZ=0 EndX=-1 EndY=-5.25 EndZ=0
    g40: LineSegment StartX=-1 StartY=-5.25 StartZ=0 EndX=-4.03109 EndY=-3.5 EndZ=0
    g41: Circle [constr] CenterX=-4.03109 CenterY=-7 CenterZ=0 NormalX=0 NormalY=0 NormalZ=1 AngleXU=0 Radius=3.5
    g42: LineSegment StartX=4.03109 StartY=-3.5 StartZ=0 EndX=1 EndY=-5.25 EndZ=0
    g43: LineSegment StartX=1 StartY=-5.25 StartZ=0 EndX=1 EndY=-8.75 EndZ=0
    g44: LineSegment StartX=1 StartY=-8.75 StartZ=0 EndX=4.03109 EndY=-10.5 EndZ=0
    g45: LineSegment StartX=4.03109 StartY=-10.5 StartZ=0 EndX=7.06218 EndY=-8.75 EndZ=0
    g46: LineSegment StartX=7.06218 StartY=-8.75 StartZ=0 EndX=7.06218 EndY=-5.25 EndZ=0
    g47: LineSegment StartX=7.06218 StartY=-5.25 StartZ=0 EndX=4.03109 EndY=-3.5 EndZ=0
    g48: Circle [constr] CenterX=4.03109 CenterY=-7 CenterZ=0 NormalX=0 NormalY=0 NormalZ=1 AngleXU=0 Radius=3.5
  constraints (117):
    c: Coincident(g0,g1)
    c: Coincident(g1,g2)
    c: Coincident(g2,g3)
    c: Coincident(g3,g4)
    c: Coincident(g4,g5)
    c: Coincident(g5,g0)
    c: Equal(g0, g1-g5) x5
    c: PointOnObject(g0,g6)
    c: PointOnObject(g1,g6)
    c: PointOnObject(g2,g6)
    c: PointOnObject(g3,g6)
    c: PointOnObject(g4,g6)
    c: PointOnObject(g5,g6)
    c: Coincident(g6,g-1)
    c: Diameter(g6) = 7
    c: PointOnObject(g0,g-2)
    c: Coincident(g7,g8)
    c: Coincident(g8,g9)
    c: Coincident(g9,g10)
    c: Coincident(g10,g11)
    c: Coincident(g11,g12)
    c: Coincident(g12,g7)
    c: Equal(g7, g8-g12) x5
    c: PointOnObject(g7,g13)
    c: PointOnObject(g8,g13)
    c: PointOnObject(g9,g13)
    c: PointOnObject(g10,g13)
    c: PointOnObject(g11,g13)
    c: PointOnObject(g12,g13)
    c: PointOnObject(g13,g-1)
    c: Diameter(g13) = 7
    c: Distance(g6,g13) = 8
    c: Horizontal(g0,g10)
    c: Coincident(g14,g15)
    c: Coincident(g15,g16)
    c: Coincident(g16,g17)
    c: Coincident(g17,g18)
    c: Coincident(g18,g19)
    c: Coincident(g19,g14)
    c: Equal(g14, g15-g19) x5
    c: PointOnObject(g14,g20)
    c: PointOnObject(g15,g20)
    c: PointOnObject(g16,g20)
    c: PointOnObject(g17,g20)
    c: PointOnObject(g18,g20)
    c: PointOnObject(g19,g20)
    c: Diameter(g20) = 7
    c: DistanceY(g-1,g20) = 7
    c: Vertical(g18)
    c: Distance(g17,g-2) = 1
    c: Coincident(g21,g22)
    c: Coincident(g22,g23)
    c: Coincident(g23,g24)
    c: Coincident(g24,g25)
    c: Coincident(g25,g26)
    c: Coincident(g26,g21)
    c: Equal(g21, g22-g26) x5
    c: PointOnObject(g21,g27)
    c: PointOnObject(g22,g27)
    c: PointOnObject(g23,g27)
    c: PointOnObject(g24,g27)
    c: PointOnObject(g25,g27)
    c: PointOnObject(g26,g27)
    c: Diameter(g27) = 7
    c: DistanceY(g-1,g27) = 7
    c: DistanceX(g21,g-1) = 1
    c: Vertical(g21)
    c: Coincident(g28,g29)
    c: Coincident(g29,g30)
    c: Coincident(g30,g31)
    c: Coincident(g31,g32)
    c: Coincident(g32,g33)
    c: Coincident(g33,g28)
    c: Equal(g28, g29-g33) x5
    c: PointOnObject(g28,g34)
    c: PointOnObject(g29,g34)
    c: PointOnObject(g30,g34)
    c: PointOnObject(g31,g34)
    c: PointOnObject(g32,g34)
    c: PointOnObject(g33,g34)
    c: PointOnObject(g34,g-1)
    c: Diameter(g34) = 7
    c: Vertical(g31)
    c: DistanceX(g34,g-1) = 8
    c: Coincident(g35,g36)
    c: Coincident(g36,g37)
    c: Coincident(g37,g38)
    c: Coincident(g38,g39)
    c: Coincident(g39,g40)
    c: Coincident(g40,g35)
    c: Equal(g35, g36-g40) x5
    c: PointOnObject(g35,g41)
    c: PointOnObject(g36,g41)
    c: PointOnObject(g37,g41)
    c: PointOnObject(g38,g41)
    c: PointOnObject(g39,g41)
    c: PointOnObject(g40,g41)
    c: Coincident(g42,g43)
    c: Coincident(g43,g44)
    c: Coincident(g44,g45)
    c: Coincident(g45,g46)
    c: Coincident(g46,g47)
    c: Coincident(g47,g42)
    c: Equal(g42, g43-g47) x5
    c: PointOnObject(g42,g48)
    c: PointOnObject(g43,g48)
    c: PointOnObject(g44,g48)
    c: PointOnObject(g45,g48)
    c: PointOnObject(g46,g48)
    c: PointOnObject(g47,g48)
    c: Equal(g41,g48)
    c: Diameter(g41) = 7
    c: Vertical(g39)
    c: Vertical(g43)
    c: Distance(g-2,g39) = 1
    c: Symmetric(g38,g43,g-2)
    c: Distance(g41,g-1) = 7
FEATURE [Part::Extrusion] Extrude678  label="hex280"
  Base = -> Sketch687
  Dir = (0,-1,2e-16)
  DirMode = 2
  FaceMakerClass = Part::FaceMakerBullseye
  FaceMakerMode = 3
  LengthFwd = 10
  LengthRev = 0
  Placement = pos=(32,0,28) rot=(0,0,1;0rad)
  Solid = true
  Symmetric = false
FEATURE [Sketcher::SketchObject] Sketch688
  ArcFitTolerance = 1e-06
  FullyConstrained = true
  MakeInternals = false
  Placement = pos=(0,0,0) rot=(1,0,0;1.5708rad)
  sketch-geometry (49):
    g0: LineSegment StartX=1e-16 StartY=3.5 StartZ=0 EndX=-3.03109 EndY=1.75 EndZ=0
    g1: LineSegment StartX=-3.03109 StartY=1.75 StartZ=0 EndX=-3.03109 EndY=-1.75 EndZ=0
    g2: LineSegment StartX=-3.03109 StartY=-1.75 StartZ=0 EndX=-1e-16 EndY=-3.5 EndZ=0
    g3: LineSegment StartX=-1e-16 StartY=-3.5 StartZ=0 EndX=3.03109 EndY=-1.75 EndZ=0
    g4: LineSegment StartX=3.03109 StartY=-1.75 StartZ=0 EndX=3.03109 EndY=1.75 EndZ=0
    g5: LineSegment StartX=3.03109 StartY=1.75 StartZ=0 EndX=1e-16 EndY=3.5 EndZ=0
    g6: Circle [constr] CenterX=0 CenterY=0 CenterZ=0 NormalX=0 NormalY=0 NormalZ=1 AngleXU=0 Radius=3.5
    g7: LineSegment StartX=4.96892 StartY=-1.75002 StartZ=0 EndX=8.00002 EndY=-3.5 EndZ=0
    g8: LineSegment StartX=8.00002 StartY=-3.5 StartZ=0 EndX=11.0311 EndY=-1.74998 EndZ=0
    g9: LineSegment StartX=11.0311 StartY=-1.74998 StartZ=0 EndX=11.0311 EndY=1.75002 EndZ=0
    g10: LineSegment StartX=11.0311 StartY=1.75002 StartZ=0 EndX=7.99998 EndY=3.5 EndZ=0
    g11: LineSegment StartX=7.99998 StartY=3.5 StartZ=0 EndX=4.9689 EndY=1.74998 EndZ=0
    g12: LineSegment StartX=4.9689 StartY=1.74998 StartZ=0 EndX=4.96892 EndY=-1.75002 EndZ=0
    g13: Circle [constr] CenterX=8 CenterY=0 CenterZ=0 NormalX=0 NormalY=0 NormalZ=1 AngleXU=0 Radius=3.5
    g14: LineSegment StartX=4.03109 StartY=3.5 StartZ=0 EndX=7.06218 EndY=5.25 EndZ=0
    g15: LineSegment StartX=7.06218 StartY=5.25 StartZ=0 EndX=7.06218 EndY=8.75 EndZ=0
    g16: LineSegment StartX=7.06218 StartY=8.75 StartZ=0 EndX=4.03109 EndY=10.5 EndZ=0
    g17: LineSegment StartX=4.03109 StartY=10.5 StartZ=0 EndX=1 EndY=8.75 EndZ=0
    g18: LineSegment StartX=1 StartY=8.75 StartZ=0 EndX=1 EndY=5.25 EndZ=0
    g19: LineSegment StartX=1 StartY=5.25 StartZ=0 EndX=4.03109 EndY=3.5 EndZ=0
    g20: Circle [constr] CenterX=4.03109 CenterY=7 CenterZ=0 NormalX=0 NormalY=0 NormalZ=1 AngleXU=0 Radius=3.5
    g21: LineSegment StartX=-1 StartY=5.25 StartZ=0 EndX=-1 EndY=8.75 EndZ=0
    g22: LineSegment StartX=-1 StartY=8.75 StartZ=0 EndX=-4.03109 EndY=10.5 EndZ=0
    g23: LineSegment StartX=-4.03109 StartY=10.5 StartZ=0 EndX=-7.06218 EndY=8.75 EndZ=0
    g24: LineSegment StartX=-7.06218 StartY=8.75 StartZ=0 EndX=-7.06218 EndY=5.25 EndZ=0
    g25: LineSegment StartX=-7.06218 StartY=5.25 StartZ=0 EndX=-4.03109 EndY=3.5 EndZ=0
    g26: LineSegment StartX=-4.03109 StartY=3.5 StartZ=0 EndX=-1 EndY=5.25 EndZ=0
    g27: Circle [constr] CenterX=-4.03109 CenterY=7 CenterZ=0 NormalX=0 NormalY=0 NormalZ=1 AngleXU=0 Radius=3.5
    g28: LineSegment StartX=-4.96891 StartY=-1.75 StartZ=0 EndX=-4.96891 EndY=1.75 EndZ=0
    g29: LineSegment StartX=-4.96891 StartY=1.75 StartZ=0 EndX=-8 EndY=3.5 EndZ=0
    g30: LineSegment StartX=-8 StartY=3.5 StartZ=0 EndX=-11.0311 EndY=1.75 EndZ=0
    g31: LineSegment StartX=-11.0311 StartY=1.75 StartZ=0 EndX=-11.0311 EndY=-1.75 EndZ=0
    g32: LineSegment StartX=-11.0311 StartY=-1.75 StartZ=0 EndX=-8 EndY=-3.5 EndZ=0
    g33: LineSegment StartX=-8 StartY=-3.5 StartZ=0 EndX=-4.96891 EndY=-1.75 EndZ=0
    g34: Circle [constr] CenterX=-8 CenterY=0 CenterZ=0 NormalX=0 NormalY=0 NormalZ=1 AngleXU=0 Radius=3.5
    g35: LineSegment StartX=-4.03109 StartY=-3.5 StartZ=0 EndX=-7.06218 EndY=-5.25 EndZ=0
    g36: LineSegment StartX=-7.06218 StartY=-5.25 StartZ=0 EndX=-7.06218 EndY=-8.75 EndZ=0
    g37: LineSegment StartX=-7.06218 StartY=-8.75 StartZ=0 EndX=-4.03109 EndY=-10.5 EndZ=0
    g38: LineSegment StartX=-4.03109 StartY=-10.5 StartZ=0 EndX=-1 EndY=-8.75 EndZ=0
    g39: LineSegment StartX=-1 StartY=-8.75 StartZ=0 EndX=-1 EndY=-5.25 EndZ=0
    g40: LineSegment StartX=-1 StartY=-5.25 StartZ=0 EndX=-4.03109 EndY=-3.5 EndZ=0
    g41: Circle [constr] CenterX=-4.03109 CenterY=-7 CenterZ=0 NormalX=0 NormalY=0 NormalZ=1 AngleXU=0 Radius=3.5
    g42: LineSegment StartX=4.03109 StartY=-3.5 StartZ=0 EndX=1 EndY=-5.25 EndZ=0
    g43: LineSegment StartX=1 StartY=-5.25 StartZ=0 EndX=1 EndY=-8.75 EndZ=0
    g44: LineSegment StartX=1 StartY=-8.75 StartZ=0 EndX=4.03109 EndY=-10.5 EndZ=0
    g45: LineSegment StartX=4.03109 StartY=-10.5 StartZ=0 EndX=7.06218 EndY=-8.75 EndZ=0
    g46: LineSegment StartX=7.06218 StartY=-8.75 StartZ=0 EndX=7.06218 EndY=-5.25 EndZ=0
    g47: LineSegment StartX=7.06218 StartY=-5.25 StartZ=0 EndX=4.03109 EndY=-3.5 EndZ=0
    g48: Circle [constr] CenterX=4.03109 CenterY=-7 CenterZ=0 NormalX=0 NormalY=0 NormalZ=1 AngleXU=0 Radius=3.5
  constraints (117):
    c: Coincident(g0,g1)
    c: Coincident(g1,g2)
    c: Coincident(g2,g3)
    c: Coincident(g3,g4)
    c: Coincident(g4,g5)
    c: Coincident(g5,g0)
    c: Equal(g0, g1-g5) x5
    c: PointOnObject(g0,g6)
    c: PointOnObject(g1,g6)
    c: PointOnObject(g2,g6)
    c: PointOnObject(g3,g6)
    c: PointOnObject(g4,g6)
    c: PointOnObject(g5,g6)
    c: Coincident(g6,g-1)
    c: Diameter(g6) = 7
    c: PointOnObject(g0,g-2)
    c: Coincident(g7,g8)
    c: Coincident(g8,g9)
    c: Coincident(g9,g10)
    c: Coincident(g10,g11)
    c: Coincident(g11,g12)
    c: Coincident(g12,g7)
    c: Equal(g7, g8-g12) x5
    c: PointOnObject(g7,g13)
    c: PointOnObject(g8,g13)
    c: PointOnObject(g9,g13)
    c: PointOnObject(g10,g13)
    c: PointOnObject(g11,g13)
    c: PointOnObject(g12,g13)
    c: PointOnObject(g13,g-1)
    c: Diameter(g13) = 7
    c: Distance(g6,g13) = 8
    c: Horizontal(g0,g10)
    c: Coincident(g14,g15)
    c: Coincident(g15,g16)
    c: Coincident(g16,g17)
    c: Coincident(g17,g18)
    c: Coincident(g18,g19)
    c: Coincident(g19,g14)
    c: Equal(g14, g15-g19) x5
    c: PointOnObject(g14,g20)
    c: PointOnObject(g15,g20)
    c: PointOnObject(g16,g20)
    c: PointOnObject(g17,g20)
    c: PointOnObject(g18,g20)
    c: PointOnObject(g19,g20)
    c: Diameter(g20) = 7
    c: DistanceY(g-1,g20) = 7
    c: Vertical(g18)
    c: Distance(g17,g-2) = 1
    c: Coincident(g21,g22)
    c: Coincident(g22,g23)
    c: Coincident(g23,g24)
    c: Coincident(g24,g25)
    c: Coincident(g25,g26)
    c: Coincident(g26,g21)
    c: Equal(g21, g22-g26) x5
    c: PointOnObject(g21,g27)
    c: PointOnObject(g22,g27)
    c: PointOnObject(g23,g27)
    c: PointOnObject(g24,g27)
    c: PointOnObject(g25,g27)
    c: PointOnObject(g26,g27)
    c: Diameter(g27) = 7
    c: DistanceY(g-1,g27) = 7
    c: DistanceX(g21,g-1) = 1
    c: Vertical(g21)
    c: Coincident(g28,g29)
    c: Coincident(g29,g30)
    c: Coincident(g30,g31)
    c: Coincident(g31,g32)
    c: Coincident(g32,g33)
    c: Coincident(g33,g28)
    c: Equal(g28, g29-g33) x5
    c: PointOnObject(g28,g34)
    c: PointOnObject(g29,g34)
    c: PointOnObject(g30,g34)
    c: PointOnObject(g31,g34)
    c: PointOnObject(g32,g34)
    c: PointOnObject(g33,g34)
    c: PointOnObject(g34,g-1)
    c: Diameter(g34) = 7
    c: Vertical(g31)
    c: DistanceX(g34,g-1) = 8
    c: Coincident(g35,g36)
    c: Coincident(g36,g37)
    c: Coincident(g37,g38)
    c: Coincident(g38,g39)
    c: Coincident(g39,g40)
    c: Coincident(g40,g35)
    c: Equal(g35, g36-g40) x5
    c: PointOnObject(g35,g41)
    c: PointOnObject(g36,g41)
    c: PointOnObject(g37,g41)
    c: PointOnObject(g38,g41)
    c: PointOnObject(g39,g41)
    c: PointOnObject(g40,g41)
    c: Coincident(g42,g43)
    c: Coincident(g43,g44)
    c: Coincident(g44,g45)
    c: Coincident(g45,g46)
    c: Coincident(g46,g47)
    c: Coincident(g47,g42)
    c: Equal(g42, g43-g47) x5
    c: PointOnObject(g42,g48)
    c: PointOnObject(g43,g48)
    c: PointOnObject(g44,g48)
    c: PointOnObject(g45,g48)
    c: PointOnObject(g46,g48)
    c: PointOnObject(g47,g48)
    c: Equal(g41,g48)
    c: Diameter(g41) = 7
    c: Vertical(g39)
    c: Vertical(g43)
    c: Distance(g-2,g39) = 1
    c: Symmetric(g38,g43,g-2)
    c: Distance(g41,g-1) = 7
FEATURE [Part::Extrusion] Extrude679  label="hex281"
  Base = -> Sketch688
  Dir = (0,-1,2e-16)
  DirMode = 2
  FaceMakerClass = Part::FaceMakerBullseye
  FaceMakerMode = 3
  LengthFwd = 10
  LengthRev = 0
  Placement = pos=(-40,0,-14) rot=(0,0,1;0rad)
  Solid = true
  Symmetric = false
FEATURE [Sketcher::SketchObject] Sketch689
  ArcFitTolerance = 1e-06
  FullyConstrained = true
  MakeInternals = false
  Placement = pos=(0,0,0) rot=(1,0,0;1.5708rad)
  sketch-geometry (49):
    g0: LineSegment StartX=1e-16 StartY=3.5 StartZ=0 EndX=-3.03109 EndY=1.75 EndZ=0
    g1: LineSegment StartX=-3.03109 StartY=1.75 StartZ=0 EndX=-3.03109 EndY=-1.75 EndZ=0
    g2: LineSegment StartX=-3.03109 StartY=-1.75 StartZ=0 EndX=-1e-16 EndY=-3.5 EndZ=0
    g3: LineSegment StartX=-1e-16 StartY=-3.5 StartZ=0 EndX=3.03109 EndY=-1.75 EndZ=0
    g4: LineSegment StartX=3.03109 StartY=-1.75 StartZ=0 EndX=3.03109 EndY=1.75 EndZ=0
    g5: LineSegment StartX=3.03109 StartY=1.75 StartZ=0 EndX=1e-16 EndY=3.5 EndZ=0
    g6: Circle [constr] CenterX=0 CenterY=0 CenterZ=0 NormalX=0 NormalY=0 NormalZ=1 AngleXU=0 Radius=3.5
    g7: LineSegment StartX=4.96892 StartY=-1.75002 StartZ=0 EndX=8.00002 EndY=-3.5 EndZ=0
    g8: LineSegment StartX=8.00002 StartY=-3.5 StartZ=0 EndX=11.0311 EndY=-1.74998 EndZ=0
    g9: LineSegment StartX=11.0311 StartY=-1.74998 StartZ=0 EndX=11.0311 EndY=1.75002 EndZ=0
    g10: LineSegment StartX=11.0311 StartY=1.75002 StartZ=0 EndX=7.99998 EndY=3.5 EndZ=0
    g11: LineSegment StartX=7.99998 StartY=3.5 StartZ=0 EndX=4.9689 EndY=1.74998 EndZ=0
    g12: LineSegment StartX=4.9689 StartY=1.74998 StartZ=0 EndX=4.96892 EndY=-1.75002 EndZ=0
    g13: Circle [constr] CenterX=8 CenterY=0 CenterZ=0 NormalX=0 NormalY=0 NormalZ=1 AngleXU=0 Radius=3.5
    g14: LineSegment StartX=4.03109 StartY=3.5 StartZ=0 EndX=7.06218 EndY=5.25 EndZ=0
    g15: LineSegment StartX=7.06218 StartY=5.25 StartZ=0 EndX=7.06218 EndY=8.75 EndZ=0
    g16: LineSegment StartX=7.06218 StartY=8.75 StartZ=0 EndX=4.03109 EndY=10.5 EndZ=0
    g17: LineSegment StartX=4.03109 StartY=10.5 StartZ=0 EndX=1 EndY=8.75 EndZ=0
    g18: LineSegment StartX=1 StartY=8.75 StartZ=0 EndX=1 EndY=5.25 EndZ=0
    g19: LineSegment StartX=1 StartY=5.25 StartZ=0 EndX=4.03109 EndY=3.5 EndZ=0
    g20: Circle [constr] CenterX=4.03109 CenterY=7 CenterZ=0 NormalX=0 NormalY=0 NormalZ=1 AngleXU=0 Radius=3.5
    g21: LineSegment StartX=-1 StartY=5.25 StartZ=0 EndX=-1 EndY=8.75 EndZ=0
    g22: LineSegment StartX=-1 StartY=8.75 StartZ=0 EndX=-4.03109 EndY=10.5 EndZ=0
    g23: LineSegment StartX=-4.03109 StartY=10.5 StartZ=0 EndX=-7.06218 EndY=8.75 EndZ=0
    g24: LineSegment StartX=-7.06218 StartY=8.75 StartZ=0 EndX=-7.06218 EndY=5.25 EndZ=0
    g25: LineSegment StartX=-7.06218 StartY=5.25 StartZ=0 EndX=-4.03109 EndY=3.5 EndZ=0
    g26: LineSegment StartX=-4.03109 StartY=3.5 StartZ=0 EndX=-1 EndY=5.25 EndZ=0
    g27: Circle [constr] CenterX=-4.03109 CenterY=7 CenterZ=0 NormalX=0 NormalY=0 NormalZ=1 AngleXU=0 Radius=3.5
    g28: LineSegment StartX=-4.96891 StartY=-1.75 StartZ=0 EndX=-4.96891 EndY=1.75 EndZ=0
    g29: LineSegment StartX=-4.96891 StartY=1.75 StartZ=0 EndX=-8 EndY=3.5 EndZ=0
    g30: LineSegment StartX=-8 StartY=3.5 StartZ=0 EndX=-11.0311 EndY=1.75 EndZ=0
    g31: LineSegment StartX=-11.0311 StartY=1.75 StartZ=0 EndX=-11.0311 EndY=-1.75 EndZ=0
    g32: LineSegment StartX=-11.0311 StartY=-1.75 StartZ=0 EndX=-8 EndY=-3.5 EndZ=0
    g33: LineSegment StartX=-8 StartY=-3.5 StartZ=0 EndX=-4.96891 EndY=-1.75 EndZ=0
    g34: Circle [constr] CenterX=-8 CenterY=0 CenterZ=0 NormalX=0 NormalY=0 NormalZ=1 AngleXU=0 Radius=3.5
    g35: LineSegment StartX=-4.03109 StartY=-3.5 StartZ=0 EndX=-7.06218 EndY=-5.25 EndZ=0
    g36: LineSegment StartX=-7.06218 StartY=-5.25 StartZ=0 EndX=-7.06218 EndY=-8.75 EndZ=0
    g37: LineSegment StartX=-7.06218 StartY=-8.75 StartZ=0 EndX=-4.03109 EndY=-10.5 EndZ=0
    g38: LineSegment StartX=-4.03109 StartY=-10.5 StartZ=0 EndX=-1 EndY=-8.75 EndZ=0
    g39: LineSegment StartX=-1 StartY=-8.75 StartZ=0 EndX=-1 EndY=-5.25 EndZ=0
    g40: LineSegment StartX=-1 StartY=-5.25 StartZ=0 EndX=-4.03109 EndY=-3.5 EndZ=0
    g41: Circle [constr] CenterX=-4.03109 CenterY=-7 CenterZ=0 NormalX=0 NormalY=0 NormalZ=1 AngleXU=0 Radius=3.5
    g42: LineSegment StartX=4.03109 StartY=-3.5 StartZ=0 EndX=1 EndY=-5.25 EndZ=0
    g43: LineSegment StartX=1 StartY=-5.25 StartZ=0 EndX=1 EndY=-8.75 EndZ=0
    g44: LineSegment StartX=1 StartY=-8.75 StartZ=0 EndX=4.03109 EndY=-10.5 EndZ=0
    g45: LineSegment StartX=4.03109 StartY=-10.5 StartZ=0 EndX=7.06218 EndY=-8.75 EndZ=0
    g46: LineSegment StartX=7.06218 StartY=-8.75 StartZ=0 EndX=7.06218 EndY=-5.25 EndZ=0
    g47: LineSegment StartX=7.06218 StartY=-5.25 StartZ=0 EndX=4.03109 EndY=-3.5 EndZ=0
    g48: Circle [constr] CenterX=4.03109 CenterY=-7 CenterZ=0 NormalX=0 NormalY=0 NormalZ=1 AngleXU=0 Radius=3.5
  constraints (117):
    c: Coincident(g0,g1)
    c: Coincident(g1,g2)
    c: Coincident(g2,g3)
    c: Coincident(g3,g4)
    c: Coincident(g4,g5)
    c: Coincident(g5,g0)
    c: Equal(g0, g1-g5) x5
    c: PointOnObject(g0,g6)
    c: PointOnObject(g1,g6)
    c: PointOnObject(g2,g6)
    c: PointOnObject(g3,g6)
    c: PointOnObject(g4,g6)
    c: PointOnObject(g5,g6)
    c: Coincident(g6,g-1)
    c: Diameter(g6) = 7
    c: PointOnObject(g0,g-2)
    c: Coincident(g7,g8)
    c: Coincident(g8,g9)
    c: Coincident(g9,g10)
    c: Coincident(g10,g11)
    c: Coincident(g11,g12)
    c: Coincident(g12,g7)
    c: Equal(g7, g8-g12) x5
    c: PointOnObject(g7,g13)
    c: PointOnObject(g8,g13)
    c: PointOnObject(g9,g13)
    c: PointOnObject(g10,g13)
    c: PointOnObject(g11,g13)
    c: PointOnObject(g12,g13)
    c: PointOnObject(g13,g-1)
    c: Diameter(g13) = 7
    c: Distance(g6,g13) = 8
    c: Horizontal(g0,g10)
    c: Coincident(g14,g15)
    c: Coincident(g15,g16)
    c: Coincident(g16,g17)
    c: Coincident(g17,g18)
    c: Coincident(g18,g19)
    c: Coincident(g19,g14)
    c: Equal(g14, g15-g19) x5
    c: PointOnObject(g14,g20)
    c: PointOnObject(g15,g20)
    c: PointOnObject(g16,g20)
    c: PointOnObject(g17,g20)
    c: PointOnObject(g18,g20)
    c: PointOnObject(g19,g20)
    c: Diameter(g20) = 7
    c: DistanceY(g-1,g20) = 7
    c: Vertical(g18)
    c: Distance(g17,g-2) = 1
    c: Coincident(g21,g22)
    c: Coincident(g22,g23)
    c: Coincident(g23,g24)
    c: Coincident(g24,g25)
    c: Coincident(g25,g26)
    c: Coincident(g26,g21)
    c: Equal(g21, g22-g26) x5
    c: PointOnObject(g21,g27)
    c: PointOnObject(g22,g27)
    c: PointOnObject(g23,g27)
    c: PointOnObject(g24,g27)
    c: PointOnObject(g25,g27)
    c: PointOnObject(g26,g27)
    c: Diameter(g27) = 7
    c: DistanceY(g-1,g27) = 7
    c: DistanceX(g21,g-1) = 1
    c: Vertical(g21)
    c: Coincident(g28,g29)
    c: Coincident(g29,g30)
    c: Coincident(g30,g31)
    c: Coincident(g31,g32)
    c: Coincident(g32,g33)
    c: Coincident(g33,g28)
    c: Equal(g28, g29-g33) x5
    c: PointOnObject(g28,g34)
    c: PointOnObject(g29,g34)
    c: PointOnObject(g30,g34)
    c: PointOnObject(g31,g34)
    c: PointOnObject(g32,g34)
    c: PointOnObject(g33,g34)
    c: PointOnObject(g34,g-1)
    c: Diameter(g34) = 7
    c: Vertical(g31)
    c: DistanceX(g34,g-1) = 8
    c: Coincident(g35,g36)
    c: Coincident(g36,g37)
    c: Coincident(g37,g38)
    c: Coincident(g38,g39)
    c: Coincident(g39,g40)
    c: Coincident(g40,g35)
    c: Equal(g35, g36-g40) x5
    c: PointOnObject(g35,g41)
    c: PointOnObject(g36,g41)
    c: PointOnObject(g37,g41)
    c: PointOnObject(g38,g41)
    c: PointOnObject(g39,g41)
    c: PointOnObject(g40,g41)
    c: Coincident(g42,g43)
    c: Coincident(g43,g44)
    c: Coincident(g44,g45)
    c: Coincident(g45,g46)
    c: Coincident(g46,g47)
    c: Coincident(g47,g42)
    c: Equal(g42, g43-g47) x5
    c: PointOnObject(g42,g48)
    c: PointOnObject(g43,g48)
    c: PointOnObject(g44,g48)
    c: PointOnObject(g45,g48)
    c: PointOnObject(g46,g48)
    c: PointOnObject(g47,g48)
    c: Equal(g41,g48)
    c: Diameter(g41) = 7
    c: Vertical(g39)
    c: Vertical(g43)
    c: Distance(g-2,g39) = 1
    c: Symmetric(g38,g43,g-2)
    c: Distance(g41,g-1) = 7
FEATURE [Part::Extrusion] Extrude680  label="hex282"
  Base = -> Sketch689
  Dir = (0,-1,2e-16)
  DirMode = 2
  FaceMakerClass = Part::FaceMakerBullseye
  FaceMakerMode = 3
  LengthFwd = 10
  LengthRev = 0
  Placement = pos=(-24,0,-28) rot=(0,0,1;0rad)
  Solid = true
  Symmetric = false
FEATURE [Sketcher::SketchObject] Sketch690
  ArcFitTolerance = 1e-06
  FullyConstrained = true
  MakeInternals = false
  Placement = pos=(0,0,0) rot=(1,0,0;1.5708rad)
  sketch-geometry (49):
    g0: LineSegment StartX=1e-16 StartY=3.5 StartZ=0 EndX=-3.03109 EndY=1.75 EndZ=0
    g1: LineSegment StartX=-3.03109 StartY=1.75 StartZ=0 EndX=-3.03109 EndY=-1.75 EndZ=0
    g2: LineSegment StartX=-3.03109 StartY=-1.75 StartZ=0 EndX=-1e-16 EndY=-3.5 EndZ=0
    g3: LineSegment StartX=-1e-16 StartY=-3.5 StartZ=0 EndX=3.03109 EndY=-1.75 EndZ=0
    g4: LineSegment StartX=3.03109 StartY=-1.75 StartZ=0 EndX=3.03109 EndY=1.75 EndZ=0
    g5: LineSegment StartX=3.03109 StartY=1.75 StartZ=0 EndX=1e-16 EndY=3.5 EndZ=0
    g6: Circle [constr] CenterX=0 CenterY=0 CenterZ=0 NormalX=0 NormalY=0 NormalZ=1 AngleXU=0 Radius=3.5
    g7: LineSegment StartX=4.96892 StartY=-1.75002 StartZ=0 EndX=8.00002 EndY=-3.5 EndZ=0
    g8: LineSegment StartX=8.00002 StartY=-3.5 StartZ=0 EndX=11.0311 EndY=-1.74998 EndZ=0
    g9: LineSegment StartX=11.0311 StartY=-1.74998 StartZ=0 EndX=11.0311 EndY=1.75002 EndZ=0
    g10: LineSegment StartX=11.0311 StartY=1.75002 StartZ=0 EndX=7.99998 EndY=3.5 EndZ=0
    g11: LineSegment StartX=7.99998 StartY=3.5 StartZ=0 EndX=4.9689 EndY=1.74998 EndZ=0
    g12: LineSegment StartX=4.9689 StartY=1.74998 StartZ=0 EndX=4.96892 EndY=-1.75002 EndZ=0
    g13: Circle [constr] CenterX=8 CenterY=0 CenterZ=0 NormalX=0 NormalY=0 NormalZ=1 AngleXU=0 Radius=3.5
    g14: LineSegment StartX=4.03109 StartY=3.5 StartZ=0 EndX=7.06218 EndY=5.25 EndZ=0
    g15: LineSegment StartX=7.06218 StartY=5.25 StartZ=0 EndX=7.06218 EndY=8.75 EndZ=0
    g16: LineSegment StartX=7.06218 StartY=8.75 StartZ=0 EndX=4.03109 EndY=10.5 EndZ=0
    g17: LineSegment StartX=4.03109 StartY=10.5 StartZ=0 EndX=1 EndY=8.75 EndZ=0
    g18: LineSegment StartX=1 StartY=8.75 StartZ=0 EndX=1 EndY=5.25 EndZ=0
    g19: LineSegment StartX=1 StartY=5.25 StartZ=0 EndX=4.03109 EndY=3.5 EndZ=0
    g20: Circle [constr] CenterX=4.03109 CenterY=7 CenterZ=0 NormalX=0 NormalY=0 NormalZ=1 AngleXU=0 Radius=3.5
    g21: LineSegment StartX=-1 StartY=5.25 StartZ=0 EndX=-1 EndY=8.75 EndZ=0
    g22: LineSegment StartX=-1 StartY=8.75 StartZ=0 EndX=-4.03109 EndY=10.5 EndZ=0
    g23: LineSegment StartX=-4.03109 StartY=10.5 StartZ=0 EndX=-7.06218 EndY=8.75 EndZ=0
    g24: LineSegment StartX=-7.06218 StartY=8.75 StartZ=0 EndX=-7.06218 EndY=5.25 EndZ=0
    g25: LineSegment StartX=-7.06218 StartY=5.25 StartZ=0 EndX=-4.03109 EndY=3.5 EndZ=0
    g26: LineSegment StartX=-4.03109 StartY=3.5 StartZ=0 EndX=-1 EndY=5.25 EndZ=0
    g27: Circle [constr] CenterX=-4.03109 CenterY=7 CenterZ=0 NormalX=0 NormalY=0 NormalZ=1 AngleXU=0 Radius=3.5
    g28: LineSegment StartX=-4.96891 StartY=-1.75 StartZ=0 EndX=-4.96891 EndY=1.75 EndZ=0
    g29: LineSegment StartX=-4.96891 StartY=1.75 StartZ=0 EndX=-8 EndY=3.5 EndZ=0
    g30: LineSegment StartX=-8 StartY=3.5 StartZ=0 EndX=-11.0311 EndY=1.75 EndZ=0
    g31: LineSegment StartX=-11.0311 StartY=1.75 StartZ=0 EndX=-11.0311 EndY=-1.75 EndZ=0
    g32: LineSegment StartX=-11.0311 StartY=-1.75 StartZ=0 EndX=-8 EndY=-3.5 EndZ=0
    g33: LineSegment StartX=-8 StartY=-3.5 StartZ=0 EndX=-4.96891 EndY=-1.75 EndZ=0
    g34: Circle [constr] CenterX=-8 CenterY=0 CenterZ=0 NormalX=0 NormalY=0 NormalZ=1 AngleXU=0 Radius=3.5
    g35: LineSegment StartX=-4.03109 StartY=-3.5 StartZ=0 EndX=-7.06218 EndY=-5.25 EndZ=0
    g36: LineSegment StartX=-7.06218 StartY=-5.25 StartZ=0 EndX=-7.06218 EndY=-8.75 EndZ=0
    g37: LineSegment StartX=-7.06218 StartY=-8.75 StartZ=0 EndX=-4.03109 EndY=-10.5 EndZ=0
    g38: LineSegment StartX=-4.03109 StartY=-10.5 StartZ=0 EndX=-1 EndY=-8.75 EndZ=0
    g39: LineSegment StartX=-1 StartY=-8.75 StartZ=0 EndX=-1 EndY=-5.25 EndZ=0
    g40: LineSegment StartX=-1 StartY=-5.25 StartZ=0 EndX=-4.03109 EndY=-3.5 EndZ=0
    g41: Circle [constr] CenterX=-4.03109 CenterY=-7 CenterZ=0 NormalX=0 NormalY=0 NormalZ=1 AngleXU=0 Radius=3.5
    g42: LineSegment StartX=4.03109 StartY=-3.5 StartZ=0 EndX=1 EndY=-5.25 EndZ=0
    g43: LineSegment StartX=1 StartY=-5.25 StartZ=0 EndX=1 EndY=-8.75 EndZ=0
    g44: LineSegment StartX=1 StartY=-8.75 StartZ=0 EndX=4.03109 EndY=-10.5 EndZ=0
    g45: LineSegment StartX=4.03109 StartY=-10.5 StartZ=0 EndX=7.06218 EndY=-8.75 EndZ=0
    g46: LineSegment StartX=7.06218 StartY=-8.75 StartZ=0 EndX=7.06218 EndY=-5.25 EndZ=0
    g47: LineSegment StartX=7.06218 StartY=-5.25 StartZ=0 EndX=4.03109 EndY=-3.5 EndZ=0
    g48: Circle [constr] CenterX=4.03109 CenterY=-7 CenterZ=0 NormalX=0 NormalY=0 NormalZ=1 AngleXU=0 Radius=3.5
  constraints (117):
    c: Coincident(g0,g1)
    c: Coincident(g1,g2)
    c: Coincident(g2,g3)
    c: Coincident(g3,g4)
    c: Coincident(g4,g5)
    c: Coincident(g5,g0)
    c: Equal(g0, g1-g5) x5
    c: PointOnObject(g0,g6)
    c: PointOnObject(g1,g6)
    c: PointOnObject(g2,g6)
    c: PointOnObject(g3,g6)
    c: PointOnObject(g4,g6)
    c: PointOnObject(g5,g6)
    c: Coincident(g6,g-1)
    c: Diameter(g6) = 7
    c: PointOnObject(g0,g-2)
    c: Coincident(g7,g8)
    c: Coincident(g8,g9)
    c: Coincident(g9,g10)
    c: Coincident(g10,g11)
    c: Coincident(g11,g12)
    c: Coincident(g12,g7)
    c: Equal(g7, g8-g12) x5
    c: PointOnObject(g7,g13)
    c: PointOnObject(g8,g13)
    c: PointOnObject(g9,g13)
    c: PointOnObject(g10,g13)
    c: PointOnObject(g11,g13)
    c: PointOnObject(g12,g13)
    c: PointOnObject(g13,g-1)
    c: Diameter(g13) = 7
    c: Distance(g6,g13) = 8
    c: Horizontal(g0,g10)
    c: Coincident(g14,g15)
    c: Coincident(g15,g16)
    c: Coincident(g16,g17)
    c: Coincident(g17,g18)
    c: Coincident(g18,g19)
    c: Coincident(g19,g14)
    c: Equal(g14, g15-g19) x5
    c: PointOnObject(g14,g20)
    c: PointOnObject(g15,g20)
    c: PointOnObject(g16,g20)
    c: PointOnObject(g17,g20)
    c: PointOnObject(g18,g20)
    c: PointOnObject(g19,g20)
    c: Diameter(g20) = 7
    c: DistanceY(g-1,g20) = 7
    c: Vertical(g18)
    c: Distance(g17,g-2) = 1
    c: Coincident(g21,g22)
    c: Coincident(g22,g23)
    c: Coincident(g23,g24)
    c: Coincident(g24,g25)
    c: Coincident(g25,g26)
    c: Coincident(g26,g21)
    c: Equal(g21, g22-g26) x5
    c: PointOnObject(g21,g27)
    c: PointOnObject(g22,g27)
    c: PointOnObject(g23,g27)
    c: PointOnObject(g24,g27)
    c: PointOnObject(g25,g27)
    c: PointOnObject(g26,g27)
    c: Diameter(g27) = 7
    c: DistanceY(g-1,g27) = 7
    c: DistanceX(g21,g-1) = 1
    c: Vertical(g21)
    c: Coincident(g28,g29)
    c: Coincident(g29,g30)
    c: Coincident(g30,g31)
    c: Coincident(g31,g32)
    c: Coincident(g32,g33)
    c: Coincident(g33,g28)
    c: Equal(g28, g29-g33) x5
    c: PointOnObject(g28,g34)
    c: PointOnObject(g29,g34)
    c: PointOnObject(g30,g34)
    c: PointOnObject(g31,g34)
    c: PointOnObject(g32,g34)
    c: PointOnObject(g33,g34)
    c: PointOnObject(g34,g-1)
    c: Diameter(g34) = 7
    c: Vertical(g31)
    c: DistanceX(g34,g-1) = 8
    c: Coincident(g35,g36)
    c: Coincident(g36,g37)
    c: Coincident(g37,g38)
    c: Coincident(g38,g39)
    c: Coincident(g39,g40)
    c: Coincident(g40,g35)
    c: Equal(g35, g36-g40) x5
    c: PointOnObject(g35,g41)
    c: PointOnObject(g36,g41)
    c: PointOnObject(g37,g41)
    c: PointOnObject(g38,g41)
    c: PointOnObject(g39,g41)
    c: PointOnObject(g40,g41)
    c: Coincident(g42,g43)
    c: Coincident(g43,g44)
    c: Coincident(g44,g45)
    c: Coincident(g45,g46)
    c: Coincident(g46,g47)
    c: Coincident(g47,g42)
    c: Equal(g42, g43-g47) x5
    c: PointOnObject(g42,g48)
    c: PointOnObject(g43,g48)
    c: PointOnObject(g44,g48)
    c: PointOnObject(g45,g48)
    c: PointOnObject(g46,g48)
    c: PointOnObject(g47,g48)
    c: Equal(g41,g48)
    c: Diameter(g41) = 7
    c: Vertical(g39)
    c: Vertical(g43)
    c: Distance(g-2,g39) = 1
    c: Symmetric(g38,g43,g-2)
    c: Distance(g41,g-1) = 7
FEATURE [Part::Extrusion] Extrude681  label="hex283"
  Base = -> Sketch690
  Dir = (0,-1,2e-16)
  DirMode = 2
  FaceMakerClass = Part::FaceMakerBullseye
  FaceMakerMode = 3
  LengthFwd = 10
  LengthRev = 0
  Placement = pos=(-8,0,-42) rot=(0,0,1;0rad)
  Solid = true
  Symmetric = false
FEATURE [Sketcher::SketchObject] Sketch691
  ArcFitTolerance = 1e-06
  FullyConstrained = true
  MakeInternals = false
  Placement = pos=(0,0,0) rot=(1,0,0;1.5708rad)
  sketch-geometry (49):
    g0: LineSegment StartX=1e-16 StartY=3.5 StartZ=0 EndX=-3.03109 EndY=1.75 EndZ=0
    g1: LineSegment StartX=-3.03109 StartY=1.75 StartZ=0 EndX=-3.03109 EndY=-1.75 EndZ=0
    g2: LineSegment StartX=-3.03109 StartY=-1.75 StartZ=0 EndX=-1e-16 EndY=-3.5 EndZ=0
    g3: LineSegment StartX=-1e-16 StartY=-3.5 StartZ=0 EndX=3.03109 EndY=-1.75 EndZ=0
    g4: LineSegment StartX=3.03109 StartY=-1.75 StartZ=0 EndX=3.03109 EndY=1.75 EndZ=0
    g5: LineSegment StartX=3.03109 StartY=1.75 StartZ=0 EndX=1e-16 EndY=3.5 EndZ=0
    g6: Circle [constr] CenterX=0 CenterY=0 CenterZ=0 NormalX=0 NormalY=0 NormalZ=1 AngleXU=0 Radius=3.5
    g7: LineSegment StartX=4.96892 StartY=-1.75002 StartZ=0 EndX=8.00002 EndY=-3.5 EndZ=0
    g8: LineSegment StartX=8.00002 StartY=-3.5 StartZ=0 EndX=11.0311 EndY=-1.74998 EndZ=0
    g9: LineSegment StartX=11.0311 StartY=-1.74998 StartZ=0 EndX=11.0311 EndY=1.75002 EndZ=0
    g10: LineSegment StartX=11.0311 StartY=1.75002 StartZ=0 EndX=7.99998 EndY=3.5 EndZ=0
    g11: LineSegment StartX=7.99998 StartY=3.5 StartZ=0 EndX=4.9689 EndY=1.74998 EndZ=0
    g12: LineSegment StartX=4.9689 StartY=1.74998 StartZ=0 EndX=4.96892 EndY=-1.75002 EndZ=0
    g13: Circle [constr] CenterX=8 CenterY=0 CenterZ=0 NormalX=0 NormalY=0 NormalZ=1 AngleXU=0 Radius=3.5
    g14: LineSegment StartX=4.03109 StartY=3.5 StartZ=0 EndX=7.06218 EndY=5.25 EndZ=0
    g15: LineSegment StartX=7.06218 StartY=5.25 StartZ=0 EndX=7.06218 EndY=8.75 EndZ=0
    g16: LineSegment StartX=7.06218 StartY=8.75 StartZ=0 EndX=4.03109 EndY=10.5 EndZ=0
    g17: LineSegment StartX=4.03109 StartY=10.5 StartZ=0 EndX=1 EndY=8.75 EndZ=0
    g18: LineSegment StartX=1 StartY=8.75 StartZ=0 EndX=1 EndY=5.25 EndZ=0
    g19: LineSegment StartX=1 StartY=5.25 StartZ=0 EndX=4.03109 EndY=3.5 EndZ=0
    g20: Circle [constr] CenterX=4.03109 CenterY=7 CenterZ=0 NormalX=0 NormalY=0 NormalZ=1 AngleXU=0 Radius=3.5
    g21: LineSegment StartX=-1 StartY=5.25 StartZ=0 EndX=-1 EndY=8.75 EndZ=0
    g22: LineSegment StartX=-1 StartY=8.75 StartZ=0 EndX=-4.03109 EndY=10.5 EndZ=0
    g23: LineSegment StartX=-4.03109 StartY=10.5 StartZ=0 EndX=-7.06218 EndY=8.75 EndZ=0
    g24: LineSegment StartX=-7.06218 StartY=8.75 StartZ=0 EndX=-7.06218 EndY=5.25 EndZ=0
    g25: LineSegment StartX=-7.06218 StartY=5.25 StartZ=0 EndX=-4.03109 EndY=3.5 EndZ=0
    g26: LineSegment StartX=-4.03109 StartY=3.5 StartZ=0 EndX=-1 EndY=5.25 EndZ=0
    g27: Circle [constr] CenterX=-4.03109 CenterY=7 CenterZ=0 NormalX=0 NormalY=0 NormalZ=1 AngleXU=0 Radius=3.5
    g28: LineSegment StartX=-4.96891 StartY=-1.75 StartZ=0 EndX=-4.96891 EndY=1.75 EndZ=0
    g29: LineSegment StartX=-4.96891 StartY=1.75 StartZ=0 EndX=-8 EndY=3.5 EndZ=0
    g30: LineSegment StartX=-8 StartY=3.5 StartZ=0 EndX=-11.0311 EndY=1.75 EndZ=0
    g31: LineSegment StartX=-11.0311 StartY=1.75 StartZ=0 EndX=-11.0311 EndY=-1.75 EndZ=0
    g32: LineSegment StartX=-11.0311 StartY=-1.75 StartZ=0 EndX=-8 EndY=-3.5 EndZ=0
    g33: LineSegment StartX=-8 StartY=-3.5 StartZ=0 EndX=-4.96891 EndY=-1.75 EndZ=0
    g34: Circle [constr] CenterX=-8 CenterY=0 CenterZ=0 NormalX=0 NormalY=0 NormalZ=1 AngleXU=0 Radius=3.5
    g35: LineSegment StartX=-4.03109 StartY=-3.5 StartZ=0 EndX=-7.06218 EndY=-5.25 EndZ=0
    g36: LineSegment StartX=-7.06218 StartY=-5.25 StartZ=0 EndX=-7.06218 EndY=-8.75 EndZ=0
    g37: LineSegment StartX=-7.06218 StartY=-8.75 StartZ=0 EndX=-4.03109 EndY=-10.5 EndZ=0
    g38: LineSegment StartX=-4.03109 StartY=-10.5 StartZ=0 EndX=-1 EndY=-8.75 EndZ=0
    g39: LineSegment StartX=-1 StartY=-8.75 StartZ=0 EndX=-1 EndY=-5.25 EndZ=0
    g40: LineSegment StartX=-1 StartY=-5.25 StartZ=0 EndX=-4.03109 EndY=-3.5 EndZ=0
    g41: Circle [constr] CenterX=-4.03109 CenterY=-7 CenterZ=0 NormalX=0 NormalY=0 NormalZ=1 AngleXU=0 Radius=3.5
    g42: LineSegment StartX=4.03109 StartY=-3.5 StartZ=0 EndX=1 EndY=-5.25 EndZ=0
    g43: LineSegment StartX=1 StartY=-5.25 StartZ=0 EndX=1 EndY=-8.75 EndZ=0
    g44: LineSegment StartX=1 StartY=-8.75 StartZ=0 EndX=4.03109 EndY=-10.5 EndZ=0
    g45: LineSegment StartX=4.03109 StartY=-10.5 StartZ=0 EndX=7.06218 EndY=-8.75 EndZ=0
    g46: LineSegment StartX=7.06218 StartY=-8.75 StartZ=0 EndX=7.06218 EndY=-5.25 EndZ=0
    g47: LineSegment StartX=7.06218 StartY=-5.25 StartZ=0 EndX=4.03109 EndY=-3.5 EndZ=0
    g48: Circle [constr] CenterX=4.03109 CenterY=-7 CenterZ=0 NormalX=0 NormalY=0 NormalZ=1 AngleXU=0 Radius=3.5
  constraints (117):
    c: Coincident(g0,g1)
    c: Coincident(g1,g2)
    c: Coincident(g2,g3)
    c: Coincident(g3,g4)
    c: Coincident(g4,g5)
    c: Coincident(g5,g0)
    c: Equal(g0, g1-g5) x5
    c: PointOnObject(g0,g6)
    c: PointOnObject(g1,g6)
    c: PointOnObject(g2,g6)
    c: PointOnObject(g3,g6)
    c: PointOnObject(g4,g6)
    c: PointOnObject(g5,g6)
    c: Coincident(g6,g-1)
    c: Diameter(g6) = 7
    c: PointOnObject(g0,g-2)
    c: Coincident(g7,g8)
    c: Coincident(g8,g9)
    c: Coincident(g9,g10)
    c: Coincident(g10,g11)
    c: Coincident(g11,g12)
    c: Coincident(g12,g7)
    c: Equal(g7, g8-g12) x5
    c: PointOnObject(g7,g13)
    c: PointOnObject(g8,g13)
    c: PointOnObject(g9,g13)
    c: PointOnObject(g10,g13)
    c: PointOnObject(g11,g13)
    c: PointOnObject(g12,g13)
    c: PointOnObject(g13,g-1)
    c: Diameter(g13) = 7
    c: Distance(g6,g13) = 8
    c: Horizontal(g0,g10)
    c: Coincident(g14,g15)
    c: Coincident(g15,g16)
    c: Coincident(g16,g17)
    c: Coincident(g17,g18)
    c: Coincident(g18,g19)
    c: Coincident(g19,g14)
    c: Equal(g14, g15-g19) x5
    c: PointOnObject(g14,g20)
    c: PointOnObject(g15,g20)
    c: PointOnObject(g16,g20)
    c: PointOnObject(g17,g20)
    c: PointOnObject(g18,g20)
    c: PointOnObject(g19,g20)
    c: Diameter(g20) = 7
    c: DistanceY(g-1,g20) = 7
    c: Vertical(g18)
    c: Distance(g17,g-2) = 1
    c: Coincident(g21,g22)
    c: Coincident(g22,g23)
    c: Coincident(g23,g24)
    c: Coincident(g24,g25)
    c: Coincident(g25,g26)
    c: Coincident(g26,g21)
    c: Equal(g21, g22-g26) x5
    c: PointOnObject(g21,g27)
    c: PointOnObject(g22,g27)
    c: PointOnObject(g23,g27)
    c: PointOnObject(g24,g27)
    c: PointOnObject(g25,g27)
    c: PointOnObject(g26,g27)
    c: Diameter(g27) = 7
    c: DistanceY(g-1,g27) = 7
    c: DistanceX(g21,g-1) = 1
    c: Vertical(g21)
    c: Coincident(g28,g29)
    c: Coincident(g29,g30)
    c: Coincident(g30,g31)
    c: Coincident(g31,g32)
    c: Coincident(g32,g33)
    c: Coincident(g33,g28)
    c: Equal(g28, g29-g33) x5
    c: PointOnObject(g28,g34)
    c: PointOnObject(g29,g34)
    c: PointOnObject(g30,g34)
    c: PointOnObject(g31,g34)
    c: PointOnObject(g32,g34)
    c: PointOnObject(g33,g34)
    c: PointOnObject(g34,g-1)
    c: Diameter(g34) = 7
    c: Vertical(g31)
    c: DistanceX(g34,g-1) = 8
    c: Coincident(g35,g36)
    c: Coincident(g36,g37)
    c: Coincident(g37,g38)
    c: Coincident(g38,g39)
    c: Coincident(g39,g40)
    c: Coincident(g40,g35)
    c: Equal(g35, g36-g40) x5
    c: PointOnObject(g35,g41)
    c: PointOnObject(g36,g41)
    c: PointOnObject(g37,g41)
    c: PointOnObject(g38,g41)
    c: PointOnObject(g39,g41)
    c: PointOnObject(g40,g41)
    c: Coincident(g42,g43)
    c: Coincident(g43,g44)
    c: Coincident(g44,g45)
    c: Coincident(g45,g46)
    c: Coincident(g46,g47)
    c: Coincident(g47,g42)
    c: Equal(g42, g43-g47) x5
    c: PointOnObject(g42,g48)
    c: PointOnObject(g43,g48)
    c: PointOnObject(g44,g48)
    c: PointOnObject(g45,g48)
    c: PointOnObject(g46,g48)
    c: PointOnObject(g47,g48)
    c: Equal(g41,g48)
    c: Diameter(g41) = 7
    c: Vertical(g39)
    c: Vertical(g43)
    c: Distance(g-2,g39) = 1
    c: Symmetric(g38,g43,g-2)
    c: Distance(g41,g-1) = 7
FEATURE [Part::Extrusion] Extrude682  label="hex284"
  Base = -> Sketch691
  Dir = (0,-1,2e-16)
  DirMode = 2
  FaceMakerClass = Part::FaceMakerBullseye
  FaceMakerMode = 3
  LengthFwd = 10
  LengthRev = 0
  Placement = pos=(32,0,-28) rot=(0,0,1;0rad)
  Solid = true
  Symmetric = false
FEATURE [Sketcher::SketchObject] Sketch692
  ArcFitTolerance = 1e-06
  FullyConstrained = true
  MakeInternals = false
  Placement = pos=(0,0,0) rot=(1,0,0;1.5708rad)
  sketch-geometry (49):
    g0: LineSegment StartX=1e-16 StartY=3.5 StartZ=0 EndX=-3.03109 EndY=1.75 EndZ=0
    g1: LineSegment StartX=-3.03109 StartY=1.75 StartZ=0 EndX=-3.03109 EndY=-1.75 EndZ=0
    g2: LineSegment StartX=-3.03109 StartY=-1.75 StartZ=0 EndX=-1e-16 EndY=-3.5 EndZ=0
    g3: LineSegment StartX=-1e-16 StartY=-3.5 StartZ=0 EndX=3.03109 EndY=-1.75 EndZ=0
    g4: LineSegment StartX=3.03109 StartY=-1.75 StartZ=0 EndX=3.03109 EndY=1.75 EndZ=0
    g5: LineSegment StartX=3.03109 StartY=1.75 StartZ=0 EndX=1e-16 EndY=3.5 EndZ=0
    g6: Circle [constr] CenterX=0 CenterY=0 CenterZ=0 NormalX=0 NormalY=0 NormalZ=1 AngleXU=0 Radius=3.5
    g7: LineSegment StartX=4.96892 StartY=-1.75002 StartZ=0 EndX=8.00002 EndY=-3.5 EndZ=0
    g8: LineSegment StartX=8.00002 StartY=-3.5 StartZ=0 EndX=11.0311 EndY=-1.74998 EndZ=0
    g9: LineSegment StartX=11.0311 StartY=-1.74998 StartZ=0 EndX=11.0311 EndY=1.75002 EndZ=0
    g10: LineSegment StartX=11.0311 StartY=1.75002 StartZ=0 EndX=7.99998 EndY=3.5 EndZ=0
    g11: LineSegment StartX=7.99998 StartY=3.5 StartZ=0 EndX=4.9689 EndY=1.74998 EndZ=0
    g12: LineSegment StartX=4.9689 StartY=1.74998 StartZ=0 EndX=4.96892 EndY=-1.75002 EndZ=0
    g13: Circle [constr] CenterX=8 CenterY=0 CenterZ=0 NormalX=0 NormalY=0 NormalZ=1 AngleXU=0 Radius=3.5
    g14: LineSegment StartX=4.03109 StartY=3.5 StartZ=0 EndX=7.06218 EndY=5.25 EndZ=0
    g15: LineSegment StartX=7.06218 StartY=5.25 StartZ=0 EndX=7.06218 EndY=8.75 EndZ=0
    g16: LineSegment StartX=7.06218 StartY=8.75 StartZ=0 EndX=4.03109 EndY=10.5 EndZ=0
    g17: LineSegment StartX=4.03109 StartY=10.5 StartZ=0 EndX=1 EndY=8.75 EndZ=0
    g18: LineSegment StartX=1 StartY=8.75 StartZ=0 EndX=1 EndY=5.25 EndZ=0
    g19: LineSegment StartX=1 StartY=5.25 StartZ=0 EndX=4.03109 EndY=3.5 EndZ=0
    g20: Circle [constr] CenterX=4.03109 CenterY=7 CenterZ=0 NormalX=0 NormalY=0 NormalZ=1 AngleXU=0 Radius=3.5
    g21: LineSegment StartX=-1 StartY=5.25 StartZ=0 EndX=-1 EndY=8.75 EndZ=0
    g22: LineSegment StartX=-1 StartY=8.75 StartZ=0 EndX=-4.03109 EndY=10.5 EndZ=0
    g23: LineSegment StartX=-4.03109 StartY=10.5 StartZ=0 EndX=-7.06218 EndY=8.75 EndZ=0
    g24: LineSegment StartX=-7.06218 StartY=8.75 StartZ=0 EndX=-7.06218 EndY=5.25 EndZ=0
    g25: LineSegment StartX=-7.06218 StartY=5.25 StartZ=0 EndX=-4.03109 EndY=3.5 EndZ=0
    g26: LineSegment StartX=-4.03109 StartY=3.5 StartZ=0 EndX=-1 EndY=5.25 EndZ=0
    g27: Circle [constr] CenterX=-4.03109 CenterY=7 CenterZ=0 NormalX=0 NormalY=0 NormalZ=1 AngleXU=0 Radius=3.5
    g28: LineSegment StartX=-4.96891 StartY=-1.75 StartZ=0 EndX=-4.96891 EndY=1.75 EndZ=0
    g29: LineSegment StartX=-4.96891 StartY=1.75 StartZ=0 EndX=-8 EndY=3.5 EndZ=0
    g30: LineSegment StartX=-8 StartY=3.5 StartZ=0 EndX=-11.0311 EndY=1.75 EndZ=0
    g31: LineSegment StartX=-11.0311 StartY=1.75 StartZ=0 EndX=-11.0311 EndY=-1.75 EndZ=0
    g32: LineSegment StartX=-11.0311 StartY=-1.75 StartZ=0 EndX=-8 EndY=-3.5 EndZ=0
    g33: LineSegment StartX=-8 StartY=-3.5 StartZ=0 EndX=-4.96891 EndY=-1.75 EndZ=0
    g34: Circle [constr] CenterX=-8 CenterY=0 CenterZ=0 NormalX=0 NormalY=0 NormalZ=1 AngleXU=0 Radius=3.5
    g35: LineSegment StartX=-4.03109 StartY=-3.5 StartZ=0 EndX=-7.06218 EndY=-5.25 EndZ=0
    g36: LineSegment StartX=-7.06218 StartY=-5.25 StartZ=0 EndX=-7.06218 EndY=-8.75 EndZ=0
    g37: LineSegment StartX=-7.06218 StartY=-8.75 StartZ=0 EndX=-4.03109 EndY=-10.5 EndZ=0
    g38: LineSegment StartX=-4.03109 StartY=-10.5 StartZ=0 EndX=-1 EndY=-8.75 EndZ=0
    g39: LineSegment StartX=-1 StartY=-8.75 StartZ=0 EndX=-1 EndY=-5.25 EndZ=0
    g40: LineSegment StartX=-1 StartY=-5.25 StartZ=0 EndX=-4.03109 EndY=-3.5 EndZ=0
    g41: Circle [constr] CenterX=-4.03109 CenterY=-7 CenterZ=0 NormalX=0 NormalY=0 NormalZ=1 AngleXU=0 Radius=3.5
    g42: LineSegment StartX=4.03109 StartY=-3.5 StartZ=0 EndX=1 EndY=-5.25 EndZ=0
    g43: LineSegment StartX=1 StartY=-5.25 StartZ=0 EndX=1 EndY=-8.75 EndZ=0
    g44: LineSegment StartX=1 StartY=-8.75 StartZ=0 EndX=4.03109 EndY=-10.5 EndZ=0
    g45: LineSegment StartX=4.03109 StartY=-10.5 StartZ=0 EndX=7.06218 EndY=-8.75 EndZ=0
    g46: LineSegment StartX=7.06218 StartY=-8.75 StartZ=0 EndX=7.06218 EndY=-5.25 EndZ=0
    g47: LineSegment StartX=7.06218 StartY=-5.25 StartZ=0 EndX=4.03109 EndY=-3.5 EndZ=0
    g48: Circle [constr] CenterX=4.03109 CenterY=-7 CenterZ=0 NormalX=0 NormalY=0 NormalZ=1 AngleXU=0 Radius=3.5
  constraints (117):
    c: Coincident(g0,g1)
    c: Coincident(g1,g2)
    c: Coincident(g2,g3)
    c: Coincident(g3,g4)
    c: Coincident(g4,g5)
    c: Coincident(g5,g0)
    c: Equal(g0, g1-g5) x5
    c: PointOnObject(g0,g6)
    c: PointOnObject(g1,g6)
    c: PointOnObject(g2,g6)
    c: PointOnObject(g3,g6)
    c: PointOnObject(g4,g6)
    c: PointOnObject(g5,g6)
    c: Coincident(g6,g-1)
    c: Diameter(g6) = 7
    c: PointOnObject(g0,g-2)
    c: Coincident(g7,g8)
    c: Coincident(g8,g9)
    c: Coincident(g9,g10)
    c: Coincident(g10,g11)
    c: Coincident(g11,g12)
    c: Coincident(g12,g7)
    c: Equal(g7, g8-g12) x5
    c: PointOnObject(g7,g13)
    c: PointOnObject(g8,g13)
    c: PointOnObject(g9,g13)
    c: PointOnObject(g10,g13)
    c: PointOnObject(g11,g13)
    c: PointOnObject(g12,g13)
    c: PointOnObject(g13,g-1)
    c: Diameter(g13) = 7
    c: Distance(g6,g13) = 8
    c: Horizontal(g0,g10)
    c: Coincident(g14,g15)
    c: Coincident(g15,g16)
    c: Coincident(g16,g17)
    c: Coincident(g17,g18)
    c: Coincident(g18,g19)
    c: Coincident(g19,g14)
    c: Equal(g14, g15-g19) x5
    c: PointOnObject(g14,g20)
    c: PointOnObject(g15,g20)
    c: PointOnObject(g16,g20)
    c: PointOnObject(g17,g20)
    c: PointOnObject(g18,g20)
    c: PointOnObject(g19,g20)
    c: Diameter(g20) = 7
    c: DistanceY(g-1,g20) = 7
    c: Vertical(g18)
    c: Distance(g17,g-2) = 1
    c: Coincident(g21,g22)
    c: Coincident(g22,g23)
    c: Coincident(g23,g24)
    c: Coincident(g24,g25)
    c: Coincident(g25,g26)
    c: Coincident(g26,g21)
    c: Equal(g21, g22-g26) x5
    c: PointOnObject(g21,g27)
    c: PointOnObject(g22,g27)
    c: PointOnObject(g23,g27)
    c: PointOnObject(g24,g27)
    c: PointOnObject(g25,g27)
    c: PointOnObject(g26,g27)
    c: Diameter(g27) = 7
    c: DistanceY(g-1,g27) = 7
    c: DistanceX(g21,g-1) = 1
    c: Vertical(g21)
    c: Coincident(g28,g29)
    c: Coincident(g29,g30)
    c: Coincident(g30,g31)
    c: Coincident(g31,g32)
    c: Coincident(g32,g33)
    c: Coincident(g33,g28)
    c: Equal(g28, g29-g33) x5
    c: PointOnObject(g28,g34)
    c: PointOnObject(g29,g34)
    c: PointOnObject(g30,g34)
    c: PointOnObject(g31,g34)
    c: PointOnObject(g32,g34)
    c: PointOnObject(g33,g34)
    c: PointOnObject(g34,g-1)
    c: Diameter(g34) = 7
    c: Vertical(g31)
    c: DistanceX(g34,g-1) = 8
    c: Coincident(g35,g36)
    c: Coincident(g36,g37)
    c: Coincident(g37,g38)
    c: Coincident(g38,g39)
    c: Coincident(g39,g40)
    c: Coincident(g40,g35)
    c: Equal(g35, g36-g40) x5
    c: PointOnObject(g35,g41)
    c: PointOnObject(g36,g41)
    c: PointOnObject(g37,g41)
    c: PointOnObject(g38,g41)
    c: PointOnObject(g39,g41)
    c: PointOnObject(g40,g41)
    c: Coincident(g42,g43)
    c: Coincident(g43,g44)
    c: Coincident(g44,g45)
    c: Coincident(g45,g46)
    c: Coincident(g46,g47)
    c: Coincident(g47,g42)
    c: Equal(g42, g43-g47) x5
    c: PointOnObject(g42,g48)
    c: PointOnObject(g43,g48)
    c: PointOnObject(g44,g48)
    c: PointOnObject(g45,g48)
    c: PointOnObject(g46,g48)
    c: PointOnObject(g47,g48)
    c: Equal(g41,g48)
    c: Diameter(g41) = 7
    c: Vertical(g39)
    c: Vertical(g43)
    c: Distance(g-2,g39) = 1
    c: Symmetric(g38,g43,g-2)
    c: Distance(g41,g-1) = 7
FEATURE [Part::Extrusion] Extrude683  label="hex285"
  Base = -> Sketch692
  Dir = (0,-1,2e-16)
  DirMode = 2
  FaceMakerClass = Part::FaceMakerBullseye
  FaceMakerMode = 3
  LengthFwd = 10
  LengthRev = 0
  Placement = pos=(36,0,-7) rot=(0,0,1;0rad)
  Solid = true
  Symmetric = false
FEATURE [Sketcher::SketchObject] Sketch693
  ArcFitTolerance = 1e-06
  FullyConstrained = true
  MakeInternals = false
  Placement = pos=(0,0,0) rot=(1,0,0;1.5708rad)
  sketch-geometry (49):
    g0: LineSegment StartX=1e-16 StartY=3.5 StartZ=0 EndX=-3.03109 EndY=1.75 EndZ=0
    g1: LineSegment StartX=-3.03109 StartY=1.75 StartZ=0 EndX=-3.03109 EndY=-1.75 EndZ=0
    g2: LineSegment StartX=-3.03109 StartY=-1.75 StartZ=0 EndX=-1e-16 EndY=-3.5 EndZ=0
    g3: LineSegment StartX=-1e-16 StartY=-3.5 StartZ=0 EndX=3.03109 EndY=-1.75 EndZ=0
    g4: LineSegment StartX=3.03109 StartY=-1.75 StartZ=0 EndX=3.03109 EndY=1.75 EndZ=0
    g5: LineSegment StartX=3.03109 StartY=1.75 StartZ=0 EndX=1e-16 EndY=3.5 EndZ=0
    g6: Circle [constr] CenterX=0 CenterY=0 CenterZ=0 NormalX=0 NormalY=0 NormalZ=1 AngleXU=0 Radius=3.5
    g7: LineSegment StartX=4.96892 StartY=-1.75002 StartZ=0 EndX=8.00002 EndY=-3.5 EndZ=0
    g8: LineSegment StartX=8.00002 StartY=-3.5 StartZ=0 EndX=11.0311 EndY=-1.74998 EndZ=0
    g9: LineSegment StartX=11.0311 StartY=-1.74998 StartZ=0 EndX=11.0311 EndY=1.75002 EndZ=0
    g10: LineSegment StartX=11.0311 StartY=1.75002 StartZ=0 EndX=7.99998 EndY=3.5 EndZ=0
    g11: LineSegment StartX=7.99998 StartY=3.5 StartZ=0 EndX=4.9689 EndY=1.74998 EndZ=0
    g12: LineSegment StartX=4.9689 StartY=1.74998 StartZ=0 EndX=4.96892 EndY=-1.75002 EndZ=0
    g13: Circle [constr] CenterX=8 CenterY=0 CenterZ=0 NormalX=0 NormalY=0 NormalZ=1 AngleXU=0 Radius=3.5
    g14: LineSegment StartX=4.03109 StartY=3.5 StartZ=0 EndX=7.06218 EndY=5.25 EndZ=0
    g15: LineSegment StartX=7.06218 StartY=5.25 StartZ=0 EndX=7.06218 EndY=8.75 EndZ=0
    g16: LineSegment StartX=7.06218 StartY=8.75 StartZ=0 EndX=4.03109 EndY=10.5 EndZ=0
    g17: LineSegment StartX=4.03109 StartY=10.5 StartZ=0 EndX=1 EndY=8.75 EndZ=0
    g18: LineSegment StartX=1 StartY=8.75 StartZ=0 EndX=1 EndY=5.25 EndZ=0
    g19: LineSegment StartX=1 StartY=5.25 StartZ=0 EndX=4.03109 EndY=3.5 EndZ=0
    g20: Circle [constr] CenterX=4.03109 CenterY=7 CenterZ=0 NormalX=0 NormalY=0 NormalZ=1 AngleXU=0 Radius=3.5
    g21: LineSegment StartX=-1 StartY=5.25 StartZ=0 EndX=-1 EndY=8.75 EndZ=0
    g22: LineSegment StartX=-1 StartY=8.75 StartZ=0 EndX=-4.03109 EndY=10.5 EndZ=0
    g23: LineSegment StartX=-4.03109 StartY=10.5 StartZ=0 EndX=-7.06218 EndY=8.75 EndZ=0
    g24: LineSegment StartX=-7.06218 StartY=8.75 StartZ=0 EndX=-7.06218 EndY=5.25 EndZ=0
    g25: LineSegment StartX=-7.06218 StartY=5.25 StartZ=0 EndX=-4.03109 EndY=3.5 EndZ=0
    g26: LineSegment StartX=-4.03109 StartY=3.5 StartZ=0 EndX=-1 EndY=5.25 EndZ=0
    g27: Circle [constr] CenterX=-4.03109 CenterY=7 CenterZ=0 NormalX=0 NormalY=0 NormalZ=1 AngleXU=0 Radius=3.5
    g28: LineSegment StartX=-4.96891 StartY=-1.75 StartZ=0 EndX=-4.96891 EndY=1.75 EndZ=0
    g29: LineSegment StartX=-4.96891 StartY=1.75 StartZ=0 EndX=-8 EndY=3.5 EndZ=0
    g30: LineSegment StartX=-8 StartY=3.5 StartZ=0 EndX=-11.0311 EndY=1.75 EndZ=0
    g31: LineSegment StartX=-11.0311 StartY=1.75 StartZ=0 EndX=-11.0311 EndY=-1.75 EndZ=0
    g32: LineSegment StartX=-11.0311 StartY=-1.75 StartZ=0 EndX=-8 EndY=-3.5 EndZ=0
    g33: LineSegment StartX=-8 StartY=-3.5 StartZ=0 EndX=-4.96891 EndY=-1.75 EndZ=0
    g34: Circle [constr] CenterX=-8 CenterY=0 CenterZ=0 NormalX=0 NormalY=0 NormalZ=1 AngleXU=0 Radius=3.5
    g35: LineSegment StartX=-4.03109 StartY=-3.5 StartZ=0 EndX=-7.06218 EndY=-5.25 EndZ=0
    g36: LineSegment StartX=-7.06218 StartY=-5.25 StartZ=0 EndX=-7.06218 EndY=-8.75 EndZ=0
    g37: LineSegment StartX=-7.06218 StartY=-8.75 StartZ=0 EndX=-4.03109 EndY=-10.5 EndZ=0
    g38: LineSegment StartX=-4.03109 StartY=-10.5 StartZ=0 EndX=-1 EndY=-8.75 EndZ=0
    g39: LineSegment StartX=-1 StartY=-8.75 StartZ=0 EndX=-1 EndY=-5.25 EndZ=0
    g40: LineSegment StartX=-1 StartY=-5.25 StartZ=0 EndX=-4.03109 EndY=-3.5 EndZ=0
    g41: Circle [constr] CenterX=-4.03109 CenterY=-7 CenterZ=0 NormalX=0 NormalY=0 NormalZ=1 AngleXU=0 Radius=3.5
    g42: LineSegment StartX=4.03109 StartY=-3.5 StartZ=0 EndX=1 EndY=-5.25 EndZ=0
    g43: LineSegment StartX=1 StartY=-5.25 StartZ=0 EndX=1 EndY=-8.75 EndZ=0
    g44: LineSegment StartX=1 StartY=-8.75 StartZ=0 EndX=4.03109 EndY=-10.5 EndZ=0
    g45: LineSegment StartX=4.03109 StartY=-10.5 StartZ=0 EndX=7.06218 EndY=-8.75 EndZ=0
    g46: LineSegment StartX=7.06218 StartY=-8.75 StartZ=0 EndX=7.06218 EndY=-5.25 EndZ=0
    g47: LineSegment StartX=7.06218 StartY=-5.25 StartZ=0 EndX=4.03109 EndY=-3.5 EndZ=0
    g48: Circle [constr] CenterX=4.03109 CenterY=-7 CenterZ=0 NormalX=0 NormalY=0 NormalZ=1 AngleXU=0 Radius=3.5
  constraints (117):
    c: Coincident(g0,g1)
    c: Coincident(g1,g2)
    c: Coincident(g2,g3)
    c: Coincident(g3,g4)
    c: Coincident(g4,g5)
    c: Coincident(g5,g0)
    c: Equal(g0, g1-g5) x5
    c: PointOnObject(g0,g6)
    c: PointOnObject(g1,g6)
    c: PointOnObject(g2,g6)
    c: PointOnObject(g3,g6)
    c: PointOnObject(g4,g6)
    c: PointOnObject(g5,g6)
    c: Coincident(g6,g-1)
    c: Diameter(g6) = 7
    c: PointOnObject(g0,g-2)
    c: Coincident(g7,g8)
    c: Coincident(g8,g9)
    c: Coincident(g9,g10)
    c: Coincident(g10,g11)
    c: Coincident(g11,g12)
    c: Coincident(g12,g7)
    c: Equal(g7, g8-g12) x5
    c: PointOnObject(g7,g13)
    c: PointOnObject(g8,g13)
    c: PointOnObject(g9,g13)
    c: PointOnObject(g10,g13)
    c: PointOnObject(g11,g13)
    c: PointOnObject(g12,g13)
    c: PointOnObject(g13,g-1)
    c: Diameter(g13) = 7
    c: Distance(g6,g13) = 8
    c: Horizontal(g0,g10)
    c: Coincident(g14,g15)
    c: Coincident(g15,g16)
    c: Coincident(g16,g17)
    c: Coincident(g17,g18)
    c: Coincident(g18,g19)
    c: Coincident(g19,g14)
    c: Equal(g14, g15-g19) x5
    c: PointOnObject(g14,g20)
    c: PointOnObject(g15,g20)
    c: PointOnObject(g16,g20)
    c: PointOnObject(g17,g20)
    c: PointOnObject(g18,g20)
    c: PointOnObject(g19,g20)
    c: Diameter(g20) = 7
    c: DistanceY(g-1,g20) = 7
    c: Vertical(g18)
    c: Distance(g17,g-2) = 1
    c: Coincident(g21,g22)
    c: Coincident(g22,g23)
    c: Coincident(g23,g24)
    c: Coincident(g24,g25)
    c: Coincident(g25,g26)
    c: Coincident(g26,g21)
    c: Equal(g21, g22-g26) x5
    c: PointOnObject(g21,g27)
    c: PointOnObject(g22,g27)
    c: PointOnObject(g23,g27)
    c: PointOnObject(g24,g27)
    c: PointOnObject(g25,g27)
    c: PointOnObject(g26,g27)
    c: Diameter(g27) = 7
    c: DistanceY(g-1,g27) = 7
    c: DistanceX(g21,g-1) = 1
    c: Vertical(g21)
    c: Coincident(g28,g29)
    c: Coincident(g29,g30)
    c: Coincident(g30,g31)
    c: Coincident(g31,g32)
    c: Coincident(g32,g33)
    c: Coincident(g33,g28)
    c: Equal(g28, g29-g33) x5
    c: PointOnObject(g28,g34)
    c: PointOnObject(g29,g34)
    c: PointOnObject(g30,g34)
    c: PointOnObject(g31,g34)
    c: PointOnObject(g32,g34)
    c: PointOnObject(g33,g34)
    c: PointOnObject(g34,g-1)
    c: Diameter(g34) = 7
    c: Vertical(g31)
    c: DistanceX(g34,g-1) = 8
    c: Coincident(g35,g36)
    c: Coincident(g36,g37)
    c: Coincident(g37,g38)
    c: Coincident(g38,g39)
    c: Coincident(g39,g40)
    c: Coincident(g40,g35)
    c: Equal(g35, g36-g40) x5
    c: PointOnObject(g35,g41)
    c: PointOnObject(g36,g41)
    c: PointOnObject(g37,g41)
    c: PointOnObject(g38,g41)
    c: PointOnObject(g39,g41)
    c: PointOnObject(g40,g41)
    c: Coincident(g42,g43)
    c: Coincident(g43,g44)
    c: Coincident(g44,g45)
    c: Coincident(g45,g46)
    c: Coincident(g46,g47)
    c: Coincident(g47,g42)
    c: Equal(g42, g43-g47) x5
    c: PointOnObject(g42,g48)
    c: PointOnObject(g43,g48)
    c: PointOnObject(g44,g48)
    c: PointOnObject(g45,g48)
    c: PointOnObject(g46,g48)
    c: PointOnObject(g47,g48)
    c: Equal(g41,g48)
    c: Diameter(g41) = 7
    c: Vertical(g39)
    c: Vertical(g43)
    c: Distance(g-2,g39) = 1
    c: Symmetric(g38,g43,g-2)
    c: Distance(g41,g-1) = 7
FEATURE [Part::Extrusion] Extrude684  label="hex286"
  Base = -> Sketch693
  Dir = (0,-1,2e-16)
  DirMode = 2
  FaceMakerClass = Part::FaceMakerBullseye
  FaceMakerMode = 3
  LengthFwd = 10
  LengthRev = 0
  Placement = pos=(56,0,0) rot=(0,0,1;0rad)
  Solid = true
  Symmetric = false
FEATURE [Sketcher::SketchObject] Sketch694
  ArcFitTolerance = 1e-06
  FullyConstrained = true
  MakeInternals = false
  Placement = pos=(0,0,0) rot=(1,0,0;1.5708rad)
  sketch-geometry (49):
    g0: LineSegment StartX=1e-16 StartY=3.5 StartZ=0 EndX=-3.03109 EndY=1.75 EndZ=0
    g1: LineSegment StartX=-3.03109 StartY=1.75 StartZ=0 EndX=-3.03109 EndY=-1.75 EndZ=0
    g2: LineSegment StartX=-3.03109 StartY=-1.75 StartZ=0 EndX=-1e-16 EndY=-3.5 EndZ=0
    g3: LineSegment StartX=-1e-16 StartY=-3.5 StartZ=0 EndX=3.03109 EndY=-1.75 EndZ=0
    g4: LineSegment StartX=3.03109 StartY=-1.75 StartZ=0 EndX=3.03109 EndY=1.75 EndZ=0
    g5: LineSegment StartX=3.03109 StartY=1.75 StartZ=0 EndX=1e-16 EndY=3.5 EndZ=0
    g6: Circle [constr] CenterX=0 CenterY=0 CenterZ=0 NormalX=0 NormalY=0 NormalZ=1 AngleXU=0 Radius=3.5
    g7: LineSegment StartX=4.96892 StartY=-1.75002 StartZ=0 EndX=8.00002 EndY=-3.5 EndZ=0
    g8: LineSegment StartX=8.00002 StartY=-3.5 StartZ=0 EndX=11.0311 EndY=-1.74998 EndZ=0
    g9: LineSegment StartX=11.0311 StartY=-1.74998 StartZ=0 EndX=11.0311 EndY=1.75002 EndZ=0
    g10: LineSegment StartX=11.0311 StartY=1.75002 StartZ=0 EndX=7.99998 EndY=3.5 EndZ=0
    g11: LineSegment StartX=7.99998 StartY=3.5 StartZ=0 EndX=4.9689 EndY=1.74998 EndZ=0
    g12: LineSegment StartX=4.9689 StartY=1.74998 StartZ=0 EndX=4.96892 EndY=-1.75002 EndZ=0
    g13: Circle [constr] CenterX=8 CenterY=0 CenterZ=0 NormalX=0 NormalY=0 NormalZ=1 AngleXU=0 Radius=3.5
    g14: LineSegment StartX=4.03109 StartY=3.5 StartZ=0 EndX=7.06218 EndY=5.25 EndZ=0
    g15: LineSegment StartX=7.06218 StartY=5.25 StartZ=0 EndX=7.06218 EndY=8.75 EndZ=0
    g16: LineSegment StartX=7.06218 StartY=8.75 StartZ=0 EndX=4.03109 EndY=10.5 EndZ=0
    g17: LineSegment StartX=4.03109 StartY=10.5 StartZ=0 EndX=1 EndY=8.75 EndZ=0
    g18: LineSegment StartX=1 StartY=8.75 StartZ=0 EndX=1 EndY=5.25 EndZ=0
    g19: LineSegment StartX=1 StartY=5.25 StartZ=0 EndX=4.03109 EndY=3.5 EndZ=0
    g20: Circle [constr] CenterX=4.03109 CenterY=7 CenterZ=0 NormalX=0 NormalY=0 NormalZ=1 AngleXU=0 Radius=3.5
    g21: LineSegment StartX=-1 StartY=5.25 StartZ=0 EndX=-1 EndY=8.75 EndZ=0
    g22: LineSegment StartX=-1 StartY=8.75 StartZ=0 EndX=-4.03109 EndY=10.5 EndZ=0
    g23: LineSegment StartX=-4.03109 StartY=10.5 StartZ=0 EndX=-7.06218 EndY=8.75 EndZ=0
    g24: LineSegment StartX=-7.06218 StartY=8.75 StartZ=0 EndX=-7.06218 EndY=5.25 EndZ=0
    g25: LineSegment StartX=-7.06218 StartY=5.25 StartZ=0 EndX=-4.03109 EndY=3.5 EndZ=0
    g26: LineSegment StartX=-4.03109 StartY=3.5 StartZ=0 EndX=-1 EndY=5.25 EndZ=0
    g27: Circle [constr] CenterX=-4.03109 CenterY=7 CenterZ=0 NormalX=0 NormalY=0 NormalZ=1 AngleXU=0 Radius=3.5
    g28: LineSegment StartX=-4.96891 StartY=-1.75 StartZ=0 EndX=-4.96891 EndY=1.75 EndZ=0
    g29: LineSegment StartX=-4.96891 StartY=1.75 StartZ=0 EndX=-8 EndY=3.5 EndZ=0
    g30: LineSegment StartX=-8 StartY=3.5 StartZ=0 EndX=-11.0311 EndY=1.75 EndZ=0
    g31: LineSegment StartX=-11.0311 StartY=1.75 StartZ=0 EndX=-11.0311 EndY=-1.75 EndZ=0
    g32: LineSegment StartX=-11.0311 StartY=-1.75 StartZ=0 EndX=-8 EndY=-3.5 EndZ=0
    g33: LineSegment StartX=-8 StartY=-3.5 StartZ=0 EndX=-4.96891 EndY=-1.75 EndZ=0
    g34: Circle [constr] CenterX=-8 CenterY=0 CenterZ=0 NormalX=0 NormalY=0 NormalZ=1 AngleXU=0 Radius=3.5
    g35: LineSegment StartX=-4.03109 StartY=-3.5 StartZ=0 EndX=-7.06218 EndY=-5.25 EndZ=0
    g36: LineSegment StartX=-7.06218 StartY=-5.25 StartZ=0 EndX=-7.06218 EndY=-8.75 EndZ=0
    g37: LineSegment StartX=-7.06218 StartY=-8.75 StartZ=0 EndX=-4.03109 EndY=-10.5 EndZ=0
    g38: LineSegment StartX=-4.03109 StartY=-10.5 StartZ=0 EndX=-1 EndY=-8.75 EndZ=0
    g39: LineSegment StartX=-1 StartY=-8.75 StartZ=0 EndX=-1 EndY=-5.25 EndZ=0
    g40: LineSegment StartX=-1 StartY=-5.25 StartZ=0 EndX=-4.03109 EndY=-3.5 EndZ=0
    g41: Circle [constr] CenterX=-4.03109 CenterY=-7 CenterZ=0 NormalX=0 NormalY=0 NormalZ=1 AngleXU=0 Radius=3.5
    g42: LineSegment StartX=4.03109 StartY=-3.5 StartZ=0 EndX=1 EndY=-5.25 EndZ=0
    g43: LineSegment StartX=1 StartY=-5.25 StartZ=0 EndX=1 EndY=-8.75 EndZ=0
    g44: LineSegment StartX=1 StartY=-8.75 StartZ=0 EndX=4.03109 EndY=-10.5 EndZ=0
    g45: LineSegment StartX=4.03109 StartY=-10.5 StartZ=0 EndX=7.06218 EndY=-8.75 EndZ=0
    g46: LineSegment StartX=7.06218 StartY=-8.75 StartZ=0 EndX=7.06218 EndY=-5.25 EndZ=0
    g47: LineSegment StartX=7.06218 StartY=-5.25 StartZ=0 EndX=4.03109 EndY=-3.5 EndZ=0
    g48: Circle [constr] CenterX=4.03109 CenterY=-7 CenterZ=0 NormalX=0 NormalY=0 NormalZ=1 AngleXU=0 Radius=3.5
  constraints (117):
    c: Coincident(g0,g1)
    c: Coincident(g1,g2)
    c: Coincident(g2,g3)
    c: Coincident(g3,g4)
    c: Coincident(g4,g5)
    c: Coincident(g5,g0)
    c: Equal(g0, g1-g5) x5
    c: PointOnObject(g0,g6)
    c: PointOnObject(g1,g6)
    c: PointOnObject(g2,g6)
    c: PointOnObject(g3,g6)
    c: PointOnObject(g4,g6)
    c: PointOnObject(g5,g6)
    c: Coincident(g6,g-1)
    c: Diameter(g6) = 7
    c: PointOnObject(g0,g-2)
    c: Coincident(g7,g8)
    c: Coincident(g8,g9)
    c: Coincident(g9,g10)
    c: Coincident(g10,g11)
    c: Coincident(g11,g12)
    c: Coincident(g12,g7)
    c: Equal(g7, g8-g12) x5
    c: PointOnObject(g7,g13)
    c: PointOnObject(g8,g13)
    c: PointOnObject(g9,g13)
    c: PointOnObject(g10,g13)
    c: PointOnObject(g11,g13)
    c: PointOnObject(g12,g13)
    c: PointOnObject(g13,g-1)
    c: Diameter(g13) = 7
    c: Distance(g6,g13) = 8
    c: Horizontal(g0,g10)
    c: Coincident(g14,g15)
    c: Coincident(g15,g16)
    c: Coincident(g16,g17)
    c: Coincident(g17,g18)
    c: Coincident(g18,g19)
    c: Coincident(g19,g14)
    c: Equal(g14, g15-g19) x5
    c: PointOnObject(g14,g20)
    c: PointOnObject(g15,g20)
    c: PointOnObject(g16,g20)
    c: PointOnObject(g17,g20)
    c: PointOnObject(g18,g20)
    c: PointOnObject(g19,g20)
    c: Diameter(g20) = 7
    c: DistanceY(g-1,g20) = 7
    c: Vertical(g18)
    c: Distance(g17,g-2) = 1
    c: Coincident(g21,g22)
    c: Coincident(g22,g23)
    c: Coincident(g23,g24)
    c: Coincident(g24,g25)
    c: Coincident(g25,g26)
    c: Coincident(g26,g21)
    c: Equal(g21, g22-g26) x5
    c: PointOnObject(g21,g27)
    c: PointOnObject(g22,g27)
    c: PointOnObject(g23,g27)
    c: PointOnObject(g24,g27)
    c: PointOnObject(g25,g27)
    c: PointOnObject(g26,g27)
    c: Diameter(g27) = 7
    c: DistanceY(g-1,g27) = 7
    c: DistanceX(g21,g-1) = 1
    c: Vertical(g21)
    c: Coincident(g28,g29)
    c: Coincident(g29,g30)
    c: Coincident(g30,g31)
    c: Coincident(g31,g32)
    c: Coincident(g32,g33)
    c: Coincident(g33,g28)
    c: Equal(g28, g29-g33) x5
    c: PointOnObject(g28,g34)
    c: PointOnObject(g29,g34)
    c: PointOnObject(g30,g34)
    c: PointOnObject(g31,g34)
    c: PointOnObject(g32,g34)
    c: PointOnObject(g33,g34)
    c: PointOnObject(g34,g-1)
    c: Diameter(g34) = 7
    c: Vertical(g31)
    c: DistanceX(g34,g-1) = 8
    c: Coincident(g35,g36)
    c: Coincident(g36,g37)
    c: Coincident(g37,g38)
    c: Coincident(g38,g39)
    c: Coincident(g39,g40)
    c: Coincident(g40,g35)
    c: Equal(g35, g36-g40) x5
    c: PointOnObject(g35,g41)
    c: PointOnObject(g36,g41)
    c: PointOnObject(g37,g41)
    c: PointOnObject(g38,g41)
    c: PointOnObject(g39,g41)
    c: PointOnObject(g40,g41)
    c: Coincident(g42,g43)
    c: Coincident(g43,g44)
    c: Coincident(g44,g45)
    c: Coincident(g45,g46)
    c: Coincident(g46,g47)
    c: Coincident(g47,g42)
    c: Equal(g42, g43-g47) x5
    c: PointOnObject(g42,g48)
    c: PointOnObject(g43,g48)
    c: PointOnObject(g44,g48)
    c: PointOnObject(g45,g48)
    c: PointOnObject(g46,g48)
    c: PointOnObject(g47,g48)
    c: Equal(g41,g48)
    c: Diameter(g41) = 7
    c: Vertical(g39)
    c: Vertical(g43)
    c: Distance(g-2,g39) = 1
    c: Symmetric(g38,g43,g-2)
    c: Distance(g41,g-1) = 7
FEATURE [Part::Extrusion] Extrude685  label="hex287"
  Base = -> Sketch694
  Dir = (0,-1,2e-16)
  DirMode = 2
  FaceMakerClass = Part::FaceMakerBullseye
  FaceMakerMode = 3
  LengthFwd = 10
  LengthRev = 0
  Placement = pos=(52,0,-21) rot=(0,0,1;0rad)
  Solid = true
  Symmetric = false
FEATURE [Sketcher::SketchObject] Sketch695
  ArcFitTolerance = 1e-06
  FullyConstrained = true
  MakeInternals = false
  Placement = pos=(0,0,0) rot=(1,0,0;1.5708rad)
  sketch-geometry (49):
    g0: LineSegment StartX=1e-16 StartY=3.5 StartZ=0 EndX=-3.03109 EndY=1.75 EndZ=0
    g1: LineSegment StartX=-3.03109 StartY=1.75 StartZ=0 EndX=-3.03109 EndY=-1.75 EndZ=0
    g2: LineSegment StartX=-3.03109 StartY=-1.75 StartZ=0 EndX=-1e-16 EndY=-3.5 EndZ=0
    g3: LineSegment StartX=-1e-16 StartY=-3.5 StartZ=0 EndX=3.03109 EndY=-1.75 EndZ=0
    g4: LineSegment StartX=3.03109 StartY=-1.75 StartZ=0 EndX=3.03109 EndY=1.75 EndZ=0
    g5: LineSegment StartX=3.03109 StartY=1.75 StartZ=0 EndX=1e-16 EndY=3.5 EndZ=0
    g6: Circle [constr] CenterX=0 CenterY=0 CenterZ=0 NormalX=0 NormalY=0 NormalZ=1 AngleXU=0 Radius=3.5
    g7: LineSegment StartX=4.96892 StartY=-1.75002 StartZ=0 EndX=8.00002 EndY=-3.5 EndZ=0
    g8: LineSegment StartX=8.00002 StartY=-3.5 StartZ=0 EndX=11.0311 EndY=-1.74998 EndZ=0
    g9: LineSegment StartX=11.0311 StartY=-1.74998 StartZ=0 EndX=11.0311 EndY=1.75002 EndZ=0
    g10: LineSegment StartX=11.0311 StartY=1.75002 StartZ=0 EndX=7.99998 EndY=3.5 EndZ=0
    g11: LineSegment StartX=7.99998 StartY=3.5 StartZ=0 EndX=4.9689 EndY=1.74998 EndZ=0
    g12: LineSegment StartX=4.9689 StartY=1.74998 StartZ=0 EndX=4.96892 EndY=-1.75002 EndZ=0
    g13: Circle [constr] CenterX=8 CenterY=0 CenterZ=0 NormalX=0 NormalY=0 NormalZ=1 AngleXU=0 Radius=3.5
    g14: LineSegment StartX=4.03109 StartY=3.5 StartZ=0 EndX=7.06218 EndY=5.25 EndZ=0
    g15: LineSegment StartX=7.06218 StartY=5.25 StartZ=0 EndX=7.06218 EndY=8.75 EndZ=0
    g16: LineSegment StartX=7.06218 StartY=8.75 StartZ=0 EndX=4.03109 EndY=10.5 EndZ=0
    g17: LineSegment StartX=4.03109 StartY=10.5 StartZ=0 EndX=1 EndY=8.75 EndZ=0
    g18: LineSegment StartX=1 StartY=8.75 StartZ=0 EndX=1 EndY=5.25 EndZ=0
    g19: LineSegment StartX=1 StartY=5.25 StartZ=0 EndX=4.03109 EndY=3.5 EndZ=0
    g20: Circle [constr] CenterX=4.03109 CenterY=7 CenterZ=0 NormalX=0 NormalY=0 NormalZ=1 AngleXU=0 Radius=3.5
    g21: LineSegment StartX=-1 StartY=5.25 StartZ=0 EndX=-1 EndY=8.75 EndZ=0
    g22: LineSegment StartX=-1 StartY=8.75 StartZ=0 EndX=-4.03109 EndY=10.5 EndZ=0
    g23: LineSegment StartX=-4.03109 StartY=10.5 StartZ=0 EndX=-7.06218 EndY=8.75 EndZ=0
    g24: LineSegment StartX=-7.06218 StartY=8.75 StartZ=0 EndX=-7.06218 EndY=5.25 EndZ=0
    g25: LineSegment StartX=-7.06218 StartY=5.25 StartZ=0 EndX=-4.03109 EndY=3.5 EndZ=0
    g26: LineSegment StartX=-4.03109 StartY=3.5 StartZ=0 EndX=-1 EndY=5.25 EndZ=0
    g27: Circle [constr] CenterX=-4.03109 CenterY=7 CenterZ=0 NormalX=0 NormalY=0 NormalZ=1 AngleXU=0 Radius=3.5
    g28: LineSegment StartX=-4.96891 StartY=-1.75 StartZ=0 EndX=-4.96891 EndY=1.75 EndZ=0
    g29: LineSegment StartX=-4.96891 StartY=1.75 StartZ=0 EndX=-8 EndY=3.5 EndZ=0
    g30: LineSegment StartX=-8 StartY=3.5 StartZ=0 EndX=-11.0311 EndY=1.75 EndZ=0
    g31: LineSegment StartX=-11.0311 StartY=1.75 StartZ=0 EndX=-11.0311 EndY=-1.75 EndZ=0
    g32: LineSegment StartX=-11.0311 StartY=-1.75 StartZ=0 EndX=-8 EndY=-3.5 EndZ=0
    g33: LineSegment StartX=-8 StartY=-3.5 StartZ=0 EndX=-4.96891 EndY=-1.75 EndZ=0
    g34: Circle [constr] CenterX=-8 CenterY=0 CenterZ=0 NormalX=0 NormalY=0 NormalZ=1 AngleXU=0 Radius=3.5
    g35: LineSegment StartX=-4.03109 StartY=-3.5 StartZ=0 EndX=-7.06218 EndY=-5.25 EndZ=0
    g36: LineSegment StartX=-7.06218 StartY=-5.25 StartZ=0 EndX=-7.06218 EndY=-8.75 EndZ=0
    g37: LineSegment StartX=-7.06218 StartY=-8.75 StartZ=0 EndX=-4.03109 EndY=-10.5 EndZ=0
    g38: LineSegment StartX=-4.03109 StartY=-10.5 StartZ=0 EndX=-1 EndY=-8.75 EndZ=0
    g39: LineSegment StartX=-1 StartY=-8.75 StartZ=0 EndX=-1 EndY=-5.25 EndZ=0
    g40: LineSegment StartX=-1 StartY=-5.25 StartZ=0 EndX=-4.03109 EndY=-3.5 EndZ=0
    g41: Circle [constr] CenterX=-4.03109 CenterY=-7 CenterZ=0 NormalX=0 NormalY=0 NormalZ=1 AngleXU=0 Radius=3.5
    g42: LineSegment StartX=4.03109 StartY=-3.5 StartZ=0 EndX=1 EndY=-5.25 EndZ=0
    g43: LineSegment StartX=1 StartY=-5.25 StartZ=0 EndX=1 EndY=-8.75 EndZ=0
    g44: LineSegment StartX=1 StartY=-8.75 StartZ=0 EndX=4.03109 EndY=-10.5 EndZ=0
    g45: LineSegment StartX=4.03109 StartY=-10.5 StartZ=0 EndX=7.06218 EndY=-8.75 EndZ=0
    g46: LineSegment StartX=7.06218 StartY=-8.75 StartZ=0 EndX=7.06218 EndY=-5.25 EndZ=0
    g47: LineSegment StartX=7.06218 StartY=-5.25 StartZ=0 EndX=4.03109 EndY=-3.5 EndZ=0
    g48: Circle [constr] CenterX=4.03109 CenterY=-7 CenterZ=0 NormalX=0 NormalY=0 NormalZ=1 AngleXU=0 Radius=3.5
  constraints (117):
    c: Coincident(g0,g1)
    c: Coincident(g1,g2)
    c: Coincident(g2,g3)
    c: Coincident(g3,g4)
    c: Coincident(g4,g5)
    c: Coincident(g5,g0)
    c: Equal(g0, g1-g5) x5
    c: PointOnObject(g0,g6)
    c: PointOnObject(g1,g6)
    c: PointOnObject(g2,g6)
    c: PointOnObject(g3,g6)
    c: PointOnObject(g4,g6)
    c: PointOnObject(g5,g6)
    c: Coincident(g6,g-1)
    c: Diameter(g6) = 7
    c: PointOnObject(g0,g-2)
    c: Coincident(g7,g8)
    c: Coincident(g8,g9)
    c: Coincident(g9,g10)
    c: Coincident(g10,g11)
    c: Coincident(g11,g12)
    c: Coincident(g12,g7)
    c: Equal(g7, g8-g12) x5
    c: PointOnObject(g7,g13)
    c: PointOnObject(g8,g13)
    c: PointOnObject(g9,g13)
    c: PointOnObject(g10,g13)
    c: PointOnObject(g11,g13)
    c: PointOnObject(g12,g13)
    c: PointOnObject(g13,g-1)
    c: Diameter(g13) = 7
    c: Distance(g6,g13) = 8
    c: Horizontal(g0,g10)
    c: Coincident(g14,g15)
    c: Coincident(g15,g16)
    c: Coincident(g16,g17)
    c: Coincident(g17,g18)
    c: Coincident(g18,g19)
    c: Coincident(g19,g14)
    c: Equal(g14, g15-g19) x5
    c: PointOnObject(g14,g20)
    c: PointOnObject(g15,g20)
    c: PointOnObject(g16,g20)
    c: PointOnObject(g17,g20)
    c: PointOnObject(g18,g20)
    c: PointOnObject(g19,g20)
    c: Diameter(g20) = 7
    c: DistanceY(g-1,g20) = 7
    c: Vertical(g18)
    c: Distance(g17,g-2) = 1
    c: Coincident(g21,g22)
    c: Coincident(g22,g23)
    c: Coincident(g23,g24)
    c: Coincident(g24,g25)
    c: Coincident(g25,g26)
    c: Coincident(g26,g21)
    c: Equal(g21, g22-g26) x5
    c: PointOnObject(g21,g27)
    c: PointOnObject(g22,g27)
    c: PointOnObject(g23,g27)
    c: PointOnObject(g24,g27)
    c: PointOnObject(g25,g27)
    c: PointOnObject(g26,g27)
    c: Diameter(g27) = 7
    c: DistanceY(g-1,g27) = 7
    c: DistanceX(g21,g-1) = 1
    c: Vertical(g21)
    c: Coincident(g28,g29)
    c: Coincident(g29,g30)
    c: Coincident(g30,g31)
    c: Coincident(g31,g32)
    c: Coincident(g32,g33)
    c: Coincident(g33,g28)
    c: Equal(g28, g29-g33) x5
    c: PointOnObject(g28,g34)
    c: PointOnObject(g29,g34)
    c: PointOnObject(g30,g34)
    c: PointOnObject(g31,g34)
    c: PointOnObject(g32,g34)
    c: PointOnObject(g33,g34)
    c: PointOnObject(g34,g-1)
    c: Diameter(g34) = 7
    c: Vertical(g31)
    c: DistanceX(g34,g-1) = 8
    c: Coincident(g35,g36)
    c: Coincident(g36,g37)
    c: Coincident(g37,g38)
    c: Coincident(g38,g39)
    c: Coincident(g39,g40)
    c: Coincident(g40,g35)
    c: Equal(g35, g36-g40) x5
    c: PointOnObject(g35,g41)
    c: PointOnObject(g36,g41)
    c: PointOnObject(g37,g41)
    c: PointOnObject(g38,g41)
    c: PointOnObject(g39,g41)
    c: PointOnObject(g40,g41)
    c: Coincident(g42,g43)
    c: Coincident(g43,g44)
    c: Coincident(g44,g45)
    c: Coincident(g45,g46)
    c: Coincident(g46,g47)
    c: Coincident(g47,g42)
    c: Equal(g42, g43-g47) x5
    c: PointOnObject(g42,g48)
    c: PointOnObject(g43,g48)
    c: PointOnObject(g44,g48)
    c: PointOnObject(g45,g48)
    c: PointOnObject(g46,g48)
    c: PointOnObject(g47,g48)
    c: Equal(g41,g48)
    c: Diameter(g41) = 7
    c: Vertical(g39)
    c: Vertical(g43)
    c: Distance(g-2,g39) = 1
    c: Symmetric(g38,g43,g-2)
    c: Distance(g41,g-1) = 7
FEATURE [Part::Extrusion] Extrude686  label="hex288"
  Base = -> Sketch695
  Dir = (0,-1,2e-16)
  DirMode = 2
  FaceMakerClass = Part::FaceMakerBullseye
  FaceMakerMode = 3
  LengthFwd = 10
  LengthRev = 0
  Placement = pos=(-56,0,0) rot=(0,0,1;0rad)
  Solid = true
  Symmetric = false
FEATURE [Sketcher::SketchObject] Sketch696
  ArcFitTolerance = 1e-06
  FullyConstrained = true
  MakeInternals = false
  Placement = pos=(0,0,0) rot=(1,0,0;1.5708rad)
  sketch-geometry (49):
    g0: LineSegment StartX=1e-16 StartY=3.5 StartZ=0 EndX=-3.03109 EndY=1.75 EndZ=0
    g1: LineSegment StartX=-3.03109 StartY=1.75 StartZ=0 EndX=-3.03109 EndY=-1.75 EndZ=0
    g2: LineSegment StartX=-3.03109 StartY=-1.75 StartZ=0 EndX=-1e-16 EndY=-3.5 EndZ=0
    g3: LineSegment StartX=-1e-16 StartY=-3.5 StartZ=0 EndX=3.03109 EndY=-1.75 EndZ=0
    g4: LineSegment StartX=3.03109 StartY=-1.75 StartZ=0 EndX=3.03109 EndY=1.75 EndZ=0
    g5: LineSegment StartX=3.03109 StartY=1.75 StartZ=0 EndX=1e-16 EndY=3.5 EndZ=0
    g6: Circle [constr] CenterX=0 CenterY=0 CenterZ=0 NormalX=0 NormalY=0 NormalZ=1 AngleXU=0 Radius=3.5
    g7: LineSegment StartX=4.96892 StartY=-1.75002 StartZ=0 EndX=8.00002 EndY=-3.5 EndZ=0
    g8: LineSegment StartX=8.00002 StartY=-3.5 StartZ=0 EndX=11.0311 EndY=-1.74998 EndZ=0
    g9: LineSegment StartX=11.0311 StartY=-1.74998 StartZ=0 EndX=11.0311 EndY=1.75002 EndZ=0
    g10: LineSegment StartX=11.0311 StartY=1.75002 StartZ=0 EndX=7.99998 EndY=3.5 EndZ=0
    g11: LineSegment StartX=7.99998 StartY=3.5 StartZ=0 EndX=4.9689 EndY=1.74998 EndZ=0
    g12: LineSegment StartX=4.9689 StartY=1.74998 StartZ=0 EndX=4.96892 EndY=-1.75002 EndZ=0
    g13: Circle [constr] CenterX=8 CenterY=0 CenterZ=0 NormalX=0 NormalY=0 NormalZ=1 AngleXU=0 Radius=3.5
    g14: LineSegment StartX=4.03109 StartY=3.5 StartZ=0 EndX=7.06218 EndY=5.25 EndZ=0
    g15: LineSegment StartX=7.06218 StartY=5.25 StartZ=0 EndX=7.06218 EndY=8.75 EndZ=0
    g16: LineSegment StartX=7.06218 StartY=8.75 StartZ=0 EndX=4.03109 EndY=10.5 EndZ=0
    g17: LineSegment StartX=4.03109 StartY=10.5 StartZ=0 EndX=1 EndY=8.75 EndZ=0
    g18: LineSegment StartX=1 StartY=8.75 StartZ=0 EndX=1 EndY=5.25 EndZ=0
    g19: LineSegment StartX=1 StartY=5.25 StartZ=0 EndX=4.03109 EndY=3.5 EndZ=0
    g20: Circle [constr] CenterX=4.03109 CenterY=7 CenterZ=0 NormalX=0 NormalY=0 NormalZ=1 AngleXU=0 Radius=3.5
    g21: LineSegment StartX=-1 StartY=5.25 StartZ=0 EndX=-1 EndY=8.75 EndZ=0
    g22: LineSegment StartX=-1 StartY=8.75 StartZ=0 EndX=-4.03109 EndY=10.5 EndZ=0
    g23: LineSegment StartX=-4.03109 StartY=10.5 StartZ=0 EndX=-7.06218 EndY=8.75 EndZ=0
    g24: LineSegment StartX=-7.06218 StartY=8.75 StartZ=0 EndX=-7.06218 EndY=5.25 EndZ=0
    g25: LineSegment StartX=-7.06218 StartY=5.25 StartZ=0 EndX=-4.03109 EndY=3.5 EndZ=0
    g26: LineSegment StartX=-4.03109 StartY=3.5 StartZ=0 EndX=-1 EndY=5.25 EndZ=0
    g27: Circle [constr] CenterX=-4.03109 CenterY=7 CenterZ=0 NormalX=0 NormalY=0 NormalZ=1 AngleXU=0 Radius=3.5
    g28: LineSegment StartX=-4.96891 StartY=-1.75 StartZ=0 EndX=-4.96891 EndY=1.75 EndZ=0
    g29: LineSegment StartX=-4.96891 StartY=1.75 StartZ=0 EndX=-8 EndY=3.5 EndZ=0
    g30: LineSegment StartX=-8 StartY=3.5 StartZ=0 EndX=-11.0311 EndY=1.75 EndZ=0
    g31: LineSegment StartX=-11.0311 StartY=1.75 StartZ=0 EndX=-11.0311 EndY=-1.75 EndZ=0
    g32: LineSegment StartX=-11.0311 StartY=-1.75 StartZ=0 EndX=-8 EndY=-3.5 EndZ=0
    g33: LineSegment StartX=-8 StartY=-3.5 StartZ=0 EndX=-4.96891 EndY=-1.75 EndZ=0
    g34: Circle [constr] CenterX=-8 CenterY=0 CenterZ=0 NormalX=0 NormalY=0 NormalZ=1 AngleXU=0 Radius=3.5
    g35: LineSegment StartX=-4.03109 StartY=-3.5 StartZ=0 EndX=-7.06218 EndY=-5.25 EndZ=0
    g36: LineSegment StartX=-7.06218 StartY=-5.25 StartZ=0 EndX=-7.06218 EndY=-8.75 EndZ=0
    g37: LineSegment StartX=-7.06218 StartY=-8.75 StartZ=0 EndX=-4.03109 EndY=-10.5 EndZ=0
    g38: LineSegment StartX=-4.03109 StartY=-10.5 StartZ=0 EndX=-1 EndY=-8.75 EndZ=0
    g39: LineSegment StartX=-1 StartY=-8.75 StartZ=0 EndX=-1 EndY=-5.25 EndZ=0
    g40: LineSegment StartX=-1 StartY=-5.25 StartZ=0 EndX=-4.03109 EndY=-3.5 EndZ=0
    g41: Circle [constr] CenterX=-4.03109 CenterY=-7 CenterZ=0 NormalX=0 NormalY=0 NormalZ=1 AngleXU=0 Radius=3.5
    g42: LineSegment StartX=4.03109 StartY=-3.5 StartZ=0 EndX=1 EndY=-5.25 EndZ=0
    g43: LineSegment StartX=1 StartY=-5.25 StartZ=0 EndX=1 EndY=-8.75 EndZ=0
    g44: LineSegment StartX=1 StartY=-8.75 StartZ=0 EndX=4.03109 EndY=-10.5 EndZ=0
    g45: LineSegment StartX=4.03109 StartY=-10.5 StartZ=0 EndX=7.06218 EndY=-8.75 EndZ=0
    g46: LineSegment StartX=7.06218 StartY=-8.75 StartZ=0 EndX=7.06218 EndY=-5.25 EndZ=0
    g47: LineSegment StartX=7.06218 StartY=-5.25 StartZ=0 EndX=4.03109 EndY=-3.5 EndZ=0
    g48: Circle [constr] CenterX=4.03109 CenterY=-7 CenterZ=0 NormalX=0 NormalY=0 NormalZ=1 AngleXU=0 Radius=3.5
  constraints (117):
    c: Coincident(g0,g1)
    c: Coincident(g1,g2)
    c: Coincident(g2,g3)
    c: Coincident(g3,g4)
    c: Coincident(g4,g5)
    c: Coincident(g5,g0)
    c: Equal(g0, g1-g5) x5
    c: PointOnObject(g0,g6)
    c: PointOnObject(g1,g6)
    c: PointOnObject(g2,g6)
    c: PointOnObject(g3,g6)
    c: PointOnObject(g4,g6)
    c: PointOnObject(g5,g6)
    c: Coincident(g6,g-1)
    c: Diameter(g6) = 7
    c: PointOnObject(g0,g-2)
    c: Coincident(g7,g8)
    c: Coincident(g8,g9)
    c: Coincident(g9,g10)
    c: Coincident(g10,g11)
    c: Coincident(g11,g12)
    c: Coincident(g12,g7)
    c: Equal(g7, g8-g12) x5
    c: PointOnObject(g7,g13)
    c: PointOnObject(g8,g13)
    c: PointOnObject(g9,g13)
    c: PointOnObject(g10,g13)
    c: PointOnObject(g11,g13)
    c: PointOnObject(g12,g13)
    c: PointOnObject(g13,g-1)
    c: Diameter(g13) = 7
    c: Distance(g6,g13) = 8
    c: Horizontal(g0,g10)
    c: Coincident(g14,g15)
    c: Coincident(g15,g16)
    c: Coincident(g16,g17)
    c: Coincident(g17,g18)
    c: Coincident(g18,g19)
    c: Coincident(g19,g14)
    c: Equal(g14, g15-g19) x5
    c: PointOnObject(g14,g20)
    c: PointOnObject(g15,g20)
    c: PointOnObject(g16,g20)
    c: PointOnObject(g17,g20)
    c: PointOnObject(g18,g20)
    c: PointOnObject(g19,g20)
    c: Diameter(g20) = 7
    c: DistanceY(g-1,g20) = 7
    c: Vertical(g18)
    c: Distance(g17,g-2) = 1
    c: Coincident(g21,g22)
    c: Coincident(g22,g23)
    c: Coincident(g23,g24)
    c: Coincident(g24,g25)
    c: Coincident(g25,g26)
    c: Coincident(g26,g21)
    c: Equal(g21, g22-g26) x5
    c: PointOnObject(g21,g27)
    c: PointOnObject(g22,g27)
    c: PointOnObject(g23,g27)
    c: PointOnObject(g24,g27)
    c: PointOnObject(g25,g27)
    c: PointOnObject(g26,g27)
    c: Diameter(g27) = 7
    c: DistanceY(g-1,g27) = 7
    c: DistanceX(g21,g-1) = 1
    c: Vertical(g21)
    c: Coincident(g28,g29)
    c: Coincident(g29,g30)
    c: Coincident(g30,g31)
    c: Coincident(g31,g32)
    c: Coincident(g32,g33)
    c: Coincident(g33,g28)
    c: Equal(g28, g29-g33) x5
    c: PointOnObject(g28,g34)
    c: PointOnObject(g29,g34)
    c: PointOnObject(g30,g34)
    c: PointOnObject(g31,g34)
    c: PointOnObject(g32,g34)
    c: PointOnObject(g33,g34)
    c: PointOnObject(g34,g-1)
    c: Diameter(g34) = 7
    c: Vertical(g31)
    c: DistanceX(g34,g-1) = 8
    c: Coincident(g35,g36)
    c: Coincident(g36,g37)
    c: Coincident(g37,g38)
    c: Coincident(g38,g39)
    c: Coincident(g39,g40)
    c: Coincident(g40,g35)
    c: Equal(g35, g36-g40) x5
    c: PointOnObject(g35,g41)
    c: PointOnObject(g36,g41)
    c: PointOnObject(g37,g41)
    c: PointOnObject(g38,g41)
    c: PointOnObject(g39,g41)
    c: PointOnObject(g40,g41)
    c: Coincident(g42,g43)
    c: Coincident(g43,g44)
    c: Coincident(g44,g45)
    c: Coincident(g45,g46)
    c: Coincident(g46,g47)
    c: Coincident(g47,g42)
    c: Equal(g42, g43-g47) x5
    c: PointOnObject(g42,g48)
    c: PointOnObject(g43,g48)
    c: PointOnObject(g44,g48)
    c: PointOnObject(g45,g48)
    c: PointOnObject(g46,g48)
    c: PointOnObject(g47,g48)
    c: Equal(g41,g48)
    c: Diameter(g41) = 7
    c: Vertical(g39)
    c: Vertical(g43)
    c: Distance(g-2,g39) = 1
    c: Symmetric(g38,g43,g-2)
    c: Distance(g41,g-1) = 7
FEATURE [Part::Extrusion] Extrude687  label="hex289"
  Base = -> Sketch696
  Dir = (0,-1,2e-16)
  DirMode = 2
  FaceMakerClass = Part::FaceMakerBullseye
  FaceMakerMode = 3
  LengthFwd = 10
  LengthRev = 0
  Placement = pos=(-52,0,21) rot=(0,0,1;0rad)
  Solid = true
  Symmetric = false
FEATURE [Sketcher::SketchObject] Sketch697
  ArcFitTolerance = 1e-06
  FullyConstrained = true
  MakeInternals = false
  Placement = pos=(0,0,0) rot=(1,0,0;1.5708rad)
  sketch-geometry (49):
    g0: LineSegment StartX=1e-16 StartY=3.5 StartZ=0 EndX=-3.03109 EndY=1.75 EndZ=0
    g1: LineSegment StartX=-3.03109 StartY=1.75 StartZ=0 EndX=-3.03109 EndY=-1.75 EndZ=0
    g2: LineSegment StartX=-3.03109 StartY=-1.75 StartZ=0 EndX=-1e-16 EndY=-3.5 EndZ=0
    g3: LineSegment StartX=-1e-16 StartY=-3.5 StartZ=0 EndX=3.03109 EndY=-1.75 EndZ=0
    g4: LineSegment StartX=3.03109 StartY=-1.75 StartZ=0 EndX=3.03109 EndY=1.75 EndZ=0
    g5: LineSegment StartX=3.03109 StartY=1.75 StartZ=0 EndX=1e-16 EndY=3.5 EndZ=0
    g6: Circle [constr] CenterX=0 CenterY=0 CenterZ=0 NormalX=0 NormalY=0 NormalZ=1 AngleXU=0 Radius=3.5
    g7: LineSegment StartX=4.96892 StartY=-1.75002 StartZ=0 EndX=8.00002 EndY=-3.5 EndZ=0
    g8: LineSegment StartX=8.00002 StartY=-3.5 StartZ=0 EndX=11.0311 EndY=-1.74998 EndZ=0
    g9: LineSegment StartX=11.0311 StartY=-1.74998 StartZ=0 EndX=11.0311 EndY=1.75002 EndZ=0
    g10: LineSegment StartX=11.0311 StartY=1.75002 StartZ=0 EndX=7.99998 EndY=3.5 EndZ=0
    g11: LineSegment StartX=7.99998 StartY=3.5 StartZ=0 EndX=4.9689 EndY=1.74998 EndZ=0
    g12: LineSegment StartX=4.9689 StartY=1.74998 StartZ=0 EndX=4.96892 EndY=-1.75002 EndZ=0
    g13: Circle [constr] CenterX=8 CenterY=0 CenterZ=0 NormalX=0 NormalY=0 NormalZ=1 AngleXU=0 Radius=3.5
    g14: LineSegment StartX=4.03109 StartY=3.5 StartZ=0 EndX=7.06218 EndY=5.25 EndZ=0
    g15: LineSegment StartX=7.06218 StartY=5.25 StartZ=0 EndX=7.06218 EndY=8.75 EndZ=0
    g16: LineSegment StartX=7.06218 StartY=8.75 StartZ=0 EndX=4.03109 EndY=10.5 EndZ=0
    g17: LineSegment StartX=4.03109 StartY=10.5 StartZ=0 EndX=1 EndY=8.75 EndZ=0
    g18: LineSegment StartX=1 StartY=8.75 StartZ=0 EndX=1 EndY=5.25 EndZ=0
    g19: LineSegment StartX=1 StartY=5.25 StartZ=0 EndX=4.03109 EndY=3.5 EndZ=0
    g20: Circle [constr] CenterX=4.03109 CenterY=7 CenterZ=0 NormalX=0 NormalY=0 NormalZ=1 AngleXU=0 Radius=3.5
    g21: LineSegment StartX=-1 StartY=5.25 StartZ=0 EndX=-1 EndY=8.75 EndZ=0
    g22: LineSegment StartX=-1 StartY=8.75 StartZ=0 EndX=-4.03109 EndY=10.5 EndZ=0
    g23: LineSegment StartX=-4.03109 StartY=10.5 StartZ=0 EndX=-7.06218 EndY=8.75 EndZ=0
    g24: LineSegment StartX=-7.06218 StartY=8.75 StartZ=0 EndX=-7.06218 EndY=5.25 EndZ=0
    g25: LineSegment StartX=-7.06218 StartY=5.25 StartZ=0 EndX=-4.03109 EndY=3.5 EndZ=0
    g26: LineSegment StartX=-4.03109 StartY=3.5 StartZ=0 EndX=-1 EndY=5.25 EndZ=0
    g27: Circle [constr] CenterX=-4.03109 CenterY=7 CenterZ=0 NormalX=0 NormalY=0 NormalZ=1 AngleXU=0 Radius=3.5
    g28: LineSegment StartX=-4.96891 StartY=-1.75 StartZ=0 EndX=-4.96891 EndY=1.75 EndZ=0
    g29: LineSegment StartX=-4.96891 StartY=1.75 StartZ=0 EndX=-8 EndY=3.5 EndZ=0
    g30: LineSegment StartX=-8 StartY=3.5 StartZ=0 EndX=-11.0311 EndY=1.75 EndZ=0
    g31: LineSegment StartX=-11.0311 StartY=1.75 StartZ=0 EndX=-11.0311 EndY=-1.75 EndZ=0
    g32: LineSegment StartX=-11.0311 StartY=-1.75 StartZ=0 EndX=-8 EndY=-3.5 EndZ=0
    g33: LineSegment StartX=-8 StartY=-3.5 StartZ=0 EndX=-4.96891 EndY=-1.75 EndZ=0
    g34: Circle [constr] CenterX=-8 CenterY=0 CenterZ=0 NormalX=0 NormalY=0 NormalZ=1 AngleXU=0 Radius=3.5
    g35: LineSegment StartX=-4.03109 StartY=-3.5 StartZ=0 EndX=-7.06218 EndY=-5.25 EndZ=0
    g36: LineSegment StartX=-7.06218 StartY=-5.25 StartZ=0 EndX=-7.06218 EndY=-8.75 EndZ=0
    g37: LineSegment StartX=-7.06218 StartY=-8.75 StartZ=0 EndX=-4.03109 EndY=-10.5 EndZ=0
    g38: LineSegment StartX=-4.03109 StartY=-10.5 StartZ=0 EndX=-1 EndY=-8.75 EndZ=0
    g39: LineSegment StartX=-1 StartY=-8.75 StartZ=0 EndX=-1 EndY=-5.25 EndZ=0
    g40: LineSegment StartX=-1 StartY=-5.25 StartZ=0 EndX=-4.03109 EndY=-3.5 EndZ=0
    g41: Circle [constr] CenterX=-4.03109 CenterY=-7 CenterZ=0 NormalX=0 NormalY=0 NormalZ=1 AngleXU=0 Radius=3.5
    g42: LineSegment StartX=4.03109 StartY=-3.5 StartZ=0 EndX=1 EndY=-5.25 EndZ=0
    g43: LineSegment StartX=1 StartY=-5.25 StartZ=0 EndX=1 EndY=-8.75 EndZ=0
    g44: LineSegment StartX=1 StartY=-8.75 StartZ=0 EndX=4.03109 EndY=-10.5 EndZ=0
    g45: LineSegment StartX=4.03109 StartY=-10.5 StartZ=0 EndX=7.06218 EndY=-8.75 EndZ=0
    g46: LineSegment StartX=7.06218 StartY=-8.75 StartZ=0 EndX=7.06218 EndY=-5.25 EndZ=0
    g47: LineSegment StartX=7.06218 StartY=-5.25 StartZ=0 EndX=4.03109 EndY=-3.5 EndZ=0
    g48: Circle [constr] CenterX=4.03109 CenterY=-7 CenterZ=0 NormalX=0 NormalY=0 NormalZ=1 AngleXU=0 Radius=3.5
  constraints (117):
    c: Coincident(g0,g1)
    c: Coincident(g1,g2)
    c: Coincident(g2,g3)
    c: Coincident(g3,g4)
    c: Coincident(g4,g5)
    c: Coincident(g5,g0)
    c: Equal(g0, g1-g5) x5
    c: PointOnObject(g0,g6)
    c: PointOnObject(g1,g6)
    c: PointOnObject(g2,g6)
    c: PointOnObject(g3,g6)
    c: PointOnObject(g4,g6)
    c: PointOnObject(g5,g6)
    c: Coincident(g6,g-1)
    c: Diameter(g6) = 7
    c: PointOnObject(g0,g-2)
    c: Coincident(g7,g8)
    c: Coincident(g8,g9)
    c: Coincident(g9,g10)
    c: Coincident(g10,g11)
    c: Coincident(g11,g12)
    c: Coincident(g12,g7)
    c: Equal(g7, g8-g12) x5
    c: PointOnObject(g7,g13)
    c: PointOnObject(g8,g13)
    c: PointOnObject(g9,g13)
    c: PointOnObject(g10,g13)
    c: PointOnObject(g11,g13)
    c: PointOnObject(g12,g13)
    c: PointOnObject(g13,g-1)
    c: Diameter(g13) = 7
    c: Distance(g6,g13) = 8
    c: Horizontal(g0,g10)
    c: Coincident(g14,g15)
    c: Coincident(g15,g16)
    c: Coincident(g16,g17)
    c: Coincident(g17,g18)
    c: Coincident(g18,g19)
    c: Coincident(g19,g14)
    c: Equal(g14, g15-g19) x5
    c: PointOnObject(g14,g20)
    c: PointOnObject(g15,g20)
    c: PointOnObject(g16,g20)
    c: PointOnObject(g17,g20)
    c: PointOnObject(g18,g20)
    c: PointOnObject(g19,g20)
    c: Diameter(g20) = 7
    c: DistanceY(g-1,g20) = 7
    c: Vertical(g18)
    c: Distance(g17,g-2) = 1
    c: Coincident(g21,g22)
    c: Coincident(g22,g23)
    c: Coincident(g23,g24)
    c: Coincident(g24,g25)
    c: Coincident(g25,g26)
    c: Coincident(g26,g21)
    c: Equal(g21, g22-g26) x5
    c: PointOnObject(g21,g27)
    c: PointOnObject(g22,g27)
    c: PointOnObject(g23,g27)
    c: PointOnObject(g24,g27)
    c: PointOnObject(g25,g27)
    c: PointOnObject(g26,g27)
    c: Diameter(g27) = 7
    c: DistanceY(g-1,g27) = 7
    c: DistanceX(g21,g-1) = 1
    c: Vertical(g21)
    c: Coincident(g28,g29)
    c: Coincident(g29,g30)
    c: Coincident(g30,g31)
    c: Coincident(g31,g32)
    c: Coincident(g32,g33)
    c: Coincident(g33,g28)
    c: Equal(g28, g29-g33) x5
    c: PointOnObject(g28,g34)
    c: PointOnObject(g29,g34)
    c: PointOnObject(g30,g34)
    c: PointOnObject(g31,g34)
    c: PointOnObject(g32,g34)
    c: PointOnObject(g33,g34)
    c: PointOnObject(g34,g-1)
    c: Diameter(g34) = 7
    c: Vertical(g31)
    c: DistanceX(g34,g-1) = 8
    c: Coincident(g35,g36)
    c: Coincident(g36,g37)
    c: Coincident(g37,g38)
    c: Coincident(g38,g39)
    c: Coincident(g39,g40)
    c: Coincident(g40,g35)
    c: Equal(g35, g36-g40) x5
    c: PointOnObject(g35,g41)
    c: PointOnObject(g36,g41)
    c: PointOnObject(g37,g41)
    c: PointOnObject(g38,g41)
    c: PointOnObject(g39,g41)
    c: PointOnObject(g40,g41)
    c: Coincident(g42,g43)
    c: Coincident(g43,g44)
    c: Coincident(g44,g45)
    c: Coincident(g45,g46)
    c: Coincident(g46,g47)
    c: Coincident(g47,g42)
    c: Equal(g42, g43-g47) x5
    c: PointOnObject(g42,g48)
    c: PointOnObject(g43,g48)
    c: PointOnObject(g44,g48)
    c: PointOnObject(g45,g48)
    c: PointOnObject(g46,g48)
    c: PointOnObject(g47,g48)
    c: Equal(g41,g48)
    c: Diameter(g41) = 7
    c: Vertical(g39)
    c: Vertical(g43)
    c: Distance(g-2,g39) = 1
    c: Symmetric(g38,g43,g-2)
    c: Distance(g41,g-1) = 7
FEATURE [Part::Extrusion] Extrude688  label="hex290"
  Base = -> Sketch697
  Dir = (0,-1,2e-16)
  DirMode = 2
  FaceMakerClass = Part::FaceMakerBullseye
  FaceMakerMode = 3
  LengthFwd = 10
  LengthRev = 0
  Placement = pos=(52,0,21) rot=(0,0,1;0rad)
  Solid = true
  Symmetric = false
FEATURE [Sketcher::SketchObject] Sketch698
  ArcFitTolerance = 1e-06
  FullyConstrained = true
  MakeInternals = false
  Placement = pos=(0,0,0) rot=(1,0,0;1.5708rad)
  sketch-geometry (49):
    g0: LineSegment StartX=1e-16 StartY=3.5 StartZ=0 EndX=-3.03109 EndY=1.75 EndZ=0
    g1: LineSegment StartX=-3.03109 StartY=1.75 StartZ=0 EndX=-3.03109 EndY=-1.75 EndZ=0
    g2: LineSegment StartX=-3.03109 StartY=-1.75 StartZ=0 EndX=-1e-16 EndY=-3.5 EndZ=0
    g3: LineSegment StartX=-1e-16 StartY=-3.5 StartZ=0 EndX=3.03109 EndY=-1.75 EndZ=0
    g4: LineSegment StartX=3.03109 StartY=-1.75 StartZ=0 EndX=3.03109 EndY=1.75 EndZ=0
    g5: LineSegment StartX=3.03109 StartY=1.75 StartZ=0 EndX=1e-16 EndY=3.5 EndZ=0
    g6: Circle [constr] CenterX=0 CenterY=0 CenterZ=0 NormalX=0 NormalY=0 NormalZ=1 AngleXU=0 Radius=3.5
    g7: LineSegment StartX=4.96892 StartY=-1.75002 StartZ=0 EndX=8.00002 EndY=-3.5 EndZ=0
    g8: LineSegment StartX=8.00002 StartY=-3.5 StartZ=0 EndX=11.0311 EndY=-1.74998 EndZ=0
    g9: LineSegment StartX=11.0311 StartY=-1.74998 StartZ=0 EndX=11.0311 EndY=1.75002 EndZ=0
    g10: LineSegment StartX=11.0311 StartY=1.75002 StartZ=0 EndX=7.99998 EndY=3.5 EndZ=0
    g11: LineSegment StartX=7.99998 StartY=3.5 StartZ=0 EndX=4.9689 EndY=1.74998 EndZ=0
    g12: LineSegment StartX=4.9689 StartY=1.74998 StartZ=0 EndX=4.96892 EndY=-1.75002 EndZ=0
    g13: Circle [constr] CenterX=8 CenterY=0 CenterZ=0 NormalX=0 NormalY=0 NormalZ=1 AngleXU=0 Radius=3.5
    g14: LineSegment StartX=4.03109 StartY=3.5 StartZ=0 EndX=7.06218 EndY=5.25 EndZ=0
    g15: LineSegment StartX=7.06218 StartY=5.25 StartZ=0 EndX=7.06218 EndY=8.75 EndZ=0
    g16: LineSegment StartX=7.06218 StartY=8.75 StartZ=0 EndX=4.03109 EndY=10.5 EndZ=0
    g17: LineSegment StartX=4.03109 StartY=10.5 StartZ=0 EndX=1 EndY=8.75 EndZ=0
    g18: LineSegment StartX=1 StartY=8.75 StartZ=0 EndX=1 EndY=5.25 EndZ=0
    g19: LineSegment StartX=1 StartY=5.25 StartZ=0 EndX=4.03109 EndY=3.5 EndZ=0
    g20: Circle [constr] CenterX=4.03109 CenterY=7 CenterZ=0 NormalX=0 NormalY=0 NormalZ=1 AngleXU=0 Radius=3.5
    g21: LineSegment StartX=-1 StartY=5.25 StartZ=0 EndX=-1 EndY=8.75 EndZ=0
    g22: LineSegment StartX=-1 StartY=8.75 StartZ=0 EndX=-4.03109 EndY=10.5 EndZ=0
    g23: LineSegment StartX=-4.03109 StartY=10.5 StartZ=0 EndX=-7.06218 EndY=8.75 EndZ=0
    g24: LineSegment StartX=-7.06218 StartY=8.75 StartZ=0 EndX=-7.06218 EndY=5.25 EndZ=0
    g25: LineSegment StartX=-7.06218 StartY=5.25 StartZ=0 EndX=-4.03109 EndY=3.5 EndZ=0
    g26: LineSegment StartX=-4.03109 StartY=3.5 StartZ=0 EndX=-1 EndY=5.25 EndZ=0
    g27: Circle [constr] CenterX=-4.03109 CenterY=7 CenterZ=0 NormalX=0 NormalY=0 NormalZ=1 AngleXU=0 Radius=3.5
    g28: LineSegment StartX=-4.96891 StartY=-1.75 StartZ=0 EndX=-4.96891 EndY=1.75 EndZ=0
    g29: LineSegment StartX=-4.96891 StartY=1.75 StartZ=0 EndX=-8 EndY=3.5 EndZ=0
    g30: LineSegment StartX=-8 StartY=3.5 StartZ=0 EndX=-11.0311 EndY=1.75 EndZ=0
    g31: LineSegment StartX=-11.0311 StartY=1.75 StartZ=0 EndX=-11.0311 EndY=-1.75 EndZ=0
    g32: LineSegment StartX=-11.0311 StartY=-1.75 StartZ=0 EndX=-8 EndY=-3.5 EndZ=0
    g33: LineSegment StartX=-8 StartY=-3.5 StartZ=0 EndX=-4.96891 EndY=-1.75 EndZ=0
    g34: Circle [constr] CenterX=-8 CenterY=0 CenterZ=0 NormalX=0 NormalY=0 NormalZ=1 AngleXU=0 Radius=3.5
    g35: LineSegment StartX=-4.03109 StartY=-3.5 StartZ=0 EndX=-7.06218 EndY=-5.25 EndZ=0
    g36: LineSegment StartX=-7.06218 StartY=-5.25 StartZ=0 EndX=-7.06218 EndY=-8.75 EndZ=0
    g37: LineSegment StartX=-7.06218 StartY=-8.75 StartZ=0 EndX=-4.03109 EndY=-10.5 EndZ=0
    g38: LineSegment StartX=-4.03109 StartY=-10.5 StartZ=0 EndX=-1 EndY=-8.75 EndZ=0
    g39: LineSegment StartX=-1 StartY=-8.75 StartZ=0 EndX=-1 EndY=-5.25 EndZ=0
    g40: LineSegment StartX=-1 StartY=-5.25 StartZ=0 EndX=-4.03109 EndY=-3.5 EndZ=0
    g41: Circle [constr] CenterX=-4.03109 CenterY=-7 CenterZ=0 NormalX=0 NormalY=0 NormalZ=1 AngleXU=0 Radius=3.5
    g42: LineSegment StartX=4.03109 StartY=-3.5 StartZ=0 EndX=1 EndY=-5.25 EndZ=0
    g43: LineSegment StartX=1 StartY=-5.25 StartZ=0 EndX=1 EndY=-8.75 EndZ=0
    g44: LineSegment StartX=1 StartY=-8.75 StartZ=0 EndX=4.03109 EndY=-10.5 EndZ=0
    g45: LineSegment StartX=4.03109 StartY=-10.5 StartZ=0 EndX=7.06218 EndY=-8.75 EndZ=0
    g46: LineSegment StartX=7.06218 StartY=-8.75 StartZ=0 EndX=7.06218 EndY=-5.25 EndZ=0
    g47: LineSegment StartX=7.06218 StartY=-5.25 StartZ=0 EndX=4.03109 EndY=-3.5 EndZ=0
    g48: Circle [constr] CenterX=4.03109 CenterY=-7 CenterZ=0 NormalX=0 NormalY=0 NormalZ=1 AngleXU=0 Radius=3.5
  constraints (117):
    c: Coincident(g0,g1)
    c: Coincident(g1,g2)
    c: Coincident(g2,g3)
    c: Coincident(g3,g4)
    c: Coincident(g4,g5)
    c: Coincident(g5,g0)
    c: Equal(g0, g1-g5) x5
    c: PointOnObject(g0,g6)
    c: PointOnObject(g1,g6)
    c: PointOnObject(g2,g6)
    c: PointOnObject(g3,g6)
    c: PointOnObject(g4,g6)
    c: PointOnObject(g5,g6)
    c: Coincident(g6,g-1)
    c: Diameter(g6) = 7
    c: PointOnObject(g0,g-2)
    c: Coincident(g7,g8)
    c: Coincident(g8,g9)
    c: Coincident(g9,g10)
    c: Coincident(g10,g11)
    c: Coincident(g11,g12)
    c: Coincident(g12,g7)
    c: Equal(g7, g8-g12) x5
    c: PointOnObject(g7,g13)
    c: PointOnObject(g8,g13)
    c: PointOnObject(g9,g13)
    c: PointOnObject(g10,g13)
    c: PointOnObject(g11,g13)
    c: PointOnObject(g12,g13)
    c: PointOnObject(g13,g-1)
    c: Diameter(g13) = 7
    c: Distance(g6,g13) = 8
    c: Horizontal(g0,g10)
    c: Coincident(g14,g15)
    c: Coincident(g15,g16)
    c: Coincident(g16,g17)
    c: Coincident(g17,g18)
    c: Coincident(g18,g19)
    c: Coincident(g19,g14)
    c: Equal(g14, g15-g19) x5
    c: PointOnObject(g14,g20)
    c: PointOnObject(g15,g20)
    c: PointOnObject(g16,g20)
    c: PointOnObject(g17,g20)
    c: PointOnObject(g18,g20)
    c: PointOnObject(g19,g20)
    c: Diameter(g20) = 7
    c: DistanceY(g-1,g20) = 7
    c: Vertical(g18)
    c: Distance(g17,g-2) = 1
    c: Coincident(g21,g22)
    c: Coincident(g22,g23)
    c: Coincident(g23,g24)
    c: Coincident(g24,g25)
    c: Coincident(g25,g26)
    c: Coincident(g26,g21)
    c: Equal(g21, g22-g26) x5
    c: PointOnObject(g21,g27)
    c: PointOnObject(g22,g27)
    c: PointOnObject(g23,g27)
    c: PointOnObject(g24,g27)
    c: PointOnObject(g25,g27)
    c: PointOnObject(g26,g27)
    c: Diameter(g27) = 7
    c: DistanceY(g-1,g27) = 7
    c: DistanceX(g21,g-1) = 1
    c: Vertical(g21)
    c: Coincident(g28,g29)
    c: Coincident(g29,g30)
    c: Coincident(g30,g31)
    c: Coincident(g31,g32)
    c: Coincident(g32,g33)
    c: Coincident(g33,g28)
    c: Equal(g28, g29-g33) x5
    c: PointOnObject(g28,g34)
    c: PointOnObject(g29,g34)
    c: PointOnObject(g30,g34)
    c: PointOnObject(g31,g34)
    c: PointOnObject(g32,g34)
    c: PointOnObject(g33,g34)
    c: PointOnObject(g34,g-1)
    c: Diameter(g34) = 7
    c: Vertical(g31)
    c: DistanceX(g34,g-1) = 8
    c: Coincident(g35,g36)
    c: Coincident(g36,g37)
    c: Coincident(g37,g38)
    c: Coincident(g38,g39)
    c: Coincident(g39,g40)
    c: Coincident(g40,g35)
    c: Equal(g35, g36-g40) x5
    c: PointOnObject(g35,g41)
    c: PointOnObject(g36,g41)
    c: PointOnObject(g37,g41)
    c: PointOnObject(g38,g41)
    c: PointOnObject(g39,g41)
    c: PointOnObject(g40,g41)
    c: Coincident(g42,g43)
    c: Coincident(g43,g44)
    c: Coincident(g44,g45)
    c: Coincident(g45,g46)
    c: Coincident(g46,g47)
    c: Coincident(g47,g42)
    c: Equal(g42, g43-g47) x5
    c: PointOnObject(g42,g48)
    c: PointOnObject(g43,g48)
    c: PointOnObject(g44,g48)
    c: PointOnObject(g45,g48)
    c: PointOnObject(g46,g48)
    c: PointOnObject(g47,g48)
    c: Equal(g41,g48)
    c: Diameter(g41) = 7
    c: Vertical(g39)
    c: Vertical(g43)
    c: Distance(g-2,g39) = 1
    c: Symmetric(g38,g43,g-2)
    c: Distance(g41,g-1) = 7
FEATURE [Part::Extrusion] Extrude689  label="hex291"
  Base = -> Sketch698
  Dir = (0,-1,2e-16)
  DirMode = 2
  FaceMakerClass = Part::FaceMakerBullseye
  FaceMakerMode = 3
  LengthFwd = 10
  LengthRev = 0
  Placement = pos=(-32,0,28) rot=(0,0,1;0rad)
  Solid = true
  Symmetric = false
FEATURE [Sketcher::SketchObject] Sketch699
  ArcFitTolerance = 1e-06
  FullyConstrained = true
  MakeInternals = false
  Placement = pos=(0,0,0) rot=(1,0,0;1.5708rad)
  sketch-geometry (49):
    g0: LineSegment StartX=1e-16 StartY=3.5 StartZ=0 EndX=-3.03109 EndY=1.75 EndZ=0
    g1: LineSegment StartX=-3.03109 StartY=1.75 StartZ=0 EndX=-3.03109 EndY=-1.75 EndZ=0
    g2: LineSegment StartX=-3.03109 StartY=-1.75 StartZ=0 EndX=-1e-16 EndY=-3.5 EndZ=0
    g3: LineSegment StartX=-1e-16 StartY=-3.5 StartZ=0 EndX=3.03109 EndY=-1.75 EndZ=0
    g4: LineSegment StartX=3.03109 StartY=-1.75 StartZ=0 EndX=3.03109 EndY=1.75 EndZ=0
    g5: LineSegment StartX=3.03109 StartY=1.75 StartZ=0 EndX=1e-16 EndY=3.5 EndZ=0
    g6: Circle [constr] CenterX=0 CenterY=0 CenterZ=0 NormalX=0 NormalY=0 NormalZ=1 AngleXU=0 Radius=3.5
    g7: LineSegment StartX=4.96892 StartY=-1.75002 StartZ=0 EndX=8.00002 EndY=-3.5 EndZ=0
    g8: LineSegment StartX=8.00002 StartY=-3.5 StartZ=0 EndX=11.0311 EndY=-1.74998 EndZ=0
    g9: LineSegment StartX=11.0311 StartY=-1.74998 StartZ=0 EndX=11.0311 EndY=1.75002 EndZ=0
    g10: LineSegment StartX=11.0311 StartY=1.75002 StartZ=0 EndX=7.99998 EndY=3.5 EndZ=0
    g11: LineSegment StartX=7.99998 StartY=3.5 StartZ=0 EndX=4.9689 EndY=1.74998 EndZ=0
    g12: LineSegment StartX=4.9689 StartY=1.74998 StartZ=0 EndX=4.96892 EndY=-1.75002 EndZ=0
    g13: Circle [constr] CenterX=8 CenterY=0 CenterZ=0 NormalX=0 NormalY=0 NormalZ=1 AngleXU=0 Radius=3.5
    g14: LineSegment StartX=4.03109 StartY=3.5 StartZ=0 EndX=7.06218 EndY=5.25 EndZ=0
    g15: LineSegment StartX=7.06218 StartY=5.25 StartZ=0 EndX=7.06218 EndY=8.75 EndZ=0
    g16: LineSegment StartX=7.06218 StartY=8.75 StartZ=0 EndX=4.03109 EndY=10.5 EndZ=0
    g17: LineSegment StartX=4.03109 StartY=10.5 StartZ=0 EndX=1 EndY=8.75 EndZ=0
    g18: LineSegment StartX=1 StartY=8.75 StartZ=0 EndX=1 EndY=5.25 EndZ=0
    g19: LineSegment StartX=1 StartY=5.25 StartZ=0 EndX=4.03109 EndY=3.5 EndZ=0
    g20: Circle [constr] CenterX=4.03109 CenterY=7 CenterZ=0 NormalX=0 NormalY=0 NormalZ=1 AngleXU=0 Radius=3.5
    g21: LineSegment StartX=-1 StartY=5.25 StartZ=0 EndX=-1 EndY=8.75 EndZ=0
    g22: LineSegment StartX=-1 StartY=8.75 StartZ=0 EndX=-4.03109 EndY=10.5 EndZ=0
    g23: LineSegment StartX=-4.03109 StartY=10.5 StartZ=0 EndX=-7.06218 EndY=8.75 EndZ=0
    g24: LineSegment StartX=-7.06218 StartY=8.75 StartZ=0 EndX=-7.06218 EndY=5.25 EndZ=0
    g25: LineSegment StartX=-7.06218 StartY=5.25 StartZ=0 EndX=-4.03109 EndY=3.5 EndZ=0
    g26: LineSegment StartX=-4.03109 StartY=3.5 StartZ=0 EndX=-1 EndY=5.25 EndZ=0
    g27: Circle [constr] CenterX=-4.03109 CenterY=7 CenterZ=0 NormalX=0 NormalY=0 NormalZ=1 AngleXU=0 Radius=3.5
    g28: LineSegment StartX=-4.96891 StartY=-1.75 StartZ=0 EndX=-4.96891 EndY=1.75 EndZ=0
    g29: LineSegment StartX=-4.96891 StartY=1.75 StartZ=0 EndX=-8 EndY=3.5 EndZ=0
    g30: LineSegment StartX=-8 StartY=3.5 StartZ=0 EndX=-11.0311 EndY=1.75 EndZ=0
    g31: LineSegment StartX=-11.0311 StartY=1.75 StartZ=0 EndX=-11.0311 EndY=-1.75 EndZ=0
    g32: LineSegment StartX=-11.0311 StartY=-1.75 StartZ=0 EndX=-8 EndY=-3.5 EndZ=0
    g33: LineSegment StartX=-8 StartY=-3.5 StartZ=0 EndX=-4.96891 EndY=-1.75 EndZ=0
    g34: Circle [constr] CenterX=-8 CenterY=0 CenterZ=0 NormalX=0 NormalY=0 NormalZ=1 AngleXU=0 Radius=3.5
    g35: LineSegment StartX=-4.03109 StartY=-3.5 StartZ=0 EndX=-7.06218 EndY=-5.25 EndZ=0
    g36: LineSegment StartX=-7.06218 StartY=-5.25 StartZ=0 EndX=-7.06218 EndY=-8.75 EndZ=0
    g37: LineSegment StartX=-7.06218 StartY=-8.75 StartZ=0 EndX=-4.03109 EndY=-10.5 EndZ=0
    g38: LineSegment StartX=-4.03109 StartY=-10.5 StartZ=0 EndX=-1 EndY=-8.75 EndZ=0
    g39: LineSegment StartX=-1 StartY=-8.75 StartZ=0 EndX=-1 EndY=-5.25 EndZ=0
    g40: LineSegment StartX=-1 StartY=-5.25 StartZ=0 EndX=-4.03109 EndY=-3.5 EndZ=0
    g41: Circle [constr] CenterX=-4.03109 CenterY=-7 CenterZ=0 NormalX=0 NormalY=0 NormalZ=1 AngleXU=0 Radius=3.5
    g42: LineSegment StartX=4.03109 StartY=-3.5 StartZ=0 EndX=1 EndY=-5.25 EndZ=0
    g43: LineSegment StartX=1 StartY=-5.25 StartZ=0 EndX=1 EndY=-8.75 EndZ=0
    g44: LineSegment StartX=1 StartY=-8.75 StartZ=0 EndX=4.03109 EndY=-10.5 EndZ=0
    g45: LineSegment StartX=4.03109 StartY=-10.5 StartZ=0 EndX=7.06218 EndY=-8.75 EndZ=0
    g46: LineSegment StartX=7.06218 StartY=-8.75 StartZ=0 EndX=7.06218 EndY=-5.25 EndZ=0
    g47: LineSegment StartX=7.06218 StartY=-5.25 StartZ=0 EndX=4.03109 EndY=-3.5 EndZ=0
    g48: Circle [constr] CenterX=4.03109 CenterY=-7 CenterZ=0 NormalX=0 NormalY=0 NormalZ=1 AngleXU=0 Radius=3.5
  constraints (117):
    c: Coincident(g0,g1)
    c: Coincident(g1,g2)
    c: Coincident(g2,g3)
    c: Coincident(g3,g4)
    c: Coincident(g4,g5)
    c: Coincident(g5,g0)
    c: Equal(g0, g1-g5) x5
    c: PointOnObject(g0,g6)
    c: PointOnObject(g1,g6)
    c: PointOnObject(g2,g6)
    c: PointOnObject(g3,g6)
    c: PointOnObject(g4,g6)
    c: PointOnObject(g5,g6)
    c: Coincident(g6,g-1)
    c: Diameter(g6) = 7
    c: PointOnObject(g0,g-2)
    c: Coincident(g7,g8)
    c: Coincident(g8,g9)
    c: Coincident(g9,g10)
    c: Coincident(g10,g11)
    c: Coincident(g11,g12)
    c: Coincident(g12,g7)
    c: Equal(g7, g8-g12) x5
    c: PointOnObject(g7,g13)
    c: PointOnObject(g8,g13)
    c: PointOnObject(g9,g13)
    c: PointOnObject(g10,g13)
    c: PointOnObject(g11,g13)
    c: PointOnObject(g12,g13)
    c: PointOnObject(g13,g-1)
    c: Diameter(g13) = 7
    c: Distance(g6,g13) = 8
    c: Horizontal(g0,g10)
    c: Coincident(g14,g15)
    c: Coincident(g15,g16)
    c: Coincident(g16,g17)
    c: Coincident(g17,g18)
    c: Coincident(g18,g19)
    c: Coincident(g19,g14)
    c: Equal(g14, g15-g19) x5
    c: PointOnObject(g14,g20)
    c: PointOnObject(g15,g20)
    c: PointOnObject(g16,g20)
    c: PointOnObject(g17,g20)
    c: PointOnObject(g18,g20)
    c: PointOnObject(g19,g20)
    c: Diameter(g20) = 7
    c: DistanceY(g-1,g20) = 7
    c: Vertical(g18)
    c: Distance(g17,g-2) = 1
    c: Coincident(g21,g22)
    c: Coincident(g22,g23)
    c: Coincident(g23,g24)
    c: Coincident(g24,g25)
    c: Coincident(g25,g26)
    c: Coincident(g26,g21)
    c: Equal(g21, g22-g26) x5
    c: PointOnObject(g21,g27)
    c: PointOnObject(g22,g27)
    c: PointOnObject(g23,g27)
    c: PointOnObject(g24,g27)
    c: PointOnObject(g25,g27)
    c: PointOnObject(g26,g27)
    c: Diameter(g27) = 7
    c: DistanceY(g-1,g27) = 7
    c: DistanceX(g21,g-1) = 1
    c: Vertical(g21)
    c: Coincident(g28,g29)
    c: Coincident(g29,g30)
    c: Coincident(g30,g31)
    c: Coincident(g31,g32)
    c: Coincident(g32,g33)
    c: Coincident(g33,g28)
    c: Equal(g28, g29-g33) x5
    c: PointOnObject(g28,g34)
    c: PointOnObject(g29,g34)
    c: PointOnObject(g30,g34)
    c: PointOnObject(g31,g34)
    c: PointOnObject(g32,g34)
    c: PointOnObject(g33,g34)
    c: PointOnObject(g34,g-1)
    c: Diameter(g34) = 7
    c: Vertical(g31)
    c: DistanceX(g34,g-1) = 8
    c: Coincident(g35,g36)
    c: Coincident(g36,g37)
    c: Coincident(g37,g38)
    c: Coincident(g38,g39)
    c: Coincident(g39,g40)
    c: Coincident(g40,g35)
    c: Equal(g35, g36-g40) x5
    c: PointOnObject(g35,g41)
    c: PointOnObject(g36,g41)
    c: PointOnObject(g37,g41)
    c: PointOnObject(g38,g41)
    c: PointOnObject(g39,g41)
    c: PointOnObject(g40,g41)
    c: Coincident(g42,g43)
    c: Coincident(g43,g44)
    c: Coincident(g44,g45)
    c: Coincident(g45,g46)
    c: Coincident(g46,g47)
    c: Coincident(g47,g42)
    c: Equal(g42, g43-g47) x5
    c: PointOnObject(g42,g48)
    c: PointOnObject(g43,g48)
    c: PointOnObject(g44,g48)
    c: PointOnObject(g45,g48)
    c: PointOnObject(g46,g48)
    c: PointOnObject(g47,g48)
    c: Equal(g41,g48)
    c: Diameter(g41) = 7
    c: Vertical(g39)
    c: Vertical(g43)
    c: Distance(g-2,g39) = 1
    c: Symmetric(g38,g43,g-2)
    c: Distance(g41,g-1) = 7
FEATURE [Part::Extrusion] Extrude690  label="hex292"
  Base = -> Sketch699
  Dir = (0,-1,2e-16)
  DirMode = 2
  FaceMakerClass = Part::FaceMakerBullseye
  FaceMakerMode = 3
  LengthFwd = 10
  LengthRev = 0
  Placement = pos=(-12,0,35) rot=(0,0,1;0rad)
  Solid = true
  Symmetric = false
FEATURE [Sketcher::SketchObject] Sketch700
  ArcFitTolerance = 1e-06
  FullyConstrained = true
  MakeInternals = false
  Placement = pos=(0,0,0) rot=(1,0,0;1.5708rad)
  sketch-geometry (49):
    g0: LineSegment StartX=1e-16 StartY=3.5 StartZ=0 EndX=-3.03109 EndY=1.75 EndZ=0
    g1: LineSegment StartX=-3.03109 StartY=1.75 StartZ=0 EndX=-3.03109 EndY=-1.75 EndZ=0
    g2: LineSegment StartX=-3.03109 StartY=-1.75 StartZ=0 EndX=-1e-16 EndY=-3.5 EndZ=0
    g3: LineSegment StartX=-1e-16 StartY=-3.5 StartZ=0 EndX=3.03109 EndY=-1.75 EndZ=0
    g4: LineSegment StartX=3.03109 StartY=-1.75 StartZ=0 EndX=3.03109 EndY=1.75 EndZ=0
    g5: LineSegment StartX=3.03109 StartY=1.75 StartZ=0 EndX=1e-16 EndY=3.5 EndZ=0
    g6: Circle [constr] CenterX=0 CenterY=0 CenterZ=0 NormalX=0 NormalY=0 NormalZ=1 AngleXU=0 Radius=3.5
    g7: LineSegment StartX=4.96892 StartY=-1.75002 StartZ=0 EndX=8.00002 EndY=-3.5 EndZ=0
    g8: LineSegment StartX=8.00002 StartY=-3.5 StartZ=0 EndX=11.0311 EndY=-1.74998 EndZ=0
    g9: LineSegment StartX=11.0311 StartY=-1.74998 StartZ=0 EndX=11.0311 EndY=1.75002 EndZ=0
    g10: LineSegment StartX=11.0311 StartY=1.75002 StartZ=0 EndX=7.99998 EndY=3.5 EndZ=0
    g11: LineSegment StartX=7.99998 StartY=3.5 StartZ=0 EndX=4.9689 EndY=1.74998 EndZ=0
    g12: LineSegment StartX=4.9689 StartY=1.74998 StartZ=0 EndX=4.96892 EndY=-1.75002 EndZ=0
    g13: Circle [constr] CenterX=8 CenterY=0 CenterZ=0 NormalX=0 NormalY=0 NormalZ=1 AngleXU=0 Radius=3.5
    g14: LineSegment StartX=4.03109 StartY=3.5 StartZ=0 EndX=7.06218 EndY=5.25 EndZ=0
    g15: LineSegment StartX=7.06218 StartY=5.25 StartZ=0 EndX=7.06218 EndY=8.75 EndZ=0
    g16: LineSegment StartX=7.06218 StartY=8.75 StartZ=0 EndX=4.03109 EndY=10.5 EndZ=0
    g17: LineSegment StartX=4.03109 StartY=10.5 StartZ=0 EndX=1 EndY=8.75 EndZ=0
    g18: LineSegment StartX=1 StartY=8.75 StartZ=0 EndX=1 EndY=5.25 EndZ=0
    g19: LineSegment StartX=1 StartY=5.25 StartZ=0 EndX=4.03109 EndY=3.5 EndZ=0
    g20: Circle [constr] CenterX=4.03109 CenterY=7 CenterZ=0 NormalX=0 NormalY=0 NormalZ=1 AngleXU=0 Radius=3.5
    g21: LineSegment StartX=-1 StartY=5.25 StartZ=0 EndX=-1 EndY=8.75 EndZ=0
    g22: LineSegment StartX=-1 StartY=8.75 StartZ=0 EndX=-4.03109 EndY=10.5 EndZ=0
    g23: LineSegment StartX=-4.03109 StartY=10.5 StartZ=0 EndX=-7.06218 EndY=8.75 EndZ=0
    g24: LineSegment StartX=-7.06218 StartY=8.75 StartZ=0 EndX=-7.06218 EndY=5.25 EndZ=0
    g25: LineSegment StartX=-7.06218 StartY=5.25 StartZ=0 EndX=-4.03109 EndY=3.5 EndZ=0
    g26: LineSegment StartX=-4.03109 StartY=3.5 StartZ=0 EndX=-1 EndY=5.25 EndZ=0
    g27: Circle [constr] CenterX=-4.03109 CenterY=7 CenterZ=0 NormalX=0 NormalY=0 NormalZ=1 AngleXU=0 Radius=3.5
    g28: LineSegment StartX=-4.96891 StartY=-1.75 StartZ=0 EndX=-4.96891 EndY=1.75 EndZ=0
    g29: LineSegment StartX=-4.96891 StartY=1.75 StartZ=0 EndX=-8 EndY=3.5 EndZ=0
    g30: LineSegment StartX=-8 StartY=3.5 StartZ=0 EndX=-11.0311 EndY=1.75 EndZ=0
    g31: LineSegment StartX=-11.0311 StartY=1.75 StartZ=0 EndX=-11.0311 EndY=-1.75 EndZ=0
    g32: LineSegment StartX=-11.0311 StartY=-1.75 StartZ=0 EndX=-8 EndY=-3.5 EndZ=0
    g33: LineSegment StartX=-8 StartY=-3.5 StartZ=0 EndX=-4.96891 EndY=-1.75 EndZ=0
    g34: Circle [constr] CenterX=-8 CenterY=0 CenterZ=0 NormalX=0 NormalY=0 NormalZ=1 AngleXU=0 Radius=3.5
    g35: LineSegment StartX=-4.03109 StartY=-3.5 StartZ=0 EndX=-7.06218 EndY=-5.25 EndZ=0
    g36: LineSegment StartX=-7.06218 StartY=-5.25 StartZ=0 EndX=-7.06218 EndY=-8.75 EndZ=0
    g37: LineSegment StartX=-7.06218 StartY=-8.75 StartZ=0 EndX=-4.03109 EndY=-10.5 EndZ=0
    g38: LineSegment StartX=-4.03109 StartY=-10.5 StartZ=0 EndX=-1 EndY=-8.75 EndZ=0
    g39: LineSegment StartX=-1 StartY=-8.75 StartZ=0 EndX=-1 EndY=-5.25 EndZ=0
    g40: LineSegment StartX=-1 StartY=-5.25 StartZ=0 EndX=-4.03109 EndY=-3.5 EndZ=0
    g41: Circle [constr] CenterX=-4.03109 CenterY=-7 CenterZ=0 NormalX=0 NormalY=0 NormalZ=1 AngleXU=0 Radius=3.5
    g42: LineSegment StartX=4.03109 StartY=-3.5 StartZ=0 EndX=1 EndY=-5.25 EndZ=0
    g43: LineSegment StartX=1 StartY=-5.25 StartZ=0 EndX=1 EndY=-8.75 EndZ=0
    g44: LineSegment StartX=1 StartY=-8.75 StartZ=0 EndX=4.03109 EndY=-10.5 EndZ=0
    g45: LineSegment StartX=4.03109 StartY=-10.5 StartZ=0 EndX=7.06218 EndY=-8.75 EndZ=0
    g46: LineSegment StartX=7.06218 StartY=-8.75 StartZ=0 EndX=7.06218 EndY=-5.25 EndZ=0
    g47: LineSegment StartX=7.06218 StartY=-5.25 StartZ=0 EndX=4.03109 EndY=-3.5 EndZ=0
    g48: Circle [constr] CenterX=4.03109 CenterY=-7 CenterZ=0 NormalX=0 NormalY=0 NormalZ=1 AngleXU=0 Radius=3.5
  constraints (117):
    c: Coincident(g0,g1)
    c: Coincident(g1,g2)
    c: Coincident(g2,g3)
    c: Coincident(g3,g4)
    c: Coincident(g4,g5)
    c: Coincident(g5,g0)
    c: Equal(g0, g1-g5) x5
    c: PointOnObject(g0,g6)
    c: PointOnObject(g1,g6)
    c: PointOnObject(g2,g6)
    c: PointOnObject(g3,g6)
    c: PointOnObject(g4,g6)
    c: PointOnObject(g5,g6)
    c: Coincident(g6,g-1)
    c: Diameter(g6) = 7
    c: PointOnObject(g0,g-2)
    c: Coincident(g7,g8)
    c: Coincident(g8,g9)
    c: Coincident(g9,g10)
    c: Coincident(g10,g11)
    c: Coincident(g11,g12)
    c: Coincident(g12,g7)
    c: Equal(g7, g8-g12) x5
    c: PointOnObject(g7,g13)
    c: PointOnObject(g8,g13)
    c: PointOnObject(g9,g13)
    c: PointOnObject(g10,g13)
    c: PointOnObject(g11,g13)
    c: PointOnObject(g12,g13)
    c: PointOnObject(g13,g-1)
    c: Diameter(g13) = 7
    c: Distance(g6,g13) = 8
    c: Horizontal(g0,g10)
    c: Coincident(g14,g15)
    c: Coincident(g15,g16)
    c: Coincident(g16,g17)
    c: Coincident(g17,g18)
    c: Coincident(g18,g19)
    c: Coincident(g19,g14)
    c: Equal(g14, g15-g19) x5
    c: PointOnObject(g14,g20)
    c: PointOnObject(g15,g20)
    c: PointOnObject(g16,g20)
    c: PointOnObject(g17,g20)
    c: PointOnObject(g18,g20)
    c: PointOnObject(g19,g20)
    c: Diameter(g20) = 7
    c: DistanceY(g-1,g20) = 7
    c: Vertical(g18)
    c: Distance(g17,g-2) = 1
    c: Coincident(g21,g22)
    c: Coincident(g22,g23)
    c: Coincident(g23,g24)
    c: Coincident(g24,g25)
    c: Coincident(g25,g26)
    c: Coincident(g26,g21)
    c: Equal(g21, g22-g26) x5
    c: PointOnObject(g21,g27)
    c: PointOnObject(g22,g27)
    c: PointOnObject(g23,g27)
    c: PointOnObject(g24,g27)
    c: PointOnObject(g25,g27)
    c: PointOnObject(g26,g27)
    c: Diameter(g27) = 7
    c: DistanceY(g-1,g27) = 7
    c: DistanceX(g21,g-1) = 1
    c: Vertical(g21)
    c: Coincident(g28,g29)
    c: Coincident(g29,g30)
    c: Coincident(g30,g31)
    c: Coincident(g31,g32)
    c: Coincident(g32,g33)
    c: Coincident(g33,g28)
    c: Equal(g28, g29-g33) x5
    c: PointOnObject(g28,g34)
    c: PointOnObject(g29,g34)
    c: PointOnObject(g30,g34)
    c: PointOnObject(g31,g34)
    c: PointOnObject(g32,g34)
    c: PointOnObject(g33,g34)
    c: PointOnObject(g34,g-1)
    c: Diameter(g34) = 7
    c: Vertical(g31)
    c: DistanceX(g34,g-1) = 8
    c: Coincident(g35,g36)
    c: Coincident(g36,g37)
    c: Coincident(g37,g38)
    c: Coincident(g38,g39)
    c: Coincident(g39,g40)
    c: Coincident(g40,g35)
    c: Equal(g35, g36-g40) x5
    c: PointOnObject(g35,g41)
    c: PointOnObject(g36,g41)
    c: PointOnObject(g37,g41)
    c: PointOnObject(g38,g41)
    c: PointOnObject(g39,g41)
    c: PointOnObject(g40,g41)
    c: Coincident(g42,g43)
    c: Coincident(g43,g44)
    c: Coincident(g44,g45)
    c: Coincident(g45,g46)
    c: Coincident(g46,g47)
    c: Coincident(g47,g42)
    c: Equal(g42, g43-g47) x5
    c: PointOnObject(g42,g48)
    c: PointOnObject(g43,g48)
    c: PointOnObject(g44,g48)
    c: PointOnObject(g45,g48)
    c: PointOnObject(g46,g48)
    c: PointOnObject(g47,g48)
    c: Equal(g41,g48)
    c: Diameter(g41) = 7
    c: Vertical(g39)
    c: Vertical(g43)
    c: Distance(g-2,g39) = 1
    c: Symmetric(g38,g43,g-2)
    c: Distance(g41,g-1) = 7
FEATURE [Part::Extrusion] Extrude691  label="hex293"
  Base = -> Sketch700
  Dir = (0,-1,2e-16)
  DirMode = 2
  FaceMakerClass = Part::FaceMakerBullseye
  FaceMakerMode = 3
  LengthFwd = 10
  LengthRev = 0
  Placement = pos=(-80,0,0) rot=(0,0,1;0rad)
  Solid = true
  Symmetric = false
FEATURE [Sketcher::SketchObject] Sketch701
  ArcFitTolerance = 1e-06
  FullyConstrained = true
  MakeInternals = false
  Placement = pos=(0,0,0) rot=(1,0,0;1.5708rad)
  sketch-geometry (49):
    g0: LineSegment StartX=1e-16 StartY=3.5 StartZ=0 EndX=-3.03109 EndY=1.75 EndZ=0
    g1: LineSegment StartX=-3.03109 StartY=1.75 StartZ=0 EndX=-3.03109 EndY=-1.75 EndZ=0
    g2: LineSegment StartX=-3.03109 StartY=-1.75 StartZ=0 EndX=-1e-16 EndY=-3.5 EndZ=0
    g3: LineSegment StartX=-1e-16 StartY=-3.5 StartZ=0 EndX=3.03109 EndY=-1.75 EndZ=0
    g4: LineSegment StartX=3.03109 StartY=-1.75 StartZ=0 EndX=3.03109 EndY=1.75 EndZ=0
    g5: LineSegment StartX=3.03109 StartY=1.75 StartZ=0 EndX=1e-16 EndY=3.5 EndZ=0
    g6: Circle [constr] CenterX=0 CenterY=0 CenterZ=0 NormalX=0 NormalY=0 NormalZ=1 AngleXU=0 Radius=3.5
    g7: LineSegment StartX=4.96892 StartY=-1.75002 StartZ=0 EndX=8.00002 EndY=-3.5 EndZ=0
    g8: LineSegment StartX=8.00002 StartY=-3.5 StartZ=0 EndX=11.0311 EndY=-1.74998 EndZ=0
    g9: LineSegment StartX=11.0311 StartY=-1.74998 StartZ=0 EndX=11.0311 EndY=1.75002 EndZ=0
    g10: LineSegment StartX=11.0311 StartY=1.75002 StartZ=0 EndX=7.99998 EndY=3.5 EndZ=0
    g11: LineSegment StartX=7.99998 StartY=3.5 StartZ=0 EndX=4.9689 EndY=1.74998 EndZ=0
    g12: LineSegment StartX=4.9689 StartY=1.74998 StartZ=0 EndX=4.96892 EndY=-1.75002 EndZ=0
    g13: Circle [constr] CenterX=8 CenterY=0 CenterZ=0 NormalX=0 NormalY=0 NormalZ=1 AngleXU=0 Radius=3.5
    g14: LineSegment StartX=4.03109 StartY=3.5 StartZ=0 EndX=7.06218 EndY=5.25 EndZ=0
    g15: LineSegment StartX=7.06218 StartY=5.25 StartZ=0 EndX=7.06218 EndY=8.75 EndZ=0
    g16: LineSegment StartX=7.06218 StartY=8.75 StartZ=0 EndX=4.03109 EndY=10.5 EndZ=0
    g17: LineSegment StartX=4.03109 StartY=10.5 StartZ=0 EndX=1 EndY=8.75 EndZ=0
    g18: LineSegment StartX=1 StartY=8.75 StartZ=0 EndX=1 EndY=5.25 EndZ=0
    g19: LineSegment StartX=1 StartY=5.25 StartZ=0 EndX=4.03109 EndY=3.5 EndZ=0
    g20: Circle [constr] CenterX=4.03109 CenterY=7 CenterZ=0 NormalX=0 NormalY=0 NormalZ=1 AngleXU=0 Radius=3.5
    g21: LineSegment StartX=-1 StartY=5.25 StartZ=0 EndX=-1 EndY=8.75 EndZ=0
    g22: LineSegment StartX=-1 StartY=8.75 StartZ=0 EndX=-4.03109 EndY=10.5 EndZ=0
    g23: LineSegment StartX=-4.03109 StartY=10.5 StartZ=0 EndX=-7.06218 EndY=8.75 EndZ=0
    g24: LineSegment StartX=-7.06218 StartY=8.75 StartZ=0 EndX=-7.06218 EndY=5.25 EndZ=0
    g25: LineSegment StartX=-7.06218 StartY=5.25 StartZ=0 EndX=-4.03109 EndY=3.5 EndZ=0
    g26: LineSegment StartX=-4.03109 StartY=3.5 StartZ=0 EndX=-1 EndY=5.25 EndZ=0
    g27: Circle [constr] CenterX=-4.03109 CenterY=7 CenterZ=0 NormalX=0 NormalY=0 NormalZ=1 AngleXU=0 Radius=3.5
    g28: LineSegment StartX=-4.96891 StartY=-1.75 StartZ=0 EndX=-4.96891 EndY=1.75 EndZ=0
    g29: LineSegment StartX=-4.96891 StartY=1.75 StartZ=0 EndX=-8 EndY=3.5 EndZ=0
    g30: LineSegment StartX=-8 StartY=3.5 StartZ=0 EndX=-11.0311 EndY=1.75 EndZ=0
    g31: LineSegment StartX=-11.0311 StartY=1.75 StartZ=0 EndX=-11.0311 EndY=-1.75 EndZ=0
    g32: LineSegment StartX=-11.0311 StartY=-1.75 StartZ=0 EndX=-8 EndY=-3.5 EndZ=0
    g33: LineSegment StartX=-8 StartY=-3.5 StartZ=0 EndX=-4.96891 EndY=-1.75 EndZ=0
    g34: Circle [constr] CenterX=-8 CenterY=0 CenterZ=0 NormalX=0 NormalY=0 NormalZ=1 AngleXU=0 Radius=3.5
    g35: LineSegment StartX=-4.03109 StartY=-3.5 StartZ=0 EndX=-7.06218 EndY=-5.25 EndZ=0
    g36: LineSegment StartX=-7.06218 StartY=-5.25 StartZ=0 EndX=-7.06218 EndY=-8.75 EndZ=0
    g37: LineSegment StartX=-7.06218 StartY=-8.75 StartZ=0 EndX=-4.03109 EndY=-10.5 EndZ=0
    g38: LineSegment StartX=-4.03109 StartY=-10.5 StartZ=0 EndX=-1 EndY=-8.75 EndZ=0
    g39: LineSegment StartX=-1 StartY=-8.75 StartZ=0 EndX=-1 EndY=-5.25 EndZ=0
    g40: LineSegment StartX=-1 StartY=-5.25 StartZ=0 EndX=-4.03109 EndY=-3.5 EndZ=0
    g41: Circle [constr] CenterX=-4.03109 CenterY=-7 CenterZ=0 NormalX=0 NormalY=0 NormalZ=1 AngleXU=0 Radius=3.5
    g42: LineSegment StartX=4.03109 StartY=-3.5 StartZ=0 EndX=1 EndY=-5.25 EndZ=0
    g43: LineSegment StartX=1 StartY=-5.25 StartZ=0 EndX=1 EndY=-8.75 EndZ=0
    g44: LineSegment StartX=1 StartY=-8.75 StartZ=0 EndX=4.03109 EndY=-10.5 EndZ=0
    g45: LineSegment StartX=4.03109 StartY=-10.5 StartZ=0 EndX=7.06218 EndY=-8.75 EndZ=0
    g46: LineSegment StartX=7.06218 StartY=-8.75 StartZ=0 EndX=7.06218 EndY=-5.25 EndZ=0
    g47: LineSegment StartX=7.06218 StartY=-5.25 StartZ=0 EndX=4.03109 EndY=-3.5 EndZ=0
    g48: Circle [constr] CenterX=4.03109 CenterY=-7 CenterZ=0 NormalX=0 NormalY=0 NormalZ=1 AngleXU=0 Radius=3.5
  constraints (117):
    c: Coincident(g0,g1)
    c: Coincident(g1,g2)
    c: Coincident(g2,g3)
    c: Coincident(g3,g4)
    c: Coincident(g4,g5)
    c: Coincident(g5,g0)
    c: Equal(g0, g1-g5) x5
    c: PointOnObject(g0,g6)
    c: PointOnObject(g1,g6)
    c: PointOnObject(g2,g6)
    c: PointOnObject(g3,g6)
    c: PointOnObject(g4,g6)
    c: PointOnObject(g5,g6)
    c: Coincident(g6,g-1)
    c: Diameter(g6) = 7
    c: PointOnObject(g0,g-2)
    c: Coincident(g7,g8)
    c: Coincident(g8,g9)
    c: Coincident(g9,g10)
    c: Coincident(g10,g11)
    c: Coincident(g11,g12)
    c: Coincident(g12,g7)
    c: Equal(g7, g8-g12) x5
    c: PointOnObject(g7,g13)
    c: PointOnObject(g8,g13)
    c: PointOnObject(g9,g13)
    c: PointOnObject(g10,g13)
    c: PointOnObject(g11,g13)
    c: PointOnObject(g12,g13)
    c: PointOnObject(g13,g-1)
    c: Diameter(g13) = 7
    c: Distance(g6,g13) = 8
    c: Horizontal(g0,g10)
    c: Coincident(g14,g15)
    c: Coincident(g15,g16)
    c: Coincident(g16,g17)
    c: Coincident(g17,g18)
    c: Coincident(g18,g19)
    c: Coincident(g19,g14)
    c: Equal(g14, g15-g19) x5
    c: PointOnObject(g14,g20)
    c: PointOnObject(g15,g20)
    c: PointOnObject(g16,g20)
    c: PointOnObject(g17,g20)
    c: PointOnObject(g18,g20)
    c: PointOnObject(g19,g20)
    c: Diameter(g20) = 7
    c: DistanceY(g-1,g20) = 7
    c: Vertical(g18)
    c: Distance(g17,g-2) = 1
    c: Coincident(g21,g22)
    c: Coincident(g22,g23)
    c: Coincident(g23,g24)
    c: Coincident(g24,g25)
    c: Coincident(g25,g26)
    c: Coincident(g26,g21)
    c: Equal(g21, g22-g26) x5
    c: PointOnObject(g21,g27)
    c: PointOnObject(g22,g27)
    c: PointOnObject(g23,g27)
    c: PointOnObject(g24,g27)
    c: PointOnObject(g25,g27)
    c: PointOnObject(g26,g27)
    c: Diameter(g27) = 7
    c: DistanceY(g-1,g27) = 7
    c: DistanceX(g21,g-1) = 1
    c: Vertical(g21)
    c: Coincident(g28,g29)
    c: Coincident(g29,g30)
    c: Coincident(g30,g31)
    c: Coincident(g31,g32)
    c: Coincident(g32,g33)
    c: Coincident(g33,g28)
    c: Equal(g28, g29-g33) x5
    c: PointOnObject(g28,g34)
    c: PointOnObject(g29,g34)
    c: PointOnObject(g30,g34)
    c: PointOnObject(g31,g34)
    c: PointOnObject(g32,g34)
    c: PointOnObject(g33,g34)
    c: PointOnObject(g34,g-1)
    c: Diameter(g34) = 7
    c: Vertical(g31)
    c: DistanceX(g34,g-1) = 8
    c: Coincident(g35,g36)
    c: Coincident(g36,g37)
    c: Coincident(g37,g38)
    c: Coincident(g38,g39)
    c: Coincident(g39,g40)
    c: Coincident(g40,g35)
    c: Equal(g35, g36-g40) x5
    c: PointOnObject(g35,g41)
    c: PointOnObject(g36,g41)
    c: PointOnObject(g37,g41)
    c: PointOnObject(g38,g41)
    c: PointOnObject(g39,g41)
    c: PointOnObject(g40,g41)
    c: Coincident(g42,g43)
    c: Coincident(g43,g44)
    c: Coincident(g44,g45)
    c: Coincident(g45,g46)
    c: Coincident(g46,g47)
    c: Coincident(g47,g42)
    c: Equal(g42, g43-g47) x5
    c: PointOnObject(g42,g48)
    c: PointOnObject(g43,g48)
    c: PointOnObject(g44,g48)
    c: PointOnObject(g45,g48)
    c: PointOnObject(g46,g48)
    c: PointOnObject(g47,g48)
    c: Equal(g41,g48)
    c: Diameter(g41) = 7
    c: Vertical(g39)
    c: Vertical(g43)
    c: Distance(g-2,g39) = 1
    c: Symmetric(g38,g43,g-2)
    c: Distance(g41,g-1) = 7
FEATURE [Part::Extrusion] Extrude692  label="hex294"
  Base = -> Sketch701
  Dir = (0,-1,2e-16)
  DirMode = 2
  FaceMakerClass = Part::FaceMakerBullseye
  FaceMakerMode = 3
  LengthFwd = 10
  LengthRev = 0
  Placement = pos=(-104,0,0) rot=(0,0,1;0rad)
  Solid = true
  Symmetric = false
FEATURE [Sketcher::SketchObject] Sketch702
  ArcFitTolerance = 1e-06
  FullyConstrained = true
  MakeInternals = false
  Placement = pos=(0,0,0) rot=(1,0,0;1.5708rad)
  sketch-geometry (49):
    g0: LineSegment StartX=1e-16 StartY=3.5 StartZ=0 EndX=-3.03109 EndY=1.75 EndZ=0
    g1: LineSegment StartX=-3.03109 StartY=1.75 StartZ=0 EndX=-3.03109 EndY=-1.75 EndZ=0
    g2: LineSegment StartX=-3.03109 StartY=-1.75 StartZ=0 EndX=-1e-16 EndY=-3.5 EndZ=0
    g3: LineSegment StartX=-1e-16 StartY=-3.5 StartZ=0 EndX=3.03109 EndY=-1.75 EndZ=0
    g4: LineSegment StartX=3.03109 StartY=-1.75 StartZ=0 EndX=3.03109 EndY=1.75 EndZ=0
    g5: LineSegment StartX=3.03109 StartY=1.75 StartZ=0 EndX=1e-16 EndY=3.5 EndZ=0
    g6: Circle [constr] CenterX=0 CenterY=0 CenterZ=0 NormalX=0 NormalY=0 NormalZ=1 AngleXU=0 Radius=3.5
    g7: LineSegment StartX=4.96892 StartY=-1.75002 StartZ=0 EndX=8.00002 EndY=-3.5 EndZ=0
    g8: LineSegment StartX=8.00002 StartY=-3.5 StartZ=0 EndX=11.0311 EndY=-1.74998 EndZ=0
    g9: LineSegment StartX=11.0311 StartY=-1.74998 StartZ=0 EndX=11.0311 EndY=1.75002 EndZ=0
    g10: LineSegment StartX=11.0311 StartY=1.75002 StartZ=0 EndX=7.99998 EndY=3.5 EndZ=0
    g11: LineSegment StartX=7.99998 StartY=3.5 StartZ=0 EndX=4.9689 EndY=1.74998 EndZ=0
    g12: LineSegment StartX=4.9689 StartY=1.74998 StartZ=0 EndX=4.96892 EndY=-1.75002 EndZ=0
    g13: Circle [constr] CenterX=8 CenterY=0 CenterZ=0 NormalX=0 NormalY=0 NormalZ=1 AngleXU=0 Radius=3.5
    g14: LineSegment StartX=4.03109 StartY=3.5 StartZ=0 EndX=7.06218 EndY=5.25 EndZ=0
    g15: LineSegment StartX=7.06218 StartY=5.25 StartZ=0 EndX=7.06218 EndY=8.75 EndZ=0
    g16: LineSegment StartX=7.06218 StartY=8.75 StartZ=0 EndX=4.03109 EndY=10.5 EndZ=0
    g17: LineSegment StartX=4.03109 StartY=10.5 StartZ=0 EndX=1 EndY=8.75 EndZ=0
    g18: LineSegment StartX=1 StartY=8.75 StartZ=0 EndX=1 EndY=5.25 EndZ=0
    g19: LineSegment StartX=1 StartY=5.25 StartZ=0 EndX=4.03109 EndY=3.5 EndZ=0
    g20: Circle [constr] CenterX=4.03109 CenterY=7 CenterZ=0 NormalX=0 NormalY=0 NormalZ=1 AngleXU=0 Radius=3.5
    g21: LineSegment StartX=-1 StartY=5.25 StartZ=0 EndX=-1 EndY=8.75 EndZ=0
    g22: LineSegment StartX=-1 StartY=8.75 StartZ=0 EndX=-4.03109 EndY=10.5 EndZ=0
    g23: LineSegment StartX=-4.03109 StartY=10.5 StartZ=0 EndX=-7.06218 EndY=8.75 EndZ=0
    g24: LineSegment StartX=-7.06218 StartY=8.75 StartZ=0 EndX=-7.06218 EndY=5.25 EndZ=0
    g25: LineSegment StartX=-7.06218 StartY=5.25 StartZ=0 EndX=-4.03109 EndY=3.5 EndZ=0
    g26: LineSegment StartX=-4.03109 StartY=3.5 StartZ=0 EndX=-1 EndY=5.25 EndZ=0
    g27: Circle [constr] CenterX=-4.03109 CenterY=7 CenterZ=0 NormalX=0 NormalY=0 NormalZ=1 AngleXU=0 Radius=3.5
    g28: LineSegment StartX=-4.96891 StartY=-1.75 StartZ=0 EndX=-4.96891 EndY=1.75 EndZ=0
    g29: LineSegment StartX=-4.96891 StartY=1.75 StartZ=0 EndX=-8 EndY=3.5 EndZ=0
    g30: LineSegment StartX=-8 StartY=3.5 StartZ=0 EndX=-11.0311 EndY=1.75 EndZ=0
    g31: LineSegment StartX=-11.0311 StartY=1.75 StartZ=0 EndX=-11.0311 EndY=-1.75 EndZ=0
    g32: LineSegment StartX=-11.0311 StartY=-1.75 StartZ=0 EndX=-8 EndY=-3.5 EndZ=0
    g33: LineSegment StartX=-8 StartY=-3.5 StartZ=0 EndX=-4.96891 EndY=-1.75 EndZ=0
    g34: Circle [constr] CenterX=-8 CenterY=0 CenterZ=0 NormalX=0 NormalY=0 NormalZ=1 AngleXU=0 Radius=3.5
    g35: LineSegment StartX=-4.03109 StartY=-3.5 StartZ=0 EndX=-7.06218 EndY=-5.25 EndZ=0
    g36: LineSegment StartX=-7.06218 StartY=-5.25 StartZ=0 EndX=-7.06218 EndY=-8.75 EndZ=0
    g37: LineSegment StartX=-7.06218 StartY=-8.75 StartZ=0 EndX=-4.03109 EndY=-10.5 EndZ=0
    g38: LineSegment StartX=-4.03109 StartY=-10.5 StartZ=0 EndX=-1 EndY=-8.75 EndZ=0
    g39: LineSegment StartX=-1 StartY=-8.75 StartZ=0 EndX=-1 EndY=-5.25 EndZ=0
    g40: LineSegment StartX=-1 StartY=-5.25 StartZ=0 EndX=-4.03109 EndY=-3.5 EndZ=0
    g41: Circle [constr] CenterX=-4.03109 CenterY=-7 CenterZ=0 NormalX=0 NormalY=0 NormalZ=1 AngleXU=0 Radius=3.5
    g42: LineSegment StartX=4.03109 StartY=-3.5 StartZ=0 EndX=1 EndY=-5.25 EndZ=0
    g43: LineSegment StartX=1 StartY=-5.25 StartZ=0 EndX=1 EndY=-8.75 EndZ=0
    g44: LineSegment StartX=1 StartY=-8.75 StartZ=0 EndX=4.03109 EndY=-10.5 EndZ=0
    g45: LineSegment StartX=4.03109 StartY=-10.5 StartZ=0 EndX=7.06218 EndY=-8.75 EndZ=0
    g46: LineSegment StartX=7.06218 StartY=-8.75 StartZ=0 EndX=7.06218 EndY=-5.25 EndZ=0
    g47: LineSegment StartX=7.06218 StartY=-5.25 StartZ=0 EndX=4.03109 EndY=-3.5 EndZ=0
    g48: Circle [constr] CenterX=4.03109 CenterY=-7 CenterZ=0 NormalX=0 NormalY=0 NormalZ=1 AngleXU=0 Radius=3.5
  constraints (117):
    c: Coincident(g0,g1)
    c: Coincident(g1,g2)
    c: Coincident(g2,g3)
    c: Coincident(g3,g4)
    c: Coincident(g4,g5)
    c: Coincident(g5,g0)
    c: Equal(g0, g1-g5) x5
    c: PointOnObject(g0,g6)
    c: PointOnObject(g1,g6)
    c: PointOnObject(g2,g6)
    c: PointOnObject(g3,g6)
    c: PointOnObject(g4,g6)
    c: PointOnObject(g5,g6)
    c: Coincident(g6,g-1)
    c: Diameter(g6) = 7
    c: PointOnObject(g0,g-2)
    c: Coincident(g7,g8)
    c: Coincident(g8,g9)
    c: Coincident(g9,g10)
    c: Coincident(g10,g11)
    c: Coincident(g11,g12)
    c: Coincident(g12,g7)
    c: Equal(g7, g8-g12) x5
    c: PointOnObject(g7,g13)
    c: PointOnObject(g8,g13)
    c: PointOnObject(g9,g13)
    c: PointOnObject(g10,g13)
    c: PointOnObject(g11,g13)
    c: PointOnObject(g12,g13)
    c: PointOnObject(g13,g-1)
    c: Diameter(g13) = 7
    c: Distance(g6,g13) = 8
    c: Horizontal(g0,g10)
    c: Coincident(g14,g15)
    c: Coincident(g15,g16)
    c: Coincident(g16,g17)
    c: Coincident(g17,g18)
    c: Coincident(g18,g19)
    c: Coincident(g19,g14)
    c: Equal(g14, g15-g19) x5
    c: PointOnObject(g14,g20)
    c: PointOnObject(g15,g20)
    c: PointOnObject(g16,g20)
    c: PointOnObject(g17,g20)
    c: PointOnObject(g18,g20)
    c: PointOnObject(g19,g20)
    c: Diameter(g20) = 7
    c: DistanceY(g-1,g20) = 7
    c: Vertical(g18)
    c: Distance(g17,g-2) = 1
    c: Coincident(g21,g22)
    c: Coincident(g22,g23)
    c: Coincident(g23,g24)
    c: Coincident(g24,g25)
    c: Coincident(g25,g26)
    c: Coincident(g26,g21)
    c: Equal(g21, g22-g26) x5
    c: PointOnObject(g21,g27)
    c: PointOnObject(g22,g27)
    c: PointOnObject(g23,g27)
    c: PointOnObject(g24,g27)
    c: PointOnObject(g25,g27)
    c: PointOnObject(g26,g27)
    c: Diameter(g27) = 7
    c: DistanceY(g-1,g27) = 7
    c: DistanceX(g21,g-1) = 1
    c: Vertical(g21)
    c: Coincident(g28,g29)
    c: Coincident(g29,g30)
    c: Coincident(g30,g31)
    c: Coincident(g31,g32)
    c: Coincident(g32,g33)
    c: Coincident(g33,g28)
    c: Equal(g28, g29-g33) x5
    c: PointOnObject(g28,g34)
    c: PointOnObject(g29,g34)
    c: PointOnObject(g30,g34)
    c: PointOnObject(g31,g34)
    c: PointOnObject(g32,g34)
    c: PointOnObject(g33,g34)
    c: PointOnObject(g34,g-1)
    c: Diameter(g34) = 7
    c: Vertical(g31)
    c: DistanceX(g34,g-1) = 8
    c: Coincident(g35,g36)
    c: Coincident(g36,g37)
    c: Coincident(g37,g38)
    c: Coincident(g38,g39)
    c: Coincident(g39,g40)
    c: Coincident(g40,g35)
    c: Equal(g35, g36-g40) x5
    c: PointOnObject(g35,g41)
    c: PointOnObject(g36,g41)
    c: PointOnObject(g37,g41)
    c: PointOnObject(g38,g41)
    c: PointOnObject(g39,g41)
    c: PointOnObject(g40,g41)
    c: Coincident(g42,g43)
    c: Coincident(g43,g44)
    c: Coincident(g44,g45)
    c: Coincident(g45,g46)
    c: Coincident(g46,g47)
    c: Coincident(g47,g42)
    c: Equal(g42, g43-g47) x5
    c: PointOnObject(g42,g48)
    c: PointOnObject(g43,g48)
    c: PointOnObject(g44,g48)
    c: PointOnObject(g45,g48)
    c: PointOnObject(g46,g48)
    c: PointOnObject(g47,g48)
    c: Equal(g41,g48)
    c: Diameter(g41) = 7
    c: Vertical(g39)
    c: Vertical(g43)
    c: Distance(g-2,g39) = 1
    c: Symmetric(g38,g43,g-2)
    c: Distance(g41,g-1) = 7
FEATURE [Part::Extrusion] Extrude693  label="hex295"
  Base = -> Sketch702
  Dir = (0,-1,2e-16)
  DirMode = 2
  FaceMakerClass = Part::FaceMakerBullseye
  FaceMakerMode = 3
  LengthFwd = 10
  LengthRev = 0
  Placement = pos=(-64,0,14) rot=(0,0,1;0rad)
  Solid = true
  Symmetric = false
FEATURE [Sketcher::SketchObject] Sketch703
  ArcFitTolerance = 1e-06
  FullyConstrained = true
  MakeInternals = false
  Placement = pos=(0,0,0) rot=(1,0,0;1.5708rad)
  sketch-geometry (49):
    g0: LineSegment StartX=1e-16 StartY=3.5 StartZ=0 EndX=-3.03109 EndY=1.75 EndZ=0
    g1: LineSegment StartX=-3.03109 StartY=1.75 StartZ=0 EndX=-3.03109 EndY=-1.75 EndZ=0
    g2: LineSegment StartX=-3.03109 StartY=-1.75 StartZ=0 EndX=-1e-16 EndY=-3.5 EndZ=0
    g3: LineSegment StartX=-1e-16 StartY=-3.5 StartZ=0 EndX=3.03109 EndY=-1.75 EndZ=0
    g4: LineSegment StartX=3.03109 StartY=-1.75 StartZ=0 EndX=3.03109 EndY=1.75 EndZ=0
    g5: LineSegment StartX=3.03109 StartY=1.75 StartZ=0 EndX=1e-16 EndY=3.5 EndZ=0
    g6: Circle [constr] CenterX=0 CenterY=0 CenterZ=0 NormalX=0 NormalY=0 NormalZ=1 AngleXU=0 Radius=3.5
    g7: LineSegment StartX=4.96892 StartY=-1.75002 StartZ=0 EndX=8.00002 EndY=-3.5 EndZ=0
    g8: LineSegment StartX=8.00002 StartY=-3.5 StartZ=0 EndX=11.0311 EndY=-1.74998 EndZ=0
    g9: LineSegment StartX=11.0311 StartY=-1.74998 StartZ=0 EndX=11.0311 EndY=1.75002 EndZ=0
    g10: LineSegment StartX=11.0311 StartY=1.75002 StartZ=0 EndX=7.99998 EndY=3.5 EndZ=0
    g11: LineSegment StartX=7.99998 StartY=3.5 StartZ=0 EndX=4.9689 EndY=1.74998 EndZ=0
    g12: LineSegment StartX=4.9689 StartY=1.74998 StartZ=0 EndX=4.96892 EndY=-1.75002 EndZ=0
    g13: Circle [constr] CenterX=8 CenterY=0 CenterZ=0 NormalX=0 NormalY=0 NormalZ=1 AngleXU=0 Radius=3.5
    g14: LineSegment StartX=4.03109 StartY=3.5 StartZ=0 EndX=7.06218 EndY=5.25 EndZ=0
    g15: LineSegment StartX=7.06218 StartY=5.25 StartZ=0 EndX=7.06218 EndY=8.75 EndZ=0
    g16: LineSegment StartX=7.06218 StartY=8.75 StartZ=0 EndX=4.03109 EndY=10.5 EndZ=0
    g17: LineSegment StartX=4.03109 StartY=10.5 StartZ=0 EndX=1 EndY=8.75 EndZ=0
    g18: LineSegment StartX=1 StartY=8.75 StartZ=0 EndX=1 EndY=5.25 EndZ=0
    g19: LineSegment StartX=1 StartY=5.25 StartZ=0 EndX=4.03109 EndY=3.5 EndZ=0
    g20: Circle [constr] CenterX=4.03109 CenterY=7 CenterZ=0 NormalX=0 NormalY=0 NormalZ=1 AngleXU=0 Radius=3.5
    g21: LineSegment StartX=-1 StartY=5.25 StartZ=0 EndX=-1 EndY=8.75 EndZ=0
    g22: LineSegment StartX=-1 StartY=8.75 StartZ=0 EndX=-4.03109 EndY=10.5 EndZ=0
    g23: LineSegment StartX=-4.03109 StartY=10.5 StartZ=0 EndX=-7.06218 EndY=8.75 EndZ=0
    g24: LineSegment StartX=-7.06218 StartY=8.75 StartZ=0 EndX=-7.06218 EndY=5.25 EndZ=0
    g25: LineSegment StartX=-7.06218 StartY=5.25 StartZ=0 EndX=-4.03109 EndY=3.5 EndZ=0
    g26: LineSegment StartX=-4.03109 StartY=3.5 StartZ=0 EndX=-1 EndY=5.25 EndZ=0
    g27: Circle [constr] CenterX=-4.03109 CenterY=7 CenterZ=0 NormalX=0 NormalY=0 NormalZ=1 AngleXU=0 Radius=3.5
    g28: LineSegment StartX=-4.96891 StartY=-1.75 StartZ=0 EndX=-4.96891 EndY=1.75 EndZ=0
    g29: LineSegment StartX=-4.96891 StartY=1.75 StartZ=0 EndX=-8 EndY=3.5 EndZ=0
    g30: LineSegment StartX=-8 StartY=3.5 StartZ=0 EndX=-11.0311 EndY=1.75 EndZ=0
    g31: LineSegment StartX=-11.0311 StartY=1.75 StartZ=0 EndX=-11.0311 EndY=-1.75 EndZ=0
    g32: LineSegment StartX=-11.0311 StartY=-1.75 StartZ=0 EndX=-8 EndY=-3.5 EndZ=0
    g33: LineSegment StartX=-8 StartY=-3.5 StartZ=0 EndX=-4.96891 EndY=-1.75 EndZ=0
    g34: Circle [constr] CenterX=-8 CenterY=0 CenterZ=0 NormalX=0 NormalY=0 NormalZ=1 AngleXU=0 Radius=3.5
    g35: LineSegment StartX=-4.03109 StartY=-3.5 StartZ=0 EndX=-7.06218 EndY=-5.25 EndZ=0
    g36: LineSegment StartX=-7.06218 StartY=-5.25 StartZ=0 EndX=-7.06218 EndY=-8.75 EndZ=0
    g37: LineSegment StartX=-7.06218 StartY=-8.75 StartZ=0 EndX=-4.03109 EndY=-10.5 EndZ=0
    g38: LineSegment StartX=-4.03109 StartY=-10.5 StartZ=0 EndX=-1 EndY=-8.75 EndZ=0
    g39: LineSegment StartX=-1 StartY=-8.75 StartZ=0 EndX=-1 EndY=-5.25 EndZ=0
    g40: LineSegment StartX=-1 StartY=-5.25 StartZ=0 EndX=-4.03109 EndY=-3.5 EndZ=0
    g41: Circle [constr] CenterX=-4.03109 CenterY=-7 CenterZ=0 NormalX=0 NormalY=0 NormalZ=1 AngleXU=0 Radius=3.5
    g42: LineSegment StartX=4.03109 StartY=-3.5 StartZ=0 EndX=1 EndY=-5.25 EndZ=0
    g43: LineSegment StartX=1 StartY=-5.25 StartZ=0 EndX=1 EndY=-8.75 EndZ=0
    g44: LineSegment StartX=1 StartY=-8.75 StartZ=0 EndX=4.03109 EndY=-10.5 EndZ=0
    g45: LineSegment StartX=4.03109 StartY=-10.5 StartZ=0 EndX=7.06218 EndY=-8.75 EndZ=0
    g46: LineSegment StartX=7.06218 StartY=-8.75 StartZ=0 EndX=7.06218 EndY=-5.25 EndZ=0
    g47: LineSegment StartX=7.06218 StartY=-5.25 StartZ=0 EndX=4.03109 EndY=-3.5 EndZ=0
    g48: Circle [constr] CenterX=4.03109 CenterY=-7 CenterZ=0 NormalX=0 NormalY=0 NormalZ=1 AngleXU=0 Radius=3.5
  constraints (117):
    c: Coincident(g0,g1)
    c: Coincident(g1,g2)
    c: Coincident(g2,g3)
    c: Coincident(g3,g4)
    c: Coincident(g4,g5)
    c: Coincident(g5,g0)
    c: Equal(g0, g1-g5) x5
    c: PointOnObject(g0,g6)
    c: PointOnObject(g1,g6)
    c: PointOnObject(g2,g6)
    c: PointOnObject(g3,g6)
    c: PointOnObject(g4,g6)
    c: PointOnObject(g5,g6)
    c: Coincident(g6,g-1)
    c: Diameter(g6) = 7
    c: PointOnObject(g0,g-2)
    c: Coincident(g7,g8)
    c: Coincident(g8,g9)
    c: Coincident(g9,g10)
    c: Coincident(g10,g11)
    c: Coincident(g11,g12)
    c: Coincident(g12,g7)
    c: Equal(g7, g8-g12) x5
    c: PointOnObject(g7,g13)
    c: PointOnObject(g8,g13)
    c: PointOnObject(g9,g13)
    c: PointOnObject(g10,g13)
    c: PointOnObject(g11,g13)
    c: PointOnObject(g12,g13)
    c: PointOnObject(g13,g-1)
    c: Diameter(g13) = 7
    c: Distance(g6,g13) = 8
    c: Horizontal(g0,g10)
    c: Coincident(g14,g15)
    c: Coincident(g15,g16)
    c: Coincident(g16,g17)
    c: Coincident(g17,g18)
    c: Coincident(g18,g19)
    c: Coincident(g19,g14)
    c: Equal(g14, g15-g19) x5
    c: PointOnObject(g14,g20)
    c: PointOnObject(g15,g20)
    c: PointOnObject(g16,g20)
    c: PointOnObject(g17,g20)
    c: PointOnObject(g18,g20)
    c: PointOnObject(g19,g20)
    c: Diameter(g20) = 7
    c: DistanceY(g-1,g20) = 7
    c: Vertical(g18)
    c: Distance(g17,g-2) = 1
    c: Coincident(g21,g22)
    c: Coincident(g22,g23)
    c: Coincident(g23,g24)
    c: Coincident(g24,g25)
    c: Coincident(g25,g26)
    c: Coincident(g26,g21)
    c: Equal(g21, g22-g26) x5
    c: PointOnObject(g21,g27)
    c: PointOnObject(g22,g27)
    c: PointOnObject(g23,g27)
    c: PointOnObject(g24,g27)
    c: PointOnObject(g25,g27)
    c: PointOnObject(g26,g27)
    c: Diameter(g27) = 7
    c: DistanceY(g-1,g27) = 7
    c: DistanceX(g21,g-1) = 1
    c: Vertical(g21)
    c: Coincident(g28,g29)
    c: Coincident(g29,g30)
    c: Coincident(g30,g31)
    c: Coincident(g31,g32)
    c: Coincident(g32,g33)
    c: Coincident(g33,g28)
    c: Equal(g28, g29-g33) x5
    c: PointOnObject(g28,g34)
    c: PointOnObject(g29,g34)
    c: PointOnObject(g30,g34)
    c: PointOnObject(g31,g34)
    c: PointOnObject(g32,g34)
    c: PointOnObject(g33,g34)
    c: PointOnObject(g34,g-1)
    c: Diameter(g34) = 7
    c: Vertical(g31)
    c: DistanceX(g34,g-1) = 8
    c: Coincident(g35,g36)
    c: Coincident(g36,g37)
    c: Coincident(g37,g38)
    c: Coincident(g38,g39)
    c: Coincident(g39,g40)
    c: Coincident(g40,g35)
    c: Equal(g35, g36-g40) x5
    c: PointOnObject(g35,g41)
    c: PointOnObject(g36,g41)
    c: PointOnObject(g37,g41)
    c: PointOnObject(g38,g41)
    c: PointOnObject(g39,g41)
    c: PointOnObject(g40,g41)
    c: Coincident(g42,g43)
    c: Coincident(g43,g44)
    c: Coincident(g44,g45)
    c: Coincident(g45,g46)
    c: Coincident(g46,g47)
    c: Coincident(g47,g42)
    c: Equal(g42, g43-g47) x5
    c: PointOnObject(g42,g48)
    c: PointOnObject(g43,g48)
    c: PointOnObject(g44,g48)
    c: PointOnObject(g45,g48)
    c: PointOnObject(g46,g48)
    c: PointOnObject(g47,g48)
    c: Equal(g41,g48)
    c: Diameter(g41) = 7
    c: Vertical(g39)
    c: Vertical(g43)
    c: Distance(g-2,g39) = 1
    c: Symmetric(g38,g43,g-2)
    c: Distance(g41,g-1) = 7
FEATURE [Part::Extrusion] Extrude694  label="hex296"
  Base = -> Sketch703
  Dir = (0,-1,2e-16)
  DirMode = 2
  FaceMakerClass = Part::FaceMakerBullseye
  FaceMakerMode = 3
  LengthFwd = 10
  LengthRev = 0
  Placement = pos=(-64,0,-14) rot=(0,0,1;0rad)
  Solid = true
  Symmetric = false
FEATURE [Sketcher::SketchObject] Sketch704
  ArcFitTolerance = 1e-06
  FullyConstrained = true
  MakeInternals = false
  Placement = pos=(0,0,0) rot=(1,0,0;1.5708rad)
  sketch-geometry (49):
    g0: LineSegment StartX=1e-16 StartY=3.5 StartZ=0 EndX=-3.03109 EndY=1.75 EndZ=0
    g1: LineSegment StartX=-3.03109 StartY=1.75 StartZ=0 EndX=-3.03109 EndY=-1.75 EndZ=0
    g2: LineSegment StartX=-3.03109 StartY=-1.75 StartZ=0 EndX=-1e-16 EndY=-3.5 EndZ=0
    g3: LineSegment StartX=-1e-16 StartY=-3.5 StartZ=0 EndX=3.03109 EndY=-1.75 EndZ=0
    g4: LineSegment StartX=3.03109 StartY=-1.75 StartZ=0 EndX=3.03109 EndY=1.75 EndZ=0
    g5: LineSegment StartX=3.03109 StartY=1.75 StartZ=0 EndX=1e-16 EndY=3.5 EndZ=0
    g6: Circle [constr] CenterX=0 CenterY=0 CenterZ=0 NormalX=0 NormalY=0 NormalZ=1 AngleXU=0 Radius=3.5
    g7: LineSegment StartX=4.96892 StartY=-1.75002 StartZ=0 EndX=8.00002 EndY=-3.5 EndZ=0
    g8: LineSegment StartX=8.00002 StartY=-3.5 StartZ=0 EndX=11.0311 EndY=-1.74998 EndZ=0
    g9: LineSegment StartX=11.0311 StartY=-1.74998 StartZ=0 EndX=11.0311 EndY=1.75002 EndZ=0
    g10: LineSegment StartX=11.0311 StartY=1.75002 StartZ=0 EndX=7.99998 EndY=3.5 EndZ=0
    g11: LineSegment StartX=7.99998 StartY=3.5 StartZ=0 EndX=4.9689 EndY=1.74998 EndZ=0
    g12: LineSegment StartX=4.9689 StartY=1.74998 StartZ=0 EndX=4.96892 EndY=-1.75002 EndZ=0
    g13: Circle [constr] CenterX=8 CenterY=0 CenterZ=0 NormalX=0 NormalY=0 NormalZ=1 AngleXU=0 Radius=3.5
    g14: LineSegment StartX=4.03109 StartY=3.5 StartZ=0 EndX=7.06218 EndY=5.25 EndZ=0
    g15: LineSegment StartX=7.06218 StartY=5.25 StartZ=0 EndX=7.06218 EndY=8.75 EndZ=0
    g16: LineSegment StartX=7.06218 StartY=8.75 StartZ=0 EndX=4.03109 EndY=10.5 EndZ=0
    g17: LineSegment StartX=4.03109 StartY=10.5 StartZ=0 EndX=1 EndY=8.75 EndZ=0
    g18: LineSegment StartX=1 StartY=8.75 StartZ=0 EndX=1 EndY=5.25 EndZ=0
    g19: LineSegment StartX=1 StartY=5.25 StartZ=0 EndX=4.03109 EndY=3.5 EndZ=0
    g20: Circle [constr] CenterX=4.03109 CenterY=7 CenterZ=0 NormalX=0 NormalY=0 NormalZ=1 AngleXU=0 Radius=3.5
    g21: LineSegment StartX=-1 StartY=5.25 StartZ=0 EndX=-1 EndY=8.75 EndZ=0
    g22: LineSegment StartX=-1 StartY=8.75 StartZ=0 EndX=-4.03109 EndY=10.5 EndZ=0
    g23: LineSegment StartX=-4.03109 StartY=10.5 StartZ=0 EndX=-7.06218 EndY=8.75 EndZ=0
    g24: LineSegment StartX=-7.06218 StartY=8.75 StartZ=0 EndX=-7.06218 EndY=5.25 EndZ=0
    g25: LineSegment StartX=-7.06218 StartY=5.25 StartZ=0 EndX=-4.03109 EndY=3.5 EndZ=0
    g26: LineSegment StartX=-4.03109 StartY=3.5 StartZ=0 EndX=-1 EndY=5.25 EndZ=0
    g27: Circle [constr] CenterX=-4.03109 CenterY=7 CenterZ=0 NormalX=0 NormalY=0 NormalZ=1 AngleXU=0 Radius=3.5
    g28: LineSegment StartX=-4.96891 StartY=-1.75 StartZ=0 EndX=-4.96891 EndY=1.75 EndZ=0
    g29: LineSegment StartX=-4.96891 StartY=1.75 StartZ=0 EndX=-8 EndY=3.5 EndZ=0
    g30: LineSegment StartX=-8 StartY=3.5 StartZ=0 EndX=-11.0311 EndY=1.75 EndZ=0
    g31: LineSegment StartX=-11.0311 StartY=1.75 StartZ=0 EndX=-11.0311 EndY=-1.75 EndZ=0
    g32: LineSegment StartX=-11.0311 StartY=-1.75 StartZ=0 EndX=-8 EndY=-3.5 EndZ=0
    g33: LineSegment StartX=-8 StartY=-3.5 StartZ=0 EndX=-4.96891 EndY=-1.75 EndZ=0
    g34: Circle [constr] CenterX=-8 CenterY=0 CenterZ=0 NormalX=0 NormalY=0 NormalZ=1 AngleXU=0 Radius=3.5
    g35: LineSegment StartX=-4.03109 StartY=-3.5 StartZ=0 EndX=-7.06218 EndY=-5.25 EndZ=0
    g36: LineSegment StartX=-7.06218 StartY=-5.25 StartZ=0 EndX=-7.06218 EndY=-8.75 EndZ=0
    g37: LineSegment StartX=-7.06218 StartY=-8.75 StartZ=0 EndX=-4.03109 EndY=-10.5 EndZ=0
    g38: LineSegment StartX=-4.03109 StartY=-10.5 StartZ=0 EndX=-1 EndY=-8.75 EndZ=0
    g39: LineSegment StartX=-1 StartY=-8.75 StartZ=0 EndX=-1 EndY=-5.25 EndZ=0
    g40: LineSegment StartX=-1 StartY=-5.25 StartZ=0 EndX=-4.03109 EndY=-3.5 EndZ=0
    g41: Circle [constr] CenterX=-4.03109 CenterY=-7 CenterZ=0 NormalX=0 NormalY=0 NormalZ=1 AngleXU=0 Radius=3.5
    g42: LineSegment StartX=4.03109 StartY=-3.5 StartZ=0 EndX=1 EndY=-5.25 EndZ=0
    g43: LineSegment StartX=1 StartY=-5.25 StartZ=0 EndX=1 EndY=-8.75 EndZ=0
    g44: LineSegment StartX=1 StartY=-8.75 StartZ=0 EndX=4.03109 EndY=-10.5 EndZ=0
    g45: LineSegment StartX=4.03109 StartY=-10.5 StartZ=0 EndX=7.06218 EndY=-8.75 EndZ=0
    g46: LineSegment StartX=7.06218 StartY=-8.75 StartZ=0 EndX=7.06218 EndY=-5.25 EndZ=0
    g47: LineSegment StartX=7.06218 StartY=-5.25 StartZ=0 EndX=4.03109 EndY=-3.5 EndZ=0
    g48: Circle [constr] CenterX=4.03109 CenterY=-7 CenterZ=0 NormalX=0 NormalY=0 NormalZ=1 AngleXU=0 Radius=3.5
  constraints (117):
    c: Coincident(g0,g1)
    c: Coincident(g1,g2)
    c: Coincident(g2,g3)
    c: Coincident(g3,g4)
    c: Coincident(g4,g5)
    c: Coincident(g5,g0)
    c: Equal(g0, g1-g5) x5
    c: PointOnObject(g0,g6)
    c: PointOnObject(g1,g6)
    c: PointOnObject(g2,g6)
    c: PointOnObject(g3,g6)
    c: PointOnObject(g4,g6)
    c: PointOnObject(g5,g6)
    c: Coincident(g6,g-1)
    c: Diameter(g6) = 7
    c: PointOnObject(g0,g-2)
    c: Coincident(g7,g8)
    c: Coincident(g8,g9)
    c: Coincident(g9,g10)
    c: Coincident(g10,g11)
    c: Coincident(g11,g12)
    c: Coincident(g12,g7)
    c: Equal(g7, g8-g12) x5
    c: PointOnObject(g7,g13)
    c: PointOnObject(g8,g13)
    c: PointOnObject(g9,g13)
    c: PointOnObject(g10,g13)
    c: PointOnObject(g11,g13)
    c: PointOnObject(g12,g13)
    c: PointOnObject(g13,g-1)
    c: Diameter(g13) = 7
    c: Distance(g6,g13) = 8
    c: Horizontal(g0,g10)
    c: Coincident(g14,g15)
    c: Coincident(g15,g16)
    c: Coincident(g16,g17)
    c: Coincident(g17,g18)
    c: Coincident(g18,g19)
    c: Coincident(g19,g14)
    c: Equal(g14, g15-g19) x5
    c: PointOnObject(g14,g20)
    c: PointOnObject(g15,g20)
    c: PointOnObject(g16,g20)
    c: PointOnObject(g17,g20)
    c: PointOnObject(g18,g20)
    c: PointOnObject(g19,g20)
    c: Diameter(g20) = 7
    c: DistanceY(g-1,g20) = 7
    c: Vertical(g18)
    c: Distance(g17,g-2) = 1
    c: Coincident(g21,g22)
    c: Coincident(g22,g23)
    c: Coincident(g23,g24)
    c: Coincident(g24,g25)
    c: Coincident(g25,g26)
    c: Coincident(g26,g21)
    c: Equal(g21, g22-g26) x5
    c: PointOnObject(g21,g27)
    c: PointOnObject(g22,g27)
    c: PointOnObject(g23,g27)
    c: PointOnObject(g24,g27)
    c: PointOnObject(g25,g27)
    c: PointOnObject(g26,g27)
    c: Diameter(g27) = 7
    c: DistanceY(g-1,g27) = 7
    c: DistanceX(g21,g-1) = 1
    c: Vertical(g21)
    c: Coincident(g28,g29)
    c: Coincident(g29,g30)
    c: Coincident(g30,g31)
    c: Coincident(g31,g32)
    c: Coincident(g32,g33)
    c: Coincident(g33,g28)
    c: Equal(g28, g29-g33) x5
    c: PointOnObject(g28,g34)
    c: PointOnObject(g29,g34)
    c: PointOnObject(g30,g34)
    c: PointOnObject(g31,g34)
    c: PointOnObject(g32,g34)
    c: PointOnObject(g33,g34)
    c: PointOnObject(g34,g-1)
    c: Diameter(g34) = 7
    c: Vertical(g31)
    c: DistanceX(g34,g-1) = 8
    c: Coincident(g35,g36)
    c: Coincident(g36,g37)
    c: Coincident(g37,g38)
    c: Coincident(g38,g39)
    c: Coincident(g39,g40)
    c: Coincident(g40,g35)
    c: Equal(g35, g36-g40) x5
    c: PointOnObject(g35,g41)
    c: PointOnObject(g36,g41)
    c: PointOnObject(g37,g41)
    c: PointOnObject(g38,g41)
    c: PointOnObject(g39,g41)
    c: PointOnObject(g40,g41)
    c: Coincident(g42,g43)
    c: Coincident(g43,g44)
    c: Coincident(g44,g45)
    c: Coincident(g45,g46)
    c: Coincident(g46,g47)
    c: Coincident(g47,g42)
    c: Equal(g42, g43-g47) x5
    c: PointOnObject(g42,g48)
    c: PointOnObject(g43,g48)
    c: PointOnObject(g44,g48)
    c: PointOnObject(g45,g48)
    c: PointOnObject(g46,g48)
    c: PointOnObject(g47,g48)
    c: Equal(g41,g48)
    c: Diameter(g41) = 7
    c: Vertical(g39)
    c: Vertical(g43)
    c: Distance(g-2,g39) = 1
    c: Symmetric(g38,g43,g-2)
    c: Distance(g41,g-1) = 7
FEATURE [Part::Extrusion] Extrude695  label="hex297"
  Base = -> Sketch704
  Dir = (0,-1,2e-16)
  DirMode = 2
  FaceMakerClass = Part::FaceMakerBullseye
  FaceMakerMode = 3
  LengthFwd = 10
  LengthRev = 0
  Placement = pos=(-48,0,-28) rot=(0,0,1;0rad)
  Solid = true
  Symmetric = false
FEATURE [Sketcher::SketchObject] Sketch705
  ArcFitTolerance = 1e-06
  FullyConstrained = true
  MakeInternals = false
  Placement = pos=(0,0,0) rot=(1,0,0;1.5708rad)
  sketch-geometry (49):
    g0: LineSegment StartX=1e-16 StartY=3.5 StartZ=0 EndX=-3.03109 EndY=1.75 EndZ=0
    g1: LineSegment StartX=-3.03109 StartY=1.75 StartZ=0 EndX=-3.03109 EndY=-1.75 EndZ=0
    g2: LineSegment StartX=-3.03109 StartY=-1.75 StartZ=0 EndX=-1e-16 EndY=-3.5 EndZ=0
    g3: LineSegment StartX=-1e-16 StartY=-3.5 StartZ=0 EndX=3.03109 EndY=-1.75 EndZ=0
    g4: LineSegment StartX=3.03109 StartY=-1.75 StartZ=0 EndX=3.03109 EndY=1.75 EndZ=0
    g5: LineSegment StartX=3.03109 StartY=1.75 StartZ=0 EndX=1e-16 EndY=3.5 EndZ=0
    g6: Circle [constr] CenterX=0 CenterY=0 CenterZ=0 NormalX=0 NormalY=0 NormalZ=1 AngleXU=0 Radius=3.5
    g7: LineSegment StartX=4.96892 StartY=-1.75002 StartZ=0 EndX=8.00002 EndY=-3.5 EndZ=0
    g8: LineSegment StartX=8.00002 StartY=-3.5 StartZ=0 EndX=11.0311 EndY=-1.74998 EndZ=0
    g9: LineSegment StartX=11.0311 StartY=-1.74998 StartZ=0 EndX=11.0311 EndY=1.75002 EndZ=0
    g10: LineSegment StartX=11.0311 StartY=1.75002 StartZ=0 EndX=7.99998 EndY=3.5 EndZ=0
    g11: LineSegment StartX=7.99998 StartY=3.5 StartZ=0 EndX=4.9689 EndY=1.74998 EndZ=0
    g12: LineSegment StartX=4.9689 StartY=1.74998 StartZ=0 EndX=4.96892 EndY=-1.75002 EndZ=0
    g13: Circle [constr] CenterX=8 CenterY=0 CenterZ=0 NormalX=0 NormalY=0 NormalZ=1 AngleXU=0 Radius=3.5
    g14: LineSegment StartX=4.03109 StartY=3.5 StartZ=0 EndX=7.06218 EndY=5.25 EndZ=0
    g15: LineSegment StartX=7.06218 StartY=5.25 StartZ=0 EndX=7.06218 EndY=8.75 EndZ=0
    g16: LineSegment StartX=7.06218 StartY=8.75 StartZ=0 EndX=4.03109 EndY=10.5 EndZ=0
    g17: LineSegment StartX=4.03109 StartY=10.5 StartZ=0 EndX=1 EndY=8.75 EndZ=0
    g18: LineSegment StartX=1 StartY=8.75 StartZ=0 EndX=1 EndY=5.25 EndZ=0
    g19: LineSegment StartX=1 StartY=5.25 StartZ=0 EndX=4.03109 EndY=3.5 EndZ=0
    g20: Circle [constr] CenterX=4.03109 CenterY=7 CenterZ=0 NormalX=0 NormalY=0 NormalZ=1 AngleXU=0 Radius=3.5
    g21: LineSegment StartX=-1 StartY=5.25 StartZ=0 EndX=-1 EndY=8.75 EndZ=0
    g22: LineSegment StartX=-1 StartY=8.75 StartZ=0 EndX=-4.03109 EndY=10.5 EndZ=0
    g23: LineSegment StartX=-4.03109 StartY=10.5 StartZ=0 EndX=-7.06218 EndY=8.75 EndZ=0
    g24: LineSegment StartX=-7.06218 StartY=8.75 StartZ=0 EndX=-7.06218 EndY=5.25 EndZ=0
    g25: LineSegment StartX=-7.06218 StartY=5.25 StartZ=0 EndX=-4.03109 EndY=3.5 EndZ=0
    g26: LineSegment StartX=-4.03109 StartY=3.5 StartZ=0 EndX=-1 EndY=5.25 EndZ=0
    g27: Circle [constr] CenterX=-4.03109 CenterY=7 CenterZ=0 NormalX=0 NormalY=0 NormalZ=1 AngleXU=0 Radius=3.5
    g28: LineSegment StartX=-4.96891 StartY=-1.75 StartZ=0 EndX=-4.96891 EndY=1.75 EndZ=0
    g29: LineSegment StartX=-4.96891 StartY=1.75 StartZ=0 EndX=-8 EndY=3.5 EndZ=0
    g30: LineSegment StartX=-8 StartY=3.5 StartZ=0 EndX=-11.0311 EndY=1.75 EndZ=0
    g31: LineSegment StartX=-11.0311 StartY=1.75 StartZ=0 EndX=-11.0311 EndY=-1.75 EndZ=0
    g32: LineSegment StartX=-11.0311 StartY=-1.75 StartZ=0 EndX=-8 EndY=-3.5 EndZ=0
    g33: LineSegment StartX=-8 StartY=-3.5 StartZ=0 EndX=-4.96891 EndY=-1.75 EndZ=0
    g34: Circle [constr] CenterX=-8 CenterY=0 CenterZ=0 NormalX=0 NormalY=0 NormalZ=1 AngleXU=0 Radius=3.5
    g35: LineSegment StartX=-4.03109 StartY=-3.5 StartZ=0 EndX=-7.06218 EndY=-5.25 EndZ=0
    g36: LineSegment StartX=-7.06218 StartY=-5.25 StartZ=0 EndX=-7.06218 EndY=-8.75 EndZ=0
    g37: LineSegment StartX=-7.06218 StartY=-8.75 StartZ=0 EndX=-4.03109 EndY=-10.5 EndZ=0
    g38: LineSegment StartX=-4.03109 StartY=-10.5 StartZ=0 EndX=-1 EndY=-8.75 EndZ=0
    g39: LineSegment StartX=-1 StartY=-8.75 StartZ=0 EndX=-1 EndY=-5.25 EndZ=0
    g40: LineSegment StartX=-1 StartY=-5.25 StartZ=0 EndX=-4.03109 EndY=-3.5 EndZ=0
    g41: Circle [constr] CenterX=-4.03109 CenterY=-7 CenterZ=0 NormalX=0 NormalY=0 NormalZ=1 AngleXU=0 Radius=3.5
    g42: LineSegment StartX=4.03109 StartY=-3.5 StartZ=0 EndX=1 EndY=-5.25 EndZ=0
    g43: LineSegment StartX=1 StartY=-5.25 StartZ=0 EndX=1 EndY=-8.75 EndZ=0
    g44: LineSegment StartX=1 StartY=-8.75 StartZ=0 EndX=4.03109 EndY=-10.5 EndZ=0
    g45: LineSegment StartX=4.03109 StartY=-10.5 StartZ=0 EndX=7.06218 EndY=-8.75 EndZ=0
    g46: LineSegment StartX=7.06218 StartY=-8.75 StartZ=0 EndX=7.06218 EndY=-5.25 EndZ=0
    g47: LineSegment StartX=7.06218 StartY=-5.25 StartZ=0 EndX=4.03109 EndY=-3.5 EndZ=0
    g48: Circle [constr] CenterX=4.03109 CenterY=-7 CenterZ=0 NormalX=0 NormalY=0 NormalZ=1 AngleXU=0 Radius=3.5
  constraints (117):
    c: Coincident(g0,g1)
    c: Coincident(g1,g2)
    c: Coincident(g2,g3)
    c: Coincident(g3,g4)
    c: Coincident(g4,g5)
    c: Coincident(g5,g0)
    c: Equal(g0, g1-g5) x5
    c: PointOnObject(g0,g6)
    c: PointOnObject(g1,g6)
    c: PointOnObject(g2,g6)
    c: PointOnObject(g3,g6)
    c: PointOnObject(g4,g6)
    c: PointOnObject(g5,g6)
    c: Coincident(g6,g-1)
    c: Diameter(g6) = 7
    c: PointOnObject(g0,g-2)
    c: Coincident(g7,g8)
    c: Coincident(g8,g9)
    c: Coincident(g9,g10)
    c: Coincident(g10,g11)
    c: Coincident(g11,g12)
    c: Coincident(g12,g7)
    c: Equal(g7, g8-g12) x5
    c: PointOnObject(g7,g13)
    c: PointOnObject(g8,g13)
    c: PointOnObject(g9,g13)
    c: PointOnObject(g10,g13)
    c: PointOnObject(g11,g13)
    c: PointOnObject(g12,g13)
    c: PointOnObject(g13,g-1)
    c: Diameter(g13) = 7
    c: Distance(g6,g13) = 8
    c: Horizontal(g0,g10)
    c: Coincident(g14,g15)
    c: Coincident(g15,g16)
    c: Coincident(g16,g17)
    c: Coincident(g17,g18)
    c: Coincident(g18,g19)
    c: Coincident(g19,g14)
    c: Equal(g14, g15-g19) x5
    c: PointOnObject(g14,g20)
    c: PointOnObject(g15,g20)
    c: PointOnObject(g16,g20)
    c: PointOnObject(g17,g20)
    c: PointOnObject(g18,g20)
    c: PointOnObject(g19,g20)
    c: Diameter(g20) = 7
    c: DistanceY(g-1,g20) = 7
    c: Vertical(g18)
    c: Distance(g17,g-2) = 1
    c: Coincident(g21,g22)
    c: Coincident(g22,g23)
    c: Coincident(g23,g24)
    c: Coincident(g24,g25)
    c: Coincident(g25,g26)
    c: Coincident(g26,g21)
    c: Equal(g21, g22-g26) x5
    c: PointOnObject(g21,g27)
    c: PointOnObject(g22,g27)
    c: PointOnObject(g23,g27)
    c: PointOnObject(g24,g27)
    c: PointOnObject(g25,g27)
    c: PointOnObject(g26,g27)
    c: Diameter(g27) = 7
    c: DistanceY(g-1,g27) = 7
    c: DistanceX(g21,g-1) = 1
    c: Vertical(g21)
    c: Coincident(g28,g29)
    c: Coincident(g29,g30)
    c: Coincident(g30,g31)
    c: Coincident(g31,g32)
    c: Coincident(g32,g33)
    c: Coincident(g33,g28)
    c: Equal(g28, g29-g33) x5
    c: PointOnObject(g28,g34)
    c: PointOnObject(g29,g34)
    c: PointOnObject(g30,g34)
    c: PointOnObject(g31,g34)
    c: PointOnObject(g32,g34)
    c: PointOnObject(g33,g34)
    c: PointOnObject(g34,g-1)
    c: Diameter(g34) = 7
    c: Vertical(g31)
    c: DistanceX(g34,g-1) = 8
    c: Coincident(g35,g36)
    c: Coincident(g36,g37)
    c: Coincident(g37,g38)
    c: Coincident(g38,g39)
    c: Coincident(g39,g40)
    c: Coincident(g40,g35)
    c: Equal(g35, g36-g40) x5
    c: PointOnObject(g35,g41)
    c: PointOnObject(g36,g41)
    c: PointOnObject(g37,g41)
    c: PointOnObject(g38,g41)
    c: PointOnObject(g39,g41)
    c: PointOnObject(g40,g41)
    c: Coincident(g42,g43)
    c: Coincident(g43,g44)
    c: Coincident(g44,g45)
    c: Coincident(g45,g46)
    c: Coincident(g46,g47)
    c: Coincident(g47,g42)
    c: Equal(g42, g43-g47) x5
    c: PointOnObject(g42,g48)
    c: PointOnObject(g43,g48)
    c: PointOnObject(g44,g48)
    c: PointOnObject(g45,g48)
    c: PointOnObject(g46,g48)
    c: PointOnObject(g47,g48)
    c: Equal(g41,g48)
    c: Diameter(g41) = 7
    c: Vertical(g39)
    c: Vertical(g43)
    c: Distance(g-2,g39) = 1
    c: Symmetric(g38,g43,g-2)
    c: Distance(g41,g-1) = 7
FEATURE [Part::Extrusion] Extrude696  label="hex298"
  Base = -> Sketch705
  Dir = (0,-1,2e-16)
  DirMode = 2
  FaceMakerClass = Part::FaceMakerBullseye
  FaceMakerMode = 3
  LengthFwd = 10
  LengthRev = 0
  Placement = pos=(-32,0,-42) rot=(0,0,1;0rad)
  Solid = true
  Symmetric = false
FEATURE [Sketcher::SketchObject] Sketch706
  ArcFitTolerance = 1e-06
  FullyConstrained = true
  MakeInternals = false
  Placement = pos=(0,0,0) rot=(1,0,0;1.5708rad)
  sketch-geometry (49):
    g0: LineSegment StartX=1e-16 StartY=3.5 StartZ=0 EndX=-3.03109 EndY=1.75 EndZ=0
    g1: LineSegment StartX=-3.03109 StartY=1.75 StartZ=0 EndX=-3.03109 EndY=-1.75 EndZ=0
    g2: LineSegment StartX=-3.03109 StartY=-1.75 StartZ=0 EndX=-1e-16 EndY=-3.5 EndZ=0
    g3: LineSegment StartX=-1e-16 StartY=-3.5 StartZ=0 EndX=3.03109 EndY=-1.75 EndZ=0
    g4: LineSegment StartX=3.03109 StartY=-1.75 StartZ=0 EndX=3.03109 EndY=1.75 EndZ=0
    g5: LineSegment StartX=3.03109 StartY=1.75 StartZ=0 EndX=1e-16 EndY=3.5 EndZ=0
    g6: Circle [constr] CenterX=0 CenterY=0 CenterZ=0 NormalX=0 NormalY=0 NormalZ=1 AngleXU=0 Radius=3.5
    g7: LineSegment StartX=4.96892 StartY=-1.75002 StartZ=0 EndX=8.00002 EndY=-3.5 EndZ=0
    g8: LineSegment StartX=8.00002 StartY=-3.5 StartZ=0 EndX=11.0311 EndY=-1.74998 EndZ=0
    g9: LineSegment StartX=11.0311 StartY=-1.74998 StartZ=0 EndX=11.0311 EndY=1.75002 EndZ=0
    g10: LineSegment StartX=11.0311 StartY=1.75002 StartZ=0 EndX=7.99998 EndY=3.5 EndZ=0
    g11: LineSegment StartX=7.99998 StartY=3.5 StartZ=0 EndX=4.9689 EndY=1.74998 EndZ=0
    g12: LineSegment StartX=4.9689 StartY=1.74998 StartZ=0 EndX=4.96892 EndY=-1.75002 EndZ=0
    g13: Circle [constr] CenterX=8 CenterY=0 CenterZ=0 NormalX=0 NormalY=0 NormalZ=1 AngleXU=0 Radius=3.5
    g14: LineSegment StartX=4.03109 StartY=3.5 StartZ=0 EndX=7.06218 EndY=5.25 EndZ=0
    g15: LineSegment StartX=7.06218 StartY=5.25 StartZ=0 EndX=7.06218 EndY=8.75 EndZ=0
    g16: LineSegment StartX=7.06218 StartY=8.75 StartZ=0 EndX=4.03109 EndY=10.5 EndZ=0
    g17: LineSegment StartX=4.03109 StartY=10.5 StartZ=0 EndX=1 EndY=8.75 EndZ=0
    g18: LineSegment StartX=1 StartY=8.75 StartZ=0 EndX=1 EndY=5.25 EndZ=0
    g19: LineSegment StartX=1 StartY=5.25 StartZ=0 EndX=4.03109 EndY=3.5 EndZ=0
    g20: Circle [constr] CenterX=4.03109 CenterY=7 CenterZ=0 NormalX=0 NormalY=0 NormalZ=1 AngleXU=0 Radius=3.5
    g21: LineSegment StartX=-1 StartY=5.25 StartZ=0 EndX=-1 EndY=8.75 EndZ=0
    g22: LineSegment StartX=-1 StartY=8.75 StartZ=0 EndX=-4.03109 EndY=10.5 EndZ=0
    g23: LineSegment StartX=-4.03109 StartY=10.5 StartZ=0 EndX=-7.06218 EndY=8.75 EndZ=0
    g24: LineSegment StartX=-7.06218 StartY=8.75 StartZ=0 EndX=-7.06218 EndY=5.25 EndZ=0
    g25: LineSegment StartX=-7.06218 StartY=5.25 StartZ=0 EndX=-4.03109 EndY=3.5 EndZ=0
    g26: LineSegment StartX=-4.03109 StartY=3.5 StartZ=0 EndX=-1 EndY=5.25 EndZ=0
    g27: Circle [constr] CenterX=-4.03109 CenterY=7 CenterZ=0 NormalX=0 NormalY=0 NormalZ=1 AngleXU=0 Radius=3.5
    g28: LineSegment StartX=-4.96891 StartY=-1.75 StartZ=0 EndX=-4.96891 EndY=1.75 EndZ=0
    g29: LineSegment StartX=-4.96891 StartY=1.75 StartZ=0 EndX=-8 EndY=3.5 EndZ=0
    g30: LineSegment StartX=-8 StartY=3.5 StartZ=0 EndX=-11.0311 EndY=1.75 EndZ=0
    g31: LineSegment StartX=-11.0311 StartY=1.75 StartZ=0 EndX=-11.0311 EndY=-1.75 EndZ=0
    g32: LineSegment StartX=-11.0311 StartY=-1.75 StartZ=0 EndX=-8 EndY=-3.5 EndZ=0
    g33: LineSegment StartX=-8 StartY=-3.5 StartZ=0 EndX=-4.96891 EndY=-1.75 EndZ=0
    g34: Circle [constr] CenterX=-8 CenterY=0 CenterZ=0 NormalX=0 NormalY=0 NormalZ=1 AngleXU=0 Radius=3.5
    g35: LineSegment StartX=-4.03109 StartY=-3.5 StartZ=0 EndX=-7.06218 EndY=-5.25 EndZ=0
    g36: LineSegment StartX=-7.06218 StartY=-5.25 StartZ=0 EndX=-7.06218 EndY=-8.75 EndZ=0
    g37: LineSegment StartX=-7.06218 StartY=-8.75 StartZ=0 EndX=-4.03109 EndY=-10.5 EndZ=0
    g38: LineSegment StartX=-4.03109 StartY=-10.5 StartZ=0 EndX=-1 EndY=-8.75 EndZ=0
    g39: LineSegment StartX=-1 StartY=-8.75 StartZ=0 EndX=-1 EndY=-5.25 EndZ=0
    g40: LineSegment StartX=-1 StartY=-5.25 StartZ=0 EndX=-4.03109 EndY=-3.5 EndZ=0
    g41: Circle [constr] CenterX=-4.03109 CenterY=-7 CenterZ=0 NormalX=0 NormalY=0 NormalZ=1 AngleXU=0 Radius=3.5
    g42: LineSegment StartX=4.03109 StartY=-3.5 StartZ=0 EndX=1 EndY=-5.25 EndZ=0
    g43: LineSegment StartX=1 StartY=-5.25 StartZ=0 EndX=1 EndY=-8.75 EndZ=0
    g44: LineSegment StartX=1 StartY=-8.75 StartZ=0 EndX=4.03109 EndY=-10.5 EndZ=0
    g45: LineSegment StartX=4.03109 StartY=-10.5 StartZ=0 EndX=7.06218 EndY=-8.75 EndZ=0
    g46: LineSegment StartX=7.06218 StartY=-8.75 StartZ=0 EndX=7.06218 EndY=-5.25 EndZ=0
    g47: LineSegment StartX=7.06218 StartY=-5.25 StartZ=0 EndX=4.03109 EndY=-3.5 EndZ=0
    g48: Circle [constr] CenterX=4.03109 CenterY=-7 CenterZ=0 NormalX=0 NormalY=0 NormalZ=1 AngleXU=0 Radius=3.5
  constraints (117):
    c: Coincident(g0,g1)
    c: Coincident(g1,g2)
    c: Coincident(g2,g3)
    c: Coincident(g3,g4)
    c: Coincident(g4,g5)
    c: Coincident(g5,g0)
    c: Equal(g0, g1-g5) x5
    c: PointOnObject(g0,g6)
    c: PointOnObject(g1,g6)
    c: PointOnObject(g2,g6)
    c: PointOnObject(g3,g6)
    c: PointOnObject(g4,g6)
    c: PointOnObject(g5,g6)
    c: Coincident(g6,g-1)
    c: Diameter(g6) = 7
    c: PointOnObject(g0,g-2)
    c: Coincident(g7,g8)
    c: Coincident(g8,g9)
    c: Coincident(g9,g10)
    c: Coincident(g10,g11)
    c: Coincident(g11,g12)
    c: Coincident(g12,g7)
    c: Equal(g7, g8-g12) x5
    c: PointOnObject(g7,g13)
    c: PointOnObject(g8,g13)
    c: PointOnObject(g9,g13)
    c: PointOnObject(g10,g13)
    c: PointOnObject(g11,g13)
    c: PointOnObject(g12,g13)
    c: PointOnObject(g13,g-1)
    c: Diameter(g13) = 7
    c: Distance(g6,g13) = 8
    c: Horizontal(g0,g10)
    c: Coincident(g14,g15)
    c: Coincident(g15,g16)
    c: Coincident(g16,g17)
    c: Coincident(g17,g18)
    c: Coincident(g18,g19)
    c: Coincident(g19,g14)
    c: Equal(g14, g15-g19) x5
    c: PointOnObject(g14,g20)
    c: PointOnObject(g15,g20)
    c: PointOnObject(g16,g20)
    c: PointOnObject(g17,g20)
    c: PointOnObject(g18,g20)
    c: PointOnObject(g19,g20)
    c: Diameter(g20) = 7
    c: DistanceY(g-1,g20) = 7
    c: Vertical(g18)
    c: Distance(g17,g-2) = 1
    c: Coincident(g21,g22)
    c: Coincident(g22,g23)
    c: Coincident(g23,g24)
    c: Coincident(g24,g25)
    c: Coincident(g25,g26)
    c: Coincident(g26,g21)
    c: Equal(g21, g22-g26) x5
    c: PointOnObject(g21,g27)
    c: PointOnObject(g22,g27)
    c: PointOnObject(g23,g27)
    c: PointOnObject(g24,g27)
    c: PointOnObject(g25,g27)
    c: PointOnObject(g26,g27)
    c: Diameter(g27) = 7
    c: DistanceY(g-1,g27) = 7
    c: DistanceX(g21,g-1) = 1
    c: Vertical(g21)
    c: Coincident(g28,g29)
    c: Coincident(g29,g30)
    c: Coincident(g30,g31)
    c: Coincident(g31,g32)
    c: Coincident(g32,g33)
    c: Coincident(g33,g28)
    c: Equal(g28, g29-g33) x5
    c: PointOnObject(g28,g34)
    c: PointOnObject(g29,g34)
    c: PointOnObject(g30,g34)
    c: PointOnObject(g31,g34)
    c: PointOnObject(g32,g34)
    c: PointOnObject(g33,g34)
    c: PointOnObject(g34,g-1)
    c: Diameter(g34) = 7
    c: Vertical(g31)
    c: DistanceX(g34,g-1) = 8
    c: Coincident(g35,g36)
    c: Coincident(g36,g37)
    c: Coincident(g37,g38)
    c: Coincident(g38,g39)
    c: Coincident(g39,g40)
    c: Coincident(g40,g35)
    c: Equal(g35, g36-g40) x5
    c: PointOnObject(g35,g41)
    c: PointOnObject(g36,g41)
    c: PointOnObject(g37,g41)
    c: PointOnObject(g38,g41)
    c: PointOnObject(g39,g41)
    c: PointOnObject(g40,g41)
    c: Coincident(g42,g43)
    c: Coincident(g43,g44)
    c: Coincident(g44,g45)
    c: Coincident(g45,g46)
    c: Coincident(g46,g47)
    c: Coincident(g47,g42)
    c: Equal(g42, g43-g47) x5
    c: PointOnObject(g42,g48)
    c: PointOnObject(g43,g48)
    c: PointOnObject(g44,g48)
    c: PointOnObject(g45,g48)
    c: PointOnObject(g46,g48)
    c: PointOnObject(g47,g48)
    c: Equal(g41,g48)
    c: Diameter(g41) = 7
    c: Vertical(g39)
    c: Vertical(g43)
    c: Distance(g-2,g39) = 1
    c: Symmetric(g38,g43,g-2)
    c: Distance(g41,g-1) = 7
FEATURE [Part::Extrusion] Extrude697  label="hex299"
  Base = -> Sketch706
  Dir = (0,-1,2e-16)
  DirMode = 2
  FaceMakerClass = Part::FaceMakerBullseye
  FaceMakerMode = 3
  LengthFwd = 10
  LengthRev = 0
  Placement = pos=(-56,0,-42) rot=(0,0,1;0rad)
  Solid = true
  Symmetric = false
FEATURE [Sketcher::SketchObject] Sketch707
  ArcFitTolerance = 1e-06
  FullyConstrained = true
  MakeInternals = false
  Placement = pos=(0,0,0) rot=(1,0,0;1.5708rad)
  sketch-geometry (49):
    g0: LineSegment StartX=1e-16 StartY=3.5 StartZ=0 EndX=-3.03109 EndY=1.75 EndZ=0
    g1: LineSegment StartX=-3.03109 StartY=1.75 StartZ=0 EndX=-3.03109 EndY=-1.75 EndZ=0
    g2: LineSegment StartX=-3.03109 StartY=-1.75 StartZ=0 EndX=-1e-16 EndY=-3.5 EndZ=0
    g3: LineSegment StartX=-1e-16 StartY=-3.5 StartZ=0 EndX=3.03109 EndY=-1.75 EndZ=0
    g4: LineSegment StartX=3.03109 StartY=-1.75 StartZ=0 EndX=3.03109 EndY=1.75 EndZ=0
    g5: LineSegment StartX=3.03109 StartY=1.75 StartZ=0 EndX=1e-16 EndY=3.5 EndZ=0
    g6: Circle [constr] CenterX=0 CenterY=0 CenterZ=0 NormalX=0 NormalY=0 NormalZ=1 AngleXU=0 Radius=3.5
    g7: LineSegment StartX=4.96892 StartY=-1.75002 StartZ=0 EndX=8.00002 EndY=-3.5 EndZ=0
    g8: LineSegment StartX=8.00002 StartY=-3.5 StartZ=0 EndX=11.0311 EndY=-1.74998 EndZ=0
    g9: LineSegment StartX=11.0311 StartY=-1.74998 StartZ=0 EndX=11.0311 EndY=1.75002 EndZ=0
    g10: LineSegment StartX=11.0311 StartY=1.75002 StartZ=0 EndX=7.99998 EndY=3.5 EndZ=0
    g11: LineSegment StartX=7.99998 StartY=3.5 StartZ=0 EndX=4.9689 EndY=1.74998 EndZ=0
    g12: LineSegment StartX=4.9689 StartY=1.74998 StartZ=0 EndX=4.96892 EndY=-1.75002 EndZ=0
    g13: Circle [constr] CenterX=8 CenterY=0 CenterZ=0 NormalX=0 NormalY=0 NormalZ=1 AngleXU=0 Radius=3.5
    g14: LineSegment StartX=4.03109 StartY=3.5 StartZ=0 EndX=7.06218 EndY=5.25 EndZ=0
    g15: LineSegment StartX=7.06218 StartY=5.25 StartZ=0 EndX=7.06218 EndY=8.75 EndZ=0
    g16: LineSegment StartX=7.06218 StartY=8.75 StartZ=0 EndX=4.03109 EndY=10.5 EndZ=0
    g17: LineSegment StartX=4.03109 StartY=10.5 StartZ=0 EndX=1 EndY=8.75 EndZ=0
    g18: LineSegment StartX=1 StartY=8.75 StartZ=0 EndX=1 EndY=5.25 EndZ=0
    g19: LineSegment StartX=1 StartY=5.25 StartZ=0 EndX=4.03109 EndY=3.5 EndZ=0
    g20: Circle [constr] CenterX=4.03109 CenterY=7 CenterZ=0 NormalX=0 NormalY=0 NormalZ=1 AngleXU=0 Radius=3.5
    g21: LineSegment StartX=-1 StartY=5.25 StartZ=0 EndX=-1 EndY=8.75 EndZ=0
    g22: LineSegment StartX=-1 StartY=8.75 StartZ=0 EndX=-4.03109 EndY=10.5 EndZ=0
    g23: LineSegment StartX=-4.03109 StartY=10.5 StartZ=0 EndX=-7.06218 EndY=8.75 EndZ=0
    g24: LineSegment StartX=-7.06218 StartY=8.75 StartZ=0 EndX=-7.06218 EndY=5.25 EndZ=0
    g25: LineSegment StartX=-7.06218 StartY=5.25 StartZ=0 EndX=-4.03109 EndY=3.5 EndZ=0
    g26: LineSegment StartX=-4.03109 StartY=3.5 StartZ=0 EndX=-1 EndY=5.25 EndZ=0
    g27: Circle [constr] CenterX=-4.03109 CenterY=7 CenterZ=0 NormalX=0 NormalY=0 NormalZ=1 AngleXU=0 Radius=3.5
    g28: LineSegment StartX=-4.96891 StartY=-1.75 StartZ=0 EndX=-4.96891 EndY=1.75 EndZ=0
    g29: LineSegment StartX=-4.96891 StartY=1.75 StartZ=0 EndX=-8 EndY=3.5 EndZ=0
    g30: LineSegment StartX=-8 StartY=3.5 StartZ=0 EndX=-11.0311 EndY=1.75 EndZ=0
    g31: LineSegment StartX=-11.0311 StartY=1.75 StartZ=0 EndX=-11.0311 EndY=-1.75 EndZ=0
    g32: LineSegment StartX=-11.0311 StartY=-1.75 StartZ=0 EndX=-8 EndY=-3.5 EndZ=0
    g33: LineSegment StartX=-8 StartY=-3.5 StartZ=0 EndX=-4.96891 EndY=-1.75 EndZ=0
    g34: Circle [constr] CenterX=-8 CenterY=0 CenterZ=0 NormalX=0 NormalY=0 NormalZ=1 AngleXU=0 Radius=3.5
    g35: LineSegment StartX=-4.03109 StartY=-3.5 StartZ=0 EndX=-7.06218 EndY=-5.25 EndZ=0
    g36: LineSegment StartX=-7.06218 StartY=-5.25 StartZ=0 EndX=-7.06218 EndY=-8.75 EndZ=0
    g37: LineSegment StartX=-7.06218 StartY=-8.75 StartZ=0 EndX=-4.03109 EndY=-10.5 EndZ=0
    g38: LineSegment StartX=-4.03109 StartY=-10.5 StartZ=0 EndX=-1 EndY=-8.75 EndZ=0
    g39: LineSegment StartX=-1 StartY=-8.75 StartZ=0 EndX=-1 EndY=-5.25 EndZ=0
    g40: LineSegment StartX=-1 StartY=-5.25 StartZ=0 EndX=-4.03109 EndY=-3.5 EndZ=0
    g41: Circle [constr] CenterX=-4.03109 CenterY=-7 CenterZ=0 NormalX=0 NormalY=0 NormalZ=1 AngleXU=0 Radius=3.5
    g42: LineSegment StartX=4.03109 StartY=-3.5 StartZ=0 EndX=1 EndY=-5.25 EndZ=0
    g43: LineSegment StartX=1 StartY=-5.25 StartZ=0 EndX=1 EndY=-8.75 EndZ=0
    g44: LineSegment StartX=1 StartY=-8.75 StartZ=0 EndX=4.03109 EndY=-10.5 EndZ=0
    g45: LineSegment StartX=4.03109 StartY=-10.5 StartZ=0 EndX=7.06218 EndY=-8.75 EndZ=0
    g46: LineSegment StartX=7.06218 StartY=-8.75 StartZ=0 EndX=7.06218 EndY=-5.25 EndZ=0
    g47: LineSegment StartX=7.06218 StartY=-5.25 StartZ=0 EndX=4.03109 EndY=-3.5 EndZ=0
    g48: Circle [constr] CenterX=4.03109 CenterY=-7 CenterZ=0 NormalX=0 NormalY=0 NormalZ=1 AngleXU=0 Radius=3.5
  constraints (117):
    c: Coincident(g0,g1)
    c: Coincident(g1,g2)
    c: Coincident(g2,g3)
    c: Coincident(g3,g4)
    c: Coincident(g4,g5)
    c: Coincident(g5,g0)
    c: Equal(g0, g1-g5) x5
    c: PointOnObject(g0,g6)
    c: PointOnObject(g1,g6)
    c: PointOnObject(g2,g6)
    c: PointOnObject(g3,g6)
    c: PointOnObject(g4,g6)
    c: PointOnObject(g5,g6)
    c: Coincident(g6,g-1)
    c: Diameter(g6) = 7
    c: PointOnObject(g0,g-2)
    c: Coincident(g7,g8)
    c: Coincident(g8,g9)
    c: Coincident(g9,g10)
    c: Coincident(g10,g11)
    c: Coincident(g11,g12)
    c: Coincident(g12,g7)
    c: Equal(g7, g8-g12) x5
    c: PointOnObject(g7,g13)
    c: PointOnObject(g8,g13)
    c: PointOnObject(g9,g13)
    c: PointOnObject(g10,g13)
    c: PointOnObject(g11,g13)
    c: PointOnObject(g12,g13)
    c: PointOnObject(g13,g-1)
    c: Diameter(g13) = 7
    c: Distance(g6,g13) = 8
    c: Horizontal(g0,g10)
    c: Coincident(g14,g15)
    c: Coincident(g15,g16)
    c: Coincident(g16,g17)
    c: Coincident(g17,g18)
    c: Coincident(g18,g19)
    c: Coincident(g19,g14)
    c: Equal(g14, g15-g19) x5
    c: PointOnObject(g14,g20)
    c: PointOnObject(g15,g20)
    c: PointOnObject(g16,g20)
    c: PointOnObject(g17,g20)
    c: PointOnObject(g18,g20)
    c: PointOnObject(g19,g20)
    c: Diameter(g20) = 7
    c: DistanceY(g-1,g20) = 7
    c: Vertical(g18)
    c: Distance(g17,g-2) = 1
    c: Coincident(g21,g22)
    c: Coincident(g22,g23)
    c: Coincident(g23,g24)
    c: Coincident(g24,g25)
    c: Coincident(g25,g26)
    c: Coincident(g26,g21)
    c: Equal(g21, g22-g26) x5
    c: PointOnObject(g21,g27)
    c: PointOnObject(g22,g27)
    c: PointOnObject(g23,g27)
    c: PointOnObject(g24,g27)
    c: PointOnObject(g25,g27)
    c: PointOnObject(g26,g27)
    c: Diameter(g27) = 7
    c: DistanceY(g-1,g27) = 7
    c: DistanceX(g21,g-1) = 1
    c: Vertical(g21)
    c: Coincident(g28,g29)
    c: Coincident(g29,g30)
    c: Coincident(g30,g31)
    c: Coincident(g31,g32)
    c: Coincident(g32,g33)
    c: Coincident(g33,g28)
    c: Equal(g28, g29-g33) x5
    c: PointOnObject(g28,g34)
    c: PointOnObject(g29,g34)
    c: PointOnObject(g30,g34)
    c: PointOnObject(g31,g34)
    c: PointOnObject(g32,g34)
    c: PointOnObject(g33,g34)
    c: PointOnObject(g34,g-1)
    c: Diameter(g34) = 7
    c: Vertical(g31)
    c: DistanceX(g34,g-1) = 8
    c: Coincident(g35,g36)
    c: Coincident(g36,g37)
    c: Coincident(g37,g38)
    c: Coincident(g38,g39)
    c: Coincident(g39,g40)
    c: Coincident(g40,g35)
    c: Equal(g35, g36-g40) x5
    c: PointOnObject(g35,g41)
    c: PointOnObject(g36,g41)
    c: PointOnObject(g37,g41)
    c: PointOnObject(g38,g41)
    c: PointOnObject(g39,g41)
    c: PointOnObject(g40,g41)
    c: Coincident(g42,g43)
    c: Coincident(g43,g44)
    c: Coincident(g44,g45)
    c: Coincident(g45,g46)
    c: Coincident(g46,g47)
    c: Coincident(g47,g42)
    c: Equal(g42, g43-g47) x5
    c: PointOnObject(g42,g48)
    c: PointOnObject(g43,g48)
    c: PointOnObject(g44,g48)
    c: PointOnObject(g45,g48)
    c: PointOnObject(g46,g48)
    c: PointOnObject(g47,g48)
    c: Equal(g41,g48)
    c: Diameter(g41) = 7
    c: Vertical(g39)
    c: Vertical(g43)
    c: Distance(g-2,g39) = 1
    c: Symmetric(g38,g43,g-2)
    c: Distance(g41,g-1) = 7
FEATURE [Part::Extrusion] Extrude698  label="hex300"
  Base = -> Sketch707
  Dir = (0,-1,2e-16)
  DirMode = 2
  FaceMakerClass = Part::FaceMakerBullseye
  FaceMakerMode = 3
  LengthFwd = 10
  LengthRev = 0
  Placement = pos=(-40,0,-56) rot=(0,0,1;0rad)
  Solid = true
  Symmetric = false
FEATURE [Sketcher::SketchObject] Sketch708
  ArcFitTolerance = 1e-06
  FullyConstrained = true
  MakeInternals = false
  Placement = pos=(0,0,0) rot=(1,0,0;1.5708rad)
  sketch-geometry (49):
    g0: LineSegment StartX=1e-16 StartY=3.5 StartZ=0 EndX=-3.03109 EndY=1.75 EndZ=0
    g1: LineSegment StartX=-3.03109 StartY=1.75 StartZ=0 EndX=-3.03109 EndY=-1.75 EndZ=0
    g2: LineSegment StartX=-3.03109 StartY=-1.75 StartZ=0 EndX=-1e-16 EndY=-3.5 EndZ=0
    g3: LineSegment StartX=-1e-16 StartY=-3.5 StartZ=0 EndX=3.03109 EndY=-1.75 EndZ=0
    g4: LineSegment StartX=3.03109 StartY=-1.75 StartZ=0 EndX=3.03109 EndY=1.75 EndZ=0
    g5: LineSegment StartX=3.03109 StartY=1.75 StartZ=0 EndX=1e-16 EndY=3.5 EndZ=0
    g6: Circle [constr] CenterX=0 CenterY=0 CenterZ=0 NormalX=0 NormalY=0 NormalZ=1 AngleXU=0 Radius=3.5
    g7: LineSegment StartX=4.96892 StartY=-1.75002 StartZ=0 EndX=8.00002 EndY=-3.5 EndZ=0
    g8: LineSegment StartX=8.00002 StartY=-3.5 StartZ=0 EndX=11.0311 EndY=-1.74998 EndZ=0
    g9: LineSegment StartX=11.0311 StartY=-1.74998 StartZ=0 EndX=11.0311 EndY=1.75002 EndZ=0
    g10: LineSegment StartX=11.0311 StartY=1.75002 StartZ=0 EndX=7.99998 EndY=3.5 EndZ=0
    g11: LineSegment StartX=7.99998 StartY=3.5 StartZ=0 EndX=4.9689 EndY=1.74998 EndZ=0
    g12: LineSegment StartX=4.9689 StartY=1.74998 StartZ=0 EndX=4.96892 EndY=-1.75002 EndZ=0
    g13: Circle [constr] CenterX=8 CenterY=0 CenterZ=0 NormalX=0 NormalY=0 NormalZ=1 AngleXU=0 Radius=3.5
    g14: LineSegment StartX=4.03109 StartY=3.5 StartZ=0 EndX=7.06218 EndY=5.25 EndZ=0
    g15: LineSegment StartX=7.06218 StartY=5.25 StartZ=0 EndX=7.06218 EndY=8.75 EndZ=0
    g16: LineSegment StartX=7.06218 StartY=8.75 StartZ=0 EndX=4.03109 EndY=10.5 EndZ=0
    g17: LineSegment StartX=4.03109 StartY=10.5 StartZ=0 EndX=1 EndY=8.75 EndZ=0
    g18: LineSegment StartX=1 StartY=8.75 StartZ=0 EndX=1 EndY=5.25 EndZ=0
    g19: LineSegment StartX=1 StartY=5.25 StartZ=0 EndX=4.03109 EndY=3.5 EndZ=0
    g20: Circle [constr] CenterX=4.03109 CenterY=7 CenterZ=0 NormalX=0 NormalY=0 NormalZ=1 AngleXU=0 Radius=3.5
    g21: LineSegment StartX=-1 StartY=5.25 StartZ=0 EndX=-1 EndY=8.75 EndZ=0
    g22: LineSegment StartX=-1 StartY=8.75 StartZ=0 EndX=-4.03109 EndY=10.5 EndZ=0
    g23: LineSegment StartX=-4.03109 StartY=10.5 StartZ=0 EndX=-7.06218 EndY=8.75 EndZ=0
    g24: LineSegment StartX=-7.06218 StartY=8.75 StartZ=0 EndX=-7.06218 EndY=5.25 EndZ=0
    g25: LineSegment StartX=-7.06218 StartY=5.25 StartZ=0 EndX=-4.03109 EndY=3.5 EndZ=0
    g26: LineSegment StartX=-4.03109 StartY=3.5 StartZ=0 EndX=-1 EndY=5.25 EndZ=0
    g27: Circle [constr] CenterX=-4.03109 CenterY=7 CenterZ=0 NormalX=0 NormalY=0 NormalZ=1 AngleXU=0 Radius=3.5
    g28: LineSegment StartX=-4.96891 StartY=-1.75 StartZ=0 EndX=-4.96891 EndY=1.75 EndZ=0
    g29: LineSegment StartX=-4.96891 StartY=1.75 StartZ=0 EndX=-8 EndY=3.5 EndZ=0
    g30: LineSegment StartX=-8 StartY=3.5 StartZ=0 EndX=-11.0311 EndY=1.75 EndZ=0
    g31: LineSegment StartX=-11.0311 StartY=1.75 StartZ=0 EndX=-11.0311 EndY=-1.75 EndZ=0
    g32: LineSegment StartX=-11.0311 StartY=-1.75 StartZ=0 EndX=-8 EndY=-3.5 EndZ=0
    g33: LineSegment StartX=-8 StartY=-3.5 StartZ=0 EndX=-4.96891 EndY=-1.75 EndZ=0
    g34: Circle [constr] CenterX=-8 CenterY=0 CenterZ=0 NormalX=0 NormalY=0 NormalZ=1 AngleXU=0 Radius=3.5
    g35: LineSegment StartX=-4.03109 StartY=-3.5 StartZ=0 EndX=-7.06218 EndY=-5.25 EndZ=0
    g36: LineSegment StartX=-7.06218 StartY=-5.25 StartZ=0 EndX=-7.06218 EndY=-8.75 EndZ=0
    g37: LineSegment StartX=-7.06218 StartY=-8.75 StartZ=0 EndX=-4.03109 EndY=-10.5 EndZ=0
    g38: LineSegment StartX=-4.03109 StartY=-10.5 StartZ=0 EndX=-1 EndY=-8.75 EndZ=0
    g39: LineSegment StartX=-1 StartY=-8.75 StartZ=0 EndX=-1 EndY=-5.25 EndZ=0
    g40: LineSegment StartX=-1 StartY=-5.25 StartZ=0 EndX=-4.03109 EndY=-3.5 EndZ=0
    g41: Circle [constr] CenterX=-4.03109 CenterY=-7 CenterZ=0 NormalX=0 NormalY=0 NormalZ=1 AngleXU=0 Radius=3.5
    g42: LineSegment StartX=4.03109 StartY=-3.5 StartZ=0 EndX=1 EndY=-5.25 EndZ=0
    g43: LineSegment StartX=1 StartY=-5.25 StartZ=0 EndX=1 EndY=-8.75 EndZ=0
    g44: LineSegment StartX=1 StartY=-8.75 StartZ=0 EndX=4.03109 EndY=-10.5 EndZ=0
    g45: LineSegment StartX=4.03109 StartY=-10.5 StartZ=0 EndX=7.06218 EndY=-8.75 EndZ=0
    g46: LineSegment StartX=7.06218 StartY=-8.75 StartZ=0 EndX=7.06218 EndY=-5.25 EndZ=0
    g47: LineSegment StartX=7.06218 StartY=-5.25 StartZ=0 EndX=4.03109 EndY=-3.5 EndZ=0
    g48: Circle [constr] CenterX=4.03109 CenterY=-7 CenterZ=0 NormalX=0 NormalY=0 NormalZ=1 AngleXU=0 Radius=3.5
  constraints (117):
    c: Coincident(g0,g1)
    c: Coincident(g1,g2)
    c: Coincident(g2,g3)
    c: Coincident(g3,g4)
    c: Coincident(g4,g5)
    c: Coincident(g5,g0)
    c: Equal(g0, g1-g5) x5
    c: PointOnObject(g0,g6)
    c: PointOnObject(g1,g6)
    c: PointOnObject(g2,g6)
    c: PointOnObject(g3,g6)
    c: PointOnObject(g4,g6)
    c: PointOnObject(g5,g6)
    c: Coincident(g6,g-1)
    c: Diameter(g6) = 7
    c: PointOnObject(g0,g-2)
    c: Coincident(g7,g8)
    c: Coincident(g8,g9)
    c: Coincident(g9,g10)
    c: Coincident(g10,g11)
    c: Coincident(g11,g12)
    c: Coincident(g12,g7)
    c: Equal(g7, g8-g12) x5
    c: PointOnObject(g7,g13)
    c: PointOnObject(g8,g13)
    c: PointOnObject(g9,g13)
    c: PointOnObject(g10,g13)
    c: PointOnObject(g11,g13)
    c: PointOnObject(g12,g13)
    c: PointOnObject(g13,g-1)
    c: Diameter(g13) = 7
    c: Distance(g6,g13) = 8
    c: Horizontal(g0,g10)
    c: Coincident(g14,g15)
    c: Coincident(g15,g16)
    c: Coincident(g16,g17)
    c: Coincident(g17,g18)
    c: Coincident(g18,g19)
    c: Coincident(g19,g14)
    c: Equal(g14, g15-g19) x5
    c: PointOnObject(g14,g20)
    c: PointOnObject(g15,g20)
    c: PointOnObject(g16,g20)
    c: PointOnObject(g17,g20)
    c: PointOnObject(g18,g20)
    c: PointOnObject(g19,g20)
    c: Diameter(g20) = 7
    c: DistanceY(g-1,g20) = 7
    c: Vertical(g18)
    c: Distance(g17,g-2) = 1
    c: Coincident(g21,g22)
    c: Coincident(g22,g23)
    c: Coincident(g23,g24)
    c: Coincident(g24,g25)
    c: Coincident(g25,g26)
    c: Coincident(g26,g21)
    c: Equal(g21, g22-g26) x5
    c: PointOnObject(g21,g27)
    c: PointOnObject(g22,g27)
    c: PointOnObject(g23,g27)
    c: PointOnObject(g24,g27)
    c: PointOnObject(g25,g27)
    c: PointOnObject(g26,g27)
    c: Diameter(g27) = 7
    c: DistanceY(g-1,g27) = 7
    c: DistanceX(g21,g-1) = 1
    c: Vertical(g21)
    c: Coincident(g28,g29)
    c: Coincident(g29,g30)
    c: Coincident(g30,g31)
    c: Coincident(g31,g32)
    c: Coincident(g32,g33)
    c: Coincident(g33,g28)
    c: Equal(g28, g29-g33) x5
    c: PointOnObject(g28,g34)
    c: PointOnObject(g29,g34)
    c: PointOnObject(g30,g34)
    c: PointOnObject(g31,g34)
    c: PointOnObject(g32,g34)
    c: PointOnObject(g33,g34)
    c: PointOnObject(g34,g-1)
    c: Diameter(g34) = 7
    c: Vertical(g31)
    c: DistanceX(g34,g-1) = 8
    c: Coincident(g35,g36)
    c: Coincident(g36,g37)
    c: Coincident(g37,g38)
    c: Coincident(g38,g39)
    c: Coincident(g39,g40)
    c: Coincident(g40,g35)
    c: Equal(g35, g36-g40) x5
    c: PointOnObject(g35,g41)
    c: PointOnObject(g36,g41)
    c: PointOnObject(g37,g41)
    c: PointOnObject(g38,g41)
    c: PointOnObject(g39,g41)
    c: PointOnObject(g40,g41)
    c: Coincident(g42,g43)
    c: Coincident(g43,g44)
    c: Coincident(g44,g45)
    c: Coincident(g45,g46)
    c: Coincident(g46,g47)
    c: Coincident(g47,g42)
    c: Equal(g42, g43-g47) x5
    c: PointOnObject(g42,g48)
    c: PointOnObject(g43,g48)
    c: PointOnObject(g44,g48)
    c: PointOnObject(g45,g48)
    c: PointOnObject(g46,g48)
    c: PointOnObject(g47,g48)
    c: Equal(g41,g48)
    c: Diameter(g41) = 7
    c: Vertical(g39)
    c: Vertical(g43)
    c: Distance(g-2,g39) = 1
    c: Symmetric(g38,g43,g-2)
    c: Distance(g41,g-1) = 7
FEATURE [Part::Extrusion] Extrude699  label="hex301"
  Base = -> Sketch708
  Dir = (0,-1,2e-16)
  DirMode = 2
  FaceMakerClass = Part::FaceMakerBullseye
  FaceMakerMode = 3
  LengthFwd = 10
  LengthRev = 0
  Placement = pos=(-16,0,-56) rot=(0,0,1;0rad)
  Solid = true
  Symmetric = false
FEATURE [Sketcher::SketchObject] Sketch709
  ArcFitTolerance = 1e-06
  FullyConstrained = true
  MakeInternals = false
  Placement = pos=(0,0,0) rot=(1,0,0;1.5708rad)
  sketch-geometry (49):
    g0: LineSegment StartX=1e-16 StartY=3.5 StartZ=0 EndX=-3.03109 EndY=1.75 EndZ=0
    g1: LineSegment StartX=-3.03109 StartY=1.75 StartZ=0 EndX=-3.03109 EndY=-1.75 EndZ=0
    g2: LineSegment StartX=-3.03109 StartY=-1.75 StartZ=0 EndX=-1e-16 EndY=-3.5 EndZ=0
    g3: LineSegment StartX=-1e-16 StartY=-3.5 StartZ=0 EndX=3.03109 EndY=-1.75 EndZ=0
    g4: LineSegment StartX=3.03109 StartY=-1.75 StartZ=0 EndX=3.03109 EndY=1.75 EndZ=0
    g5: LineSegment StartX=3.03109 StartY=1.75 StartZ=0 EndX=1e-16 EndY=3.5 EndZ=0
    g6: Circle [constr] CenterX=0 CenterY=0 CenterZ=0 NormalX=0 NormalY=0 NormalZ=1 AngleXU=0 Radius=3.5
    g7: LineSegment StartX=4.96892 StartY=-1.75002 StartZ=0 EndX=8.00002 EndY=-3.5 EndZ=0
    g8: LineSegment StartX=8.00002 StartY=-3.5 StartZ=0 EndX=11.0311 EndY=-1.74998 EndZ=0
    g9: LineSegment StartX=11.0311 StartY=-1.74998 StartZ=0 EndX=11.0311 EndY=1.75002 EndZ=0
    g10: LineSegment StartX=11.0311 StartY=1.75002 StartZ=0 EndX=7.99998 EndY=3.5 EndZ=0
    g11: LineSegment StartX=7.99998 StartY=3.5 StartZ=0 EndX=4.9689 EndY=1.74998 EndZ=0
    g12: LineSegment StartX=4.9689 StartY=1.74998 StartZ=0 EndX=4.96892 EndY=-1.75002 EndZ=0
    g13: Circle [constr] CenterX=8 CenterY=0 CenterZ=0 NormalX=0 NormalY=0 NormalZ=1 AngleXU=0 Radius=3.5
    g14: LineSegment StartX=4.03109 StartY=3.5 StartZ=0 EndX=7.06218 EndY=5.25 EndZ=0
    g15: LineSegment StartX=7.06218 StartY=5.25 StartZ=0 EndX=7.06218 EndY=8.75 EndZ=0
    g16: LineSegment StartX=7.06218 StartY=8.75 StartZ=0 EndX=4.03109 EndY=10.5 EndZ=0
    g17: LineSegment StartX=4.03109 StartY=10.5 StartZ=0 EndX=1 EndY=8.75 EndZ=0
    g18: LineSegment StartX=1 StartY=8.75 StartZ=0 EndX=1 EndY=5.25 EndZ=0
    g19: LineSegment StartX=1 StartY=5.25 StartZ=0 EndX=4.03109 EndY=3.5 EndZ=0
    g20: Circle [constr] CenterX=4.03109 CenterY=7 CenterZ=0 NormalX=0 NormalY=0 NormalZ=1 AngleXU=0 Radius=3.5
    g21: LineSegment StartX=-1 StartY=5.25 StartZ=0 EndX=-1 EndY=8.75 EndZ=0
    g22: LineSegment StartX=-1 StartY=8.75 StartZ=0 EndX=-4.03109 EndY=10.5 EndZ=0
    g23: LineSegment StartX=-4.03109 StartY=10.5 StartZ=0 EndX=-7.06218 EndY=8.75 EndZ=0
    g24: LineSegment StartX=-7.06218 StartY=8.75 StartZ=0 EndX=-7.06218 EndY=5.25 EndZ=0
    g25: LineSegment StartX=-7.06218 StartY=5.25 StartZ=0 EndX=-4.03109 EndY=3.5 EndZ=0
    g26: LineSegment StartX=-4.03109 StartY=3.5 StartZ=0 EndX=-1 EndY=5.25 EndZ=0
    g27: Circle [constr] CenterX=-4.03109 CenterY=7 CenterZ=0 NormalX=0 NormalY=0 NormalZ=1 AngleXU=0 Radius=3.5
    g28: LineSegment StartX=-4.96891 StartY=-1.75 StartZ=0 EndX=-4.96891 EndY=1.75 EndZ=0
    g29: LineSegment StartX=-4.96891 StartY=1.75 StartZ=0 EndX=-8 EndY=3.5 EndZ=0
    g30: LineSegment StartX=-8 StartY=3.5 StartZ=0 EndX=-11.0311 EndY=1.75 EndZ=0
    g31: LineSegment StartX=-11.0311 StartY=1.75 StartZ=0 EndX=-11.0311 EndY=-1.75 EndZ=0
    g32: LineSegment StartX=-11.0311 StartY=-1.75 StartZ=0 EndX=-8 EndY=-3.5 EndZ=0
    g33: LineSegment StartX=-8 StartY=-3.5 StartZ=0 EndX=-4.96891 EndY=-1.75 EndZ=0
    g34: Circle [constr] CenterX=-8 CenterY=0 CenterZ=0 NormalX=0 NormalY=0 NormalZ=1 AngleXU=0 Radius=3.5
    g35: LineSegment StartX=-4.03109 StartY=-3.5 StartZ=0 EndX=-7.06218 EndY=-5.25 EndZ=0
    g36: LineSegment StartX=-7.06218 StartY=-5.25 StartZ=0 EndX=-7.06218 EndY=-8.75 EndZ=0
    g37: LineSegment StartX=-7.06218 StartY=-8.75 StartZ=0 EndX=-4.03109 EndY=-10.5 EndZ=0
    g38: LineSegment StartX=-4.03109 StartY=-10.5 StartZ=0 EndX=-1 EndY=-8.75 EndZ=0
    g39: LineSegment StartX=-1 StartY=-8.75 StartZ=0 EndX=-1 EndY=-5.25 EndZ=0
    g40: LineSegment StartX=-1 StartY=-5.25 StartZ=0 EndX=-4.03109 EndY=-3.5 EndZ=0
    g41: Circle [constr] CenterX=-4.03109 CenterY=-7 CenterZ=0 NormalX=0 NormalY=0 NormalZ=1 AngleXU=0 Radius=3.5
    g42: LineSegment StartX=4.03109 StartY=-3.5 StartZ=0 EndX=1 EndY=-5.25 EndZ=0
    g43: LineSegment StartX=1 StartY=-5.25 StartZ=0 EndX=1 EndY=-8.75 EndZ=0
    g44: LineSegment StartX=1 StartY=-8.75 StartZ=0 EndX=4.03109 EndY=-10.5 EndZ=0
    g45: LineSegment StartX=4.03109 StartY=-10.5 StartZ=0 EndX=7.06218 EndY=-8.75 EndZ=0
    g46: LineSegment StartX=7.06218 StartY=-8.75 StartZ=0 EndX=7.06218 EndY=-5.25 EndZ=0
    g47: LineSegment StartX=7.06218 StartY=-5.25 StartZ=0 EndX=4.03109 EndY=-3.5 EndZ=0
    g48: Circle [constr] CenterX=4.03109 CenterY=-7 CenterZ=0 NormalX=0 NormalY=0 NormalZ=1 AngleXU=0 Radius=3.5
  constraints (117):
    c: Coincident(g0,g1)
    c: Coincident(g1,g2)
    c: Coincident(g2,g3)
    c: Coincident(g3,g4)
    c: Coincident(g4,g5)
    c: Coincident(g5,g0)
    c: Equal(g0, g1-g5) x5
    c: PointOnObject(g0,g6)
    c: PointOnObject(g1,g6)
    c: PointOnObject(g2,g6)
    c: PointOnObject(g3,g6)
    c: PointOnObject(g4,g6)
    c: PointOnObject(g5,g6)
    c: Coincident(g6,g-1)
    c: Diameter(g6) = 7
    c: PointOnObject(g0,g-2)
    c: Coincident(g7,g8)
    c: Coincident(g8,g9)
    c: Coincident(g9,g10)
    c: Coincident(g10,g11)
    c: Coincident(g11,g12)
    c: Coincident(g12,g7)
    c: Equal(g7, g8-g12) x5
    c: PointOnObject(g7,g13)
    c: PointOnObject(g8,g13)
    c: PointOnObject(g9,g13)
    c: PointOnObject(g10,g13)
    c: PointOnObject(g11,g13)
    c: PointOnObject(g12,g13)
    c: PointOnObject(g13,g-1)
    c: Diameter(g13) = 7
    c: Distance(g6,g13) = 8
    c: Horizontal(g0,g10)
    c: Coincident(g14,g15)
    c: Coincident(g15,g16)
    c: Coincident(g16,g17)
    c: Coincident(g17,g18)
    c: Coincident(g18,g19)
    c: Coincident(g19,g14)
    c: Equal(g14, g15-g19) x5
    c: PointOnObject(g14,g20)
    c: PointOnObject(g15,g20)
    c: PointOnObject(g16,g20)
    c: PointOnObject(g17,g20)
    c: PointOnObject(g18,g20)
    c: PointOnObject(g19,g20)
    c: Diameter(g20) = 7
    c: DistanceY(g-1,g20) = 7
    c: Vertical(g18)
    c: Distance(g17,g-2) = 1
    c: Coincident(g21,g22)
    c: Coincident(g22,g23)
    c: Coincident(g23,g24)
    c: Coincident(g24,g25)
    c: Coincident(g25,g26)
    c: Coincident(g26,g21)
    c: Equal(g21, g22-g26) x5
    c: PointOnObject(g21,g27)
    c: PointOnObject(g22,g27)
    c: PointOnObject(g23,g27)
    c: PointOnObject(g24,g27)
    c: PointOnObject(g25,g27)
    c: PointOnObject(g26,g27)
    c: Diameter(g27) = 7
    c: DistanceY(g-1,g27) = 7
    c: DistanceX(g21,g-1) = 1
    c: Vertical(g21)
    c: Coincident(g28,g29)
    c: Coincident(g29,g30)
    c: Coincident(g30,g31)
    c: Coincident(g31,g32)
    c: Coincident(g32,g33)
    c: Coincident(g33,g28)
    c: Equal(g28, g29-g33) x5
    c: PointOnObject(g28,g34)
    c: PointOnObject(g29,g34)
    c: PointOnObject(g30,g34)
    c: PointOnObject(g31,g34)
    c: PointOnObject(g32,g34)
    c: PointOnObject(g33,g34)
    c: PointOnObject(g34,g-1)
    c: Diameter(g34) = 7
    c: Vertical(g31)
    c: DistanceX(g34,g-1) = 8
    c: Coincident(g35,g36)
    c: Coincident(g36,g37)
    c: Coincident(g37,g38)
    c: Coincident(g38,g39)
    c: Coincident(g39,g40)
    c: Coincident(g40,g35)
    c: Equal(g35, g36-g40) x5
    c: PointOnObject(g35,g41)
    c: PointOnObject(g36,g41)
    c: PointOnObject(g37,g41)
    c: PointOnObject(g38,g41)
    c: PointOnObject(g39,g41)
    c: PointOnObject(g40,g41)
    c: Coincident(g42,g43)
    c: Coincident(g43,g44)
    c: Coincident(g44,g45)
    c: Coincident(g45,g46)
    c: Coincident(g46,g47)
    c: Coincident(g47,g42)
    c: Equal(g42, g43-g47) x5
    c: PointOnObject(g42,g48)
    c: PointOnObject(g43,g48)
    c: PointOnObject(g44,g48)
    c: PointOnObject(g45,g48)
    c: PointOnObject(g46,g48)
    c: PointOnObject(g47,g48)
    c: Equal(g41,g48)
    c: Diameter(g41) = 7
    c: Vertical(g39)
    c: Vertical(g43)
    c: Distance(g-2,g39) = 1
    c: Symmetric(g38,g43,g-2)
    c: Distance(g41,g-1) = 7
FEATURE [Part::Extrusion] Extrude700  label="hex302"
  Base = -> Sketch709
  Dir = (0,-1,2e-16)
  DirMode = 2
  FaceMakerClass = Part::FaceMakerBullseye
  FaceMakerMode = 3
  LengthFwd = 10
  LengthRev = 0
  Placement = pos=(8,0,-56) rot=(0,0,1;0rad)
  Solid = true
  Symmetric = false
FEATURE [Sketcher::SketchObject] Sketch710
  ArcFitTolerance = 1e-06
  FullyConstrained = true
  MakeInternals = false
  Placement = pos=(0,0,0) rot=(1,0,0;1.5708rad)
  sketch-geometry (49):
    g0: LineSegment StartX=1e-16 StartY=3.5 StartZ=0 EndX=-3.03109 EndY=1.75 EndZ=0
    g1: LineSegment StartX=-3.03109 StartY=1.75 StartZ=0 EndX=-3.03109 EndY=-1.75 EndZ=0
    g2: LineSegment StartX=-3.03109 StartY=-1.75 StartZ=0 EndX=-1e-16 EndY=-3.5 EndZ=0
    g3: LineSegment StartX=-1e-16 StartY=-3.5 StartZ=0 EndX=3.03109 EndY=-1.75 EndZ=0
    g4: LineSegment StartX=3.03109 StartY=-1.75 StartZ=0 EndX=3.03109 EndY=1.75 EndZ=0
    g5: LineSegment StartX=3.03109 StartY=1.75 StartZ=0 EndX=1e-16 EndY=3.5 EndZ=0
    g6: Circle [constr] CenterX=0 CenterY=0 CenterZ=0 NormalX=0 NormalY=0 NormalZ=1 AngleXU=0 Radius=3.5
    g7: LineSegment StartX=4.96892 StartY=-1.75002 StartZ=0 EndX=8.00002 EndY=-3.5 EndZ=0
    g8: LineSegment StartX=8.00002 StartY=-3.5 StartZ=0 EndX=11.0311 EndY=-1.74998 EndZ=0
    g9: LineSegment StartX=11.0311 StartY=-1.74998 StartZ=0 EndX=11.0311 EndY=1.75002 EndZ=0
    g10: LineSegment StartX=11.0311 StartY=1.75002 StartZ=0 EndX=7.99998 EndY=3.5 EndZ=0
    g11: LineSegment StartX=7.99998 StartY=3.5 StartZ=0 EndX=4.9689 EndY=1.74998 EndZ=0
    g12: LineSegment StartX=4.9689 StartY=1.74998 StartZ=0 EndX=4.96892 EndY=-1.75002 EndZ=0
    g13: Circle [constr] CenterX=8 CenterY=0 CenterZ=0 NormalX=0 NormalY=0 NormalZ=1 AngleXU=0 Radius=3.5
    g14: LineSegment StartX=4.03109 StartY=3.5 StartZ=0 EndX=7.06218 EndY=5.25 EndZ=0
    g15: LineSegment StartX=7.06218 StartY=5.25 StartZ=0 EndX=7.06218 EndY=8.75 EndZ=0
    g16: LineSegment StartX=7.06218 StartY=8.75 StartZ=0 EndX=4.03109 EndY=10.5 EndZ=0
    g17: LineSegment StartX=4.03109 StartY=10.5 StartZ=0 EndX=1 EndY=8.75 EndZ=0
    g18: LineSegment StartX=1 StartY=8.75 StartZ=0 EndX=1 EndY=5.25 EndZ=0
    g19: LineSegment StartX=1 StartY=5.25 StartZ=0 EndX=4.03109 EndY=3.5 EndZ=0
    g20: Circle [constr] CenterX=4.03109 CenterY=7 CenterZ=0 NormalX=0 NormalY=0 NormalZ=1 AngleXU=0 Radius=3.5
    g21: LineSegment StartX=-1 StartY=5.25 StartZ=0 EndX=-1 EndY=8.75 EndZ=0
    g22: LineSegment StartX=-1 StartY=8.75 StartZ=0 EndX=-4.03109 EndY=10.5 EndZ=0
    g23: LineSegment StartX=-4.03109 StartY=10.5 StartZ=0 EndX=-7.06218 EndY=8.75 EndZ=0
    g24: LineSegment StartX=-7.06218 StartY=8.75 StartZ=0 EndX=-7.06218 EndY=5.25 EndZ=0
    g25: LineSegment StartX=-7.06218 StartY=5.25 StartZ=0 EndX=-4.03109 EndY=3.5 EndZ=0
    g26: LineSegment StartX=-4.03109 StartY=3.5 StartZ=0 EndX=-1 EndY=5.25 EndZ=0
    g27: Circle [constr] CenterX=-4.03109 CenterY=7 CenterZ=0 NormalX=0 NormalY=0 NormalZ=1 AngleXU=0 Radius=3.5
    g28: LineSegment StartX=-4.96891 StartY=-1.75 StartZ=0 EndX=-4.96891 EndY=1.75 EndZ=0
    g29: LineSegment StartX=-4.96891 StartY=1.75 StartZ=0 EndX=-8 EndY=3.5 EndZ=0
    g30: LineSegment StartX=-8 StartY=3.5 StartZ=0 EndX=-11.0311 EndY=1.75 EndZ=0
    g31: LineSegment StartX=-11.0311 StartY=1.75 StartZ=0 EndX=-11.0311 EndY=-1.75 EndZ=0
    g32: LineSegment StartX=-11.0311 StartY=-1.75 StartZ=0 EndX=-8 EndY=-3.5 EndZ=0
    g33: LineSegment StartX=-8 StartY=-3.5 StartZ=0 EndX=-4.96891 EndY=-1.75 EndZ=0
    g34: Circle [constr] CenterX=-8 CenterY=0 CenterZ=0 NormalX=0 NormalY=0 NormalZ=1 AngleXU=0 Radius=3.5
    g35: LineSegment StartX=-4.03109 StartY=-3.5 StartZ=0 EndX=-7.06218 EndY=-5.25 EndZ=0
    g36: LineSegment StartX=-7.06218 StartY=-5.25 StartZ=0 EndX=-7.06218 EndY=-8.75 EndZ=0
    g37: LineSegment StartX=-7.06218 StartY=-8.75 StartZ=0 EndX=-4.03109 EndY=-10.5 EndZ=0
    g38: LineSegment StartX=-4.03109 StartY=-10.5 StartZ=0 EndX=-1 EndY=-8.75 EndZ=0
    g39: LineSegment StartX=-1 StartY=-8.75 StartZ=0 EndX=-1 EndY=-5.25 EndZ=0
    g40: LineSegment StartX=-1 StartY=-5.25 StartZ=0 EndX=-4.03109 EndY=-3.5 EndZ=0
    g41: Circle [constr] CenterX=-4.03109 CenterY=-7 CenterZ=0 NormalX=0 NormalY=0 NormalZ=1 AngleXU=0 Radius=3.5
    g42: LineSegment StartX=4.03109 StartY=-3.5 StartZ=0 EndX=1 EndY=-5.25 EndZ=0
    g43: LineSegment StartX=1 StartY=-5.25 StartZ=0 EndX=1 EndY=-8.75 EndZ=0
    g44: LineSegment StartX=1 StartY=-8.75 StartZ=0 EndX=4.03109 EndY=-10.5 EndZ=0
    g45: LineSegment StartX=4.03109 StartY=-10.5 StartZ=0 EndX=7.06218 EndY=-8.75 EndZ=0
    g46: LineSegment StartX=7.06218 StartY=-8.75 StartZ=0 EndX=7.06218 EndY=-5.25 EndZ=0
    g47: LineSegment StartX=7.06218 StartY=-5.25 StartZ=0 EndX=4.03109 EndY=-3.5 EndZ=0
    g48: Circle [constr] CenterX=4.03109 CenterY=-7 CenterZ=0 NormalX=0 NormalY=0 NormalZ=1 AngleXU=0 Radius=3.5
  constraints (117):
    c: Coincident(g0,g1)
    c: Coincident(g1,g2)
    c: Coincident(g2,g3)
    c: Coincident(g3,g4)
    c: Coincident(g4,g5)
    c: Coincident(g5,g0)
    c: Equal(g0, g1-g5) x5
    c: PointOnObject(g0,g6)
    c: PointOnObject(g1,g6)
    c: PointOnObject(g2,g6)
    c: PointOnObject(g3,g6)
    c: PointOnObject(g4,g6)
    c: PointOnObject(g5,g6)
    c: Coincident(g6,g-1)
    c: Diameter(g6) = 7
    c: PointOnObject(g0,g-2)
    c: Coincident(g7,g8)
    c: Coincident(g8,g9)
    c: Coincident(g9,g10)
    c: Coincident(g10,g11)
    c: Coincident(g11,g12)
    c: Coincident(g12,g7)
    c: Equal(g7, g8-g12) x5
    c: PointOnObject(g7,g13)
    c: PointOnObject(g8,g13)
    c: PointOnObject(g9,g13)
    c: PointOnObject(g10,g13)
    c: PointOnObject(g11,g13)
    c: PointOnObject(g12,g13)
    c: PointOnObject(g13,g-1)
    c: Diameter(g13) = 7
    c: Distance(g6,g13) = 8
    c: Horizontal(g0,g10)
    c: Coincident(g14,g15)
    c: Coincident(g15,g16)
    c: Coincident(g16,g17)
    c: Coincident(g17,g18)
    c: Coincident(g18,g19)
    c: Coincident(g19,g14)
    c: Equal(g14, g15-g19) x5
    c: PointOnObject(g14,g20)
    c: PointOnObject(g15,g20)
    c: PointOnObject(g16,g20)
    c: PointOnObject(g17,g20)
    c: PointOnObject(g18,g20)
    c: PointOnObject(g19,g20)
    c: Diameter(g20) = 7
    c: DistanceY(g-1,g20) = 7
    c: Vertical(g18)
    c: Distance(g17,g-2) = 1
    c: Coincident(g21,g22)
    c: Coincident(g22,g23)
    c: Coincident(g23,g24)
    c: Coincident(g24,g25)
    c: Coincident(g25,g26)
    c: Coincident(g26,g21)
    c: Equal(g21, g22-g26) x5
    c: PointOnObject(g21,g27)
    c: PointOnObject(g22,g27)
    c: PointOnObject(g23,g27)
    c: PointOnObject(g24,g27)
    c: PointOnObject(g25,g27)
    c: PointOnObject(g26,g27)
    c: Diameter(g27) = 7
    c: DistanceY(g-1,g27) = 7
    c: DistanceX(g21,g-1) = 1
    c: Vertical(g21)
    c: Coincident(g28,g29)
    c: Coincident(g29,g30)
    c: Coincident(g30,g31)
    c: Coincident(g31,g32)
    c: Coincident(g32,g33)
    c: Coincident(g33,g28)
    c: Equal(g28, g29-g33) x5
    c: PointOnObject(g28,g34)
    c: PointOnObject(g29,g34)
    c: PointOnObject(g30,g34)
    c: PointOnObject(g31,g34)
    c: PointOnObject(g32,g34)
    c: PointOnObject(g33,g34)
    c: PointOnObject(g34,g-1)
    c: Diameter(g34) = 7
    c: Vertical(g31)
    c: DistanceX(g34,g-1) = 8
    c: Coincident(g35,g36)
    c: Coincident(g36,g37)
    c: Coincident(g37,g38)
    c: Coincident(g38,g39)
    c: Coincident(g39,g40)
    c: Coincident(g40,g35)
    c: Equal(g35, g36-g40) x5
    c: PointOnObject(g35,g41)
    c: PointOnObject(g36,g41)
    c: PointOnObject(g37,g41)
    c: PointOnObject(g38,g41)
    c: PointOnObject(g39,g41)
    c: PointOnObject(g40,g41)
    c: Coincident(g42,g43)
    c: Coincident(g43,g44)
    c: Coincident(g44,g45)
    c: Coincident(g45,g46)
    c: Coincident(g46,g47)
    c: Coincident(g47,g42)
    c: Equal(g42, g43-g47) x5
    c: PointOnObject(g42,g48)
    c: PointOnObject(g43,g48)
    c: PointOnObject(g44,g48)
    c: PointOnObject(g45,g48)
    c: PointOnObject(g46,g48)
    c: PointOnObject(g47,g48)
    c: Equal(g41,g48)
    c: Diameter(g41) = 7
    c: Vertical(g39)
    c: Vertical(g43)
    c: Distance(g-2,g39) = 1
    c: Symmetric(g38,g43,g-2)
    c: Distance(g41,g-1) = 7
FEATURE [Part::Extrusion] Extrude701  label="hex303"
  Base = -> Sketch710
  Dir = (0,-1,2e-16)
  DirMode = 2
  FaceMakerClass = Part::FaceMakerBullseye
  FaceMakerMode = 3
  LengthFwd = 10
  LengthRev = 0
  Placement = pos=(28,0,-49) rot=(0,0,1;0rad)
  Solid = true
  Symmetric = false
FEATURE [Sketcher::SketchObject] Sketch711
  ArcFitTolerance = 1e-06
  FullyConstrained = true
  MakeInternals = false
  Placement = pos=(0,0,0) rot=(1,0,0;1.5708rad)
  sketch-geometry (49):
    g0: LineSegment StartX=1e-16 StartY=3.5 StartZ=0 EndX=-3.03109 EndY=1.75 EndZ=0
    g1: LineSegment StartX=-3.03109 StartY=1.75 StartZ=0 EndX=-3.03109 EndY=-1.75 EndZ=0
    g2: LineSegment StartX=-3.03109 StartY=-1.75 StartZ=0 EndX=-1e-16 EndY=-3.5 EndZ=0
    g3: LineSegment StartX=-1e-16 StartY=-3.5 StartZ=0 EndX=3.03109 EndY=-1.75 EndZ=0
    g4: LineSegment StartX=3.03109 StartY=-1.75 StartZ=0 EndX=3.03109 EndY=1.75 EndZ=0
    g5: LineSegment StartX=3.03109 StartY=1.75 StartZ=0 EndX=1e-16 EndY=3.5 EndZ=0
    g6: Circle [constr] CenterX=0 CenterY=0 CenterZ=0 NormalX=0 NormalY=0 NormalZ=1 AngleXU=0 Radius=3.5
    g7: LineSegment StartX=4.96892 StartY=-1.75002 StartZ=0 EndX=8.00002 EndY=-3.5 EndZ=0
    g8: LineSegment StartX=8.00002 StartY=-3.5 StartZ=0 EndX=11.0311 EndY=-1.74998 EndZ=0
    g9: LineSegment StartX=11.0311 StartY=-1.74998 StartZ=0 EndX=11.0311 EndY=1.75002 EndZ=0
    g10: LineSegment StartX=11.0311 StartY=1.75002 StartZ=0 EndX=7.99998 EndY=3.5 EndZ=0
    g11: LineSegment StartX=7.99998 StartY=3.5 StartZ=0 EndX=4.9689 EndY=1.74998 EndZ=0
    g12: LineSegment StartX=4.9689 StartY=1.74998 StartZ=0 EndX=4.96892 EndY=-1.75002 EndZ=0
    g13: Circle [constr] CenterX=8 CenterY=0 CenterZ=0 NormalX=0 NormalY=0 NormalZ=1 AngleXU=0 Radius=3.5
    g14: LineSegment StartX=4.03109 StartY=3.5 StartZ=0 EndX=7.06218 EndY=5.25 EndZ=0
    g15: LineSegment StartX=7.06218 StartY=5.25 StartZ=0 EndX=7.06218 EndY=8.75 EndZ=0
    g16: LineSegment StartX=7.06218 StartY=8.75 StartZ=0 EndX=4.03109 EndY=10.5 EndZ=0
    g17: LineSegment StartX=4.03109 StartY=10.5 StartZ=0 EndX=1 EndY=8.75 EndZ=0
    g18: LineSegment StartX=1 StartY=8.75 StartZ=0 EndX=1 EndY=5.25 EndZ=0
    g19: LineSegment StartX=1 StartY=5.25 StartZ=0 EndX=4.03109 EndY=3.5 EndZ=0
    g20: Circle [constr] CenterX=4.03109 CenterY=7 CenterZ=0 NormalX=0 NormalY=0 NormalZ=1 AngleXU=0 Radius=3.5
    g21: LineSegment StartX=-1 StartY=5.25 StartZ=0 EndX=-1 EndY=8.75 EndZ=0
    g22: LineSegment StartX=-1 StartY=8.75 StartZ=0 EndX=-4.03109 EndY=10.5 EndZ=0
    g23: LineSegment StartX=-4.03109 StartY=10.5 StartZ=0 EndX=-7.06218 EndY=8.75 EndZ=0
    g24: LineSegment StartX=-7.06218 StartY=8.75 StartZ=0 EndX=-7.06218 EndY=5.25 EndZ=0
    g25: LineSegment StartX=-7.06218 StartY=5.25 StartZ=0 EndX=-4.03109 EndY=3.5 EndZ=0
    g26: LineSegment StartX=-4.03109 StartY=3.5 StartZ=0 EndX=-1 EndY=5.25 EndZ=0
    g27: Circle [constr] CenterX=-4.03109 CenterY=7 CenterZ=0 NormalX=0 NormalY=0 NormalZ=1 AngleXU=0 Radius=3.5
    g28: LineSegment StartX=-4.96891 StartY=-1.75 StartZ=0 EndX=-4.96891 EndY=1.75 EndZ=0
    g29: LineSegment StartX=-4.96891 StartY=1.75 StartZ=0 EndX=-8 EndY=3.5 EndZ=0
    g30: LineSegment StartX=-8 StartY=3.5 StartZ=0 EndX=-11.0311 EndY=1.75 EndZ=0
    g31: LineSegment StartX=-11.0311 StartY=1.75 StartZ=0 EndX=-11.0311 EndY=-1.75 EndZ=0
    g32: LineSegment StartX=-11.0311 StartY=-1.75 StartZ=0 EndX=-8 EndY=-3.5 EndZ=0
    g33: LineSegment StartX=-8 StartY=-3.5 StartZ=0 EndX=-4.96891 EndY=-1.75 EndZ=0
    g34: Circle [constr] CenterX=-8 CenterY=0 CenterZ=0 NormalX=0 NormalY=0 NormalZ=1 AngleXU=0 Radius=3.5
    g35: LineSegment StartX=-4.03109 StartY=-3.5 StartZ=0 EndX=-7.06218 EndY=-5.25 EndZ=0
    g36: LineSegment StartX=-7.06218 StartY=-5.25 StartZ=0 EndX=-7.06218 EndY=-8.75 EndZ=0
    g37: LineSegment StartX=-7.06218 StartY=-8.75 StartZ=0 EndX=-4.03109 EndY=-10.5 EndZ=0
    g38: LineSegment StartX=-4.03109 StartY=-10.5 StartZ=0 EndX=-1 EndY=-8.75 EndZ=0
    g39: LineSegment StartX=-1 StartY=-8.75 StartZ=0 EndX=-1 EndY=-5.25 EndZ=0
    g40: LineSegment StartX=-1 StartY=-5.25 StartZ=0 EndX=-4.03109 EndY=-3.5 EndZ=0
    g41: Circle [constr] CenterX=-4.03109 CenterY=-7 CenterZ=0 NormalX=0 NormalY=0 NormalZ=1 AngleXU=0 Radius=3.5
    g42: LineSegment StartX=4.03109 StartY=-3.5 StartZ=0 EndX=1 EndY=-5.25 EndZ=0
    g43: LineSegment StartX=1 StartY=-5.25 StartZ=0 EndX=1 EndY=-8.75 EndZ=0
    g44: LineSegment StartX=1 StartY=-8.75 StartZ=0 EndX=4.03109 EndY=-10.5 EndZ=0
    g45: LineSegment StartX=4.03109 StartY=-10.5 StartZ=0 EndX=7.06218 EndY=-8.75 EndZ=0
    g46: LineSegment StartX=7.06218 StartY=-8.75 StartZ=0 EndX=7.06218 EndY=-5.25 EndZ=0
    g47: LineSegment StartX=7.06218 StartY=-5.25 StartZ=0 EndX=4.03109 EndY=-3.5 EndZ=0
    g48: Circle [constr] CenterX=4.03109 CenterY=-7 CenterZ=0 NormalX=0 NormalY=0 NormalZ=1 AngleXU=0 Radius=3.5
  constraints (117):
    c: Coincident(g0,g1)
    c: Coincident(g1,g2)
    c: Coincident(g2,g3)
    c: Coincident(g3,g4)
    c: Coincident(g4,g5)
    c: Coincident(g5,g0)
    c: Equal(g0, g1-g5) x5
    c: PointOnObject(g0,g6)
    c: PointOnObject(g1,g6)
    c: PointOnObject(g2,g6)
    c: PointOnObject(g3,g6)
    c: PointOnObject(g4,g6)
    c: PointOnObject(g5,g6)
    c: Coincident(g6,g-1)
    c: Diameter(g6) = 7
    c: PointOnObject(g0,g-2)
    c: Coincident(g7,g8)
    c: Coincident(g8,g9)
    c: Coincident(g9,g10)
    c: Coincident(g10,g11)
    c: Coincident(g11,g12)
    c: Coincident(g12,g7)
    c: Equal(g7, g8-g12) x5
    c: PointOnObject(g7,g13)
    c: PointOnObject(g8,g13)
    c: PointOnObject(g9,g13)
    c: PointOnObject(g10,g13)
    c: PointOnObject(g11,g13)
    c: PointOnObject(g12,g13)
    c: PointOnObject(g13,g-1)
    c: Diameter(g13) = 7
    c: Distance(g6,g13) = 8
    c: Horizontal(g0,g10)
    c: Coincident(g14,g15)
    c: Coincident(g15,g16)
    c: Coincident(g16,g17)
    c: Coincident(g17,g18)
    c: Coincident(g18,g19)
    c: Coincident(g19,g14)
    c: Equal(g14, g15-g19) x5
    c: PointOnObject(g14,g20)
    c: PointOnObject(g15,g20)
    c: PointOnObject(g16,g20)
    c: PointOnObject(g17,g20)
    c: PointOnObject(g18,g20)
    c: PointOnObject(g19,g20)
    c: Diameter(g20) = 7
    c: DistanceY(g-1,g20) = 7
    c: Vertical(g18)
    c: Distance(g17,g-2) = 1
    c: Coincident(g21,g22)
    c: Coincident(g22,g23)
    c: Coincident(g23,g24)
    c: Coincident(g24,g25)
    c: Coincident(g25,g26)
    c: Coincident(g26,g21)
    c: Equal(g21, g22-g26) x5
    c: PointOnObject(g21,g27)
    c: PointOnObject(g22,g27)
    c: PointOnObject(g23,g27)
    c: PointOnObject(g24,g27)
    c: PointOnObject(g25,g27)
    c: PointOnObject(g26,g27)
    c: Diameter(g27) = 7
    c: DistanceY(g-1,g27) = 7
    c: DistanceX(g21,g-1) = 1
    c: Vertical(g21)
    c: Coincident(g28,g29)
    c: Coincident(g29,g30)
    c: Coincident(g30,g31)
    c: Coincident(g31,g32)
    c: Coincident(g32,g33)
    c: Coincident(g33,g28)
    c: Equal(g28, g29-g33) x5
    c: PointOnObject(g28,g34)
    c: PointOnObject(g29,g34)
    c: PointOnObject(g30,g34)
    c: PointOnObject(g31,g34)
    c: PointOnObject(g32,g34)
    c: PointOnObject(g33,g34)
    c: PointOnObject(g34,g-1)
    c: Diameter(g34) = 7
    c: Vertical(g31)
    c: DistanceX(g34,g-1) = 8
    c: Coincident(g35,g36)
    c: Coincident(g36,g37)
    c: Coincident(g37,g38)
    c: Coincident(g38,g39)
    c: Coincident(g39,g40)
    c: Coincident(g40,g35)
    c: Equal(g35, g36-g40) x5
    c: PointOnObject(g35,g41)
    c: PointOnObject(g36,g41)
    c: PointOnObject(g37,g41)
    c: PointOnObject(g38,g41)
    c: PointOnObject(g39,g41)
    c: PointOnObject(g40,g41)
    c: Coincident(g42,g43)
    c: Coincident(g43,g44)
    c: Coincident(g44,g45)
    c: Coincident(g45,g46)
    c: Coincident(g46,g47)
    c: Coincident(g47,g42)
    c: Equal(g42, g43-g47) x5
    c: PointOnObject(g42,g48)
    c: PointOnObject(g43,g48)
    c: PointOnObject(g44,g48)
    c: PointOnObject(g45,g48)
    c: PointOnObject(g46,g48)
    c: PointOnObject(g47,g48)
    c: Equal(g41,g48)
    c: Diameter(g41) = 7
    c: Vertical(g39)
    c: Vertical(g43)
    c: Distance(g-2,g39) = 1
    c: Symmetric(g38,g43,g-2)
    c: Distance(g41,g-1) = 7
FEATURE [Part::Extrusion] Extrude702  label="hex304"
  Base = -> Sketch711
  Dir = (0,-1,2e-16)
  DirMode = 2
  FaceMakerClass = Part::FaceMakerBullseye
  FaceMakerMode = 3
  LengthFwd = 10
  LengthRev = 0
  Placement = pos=(48,0,-42) rot=(0,0,1;0rad)
  Solid = true
  Symmetric = false
FEATURE [Sketcher::SketchObject] Sketch712
  ArcFitTolerance = 1e-06
  FullyConstrained = true
  MakeInternals = false
  Placement = pos=(0,0,0) rot=(1,0,0;1.5708rad)
  sketch-geometry (49):
    g0: LineSegment StartX=1e-16 StartY=3.5 StartZ=0 EndX=-3.03109 EndY=1.75 EndZ=0
    g1: LineSegment StartX=-3.03109 StartY=1.75 StartZ=0 EndX=-3.03109 EndY=-1.75 EndZ=0
    g2: LineSegment StartX=-3.03109 StartY=-1.75 StartZ=0 EndX=-1e-16 EndY=-3.5 EndZ=0
    g3: LineSegment StartX=-1e-16 StartY=-3.5 StartZ=0 EndX=3.03109 EndY=-1.75 EndZ=0
    g4: LineSegment StartX=3.03109 StartY=-1.75 StartZ=0 EndX=3.03109 EndY=1.75 EndZ=0
    g5: LineSegment StartX=3.03109 StartY=1.75 StartZ=0 EndX=1e-16 EndY=3.5 EndZ=0
    g6: Circle [constr] CenterX=0 CenterY=0 CenterZ=0 NormalX=0 NormalY=0 NormalZ=1 AngleXU=0 Radius=3.5
    g7: LineSegment StartX=4.96892 StartY=-1.75002 StartZ=0 EndX=8.00002 EndY=-3.5 EndZ=0
    g8: LineSegment StartX=8.00002 StartY=-3.5 StartZ=0 EndX=11.0311 EndY=-1.74998 EndZ=0
    g9: LineSegment StartX=11.0311 StartY=-1.74998 StartZ=0 EndX=11.0311 EndY=1.75002 EndZ=0
    g10: LineSegment StartX=11.0311 StartY=1.75002 StartZ=0 EndX=7.99998 EndY=3.5 EndZ=0
    g11: LineSegment StartX=7.99998 StartY=3.5 StartZ=0 EndX=4.9689 EndY=1.74998 EndZ=0
    g12: LineSegment StartX=4.9689 StartY=1.74998 StartZ=0 EndX=4.96892 EndY=-1.75002 EndZ=0
    g13: Circle [constr] CenterX=8 CenterY=0 CenterZ=0 NormalX=0 NormalY=0 NormalZ=1 AngleXU=0 Radius=3.5
    g14: LineSegment StartX=4.03109 StartY=3.5 StartZ=0 EndX=7.06218 EndY=5.25 EndZ=0
    g15: LineSegment StartX=7.06218 StartY=5.25 StartZ=0 EndX=7.06218 EndY=8.75 EndZ=0
    g16: LineSegment StartX=7.06218 StartY=8.75 StartZ=0 EndX=4.03109 EndY=10.5 EndZ=0
    g17: LineSegment StartX=4.03109 StartY=10.5 StartZ=0 EndX=1 EndY=8.75 EndZ=0
    g18: LineSegment StartX=1 StartY=8.75 StartZ=0 EndX=1 EndY=5.25 EndZ=0
    g19: LineSegment StartX=1 StartY=5.25 StartZ=0 EndX=4.03109 EndY=3.5 EndZ=0
    g20: Circle [constr] CenterX=4.03109 CenterY=7 CenterZ=0 NormalX=0 NormalY=0 NormalZ=1 AngleXU=0 Radius=3.5
    g21: LineSegment StartX=-1 StartY=5.25 StartZ=0 EndX=-1 EndY=8.75 EndZ=0
    g22: LineSegment StartX=-1 StartY=8.75 StartZ=0 EndX=-4.03109 EndY=10.5 EndZ=0
    g23: LineSegment StartX=-4.03109 StartY=10.5 StartZ=0 EndX=-7.06218 EndY=8.75 EndZ=0
    g24: LineSegment StartX=-7.06218 StartY=8.75 StartZ=0 EndX=-7.06218 EndY=5.25 EndZ=0
    g25: LineSegment StartX=-7.06218 StartY=5.25 StartZ=0 EndX=-4.03109 EndY=3.5 EndZ=0
    g26: LineSegment StartX=-4.03109 StartY=3.5 StartZ=0 EndX=-1 EndY=5.25 EndZ=0
    g27: Circle [constr] CenterX=-4.03109 CenterY=7 CenterZ=0 NormalX=0 NormalY=0 NormalZ=1 AngleXU=0 Radius=3.5
    g28: LineSegment StartX=-4.96891 StartY=-1.75 StartZ=0 EndX=-4.96891 EndY=1.75 EndZ=0
    g29: LineSegment StartX=-4.96891 StartY=1.75 StartZ=0 EndX=-8 EndY=3.5 EndZ=0
    g30: LineSegment StartX=-8 StartY=3.5 StartZ=0 EndX=-11.0311 EndY=1.75 EndZ=0
    g31: LineSegment StartX=-11.0311 StartY=1.75 StartZ=0 EndX=-11.0311 EndY=-1.75 EndZ=0
    g32: LineSegment StartX=-11.0311 StartY=-1.75 StartZ=0 EndX=-8 EndY=-3.5 EndZ=0
    g33: LineSegment StartX=-8 StartY=-3.5 StartZ=0 EndX=-4.96891 EndY=-1.75 EndZ=0
    g34: Circle [constr] CenterX=-8 CenterY=0 CenterZ=0 NormalX=0 NormalY=0 NormalZ=1 AngleXU=0 Radius=3.5
    g35: LineSegment StartX=-4.03109 StartY=-3.5 StartZ=0 EndX=-7.06218 EndY=-5.25 EndZ=0
    g36: LineSegment StartX=-7.06218 StartY=-5.25 StartZ=0 EndX=-7.06218 EndY=-8.75 EndZ=0
    g37: LineSegment StartX=-7.06218 StartY=-8.75 StartZ=0 EndX=-4.03109 EndY=-10.5 EndZ=0
    g38: LineSegment StartX=-4.03109 StartY=-10.5 StartZ=0 EndX=-1 EndY=-8.75 EndZ=0
    g39: LineSegment StartX=-1 StartY=-8.75 StartZ=0 EndX=-1 EndY=-5.25 EndZ=0
    g40: LineSegment StartX=-1 StartY=-5.25 StartZ=0 EndX=-4.03109 EndY=-3.5 EndZ=0
    g41: Circle [constr] CenterX=-4.03109 CenterY=-7 CenterZ=0 NormalX=0 NormalY=0 NormalZ=1 AngleXU=0 Radius=3.5
    g42: LineSegment StartX=4.03109 StartY=-3.5 StartZ=0 EndX=1 EndY=-5.25 EndZ=0
    g43: LineSegment StartX=1 StartY=-5.25 StartZ=0 EndX=1 EndY=-8.75 EndZ=0
    g44: LineSegment StartX=1 StartY=-8.75 StartZ=0 EndX=4.03109 EndY=-10.5 EndZ=0
    g45: LineSegment StartX=4.03109 StartY=-10.5 StartZ=0 EndX=7.06218 EndY=-8.75 EndZ=0
    g46: LineSegment StartX=7.06218 StartY=-8.75 StartZ=0 EndX=7.06218 EndY=-5.25 EndZ=0
    g47: LineSegment StartX=7.06218 StartY=-5.25 StartZ=0 EndX=4.03109 EndY=-3.5 EndZ=0
    g48: Circle [constr] CenterX=4.03109 CenterY=-7 CenterZ=0 NormalX=0 NormalY=0 NormalZ=1 AngleXU=0 Radius=3.5
  constraints (117):
    c: Coincident(g0,g1)
    c: Coincident(g1,g2)
    c: Coincident(g2,g3)
    c: Coincident(g3,g4)
    c: Coincident(g4,g5)
    c: Coincident(g5,g0)
    c: Equal(g0, g1-g5) x5
    c: PointOnObject(g0,g6)
    c: PointOnObject(g1,g6)
    c: PointOnObject(g2,g6)
    c: PointOnObject(g3,g6)
    c: PointOnObject(g4,g6)
    c: PointOnObject(g5,g6)
    c: Coincident(g6,g-1)
    c: Diameter(g6) = 7
    c: PointOnObject(g0,g-2)
    c: Coincident(g7,g8)
    c: Coincident(g8,g9)
    c: Coincident(g9,g10)
    c: Coincident(g10,g11)
    c: Coincident(g11,g12)
    c: Coincident(g12,g7)
    c: Equal(g7, g8-g12) x5
    c: PointOnObject(g7,g13)
    c: PointOnObject(g8,g13)
    c: PointOnObject(g9,g13)
    c: PointOnObject(g10,g13)
    c: PointOnObject(g11,g13)
    c: PointOnObject(g12,g13)
    c: PointOnObject(g13,g-1)
    c: Diameter(g13) = 7
    c: Distance(g6,g13) = 8
    c: Horizontal(g0,g10)
    c: Coincident(g14,g15)
    c: Coincident(g15,g16)
    c: Coincident(g16,g17)
    c: Coincident(g17,g18)
    c: Coincident(g18,g19)
    c: Coincident(g19,g14)
    c: Equal(g14, g15-g19) x5
    c: PointOnObject(g14,g20)
    c: PointOnObject(g15,g20)
    c: PointOnObject(g16,g20)
    c: PointOnObject(g17,g20)
    c: PointOnObject(g18,g20)
    c: PointOnObject(g19,g20)
    c: Diameter(g20) = 7
    c: DistanceY(g-1,g20) = 7
    c: Vertical(g18)
    c: Distance(g17,g-2) = 1
    c: Coincident(g21,g22)
    c: Coincident(g22,g23)
    c: Coincident(g23,g24)
    c: Coincident(g24,g25)
    c: Coincident(g25,g26)
    c: Coincident(g26,g21)
    c: Equal(g21, g22-g26) x5
    c: PointOnObject(g21,g27)
    c: PointOnObject(g22,g27)
    c: PointOnObject(g23,g27)
    c: PointOnObject(g24,g27)
    c: PointOnObject(g25,g27)
    c: PointOnObject(g26,g27)
    c: Diameter(g27) = 7
    c: DistanceY(g-1,g27) = 7
    c: DistanceX(g21,g-1) = 1
    c: Vertical(g21)
    c: Coincident(g28,g29)
    c: Coincident(g29,g30)
    c: Coincident(g30,g31)
    c: Coincident(g31,g32)
    c: Coincident(g32,g33)
    c: Coincident(g33,g28)
    c: Equal(g28, g29-g33) x5
    c: PointOnObject(g28,g34)
    c: PointOnObject(g29,g34)
    c: PointOnObject(g30,g34)
    c: PointOnObject(g31,g34)
    c: PointOnObject(g32,g34)
    c: PointOnObject(g33,g34)
    c: PointOnObject(g34,g-1)
    c: Diameter(g34) = 7
    c: Vertical(g31)
    c: DistanceX(g34,g-1) = 8
    c: Coincident(g35,g36)
    c: Coincident(g36,g37)
    c: Coincident(g37,g38)
    c: Coincident(g38,g39)
    c: Coincident(g39,g40)
    c: Coincident(g40,g35)
    c: Equal(g35, g36-g40) x5
    c: PointOnObject(g35,g41)
    c: PointOnObject(g36,g41)
    c: PointOnObject(g37,g41)
    c: PointOnObject(g38,g41)
    c: PointOnObject(g39,g41)
    c: PointOnObject(g40,g41)
    c: Coincident(g42,g43)
    c: Coincident(g43,g44)
    c: Coincident(g44,g45)
    c: Coincident(g45,g46)
    c: Coincident(g46,g47)
    c: Coincident(g47,g42)
    c: Equal(g42, g43-g47) x5
    c: PointOnObject(g42,g48)
    c: PointOnObject(g43,g48)
    c: PointOnObject(g44,g48)
    c: PointOnObject(g45,g48)
    c: PointOnObject(g46,g48)
    c: PointOnObject(g47,g48)
    c: Equal(g41,g48)
    c: Diameter(g41) = 7
    c: Vertical(g39)
    c: Vertical(g43)
    c: Distance(g-2,g39) = 1
    c: Symmetric(g38,g43,g-2)
    c: Distance(g41,g-1) = 7
FEATURE [Part::Extrusion] Extrude703  label="hex305"
  Base = -> Sketch712
  Dir = (0,-1,2e-16)
  DirMode = 2
  FaceMakerClass = Part::FaceMakerBullseye
  FaceMakerMode = 3
  LengthFwd = 10
  LengthRev = 0
  Placement = pos=(68,0,-35) rot=(0,0,1;0rad)
  Solid = true
  Symmetric = false
FEATURE [Sketcher::SketchObject] Sketch713
  ArcFitTolerance = 1e-06
  FullyConstrained = true
  MakeInternals = false
  Placement = pos=(0,0,0) rot=(1,0,0;1.5708rad)
  sketch-geometry (49):
    g0: LineSegment StartX=1e-16 StartY=3.5 StartZ=0 EndX=-3.03109 EndY=1.75 EndZ=0
    g1: LineSegment StartX=-3.03109 StartY=1.75 StartZ=0 EndX=-3.03109 EndY=-1.75 EndZ=0
    g2: LineSegment StartX=-3.03109 StartY=-1.75 StartZ=0 EndX=-1e-16 EndY=-3.5 EndZ=0
    g3: LineSegment StartX=-1e-16 StartY=-3.5 StartZ=0 EndX=3.03109 EndY=-1.75 EndZ=0
    g4: LineSegment StartX=3.03109 StartY=-1.75 StartZ=0 EndX=3.03109 EndY=1.75 EndZ=0
    g5: LineSegment StartX=3.03109 StartY=1.75 StartZ=0 EndX=1e-16 EndY=3.5 EndZ=0
    g6: Circle [constr] CenterX=0 CenterY=0 CenterZ=0 NormalX=0 NormalY=0 NormalZ=1 AngleXU=0 Radius=3.5
    g7: LineSegment StartX=4.96892 StartY=-1.75002 StartZ=0 EndX=8.00002 EndY=-3.5 EndZ=0
    g8: LineSegment StartX=8.00002 StartY=-3.5 StartZ=0 EndX=11.0311 EndY=-1.74998 EndZ=0
    g9: LineSegment StartX=11.0311 StartY=-1.74998 StartZ=0 EndX=11.0311 EndY=1.75002 EndZ=0
    g10: LineSegment StartX=11.0311 StartY=1.75002 StartZ=0 EndX=7.99998 EndY=3.5 EndZ=0
    g11: LineSegment StartX=7.99998 StartY=3.5 StartZ=0 EndX=4.9689 EndY=1.74998 EndZ=0
    g12: LineSegment StartX=4.9689 StartY=1.74998 StartZ=0 EndX=4.96892 EndY=-1.75002 EndZ=0
    g13: Circle [constr] CenterX=8 CenterY=0 CenterZ=0 NormalX=0 NormalY=0 NormalZ=1 AngleXU=0 Radius=3.5
    g14: LineSegment StartX=4.03109 StartY=3.5 StartZ=0 EndX=7.06218 EndY=5.25 EndZ=0
    g15: LineSegment StartX=7.06218 StartY=5.25 StartZ=0 EndX=7.06218 EndY=8.75 EndZ=0
    g16: LineSegment StartX=7.06218 StartY=8.75 StartZ=0 EndX=4.03109 EndY=10.5 EndZ=0
    g17: LineSegment StartX=4.03109 StartY=10.5 StartZ=0 EndX=1 EndY=8.75 EndZ=0
    g18: LineSegment StartX=1 StartY=8.75 StartZ=0 EndX=1 EndY=5.25 EndZ=0
    g19: LineSegment StartX=1 StartY=5.25 StartZ=0 EndX=4.03109 EndY=3.5 EndZ=0
    g20: Circle [constr] CenterX=4.03109 CenterY=7 CenterZ=0 NormalX=0 NormalY=0 NormalZ=1 AngleXU=0 Radius=3.5
    g21: LineSegment StartX=-1 StartY=5.25 StartZ=0 EndX=-1 EndY=8.75 EndZ=0
    g22: LineSegment StartX=-1 StartY=8.75 StartZ=0 EndX=-4.03109 EndY=10.5 EndZ=0
    g23: LineSegment StartX=-4.03109 StartY=10.5 StartZ=0 EndX=-7.06218 EndY=8.75 EndZ=0
    g24: LineSegment StartX=-7.06218 StartY=8.75 StartZ=0 EndX=-7.06218 EndY=5.25 EndZ=0
    g25: LineSegment StartX=-7.06218 StartY=5.25 StartZ=0 EndX=-4.03109 EndY=3.5 EndZ=0
    g26: LineSegment StartX=-4.03109 StartY=3.5 StartZ=0 EndX=-1 EndY=5.25 EndZ=0
    g27: Circle [constr] CenterX=-4.03109 CenterY=7 CenterZ=0 NormalX=0 NormalY=0 NormalZ=1 AngleXU=0 Radius=3.5
    g28: LineSegment StartX=-4.96891 StartY=-1.75 StartZ=0 EndX=-4.96891 EndY=1.75 EndZ=0
    g29: LineSegment StartX=-4.96891 StartY=1.75 StartZ=0 EndX=-8 EndY=3.5 EndZ=0
    g30: LineSegment StartX=-8 StartY=3.5 StartZ=0 EndX=-11.0311 EndY=1.75 EndZ=0
    g31: LineSegment StartX=-11.0311 StartY=1.75 StartZ=0 EndX=-11.0311 EndY=-1.75 EndZ=0
    g32: LineSegment StartX=-11.0311 StartY=-1.75 StartZ=0 EndX=-8 EndY=-3.5 EndZ=0
    g33: LineSegment StartX=-8 StartY=-3.5 StartZ=0 EndX=-4.96891 EndY=-1.75 EndZ=0
    g34: Circle [constr] CenterX=-8 CenterY=0 CenterZ=0 NormalX=0 NormalY=0 NormalZ=1 AngleXU=0 Radius=3.5
    g35: LineSegment StartX=-4.03109 StartY=-3.5 StartZ=0 EndX=-7.06218 EndY=-5.25 EndZ=0
    g36: LineSegment StartX=-7.06218 StartY=-5.25 StartZ=0 EndX=-7.06218 EndY=-8.75 EndZ=0
    g37: LineSegment StartX=-7.06218 StartY=-8.75 StartZ=0 EndX=-4.03109 EndY=-10.5 EndZ=0
    g38: LineSegment StartX=-4.03109 StartY=-10.5 StartZ=0 EndX=-1 EndY=-8.75 EndZ=0
    g39: LineSegment StartX=-1 StartY=-8.75 StartZ=0 EndX=-1 EndY=-5.25 EndZ=0
    g40: LineSegment StartX=-1 StartY=-5.25 StartZ=0 EndX=-4.03109 EndY=-3.5 EndZ=0
    g41: Circle [constr] CenterX=-4.03109 CenterY=-7 CenterZ=0 NormalX=0 NormalY=0 NormalZ=1 AngleXU=0 Radius=3.5
    g42: LineSegment StartX=4.03109 StartY=-3.5 StartZ=0 EndX=1 EndY=-5.25 EndZ=0
    g43: LineSegment StartX=1 StartY=-5.25 StartZ=0 EndX=1 EndY=-8.75 EndZ=0
    g44: LineSegment StartX=1 StartY=-8.75 StartZ=0 EndX=4.03109 EndY=-10.5 EndZ=0
    g45: LineSegment StartX=4.03109 StartY=-10.5 StartZ=0 EndX=7.06218 EndY=-8.75 EndZ=0
    g46: LineSegment StartX=7.06218 StartY=-8.75 StartZ=0 EndX=7.06218 EndY=-5.25 EndZ=0
    g47: LineSegment StartX=7.06218 StartY=-5.25 StartZ=0 EndX=4.03109 EndY=-3.5 EndZ=0
    g48: Circle [constr] CenterX=4.03109 CenterY=-7 CenterZ=0 NormalX=0 NormalY=0 NormalZ=1 AngleXU=0 Radius=3.5
  constraints (117):
    c: Coincident(g0,g1)
    c: Coincident(g1,g2)
    c: Coincident(g2,g3)
    c: Coincident(g3,g4)
    c: Coincident(g4,g5)
    c: Coincident(g5,g0)
    c: Equal(g0, g1-g5) x5
    c: PointOnObject(g0,g6)
    c: PointOnObject(g1,g6)
    c: PointOnObject(g2,g6)
    c: PointOnObject(g3,g6)
    c: PointOnObject(g4,g6)
    c: PointOnObject(g5,g6)
    c: Coincident(g6,g-1)
    c: Diameter(g6) = 7
    c: PointOnObject(g0,g-2)
    c: Coincident(g7,g8)
    c: Coincident(g8,g9)
    c: Coincident(g9,g10)
    c: Coincident(g10,g11)
    c: Coincident(g11,g12)
    c: Coincident(g12,g7)
    c: Equal(g7, g8-g12) x5
    c: PointOnObject(g7,g13)
    c: PointOnObject(g8,g13)
    c: PointOnObject(g9,g13)
    c: PointOnObject(g10,g13)
    c: PointOnObject(g11,g13)
    c: PointOnObject(g12,g13)
    c: PointOnObject(g13,g-1)
    c: Diameter(g13) = 7
    c: Distance(g6,g13) = 8
    c: Horizontal(g0,g10)
    c: Coincident(g14,g15)
    c: Coincident(g15,g16)
    c: Coincident(g16,g17)
    c: Coincident(g17,g18)
    c: Coincident(g18,g19)
    c: Coincident(g19,g14)
    c: Equal(g14, g15-g19) x5
    c: PointOnObject(g14,g20)
    c: PointOnObject(g15,g20)
    c: PointOnObject(g16,g20)
    c: PointOnObject(g17,g20)
    c: PointOnObject(g18,g20)
    c: PointOnObject(g19,g20)
    c: Diameter(g20) = 7
    c: DistanceY(g-1,g20) = 7
    c: Vertical(g18)
    c: Distance(g17,g-2) = 1
    c: Coincident(g21,g22)
    c: Coincident(g22,g23)
    c: Coincident(g23,g24)
    c: Coincident(g24,g25)
    c: Coincident(g25,g26)
    c: Coincident(g26,g21)
    c: Equal(g21, g22-g26) x5
    c: PointOnObject(g21,g27)
    c: PointOnObject(g22,g27)
    c: PointOnObject(g23,g27)
    c: PointOnObject(g24,g27)
    c: PointOnObject(g25,g27)
    c: PointOnObject(g26,g27)
    c: Diameter(g27) = 7
    c: DistanceY(g-1,g27) = 7
    c: DistanceX(g21,g-1) = 1
    c: Vertical(g21)
    c: Coincident(g28,g29)
    c: Coincident(g29,g30)
    c: Coincident(g30,g31)
    c: Coincident(g31,g32)
    c: Coincident(g32,g33)
    c: Coincident(g33,g28)
    c: Equal(g28, g29-g33) x5
    c: PointOnObject(g28,g34)
    c: PointOnObject(g29,g34)
    c: PointOnObject(g30,g34)
    c: PointOnObject(g31,g34)
    c: PointOnObject(g32,g34)
    c: PointOnObject(g33,g34)
    c: PointOnObject(g34,g-1)
    c: Diameter(g34) = 7
    c: Vertical(g31)
    c: DistanceX(g34,g-1) = 8
    c: Coincident(g35,g36)
    c: Coincident(g36,g37)
    c: Coincident(g37,g38)
    c: Coincident(g38,g39)
    c: Coincident(g39,g40)
    c: Coincident(g40,g35)
    c: Equal(g35, g36-g40) x5
    c: PointOnObject(g35,g41)
    c: PointOnObject(g36,g41)
    c: PointOnObject(g37,g41)
    c: PointOnObject(g38,g41)
    c: PointOnObject(g39,g41)
    c: PointOnObject(g40,g41)
    c: Coincident(g42,g43)
    c: Coincident(g43,g44)
    c: Coincident(g44,g45)
    c: Coincident(g45,g46)
    c: Coincident(g46,g47)
    c: Coincident(g47,g42)
    c: Equal(g42, g43-g47) x5
    c: PointOnObject(g42,g48)
    c: PointOnObject(g43,g48)
    c: PointOnObject(g44,g48)
    c: PointOnObject(g45,g48)
    c: PointOnObject(g46,g48)
    c: PointOnObject(g47,g48)
    c: Equal(g41,g48)
    c: Diameter(g41) = 7
    c: Vertical(g39)
    c: Vertical(g43)
    c: Distance(g-2,g39) = 1
    c: Symmetric(g38,g43,g-2)
    c: Distance(g41,g-1) = 7
FEATURE [Part::Extrusion] Extrude704  label="hex306"
  Base = -> Sketch713
  Dir = (0,-1,2e-16)
  DirMode = 2
  FaceMakerClass = Part::FaceMakerBullseye
  FaceMakerMode = 3
  LengthFwd = 10
  LengthRev = 0
  Placement = pos=(72,0,-14) rot=(0,0,1;0rad)
  Solid = true
  Symmetric = false
FEATURE [Sketcher::SketchObject] Sketch714
  ArcFitTolerance = 1e-06
  FullyConstrained = true
  MakeInternals = false
  Placement = pos=(0,0,0) rot=(1,0,0;1.5708rad)
  sketch-geometry (49):
    g0: LineSegment StartX=1e-16 StartY=3.5 StartZ=0 EndX=-3.03109 EndY=1.75 EndZ=0
    g1: LineSegment StartX=-3.03109 StartY=1.75 StartZ=0 EndX=-3.03109 EndY=-1.75 EndZ=0
    g2: LineSegment StartX=-3.03109 StartY=-1.75 StartZ=0 EndX=-1e-16 EndY=-3.5 EndZ=0
    g3: LineSegment StartX=-1e-16 StartY=-3.5 StartZ=0 EndX=3.03109 EndY=-1.75 EndZ=0
    g4: LineSegment StartX=3.03109 StartY=-1.75 StartZ=0 EndX=3.03109 EndY=1.75 EndZ=0
    g5: LineSegment StartX=3.03109 StartY=1.75 StartZ=0 EndX=1e-16 EndY=3.5 EndZ=0
    g6: Circle [constr] CenterX=0 CenterY=0 CenterZ=0 NormalX=0 NormalY=0 NormalZ=1 AngleXU=0 Radius=3.5
    g7: LineSegment StartX=4.96892 StartY=-1.75002 StartZ=0 EndX=8.00002 EndY=-3.5 EndZ=0
    g8: LineSegment StartX=8.00002 StartY=-3.5 StartZ=0 EndX=11.0311 EndY=-1.74998 EndZ=0
    g9: LineSegment StartX=11.0311 StartY=-1.74998 StartZ=0 EndX=11.0311 EndY=1.75002 EndZ=0
    g10: LineSegment StartX=11.0311 StartY=1.75002 StartZ=0 EndX=7.99998 EndY=3.5 EndZ=0
    g11: LineSegment StartX=7.99998 StartY=3.5 StartZ=0 EndX=4.9689 EndY=1.74998 EndZ=0
    g12: LineSegment StartX=4.9689 StartY=1.74998 StartZ=0 EndX=4.96892 EndY=-1.75002 EndZ=0
    g13: Circle [constr] CenterX=8 CenterY=0 CenterZ=0 NormalX=0 NormalY=0 NormalZ=1 AngleXU=0 Radius=3.5
    g14: LineSegment StartX=4.03109 StartY=3.5 StartZ=0 EndX=7.06218 EndY=5.25 EndZ=0
    g15: LineSegment StartX=7.06218 StartY=5.25 StartZ=0 EndX=7.06218 EndY=8.75 EndZ=0
    g16: LineSegment StartX=7.06218 StartY=8.75 StartZ=0 EndX=4.03109 EndY=10.5 EndZ=0
    g17: LineSegment StartX=4.03109 StartY=10.5 StartZ=0 EndX=1 EndY=8.75 EndZ=0
    g18: LineSegment StartX=1 StartY=8.75 StartZ=0 EndX=1 EndY=5.25 EndZ=0
    g19: LineSegment StartX=1 StartY=5.25 StartZ=0 EndX=4.03109 EndY=3.5 EndZ=0
    g20: Circle [constr] CenterX=4.03109 CenterY=7 CenterZ=0 NormalX=0 NormalY=0 NormalZ=1 AngleXU=0 Radius=3.5
    g21: LineSegment StartX=-1 StartY=5.25 StartZ=0 EndX=-1 EndY=8.75 EndZ=0
    g22: LineSegment StartX=-1 StartY=8.75 StartZ=0 EndX=-4.03109 EndY=10.5 EndZ=0
    g23: LineSegment StartX=-4.03109 StartY=10.5 StartZ=0 EndX=-7.06218 EndY=8.75 EndZ=0
    g24: LineSegment StartX=-7.06218 StartY=8.75 StartZ=0 EndX=-7.06218 EndY=5.25 EndZ=0
    g25: LineSegment StartX=-7.06218 StartY=5.25 StartZ=0 EndX=-4.03109 EndY=3.5 EndZ=0
    g26: LineSegment StartX=-4.03109 StartY=3.5 StartZ=0 EndX=-1 EndY=5.25 EndZ=0
    g27: Circle [constr] CenterX=-4.03109 CenterY=7 CenterZ=0 NormalX=0 NormalY=0 NormalZ=1 AngleXU=0 Radius=3.5
    g28: LineSegment StartX=-4.96891 StartY=-1.75 StartZ=0 EndX=-4.96891 EndY=1.75 EndZ=0
    g29: LineSegment StartX=-4.96891 StartY=1.75 StartZ=0 EndX=-8 EndY=3.5 EndZ=0
    g30: LineSegment StartX=-8 StartY=3.5 StartZ=0 EndX=-11.0311 EndY=1.75 EndZ=0
    g31: LineSegment StartX=-11.0311 StartY=1.75 StartZ=0 EndX=-11.0311 EndY=-1.75 EndZ=0
    g32: LineSegment StartX=-11.0311 StartY=-1.75 StartZ=0 EndX=-8 EndY=-3.5 EndZ=0
    g33: LineSegment StartX=-8 StartY=-3.5 StartZ=0 EndX=-4.96891 EndY=-1.75 EndZ=0
    g34: Circle [constr] CenterX=-8 CenterY=0 CenterZ=0 NormalX=0 NormalY=0 NormalZ=1 AngleXU=0 Radius=3.5
    g35: LineSegment StartX=-4.03109 StartY=-3.5 StartZ=0 EndX=-7.06218 EndY=-5.25 EndZ=0
    g36: LineSegment StartX=-7.06218 StartY=-5.25 StartZ=0 EndX=-7.06218 EndY=-8.75 EndZ=0
    g37: LineSegment StartX=-7.06218 StartY=-8.75 StartZ=0 EndX=-4.03109 EndY=-10.5 EndZ=0
    g38: LineSegment StartX=-4.03109 StartY=-10.5 StartZ=0 EndX=-1 EndY=-8.75 EndZ=0
    g39: LineSegment StartX=-1 StartY=-8.75 StartZ=0 EndX=-1 EndY=-5.25 EndZ=0
    g40: LineSegment StartX=-1 StartY=-5.25 StartZ=0 EndX=-4.03109 EndY=-3.5 EndZ=0
    g41: Circle [constr] CenterX=-4.03109 CenterY=-7 CenterZ=0 NormalX=0 NormalY=0 NormalZ=1 AngleXU=0 Radius=3.5
    g42: LineSegment StartX=4.03109 StartY=-3.5 StartZ=0 EndX=1 EndY=-5.25 EndZ=0
    g43: LineSegment StartX=1 StartY=-5.25 StartZ=0 EndX=1 EndY=-8.75 EndZ=0
    g44: LineSegment StartX=1 StartY=-8.75 StartZ=0 EndX=4.03109 EndY=-10.5 EndZ=0
    g45: LineSegment StartX=4.03109 StartY=-10.5 StartZ=0 EndX=7.06218 EndY=-8.75 EndZ=0
    g46: LineSegment StartX=7.06218 StartY=-8.75 StartZ=0 EndX=7.06218 EndY=-5.25 EndZ=0
    g47: LineSegment StartX=7.06218 StartY=-5.25 StartZ=0 EndX=4.03109 EndY=-3.5 EndZ=0
    g48: Circle [constr] CenterX=4.03109 CenterY=-7 CenterZ=0 NormalX=0 NormalY=0 NormalZ=1 AngleXU=0 Radius=3.5
  constraints (117):
    c: Coincident(g0,g1)
    c: Coincident(g1,g2)
    c: Coincident(g2,g3)
    c: Coincident(g3,g4)
    c: Coincident(g4,g5)
    c: Coincident(g5,g0)
    c: Equal(g0, g1-g5) x5
    c: PointOnObject(g0,g6)
    c: PointOnObject(g1,g6)
    c: PointOnObject(g2,g6)
    c: PointOnObject(g3,g6)
    c: PointOnObject(g4,g6)
    c: PointOnObject(g5,g6)
    c: Coincident(g6,g-1)
    c: Diameter(g6) = 7
    c: PointOnObject(g0,g-2)
    c: Coincident(g7,g8)
    c: Coincident(g8,g9)
    c: Coincident(g9,g10)
    c: Coincident(g10,g11)
    c: Coincident(g11,g12)
    c: Coincident(g12,g7)
    c: Equal(g7, g8-g12) x5
    c: PointOnObject(g7,g13)
    c: PointOnObject(g8,g13)
    c: PointOnObject(g9,g13)
    c: PointOnObject(g10,g13)
    c: PointOnObject(g11,g13)
    c: PointOnObject(g12,g13)
    c: PointOnObject(g13,g-1)
    c: Diameter(g13) = 7
    c: Distance(g6,g13) = 8
    c: Horizontal(g0,g10)
    c: Coincident(g14,g15)
    c: Coincident(g15,g16)
    c: Coincident(g16,g17)
    c: Coincident(g17,g18)
    c: Coincident(g18,g19)
    c: Coincident(g19,g14)
    c: Equal(g14, g15-g19) x5
    c: PointOnObject(g14,g20)
    c: PointOnObject(g15,g20)
    c: PointOnObject(g16,g20)
    c: PointOnObject(g17,g20)
    c: PointOnObject(g18,g20)
    c: PointOnObject(g19,g20)
    c: Diameter(g20) = 7
    c: DistanceY(g-1,g20) = 7
    c: Vertical(g18)
    c: Distance(g17,g-2) = 1
    c: Coincident(g21,g22)
    c: Coincident(g22,g23)
    c: Coincident(g23,g24)
    c: Coincident(g24,g25)
    c: Coincident(g25,g26)
    c: Coincident(g26,g21)
    c: Equal(g21, g22-g26) x5
    c: PointOnObject(g21,g27)
    c: PointOnObject(g22,g27)
    c: PointOnObject(g23,g27)
    c: PointOnObject(g24,g27)
    c: PointOnObject(g25,g27)
    c: PointOnObject(g26,g27)
    c: Diameter(g27) = 7
    c: DistanceY(g-1,g27) = 7
    c: DistanceX(g21,g-1) = 1
    c: Vertical(g21)
    c: Coincident(g28,g29)
    c: Coincident(g29,g30)
    c: Coincident(g30,g31)
    c: Coincident(g31,g32)
    c: Coincident(g32,g33)
    c: Coincident(g33,g28)
    c: Equal(g28, g29-g33) x5
    c: PointOnObject(g28,g34)
    c: PointOnObject(g29,g34)
    c: PointOnObject(g30,g34)
    c: PointOnObject(g31,g34)
    c: PointOnObject(g32,g34)
    c: PointOnObject(g33,g34)
    c: PointOnObject(g34,g-1)
    c: Diameter(g34) = 7
    c: Vertical(g31)
    c: DistanceX(g34,g-1) = 8
    c: Coincident(g35,g36)
    c: Coincident(g36,g37)
    c: Coincident(g37,g38)
    c: Coincident(g38,g39)
    c: Coincident(g39,g40)
    c: Coincident(g40,g35)
    c: Equal(g35, g36-g40) x5
    c: PointOnObject(g35,g41)
    c: PointOnObject(g36,g41)
    c: PointOnObject(g37,g41)
    c: PointOnObject(g38,g41)
    c: PointOnObject(g39,g41)
    c: PointOnObject(g40,g41)
    c: Coincident(g42,g43)
    c: Coincident(g43,g44)
    c: Coincident(g44,g45)
    c: Coincident(g45,g46)
    c: Coincident(g46,g47)
    c: Coincident(g47,g42)
    c: Equal(g42, g43-g47) x5
    c: PointOnObject(g42,g48)
    c: PointOnObject(g43,g48)
    c: PointOnObject(g44,g48)
    c: PointOnObject(g45,g48)
    c: PointOnObject(g46,g48)
    c: PointOnObject(g47,g48)
    c: Equal(g41,g48)
    c: Diameter(g41) = 7
    c: Vertical(g39)
    c: Vertical(g43)
    c: Distance(g-2,g39) = 1
    c: Symmetric(g38,g43,g-2)
    c: Distance(g41,g-1) = 7
FEATURE [Part::Extrusion] Extrude705  label="hex307"
  Base = -> Sketch714
  Dir = (0,-1,2e-16)
  DirMode = 2
  FaceMakerClass = Part::FaceMakerBullseye
  FaceMakerMode = 3
  LengthFwd = 10
  LengthRev = 0
  Placement = pos=(72,0,14) rot=(0,0,1;0rad)
  Solid = true
  Symmetric = false
FEATURE [Sketcher::SketchObject] Sketch715
  ArcFitTolerance = 1e-06
  FullyConstrained = true
  MakeInternals = false
  Placement = pos=(0,0,0) rot=(1,0,0;1.5708rad)
  sketch-geometry (49):
    g0: LineSegment StartX=1e-16 StartY=3.5 StartZ=0 EndX=-3.03109 EndY=1.75 EndZ=0
    g1: LineSegment StartX=-3.03109 StartY=1.75 StartZ=0 EndX=-3.03109 EndY=-1.75 EndZ=0
    g2: LineSegment StartX=-3.03109 StartY=-1.75 StartZ=0 EndX=-1e-16 EndY=-3.5 EndZ=0
    g3: LineSegment StartX=-1e-16 StartY=-3.5 StartZ=0 EndX=3.03109 EndY=-1.75 EndZ=0
    g4: LineSegment StartX=3.03109 StartY=-1.75 StartZ=0 EndX=3.03109 EndY=1.75 EndZ=0
    g5: LineSegment StartX=3.03109 StartY=1.75 StartZ=0 EndX=1e-16 EndY=3.5 EndZ=0
    g6: Circle [constr] CenterX=0 CenterY=0 CenterZ=0 NormalX=0 NormalY=0 NormalZ=1 AngleXU=0 Radius=3.5
    g7: LineSegment StartX=4.96892 StartY=-1.75002 StartZ=0 EndX=8.00002 EndY=-3.5 EndZ=0
    g8: LineSegment StartX=8.00002 StartY=-3.5 StartZ=0 EndX=11.0311 EndY=-1.74998 EndZ=0
    g9: LineSegment StartX=11.0311 StartY=-1.74998 StartZ=0 EndX=11.0311 EndY=1.75002 EndZ=0
    g10: LineSegment StartX=11.0311 StartY=1.75002 StartZ=0 EndX=7.99998 EndY=3.5 EndZ=0
    g11: LineSegment StartX=7.99998 StartY=3.5 StartZ=0 EndX=4.9689 EndY=1.74998 EndZ=0
    g12: LineSegment StartX=4.9689 StartY=1.74998 StartZ=0 EndX=4.96892 EndY=-1.75002 EndZ=0
    g13: Circle [constr] CenterX=8 CenterY=0 CenterZ=0 NormalX=0 NormalY=0 NormalZ=1 AngleXU=0 Radius=3.5
    g14: LineSegment StartX=4.03109 StartY=3.5 StartZ=0 EndX=7.06218 EndY=5.25 EndZ=0
    g15: LineSegment StartX=7.06218 StartY=5.25 StartZ=0 EndX=7.06218 EndY=8.75 EndZ=0
    g16: LineSegment StartX=7.06218 StartY=8.75 StartZ=0 EndX=4.03109 EndY=10.5 EndZ=0
    g17: LineSegment StartX=4.03109 StartY=10.5 StartZ=0 EndX=1 EndY=8.75 EndZ=0
    g18: LineSegment StartX=1 StartY=8.75 StartZ=0 EndX=1 EndY=5.25 EndZ=0
    g19: LineSegment StartX=1 StartY=5.25 StartZ=0 EndX=4.03109 EndY=3.5 EndZ=0
    g20: Circle [constr] CenterX=4.03109 CenterY=7 CenterZ=0 NormalX=0 NormalY=0 NormalZ=1 AngleXU=0 Radius=3.5
    g21: LineSegment StartX=-1 StartY=5.25 StartZ=0 EndX=-1 EndY=8.75 EndZ=0
    g22: LineSegment StartX=-1 StartY=8.75 StartZ=0 EndX=-4.03109 EndY=10.5 EndZ=0
    g23: LineSegment StartX=-4.03109 StartY=10.5 StartZ=0 EndX=-7.06218 EndY=8.75 EndZ=0
    g24: LineSegment StartX=-7.06218 StartY=8.75 StartZ=0 EndX=-7.06218 EndY=5.25 EndZ=0
    g25: LineSegment StartX=-7.06218 StartY=5.25 StartZ=0 EndX=-4.03109 EndY=3.5 EndZ=0
    g26: LineSegment StartX=-4.03109 StartY=3.5 StartZ=0 EndX=-1 EndY=5.25 EndZ=0
    g27: Circle [constr] CenterX=-4.03109 CenterY=7 CenterZ=0 NormalX=0 NormalY=0 NormalZ=1 AngleXU=0 Radius=3.5
    g28: LineSegment StartX=-4.96891 StartY=-1.75 StartZ=0 EndX=-4.96891 EndY=1.75 EndZ=0
    g29: LineSegment StartX=-4.96891 StartY=1.75 StartZ=0 EndX=-8 EndY=3.5 EndZ=0
    g30: LineSegment StartX=-8 StartY=3.5 StartZ=0 EndX=-11.0311 EndY=1.75 EndZ=0
    g31: LineSegment StartX=-11.0311 StartY=1.75 StartZ=0 EndX=-11.0311 EndY=-1.75 EndZ=0
    g32: LineSegment StartX=-11.0311 StartY=-1.75 StartZ=0 EndX=-8 EndY=-3.5 EndZ=0
    g33: LineSegment StartX=-8 StartY=-3.5 StartZ=0 EndX=-4.96891 EndY=-1.75 EndZ=0
    g34: Circle [constr] CenterX=-8 CenterY=0 CenterZ=0 NormalX=0 NormalY=0 NormalZ=1 AngleXU=0 Radius=3.5
    g35: LineSegment StartX=-4.03109 StartY=-3.5 StartZ=0 EndX=-7.06218 EndY=-5.25 EndZ=0
    g36: LineSegment StartX=-7.06218 StartY=-5.25 StartZ=0 EndX=-7.06218 EndY=-8.75 EndZ=0
    g37: LineSegment StartX=-7.06218 StartY=-8.75 StartZ=0 EndX=-4.03109 EndY=-10.5 EndZ=0
    g38: LineSegment StartX=-4.03109 StartY=-10.5 StartZ=0 EndX=-1 EndY=-8.75 EndZ=0
    g39: LineSegment StartX=-1 StartY=-8.75 StartZ=0 EndX=-1 EndY=-5.25 EndZ=0
    g40: LineSegment StartX=-1 StartY=-5.25 StartZ=0 EndX=-4.03109 EndY=-3.5 EndZ=0
    g41: Circle [constr] CenterX=-4.03109 CenterY=-7 CenterZ=0 NormalX=0 NormalY=0 NormalZ=1 AngleXU=0 Radius=3.5
    g42: LineSegment StartX=4.03109 StartY=-3.5 StartZ=0 EndX=1 EndY=-5.25 EndZ=0
    g43: LineSegment StartX=1 StartY=-5.25 StartZ=0 EndX=1 EndY=-8.75 EndZ=0
    g44: LineSegment StartX=1 StartY=-8.75 StartZ=0 EndX=4.03109 EndY=-10.5 EndZ=0
    g45: LineSegment StartX=4.03109 StartY=-10.5 StartZ=0 EndX=7.06218 EndY=-8.75 EndZ=0
    g46: LineSegment StartX=7.06218 StartY=-8.75 StartZ=0 EndX=7.06218 EndY=-5.25 EndZ=0
    g47: LineSegment StartX=7.06218 StartY=-5.25 StartZ=0 EndX=4.03109 EndY=-3.5 EndZ=0
    g48: Circle [constr] CenterX=4.03109 CenterY=-7 CenterZ=0 NormalX=0 NormalY=0 NormalZ=1 AngleXU=0 Radius=3.5
  constraints (117):
    c: Coincident(g0,g1)
    c: Coincident(g1,g2)
    c: Coincident(g2,g3)
    c: Coincident(g3,g4)
    c: Coincident(g4,g5)
    c: Coincident(g5,g0)
    c: Equal(g0, g1-g5) x5
    c: PointOnObject(g0,g6)
    c: PointOnObject(g1,g6)
    c: PointOnObject(g2,g6)
    c: PointOnObject(g3,g6)
    c: PointOnObject(g4,g6)
    c: PointOnObject(g5,g6)
    c: Coincident(g6,g-1)
    c: Diameter(g6) = 7
    c: PointOnObject(g0,g-2)
    c: Coincident(g7,g8)
    c: Coincident(g8,g9)
    c: Coincident(g9,g10)
    c: Coincident(g10,g11)
    c: Coincident(g11,g12)
    c: Coincident(g12,g7)
    c: Equal(g7, g8-g12) x5
    c: PointOnObject(g7,g13)
    c: PointOnObject(g8,g13)
    c: PointOnObject(g9,g13)
    c: PointOnObject(g10,g13)
    c: PointOnObject(g11,g13)
    c: PointOnObject(g12,g13)
    c: PointOnObject(g13,g-1)
    c: Diameter(g13) = 7
    c: Distance(g6,g13) = 8
    c: Horizontal(g0,g10)
    c: Coincident(g14,g15)
    c: Coincident(g15,g16)
    c: Coincident(g16,g17)
    c: Coincident(g17,g18)
    c: Coincident(g18,g19)
    c: Coincident(g19,g14)
    c: Equal(g14, g15-g19) x5
    c: PointOnObject(g14,g20)
    c: PointOnObject(g15,g20)
    c: PointOnObject(g16,g20)
    c: PointOnObject(g17,g20)
    c: PointOnObject(g18,g20)
    c: PointOnObject(g19,g20)
    c: Diameter(g20) = 7
    c: DistanceY(g-1,g20) = 7
    c: Vertical(g18)
    c: Distance(g17,g-2) = 1
    c: Coincident(g21,g22)
    c: Coincident(g22,g23)
    c: Coincident(g23,g24)
    c: Coincident(g24,g25)
    c: Coincident(g25,g26)
    c: Coincident(g26,g21)
    c: Equal(g21, g22-g26) x5
    c: PointOnObject(g21,g27)
    c: PointOnObject(g22,g27)
    c: PointOnObject(g23,g27)
    c: PointOnObject(g24,g27)
    c: PointOnObject(g25,g27)
    c: PointOnObject(g26,g27)
    c: Diameter(g27) = 7
    c: DistanceY(g-1,g27) = 7
    c: DistanceX(g21,g-1) = 1
    c: Vertical(g21)
    c: Coincident(g28,g29)
    c: Coincident(g29,g30)
    c: Coincident(g30,g31)
    c: Coincident(g31,g32)
    c: Coincident(g32,g33)
    c: Coincident(g33,g28)
    c: Equal(g28, g29-g33) x5
    c: PointOnObject(g28,g34)
    c: PointOnObject(g29,g34)
    c: PointOnObject(g30,g34)
    c: PointOnObject(g31,g34)
    c: PointOnObject(g32,g34)
    c: PointOnObject(g33,g34)
    c: PointOnObject(g34,g-1)
    c: Diameter(g34) = 7
    c: Vertical(g31)
    c: DistanceX(g34,g-1) = 8
    c: Coincident(g35,g36)
    c: Coincident(g36,g37)
    c: Coincident(g37,g38)
    c: Coincident(g38,g39)
    c: Coincident(g39,g40)
    c: Coincident(g40,g35)
    c: Equal(g35, g36-g40) x5
    c: PointOnObject(g35,g41)
    c: PointOnObject(g36,g41)
    c: PointOnObject(g37,g41)
    c: PointOnObject(g38,g41)
    c: PointOnObject(g39,g41)
    c: PointOnObject(g40,g41)
    c: Coincident(g42,g43)
    c: Coincident(g43,g44)
    c: Coincident(g44,g45)
    c: Coincident(g45,g46)
    c: Coincident(g46,g47)
    c: Coincident(g47,g42)
    c: Equal(g42, g43-g47) x5
    c: PointOnObject(g42,g48)
    c: PointOnObject(g43,g48)
    c: PointOnObject(g44,g48)
    c: PointOnObject(g45,g48)
    c: PointOnObject(g46,g48)
    c: PointOnObject(g47,g48)
    c: Equal(g41,g48)
    c: Diameter(g41) = 7
    c: Vertical(g39)
    c: Vertical(g43)
    c: Distance(g-2,g39) = 1
    c: Symmetric(g38,g43,g-2)
    c: Distance(g41,g-1) = 7
FEATURE [Part::Extrusion] Extrude706  label="hex308"
  Base = -> Sketch715
  Dir = (0,-1,2e-16)
  DirMode = 2
  FaceMakerClass = Part::FaceMakerBullseye
  FaceMakerMode = 3
  LengthFwd = 10
  LengthRev = 0
  Placement = pos=(80,0,0) rot=(0,0,1;0rad)
  Solid = true
  Symmetric = false
FEATURE [Sketcher::SketchObject] Sketch716
  ArcFitTolerance = 1e-06
  FullyConstrained = true
  MakeInternals = false
  Placement = pos=(0,0,0) rot=(1,0,0;1.5708rad)
  sketch-geometry (49):
    g0: LineSegment StartX=1e-16 StartY=3.5 StartZ=0 EndX=-3.03109 EndY=1.75 EndZ=0
    g1: LineSegment StartX=-3.03109 StartY=1.75 StartZ=0 EndX=-3.03109 EndY=-1.75 EndZ=0
    g2: LineSegment StartX=-3.03109 StartY=-1.75 StartZ=0 EndX=-1e-16 EndY=-3.5 EndZ=0
    g3: LineSegment StartX=-1e-16 StartY=-3.5 StartZ=0 EndX=3.03109 EndY=-1.75 EndZ=0
    g4: LineSegment StartX=3.03109 StartY=-1.75 StartZ=0 EndX=3.03109 EndY=1.75 EndZ=0
    g5: LineSegment StartX=3.03109 StartY=1.75 StartZ=0 EndX=1e-16 EndY=3.5 EndZ=0
    g6: Circle [constr] CenterX=0 CenterY=0 CenterZ=0 NormalX=0 NormalY=0 NormalZ=1 AngleXU=0 Radius=3.5
    g7: LineSegment StartX=4.96892 StartY=-1.75002 StartZ=0 EndX=8.00002 EndY=-3.5 EndZ=0
    g8: LineSegment StartX=8.00002 StartY=-3.5 StartZ=0 EndX=11.0311 EndY=-1.74998 EndZ=0
    g9: LineSegment StartX=11.0311 StartY=-1.74998 StartZ=0 EndX=11.0311 EndY=1.75002 EndZ=0
    g10: LineSegment StartX=11.0311 StartY=1.75002 StartZ=0 EndX=7.99998 EndY=3.5 EndZ=0
    g11: LineSegment StartX=7.99998 StartY=3.5 StartZ=0 EndX=4.9689 EndY=1.74998 EndZ=0
    g12: LineSegment StartX=4.9689 StartY=1.74998 StartZ=0 EndX=4.96892 EndY=-1.75002 EndZ=0
    g13: Circle [constr] CenterX=8 CenterY=0 CenterZ=0 NormalX=0 NormalY=0 NormalZ=1 AngleXU=0 Radius=3.5
    g14: LineSegment StartX=4.03109 StartY=3.5 StartZ=0 EndX=7.06218 EndY=5.25 EndZ=0
    g15: LineSegment StartX=7.06218 StartY=5.25 StartZ=0 EndX=7.06218 EndY=8.75 EndZ=0
    g16: LineSegment StartX=7.06218 StartY=8.75 StartZ=0 EndX=4.03109 EndY=10.5 EndZ=0
    g17: LineSegment StartX=4.03109 StartY=10.5 StartZ=0 EndX=1 EndY=8.75 EndZ=0
    g18: LineSegment StartX=1 StartY=8.75 StartZ=0 EndX=1 EndY=5.25 EndZ=0
    g19: LineSegment StartX=1 StartY=5.25 StartZ=0 EndX=4.03109 EndY=3.5 EndZ=0
    g20: Circle [constr] CenterX=4.03109 CenterY=7 CenterZ=0 NormalX=0 NormalY=0 NormalZ=1 AngleXU=0 Radius=3.5
    g21: LineSegment StartX=-1 StartY=5.25 StartZ=0 EndX=-1 EndY=8.75 EndZ=0
    g22: LineSegment StartX=-1 StartY=8.75 StartZ=0 EndX=-4.03109 EndY=10.5 EndZ=0
    g23: LineSegment StartX=-4.03109 StartY=10.5 StartZ=0 EndX=-7.06218 EndY=8.75 EndZ=0
    g24: LineSegment StartX=-7.06218 StartY=8.75 StartZ=0 EndX=-7.06218 EndY=5.25 EndZ=0
    g25: LineSegment StartX=-7.06218 StartY=5.25 StartZ=0 EndX=-4.03109 EndY=3.5 EndZ=0
    g26: LineSegment StartX=-4.03109 StartY=3.5 StartZ=0 EndX=-1 EndY=5.25 EndZ=0
    g27: Circle [constr] CenterX=-4.03109 CenterY=7 CenterZ=0 NormalX=0 NormalY=0 NormalZ=1 AngleXU=0 Radius=3.5
    g28: LineSegment StartX=-4.96891 StartY=-1.75 StartZ=0 EndX=-4.96891 EndY=1.75 EndZ=0
    g29: LineSegment StartX=-4.96891 StartY=1.75 StartZ=0 EndX=-8 EndY=3.5 EndZ=0
    g30: LineSegment StartX=-8 StartY=3.5 StartZ=0 EndX=-11.0311 EndY=1.75 EndZ=0
    g31: LineSegment StartX=-11.0311 StartY=1.75 StartZ=0 EndX=-11.0311 EndY=-1.75 EndZ=0
    g32: LineSegment StartX=-11.0311 StartY=-1.75 StartZ=0 EndX=-8 EndY=-3.5 EndZ=0
    g33: LineSegment StartX=-8 StartY=-3.5 StartZ=0 EndX=-4.96891 EndY=-1.75 EndZ=0
    g34: Circle [constr] CenterX=-8 CenterY=0 CenterZ=0 NormalX=0 NormalY=0 NormalZ=1 AngleXU=0 Radius=3.5
    g35: LineSegment StartX=-4.03109 StartY=-3.5 StartZ=0 EndX=-7.06218 EndY=-5.25 EndZ=0
    g36: LineSegment StartX=-7.06218 StartY=-5.25 StartZ=0 EndX=-7.06218 EndY=-8.75 EndZ=0
    g37: LineSegment StartX=-7.06218 StartY=-8.75 StartZ=0 EndX=-4.03109 EndY=-10.5 EndZ=0
    g38: LineSegment StartX=-4.03109 StartY=-10.5 StartZ=0 EndX=-1 EndY=-8.75 EndZ=0
    g39: LineSegment StartX=-1 StartY=-8.75 StartZ=0 EndX=-1 EndY=-5.25 EndZ=0
    g40: LineSegment StartX=-1 StartY=-5.25 StartZ=0 EndX=-4.03109 EndY=-3.5 EndZ=0
    g41: Circle [constr] CenterX=-4.03109 CenterY=-7 CenterZ=0 NormalX=0 NormalY=0 NormalZ=1 AngleXU=0 Radius=3.5
    g42: LineSegment StartX=4.03109 StartY=-3.5 StartZ=0 EndX=1 EndY=-5.25 EndZ=0
    g43: LineSegment StartX=1 StartY=-5.25 StartZ=0 EndX=1 EndY=-8.75 EndZ=0
    g44: LineSegment StartX=1 StartY=-8.75 StartZ=0 EndX=4.03109 EndY=-10.5 EndZ=0
    g45: LineSegment StartX=4.03109 StartY=-10.5 StartZ=0 EndX=7.06218 EndY=-8.75 EndZ=0
    g46: LineSegment StartX=7.06218 StartY=-8.75 StartZ=0 EndX=7.06218 EndY=-5.25 EndZ=0
    g47: LineSegment StartX=7.06218 StartY=-5.25 StartZ=0 EndX=4.03109 EndY=-3.5 EndZ=0
    g48: Circle [constr] CenterX=4.03109 CenterY=-7 CenterZ=0 NormalX=0 NormalY=0 NormalZ=1 AngleXU=0 Radius=3.5
  constraints (117):
    c: Coincident(g0,g1)
    c: Coincident(g1,g2)
    c: Coincident(g2,g3)
    c: Coincident(g3,g4)
    c: Coincident(g4,g5)
    c: Coincident(g5,g0)
    c: Equal(g0, g1-g5) x5
    c: PointOnObject(g0,g6)
    c: PointOnObject(g1,g6)
    c: PointOnObject(g2,g6)
    c: PointOnObject(g3,g6)
    c: PointOnObject(g4,g6)
    c: PointOnObject(g5,g6)
    c: Coincident(g6,g-1)
    c: Diameter(g6) = 7
    c: PointOnObject(g0,g-2)
    c: Coincident(g7,g8)
    c: Coincident(g8,g9)
    c: Coincident(g9,g10)
    c: Coincident(g10,g11)
    c: Coincident(g11,g12)
    c: Coincident(g12,g7)
    c: Equal(g7, g8-g12) x5
    c: PointOnObject(g7,g13)
    c: PointOnObject(g8,g13)
    c: PointOnObject(g9,g13)
    c: PointOnObject(g10,g13)
    c: PointOnObject(g11,g13)
    c: PointOnObject(g12,g13)
    c: PointOnObject(g13,g-1)
    c: Diameter(g13) = 7
    c: Distance(g6,g13) = 8
    c: Horizontal(g0,g10)
    c: Coincident(g14,g15)
    c: Coincident(g15,g16)
    c: Coincident(g16,g17)
    c: Coincident(g17,g18)
    c: Coincident(g18,g19)
    c: Coincident(g19,g14)
    c: Equal(g14, g15-g19) x5
    c: PointOnObject(g14,g20)
    c: PointOnObject(g15,g20)
    c: PointOnObject(g16,g20)
    c: PointOnObject(g17,g20)
    c: PointOnObject(g18,g20)
    c: PointOnObject(g19,g20)
    c: Diameter(g20) = 7
    c: DistanceY(g-1,g20) = 7
    c: Vertical(g18)
    c: Distance(g17,g-2) = 1
    c: Coincident(g21,g22)
    c: Coincident(g22,g23)
    c: Coincident(g23,g24)
    c: Coincident(g24,g25)
    c: Coincident(g25,g26)
    c: Coincident(g26,g21)
    c: Equal(g21, g22-g26) x5
    c: PointOnObject(g21,g27)
    c: PointOnObject(g22,g27)
    c: PointOnObject(g23,g27)
    c: PointOnObject(g24,g27)
    c: PointOnObject(g25,g27)
    c: PointOnObject(g26,g27)
    c: Diameter(g27) = 7
    c: DistanceY(g-1,g27) = 7
    c: DistanceX(g21,g-1) = 1
    c: Vertical(g21)
    c: Coincident(g28,g29)
    c: Coincident(g29,g30)
    c: Coincident(g30,g31)
    c: Coincident(g31,g32)
    c: Coincident(g32,g33)
    c: Coincident(g33,g28)
    c: Equal(g28, g29-g33) x5
    c: PointOnObject(g28,g34)
    c: PointOnObject(g29,g34)
    c: PointOnObject(g30,g34)
    c: PointOnObject(g31,g34)
    c: PointOnObject(g32,g34)
    c: PointOnObject(g33,g34)
    c: PointOnObject(g34,g-1)
    c: Diameter(g34) = 7
    c: Vertical(g31)
    c: DistanceX(g34,g-1) = 8
    c: Coincident(g35,g36)
    c: Coincident(g36,g37)
    c: Coincident(g37,g38)
    c: Coincident(g38,g39)
    c: Coincident(g39,g40)
    c: Coincident(g40,g35)
    c: Equal(g35, g36-g40) x5
    c: PointOnObject(g35,g41)
    c: PointOnObject(g36,g41)
    c: PointOnObject(g37,g41)
    c: PointOnObject(g38,g41)
    c: PointOnObject(g39,g41)
    c: PointOnObject(g40,g41)
    c: Coincident(g42,g43)
    c: Coincident(g43,g44)
    c: Coincident(g44,g45)
    c: Coincident(g45,g46)
    c: Coincident(g46,g47)
    c: Coincident(g47,g42)
    c: Equal(g42, g43-g47) x5
    c: PointOnObject(g42,g48)
    c: PointOnObject(g43,g48)
    c: PointOnObject(g44,g48)
    c: PointOnObject(g45,g48)
    c: PointOnObject(g46,g48)
    c: PointOnObject(g47,g48)
    c: Equal(g41,g48)
    c: Diameter(g41) = 7
    c: Vertical(g39)
    c: Vertical(g43)
    c: Distance(g-2,g39) = 1
    c: Symmetric(g38,g43,g-2)
    c: Distance(g41,g-1) = 7
FEATURE [Part::Extrusion] Extrude707  label="hex309"
  Base = -> Sketch716
  Dir = (0,-1,2e-16)
  DirMode = 2
  FaceMakerClass = Part::FaceMakerBullseye
  FaceMakerMode = 3
  LengthFwd = 10
  LengthRev = 0
  Placement = pos=(104,0,0) rot=(0,0,1;0rad)
  Solid = true
  Symmetric = false
FEATURE [Sketcher::SketchObject] Sketch717
  ArcFitTolerance = 1e-06
  FullyConstrained = true
  MakeInternals = false
  Placement = pos=(0,0,0) rot=(1,0,0;1.5708rad)
  sketch-geometry (49):
    g0: LineSegment StartX=1e-16 StartY=3.5 StartZ=0 EndX=-3.03109 EndY=1.75 EndZ=0
    g1: LineSegment StartX=-3.03109 StartY=1.75 StartZ=0 EndX=-3.03109 EndY=-1.75 EndZ=0
    g2: LineSegment StartX=-3.03109 StartY=-1.75 StartZ=0 EndX=-1e-16 EndY=-3.5 EndZ=0
    g3: LineSegment StartX=-1e-16 StartY=-3.5 StartZ=0 EndX=3.03109 EndY=-1.75 EndZ=0
    g4: LineSegment StartX=3.03109 StartY=-1.75 StartZ=0 EndX=3.03109 EndY=1.75 EndZ=0
    g5: LineSegment StartX=3.03109 StartY=1.75 StartZ=0 EndX=1e-16 EndY=3.5 EndZ=0
    g6: Circle [constr] CenterX=0 CenterY=0 CenterZ=0 NormalX=0 NormalY=0 NormalZ=1 AngleXU=0 Radius=3.5
    g7: LineSegment StartX=4.96892 StartY=-1.75002 StartZ=0 EndX=8.00002 EndY=-3.5 EndZ=0
    g8: LineSegment StartX=8.00002 StartY=-3.5 StartZ=0 EndX=11.0311 EndY=-1.74998 EndZ=0
    g9: LineSegment StartX=11.0311 StartY=-1.74998 StartZ=0 EndX=11.0311 EndY=1.75002 EndZ=0
    g10: LineSegment StartX=11.0311 StartY=1.75002 StartZ=0 EndX=7.99998 EndY=3.5 EndZ=0
    g11: LineSegment StartX=7.99998 StartY=3.5 StartZ=0 EndX=4.9689 EndY=1.74998 EndZ=0
    g12: LineSegment StartX=4.9689 StartY=1.74998 StartZ=0 EndX=4.96892 EndY=-1.75002 EndZ=0
    g13: Circle [constr] CenterX=8 CenterY=0 CenterZ=0 NormalX=0 NormalY=0 NormalZ=1 AngleXU=0 Radius=3.5
    g14: LineSegment StartX=4.03109 StartY=3.5 StartZ=0 EndX=7.06218 EndY=5.25 EndZ=0
    g15: LineSegment StartX=7.06218 StartY=5.25 StartZ=0 EndX=7.06218 EndY=8.75 EndZ=0
    g16: LineSegment StartX=7.06218 StartY=8.75 StartZ=0 EndX=4.03109 EndY=10.5 EndZ=0
    g17: LineSegment StartX=4.03109 StartY=10.5 StartZ=0 EndX=1 EndY=8.75 EndZ=0
    g18: LineSegment StartX=1 StartY=8.75 StartZ=0 EndX=1 EndY=5.25 EndZ=0
    g19: LineSegment StartX=1 StartY=5.25 StartZ=0 EndX=4.03109 EndY=3.5 EndZ=0
    g20: Circle [constr] CenterX=4.03109 CenterY=7 CenterZ=0 NormalX=0 NormalY=0 NormalZ=1 AngleXU=0 Radius=3.5
    g21: LineSegment StartX=-1 StartY=5.25 StartZ=0 EndX=-1 EndY=8.75 EndZ=0
    g22: LineSegment StartX=-1 StartY=8.75 StartZ=0 EndX=-4.03109 EndY=10.5 EndZ=0
    g23: LineSegment StartX=-4.03109 StartY=10.5 StartZ=0 EndX=-7.06218 EndY=8.75 EndZ=0
    g24: LineSegment StartX=-7.06218 StartY=8.75 StartZ=0 EndX=-7.06218 EndY=5.25 EndZ=0
    g25: LineSegment StartX=-7.06218 StartY=5.25 StartZ=0 EndX=-4.03109 EndY=3.5 EndZ=0
    g26: LineSegment StartX=-4.03109 StartY=3.5 StartZ=0 EndX=-1 EndY=5.25 EndZ=0
    g27: Circle [constr] CenterX=-4.03109 CenterY=7 CenterZ=0 NormalX=0 NormalY=0 NormalZ=1 AngleXU=0 Radius=3.5
    g28: LineSegment StartX=-4.96891 StartY=-1.75 StartZ=0 EndX=-4.96891 EndY=1.75 EndZ=0
    g29: LineSegment StartX=-4.96891 StartY=1.75 StartZ=0 EndX=-8 EndY=3.5 EndZ=0
    g30: LineSegment StartX=-8 StartY=3.5 StartZ=0 EndX=-11.0311 EndY=1.75 EndZ=0
    g31: LineSegment StartX=-11.0311 StartY=1.75 StartZ=0 EndX=-11.0311 EndY=-1.75 EndZ=0
    g32: LineSegment StartX=-11.0311 StartY=-1.75 StartZ=0 EndX=-8 EndY=-3.5 EndZ=0
    g33: LineSegment StartX=-8 StartY=-3.5 StartZ=0 EndX=-4.96891 EndY=-1.75 EndZ=0
    g34: Circle [constr] CenterX=-8 CenterY=0 CenterZ=0 NormalX=0 NormalY=0 NormalZ=1 AngleXU=0 Radius=3.5
    g35: LineSegment StartX=-4.03109 StartY=-3.5 StartZ=0 EndX=-7.06218 EndY=-5.25 EndZ=0
    g36: LineSegment StartX=-7.06218 StartY=-5.25 StartZ=0 EndX=-7.06218 EndY=-8.75 EndZ=0
    g37: LineSegment StartX=-7.06218 StartY=-8.75 StartZ=0 EndX=-4.03109 EndY=-10.5 EndZ=0
    g38: LineSegment StartX=-4.03109 StartY=-10.5 StartZ=0 EndX=-1 EndY=-8.75 EndZ=0
    g39: LineSegment StartX=-1 StartY=-8.75 StartZ=0 EndX=-1 EndY=-5.25 EndZ=0
    g40: LineSegment StartX=-1 StartY=-5.25 StartZ=0 EndX=-4.03109 EndY=-3.5 EndZ=0
    g41: Circle [constr] CenterX=-4.03109 CenterY=-7 CenterZ=0 NormalX=0 NormalY=0 NormalZ=1 AngleXU=0 Radius=3.5
    g42: LineSegment StartX=4.03109 StartY=-3.5 StartZ=0 EndX=1 EndY=-5.25 EndZ=0
    g43: LineSegment StartX=1 StartY=-5.25 StartZ=0 EndX=1 EndY=-8.75 EndZ=0
    g44: LineSegment StartX=1 StartY=-8.75 StartZ=0 EndX=4.03109 EndY=-10.5 EndZ=0
    g45: LineSegment StartX=4.03109 StartY=-10.5 StartZ=0 EndX=7.06218 EndY=-8.75 EndZ=0
    g46: LineSegment StartX=7.06218 StartY=-8.75 StartZ=0 EndX=7.06218 EndY=-5.25 EndZ=0
    g47: LineSegment StartX=7.06218 StartY=-5.25 StartZ=0 EndX=4.03109 EndY=-3.5 EndZ=0
    g48: Circle [constr] CenterX=4.03109 CenterY=-7 CenterZ=0 NormalX=0 NormalY=0 NormalZ=1 AngleXU=0 Radius=3.5
  constraints (117):
    c: Coincident(g0,g1)
    c: Coincident(g1,g2)
    c: Coincident(g2,g3)
    c: Coincident(g3,g4)
    c: Coincident(g4,g5)
    c: Coincident(g5,g0)
    c: Equal(g0, g1-g5) x5
    c: PointOnObject(g0,g6)
    c: PointOnObject(g1,g6)
    c: PointOnObject(g2,g6)
    c: PointOnObject(g3,g6)
    c: PointOnObject(g4,g6)
    c: PointOnObject(g5,g6)
    c: Coincident(g6,g-1)
    c: Diameter(g6) = 7
    c: PointOnObject(g0,g-2)
    c: Coincident(g7,g8)
    c: Coincident(g8,g9)
    c: Coincident(g9,g10)
    c: Coincident(g10,g11)
    c: Coincident(g11,g12)
    c: Coincident(g12,g7)
    c: Equal(g7, g8-g12) x5
    c: PointOnObject(g7,g13)
    c: PointOnObject(g8,g13)
    c: PointOnObject(g9,g13)
    c: PointOnObject(g10,g13)
    c: PointOnObject(g11,g13)
    c: PointOnObject(g12,g13)
    c: PointOnObject(g13,g-1)
    c: Diameter(g13) = 7
    c: Distance(g6,g13) = 8
    c: Horizontal(g0,g10)
    c: Coincident(g14,g15)
    c: Coincident(g15,g16)
    c: Coincident(g16,g17)
    c: Coincident(g17,g18)
    c: Coincident(g18,g19)
    c: Coincident(g19,g14)
    c: Equal(g14, g15-g19) x5
    c: PointOnObject(g14,g20)
    c: PointOnObject(g15,g20)
    c: PointOnObject(g16,g20)
    c: PointOnObject(g17,g20)
    c: PointOnObject(g18,g20)
    c: PointOnObject(g19,g20)
    c: Diameter(g20) = 7
    c: DistanceY(g-1,g20) = 7
    c: Vertical(g18)
    c: Distance(g17,g-2) = 1
    c: Coincident(g21,g22)
    c: Coincident(g22,g23)
    c: Coincident(g23,g24)
    c: Coincident(g24,g25)
    c: Coincident(g25,g26)
    c: Coincident(g26,g21)
    c: Equal(g21, g22-g26) x5
    c: PointOnObject(g21,g27)
    c: PointOnObject(g22,g27)
    c: PointOnObject(g23,g27)
    c: PointOnObject(g24,g27)
    c: PointOnObject(g25,g27)
    c: PointOnObject(g26,g27)
    c: Diameter(g27) = 7
    c: DistanceY(g-1,g27) = 7
    c: DistanceX(g21,g-1) = 1
    c: Vertical(g21)
    c: Coincident(g28,g29)
    c: Coincident(g29,g30)
    c: Coincident(g30,g31)
    c: Coincident(g31,g32)
    c: Coincident(g32,g33)
    c: Coincident(g33,g28)
    c: Equal(g28, g29-g33) x5
    c: PointOnObject(g28,g34)
    c: PointOnObject(g29,g34)
    c: PointOnObject(g30,g34)
    c: PointOnObject(g31,g34)
    c: PointOnObject(g32,g34)
    c: PointOnObject(g33,g34)
    c: PointOnObject(g34,g-1)
    c: Diameter(g34) = 7
    c: Vertical(g31)
    c: DistanceX(g34,g-1) = 8
    c: Coincident(g35,g36)
    c: Coincident(g36,g37)
    c: Coincident(g37,g38)
    c: Coincident(g38,g39)
    c: Coincident(g39,g40)
    c: Coincident(g40,g35)
    c: Equal(g35, g36-g40) x5
    c: PointOnObject(g35,g41)
    c: PointOnObject(g36,g41)
    c: PointOnObject(g37,g41)
    c: PointOnObject(g38,g41)
    c: PointOnObject(g39,g41)
    c: PointOnObject(g40,g41)
    c: Coincident(g42,g43)
    c: Coincident(g43,g44)
    c: Coincident(g44,g45)
    c: Coincident(g45,g46)
    c: Coincident(g46,g47)
    c: Coincident(g47,g42)
    c: Equal(g42, g43-g47) x5
    c: PointOnObject(g42,g48)
    c: PointOnObject(g43,g48)
    c: PointOnObject(g44,g48)
    c: PointOnObject(g45,g48)
    c: PointOnObject(g46,g48)
    c: PointOnObject(g47,g48)
    c: Equal(g41,g48)
    c: Diameter(g41) = 7
    c: Vertical(g39)
    c: Vertical(g43)
    c: Distance(g-2,g39) = 1
    c: Symmetric(g38,g43,g-2)
    c: Distance(g41,g-1) = 7
FEATURE [Part::Extrusion] Extrude708  label="hex310"
  Base = -> Sketch717
  Dir = (0,-1,2e-16)
  DirMode = 2
  FaceMakerClass = Part::FaceMakerBullseye
  FaceMakerMode = 3
  LengthFwd = 10
  LengthRev = 0
  Placement = pos=(96,0,-14) rot=(0,0,1;0rad)
  Solid = true
  Symmetric = false
FEATURE [Sketcher::SketchObject] Sketch718
  ArcFitTolerance = 1e-06
  FullyConstrained = true
  MakeInternals = false
  Placement = pos=(0,0,0) rot=(1,0,0;1.5708rad)
  sketch-geometry (49):
    g0: LineSegment StartX=1e-16 StartY=3.5 StartZ=0 EndX=-3.03109 EndY=1.75 EndZ=0
    g1: LineSegment StartX=-3.03109 StartY=1.75 StartZ=0 EndX=-3.03109 EndY=-1.75 EndZ=0
    g2: LineSegment StartX=-3.03109 StartY=-1.75 StartZ=0 EndX=-1e-16 EndY=-3.5 EndZ=0
    g3: LineSegment StartX=-1e-16 StartY=-3.5 StartZ=0 EndX=3.03109 EndY=-1.75 EndZ=0
    g4: LineSegment StartX=3.03109 StartY=-1.75 StartZ=0 EndX=3.03109 EndY=1.75 EndZ=0
    g5: LineSegment StartX=3.03109 StartY=1.75 StartZ=0 EndX=1e-16 EndY=3.5 EndZ=0
    g6: Circle [constr] CenterX=0 CenterY=0 CenterZ=0 NormalX=0 NormalY=0 NormalZ=1 AngleXU=0 Radius=3.5
    g7: LineSegment StartX=4.96892 StartY=-1.75002 StartZ=0 EndX=8.00002 EndY=-3.5 EndZ=0
    g8: LineSegment StartX=8.00002 StartY=-3.5 StartZ=0 EndX=11.0311 EndY=-1.74998 EndZ=0
    g9: LineSegment StartX=11.0311 StartY=-1.74998 StartZ=0 EndX=11.0311 EndY=1.75002 EndZ=0
    g10: LineSegment StartX=11.0311 StartY=1.75002 StartZ=0 EndX=7.99998 EndY=3.5 EndZ=0
    g11: LineSegment StartX=7.99998 StartY=3.5 StartZ=0 EndX=4.9689 EndY=1.74998 EndZ=0
    g12: LineSegment StartX=4.9689 StartY=1.74998 StartZ=0 EndX=4.96892 EndY=-1.75002 EndZ=0
    g13: Circle [constr] CenterX=8 CenterY=0 CenterZ=0 NormalX=0 NormalY=0 NormalZ=1 AngleXU=0 Radius=3.5
    g14: LineSegment StartX=4.03109 StartY=3.5 StartZ=0 EndX=7.06218 EndY=5.25 EndZ=0
    g15: LineSegment StartX=7.06218 StartY=5.25 StartZ=0 EndX=7.06218 EndY=8.75 EndZ=0
    g16: LineSegment StartX=7.06218 StartY=8.75 StartZ=0 EndX=4.03109 EndY=10.5 EndZ=0
    g17: LineSegment StartX=4.03109 StartY=10.5 StartZ=0 EndX=1 EndY=8.75 EndZ=0
    g18: LineSegment StartX=1 StartY=8.75 StartZ=0 EndX=1 EndY=5.25 EndZ=0
    g19: LineSegment StartX=1 StartY=5.25 StartZ=0 EndX=4.03109 EndY=3.5 EndZ=0
    g20: Circle [constr] CenterX=4.03109 CenterY=7 CenterZ=0 NormalX=0 NormalY=0 NormalZ=1 AngleXU=0 Radius=3.5
    g21: LineSegment StartX=-1 StartY=5.25 StartZ=0 EndX=-1 EndY=8.75 EndZ=0
    g22: LineSegment StartX=-1 StartY=8.75 StartZ=0 EndX=-4.03109 EndY=10.5 EndZ=0
    g23: LineSegment StartX=-4.03109 StartY=10.5 StartZ=0 EndX=-7.06218 EndY=8.75 EndZ=0
    g24: LineSegment StartX=-7.06218 StartY=8.75 StartZ=0 EndX=-7.06218 EndY=5.25 EndZ=0
    g25: LineSegment StartX=-7.06218 StartY=5.25 StartZ=0 EndX=-4.03109 EndY=3.5 EndZ=0
    g26: LineSegment StartX=-4.03109 StartY=3.5 StartZ=0 EndX=-1 EndY=5.25 EndZ=0
    g27: Circle [constr] CenterX=-4.03109 CenterY=7 CenterZ=0 NormalX=0 NormalY=0 NormalZ=1 AngleXU=0 Radius=3.5
    g28: LineSegment StartX=-4.96891 StartY=-1.75 StartZ=0 EndX=-4.96891 EndY=1.75 EndZ=0
    g29: LineSegment StartX=-4.96891 StartY=1.75 StartZ=0 EndX=-8 EndY=3.5 EndZ=0
    g30: LineSegment StartX=-8 StartY=3.5 StartZ=0 EndX=-11.0311 EndY=1.75 EndZ=0
    g31: LineSegment StartX=-11.0311 StartY=1.75 StartZ=0 EndX=-11.0311 EndY=-1.75 EndZ=0
    g32: LineSegment StartX=-11.0311 StartY=-1.75 StartZ=0 EndX=-8 EndY=-3.5 EndZ=0
    g33: LineSegment StartX=-8 StartY=-3.5 StartZ=0 EndX=-4.96891 EndY=-1.75 EndZ=0
    g34: Circle [constr] CenterX=-8 CenterY=0 CenterZ=0 NormalX=0 NormalY=0 NormalZ=1 AngleXU=0 Radius=3.5
    g35: LineSegment StartX=-4.03109 StartY=-3.5 StartZ=0 EndX=-7.06218 EndY=-5.25 EndZ=0
    g36: LineSegment StartX=-7.06218 StartY=-5.25 StartZ=0 EndX=-7.06218 EndY=-8.75 EndZ=0
    g37: LineSegment StartX=-7.06218 StartY=-8.75 StartZ=0 EndX=-4.03109 EndY=-10.5 EndZ=0
    g38: LineSegment StartX=-4.03109 StartY=-10.5 StartZ=0 EndX=-1 EndY=-8.75 EndZ=0
    g39: LineSegment StartX=-1 StartY=-8.75 StartZ=0 EndX=-1 EndY=-5.25 EndZ=0
    g40: LineSegment StartX=-1 StartY=-5.25 StartZ=0 EndX=-4.03109 EndY=-3.5 EndZ=0
    g41: Circle [constr] CenterX=-4.03109 CenterY=-7 CenterZ=0 NormalX=0 NormalY=0 NormalZ=1 AngleXU=0 Radius=3.5
    g42: LineSegment StartX=4.03109 StartY=-3.5 StartZ=0 EndX=1 EndY=-5.25 EndZ=0
    g43: LineSegment StartX=1 StartY=-5.25 StartZ=0 EndX=1 EndY=-8.75 EndZ=0
    g44: LineSegment StartX=1 StartY=-8.75 StartZ=0 EndX=4.03109 EndY=-10.5 EndZ=0
    g45: LineSegment StartX=4.03109 StartY=-10.5 StartZ=0 EndX=7.06218 EndY=-8.75 EndZ=0
    g46: LineSegment StartX=7.06218 StartY=-8.75 StartZ=0 EndX=7.06218 EndY=-5.25 EndZ=0
    g47: LineSegment StartX=7.06218 StartY=-5.25 StartZ=0 EndX=4.03109 EndY=-3.5 EndZ=0
    g48: Circle [constr] CenterX=4.03109 CenterY=-7 CenterZ=0 NormalX=0 NormalY=0 NormalZ=1 AngleXU=0 Radius=3.5
  constraints (117):
    c: Coincident(g0,g1)
    c: Coincident(g1,g2)
    c: Coincident(g2,g3)
    c: Coincident(g3,g4)
    c: Coincident(g4,g5)
    c: Coincident(g5,g0)
    c: Equal(g0, g1-g5) x5
    c: PointOnObject(g0,g6)
    c: PointOnObject(g1,g6)
    c: PointOnObject(g2,g6)
    c: PointOnObject(g3,g6)
    c: PointOnObject(g4,g6)
    c: PointOnObject(g5,g6)
    c: Coincident(g6,g-1)
    c: Diameter(g6) = 7
    c: PointOnObject(g0,g-2)
    c: Coincident(g7,g8)
    c: Coincident(g8,g9)
    c: Coincident(g9,g10)
    c: Coincident(g10,g11)
    c: Coincident(g11,g12)
    c: Coincident(g12,g7)
    c: Equal(g7, g8-g12) x5
    c: PointOnObject(g7,g13)
    c: PointOnObject(g8,g13)
    c: PointOnObject(g9,g13)
    c: PointOnObject(g10,g13)
    c: PointOnObject(g11,g13)
    c: PointOnObject(g12,g13)
    c: PointOnObject(g13,g-1)
    c: Diameter(g13) = 7
    c: Distance(g6,g13) = 8
    c: Horizontal(g0,g10)
    c: Coincident(g14,g15)
    c: Coincident(g15,g16)
    c: Coincident(g16,g17)
    c: Coincident(g17,g18)
    c: Coincident(g18,g19)
    c: Coincident(g19,g14)
    c: Equal(g14, g15-g19) x5
    c: PointOnObject(g14,g20)
    c: PointOnObject(g15,g20)
    c: PointOnObject(g16,g20)
    c: PointOnObject(g17,g20)
    c: PointOnObject(g18,g20)
    c: PointOnObject(g19,g20)
    c: Diameter(g20) = 7
    c: DistanceY(g-1,g20) = 7
    c: Vertical(g18)
    c: Distance(g17,g-2) = 1
    c: Coincident(g21,g22)
    c: Coincident(g22,g23)
    c: Coincident(g23,g24)
    c: Coincident(g24,g25)
    c: Coincident(g25,g26)
    c: Coincident(g26,g21)
    c: Equal(g21, g22-g26) x5
    c: PointOnObject(g21,g27)
    c: PointOnObject(g22,g27)
    c: PointOnObject(g23,g27)
    c: PointOnObject(g24,g27)
    c: PointOnObject(g25,g27)
    c: PointOnObject(g26,g27)
    c: Diameter(g27) = 7
    c: DistanceY(g-1,g27) = 7
    c: DistanceX(g21,g-1) = 1
    c: Vertical(g21)
    c: Coincident(g28,g29)
    c: Coincident(g29,g30)
    c: Coincident(g30,g31)
    c: Coincident(g31,g32)
    c: Coincident(g32,g33)
    c: Coincident(g33,g28)
    c: Equal(g28, g29-g33) x5
    c: PointOnObject(g28,g34)
    c: PointOnObject(g29,g34)
    c: PointOnObject(g30,g34)
    c: PointOnObject(g31,g34)
    c: PointOnObject(g32,g34)
    c: PointOnObject(g33,g34)
    c: PointOnObject(g34,g-1)
    c: Diameter(g34) = 7
    c: Vertical(g31)
    c: DistanceX(g34,g-1) = 8
    c: Coincident(g35,g36)
    c: Coincident(g36,g37)
    c: Coincident(g37,g38)
    c: Coincident(g38,g39)
    c: Coincident(g39,g40)
    c: Coincident(g40,g35)
    c: Equal(g35, g36-g40) x5
    c: PointOnObject(g35,g41)
    c: PointOnObject(g36,g41)
    c: PointOnObject(g37,g41)
    c: PointOnObject(g38,g41)
    c: PointOnObject(g39,g41)
    c: PointOnObject(g40,g41)
    c: Coincident(g42,g43)
    c: Coincident(g43,g44)
    c: Coincident(g44,g45)
    c: Coincident(g45,g46)
    c: Coincident(g46,g47)
    c: Coincident(g47,g42)
    c: Equal(g42, g43-g47) x5
    c: PointOnObject(g42,g48)
    c: PointOnObject(g43,g48)
    c: PointOnObject(g44,g48)
    c: PointOnObject(g45,g48)
    c: PointOnObject(g46,g48)
    c: PointOnObject(g47,g48)
    c: Equal(g41,g48)
    c: Diameter(g41) = 7
    c: Vertical(g39)
    c: Vertical(g43)
    c: Distance(g-2,g39) = 1
    c: Symmetric(g38,g43,g-2)
    c: Distance(g41,g-1) = 7
FEATURE [Part::Extrusion] Extrude709  label="hex311"
  Base = -> Sketch718
  Dir = (0,-1,2e-16)
  DirMode = 2
  FaceMakerClass = Part::FaceMakerBullseye
  FaceMakerMode = 3
  LengthFwd = 10
  LengthRev = 0
  Placement = pos=(88,0,-28) rot=(0,0,1;0rad)
  Solid = true
  Symmetric = false
FEATURE [Sketcher::SketchObject] Sketch719
  ArcFitTolerance = 1e-06
  FullyConstrained = true
  MakeInternals = false
  Placement = pos=(0,0,0) rot=(1,0,0;1.5708rad)
  sketch-geometry (49):
    g0: LineSegment StartX=1e-16 StartY=3.5 StartZ=0 EndX=-3.03109 EndY=1.75 EndZ=0
    g1: LineSegment StartX=-3.03109 StartY=1.75 StartZ=0 EndX=-3.03109 EndY=-1.75 EndZ=0
    g2: LineSegment StartX=-3.03109 StartY=-1.75 StartZ=0 EndX=-1e-16 EndY=-3.5 EndZ=0
    g3: LineSegment StartX=-1e-16 StartY=-3.5 StartZ=0 EndX=3.03109 EndY=-1.75 EndZ=0
    g4: LineSegment StartX=3.03109 StartY=-1.75 StartZ=0 EndX=3.03109 EndY=1.75 EndZ=0
    g5: LineSegment StartX=3.03109 StartY=1.75 StartZ=0 EndX=1e-16 EndY=3.5 EndZ=0
    g6: Circle [constr] CenterX=0 CenterY=0 CenterZ=0 NormalX=0 NormalY=0 NormalZ=1 AngleXU=0 Radius=3.5
    g7: LineSegment StartX=4.96892 StartY=-1.75002 StartZ=0 EndX=8.00002 EndY=-3.5 EndZ=0
    g8: LineSegment StartX=8.00002 StartY=-3.5 StartZ=0 EndX=11.0311 EndY=-1.74998 EndZ=0
    g9: LineSegment StartX=11.0311 StartY=-1.74998 StartZ=0 EndX=11.0311 EndY=1.75002 EndZ=0
    g10: LineSegment StartX=11.0311 StartY=1.75002 StartZ=0 EndX=7.99998 EndY=3.5 EndZ=0
    g11: LineSegment StartX=7.99998 StartY=3.5 StartZ=0 EndX=4.9689 EndY=1.74998 EndZ=0
    g12: LineSegment StartX=4.9689 StartY=1.74998 StartZ=0 EndX=4.96892 EndY=-1.75002 EndZ=0
    g13: Circle [constr] CenterX=8 CenterY=0 CenterZ=0 NormalX=0 NormalY=0 NormalZ=1 AngleXU=0 Radius=3.5
    g14: LineSegment StartX=4.03109 StartY=3.5 StartZ=0 EndX=7.06218 EndY=5.25 EndZ=0
    g15: LineSegment StartX=7.06218 StartY=5.25 StartZ=0 EndX=7.06218 EndY=8.75 EndZ=0
    g16: LineSegment StartX=7.06218 StartY=8.75 StartZ=0 EndX=4.03109 EndY=10.5 EndZ=0
    g17: LineSegment StartX=4.03109 StartY=10.5 StartZ=0 EndX=1 EndY=8.75 EndZ=0
    g18: LineSegment StartX=1 StartY=8.75 StartZ=0 EndX=1 EndY=5.25 EndZ=0
    g19: LineSegment StartX=1 StartY=5.25 StartZ=0 EndX=4.03109 EndY=3.5 EndZ=0
    g20: Circle [constr] CenterX=4.03109 CenterY=7 CenterZ=0 NormalX=0 NormalY=0 NormalZ=1 AngleXU=0 Radius=3.5
    g21: LineSegment StartX=-1 StartY=5.25 StartZ=0 EndX=-1 EndY=8.75 EndZ=0
    g22: LineSegment StartX=-1 StartY=8.75 StartZ=0 EndX=-4.03109 EndY=10.5 EndZ=0
    g23: LineSegment StartX=-4.03109 StartY=10.5 StartZ=0 EndX=-7.06218 EndY=8.75 EndZ=0
    g24: LineSegment StartX=-7.06218 StartY=8.75 StartZ=0 EndX=-7.06218 EndY=5.25 EndZ=0
    g25: LineSegment StartX=-7.06218 StartY=5.25 StartZ=0 EndX=-4.03109 EndY=3.5 EndZ=0
    g26: LineSegment StartX=-4.03109 StartY=3.5 StartZ=0 EndX=-1 EndY=5.25 EndZ=0
    g27: Circle [constr] CenterX=-4.03109 CenterY=7 CenterZ=0 NormalX=0 NormalY=0 NormalZ=1 AngleXU=0 Radius=3.5
    g28: LineSegment StartX=-4.96891 StartY=-1.75 StartZ=0 EndX=-4.96891 EndY=1.75 EndZ=0
    g29: LineSegment StartX=-4.96891 StartY=1.75 StartZ=0 EndX=-8 EndY=3.5 EndZ=0
    g30: LineSegment StartX=-8 StartY=3.5 StartZ=0 EndX=-11.0311 EndY=1.75 EndZ=0
    g31: LineSegment StartX=-11.0311 StartY=1.75 StartZ=0 EndX=-11.0311 EndY=-1.75 EndZ=0
    g32: LineSegment StartX=-11.0311 StartY=-1.75 StartZ=0 EndX=-8 EndY=-3.5 EndZ=0
    g33: LineSegment StartX=-8 StartY=-3.5 StartZ=0 EndX=-4.96891 EndY=-1.75 EndZ=0
    g34: Circle [constr] CenterX=-8 CenterY=0 CenterZ=0 NormalX=0 NormalY=0 NormalZ=1 AngleXU=0 Radius=3.5
    g35: LineSegment StartX=-4.03109 StartY=-3.5 StartZ=0 EndX=-7.06218 EndY=-5.25 EndZ=0
    g36: LineSegment StartX=-7.06218 StartY=-5.25 StartZ=0 EndX=-7.06218 EndY=-8.75 EndZ=0
    g37: LineSegment StartX=-7.06218 StartY=-8.75 StartZ=0 EndX=-4.03109 EndY=-10.5 EndZ=0
    g38: LineSegment StartX=-4.03109 StartY=-10.5 StartZ=0 EndX=-1 EndY=-8.75 EndZ=0
    g39: LineSegment StartX=-1 StartY=-8.75 StartZ=0 EndX=-1 EndY=-5.25 EndZ=0
    g40: LineSegment StartX=-1 StartY=-5.25 StartZ=0 EndX=-4.03109 EndY=-3.5 EndZ=0
    g41: Circle [constr] CenterX=-4.03109 CenterY=-7 CenterZ=0 NormalX=0 NormalY=0 NormalZ=1 AngleXU=0 Radius=3.5
    g42: LineSegment StartX=4.03109 StartY=-3.5 StartZ=0 EndX=1 EndY=-5.25 EndZ=0
    g43: LineSegment StartX=1 StartY=-5.25 StartZ=0 EndX=1 EndY=-8.75 EndZ=0
    g44: LineSegment StartX=1 StartY=-8.75 StartZ=0 EndX=4.03109 EndY=-10.5 EndZ=0
    g45: LineSegment StartX=4.03109 StartY=-10.5 StartZ=0 EndX=7.06218 EndY=-8.75 EndZ=0
    g46: LineSegment StartX=7.06218 StartY=-8.75 StartZ=0 EndX=7.06218 EndY=-5.25 EndZ=0
    g47: LineSegment StartX=7.06218 StartY=-5.25 StartZ=0 EndX=4.03109 EndY=-3.5 EndZ=0
    g48: Circle [constr] CenterX=4.03109 CenterY=-7 CenterZ=0 NormalX=0 NormalY=0 NormalZ=1 AngleXU=0 Radius=3.5
  constraints (117):
    c: Coincident(g0,g1)
    c: Coincident(g1,g2)
    c: Coincident(g2,g3)
    c: Coincident(g3,g4)
    c: Coincident(g4,g5)
    c: Coincident(g5,g0)
    c: Equal(g0, g1-g5) x5
    c: PointOnObject(g0,g6)
    c: PointOnObject(g1,g6)
    c: PointOnObject(g2,g6)
    c: PointOnObject(g3,g6)
    c: PointOnObject(g4,g6)
    c: PointOnObject(g5,g6)
    c: Coincident(g6,g-1)
    c: Diameter(g6) = 7
    c: PointOnObject(g0,g-2)
    c: Coincident(g7,g8)
    c: Coincident(g8,g9)
    c: Coincident(g9,g10)
    c: Coincident(g10,g11)
    c: Coincident(g11,g12)
    c: Coincident(g12,g7)
    c: Equal(g7, g8-g12) x5
    c: PointOnObject(g7,g13)
    c: PointOnObject(g8,g13)
    c: PointOnObject(g9,g13)
    c: PointOnObject(g10,g13)
    c: PointOnObject(g11,g13)
    c: PointOnObject(g12,g13)
    c: PointOnObject(g13,g-1)
    c: Diameter(g13) = 7
    c: Distance(g6,g13) = 8
    c: Horizontal(g0,g10)
    c: Coincident(g14,g15)
    c: Coincident(g15,g16)
    c: Coincident(g16,g17)
    c: Coincident(g17,g18)
    c: Coincident(g18,g19)
    c: Coincident(g19,g14)
    c: Equal(g14, g15-g19) x5
    c: PointOnObject(g14,g20)
    c: PointOnObject(g15,g20)
    c: PointOnObject(g16,g20)
    c: PointOnObject(g17,g20)
    c: PointOnObject(g18,g20)
    c: PointOnObject(g19,g20)
    c: Diameter(g20) = 7
    c: DistanceY(g-1,g20) = 7
    c: Vertical(g18)
    c: Distance(g17,g-2) = 1
    c: Coincident(g21,g22)
    c: Coincident(g22,g23)
    c: Coincident(g23,g24)
    c: Coincident(g24,g25)
    c: Coincident(g25,g26)
    c: Coincident(g26,g21)
    c: Equal(g21, g22-g26) x5
    c: PointOnObject(g21,g27)
    c: PointOnObject(g22,g27)
    c: PointOnObject(g23,g27)
    c: PointOnObject(g24,g27)
    c: PointOnObject(g25,g27)
    c: PointOnObject(g26,g27)
    c: Diameter(g27) = 7
    c: DistanceY(g-1,g27) = 7
    c: DistanceX(g21,g-1) = 1
    c: Vertical(g21)
    c: Coincident(g28,g29)
    c: Coincident(g29,g30)
    c: Coincident(g30,g31)
    c: Coincident(g31,g32)
    c: Coincident(g32,g33)
    c: Coincident(g33,g28)
    c: Equal(g28, g29-g33) x5
    c: PointOnObject(g28,g34)
    c: PointOnObject(g29,g34)
    c: PointOnObject(g30,g34)
    c: PointOnObject(g31,g34)
    c: PointOnObject(g32,g34)
    c: PointOnObject(g33,g34)
    c: PointOnObject(g34,g-1)
    c: Diameter(g34) = 7
    c: Vertical(g31)
    c: DistanceX(g34,g-1) = 8
    c: Coincident(g35,g36)
    c: Coincident(g36,g37)
    c: Coincident(g37,g38)
    c: Coincident(g38,g39)
    c: Coincident(g39,g40)
    c: Coincident(g40,g35)
    c: Equal(g35, g36-g40) x5
    c: PointOnObject(g35,g41)
    c: PointOnObject(g36,g41)
    c: PointOnObject(g37,g41)
    c: PointOnObject(g38,g41)
    c: PointOnObject(g39,g41)
    c: PointOnObject(g40,g41)
    c: Coincident(g42,g43)
    c: Coincident(g43,g44)
    c: Coincident(g44,g45)
    c: Coincident(g45,g46)
    c: Coincident(g46,g47)
    c: Coincident(g47,g42)
    c: Equal(g42, g43-g47) x5
    c: PointOnObject(g42,g48)
    c: PointOnObject(g43,g48)
    c: PointOnObject(g44,g48)
    c: PointOnObject(g45,g48)
    c: PointOnObject(g46,g48)
    c: PointOnObject(g47,g48)
    c: Equal(g41,g48)
    c: Diameter(g41) = 7
    c: Vertical(g39)
    c: Vertical(g43)
    c: Distance(g-2,g39) = 1
    c: Symmetric(g38,g43,g-2)
    c: Distance(g41,g-1) = 7
FEATURE [Part::Extrusion] Extrude710  label="hex312"
  Base = -> Sketch719
  Dir = (0,-1,2e-16)
  DirMode = 2
  FaceMakerClass = Part::FaceMakerBullseye
  FaceMakerMode = 3
  LengthFwd = 10
  LengthRev = 0
  Placement = pos=(104,0,-28) rot=(0,0,1;0rad)
  Solid = true
  Symmetric = false
FEATURE [Sketcher::SketchObject] Sketch720
  ArcFitTolerance = 1e-06
  FullyConstrained = true
  MakeInternals = false
  Placement = pos=(0,0,0) rot=(1,0,0;1.5708rad)
  sketch-geometry (49):
    g0: LineSegment StartX=1e-16 StartY=3.5 StartZ=0 EndX=-3.03109 EndY=1.75 EndZ=0
    g1: LineSegment StartX=-3.03109 StartY=1.75 StartZ=0 EndX=-3.03109 EndY=-1.75 EndZ=0
    g2: LineSegment StartX=-3.03109 StartY=-1.75 StartZ=0 EndX=-1e-16 EndY=-3.5 EndZ=0
    g3: LineSegment StartX=-1e-16 StartY=-3.5 StartZ=0 EndX=3.03109 EndY=-1.75 EndZ=0
    g4: LineSegment StartX=3.03109 StartY=-1.75 StartZ=0 EndX=3.03109 EndY=1.75 EndZ=0
    g5: LineSegment StartX=3.03109 StartY=1.75 StartZ=0 EndX=1e-16 EndY=3.5 EndZ=0
    g6: Circle [constr] CenterX=0 CenterY=0 CenterZ=0 NormalX=0 NormalY=0 NormalZ=1 AngleXU=0 Radius=3.5
    g7: LineSegment StartX=4.96892 StartY=-1.75002 StartZ=0 EndX=8.00002 EndY=-3.5 EndZ=0
    g8: LineSegment StartX=8.00002 StartY=-3.5 StartZ=0 EndX=11.0311 EndY=-1.74998 EndZ=0
    g9: LineSegment StartX=11.0311 StartY=-1.74998 StartZ=0 EndX=11.0311 EndY=1.75002 EndZ=0
    g10: LineSegment StartX=11.0311 StartY=1.75002 StartZ=0 EndX=7.99998 EndY=3.5 EndZ=0
    g11: LineSegment StartX=7.99998 StartY=3.5 StartZ=0 EndX=4.9689 EndY=1.74998 EndZ=0
    g12: LineSegment StartX=4.9689 StartY=1.74998 StartZ=0 EndX=4.96892 EndY=-1.75002 EndZ=0
    g13: Circle [constr] CenterX=8 CenterY=0 CenterZ=0 NormalX=0 NormalY=0 NormalZ=1 AngleXU=0 Radius=3.5
    g14: LineSegment StartX=4.03109 StartY=3.5 StartZ=0 EndX=7.06218 EndY=5.25 EndZ=0
    g15: LineSegment StartX=7.06218 StartY=5.25 StartZ=0 EndX=7.06218 EndY=8.75 EndZ=0
    g16: LineSegment StartX=7.06218 StartY=8.75 StartZ=0 EndX=4.03109 EndY=10.5 EndZ=0
    g17: LineSegment StartX=4.03109 StartY=10.5 StartZ=0 EndX=1 EndY=8.75 EndZ=0
    g18: LineSegment StartX=1 StartY=8.75 StartZ=0 EndX=1 EndY=5.25 EndZ=0
    g19: LineSegment StartX=1 StartY=5.25 StartZ=0 EndX=4.03109 EndY=3.5 EndZ=0
    g20: Circle [constr] CenterX=4.03109 CenterY=7 CenterZ=0 NormalX=0 NormalY=0 NormalZ=1 AngleXU=0 Radius=3.5
    g21: LineSegment StartX=-1 StartY=5.25 StartZ=0 EndX=-1 EndY=8.75 EndZ=0
    g22: LineSegment StartX=-1 StartY=8.75 StartZ=0 EndX=-4.03109 EndY=10.5 EndZ=0
    g23: LineSegment StartX=-4.03109 StartY=10.5 StartZ=0 EndX=-7.06218 EndY=8.75 EndZ=0
    g24: LineSegment StartX=-7.06218 StartY=8.75 StartZ=0 EndX=-7.06218 EndY=5.25 EndZ=0
    g25: LineSegment StartX=-7.06218 StartY=5.25 StartZ=0 EndX=-4.03109 EndY=3.5 EndZ=0
    g26: LineSegment StartX=-4.03109 StartY=3.5 StartZ=0 EndX=-1 EndY=5.25 EndZ=0
    g27: Circle [constr] CenterX=-4.03109 CenterY=7 CenterZ=0 NormalX=0 NormalY=0 NormalZ=1 AngleXU=0 Radius=3.5
    g28: LineSegment StartX=-4.96891 StartY=-1.75 StartZ=0 EndX=-4.96891 EndY=1.75 EndZ=0
    g29: LineSegment StartX=-4.96891 StartY=1.75 StartZ=0 EndX=-8 EndY=3.5 EndZ=0
    g30: LineSegment StartX=-8 StartY=3.5 StartZ=0 EndX=-11.0311 EndY=1.75 EndZ=0
    g31: LineSegment StartX=-11.0311 StartY=1.75 StartZ=0 EndX=-11.0311 EndY=-1.75 EndZ=0
    g32: LineSegment StartX=-11.0311 StartY=-1.75 StartZ=0 EndX=-8 EndY=-3.5 EndZ=0
    g33: LineSegment StartX=-8 StartY=-3.5 StartZ=0 EndX=-4.96891 EndY=-1.75 EndZ=0
    g34: Circle [constr] CenterX=-8 CenterY=0 CenterZ=0 NormalX=0 NormalY=0 NormalZ=1 AngleXU=0 Radius=3.5
    g35: LineSegment StartX=-4.03109 StartY=-3.5 StartZ=0 EndX=-7.06218 EndY=-5.25 EndZ=0
    g36: LineSegment StartX=-7.06218 StartY=-5.25 StartZ=0 EndX=-7.06218 EndY=-8.75 EndZ=0
    g37: LineSegment StartX=-7.06218 StartY=-8.75 StartZ=0 EndX=-4.03109 EndY=-10.5 EndZ=0
    g38: LineSegment StartX=-4.03109 StartY=-10.5 StartZ=0 EndX=-1 EndY=-8.75 EndZ=0
    g39: LineSegment StartX=-1 StartY=-8.75 StartZ=0 EndX=-1 EndY=-5.25 EndZ=0
    g40: LineSegment StartX=-1 StartY=-5.25 StartZ=0 EndX=-4.03109 EndY=-3.5 EndZ=0
    g41: Circle [constr] CenterX=-4.03109 CenterY=-7 CenterZ=0 NormalX=0 NormalY=0 NormalZ=1 AngleXU=0 Radius=3.5
    g42: LineSegment StartX=4.03109 StartY=-3.5 StartZ=0 EndX=1 EndY=-5.25 EndZ=0
    g43: LineSegment StartX=1 StartY=-5.25 StartZ=0 EndX=1 EndY=-8.75 EndZ=0
    g44: LineSegment StartX=1 StartY=-8.75 StartZ=0 EndX=4.03109 EndY=-10.5 EndZ=0
    g45: LineSegment StartX=4.03109 StartY=-10.5 StartZ=0 EndX=7.06218 EndY=-8.75 EndZ=0
    g46: LineSegment StartX=7.06218 StartY=-8.75 StartZ=0 EndX=7.06218 EndY=-5.25 EndZ=0
    g47: LineSegment StartX=7.06218 StartY=-5.25 StartZ=0 EndX=4.03109 EndY=-3.5 EndZ=0
    g48: Circle [constr] CenterX=4.03109 CenterY=-7 CenterZ=0 NormalX=0 NormalY=0 NormalZ=1 AngleXU=0 Radius=3.5
  constraints (117):
    c: Coincident(g0,g1)
    c: Coincident(g1,g2)
    c: Coincident(g2,g3)
    c: Coincident(g3,g4)
    c: Coincident(g4,g5)
    c: Coincident(g5,g0)
    c: Equal(g0, g1-g5) x5
    c: PointOnObject(g0,g6)
    c: PointOnObject(g1,g6)
    c: PointOnObject(g2,g6)
    c: PointOnObject(g3,g6)
    c: PointOnObject(g4,g6)
    c: PointOnObject(g5,g6)
    c: Coincident(g6,g-1)
    c: Diameter(g6) = 7
    c: PointOnObject(g0,g-2)
    c: Coincident(g7,g8)
    c: Coincident(g8,g9)
    c: Coincident(g9,g10)
    c: Coincident(g10,g11)
    c: Coincident(g11,g12)
    c: Coincident(g12,g7)
    c: Equal(g7, g8-g12) x5
    c: PointOnObject(g7,g13)
    c: PointOnObject(g8,g13)
    c: PointOnObject(g9,g13)
    c: PointOnObject(g10,g13)
    c: PointOnObject(g11,g13)
    c: PointOnObject(g12,g13)
    c: PointOnObject(g13,g-1)
    c: Diameter(g13) = 7
    c: Distance(g6,g13) = 8
    c: Horizontal(g0,g10)
    c: Coincident(g14,g15)
    c: Coincident(g15,g16)
    c: Coincident(g16,g17)
    c: Coincident(g17,g18)
    c: Coincident(g18,g19)
    c: Coincident(g19,g14)
    c: Equal(g14, g15-g19) x5
    c: PointOnObject(g14,g20)
    c: PointOnObject(g15,g20)
    c: PointOnObject(g16,g20)
    c: PointOnObject(g17,g20)
    c: PointOnObject(g18,g20)
    c: PointOnObject(g19,g20)
    c: Diameter(g20) = 7
    c: DistanceY(g-1,g20) = 7
    c: Vertical(g18)
    c: Distance(g17,g-2) = 1
    c: Coincident(g21,g22)
    c: Coincident(g22,g23)
    c: Coincident(g23,g24)
    c: Coincident(g24,g25)
    c: Coincident(g25,g26)
    c: Coincident(g26,g21)
    c: Equal(g21, g22-g26) x5
    c: PointOnObject(g21,g27)
    c: PointOnObject(g22,g27)
    c: PointOnObject(g23,g27)
    c: PointOnObject(g24,g27)
    c: PointOnObject(g25,g27)
    c: PointOnObject(g26,g27)
    c: Diameter(g27) = 7
    c: DistanceY(g-1,g27) = 7
    c: DistanceX(g21,g-1) = 1
    c: Vertical(g21)
    c: Coincident(g28,g29)
    c: Coincident(g29,g30)
    c: Coincident(g30,g31)
    c: Coincident(g31,g32)
    c: Coincident(g32,g33)
    c: Coincident(g33,g28)
    c: Equal(g28, g29-g33) x5
    c: PointOnObject(g28,g34)
    c: PointOnObject(g29,g34)
    c: PointOnObject(g30,g34)
    c: PointOnObject(g31,g34)
    c: PointOnObject(g32,g34)
    c: PointOnObject(g33,g34)
    c: PointOnObject(g34,g-1)
    c: Diameter(g34) = 7
    c: Vertical(g31)
    c: DistanceX(g34,g-1) = 8
    c: Coincident(g35,g36)
    c: Coincident(g36,g37)
    c: Coincident(g37,g38)
    c: Coincident(g38,g39)
    c: Coincident(g39,g40)
    c: Coincident(g40,g35)
    c: Equal(g35, g36-g40) x5
    c: PointOnObject(g35,g41)
    c: PointOnObject(g36,g41)
    c: PointOnObject(g37,g41)
    c: PointOnObject(g38,g41)
    c: PointOnObject(g39,g41)
    c: PointOnObject(g40,g41)
    c: Coincident(g42,g43)
    c: Coincident(g43,g44)
    c: Coincident(g44,g45)
    c: Coincident(g45,g46)
    c: Coincident(g46,g47)
    c: Coincident(g47,g42)
    c: Equal(g42, g43-g47) x5
    c: PointOnObject(g42,g48)
    c: PointOnObject(g43,g48)
    c: PointOnObject(g44,g48)
    c: PointOnObject(g45,g48)
    c: PointOnObject(g46,g48)
    c: PointOnObject(g47,g48)
    c: Equal(g41,g48)
    c: Diameter(g41) = 7
    c: Vertical(g39)
    c: Vertical(g43)
    c: Distance(g-2,g39) = 1
    c: Symmetric(g38,g43,g-2)
    c: Distance(g41,g-1) = 7
FEATURE [Part::Extrusion] Extrude711  label="hex313"
  Base = -> Sketch720
  Dir = (0,-1,2e-16)
  DirMode = 2
  FaceMakerClass = Part::FaceMakerBullseye
  FaceMakerMode = 3
  LengthFwd = 10
  LengthRev = 0
  Placement = pos=(-96,0,-14) rot=(0,0,1;0rad)
  Solid = true
  Symmetric = false
FEATURE [Sketcher::SketchObject] Sketch721
  ArcFitTolerance = 1e-06
  FullyConstrained = true
  MakeInternals = false
  Placement = pos=(0,0,0) rot=(1,0,0;1.5708rad)
  sketch-geometry (49):
    g0: LineSegment StartX=1e-16 StartY=3.5 StartZ=0 EndX=-3.03109 EndY=1.75 EndZ=0
    g1: LineSegment StartX=-3.03109 StartY=1.75 StartZ=0 EndX=-3.03109 EndY=-1.75 EndZ=0
    g2: LineSegment StartX=-3.03109 StartY=-1.75 StartZ=0 EndX=-1e-16 EndY=-3.5 EndZ=0
    g3: LineSegment StartX=-1e-16 StartY=-3.5 StartZ=0 EndX=3.03109 EndY=-1.75 EndZ=0
    g4: LineSegment StartX=3.03109 StartY=-1.75 StartZ=0 EndX=3.03109 EndY=1.75 EndZ=0
    g5: LineSegment StartX=3.03109 StartY=1.75 StartZ=0 EndX=1e-16 EndY=3.5 EndZ=0
    g6: Circle [constr] CenterX=0 CenterY=0 CenterZ=0 NormalX=0 NormalY=0 NormalZ=1 AngleXU=0 Radius=3.5
    g7: LineSegment StartX=4.96892 StartY=-1.75002 StartZ=0 EndX=8.00002 EndY=-3.5 EndZ=0
    g8: LineSegment StartX=8.00002 StartY=-3.5 StartZ=0 EndX=11.0311 EndY=-1.74998 EndZ=0
    g9: LineSegment StartX=11.0311 StartY=-1.74998 StartZ=0 EndX=11.0311 EndY=1.75002 EndZ=0
    g10: LineSegment StartX=11.0311 StartY=1.75002 StartZ=0 EndX=7.99998 EndY=3.5 EndZ=0
    g11: LineSegment StartX=7.99998 StartY=3.5 StartZ=0 EndX=4.9689 EndY=1.74998 EndZ=0
    g12: LineSegment StartX=4.9689 StartY=1.74998 StartZ=0 EndX=4.96892 EndY=-1.75002 EndZ=0
    g13: Circle [constr] CenterX=8 CenterY=0 CenterZ=0 NormalX=0 NormalY=0 NormalZ=1 AngleXU=0 Radius=3.5
    g14: LineSegment StartX=4.03109 StartY=3.5 StartZ=0 EndX=7.06218 EndY=5.25 EndZ=0
    g15: LineSegment StartX=7.06218 StartY=5.25 StartZ=0 EndX=7.06218 EndY=8.75 EndZ=0
    g16: LineSegment StartX=7.06218 StartY=8.75 StartZ=0 EndX=4.03109 EndY=10.5 EndZ=0
    g17: LineSegment StartX=4.03109 StartY=10.5 StartZ=0 EndX=1 EndY=8.75 EndZ=0
    g18: LineSegment StartX=1 StartY=8.75 StartZ=0 EndX=1 EndY=5.25 EndZ=0
    g19: LineSegment StartX=1 StartY=5.25 StartZ=0 EndX=4.03109 EndY=3.5 EndZ=0
    g20: Circle [constr] CenterX=4.03109 CenterY=7 CenterZ=0 NormalX=0 NormalY=0 NormalZ=1 AngleXU=0 Radius=3.5
    g21: LineSegment StartX=-1 StartY=5.25 StartZ=0 EndX=-1 EndY=8.75 EndZ=0
    g22: LineSegment StartX=-1 StartY=8.75 StartZ=0 EndX=-4.03109 EndY=10.5 EndZ=0
    g23: LineSegment StartX=-4.03109 StartY=10.5 StartZ=0 EndX=-7.06218 EndY=8.75 EndZ=0
    g24: LineSegment StartX=-7.06218 StartY=8.75 StartZ=0 EndX=-7.06218 EndY=5.25 EndZ=0
    g25: LineSegment StartX=-7.06218 StartY=5.25 StartZ=0 EndX=-4.03109 EndY=3.5 EndZ=0
    g26: LineSegment StartX=-4.03109 StartY=3.5 StartZ=0 EndX=-1 EndY=5.25 EndZ=0
    g27: Circle [constr] CenterX=-4.03109 CenterY=7 CenterZ=0 NormalX=0 NormalY=0 NormalZ=1 AngleXU=0 Radius=3.5
    g28: LineSegment StartX=-4.96891 StartY=-1.75 StartZ=0 EndX=-4.96891 EndY=1.75 EndZ=0
    g29: LineSegment StartX=-4.96891 StartY=1.75 StartZ=0 EndX=-8 EndY=3.5 EndZ=0
    g30: LineSegment StartX=-8 StartY=3.5 StartZ=0 EndX=-11.0311 EndY=1.75 EndZ=0
    g31: LineSegment StartX=-11.0311 StartY=1.75 StartZ=0 EndX=-11.0311 EndY=-1.75 EndZ=0
    g32: LineSegment StartX=-11.0311 StartY=-1.75 StartZ=0 EndX=-8 EndY=-3.5 EndZ=0
    g33: LineSegment StartX=-8 StartY=-3.5 StartZ=0 EndX=-4.96891 EndY=-1.75 EndZ=0
    g34: Circle [constr] CenterX=-8 CenterY=0 CenterZ=0 NormalX=0 NormalY=0 NormalZ=1 AngleXU=0 Radius=3.5
    g35: LineSegment StartX=-4.03109 StartY=-3.5 StartZ=0 EndX=-7.06218 EndY=-5.25 EndZ=0
    g36: LineSegment StartX=-7.06218 StartY=-5.25 StartZ=0 EndX=-7.06218 EndY=-8.75 EndZ=0
    g37: LineSegment StartX=-7.06218 StartY=-8.75 StartZ=0 EndX=-4.03109 EndY=-10.5 EndZ=0
    g38: LineSegment StartX=-4.03109 StartY=-10.5 StartZ=0 EndX=-1 EndY=-8.75 EndZ=0
    g39: LineSegment StartX=-1 StartY=-8.75 StartZ=0 EndX=-1 EndY=-5.25 EndZ=0
    g40: LineSegment StartX=-1 StartY=-5.25 StartZ=0 EndX=-4.03109 EndY=-3.5 EndZ=0
    g41: Circle [constr] CenterX=-4.03109 CenterY=-7 CenterZ=0 NormalX=0 NormalY=0 NormalZ=1 AngleXU=0 Radius=3.5
    g42: LineSegment StartX=4.03109 StartY=-3.5 StartZ=0 EndX=1 EndY=-5.25 EndZ=0
    g43: LineSegment StartX=1 StartY=-5.25 StartZ=0 EndX=1 EndY=-8.75 EndZ=0
    g44: LineSegment StartX=1 StartY=-8.75 StartZ=0 EndX=4.03109 EndY=-10.5 EndZ=0
    g45: LineSegment StartX=4.03109 StartY=-10.5 StartZ=0 EndX=7.06218 EndY=-8.75 EndZ=0
    g46: LineSegment StartX=7.06218 StartY=-8.75 StartZ=0 EndX=7.06218 EndY=-5.25 EndZ=0
    g47: LineSegment StartX=7.06218 StartY=-5.25 StartZ=0 EndX=4.03109 EndY=-3.5 EndZ=0
    g48: Circle [constr] CenterX=4.03109 CenterY=-7 CenterZ=0 NormalX=0 NormalY=0 NormalZ=1 AngleXU=0 Radius=3.5
  constraints (117):
    c: Coincident(g0,g1)
    c: Coincident(g1,g2)
    c: Coincident(g2,g3)
    c: Coincident(g3,g4)
    c: Coincident(g4,g5)
    c: Coincident(g5,g0)
    c: Equal(g0, g1-g5) x5
    c: PointOnObject(g0,g6)
    c: PointOnObject(g1,g6)
    c: PointOnObject(g2,g6)
    c: PointOnObject(g3,g6)
    c: PointOnObject(g4,g6)
    c: PointOnObject(g5,g6)
    c: Coincident(g6,g-1)
    c: Diameter(g6) = 7
    c: PointOnObject(g0,g-2)
    c: Coincident(g7,g8)
    c: Coincident(g8,g9)
    c: Coincident(g9,g10)
    c: Coincident(g10,g11)
    c: Coincident(g11,g12)
    c: Coincident(g12,g7)
    c: Equal(g7, g8-g12) x5
    c: PointOnObject(g7,g13)
    c: PointOnObject(g8,g13)
    c: PointOnObject(g9,g13)
    c: PointOnObject(g10,g13)
    c: PointOnObject(g11,g13)
    c: PointOnObject(g12,g13)
    c: PointOnObject(g13,g-1)
    c: Diameter(g13) = 7
    c: Distance(g6,g13) = 8
    c: Horizontal(g0,g10)
    c: Coincident(g14,g15)
    c: Coincident(g15,g16)
    c: Coincident(g16,g17)
    c: Coincident(g17,g18)
    c: Coincident(g18,g19)
    c: Coincident(g19,g14)
    c: Equal(g14, g15-g19) x5
    c: PointOnObject(g14,g20)
    c: PointOnObject(g15,g20)
    c: PointOnObject(g16,g20)
    c: PointOnObject(g17,g20)
    c: PointOnObject(g18,g20)
    c: PointOnObject(g19,g20)
    c: Diameter(g20) = 7
    c: DistanceY(g-1,g20) = 7
    c: Vertical(g18)
    c: Distance(g17,g-2) = 1
    c: Coincident(g21,g22)
    c: Coincident(g22,g23)
    c: Coincident(g23,g24)
    c: Coincident(g24,g25)
    c: Coincident(g25,g26)
    c: Coincident(g26,g21)
    c: Equal(g21, g22-g26) x5
    c: PointOnObject(g21,g27)
    c: PointOnObject(g22,g27)
    c: PointOnObject(g23,g27)
    c: PointOnObject(g24,g27)
    c: PointOnObject(g25,g27)
    c: PointOnObject(g26,g27)
    c: Diameter(g27) = 7
    c: DistanceY(g-1,g27) = 7
    c: DistanceX(g21,g-1) = 1
    c: Vertical(g21)
    c: Coincident(g28,g29)
    c: Coincident(g29,g30)
    c: Coincident(g30,g31)
    c: Coincident(g31,g32)
    c: Coincident(g32,g33)
    c: Coincident(g33,g28)
    c: Equal(g28, g29-g33) x5
    c: PointOnObject(g28,g34)
    c: PointOnObject(g29,g34)
    c: PointOnObject(g30,g34)
    c: PointOnObject(g31,g34)
    c: PointOnObject(g32,g34)
    c: PointOnObject(g33,g34)
    c: PointOnObject(g34,g-1)
    c: Diameter(g34) = 7
    c: Vertical(g31)
    c: DistanceX(g34,g-1) = 8
    c: Coincident(g35,g36)
    c: Coincident(g36,g37)
    c: Coincident(g37,g38)
    c: Coincident(g38,g39)
    c: Coincident(g39,g40)
    c: Coincident(g40,g35)
    c: Equal(g35, g36-g40) x5
    c: PointOnObject(g35,g41)
    c: PointOnObject(g36,g41)
    c: PointOnObject(g37,g41)
    c: PointOnObject(g38,g41)
    c: PointOnObject(g39,g41)
    c: PointOnObject(g40,g41)
    c: Coincident(g42,g43)
    c: Coincident(g43,g44)
    c: Coincident(g44,g45)
    c: Coincident(g45,g46)
    c: Coincident(g46,g47)
    c: Coincident(g47,g42)
    c: Equal(g42, g43-g47) x5
    c: PointOnObject(g42,g48)
    c: PointOnObject(g43,g48)
    c: PointOnObject(g44,g48)
    c: PointOnObject(g45,g48)
    c: PointOnObject(g46,g48)
    c: PointOnObject(g47,g48)
    c: Equal(g41,g48)
    c: Diameter(g41) = 7
    c: Vertical(g39)
    c: Vertical(g43)
    c: Distance(g-2,g39) = 1
    c: Symmetric(g38,g43,g-2)
    c: Distance(g41,g-1) = 7
FEATURE [Part::Extrusion] Extrude712  label="hex314"
  Base = -> Sketch721
  Dir = (0,-1,2e-16)
  DirMode = 2
  FaceMakerClass = Part::FaceMakerBullseye
  FaceMakerMode = 3
  LengthFwd = 10
  LengthRev = 0
  Placement = pos=(-68,0,-35) rot=(0,0,1;0rad)
  Solid = true
  Symmetric = false
FEATURE [Sketcher::SketchObject] Sketch722
  ArcFitTolerance = 1e-06
  FullyConstrained = true
  MakeInternals = false
  Placement = pos=(0,0,0) rot=(1,0,0;1.5708rad)
  sketch-geometry (49):
    g0: LineSegment StartX=1e-16 StartY=3.5 StartZ=0 EndX=-3.03109 EndY=1.75 EndZ=0
    g1: LineSegment StartX=-3.03109 StartY=1.75 StartZ=0 EndX=-3.03109 EndY=-1.75 EndZ=0
    g2: LineSegment StartX=-3.03109 StartY=-1.75 StartZ=0 EndX=-1e-16 EndY=-3.5 EndZ=0
    g3: LineSegment StartX=-1e-16 StartY=-3.5 StartZ=0 EndX=3.03109 EndY=-1.75 EndZ=0
    g4: LineSegment StartX=3.03109 StartY=-1.75 StartZ=0 EndX=3.03109 EndY=1.75 EndZ=0
    g5: LineSegment StartX=3.03109 StartY=1.75 StartZ=0 EndX=1e-16 EndY=3.5 EndZ=0
    g6: Circle [constr] CenterX=0 CenterY=0 CenterZ=0 NormalX=0 NormalY=0 NormalZ=1 AngleXU=0 Radius=3.5
    g7: LineSegment StartX=4.96892 StartY=-1.75002 StartZ=0 EndX=8.00002 EndY=-3.5 EndZ=0
    g8: LineSegment StartX=8.00002 StartY=-3.5 StartZ=0 EndX=11.0311 EndY=-1.74998 EndZ=0
    g9: LineSegment StartX=11.0311 StartY=-1.74998 StartZ=0 EndX=11.0311 EndY=1.75002 EndZ=0
    g10: LineSegment StartX=11.0311 StartY=1.75002 StartZ=0 EndX=7.99998 EndY=3.5 EndZ=0
    g11: LineSegment StartX=7.99998 StartY=3.5 StartZ=0 EndX=4.9689 EndY=1.74998 EndZ=0
    g12: LineSegment StartX=4.9689 StartY=1.74998 StartZ=0 EndX=4.96892 EndY=-1.75002 EndZ=0
    g13: Circle [constr] CenterX=8 CenterY=0 CenterZ=0 NormalX=0 NormalY=0 NormalZ=1 AngleXU=0 Radius=3.5
    g14: LineSegment StartX=4.03109 StartY=3.5 StartZ=0 EndX=7.06218 EndY=5.25 EndZ=0
    g15: LineSegment StartX=7.06218 StartY=5.25 StartZ=0 EndX=7.06218 EndY=8.75 EndZ=0
    g16: LineSegment StartX=7.06218 StartY=8.75 StartZ=0 EndX=4.03109 EndY=10.5 EndZ=0
    g17: LineSegment StartX=4.03109 StartY=10.5 StartZ=0 EndX=1 EndY=8.75 EndZ=0
    g18: LineSegment StartX=1 StartY=8.75 StartZ=0 EndX=1 EndY=5.25 EndZ=0
    g19: LineSegment StartX=1 StartY=5.25 StartZ=0 EndX=4.03109 EndY=3.5 EndZ=0
    g20: Circle [constr] CenterX=4.03109 CenterY=7 CenterZ=0 NormalX=0 NormalY=0 NormalZ=1 AngleXU=0 Radius=3.5
    g21: LineSegment StartX=-1 StartY=5.25 StartZ=0 EndX=-1 EndY=8.75 EndZ=0
    g22: LineSegment StartX=-1 StartY=8.75 StartZ=0 EndX=-4.03109 EndY=10.5 EndZ=0
    g23: LineSegment StartX=-4.03109 StartY=10.5 StartZ=0 EndX=-7.06218 EndY=8.75 EndZ=0
    g24: LineSegment StartX=-7.06218 StartY=8.75 StartZ=0 EndX=-7.06218 EndY=5.25 EndZ=0
    g25: LineSegment StartX=-7.06218 StartY=5.25 StartZ=0 EndX=-4.03109 EndY=3.5 EndZ=0
    g26: LineSegment StartX=-4.03109 StartY=3.5 StartZ=0 EndX=-1 EndY=5.25 EndZ=0
    g27: Circle [constr] CenterX=-4.03109 CenterY=7 CenterZ=0 NormalX=0 NormalY=0 NormalZ=1 AngleXU=0 Radius=3.5
    g28: LineSegment StartX=-4.96891 StartY=-1.75 StartZ=0 EndX=-4.96891 EndY=1.75 EndZ=0
    g29: LineSegment StartX=-4.96891 StartY=1.75 StartZ=0 EndX=-8 EndY=3.5 EndZ=0
    g30: LineSegment StartX=-8 StartY=3.5 StartZ=0 EndX=-11.0311 EndY=1.75 EndZ=0
    g31: LineSegment StartX=-11.0311 StartY=1.75 StartZ=0 EndX=-11.0311 EndY=-1.75 EndZ=0
    g32: LineSegment StartX=-11.0311 StartY=-1.75 StartZ=0 EndX=-8 EndY=-3.5 EndZ=0
    g33: LineSegment StartX=-8 StartY=-3.5 StartZ=0 EndX=-4.96891 EndY=-1.75 EndZ=0
    g34: Circle [constr] CenterX=-8 CenterY=0 CenterZ=0 NormalX=0 NormalY=0 NormalZ=1 AngleXU=0 Radius=3.5
    g35: LineSegment StartX=-4.03109 StartY=-3.5 StartZ=0 EndX=-7.06218 EndY=-5.25 EndZ=0
    g36: LineSegment StartX=-7.06218 StartY=-5.25 StartZ=0 EndX=-7.06218 EndY=-8.75 EndZ=0
    g37: LineSegment StartX=-7.06218 StartY=-8.75 StartZ=0 EndX=-4.03109 EndY=-10.5 EndZ=0
    g38: LineSegment StartX=-4.03109 StartY=-10.5 StartZ=0 EndX=-1 EndY=-8.75 EndZ=0
    g39: LineSegment StartX=-1 StartY=-8.75 StartZ=0 EndX=-1 EndY=-5.25 EndZ=0
    g40: LineSegment StartX=-1 StartY=-5.25 StartZ=0 EndX=-4.03109 EndY=-3.5 EndZ=0
    g41: Circle [constr] CenterX=-4.03109 CenterY=-7 CenterZ=0 NormalX=0 NormalY=0 NormalZ=1 AngleXU=0 Radius=3.5
    g42: LineSegment StartX=4.03109 StartY=-3.5 StartZ=0 EndX=1 EndY=-5.25 EndZ=0
    g43: LineSegment StartX=1 StartY=-5.25 StartZ=0 EndX=1 EndY=-8.75 EndZ=0
    g44: LineSegment StartX=1 StartY=-8.75 StartZ=0 EndX=4.03109 EndY=-10.5 EndZ=0
    g45: LineSegment StartX=4.03109 StartY=-10.5 StartZ=0 EndX=7.06218 EndY=-8.75 EndZ=0
    g46: LineSegment StartX=7.06218 StartY=-8.75 StartZ=0 EndX=7.06218 EndY=-5.25 EndZ=0
    g47: LineSegment StartX=7.06218 StartY=-5.25 StartZ=0 EndX=4.03109 EndY=-3.5 EndZ=0
    g48: Circle [constr] CenterX=4.03109 CenterY=-7 CenterZ=0 NormalX=0 NormalY=0 NormalZ=1 AngleXU=0 Radius=3.5
  constraints (117):
    c: Coincident(g0,g1)
    c: Coincident(g1,g2)
    c: Coincident(g2,g3)
    c: Coincident(g3,g4)
    c: Coincident(g4,g5)
    c: Coincident(g5,g0)
    c: Equal(g0, g1-g5) x5
    c: PointOnObject(g0,g6)
    c: PointOnObject(g1,g6)
    c: PointOnObject(g2,g6)
    c: PointOnObject(g3,g6)
    c: PointOnObject(g4,g6)
    c: PointOnObject(g5,g6)
    c: Coincident(g6,g-1)
    c: Diameter(g6) = 7
    c: PointOnObject(g0,g-2)
    c: Coincident(g7,g8)
    c: Coincident(g8,g9)
    c: Coincident(g9,g10)
    c: Coincident(g10,g11)
    c: Coincident(g11,g12)
    c: Coincident(g12,g7)
    c: Equal(g7, g8-g12) x5
    c: PointOnObject(g7,g13)
    c: PointOnObject(g8,g13)
    c: PointOnObject(g9,g13)
    c: PointOnObject(g10,g13)
    c: PointOnObject(g11,g13)
    c: PointOnObject(g12,g13)
    c: PointOnObject(g13,g-1)
    c: Diameter(g13) = 7
    c: Distance(g6,g13) = 8
    c: Horizontal(g0,g10)
    c: Coincident(g14,g15)
    c: Coincident(g15,g16)
    c: Coincident(g16,g17)
    c: Coincident(g17,g18)
    c: Coincident(g18,g19)
    c: Coincident(g19,g14)
    c: Equal(g14, g15-g19) x5
    c: PointOnObject(g14,g20)
    c: PointOnObject(g15,g20)
    c: PointOnObject(g16,g20)
    c: PointOnObject(g17,g20)
    c: PointOnObject(g18,g20)
    c: PointOnObject(g19,g20)
    c: Diameter(g20) = 7
    c: DistanceY(g-1,g20) = 7
    c: Vertical(g18)
    c: Distance(g17,g-2) = 1
    c: Coincident(g21,g22)
    c: Coincident(g22,g23)
    c: Coincident(g23,g24)
    c: Coincident(g24,g25)
    c: Coincident(g25,g26)
    c: Coincident(g26,g21)
    c: Equal(g21, g22-g26) x5
    c: PointOnObject(g21,g27)
    c: PointOnObject(g22,g27)
    c: PointOnObject(g23,g27)
    c: PointOnObject(g24,g27)
    c: PointOnObject(g25,g27)
    c: PointOnObject(g26,g27)
    c: Diameter(g27) = 7
    c: DistanceY(g-1,g27) = 7
    c: DistanceX(g21,g-1) = 1
    c: Vertical(g21)
    c: Coincident(g28,g29)
    c: Coincident(g29,g30)
    c: Coincident(g30,g31)
    c: Coincident(g31,g32)
    c: Coincident(g32,g33)
    c: Coincident(g33,g28)
    c: Equal(g28, g29-g33) x5
    c: PointOnObject(g28,g34)
    c: PointOnObject(g29,g34)
    c: PointOnObject(g30,g34)
    c: PointOnObject(g31,g34)
    c: PointOnObject(g32,g34)
    c: PointOnObject(g33,g34)
    c: PointOnObject(g34,g-1)
    c: Diameter(g34) = 7
    c: Vertical(g31)
    c: DistanceX(g34,g-1) = 8
    c: Coincident(g35,g36)
    c: Coincident(g36,g37)
    c: Coincident(g37,g38)
    c: Coincident(g38,g39)
    c: Coincident(g39,g40)
    c: Coincident(g40,g35)
    c: Equal(g35, g36-g40) x5
    c: PointOnObject(g35,g41)
    c: PointOnObject(g36,g41)
    c: PointOnObject(g37,g41)
    c: PointOnObject(g38,g41)
    c: PointOnObject(g39,g41)
    c: PointOnObject(g40,g41)
    c: Coincident(g42,g43)
    c: Coincident(g43,g44)
    c: Coincident(g44,g45)
    c: Coincident(g45,g46)
    c: Coincident(g46,g47)
    c: Coincident(g47,g42)
    c: Equal(g42, g43-g47) x5
    c: PointOnObject(g42,g48)
    c: PointOnObject(g43,g48)
    c: PointOnObject(g44,g48)
    c: PointOnObject(g45,g48)
    c: PointOnObject(g46,g48)
    c: PointOnObject(g47,g48)
    c: Equal(g41,g48)
    c: Diameter(g41) = 7
    c: Vertical(g39)
    c: Vertical(g43)
    c: Distance(g-2,g39) = 1
    c: Symmetric(g38,g43,g-2)
    c: Distance(g41,g-1) = 7
FEATURE [Part::Extrusion] Extrude713  label="hex315"
  Base = -> Sketch722
  Dir = (0,-1,2e-16)
  DirMode = 2
  FaceMakerClass = Part::FaceMakerBullseye
  FaceMakerMode = 3
  LengthFwd = 10
  LengthRev = 0
  Placement = pos=(-84,0,-21) rot=(0,0,1;0rad)
  Solid = true
  Symmetric = false
FEATURE [Sketcher::SketchObject] Sketch723
  ArcFitTolerance = 1e-06
  FullyConstrained = true
  MakeInternals = false
  Placement = pos=(0,0,0) rot=(1,0,0;1.5708rad)
  sketch-geometry (49):
    g0: LineSegment StartX=1e-16 StartY=3.5 StartZ=0 EndX=-3.03109 EndY=1.75 EndZ=0
    g1: LineSegment StartX=-3.03109 StartY=1.75 StartZ=0 EndX=-3.03109 EndY=-1.75 EndZ=0
    g2: LineSegment StartX=-3.03109 StartY=-1.75 StartZ=0 EndX=-1e-16 EndY=-3.5 EndZ=0
    g3: LineSegment StartX=-1e-16 StartY=-3.5 StartZ=0 EndX=3.03109 EndY=-1.75 EndZ=0
    g4: LineSegment StartX=3.03109 StartY=-1.75 StartZ=0 EndX=3.03109 EndY=1.75 EndZ=0
    g5: LineSegment StartX=3.03109 StartY=1.75 StartZ=0 EndX=1e-16 EndY=3.5 EndZ=0
    g6: Circle [constr] CenterX=0 CenterY=0 CenterZ=0 NormalX=0 NormalY=0 NormalZ=1 AngleXU=0 Radius=3.5
    g7: LineSegment StartX=4.96892 StartY=-1.75002 StartZ=0 EndX=8.00002 EndY=-3.5 EndZ=0
    g8: LineSegment StartX=8.00002 StartY=-3.5 StartZ=0 EndX=11.0311 EndY=-1.74998 EndZ=0
    g9: LineSegment StartX=11.0311 StartY=-1.74998 StartZ=0 EndX=11.0311 EndY=1.75002 EndZ=0
    g10: LineSegment StartX=11.0311 StartY=1.75002 StartZ=0 EndX=7.99998 EndY=3.5 EndZ=0
    g11: LineSegment StartX=7.99998 StartY=3.5 StartZ=0 EndX=4.9689 EndY=1.74998 EndZ=0
    g12: LineSegment StartX=4.9689 StartY=1.74998 StartZ=0 EndX=4.96892 EndY=-1.75002 EndZ=0
    g13: Circle [constr] CenterX=8 CenterY=0 CenterZ=0 NormalX=0 NormalY=0 NormalZ=1 AngleXU=0 Radius=3.5
    g14: LineSegment StartX=4.03109 StartY=3.5 StartZ=0 EndX=7.06218 EndY=5.25 EndZ=0
    g15: LineSegment StartX=7.06218 StartY=5.25 StartZ=0 EndX=7.06218 EndY=8.75 EndZ=0
    g16: LineSegment StartX=7.06218 StartY=8.75 StartZ=0 EndX=4.03109 EndY=10.5 EndZ=0
    g17: LineSegment StartX=4.03109 StartY=10.5 StartZ=0 EndX=1 EndY=8.75 EndZ=0
    g18: LineSegment StartX=1 StartY=8.75 StartZ=0 EndX=1 EndY=5.25 EndZ=0
    g19: LineSegment StartX=1 StartY=5.25 StartZ=0 EndX=4.03109 EndY=3.5 EndZ=0
    g20: Circle [constr] CenterX=4.03109 CenterY=7 CenterZ=0 NormalX=0 NormalY=0 NormalZ=1 AngleXU=0 Radius=3.5
    g21: LineSegment StartX=-1 StartY=5.25 StartZ=0 EndX=-1 EndY=8.75 EndZ=0
    g22: LineSegment StartX=-1 StartY=8.75 StartZ=0 EndX=-4.03109 EndY=10.5 EndZ=0
    g23: LineSegment StartX=-4.03109 StartY=10.5 StartZ=0 EndX=-7.06218 EndY=8.75 EndZ=0
    g24: LineSegment StartX=-7.06218 StartY=8.75 StartZ=0 EndX=-7.06218 EndY=5.25 EndZ=0
    g25: LineSegment StartX=-7.06218 StartY=5.25 StartZ=0 EndX=-4.03109 EndY=3.5 EndZ=0
    g26: LineSegment StartX=-4.03109 StartY=3.5 StartZ=0 EndX=-1 EndY=5.25 EndZ=0
    g27: Circle [constr] CenterX=-4.03109 CenterY=7 CenterZ=0 NormalX=0 NormalY=0 NormalZ=1 AngleXU=0 Radius=3.5
    g28: LineSegment StartX=-4.96891 StartY=-1.75 StartZ=0 EndX=-4.96891 EndY=1.75 EndZ=0
    g29: LineSegment StartX=-4.96891 StartY=1.75 StartZ=0 EndX=-8 EndY=3.5 EndZ=0
    g30: LineSegment StartX=-8 StartY=3.5 StartZ=0 EndX=-11.0311 EndY=1.75 EndZ=0
    g31: LineSegment StartX=-11.0311 StartY=1.75 StartZ=0 EndX=-11.0311 EndY=-1.75 EndZ=0
    g32: LineSegment StartX=-11.0311 StartY=-1.75 StartZ=0 EndX=-8 EndY=-3.5 EndZ=0
    g33: LineSegment StartX=-8 StartY=-3.5 StartZ=0 EndX=-4.96891 EndY=-1.75 EndZ=0
    g34: Circle [constr] CenterX=-8 CenterY=0 CenterZ=0 NormalX=0 NormalY=0 NormalZ=1 AngleXU=0 Radius=3.5
    g35: LineSegment StartX=-4.03109 StartY=-3.5 StartZ=0 EndX=-7.06218 EndY=-5.25 EndZ=0
    g36: LineSegment StartX=-7.06218 StartY=-5.25 StartZ=0 EndX=-7.06218 EndY=-8.75 EndZ=0
    g37: LineSegment StartX=-7.06218 StartY=-8.75 StartZ=0 EndX=-4.03109 EndY=-10.5 EndZ=0
    g38: LineSegment StartX=-4.03109 StartY=-10.5 StartZ=0 EndX=-1 EndY=-8.75 EndZ=0
    g39: LineSegment StartX=-1 StartY=-8.75 StartZ=0 EndX=-1 EndY=-5.25 EndZ=0
    g40: LineSegment StartX=-1 StartY=-5.25 StartZ=0 EndX=-4.03109 EndY=-3.5 EndZ=0
    g41: Circle [constr] CenterX=-4.03109 CenterY=-7 CenterZ=0 NormalX=0 NormalY=0 NormalZ=1 AngleXU=0 Radius=3.5
    g42: LineSegment StartX=4.03109 StartY=-3.5 StartZ=0 EndX=1 EndY=-5.25 EndZ=0
    g43: LineSegment StartX=1 StartY=-5.25 StartZ=0 EndX=1 EndY=-8.75 EndZ=0
    g44: LineSegment StartX=1 StartY=-8.75 StartZ=0 EndX=4.03109 EndY=-10.5 EndZ=0
    g45: LineSegment StartX=4.03109 StartY=-10.5 StartZ=0 EndX=7.06218 EndY=-8.75 EndZ=0
    g46: LineSegment StartX=7.06218 StartY=-8.75 StartZ=0 EndX=7.06218 EndY=-5.25 EndZ=0
    g47: LineSegment StartX=7.06218 StartY=-5.25 StartZ=0 EndX=4.03109 EndY=-3.5 EndZ=0
    g48: Circle [constr] CenterX=4.03109 CenterY=-7 CenterZ=0 NormalX=0 NormalY=0 NormalZ=1 AngleXU=0 Radius=3.5
  constraints (117):
    c: Coincident(g0,g1)
    c: Coincident(g1,g2)
    c: Coincident(g2,g3)
    c: Coincident(g3,g4)
    c: Coincident(g4,g5)
    c: Coincident(g5,g0)
    c: Equal(g0, g1-g5) x5
    c: PointOnObject(g0,g6)
    c: PointOnObject(g1,g6)
    c: PointOnObject(g2,g6)
    c: PointOnObject(g3,g6)
    c: PointOnObject(g4,g6)
    c: PointOnObject(g5,g6)
    c: Coincident(g6,g-1)
    c: Diameter(g6) = 7
    c: PointOnObject(g0,g-2)
    c: Coincident(g7,g8)
    c: Coincident(g8,g9)
    c: Coincident(g9,g10)
    c: Coincident(g10,g11)
    c: Coincident(g11,g12)
    c: Coincident(g12,g7)
    c: Equal(g7, g8-g12) x5
    c: PointOnObject(g7,g13)
    c: PointOnObject(g8,g13)
    c: PointOnObject(g9,g13)
    c: PointOnObject(g10,g13)
    c: PointOnObject(g11,g13)
    c: PointOnObject(g12,g13)
    c: PointOnObject(g13,g-1)
    c: Diameter(g13) = 7
    c: Distance(g6,g13) = 8
    c: Horizontal(g0,g10)
    c: Coincident(g14,g15)
    c: Coincident(g15,g16)
    c: Coincident(g16,g17)
    c: Coincident(g17,g18)
    c: Coincident(g18,g19)
    c: Coincident(g19,g14)
    c: Equal(g14, g15-g19) x5
    c: PointOnObject(g14,g20)
    c: PointOnObject(g15,g20)
    c: PointOnObject(g16,g20)
    c: PointOnObject(g17,g20)
    c: PointOnObject(g18,g20)
    c: PointOnObject(g19,g20)
    c: Diameter(g20) = 7
    c: DistanceY(g-1,g20) = 7
    c: Vertical(g18)
    c: Distance(g17,g-2) = 1
    c: Coincident(g21,g22)
    c: Coincident(g22,g23)
    c: Coincident(g23,g24)
    c: Coincident(g24,g25)
    c: Coincident(g25,g26)
    c: Coincident(g26,g21)
    c: Equal(g21, g22-g26) x5
    c: PointOnObject(g21,g27)
    c: PointOnObject(g22,g27)
    c: PointOnObject(g23,g27)
    c: PointOnObject(g24,g27)
    c: PointOnObject(g25,g27)
    c: PointOnObject(g26,g27)
    c: Diameter(g27) = 7
    c: DistanceY(g-1,g27) = 7
    c: DistanceX(g21,g-1) = 1
    c: Vertical(g21)
    c: Coincident(g28,g29)
    c: Coincident(g29,g30)
    c: Coincident(g30,g31)
    c: Coincident(g31,g32)
    c: Coincident(g32,g33)
    c: Coincident(g33,g28)
    c: Equal(g28, g29-g33) x5
    c: PointOnObject(g28,g34)
    c: PointOnObject(g29,g34)
    c: PointOnObject(g30,g34)
    c: PointOnObject(g31,g34)
    c: PointOnObject(g32,g34)
    c: PointOnObject(g33,g34)
    c: PointOnObject(g34,g-1)
    c: Diameter(g34) = 7
    c: Vertical(g31)
    c: DistanceX(g34,g-1) = 8
    c: Coincident(g35,g36)
    c: Coincident(g36,g37)
    c: Coincident(g37,g38)
    c: Coincident(g38,g39)
    c: Coincident(g39,g40)
    c: Coincident(g40,g35)
    c: Equal(g35, g36-g40) x5
    c: PointOnObject(g35,g41)
    c: PointOnObject(g36,g41)
    c: PointOnObject(g37,g41)
    c: PointOnObject(g38,g41)
    c: PointOnObject(g39,g41)
    c: PointOnObject(g40,g41)
    c: Coincident(g42,g43)
    c: Coincident(g43,g44)
    c: Coincident(g44,g45)
    c: Coincident(g45,g46)
    c: Coincident(g46,g47)
    c: Coincident(g47,g42)
    c: Equal(g42, g43-g47) x5
    c: PointOnObject(g42,g48)
    c: PointOnObject(g43,g48)
    c: PointOnObject(g44,g48)
    c: PointOnObject(g45,g48)
    c: PointOnObject(g46,g48)
    c: PointOnObject(g47,g48)
    c: Equal(g41,g48)
    c: Diameter(g41) = 7
    c: Vertical(g39)
    c: Vertical(g43)
    c: Distance(g-2,g39) = 1
    c: Symmetric(g38,g43,g-2)
    c: Distance(g41,g-1) = 7
FEATURE [Part::Extrusion] Extrude714  label="hex316"
  Base = -> Sketch723
  Dir = (0,-1,2e-16)
  DirMode = 2
  FaceMakerClass = Part::FaceMakerBullseye
  FaceMakerMode = 3
  LengthFwd = 10
  LengthRev = 0
  Placement = pos=(-88,0,14) rot=(0,0,1;0rad)
  Solid = true
  Symmetric = false
FEATURE [Sketcher::SketchObject] Sketch724
  ArcFitTolerance = 1e-06
  FullyConstrained = true
  MakeInternals = false
  Placement = pos=(0,0,0) rot=(1,0,0;1.5708rad)
  sketch-geometry (49):
    g0: LineSegment StartX=1e-16 StartY=3.5 StartZ=0 EndX=-3.03109 EndY=1.75 EndZ=0
    g1: LineSegment StartX=-3.03109 StartY=1.75 StartZ=0 EndX=-3.03109 EndY=-1.75 EndZ=0
    g2: LineSegment StartX=-3.03109 StartY=-1.75 StartZ=0 EndX=-1e-16 EndY=-3.5 EndZ=0
    g3: LineSegment StartX=-1e-16 StartY=-3.5 StartZ=0 EndX=3.03109 EndY=-1.75 EndZ=0
    g4: LineSegment StartX=3.03109 StartY=-1.75 StartZ=0 EndX=3.03109 EndY=1.75 EndZ=0
    g5: LineSegment StartX=3.03109 StartY=1.75 StartZ=0 EndX=1e-16 EndY=3.5 EndZ=0
    g6: Circle [constr] CenterX=0 CenterY=0 CenterZ=0 NormalX=0 NormalY=0 NormalZ=1 AngleXU=0 Radius=3.5
    g7: LineSegment StartX=4.96892 StartY=-1.75002 StartZ=0 EndX=8.00002 EndY=-3.5 EndZ=0
    g8: LineSegment StartX=8.00002 StartY=-3.5 StartZ=0 EndX=11.0311 EndY=-1.74998 EndZ=0
    g9: LineSegment StartX=11.0311 StartY=-1.74998 StartZ=0 EndX=11.0311 EndY=1.75002 EndZ=0
    g10: LineSegment StartX=11.0311 StartY=1.75002 StartZ=0 EndX=7.99998 EndY=3.5 EndZ=0
    g11: LineSegment StartX=7.99998 StartY=3.5 StartZ=0 EndX=4.9689 EndY=1.74998 EndZ=0
    g12: LineSegment StartX=4.9689 StartY=1.74998 StartZ=0 EndX=4.96892 EndY=-1.75002 EndZ=0
    g13: Circle [constr] CenterX=8 CenterY=0 CenterZ=0 NormalX=0 NormalY=0 NormalZ=1 AngleXU=0 Radius=3.5
    g14: LineSegment StartX=4.03109 StartY=3.5 StartZ=0 EndX=7.06218 EndY=5.25 EndZ=0
    g15: LineSegment StartX=7.06218 StartY=5.25 StartZ=0 EndX=7.06218 EndY=8.75 EndZ=0
    g16: LineSegment StartX=7.06218 StartY=8.75 StartZ=0 EndX=4.03109 EndY=10.5 EndZ=0
    g17: LineSegment StartX=4.03109 StartY=10.5 StartZ=0 EndX=1 EndY=8.75 EndZ=0
    g18: LineSegment StartX=1 StartY=8.75 StartZ=0 EndX=1 EndY=5.25 EndZ=0
    g19: LineSegment StartX=1 StartY=5.25 StartZ=0 EndX=4.03109 EndY=3.5 EndZ=0
    g20: Circle [constr] CenterX=4.03109 CenterY=7 CenterZ=0 NormalX=0 NormalY=0 NormalZ=1 AngleXU=0 Radius=3.5
    g21: LineSegment StartX=-1 StartY=5.25 StartZ=0 EndX=-1 EndY=8.75 EndZ=0
    g22: LineSegment StartX=-1 StartY=8.75 StartZ=0 EndX=-4.03109 EndY=10.5 EndZ=0
    g23: LineSegment StartX=-4.03109 StartY=10.5 StartZ=0 EndX=-7.06218 EndY=8.75 EndZ=0
    g24: LineSegment StartX=-7.06218 StartY=8.75 StartZ=0 EndX=-7.06218 EndY=5.25 EndZ=0
    g25: LineSegment StartX=-7.06218 StartY=5.25 StartZ=0 EndX=-4.03109 EndY=3.5 EndZ=0
    g26: LineSegment StartX=-4.03109 StartY=3.5 StartZ=0 EndX=-1 EndY=5.25 EndZ=0
    g27: Circle [constr] CenterX=-4.03109 CenterY=7 CenterZ=0 NormalX=0 NormalY=0 NormalZ=1 AngleXU=0 Radius=3.5
    g28: LineSegment StartX=-4.96891 StartY=-1.75 StartZ=0 EndX=-4.96891 EndY=1.75 EndZ=0
    g29: LineSegment StartX=-4.96891 StartY=1.75 StartZ=0 EndX=-8 EndY=3.5 EndZ=0
    g30: LineSegment StartX=-8 StartY=3.5 StartZ=0 EndX=-11.0311 EndY=1.75 EndZ=0
    g31: LineSegment StartX=-11.0311 StartY=1.75 StartZ=0 EndX=-11.0311 EndY=-1.75 EndZ=0
    g32: LineSegment StartX=-11.0311 StartY=-1.75 StartZ=0 EndX=-8 EndY=-3.5 EndZ=0
    g33: LineSegment StartX=-8 StartY=-3.5 StartZ=0 EndX=-4.96891 EndY=-1.75 EndZ=0
    g34: Circle [constr] CenterX=-8 CenterY=0 CenterZ=0 NormalX=0 NormalY=0 NormalZ=1 AngleXU=0 Radius=3.5
    g35: LineSegment StartX=-4.03109 StartY=-3.5 StartZ=0 EndX=-7.06218 EndY=-5.25 EndZ=0
    g36: LineSegment StartX=-7.06218 StartY=-5.25 StartZ=0 EndX=-7.06218 EndY=-8.75 EndZ=0
    g37: LineSegment StartX=-7.06218 StartY=-8.75 StartZ=0 EndX=-4.03109 EndY=-10.5 EndZ=0
    g38: LineSegment StartX=-4.03109 StartY=-10.5 StartZ=0 EndX=-1 EndY=-8.75 EndZ=0
    g39: LineSegment StartX=-1 StartY=-8.75 StartZ=0 EndX=-1 EndY=-5.25 EndZ=0
    g40: LineSegment StartX=-1 StartY=-5.25 StartZ=0 EndX=-4.03109 EndY=-3.5 EndZ=0
    g41: Circle [constr] CenterX=-4.03109 CenterY=-7 CenterZ=0 NormalX=0 NormalY=0 NormalZ=1 AngleXU=0 Radius=3.5
    g42: LineSegment StartX=4.03109 StartY=-3.5 StartZ=0 EndX=1 EndY=-5.25 EndZ=0
    g43: LineSegment StartX=1 StartY=-5.25 StartZ=0 EndX=1 EndY=-8.75 EndZ=0
    g44: LineSegment StartX=1 StartY=-8.75 StartZ=0 EndX=4.03109 EndY=-10.5 EndZ=0
    g45: LineSegment StartX=4.03109 StartY=-10.5 StartZ=0 EndX=7.06218 EndY=-8.75 EndZ=0
    g46: LineSegment StartX=7.06218 StartY=-8.75 StartZ=0 EndX=7.06218 EndY=-5.25 EndZ=0
    g47: LineSegment StartX=7.06218 StartY=-5.25 StartZ=0 EndX=4.03109 EndY=-3.5 EndZ=0
    g48: Circle [constr] CenterX=4.03109 CenterY=-7 CenterZ=0 NormalX=0 NormalY=0 NormalZ=1 AngleXU=0 Radius=3.5
  constraints (117):
    c: Coincident(g0,g1)
    c: Coincident(g1,g2)
    c: Coincident(g2,g3)
    c: Coincident(g3,g4)
    c: Coincident(g4,g5)
    c: Coincident(g5,g0)
    c: Equal(g0, g1-g5) x5
    c: PointOnObject(g0,g6)
    c: PointOnObject(g1,g6)
    c: PointOnObject(g2,g6)
    c: PointOnObject(g3,g6)
    c: PointOnObject(g4,g6)
    c: PointOnObject(g5,g6)
    c: Coincident(g6,g-1)
    c: Diameter(g6) = 7
    c: PointOnObject(g0,g-2)
    c: Coincident(g7,g8)
    c: Coincident(g8,g9)
    c: Coincident(g9,g10)
    c: Coincident(g10,g11)
    c: Coincident(g11,g12)
    c: Coincident(g12,g7)
    c: Equal(g7, g8-g12) x5
    c: PointOnObject(g7,g13)
    c: PointOnObject(g8,g13)
    c: PointOnObject(g9,g13)
    c: PointOnObject(g10,g13)
    c: PointOnObject(g11,g13)
    c: PointOnObject(g12,g13)
    c: PointOnObject(g13,g-1)
    c: Diameter(g13) = 7
    c: Distance(g6,g13) = 8
    c: Horizontal(g0,g10)
    c: Coincident(g14,g15)
    c: Coincident(g15,g16)
    c: Coincident(g16,g17)
    c: Coincident(g17,g18)
    c: Coincident(g18,g19)
    c: Coincident(g19,g14)
    c: Equal(g14, g15-g19) x5
    c: PointOnObject(g14,g20)
    c: PointOnObject(g15,g20)
    c: PointOnObject(g16,g20)
    c: PointOnObject(g17,g20)
    c: PointOnObject(g18,g20)
    c: PointOnObject(g19,g20)
    c: Diameter(g20) = 7
    c: DistanceY(g-1,g20) = 7
    c: Vertical(g18)
    c: Distance(g17,g-2) = 1
    c: Coincident(g21,g22)
    c: Coincident(g22,g23)
    c: Coincident(g23,g24)
    c: Coincident(g24,g25)
    c: Coincident(g25,g26)
    c: Coincident(g26,g21)
    c: Equal(g21, g22-g26) x5
    c: PointOnObject(g21,g27)
    c: PointOnObject(g22,g27)
    c: PointOnObject(g23,g27)
    c: PointOnObject(g24,g27)
    c: PointOnObject(g25,g27)
    c: PointOnObject(g26,g27)
    c: Diameter(g27) = 7
    c: DistanceY(g-1,g27) = 7
    c: DistanceX(g21,g-1) = 1
    c: Vertical(g21)
    c: Coincident(g28,g29)
    c: Coincident(g29,g30)
    c: Coincident(g30,g31)
    c: Coincident(g31,g32)
    c: Coincident(g32,g33)
    c: Coincident(g33,g28)
    c: Equal(g28, g29-g33) x5
    c: PointOnObject(g28,g34)
    c: PointOnObject(g29,g34)
    c: PointOnObject(g30,g34)
    c: PointOnObject(g31,g34)
    c: PointOnObject(g32,g34)
    c: PointOnObject(g33,g34)
    c: PointOnObject(g34,g-1)
    c: Diameter(g34) = 7
    c: Vertical(g31)
    c: DistanceX(g34,g-1) = 8
    c: Coincident(g35,g36)
    c: Coincident(g36,g37)
    c: Coincident(g37,g38)
    c: Coincident(g38,g39)
    c: Coincident(g39,g40)
    c: Coincident(g40,g35)
    c: Equal(g35, g36-g40) x5
    c: PointOnObject(g35,g41)
    c: PointOnObject(g36,g41)
    c: PointOnObject(g37,g41)
    c: PointOnObject(g38,g41)
    c: PointOnObject(g39,g41)
    c: PointOnObject(g40,g41)
    c: Coincident(g42,g43)
    c: Coincident(g43,g44)
    c: Coincident(g44,g45)
    c: Coincident(g45,g46)
    c: Coincident(g46,g47)
    c: Coincident(g47,g42)
    c: Equal(g42, g43-g47) x5
    c: PointOnObject(g42,g48)
    c: PointOnObject(g43,g48)
    c: PointOnObject(g44,g48)
    c: PointOnObject(g45,g48)
    c: PointOnObject(g46,g48)
    c: PointOnObject(g47,g48)
    c: Equal(g41,g48)
    c: Diameter(g41) = 7
    c: Vertical(g39)
    c: Vertical(g43)
    c: Distance(g-2,g39) = 1
    c: Symmetric(g38,g43,g-2)
    c: Distance(g41,g-1) = 7
FEATURE [Part::Extrusion] Extrude715  label="hex317"
  Base = -> Sketch724
  Dir = (0,-1,2e-16)
  DirMode = 2
  FaceMakerClass = Part::FaceMakerBullseye
  FaceMakerMode = 3
  LengthFwd = 10
  LengthRev = 0
  Placement = pos=(96,0,14) rot=(0,0,1;0rad)
  Solid = true
  Symmetric = false
FEATURE [Part::MultiFuse] Fusion565
  Placement = pos=(-8,0,-56) rot=(0,0,1;0rad)
  Refine = true
  Shapes = -> [Extrude666,Extrude667,Extrude668,Extrude669,Extrude670,Extrude671,Extrude672,Extrude673,Extrude674,Extrude675,Extrude676,Extrude677,Extrude678,Extrude679,Extrude680,Extrude681,Extrude682,Extrude683,Extrude684,Extrude685,Extrude686,Extrude687,Extrude688,Extrude689,Extrude690,Extrude691,Extrude692,Extrude693,Extrude694,Extrude695,Extrude696,Extrude697,Extrude698,Extrude699,Extrude700,Extrude701,+14 more]
FEATURE [Sketcher::SketchObject] Sketch725
  ArcFitTolerance = 1e-06
  FullyConstrained = true
  MakeInternals = false
  Placement = pos=(0,0,0) rot=(1,0,0;1.5708rad)
  sketch-geometry (49):
    g0: LineSegment StartX=1e-16 StartY=3.5 StartZ=0 EndX=-3.03109 EndY=1.75 EndZ=0
    g1: LineSegment StartX=-3.03109 StartY=1.75 StartZ=0 EndX=-3.03109 EndY=-1.75 EndZ=0
    g2: LineSegment StartX=-3.03109 StartY=-1.75 StartZ=0 EndX=-1e-16 EndY=-3.5 EndZ=0
    g3: LineSegment StartX=-1e-16 StartY=-3.5 StartZ=0 EndX=3.03109 EndY=-1.75 EndZ=0
    g4: LineSegment StartX=3.03109 StartY=-1.75 StartZ=0 EndX=3.03109 EndY=1.75 EndZ=0
    g5: LineSegment StartX=3.03109 StartY=1.75 StartZ=0 EndX=1e-16 EndY=3.5 EndZ=0
    g6: Circle [constr] CenterX=0 CenterY=0 CenterZ=0 NormalX=0 NormalY=0 NormalZ=1 AngleXU=0 Radius=3.5
    g7: LineSegment StartX=4.96892 StartY=-1.75002 StartZ=0 EndX=8.00002 EndY=-3.5 EndZ=0
    g8: LineSegment StartX=8.00002 StartY=-3.5 StartZ=0 EndX=11.0311 EndY=-1.74998 EndZ=0
    g9: LineSegment StartX=11.0311 StartY=-1.74998 StartZ=0 EndX=11.0311 EndY=1.75002 EndZ=0
    g10: LineSegment StartX=11.0311 StartY=1.75002 StartZ=0 EndX=7.99998 EndY=3.5 EndZ=0
    g11: LineSegment StartX=7.99998 StartY=3.5 StartZ=0 EndX=4.9689 EndY=1.74998 EndZ=0
    g12: LineSegment StartX=4.9689 StartY=1.74998 StartZ=0 EndX=4.96892 EndY=-1.75002 EndZ=0
    g13: Circle [constr] CenterX=8 CenterY=0 CenterZ=0 NormalX=0 NormalY=0 NormalZ=1 AngleXU=0 Radius=3.5
    g14: LineSegment StartX=4.03109 StartY=3.5 StartZ=0 EndX=7.06218 EndY=5.25 EndZ=0
    g15: LineSegment StartX=7.06218 StartY=5.25 StartZ=0 EndX=7.06218 EndY=8.75 EndZ=0
    g16: LineSegment StartX=7.06218 StartY=8.75 StartZ=0 EndX=4.03109 EndY=10.5 EndZ=0
    g17: LineSegment StartX=4.03109 StartY=10.5 StartZ=0 EndX=1 EndY=8.75 EndZ=0
    g18: LineSegment StartX=1 StartY=8.75 StartZ=0 EndX=1 EndY=5.25 EndZ=0
    g19: LineSegment StartX=1 StartY=5.25 StartZ=0 EndX=4.03109 EndY=3.5 EndZ=0
    g20: Circle [constr] CenterX=4.03109 CenterY=7 CenterZ=0 NormalX=0 NormalY=0 NormalZ=1 AngleXU=0 Radius=3.5
    g21: LineSegment StartX=-1 StartY=5.25 StartZ=0 EndX=-1 EndY=8.75 EndZ=0
    g22: LineSegment StartX=-1 StartY=8.75 StartZ=0 EndX=-4.03109 EndY=10.5 EndZ=0
    g23: LineSegment StartX=-4.03109 StartY=10.5 StartZ=0 EndX=-7.06218 EndY=8.75 EndZ=0
    g24: LineSegment StartX=-7.06218 StartY=8.75 StartZ=0 EndX=-7.06218 EndY=5.25 EndZ=0
    g25: LineSegment StartX=-7.06218 StartY=5.25 StartZ=0 EndX=-4.03109 EndY=3.5 EndZ=0
    g26: LineSegment StartX=-4.03109 StartY=3.5 StartZ=0 EndX=-1 EndY=5.25 EndZ=0
    g27: Circle [constr] CenterX=-4.03109 CenterY=7 CenterZ=0 NormalX=0 NormalY=0 NormalZ=1 AngleXU=0 Radius=3.5
    g28: LineSegment StartX=-4.96891 StartY=-1.75 StartZ=0 EndX=-4.96891 EndY=1.75 EndZ=0
    g29: LineSegment StartX=-4.96891 StartY=1.75 StartZ=0 EndX=-8 EndY=3.5 EndZ=0
    g30: LineSegment StartX=-8 StartY=3.5 StartZ=0 EndX=-11.0311 EndY=1.75 EndZ=0
    g31: LineSegment StartX=-11.0311 StartY=1.75 StartZ=0 EndX=-11.0311 EndY=-1.75 EndZ=0
    g32: LineSegment StartX=-11.0311 StartY=-1.75 StartZ=0 EndX=-8 EndY=-3.5 EndZ=0
    g33: LineSegment StartX=-8 StartY=-3.5 StartZ=0 EndX=-4.96891 EndY=-1.75 EndZ=0
    g34: Circle [constr] CenterX=-8 CenterY=0 CenterZ=0 NormalX=0 NormalY=0 NormalZ=1 AngleXU=0 Radius=3.5
    g35: LineSegment StartX=-4.03109 StartY=-3.5 StartZ=0 EndX=-7.06218 EndY=-5.25 EndZ=0
    g36: LineSegment StartX=-7.06218 StartY=-5.25 StartZ=0 EndX=-7.06218 EndY=-8.75 EndZ=0
    g37: LineSegment StartX=-7.06218 StartY=-8.75 StartZ=0 EndX=-4.03109 EndY=-10.5 EndZ=0
    g38: LineSegment StartX=-4.03109 StartY=-10.5 StartZ=0 EndX=-1 EndY=-8.75 EndZ=0
    g39: LineSegment StartX=-1 StartY=-8.75 StartZ=0 EndX=-1 EndY=-5.25 EndZ=0
    g40: LineSegment StartX=-1 StartY=-5.25 StartZ=0 EndX=-4.03109 EndY=-3.5 EndZ=0
    g41: Circle [constr] CenterX=-4.03109 CenterY=-7 CenterZ=0 NormalX=0 NormalY=0 NormalZ=1 AngleXU=0 Radius=3.5
    g42: LineSegment StartX=4.03109 StartY=-3.5 StartZ=0 EndX=1 EndY=-5.25 EndZ=0
    g43: LineSegment StartX=1 StartY=-5.25 StartZ=0 EndX=1 EndY=-8.75 EndZ=0
    g44: LineSegment StartX=1 StartY=-8.75 StartZ=0 EndX=4.03109 EndY=-10.5 EndZ=0
    g45: LineSegment StartX=4.03109 StartY=-10.5 StartZ=0 EndX=7.06218 EndY=-8.75 EndZ=0
    g46: LineSegment StartX=7.06218 StartY=-8.75 StartZ=0 EndX=7.06218 EndY=-5.25 EndZ=0
    g47: LineSegment StartX=7.06218 StartY=-5.25 StartZ=0 EndX=4.03109 EndY=-3.5 EndZ=0
    g48: Circle [constr] CenterX=4.03109 CenterY=-7 CenterZ=0 NormalX=0 NormalY=0 NormalZ=1 AngleXU=0 Radius=3.5
  constraints (117):
    c: Coincident(g0,g1)
    c: Coincident(g1,g2)
    c: Coincident(g2,g3)
    c: Coincident(g3,g4)
    c: Coincident(g4,g5)
    c: Coincident(g5,g0)
    c: Equal(g0, g1-g5) x5
    c: PointOnObject(g0,g6)
    c: PointOnObject(g1,g6)
    c: PointOnObject(g2,g6)
    c: PointOnObject(g3,g6)
    c: PointOnObject(g4,g6)
    c: PointOnObject(g5,g6)
    c: Coincident(g6,g-1)
    c: Diameter(g6) = 7
    c: PointOnObject(g0,g-2)
    c: Coincident(g7,g8)
    c: Coincident(g8,g9)
    c: Coincident(g9,g10)
    c: Coincident(g10,g11)
    c: Coincident(g11,g12)
    c: Coincident(g12,g7)
    c: Equal(g7, g8-g12) x5
    c: PointOnObject(g7,g13)
    c: PointOnObject(g8,g13)
    c: PointOnObject(g9,g13)
    c: PointOnObject(g10,g13)
    c: PointOnObject(g11,g13)
    c: PointOnObject(g12,g13)
    c: PointOnObject(g13,g-1)
    c: Diameter(g13) = 7
    c: Distance(g6,g13) = 8
    c: Horizontal(g0,g10)
    c: Coincident(g14,g15)
    c: Coincident(g15,g16)
    c: Coincident(g16,g17)
    c: Coincident(g17,g18)
    c: Coincident(g18,g19)
    c: Coincident(g19,g14)
    c: Equal(g14, g15-g19) x5
    c: PointOnObject(g14,g20)
    c: PointOnObject(g15,g20)
    c: PointOnObject(g16,g20)
    c: PointOnObject(g17,g20)
    c: PointOnObject(g18,g20)
    c: PointOnObject(g19,g20)
    c: Diameter(g20) = 7
    c: DistanceY(g-1,g20) = 7
    c: Vertical(g18)
    c: Distance(g17,g-2) = 1
    c: Coincident(g21,g22)
    c: Coincident(g22,g23)
    c: Coincident(g23,g24)
    c: Coincident(g24,g25)
    c: Coincident(g25,g26)
    c: Coincident(g26,g21)
    c: Equal(g21, g22-g26) x5
    c: PointOnObject(g21,g27)
    c: PointOnObject(g22,g27)
    c: PointOnObject(g23,g27)
    c: PointOnObject(g24,g27)
    c: PointOnObject(g25,g27)
    c: PointOnObject(g26,g27)
    c: Diameter(g27) = 7
    c: DistanceY(g-1,g27) = 7
    c: DistanceX(g21,g-1) = 1
    c: Vertical(g21)
    c: Coincident(g28,g29)
    c: Coincident(g29,g30)
    c: Coincident(g30,g31)
    c: Coincident(g31,g32)
    c: Coincident(g32,g33)
    c: Coincident(g33,g28)
    c: Equal(g28, g29-g33) x5
    c: PointOnObject(g28,g34)
    c: PointOnObject(g29,g34)
    c: PointOnObject(g30,g34)
    c: PointOnObject(g31,g34)
    c: PointOnObject(g32,g34)
    c: PointOnObject(g33,g34)
    c: PointOnObject(g34,g-1)
    c: Diameter(g34) = 7
    c: Vertical(g31)
    c: DistanceX(g34,g-1) = 8
    c: Coincident(g35,g36)
    c: Coincident(g36,g37)
    c: Coincident(g37,g38)
    c: Coincident(g38,g39)
    c: Coincident(g39,g40)
    c: Coincident(g40,g35)
    c: Equal(g35, g36-g40) x5
    c: PointOnObject(g35,g41)
    c: PointOnObject(g36,g41)
    c: PointOnObject(g37,g41)
    c: PointOnObject(g38,g41)
    c: PointOnObject(g39,g41)
    c: PointOnObject(g40,g41)
    c: Coincident(g42,g43)
    c: Coincident(g43,g44)
    c: Coincident(g44,g45)
    c: Coincident(g45,g46)
    c: Coincident(g46,g47)
    c: Coincident(g47,g42)
    c: Equal(g42, g43-g47) x5
    c: PointOnObject(g42,g48)
    c: PointOnObject(g43,g48)
    c: PointOnObject(g44,g48)
    c: PointOnObject(g45,g48)
    c: PointOnObject(g46,g48)
    c: PointOnObject(g47,g48)
    c: Equal(g41,g48)
    c: Diameter(g41) = 7
    c: Vertical(g39)
    c: Vertical(g43)
    c: Distance(g-2,g39) = 1
    c: Symmetric(g38,g43,g-2)
    c: Distance(g41,g-1) = 7
FEATURE [Part::Extrusion] Extrude716  label="hex318"
  Base = -> Sketch725
  Dir = (0,-1,2e-16)
  DirMode = 2
  FaceMakerClass = Part::FaceMakerBullseye
  FaceMakerMode = 3
  LengthFwd = 10
  LengthRev = 0
  Placement = pos=(100,0,-49) rot=(0,0,1;0rad)
  Solid = true
  Symmetric = false
FEATURE [Sketcher::SketchObject] Sketch726
  ArcFitTolerance = 1e-06
  FullyConstrained = true
  MakeInternals = false
  Placement = pos=(0,0,0) rot=(1,0,0;1.5708rad)
  sketch-geometry (49):
    g0: LineSegment StartX=1e-16 StartY=3.5 StartZ=0 EndX=-3.03109 EndY=1.75 EndZ=0
    g1: LineSegment StartX=-3.03109 StartY=1.75 StartZ=0 EndX=-3.03109 EndY=-1.75 EndZ=0
    g2: LineSegment StartX=-3.03109 StartY=-1.75 StartZ=0 EndX=-1e-16 EndY=-3.5 EndZ=0
    g3: LineSegment StartX=-1e-16 StartY=-3.5 StartZ=0 EndX=3.03109 EndY=-1.75 EndZ=0
    g4: LineSegment StartX=3.03109 StartY=-1.75 StartZ=0 EndX=3.03109 EndY=1.75 EndZ=0
    g5: LineSegment StartX=3.03109 StartY=1.75 StartZ=0 EndX=1e-16 EndY=3.5 EndZ=0
    g6: Circle [constr] CenterX=0 CenterY=0 CenterZ=0 NormalX=0 NormalY=0 NormalZ=1 AngleXU=0 Radius=3.5
    g7: LineSegment StartX=4.96892 StartY=-1.75002 StartZ=0 EndX=8.00002 EndY=-3.5 EndZ=0
    g8: LineSegment StartX=8.00002 StartY=-3.5 StartZ=0 EndX=11.0311 EndY=-1.74998 EndZ=0
    g9: LineSegment StartX=11.0311 StartY=-1.74998 StartZ=0 EndX=11.0311 EndY=1.75002 EndZ=0
    g10: LineSegment StartX=11.0311 StartY=1.75002 StartZ=0 EndX=7.99998 EndY=3.5 EndZ=0
    g11: LineSegment StartX=7.99998 StartY=3.5 StartZ=0 EndX=4.9689 EndY=1.74998 EndZ=0
    g12: LineSegment StartX=4.9689 StartY=1.74998 StartZ=0 EndX=4.96892 EndY=-1.75002 EndZ=0
    g13: Circle [constr] CenterX=8 CenterY=0 CenterZ=0 NormalX=0 NormalY=0 NormalZ=1 AngleXU=0 Radius=3.5
    g14: LineSegment StartX=4.03109 StartY=3.5 StartZ=0 EndX=7.06218 EndY=5.25 EndZ=0
    g15: LineSegment StartX=7.06218 StartY=5.25 StartZ=0 EndX=7.06218 EndY=8.75 EndZ=0
    g16: LineSegment StartX=7.06218 StartY=8.75 StartZ=0 EndX=4.03109 EndY=10.5 EndZ=0
    g17: LineSegment StartX=4.03109 StartY=10.5 StartZ=0 EndX=1 EndY=8.75 EndZ=0
    g18: LineSegment StartX=1 StartY=8.75 StartZ=0 EndX=1 EndY=5.25 EndZ=0
    g19: LineSegment StartX=1 StartY=5.25 StartZ=0 EndX=4.03109 EndY=3.5 EndZ=0
    g20: Circle [constr] CenterX=4.03109 CenterY=7 CenterZ=0 NormalX=0 NormalY=0 NormalZ=1 AngleXU=0 Radius=3.5
    g21: LineSegment StartX=-1 StartY=5.25 StartZ=0 EndX=-1 EndY=8.75 EndZ=0
    g22: LineSegment StartX=-1 StartY=8.75 StartZ=0 EndX=-4.03109 EndY=10.5 EndZ=0
    g23: LineSegment StartX=-4.03109 StartY=10.5 StartZ=0 EndX=-7.06218 EndY=8.75 EndZ=0
    g24: LineSegment StartX=-7.06218 StartY=8.75 StartZ=0 EndX=-7.06218 EndY=5.25 EndZ=0
    g25: LineSegment StartX=-7.06218 StartY=5.25 StartZ=0 EndX=-4.03109 EndY=3.5 EndZ=0
    g26: LineSegment StartX=-4.03109 StartY=3.5 StartZ=0 EndX=-1 EndY=5.25 EndZ=0
    g27: Circle [constr] CenterX=-4.03109 CenterY=7 CenterZ=0 NormalX=0 NormalY=0 NormalZ=1 AngleXU=0 Radius=3.5
    g28: LineSegment StartX=-4.96891 StartY=-1.75 StartZ=0 EndX=-4.96891 EndY=1.75 EndZ=0
    g29: LineSegment StartX=-4.96891 StartY=1.75 StartZ=0 EndX=-8 EndY=3.5 EndZ=0
    g30: LineSegment StartX=-8 StartY=3.5 StartZ=0 EndX=-11.0311 EndY=1.75 EndZ=0
    g31: LineSegment StartX=-11.0311 StartY=1.75 StartZ=0 EndX=-11.0311 EndY=-1.75 EndZ=0
    g32: LineSegment StartX=-11.0311 StartY=-1.75 StartZ=0 EndX=-8 EndY=-3.5 EndZ=0
    g33: LineSegment StartX=-8 StartY=-3.5 StartZ=0 EndX=-4.96891 EndY=-1.75 EndZ=0
    g34: Circle [constr] CenterX=-8 CenterY=0 CenterZ=0 NormalX=0 NormalY=0 NormalZ=1 AngleXU=0 Radius=3.5
    g35: LineSegment StartX=-4.03109 StartY=-3.5 StartZ=0 EndX=-7.06218 EndY=-5.25 EndZ=0
    g36: LineSegment StartX=-7.06218 StartY=-5.25 StartZ=0 EndX=-7.06218 EndY=-8.75 EndZ=0
    g37: LineSegment StartX=-7.06218 StartY=-8.75 StartZ=0 EndX=-4.03109 EndY=-10.5 EndZ=0
    g38: LineSegment StartX=-4.03109 StartY=-10.5 StartZ=0 EndX=-1 EndY=-8.75 EndZ=0
    g39: LineSegment StartX=-1 StartY=-8.75 StartZ=0 EndX=-1 EndY=-5.25 EndZ=0
    g40: LineSegment StartX=-1 StartY=-5.25 StartZ=0 EndX=-4.03109 EndY=-3.5 EndZ=0
    g41: Circle [constr] CenterX=-4.03109 CenterY=-7 CenterZ=0 NormalX=0 NormalY=0 NormalZ=1 AngleXU=0 Radius=3.5
    g42: LineSegment StartX=4.03109 StartY=-3.5 StartZ=0 EndX=1 EndY=-5.25 EndZ=0
    g43: LineSegment StartX=1 StartY=-5.25 StartZ=0 EndX=1 EndY=-8.75 EndZ=0
    g44: LineSegment StartX=1 StartY=-8.75 StartZ=0 EndX=4.03109 EndY=-10.5 EndZ=0
    g45: LineSegment StartX=4.03109 StartY=-10.5 StartZ=0 EndX=7.06218 EndY=-8.75 EndZ=0
    g46: LineSegment StartX=7.06218 StartY=-8.75 StartZ=0 EndX=7.06218 EndY=-5.25 EndZ=0
    g47: LineSegment StartX=7.06218 StartY=-5.25 StartZ=0 EndX=4.03109 EndY=-3.5 EndZ=0
    g48: Circle [constr] CenterX=4.03109 CenterY=-7 CenterZ=0 NormalX=0 NormalY=0 NormalZ=1 AngleXU=0 Radius=3.5
  constraints (117):
    c: Coincident(g0,g1)
    c: Coincident(g1,g2)
    c: Coincident(g2,g3)
    c: Coincident(g3,g4)
    c: Coincident(g4,g5)
    c: Coincident(g5,g0)
    c: Equal(g0, g1-g5) x5
    c: PointOnObject(g0,g6)
    c: PointOnObject(g1,g6)
    c: PointOnObject(g2,g6)
    c: PointOnObject(g3,g6)
    c: PointOnObject(g4,g6)
    c: PointOnObject(g5,g6)
    c: Coincident(g6,g-1)
    c: Diameter(g6) = 7
    c: PointOnObject(g0,g-2)
    c: Coincident(g7,g8)
    c: Coincident(g8,g9)
    c: Coincident(g9,g10)
    c: Coincident(g10,g11)
    c: Coincident(g11,g12)
    c: Coincident(g12,g7)
    c: Equal(g7, g8-g12) x5
    c: PointOnObject(g7,g13)
    c: PointOnObject(g8,g13)
    c: PointOnObject(g9,g13)
    c: PointOnObject(g10,g13)
    c: PointOnObject(g11,g13)
    c: PointOnObject(g12,g13)
    c: PointOnObject(g13,g-1)
    c: Diameter(g13) = 7
    c: Distance(g6,g13) = 8
    c: Horizontal(g0,g10)
    c: Coincident(g14,g15)
    c: Coincident(g15,g16)
    c: Coincident(g16,g17)
    c: Coincident(g17,g18)
    c: Coincident(g18,g19)
    c: Coincident(g19,g14)
    c: Equal(g14, g15-g19) x5
    c: PointOnObject(g14,g20)
    c: PointOnObject(g15,g20)
    c: PointOnObject(g16,g20)
    c: PointOnObject(g17,g20)
    c: PointOnObject(g18,g20)
    c: PointOnObject(g19,g20)
    c: Diameter(g20) = 7
    c: DistanceY(g-1,g20) = 7
    c: Vertical(g18)
    c: Distance(g17,g-2) = 1
    c: Coincident(g21,g22)
    c: Coincident(g22,g23)
    c: Coincident(g23,g24)
    c: Coincident(g24,g25)
    c: Coincident(g25,g26)
    c: Coincident(g26,g21)
    c: Equal(g21, g22-g26) x5
    c: PointOnObject(g21,g27)
    c: PointOnObject(g22,g27)
    c: PointOnObject(g23,g27)
    c: PointOnObject(g24,g27)
    c: PointOnObject(g25,g27)
    c: PointOnObject(g26,g27)
    c: Diameter(g27) = 7
    c: DistanceY(g-1,g27) = 7
    c: DistanceX(g21,g-1) = 1
    c: Vertical(g21)
    c: Coincident(g28,g29)
    c: Coincident(g29,g30)
    c: Coincident(g30,g31)
    c: Coincident(g31,g32)
    c: Coincident(g32,g33)
    c: Coincident(g33,g28)
    c: Equal(g28, g29-g33) x5
    c: PointOnObject(g28,g34)
    c: PointOnObject(g29,g34)
    c: PointOnObject(g30,g34)
    c: PointOnObject(g31,g34)
    c: PointOnObject(g32,g34)
    c: PointOnObject(g33,g34)
    c: PointOnObject(g34,g-1)
    c: Diameter(g34) = 7
    c: Vertical(g31)
    c: DistanceX(g34,g-1) = 8
    c: Coincident(g35,g36)
    c: Coincident(g36,g37)
    c: Coincident(g37,g38)
    c: Coincident(g38,g39)
    c: Coincident(g39,g40)
    c: Coincident(g40,g35)
    c: Equal(g35, g36-g40) x5
    c: PointOnObject(g35,g41)
    c: PointOnObject(g36,g41)
    c: PointOnObject(g37,g41)
    c: PointOnObject(g38,g41)
    c: PointOnObject(g39,g41)
    c: PointOnObject(g40,g41)
    c: Coincident(g42,g43)
    c: Coincident(g43,g44)
    c: Coincident(g44,g45)
    c: Coincident(g45,g46)
    c: Coincident(g46,g47)
    c: Coincident(g47,g42)
    c: Equal(g42, g43-g47) x5
    c: PointOnObject(g42,g48)
    c: PointOnObject(g43,g48)
    c: PointOnObject(g44,g48)
    c: PointOnObject(g45,g48)
    c: PointOnObject(g46,g48)
    c: PointOnObject(g47,g48)
    c: Equal(g41,g48)
    c: Diameter(g41) = 7
    c: Vertical(g39)
    c: Vertical(g43)
    c: Distance(g-2,g39) = 1
    c: Symmetric(g38,g43,g-2)
    c: Distance(g41,g-1) = 7
FEATURE [Part::Extrusion] Extrude717  label="hex319"
  Base = -> Sketch726
  Dir = (0,-1,2e-16)
  DirMode = 2
  FaceMakerClass = Part::FaceMakerBullseye
  FaceMakerMode = 3
  LengthFwd = 10
  LengthRev = 0
  Placement = pos=(-92,0,-35) rot=(0,0,1;0rad)
  Solid = true
  Symmetric = false
FEATURE [Sketcher::SketchObject] Sketch727
  ArcFitTolerance = 1e-06
  FullyConstrained = true
  MakeInternals = false
  Placement = pos=(0,0,0) rot=(1,0,0;1.5708rad)
  sketch-geometry (49):
    g0: LineSegment StartX=1e-16 StartY=3.5 StartZ=0 EndX=-3.03109 EndY=1.75 EndZ=0
    g1: LineSegment StartX=-3.03109 StartY=1.75 StartZ=0 EndX=-3.03109 EndY=-1.75 EndZ=0
    g2: LineSegment StartX=-3.03109 StartY=-1.75 StartZ=0 EndX=-1e-16 EndY=-3.5 EndZ=0
    g3: LineSegment StartX=-1e-16 StartY=-3.5 StartZ=0 EndX=3.03109 EndY=-1.75 EndZ=0
    g4: LineSegment StartX=3.03109 StartY=-1.75 StartZ=0 EndX=3.03109 EndY=1.75 EndZ=0
    g5: LineSegment StartX=3.03109 StartY=1.75 StartZ=0 EndX=1e-16 EndY=3.5 EndZ=0
    g6: Circle [constr] CenterX=0 CenterY=0 CenterZ=0 NormalX=0 NormalY=0 NormalZ=1 AngleXU=0 Radius=3.5
    g7: LineSegment StartX=4.96892 StartY=-1.75002 StartZ=0 EndX=8.00002 EndY=-3.5 EndZ=0
    g8: LineSegment StartX=8.00002 StartY=-3.5 StartZ=0 EndX=11.0311 EndY=-1.74998 EndZ=0
    g9: LineSegment StartX=11.0311 StartY=-1.74998 StartZ=0 EndX=11.0311 EndY=1.75002 EndZ=0
    g10: LineSegment StartX=11.0311 StartY=1.75002 StartZ=0 EndX=7.99998 EndY=3.5 EndZ=0
    g11: LineSegment StartX=7.99998 StartY=3.5 StartZ=0 EndX=4.9689 EndY=1.74998 EndZ=0
    g12: LineSegment StartX=4.9689 StartY=1.74998 StartZ=0 EndX=4.96892 EndY=-1.75002 EndZ=0
    g13: Circle [constr] CenterX=8 CenterY=0 CenterZ=0 NormalX=0 NormalY=0 NormalZ=1 AngleXU=0 Radius=3.5
    g14: LineSegment StartX=4.03109 StartY=3.5 StartZ=0 EndX=7.06218 EndY=5.25 EndZ=0
    g15: LineSegment StartX=7.06218 StartY=5.25 StartZ=0 EndX=7.06218 EndY=8.75 EndZ=0
    g16: LineSegment StartX=7.06218 StartY=8.75 StartZ=0 EndX=4.03109 EndY=10.5 EndZ=0
    g17: LineSegment StartX=4.03109 StartY=10.5 StartZ=0 EndX=1 EndY=8.75 EndZ=0
    g18: LineSegment StartX=1 StartY=8.75 StartZ=0 EndX=1 EndY=5.25 EndZ=0
    g19: LineSegment StartX=1 StartY=5.25 StartZ=0 EndX=4.03109 EndY=3.5 EndZ=0
    g20: Circle [constr] CenterX=4.03109 CenterY=7 CenterZ=0 NormalX=0 NormalY=0 NormalZ=1 AngleXU=0 Radius=3.5
    g21: LineSegment StartX=-1 StartY=5.25 StartZ=0 EndX=-1 EndY=8.75 EndZ=0
    g22: LineSegment StartX=-1 StartY=8.75 StartZ=0 EndX=-4.03109 EndY=10.5 EndZ=0
    g23: LineSegment StartX=-4.03109 StartY=10.5 StartZ=0 EndX=-7.06218 EndY=8.75 EndZ=0
    g24: LineSegment StartX=-7.06218 StartY=8.75 StartZ=0 EndX=-7.06218 EndY=5.25 EndZ=0
    g25: LineSegment StartX=-7.06218 StartY=5.25 StartZ=0 EndX=-4.03109 EndY=3.5 EndZ=0
    g26: LineSegment StartX=-4.03109 StartY=3.5 StartZ=0 EndX=-1 EndY=5.25 EndZ=0
    g27: Circle [constr] CenterX=-4.03109 CenterY=7 CenterZ=0 NormalX=0 NormalY=0 NormalZ=1 AngleXU=0 Radius=3.5
    g28: LineSegment StartX=-4.96891 StartY=-1.75 StartZ=0 EndX=-4.96891 EndY=1.75 EndZ=0
    g29: LineSegment StartX=-4.96891 StartY=1.75 StartZ=0 EndX=-8 EndY=3.5 EndZ=0
    g30: LineSegment StartX=-8 StartY=3.5 StartZ=0 EndX=-11.0311 EndY=1.75 EndZ=0
    g31: LineSegment StartX=-11.0311 StartY=1.75 StartZ=0 EndX=-11.0311 EndY=-1.75 EndZ=0
    g32: LineSegment StartX=-11.0311 StartY=-1.75 StartZ=0 EndX=-8 EndY=-3.5 EndZ=0
    g33: LineSegment StartX=-8 StartY=-3.5 StartZ=0 EndX=-4.96891 EndY=-1.75 EndZ=0
    g34: Circle [constr] CenterX=-8 CenterY=0 CenterZ=0 NormalX=0 NormalY=0 NormalZ=1 AngleXU=0 Radius=3.5
    g35: LineSegment StartX=-4.03109 StartY=-3.5 StartZ=0 EndX=-7.06218 EndY=-5.25 EndZ=0
    g36: LineSegment StartX=-7.06218 StartY=-5.25 StartZ=0 EndX=-7.06218 EndY=-8.75 EndZ=0
    g37: LineSegment StartX=-7.06218 StartY=-8.75 StartZ=0 EndX=-4.03109 EndY=-10.5 EndZ=0
    g38: LineSegment StartX=-4.03109 StartY=-10.5 StartZ=0 EndX=-1 EndY=-8.75 EndZ=0
    g39: LineSegment StartX=-1 StartY=-8.75 StartZ=0 EndX=-1 EndY=-5.25 EndZ=0
    g40: LineSegment StartX=-1 StartY=-5.25 StartZ=0 EndX=-4.03109 EndY=-3.5 EndZ=0
    g41: Circle [constr] CenterX=-4.03109 CenterY=-7 CenterZ=0 NormalX=0 NormalY=0 NormalZ=1 AngleXU=0 Radius=3.5
    g42: LineSegment StartX=4.03109 StartY=-3.5 StartZ=0 EndX=1 EndY=-5.25 EndZ=0
    g43: LineSegment StartX=1 StartY=-5.25 StartZ=0 EndX=1 EndY=-8.75 EndZ=0
    g44: LineSegment StartX=1 StartY=-8.75 StartZ=0 EndX=4.03109 EndY=-10.5 EndZ=0
    g45: LineSegment StartX=4.03109 StartY=-10.5 StartZ=0 EndX=7.06218 EndY=-8.75 EndZ=0
    g46: LineSegment StartX=7.06218 StartY=-8.75 StartZ=0 EndX=7.06218 EndY=-5.25 EndZ=0
    g47: LineSegment StartX=7.06218 StartY=-5.25 StartZ=0 EndX=4.03109 EndY=-3.5 EndZ=0
    g48: Circle [constr] CenterX=4.03109 CenterY=-7 CenterZ=0 NormalX=0 NormalY=0 NormalZ=1 AngleXU=0 Radius=3.5
  constraints (117):
    c: Coincident(g0,g1)
    c: Coincident(g1,g2)
    c: Coincident(g2,g3)
    c: Coincident(g3,g4)
    c: Coincident(g4,g5)
    c: Coincident(g5,g0)
    c: Equal(g0, g1-g5) x5
    c: PointOnObject(g0,g6)
    c: PointOnObject(g1,g6)
    c: PointOnObject(g2,g6)
    c: PointOnObject(g3,g6)
    c: PointOnObject(g4,g6)
    c: PointOnObject(g5,g6)
    c: Coincident(g6,g-1)
    c: Diameter(g6) = 7
    c: PointOnObject(g0,g-2)
    c: Coincident(g7,g8)
    c: Coincident(g8,g9)
    c: Coincident(g9,g10)
    c: Coincident(g10,g11)
    c: Coincident(g11,g12)
    c: Coincident(g12,g7)
    c: Equal(g7, g8-g12) x5
    c: PointOnObject(g7,g13)
    c: PointOnObject(g8,g13)
    c: PointOnObject(g9,g13)
    c: PointOnObject(g10,g13)
    c: PointOnObject(g11,g13)
    c: PointOnObject(g12,g13)
    c: PointOnObject(g13,g-1)
    c: Diameter(g13) = 7
    c: Distance(g6,g13) = 8
    c: Horizontal(g0,g10)
    c: Coincident(g14,g15)
    c: Coincident(g15,g16)
    c: Coincident(g16,g17)
    c: Coincident(g17,g18)
    c: Coincident(g18,g19)
    c: Coincident(g19,g14)
    c: Equal(g14, g15-g19) x5
    c: PointOnObject(g14,g20)
    c: PointOnObject(g15,g20)
    c: PointOnObject(g16,g20)
    c: PointOnObject(g17,g20)
    c: PointOnObject(g18,g20)
    c: PointOnObject(g19,g20)
    c: Diameter(g20) = 7
    c: DistanceY(g-1,g20) = 7
    c: Vertical(g18)
    c: Distance(g17,g-2) = 1
    c: Coincident(g21,g22)
    c: Coincident(g22,g23)
    c: Coincident(g23,g24)
    c: Coincident(g24,g25)
    c: Coincident(g25,g26)
    c: Coincident(g26,g21)
    c: Equal(g21, g22-g26) x5
    c: PointOnObject(g21,g27)
    c: PointOnObject(g22,g27)
    c: PointOnObject(g23,g27)
    c: PointOnObject(g24,g27)
    c: PointOnObject(g25,g27)
    c: PointOnObject(g26,g27)
    c: Diameter(g27) = 7
    c: DistanceY(g-1,g27) = 7
    c: DistanceX(g21,g-1) = 1
    c: Vertical(g21)
    c: Coincident(g28,g29)
    c: Coincident(g29,g30)
    c: Coincident(g30,g31)
    c: Coincident(g31,g32)
    c: Coincident(g32,g33)
    c: Coincident(g33,g28)
    c: Equal(g28, g29-g33) x5
    c: PointOnObject(g28,g34)
    c: PointOnObject(g29,g34)
    c: PointOnObject(g30,g34)
    c: PointOnObject(g31,g34)
    c: PointOnObject(g32,g34)
    c: PointOnObject(g33,g34)
    c: PointOnObject(g34,g-1)
    c: Diameter(g34) = 7
    c: Vertical(g31)
    c: DistanceX(g34,g-1) = 8
    c: Coincident(g35,g36)
    c: Coincident(g36,g37)
    c: Coincident(g37,g38)
    c: Coincident(g38,g39)
    c: Coincident(g39,g40)
    c: Coincident(g40,g35)
    c: Equal(g35, g36-g40) x5
    c: PointOnObject(g35,g41)
    c: PointOnObject(g36,g41)
    c: PointOnObject(g37,g41)
    c: PointOnObject(g38,g41)
    c: PointOnObject(g39,g41)
    c: PointOnObject(g40,g41)
    c: Coincident(g42,g43)
    c: Coincident(g43,g44)
    c: Coincident(g44,g45)
    c: Coincident(g45,g46)
    c: Coincident(g46,g47)
    c: Coincident(g47,g42)
    c: Equal(g42, g43-g47) x5
    c: PointOnObject(g42,g48)
    c: PointOnObject(g43,g48)
    c: PointOnObject(g44,g48)
    c: PointOnObject(g45,g48)
    c: PointOnObject(g46,g48)
    c: PointOnObject(g47,g48)
    c: Equal(g41,g48)
    c: Diameter(g41) = 7
    c: Vertical(g39)
    c: Vertical(g43)
    c: Distance(g-2,g39) = 1
    c: Symmetric(g38,g43,g-2)
    c: Distance(g41,g-1) = 7
FEATURE [Part::Extrusion] Extrude718  label="hex320"
  Base = -> Sketch727
  Dir = (0,-1,2e-16)
  DirMode = 2
  FaceMakerClass = Part::FaceMakerBullseye
  FaceMakerMode = 3
  LengthFwd = 10
  LengthRev = 0
  Placement = pos=(-100,0,21) rot=(0,0,1;0rad)
  Solid = true
  Symmetric = false
FEATURE [Sketcher::SketchObject] Sketch728
  ArcFitTolerance = 1e-06
  FullyConstrained = true
  MakeInternals = false
  Placement = pos=(0,0,0) rot=(1,0,0;1.5708rad)
  sketch-geometry (49):
    g0: LineSegment StartX=1e-16 StartY=3.5 StartZ=0 EndX=-3.03109 EndY=1.75 EndZ=0
    g1: LineSegment StartX=-3.03109 StartY=1.75 StartZ=0 EndX=-3.03109 EndY=-1.75 EndZ=0
    g2: LineSegment StartX=-3.03109 StartY=-1.75 StartZ=0 EndX=-1e-16 EndY=-3.5 EndZ=0
    g3: LineSegment StartX=-1e-16 StartY=-3.5 StartZ=0 EndX=3.03109 EndY=-1.75 EndZ=0
    g4: LineSegment StartX=3.03109 StartY=-1.75 StartZ=0 EndX=3.03109 EndY=1.75 EndZ=0
    g5: LineSegment StartX=3.03109 StartY=1.75 StartZ=0 EndX=1e-16 EndY=3.5 EndZ=0
    g6: Circle [constr] CenterX=0 CenterY=0 CenterZ=0 NormalX=0 NormalY=0 NormalZ=1 AngleXU=0 Radius=3.5
    g7: LineSegment StartX=4.96892 StartY=-1.75002 StartZ=0 EndX=8.00002 EndY=-3.5 EndZ=0
    g8: LineSegment StartX=8.00002 StartY=-3.5 StartZ=0 EndX=11.0311 EndY=-1.74998 EndZ=0
    g9: LineSegment StartX=11.0311 StartY=-1.74998 StartZ=0 EndX=11.0311 EndY=1.75002 EndZ=0
    g10: LineSegment StartX=11.0311 StartY=1.75002 StartZ=0 EndX=7.99998 EndY=3.5 EndZ=0
    g11: LineSegment StartX=7.99998 StartY=3.5 StartZ=0 EndX=4.9689 EndY=1.74998 EndZ=0
    g12: LineSegment StartX=4.9689 StartY=1.74998 StartZ=0 EndX=4.96892 EndY=-1.75002 EndZ=0
    g13: Circle [constr] CenterX=8 CenterY=0 CenterZ=0 NormalX=0 NormalY=0 NormalZ=1 AngleXU=0 Radius=3.5
    g14: LineSegment StartX=4.03109 StartY=3.5 StartZ=0 EndX=7.06218 EndY=5.25 EndZ=0
    g15: LineSegment StartX=7.06218 StartY=5.25 StartZ=0 EndX=7.06218 EndY=8.75 EndZ=0
    g16: LineSegment StartX=7.06218 StartY=8.75 StartZ=0 EndX=4.03109 EndY=10.5 EndZ=0
    g17: LineSegment StartX=4.03109 StartY=10.5 StartZ=0 EndX=1 EndY=8.75 EndZ=0
    g18: LineSegment StartX=1 StartY=8.75 StartZ=0 EndX=1 EndY=5.25 EndZ=0
    g19: LineSegment StartX=1 StartY=5.25 StartZ=0 EndX=4.03109 EndY=3.5 EndZ=0
    g20: Circle [constr] CenterX=4.03109 CenterY=7 CenterZ=0 NormalX=0 NormalY=0 NormalZ=1 AngleXU=0 Radius=3.5
    g21: LineSegment StartX=-1 StartY=5.25 StartZ=0 EndX=-1 EndY=8.75 EndZ=0
    g22: LineSegment StartX=-1 StartY=8.75 StartZ=0 EndX=-4.03109 EndY=10.5 EndZ=0
    g23: LineSegment StartX=-4.03109 StartY=10.5 StartZ=0 EndX=-7.06218 EndY=8.75 EndZ=0
    g24: LineSegment StartX=-7.06218 StartY=8.75 StartZ=0 EndX=-7.06218 EndY=5.25 EndZ=0
    g25: LineSegment StartX=-7.06218 StartY=5.25 StartZ=0 EndX=-4.03109 EndY=3.5 EndZ=0
    g26: LineSegment StartX=-4.03109 StartY=3.5 StartZ=0 EndX=-1 EndY=5.25 EndZ=0
    g27: Circle [constr] CenterX=-4.03109 CenterY=7 CenterZ=0 NormalX=0 NormalY=0 NormalZ=1 AngleXU=0 Radius=3.5
    g28: LineSegment StartX=-4.96891 StartY=-1.75 StartZ=0 EndX=-4.96891 EndY=1.75 EndZ=0
    g29: LineSegment StartX=-4.96891 StartY=1.75 StartZ=0 EndX=-8 EndY=3.5 EndZ=0
    g30: LineSegment StartX=-8 StartY=3.5 StartZ=0 EndX=-11.0311 EndY=1.75 EndZ=0
    g31: LineSegment StartX=-11.0311 StartY=1.75 StartZ=0 EndX=-11.0311 EndY=-1.75 EndZ=0
    g32: LineSegment StartX=-11.0311 StartY=-1.75 StartZ=0 EndX=-8 EndY=-3.5 EndZ=0
    g33: LineSegment StartX=-8 StartY=-3.5 StartZ=0 EndX=-4.96891 EndY=-1.75 EndZ=0
    g34: Circle [constr] CenterX=-8 CenterY=0 CenterZ=0 NormalX=0 NormalY=0 NormalZ=1 AngleXU=0 Radius=3.5
    g35: LineSegment StartX=-4.03109 StartY=-3.5 StartZ=0 EndX=-7.06218 EndY=-5.25 EndZ=0
    g36: LineSegment StartX=-7.06218 StartY=-5.25 StartZ=0 EndX=-7.06218 EndY=-8.75 EndZ=0
    g37: LineSegment StartX=-7.06218 StartY=-8.75 StartZ=0 EndX=-4.03109 EndY=-10.5 EndZ=0
    g38: LineSegment StartX=-4.03109 StartY=-10.5 StartZ=0 EndX=-1 EndY=-8.75 EndZ=0
    g39: LineSegment StartX=-1 StartY=-8.75 StartZ=0 EndX=-1 EndY=-5.25 EndZ=0
    g40: LineSegment StartX=-1 StartY=-5.25 StartZ=0 EndX=-4.03109 EndY=-3.5 EndZ=0
    g41: Circle [constr] CenterX=-4.03109 CenterY=-7 CenterZ=0 NormalX=0 NormalY=0 NormalZ=1 AngleXU=0 Radius=3.5
    g42: LineSegment StartX=4.03109 StartY=-3.5 StartZ=0 EndX=1 EndY=-5.25 EndZ=0
    g43: LineSegment StartX=1 StartY=-5.25 StartZ=0 EndX=1 EndY=-8.75 EndZ=0
    g44: LineSegment StartX=1 StartY=-8.75 StartZ=0 EndX=4.03109 EndY=-10.5 EndZ=0
    g45: LineSegment StartX=4.03109 StartY=-10.5 StartZ=0 EndX=7.06218 EndY=-8.75 EndZ=0
    g46: LineSegment StartX=7.06218 StartY=-8.75 StartZ=0 EndX=7.06218 EndY=-5.25 EndZ=0
    g47: LineSegment StartX=7.06218 StartY=-5.25 StartZ=0 EndX=4.03109 EndY=-3.5 EndZ=0
    g48: Circle [constr] CenterX=4.03109 CenterY=-7 CenterZ=0 NormalX=0 NormalY=0 NormalZ=1 AngleXU=0 Radius=3.5
  constraints (117):
    c: Coincident(g0,g1)
    c: Coincident(g1,g2)
    c: Coincident(g2,g3)
    c: Coincident(g3,g4)
    c: Coincident(g4,g5)
    c: Coincident(g5,g0)
    c: Equal(g0, g1-g5) x5
    c: PointOnObject(g0,g6)
    c: PointOnObject(g1,g6)
    c: PointOnObject(g2,g6)
    c: PointOnObject(g3,g6)
    c: PointOnObject(g4,g6)
    c: PointOnObject(g5,g6)
    c: Coincident(g6,g-1)
    c: Diameter(g6) = 7
    c: PointOnObject(g0,g-2)
    c: Coincident(g7,g8)
    c: Coincident(g8,g9)
    c: Coincident(g9,g10)
    c: Coincident(g10,g11)
    c: Coincident(g11,g12)
    c: Coincident(g12,g7)
    c: Equal(g7, g8-g12) x5
    c: PointOnObject(g7,g13)
    c: PointOnObject(g8,g13)
    c: PointOnObject(g9,g13)
    c: PointOnObject(g10,g13)
    c: PointOnObject(g11,g13)
    c: PointOnObject(g12,g13)
    c: PointOnObject(g13,g-1)
    c: Diameter(g13) = 7
    c: Distance(g6,g13) = 8
    c: Horizontal(g0,g10)
    c: Coincident(g14,g15)
    c: Coincident(g15,g16)
    c: Coincident(g16,g17)
    c: Coincident(g17,g18)
    c: Coincident(g18,g19)
    c: Coincident(g19,g14)
    c: Equal(g14, g15-g19) x5
    c: PointOnObject(g14,g20)
    c: PointOnObject(g15,g20)
    c: PointOnObject(g16,g20)
    c: PointOnObject(g17,g20)
    c: PointOnObject(g18,g20)
    c: PointOnObject(g19,g20)
    c: Diameter(g20) = 7
    c: DistanceY(g-1,g20) = 7
    c: Vertical(g18)
    c: Distance(g17,g-2) = 1
    c: Coincident(g21,g22)
    c: Coincident(g22,g23)
    c: Coincident(g23,g24)
    c: Coincident(g24,g25)
    c: Coincident(g25,g26)
    c: Coincident(g26,g21)
    c: Equal(g21, g22-g26) x5
    c: PointOnObject(g21,g27)
    c: PointOnObject(g22,g27)
    c: PointOnObject(g23,g27)
    c: PointOnObject(g24,g27)
    c: PointOnObject(g25,g27)
    c: PointOnObject(g26,g27)
    c: Diameter(g27) = 7
    c: DistanceY(g-1,g27) = 7
    c: DistanceX(g21,g-1) = 1
    c: Vertical(g21)
    c: Coincident(g28,g29)
    c: Coincident(g29,g30)
    c: Coincident(g30,g31)
    c: Coincident(g31,g32)
    c: Coincident(g32,g33)
    c: Coincident(g33,g28)
    c: Equal(g28, g29-g33) x5
    c: PointOnObject(g28,g34)
    c: PointOnObject(g29,g34)
    c: PointOnObject(g30,g34)
    c: PointOnObject(g31,g34)
    c: PointOnObject(g32,g34)
    c: PointOnObject(g33,g34)
    c: PointOnObject(g34,g-1)
    c: Diameter(g34) = 7
    c: Vertical(g31)
    c: DistanceX(g34,g-1) = 8
    c: Coincident(g35,g36)
    c: Coincident(g36,g37)
    c: Coincident(g37,g38)
    c: Coincident(g38,g39)
    c: Coincident(g39,g40)
    c: Coincident(g40,g35)
    c: Equal(g35, g36-g40) x5
    c: PointOnObject(g35,g41)
    c: PointOnObject(g36,g41)
    c: PointOnObject(g37,g41)
    c: PointOnObject(g38,g41)
    c: PointOnObject(g39,g41)
    c: PointOnObject(g40,g41)
    c: Coincident(g42,g43)
    c: Coincident(g43,g44)
    c: Coincident(g44,g45)
    c: Coincident(g45,g46)
    c: Coincident(g46,g47)
    c: Coincident(g47,g42)
    c: Equal(g42, g43-g47) x5
    c: PointOnObject(g42,g48)
    c: PointOnObject(g43,g48)
    c: PointOnObject(g44,g48)
    c: PointOnObject(g45,g48)
    c: PointOnObject(g46,g48)
    c: PointOnObject(g47,g48)
    c: Equal(g41,g48)
    c: Diameter(g41) = 7
    c: Vertical(g39)
    c: Vertical(g43)
    c: Distance(g-2,g39) = 1
    c: Symmetric(g38,g43,g-2)
    c: Distance(g41,g-1) = 7
FEATURE [Part::Extrusion] Extrude719  label="hex321"
  Base = -> Sketch728
  Dir = (0,-1,2e-16)
  DirMode = 2
  FaceMakerClass = Part::FaceMakerBullseye
  FaceMakerMode = 3
  LengthFwd = 10
  LengthRev = 0
  Placement = pos=(-104,0,-28) rot=(0,0,1;0rad)
  Solid = true
  Symmetric = false
FEATURE [Sketcher::SketchObject] Sketch729
  ArcFitTolerance = 1e-06
  FullyConstrained = true
  MakeInternals = false
  Placement = pos=(0,0,0) rot=(1,0,0;1.5708rad)
  sketch-geometry (49):
    g0: LineSegment StartX=1e-16 StartY=3.5 StartZ=0 EndX=-3.03109 EndY=1.75 EndZ=0
    g1: LineSegment StartX=-3.03109 StartY=1.75 StartZ=0 EndX=-3.03109 EndY=-1.75 EndZ=0
    g2: LineSegment StartX=-3.03109 StartY=-1.75 StartZ=0 EndX=-1e-16 EndY=-3.5 EndZ=0
    g3: LineSegment StartX=-1e-16 StartY=-3.5 StartZ=0 EndX=3.03109 EndY=-1.75 EndZ=0
    g4: LineSegment StartX=3.03109 StartY=-1.75 StartZ=0 EndX=3.03109 EndY=1.75 EndZ=0
    g5: LineSegment StartX=3.03109 StartY=1.75 StartZ=0 EndX=1e-16 EndY=3.5 EndZ=0
    g6: Circle [constr] CenterX=0 CenterY=0 CenterZ=0 NormalX=0 NormalY=0 NormalZ=1 AngleXU=0 Radius=3.5
    g7: LineSegment StartX=4.96892 StartY=-1.75002 StartZ=0 EndX=8.00002 EndY=-3.5 EndZ=0
    g8: LineSegment StartX=8.00002 StartY=-3.5 StartZ=0 EndX=11.0311 EndY=-1.74998 EndZ=0
    g9: LineSegment StartX=11.0311 StartY=-1.74998 StartZ=0 EndX=11.0311 EndY=1.75002 EndZ=0
    g10: LineSegment StartX=11.0311 StartY=1.75002 StartZ=0 EndX=7.99998 EndY=3.5 EndZ=0
    g11: LineSegment StartX=7.99998 StartY=3.5 StartZ=0 EndX=4.9689 EndY=1.74998 EndZ=0
    g12: LineSegment StartX=4.9689 StartY=1.74998 StartZ=0 EndX=4.96892 EndY=-1.75002 EndZ=0
    g13: Circle [constr] CenterX=8 CenterY=0 CenterZ=0 NormalX=0 NormalY=0 NormalZ=1 AngleXU=0 Radius=3.5
    g14: LineSegment StartX=4.03109 StartY=3.5 StartZ=0 EndX=7.06218 EndY=5.25 EndZ=0
    g15: LineSegment StartX=7.06218 StartY=5.25 StartZ=0 EndX=7.06218 EndY=8.75 EndZ=0
    g16: LineSegment StartX=7.06218 StartY=8.75 StartZ=0 EndX=4.03109 EndY=10.5 EndZ=0
    g17: LineSegment StartX=4.03109 StartY=10.5 StartZ=0 EndX=1 EndY=8.75 EndZ=0
    g18: LineSegment StartX=1 StartY=8.75 StartZ=0 EndX=1 EndY=5.25 EndZ=0
    g19: LineSegment StartX=1 StartY=5.25 StartZ=0 EndX=4.03109 EndY=3.5 EndZ=0
    g20: Circle [constr] CenterX=4.03109 CenterY=7 CenterZ=0 NormalX=0 NormalY=0 NormalZ=1 AngleXU=0 Radius=3.5
    g21: LineSegment StartX=-1 StartY=5.25 StartZ=0 EndX=-1 EndY=8.75 EndZ=0
    g22: LineSegment StartX=-1 StartY=8.75 StartZ=0 EndX=-4.03109 EndY=10.5 EndZ=0
    g23: LineSegment StartX=-4.03109 StartY=10.5 StartZ=0 EndX=-7.06218 EndY=8.75 EndZ=0
    g24: LineSegment StartX=-7.06218 StartY=8.75 StartZ=0 EndX=-7.06218 EndY=5.25 EndZ=0
    g25: LineSegment StartX=-7.06218 StartY=5.25 StartZ=0 EndX=-4.03109 EndY=3.5 EndZ=0
    g26: LineSegment StartX=-4.03109 StartY=3.5 StartZ=0 EndX=-1 EndY=5.25 EndZ=0
    g27: Circle [constr] CenterX=-4.03109 CenterY=7 CenterZ=0 NormalX=0 NormalY=0 NormalZ=1 AngleXU=0 Radius=3.5
    g28: LineSegment StartX=-4.96891 StartY=-1.75 StartZ=0 EndX=-4.96891 EndY=1.75 EndZ=0
    g29: LineSegment StartX=-4.96891 StartY=1.75 StartZ=0 EndX=-8 EndY=3.5 EndZ=0
    g30: LineSegment StartX=-8 StartY=3.5 StartZ=0 EndX=-11.0311 EndY=1.75 EndZ=0
    g31: LineSegment StartX=-11.0311 StartY=1.75 StartZ=0 EndX=-11.0311 EndY=-1.75 EndZ=0
    g32: LineSegment StartX=-11.0311 StartY=-1.75 StartZ=0 EndX=-8 EndY=-3.5 EndZ=0
    g33: LineSegment StartX=-8 StartY=-3.5 StartZ=0 EndX=-4.96891 EndY=-1.75 EndZ=0
    g34: Circle [constr] CenterX=-8 CenterY=0 CenterZ=0 NormalX=0 NormalY=0 NormalZ=1 AngleXU=0 Radius=3.5
    g35: LineSegment StartX=-4.03109 StartY=-3.5 StartZ=0 EndX=-7.06218 EndY=-5.25 EndZ=0
    g36: LineSegment StartX=-7.06218 StartY=-5.25 StartZ=0 EndX=-7.06218 EndY=-8.75 EndZ=0
    g37: LineSegment StartX=-7.06218 StartY=-8.75 StartZ=0 EndX=-4.03109 EndY=-10.5 EndZ=0
    g38: LineSegment StartX=-4.03109 StartY=-10.5 StartZ=0 EndX=-1 EndY=-8.75 EndZ=0
    g39: LineSegment StartX=-1 StartY=-8.75 StartZ=0 EndX=-1 EndY=-5.25 EndZ=0
    g40: LineSegment StartX=-1 StartY=-5.25 StartZ=0 EndX=-4.03109 EndY=-3.5 EndZ=0
    g41: Circle [constr] CenterX=-4.03109 CenterY=-7 CenterZ=0 NormalX=0 NormalY=0 NormalZ=1 AngleXU=0 Radius=3.5
    g42: LineSegment StartX=4.03109 StartY=-3.5 StartZ=0 EndX=1 EndY=-5.25 EndZ=0
    g43: LineSegment StartX=1 StartY=-5.25 StartZ=0 EndX=1 EndY=-8.75 EndZ=0
    g44: LineSegment StartX=1 StartY=-8.75 StartZ=0 EndX=4.03109 EndY=-10.5 EndZ=0
    g45: LineSegment StartX=4.03109 StartY=-10.5 StartZ=0 EndX=7.06218 EndY=-8.75 EndZ=0
    g46: LineSegment StartX=7.06218 StartY=-8.75 StartZ=0 EndX=7.06218 EndY=-5.25 EndZ=0
    g47: LineSegment StartX=7.06218 StartY=-5.25 StartZ=0 EndX=4.03109 EndY=-3.5 EndZ=0
    g48: Circle [constr] CenterX=4.03109 CenterY=-7 CenterZ=0 NormalX=0 NormalY=0 NormalZ=1 AngleXU=0 Radius=3.5
  constraints (117):
    c: Coincident(g0,g1)
    c: Coincident(g1,g2)
    c: Coincident(g2,g3)
    c: Coincident(g3,g4)
    c: Coincident(g4,g5)
    c: Coincident(g5,g0)
    c: Equal(g0, g1-g5) x5
    c: PointOnObject(g0,g6)
    c: PointOnObject(g1,g6)
    c: PointOnObject(g2,g6)
    c: PointOnObject(g3,g6)
    c: PointOnObject(g4,g6)
    c: PointOnObject(g5,g6)
    c: Coincident(g6,g-1)
    c: Diameter(g6) = 7
    c: PointOnObject(g0,g-2)
    c: Coincident(g7,g8)
    c: Coincident(g8,g9)
    c: Coincident(g9,g10)
    c: Coincident(g10,g11)
    c: Coincident(g11,g12)
    c: Coincident(g12,g7)
    c: Equal(g7, g8-g12) x5
    c: PointOnObject(g7,g13)
    c: PointOnObject(g8,g13)
    c: PointOnObject(g9,g13)
    c: PointOnObject(g10,g13)
    c: PointOnObject(g11,g13)
    c: PointOnObject(g12,g13)
    c: PointOnObject(g13,g-1)
    c: Diameter(g13) = 7
    c: Distance(g6,g13) = 8
    c: Horizontal(g0,g10)
    c: Coincident(g14,g15)
    c: Coincident(g15,g16)
    c: Coincident(g16,g17)
    c: Coincident(g17,g18)
    c: Coincident(g18,g19)
    c: Coincident(g19,g14)
    c: Equal(g14, g15-g19) x5
    c: PointOnObject(g14,g20)
    c: PointOnObject(g15,g20)
    c: PointOnObject(g16,g20)
    c: PointOnObject(g17,g20)
    c: PointOnObject(g18,g20)
    c: PointOnObject(g19,g20)
    c: Diameter(g20) = 7
    c: DistanceY(g-1,g20) = 7
    c: Vertical(g18)
    c: Distance(g17,g-2) = 1
    c: Coincident(g21,g22)
    c: Coincident(g22,g23)
    c: Coincident(g23,g24)
    c: Coincident(g24,g25)
    c: Coincident(g25,g26)
    c: Coincident(g26,g21)
    c: Equal(g21, g22-g26) x5
    c: PointOnObject(g21,g27)
    c: PointOnObject(g22,g27)
    c: PointOnObject(g23,g27)
    c: PointOnObject(g24,g27)
    c: PointOnObject(g25,g27)
    c: PointOnObject(g26,g27)
    c: Diameter(g27) = 7
    c: DistanceY(g-1,g27) = 7
    c: DistanceX(g21,g-1) = 1
    c: Vertical(g21)
    c: Coincident(g28,g29)
    c: Coincident(g29,g30)
    c: Coincident(g30,g31)
    c: Coincident(g31,g32)
    c: Coincident(g32,g33)
    c: Coincident(g33,g28)
    c: Equal(g28, g29-g33) x5
    c: PointOnObject(g28,g34)
    c: PointOnObject(g29,g34)
    c: PointOnObject(g30,g34)
    c: PointOnObject(g31,g34)
    c: PointOnObject(g32,g34)
    c: PointOnObject(g33,g34)
    c: PointOnObject(g34,g-1)
    c: Diameter(g34) = 7
    c: Vertical(g31)
    c: DistanceX(g34,g-1) = 8
    c: Coincident(g35,g36)
    c: Coincident(g36,g37)
    c: Coincident(g37,g38)
    c: Coincident(g38,g39)
    c: Coincident(g39,g40)
    c: Coincident(g40,g35)
    c: Equal(g35, g36-g40) x5
    c: PointOnObject(g35,g41)
    c: PointOnObject(g36,g41)
    c: PointOnObject(g37,g41)
    c: PointOnObject(g38,g41)
    c: PointOnObject(g39,g41)
    c: PointOnObject(g40,g41)
    c: Coincident(g42,g43)
    c: Coincident(g43,g44)
    c: Coincident(g44,g45)
    c: Coincident(g45,g46)
    c: Coincident(g46,g47)
    c: Coincident(g47,g42)
    c: Equal(g42, g43-g47) x5
    c: PointOnObject(g42,g48)
    c: PointOnObject(g43,g48)
    c: PointOnObject(g44,g48)
    c: PointOnObject(g45,g48)
    c: PointOnObject(g46,g48)
    c: PointOnObject(g47,g48)
    c: Equal(g41,g48)
    c: Diameter(g41) = 7
    c: Vertical(g39)
    c: Vertical(g43)
    c: Distance(g-2,g39) = 1
    c: Symmetric(g38,g43,g-2)
    c: Distance(g41,g-1) = 7
FEATURE [Part::Extrusion] Extrude720  label="hex322"
  Base = -> Sketch729
  Dir = (0,-1,2e-16)
  DirMode = 2
  FaceMakerClass = Part::FaceMakerBullseye
  FaceMakerMode = 3
  LengthFwd = 10
  LengthRev = 0
  Placement = pos=(-100,0,35) rot=(0,0,1;0rad)
  Solid = true
  Symmetric = false
FEATURE [Sketcher::SketchObject] Sketch730
  ArcFitTolerance = 1e-06
  FullyConstrained = true
  MakeInternals = false
  Placement = pos=(0,0,0) rot=(1,0,0;1.5708rad)
  sketch-geometry (49):
    g0: LineSegment StartX=1e-16 StartY=3.5 StartZ=0 EndX=-3.03109 EndY=1.75 EndZ=0
    g1: LineSegment StartX=-3.03109 StartY=1.75 StartZ=0 EndX=-3.03109 EndY=-1.75 EndZ=0
    g2: LineSegment StartX=-3.03109 StartY=-1.75 StartZ=0 EndX=-1e-16 EndY=-3.5 EndZ=0
    g3: LineSegment StartX=-1e-16 StartY=-3.5 StartZ=0 EndX=3.03109 EndY=-1.75 EndZ=0
    g4: LineSegment StartX=3.03109 StartY=-1.75 StartZ=0 EndX=3.03109 EndY=1.75 EndZ=0
    g5: LineSegment StartX=3.03109 StartY=1.75 StartZ=0 EndX=1e-16 EndY=3.5 EndZ=0
    g6: Circle [constr] CenterX=0 CenterY=0 CenterZ=0 NormalX=0 NormalY=0 NormalZ=1 AngleXU=0 Radius=3.5
    g7: LineSegment StartX=4.96892 StartY=-1.75002 StartZ=0 EndX=8.00002 EndY=-3.5 EndZ=0
    g8: LineSegment StartX=8.00002 StartY=-3.5 StartZ=0 EndX=11.0311 EndY=-1.74998 EndZ=0
    g9: LineSegment StartX=11.0311 StartY=-1.74998 StartZ=0 EndX=11.0311 EndY=1.75002 EndZ=0
    g10: LineSegment StartX=11.0311 StartY=1.75002 StartZ=0 EndX=7.99998 EndY=3.5 EndZ=0
    g11: LineSegment StartX=7.99998 StartY=3.5 StartZ=0 EndX=4.9689 EndY=1.74998 EndZ=0
    g12: LineSegment StartX=4.9689 StartY=1.74998 StartZ=0 EndX=4.96892 EndY=-1.75002 EndZ=0
    g13: Circle [constr] CenterX=8 CenterY=0 CenterZ=0 NormalX=0 NormalY=0 NormalZ=1 AngleXU=0 Radius=3.5
    g14: LineSegment StartX=4.03109 StartY=3.5 StartZ=0 EndX=7.06218 EndY=5.25 EndZ=0
    g15: LineSegment StartX=7.06218 StartY=5.25 StartZ=0 EndX=7.06218 EndY=8.75 EndZ=0
    g16: LineSegment StartX=7.06218 StartY=8.75 StartZ=0 EndX=4.03109 EndY=10.5 EndZ=0
    g17: LineSegment StartX=4.03109 StartY=10.5 StartZ=0 EndX=1 EndY=8.75 EndZ=0
    g18: LineSegment StartX=1 StartY=8.75 StartZ=0 EndX=1 EndY=5.25 EndZ=0
    g19: LineSegment StartX=1 StartY=5.25 StartZ=0 EndX=4.03109 EndY=3.5 EndZ=0
    g20: Circle [constr] CenterX=4.03109 CenterY=7 CenterZ=0 NormalX=0 NormalY=0 NormalZ=1 AngleXU=0 Radius=3.5
    g21: LineSegment StartX=-1 StartY=5.25 StartZ=0 EndX=-1 EndY=8.75 EndZ=0
    g22: LineSegment StartX=-1 StartY=8.75 StartZ=0 EndX=-4.03109 EndY=10.5 EndZ=0
    g23: LineSegment StartX=-4.03109 StartY=10.5 StartZ=0 EndX=-7.06218 EndY=8.75 EndZ=0
    g24: LineSegment StartX=-7.06218 StartY=8.75 StartZ=0 EndX=-7.06218 EndY=5.25 EndZ=0
    g25: LineSegment StartX=-7.06218 StartY=5.25 StartZ=0 EndX=-4.03109 EndY=3.5 EndZ=0
    g26: LineSegment StartX=-4.03109 StartY=3.5 StartZ=0 EndX=-1 EndY=5.25 EndZ=0
    g27: Circle [constr] CenterX=-4.03109 CenterY=7 CenterZ=0 NormalX=0 NormalY=0 NormalZ=1 AngleXU=0 Radius=3.5
    g28: LineSegment StartX=-4.96891 StartY=-1.75 StartZ=0 EndX=-4.96891 EndY=1.75 EndZ=0
    g29: LineSegment StartX=-4.96891 StartY=1.75 StartZ=0 EndX=-8 EndY=3.5 EndZ=0
    g30: LineSegment StartX=-8 StartY=3.5 StartZ=0 EndX=-11.0311 EndY=1.75 EndZ=0
    g31: LineSegment StartX=-11.0311 StartY=1.75 StartZ=0 EndX=-11.0311 EndY=-1.75 EndZ=0
    g32: LineSegment StartX=-11.0311 StartY=-1.75 StartZ=0 EndX=-8 EndY=-3.5 EndZ=0
    g33: LineSegment StartX=-8 StartY=-3.5 StartZ=0 EndX=-4.96891 EndY=-1.75 EndZ=0
    g34: Circle [constr] CenterX=-8 CenterY=0 CenterZ=0 NormalX=0 NormalY=0 NormalZ=1 AngleXU=0 Radius=3.5
    g35: LineSegment StartX=-4.03109 StartY=-3.5 StartZ=0 EndX=-7.06218 EndY=-5.25 EndZ=0
    g36: LineSegment StartX=-7.06218 StartY=-5.25 StartZ=0 EndX=-7.06218 EndY=-8.75 EndZ=0
    g37: LineSegment StartX=-7.06218 StartY=-8.75 StartZ=0 EndX=-4.03109 EndY=-10.5 EndZ=0
    g38: LineSegment StartX=-4.03109 StartY=-10.5 StartZ=0 EndX=-1 EndY=-8.75 EndZ=0
    g39: LineSegment StartX=-1 StartY=-8.75 StartZ=0 EndX=-1 EndY=-5.25 EndZ=0
    g40: LineSegment StartX=-1 StartY=-5.25 StartZ=0 EndX=-4.03109 EndY=-3.5 EndZ=0
    g41: Circle [constr] CenterX=-4.03109 CenterY=-7 CenterZ=0 NormalX=0 NormalY=0 NormalZ=1 AngleXU=0 Radius=3.5
    g42: LineSegment StartX=4.03109 StartY=-3.5 StartZ=0 EndX=1 EndY=-5.25 EndZ=0
    g43: LineSegment StartX=1 StartY=-5.25 StartZ=0 EndX=1 EndY=-8.75 EndZ=0
    g44: LineSegment StartX=1 StartY=-8.75 StartZ=0 EndX=4.03109 EndY=-10.5 EndZ=0
    g45: LineSegment StartX=4.03109 StartY=-10.5 StartZ=0 EndX=7.06218 EndY=-8.75 EndZ=0
    g46: LineSegment StartX=7.06218 StartY=-8.75 StartZ=0 EndX=7.06218 EndY=-5.25 EndZ=0
    g47: LineSegment StartX=7.06218 StartY=-5.25 StartZ=0 EndX=4.03109 EndY=-3.5 EndZ=0
    g48: Circle [constr] CenterX=4.03109 CenterY=-7 CenterZ=0 NormalX=0 NormalY=0 NormalZ=1 AngleXU=0 Radius=3.5
  constraints (117):
    c: Coincident(g0,g1)
    c: Coincident(g1,g2)
    c: Coincident(g2,g3)
    c: Coincident(g3,g4)
    c: Coincident(g4,g5)
    c: Coincident(g5,g0)
    c: Equal(g0, g1-g5) x5
    c: PointOnObject(g0,g6)
    c: PointOnObject(g1,g6)
    c: PointOnObject(g2,g6)
    c: PointOnObject(g3,g6)
    c: PointOnObject(g4,g6)
    c: PointOnObject(g5,g6)
    c: Coincident(g6,g-1)
    c: Diameter(g6) = 7
    c: PointOnObject(g0,g-2)
    c: Coincident(g7,g8)
    c: Coincident(g8,g9)
    c: Coincident(g9,g10)
    c: Coincident(g10,g11)
    c: Coincident(g11,g12)
    c: Coincident(g12,g7)
    c: Equal(g7, g8-g12) x5
    c: PointOnObject(g7,g13)
    c: PointOnObject(g8,g13)
    c: PointOnObject(g9,g13)
    c: PointOnObject(g10,g13)
    c: PointOnObject(g11,g13)
    c: PointOnObject(g12,g13)
    c: PointOnObject(g13,g-1)
    c: Diameter(g13) = 7
    c: Distance(g6,g13) = 8
    c: Horizontal(g0,g10)
    c: Coincident(g14,g15)
    c: Coincident(g15,g16)
    c: Coincident(g16,g17)
    c: Coincident(g17,g18)
    c: Coincident(g18,g19)
    c: Coincident(g19,g14)
    c: Equal(g14, g15-g19) x5
    c: PointOnObject(g14,g20)
    c: PointOnObject(g15,g20)
    c: PointOnObject(g16,g20)
    c: PointOnObject(g17,g20)
    c: PointOnObject(g18,g20)
    c: PointOnObject(g19,g20)
    c: Diameter(g20) = 7
    c: DistanceY(g-1,g20) = 7
    c: Vertical(g18)
    c: Distance(g17,g-2) = 1
    c: Coincident(g21,g22)
    c: Coincident(g22,g23)
    c: Coincident(g23,g24)
    c: Coincident(g24,g25)
    c: Coincident(g25,g26)
    c: Coincident(g26,g21)
    c: Equal(g21, g22-g26) x5
    c: PointOnObject(g21,g27)
    c: PointOnObject(g22,g27)
    c: PointOnObject(g23,g27)
    c: PointOnObject(g24,g27)
    c: PointOnObject(g25,g27)
    c: PointOnObject(g26,g27)
    c: Diameter(g27) = 7
    c: DistanceY(g-1,g27) = 7
    c: DistanceX(g21,g-1) = 1
    c: Vertical(g21)
    c: Coincident(g28,g29)
    c: Coincident(g29,g30)
    c: Coincident(g30,g31)
    c: Coincident(g31,g32)
    c: Coincident(g32,g33)
    c: Coincident(g33,g28)
    c: Equal(g28, g29-g33) x5
    c: PointOnObject(g28,g34)
    c: PointOnObject(g29,g34)
    c: PointOnObject(g30,g34)
    c: PointOnObject(g31,g34)
    c: PointOnObject(g32,g34)
    c: PointOnObject(g33,g34)
    c: PointOnObject(g34,g-1)
    c: Diameter(g34) = 7
    c: Vertical(g31)
    c: DistanceX(g34,g-1) = 8
    c: Coincident(g35,g36)
    c: Coincident(g36,g37)
    c: Coincident(g37,g38)
    c: Coincident(g38,g39)
    c: Coincident(g39,g40)
    c: Coincident(g40,g35)
    c: Equal(g35, g36-g40) x5
    c: PointOnObject(g35,g41)
    c: PointOnObject(g36,g41)
    c: PointOnObject(g37,g41)
    c: PointOnObject(g38,g41)
    c: PointOnObject(g39,g41)
    c: PointOnObject(g40,g41)
    c: Coincident(g42,g43)
    c: Coincident(g43,g44)
    c: Coincident(g44,g45)
    c: Coincident(g45,g46)
    c: Coincident(g46,g47)
    c: Coincident(g47,g42)
    c: Equal(g42, g43-g47) x5
    c: PointOnObject(g42,g48)
    c: PointOnObject(g43,g48)
    c: PointOnObject(g44,g48)
    c: PointOnObject(g45,g48)
    c: PointOnObject(g46,g48)
    c: PointOnObject(g47,g48)
    c: Equal(g41,g48)
    c: Diameter(g41) = 7
    c: Vertical(g39)
    c: Vertical(g43)
    c: Distance(g-2,g39) = 1
    c: Symmetric(g38,g43,g-2)
    c: Distance(g41,g-1) = 7
FEATURE [Part::Extrusion] Extrude721  label="hex323"
  Base = -> Sketch730
  Dir = (0,-1,2e-16)
  DirMode = 2
  FaceMakerClass = Part::FaceMakerBullseye
  FaceMakerMode = 3
  LengthFwd = 10
  LengthRev = 0
  Placement = pos=(56,0,84) rot=(0,0,1;0rad)
  Solid = true
  Symmetric = false
FEATURE [Sketcher::SketchObject] Sketch731
  ArcFitTolerance = 1e-06
  FullyConstrained = true
  MakeInternals = false
  Placement = pos=(0,0,0) rot=(1,0,0;1.5708rad)
  sketch-geometry (49):
    g0: LineSegment StartX=1e-16 StartY=3.5 StartZ=0 EndX=-3.03109 EndY=1.75 EndZ=0
    g1: LineSegment StartX=-3.03109 StartY=1.75 StartZ=0 EndX=-3.03109 EndY=-1.75 EndZ=0
    g2: LineSegment StartX=-3.03109 StartY=-1.75 StartZ=0 EndX=-1e-16 EndY=-3.5 EndZ=0
    g3: LineSegment StartX=-1e-16 StartY=-3.5 StartZ=0 EndX=3.03109 EndY=-1.75 EndZ=0
    g4: LineSegment StartX=3.03109 StartY=-1.75 StartZ=0 EndX=3.03109 EndY=1.75 EndZ=0
    g5: LineSegment StartX=3.03109 StartY=1.75 StartZ=0 EndX=1e-16 EndY=3.5 EndZ=0
    g6: Circle [constr] CenterX=0 CenterY=0 CenterZ=0 NormalX=0 NormalY=0 NormalZ=1 AngleXU=0 Radius=3.5
    g7: LineSegment StartX=4.96892 StartY=-1.75002 StartZ=0 EndX=8.00002 EndY=-3.5 EndZ=0
    g8: LineSegment StartX=8.00002 StartY=-3.5 StartZ=0 EndX=11.0311 EndY=-1.74998 EndZ=0
    g9: LineSegment StartX=11.0311 StartY=-1.74998 StartZ=0 EndX=11.0311 EndY=1.75002 EndZ=0
    g10: LineSegment StartX=11.0311 StartY=1.75002 StartZ=0 EndX=7.99998 EndY=3.5 EndZ=0
    g11: LineSegment StartX=7.99998 StartY=3.5 StartZ=0 EndX=4.9689 EndY=1.74998 EndZ=0
    g12: LineSegment StartX=4.9689 StartY=1.74998 StartZ=0 EndX=4.96892 EndY=-1.75002 EndZ=0
    g13: Circle [constr] CenterX=8 CenterY=0 CenterZ=0 NormalX=0 NormalY=0 NormalZ=1 AngleXU=0 Radius=3.5
    g14: LineSegment StartX=4.03109 StartY=3.5 StartZ=0 EndX=7.06218 EndY=5.25 EndZ=0
    g15: LineSegment StartX=7.06218 StartY=5.25 StartZ=0 EndX=7.06218 EndY=8.75 EndZ=0
    g16: LineSegment StartX=7.06218 StartY=8.75 StartZ=0 EndX=4.03109 EndY=10.5 EndZ=0
    g17: LineSegment StartX=4.03109 StartY=10.5 StartZ=0 EndX=1 EndY=8.75 EndZ=0
    g18: LineSegment StartX=1 StartY=8.75 StartZ=0 EndX=1 EndY=5.25 EndZ=0
    g19: LineSegment StartX=1 StartY=5.25 StartZ=0 EndX=4.03109 EndY=3.5 EndZ=0
    g20: Circle [constr] CenterX=4.03109 CenterY=7 CenterZ=0 NormalX=0 NormalY=0 NormalZ=1 AngleXU=0 Radius=3.5
    g21: LineSegment StartX=-1 StartY=5.25 StartZ=0 EndX=-1 EndY=8.75 EndZ=0
    g22: LineSegment StartX=-1 StartY=8.75 StartZ=0 EndX=-4.03109 EndY=10.5 EndZ=0
    g23: LineSegment StartX=-4.03109 StartY=10.5 StartZ=0 EndX=-7.06218 EndY=8.75 EndZ=0
    g24: LineSegment StartX=-7.06218 StartY=8.75 StartZ=0 EndX=-7.06218 EndY=5.25 EndZ=0
    g25: LineSegment StartX=-7.06218 StartY=5.25 StartZ=0 EndX=-4.03109 EndY=3.5 EndZ=0
    g26: LineSegment StartX=-4.03109 StartY=3.5 StartZ=0 EndX=-1 EndY=5.25 EndZ=0
    g27: Circle [constr] CenterX=-4.03109 CenterY=7 CenterZ=0 NormalX=0 NormalY=0 NormalZ=1 AngleXU=0 Radius=3.5
    g28: LineSegment StartX=-4.96891 StartY=-1.75 StartZ=0 EndX=-4.96891 EndY=1.75 EndZ=0
    g29: LineSegment StartX=-4.96891 StartY=1.75 StartZ=0 EndX=-8 EndY=3.5 EndZ=0
    g30: LineSegment StartX=-8 StartY=3.5 StartZ=0 EndX=-11.0311 EndY=1.75 EndZ=0
    g31: LineSegment StartX=-11.0311 StartY=1.75 StartZ=0 EndX=-11.0311 EndY=-1.75 EndZ=0
    g32: LineSegment StartX=-11.0311 StartY=-1.75 StartZ=0 EndX=-8 EndY=-3.5 EndZ=0
    g33: LineSegment StartX=-8 StartY=-3.5 StartZ=0 EndX=-4.96891 EndY=-1.75 EndZ=0
    g34: Circle [constr] CenterX=-8 CenterY=0 CenterZ=0 NormalX=0 NormalY=0 NormalZ=1 AngleXU=0 Radius=3.5
    g35: LineSegment StartX=-4.03109 StartY=-3.5 StartZ=0 EndX=-7.06218 EndY=-5.25 EndZ=0
    g36: LineSegment StartX=-7.06218 StartY=-5.25 StartZ=0 EndX=-7.06218 EndY=-8.75 EndZ=0
    g37: LineSegment StartX=-7.06218 StartY=-8.75 StartZ=0 EndX=-4.03109 EndY=-10.5 EndZ=0
    g38: LineSegment StartX=-4.03109 StartY=-10.5 StartZ=0 EndX=-1 EndY=-8.75 EndZ=0
    g39: LineSegment StartX=-1 StartY=-8.75 StartZ=0 EndX=-1 EndY=-5.25 EndZ=0
    g40: LineSegment StartX=-1 StartY=-5.25 StartZ=0 EndX=-4.03109 EndY=-3.5 EndZ=0
    g41: Circle [constr] CenterX=-4.03109 CenterY=-7 CenterZ=0 NormalX=0 NormalY=0 NormalZ=1 AngleXU=0 Radius=3.5
    g42: LineSegment StartX=4.03109 StartY=-3.5 StartZ=0 EndX=1 EndY=-5.25 EndZ=0
    g43: LineSegment StartX=1 StartY=-5.25 StartZ=0 EndX=1 EndY=-8.75 EndZ=0
    g44: LineSegment StartX=1 StartY=-8.75 StartZ=0 EndX=4.03109 EndY=-10.5 EndZ=0
    g45: LineSegment StartX=4.03109 StartY=-10.5 StartZ=0 EndX=7.06218 EndY=-8.75 EndZ=0
    g46: LineSegment StartX=7.06218 StartY=-8.75 StartZ=0 EndX=7.06218 EndY=-5.25 EndZ=0
    g47: LineSegment StartX=7.06218 StartY=-5.25 StartZ=0 EndX=4.03109 EndY=-3.5 EndZ=0
    g48: Circle [constr] CenterX=4.03109 CenterY=-7 CenterZ=0 NormalX=0 NormalY=0 NormalZ=1 AngleXU=0 Radius=3.5
  constraints (117):
    c: Coincident(g0,g1)
    c: Coincident(g1,g2)
    c: Coincident(g2,g3)
    c: Coincident(g3,g4)
    c: Coincident(g4,g5)
    c: Coincident(g5,g0)
    c: Equal(g0, g1-g5) x5
    c: PointOnObject(g0,g6)
    c: PointOnObject(g1,g6)
    c: PointOnObject(g2,g6)
    c: PointOnObject(g3,g6)
    c: PointOnObject(g4,g6)
    c: PointOnObject(g5,g6)
    c: Coincident(g6,g-1)
    c: Diameter(g6) = 7
    c: PointOnObject(g0,g-2)
    c: Coincident(g7,g8)
    c: Coincident(g8,g9)
    c: Coincident(g9,g10)
    c: Coincident(g10,g11)
    c: Coincident(g11,g12)
    c: Coincident(g12,g7)
    c: Equal(g7, g8-g12) x5
    c: PointOnObject(g7,g13)
    c: PointOnObject(g8,g13)
    c: PointOnObject(g9,g13)
    c: PointOnObject(g10,g13)
    c: PointOnObject(g11,g13)
    c: PointOnObject(g12,g13)
    c: PointOnObject(g13,g-1)
    c: Diameter(g13) = 7
    c: Distance(g6,g13) = 8
    c: Horizontal(g0,g10)
    c: Coincident(g14,g15)
    c: Coincident(g15,g16)
    c: Coincident(g16,g17)
    c: Coincident(g17,g18)
    c: Coincident(g18,g19)
    c: Coincident(g19,g14)
    c: Equal(g14, g15-g19) x5
    c: PointOnObject(g14,g20)
    c: PointOnObject(g15,g20)
    c: PointOnObject(g16,g20)
    c: PointOnObject(g17,g20)
    c: PointOnObject(g18,g20)
    c: PointOnObject(g19,g20)
    c: Diameter(g20) = 7
    c: DistanceY(g-1,g20) = 7
    c: Vertical(g18)
    c: Distance(g17,g-2) = 1
    c: Coincident(g21,g22)
    c: Coincident(g22,g23)
    c: Coincident(g23,g24)
    c: Coincident(g24,g25)
    c: Coincident(g25,g26)
    c: Coincident(g26,g21)
    c: Equal(g21, g22-g26) x5
    c: PointOnObject(g21,g27)
    c: PointOnObject(g22,g27)
    c: PointOnObject(g23,g27)
    c: PointOnObject(g24,g27)
    c: PointOnObject(g25,g27)
    c: PointOnObject(g26,g27)
    c: Diameter(g27) = 7
    c: DistanceY(g-1,g27) = 7
    c: DistanceX(g21,g-1) = 1
    c: Vertical(g21)
    c: Coincident(g28,g29)
    c: Coincident(g29,g30)
    c: Coincident(g30,g31)
    c: Coincident(g31,g32)
    c: Coincident(g32,g33)
    c: Coincident(g33,g28)
    c: Equal(g28, g29-g33) x5
    c: PointOnObject(g28,g34)
    c: PointOnObject(g29,g34)
    c: PointOnObject(g30,g34)
    c: PointOnObject(g31,g34)
    c: PointOnObject(g32,g34)
    c: PointOnObject(g33,g34)
    c: PointOnObject(g34,g-1)
    c: Diameter(g34) = 7
    c: Vertical(g31)
    c: DistanceX(g34,g-1) = 8
    c: Coincident(g35,g36)
    c: Coincident(g36,g37)
    c: Coincident(g37,g38)
    c: Coincident(g38,g39)
    c: Coincident(g39,g40)
    c: Coincident(g40,g35)
    c: Equal(g35, g36-g40) x5
    c: PointOnObject(g35,g41)
    c: PointOnObject(g36,g41)
    c: PointOnObject(g37,g41)
    c: PointOnObject(g38,g41)
    c: PointOnObject(g39,g41)
    c: PointOnObject(g40,g41)
    c: Coincident(g42,g43)
    c: Coincident(g43,g44)
    c: Coincident(g44,g45)
    c: Coincident(g45,g46)
    c: Coincident(g46,g47)
    c: Coincident(g47,g42)
    c: Equal(g42, g43-g47) x5
    c: PointOnObject(g42,g48)
    c: PointOnObject(g43,g48)
    c: PointOnObject(g44,g48)
    c: PointOnObject(g45,g48)
    c: PointOnObject(g46,g48)
    c: PointOnObject(g47,g48)
    c: Equal(g41,g48)
    c: Diameter(g41) = 7
    c: Vertical(g39)
    c: Vertical(g43)
    c: Distance(g-2,g39) = 1
    c: Symmetric(g38,g43,g-2)
    c: Distance(g41,g-1) = 7
FEATURE [Part::Extrusion] Extrude722  label="hex324"
  Base = -> Sketch731
  Dir = (0,-1,2e-16)
  DirMode = 2
  FaceMakerClass = Part::FaceMakerBullseye
  FaceMakerMode = 3
  LengthFwd = 10
  LengthRev = 0
  Placement = pos=(40,0,98) rot=(0,0,1;0rad)
  Solid = true
  Symmetric = false
FEATURE [Sketcher::SketchObject] Sketch732
  ArcFitTolerance = 1e-06
  FullyConstrained = true
  MakeInternals = false
  Placement = pos=(0,0,0) rot=(1,0,0;1.5708rad)
  sketch-geometry (49):
    g0: LineSegment StartX=1e-16 StartY=3.5 StartZ=0 EndX=-3.03109 EndY=1.75 EndZ=0
    g1: LineSegment StartX=-3.03109 StartY=1.75 StartZ=0 EndX=-3.03109 EndY=-1.75 EndZ=0
    g2: LineSegment StartX=-3.03109 StartY=-1.75 StartZ=0 EndX=-1e-16 EndY=-3.5 EndZ=0
    g3: LineSegment StartX=-1e-16 StartY=-3.5 StartZ=0 EndX=3.03109 EndY=-1.75 EndZ=0
    g4: LineSegment StartX=3.03109 StartY=-1.75 StartZ=0 EndX=3.03109 EndY=1.75 EndZ=0
    g5: LineSegment StartX=3.03109 StartY=1.75 StartZ=0 EndX=1e-16 EndY=3.5 EndZ=0
    g6: Circle [constr] CenterX=0 CenterY=0 CenterZ=0 NormalX=0 NormalY=0 NormalZ=1 AngleXU=0 Radius=3.5
    g7: LineSegment StartX=4.96892 StartY=-1.75002 StartZ=0 EndX=8.00002 EndY=-3.5 EndZ=0
    g8: LineSegment StartX=8.00002 StartY=-3.5 StartZ=0 EndX=11.0311 EndY=-1.74998 EndZ=0
    g9: LineSegment StartX=11.0311 StartY=-1.74998 StartZ=0 EndX=11.0311 EndY=1.75002 EndZ=0
    g10: LineSegment StartX=11.0311 StartY=1.75002 StartZ=0 EndX=7.99998 EndY=3.5 EndZ=0
    g11: LineSegment StartX=7.99998 StartY=3.5 StartZ=0 EndX=4.9689 EndY=1.74998 EndZ=0
    g12: LineSegment StartX=4.9689 StartY=1.74998 StartZ=0 EndX=4.96892 EndY=-1.75002 EndZ=0
    g13: Circle [constr] CenterX=8 CenterY=0 CenterZ=0 NormalX=0 NormalY=0 NormalZ=1 AngleXU=0 Radius=3.5
    g14: LineSegment StartX=4.03109 StartY=3.5 StartZ=0 EndX=7.06218 EndY=5.25 EndZ=0
    g15: LineSegment StartX=7.06218 StartY=5.25 StartZ=0 EndX=7.06218 EndY=8.75 EndZ=0
    g16: LineSegment StartX=7.06218 StartY=8.75 StartZ=0 EndX=4.03109 EndY=10.5 EndZ=0
    g17: LineSegment StartX=4.03109 StartY=10.5 StartZ=0 EndX=1 EndY=8.75 EndZ=0
    g18: LineSegment StartX=1 StartY=8.75 StartZ=0 EndX=1 EndY=5.25 EndZ=0
    g19: LineSegment StartX=1 StartY=5.25 StartZ=0 EndX=4.03109 EndY=3.5 EndZ=0
    g20: Circle [constr] CenterX=4.03109 CenterY=7 CenterZ=0 NormalX=0 NormalY=0 NormalZ=1 AngleXU=0 Radius=3.5
    g21: LineSegment StartX=-1 StartY=5.25 StartZ=0 EndX=-1 EndY=8.75 EndZ=0
    g22: LineSegment StartX=-1 StartY=8.75 StartZ=0 EndX=-4.03109 EndY=10.5 EndZ=0
    g23: LineSegment StartX=-4.03109 StartY=10.5 StartZ=0 EndX=-7.06218 EndY=8.75 EndZ=0
    g24: LineSegment StartX=-7.06218 StartY=8.75 StartZ=0 EndX=-7.06218 EndY=5.25 EndZ=0
    g25: LineSegment StartX=-7.06218 StartY=5.25 StartZ=0 EndX=-4.03109 EndY=3.5 EndZ=0
    g26: LineSegment StartX=-4.03109 StartY=3.5 StartZ=0 EndX=-1 EndY=5.25 EndZ=0
    g27: Circle [constr] CenterX=-4.03109 CenterY=7 CenterZ=0 NormalX=0 NormalY=0 NormalZ=1 AngleXU=0 Radius=3.5
    g28: LineSegment StartX=-4.96891 StartY=-1.75 StartZ=0 EndX=-4.96891 EndY=1.75 EndZ=0
    g29: LineSegment StartX=-4.96891 StartY=1.75 StartZ=0 EndX=-8 EndY=3.5 EndZ=0
    g30: LineSegment StartX=-8 StartY=3.5 StartZ=0 EndX=-11.0311 EndY=1.75 EndZ=0
    g31: LineSegment StartX=-11.0311 StartY=1.75 StartZ=0 EndX=-11.0311 EndY=-1.75 EndZ=0
    g32: LineSegment StartX=-11.0311 StartY=-1.75 StartZ=0 EndX=-8 EndY=-3.5 EndZ=0
    g33: LineSegment StartX=-8 StartY=-3.5 StartZ=0 EndX=-4.96891 EndY=-1.75 EndZ=0
    g34: Circle [constr] CenterX=-8 CenterY=0 CenterZ=0 NormalX=0 NormalY=0 NormalZ=1 AngleXU=0 Radius=3.5
    g35: LineSegment StartX=-4.03109 StartY=-3.5 StartZ=0 EndX=-7.06218 EndY=-5.25 EndZ=0
    g36: LineSegment StartX=-7.06218 StartY=-5.25 StartZ=0 EndX=-7.06218 EndY=-8.75 EndZ=0
    g37: LineSegment StartX=-7.06218 StartY=-8.75 StartZ=0 EndX=-4.03109 EndY=-10.5 EndZ=0
    g38: LineSegment StartX=-4.03109 StartY=-10.5 StartZ=0 EndX=-1 EndY=-8.75 EndZ=0
    g39: LineSegment StartX=-1 StartY=-8.75 StartZ=0 EndX=-1 EndY=-5.25 EndZ=0
    g40: LineSegment StartX=-1 StartY=-5.25 StartZ=0 EndX=-4.03109 EndY=-3.5 EndZ=0
    g41: Circle [constr] CenterX=-4.03109 CenterY=-7 CenterZ=0 NormalX=0 NormalY=0 NormalZ=1 AngleXU=0 Radius=3.5
    g42: LineSegment StartX=4.03109 StartY=-3.5 StartZ=0 EndX=1 EndY=-5.25 EndZ=0
    g43: LineSegment StartX=1 StartY=-5.25 StartZ=0 EndX=1 EndY=-8.75 EndZ=0
    g44: LineSegment StartX=1 StartY=-8.75 StartZ=0 EndX=4.03109 EndY=-10.5 EndZ=0
    g45: LineSegment StartX=4.03109 StartY=-10.5 StartZ=0 EndX=7.06218 EndY=-8.75 EndZ=0
    g46: LineSegment StartX=7.06218 StartY=-8.75 StartZ=0 EndX=7.06218 EndY=-5.25 EndZ=0
    g47: LineSegment StartX=7.06218 StartY=-5.25 StartZ=0 EndX=4.03109 EndY=-3.5 EndZ=0
    g48: Circle [constr] CenterX=4.03109 CenterY=-7 CenterZ=0 NormalX=0 NormalY=0 NormalZ=1 AngleXU=0 Radius=3.5
  constraints (117):
    c: Coincident(g0,g1)
    c: Coincident(g1,g2)
    c: Coincident(g2,g3)
    c: Coincident(g3,g4)
    c: Coincident(g4,g5)
    c: Coincident(g5,g0)
    c: Equal(g0, g1-g5) x5
    c: PointOnObject(g0,g6)
    c: PointOnObject(g1,g6)
    c: PointOnObject(g2,g6)
    c: PointOnObject(g3,g6)
    c: PointOnObject(g4,g6)
    c: PointOnObject(g5,g6)
    c: Coincident(g6,g-1)
    c: Diameter(g6) = 7
    c: PointOnObject(g0,g-2)
    c: Coincident(g7,g8)
    c: Coincident(g8,g9)
    c: Coincident(g9,g10)
    c: Coincident(g10,g11)
    c: Coincident(g11,g12)
    c: Coincident(g12,g7)
    c: Equal(g7, g8-g12) x5
    c: PointOnObject(g7,g13)
    c: PointOnObject(g8,g13)
    c: PointOnObject(g9,g13)
    c: PointOnObject(g10,g13)
    c: PointOnObject(g11,g13)
    c: PointOnObject(g12,g13)
    c: PointOnObject(g13,g-1)
    c: Diameter(g13) = 7
    c: Distance(g6,g13) = 8
    c: Horizontal(g0,g10)
    c: Coincident(g14,g15)
    c: Coincident(g15,g16)
    c: Coincident(g16,g17)
    c: Coincident(g17,g18)
    c: Coincident(g18,g19)
    c: Coincident(g19,g14)
    c: Equal(g14, g15-g19) x5
    c: PointOnObject(g14,g20)
    c: PointOnObject(g15,g20)
    c: PointOnObject(g16,g20)
    c: PointOnObject(g17,g20)
    c: PointOnObject(g18,g20)
    c: PointOnObject(g19,g20)
    c: Diameter(g20) = 7
    c: DistanceY(g-1,g20) = 7
    c: Vertical(g18)
    c: Distance(g17,g-2) = 1
    c: Coincident(g21,g22)
    c: Coincident(g22,g23)
    c: Coincident(g23,g24)
    c: Coincident(g24,g25)
    c: Coincident(g25,g26)
    c: Coincident(g26,g21)
    c: Equal(g21, g22-g26) x5
    c: PointOnObject(g21,g27)
    c: PointOnObject(g22,g27)
    c: PointOnObject(g23,g27)
    c: PointOnObject(g24,g27)
    c: PointOnObject(g25,g27)
    c: PointOnObject(g26,g27)
    c: Diameter(g27) = 7
    c: DistanceY(g-1,g27) = 7
    c: DistanceX(g21,g-1) = 1
    c: Vertical(g21)
    c: Coincident(g28,g29)
    c: Coincident(g29,g30)
    c: Coincident(g30,g31)
    c: Coincident(g31,g32)
    c: Coincident(g32,g33)
    c: Coincident(g33,g28)
    c: Equal(g28, g29-g33) x5
    c: PointOnObject(g28,g34)
    c: PointOnObject(g29,g34)
    c: PointOnObject(g30,g34)
    c: PointOnObject(g31,g34)
    c: PointOnObject(g32,g34)
    c: PointOnObject(g33,g34)
    c: PointOnObject(g34,g-1)
    c: Diameter(g34) = 7
    c: Vertical(g31)
    c: DistanceX(g34,g-1) = 8
    c: Coincident(g35,g36)
    c: Coincident(g36,g37)
    c: Coincident(g37,g38)
    c: Coincident(g38,g39)
    c: Coincident(g39,g40)
    c: Coincident(g40,g35)
    c: Equal(g35, g36-g40) x5
    c: PointOnObject(g35,g41)
    c: PointOnObject(g36,g41)
    c: PointOnObject(g37,g41)
    c: PointOnObject(g38,g41)
    c: PointOnObject(g39,g41)
    c: PointOnObject(g40,g41)
    c: Coincident(g42,g43)
    c: Coincident(g43,g44)
    c: Coincident(g44,g45)
    c: Coincident(g45,g46)
    c: Coincident(g46,g47)
    c: Coincident(g47,g42)
    c: Equal(g42, g43-g47) x5
    c: PointOnObject(g42,g48)
    c: PointOnObject(g43,g48)
    c: PointOnObject(g44,g48)
    c: PointOnObject(g45,g48)
    c: PointOnObject(g46,g48)
    c: PointOnObject(g47,g48)
    c: Equal(g41,g48)
    c: Diameter(g41) = 7
    c: Vertical(g39)
    c: Vertical(g43)
    c: Distance(g-2,g39) = 1
    c: Symmetric(g38,g43,g-2)
    c: Distance(g41,g-1) = 7
FEATURE [Part::Extrusion] Extrude723  label="hex325"
  Base = -> Sketch732
  Dir = (0,-1,2e-16)
  DirMode = 2
  FaceMakerClass = Part::FaceMakerBullseye
  FaceMakerMode = 3
  LengthFwd = 10
  LengthRev = 0
  Placement = pos=(20,0,105) rot=(0,0,1;0rad)
  Solid = true
  Symmetric = false
FEATURE [Sketcher::SketchObject] Sketch733
  ArcFitTolerance = 1e-06
  FullyConstrained = true
  MakeInternals = false
  Placement = pos=(0,0,0) rot=(1,0,0;1.5708rad)
  sketch-geometry (49):
    g0: LineSegment StartX=1e-16 StartY=3.5 StartZ=0 EndX=-3.03109 EndY=1.75 EndZ=0
    g1: LineSegment StartX=-3.03109 StartY=1.75 StartZ=0 EndX=-3.03109 EndY=-1.75 EndZ=0
    g2: LineSegment StartX=-3.03109 StartY=-1.75 StartZ=0 EndX=-1e-16 EndY=-3.5 EndZ=0
    g3: LineSegment StartX=-1e-16 StartY=-3.5 StartZ=0 EndX=3.03109 EndY=-1.75 EndZ=0
    g4: LineSegment StartX=3.03109 StartY=-1.75 StartZ=0 EndX=3.03109 EndY=1.75 EndZ=0
    g5: LineSegment StartX=3.03109 StartY=1.75 StartZ=0 EndX=1e-16 EndY=3.5 EndZ=0
    g6: Circle [constr] CenterX=0 CenterY=0 CenterZ=0 NormalX=0 NormalY=0 NormalZ=1 AngleXU=0 Radius=3.5
    g7: LineSegment StartX=4.96892 StartY=-1.75002 StartZ=0 EndX=8.00002 EndY=-3.5 EndZ=0
    g8: LineSegment StartX=8.00002 StartY=-3.5 StartZ=0 EndX=11.0311 EndY=-1.74998 EndZ=0
    g9: LineSegment StartX=11.0311 StartY=-1.74998 StartZ=0 EndX=11.0311 EndY=1.75002 EndZ=0
    g10: LineSegment StartX=11.0311 StartY=1.75002 StartZ=0 EndX=7.99998 EndY=3.5 EndZ=0
    g11: LineSegment StartX=7.99998 StartY=3.5 StartZ=0 EndX=4.9689 EndY=1.74998 EndZ=0
    g12: LineSegment StartX=4.9689 StartY=1.74998 StartZ=0 EndX=4.96892 EndY=-1.75002 EndZ=0
    g13: Circle [constr] CenterX=8 CenterY=0 CenterZ=0 NormalX=0 NormalY=0 NormalZ=1 AngleXU=0 Radius=3.5
    g14: LineSegment StartX=4.03109 StartY=3.5 StartZ=0 EndX=7.06218 EndY=5.25 EndZ=0
    g15: LineSegment StartX=7.06218 StartY=5.25 StartZ=0 EndX=7.06218 EndY=8.75 EndZ=0
    g16: LineSegment StartX=7.06218 StartY=8.75 StartZ=0 EndX=4.03109 EndY=10.5 EndZ=0
    g17: LineSegment StartX=4.03109 StartY=10.5 StartZ=0 EndX=1 EndY=8.75 EndZ=0
    g18: LineSegment StartX=1 StartY=8.75 StartZ=0 EndX=1 EndY=5.25 EndZ=0
    g19: LineSegment StartX=1 StartY=5.25 StartZ=0 EndX=4.03109 EndY=3.5 EndZ=0
    g20: Circle [constr] CenterX=4.03109 CenterY=7 CenterZ=0 NormalX=0 NormalY=0 NormalZ=1 AngleXU=0 Radius=3.5
    g21: LineSegment StartX=-1 StartY=5.25 StartZ=0 EndX=-1 EndY=8.75 EndZ=0
    g22: LineSegment StartX=-1 StartY=8.75 StartZ=0 EndX=-4.03109 EndY=10.5 EndZ=0
    g23: LineSegment StartX=-4.03109 StartY=10.5 StartZ=0 EndX=-7.06218 EndY=8.75 EndZ=0
    g24: LineSegment StartX=-7.06218 StartY=8.75 StartZ=0 EndX=-7.06218 EndY=5.25 EndZ=0
    g25: LineSegment StartX=-7.06218 StartY=5.25 StartZ=0 EndX=-4.03109 EndY=3.5 EndZ=0
    g26: LineSegment StartX=-4.03109 StartY=3.5 StartZ=0 EndX=-1 EndY=5.25 EndZ=0
    g27: Circle [constr] CenterX=-4.03109 CenterY=7 CenterZ=0 NormalX=0 NormalY=0 NormalZ=1 AngleXU=0 Radius=3.5
    g28: LineSegment StartX=-4.96891 StartY=-1.75 StartZ=0 EndX=-4.96891 EndY=1.75 EndZ=0
    g29: LineSegment StartX=-4.96891 StartY=1.75 StartZ=0 EndX=-8 EndY=3.5 EndZ=0
    g30: LineSegment StartX=-8 StartY=3.5 StartZ=0 EndX=-11.0311 EndY=1.75 EndZ=0
    g31: LineSegment StartX=-11.0311 StartY=1.75 StartZ=0 EndX=-11.0311 EndY=-1.75 EndZ=0
    g32: LineSegment StartX=-11.0311 StartY=-1.75 StartZ=0 EndX=-8 EndY=-3.5 EndZ=0
    g33: LineSegment StartX=-8 StartY=-3.5 StartZ=0 EndX=-4.96891 EndY=-1.75 EndZ=0
    g34: Circle [constr] CenterX=-8 CenterY=0 CenterZ=0 NormalX=0 NormalY=0 NormalZ=1 AngleXU=0 Radius=3.5
    g35: LineSegment StartX=-4.03109 StartY=-3.5 StartZ=0 EndX=-7.06218 EndY=-5.25 EndZ=0
    g36: LineSegment StartX=-7.06218 StartY=-5.25 StartZ=0 EndX=-7.06218 EndY=-8.75 EndZ=0
    g37: LineSegment StartX=-7.06218 StartY=-8.75 StartZ=0 EndX=-4.03109 EndY=-10.5 EndZ=0
    g38: LineSegment StartX=-4.03109 StartY=-10.5 StartZ=0 EndX=-1 EndY=-8.75 EndZ=0
    g39: LineSegment StartX=-1 StartY=-8.75 StartZ=0 EndX=-1 EndY=-5.25 EndZ=0
    g40: LineSegment StartX=-1 StartY=-5.25 StartZ=0 EndX=-4.03109 EndY=-3.5 EndZ=0
    g41: Circle [constr] CenterX=-4.03109 CenterY=-7 CenterZ=0 NormalX=0 NormalY=0 NormalZ=1 AngleXU=0 Radius=3.5
    g42: LineSegment StartX=4.03109 StartY=-3.5 StartZ=0 EndX=1 EndY=-5.25 EndZ=0
    g43: LineSegment StartX=1 StartY=-5.25 StartZ=0 EndX=1 EndY=-8.75 EndZ=0
    g44: LineSegment StartX=1 StartY=-8.75 StartZ=0 EndX=4.03109 EndY=-10.5 EndZ=0
    g45: LineSegment StartX=4.03109 StartY=-10.5 StartZ=0 EndX=7.06218 EndY=-8.75 EndZ=0
    g46: LineSegment StartX=7.06218 StartY=-8.75 StartZ=0 EndX=7.06218 EndY=-5.25 EndZ=0
    g47: LineSegment StartX=7.06218 StartY=-5.25 StartZ=0 EndX=4.03109 EndY=-3.5 EndZ=0
    g48: Circle [constr] CenterX=4.03109 CenterY=-7 CenterZ=0 NormalX=0 NormalY=0 NormalZ=1 AngleXU=0 Radius=3.5
  constraints (117):
    c: Coincident(g0,g1)
    c: Coincident(g1,g2)
    c: Coincident(g2,g3)
    c: Coincident(g3,g4)
    c: Coincident(g4,g5)
    c: Coincident(g5,g0)
    c: Equal(g0, g1-g5) x5
    c: PointOnObject(g0,g6)
    c: PointOnObject(g1,g6)
    c: PointOnObject(g2,g6)
    c: PointOnObject(g3,g6)
    c: PointOnObject(g4,g6)
    c: PointOnObject(g5,g6)
    c: Coincident(g6,g-1)
    c: Diameter(g6) = 7
    c: PointOnObject(g0,g-2)
    c: Coincident(g7,g8)
    c: Coincident(g8,g9)
    c: Coincident(g9,g10)
    c: Coincident(g10,g11)
    c: Coincident(g11,g12)
    c: Coincident(g12,g7)
    c: Equal(g7, g8-g12) x5
    c: PointOnObject(g7,g13)
    c: PointOnObject(g8,g13)
    c: PointOnObject(g9,g13)
    c: PointOnObject(g10,g13)
    c: PointOnObject(g11,g13)
    c: PointOnObject(g12,g13)
    c: PointOnObject(g13,g-1)
    c: Diameter(g13) = 7
    c: Distance(g6,g13) = 8
    c: Horizontal(g0,g10)
    c: Coincident(g14,g15)
    c: Coincident(g15,g16)
    c: Coincident(g16,g17)
    c: Coincident(g17,g18)
    c: Coincident(g18,g19)
    c: Coincident(g19,g14)
    c: Equal(g14, g15-g19) x5
    c: PointOnObject(g14,g20)
    c: PointOnObject(g15,g20)
    c: PointOnObject(g16,g20)
    c: PointOnObject(g17,g20)
    c: PointOnObject(g18,g20)
    c: PointOnObject(g19,g20)
    c: Diameter(g20) = 7
    c: DistanceY(g-1,g20) = 7
    c: Vertical(g18)
    c: Distance(g17,g-2) = 1
    c: Coincident(g21,g22)
    c: Coincident(g22,g23)
    c: Coincident(g23,g24)
    c: Coincident(g24,g25)
    c: Coincident(g25,g26)
    c: Coincident(g26,g21)
    c: Equal(g21, g22-g26) x5
    c: PointOnObject(g21,g27)
    c: PointOnObject(g22,g27)
    c: PointOnObject(g23,g27)
    c: PointOnObject(g24,g27)
    c: PointOnObject(g25,g27)
    c: PointOnObject(g26,g27)
    c: Diameter(g27) = 7
    c: DistanceY(g-1,g27) = 7
    c: DistanceX(g21,g-1) = 1
    c: Vertical(g21)
    c: Coincident(g28,g29)
    c: Coincident(g29,g30)
    c: Coincident(g30,g31)
    c: Coincident(g31,g32)
    c: Coincident(g32,g33)
    c: Coincident(g33,g28)
    c: Equal(g28, g29-g33) x5
    c: PointOnObject(g28,g34)
    c: PointOnObject(g29,g34)
    c: PointOnObject(g30,g34)
    c: PointOnObject(g31,g34)
    c: PointOnObject(g32,g34)
    c: PointOnObject(g33,g34)
    c: PointOnObject(g34,g-1)
    c: Diameter(g34) = 7
    c: Vertical(g31)
    c: DistanceX(g34,g-1) = 8
    c: Coincident(g35,g36)
    c: Coincident(g36,g37)
    c: Coincident(g37,g38)
    c: Coincident(g38,g39)
    c: Coincident(g39,g40)
    c: Coincident(g40,g35)
    c: Equal(g35, g36-g40) x5
    c: PointOnObject(g35,g41)
    c: PointOnObject(g36,g41)
    c: PointOnObject(g37,g41)
    c: PointOnObject(g38,g41)
    c: PointOnObject(g39,g41)
    c: PointOnObject(g40,g41)
    c: Coincident(g42,g43)
    c: Coincident(g43,g44)
    c: Coincident(g44,g45)
    c: Coincident(g45,g46)
    c: Coincident(g46,g47)
    c: Coincident(g47,g42)
    c: Equal(g42, g43-g47) x5
    c: PointOnObject(g42,g48)
    c: PointOnObject(g43,g48)
    c: PointOnObject(g44,g48)
    c: PointOnObject(g45,g48)
    c: PointOnObject(g46,g48)
    c: PointOnObject(g47,g48)
    c: Equal(g41,g48)
    c: Diameter(g41) = 7
    c: Vertical(g39)
    c: Vertical(g43)
    c: Distance(g-2,g39) = 1
    c: Symmetric(g38,g43,g-2)
    c: Distance(g41,g-1) = 7
FEATURE [Part::Extrusion] Extrude724  label="hex326"
  Base = -> Sketch733
  Dir = (0,-1,2e-16)
  DirMode = 2
  FaceMakerClass = Part::FaceMakerBullseye
  FaceMakerMode = 3
  LengthFwd = 10
  LengthRev = 0
  Placement = pos=(4,0,119) rot=(0,0,1;0rad)
  Solid = true
  Symmetric = false
FEATURE [Sketcher::SketchObject] Sketch734
  ArcFitTolerance = 1e-06
  FullyConstrained = true
  MakeInternals = false
  Placement = pos=(0,0,0) rot=(1,0,0;1.5708rad)
  sketch-geometry (49):
    g0: LineSegment StartX=1e-16 StartY=3.5 StartZ=0 EndX=-3.03109 EndY=1.75 EndZ=0
    g1: LineSegment StartX=-3.03109 StartY=1.75 StartZ=0 EndX=-3.03109 EndY=-1.75 EndZ=0
    g2: LineSegment StartX=-3.03109 StartY=-1.75 StartZ=0 EndX=-1e-16 EndY=-3.5 EndZ=0
    g3: LineSegment StartX=-1e-16 StartY=-3.5 StartZ=0 EndX=3.03109 EndY=-1.75 EndZ=0
    g4: LineSegment StartX=3.03109 StartY=-1.75 StartZ=0 EndX=3.03109 EndY=1.75 EndZ=0
    g5: LineSegment StartX=3.03109 StartY=1.75 StartZ=0 EndX=1e-16 EndY=3.5 EndZ=0
    g6: Circle [constr] CenterX=0 CenterY=0 CenterZ=0 NormalX=0 NormalY=0 NormalZ=1 AngleXU=0 Radius=3.5
    g7: LineSegment StartX=4.96892 StartY=-1.75002 StartZ=0 EndX=8.00002 EndY=-3.5 EndZ=0
    g8: LineSegment StartX=8.00002 StartY=-3.5 StartZ=0 EndX=11.0311 EndY=-1.74998 EndZ=0
    g9: LineSegment StartX=11.0311 StartY=-1.74998 StartZ=0 EndX=11.0311 EndY=1.75002 EndZ=0
    g10: LineSegment StartX=11.0311 StartY=1.75002 StartZ=0 EndX=7.99998 EndY=3.5 EndZ=0
    g11: LineSegment StartX=7.99998 StartY=3.5 StartZ=0 EndX=4.9689 EndY=1.74998 EndZ=0
    g12: LineSegment StartX=4.9689 StartY=1.74998 StartZ=0 EndX=4.96892 EndY=-1.75002 EndZ=0
    g13: Circle [constr] CenterX=8 CenterY=0 CenterZ=0 NormalX=0 NormalY=0 NormalZ=1 AngleXU=0 Radius=3.5
    g14: LineSegment StartX=4.03109 StartY=3.5 StartZ=0 EndX=7.06218 EndY=5.25 EndZ=0
    g15: LineSegment StartX=7.06218 StartY=5.25 StartZ=0 EndX=7.06218 EndY=8.75 EndZ=0
    g16: LineSegment StartX=7.06218 StartY=8.75 StartZ=0 EndX=4.03109 EndY=10.5 EndZ=0
    g17: LineSegment StartX=4.03109 StartY=10.5 StartZ=0 EndX=1 EndY=8.75 EndZ=0
    g18: LineSegment StartX=1 StartY=8.75 StartZ=0 EndX=1 EndY=5.25 EndZ=0
    g19: LineSegment StartX=1 StartY=5.25 StartZ=0 EndX=4.03109 EndY=3.5 EndZ=0
    g20: Circle [constr] CenterX=4.03109 CenterY=7 CenterZ=0 NormalX=0 NormalY=0 NormalZ=1 AngleXU=0 Radius=3.5
    g21: LineSegment StartX=-1 StartY=5.25 StartZ=0 EndX=-1 EndY=8.75 EndZ=0
    g22: LineSegment StartX=-1 StartY=8.75 StartZ=0 EndX=-4.03109 EndY=10.5 EndZ=0
    g23: LineSegment StartX=-4.03109 StartY=10.5 StartZ=0 EndX=-7.06218 EndY=8.75 EndZ=0
    g24: LineSegment StartX=-7.06218 StartY=8.75 StartZ=0 EndX=-7.06218 EndY=5.25 EndZ=0
    g25: LineSegment StartX=-7.06218 StartY=5.25 StartZ=0 EndX=-4.03109 EndY=3.5 EndZ=0
    g26: LineSegment StartX=-4.03109 StartY=3.5 StartZ=0 EndX=-1 EndY=5.25 EndZ=0
    g27: Circle [constr] CenterX=-4.03109 CenterY=7 CenterZ=0 NormalX=0 NormalY=0 NormalZ=1 AngleXU=0 Radius=3.5
    g28: LineSegment StartX=-4.96891 StartY=-1.75 StartZ=0 EndX=-4.96891 EndY=1.75 EndZ=0
    g29: LineSegment StartX=-4.96891 StartY=1.75 StartZ=0 EndX=-8 EndY=3.5 EndZ=0
    g30: LineSegment StartX=-8 StartY=3.5 StartZ=0 EndX=-11.0311 EndY=1.75 EndZ=0
    g31: LineSegment StartX=-11.0311 StartY=1.75 StartZ=0 EndX=-11.0311 EndY=-1.75 EndZ=0
    g32: LineSegment StartX=-11.0311 StartY=-1.75 StartZ=0 EndX=-8 EndY=-3.5 EndZ=0
    g33: LineSegment StartX=-8 StartY=-3.5 StartZ=0 EndX=-4.96891 EndY=-1.75 EndZ=0
    g34: Circle [constr] CenterX=-8 CenterY=0 CenterZ=0 NormalX=0 NormalY=0 NormalZ=1 AngleXU=0 Radius=3.5
    g35: LineSegment StartX=-4.03109 StartY=-3.5 StartZ=0 EndX=-7.06218 EndY=-5.25 EndZ=0
    g36: LineSegment StartX=-7.06218 StartY=-5.25 StartZ=0 EndX=-7.06218 EndY=-8.75 EndZ=0
    g37: LineSegment StartX=-7.06218 StartY=-8.75 StartZ=0 EndX=-4.03109 EndY=-10.5 EndZ=0
    g38: LineSegment StartX=-4.03109 StartY=-10.5 StartZ=0 EndX=-1 EndY=-8.75 EndZ=0
    g39: LineSegment StartX=-1 StartY=-8.75 StartZ=0 EndX=-1 EndY=-5.25 EndZ=0
    g40: LineSegment StartX=-1 StartY=-5.25 StartZ=0 EndX=-4.03109 EndY=-3.5 EndZ=0
    g41: Circle [constr] CenterX=-4.03109 CenterY=-7 CenterZ=0 NormalX=0 NormalY=0 NormalZ=1 AngleXU=0 Radius=3.5
    g42: LineSegment StartX=4.03109 StartY=-3.5 StartZ=0 EndX=1 EndY=-5.25 EndZ=0
    g43: LineSegment StartX=1 StartY=-5.25 StartZ=0 EndX=1 EndY=-8.75 EndZ=0
    g44: LineSegment StartX=1 StartY=-8.75 StartZ=0 EndX=4.03109 EndY=-10.5 EndZ=0
    g45: LineSegment StartX=4.03109 StartY=-10.5 StartZ=0 EndX=7.06218 EndY=-8.75 EndZ=0
    g46: LineSegment StartX=7.06218 StartY=-8.75 StartZ=0 EndX=7.06218 EndY=-5.25 EndZ=0
    g47: LineSegment StartX=7.06218 StartY=-5.25 StartZ=0 EndX=4.03109 EndY=-3.5 EndZ=0
    g48: Circle [constr] CenterX=4.03109 CenterY=-7 CenterZ=0 NormalX=0 NormalY=0 NormalZ=1 AngleXU=0 Radius=3.5
  constraints (117):
    c: Coincident(g0,g1)
    c: Coincident(g1,g2)
    c: Coincident(g2,g3)
    c: Coincident(g3,g4)
    c: Coincident(g4,g5)
    c: Coincident(g5,g0)
    c: Equal(g0, g1-g5) x5
    c: PointOnObject(g0,g6)
    c: PointOnObject(g1,g6)
    c: PointOnObject(g2,g6)
    c: PointOnObject(g3,g6)
    c: PointOnObject(g4,g6)
    c: PointOnObject(g5,g6)
    c: Coincident(g6,g-1)
    c: Diameter(g6) = 7
    c: PointOnObject(g0,g-2)
    c: Coincident(g7,g8)
    c: Coincident(g8,g9)
    c: Coincident(g9,g10)
    c: Coincident(g10,g11)
    c: Coincident(g11,g12)
    c: Coincident(g12,g7)
    c: Equal(g7, g8-g12) x5
    c: PointOnObject(g7,g13)
    c: PointOnObject(g8,g13)
    c: PointOnObject(g9,g13)
    c: PointOnObject(g10,g13)
    c: PointOnObject(g11,g13)
    c: PointOnObject(g12,g13)
    c: PointOnObject(g13,g-1)
    c: Diameter(g13) = 7
    c: Distance(g6,g13) = 8
    c: Horizontal(g0,g10)
    c: Coincident(g14,g15)
    c: Coincident(g15,g16)
    c: Coincident(g16,g17)
    c: Coincident(g17,g18)
    c: Coincident(g18,g19)
    c: Coincident(g19,g14)
    c: Equal(g14, g15-g19) x5
    c: PointOnObject(g14,g20)
    c: PointOnObject(g15,g20)
    c: PointOnObject(g16,g20)
    c: PointOnObject(g17,g20)
    c: PointOnObject(g18,g20)
    c: PointOnObject(g19,g20)
    c: Diameter(g20) = 7
    c: DistanceY(g-1,g20) = 7
    c: Vertical(g18)
    c: Distance(g17,g-2) = 1
    c: Coincident(g21,g22)
    c: Coincident(g22,g23)
    c: Coincident(g23,g24)
    c: Coincident(g24,g25)
    c: Coincident(g25,g26)
    c: Coincident(g26,g21)
    c: Equal(g21, g22-g26) x5
    c: PointOnObject(g21,g27)
    c: PointOnObject(g22,g27)
    c: PointOnObject(g23,g27)
    c: PointOnObject(g24,g27)
    c: PointOnObject(g25,g27)
    c: PointOnObject(g26,g27)
    c: Diameter(g27) = 7
    c: DistanceY(g-1,g27) = 7
    c: DistanceX(g21,g-1) = 1
    c: Vertical(g21)
    c: Coincident(g28,g29)
    c: Coincident(g29,g30)
    c: Coincident(g30,g31)
    c: Coincident(g31,g32)
    c: Coincident(g32,g33)
    c: Coincident(g33,g28)
    c: Equal(g28, g29-g33) x5
    c: PointOnObject(g28,g34)
    c: PointOnObject(g29,g34)
    c: PointOnObject(g30,g34)
    c: PointOnObject(g31,g34)
    c: PointOnObject(g32,g34)
    c: PointOnObject(g33,g34)
    c: PointOnObject(g34,g-1)
    c: Diameter(g34) = 7
    c: Vertical(g31)
    c: DistanceX(g34,g-1) = 8
    c: Coincident(g35,g36)
    c: Coincident(g36,g37)
    c: Coincident(g37,g38)
    c: Coincident(g38,g39)
    c: Coincident(g39,g40)
    c: Coincident(g40,g35)
    c: Equal(g35, g36-g40) x5
    c: PointOnObject(g35,g41)
    c: PointOnObject(g36,g41)
    c: PointOnObject(g37,g41)
    c: PointOnObject(g38,g41)
    c: PointOnObject(g39,g41)
    c: PointOnObject(g40,g41)
    c: Coincident(g42,g43)
    c: Coincident(g43,g44)
    c: Coincident(g44,g45)
    c: Coincident(g45,g46)
    c: Coincident(g46,g47)
    c: Coincident(g47,g42)
    c: Equal(g42, g43-g47) x5
    c: PointOnObject(g42,g48)
    c: PointOnObject(g43,g48)
    c: PointOnObject(g44,g48)
    c: PointOnObject(g45,g48)
    c: PointOnObject(g46,g48)
    c: PointOnObject(g47,g48)
    c: Equal(g41,g48)
    c: Diameter(g41) = 7
    c: Vertical(g39)
    c: Vertical(g43)
    c: Distance(g-2,g39) = 1
    c: Symmetric(g38,g43,g-2)
    c: Distance(g41,g-1) = 7
FEATURE [Part::Extrusion] Extrude725  label="hex327"
  Base = -> Sketch734
  Dir = (0,-1,2e-16)
  DirMode = 2
  FaceMakerClass = Part::FaceMakerBullseye
  FaceMakerMode = 3
  LengthFwd = 10
  LengthRev = 0
  Placement = pos=(-4,0,105) rot=(0,0,1;0rad)
  Solid = true
  Symmetric = false
FEATURE [Sketcher::SketchObject] Sketch735
  ArcFitTolerance = 1e-06
  FullyConstrained = true
  MakeInternals = false
  Placement = pos=(0,0,0) rot=(1,0,0;1.5708rad)
  sketch-geometry (49):
    g0: LineSegment StartX=1e-16 StartY=3.5 StartZ=0 EndX=-3.03109 EndY=1.75 EndZ=0
    g1: LineSegment StartX=-3.03109 StartY=1.75 StartZ=0 EndX=-3.03109 EndY=-1.75 EndZ=0
    g2: LineSegment StartX=-3.03109 StartY=-1.75 StartZ=0 EndX=-1e-16 EndY=-3.5 EndZ=0
    g3: LineSegment StartX=-1e-16 StartY=-3.5 StartZ=0 EndX=3.03109 EndY=-1.75 EndZ=0
    g4: LineSegment StartX=3.03109 StartY=-1.75 StartZ=0 EndX=3.03109 EndY=1.75 EndZ=0
    g5: LineSegment StartX=3.03109 StartY=1.75 StartZ=0 EndX=1e-16 EndY=3.5 EndZ=0
    g6: Circle [constr] CenterX=0 CenterY=0 CenterZ=0 NormalX=0 NormalY=0 NormalZ=1 AngleXU=0 Radius=3.5
    g7: LineSegment StartX=4.96892 StartY=-1.75002 StartZ=0 EndX=8.00002 EndY=-3.5 EndZ=0
    g8: LineSegment StartX=8.00002 StartY=-3.5 StartZ=0 EndX=11.0311 EndY=-1.74998 EndZ=0
    g9: LineSegment StartX=11.0311 StartY=-1.74998 StartZ=0 EndX=11.0311 EndY=1.75002 EndZ=0
    g10: LineSegment StartX=11.0311 StartY=1.75002 StartZ=0 EndX=7.99998 EndY=3.5 EndZ=0
    g11: LineSegment StartX=7.99998 StartY=3.5 StartZ=0 EndX=4.9689 EndY=1.74998 EndZ=0
    g12: LineSegment StartX=4.9689 StartY=1.74998 StartZ=0 EndX=4.96892 EndY=-1.75002 EndZ=0
    g13: Circle [constr] CenterX=8 CenterY=0 CenterZ=0 NormalX=0 NormalY=0 NormalZ=1 AngleXU=0 Radius=3.5
    g14: LineSegment StartX=4.03109 StartY=3.5 StartZ=0 EndX=7.06218 EndY=5.25 EndZ=0
    g15: LineSegment StartX=7.06218 StartY=5.25 StartZ=0 EndX=7.06218 EndY=8.75 EndZ=0
    g16: LineSegment StartX=7.06218 StartY=8.75 StartZ=0 EndX=4.03109 EndY=10.5 EndZ=0
    g17: LineSegment StartX=4.03109 StartY=10.5 StartZ=0 EndX=1 EndY=8.75 EndZ=0
    g18: LineSegment StartX=1 StartY=8.75 StartZ=0 EndX=1 EndY=5.25 EndZ=0
    g19: LineSegment StartX=1 StartY=5.25 StartZ=0 EndX=4.03109 EndY=3.5 EndZ=0
    g20: Circle [constr] CenterX=4.03109 CenterY=7 CenterZ=0 NormalX=0 NormalY=0 NormalZ=1 AngleXU=0 Radius=3.5
    g21: LineSegment StartX=-1 StartY=5.25 StartZ=0 EndX=-1 EndY=8.75 EndZ=0
    g22: LineSegment StartX=-1 StartY=8.75 StartZ=0 EndX=-4.03109 EndY=10.5 EndZ=0
    g23: LineSegment StartX=-4.03109 StartY=10.5 StartZ=0 EndX=-7.06218 EndY=8.75 EndZ=0
    g24: LineSegment StartX=-7.06218 StartY=8.75 StartZ=0 EndX=-7.06218 EndY=5.25 EndZ=0
    g25: LineSegment StartX=-7.06218 StartY=5.25 StartZ=0 EndX=-4.03109 EndY=3.5 EndZ=0
    g26: LineSegment StartX=-4.03109 StartY=3.5 StartZ=0 EndX=-1 EndY=5.25 EndZ=0
    g27: Circle [constr] CenterX=-4.03109 CenterY=7 CenterZ=0 NormalX=0 NormalY=0 NormalZ=1 AngleXU=0 Radius=3.5
    g28: LineSegment StartX=-4.96891 StartY=-1.75 StartZ=0 EndX=-4.96891 EndY=1.75 EndZ=0
    g29: LineSegment StartX=-4.96891 StartY=1.75 StartZ=0 EndX=-8 EndY=3.5 EndZ=0
    g30: LineSegment StartX=-8 StartY=3.5 StartZ=0 EndX=-11.0311 EndY=1.75 EndZ=0
    g31: LineSegment StartX=-11.0311 StartY=1.75 StartZ=0 EndX=-11.0311 EndY=-1.75 EndZ=0
    g32: LineSegment StartX=-11.0311 StartY=-1.75 StartZ=0 EndX=-8 EndY=-3.5 EndZ=0
    g33: LineSegment StartX=-8 StartY=-3.5 StartZ=0 EndX=-4.96891 EndY=-1.75 EndZ=0
    g34: Circle [constr] CenterX=-8 CenterY=0 CenterZ=0 NormalX=0 NormalY=0 NormalZ=1 AngleXU=0 Radius=3.5
    g35: LineSegment StartX=-4.03109 StartY=-3.5 StartZ=0 EndX=-7.06218 EndY=-5.25 EndZ=0
    g36: LineSegment StartX=-7.06218 StartY=-5.25 StartZ=0 EndX=-7.06218 EndY=-8.75 EndZ=0
    g37: LineSegment StartX=-7.06218 StartY=-8.75 StartZ=0 EndX=-4.03109 EndY=-10.5 EndZ=0
    g38: LineSegment StartX=-4.03109 StartY=-10.5 StartZ=0 EndX=-1 EndY=-8.75 EndZ=0
    g39: LineSegment StartX=-1 StartY=-8.75 StartZ=0 EndX=-1 EndY=-5.25 EndZ=0
    g40: LineSegment StartX=-1 StartY=-5.25 StartZ=0 EndX=-4.03109 EndY=-3.5 EndZ=0
    g41: Circle [constr] CenterX=-4.03109 CenterY=-7 CenterZ=0 NormalX=0 NormalY=0 NormalZ=1 AngleXU=0 Radius=3.5
    g42: LineSegment StartX=4.03109 StartY=-3.5 StartZ=0 EndX=1 EndY=-5.25 EndZ=0
    g43: LineSegment StartX=1 StartY=-5.25 StartZ=0 EndX=1 EndY=-8.75 EndZ=0
    g44: LineSegment StartX=1 StartY=-8.75 StartZ=0 EndX=4.03109 EndY=-10.5 EndZ=0
    g45: LineSegment StartX=4.03109 StartY=-10.5 StartZ=0 EndX=7.06218 EndY=-8.75 EndZ=0
    g46: LineSegment StartX=7.06218 StartY=-8.75 StartZ=0 EndX=7.06218 EndY=-5.25 EndZ=0
    g47: LineSegment StartX=7.06218 StartY=-5.25 StartZ=0 EndX=4.03109 EndY=-3.5 EndZ=0
    g48: Circle [constr] CenterX=4.03109 CenterY=-7 CenterZ=0 NormalX=0 NormalY=0 NormalZ=1 AngleXU=0 Radius=3.5
  constraints (117):
    c: Coincident(g0,g1)
    c: Coincident(g1,g2)
    c: Coincident(g2,g3)
    c: Coincident(g3,g4)
    c: Coincident(g4,g5)
    c: Coincident(g5,g0)
    c: Equal(g0, g1-g5) x5
    c: PointOnObject(g0,g6)
    c: PointOnObject(g1,g6)
    c: PointOnObject(g2,g6)
    c: PointOnObject(g3,g6)
    c: PointOnObject(g4,g6)
    c: PointOnObject(g5,g6)
    c: Coincident(g6,g-1)
    c: Diameter(g6) = 7
    c: PointOnObject(g0,g-2)
    c: Coincident(g7,g8)
    c: Coincident(g8,g9)
    c: Coincident(g9,g10)
    c: Coincident(g10,g11)
    c: Coincident(g11,g12)
    c: Coincident(g12,g7)
    c: Equal(g7, g8-g12) x5
    c: PointOnObject(g7,g13)
    c: PointOnObject(g8,g13)
    c: PointOnObject(g9,g13)
    c: PointOnObject(g10,g13)
    c: PointOnObject(g11,g13)
    c: PointOnObject(g12,g13)
    c: PointOnObject(g13,g-1)
    c: Diameter(g13) = 7
    c: Distance(g6,g13) = 8
    c: Horizontal(g0,g10)
    c: Coincident(g14,g15)
    c: Coincident(g15,g16)
    c: Coincident(g16,g17)
    c: Coincident(g17,g18)
    c: Coincident(g18,g19)
    c: Coincident(g19,g14)
    c: Equal(g14, g15-g19) x5
    c: PointOnObject(g14,g20)
    c: PointOnObject(g15,g20)
    c: PointOnObject(g16,g20)
    c: PointOnObject(g17,g20)
    c: PointOnObject(g18,g20)
    c: PointOnObject(g19,g20)
    c: Diameter(g20) = 7
    c: DistanceY(g-1,g20) = 7
    c: Vertical(g18)
    c: Distance(g17,g-2) = 1
    c: Coincident(g21,g22)
    c: Coincident(g22,g23)
    c: Coincident(g23,g24)
    c: Coincident(g24,g25)
    c: Coincident(g25,g26)
    c: Coincident(g26,g21)
    c: Equal(g21, g22-g26) x5
    c: PointOnObject(g21,g27)
    c: PointOnObject(g22,g27)
    c: PointOnObject(g23,g27)
    c: PointOnObject(g24,g27)
    c: PointOnObject(g25,g27)
    c: PointOnObject(g26,g27)
    c: Diameter(g27) = 7
    c: DistanceY(g-1,g27) = 7
    c: DistanceX(g21,g-1) = 1
    c: Vertical(g21)
    c: Coincident(g28,g29)
    c: Coincident(g29,g30)
    c: Coincident(g30,g31)
    c: Coincident(g31,g32)
    c: Coincident(g32,g33)
    c: Coincident(g33,g28)
    c: Equal(g28, g29-g33) x5
    c: PointOnObject(g28,g34)
    c: PointOnObject(g29,g34)
    c: PointOnObject(g30,g34)
    c: PointOnObject(g31,g34)
    c: PointOnObject(g32,g34)
    c: PointOnObject(g33,g34)
    c: PointOnObject(g34,g-1)
    c: Diameter(g34) = 7
    c: Vertical(g31)
    c: DistanceX(g34,g-1) = 8
    c: Coincident(g35,g36)
    c: Coincident(g36,g37)
    c: Coincident(g37,g38)
    c: Coincident(g38,g39)
    c: Coincident(g39,g40)
    c: Coincident(g40,g35)
    c: Equal(g35, g36-g40) x5
    c: PointOnObject(g35,g41)
    c: PointOnObject(g36,g41)
    c: PointOnObject(g37,g41)
    c: PointOnObject(g38,g41)
    c: PointOnObject(g39,g41)
    c: PointOnObject(g40,g41)
    c: Coincident(g42,g43)
    c: Coincident(g43,g44)
    c: Coincident(g44,g45)
    c: Coincident(g45,g46)
    c: Coincident(g46,g47)
    c: Coincident(g47,g42)
    c: Equal(g42, g43-g47) x5
    c: PointOnObject(g42,g48)
    c: PointOnObject(g43,g48)
    c: PointOnObject(g44,g48)
    c: PointOnObject(g45,g48)
    c: PointOnObject(g46,g48)
    c: PointOnObject(g47,g48)
    c: Equal(g41,g48)
    c: Diameter(g41) = 7
    c: Vertical(g39)
    c: Vertical(g43)
    c: Distance(g-2,g39) = 1
    c: Symmetric(g38,g43,g-2)
    c: Distance(g41,g-1) = 7
FEATURE [Part::Extrusion] Extrude726  label="hex328"
  Base = -> Sketch735
  Dir = (0,-1,2e-16)
  DirMode = 2
  FaceMakerClass = Part::FaceMakerBullseye
  FaceMakerMode = 3
  LengthFwd = 10
  LengthRev = 0
  Placement = pos=(-16,0,112) rot=(0,0,1;0rad)
  Solid = true
  Symmetric = false
FEATURE [Sketcher::SketchObject] Sketch736
  ArcFitTolerance = 1e-06
  FullyConstrained = true
  MakeInternals = false
  Placement = pos=(0,0,0) rot=(1,0,0;1.5708rad)
  sketch-geometry (49):
    g0: LineSegment StartX=1e-16 StartY=3.5 StartZ=0 EndX=-3.03109 EndY=1.75 EndZ=0
    g1: LineSegment StartX=-3.03109 StartY=1.75 StartZ=0 EndX=-3.03109 EndY=-1.75 EndZ=0
    g2: LineSegment StartX=-3.03109 StartY=-1.75 StartZ=0 EndX=-1e-16 EndY=-3.5 EndZ=0
    g3: LineSegment StartX=-1e-16 StartY=-3.5 StartZ=0 EndX=3.03109 EndY=-1.75 EndZ=0
    g4: LineSegment StartX=3.03109 StartY=-1.75 StartZ=0 EndX=3.03109 EndY=1.75 EndZ=0
    g5: LineSegment StartX=3.03109 StartY=1.75 StartZ=0 EndX=1e-16 EndY=3.5 EndZ=0
    g6: Circle [constr] CenterX=0 CenterY=0 CenterZ=0 NormalX=0 NormalY=0 NormalZ=1 AngleXU=0 Radius=3.5
    g7: LineSegment StartX=4.96892 StartY=-1.75002 StartZ=0 EndX=8.00002 EndY=-3.5 EndZ=0
    g8: LineSegment StartX=8.00002 StartY=-3.5 StartZ=0 EndX=11.0311 EndY=-1.74998 EndZ=0
    g9: LineSegment StartX=11.0311 StartY=-1.74998 StartZ=0 EndX=11.0311 EndY=1.75002 EndZ=0
    g10: LineSegment StartX=11.0311 StartY=1.75002 StartZ=0 EndX=7.99998 EndY=3.5 EndZ=0
    g11: LineSegment StartX=7.99998 StartY=3.5 StartZ=0 EndX=4.9689 EndY=1.74998 EndZ=0
    g12: LineSegment StartX=4.9689 StartY=1.74998 StartZ=0 EndX=4.96892 EndY=-1.75002 EndZ=0
    g13: Circle [constr] CenterX=8 CenterY=0 CenterZ=0 NormalX=0 NormalY=0 NormalZ=1 AngleXU=0 Radius=3.5
    g14: LineSegment StartX=4.03109 StartY=3.5 StartZ=0 EndX=7.06218 EndY=5.25 EndZ=0
    g15: LineSegment StartX=7.06218 StartY=5.25 StartZ=0 EndX=7.06218 EndY=8.75 EndZ=0
    g16: LineSegment StartX=7.06218 StartY=8.75 StartZ=0 EndX=4.03109 EndY=10.5 EndZ=0
    g17: LineSegment StartX=4.03109 StartY=10.5 StartZ=0 EndX=1 EndY=8.75 EndZ=0
    g18: LineSegment StartX=1 StartY=8.75 StartZ=0 EndX=1 EndY=5.25 EndZ=0
    g19: LineSegment StartX=1 StartY=5.25 StartZ=0 EndX=4.03109 EndY=3.5 EndZ=0
    g20: Circle [constr] CenterX=4.03109 CenterY=7 CenterZ=0 NormalX=0 NormalY=0 NormalZ=1 AngleXU=0 Radius=3.5
    g21: LineSegment StartX=-1 StartY=5.25 StartZ=0 EndX=-1 EndY=8.75 EndZ=0
    g22: LineSegment StartX=-1 StartY=8.75 StartZ=0 EndX=-4.03109 EndY=10.5 EndZ=0
    g23: LineSegment StartX=-4.03109 StartY=10.5 StartZ=0 EndX=-7.06218 EndY=8.75 EndZ=0
    g24: LineSegment StartX=-7.06218 StartY=8.75 StartZ=0 EndX=-7.06218 EndY=5.25 EndZ=0
    g25: LineSegment StartX=-7.06218 StartY=5.25 StartZ=0 EndX=-4.03109 EndY=3.5 EndZ=0
    g26: LineSegment StartX=-4.03109 StartY=3.5 StartZ=0 EndX=-1 EndY=5.25 EndZ=0
    g27: Circle [constr] CenterX=-4.03109 CenterY=7 CenterZ=0 NormalX=0 NormalY=0 NormalZ=1 AngleXU=0 Radius=3.5
    g28: LineSegment StartX=-4.96891 StartY=-1.75 StartZ=0 EndX=-4.96891 EndY=1.75 EndZ=0
    g29: LineSegment StartX=-4.96891 StartY=1.75 StartZ=0 EndX=-8 EndY=3.5 EndZ=0
    g30: LineSegment StartX=-8 StartY=3.5 StartZ=0 EndX=-11.0311 EndY=1.75 EndZ=0
    g31: LineSegment StartX=-11.0311 StartY=1.75 StartZ=0 EndX=-11.0311 EndY=-1.75 EndZ=0
    g32: LineSegment StartX=-11.0311 StartY=-1.75 StartZ=0 EndX=-8 EndY=-3.5 EndZ=0
    g33: LineSegment StartX=-8 StartY=-3.5 StartZ=0 EndX=-4.96891 EndY=-1.75 EndZ=0
    g34: Circle [constr] CenterX=-8 CenterY=0 CenterZ=0 NormalX=0 NormalY=0 NormalZ=1 AngleXU=0 Radius=3.5
    g35: LineSegment StartX=-4.03109 StartY=-3.5 StartZ=0 EndX=-7.06218 EndY=-5.25 EndZ=0
    g36: LineSegment StartX=-7.06218 StartY=-5.25 StartZ=0 EndX=-7.06218 EndY=-8.75 EndZ=0
    g37: LineSegment StartX=-7.06218 StartY=-8.75 StartZ=0 EndX=-4.03109 EndY=-10.5 EndZ=0
    g38: LineSegment StartX=-4.03109 StartY=-10.5 StartZ=0 EndX=-1 EndY=-8.75 EndZ=0
    g39: LineSegment StartX=-1 StartY=-8.75 StartZ=0 EndX=-1 EndY=-5.25 EndZ=0
    g40: LineSegment StartX=-1 StartY=-5.25 StartZ=0 EndX=-4.03109 EndY=-3.5 EndZ=0
    g41: Circle [constr] CenterX=-4.03109 CenterY=-7 CenterZ=0 NormalX=0 NormalY=0 NormalZ=1 AngleXU=0 Radius=3.5
    g42: LineSegment StartX=4.03109 StartY=-3.5 StartZ=0 EndX=1 EndY=-5.25 EndZ=0
    g43: LineSegment StartX=1 StartY=-5.25 StartZ=0 EndX=1 EndY=-8.75 EndZ=0
    g44: LineSegment StartX=1 StartY=-8.75 StartZ=0 EndX=4.03109 EndY=-10.5 EndZ=0
    g45: LineSegment StartX=4.03109 StartY=-10.5 StartZ=0 EndX=7.06218 EndY=-8.75 EndZ=0
    g46: LineSegment StartX=7.06218 StartY=-8.75 StartZ=0 EndX=7.06218 EndY=-5.25 EndZ=0
    g47: LineSegment StartX=7.06218 StartY=-5.25 StartZ=0 EndX=4.03109 EndY=-3.5 EndZ=0
    g48: Circle [constr] CenterX=4.03109 CenterY=-7 CenterZ=0 NormalX=0 NormalY=0 NormalZ=1 AngleXU=0 Radius=3.5
  constraints (117):
    c: Coincident(g0,g1)
    c: Coincident(g1,g2)
    c: Coincident(g2,g3)
    c: Coincident(g3,g4)
    c: Coincident(g4,g5)
    c: Coincident(g5,g0)
    c: Equal(g0, g1-g5) x5
    c: PointOnObject(g0,g6)
    c: PointOnObject(g1,g6)
    c: PointOnObject(g2,g6)
    c: PointOnObject(g3,g6)
    c: PointOnObject(g4,g6)
    c: PointOnObject(g5,g6)
    c: Coincident(g6,g-1)
    c: Diameter(g6) = 7
    c: PointOnObject(g0,g-2)
    c: Coincident(g7,g8)
    c: Coincident(g8,g9)
    c: Coincident(g9,g10)
    c: Coincident(g10,g11)
    c: Coincident(g11,g12)
    c: Coincident(g12,g7)
    c: Equal(g7, g8-g12) x5
    c: PointOnObject(g7,g13)
    c: PointOnObject(g8,g13)
    c: PointOnObject(g9,g13)
    c: PointOnObject(g10,g13)
    c: PointOnObject(g11,g13)
    c: PointOnObject(g12,g13)
    c: PointOnObject(g13,g-1)
    c: Diameter(g13) = 7
    c: Distance(g6,g13) = 8
    c: Horizontal(g0,g10)
    c: Coincident(g14,g15)
    c: Coincident(g15,g16)
    c: Coincident(g16,g17)
    c: Coincident(g17,g18)
    c: Coincident(g18,g19)
    c: Coincident(g19,g14)
    c: Equal(g14, g15-g19) x5
    c: PointOnObject(g14,g20)
    c: PointOnObject(g15,g20)
    c: PointOnObject(g16,g20)
    c: PointOnObject(g17,g20)
    c: PointOnObject(g18,g20)
    c: PointOnObject(g19,g20)
    c: Diameter(g20) = 7
    c: DistanceY(g-1,g20) = 7
    c: Vertical(g18)
    c: Distance(g17,g-2) = 1
    c: Coincident(g21,g22)
    c: Coincident(g22,g23)
    c: Coincident(g23,g24)
    c: Coincident(g24,g25)
    c: Coincident(g25,g26)
    c: Coincident(g26,g21)
    c: Equal(g21, g22-g26) x5
    c: PointOnObject(g21,g27)
    c: PointOnObject(g22,g27)
    c: PointOnObject(g23,g27)
    c: PointOnObject(g24,g27)
    c: PointOnObject(g25,g27)
    c: PointOnObject(g26,g27)
    c: Diameter(g27) = 7
    c: DistanceY(g-1,g27) = 7
    c: DistanceX(g21,g-1) = 1
    c: Vertical(g21)
    c: Coincident(g28,g29)
    c: Coincident(g29,g30)
    c: Coincident(g30,g31)
    c: Coincident(g31,g32)
    c: Coincident(g32,g33)
    c: Coincident(g33,g28)
    c: Equal(g28, g29-g33) x5
    c: PointOnObject(g28,g34)
    c: PointOnObject(g29,g34)
    c: PointOnObject(g30,g34)
    c: PointOnObject(g31,g34)
    c: PointOnObject(g32,g34)
    c: PointOnObject(g33,g34)
    c: PointOnObject(g34,g-1)
    c: Diameter(g34) = 7
    c: Vertical(g31)
    c: DistanceX(g34,g-1) = 8
    c: Coincident(g35,g36)
    c: Coincident(g36,g37)
    c: Coincident(g37,g38)
    c: Coincident(g38,g39)
    c: Coincident(g39,g40)
    c: Coincident(g40,g35)
    c: Equal(g35, g36-g40) x5
    c: PointOnObject(g35,g41)
    c: PointOnObject(g36,g41)
    c: PointOnObject(g37,g41)
    c: PointOnObject(g38,g41)
    c: PointOnObject(g39,g41)
    c: PointOnObject(g40,g41)
    c: Coincident(g42,g43)
    c: Coincident(g43,g44)
    c: Coincident(g44,g45)
    c: Coincident(g45,g46)
    c: Coincident(g46,g47)
    c: Coincident(g47,g42)
    c: Equal(g42, g43-g47) x5
    c: PointOnObject(g42,g48)
    c: PointOnObject(g43,g48)
    c: PointOnObject(g44,g48)
    c: PointOnObject(g45,g48)
    c: PointOnObject(g46,g48)
    c: PointOnObject(g47,g48)
    c: Equal(g41,g48)
    c: Diameter(g41) = 7
    c: Vertical(g39)
    c: Vertical(g43)
    c: Distance(g-2,g39) = 1
    c: Symmetric(g38,g43,g-2)
    c: Distance(g41,g-1) = 7
FEATURE [Part::Extrusion] Extrude727  label="hex329"
  Base = -> Sketch736
  Dir = (0,-1,2e-16)
  DirMode = 2
  FaceMakerClass = Part::FaceMakerBullseye
  FaceMakerMode = 3
  LengthFwd = 10
  LengthRev = 0
  Placement = pos=(-32,0,98) rot=(0,0,1;0rad)
  Solid = true
  Symmetric = false
FEATURE [Sketcher::SketchObject] Sketch737
  ArcFitTolerance = 1e-06
  FullyConstrained = true
  MakeInternals = false
  Placement = pos=(0,0,0) rot=(1,0,0;1.5708rad)
  sketch-geometry (49):
    g0: LineSegment StartX=1e-16 StartY=3.5 StartZ=0 EndX=-3.03109 EndY=1.75 EndZ=0
    g1: LineSegment StartX=-3.03109 StartY=1.75 StartZ=0 EndX=-3.03109 EndY=-1.75 EndZ=0
    g2: LineSegment StartX=-3.03109 StartY=-1.75 StartZ=0 EndX=-1e-16 EndY=-3.5 EndZ=0
    g3: LineSegment StartX=-1e-16 StartY=-3.5 StartZ=0 EndX=3.03109 EndY=-1.75 EndZ=0
    g4: LineSegment StartX=3.03109 StartY=-1.75 StartZ=0 EndX=3.03109 EndY=1.75 EndZ=0
    g5: LineSegment StartX=3.03109 StartY=1.75 StartZ=0 EndX=1e-16 EndY=3.5 EndZ=0
    g6: Circle [constr] CenterX=0 CenterY=0 CenterZ=0 NormalX=0 NormalY=0 NormalZ=1 AngleXU=0 Radius=3.5
    g7: LineSegment StartX=4.96892 StartY=-1.75002 StartZ=0 EndX=8.00002 EndY=-3.5 EndZ=0
    g8: LineSegment StartX=8.00002 StartY=-3.5 StartZ=0 EndX=11.0311 EndY=-1.74998 EndZ=0
    g9: LineSegment StartX=11.0311 StartY=-1.74998 StartZ=0 EndX=11.0311 EndY=1.75002 EndZ=0
    g10: LineSegment StartX=11.0311 StartY=1.75002 StartZ=0 EndX=7.99998 EndY=3.5 EndZ=0
    g11: LineSegment StartX=7.99998 StartY=3.5 StartZ=0 EndX=4.9689 EndY=1.74998 EndZ=0
    g12: LineSegment StartX=4.9689 StartY=1.74998 StartZ=0 EndX=4.96892 EndY=-1.75002 EndZ=0
    g13: Circle [constr] CenterX=8 CenterY=0 CenterZ=0 NormalX=0 NormalY=0 NormalZ=1 AngleXU=0 Radius=3.5
    g14: LineSegment StartX=4.03109 StartY=3.5 StartZ=0 EndX=7.06218 EndY=5.25 EndZ=0
    g15: LineSegment StartX=7.06218 StartY=5.25 StartZ=0 EndX=7.06218 EndY=8.75 EndZ=0
    g16: LineSegment StartX=7.06218 StartY=8.75 StartZ=0 EndX=4.03109 EndY=10.5 EndZ=0
    g17: LineSegment StartX=4.03109 StartY=10.5 StartZ=0 EndX=1 EndY=8.75 EndZ=0
    g18: LineSegment StartX=1 StartY=8.75 StartZ=0 EndX=1 EndY=5.25 EndZ=0
    g19: LineSegment StartX=1 StartY=5.25 StartZ=0 EndX=4.03109 EndY=3.5 EndZ=0
    g20: Circle [constr] CenterX=4.03109 CenterY=7 CenterZ=0 NormalX=0 NormalY=0 NormalZ=1 AngleXU=0 Radius=3.5
    g21: LineSegment StartX=-1 StartY=5.25 StartZ=0 EndX=-1 EndY=8.75 EndZ=0
    g22: LineSegment StartX=-1 StartY=8.75 StartZ=0 EndX=-4.03109 EndY=10.5 EndZ=0
    g23: LineSegment StartX=-4.03109 StartY=10.5 StartZ=0 EndX=-7.06218 EndY=8.75 EndZ=0
    g24: LineSegment StartX=-7.06218 StartY=8.75 StartZ=0 EndX=-7.06218 EndY=5.25 EndZ=0
    g25: LineSegment StartX=-7.06218 StartY=5.25 StartZ=0 EndX=-4.03109 EndY=3.5 EndZ=0
    g26: LineSegment StartX=-4.03109 StartY=3.5 StartZ=0 EndX=-1 EndY=5.25 EndZ=0
    g27: Circle [constr] CenterX=-4.03109 CenterY=7 CenterZ=0 NormalX=0 NormalY=0 NormalZ=1 AngleXU=0 Radius=3.5
    g28: LineSegment StartX=-4.96891 StartY=-1.75 StartZ=0 EndX=-4.96891 EndY=1.75 EndZ=0
    g29: LineSegment StartX=-4.96891 StartY=1.75 StartZ=0 EndX=-8 EndY=3.5 EndZ=0
    g30: LineSegment StartX=-8 StartY=3.5 StartZ=0 EndX=-11.0311 EndY=1.75 EndZ=0
    g31: LineSegment StartX=-11.0311 StartY=1.75 StartZ=0 EndX=-11.0311 EndY=-1.75 EndZ=0
    g32: LineSegment StartX=-11.0311 StartY=-1.75 StartZ=0 EndX=-8 EndY=-3.5 EndZ=0
    g33: LineSegment StartX=-8 StartY=-3.5 StartZ=0 EndX=-4.96891 EndY=-1.75 EndZ=0
    g34: Circle [constr] CenterX=-8 CenterY=0 CenterZ=0 NormalX=0 NormalY=0 NormalZ=1 AngleXU=0 Radius=3.5
    g35: LineSegment StartX=-4.03109 StartY=-3.5 StartZ=0 EndX=-7.06218 EndY=-5.25 EndZ=0
    g36: LineSegment StartX=-7.06218 StartY=-5.25 StartZ=0 EndX=-7.06218 EndY=-8.75 EndZ=0
    g37: LineSegment StartX=-7.06218 StartY=-8.75 StartZ=0 EndX=-4.03109 EndY=-10.5 EndZ=0
    g38: LineSegment StartX=-4.03109 StartY=-10.5 StartZ=0 EndX=-1 EndY=-8.75 EndZ=0
    g39: LineSegment StartX=-1 StartY=-8.75 StartZ=0 EndX=-1 EndY=-5.25 EndZ=0
    g40: LineSegment StartX=-1 StartY=-5.25 StartZ=0 EndX=-4.03109 EndY=-3.5 EndZ=0
    g41: Circle [constr] CenterX=-4.03109 CenterY=-7 CenterZ=0 NormalX=0 NormalY=0 NormalZ=1 AngleXU=0 Radius=3.5
    g42: LineSegment StartX=4.03109 StartY=-3.5 StartZ=0 EndX=1 EndY=-5.25 EndZ=0
    g43: LineSegment StartX=1 StartY=-5.25 StartZ=0 EndX=1 EndY=-8.75 EndZ=0
    g44: LineSegment StartX=1 StartY=-8.75 StartZ=0 EndX=4.03109 EndY=-10.5 EndZ=0
    g45: LineSegment StartX=4.03109 StartY=-10.5 StartZ=0 EndX=7.06218 EndY=-8.75 EndZ=0
    g46: LineSegment StartX=7.06218 StartY=-8.75 StartZ=0 EndX=7.06218 EndY=-5.25 EndZ=0
    g47: LineSegment StartX=7.06218 StartY=-5.25 StartZ=0 EndX=4.03109 EndY=-3.5 EndZ=0
    g48: Circle [constr] CenterX=4.03109 CenterY=-7 CenterZ=0 NormalX=0 NormalY=0 NormalZ=1 AngleXU=0 Radius=3.5
  constraints (117):
    c: Coincident(g0,g1)
    c: Coincident(g1,g2)
    c: Coincident(g2,g3)
    c: Coincident(g3,g4)
    c: Coincident(g4,g5)
    c: Coincident(g5,g0)
    c: Equal(g0, g1-g5) x5
    c: PointOnObject(g0,g6)
    c: PointOnObject(g1,g6)
    c: PointOnObject(g2,g6)
    c: PointOnObject(g3,g6)
    c: PointOnObject(g4,g6)
    c: PointOnObject(g5,g6)
    c: Coincident(g6,g-1)
    c: Diameter(g6) = 7
    c: PointOnObject(g0,g-2)
    c: Coincident(g7,g8)
    c: Coincident(g8,g9)
    c: Coincident(g9,g10)
    c: Coincident(g10,g11)
    c: Coincident(g11,g12)
    c: Coincident(g12,g7)
    c: Equal(g7, g8-g12) x5
    c: PointOnObject(g7,g13)
    c: PointOnObject(g8,g13)
    c: PointOnObject(g9,g13)
    c: PointOnObject(g10,g13)
    c: PointOnObject(g11,g13)
    c: PointOnObject(g12,g13)
    c: PointOnObject(g13,g-1)
    c: Diameter(g13) = 7
    c: Distance(g6,g13) = 8
    c: Horizontal(g0,g10)
    c: Coincident(g14,g15)
    c: Coincident(g15,g16)
    c: Coincident(g16,g17)
    c: Coincident(g17,g18)
    c: Coincident(g18,g19)
    c: Coincident(g19,g14)
    c: Equal(g14, g15-g19) x5
    c: PointOnObject(g14,g20)
    c: PointOnObject(g15,g20)
    c: PointOnObject(g16,g20)
    c: PointOnObject(g17,g20)
    c: PointOnObject(g18,g20)
    c: PointOnObject(g19,g20)
    c: Diameter(g20) = 7
    c: DistanceY(g-1,g20) = 7
    c: Vertical(g18)
    c: Distance(g17,g-2) = 1
    c: Coincident(g21,g22)
    c: Coincident(g22,g23)
    c: Coincident(g23,g24)
    c: Coincident(g24,g25)
    c: Coincident(g25,g26)
    c: Coincident(g26,g21)
    c: Equal(g21, g22-g26) x5
    c: PointOnObject(g21,g27)
    c: PointOnObject(g22,g27)
    c: PointOnObject(g23,g27)
    c: PointOnObject(g24,g27)
    c: PointOnObject(g25,g27)
    c: PointOnObject(g26,g27)
    c: Diameter(g27) = 7
    c: DistanceY(g-1,g27) = 7
    c: DistanceX(g21,g-1) = 1
    c: Vertical(g21)
    c: Coincident(g28,g29)
    c: Coincident(g29,g30)
    c: Coincident(g30,g31)
    c: Coincident(g31,g32)
    c: Coincident(g32,g33)
    c: Coincident(g33,g28)
    c: Equal(g28, g29-g33) x5
    c: PointOnObject(g28,g34)
    c: PointOnObject(g29,g34)
    c: PointOnObject(g30,g34)
    c: PointOnObject(g31,g34)
    c: PointOnObject(g32,g34)
    c: PointOnObject(g33,g34)
    c: PointOnObject(g34,g-1)
    c: Diameter(g34) = 7
    c: Vertical(g31)
    c: DistanceX(g34,g-1) = 8
    c: Coincident(g35,g36)
    c: Coincident(g36,g37)
    c: Coincident(g37,g38)
    c: Coincident(g38,g39)
    c: Coincident(g39,g40)
    c: Coincident(g40,g35)
    c: Equal(g35, g36-g40) x5
    c: PointOnObject(g35,g41)
    c: PointOnObject(g36,g41)
    c: PointOnObject(g37,g41)
    c: PointOnObject(g38,g41)
    c: PointOnObject(g39,g41)
    c: PointOnObject(g40,g41)
    c: Coincident(g42,g43)
    c: Coincident(g43,g44)
    c: Coincident(g44,g45)
    c: Coincident(g45,g46)
    c: Coincident(g46,g47)
    c: Coincident(g47,g42)
    c: Equal(g42, g43-g47) x5
    c: PointOnObject(g42,g48)
    c: PointOnObject(g43,g48)
    c: PointOnObject(g44,g48)
    c: PointOnObject(g45,g48)
    c: PointOnObject(g46,g48)
    c: PointOnObject(g47,g48)
    c: Equal(g41,g48)
    c: Diameter(g41) = 7
    c: Vertical(g39)
    c: Vertical(g43)
    c: Distance(g-2,g39) = 1
    c: Symmetric(g38,g43,g-2)
    c: Distance(g41,g-1) = 7
FEATURE [Part::Extrusion] Extrude728  label="hex330"
  Base = -> Sketch737
  Dir = (0,-1,2e-16)
  DirMode = 2
  FaceMakerClass = Part::FaceMakerBullseye
  FaceMakerMode = 3
  LengthFwd = 10
  LengthRev = 0
  Placement = pos=(-52,0,91) rot=(0,0,1;0rad)
  Solid = true
  Symmetric = false
FEATURE [Sketcher::SketchObject] Sketch738
  ArcFitTolerance = 1e-06
  FullyConstrained = true
  MakeInternals = false
  Placement = pos=(0,0,0) rot=(1,0,0;1.5708rad)
  sketch-geometry (49):
    g0: LineSegment StartX=1e-16 StartY=3.5 StartZ=0 EndX=-3.03109 EndY=1.75 EndZ=0
    g1: LineSegment StartX=-3.03109 StartY=1.75 StartZ=0 EndX=-3.03109 EndY=-1.75 EndZ=0
    g2: LineSegment StartX=-3.03109 StartY=-1.75 StartZ=0 EndX=-1e-16 EndY=-3.5 EndZ=0
    g3: LineSegment StartX=-1e-16 StartY=-3.5 StartZ=0 EndX=3.03109 EndY=-1.75 EndZ=0
    g4: LineSegment StartX=3.03109 StartY=-1.75 StartZ=0 EndX=3.03109 EndY=1.75 EndZ=0
    g5: LineSegment StartX=3.03109 StartY=1.75 StartZ=0 EndX=1e-16 EndY=3.5 EndZ=0
    g6: Circle [constr] CenterX=0 CenterY=0 CenterZ=0 NormalX=0 NormalY=0 NormalZ=1 AngleXU=0 Radius=3.5
    g7: LineSegment StartX=4.96892 StartY=-1.75002 StartZ=0 EndX=8.00002 EndY=-3.5 EndZ=0
    g8: LineSegment StartX=8.00002 StartY=-3.5 StartZ=0 EndX=11.0311 EndY=-1.74998 EndZ=0
    g9: LineSegment StartX=11.0311 StartY=-1.74998 StartZ=0 EndX=11.0311 EndY=1.75002 EndZ=0
    g10: LineSegment StartX=11.0311 StartY=1.75002 StartZ=0 EndX=7.99998 EndY=3.5 EndZ=0
    g11: LineSegment StartX=7.99998 StartY=3.5 StartZ=0 EndX=4.9689 EndY=1.74998 EndZ=0
    g12: LineSegment StartX=4.9689 StartY=1.74998 StartZ=0 EndX=4.96892 EndY=-1.75002 EndZ=0
    g13: Circle [constr] CenterX=8 CenterY=0 CenterZ=0 NormalX=0 NormalY=0 NormalZ=1 AngleXU=0 Radius=3.5
    g14: LineSegment StartX=4.03109 StartY=3.5 StartZ=0 EndX=7.06218 EndY=5.25 EndZ=0
    g15: LineSegment StartX=7.06218 StartY=5.25 StartZ=0 EndX=7.06218 EndY=8.75 EndZ=0
    g16: LineSegment StartX=7.06218 StartY=8.75 StartZ=0 EndX=4.03109 EndY=10.5 EndZ=0
    g17: LineSegment StartX=4.03109 StartY=10.5 StartZ=0 EndX=1 EndY=8.75 EndZ=0
    g18: LineSegment StartX=1 StartY=8.75 StartZ=0 EndX=1 EndY=5.25 EndZ=0
    g19: LineSegment StartX=1 StartY=5.25 StartZ=0 EndX=4.03109 EndY=3.5 EndZ=0
    g20: Circle [constr] CenterX=4.03109 CenterY=7 CenterZ=0 NormalX=0 NormalY=0 NormalZ=1 AngleXU=0 Radius=3.5
    g21: LineSegment StartX=-1 StartY=5.25 StartZ=0 EndX=-1 EndY=8.75 EndZ=0
    g22: LineSegment StartX=-1 StartY=8.75 StartZ=0 EndX=-4.03109 EndY=10.5 EndZ=0
    g23: LineSegment StartX=-4.03109 StartY=10.5 StartZ=0 EndX=-7.06218 EndY=8.75 EndZ=0
    g24: LineSegment StartX=-7.06218 StartY=8.75 StartZ=0 EndX=-7.06218 EndY=5.25 EndZ=0
    g25: LineSegment StartX=-7.06218 StartY=5.25 StartZ=0 EndX=-4.03109 EndY=3.5 EndZ=0
    g26: LineSegment StartX=-4.03109 StartY=3.5 StartZ=0 EndX=-1 EndY=5.25 EndZ=0
    g27: Circle [constr] CenterX=-4.03109 CenterY=7 CenterZ=0 NormalX=0 NormalY=0 NormalZ=1 AngleXU=0 Radius=3.5
    g28: LineSegment StartX=-4.96891 StartY=-1.75 StartZ=0 EndX=-4.96891 EndY=1.75 EndZ=0
    g29: LineSegment StartX=-4.96891 StartY=1.75 StartZ=0 EndX=-8 EndY=3.5 EndZ=0
    g30: LineSegment StartX=-8 StartY=3.5 StartZ=0 EndX=-11.0311 EndY=1.75 EndZ=0
    g31: LineSegment StartX=-11.0311 StartY=1.75 StartZ=0 EndX=-11.0311 EndY=-1.75 EndZ=0
    g32: LineSegment StartX=-11.0311 StartY=-1.75 StartZ=0 EndX=-8 EndY=-3.5 EndZ=0
    g33: LineSegment StartX=-8 StartY=-3.5 StartZ=0 EndX=-4.96891 EndY=-1.75 EndZ=0
    g34: Circle [constr] CenterX=-8 CenterY=0 CenterZ=0 NormalX=0 NormalY=0 NormalZ=1 AngleXU=0 Radius=3.5
    g35: LineSegment StartX=-4.03109 StartY=-3.5 StartZ=0 EndX=-7.06218 EndY=-5.25 EndZ=0
    g36: LineSegment StartX=-7.06218 StartY=-5.25 StartZ=0 EndX=-7.06218 EndY=-8.75 EndZ=0
    g37: LineSegment StartX=-7.06218 StartY=-8.75 StartZ=0 EndX=-4.03109 EndY=-10.5 EndZ=0
    g38: LineSegment StartX=-4.03109 StartY=-10.5 StartZ=0 EndX=-1 EndY=-8.75 EndZ=0
    g39: LineSegment StartX=-1 StartY=-8.75 StartZ=0 EndX=-1 EndY=-5.25 EndZ=0
    g40: LineSegment StartX=-1 StartY=-5.25 StartZ=0 EndX=-4.03109 EndY=-3.5 EndZ=0
    g41: Circle [constr] CenterX=-4.03109 CenterY=-7 CenterZ=0 NormalX=0 NormalY=0 NormalZ=1 AngleXU=0 Radius=3.5
    g42: LineSegment StartX=4.03109 StartY=-3.5 StartZ=0 EndX=1 EndY=-5.25 EndZ=0
    g43: LineSegment StartX=1 StartY=-5.25 StartZ=0 EndX=1 EndY=-8.75 EndZ=0
    g44: LineSegment StartX=1 StartY=-8.75 StartZ=0 EndX=4.03109 EndY=-10.5 EndZ=0
    g45: LineSegment StartX=4.03109 StartY=-10.5 StartZ=0 EndX=7.06218 EndY=-8.75 EndZ=0
    g46: LineSegment StartX=7.06218 StartY=-8.75 StartZ=0 EndX=7.06218 EndY=-5.25 EndZ=0
    g47: LineSegment StartX=7.06218 StartY=-5.25 StartZ=0 EndX=4.03109 EndY=-3.5 EndZ=0
    g48: Circle [constr] CenterX=4.03109 CenterY=-7 CenterZ=0 NormalX=0 NormalY=0 NormalZ=1 AngleXU=0 Radius=3.5
  constraints (117):
    c: Coincident(g0,g1)
    c: Coincident(g1,g2)
    c: Coincident(g2,g3)
    c: Coincident(g3,g4)
    c: Coincident(g4,g5)
    c: Coincident(g5,g0)
    c: Equal(g0, g1-g5) x5
    c: PointOnObject(g0,g6)
    c: PointOnObject(g1,g6)
    c: PointOnObject(g2,g6)
    c: PointOnObject(g3,g6)
    c: PointOnObject(g4,g6)
    c: PointOnObject(g5,g6)
    c: Coincident(g6,g-1)
    c: Diameter(g6) = 7
    c: PointOnObject(g0,g-2)
    c: Coincident(g7,g8)
    c: Coincident(g8,g9)
    c: Coincident(g9,g10)
    c: Coincident(g10,g11)
    c: Coincident(g11,g12)
    c: Coincident(g12,g7)
    c: Equal(g7, g8-g12) x5
    c: PointOnObject(g7,g13)
    c: PointOnObject(g8,g13)
    c: PointOnObject(g9,g13)
    c: PointOnObject(g10,g13)
    c: PointOnObject(g11,g13)
    c: PointOnObject(g12,g13)
    c: PointOnObject(g13,g-1)
    c: Diameter(g13) = 7
    c: Distance(g6,g13) = 8
    c: Horizontal(g0,g10)
    c: Coincident(g14,g15)
    c: Coincident(g15,g16)
    c: Coincident(g16,g17)
    c: Coincident(g17,g18)
    c: Coincident(g18,g19)
    c: Coincident(g19,g14)
    c: Equal(g14, g15-g19) x5
    c: PointOnObject(g14,g20)
    c: PointOnObject(g15,g20)
    c: PointOnObject(g16,g20)
    c: PointOnObject(g17,g20)
    c: PointOnObject(g18,g20)
    c: PointOnObject(g19,g20)
    c: Diameter(g20) = 7
    c: DistanceY(g-1,g20) = 7
    c: Vertical(g18)
    c: Distance(g17,g-2) = 1
    c: Coincident(g21,g22)
    c: Coincident(g22,g23)
    c: Coincident(g23,g24)
    c: Coincident(g24,g25)
    c: Coincident(g25,g26)
    c: Coincident(g26,g21)
    c: Equal(g21, g22-g26) x5
    c: PointOnObject(g21,g27)
    c: PointOnObject(g22,g27)
    c: PointOnObject(g23,g27)
    c: PointOnObject(g24,g27)
    c: PointOnObject(g25,g27)
    c: PointOnObject(g26,g27)
    c: Diameter(g27) = 7
    c: DistanceY(g-1,g27) = 7
    c: DistanceX(g21,g-1) = 1
    c: Vertical(g21)
    c: Coincident(g28,g29)
    c: Coincident(g29,g30)
    c: Coincident(g30,g31)
    c: Coincident(g31,g32)
    c: Coincident(g32,g33)
    c: Coincident(g33,g28)
    c: Equal(g28, g29-g33) x5
    c: PointOnObject(g28,g34)
    c: PointOnObject(g29,g34)
    c: PointOnObject(g30,g34)
    c: PointOnObject(g31,g34)
    c: PointOnObject(g32,g34)
    c: PointOnObject(g33,g34)
    c: PointOnObject(g34,g-1)
    c: Diameter(g34) = 7
    c: Vertical(g31)
    c: DistanceX(g34,g-1) = 8
    c: Coincident(g35,g36)
    c: Coincident(g36,g37)
    c: Coincident(g37,g38)
    c: Coincident(g38,g39)
    c: Coincident(g39,g40)
    c: Coincident(g40,g35)
    c: Equal(g35, g36-g40) x5
    c: PointOnObject(g35,g41)
    c: PointOnObject(g36,g41)
    c: PointOnObject(g37,g41)
    c: PointOnObject(g38,g41)
    c: PointOnObject(g39,g41)
    c: PointOnObject(g40,g41)
    c: Coincident(g42,g43)
    c: Coincident(g43,g44)
    c: Coincident(g44,g45)
    c: Coincident(g45,g46)
    c: Coincident(g46,g47)
    c: Coincident(g47,g42)
    c: Equal(g42, g43-g47) x5
    c: PointOnObject(g42,g48)
    c: PointOnObject(g43,g48)
    c: PointOnObject(g44,g48)
    c: PointOnObject(g45,g48)
    c: PointOnObject(g46,g48)
    c: PointOnObject(g47,g48)
    c: Equal(g41,g48)
    c: Diameter(g41) = 7
    c: Vertical(g39)
    c: Vertical(g43)
    c: Distance(g-2,g39) = 1
    c: Symmetric(g38,g43,g-2)
    c: Distance(g41,g-1) = 7
FEATURE [Part::Extrusion] Extrude729  label="hex331"
  Base = -> Sketch738
  Dir = (0,-1,2e-16)
  DirMode = 2
  FaceMakerClass = Part::FaceMakerBullseye
  FaceMakerMode = 3
  LengthFwd = 10
  LengthRev = 0
  Placement = pos=(-68,0,77) rot=(0,0,1;0rad)
  Solid = true
  Symmetric = false
FEATURE [Sketcher::SketchObject] Sketch739
  ArcFitTolerance = 1e-06
  FullyConstrained = true
  MakeInternals = false
  Placement = pos=(0,0,0) rot=(1,0,0;1.5708rad)
  sketch-geometry (49):
    g0: LineSegment StartX=1e-16 StartY=3.5 StartZ=0 EndX=-3.03109 EndY=1.75 EndZ=0
    g1: LineSegment StartX=-3.03109 StartY=1.75 StartZ=0 EndX=-3.03109 EndY=-1.75 EndZ=0
    g2: LineSegment StartX=-3.03109 StartY=-1.75 StartZ=0 EndX=-1e-16 EndY=-3.5 EndZ=0
    g3: LineSegment StartX=-1e-16 StartY=-3.5 StartZ=0 EndX=3.03109 EndY=-1.75 EndZ=0
    g4: LineSegment StartX=3.03109 StartY=-1.75 StartZ=0 EndX=3.03109 EndY=1.75 EndZ=0
    g5: LineSegment StartX=3.03109 StartY=1.75 StartZ=0 EndX=1e-16 EndY=3.5 EndZ=0
    g6: Circle [constr] CenterX=0 CenterY=0 CenterZ=0 NormalX=0 NormalY=0 NormalZ=1 AngleXU=0 Radius=3.5
    g7: LineSegment StartX=4.96892 StartY=-1.75002 StartZ=0 EndX=8.00002 EndY=-3.5 EndZ=0
    g8: LineSegment StartX=8.00002 StartY=-3.5 StartZ=0 EndX=11.0311 EndY=-1.74998 EndZ=0
    g9: LineSegment StartX=11.0311 StartY=-1.74998 StartZ=0 EndX=11.0311 EndY=1.75002 EndZ=0
    g10: LineSegment StartX=11.0311 StartY=1.75002 StartZ=0 EndX=7.99998 EndY=3.5 EndZ=0
    g11: LineSegment StartX=7.99998 StartY=3.5 StartZ=0 EndX=4.9689 EndY=1.74998 EndZ=0
    g12: LineSegment StartX=4.9689 StartY=1.74998 StartZ=0 EndX=4.96892 EndY=-1.75002 EndZ=0
    g13: Circle [constr] CenterX=8 CenterY=0 CenterZ=0 NormalX=0 NormalY=0 NormalZ=1 AngleXU=0 Radius=3.5
    g14: LineSegment StartX=4.03109 StartY=3.5 StartZ=0 EndX=7.06218 EndY=5.25 EndZ=0
    g15: LineSegment StartX=7.06218 StartY=5.25 StartZ=0 EndX=7.06218 EndY=8.75 EndZ=0
    g16: LineSegment StartX=7.06218 StartY=8.75 StartZ=0 EndX=4.03109 EndY=10.5 EndZ=0
    g17: LineSegment StartX=4.03109 StartY=10.5 StartZ=0 EndX=1 EndY=8.75 EndZ=0
    g18: LineSegment StartX=1 StartY=8.75 StartZ=0 EndX=1 EndY=5.25 EndZ=0
    g19: LineSegment StartX=1 StartY=5.25 StartZ=0 EndX=4.03109 EndY=3.5 EndZ=0
    g20: Circle [constr] CenterX=4.03109 CenterY=7 CenterZ=0 NormalX=0 NormalY=0 NormalZ=1 AngleXU=0 Radius=3.5
    g21: LineSegment StartX=-1 StartY=5.25 StartZ=0 EndX=-1 EndY=8.75 EndZ=0
    g22: LineSegment StartX=-1 StartY=8.75 StartZ=0 EndX=-4.03109 EndY=10.5 EndZ=0
    g23: LineSegment StartX=-4.03109 StartY=10.5 StartZ=0 EndX=-7.06218 EndY=8.75 EndZ=0
    g24: LineSegment StartX=-7.06218 StartY=8.75 StartZ=0 EndX=-7.06218 EndY=5.25 EndZ=0
    g25: LineSegment StartX=-7.06218 StartY=5.25 StartZ=0 EndX=-4.03109 EndY=3.5 EndZ=0
    g26: LineSegment StartX=-4.03109 StartY=3.5 StartZ=0 EndX=-1 EndY=5.25 EndZ=0
    g27: Circle [constr] CenterX=-4.03109 CenterY=7 CenterZ=0 NormalX=0 NormalY=0 NormalZ=1 AngleXU=0 Radius=3.5
    g28: LineSegment StartX=-4.96891 StartY=-1.75 StartZ=0 EndX=-4.96891 EndY=1.75 EndZ=0
    g29: LineSegment StartX=-4.96891 StartY=1.75 StartZ=0 EndX=-8 EndY=3.5 EndZ=0
    g30: LineSegment StartX=-8 StartY=3.5 StartZ=0 EndX=-11.0311 EndY=1.75 EndZ=0
    g31: LineSegment StartX=-11.0311 StartY=1.75 StartZ=0 EndX=-11.0311 EndY=-1.75 EndZ=0
    g32: LineSegment StartX=-11.0311 StartY=-1.75 StartZ=0 EndX=-8 EndY=-3.5 EndZ=0
    g33: LineSegment StartX=-8 StartY=-3.5 StartZ=0 EndX=-4.96891 EndY=-1.75 EndZ=0
    g34: Circle [constr] CenterX=-8 CenterY=0 CenterZ=0 NormalX=0 NormalY=0 NormalZ=1 AngleXU=0 Radius=3.5
    g35: LineSegment StartX=-4.03109 StartY=-3.5 StartZ=0 EndX=-7.06218 EndY=-5.25 EndZ=0
    g36: LineSegment StartX=-7.06218 StartY=-5.25 StartZ=0 EndX=-7.06218 EndY=-8.75 EndZ=0
    g37: LineSegment StartX=-7.06218 StartY=-8.75 StartZ=0 EndX=-4.03109 EndY=-10.5 EndZ=0
    g38: LineSegment StartX=-4.03109 StartY=-10.5 StartZ=0 EndX=-1 EndY=-8.75 EndZ=0
    g39: LineSegment StartX=-1 StartY=-8.75 StartZ=0 EndX=-1 EndY=-5.25 EndZ=0
    g40: LineSegment StartX=-1 StartY=-5.25 StartZ=0 EndX=-4.03109 EndY=-3.5 EndZ=0
    g41: Circle [constr] CenterX=-4.03109 CenterY=-7 CenterZ=0 NormalX=0 NormalY=0 NormalZ=1 AngleXU=0 Radius=3.5
    g42: LineSegment StartX=4.03109 StartY=-3.5 StartZ=0 EndX=1 EndY=-5.25 EndZ=0
    g43: LineSegment StartX=1 StartY=-5.25 StartZ=0 EndX=1 EndY=-8.75 EndZ=0
    g44: LineSegment StartX=1 StartY=-8.75 StartZ=0 EndX=4.03109 EndY=-10.5 EndZ=0
    g45: LineSegment StartX=4.03109 StartY=-10.5 StartZ=0 EndX=7.06218 EndY=-8.75 EndZ=0
    g46: LineSegment StartX=7.06218 StartY=-8.75 StartZ=0 EndX=7.06218 EndY=-5.25 EndZ=0
    g47: LineSegment StartX=7.06218 StartY=-5.25 StartZ=0 EndX=4.03109 EndY=-3.5 EndZ=0
    g48: Circle [constr] CenterX=4.03109 CenterY=-7 CenterZ=0 NormalX=0 NormalY=0 NormalZ=1 AngleXU=0 Radius=3.5
  constraints (117):
    c: Coincident(g0,g1)
    c: Coincident(g1,g2)
    c: Coincident(g2,g3)
    c: Coincident(g3,g4)
    c: Coincident(g4,g5)
    c: Coincident(g5,g0)
    c: Equal(g0, g1-g5) x5
    c: PointOnObject(g0,g6)
    c: PointOnObject(g1,g6)
    c: PointOnObject(g2,g6)
    c: PointOnObject(g3,g6)
    c: PointOnObject(g4,g6)
    c: PointOnObject(g5,g6)
    c: Coincident(g6,g-1)
    c: Diameter(g6) = 7
    c: PointOnObject(g0,g-2)
    c: Coincident(g7,g8)
    c: Coincident(g8,g9)
    c: Coincident(g9,g10)
    c: Coincident(g10,g11)
    c: Coincident(g11,g12)
    c: Coincident(g12,g7)
    c: Equal(g7, g8-g12) x5
    c: PointOnObject(g7,g13)
    c: PointOnObject(g8,g13)
    c: PointOnObject(g9,g13)
    c: PointOnObject(g10,g13)
    c: PointOnObject(g11,g13)
    c: PointOnObject(g12,g13)
    c: PointOnObject(g13,g-1)
    c: Diameter(g13) = 7
    c: Distance(g6,g13) = 8
    c: Horizontal(g0,g10)
    c: Coincident(g14,g15)
    c: Coincident(g15,g16)
    c: Coincident(g16,g17)
    c: Coincident(g17,g18)
    c: Coincident(g18,g19)
    c: Coincident(g19,g14)
    c: Equal(g14, g15-g19) x5
    c: PointOnObject(g14,g20)
    c: PointOnObject(g15,g20)
    c: PointOnObject(g16,g20)
    c: PointOnObject(g17,g20)
    c: PointOnObject(g18,g20)
    c: PointOnObject(g19,g20)
    c: Diameter(g20) = 7
    c: DistanceY(g-1,g20) = 7
    c: Vertical(g18)
    c: Distance(g17,g-2) = 1
    c: Coincident(g21,g22)
    c: Coincident(g22,g23)
    c: Coincident(g23,g24)
    c: Coincident(g24,g25)
    c: Coincident(g25,g26)
    c: Coincident(g26,g21)
    c: Equal(g21, g22-g26) x5
    c: PointOnObject(g21,g27)
    c: PointOnObject(g22,g27)
    c: PointOnObject(g23,g27)
    c: PointOnObject(g24,g27)
    c: PointOnObject(g25,g27)
    c: PointOnObject(g26,g27)
    c: Diameter(g27) = 7
    c: DistanceY(g-1,g27) = 7
    c: DistanceX(g21,g-1) = 1
    c: Vertical(g21)
    c: Coincident(g28,g29)
    c: Coincident(g29,g30)
    c: Coincident(g30,g31)
    c: Coincident(g31,g32)
    c: Coincident(g32,g33)
    c: Coincident(g33,g28)
    c: Equal(g28, g29-g33) x5
    c: PointOnObject(g28,g34)
    c: PointOnObject(g29,g34)
    c: PointOnObject(g30,g34)
    c: PointOnObject(g31,g34)
    c: PointOnObject(g32,g34)
    c: PointOnObject(g33,g34)
    c: PointOnObject(g34,g-1)
    c: Diameter(g34) = 7
    c: Vertical(g31)
    c: DistanceX(g34,g-1) = 8
    c: Coincident(g35,g36)
    c: Coincident(g36,g37)
    c: Coincident(g37,g38)
    c: Coincident(g38,g39)
    c: Coincident(g39,g40)
    c: Coincident(g40,g35)
    c: Equal(g35, g36-g40) x5
    c: PointOnObject(g35,g41)
    c: PointOnObject(g36,g41)
    c: PointOnObject(g37,g41)
    c: PointOnObject(g38,g41)
    c: PointOnObject(g39,g41)
    c: PointOnObject(g40,g41)
    c: Coincident(g42,g43)
    c: Coincident(g43,g44)
    c: Coincident(g44,g45)
    c: Coincident(g45,g46)
    c: Coincident(g46,g47)
    c: Coincident(g47,g42)
    c: Equal(g42, g43-g47) x5
    c: PointOnObject(g42,g48)
    c: PointOnObject(g43,g48)
    c: PointOnObject(g44,g48)
    c: PointOnObject(g45,g48)
    c: PointOnObject(g46,g48)
    c: PointOnObject(g47,g48)
    c: Equal(g41,g48)
    c: Diameter(g41) = 7
    c: Vertical(g39)
    c: Vertical(g43)
    c: Distance(g-2,g39) = 1
    c: Symmetric(g38,g43,g-2)
    c: Distance(g41,g-1) = 7
FEATURE [Part::Extrusion] Extrude730  label="hex332"
  Base = -> Sketch739
  Dir = (0,-1,2e-16)
  DirMode = 2
  FaceMakerClass = Part::FaceMakerBullseye
  FaceMakerMode = 3
  LengthFwd = 10
  LengthRev = 0
  Placement = pos=(68,0,77) rot=(0,0,1;0rad)
  Solid = true
  Symmetric = false
FEATURE [Sketcher::SketchObject] Sketch740
  ArcFitTolerance = 1e-06
  FullyConstrained = true
  MakeInternals = false
  Placement = pos=(0,0,0) rot=(1,0,0;1.5708rad)
  sketch-geometry (49):
    g0: LineSegment StartX=1e-16 StartY=3.5 StartZ=0 EndX=-3.03109 EndY=1.75 EndZ=0
    g1: LineSegment StartX=-3.03109 StartY=1.75 StartZ=0 EndX=-3.03109 EndY=-1.75 EndZ=0
    g2: LineSegment StartX=-3.03109 StartY=-1.75 StartZ=0 EndX=-1e-16 EndY=-3.5 EndZ=0
    g3: LineSegment StartX=-1e-16 StartY=-3.5 StartZ=0 EndX=3.03109 EndY=-1.75 EndZ=0
    g4: LineSegment StartX=3.03109 StartY=-1.75 StartZ=0 EndX=3.03109 EndY=1.75 EndZ=0
    g5: LineSegment StartX=3.03109 StartY=1.75 StartZ=0 EndX=1e-16 EndY=3.5 EndZ=0
    g6: Circle [constr] CenterX=0 CenterY=0 CenterZ=0 NormalX=0 NormalY=0 NormalZ=1 AngleXU=0 Radius=3.5
    g7: LineSegment StartX=4.96892 StartY=-1.75002 StartZ=0 EndX=8.00002 EndY=-3.5 EndZ=0
    g8: LineSegment StartX=8.00002 StartY=-3.5 StartZ=0 EndX=11.0311 EndY=-1.74998 EndZ=0
    g9: LineSegment StartX=11.0311 StartY=-1.74998 StartZ=0 EndX=11.0311 EndY=1.75002 EndZ=0
    g10: LineSegment StartX=11.0311 StartY=1.75002 StartZ=0 EndX=7.99998 EndY=3.5 EndZ=0
    g11: LineSegment StartX=7.99998 StartY=3.5 StartZ=0 EndX=4.9689 EndY=1.74998 EndZ=0
    g12: LineSegment StartX=4.9689 StartY=1.74998 StartZ=0 EndX=4.96892 EndY=-1.75002 EndZ=0
    g13: Circle [constr] CenterX=8 CenterY=0 CenterZ=0 NormalX=0 NormalY=0 NormalZ=1 AngleXU=0 Radius=3.5
    g14: LineSegment StartX=4.03109 StartY=3.5 StartZ=0 EndX=7.06218 EndY=5.25 EndZ=0
    g15: LineSegment StartX=7.06218 StartY=5.25 StartZ=0 EndX=7.06218 EndY=8.75 EndZ=0
    g16: LineSegment StartX=7.06218 StartY=8.75 StartZ=0 EndX=4.03109 EndY=10.5 EndZ=0
    g17: LineSegment StartX=4.03109 StartY=10.5 StartZ=0 EndX=1 EndY=8.75 EndZ=0
    g18: LineSegment StartX=1 StartY=8.75 StartZ=0 EndX=1 EndY=5.25 EndZ=0
    g19: LineSegment StartX=1 StartY=5.25 StartZ=0 EndX=4.03109 EndY=3.5 EndZ=0
    g20: Circle [constr] CenterX=4.03109 CenterY=7 CenterZ=0 NormalX=0 NormalY=0 NormalZ=1 AngleXU=0 Radius=3.5
    g21: LineSegment StartX=-1 StartY=5.25 StartZ=0 EndX=-1 EndY=8.75 EndZ=0
    g22: LineSegment StartX=-1 StartY=8.75 StartZ=0 EndX=-4.03109 EndY=10.5 EndZ=0
    g23: LineSegment StartX=-4.03109 StartY=10.5 StartZ=0 EndX=-7.06218 EndY=8.75 EndZ=0
    g24: LineSegment StartX=-7.06218 StartY=8.75 StartZ=0 EndX=-7.06218 EndY=5.25 EndZ=0
    g25: LineSegment StartX=-7.06218 StartY=5.25 StartZ=0 EndX=-4.03109 EndY=3.5 EndZ=0
    g26: LineSegment StartX=-4.03109 StartY=3.5 StartZ=0 EndX=-1 EndY=5.25 EndZ=0
    g27: Circle [constr] CenterX=-4.03109 CenterY=7 CenterZ=0 NormalX=0 NormalY=0 NormalZ=1 AngleXU=0 Radius=3.5
    g28: LineSegment StartX=-4.96891 StartY=-1.75 StartZ=0 EndX=-4.96891 EndY=1.75 EndZ=0
    g29: LineSegment StartX=-4.96891 StartY=1.75 StartZ=0 EndX=-8 EndY=3.5 EndZ=0
    g30: LineSegment StartX=-8 StartY=3.5 StartZ=0 EndX=-11.0311 EndY=1.75 EndZ=0
    g31: LineSegment StartX=-11.0311 StartY=1.75 StartZ=0 EndX=-11.0311 EndY=-1.75 EndZ=0
    g32: LineSegment StartX=-11.0311 StartY=-1.75 StartZ=0 EndX=-8 EndY=-3.5 EndZ=0
    g33: LineSegment StartX=-8 StartY=-3.5 StartZ=0 EndX=-4.96891 EndY=-1.75 EndZ=0
    g34: Circle [constr] CenterX=-8 CenterY=0 CenterZ=0 NormalX=0 NormalY=0 NormalZ=1 AngleXU=0 Radius=3.5
    g35: LineSegment StartX=-4.03109 StartY=-3.5 StartZ=0 EndX=-7.06218 EndY=-5.25 EndZ=0
    g36: LineSegment StartX=-7.06218 StartY=-5.25 StartZ=0 EndX=-7.06218 EndY=-8.75 EndZ=0
    g37: LineSegment StartX=-7.06218 StartY=-8.75 StartZ=0 EndX=-4.03109 EndY=-10.5 EndZ=0
    g38: LineSegment StartX=-4.03109 StartY=-10.5 StartZ=0 EndX=-1 EndY=-8.75 EndZ=0
    g39: LineSegment StartX=-1 StartY=-8.75 StartZ=0 EndX=-1 EndY=-5.25 EndZ=0
    g40: LineSegment StartX=-1 StartY=-5.25 StartZ=0 EndX=-4.03109 EndY=-3.5 EndZ=0
    g41: Circle [constr] CenterX=-4.03109 CenterY=-7 CenterZ=0 NormalX=0 NormalY=0 NormalZ=1 AngleXU=0 Radius=3.5
    g42: LineSegment StartX=4.03109 StartY=-3.5 StartZ=0 EndX=1 EndY=-5.25 EndZ=0
    g43: LineSegment StartX=1 StartY=-5.25 StartZ=0 EndX=1 EndY=-8.75 EndZ=0
    g44: LineSegment StartX=1 StartY=-8.75 StartZ=0 EndX=4.03109 EndY=-10.5 EndZ=0
    g45: LineSegment StartX=4.03109 StartY=-10.5 StartZ=0 EndX=7.06218 EndY=-8.75 EndZ=0
    g46: LineSegment StartX=7.06218 StartY=-8.75 StartZ=0 EndX=7.06218 EndY=-5.25 EndZ=0
    g47: LineSegment StartX=7.06218 StartY=-5.25 StartZ=0 EndX=4.03109 EndY=-3.5 EndZ=0
    g48: Circle [constr] CenterX=4.03109 CenterY=-7 CenterZ=0 NormalX=0 NormalY=0 NormalZ=1 AngleXU=0 Radius=3.5
  constraints (117):
    c: Coincident(g0,g1)
    c: Coincident(g1,g2)
    c: Coincident(g2,g3)
    c: Coincident(g3,g4)
    c: Coincident(g4,g5)
    c: Coincident(g5,g0)
    c: Equal(g0, g1-g5) x5
    c: PointOnObject(g0,g6)
    c: PointOnObject(g1,g6)
    c: PointOnObject(g2,g6)
    c: PointOnObject(g3,g6)
    c: PointOnObject(g4,g6)
    c: PointOnObject(g5,g6)
    c: Coincident(g6,g-1)
    c: Diameter(g6) = 7
    c: PointOnObject(g0,g-2)
    c: Coincident(g7,g8)
    c: Coincident(g8,g9)
    c: Coincident(g9,g10)
    c: Coincident(g10,g11)
    c: Coincident(g11,g12)
    c: Coincident(g12,g7)
    c: Equal(g7, g8-g12) x5
    c: PointOnObject(g7,g13)
    c: PointOnObject(g8,g13)
    c: PointOnObject(g9,g13)
    c: PointOnObject(g10,g13)
    c: PointOnObject(g11,g13)
    c: PointOnObject(g12,g13)
    c: PointOnObject(g13,g-1)
    c: Diameter(g13) = 7
    c: Distance(g6,g13) = 8
    c: Horizontal(g0,g10)
    c: Coincident(g14,g15)
    c: Coincident(g15,g16)
    c: Coincident(g16,g17)
    c: Coincident(g17,g18)
    c: Coincident(g18,g19)
    c: Coincident(g19,g14)
    c: Equal(g14, g15-g19) x5
    c: PointOnObject(g14,g20)
    c: PointOnObject(g15,g20)
    c: PointOnObject(g16,g20)
    c: PointOnObject(g17,g20)
    c: PointOnObject(g18,g20)
    c: PointOnObject(g19,g20)
    c: Diameter(g20) = 7
    c: DistanceY(g-1,g20) = 7
    c: Vertical(g18)
    c: Distance(g17,g-2) = 1
    c: Coincident(g21,g22)
    c: Coincident(g22,g23)
    c: Coincident(g23,g24)
    c: Coincident(g24,g25)
    c: Coincident(g25,g26)
    c: Coincident(g26,g21)
    c: Equal(g21, g22-g26) x5
    c: PointOnObject(g21,g27)
    c: PointOnObject(g22,g27)
    c: PointOnObject(g23,g27)
    c: PointOnObject(g24,g27)
    c: PointOnObject(g25,g27)
    c: PointOnObject(g26,g27)
    c: Diameter(g27) = 7
    c: DistanceY(g-1,g27) = 7
    c: DistanceX(g21,g-1) = 1
    c: Vertical(g21)
    c: Coincident(g28,g29)
    c: Coincident(g29,g30)
    c: Coincident(g30,g31)
    c: Coincident(g31,g32)
    c: Coincident(g32,g33)
    c: Coincident(g33,g28)
    c: Equal(g28, g29-g33) x5
    c: PointOnObject(g28,g34)
    c: PointOnObject(g29,g34)
    c: PointOnObject(g30,g34)
    c: PointOnObject(g31,g34)
    c: PointOnObject(g32,g34)
    c: PointOnObject(g33,g34)
    c: PointOnObject(g34,g-1)
    c: Diameter(g34) = 7
    c: Vertical(g31)
    c: DistanceX(g34,g-1) = 8
    c: Coincident(g35,g36)
    c: Coincident(g36,g37)
    c: Coincident(g37,g38)
    c: Coincident(g38,g39)
    c: Coincident(g39,g40)
    c: Coincident(g40,g35)
    c: Equal(g35, g36-g40) x5
    c: PointOnObject(g35,g41)
    c: PointOnObject(g36,g41)
    c: PointOnObject(g37,g41)
    c: PointOnObject(g38,g41)
    c: PointOnObject(g39,g41)
    c: PointOnObject(g40,g41)
    c: Coincident(g42,g43)
    c: Coincident(g43,g44)
    c: Coincident(g44,g45)
    c: Coincident(g45,g46)
    c: Coincident(g46,g47)
    c: Coincident(g47,g42)
    c: Equal(g42, g43-g47) x5
    c: PointOnObject(g42,g48)
    c: PointOnObject(g43,g48)
    c: PointOnObject(g44,g48)
    c: PointOnObject(g45,g48)
    c: PointOnObject(g46,g48)
    c: PointOnObject(g47,g48)
    c: Equal(g41,g48)
    c: Diameter(g41) = 7
    c: Vertical(g39)
    c: Vertical(g43)
    c: Distance(g-2,g39) = 1
    c: Symmetric(g38,g43,g-2)
    c: Distance(g41,g-1) = 7
FEATURE [Part::Extrusion] Extrude731  label="hex333"
  Base = -> Sketch740
  Dir = (0,-1,2e-16)
  DirMode = 2
  FaceMakerClass = Part::FaceMakerBullseye
  FaceMakerMode = 3
  LengthFwd = 10
  LengthRev = 0
  Placement = pos=(12,0,-119) rot=(0,0,1;0rad)
  Solid = true
  Symmetric = false
FEATURE [Sketcher::SketchObject] Sketch741
  ArcFitTolerance = 1e-06
  FullyConstrained = true
  MakeInternals = false
  Placement = pos=(0,0,0) rot=(1,0,0;1.5708rad)
  sketch-geometry (49):
    g0: LineSegment StartX=1e-16 StartY=3.5 StartZ=0 EndX=-3.03109 EndY=1.75 EndZ=0
    g1: LineSegment StartX=-3.03109 StartY=1.75 StartZ=0 EndX=-3.03109 EndY=-1.75 EndZ=0
    g2: LineSegment StartX=-3.03109 StartY=-1.75 StartZ=0 EndX=-1e-16 EndY=-3.5 EndZ=0
    g3: LineSegment StartX=-1e-16 StartY=-3.5 StartZ=0 EndX=3.03109 EndY=-1.75 EndZ=0
    g4: LineSegment StartX=3.03109 StartY=-1.75 StartZ=0 EndX=3.03109 EndY=1.75 EndZ=0
    g5: LineSegment StartX=3.03109 StartY=1.75 StartZ=0 EndX=1e-16 EndY=3.5 EndZ=0
    g6: Circle [constr] CenterX=0 CenterY=0 CenterZ=0 NormalX=0 NormalY=0 NormalZ=1 AngleXU=0 Radius=3.5
    g7: LineSegment StartX=4.96892 StartY=-1.75002 StartZ=0 EndX=8.00002 EndY=-3.5 EndZ=0
    g8: LineSegment StartX=8.00002 StartY=-3.5 StartZ=0 EndX=11.0311 EndY=-1.74998 EndZ=0
    g9: LineSegment StartX=11.0311 StartY=-1.74998 StartZ=0 EndX=11.0311 EndY=1.75002 EndZ=0
    g10: LineSegment StartX=11.0311 StartY=1.75002 StartZ=0 EndX=7.99998 EndY=3.5 EndZ=0
    g11: LineSegment StartX=7.99998 StartY=3.5 StartZ=0 EndX=4.9689 EndY=1.74998 EndZ=0
    g12: LineSegment StartX=4.9689 StartY=1.74998 StartZ=0 EndX=4.96892 EndY=-1.75002 EndZ=0
    g13: Circle [constr] CenterX=8 CenterY=0 CenterZ=0 NormalX=0 NormalY=0 NormalZ=1 AngleXU=0 Radius=3.5
    g14: LineSegment StartX=4.03109 StartY=3.5 StartZ=0 EndX=7.06218 EndY=5.25 EndZ=0
    g15: LineSegment StartX=7.06218 StartY=5.25 StartZ=0 EndX=7.06218 EndY=8.75 EndZ=0
    g16: LineSegment StartX=7.06218 StartY=8.75 StartZ=0 EndX=4.03109 EndY=10.5 EndZ=0
    g17: LineSegment StartX=4.03109 StartY=10.5 StartZ=0 EndX=1 EndY=8.75 EndZ=0
    g18: LineSegment StartX=1 StartY=8.75 StartZ=0 EndX=1 EndY=5.25 EndZ=0
    g19: LineSegment StartX=1 StartY=5.25 StartZ=0 EndX=4.03109 EndY=3.5 EndZ=0
    g20: Circle [constr] CenterX=4.03109 CenterY=7 CenterZ=0 NormalX=0 NormalY=0 NormalZ=1 AngleXU=0 Radius=3.5
    g21: LineSegment StartX=-1 StartY=5.25 StartZ=0 EndX=-1 EndY=8.75 EndZ=0
    g22: LineSegment StartX=-1 StartY=8.75 StartZ=0 EndX=-4.03109 EndY=10.5 EndZ=0
    g23: LineSegment StartX=-4.03109 StartY=10.5 StartZ=0 EndX=-7.06218 EndY=8.75 EndZ=0
    g24: LineSegment StartX=-7.06218 StartY=8.75 StartZ=0 EndX=-7.06218 EndY=5.25 EndZ=0
    g25: LineSegment StartX=-7.06218 StartY=5.25 StartZ=0 EndX=-4.03109 EndY=3.5 EndZ=0
    g26: LineSegment StartX=-4.03109 StartY=3.5 StartZ=0 EndX=-1 EndY=5.25 EndZ=0
    g27: Circle [constr] CenterX=-4.03109 CenterY=7 CenterZ=0 NormalX=0 NormalY=0 NormalZ=1 AngleXU=0 Radius=3.5
    g28: LineSegment StartX=-4.96891 StartY=-1.75 StartZ=0 EndX=-4.96891 EndY=1.75 EndZ=0
    g29: LineSegment StartX=-4.96891 StartY=1.75 StartZ=0 EndX=-8 EndY=3.5 EndZ=0
    g30: LineSegment StartX=-8 StartY=3.5 StartZ=0 EndX=-11.0311 EndY=1.75 EndZ=0
    g31: LineSegment StartX=-11.0311 StartY=1.75 StartZ=0 EndX=-11.0311 EndY=-1.75 EndZ=0
    g32: LineSegment StartX=-11.0311 StartY=-1.75 StartZ=0 EndX=-8 EndY=-3.5 EndZ=0
    g33: LineSegment StartX=-8 StartY=-3.5 StartZ=0 EndX=-4.96891 EndY=-1.75 EndZ=0
    g34: Circle [constr] CenterX=-8 CenterY=0 CenterZ=0 NormalX=0 NormalY=0 NormalZ=1 AngleXU=0 Radius=3.5
    g35: LineSegment StartX=-4.03109 StartY=-3.5 StartZ=0 EndX=-7.06218 EndY=-5.25 EndZ=0
    g36: LineSegment StartX=-7.06218 StartY=-5.25 StartZ=0 EndX=-7.06218 EndY=-8.75 EndZ=0
    g37: LineSegment StartX=-7.06218 StartY=-8.75 StartZ=0 EndX=-4.03109 EndY=-10.5 EndZ=0
    g38: LineSegment StartX=-4.03109 StartY=-10.5 StartZ=0 EndX=-1 EndY=-8.75 EndZ=0
    g39: LineSegment StartX=-1 StartY=-8.75 StartZ=0 EndX=-1 EndY=-5.25 EndZ=0
    g40: LineSegment StartX=-1 StartY=-5.25 StartZ=0 EndX=-4.03109 EndY=-3.5 EndZ=0
    g41: Circle [constr] CenterX=-4.03109 CenterY=-7 CenterZ=0 NormalX=0 NormalY=0 NormalZ=1 AngleXU=0 Radius=3.5
    g42: LineSegment StartX=4.03109 StartY=-3.5 StartZ=0 EndX=1 EndY=-5.25 EndZ=0
    g43: LineSegment StartX=1 StartY=-5.25 StartZ=0 EndX=1 EndY=-8.75 EndZ=0
    g44: LineSegment StartX=1 StartY=-8.75 StartZ=0 EndX=4.03109 EndY=-10.5 EndZ=0
    g45: LineSegment StartX=4.03109 StartY=-10.5 StartZ=0 EndX=7.06218 EndY=-8.75 EndZ=0
    g46: LineSegment StartX=7.06218 StartY=-8.75 StartZ=0 EndX=7.06218 EndY=-5.25 EndZ=0
    g47: LineSegment StartX=7.06218 StartY=-5.25 StartZ=0 EndX=4.03109 EndY=-3.5 EndZ=0
    g48: Circle [constr] CenterX=4.03109 CenterY=-7 CenterZ=0 NormalX=0 NormalY=0 NormalZ=1 AngleXU=0 Radius=3.5
  constraints (117):
    c: Coincident(g0,g1)
    c: Coincident(g1,g2)
    c: Coincident(g2,g3)
    c: Coincident(g3,g4)
    c: Coincident(g4,g5)
    c: Coincident(g5,g0)
    c: Equal(g0, g1-g5) x5
    c: PointOnObject(g0,g6)
    c: PointOnObject(g1,g6)
    c: PointOnObject(g2,g6)
    c: PointOnObject(g3,g6)
    c: PointOnObject(g4,g6)
    c: PointOnObject(g5,g6)
    c: Coincident(g6,g-1)
    c: Diameter(g6) = 7
    c: PointOnObject(g0,g-2)
    c: Coincident(g7,g8)
    c: Coincident(g8,g9)
    c: Coincident(g9,g10)
    c: Coincident(g10,g11)
    c: Coincident(g11,g12)
    c: Coincident(g12,g7)
    c: Equal(g7, g8-g12) x5
    c: PointOnObject(g7,g13)
    c: PointOnObject(g8,g13)
    c: PointOnObject(g9,g13)
    c: PointOnObject(g10,g13)
    c: PointOnObject(g11,g13)
    c: PointOnObject(g12,g13)
    c: PointOnObject(g13,g-1)
    c: Diameter(g13) = 7
    c: Distance(g6,g13) = 8
    c: Horizontal(g0,g10)
    c: Coincident(g14,g15)
    c: Coincident(g15,g16)
    c: Coincident(g16,g17)
    c: Coincident(g17,g18)
    c: Coincident(g18,g19)
    c: Coincident(g19,g14)
    c: Equal(g14, g15-g19) x5
    c: PointOnObject(g14,g20)
    c: PointOnObject(g15,g20)
    c: PointOnObject(g16,g20)
    c: PointOnObject(g17,g20)
    c: PointOnObject(g18,g20)
    c: PointOnObject(g19,g20)
    c: Diameter(g20) = 7
    c: DistanceY(g-1,g20) = 7
    c: Vertical(g18)
    c: Distance(g17,g-2) = 1
    c: Coincident(g21,g22)
    c: Coincident(g22,g23)
    c: Coincident(g23,g24)
    c: Coincident(g24,g25)
    c: Coincident(g25,g26)
    c: Coincident(g26,g21)
    c: Equal(g21, g22-g26) x5
    c: PointOnObject(g21,g27)
    c: PointOnObject(g22,g27)
    c: PointOnObject(g23,g27)
    c: PointOnObject(g24,g27)
    c: PointOnObject(g25,g27)
    c: PointOnObject(g26,g27)
    c: Diameter(g27) = 7
    c: DistanceY(g-1,g27) = 7
    c: DistanceX(g21,g-1) = 1
    c: Vertical(g21)
    c: Coincident(g28,g29)
    c: Coincident(g29,g30)
    c: Coincident(g30,g31)
    c: Coincident(g31,g32)
    c: Coincident(g32,g33)
    c: Coincident(g33,g28)
    c: Equal(g28, g29-g33) x5
    c: PointOnObject(g28,g34)
    c: PointOnObject(g29,g34)
    c: PointOnObject(g30,g34)
    c: PointOnObject(g31,g34)
    c: PointOnObject(g32,g34)
    c: PointOnObject(g33,g34)
    c: PointOnObject(g34,g-1)
    c: Diameter(g34) = 7
    c: Vertical(g31)
    c: DistanceX(g34,g-1) = 8
    c: Coincident(g35,g36)
    c: Coincident(g36,g37)
    c: Coincident(g37,g38)
    c: Coincident(g38,g39)
    c: Coincident(g39,g40)
    c: Coincident(g40,g35)
    c: Equal(g35, g36-g40) x5
    c: PointOnObject(g35,g41)
    c: PointOnObject(g36,g41)
    c: PointOnObject(g37,g41)
    c: PointOnObject(g38,g41)
    c: PointOnObject(g39,g41)
    c: PointOnObject(g40,g41)
    c: Coincident(g42,g43)
    c: Coincident(g43,g44)
    c: Coincident(g44,g45)
    c: Coincident(g45,g46)
    c: Coincident(g46,g47)
    c: Coincident(g47,g42)
    c: Equal(g42, g43-g47) x5
    c: PointOnObject(g42,g48)
    c: PointOnObject(g43,g48)
    c: PointOnObject(g44,g48)
    c: PointOnObject(g45,g48)
    c: PointOnObject(g46,g48)
    c: PointOnObject(g47,g48)
    c: Equal(g41,g48)
    c: Diameter(g41) = 7
    c: Vertical(g39)
    c: Vertical(g43)
    c: Distance(g-2,g39) = 1
    c: Symmetric(g38,g43,g-2)
    c: Distance(g41,g-1) = 7
FEATURE [Part::Extrusion] Extrude732  label="hex334"
  Base = -> Sketch741
  Dir = (0,-1,2e-16)
  DirMode = 2
  FaceMakerClass = Part::FaceMakerBullseye
  FaceMakerMode = 3
  LengthFwd = 10
  LengthRev = 0
  Placement = pos=(-12,0,-119) rot=(0,0,1;0rad)
  Solid = true
  Symmetric = false
FEATURE [Part::MultiFuse] Fusion566
  Refine = true
  Shapes = -> [Extrude716,Extrude717,Extrude718,Extrude719,Extrude720,Extrude721,Extrude722,Extrude723,Extrude724,Extrude725,Extrude726,Extrude727,Extrude728,Extrude729,Extrude730,Extrude731,Extrude732]
FEATURE [Part::MultiFuse] Fusion567  label="hexAll001"
  Refine = true
  Shapes = -> [Fusion563,Fusion564,Fusion565,Fusion566]
FEATURE [Sketcher::SketchObject] Sketch742
  ArcFitTolerance = 1e-06
  FullyConstrained = true
  MakeInternals = false
  Placement = pos=(0,0,0) rot=(1,0,0;1.5708rad)
  sketch-geometry (14):
    g0: LineSegment StartX=-4.8e-15 StartY=114.144 StartZ=0 EndX=-98.8513 EndY=57.0718 EndZ=0
    g1: LineSegment StartX=-98.8513 StartY=57.0718 StartZ=0 EndX=-98.8513 EndY=-57.0718 EndZ=0
    g2: LineSegment StartX=-98.8513 StartY=-57.0718 StartZ=0 EndX=1.52e-14 EndY=-114.144 EndZ=0
    g3: LineSegment StartX=1.52e-14 StartY=-114.144 StartZ=0 EndX=98.8513 EndY=-57.0718 EndZ=0
    g4: LineSegment StartX=98.8513 StartY=-57.0718 StartZ=0 EndX=98.8513 EndY=57.0718 EndZ=0
    g5: LineSegment StartX=98.8513 StartY=57.0718 StartZ=0 EndX=-4.8e-15 EndY=114.144 EndZ=0
    g6: Circle [constr] CenterX=0 CenterY=0 CenterZ=0 NormalX=0 NormalY=0 NormalZ=1 AngleXU=0 Radius=114.144
    g7: LineSegment StartX=0 StartY=128 StartZ=0 EndX=-110.851 EndY=64 EndZ=0
    g8: LineSegment StartX=-110.851 StartY=64 StartZ=0 EndX=-110.851 EndY=-64 EndZ=0
    g9: LineSegment StartX=-110.851 StartY=-64 StartZ=0 EndX=0 EndY=-128 EndZ=0
    g10: LineSegment StartX=0 StartY=-128 StartZ=0 EndX=110.851 EndY=-64 EndZ=0
    g11: LineSegment StartX=110.851 StartY=-64 StartZ=0 EndX=110.851 EndY=64 EndZ=0
    g12: LineSegment StartX=110.851 StartY=64 StartZ=0 EndX=0 EndY=128 EndZ=0
    g13: Circle [constr] CenterX=0 CenterY=0 CenterZ=0 NormalX=0 NormalY=0 NormalZ=1 AngleXU=0 Radius=128
  constraints (32):
    c: Coincident(g0,g1)
    c: Coincident(g1,g2)
    c: Coincident(g2,g3)
    c: Coincident(g3,g4)
    c: Coincident(g4,g5)
    c: Coincident(g5,g0)
    c: Equal(g0, g1-g5) x5
    c: PointOnObject(g0,g6)
    c: PointOnObject(g1,g6)
    c: PointOnObject(g2,g6)
    c: PointOnObject(g3,g6)
    c: PointOnObject(g4,g6)
    c: PointOnObject(g5,g6)
    c: Coincident(g6,g-1)
    c: PointOnObject(g5,g-2)
    c: Coincident(g7,g8)
    c: Coincident(g8,g9)
    c: Coincident(g9,g10)
    c: Coincident(g10,g11)
    c: Coincident(g11,g12)
    c: Coincident(g12,g7)
    c: Equal(g7, g8-g12) x5
    c: PointOnObject(g7,g13)
    c: PointOnObject(g8,g13)
    c: PointOnObject(g9,g13)
    c: PointOnObject(g10,g13)
    c: PointOnObject(g11,g13)
    c: PointOnObject(g12,g13)
    c: Coincident(g13,g6)
    c: PointOnObject(g12,g-2)
    c: DistanceX(g7,g0) = 12
    c: DistanceY(g8,g8) = 128
FEATURE [Part::Extrusion] Extrude733  label="hexMeshBorder001"
  Base = -> Sketch742
  Dir = (0,-1,2e-16)
  DirMode = 2
  FaceMakerClass = Part::FaceMakerBullseye
  FaceMakerMode = 3
  LengthFwd = 10
  LengthRev = 0
  Solid = true
  Symmetric = false
FEATURE [Sketcher::SketchObject] Sketch743
  ArcFitTolerance = 1e-06
  FullyConstrained = true
  MakeInternals = false
  Placement = pos=(0,0,0) rot=(1,0,0;1.5708rad)
  sketch-geometry (8):
    g0: Circle CenterX=0 CenterY=0 CenterZ=0 NormalX=0 NormalY=0 NormalZ=1 AngleXU=0 Radius=1.5
    g1: LineSegment StartX=-8.01073 StartY=-4.625 StartZ=0 EndX=-2e-16 EndY=-9.25 EndZ=0
    g2: LineSegment StartX=-2e-16 StartY=-9.25 StartZ=0 EndX=8.01073 EndY=-4.625 EndZ=0
    g3: LineSegment StartX=8.01073 StartY=-4.625 StartZ=0 EndX=8.01073 EndY=4.625 EndZ=0
    g4: LineSegment StartX=8.01073 StartY=4.625 StartZ=0 EndX=-1.5e-15 EndY=9.25 EndZ=0
    g5: LineSegment StartX=-1.5e-15 StartY=9.25 StartZ=0 EndX=-8.01073 EndY=4.625 EndZ=0
    g6: LineSegment StartX=-8.01073 StartY=4.625 StartZ=0 EndX=-8.01073 EndY=-4.625 EndZ=0
    g7: Circle [constr] CenterX=0 CenterY=0 CenterZ=0 NormalX=0 NormalY=0 NormalZ=1 AngleXU=0 Radius=9.25
  constraints (18):
    c: Coincident(g0,g-1)
    c: Diameter(g0) = 3
    c: Coincident(g1,g2)
    c: Coincident(g2,g3)
    c: Coincident(g3,g4)
    c: Coincident(g4,g5)
    c: Coincident(g5,g6)
    c: Coincident(g6,g1)
    c: Equal(g1, g2-g6) x5
    c: PointOnObject(g1,g7)
    c: PointOnObject(g2,g7)
    c: PointOnObject(g3,g7)
    c: PointOnObject(g4,g7)
    c: PointOnObject(g5,g7)
    c: PointOnObject(g6,g7)
    c: Coincident(g7,g0)
    c: Vertical(g6)
    c: DistanceY(g6,g6) = 9.25
FEATURE [Part::Extrusion] Extrude734  label="wheelHolderCut001"
  Base = -> Sketch743
  Dir = (0,-1,2e-16)
  DirMode = 2
  FaceMakerClass = Part::FaceMakerBullseye
  FaceMakerMode = 3
  LengthFwd = 20
  LengthRev = 0
  Placement = pos=(0,-10,0) rot=(0,0,1;0rad)
  Reversed = true
  Solid = true
  Symmetric = false
FEATURE [Sketcher::SketchObject] Sketch744
  ArcFitTolerance = 1e-06
  FullyConstrained = true
  MakeInternals = false
  Placement = pos=(0,0,0) rot=(1,0,0;1.5708rad)
  sketch-geometry (7):
    g0: LineSegment StartX=5.5e-15 StartY=115 StartZ=0 EndX=-99.5929 EndY=57.5 EndZ=0
    g1: LineSegment StartX=-99.5929 StartY=57.5 StartZ=0 EndX=-99.5929 EndY=-57.5 EndZ=0
    g2: LineSegment StartX=-99.5929 StartY=-57.5 StartZ=0 EndX=1.1405e-12 EndY=-115 EndZ=0
    g3: LineSegment StartX=1.1405e-12 StartY=-115 StartZ=0 EndX=99.5929 EndY=-57.5 EndZ=0
    g4: LineSegment StartX=99.5929 StartY=-57.5 StartZ=0 EndX=99.5929 EndY=57.5 EndZ=0
    g5: LineSegment StartX=99.5929 StartY=57.5 StartZ=0 EndX=5.5e-15 EndY=115 EndZ=0
    g6: Circle [constr] CenterX=0 CenterY=0 CenterZ=0 NormalX=0 NormalY=0 NormalZ=1 AngleXU=0 Radius=115
  constraints (16):
    c: Coincident(g0,g1)
    c: Coincident(g1,g2)
    c: Coincident(g2,g3)
    c: Coincident(g3,g4)
    c: Coincident(g4,g5)
    c: Coincident(g5,g0)
    c: Equal(g0, g1-g5) x5
    c: PointOnObject(g0,g6)
    c: PointOnObject(g1,g6)
    c: PointOnObject(g2,g6)
    c: PointOnObject(g3,g6)
    c: PointOnObject(g4,g6)
    c: PointOnObject(g5,g6)
    c: Coincident(g6,g-1)
    c: PointOnObject(g5,g-2)
    c: DistanceY(g1,g1) = 115
FEATURE [Part::Extrusion] Extrude735  label="meshKeep001"
  Base = -> Sketch744
  Dir = (0,-1,2e-16)
  DirMode = 2
  FaceMakerClass = Part::FaceMakerBullseye
  FaceMakerMode = 3
  LengthFwd = 10
  LengthRev = 0
  Solid = true
  Symmetric = false
FEATURE [Part::Cut] Cut008  label="mesh003"
  Base = -> Extrude735
  Refine = true
  Tool = -> Fusion567
FEATURE [Part::MultiFuse] Fusion562  label="mesh005"
  Refine = true
  Shapes = -> [Cut008,Extrude734,Extrude733]
FEATURE [Part::Cut] Cut009  label="mesh004"
  Base = -> Fusion562
  Placement = pos=(0,-60,0) rot=(0,0,1;0rad)
  Refine = true
  Tool = -> Fusion568
FEATURE [Part::Feature] Part__Feature059  label="ips7100"
  Placement = pos=(-24,0,222) rot=(0.999993,-0.003655,0;3.14159rad)
  shape: bbox 48.14 x 14.05 x 44.14 mm, 1935 faces (baked)
FEATURE [Part::Compound] Compound  label="ips7100s"
  Links = -> [Part__Feature059]
  Placement = pos=(40,-48,45) rot=(-0.003095,0.003095,-0.99999;1.56463rad)
FEATURE [Sketcher::SketchObject] Sketch
  ArcFitTolerance = 1e-06
  FullyConstrained = true
  MakeInternals = false
  Placement = pos=(0,0,0) rot=(1,0,0;1.5708rad)
  sketch-geometry (14):
    g0: LineSegment StartX=4.9e-15 StartY=130 StartZ=0 EndX=-112.583 EndY=65 EndZ=0
    g1: LineSegment StartX=-112.583 StartY=65 StartZ=0 EndX=-112.583 EndY=-65 EndZ=0
    g2: LineSegment StartX=-112.583 StartY=-65 StartZ=0 EndX=-4.9e-15 EndY=-130 EndZ=0
    g3: LineSegment StartX=-4.9e-15 StartY=-130 StartZ=0 EndX=112.583 EndY=-65 EndZ=0
    g4: LineSegment StartX=112.583 StartY=-65 StartZ=0 EndX=112.583 EndY=65 EndZ=0
    g5: LineSegment StartX=112.583 StartY=65 StartZ=0 EndX=4.9e-15 EndY=130 EndZ=0
    g6: Circle [constr] CenterX=0 CenterY=0 CenterZ=0 NormalX=0 NormalY=0 NormalZ=1 AngleXU=0 Radius=130
    g7: LineSegment StartX=-5e-15 StartY=135 StartZ=0 EndX=-116.913 EndY=67.5 EndZ=0
    g8: LineSegment StartX=-116.913 StartY=67.5 StartZ=0 EndX=-116.913 EndY=-67.5 EndZ=0
    g9: LineSegment StartX=-116.913 StartY=-67.5 StartZ=0 EndX=4.2e-15 EndY=-135 EndZ=0
    g10: LineSegment StartX=4.2e-15 StartY=-135 StartZ=0 EndX=116.913 EndY=-67.5 EndZ=0
    g11: LineSegment StartX=116.913 StartY=-67.5 StartZ=0 EndX=116.913 EndY=67.5 EndZ=0
    g12: LineSegment StartX=116.913 StartY=67.5 StartZ=0 EndX=-5e-15 EndY=135 EndZ=0
    g13: Circle [constr] CenterX=0 CenterY=0 CenterZ=0 NormalX=0 NormalY=0 NormalZ=1 AngleXU=0 Radius=135
  constraints (32):
    c: Coincident(g0,g1)
    c: Coincident(g1,g2)
    c: Coincident(g2,g3)
    c: Coincident(g3,g4)
    c: Coincident(g4,g5)
    c: Coincident(g5,g0)
    c: Equal(g0, g1-g5) x5
    c: PointOnObject(g0,g6)
    c: PointOnObject(g1,g6)
    c: PointOnObject(g2,g6)
    c: PointOnObject(g3,g6)
    c: PointOnObject(g4,g6)
    c: PointOnObject(g5,g6)
    c: Coincident(g6,g-1)
    c: PointOnObject(g5,g-2)
    c: Diameter(g6) = 260
    c: Coincident(g7,g8)
    c: Coincident(g8,g9)
    c: Coincident(g9,g10)
    c: Coincident(g10,g11)
    c: Coincident(g11,g12)
    c: Coincident(g12,g7)
    c: Equal(g7, g8-g12) x5
    c: PointOnObject(g7,g13)
    c: PointOnObject(g8,g13)
    c: PointOnObject(g9,g13)
    c: PointOnObject(g10,g13)
    c: PointOnObject(g11,g13)
    c: PointOnObject(g12,g13)
    c: Coincident(g13,g6)
    c: PointOnObject(g12,g-2)
    c: Diameter(g13) = 270
FEATURE [Part::Extrusion] Extrude  label="hexShell"
  Base = -> Sketch
  Dir = (0,-1,2e-16)
  DirMode = 2
  FaceMakerClass = Part::FaceMakerBullseye
  FaceMakerMode = 3
  LengthFwd = 70
  LengthRev = 0
  Solid = true
  Symmetric = false
FEATURE [Sketcher::SketchObject] Sketch393
  ArcFitTolerance = 1e-06
  FullyConstrained = true
  MakeInternals = false
  Placement = pos=(0,0,0) rot=(1,0,0;1.5708rad)
  sketch-geometry (14):
    g0: LineSegment StartX=-1.8e-15 StartY=125 StartZ=0 EndX=-108.253 EndY=62.5 EndZ=0
    g1: LineSegment StartX=-108.253 StartY=62.5 StartZ=0 EndX=-108.253 EndY=-62.5 EndZ=0
    g2: LineSegment StartX=-108.253 StartY=-62.5 StartZ=0 EndX=2e-16 EndY=-125 EndZ=0
    g3: LineSegment StartX=2e-16 StartY=-125 StartZ=0 EndX=108.253 EndY=-62.5 EndZ=0
    g4: LineSegment StartX=108.253 StartY=-62.5 StartZ=0 EndX=108.253 EndY=62.5 EndZ=0
    g5: LineSegment StartX=108.253 StartY=62.5 StartZ=0 EndX=-1.8e-15 EndY=125 EndZ=0
    g6: Circle [constr] CenterX=0 CenterY=0 CenterZ=0 NormalX=0 NormalY=0 NormalZ=1 AngleXU=0 Radius=125
    g7: LineSegment StartX=4.7e-15 StartY=130 StartZ=0 EndX=-112.583 EndY=65 EndZ=0
    g8: LineSegment StartX=-112.583 StartY=65 StartZ=0 EndX=-112.583 EndY=-65 EndZ=0
    g9: LineSegment StartX=-112.583 StartY=-65 StartZ=0 EndX=5.5e-15 EndY=-130 EndZ=0
    g10: LineSegment StartX=5.5e-15 StartY=-130 StartZ=0 EndX=112.583 EndY=-65 EndZ=0
    g11: LineSegment StartX=112.583 StartY=-65 StartZ=0 EndX=112.583 EndY=65 EndZ=0
    g12: LineSegment StartX=112.583 StartY=65 StartZ=0 EndX=4.7e-15 EndY=130 EndZ=0
    g13: Circle [constr] CenterX=0 CenterY=0 CenterZ=0 NormalX=0 NormalY=0 NormalZ=1 AngleXU=0 Radius=130
  constraints (32):
    c: Coincident(g0,g1)
    c: Coincident(g1,g2)
    c: Coincident(g2,g3)
    c: Coincident(g3,g4)
    c: Coincident(g4,g5)
    c: Coincident(g5,g0)
    c: Equal(g0, g1-g5) x5
    c: PointOnObject(g0,g6)
    c: PointOnObject(g1,g6)
    c: PointOnObject(g2,g6)
    c: PointOnObject(g3,g6)
    c: PointOnObject(g4,g6)
    c: PointOnObject(g5,g6)
    c: Coincident(g6,g-1)
    c: PointOnObject(g5,g-2)
    c: Diameter(g6) = 250
    c: Coincident(g7,g8)
    c: Coincident(g8,g9)
    c: Coincident(g9,g10)
    c: Coincident(g10,g11)
    c: Coincident(g11,g12)
    c: Coincident(g12,g7)
    c: Equal(g7, g8-g12) x5
    c: PointOnObject(g7,g13)
    c: PointOnObject(g8,g13)
    c: PointOnObject(g9,g13)
    c: PointOnObject(g10,g13)
    c: PointOnObject(g11,g13)
    c: PointOnObject(g12,g13)
    c: Coincident(g13,g6)
    c: PointOnObject(g12,g-2)
    c: Diameter(g13) = 260
FEATURE [Part::Extrusion] Extrude385  label="hexShellinner"
  Base = -> Sketch393
  Dir = (0,-1,2e-16)
  DirMode = 2
  FaceMakerClass = Part::FaceMakerBullseye
  FaceMakerMode = 3
  LengthFwd = 10
  LengthRev = 0
  Placement = pos=(0,-49.5,0) rot=(0,0,1;0rad)
  Solid = true
  Symmetric = false
FEATURE [Part::MultiFuse] Fusion  label="frontHex"
  Refine = true
  Shapes = -> [Extrude,Extrude385]
FEATURE [Part::Cylinder] Cylinder006
  Angle = 360
  AttacherType = Attacher::AttachEngine3D
  FirstAngle = 0
  Height = 60
  Placement = pos=(30,165,-5) rot=(0,1,0;4.71239rad)
  Radius = 2.15
  SecondAngle = 0
FEATURE [Sketcher::SketchObject] Sketch745
  ArcFitTolerance = 1e-06
  FullyConstrained = true
  MakeInternals = false
  Placement = pos=(0,-150,0) rot=(1,0,0;1.5708rad)
  sketch-geometry (7):
    g0: LineSegment StartX=-4.2e-15 StartY=135 StartZ=0 EndX=-116.913 EndY=67.5 EndZ=0
    g1: LineSegment StartX=-116.913 StartY=67.5 StartZ=0 EndX=-116.913 EndY=-67.5 EndZ=0
    g2: LineSegment StartX=-116.913 StartY=-67.5 StartZ=0 EndX=1.92e-14 EndY=-135 EndZ=0
    g3: LineSegment StartX=1.92e-14 StartY=-135 StartZ=0 EndX=116.913 EndY=-67.5 EndZ=0
    g4: LineSegment StartX=116.913 StartY=-67.5 StartZ=0 EndX=116.913 EndY=67.5 EndZ=0
    g5: LineSegment StartX=116.913 StartY=67.5 StartZ=0 EndX=-4.2e-15 EndY=135 EndZ=0
    g6: Circle [constr] CenterX=0 CenterY=0 CenterZ=0 NormalX=0 NormalY=0 NormalZ=1 AngleXU=0 Radius=135
  constraints (16):
    c: Coincident(g0,g1)
    c: Coincident(g1,g2)
    c: Coincident(g2,g3)
    c: Coincident(g3,g4)
    c: Coincident(g4,g5)
    c: Coincident(g5,g0)
    c: Equal(g0, g1-g5) x5
    c: PointOnObject(g0,g6)
    c: PointOnObject(g1,g6)
    c: PointOnObject(g2,g6)
    c: PointOnObject(g3,g6)
    c: PointOnObject(g4,g6)
    c: PointOnObject(g5,g6)
    c: PointOnObject(g5,g-2)
    c: Diameter(g6) = 270
    c: Coincident(g6,g-1)
FEATURE [Sketcher::SketchObject] Sketch746
  ArcFitTolerance = 1e-06
  FullyConstrained = true
  MakeInternals = false
  Placement = pos=(0,0,0) rot=(1,0,0;1.5708rad)
  sketch-geometry (8):
    g0: Circle [constr] CenterX=0 CenterY=0 CenterZ=0 NormalX=0 NormalY=0 NormalZ=1 AngleXU=0 Radius=20
    g1: LineSegment StartX=0 StartY=25 StartZ=0 EndX=-21.6506 EndY=12.5 EndZ=0
    g2: LineSegment StartX=-21.6506 StartY=12.5 StartZ=0 EndX=-21.6506 EndY=-12.5 EndZ=0
    g3: LineSegment StartX=-21.6506 StartY=-12.5 StartZ=0 EndX=-1.7133e-12 EndY=-25 EndZ=0
    g4: LineSegment StartX=-1.7133e-12 StartY=-25 StartZ=0 EndX=21.6506 EndY=-12.5 EndZ=0
    g5: LineSegment StartX=21.6506 StartY=-12.5 StartZ=0 EndX=21.6506 EndY=12.5 EndZ=0
    g6: LineSegment StartX=21.6506 StartY=12.5 StartZ=0 EndX=1e-15 EndY=25 EndZ=0
    g7: Circle [constr] CenterX=0 CenterY=0 CenterZ=0 NormalX=0 NormalY=0 NormalZ=1 AngleXU=0 Radius=25
  constraints (18):
    c: Coincident(g0,g-1)
    c: Diameter(g0) = 40
    c: Coincident(g1,g2)
    c: Coincident(g2,g3)
    c: Coincident(g3,g4)
    c: Coincident(g4,g5)
    c: Coincident(g5,g6)
    c: Coincident(g6,g1)
    c: Equal(g1, g2-g6) x5
    c: PointOnObject(g1,g7)
    c: PointOnObject(g2,g7)
    c: PointOnObject(g3,g7)
    c: PointOnObject(g4,g7)
    c: PointOnObject(g5,g7)
    c: PointOnObject(g6,g7)
    c: Coincident(g7,g0)
    c: PointOnObject(g6,g-2)
    c: Diameter(g7) = 50
FEATURE [Part::Loft] Loft005
  Closed = false
  MaxDegree = 5
  Ruled = false
  Sections = -> [Sketch745,Sketch746]
  Solid = true
FEATURE [Sketcher::SketchObject] Sketch747
  ArcFitTolerance = 1e-06
  FullyConstrained = true
  MakeInternals = false
  Placement = pos=(0,-150,0) rot=(1,0,0;1.5708rad)
  sketch-geometry (8):
    g0: LineSegment StartX=4.7e-15 StartY=130 StartZ=0 EndX=-112.583 EndY=65 EndZ=0
    g1: LineSegment StartX=-112.583 StartY=65 StartZ=0 EndX=-112.583 EndY=-65 EndZ=0
    g2: LineSegment StartX=-112.583 StartY=-65 StartZ=0 EndX=-1.13e-14 EndY=-130 EndZ=0
    g3: LineSegment StartX=-1.13e-14 StartY=-130 StartZ=0 EndX=112.583 EndY=-65 EndZ=0
    g4: LineSegment StartX=112.583 StartY=-65 StartZ=0 EndX=112.583 EndY=65 EndZ=0
    g5: LineSegment StartX=112.583 StartY=65 StartZ=0 EndX=4.7e-15 EndY=130 EndZ=0
    g6: Circle [constr] CenterX=0 CenterY=0 CenterZ=0 NormalX=0 NormalY=0 NormalZ=1 AngleXU=0 Radius=130
    g7: Circle [constr] CenterX=0 CenterY=0 CenterZ=0 NormalX=0 NormalY=0 NormalZ=1 AngleXU=0 Radius=135
  constraints (18):
    c: Coincident(g0,g1)
    c: Coincident(g1,g2)
    c: Coincident(g2,g3)
    c: Coincident(g3,g4)
    c: Coincident(g4,g5)
    c: Coincident(g5,g0)
    c: Equal(g0, g1-g5) x5
    c: PointOnObject(g0,g6)
    c: PointOnObject(g1,g6)
    c: PointOnObject(g2,g6)
    c: PointOnObject(g3,g6)
    c: PointOnObject(g4,g6)
    c: PointOnObject(g5,g6)
    c: Coincident(g6,g-1)
    c: PointOnObject(g5,g-2)
    c: Diameter(g6) = 260
    c: Coincident(g7,g6)
    c: Diameter(g7) = 270
FEATURE [Sketcher::SketchObject] Sketch748
  ArcFitTolerance = 1e-06
  FullyConstrained = true
  MakeInternals = false
  Placement = pos=(0,0,0) rot=(1,0,0;1.5708rad)
  sketch-geometry (8):
    g0: LineSegment StartX=0 StartY=20 StartZ=0 EndX=-17.3205 EndY=10 EndZ=0
    g1: LineSegment StartX=-17.3205 StartY=10 StartZ=0 EndX=-17.3205 EndY=-10 EndZ=0
    g2: LineSegment StartX=-17.3205 StartY=-10 StartZ=0 EndX=-2.7e-15 EndY=-20 EndZ=0
    g3: LineSegment StartX=-2.7e-15 StartY=-20 StartZ=0 EndX=17.3205 EndY=-10 EndZ=0
    g4: LineSegment StartX=17.3205 StartY=-10 StartZ=0 EndX=17.3205 EndY=10 EndZ=0
    g5: LineSegment StartX=17.3205 StartY=10 StartZ=0 EndX=4e-16 EndY=20 EndZ=0
    g6: Circle [constr] CenterX=0 CenterY=0 CenterZ=0 NormalX=0 NormalY=0 NormalZ=1 AngleXU=0 Radius=20
    g7: Circle [constr] CenterX=0 CenterY=0 CenterZ=0 NormalX=0 NormalY=0 NormalZ=1 AngleXU=0 Radius=25
  constraints (18):
    c: Coincident(g0,g1)
    c: Coincident(g1,g2)
    c: Coincident(g2,g3)
    c: Coincident(g3,g4)
    c: Coincident(g4,g5)
    c: Coincident(g5,g0)
    c: Equal(g0, g1-g5) x5
    c: PointOnObject(g0,g6)
    c: PointOnObject(g1,g6)
    c: PointOnObject(g2,g6)
    c: PointOnObject(g3,g6)
    c: PointOnObject(g4,g6)
    c: PointOnObject(g5,g6)
    c: Coincident(g6,g-1)
    c: PointOnObject(g5,g-2)
    c: Diameter(g6) = 40
    c: Coincident(g7,g6)
    c: Diameter(g7) = 50
FEATURE [Part::Loft] Loft004
  Closed = false
  MaxDegree = 5
  Ruled = false
  Sections = -> [Sketch747,Sketch748]
  Solid = true
FEATURE [Part::Cut] Cut010  label="backEncloser001"
  Base = -> Loft005
  Placement = pos=(0,150,0) rot=(0,0,1;0rad)
  Refine = true
  Tool = -> Loft004
FEATURE [Sketcher::SketchObject] Sketch751
  ArcFitTolerance = 1e-06
  FullyConstrained = true
  MakeInternals = false
  Placement = pos=(0,0,0) rot=(0,0.707107,0.707107;3.14159rad)
  sketch-geometry (6):
    g0: LineSegment StartX=1e-15 StartY=-25 StartZ=0 EndX=21.65 EndY=-12.5011 EndZ=0
    g1: LineSegment StartX=21.65 StartY=-12.5011 StartZ=0 EndX=21.65 EndY=2.4989 EndZ=0
    g2: LineSegment StartX=-21.65 StartY=2.4989 StartZ=0 EndX=-21.65 EndY=-12.5011 EndZ=0
    g3: LineSegment StartX=-21.65 StartY=-12.5011 StartZ=0 EndX=1e-15 EndY=-25 EndZ=0
    g4: Circle [constr] CenterX=0 CenterY=0 CenterZ=0 NormalX=0 NormalY=0 NormalZ=1 AngleXU=0 Radius=25
    g5: LineSegment StartX=-21.65 StartY=2.4989 StartZ=0 EndX=21.65 EndY=2.4989 EndZ=0
  constraints (20):
    c: Coincident(g0,g1)
    c: Coincident(g2,g3)
    c: Coincident(g3,g0)
    c: Equal(g0,g3)
    c: PointOnObject(g0,g4)
    c: PointOnObject(g2,g4)
    c: PointOnObject(g3,g4)
    c: Coincident(g4,g-1)
    c: PointOnObject(g3,g-2)
    c: Diameter(g4) = 50
    c: Coincident(g5,g2)
    c: Coincident(g5,g1)
    c: Vertical(g2)
    c: Block(g3)
    c: Block(g0)
    c: DistanceX(g2,g-1) = 21.65
    c: DistanceX(g-1,g0) = 21.65
    c: DistanceY(g2,g2) = 15
    c: DistanceY(g1,g1) = 15
    c: DistanceX(g5,g5) = 43.3
FEATURE [Part::Extrusion] Extrude738  label="standmount001"
  Base = -> Sketch751
  Dir = (0,1,-2e-16)
  DirMode = 2
  FaceMakerClass = Part::FaceMakerBullseye
  FaceMakerMode = 3
  LengthFwd = 30
  LengthRev = 0
  Placement = pos=(0,150,0) rot=(0,0,1;0rad)
  Solid = true
  Symmetric = false
FEATURE [Part::Compound] Compound001  label="sensingAndCompute"
  Links = -> [Adafruit_AS7341_STEMMA_QT_v005,Compound,Part__Feature356,COZIR_Sensor_v2]
FEATURE [Sketcher::SketchObject] Sketch757
  ArcFitTolerance = 1e-06
  FullyConstrained = true
  MakeInternals = false
  Placement = pos=(0,15,0) rot=(1,0,0;1.5708rad)
  sketch-geometry (10):
    g0: Circle CenterX=-60 CenterY=70 CenterZ=0 NormalX=0 NormalY=0 NormalZ=1 AngleXU=0 Radius=2
    g1: Circle CenterX=60 CenterY=70 CenterZ=0 NormalX=0 NormalY=0 NormalZ=1 AngleXU=0 Radius=2
    g2: Circle CenterX=-6 CenterY=100 CenterZ=0 NormalX=0 NormalY=0 NormalZ=1 AngleXU=0 Radius=2
    g3: Circle CenterX=6 CenterY=100 CenterZ=0 NormalX=0 NormalY=0 NormalZ=1 AngleXU=0 Radius=2
    g4: Circle CenterX=-60 CenterY=70 CenterZ=0 NormalX=0 NormalY=0 NormalZ=1 AngleXU=0 Radius=7.5
    g5: Circle CenterX=60 CenterY=70 CenterZ=0 NormalX=0 NormalY=0 NormalZ=1 AngleXU=0 Radius=7.5
    g6: ArcOfCircle CenterX=-6 CenterY=100 CenterZ=0 NormalX=0 NormalY=0 NormalZ=1 AngleXU=0 Radius=7.5 StartAngle=1.5708 EndAngle=4.71239
    g7: ArcOfCircle CenterX=6 CenterY=100 CenterZ=0 NormalX=0 NormalY=0 NormalZ=1 AngleXU=0 Radius=7.5 StartAngle=4.71239 EndAngle=7.85398
    g8: LineSegment StartX=-6 StartY=107.5 StartZ=0 EndX=6 EndY=107.5 EndZ=0
    g9: LineSegment StartX=-6 StartY=92.5 StartZ=0 EndX=6 EndY=92.5 EndZ=0
  constraints (24):
    c: Equal(g2,g3)
    c: Equal(g2,g1)
    c: Equal(g2,g0)
    c: Diameter(g2) = 4
    c: Horizontal(g0,g1)
    c: DistanceY(g-1,g0) = 70
    c: DistanceY(g-1,g2) = 100
    c: Horizontal(g2,g3)
    c: DistanceX(g-1,g1) = 60
    c: DistanceX(g0,g-1) = 60
    c: DistanceX(g2,g-1) = 6
    c: DistanceX(g-1,g3) = 6
    c: Coincident(g4,g0)
    c: Coincident(g5,g1)
    c: Equal(g4,g5)
    c: Diameter(g4) = 15
    c: Tangent(g6,g8) = 1.5708
    c: Tangent(g6,g9) = -1.5708
    c: Tangent(g7,g8) = 1.5708
    c: Tangent(g7,g9) = -1.5708
    c: Equal(g6,g7)
    c: Diameter(g6) = 15
    c: Coincident(g2,g6)
    c: Coincident(g3,g7)
FEATURE [Part::Extrusion] Extrude743  label="sensorMountHold"
  Base = -> Sketch757
  Dir = (0,-1,2e-16)
  DirMode = 2
  FaceMakerClass = Part::FaceMakerBullseye
  FaceMakerMode = 3
  LengthFwd = 40
  LengthRev = 0
  Reversed = true
  Solid = true
  Symmetric = false
FEATURE [Sketcher::SketchObject] Sketch758
  ArcFitTolerance = 1e-06
  FullyConstrained = true
  MakeInternals = false
  Placement = pos=(0,-150,0) rot=(1,0,0;1.5708rad)
  sketch-geometry (7):
    g0: LineSegment StartX=-4.2e-15 StartY=135 StartZ=0 EndX=-116.913 EndY=67.5 EndZ=0
    g1: LineSegment StartX=-116.913 StartY=67.5 StartZ=0 EndX=-116.913 EndY=-67.5 EndZ=0
    g2: LineSegment StartX=-116.913 StartY=-67.5 StartZ=0 EndX=1.92e-14 EndY=-135 EndZ=0
    g3: LineSegment StartX=1.92e-14 StartY=-135 StartZ=0 EndX=116.913 EndY=-67.5 EndZ=0
    g4: LineSegment StartX=116.913 StartY=-67.5 StartZ=0 EndX=116.913 EndY=67.5 EndZ=0
    g5: LineSegment StartX=116.913 StartY=67.5 StartZ=0 EndX=-4.2e-15 EndY=135 EndZ=0
    g6: Circle [constr] CenterX=0 CenterY=0 CenterZ=0 NormalX=0 NormalY=0 NormalZ=1 AngleXU=0 Radius=135
  constraints (16):
    c: Coincident(g0,g1)
    c: Coincident(g1,g2)
    c: Coincident(g2,g3)
    c: Coincident(g3,g4)
    c: Coincident(g4,g5)
    c: Coincident(g5,g0)
    c: Equal(g0, g1-g5) x5
    c: PointOnObject(g0,g6)
    c: PointOnObject(g1,g6)
    c: PointOnObject(g2,g6)
    c: PointOnObject(g3,g6)
    c: PointOnObject(g4,g6)
    c: PointOnObject(g5,g6)
    c: PointOnObject(g5,g-2)
    c: Diameter(g6) = 270
    c: Coincident(g6,g-1)
FEATURE [Sketcher::SketchObject] Sketch759
  ArcFitTolerance = 1e-06
  FullyConstrained = true
  MakeInternals = false
  Placement = pos=(0,0,0) rot=(1,0,0;1.5708rad)
  sketch-geometry (8):
    g0: Circle [constr] CenterX=0 CenterY=0 CenterZ=0 NormalX=0 NormalY=0 NormalZ=1 AngleXU=0 Radius=20
    g1: LineSegment StartX=1e-15 StartY=25 StartZ=0 EndX=-21.6506 EndY=12.5 EndZ=0
    g2: LineSegment StartX=-21.6506 StartY=12.5 StartZ=0 EndX=-21.6506 EndY=-12.5 EndZ=0
    g3: LineSegment StartX=-21.6506 StartY=-12.5 StartZ=0 EndX=-1.7133e-12 EndY=-25 EndZ=0
    g4: LineSegment StartX=-1.7133e-12 StartY=-25 StartZ=0 EndX=21.6506 EndY=-12.5 EndZ=0
    g5: LineSegment StartX=21.6506 StartY=-12.5 StartZ=0 EndX=21.6506 EndY=12.5 EndZ=0
    g6: LineSegment StartX=21.6506 StartY=12.5 StartZ=0 EndX=1e-15 EndY=25 EndZ=0
    g7: Circle [constr] CenterX=0 CenterY=0 CenterZ=0 NormalX=0 NormalY=0 NormalZ=1 AngleXU=0 Radius=25
  constraints (18):
    c: Coincident(g0,g-1)
    c: Diameter(g0) = 40
    c: Coincident(g1,g2)
    c: Coincident(g2,g3)
    c: Coincident(g3,g4)
    c: Coincident(g4,g5)
    c: Coincident(g5,g6)
    c: Coincident(g6,g1)
    c: Equal(g1, g2-g6) x5
    c: PointOnObject(g1,g7)
    c: PointOnObject(g2,g7)
    c: PointOnObject(g3,g7)
    c: PointOnObject(g4,g7)
    c: PointOnObject(g5,g7)
    c: PointOnObject(g6,g7)
    c: Coincident(g7,g0)
    c: PointOnObject(g6,g-2)
    c: Diameter(g7) = 50
FEATURE [Part::Loft] Loft006
  Closed = false
  MaxDegree = 5
  Placement = pos=(0,150,0) rot=(0,0,1;0rad)
  Ruled = false
  Sections = -> [Sketch758,Sketch759]
  Solid = true
FEATURE [Part::MultiCommon] Common  label="sensorMountHold001"
  Refine = true
  Shapes = -> [Loft006,Extrude743]
FEATURE [Part::MultiFuse] Fusion571  label="backEncloser"
  Refine = true
  Shapes = -> [Common,Cut010]
FEATURE [Part::Feature] Part__Feature357  label="m3x60s"
  Placement = pos=(0,-20,119.145) rot=(1,0,0;4.71239rad)
  shape: bbox 5.501 x 63 x 5.501 mm, 32 faces (baked)
FEATURE [Sketcher::SketchObject] Sketch760
  ArcFitTolerance = 1e-06
  FullyConstrained = true
  MakeInternals = false
  Placement = pos=(0,0,0) rot=(1,0,0;1.5708rad)
  sketch-geometry (20):
    g0: LineSegment StartX=-4.7e-15 StartY=114.989 StartZ=0 EndX=-99.5833 EndY=57.4944 EndZ=0
    g1: LineSegment StartX=-99.5833 StartY=57.4944 StartZ=0 EndX=-99.5833 EndY=-57.4944 EndZ=0
    g2: LineSegment StartX=-99.5833 StartY=-57.4944 StartZ=0 EndX=9.6e-15 EndY=-114.989 EndZ=0
    g3: LineSegment StartX=9.6e-15 StartY=-114.989 StartZ=0 EndX=99.5833 EndY=-57.4944 EndZ=0
    g4: LineSegment StartX=99.5833 StartY=-57.4944 StartZ=0 EndX=99.5833 EndY=57.4944 EndZ=0
    g5: LineSegment StartX=99.5833 StartY=57.4944 StartZ=0 EndX=-4.7e-15 EndY=114.989 EndZ=0
    g6: Circle [constr] CenterX=0 CenterY=0 CenterZ=0 NormalX=0 NormalY=0 NormalZ=1 AngleXU=0 Radius=114.989
    g7: LineSegment StartX=4.9e-15 StartY=130 StartZ=0 EndX=-112.583 EndY=65 EndZ=0
    g8: LineSegment StartX=-112.583 StartY=65 StartZ=0 EndX=-112.583 EndY=-65 EndZ=0
    g9: LineSegment StartX=-112.583 StartY=-65 StartZ=0 EndX=9.3e-15 EndY=-130 EndZ=0
    g10: LineSegment StartX=9.3e-15 StartY=-130 StartZ=0 EndX=112.583 EndY=-65 EndZ=0
    g11: LineSegment StartX=112.583 StartY=-65 StartZ=0 EndX=112.583 EndY=65 EndZ=0
    g12: LineSegment StartX=112.583 StartY=65 StartZ=0 EndX=4.9e-15 EndY=130 EndZ=0
    g13: Circle [constr] CenterX=0 CenterY=0 CenterZ=0 NormalX=0 NormalY=0 NormalZ=1 AngleXU=0 Radius=130
    g14: Circle CenterX=0 CenterY=119.144 CenterZ=0 NormalX=0 NormalY=0 NormalZ=1 AngleXU=0 Radius=1.625
    g15: Circle CenterX=-103.181 CenterY=59.5718 CenterZ=0 NormalX=0 NormalY=0 NormalZ=1 AngleXU=0 Radius=1.625
    g16: Circle CenterX=-103.181 CenterY=-59.5718 CenterZ=0 NormalX=0 NormalY=0 NormalZ=1 AngleXU=0 Radius=1.625
    g17: Circle CenterX=0 CenterY=-119.144 CenterZ=0 NormalX=0 NormalY=0 NormalZ=1 AngleXU=0 Radius=1.625
    g18: Circle CenterX=103.181 CenterY=-59.5718 CenterZ=0 NormalX=0 NormalY=0 NormalZ=1 AngleXU=0 Radius=1.625
    g19: Circle CenterX=103.181 CenterY=59.5718 CenterZ=0 NormalX=0 NormalY=0 NormalZ=1 AngleXU=0 Radius=1.625
  constraints (46):
    c: Coincident(g0,g1)
    c: Coincident(g1,g2)
    c: Coincident(g2,g3)
    c: Coincident(g3,g4)
    c: Coincident(g4,g5)
    c: Coincident(g5,g0)
    c: Equal(g0, g1-g5) x5
    c: PointOnObject(g0,g6)
    c: PointOnObject(g1,g6)
    c: PointOnObject(g2,g6)
    c: PointOnObject(g3,g6)
    c: PointOnObject(g4,g6)
    c: PointOnObject(g5,g6)
    c: Coincident(g6,g-1)
    c: PointOnObject(g5,g-2)
    c: Coincident(g7,g8)
    c: Coincident(g8,g9)
    c: Coincident(g9,g10)
    c: Coincident(g10,g11)
    c: Coincident(g11,g12)
    c: Coincident(g12,g7)
    c: Equal(g7, g8-g12) x5
    c: PointOnObject(g7,g13)
    c: PointOnObject(g8,g13)
    c: PointOnObject(g9,g13)
    c: PointOnObject(g10,g13)
    c: PointOnObject(g11,g13)
    c: PointOnObject(g12,g13)
    c: Coincident(g13,g6)
    c: PointOnObject(g12,g-2)
    c: DistanceX(g7,g0) = 13
    c: DistanceY(g8,g8) = 130
    c: Equal(g14, g15-g19) x5
    c: Diameter(g14) = 3.25
    c: DistanceX(g15) = -103.181
    c: DistanceY(g15) = 59.5718
    c: DistanceX(g16) = -103.181
    c: DistanceY(g16) = -59.5718
    c: DistanceX(g17) = 0
    c: DistanceY(g17) = -119.144
    c: DistanceX(g18) = 103.181
    c: DistanceY(g18) = -59.5718
    c: DistanceX(g19) = 103.181
    c: DistanceY(g19) = 59.5718
    c: DistanceX(g14) = 0
    c: DistanceY(g-1,g14) = 119.144
FEATURE [Part::Extrusion] Extrude744  label="hexMeshBorder002"
  Base = -> Sketch760
  Dir = (0,-1,2e-16)
  DirMode = 2
  FaceMakerClass = Part::FaceMakerBullseye
  FaceMakerMode = 3
  LengthFwd = 10
  LengthRev = 0
  Solid = true
  Symmetric = false
FEATURE [Part::Fillet] Fillet002  label="hexMeshBorder"
  Base = -> Extrude744
  EdgeLinks = -> Extrude744 [Edge19,Edge20,Edge23,Edge26,Edge29,Edge32]
  Edges = 6 edges r=10: [Edge19,Edge20,Edge23,Edge26,Edge29,Edge32]
FEATURE [Sketcher::SketchObject] Sketch761
  ArcFitTolerance = 1e-06
  FullyConstrained = true
  MakeInternals = false
  Placement = pos=(0,0,0) rot=(1,0,0;1.5708rad)
  sketch-geometry (20):
    g0: Circle CenterX=-60 CenterY=70 CenterZ=0 NormalX=0 NormalY=0 NormalZ=1 AngleXU=0 Radius=1.75
    g1: Circle CenterX=60 CenterY=70 CenterZ=0 NormalX=0 NormalY=0 NormalZ=1 AngleXU=0 Radius=1.75
    g2: Circle CenterX=-6 CenterY=100 CenterZ=0 NormalX=0 NormalY=0 NormalZ=1 AngleXU=0 Radius=1.75
    g3: Circle CenterX=6 CenterY=100 CenterZ=0 NormalX=0 NormalY=0 NormalZ=1 AngleXU=0 Radius=1.75
    g4: LineSegment StartX=0 StartY=113 StartZ=0 EndX=-69.282 EndY=73 EndZ=0
    g5: LineSegment StartX=0 StartY=113 StartZ=0 EndX=69.282 EndY=73 EndZ=0
    g6: LineSegment StartX=-35 StartY=8 StartZ=0 EndX=35 EndY=8 EndZ=0
    g7: LineSegment StartX=-35 StartY=8 StartZ=0 EndX=-69.282 EndY=73 EndZ=0
    g8: LineSegment StartX=35 StartY=8 StartZ=0 EndX=69.282 EndY=73 EndZ=0
    g9: Circle CenterX=-29 CenterY=36.5 CenterZ=0 NormalX=0 NormalY=0 NormalZ=1 AngleXU=0 Radius=1.125
    g10: Circle CenterX=29 CenterY=36.5 CenterZ=0 NormalX=0 NormalY=0 NormalZ=1 AngleXU=0 Radius=1.125
    g11: Circle CenterX=-29 CenterY=13.5 CenterZ=0 NormalX=0 NormalY=0 NormalZ=1 AngleXU=0 Radius=1.125
    g12: Circle CenterX=29 CenterY=13.5 CenterZ=0 NormalX=0 NormalY=0 NormalZ=1 AngleXU=0 Radius=1.125
    g13: Circle CenterX=-52 CenterY=75.4485 CenterZ=0 NormalX=0 NormalY=0 NormalZ=1 AngleXU=0 Radius=1.125
    g14: Circle CenterX=-34.35 CenterY=85.4769 CenterZ=0 NormalX=0 NormalY=0 NormalZ=1 AngleXU=0 Radius=1.125
    g15: Circle CenterX=-45.65 CenterY=64.45 CenterZ=0 NormalX=0 NormalY=0 NormalZ=1 AngleXU=0 Radius=1.125
    g16: Circle CenterX=-28 CenterY=74.4783 CenterZ=0 NormalX=0 NormalY=0 NormalZ=1 AngleXU=0 Radius=1.125
    g17: Circle CenterX=-21.3 CenterY=89.1 CenterZ=0 NormalX=0 NormalY=0 NormalZ=1 AngleXU=0 Radius=1.625
    g18: Circle CenterX=21.3 CenterY=89.1 CenterZ=0 NormalX=0 NormalY=0 NormalZ=1 AngleXU=0 Radius=1.625
    g19: Circle CenterX=0 CenterY=51.65 CenterZ=0 NormalX=0 NormalY=0 NormalZ=1 AngleXU=0 Radius=1.625
  constraints (60):
    c: Equal(g2,g3)
    c: Equal(g2,g1)
    c: Equal(g2,g0)
    c: Diameter(g2) = 3.5
    c: Horizontal(g0,g1)
    c: DistanceY(g-1,g0) = 70
    c: DistanceY(g-1,g2) = 100
    c: Horizontal(g2,g3)
    c: Coincident(g5,g4)
    c: Angle(g4,g5) = 2.0944
    c: DistanceX(g4,g-1) = 0
    c: Distance(g4,g-1) = 113
    c: Angle(g5) = -0.523599
    c: Distance(g4,g4) = 80
    c: Distance(g5,g5) = 80
    c: Horizontal(g6)
    c: Coincident(g7,g6)
    c: Coincident(g7,g4)
    c: DistanceX(g6,g-1) = 35
    c: Coincident(g8,g6)
    c: Coincident(g8,g5)
    c: DistanceX(g-1,g6) = 35
    c: DistanceY(g-1,g6) = 8
    c: DistanceX(g-1,g1) = 60
    c: DistanceX(g0,g-1) = 60
    c: DistanceX(g2,g-1) = 6
    c: DistanceX(g-1,g3) = 6
    c: Equal(g13,g14)
    c: Equal(g13,g15)
    c: Equal(g13,g16)
    c: Diameter(g13) = 2.25
    c: Distance(g15,g16) = 20.3
    c: Distance(g13,g14) = 20.3
    c: Distance(g13,g15) = 12.7
    c: Distance(g16,g14) = 12.7
    c: Equal(g17,g18)
    c: Equal(g17,g19)
    c: Diameter(g17) = 3.25
    c: DistanceY(g-1,g15) = 64.45
    c: DistanceX(g15,g-1) = 45.65
    c: DistanceX(g17,g-1) = 21.3
    c: DistanceX(g-1,g18) = 21.3
    c: DistanceX(g19,g-1) = 0
    c: DistanceY(g-1,g19) = 51.65
    c: DistanceY(g-1,g17) = 89.1
    c: DistanceY(g-1,g18) = 89.1
    c: Equal(g9,g10)
    c: Equal(g9,g11)
    c: Equal(g9,g12)
    c: Diameter(g9) = 2.25
    c: DistanceY(g-1,g11) = 13.5
    c: DistanceX(g11,g-1) = 29
    c: DistanceX(g-1,g12) = 29
    c: DistanceY(g11,g9) = 23
    c: DistanceX(g9,g-1) = 29
    c: DistanceX(g-1,g10) = 29
    c: DistanceY(g12,g10) = 23
    c: DistanceY(g-1,g12) = 13.5
    c: DistanceX(g13,g-1) = 52
    c: DistanceX(g15,g14) = 11.3
FEATURE [Part::Extrusion] Extrude745  label="sensorBase003"
  Base = -> Sketch761
  Dir = (0,-1,2e-16)
  DirMode = 2
  FaceMakerClass = Part::FaceMakerBullseye
  FaceMakerMode = 3
  LengthFwd = 5
  LengthRev = 0
  Placement = pos=(0,15,0) rot=(0,0,1;0rad)
  Solid = true
  Symmetric = false
FEATURE [Sketcher::SketchObject] Sketch762
  ArcFitTolerance = 1e-06
  FullyConstrained = true
  MakeInternals = false
  Placement = pos=(0,0,0) rot=(1,0,0;1.5708rad)
  sketch-geometry (14):
    g0: Circle CenterX=-52 CenterY=75.4485 CenterZ=0 NormalX=0 NormalY=0 NormalZ=1 AngleXU=0 Radius=1.125
    g1: Circle CenterX=-34.35 CenterY=85.4769 CenterZ=0 NormalX=0 NormalY=0 NormalZ=1 AngleXU=0 Radius=1.125
    g2: Circle CenterX=-45.65 CenterY=64.45 CenterZ=0 NormalX=0 NormalY=0 NormalZ=1 AngleXU=0 Radius=1.125
    g3: Circle CenterX=-28 CenterY=74.4783 CenterZ=0 NormalX=0 NormalY=0 NormalZ=1 AngleXU=0 Radius=1.125
    g4: Circle CenterX=-21.3 CenterY=89.1 CenterZ=0 NormalX=0 NormalY=0 NormalZ=1 AngleXU=0 Radius=1.625
    g5: Circle CenterX=21.3 CenterY=89.1 CenterZ=0 NormalX=0 NormalY=0 NormalZ=1 AngleXU=0 Radius=1.625
    g6: Circle CenterX=0 CenterY=51.65 CenterZ=0 NormalX=0 NormalY=0 NormalZ=1 AngleXU=0 Radius=1.625
    g7: Circle CenterX=-52 CenterY=75.4485 CenterZ=0 NormalX=0 NormalY=0 NormalZ=1 AngleXU=0 Radius=3
    g8: Circle CenterX=-34.35 CenterY=85.4769 CenterZ=0 NormalX=0 NormalY=0 NormalZ=1 AngleXU=0 Radius=3
    g9: Circle CenterX=-28 CenterY=74.4783 CenterZ=0 NormalX=0 NormalY=0 NormalZ=1 AngleXU=0 Radius=3
    g10: Circle CenterX=-45.65 CenterY=64.45 CenterZ=0 NormalX=0 NormalY=0 NormalZ=1 AngleXU=0 Radius=3
    g11: Circle CenterX=-21.3 CenterY=89.1 CenterZ=0 NormalX=0 NormalY=0 NormalZ=1 AngleXU=0 Radius=4
    g12: Circle CenterX=21.3 CenterY=89.1 CenterZ=0 NormalX=0 NormalY=0 NormalZ=1 AngleXU=0 Radius=4
    g13: Circle CenterX=0 CenterY=51.65 CenterZ=0 NormalX=0 NormalY=0 NormalZ=1 AngleXU=0 Radius=4
  constraints (35):
    c: Equal(g0,g1)
    c: Equal(g0,g2)
    c: Equal(g0,g3)
    c: Diameter(g0) = 2.25
    c: Distance(g2,g3) = 20.3
    c: Distance(g0,g1) = 20.3
    c: Distance(g0,g2) = 12.7
    c: Distance(g3,g1) = 12.7
    c: Equal(g4,g5)
    c: Equal(g4,g6)
    c: Diameter(g4) = 3.25
    c: DistanceY(g-1,g2) = 64.45
    c: DistanceX(g2,g-1) = 45.65
    c: DistanceX(g4,g-1) = 21.3
    c: DistanceX(g-1,g5) = 21.3
    c: DistanceX(g6,g-1) = 0
    c: DistanceY(g-1,g6) = 51.65
    c: DistanceY(g-1,g4) = 89.1
    c: DistanceY(g-1,g5) = 89.1
    c: DistanceX(g0,g-1) = 52
    c: DistanceX(g2,g1) = 11.3
    c: Coincident(g7,g0)
    c: Coincident(g8,g1)
    c: Coincident(g9,g3)
    c: Coincident(g10,g2)
    c: Coincident(g11,g4)
    c: Coincident(g12,g5)
    c: Coincident(g13,g6)
    c: Equal(g11,g12)
    c: Equal(g11,g13)
    c: Diameter(g11) = 8
    c: Equal(g7,g8)
    c: Equal(g7,g9)
    c: Equal(g7,g10)
    c: Diameter(g7) = 6
FEATURE [Part::Extrusion] Extrude746  label="sensorBase004"
  Base = -> Sketch762
  Dir = (0,-1,2e-16)
  DirMode = 2
  FaceMakerClass = Part::FaceMakerBullseye
  FaceMakerMode = 3
  LengthFwd = 30
  LengthRev = 0
  Placement = pos=(0,15,0) rot=(0,0,1;0rad)
  Solid = true
  Symmetric = false
FEATURE [Part::MultiFuse] Fusion572  label="sensorMount001"
  Refine = true
  Shapes = -> [Extrude746,Extrude745]
FEATURE [Sketcher::SketchObject] Sketch763
  ArcFitTolerance = 1e-06
  FullyConstrained = true
  MakeInternals = false
  Placement = pos=(40,0,0) rot=(0.57735,0.57735,0.57735;2.0944rad)
  sketch-geometry (10):
    g0: LineSegment StartX=-48 StartY=89 StartZ=0 EndX=-48 EndY=81 EndZ=0
    g1: LineSegment StartX=-48 StartY=81 StartZ=0 EndX=10 EndY=81 EndZ=0
    g2: LineSegment StartX=10 StartY=81 StartZ=0 EndX=10 EndY=89 EndZ=0
    g3: LineSegment StartX=10 StartY=89 StartZ=0 EndX=-48 EndY=89 EndZ=0
    g4: LineSegment StartX=-8 StartY=53 StartZ=0 EndX=-8 EndY=45 EndZ=0
    g5: LineSegment StartX=-8 StartY=45 StartZ=0 EndX=10 EndY=45 EndZ=0
    g6: LineSegment StartX=10 StartY=45 StartZ=0 EndX=10 EndY=53 EndZ=0
    g7: LineSegment StartX=10 StartY=53 StartZ=0 EndX=-8 EndY=53 EndZ=0
    g8: Circle CenterX=-3.6 CenterY=48.6 CenterZ=0 NormalX=0 NormalY=0 NormalZ=1 AngleXU=0 Radius=1.125
    g9: Circle CenterX=-44.4 CenterY=85.4 CenterZ=0 NormalX=0 NormalY=0 NormalZ=1 AngleXU=0 Radius=1.125
  constraints (30):
    c: Coincident(g0,g1)
    c: Coincident(g1,g2)
    c: Coincident(g2,g3)
    c: Coincident(g3,g0)
    c: Vertical(g0)
    c: Vertical(g2)
    c: Horizontal(g1)
    c: Horizontal(g3)
    c: Coincident(g4,g5)
    c: Coincident(g5,g6)
    c: Coincident(g6,g7)
    c: Coincident(g7,g4)
    c: Vertical(g4)
    c: Vertical(g6)
    c: Horizontal(g5)
    c: Horizontal(g7)
    c: DistanceY(g-1,g5) = 45
    c: DistanceX(g-1,g5) = 10
    c: DistanceX(g4,g-1) = 8
    c: Distance(g4,g4) = 8
    c: DistanceY(g5,g1) = 36
    c: DistanceX(g0,g-1) = 48
    c: DistanceY(g0,g0) = 8
    c: DistanceX(g-1,g1) = 10
    c: DistanceY(g-1,g8) = 48.6
    c: DistanceX(g8,g-1) = 3.6
    c: Equal(g8,g9)
    c: Diameter(g8) = 2.25
    c: DistanceX(g9,g8) = 40.8
    c: DistanceY(g8,g9) = 36.8
FEATURE [Part::Extrusion] Extrude747
  Base = -> Sketch763
  Dir = (1,0,0)
  DirMode = 2
  FaceMakerClass = Part::FaceMakerBullseye
  FaceMakerMode = 3
  LengthFwd = 6
  LengthRev = 0
  Solid = true
  Symmetric = false
FEATURE [Part::Fillet] Fillet004
  Base = -> Extrude747
  EdgeLinks = -> Extrude747 [Edge7,Edge12,Edge22,Edge27]
  Edges = 4 edges r=3: [Edge7,Edge12,Edge22,Edge27]
FEATURE [Part::MultiFuse] Fusion573
  Refine = true
  Shapes = -> [Fillet004,Fusion572]
FEATURE [Part::Fillet] Fillet005  label="sensorHold002"
  Base = -> Fusion573
  EdgeLinks = -> Fusion573 [Edge16,Edge36,Edge37,Edge38,Edge39,Edge40,Edge43,Edge50,Edge52]
  Edges = 9 edges r=3: [Edge16,Edge36,Edge37,Edge38,Edge39,Edge40,Edge43,Edge50,Edge52]
FEATURE [Part::Fillet] Fillet006  label="sensorHold"
  Base = -> Fillet005
  EdgeLinks = -> Fillet005 [Edge66]
  Edges = 1 edges r=10: [Edge66]
FEATURE [Part::MultiFuse] Fusion574  label="frontHex001"
  Refine = true
  Shapes = -> [Fillet002,Fusion]
FEATURE [Sketcher::SketchObject] Sketch765
  ArcFitTolerance = 1e-06
  FullyConstrained = true
  MakeInternals = false
  Placement = pos=(0,-59.5,0) rot=(1,0,0;1.5708rad)
  sketch-geometry (12):
    g0: Circle CenterX=0 CenterY=119.144 CenterZ=0 NormalX=0 NormalY=0 NormalZ=1 AngleXU=0 Radius=2
    g1: Circle CenterX=-103.181 CenterY=59.5718 CenterZ=0 NormalX=0 NormalY=0 NormalZ=1 AngleXU=0 Radius=2
    g2: Circle CenterX=-103.181 CenterY=-59.5718 CenterZ=0 NormalX=0 NormalY=0 NormalZ=1 AngleXU=0 Radius=2
    g3: Circle CenterX=0 CenterY=-119.144 CenterZ=0 NormalX=0 NormalY=0 NormalZ=1 AngleXU=0 Radius=2
    g4: Circle CenterX=103.181 CenterY=-59.5718 CenterZ=0 NormalX=0 NormalY=0 NormalZ=1 AngleXU=0 Radius=2
    g5: Circle CenterX=103.181 CenterY=59.5718 CenterZ=0 NormalX=0 NormalY=0 NormalZ=1 AngleXU=0 Radius=2
    g6: Circle CenterX=0 CenterY=119.144 CenterZ=0 NormalX=0 NormalY=0 NormalZ=1 AngleXU=0 Radius=15
    g7: Circle CenterX=-103.181 CenterY=59.5718 CenterZ=0 NormalX=0 NormalY=0 NormalZ=1 AngleXU=0 Radius=15
    g8: Circle CenterX=-103.181 CenterY=-59.5718 CenterZ=0 NormalX=0 NormalY=0 NormalZ=1 AngleXU=0 Radius=15
    g9: Circle CenterX=0 CenterY=-119.144 CenterZ=0 NormalX=0 NormalY=0 NormalZ=1 AngleXU=0 Radius=15
    g10: Circle CenterX=103.181 CenterY=-59.5718 CenterZ=0 NormalX=0 NormalY=0 NormalZ=1 AngleXU=0 Radius=15
    g11: Circle CenterX=103.181 CenterY=59.5718 CenterZ=0 NormalX=0 NormalY=0 NormalZ=1 AngleXU=0 Radius=15
  constraints (26):
    c: Equal(g0, g1-g5) x5
    c: Diameter(g0) = 4
    c: DistanceX(g1) = -103.181
    c: DistanceX(g2) = -103.181
    c: DistanceY(g2) = -59.5718
    c: DistanceX(g3) = 0
    c: DistanceY(g3) = -119.144
    c: DistanceX(g4) = 103.181
    c: DistanceY(g4) = -59.5718
    c: DistanceX(g5) = 103.181
    c: DistanceY(g5) = 59.5718
    c: DistanceX(g0) = 0
    c: DistanceY(g1) = 59.5718
    c: DistanceY(g0) = 119.144
    c: Coincident(g6,g0)
    c: Coincident(g7,g1)
    c: Coincident(g8,g2)
    c: Coincident(g9,g3)
    c: Coincident(g10,g4)
    c: Coincident(g11,g5)
    c: Equal(g6,g7)
    c: Equal(g7,g8)
    c: Equal(g8,g9)
    c: Equal(g9,g10)
    c: Equal(g10,g11)
    c: Diameter(g6) = 30
FEATURE [Part::Extrusion] Extrude748  label="circles"
  Base = -> Sketch765
  Dir = (0,-1,2e-16)
  DirMode = 2
  FaceMakerClass = Part::FaceMakerBullseye
  FaceMakerMode = 3
  LengthFwd = 10
  LengthRev = 0
  Reversed = true
  Solid = true
  Symmetric = false
FEATURE [Sketcher::SketchObject] Sketch766
  ArcFitTolerance = 1e-06
  FullyConstrained = true
  MakeInternals = false
  Placement = pos=(0,-59.5,0) rot=(1,0,0;1.5708rad)
  sketch-geometry (7):
    g0: LineSegment StartX=-112.583 StartY=65 StartZ=0 EndX=-112.583 EndY=-65 EndZ=0
    g1: LineSegment StartX=-112.583 StartY=-65 StartZ=0 EndX=9.5e-15 EndY=-130 EndZ=0
    g2: LineSegment StartX=9.5e-15 StartY=-130 StartZ=0 EndX=112.583 EndY=-65 EndZ=0
    g3: LineSegment StartX=112.583 StartY=-65 StartZ=0 EndX=112.583 EndY=65 EndZ=0
    g4: LineSegment StartX=112.583 StartY=65 StartZ=0 EndX=-9.3e-15 EndY=130 EndZ=0
    g5: LineSegment StartX=-9.3e-15 StartY=130 StartZ=0 EndX=-112.583 EndY=65 EndZ=0
    g6: Circle [constr] CenterX=0 CenterY=0 CenterZ=0 NormalX=0 NormalY=0 NormalZ=1 AngleXU=0 Radius=130
  constraints (16):
    c: Coincident(g0,g1)
    c: Coincident(g1,g2)
    c: Coincident(g2,g3)
    c: Coincident(g3,g4)
    c: Coincident(g4,g5)
    c: Coincident(g5,g0)
    c: Equal(g0, g1-g5) x5
    c: PointOnObject(g0,g6)
    c: PointOnObject(g1,g6)
    c: PointOnObject(g2,g6)
    c: PointOnObject(g3,g6)
    c: PointOnObject(g4,g6)
    c: PointOnObject(g5,g6)
    c: Coincident(g6,g-1)
    c: Vertical(g0)
    c: Diameter(g6) = 260
FEATURE [Part::Extrusion] Extrude749  label="hex"
  Base = -> Sketch766
  Dir = (0,-1,2e-16)
  DirMode = 2
  FaceMakerClass = Part::FaceMakerBullseye
  FaceMakerMode = 3
  LengthFwd = 10
  LengthRev = 0
  Reversed = true
  Solid = true
  Symmetric = false
FEATURE [Part::MultiCommon] Common001
  Refine = true
  Shapes = -> [Extrude749,Extrude748]
FEATURE [Part::Cut] Cut  label="frontHex002F"
  Base = -> Fusion574
  Refine = true
  Tool = -> Common001
FEATURE [Sketcher::SketchObject] Sketch767
  ArcFitTolerance = 1e-06
  FullyConstrained = true
  MakeInternals = false
  Placement = pos=(0,-60,0) rot=(1,0,0;1.5708rad)
  sketch-geometry (12):
    g0: Circle CenterX=0 CenterY=119.144 CenterZ=0 NormalX=0 NormalY=0 NormalZ=1 AngleXU=0 Radius=2
    g1: Circle CenterX=-103.181 CenterY=59.5718 CenterZ=0 NormalX=0 NormalY=0 NormalZ=1 AngleXU=0 Radius=2
    g2: Circle CenterX=-103.181 CenterY=-59.5718 CenterZ=0 NormalX=0 NormalY=0 NormalZ=1 AngleXU=0 Radius=2
    g3: Circle CenterX=0 CenterY=-119.144 CenterZ=0 NormalX=0 NormalY=0 NormalZ=1 AngleXU=0 Radius=2
    g4: Circle CenterX=103.181 CenterY=-59.5718 CenterZ=0 NormalX=0 NormalY=0 NormalZ=1 AngleXU=0 Radius=2
    g5: Circle CenterX=103.181 CenterY=59.5718 CenterZ=0 NormalX=0 NormalY=0 NormalZ=1 AngleXU=0 Radius=2
    g6: Circle CenterX=0 CenterY=119.144 CenterZ=0 NormalX=0 NormalY=0 NormalZ=1 AngleXU=0 Radius=14
    g7: Circle CenterX=-103.181 CenterY=59.5718 CenterZ=0 NormalX=0 NormalY=0 NormalZ=1 AngleXU=0 Radius=14
    g8: Circle CenterX=-103.181 CenterY=-59.5718 CenterZ=0 NormalX=0 NormalY=0 NormalZ=1 AngleXU=0 Radius=14
    g9: Circle CenterX=0 CenterY=-119.144 CenterZ=0 NormalX=0 NormalY=0 NormalZ=1 AngleXU=0 Radius=14
    g10: Circle CenterX=103.181 CenterY=-59.5718 CenterZ=0 NormalX=0 NormalY=0 NormalZ=1 AngleXU=0 Radius=14
    g11: Circle CenterX=103.181 CenterY=59.5718 CenterZ=0 NormalX=0 NormalY=0 NormalZ=1 AngleXU=0 Radius=14
  constraints (26):
    c: Equal(g0, g1-g5) x5
    c: Diameter(g0) = 4
    c: DistanceX(g1) = -103.181
    c: DistanceX(g2) = -103.181
    c: DistanceY(g2) = -59.5718
    c: DistanceX(g3) = 0
    c: DistanceY(g3) = -119.144
    c: DistanceX(g4) = 103.181
    c: DistanceY(g4) = -59.5718
    c: DistanceX(g5) = 103.181
    c: DistanceY(g5) = 59.5718
    c: DistanceX(g0) = 0
    c: DistanceY(g1) = 59.5718
    c: DistanceY(g0) = 119.144
    c: Coincident(g6,g0)
    c: Coincident(g7,g1)
    c: Coincident(g8,g2)
    c: Coincident(g9,g3)
    c: Coincident(g10,g4)
    c: Coincident(g11,g5)
    c: Equal(g6,g7)
    c: Equal(g7,g8)
    c: Equal(g8,g9)
    c: Equal(g9,g10)
    c: Equal(g10,g11)
    c: Diameter(g6) = 28
FEATURE [Part::Extrusion] Extrude750  label="circles001"
  Base = -> Sketch767
  Dir = (0,-1,2e-16)
  DirMode = 2
  FaceMakerClass = Part::FaceMakerBullseye
  FaceMakerMode = 3
  LengthFwd = 20
  LengthRev = 0
  Reversed = true
  Solid = true
  Symmetric = false
FEATURE [Sketcher::SketchObject] Sketch768
  ArcFitTolerance = 1e-06
  FullyConstrained = true
  MakeInternals = false
  Placement = pos=(0,-60,0) rot=(1,0,0;1.5708rad)
  sketch-geometry (7):
    g0: LineSegment StartX=-110.851 StartY=64 StartZ=0 EndX=-110.851 EndY=-64 EndZ=0
    g1: LineSegment StartX=-110.851 StartY=-64 StartZ=0 EndX=2.46e-14 EndY=-128 EndZ=0
    g2: LineSegment StartX=2.46e-14 StartY=-128 StartZ=0 EndX=110.851 EndY=-64 EndZ=0
    g3: LineSegment StartX=110.851 StartY=-64 StartZ=0 EndX=110.851 EndY=64 EndZ=0
    g4: LineSegment StartX=110.851 StartY=64 StartZ=0 EndX=-3.88e-14 EndY=128 EndZ=0
    g5: LineSegment StartX=-3.88e-14 StartY=128 StartZ=0 EndX=-110.851 EndY=64 EndZ=0
    g6: Circle [constr] CenterX=0 CenterY=0 CenterZ=0 NormalX=0 NormalY=0 NormalZ=1 AngleXU=0 Radius=128
  constraints (16):
    c: Coincident(g0,g1)
    c: Coincident(g1,g2)
    c: Coincident(g2,g3)
    c: Coincident(g3,g4)
    c: Coincident(g4,g5)
    c: Coincident(g5,g0)
    c: Equal(g0, g1-g5) x5
    c: PointOnObject(g0,g6)
    c: PointOnObject(g1,g6)
    c: PointOnObject(g2,g6)
    c: PointOnObject(g3,g6)
    c: PointOnObject(g4,g6)
    c: PointOnObject(g5,g6)
    c: Coincident(g6,g-1)
    c: Vertical(g0)
    c: Diameter(g6) = 256
FEATURE [Part::Extrusion] Extrude751  label="hex335"
  Base = -> Sketch768
  Dir = (0,-1,2e-16)
  DirMode = 2
  FaceMakerClass = Part::FaceMakerBullseye
  FaceMakerMode = 3
  LengthFwd = 20
  LengthRev = 0
  Reversed = true
  Solid = true
  Symmetric = false
FEATURE [Part::MultiCommon] Common002
  Refine = true
  Shapes = -> [Extrude751,Extrude750]
FEATURE [Sketcher::SketchObject] Sketch771
  ArcFitTolerance = 1e-06
  FullyConstrained = true
  MakeInternals = false
  Placement = pos=(0,0,0) rot=(1,0,0;1.5708rad)
  sketch-geometry (12):
    g0: Circle CenterX=0 CenterY=119.144 CenterZ=0 NormalX=0 NormalY=0 NormalZ=1 AngleXU=0 Radius=1.625
    g1: Circle CenterX=-103.181 CenterY=59.5718 CenterZ=0 NormalX=0 NormalY=0 NormalZ=1 AngleXU=0 Radius=1.625
    g2: Circle CenterX=-103.181 CenterY=-59.5718 CenterZ=0 NormalX=0 NormalY=0 NormalZ=1 AngleXU=0 Radius=1.625
    g3: Circle CenterX=0 CenterY=-119.144 CenterZ=0 NormalX=0 NormalY=0 NormalZ=1 AngleXU=0 Radius=1.625
    g4: Circle CenterX=103.181 CenterY=-59.5718 CenterZ=0 NormalX=0 NormalY=0 NormalZ=1 AngleXU=0 Radius=1.625
    g5: Circle CenterX=103.181 CenterY=59.5718 CenterZ=0 NormalX=0 NormalY=0 NormalZ=1 AngleXU=0 Radius=1.625
    g6: Circle CenterX=0 CenterY=119.144 CenterZ=0 NormalX=0 NormalY=0 NormalZ=1 AngleXU=0 Radius=7.5
    g7: Circle CenterX=-103.181 CenterY=59.5718 CenterZ=0 NormalX=0 NormalY=0 NormalZ=1 AngleXU=0 Radius=7.5
    g8: Circle CenterX=-103.181 CenterY=-59.5718 CenterZ=0 NormalX=0 NormalY=0 NormalZ=1 AngleXU=0 Radius=7.5
    g9: Circle CenterX=0 CenterY=-119.144 CenterZ=0 NormalX=0 NormalY=0 NormalZ=1 AngleXU=0 Radius=7.5
    g10: Circle CenterX=103.181 CenterY=-59.5718 CenterZ=0 NormalX=0 NormalY=0 NormalZ=1 AngleXU=0 Radius=7.5
    g11: Circle CenterX=103.181 CenterY=59.5718 CenterZ=0 NormalX=0 NormalY=0 NormalZ=1 AngleXU=0 Radius=7.5
  constraints (26):
    c: Equal(g0, g1-g5) x5
    c: Diameter(g0) = 3.25
    c: DistanceX(g1) = -103.181
    c: DistanceX(g2) = -103.181
    c: DistanceY(g2) = -59.5718
    c: DistanceX(g3) = 0
    c: DistanceY(g3) = -119.144
    c: DistanceX(g4) = 103.181
    c: DistanceY(g4) = -59.5718
    c: DistanceX(g5) = 103.181
    c: DistanceY(g5) = 59.5718
    c: DistanceX(g0) = 0
    c: DistanceY(g1) = 59.5718
    c: DistanceY(g0) = 119.144
    c: Coincident(g6,g0)
    c: Coincident(g7,g1)
    c: Coincident(g8,g2)
    c: Coincident(g9,g3)
    c: Coincident(g10,g4)
    c: Coincident(g11,g5)
    c: Equal(g6,g7)
    c: Equal(g7,g8)
    c: Equal(g8,g9)
    c: Equal(g9,g10)
    c: Equal(g10,g11)
    c: Diameter(g6) = 15
FEATURE [Part::Extrusion] Extrude754  label="circles003"
  Base = -> Sketch771
  Dir = (0,-1,2e-16)
  DirMode = 2
  FaceMakerClass = Part::FaceMakerBullseye
  FaceMakerMode = 3
  LengthFwd = 40
  LengthRev = 0
  Reversed = true
  Solid = true
  Symmetric = false
FEATURE [Sketcher::SketchObject] Sketch772
  ArcFitTolerance = 1e-06
  FullyConstrained = true
  MakeInternals = false
  Placement = pos=(0,-150,0) rot=(1,0,0;1.5708rad)
  sketch-geometry (7):
    g0: LineSegment StartX=-4.2e-15 StartY=135 StartZ=0 EndX=-116.913 EndY=67.5 EndZ=0
    g1: LineSegment StartX=-116.913 StartY=67.5 StartZ=0 EndX=-116.913 EndY=-67.5 EndZ=0
    g2: LineSegment StartX=-116.913 StartY=-67.5 StartZ=0 EndX=1.92e-14 EndY=-135 EndZ=0
    g3: LineSegment StartX=1.92e-14 StartY=-135 StartZ=0 EndX=116.913 EndY=-67.5 EndZ=0
    g4: LineSegment StartX=116.913 StartY=-67.5 StartZ=0 EndX=116.913 EndY=67.5 EndZ=0
    g5: LineSegment StartX=116.913 StartY=67.5 StartZ=0 EndX=-4.2e-15 EndY=135 EndZ=0
    g6: Circle [constr] CenterX=0 CenterY=0 CenterZ=0 NormalX=0 NormalY=0 NormalZ=1 AngleXU=0 Radius=135
  constraints (16):
    c: Coincident(g0,g1)
    c: Coincident(g1,g2)
    c: Coincident(g2,g3)
    c: Coincident(g3,g4)
    c: Coincident(g4,g5)
    c: Coincident(g5,g0)
    c: Equal(g0, g1-g5) x5
    c: PointOnObject(g0,g6)
    c: PointOnObject(g1,g6)
    c: PointOnObject(g2,g6)
    c: PointOnObject(g3,g6)
    c: PointOnObject(g4,g6)
    c: PointOnObject(g5,g6)
    c: PointOnObject(g5,g-2)
    c: Diameter(g6) = 270
    c: Coincident(g6,g-1)
FEATURE [Sketcher::SketchObject] Sketch773
  ArcFitTolerance = 1e-06
  FullyConstrained = true
  MakeInternals = false
  Placement = pos=(0,0,0) rot=(1,0,0;1.5708rad)
  sketch-geometry (8):
    g0: Circle [constr] CenterX=0 CenterY=0 CenterZ=0 NormalX=0 NormalY=0 NormalZ=1 AngleXU=0 Radius=20
    g1: LineSegment StartX=0 StartY=25 StartZ=0 EndX=-21.6506 EndY=12.5 EndZ=0
    g2: LineSegment StartX=-21.6506 StartY=12.5 StartZ=0 EndX=-21.6506 EndY=-12.5 EndZ=0
    g3: LineSegment StartX=-21.6506 StartY=-12.5 StartZ=0 EndX=-1.7136e-12 EndY=-25 EndZ=0
    g4: LineSegment StartX=-1.7133e-12 StartY=-25 StartZ=0 EndX=21.6506 EndY=-12.5 EndZ=0
    g5: LineSegment StartX=21.6506 StartY=-12.5 StartZ=0 EndX=21.6506 EndY=12.5 EndZ=0
    g6: LineSegment StartX=21.6506 StartY=12.5 StartZ=0 EndX=1e-15 EndY=25 EndZ=0
    g7: Circle [constr] CenterX=0 CenterY=0 CenterZ=0 NormalX=0 NormalY=0 NormalZ=1 AngleXU=0 Radius=25
  constraints (18):
    c: Coincident(g0,g-1)
    c: Diameter(g0) = 40
    c: Coincident(g1,g2)
    c: Coincident(g2,g3)
    c: Coincident(g3,g4)
    c: Coincident(g4,g5)
    c: Coincident(g5,g6)
    c: Coincident(g6,g1)
    c: Equal(g1, g2-g6) x5
    c: PointOnObject(g1,g7)
    c: PointOnObject(g2,g7)
    c: PointOnObject(g3,g7)
    c: PointOnObject(g4,g7)
    c: PointOnObject(g5,g7)
    c: PointOnObject(g6,g7)
    c: Coincident(g7,g0)
    c: PointOnObject(g6,g-2)
    c: Diameter(g7) = 50
FEATURE [Part::Loft] Loft007
  Closed = false
  MaxDegree = 5
  Placement = pos=(0,150,0) rot=(0,0,1;0rad)
  Ruled = false
  Sections = -> [Sketch772,Sketch773]
  Solid = true
FEATURE [Part::MultiCommon] Common004
  Refine = true
  Shapes = -> [Loft007,Extrude754]
FEATURE [Sketcher::SketchObject] Sketch774
  ArcFitTolerance = 1e-06
  FullyConstrained = true
  MakeInternals = false
  Placement = pos=(0,5,0) rot=(1,0,0;1.5708rad)
  sketch-geometry (6):
    g0: Circle CenterX=0 CenterY=119.144 CenterZ=0 NormalX=0 NormalY=0 NormalZ=1 AngleXU=0 Radius=3
    g1: Circle CenterX=-103.181 CenterY=59.5718 CenterZ=0 NormalX=0 NormalY=0 NormalZ=1 AngleXU=0 Radius=3
    g2: Circle CenterX=-103.181 CenterY=-59.5718 CenterZ=0 NormalX=0 NormalY=0 NormalZ=1 AngleXU=0 Radius=3
    g3: Circle CenterX=0 CenterY=-119.144 CenterZ=0 NormalX=0 NormalY=0 NormalZ=1 AngleXU=0 Radius=3
    g4: Circle CenterX=103.181 CenterY=-59.5718 CenterZ=0 NormalX=0 NormalY=0 NormalZ=1 AngleXU=0 Radius=3
    g5: Circle CenterX=103.181 CenterY=59.5718 CenterZ=0 NormalX=0 NormalY=0 NormalZ=1 AngleXU=0 Radius=3
  constraints (14):
    c: Equal(g0, g1-g5) x5
    c: Diameter(g0) = 6
    c: DistanceX(g1) = -103.181
    c: DistanceX(g2) = -103.181
    c: DistanceY(g2) = -59.5718
    c: DistanceX(g3) = 0
    c: DistanceY(g3) = -119.144
    c: DistanceX(g4) = 103.181
    c: DistanceY(g4) = -59.5718
    c: DistanceX(g5) = 103.181
    c: DistanceY(g5) = 59.5718
    c: DistanceX(g0) = 0
    c: DistanceY(g1) = 59.5718
    c: DistanceY(g0) = 119.144
FEATURE [Part::Extrusion] Extrude755  label="headCut"
  Base = -> Sketch774
  Dir = (0,-1,2e-16)
  DirMode = 2
  FaceMakerClass = Part::FaceMakerBullseye
  FaceMakerMode = 3
  LengthFwd = 40
  LengthRev = 0
  Placement = pos=(0,3,0) rot=(0,0,1;0rad)
  Reversed = true
  Solid = true
  Symmetric = false
FEATURE [Part::MultiFuse] Fusion575  label="meshF"
  Refine = true
  Shapes = -> [Common002,Cut009]
FEATURE [Part::MultiFuse] Fusion576  label="backEncloser002"
  Refine = true
  Shapes = -> [Common004,Fusion571]
FEATURE [Part::Cut] Cut012  label="backEncloser003"
  Base = -> Fusion576
  Refine = true
  Tool = -> Extrude755
FEATURE [Part::Box] Box001  label="stand"
  AttacherType = Attacher::AttachEngine3D
  Height = 500
  Length = 60
  Placement = pos=(-30,150,-472) rot=(0,0,1;0rad)
  Width = 30
FEATURE [Part::Cylinder] Cylinder001  label="Cylinder"
  Angle = 360
  AttacherType = Attacher::AttachEngine3D
  FirstAngle = 0
  Height = 60
  Placement = pos=(30,165,-5) rot=(0,1,0;4.71239rad)
  Radius = 2.15
  SecondAngle = 0
FEATURE [Sketcher::SketchObject] Sketch569
  ArcFitTolerance = 1e-06
  FullyConstrained = true
  MakeInternals = false
  Placement = pos=(0,0,0) rot=(0,0.707107,0.707107;3.14159rad)
  sketch-geometry (6):
    g0: LineSegment StartX=1.1e-15 StartY=-26 StartZ=0 EndX=22.5 EndY=-13.0288 EndZ=0
    g1: LineSegment StartX=22.5 StartY=-13.0288 StartZ=0 EndX=22.5 EndY=31.9712 EndZ=0
    g2: LineSegment StartX=-22.5 StartY=31.9712 StartZ=0 EndX=-22.5 EndY=-13.0288 EndZ=0
    g3: LineSegment StartX=-22.5 StartY=-13.0288 StartZ=0 EndX=1.1e-15 EndY=-26 EndZ=0
    g4: Circle [constr] CenterX=0 CenterY=0 CenterZ=0 NormalX=0 NormalY=0 NormalZ=1 AngleXU=0 Radius=26
    g5: LineSegment StartX=-22.5 StartY=31.9712 StartZ=0 EndX=22.5 EndY=31.9712 EndZ=0
  constraints (20):
    c: Coincident(g0,g1)
    c: Coincident(g2,g3)
    c: Coincident(g3,g0)
    c: Equal(g0,g3)
    c: PointOnObject(g0,g4)
    c: PointOnObject(g2,g4)
    c: PointOnObject(g3,g4)
    c: Coincident(g4,g-1)
    c: PointOnObject(g3,g-2)
    c: Diameter(g4) = 52
    c: Coincident(g5,g2)
    c: Coincident(g5,g1)
    c: Vertical(g2)
    c: Block(g3)
    c: Block(g0)
    c: DistanceX(g2,g-1) = 22.5
    c: DistanceX(g-1,g0) = 22.5
    c: DistanceY(g2,g2) = 45
    c: DistanceY(g1,g1) = 45
    c: DistanceX(g5,g5) = 45
FEATURE [Part::Extrusion] Extrude560  label="standmountcut"
  Base = -> Sketch569
  Dir = (0,1,-2e-16)
  DirMode = 2
  FaceMakerClass = Part::FaceMakerBullseye
  FaceMakerMode = 3
  LengthFwd = 30
  LengthRev = 0
  Placement = pos=(0,150,0) rot=(0,0,1;0rad)
  Solid = true
  Symmetric = false
FEATURE [Part::Cut] Cut005  label="standMountCut"
  Base = -> Box001
  Refine = true
  Tool = -> Extrude560
FEATURE [Part::Cut] Cut006  label="standm4cut"
  Base = -> Cut005
  Refine = true
  Tool = -> Cylinder001
FEATURE [Part::Fillet] Fillet  label="standfillet"
  Base = -> Cut006
  EdgeLinks = -> Cut006 [Edge2,Edge15,Edge26,Edge28]
  Edges = 4 edges r=3: [Edge2,Edge15,Edge26,Edge28]
FEATURE [Sketcher::SketchObject] Sketch775
  ArcFitTolerance = 1e-06
  FullyConstrained = true
  MakeInternals = false
  Placement = pos=(0,140,0) rot=(1,0,0;1.5708rad)
  sketch-geometry (7):
    g0: LineSegment StartX=1.2e-15 StartY=-25 StartZ=0 EndX=21.6506 EndY=-12.5 EndZ=0
    g1: LineSegment StartX=-21.6506 StartY=-12.5 StartZ=0 EndX=1.2e-15 EndY=-25 EndZ=0
    g2: Circle [constr] CenterX=0 CenterY=0 CenterZ=0 NormalX=0 NormalY=0 NormalZ=1 AngleXU=0 Radius=25
    g3: LineSegment StartX=-21.6506 StartY=-12.5 StartZ=0 EndX=-21.6506 EndY=0 EndZ=0
    g4: LineSegment StartX=-21.6506 StartY=0 StartZ=0 EndX=0 EndY=0 EndZ=0
    g5: LineSegment StartX=21.6506 StartY=-12.5 StartZ=0 EndX=21.6506 EndY=0 EndZ=0
    g6: LineSegment StartX=21.6506 StartY=0 StartZ=0 EndX=0 EndY=0 EndZ=0
  constraints (20):
    c: Coincident(g1,g0)
    c: Equal(g0,g1)
    c: PointOnObject(g0,g2)
    c: PointOnObject(g1,g2)
    c: PointOnObject(g1,g2)
    c: Coincident(g2,g-1)
    c: Coincident(g3,g1)
    c: PointOnObject(g3,g-1)
    c: Vertical(g3)
    c: PointOnObject(g4,g3)
    c: Coincident(g4,g2)
    c: Horizontal(g4)
    c: Coincident(g5,g0)
    c: PointOnObject(g5,g-1)
    c: Vertical(g5)
    c: Coincident(g6,g5)
    c: Coincident(g6,g2)
    c: DistanceX(g0,g-1) = 0
    c: DistanceY(g0,g-1) = 25
    c: DistanceY(g1,g-1) = 12.5
FEATURE [Part::Extrusion] Extrude756
  Base = -> Sketch775
  Dir = (0,-1,2e-16)
  DirMode = 2
  FaceMakerClass = Part::FaceMakerBullseye
  FaceMakerMode = 3
  LengthFwd = 10
  LengthRev = 0
  Solid = true
  Symmetric = false
FEATURE [Sketcher::SketchObject] Sketch776
  ArcFitTolerance = 1e-06
  FullyConstrained = true
  MakeInternals = false
  Placement = pos=(0,15,0) rot=(1,0,0;1.5708rad)
  expr: Constraints[0] = 113 mm
  sketch-geometry (4):
    g0: LineSegment StartX=0 StartY=113 StartZ=0 EndX=69.25 EndY=73 EndZ=0
    g1: LineSegment StartX=0 StartY=113 StartZ=0 EndX=2.50087 EndY=117.33 EndZ=0
    g2: LineSegment StartX=2.50087 StartY=117.33 StartZ=0 EndX=71.7509 EndY=77.3296 EndZ=0
    g3: LineSegment StartX=71.7509 StartY=77.3296 StartZ=0 EndX=69.25 EndY=73 EndZ=0
  constraints (12):
    c: DistanceY(g-1,g0) = 113
    c: DistanceY(g-1,g0) = 73
    c: Coincident(g1,g0)
    c: Coincident(g2,g1)
    c: Coincident(g3,g2)
    c: Coincident(g3,g0)
    c: Angle(g0,g1) = 1.5708
    c: DistanceX(g-1,g0) = 0
    c: DistanceX(g-1,g0) = 69.25
    c: Distance(g1,g0) = 5
    c: Angle(g2,g3) = 1.5708
    c: Distance(g3) = 5
FEATURE [Part::Extrusion] Extrude757
  Base = -> Sketch776
  Dir = (0,-1,2e-16)
  DirMode = 2
  FaceMakerClass = Part::FaceMakerBullseye
  FaceMakerMode = 3
  LengthFwd = 80
  LengthRev = 0
  Solid = true
  Symmetric = false
FEATURE [Part::Cut] Cut013  label="sensorHold003F"
  Base = -> Fillet006
  Refine = true
  Tool = -> Extrude757
